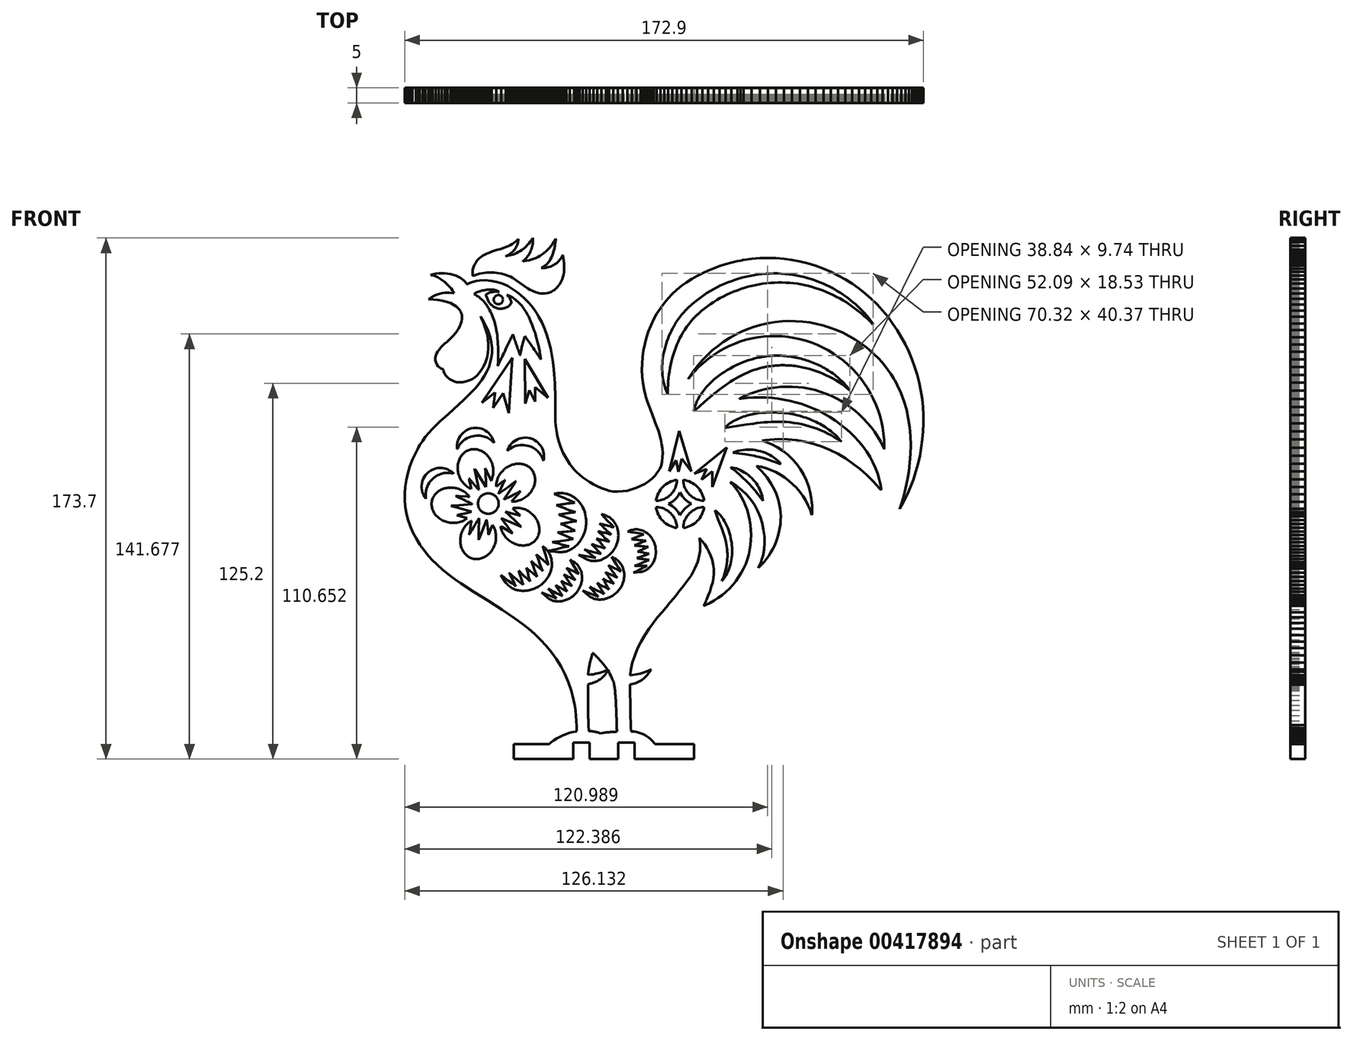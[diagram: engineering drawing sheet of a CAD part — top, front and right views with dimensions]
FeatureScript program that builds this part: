
annotation { "Feature Type Name" : "Feature", "Feature Type Description" : "" }
export const myFeature = defineFeature(function(context is Context, id is Id, definition is map)
    precondition{}
    {
        {
            var Q0;
            Q0=qCreatedBy(makeId("Front.planeOp"),FACE);
            var sketch = newSketch(context, id + "F0", { "sketchPlane" : qUnion([Q0])});
            skLineSegment(sketch, "E0", {"start": v(-42.96, 87.62) * mm, "end": v(-43, 82.82) * mm});
            skLineSegment(sketch, "E1", {"start": v(-43, 82.82) * mm, "end": v(-44.86, 86.57) * mm});
            skLineSegment(sketch, "E2", {"start": v(-44.86, 86.57) * mm, "end": v(-46.3, 82.2) * mm});
            skLineSegment(sketch, "E3", {"start": v(-46.3, 82.2) * mm, "end": v(-46.39, 97.03) * mm});
            skLineSegment(sketch, "E4", {"start": v(-46.39, 97.03) * mm, "end": v(-38.64, 84.08) * mm});
            skLineSegment(sketch, "E5", {"start": v(-38.64, 84.08) * mm, "end": v(-42.96, 87.62) * mm});
            skCircle(sketch, "E6", {"center": v(-55.22, 116.82) * mm, "radius": 1.54 * mm});
            skLineSegment(sketch, "E7", {"start": v(-50.59, 97.44) * mm, "end": v(-51.67, 79.01) * mm});
            skLineSegment(sketch, "E8", {"start": v(-51.67, 79.01) * mm, "end": v(-53.6, 85.56) * mm});
            skLineSegment(sketch, "E9", {"start": v(-53.6, 85.56) * mm, "end": v(-56.93, 80.73) * mm});
            skLineSegment(sketch, "E10", {"start": v(-56.93, 80.73) * mm, "end": v(-56.24, 85.8) * mm});
            skLineSegment(sketch, "E11", {"start": v(-56.24, 85.8) * mm, "end": v(-60.69, 82.38) * mm});
            skLineSegment(sketch, "E12", {"start": v(-60.69, 82.38) * mm, "end": v(-50.59, 97.44) * mm});
            skCircle(sketch, "E13", {"center": v(-58.57, 48.84) * mm, "radius": 3.43 * mm});
            skLineSegment(sketch, "E14", {"start": v(16.07, 54.36) * mm, "end": v(16.08, 59.58) * mm});
            skLineSegment(sketch, "E15", {"start": v(16.08, 59.58) * mm, "end": v(12.58, 56.76) * mm});
            skLineSegment(sketch, "E16", {"start": v(12.58, 56.76) * mm, "end": v(14.2, 60.34) * mm});
            skLineSegment(sketch, "E17", {"start": v(14.2, 60.34) * mm, "end": v(10.18, 58.8) * mm});
            skLineSegment(sketch, "E18", {"start": v(10.18, 58.8) * mm, "end": v(20.87, 67.64) * mm});
            skLineSegment(sketch, "E19", {"start": v(20.87, 67.64) * mm, "end": v(16.07, 54.36) * mm});
            skLineSegment(sketch, "E20", {"start": v(9.07, 59.54) * mm, "end": v(5.98, 63.75) * mm});
            skLineSegment(sketch, "E21", {"start": v(5.98, 63.75) * mm, "end": v(4.84, 59.4) * mm});
            skLineSegment(sketch, "E22", {"start": v(4.84, 59.4) * mm, "end": v(4.01, 63.23) * mm});
            skLineSegment(sketch, "E23", {"start": v(4.01, 63.23) * mm, "end": v(1.7, 59.6) * mm});
            skLineSegment(sketch, "E24", {"start": v(1.7, 59.6) * mm, "end": v(5.04, 73.08) * mm});
            skLineSegment(sketch, "E25", {"start": v(5.04, 73.08) * mm, "end": v(9.07, 59.54) * mm});
            skLineSegment(sketch, "E26", {"start": v(69.55, 108.65) * mm, "end": v(68.66, 109.56) * mm});
            skLineSegment(sketch, "E27", {"start": v(68.66, 109.56) * mm, "end": v(67.74, 110.45) * mm});
            skLineSegment(sketch, "E28", {"start": v(67.74, 110.45) * mm, "end": v(66.8, 111.3) * mm});
            skLineSegment(sketch, "E29", {"start": v(66.8, 111.3) * mm, "end": v(65.85, 112.14) * mm});
            skLineSegment(sketch, "E30", {"start": v(65.85, 112.14) * mm, "end": v(64.87, 112.95) * mm});
            skLineSegment(sketch, "E31", {"start": v(64.87, 112.95) * mm, "end": v(63.87, 113.73) * mm});
            skLineSegment(sketch, "E32", {"start": v(63.87, 113.73) * mm, "end": v(62.86, 114.48) * mm});
            skLineSegment(sketch, "E33", {"start": v(62.86, 114.48) * mm, "end": v(61.82, 115.2) * mm});
            skLineSegment(sketch, "E34", {"start": v(61.82, 115.2) * mm, "end": v(60.77, 115.9) * mm});
            skLineSegment(sketch, "E35", {"start": v(60.77, 115.9) * mm, "end": v(59.7, 116.57) * mm});
            skLineSegment(sketch, "E36", {"start": v(59.7, 116.57) * mm, "end": v(58.6, 117.2) * mm});
            skLineSegment(sketch, "E37", {"start": v(58.6, 117.2) * mm, "end": v(57.5, 117.8) * mm});
            skLineSegment(sketch, "E38", {"start": v(57.5, 117.8) * mm, "end": v(56.38, 118.37) * mm});
            skLineSegment(sketch, "E39", {"start": v(56.38, 118.37) * mm, "end": v(55.24, 118.9) * mm});
            skLineSegment(sketch, "E40", {"start": v(55.24, 118.9) * mm, "end": v(54.09, 119.41) * mm});
            skLineSegment(sketch, "E41", {"start": v(54.09, 119.41) * mm, "end": v(52.92, 119.88) * mm});
            skLineSegment(sketch, "E42", {"start": v(52.92, 119.88) * mm, "end": v(51.74, 120.31) * mm});
            skLineSegment(sketch, "E43", {"start": v(51.74, 120.31) * mm, "end": v(50.54, 120.7) * mm});
            skLineSegment(sketch, "E44", {"start": v(50.54, 120.7) * mm, "end": v(49.34, 121.07) * mm});
            skLineSegment(sketch, "E45", {"start": v(49.34, 121.07) * mm, "end": v(48.11, 121.39) * mm});
            skLineSegment(sketch, "E46", {"start": v(48.11, 121.39) * mm, "end": v(46.88, 121.67) * mm});
            skLineSegment(sketch, "E47", {"start": v(46.88, 121.67) * mm, "end": v(45.63, 121.92) * mm});
            skLineSegment(sketch, "E48", {"start": v(45.63, 121.92) * mm, "end": v(44.38, 122.12) * mm});
            skLineSegment(sketch, "E49", {"start": v(44.38, 122.12) * mm, "end": v(43.11, 122.29) * mm});
            skLineSegment(sketch, "E50", {"start": v(43.11, 122.29) * mm, "end": v(41.83, 122.41) * mm});
            skLineSegment(sketch, "E51", {"start": v(41.83, 122.41) * mm, "end": v(41.2, 122.46) * mm});
            skLineSegment(sketch, "E52", {"start": v(41.2, 122.46) * mm, "end": v(40.56, 122.5) * mm});
            skLineSegment(sketch, "E53", {"start": v(40.56, 122.5) * mm, "end": v(39.3, 122.53) * mm});
            skLineSegment(sketch, "E54", {"start": v(39.3, 122.53) * mm, "end": v(38.04, 122.53) * mm});
            skLineSegment(sketch, "E55", {"start": v(38.04, 122.53) * mm, "end": v(36.78, 122.5) * mm});
            skLineSegment(sketch, "E56", {"start": v(36.78, 122.5) * mm, "end": v(35.52, 122.41) * mm});
            skLineSegment(sketch, "E57", {"start": v(35.52, 122.41) * mm, "end": v(34.26, 122.29) * mm});
            skLineSegment(sketch, "E58", {"start": v(34.26, 122.29) * mm, "end": v(33, 122.13) * mm});
            skLineSegment(sketch, "E59", {"start": v(33, 122.13) * mm, "end": v(31.76, 121.93) * mm});
            skLineSegment(sketch, "E60", {"start": v(31.76, 121.93) * mm, "end": v(30.52, 121.7) * mm});
            skLineSegment(sketch, "E61", {"start": v(30.52, 121.7) * mm, "end": v(29.28, 121.42) * mm});
            skLineSegment(sketch, "E62", {"start": v(29.28, 121.42) * mm, "end": v(28.06, 121.1) * mm});
            skLineSegment(sketch, "E63", {"start": v(28.06, 121.1) * mm, "end": v(26.84, 120.76) * mm});
            skLineSegment(sketch, "E64", {"start": v(26.84, 120.76) * mm, "end": v(25.63, 120.37) * mm});
            skLineSegment(sketch, "E65", {"start": v(25.63, 120.37) * mm, "end": v(24.44, 119.95) * mm});
            skLineSegment(sketch, "E66", {"start": v(24.44, 119.95) * mm, "end": v(23.26, 119.5) * mm});
            skLineSegment(sketch, "E67", {"start": v(23.26, 119.5) * mm, "end": v(22.1, 119) * mm});
            skLineSegment(sketch, "E68", {"start": v(22.1, 119) * mm, "end": v(20.94, 118.47) * mm});
            skLineSegment(sketch, "E69", {"start": v(20.94, 118.47) * mm, "end": v(19.8, 117.9) * mm});
            skLineSegment(sketch, "E70", {"start": v(19.8, 117.9) * mm, "end": v(18.7, 117.3) * mm});
            skLineSegment(sketch, "E71", {"start": v(18.7, 117.3) * mm, "end": v(17.6, 116.66) * mm});
            skLineSegment(sketch, "E72", {"start": v(17.6, 116.66) * mm, "end": v(16.52, 116) * mm});
            skLineSegment(sketch, "E73", {"start": v(16.52, 116) * mm, "end": v(15.46, 115.3) * mm});
            skLineSegment(sketch, "E74", {"start": v(15.46, 115.3) * mm, "end": v(14.43, 114.56) * mm});
            skLineSegment(sketch, "E75", {"start": v(14.43, 114.56) * mm, "end": v(13.42, 113.79) * mm});
            skLineSegment(sketch, "E76", {"start": v(13.42, 113.79) * mm, "end": v(12.44, 112.99) * mm});
            skLineSegment(sketch, "E77", {"start": v(12.44, 112.99) * mm, "end": v(11.49, 112.15) * mm});
            skLineSegment(sketch, "E78", {"start": v(11.49, 112.15) * mm, "end": v(11.25, 111.94) * mm});
            skLineSegment(sketch, "E79", {"start": v(11.25, 111.94) * mm, "end": v(11.04, 111.74) * mm});
            skLineSegment(sketch, "E80", {"start": v(11.04, 111.74) * mm, "end": v(10.61, 111.34) * mm});
            skLineSegment(sketch, "E81", {"start": v(10.61, 111.34) * mm, "end": v(9.8, 110.5) * mm});
            skLineSegment(sketch, "E82", {"start": v(9.8, 110.5) * mm, "end": v(9.03, 109.63) * mm});
            skLineSegment(sketch, "E83", {"start": v(9.03, 109.63) * mm, "end": v(8.3, 108.74) * mm});
            skLineSegment(sketch, "E84", {"start": v(8.3, 108.74) * mm, "end": v(7.6, 107.82) * mm});
            skLineSegment(sketch, "E85", {"start": v(7.6, 107.82) * mm, "end": v(6.95, 106.88) * mm});
            skLineSegment(sketch, "E86", {"start": v(6.95, 106.88) * mm, "end": v(6.34, 105.9) * mm});
            skLineSegment(sketch, "E87", {"start": v(6.34, 105.9) * mm, "end": v(5.77, 104.92) * mm});
            skLineSegment(sketch, "E88", {"start": v(5.77, 104.92) * mm, "end": v(5.24, 103.9) * mm});
            skLineSegment(sketch, "E89", {"start": v(5.24, 103.9) * mm, "end": v(4.74, 102.87) * mm});
            skLineSegment(sketch, "E90", {"start": v(4.74, 102.87) * mm, "end": v(4.28, 101.83) * mm});
            skLineSegment(sketch, "E91", {"start": v(4.28, 101.83) * mm, "end": v(3.85, 100.76) * mm});
            skLineSegment(sketch, "E92", {"start": v(3.85, 100.76) * mm, "end": v(3.46, 99.68) * mm});
            skLineSegment(sketch, "E93", {"start": v(3.46, 99.68) * mm, "end": v(3.1, 98.59) * mm});
            skLineSegment(sketch, "E94", {"start": v(3.1, 98.59) * mm, "end": v(2.78, 97.48) * mm});
            skLineSegment(sketch, "E95", {"start": v(2.78, 97.48) * mm, "end": v(2.5, 96.37) * mm});
            skLineSegment(sketch, "E96", {"start": v(2.5, 96.37) * mm, "end": v(2.24, 95.24) * mm});
            skLineSegment(sketch, "E97", {"start": v(2.24, 95.24) * mm, "end": v(2.01, 94.11) * mm});
            skLineSegment(sketch, "E98", {"start": v(2.01, 94.11) * mm, "end": v(1.82, 92.97) * mm});
            skLineSegment(sketch, "E99", {"start": v(1.82, 92.97) * mm, "end": v(1.66, 91.83) * mm});
            skLineSegment(sketch, "E100", {"start": v(1.66, 91.83) * mm, "end": v(1.52, 90.68) * mm});
            skLineSegment(sketch, "E101", {"start": v(1.52, 90.68) * mm, "end": v(1.42, 89.54) * mm});
            skLineSegment(sketch, "E102", {"start": v(1.42, 89.54) * mm, "end": v(1.34, 88.39) * mm});
            skLineSegment(sketch, "E103", {"start": v(1.34, 88.39) * mm, "end": v(1.29, 87.24) * mm});
            skLineSegment(sketch, "E104", {"start": v(1.29, 87.24) * mm, "end": v(1.26, 86.1) * mm});
            skLineSegment(sketch, "E105", {"start": v(1.26, 86.1) * mm, "end": v(1.26, 85.53) * mm});
            skLineSegment(sketch, "E106", {"start": v(1.26, 85.53) * mm, "end": v(1.26, 85.24) * mm});
            skLineSegment(sketch, "E107", {"start": v(1.26, 85.24) * mm, "end": v(1.26, 85.2) * mm});
            skLineSegment(sketch, "E108", {"start": v(1.26, 85.2) * mm, "end": v(1.26, 85.2) * mm});
            skLineSegment(sketch, "E109", {"start": v(1.26, 85.2) * mm, "end": v(1.23, 85.25) * mm});
            skLineSegment(sketch, "E110", {"start": v(1.23, 85.25) * mm, "end": v(1.18, 85.36) * mm});
            skLineSegment(sketch, "E111", {"start": v(1.18, 85.36) * mm, "end": v(0.8, 86.24) * mm});
            skLineSegment(sketch, "E112", {"start": v(0.8, 86.24) * mm, "end": v(0.47, 87.14) * mm});
            skLineSegment(sketch, "E113", {"start": v(0.47, 87.14) * mm, "end": v(0.19, 88.04) * mm});
            skLineSegment(sketch, "E114", {"start": v(0.19, 88.04) * mm, "end": v(-0.05, 88.96) * mm});
            skLineSegment(sketch, "E115", {"start": v(-0.05, 88.96) * mm, "end": v(-0.25, 89.88) * mm});
            skLineSegment(sketch, "E116", {"start": v(-0.25, 89.88) * mm, "end": v(-0.4, 90.8) * mm});
            skLineSegment(sketch, "E117", {"start": v(-0.4, 90.8) * mm, "end": v(-0.52, 91.75) * mm});
            skLineSegment(sketch, "E118", {"start": v(-0.52, 91.75) * mm, "end": v(-0.6, 92.69) * mm});
            skLineSegment(sketch, "E119", {"start": v(-0.6, 92.69) * mm, "end": v(-0.62, 93.63) * mm});
            skLineSegment(sketch, "E120", {"start": v(-0.62, 93.63) * mm, "end": v(-0.62, 94.58) * mm});
            skLineSegment(sketch, "E121", {"start": v(-0.62, 94.58) * mm, "end": v(-0.57, 95.53) * mm});
            skLineSegment(sketch, "E122", {"start": v(-0.57, 95.53) * mm, "end": v(-0.5, 96.47) * mm});
            skLineSegment(sketch, "E123", {"start": v(-0.5, 96.47) * mm, "end": v(-0.38, 97.42) * mm});
            skLineSegment(sketch, "E124", {"start": v(-0.38, 97.42) * mm, "end": v(-0.23, 98.36) * mm});
            skLineSegment(sketch, "E125", {"start": v(-0.23, 98.36) * mm, "end": v(-0.05, 99.3) * mm});
            skLineSegment(sketch, "E126", {"start": v(-0.05, 99.3) * mm, "end": v(0.17, 100.23) * mm});
            skLineSegment(sketch, "E127", {"start": v(0.17, 100.23) * mm, "end": v(0.41, 101.15) * mm});
            skLineSegment(sketch, "E128", {"start": v(0.41, 101.15) * mm, "end": v(0.69, 102.07) * mm});
            skLineSegment(sketch, "E129", {"start": v(0.69, 102.07) * mm, "end": v(0.99, 102.98) * mm});
            skLineSegment(sketch, "E130", {"start": v(0.99, 102.98) * mm, "end": v(1.32, 103.87) * mm});
            skLineSegment(sketch, "E131", {"start": v(1.32, 103.87) * mm, "end": v(1.68, 104.75) * mm});
            skLineSegment(sketch, "E132", {"start": v(1.68, 104.75) * mm, "end": v(2.06, 105.62) * mm});
            skLineSegment(sketch, "E133", {"start": v(2.06, 105.62) * mm, "end": v(2.47, 106.48) * mm});
            skLineSegment(sketch, "E134", {"start": v(2.47, 106.48) * mm, "end": v(2.9, 107.32) * mm});
            skLineSegment(sketch, "E135", {"start": v(2.9, 107.32) * mm, "end": v(3.36, 108.14) * mm});
            skLineSegment(sketch, "E136", {"start": v(3.36, 108.14) * mm, "end": v(3.47, 108.34) * mm});
            skLineSegment(sketch, "E137", {"start": v(3.47, 108.34) * mm, "end": v(3.53, 108.44) * mm});
            skLineSegment(sketch, "E138", {"start": v(3.53, 108.44) * mm, "end": v(3.58, 108.52) * mm});
            skLineSegment(sketch, "E139", {"start": v(3.58, 108.52) * mm, "end": v(3.74, 108.8) * mm});
            skLineSegment(sketch, "E140", {"start": v(3.74, 108.8) * mm, "end": v(4.09, 109.34) * mm});
            skLineSegment(sketch, "E141", {"start": v(4.09, 109.34) * mm, "end": v(4.44, 109.88) * mm});
            skLineSegment(sketch, "E142", {"start": v(4.44, 109.88) * mm, "end": v(4.8, 110.4) * mm});
            skLineSegment(sketch, "E143", {"start": v(4.8, 110.4) * mm, "end": v(5.2, 110.92) * mm});
            skLineSegment(sketch, "E144", {"start": v(5.2, 110.92) * mm, "end": v(5.58, 111.43) * mm});
            skLineSegment(sketch, "E145", {"start": v(5.58, 111.43) * mm, "end": v(5.99, 111.92) * mm});
            skLineSegment(sketch, "E146", {"start": v(5.99, 111.92) * mm, "end": v(6.4, 112.4) * mm});
            skLineSegment(sketch, "E147", {"start": v(6.4, 112.4) * mm, "end": v(7.26, 113.35) * mm});
            skLineSegment(sketch, "E148", {"start": v(7.26, 113.35) * mm, "end": v(8.17, 114.26) * mm});
            skLineSegment(sketch, "E149", {"start": v(8.17, 114.26) * mm, "end": v(9.1, 115.12) * mm});
            skLineSegment(sketch, "E150", {"start": v(9.1, 115.12) * mm, "end": v(10.08, 115.96) * mm});
            skLineSegment(sketch, "E151", {"start": v(10.08, 115.96) * mm, "end": v(11.08, 116.76) * mm});
            skLineSegment(sketch, "E152", {"start": v(11.08, 116.76) * mm, "end": v(12.1, 117.52) * mm});
            skLineSegment(sketch, "E153", {"start": v(12.1, 117.52) * mm, "end": v(13.16, 118.26) * mm});
            skLineSegment(sketch, "E154", {"start": v(13.16, 118.26) * mm, "end": v(14.24, 118.96) * mm});
            skLineSegment(sketch, "E155", {"start": v(14.24, 118.96) * mm, "end": v(15.33, 119.63) * mm});
            skLineSegment(sketch, "E156", {"start": v(15.33, 119.63) * mm, "end": v(16.47, 120.29) * mm});
            skLineSegment(sketch, "E157", {"start": v(16.47, 120.29) * mm, "end": v(17.63, 120.9) * mm});
            skLineSegment(sketch, "E158", {"start": v(17.63, 120.9) * mm, "end": v(18.8, 121.49) * mm});
            skLineSegment(sketch, "E159", {"start": v(18.8, 121.49) * mm, "end": v(20, 122.03) * mm});
            skLineSegment(sketch, "E160", {"start": v(20, 122.03) * mm, "end": v(21.2, 122.54) * mm});
            skLineSegment(sketch, "E161", {"start": v(21.2, 122.54) * mm, "end": v(22.43, 123) * mm});
            skLineSegment(sketch, "E162", {"start": v(22.43, 123) * mm, "end": v(23.67, 123.43) * mm});
            skLineSegment(sketch, "E163", {"start": v(23.67, 123.43) * mm, "end": v(24.91, 123.82) * mm});
            skLineSegment(sketch, "E164", {"start": v(24.91, 123.82) * mm, "end": v(26.17, 124.18) * mm});
            skLineSegment(sketch, "E165", {"start": v(26.17, 124.18) * mm, "end": v(27.44, 124.49) * mm});
            skLineSegment(sketch, "E166", {"start": v(27.44, 124.49) * mm, "end": v(28.71, 124.76) * mm});
            skLineSegment(sketch, "E167", {"start": v(28.71, 124.76) * mm, "end": v(30, 125) * mm});
            skLineSegment(sketch, "E168", {"start": v(30, 125) * mm, "end": v(31.28, 125.2) * mm});
            skLineSegment(sketch, "E169", {"start": v(31.28, 125.2) * mm, "end": v(32.58, 125.35) * mm});
            skLineSegment(sketch, "E170", {"start": v(32.58, 125.35) * mm, "end": v(33.87, 125.46) * mm});
            skLineSegment(sketch, "E171", {"start": v(33.87, 125.46) * mm, "end": v(35.18, 125.53) * mm});
            skLineSegment(sketch, "E172", {"start": v(35.18, 125.53) * mm, "end": v(36.48, 125.56) * mm});
            skLineSegment(sketch, "E173", {"start": v(36.48, 125.56) * mm, "end": v(37.78, 125.56) * mm});
            skLineSegment(sketch, "E174", {"start": v(37.78, 125.56) * mm, "end": v(39.09, 125.5) * mm});
            skLineSegment(sketch, "E175", {"start": v(39.09, 125.5) * mm, "end": v(40.39, 125.41) * mm});
            skLineSegment(sketch, "E176", {"start": v(40.39, 125.41) * mm, "end": v(41.69, 125.28) * mm});
            skLineSegment(sketch, "E177", {"start": v(41.69, 125.28) * mm, "end": v(42.98, 125.1) * mm});
            skLineSegment(sketch, "E178", {"start": v(42.98, 125.1) * mm, "end": v(44.28, 124.88) * mm});
            skLineSegment(sketch, "E179", {"start": v(44.28, 124.88) * mm, "end": v(45.56, 124.62) * mm});
            skLineSegment(sketch, "E180", {"start": v(45.56, 124.62) * mm, "end": v(46.84, 124.32) * mm});
            skLineSegment(sketch, "E181", {"start": v(46.84, 124.32) * mm, "end": v(47.48, 124.15) * mm});
            skLineSegment(sketch, "E182", {"start": v(47.48, 124.15) * mm, "end": v(47.63, 124.11) * mm});
            skLineSegment(sketch, "E183", {"start": v(47.63, 124.11) * mm, "end": v(47.76, 124.07) * mm});
            skLineSegment(sketch, "E184", {"start": v(47.76, 124.07) * mm, "end": v(48.02, 124) * mm});
            skLineSegment(sketch, "E185", {"start": v(48.02, 124) * mm, "end": v(49.05, 123.69) * mm});
            skLineSegment(sketch, "E186", {"start": v(49.05, 123.69) * mm, "end": v(50.07, 123.35) * mm});
            skLineSegment(sketch, "E187", {"start": v(50.07, 123.35) * mm, "end": v(51.08, 122.98) * mm});
            skLineSegment(sketch, "E188", {"start": v(51.08, 122.98) * mm, "end": v(52.08, 122.6) * mm});
            skLineSegment(sketch, "E189", {"start": v(52.08, 122.6) * mm, "end": v(53.06, 122.17) * mm});
            skLineSegment(sketch, "E190", {"start": v(53.06, 122.17) * mm, "end": v(54.04, 121.73) * mm});
            skLineSegment(sketch, "E191", {"start": v(54.04, 121.73) * mm, "end": v(55, 121.26) * mm});
            skLineSegment(sketch, "E192", {"start": v(55, 121.26) * mm, "end": v(55.95, 120.77) * mm});
            skLineSegment(sketch, "E193", {"start": v(55.95, 120.77) * mm, "end": v(56.88, 120.25) * mm});
            skLineSegment(sketch, "E194", {"start": v(56.88, 120.25) * mm, "end": v(57.8, 119.7) * mm});
            skLineSegment(sketch, "E195", {"start": v(57.8, 119.7) * mm, "end": v(58.7, 119.14) * mm});
            skLineSegment(sketch, "E196", {"start": v(58.7, 119.14) * mm, "end": v(59.6, 118.55) * mm});
            skLineSegment(sketch, "E197", {"start": v(59.6, 118.55) * mm, "end": v(60.47, 117.94) * mm});
            skLineSegment(sketch, "E198", {"start": v(60.47, 117.94) * mm, "end": v(61.33, 117.3) * mm});
            skLineSegment(sketch, "E199", {"start": v(61.33, 117.3) * mm, "end": v(62.17, 116.65) * mm});
            skLineSegment(sketch, "E200", {"start": v(62.17, 116.65) * mm, "end": v(63, 115.97) * mm});
            skLineSegment(sketch, "E201", {"start": v(63, 115.97) * mm, "end": v(63.8, 115.27) * mm});
            skLineSegment(sketch, "E202", {"start": v(63.8, 115.27) * mm, "end": v(64.6, 114.55) * mm});
            skLineSegment(sketch, "E203", {"start": v(64.6, 114.55) * mm, "end": v(65.36, 113.8) * mm});
            skLineSegment(sketch, "E204", {"start": v(65.36, 113.8) * mm, "end": v(66.11, 113.04) * mm});
            skLineSegment(sketch, "E205", {"start": v(66.11, 113.04) * mm, "end": v(66.85, 112.26) * mm});
            skLineSegment(sketch, "E206", {"start": v(66.85, 112.26) * mm, "end": v(67.56, 111.46) * mm});
            skLineSegment(sketch, "E207", {"start": v(67.56, 111.46) * mm, "end": v(68.25, 110.64) * mm});
            skLineSegment(sketch, "E208", {"start": v(68.25, 110.64) * mm, "end": v(68.92, 109.8) * mm});
            skLineSegment(sketch, "E209", {"start": v(68.92, 109.8) * mm, "end": v(69.57, 108.94) * mm});
            skLineSegment(sketch, "E210", {"start": v(69.57, 108.94) * mm, "end": v(69.65, 108.83) * mm});
            skLineSegment(sketch, "E211", {"start": v(69.65, 108.83) * mm, "end": v(69.69, 108.78) * mm});
            skLineSegment(sketch, "E212", {"start": v(69.69, 108.78) * mm, "end": v(69.7, 108.77) * mm});
            skLineSegment(sketch, "E213", {"start": v(69.7, 108.77) * mm, "end": v(69.7, 108.77) * mm});
            skLineSegment(sketch, "E214", {"start": v(69.7, 108.77) * mm, "end": v(69.7, 108.76) * mm});
            skLineSegment(sketch, "E215", {"start": v(69.7, 108.76) * mm, "end": v(69.7, 108.76) * mm});
            skLineSegment(sketch, "E216", {"start": v(69.7, 108.76) * mm, "end": v(69.7, 108.75) * mm});
            skLineSegment(sketch, "E217", {"start": v(69.7, 108.75) * mm, "end": v(69.64, 108.72) * mm});
            skLineSegment(sketch, "E218", {"start": v(69.64, 108.72) * mm, "end": v(69.55, 108.65) * mm});
            skLineSegment(sketch, "E219", {"start": v(19.2, 92.16) * mm, "end": v(20.14, 92.78) * mm});
            skLineSegment(sketch, "E220", {"start": v(20.14, 92.78) * mm, "end": v(21.08, 93.37) * mm});
            skLineSegment(sketch, "E221", {"start": v(21.08, 93.37) * mm, "end": v(22.05, 93.93) * mm});
            skLineSegment(sketch, "E222", {"start": v(22.05, 93.93) * mm, "end": v(23.03, 94.45) * mm});
            skLineSegment(sketch, "E223", {"start": v(23.03, 94.45) * mm, "end": v(24.03, 94.95) * mm});
            skLineSegment(sketch, "E224", {"start": v(24.03, 94.95) * mm, "end": v(25.05, 95.42) * mm});
            skLineSegment(sketch, "E225", {"start": v(25.05, 95.42) * mm, "end": v(26.08, 95.85) * mm});
            skLineSegment(sketch, "E226", {"start": v(26.08, 95.85) * mm, "end": v(27.12, 96.25) * mm});
            skLineSegment(sketch, "E227", {"start": v(27.12, 96.25) * mm, "end": v(28.18, 96.61) * mm});
            skLineSegment(sketch, "E228", {"start": v(28.18, 96.61) * mm, "end": v(29.24, 96.94) * mm});
            skLineSegment(sketch, "E229", {"start": v(29.24, 96.94) * mm, "end": v(30.32, 97.24) * mm});
            skLineSegment(sketch, "E230", {"start": v(30.32, 97.24) * mm, "end": v(31.4, 97.5) * mm});
            skLineSegment(sketch, "E231", {"start": v(31.4, 97.5) * mm, "end": v(31.95, 97.61) * mm});
            skLineSegment(sketch, "E232", {"start": v(31.95, 97.61) * mm, "end": v(32.22, 97.66) * mm});
            skLineSegment(sketch, "E233", {"start": v(32.22, 97.66) * mm, "end": v(32.26, 97.67) * mm});
            skLineSegment(sketch, "E234", {"start": v(32.26, 97.67) * mm, "end": v(32.28, 97.67) * mm});
            skLineSegment(sketch, "E235", {"start": v(32.28, 97.67) * mm, "end": v(32.3, 97.68) * mm});
            skLineSegment(sketch, "E236", {"start": v(32.3, 97.68) * mm, "end": v(32.46, 97.7) * mm});
            skLineSegment(sketch, "E237", {"start": v(32.46, 97.7) * mm, "end": v(32.78, 97.76) * mm});
            skLineSegment(sketch, "E238", {"start": v(32.78, 97.76) * mm, "end": v(33.4, 97.86) * mm});
            skLineSegment(sketch, "E239", {"start": v(33.4, 97.86) * mm, "end": v(34.03, 97.95) * mm});
            skLineSegment(sketch, "E240", {"start": v(34.03, 97.95) * mm, "end": v(34.67, 98.02) * mm});
            skLineSegment(sketch, "E241", {"start": v(34.67, 98.02) * mm, "end": v(35.3, 98.08) * mm});
            skLineSegment(sketch, "E242", {"start": v(35.3, 98.08) * mm, "end": v(35.94, 98.12) * mm});
            skLineSegment(sketch, "E243", {"start": v(35.94, 98.12) * mm, "end": v(36.59, 98.15) * mm});
            skLineSegment(sketch, "E244", {"start": v(36.59, 98.15) * mm, "end": v(37.23, 98.16) * mm});
            skLineSegment(sketch, "E245", {"start": v(37.23, 98.16) * mm, "end": v(37.88, 98.16) * mm});
            skLineSegment(sketch, "E246", {"start": v(37.88, 98.16) * mm, "end": v(38.52, 98.15) * mm});
            skLineSegment(sketch, "E247", {"start": v(38.52, 98.15) * mm, "end": v(39.17, 98.13) * mm});
            skLineSegment(sketch, "E248", {"start": v(39.17, 98.13) * mm, "end": v(39.82, 98.09) * mm});
            skLineSegment(sketch, "E249", {"start": v(39.82, 98.09) * mm, "end": v(40.47, 98.03) * mm});
            skLineSegment(sketch, "E250", {"start": v(40.47, 98.03) * mm, "end": v(41.12, 97.97) * mm});
            skLineSegment(sketch, "E251", {"start": v(41.12, 97.97) * mm, "end": v(41.77, 97.89) * mm});
            skLineSegment(sketch, "E252", {"start": v(41.77, 97.89) * mm, "end": v(42.42, 97.8) * mm});
            skLineSegment(sketch, "E253", {"start": v(42.42, 97.8) * mm, "end": v(43.07, 97.69) * mm});
            skLineSegment(sketch, "E254", {"start": v(43.07, 97.69) * mm, "end": v(43.71, 97.57) * mm});
            skLineSegment(sketch, "E255", {"start": v(43.71, 97.57) * mm, "end": v(44.36, 97.44) * mm});
            skLineSegment(sketch, "E256", {"start": v(44.36, 97.44) * mm, "end": v(45, 97.29) * mm});
            skLineSegment(sketch, "E257", {"start": v(45, 97.29) * mm, "end": v(45.64, 97.13) * mm});
            skLineSegment(sketch, "E258", {"start": v(45.64, 97.13) * mm, "end": v(46.27, 96.96) * mm});
            skLineSegment(sketch, "E259", {"start": v(46.27, 96.96) * mm, "end": v(46.9, 96.78) * mm});
            skLineSegment(sketch, "E260", {"start": v(46.9, 96.78) * mm, "end": v(47.54, 96.58) * mm});
            skLineSegment(sketch, "E261", {"start": v(47.54, 96.58) * mm, "end": v(48.16, 96.37) * mm});
            skLineSegment(sketch, "E262", {"start": v(48.16, 96.37) * mm, "end": v(48.78, 96.15) * mm});
            skLineSegment(sketch, "E263", {"start": v(48.78, 96.15) * mm, "end": v(49.4, 95.92) * mm});
            skLineSegment(sketch, "E264", {"start": v(49.4, 95.92) * mm, "end": v(50.01, 95.67) * mm});
            skLineSegment(sketch, "E265", {"start": v(50.01, 95.67) * mm, "end": v(50.62, 95.41) * mm});
            skLineSegment(sketch, "E266", {"start": v(50.62, 95.41) * mm, "end": v(51.22, 95.14) * mm});
            skLineSegment(sketch, "E267", {"start": v(51.22, 95.14) * mm, "end": v(51.81, 94.86) * mm});
            skLineSegment(sketch, "E268", {"start": v(51.81, 94.86) * mm, "end": v(52.4, 94.56) * mm});
            skLineSegment(sketch, "E269", {"start": v(52.4, 94.56) * mm, "end": v(52.98, 94.26) * mm});
            skLineSegment(sketch, "E270", {"start": v(52.98, 94.26) * mm, "end": v(53.55, 93.94) * mm});
            skLineSegment(sketch, "E271", {"start": v(53.55, 93.94) * mm, "end": v(54.12, 93.6) * mm});
            skLineSegment(sketch, "E272", {"start": v(54.12, 93.6) * mm, "end": v(54.67, 93.26) * mm});
            skLineSegment(sketch, "E273", {"start": v(54.67, 93.26) * mm, "end": v(55.22, 92.91) * mm});
            skLineSegment(sketch, "E274", {"start": v(55.22, 92.91) * mm, "end": v(55.76, 92.55) * mm});
            skLineSegment(sketch, "E275", {"start": v(55.76, 92.55) * mm, "end": v(56.3, 92.17) * mm});
            skLineSegment(sketch, "E276", {"start": v(56.3, 92.17) * mm, "end": v(56.82, 91.78) * mm});
            skLineSegment(sketch, "E277", {"start": v(56.82, 91.78) * mm, "end": v(57.33, 91.38) * mm});
            skLineSegment(sketch, "E278", {"start": v(57.33, 91.38) * mm, "end": v(57.83, 90.97) * mm});
            skLineSegment(sketch, "E279", {"start": v(57.83, 90.97) * mm, "end": v(58.32, 90.55) * mm});
            skLineSegment(sketch, "E280", {"start": v(58.32, 90.55) * mm, "end": v(58.8, 90.11) * mm});
            skLineSegment(sketch, "E281", {"start": v(58.8, 90.11) * mm, "end": v(59.27, 89.67) * mm});
            skLineSegment(sketch, "E282", {"start": v(59.27, 89.67) * mm, "end": v(59.73, 89.21) * mm});
            skLineSegment(sketch, "E283", {"start": v(59.73, 89.21) * mm, "end": v(60.17, 88.75) * mm});
            skLineSegment(sketch, "E284", {"start": v(60.17, 88.75) * mm, "end": v(60.6, 88.27) * mm});
            skLineSegment(sketch, "E285", {"start": v(60.6, 88.27) * mm, "end": v(61.03, 87.78) * mm});
            skLineSegment(sketch, "E286", {"start": v(61.03, 87.78) * mm, "end": v(61.43, 87.28) * mm});
            skLineSegment(sketch, "E287", {"start": v(61.43, 87.28) * mm, "end": v(61.83, 86.78) * mm});
            skLineSegment(sketch, "E288", {"start": v(61.83, 86.78) * mm, "end": v(61.92, 86.65) * mm});
            skLineSegment(sketch, "E289", {"start": v(61.92, 86.65) * mm, "end": v(61.97, 86.58) * mm});
            skLineSegment(sketch, "E290", {"start": v(61.97, 86.58) * mm, "end": v(61.98, 86.57) * mm});
            skLineSegment(sketch, "E291", {"start": v(61.98, 86.57) * mm, "end": v(61.96, 86.58) * mm});
            skLineSegment(sketch, "E292", {"start": v(61.96, 86.58) * mm, "end": v(61.94, 86.6) * mm});
            skLineSegment(sketch, "E293", {"start": v(61.94, 86.6) * mm, "end": v(61.7, 86.8) * mm});
            skLineSegment(sketch, "E294", {"start": v(61.7, 86.8) * mm, "end": v(61.25, 87.18) * mm});
            skLineSegment(sketch, "E295", {"start": v(61.25, 87.18) * mm, "end": v(60.3, 87.91) * mm});
            skLineSegment(sketch, "E296", {"start": v(60.3, 87.91) * mm, "end": v(59.34, 88.62) * mm});
            skLineSegment(sketch, "E297", {"start": v(59.34, 88.62) * mm, "end": v(58.34, 89.29) * mm});
            skLineSegment(sketch, "E298", {"start": v(58.34, 89.29) * mm, "end": v(57.32, 89.92) * mm});
            skLineSegment(sketch, "E299", {"start": v(57.32, 89.92) * mm, "end": v(56.28, 90.53) * mm});
            skLineSegment(sketch, "E300", {"start": v(56.28, 90.53) * mm, "end": v(55.21, 91.1) * mm});
            skLineSegment(sketch, "E301", {"start": v(55.21, 91.1) * mm, "end": v(54.13, 91.63) * mm});
            skLineSegment(sketch, "E302", {"start": v(54.13, 91.63) * mm, "end": v(53.02, 92.13) * mm});
            skLineSegment(sketch, "E303", {"start": v(53.02, 92.13) * mm, "end": v(51.9, 92.59) * mm});
            skLineSegment(sketch, "E304", {"start": v(51.9, 92.59) * mm, "end": v(50.76, 93) * mm});
            skLineSegment(sketch, "E305", {"start": v(50.76, 93) * mm, "end": v(49.61, 93.4) * mm});
            skLineSegment(sketch, "E306", {"start": v(49.61, 93.4) * mm, "end": v(48.45, 93.73) * mm});
            skLineSegment(sketch, "E307", {"start": v(48.45, 93.73) * mm, "end": v(47.28, 94.04) * mm});
            skLineSegment(sketch, "E308", {"start": v(47.28, 94.04) * mm, "end": v(46.1, 94.3) * mm});
            skLineSegment(sketch, "E309", {"start": v(46.1, 94.3) * mm, "end": v(44.9, 94.52) * mm});
            skLineSegment(sketch, "E310", {"start": v(44.9, 94.52) * mm, "end": v(43.72, 94.7) * mm});
            skLineSegment(sketch, "E311", {"start": v(43.72, 94.7) * mm, "end": v(43.12, 94.77) * mm});
            skLineSegment(sketch, "E312", {"start": v(43.12, 94.77) * mm, "end": v(42.52, 94.83) * mm});
            skLineSegment(sketch, "E313", {"start": v(42.52, 94.83) * mm, "end": v(41.92, 94.88) * mm});
            skLineSegment(sketch, "E314", {"start": v(41.92, 94.88) * mm, "end": v(41.32, 94.91) * mm});
            skLineSegment(sketch, "E315", {"start": v(41.32, 94.91) * mm, "end": v(40.72, 94.94) * mm});
            skLineSegment(sketch, "E316", {"start": v(40.72, 94.94) * mm, "end": v(40.12, 94.96) * mm});
            skLineSegment(sketch, "E317", {"start": v(40.12, 94.96) * mm, "end": v(39.52, 94.96) * mm});
            skLineSegment(sketch, "E318", {"start": v(39.52, 94.96) * mm, "end": v(38.92, 94.95) * mm});
            skLineSegment(sketch, "E319", {"start": v(38.92, 94.95) * mm, "end": v(38.32, 94.94) * mm});
            skLineSegment(sketch, "E320", {"start": v(38.32, 94.94) * mm, "end": v(37.72, 94.9) * mm});
            skLineSegment(sketch, "E321", {"start": v(37.72, 94.9) * mm, "end": v(37.12, 94.86) * mm});
            skLineSegment(sketch, "E322", {"start": v(37.12, 94.86) * mm, "end": v(36.53, 94.8) * mm});
            skLineSegment(sketch, "E323", {"start": v(36.53, 94.8) * mm, "end": v(35.93, 94.74) * mm});
            skLineSegment(sketch, "E324", {"start": v(35.93, 94.74) * mm, "end": v(35.34, 94.66) * mm});
            skLineSegment(sketch, "E325", {"start": v(35.34, 94.66) * mm, "end": v(34.75, 94.57) * mm});
            skLineSegment(sketch, "E326", {"start": v(34.75, 94.57) * mm, "end": v(34.16, 94.46) * mm});
            skLineSegment(sketch, "E327", {"start": v(34.16, 94.46) * mm, "end": v(33.57, 94.35) * mm});
            skLineSegment(sketch, "E328", {"start": v(33.57, 94.35) * mm, "end": v(33.28, 94.28) * mm});
            skLineSegment(sketch, "E329", {"start": v(33.28, 94.28) * mm, "end": v(33, 94.22) * mm});
            skLineSegment(sketch, "E330", {"start": v(33, 94.22) * mm, "end": v(31.93, 93.95) * mm});
            skLineSegment(sketch, "E331", {"start": v(31.93, 93.95) * mm, "end": v(30.87, 93.64) * mm});
            skLineSegment(sketch, "E332", {"start": v(30.87, 93.64) * mm, "end": v(29.84, 93.3) * mm});
            skLineSegment(sketch, "E333", {"start": v(29.84, 93.3) * mm, "end": v(28.82, 92.91) * mm});
            skLineSegment(sketch, "E334", {"start": v(28.82, 92.91) * mm, "end": v(27.82, 92.5) * mm});
            skLineSegment(sketch, "E335", {"start": v(27.82, 92.5) * mm, "end": v(26.83, 92.05) * mm});
            skLineSegment(sketch, "E336", {"start": v(26.83, 92.05) * mm, "end": v(25.86, 91.58) * mm});
            skLineSegment(sketch, "E337", {"start": v(25.86, 91.58) * mm, "end": v(24.9, 91.08) * mm});
            skLineSegment(sketch, "E338", {"start": v(24.9, 91.08) * mm, "end": v(23.97, 90.55) * mm});
            skLineSegment(sketch, "E339", {"start": v(23.97, 90.55) * mm, "end": v(23.04, 90) * mm});
            skLineSegment(sketch, "E340", {"start": v(23.04, 90) * mm, "end": v(22.12, 89.42) * mm});
            skLineSegment(sketch, "E341", {"start": v(22.12, 89.42) * mm, "end": v(21.22, 88.82) * mm});
            skLineSegment(sketch, "E342", {"start": v(21.22, 88.82) * mm, "end": v(20.33, 88.2) * mm});
            skLineSegment(sketch, "E343", {"start": v(20.33, 88.2) * mm, "end": v(19.44, 87.57) * mm});
            skLineSegment(sketch, "E344", {"start": v(19.44, 87.57) * mm, "end": v(18.57, 86.92) * mm});
            skLineSegment(sketch, "E345", {"start": v(18.57, 86.92) * mm, "end": v(17.7, 86.26) * mm});
            skLineSegment(sketch, "E346", {"start": v(17.7, 86.26) * mm, "end": v(16.85, 85.58) * mm});
            skLineSegment(sketch, "E347", {"start": v(16.85, 85.58) * mm, "end": v(16, 84.9) * mm});
            skLineSegment(sketch, "E348", {"start": v(16, 84.9) * mm, "end": v(15.16, 84.2) * mm});
            skLineSegment(sketch, "E349", {"start": v(15.16, 84.2) * mm, "end": v(13.5, 82.78) * mm});
            skLineSegment(sketch, "E350", {"start": v(13.5, 82.78) * mm, "end": v(11.85, 81.35) * mm});
            skLineSegment(sketch, "E351", {"start": v(11.85, 81.35) * mm, "end": v(10.22, 79.92) * mm});
            skLineSegment(sketch, "E352", {"start": v(10.22, 79.92) * mm, "end": v(10.01, 79.74) * mm});
            skLineSegment(sketch, "E353", {"start": v(10.01, 79.74) * mm, "end": v(9.91, 79.65) * mm});
            skLineSegment(sketch, "E354", {"start": v(9.91, 79.65) * mm, "end": v(9.9, 79.64) * mm});
            skLineSegment(sketch, "E355", {"start": v(9.9, 79.64) * mm, "end": v(9.9, 79.64) * mm});
            skLineSegment(sketch, "E356", {"start": v(9.9, 79.64) * mm, "end": v(9.9, 79.65) * mm});
            skLineSegment(sketch, "E357", {"start": v(9.9, 79.65) * mm, "end": v(9.9, 79.7) * mm});
            skLineSegment(sketch, "E358", {"start": v(9.9, 79.7) * mm, "end": v(9.96, 80) * mm});
            skLineSegment(sketch, "E359", {"start": v(9.96, 80) * mm, "end": v(10.1, 80.59) * mm});
            skLineSegment(sketch, "E360", {"start": v(10.1, 80.59) * mm, "end": v(10.28, 81.18) * mm});
            skLineSegment(sketch, "E361", {"start": v(10.28, 81.18) * mm, "end": v(10.48, 81.76) * mm});
            skLineSegment(sketch, "E362", {"start": v(10.48, 81.76) * mm, "end": v(10.7, 82.33) * mm});
            skLineSegment(sketch, "E363", {"start": v(10.7, 82.33) * mm, "end": v(10.95, 82.9) * mm});
            skLineSegment(sketch, "E364", {"start": v(10.95, 82.9) * mm, "end": v(11.22, 83.46) * mm});
            skLineSegment(sketch, "E365", {"start": v(11.22, 83.46) * mm, "end": v(11.52, 84.02) * mm});
            skLineSegment(sketch, "E366", {"start": v(11.52, 84.02) * mm, "end": v(11.83, 84.56) * mm});
            skLineSegment(sketch, "E367", {"start": v(11.83, 84.56) * mm, "end": v(12.16, 85.1) * mm});
            skLineSegment(sketch, "E368", {"start": v(12.16, 85.1) * mm, "end": v(12.52, 85.62) * mm});
            skLineSegment(sketch, "E369", {"start": v(12.52, 85.62) * mm, "end": v(12.89, 86.14) * mm});
            skLineSegment(sketch, "E370", {"start": v(12.89, 86.14) * mm, "end": v(13.27, 86.65) * mm});
            skLineSegment(sketch, "E371", {"start": v(13.27, 86.65) * mm, "end": v(13.67, 87.15) * mm});
            skLineSegment(sketch, "E372", {"start": v(13.67, 87.15) * mm, "end": v(14.09, 87.63) * mm});
            skLineSegment(sketch, "E373", {"start": v(14.09, 87.63) * mm, "end": v(14.52, 88.1) * mm});
            skLineSegment(sketch, "E374", {"start": v(14.52, 88.1) * mm, "end": v(14.95, 88.57) * mm});
            skLineSegment(sketch, "E375", {"start": v(14.95, 88.57) * mm, "end": v(15.4, 89.02) * mm});
            skLineSegment(sketch, "E376", {"start": v(15.4, 89.02) * mm, "end": v(15.86, 89.46) * mm});
            skLineSegment(sketch, "E377", {"start": v(15.86, 89.46) * mm, "end": v(16.32, 89.89) * mm});
            skLineSegment(sketch, "E378", {"start": v(16.32, 89.89) * mm, "end": v(16.8, 90.3) * mm});
            skLineSegment(sketch, "E379", {"start": v(16.8, 90.3) * mm, "end": v(17.27, 90.7) * mm});
            skLineSegment(sketch, "E380", {"start": v(17.27, 90.7) * mm, "end": v(17.75, 91.09) * mm});
            skLineSegment(sketch, "E381", {"start": v(17.75, 91.09) * mm, "end": v(18.24, 91.46) * mm});
            skLineSegment(sketch, "E382", {"start": v(18.24, 91.46) * mm, "end": v(18.72, 91.82) * mm});
            skLineSegment(sketch, "E383", {"start": v(18.72, 91.82) * mm, "end": v(19.2, 92.16) * mm});
            skLineSegment(sketch, "E384", {"start": v(38.88, 79.13) * mm, "end": v(39.57, 79.08) * mm});
            skLineSegment(sketch, "E385", {"start": v(39.57, 79.08) * mm, "end": v(40.27, 79) * mm});
            skLineSegment(sketch, "E386", {"start": v(40.27, 79) * mm, "end": v(41.67, 78.82) * mm});
            skLineSegment(sketch, "E387", {"start": v(41.67, 78.82) * mm, "end": v(43.08, 78.57) * mm});
            skLineSegment(sketch, "E388", {"start": v(43.08, 78.57) * mm, "end": v(44.49, 78.26) * mm});
            skLineSegment(sketch, "E389", {"start": v(44.49, 78.26) * mm, "end": v(45.2, 78.08) * mm});
            skLineSegment(sketch, "E390", {"start": v(45.2, 78.08) * mm, "end": v(45.9, 77.88) * mm});
            skLineSegment(sketch, "E391", {"start": v(45.9, 77.88) * mm, "end": v(46.6, 77.67) * mm});
            skLineSegment(sketch, "E392", {"start": v(46.6, 77.67) * mm, "end": v(47.28, 77.44) * mm});
            skLineSegment(sketch, "E393", {"start": v(47.28, 77.44) * mm, "end": v(47.97, 77.2) * mm});
            skLineSegment(sketch, "E394", {"start": v(47.97, 77.2) * mm, "end": v(48.66, 76.93) * mm});
            skLineSegment(sketch, "E395", {"start": v(48.66, 76.93) * mm, "end": v(49.33, 76.65) * mm});
            skLineSegment(sketch, "E396", {"start": v(49.33, 76.65) * mm, "end": v(50, 76.36) * mm});
            skLineSegment(sketch, "E397", {"start": v(50, 76.36) * mm, "end": v(50.67, 76.05) * mm});
            skLineSegment(sketch, "E398", {"start": v(50.67, 76.05) * mm, "end": v(51.32, 75.73) * mm});
            skLineSegment(sketch, "E399", {"start": v(51.32, 75.73) * mm, "end": v(51.96, 75.39) * mm});
            skLineSegment(sketch, "E400", {"start": v(51.96, 75.39) * mm, "end": v(52.6, 75.03) * mm});
            skLineSegment(sketch, "E401", {"start": v(52.6, 75.03) * mm, "end": v(53.22, 74.66) * mm});
            skLineSegment(sketch, "E402", {"start": v(53.22, 74.66) * mm, "end": v(53.83, 74.27) * mm});
            skLineSegment(sketch, "E403", {"start": v(53.83, 74.27) * mm, "end": v(54.43, 73.86) * mm});
            skLineSegment(sketch, "E404", {"start": v(54.43, 73.86) * mm, "end": v(55.01, 73.44) * mm});
            skLineSegment(sketch, "E405", {"start": v(55.01, 73.44) * mm, "end": v(55.58, 73) * mm});
            skLineSegment(sketch, "E406", {"start": v(55.58, 73) * mm, "end": v(56.14, 72.55) * mm});
            skLineSegment(sketch, "E407", {"start": v(56.14, 72.55) * mm, "end": v(56.67, 72.08) * mm});
            skLineSegment(sketch, "E408", {"start": v(56.67, 72.08) * mm, "end": v(57.2, 71.6) * mm});
            skLineSegment(sketch, "E409", {"start": v(57.2, 71.6) * mm, "end": v(57.7, 71.09) * mm});
            skLineSegment(sketch, "E410", {"start": v(57.7, 71.09) * mm, "end": v(58.19, 70.57) * mm});
            skLineSegment(sketch, "E411", {"start": v(58.19, 70.57) * mm, "end": v(58.65, 70.03) * mm});
            skLineSegment(sketch, "E412", {"start": v(58.65, 70.03) * mm, "end": v(59.1, 69.48) * mm});
            skLineSegment(sketch, "E413", {"start": v(59.1, 69.48) * mm, "end": v(58.02, 70.23) * mm});
            skLineSegment(sketch, "E414", {"start": v(58.02, 70.23) * mm, "end": v(56.9, 70.93) * mm});
            skLineSegment(sketch, "E415", {"start": v(56.9, 70.93) * mm, "end": v(55.77, 71.58) * mm});
            skLineSegment(sketch, "E416", {"start": v(55.77, 71.58) * mm, "end": v(54.6, 72.2) * mm});
            skLineSegment(sketch, "E417", {"start": v(54.6, 72.2) * mm, "end": v(53.41, 72.77) * mm});
            skLineSegment(sketch, "E418", {"start": v(53.41, 72.77) * mm, "end": v(52.2, 73.3) * mm});
            skLineSegment(sketch, "E419", {"start": v(52.2, 73.3) * mm, "end": v(50.97, 73.78) * mm});
            skLineSegment(sketch, "E420", {"start": v(50.97, 73.78) * mm, "end": v(49.72, 74.22) * mm});
            skLineSegment(sketch, "E421", {"start": v(49.72, 74.22) * mm, "end": v(48.45, 74.61) * mm});
            skLineSegment(sketch, "E422", {"start": v(48.45, 74.61) * mm, "end": v(47.18, 74.96) * mm});
            skLineSegment(sketch, "E423", {"start": v(47.18, 74.96) * mm, "end": v(45.89, 75.27) * mm});
            skLineSegment(sketch, "E424", {"start": v(45.89, 75.27) * mm, "end": v(44.6, 75.53) * mm});
            skLineSegment(sketch, "E425", {"start": v(44.6, 75.53) * mm, "end": v(43.29, 75.74) * mm});
            skLineSegment(sketch, "E426", {"start": v(43.29, 75.74) * mm, "end": v(41.98, 75.9) * mm});
            skLineSegment(sketch, "E427", {"start": v(41.98, 75.9) * mm, "end": v(40.68, 76.03) * mm});
            skLineSegment(sketch, "E428", {"start": v(40.68, 76.03) * mm, "end": v(39.37, 76.1) * mm});
            skLineSegment(sketch, "E429", {"start": v(39.37, 76.1) * mm, "end": v(38.17, 76.13) * mm});
            skLineSegment(sketch, "E430", {"start": v(38.17, 76.13) * mm, "end": v(36.97, 76.12) * mm});
            skLineSegment(sketch, "E431", {"start": v(36.97, 76.12) * mm, "end": v(35.77, 76.08) * mm});
            skLineSegment(sketch, "E432", {"start": v(35.77, 76.08) * mm, "end": v(34.57, 76) * mm});
            skLineSegment(sketch, "E433", {"start": v(34.57, 76) * mm, "end": v(33.37, 75.91) * mm});
            skLineSegment(sketch, "E434", {"start": v(33.37, 75.91) * mm, "end": v(32.18, 75.8) * mm});
            skLineSegment(sketch, "E435", {"start": v(32.18, 75.8) * mm, "end": v(30.98, 75.66) * mm});
            skLineSegment(sketch, "E436", {"start": v(30.98, 75.66) * mm, "end": v(29.78, 75.5) * mm});
            skLineSegment(sketch, "E437", {"start": v(29.78, 75.5) * mm, "end": v(27.4, 75.16) * mm});
            skLineSegment(sketch, "E438", {"start": v(27.4, 75.16) * mm, "end": v(25, 74.79) * mm});
            skLineSegment(sketch, "E439", {"start": v(25, 74.79) * mm, "end": v(22.63, 74.42) * mm});
            skLineSegment(sketch, "E440", {"start": v(22.63, 74.42) * mm, "end": v(20.26, 74.07) * mm});
            skLineSegment(sketch, "E441", {"start": v(20.26, 74.07) * mm, "end": v(20.7, 74.5) * mm});
            skLineSegment(sketch, "E442", {"start": v(20.7, 74.5) * mm, "end": v(21.15, 74.9) * mm});
            skLineSegment(sketch, "E443", {"start": v(21.15, 74.9) * mm, "end": v(21.62, 75.29) * mm});
            skLineSegment(sketch, "E444", {"start": v(21.62, 75.29) * mm, "end": v(22.1, 75.65) * mm});
            skLineSegment(sketch, "E445", {"start": v(22.1, 75.65) * mm, "end": v(22.6, 76) * mm});
            skLineSegment(sketch, "E446", {"start": v(22.6, 76) * mm, "end": v(23.13, 76.31) * mm});
            skLineSegment(sketch, "E447", {"start": v(23.13, 76.31) * mm, "end": v(23.66, 76.61) * mm});
            skLineSegment(sketch, "E448", {"start": v(23.66, 76.61) * mm, "end": v(24.21, 76.9) * mm});
            skLineSegment(sketch, "E449", {"start": v(24.21, 76.9) * mm, "end": v(24.77, 77.16) * mm});
            skLineSegment(sketch, "E450", {"start": v(24.77, 77.16) * mm, "end": v(25.34, 77.4) * mm});
            skLineSegment(sketch, "E451", {"start": v(25.34, 77.4) * mm, "end": v(25.92, 77.63) * mm});
            skLineSegment(sketch, "E452", {"start": v(25.92, 77.63) * mm, "end": v(26.52, 77.84) * mm});
            skLineSegment(sketch, "E453", {"start": v(26.52, 77.84) * mm, "end": v(27.12, 78.03) * mm});
            skLineSegment(sketch, "E454", {"start": v(27.12, 78.03) * mm, "end": v(27.73, 78.2) * mm});
            skLineSegment(sketch, "E455", {"start": v(27.73, 78.2) * mm, "end": v(28.34, 78.37) * mm});
            skLineSegment(sketch, "E456", {"start": v(28.34, 78.37) * mm, "end": v(28.96, 78.51) * mm});
            skLineSegment(sketch, "E457", {"start": v(28.96, 78.51) * mm, "end": v(30.22, 78.75) * mm});
            skLineSegment(sketch, "E458", {"start": v(30.22, 78.75) * mm, "end": v(31.48, 78.94) * mm});
            skLineSegment(sketch, "E459", {"start": v(31.48, 78.94) * mm, "end": v(32.75, 79.08) * mm});
            skLineSegment(sketch, "E460", {"start": v(32.75, 79.08) * mm, "end": v(34.02, 79.17) * mm});
            skLineSegment(sketch, "E461", {"start": v(34.02, 79.17) * mm, "end": v(35.27, 79.22) * mm});
            skLineSegment(sketch, "E462", {"start": v(35.27, 79.22) * mm, "end": v(36.5, 79.22) * mm});
            skLineSegment(sketch, "E463", {"start": v(36.5, 79.22) * mm, "end": v(37.7, 79.2) * mm});
            skLineSegment(sketch, "E464", {"start": v(37.7, 79.2) * mm, "end": v(38.88, 79.13) * mm});
            skLineSegment(sketch, "E465", {"start": v(39, 61.98) * mm, "end": v(36.07, 63) * mm});
            skLineSegment(sketch, "E466", {"start": v(36.07, 63) * mm, "end": v(34.6, 63.5) * mm});
            skLineSegment(sketch, "E467", {"start": v(34.6, 63.5) * mm, "end": v(33.13, 63.97) * mm});
            skLineSegment(sketch, "E468", {"start": v(33.13, 63.97) * mm, "end": v(31.64, 64.4) * mm});
            skLineSegment(sketch, "E469", {"start": v(31.64, 64.4) * mm, "end": v(30.88, 64.58) * mm});
            skLineSegment(sketch, "E470", {"start": v(30.88, 64.58) * mm, "end": v(30.12, 64.74) * mm});
            skLineSegment(sketch, "E471", {"start": v(30.12, 64.74) * mm, "end": v(28.6, 65.02) * mm});
            skLineSegment(sketch, "E472", {"start": v(28.6, 65.02) * mm, "end": v(27.06, 65.25) * mm});
            skLineSegment(sketch, "E473", {"start": v(27.06, 65.25) * mm, "end": v(23.99, 65.66) * mm});
            skLineSegment(sketch, "E474", {"start": v(23.99, 65.66) * mm, "end": v(23.22, 65.78) * mm});
            skLineSegment(sketch, "E475", {"start": v(23.22, 65.78) * mm, "end": v(23.03, 65.8) * mm});
            skLineSegment(sketch, "E476", {"start": v(23.03, 65.8) * mm, "end": v(22.98, 65.81) * mm});
            skLineSegment(sketch, "E477", {"start": v(22.98, 65.81) * mm, "end": v(22.97, 65.82) * mm});
            skLineSegment(sketch, "E478", {"start": v(22.97, 65.82) * mm, "end": v(22.98, 65.82) * mm});
            skLineSegment(sketch, "E479", {"start": v(22.98, 65.82) * mm, "end": v(23.02, 65.84) * mm});
            skLineSegment(sketch, "E480", {"start": v(23.02, 65.84) * mm, "end": v(23.2, 65.92) * mm});
            skLineSegment(sketch, "E481", {"start": v(23.2, 65.92) * mm, "end": v(23.97, 66.2) * mm});
            skLineSegment(sketch, "E482", {"start": v(23.97, 66.2) * mm, "end": v(24.74, 66.43) * mm});
            skLineSegment(sketch, "E483", {"start": v(24.74, 66.43) * mm, "end": v(25.54, 66.6) * mm});
            skLineSegment(sketch, "E484", {"start": v(25.54, 66.6) * mm, "end": v(26.35, 66.73) * mm});
            skLineSegment(sketch, "E485", {"start": v(26.35, 66.73) * mm, "end": v(27.17, 66.8) * mm});
            skLineSegment(sketch, "E486", {"start": v(27.17, 66.8) * mm, "end": v(28, 66.84) * mm});
            skLineSegment(sketch, "E487", {"start": v(28, 66.84) * mm, "end": v(28.83, 66.82) * mm});
            skLineSegment(sketch, "E488", {"start": v(28.83, 66.82) * mm, "end": v(29.66, 66.75) * mm});
            skLineSegment(sketch, "E489", {"start": v(29.66, 66.75) * mm, "end": v(30.5, 66.64) * mm});
            skLineSegment(sketch, "E490", {"start": v(30.5, 66.64) * mm, "end": v(31.31, 66.49) * mm});
            skLineSegment(sketch, "E491", {"start": v(31.31, 66.49) * mm, "end": v(32.13, 66.28) * mm});
            skLineSegment(sketch, "E492", {"start": v(32.13, 66.28) * mm, "end": v(32.93, 66.04) * mm});
            skLineSegment(sketch, "E493", {"start": v(32.93, 66.04) * mm, "end": v(33.72, 65.75) * mm});
            skLineSegment(sketch, "E494", {"start": v(33.72, 65.75) * mm, "end": v(34.48, 65.42) * mm});
            skLineSegment(sketch, "E495", {"start": v(34.48, 65.42) * mm, "end": v(35.22, 65.05) * mm});
            skLineSegment(sketch, "E496", {"start": v(35.22, 65.05) * mm, "end": v(35.94, 64.64) * mm});
            skLineSegment(sketch, "E497", {"start": v(35.94, 64.64) * mm, "end": v(36.63, 64.18) * mm});
            skLineSegment(sketch, "E498", {"start": v(36.63, 64.18) * mm, "end": v(37.28, 63.69) * mm});
            skLineSegment(sketch, "E499", {"start": v(37.28, 63.69) * mm, "end": v(37.9, 63.16) * mm});
            skLineSegment(sketch, "E500", {"start": v(37.9, 63.16) * mm, "end": v(38.47, 62.59) * mm});
            skLineSegment(sketch, "E501", {"start": v(38.47, 62.59) * mm, "end": v(39, 61.98) * mm});
            skLineSegment(sketch, "E502", {"start": v(32.98, 49.8) * mm, "end": v(32.06, 50.93) * mm});
            skLineSegment(sketch, "E503", {"start": v(32.06, 50.93) * mm, "end": v(31.16, 52.06) * mm});
            skLineSegment(sketch, "E504", {"start": v(31.16, 52.06) * mm, "end": v(30.26, 53.2) * mm});
            skLineSegment(sketch, "E505", {"start": v(30.26, 53.2) * mm, "end": v(29.34, 54.3) * mm});
            skLineSegment(sketch, "E506", {"start": v(29.34, 54.3) * mm, "end": v(28.37, 55.4) * mm});
            skLineSegment(sketch, "E507", {"start": v(28.37, 55.4) * mm, "end": v(27.36, 56.44) * mm});
            skLineSegment(sketch, "E508", {"start": v(27.36, 56.44) * mm, "end": v(26.3, 57.43) * mm});
            skLineSegment(sketch, "E509", {"start": v(26.3, 57.43) * mm, "end": v(25.22, 58.4) * mm});
            skLineSegment(sketch, "E510", {"start": v(25.22, 58.4) * mm, "end": v(23.04, 60.3) * mm});
            skLineSegment(sketch, "E511", {"start": v(23.04, 60.3) * mm, "end": v(22.5, 60.78) * mm});
            skLineSegment(sketch, "E512", {"start": v(22.5, 60.78) * mm, "end": v(22.36, 60.9) * mm});
            skLineSegment(sketch, "E513", {"start": v(22.36, 60.9) * mm, "end": v(22.33, 60.93) * mm});
            skLineSegment(sketch, "E514", {"start": v(22.33, 60.93) * mm, "end": v(22.32, 60.94) * mm});
            skLineSegment(sketch, "E515", {"start": v(22.32, 60.94) * mm, "end": v(22.33, 60.94) * mm});
            skLineSegment(sketch, "E516", {"start": v(22.33, 60.94) * mm, "end": v(22.38, 60.93) * mm});
            skLineSegment(sketch, "E517", {"start": v(22.38, 60.93) * mm, "end": v(22.56, 60.9) * mm});
            skLineSegment(sketch, "E518", {"start": v(22.56, 60.9) * mm, "end": v(23.3, 60.75) * mm});
            skLineSegment(sketch, "E519", {"start": v(23.3, 60.75) * mm, "end": v(24.04, 60.54) * mm});
            skLineSegment(sketch, "E520", {"start": v(24.04, 60.54) * mm, "end": v(24.76, 60.29) * mm});
            skLineSegment(sketch, "E521", {"start": v(24.76, 60.29) * mm, "end": v(25.46, 59.99) * mm});
            skLineSegment(sketch, "E522", {"start": v(25.46, 59.99) * mm, "end": v(26.15, 59.64) * mm});
            skLineSegment(sketch, "E523", {"start": v(26.15, 59.64) * mm, "end": v(26.82, 59.24) * mm});
            skLineSegment(sketch, "E524", {"start": v(26.82, 59.24) * mm, "end": v(27.47, 58.8) * mm});
            skLineSegment(sketch, "E525", {"start": v(27.47, 58.8) * mm, "end": v(28.1, 58.34) * mm});
            skLineSegment(sketch, "E526", {"start": v(28.1, 58.34) * mm, "end": v(28.7, 57.83) * mm});
            skLineSegment(sketch, "E527", {"start": v(28.7, 57.83) * mm, "end": v(29.27, 57.29) * mm});
            skLineSegment(sketch, "E528", {"start": v(29.27, 57.29) * mm, "end": v(29.8, 56.71) * mm});
            skLineSegment(sketch, "E529", {"start": v(29.8, 56.71) * mm, "end": v(30.31, 56.11) * mm});
            skLineSegment(sketch, "E530", {"start": v(30.31, 56.11) * mm, "end": v(30.78, 55.48) * mm});
            skLineSegment(sketch, "E531", {"start": v(30.78, 55.48) * mm, "end": v(31.22, 54.83) * mm});
            skLineSegment(sketch, "E532", {"start": v(31.22, 54.83) * mm, "end": v(31.61, 54.16) * mm});
            skLineSegment(sketch, "E533", {"start": v(31.61, 54.16) * mm, "end": v(31.96, 53.46) * mm});
            skLineSegment(sketch, "E534", {"start": v(31.96, 53.46) * mm, "end": v(32.26, 52.76) * mm});
            skLineSegment(sketch, "E535", {"start": v(32.26, 52.76) * mm, "end": v(32.52, 52.03) * mm});
            skLineSegment(sketch, "E536", {"start": v(32.52, 52.03) * mm, "end": v(32.73, 51.3) * mm});
            skLineSegment(sketch, "E537", {"start": v(32.73, 51.3) * mm, "end": v(32.88, 50.56) * mm});
            skLineSegment(sketch, "E538", {"start": v(32.88, 50.56) * mm, "end": v(32.98, 49.8) * mm});
            skLineSegment(sketch, "E539", {"start": v(22.61, 35.03) * mm, "end": v(22.69, 34.22) * mm});
            skLineSegment(sketch, "E540", {"start": v(22.69, 34.22) * mm, "end": v(22.72, 33.4) * mm});
            skLineSegment(sketch, "E541", {"start": v(22.72, 33.4) * mm, "end": v(22.72, 32.6) * mm});
            skLineSegment(sketch, "E542", {"start": v(22.72, 32.6) * mm, "end": v(22.69, 31.8) * mm});
            skLineSegment(sketch, "E543", {"start": v(22.69, 31.8) * mm, "end": v(22.61, 31) * mm});
            skLineSegment(sketch, "E544", {"start": v(22.61, 31) * mm, "end": v(22.5, 30.22) * mm});
            skLineSegment(sketch, "E545", {"start": v(22.5, 30.22) * mm, "end": v(22.36, 29.44) * mm});
            skLineSegment(sketch, "E546", {"start": v(22.36, 29.44) * mm, "end": v(22.17, 28.67) * mm});
            skLineSegment(sketch, "E547", {"start": v(22.17, 28.67) * mm, "end": v(21.95, 27.91) * mm});
            skLineSegment(sketch, "E548", {"start": v(21.95, 27.91) * mm, "end": v(21.7, 27.17) * mm});
            skLineSegment(sketch, "E549", {"start": v(21.7, 27.17) * mm, "end": v(21.4, 26.43) * mm});
            skLineSegment(sketch, "E550", {"start": v(21.4, 26.43) * mm, "end": v(21.06, 25.71) * mm});
            skLineSegment(sketch, "E551", {"start": v(21.06, 25.71) * mm, "end": v(20.68, 25) * mm});
            skLineSegment(sketch, "E552", {"start": v(20.68, 25) * mm, "end": v(20.27, 24.32) * mm});
            skLineSegment(sketch, "E553", {"start": v(20.27, 24.32) * mm, "end": v(19.82, 23.64) * mm});
            skLineSegment(sketch, "E554", {"start": v(19.82, 23.64) * mm, "end": v(19.33, 22.99) * mm});
            skLineSegment(sketch, "E555", {"start": v(19.33, 22.99) * mm, "end": v(19.85, 24.37) * mm});
            skLineSegment(sketch, "E556", {"start": v(19.85, 24.37) * mm, "end": v(20.29, 25.75) * mm});
            skLineSegment(sketch, "E557", {"start": v(20.29, 25.75) * mm, "end": v(20.64, 27.14) * mm});
            skLineSegment(sketch, "E558", {"start": v(20.64, 27.14) * mm, "end": v(20.9, 28.53) * mm});
            skLineSegment(sketch, "E559", {"start": v(20.9, 28.53) * mm, "end": v(21.07, 29.95) * mm});
            skLineSegment(sketch, "E560", {"start": v(21.07, 29.95) * mm, "end": v(21.14, 31.38) * mm});
            skLineSegment(sketch, "E561", {"start": v(21.14, 31.38) * mm, "end": v(21.13, 32.1) * mm});
            skLineSegment(sketch, "E562", {"start": v(21.13, 32.1) * mm, "end": v(21.1, 32.83) * mm});
            skLineSegment(sketch, "E563", {"start": v(21.1, 32.83) * mm, "end": v(21.03, 33.56) * mm});
            skLineSegment(sketch, "E564", {"start": v(21.03, 33.56) * mm, "end": v(20.93, 34.3) * mm});
            skLineSegment(sketch, "E565", {"start": v(20.93, 34.3) * mm, "end": v(20.8, 35.1) * mm});
            skLineSegment(sketch, "E566", {"start": v(20.8, 35.1) * mm, "end": v(20.63, 35.9) * mm});
            skLineSegment(sketch, "E567", {"start": v(20.63, 35.9) * mm, "end": v(20.23, 37.46) * mm});
            skLineSegment(sketch, "E568", {"start": v(20.23, 37.46) * mm, "end": v(19.75, 39) * mm});
            skLineSegment(sketch, "E569", {"start": v(19.75, 39) * mm, "end": v(19.21, 40.52) * mm});
            skLineSegment(sketch, "E570", {"start": v(19.21, 40.52) * mm, "end": v(18.06, 43.55) * mm});
            skLineSegment(sketch, "E571", {"start": v(18.06, 43.55) * mm, "end": v(17.5, 45.06) * mm});
            skLineSegment(sketch, "E572", {"start": v(17.5, 45.06) * mm, "end": v(16.97, 46.59) * mm});
            skLineSegment(sketch, "E573", {"start": v(16.97, 46.59) * mm, "end": v(17.6, 46.09) * mm});
            skLineSegment(sketch, "E574", {"start": v(17.6, 46.09) * mm, "end": v(18.2, 45.54) * mm});
            skLineSegment(sketch, "E575", {"start": v(18.2, 45.54) * mm, "end": v(18.75, 44.94) * mm});
            skLineSegment(sketch, "E576", {"start": v(18.75, 44.94) * mm, "end": v(19.26, 44.3) * mm});
            skLineSegment(sketch, "E577", {"start": v(19.26, 44.3) * mm, "end": v(19.74, 43.62) * mm});
            skLineSegment(sketch, "E578", {"start": v(19.74, 43.62) * mm, "end": v(20.17, 42.9) * mm});
            skLineSegment(sketch, "E579", {"start": v(20.17, 42.9) * mm, "end": v(20.57, 42.17) * mm});
            skLineSegment(sketch, "E580", {"start": v(20.57, 42.17) * mm, "end": v(20.93, 41.4) * mm});
            skLineSegment(sketch, "E581", {"start": v(20.93, 41.4) * mm, "end": v(21.26, 40.63) * mm});
            skLineSegment(sketch, "E582", {"start": v(21.26, 40.63) * mm, "end": v(21.55, 39.83) * mm});
            skLineSegment(sketch, "E583", {"start": v(21.55, 39.83) * mm, "end": v(21.8, 39.03) * mm});
            skLineSegment(sketch, "E584", {"start": v(21.8, 39.03) * mm, "end": v(22.03, 38.22) * mm});
            skLineSegment(sketch, "E585", {"start": v(22.03, 38.22) * mm, "end": v(22.22, 37.41) * mm});
            skLineSegment(sketch, "E586", {"start": v(22.22, 37.41) * mm, "end": v(22.38, 36.6) * mm});
            skLineSegment(sketch, "E587", {"start": v(22.38, 36.6) * mm, "end": v(22.51, 35.81) * mm});
            skLineSegment(sketch, "E588", {"start": v(22.51, 35.81) * mm, "end": v(22.61, 35.03) * mm});
            skLineSegment(sketch, "E589", {"start": v(6.42, 56.73) * mm, "end": v(7.1, 56.6) * mm});
            skLineSegment(sketch, "E590", {"start": v(7.1, 56.6) * mm, "end": v(7.74, 56.44) * mm});
            skLineSegment(sketch, "E591", {"start": v(7.74, 56.44) * mm, "end": v(8.36, 56.22) * mm});
            skLineSegment(sketch, "E592", {"start": v(8.36, 56.22) * mm, "end": v(8.96, 55.95) * mm});
            skLineSegment(sketch, "E593", {"start": v(8.96, 55.95) * mm, "end": v(9.53, 55.63) * mm});
            skLineSegment(sketch, "E594", {"start": v(9.53, 55.63) * mm, "end": v(10.08, 55.27) * mm});
            skLineSegment(sketch, "E595", {"start": v(10.08, 55.27) * mm, "end": v(10.59, 54.87) * mm});
            skLineSegment(sketch, "E596", {"start": v(10.59, 54.87) * mm, "end": v(11.07, 54.43) * mm});
            skLineSegment(sketch, "E597", {"start": v(11.07, 54.43) * mm, "end": v(11.5, 53.96) * mm});
            skLineSegment(sketch, "E598", {"start": v(11.5, 53.96) * mm, "end": v(11.9, 53.44) * mm});
            skLineSegment(sketch, "E599", {"start": v(11.9, 53.44) * mm, "end": v(12.27, 52.9) * mm});
            skLineSegment(sketch, "E600", {"start": v(12.27, 52.9) * mm, "end": v(12.58, 52.33) * mm});
            skLineSegment(sketch, "E601", {"start": v(12.58, 52.33) * mm, "end": v(12.85, 51.73) * mm});
            skLineSegment(sketch, "E602", {"start": v(12.85, 51.73) * mm, "end": v(13.07, 51.1) * mm});
            skLineSegment(sketch, "E603", {"start": v(13.07, 51.1) * mm, "end": v(13.24, 50.46) * mm});
            skLineSegment(sketch, "E604", {"start": v(13.24, 50.46) * mm, "end": v(13.36, 49.8) * mm});
            skLineSegment(sketch, "E605", {"start": v(13.36, 49.8) * mm, "end": v(12.65, 49.83) * mm});
            skLineSegment(sketch, "E606", {"start": v(12.65, 49.83) * mm, "end": v(11.97, 49.94) * mm});
            skLineSegment(sketch, "E607", {"start": v(11.97, 49.94) * mm, "end": v(11.3, 50.12) * mm});
            skLineSegment(sketch, "E608", {"start": v(11.3, 50.12) * mm, "end": v(10.68, 50.36) * mm});
            skLineSegment(sketch, "E609", {"start": v(10.68, 50.36) * mm, "end": v(10.07, 50.65) * mm});
            skLineSegment(sketch, "E610", {"start": v(10.07, 50.65) * mm, "end": v(9.5, 51) * mm});
            skLineSegment(sketch, "E611", {"start": v(9.5, 51) * mm, "end": v(8.97, 51.4) * mm});
            skLineSegment(sketch, "E612", {"start": v(8.97, 51.4) * mm, "end": v(8.48, 51.85) * mm});
            skLineSegment(sketch, "E613", {"start": v(8.48, 51.85) * mm, "end": v(8.03, 52.34) * mm});
            skLineSegment(sketch, "E614", {"start": v(8.03, 52.34) * mm, "end": v(7.63, 52.87) * mm});
            skLineSegment(sketch, "E615", {"start": v(7.63, 52.87) * mm, "end": v(7.28, 53.44) * mm});
            skLineSegment(sketch, "E616", {"start": v(7.28, 53.44) * mm, "end": v(7, 54.04) * mm});
            skLineSegment(sketch, "E617", {"start": v(7, 54.04) * mm, "end": v(6.75, 54.68) * mm});
            skLineSegment(sketch, "E618", {"start": v(6.75, 54.68) * mm, "end": v(6.58, 55.34) * mm});
            skLineSegment(sketch, "E619", {"start": v(6.58, 55.34) * mm, "end": v(6.47, 56.02) * mm});
            skLineSegment(sketch, "E620", {"start": v(6.47, 56.02) * mm, "end": v(6.42, 56.73) * mm});
            skLineSegment(sketch, "E621", {"start": v(6.42, 40.72) * mm, "end": v(6.47, 41.43) * mm});
            skLineSegment(sketch, "E622", {"start": v(6.47, 41.43) * mm, "end": v(6.58, 42.11) * mm});
            skLineSegment(sketch, "E623", {"start": v(6.58, 42.11) * mm, "end": v(6.75, 42.77) * mm});
            skLineSegment(sketch, "E624", {"start": v(6.75, 42.77) * mm, "end": v(6.99, 43.4) * mm});
            skLineSegment(sketch, "E625", {"start": v(6.99, 43.4) * mm, "end": v(7.28, 44) * mm});
            skLineSegment(sketch, "E626", {"start": v(7.28, 44) * mm, "end": v(7.63, 44.58) * mm});
            skLineSegment(sketch, "E627", {"start": v(7.63, 44.58) * mm, "end": v(8.03, 45.1) * mm});
            skLineSegment(sketch, "E628", {"start": v(8.03, 45.1) * mm, "end": v(8.48, 45.6) * mm});
            skLineSegment(sketch, "E629", {"start": v(8.48, 45.6) * mm, "end": v(8.97, 46.05) * mm});
            skLineSegment(sketch, "E630", {"start": v(8.97, 46.05) * mm, "end": v(9.5, 46.45) * mm});
            skLineSegment(sketch, "E631", {"start": v(9.5, 46.45) * mm, "end": v(10.07, 46.8) * mm});
            skLineSegment(sketch, "E632", {"start": v(10.07, 46.8) * mm, "end": v(10.68, 47.1) * mm});
            skLineSegment(sketch, "E633", {"start": v(10.68, 47.1) * mm, "end": v(11.3, 47.33) * mm});
            skLineSegment(sketch, "E634", {"start": v(11.3, 47.33) * mm, "end": v(11.97, 47.5) * mm});
            skLineSegment(sketch, "E635", {"start": v(11.97, 47.5) * mm, "end": v(12.65, 47.61) * mm});
            skLineSegment(sketch, "E636", {"start": v(12.65, 47.61) * mm, "end": v(13.36, 47.66) * mm});
            skLineSegment(sketch, "E637", {"start": v(13.36, 47.66) * mm, "end": v(13.24, 46.99) * mm});
            skLineSegment(sketch, "E638", {"start": v(13.24, 46.99) * mm, "end": v(13.07, 46.34) * mm});
            skLineSegment(sketch, "E639", {"start": v(13.07, 46.34) * mm, "end": v(12.85, 45.72) * mm});
            skLineSegment(sketch, "E640", {"start": v(12.85, 45.72) * mm, "end": v(12.58, 45.12) * mm});
            skLineSegment(sketch, "E641", {"start": v(12.58, 45.12) * mm, "end": v(12.27, 44.55) * mm});
            skLineSegment(sketch, "E642", {"start": v(12.27, 44.55) * mm, "end": v(11.9, 44) * mm});
            skLineSegment(sketch, "E643", {"start": v(11.9, 44) * mm, "end": v(11.5, 43.5) * mm});
            skLineSegment(sketch, "E644", {"start": v(11.5, 43.5) * mm, "end": v(11.07, 43.01) * mm});
            skLineSegment(sketch, "E645", {"start": v(11.07, 43.01) * mm, "end": v(10.59, 42.57) * mm});
            skLineSegment(sketch, "E646", {"start": v(10.59, 42.57) * mm, "end": v(10.08, 42.17) * mm});
            skLineSegment(sketch, "E647", {"start": v(10.08, 42.17) * mm, "end": v(9.53, 41.81) * mm});
            skLineSegment(sketch, "E648", {"start": v(9.53, 41.81) * mm, "end": v(8.96, 41.5) * mm});
            skLineSegment(sketch, "E649", {"start": v(8.96, 41.5) * mm, "end": v(8.36, 41.23) * mm});
            skLineSegment(sketch, "E650", {"start": v(8.36, 41.23) * mm, "end": v(7.74, 41) * mm});
            skLineSegment(sketch, "E651", {"start": v(7.74, 41) * mm, "end": v(7.1, 40.84) * mm});
            skLineSegment(sketch, "E652", {"start": v(7.1, 40.84) * mm, "end": v(6.42, 40.72) * mm});
            skLineSegment(sketch, "E653", {"start": v(5.36, 44.9) * mm, "end": v(4.63, 46.07) * mm});
            skLineSegment(sketch, "E654", {"start": v(4.63, 46.07) * mm, "end": v(3.74, 47.1) * mm});
            skLineSegment(sketch, "E655", {"start": v(3.74, 47.1) * mm, "end": v(2.7, 48) * mm});
            skLineSegment(sketch, "E656", {"start": v(2.7, 48) * mm, "end": v(1.54, 48.72) * mm});
            skLineSegment(sketch, "E657", {"start": v(1.54, 48.72) * mm, "end": v(2.7, 49.45) * mm});
            skLineSegment(sketch, "E658", {"start": v(2.7, 49.45) * mm, "end": v(3.74, 50.34) * mm});
            skLineSegment(sketch, "E659", {"start": v(3.74, 50.34) * mm, "end": v(4.63, 51.38) * mm});
            skLineSegment(sketch, "E660", {"start": v(4.63, 51.38) * mm, "end": v(5.36, 52.54) * mm});
            skLineSegment(sketch, "E661", {"start": v(5.36, 52.54) * mm, "end": v(6.09, 51.38) * mm});
            skLineSegment(sketch, "E662", {"start": v(6.09, 51.38) * mm, "end": v(6.98, 50.34) * mm});
            skLineSegment(sketch, "E663", {"start": v(6.98, 50.34) * mm, "end": v(8.01, 49.45) * mm});
            skLineSegment(sketch, "E664", {"start": v(8.01, 49.45) * mm, "end": v(9.17, 48.72) * mm});
            skLineSegment(sketch, "E665", {"start": v(9.17, 48.72) * mm, "end": v(8.01, 48) * mm});
            skLineSegment(sketch, "E666", {"start": v(8.01, 48) * mm, "end": v(6.98, 47.1) * mm});
            skLineSegment(sketch, "E667", {"start": v(6.98, 47.1) * mm, "end": v(6.09, 46.07) * mm});
            skLineSegment(sketch, "E668", {"start": v(6.09, 46.07) * mm, "end": v(5.36, 44.9) * mm});
            skLineSegment(sketch, "E669", {"start": v(-2.65, 47.66) * mm, "end": v(-1.94, 47.61) * mm});
            skLineSegment(sketch, "E670", {"start": v(-1.94, 47.61) * mm, "end": v(-1.26, 47.5) * mm});
            skLineSegment(sketch, "E671", {"start": v(-1.26, 47.5) * mm, "end": v(-0.6, 47.33) * mm});
            skLineSegment(sketch, "E672", {"start": v(-0.6, 47.33) * mm, "end": v(0.04, 47.1) * mm});
            skLineSegment(sketch, "E673", {"start": v(0.04, 47.1) * mm, "end": v(0.64, 46.8) * mm});
            skLineSegment(sketch, "E674", {"start": v(0.64, 46.8) * mm, "end": v(1.21, 46.45) * mm});
            skLineSegment(sketch, "E675", {"start": v(1.21, 46.45) * mm, "end": v(1.74, 46.05) * mm});
            skLineSegment(sketch, "E676", {"start": v(1.74, 46.05) * mm, "end": v(2.23, 45.6) * mm});
            skLineSegment(sketch, "E677", {"start": v(2.23, 45.6) * mm, "end": v(2.68, 45.1) * mm});
            skLineSegment(sketch, "E678", {"start": v(2.68, 45.1) * mm, "end": v(3.08, 44.58) * mm});
            skLineSegment(sketch, "E679", {"start": v(3.08, 44.58) * mm, "end": v(3.43, 44) * mm});
            skLineSegment(sketch, "E680", {"start": v(3.43, 44) * mm, "end": v(3.72, 43.4) * mm});
            skLineSegment(sketch, "E681", {"start": v(3.72, 43.4) * mm, "end": v(3.96, 42.77) * mm});
            skLineSegment(sketch, "E682", {"start": v(3.96, 42.77) * mm, "end": v(4.14, 42.11) * mm});
            skLineSegment(sketch, "E683", {"start": v(4.14, 42.11) * mm, "end": v(4.25, 41.43) * mm});
            skLineSegment(sketch, "E684", {"start": v(4.25, 41.43) * mm, "end": v(4.3, 40.72) * mm});
            skLineSegment(sketch, "E685", {"start": v(4.3, 40.72) * mm, "end": v(3.62, 40.84) * mm});
            skLineSegment(sketch, "E686", {"start": v(3.62, 40.84) * mm, "end": v(2.98, 41) * mm});
            skLineSegment(sketch, "E687", {"start": v(2.98, 41) * mm, "end": v(2.35, 41.23) * mm});
            skLineSegment(sketch, "E688", {"start": v(2.35, 41.23) * mm, "end": v(1.75, 41.5) * mm});
            skLineSegment(sketch, "E689", {"start": v(1.75, 41.5) * mm, "end": v(1.18, 41.81) * mm});
            skLineSegment(sketch, "E690", {"start": v(1.18, 41.81) * mm, "end": v(0.64, 42.17) * mm});
            skLineSegment(sketch, "E691", {"start": v(0.64, 42.17) * mm, "end": v(0.13, 42.58) * mm});
            skLineSegment(sketch, "E692", {"start": v(0.13, 42.58) * mm, "end": v(-0.35, 43.02) * mm});
            skLineSegment(sketch, "E693", {"start": v(-0.35, 43.02) * mm, "end": v(-0.8, 43.5) * mm});
            skLineSegment(sketch, "E694", {"start": v(-0.8, 43.5) * mm, "end": v(-1.2, 44) * mm});
            skLineSegment(sketch, "E695", {"start": v(-1.2, 44) * mm, "end": v(-1.55, 44.55) * mm});
            skLineSegment(sketch, "E696", {"start": v(-1.55, 44.55) * mm, "end": v(-1.87, 45.12) * mm});
            skLineSegment(sketch, "E697", {"start": v(-1.87, 45.12) * mm, "end": v(-2.14, 45.72) * mm});
            skLineSegment(sketch, "E698", {"start": v(-2.14, 45.72) * mm, "end": v(-2.36, 46.34) * mm});
            skLineSegment(sketch, "E699", {"start": v(-2.36, 46.34) * mm, "end": v(-2.53, 46.99) * mm});
            skLineSegment(sketch, "E700", {"start": v(-2.53, 46.99) * mm, "end": v(-2.65, 47.66) * mm});
            skLineSegment(sketch, "E701", {"start": v(-7.86, 26.04) * mm, "end": v(-10.21, 25.73) * mm});
            skLineSegment(sketch, "E702", {"start": v(-10.21, 25.73) * mm, "end": v(-9.65, 25.99) * mm});
            skLineSegment(sketch, "E703", {"start": v(-9.65, 25.99) * mm, "end": v(-9.08, 26.27) * mm});
            skLineSegment(sketch, "E704", {"start": v(-9.08, 26.27) * mm, "end": v(-7.9, 26.89) * mm});
            skLineSegment(sketch, "E705", {"start": v(-7.9, 26.89) * mm, "end": v(-6.73, 27.5) * mm});
            skLineSegment(sketch, "E706", {"start": v(-6.73, 27.5) * mm, "end": v(-6.15, 27.79) * mm});
            skLineSegment(sketch, "E707", {"start": v(-6.15, 27.79) * mm, "end": v(-5.6, 28.04) * mm});
            skLineSegment(sketch, "E708", {"start": v(-5.6, 28.04) * mm, "end": v(-6.08, 28.02) * mm});
            skLineSegment(sketch, "E709", {"start": v(-6.08, 28.02) * mm, "end": v(-6.6, 28.02) * mm});
            skLineSegment(sketch, "E710", {"start": v(-6.6, 28.02) * mm, "end": v(-7.68, 28.06) * mm});
            skLineSegment(sketch, "E711", {"start": v(-7.68, 28.06) * mm, "end": v(-8.76, 28.1) * mm});
            skLineSegment(sketch, "E712", {"start": v(-8.76, 28.1) * mm, "end": v(-9.28, 28.1) * mm});
            skLineSegment(sketch, "E713", {"start": v(-9.28, 28.1) * mm, "end": v(-9.77, 28.07) * mm});
            skLineSegment(sketch, "E714", {"start": v(-9.77, 28.07) * mm, "end": v(-9.08, 28.3) * mm});
            skLineSegment(sketch, "E715", {"start": v(-9.08, 28.3) * mm, "end": v(-8.43, 28.54) * mm});
            skLineSegment(sketch, "E716", {"start": v(-8.43, 28.54) * mm, "end": v(-7.81, 28.78) * mm});
            skLineSegment(sketch, "E717", {"start": v(-7.81, 28.78) * mm, "end": v(-7.22, 29.04) * mm});
            skLineSegment(sketch, "E718", {"start": v(-7.22, 29.04) * mm, "end": v(-6.1, 29.54) * mm});
            skLineSegment(sketch, "E719", {"start": v(-6.1, 29.54) * mm, "end": v(-5, 30.02) * mm});
            skLineSegment(sketch, "E720", {"start": v(-5, 30.02) * mm, "end": v(-5.3, 30.06) * mm});
            skLineSegment(sketch, "E721", {"start": v(-5.3, 30.06) * mm, "end": v(-5.58, 30.1) * mm});
            skLineSegment(sketch, "E722", {"start": v(-5.58, 30.1) * mm, "end": v(-6.1, 30.18) * mm});
            skLineSegment(sketch, "E723", {"start": v(-6.1, 30.18) * mm, "end": v(-6.57, 30.25) * mm});
            skLineSegment(sketch, "E724", {"start": v(-6.57, 30.25) * mm, "end": v(-7.02, 30.32) * mm});
            skLineSegment(sketch, "E725", {"start": v(-7.02, 30.32) * mm, "end": v(-7.47, 30.39) * mm});
            skLineSegment(sketch, "E726", {"start": v(-7.47, 30.39) * mm, "end": v(-7.95, 30.47) * mm});
            skLineSegment(sketch, "E727", {"start": v(-7.95, 30.47) * mm, "end": v(-8.47, 30.55) * mm});
            skLineSegment(sketch, "E728", {"start": v(-8.47, 30.55) * mm, "end": v(-8.76, 30.6) * mm});
            skLineSegment(sketch, "E729", {"start": v(-8.76, 30.6) * mm, "end": v(-9.06, 30.65) * mm});
            skLineSegment(sketch, "E730", {"start": v(-9.06, 30.65) * mm, "end": v(-8.51, 30.81) * mm});
            skLineSegment(sketch, "E731", {"start": v(-8.51, 30.81) * mm, "end": v(-8, 30.98) * mm});
            skLineSegment(sketch, "E732", {"start": v(-8, 30.98) * mm, "end": v(-7.05, 31.32) * mm});
            skLineSegment(sketch, "E733", {"start": v(-7.05, 31.32) * mm, "end": v(-6.58, 31.5) * mm});
            skLineSegment(sketch, "E734", {"start": v(-6.58, 31.5) * mm, "end": v(-6.1, 31.7) * mm});
            skLineSegment(sketch, "E735", {"start": v(-6.1, 31.7) * mm, "end": v(-5.58, 31.9) * mm});
            skLineSegment(sketch, "E736", {"start": v(-5.58, 31.9) * mm, "end": v(-5.01, 32.1) * mm});
            skLineSegment(sketch, "E737", {"start": v(-5.01, 32.1) * mm, "end": v(-5.35, 32.14) * mm});
            skLineSegment(sketch, "E738", {"start": v(-5.35, 32.14) * mm, "end": v(-5.65, 32.19) * mm});
            skLineSegment(sketch, "E739", {"start": v(-5.65, 32.19) * mm, "end": v(-5.92, 32.24) * mm});
            skLineSegment(sketch, "E740", {"start": v(-5.92, 32.24) * mm, "end": v(-6.16, 32.29) * mm});
            skLineSegment(sketch, "E741", {"start": v(-6.16, 32.29) * mm, "end": v(-6.58, 32.4) * mm});
            skLineSegment(sketch, "E742", {"start": v(-6.58, 32.4) * mm, "end": v(-6.95, 32.5) * mm});
            skLineSegment(sketch, "E743", {"start": v(-6.95, 32.5) * mm, "end": v(-7.32, 32.6) * mm});
            skLineSegment(sketch, "E744", {"start": v(-7.32, 32.6) * mm, "end": v(-7.73, 32.69) * mm});
            skLineSegment(sketch, "E745", {"start": v(-7.73, 32.69) * mm, "end": v(-7.96, 32.73) * mm});
            skLineSegment(sketch, "E746", {"start": v(-7.96, 32.73) * mm, "end": v(-8.22, 32.77) * mm});
            skLineSegment(sketch, "E747", {"start": v(-8.22, 32.77) * mm, "end": v(-8.5, 32.8) * mm});
            skLineSegment(sketch, "E748", {"start": v(-8.5, 32.8) * mm, "end": v(-8.82, 32.83) * mm});
            skLineSegment(sketch, "E749", {"start": v(-8.82, 32.83) * mm, "end": v(-8.52, 32.95) * mm});
            skLineSegment(sketch, "E750", {"start": v(-8.52, 32.95) * mm, "end": v(-8.25, 33.06) * mm});
            skLineSegment(sketch, "E751", {"start": v(-8.25, 33.06) * mm, "end": v(-8, 33.16) * mm});
            skLineSegment(sketch, "E752", {"start": v(-8, 33.16) * mm, "end": v(-7.79, 33.26) * mm});
            skLineSegment(sketch, "E753", {"start": v(-7.79, 33.26) * mm, "end": v(-7.4, 33.44) * mm});
            skLineSegment(sketch, "E754", {"start": v(-7.4, 33.44) * mm, "end": v(-7.04, 33.61) * mm});
            skLineSegment(sketch, "E755", {"start": v(-7.04, 33.61) * mm, "end": v(-6.68, 33.79) * mm});
            skLineSegment(sketch, "E756", {"start": v(-6.68, 33.79) * mm, "end": v(-6.3, 33.97) * mm});
            skLineSegment(sketch, "E757", {"start": v(-6.3, 33.97) * mm, "end": v(-6.07, 34.07) * mm});
            skLineSegment(sketch, "E758", {"start": v(-6.07, 34.07) * mm, "end": v(-5.83, 34.17) * mm});
            skLineSegment(sketch, "E759", {"start": v(-5.83, 34.17) * mm, "end": v(-5.56, 34.28) * mm});
            skLineSegment(sketch, "E760", {"start": v(-5.56, 34.28) * mm, "end": v(-5.26, 34.4) * mm});
            skLineSegment(sketch, "E761", {"start": v(-5.26, 34.4) * mm, "end": v(-5.63, 34.43) * mm});
            skLineSegment(sketch, "E762", {"start": v(-5.63, 34.43) * mm, "end": v(-5.97, 34.46) * mm});
            skLineSegment(sketch, "E763", {"start": v(-5.97, 34.46) * mm, "end": v(-6.3, 34.48) * mm});
            skLineSegment(sketch, "E764", {"start": v(-6.3, 34.48) * mm, "end": v(-6.59, 34.51) * mm});
            skLineSegment(sketch, "E765", {"start": v(-6.59, 34.51) * mm, "end": v(-7.13, 34.57) * mm});
            skLineSegment(sketch, "E766", {"start": v(-7.13, 34.57) * mm, "end": v(-7.63, 34.63) * mm});
            skLineSegment(sketch, "E767", {"start": v(-7.63, 34.63) * mm, "end": v(-8.12, 34.7) * mm});
            skLineSegment(sketch, "E768", {"start": v(-8.12, 34.7) * mm, "end": v(-8.63, 34.76) * mm});
            skLineSegment(sketch, "E769", {"start": v(-8.63, 34.76) * mm, "end": v(-9.2, 34.82) * mm});
            skLineSegment(sketch, "E770", {"start": v(-9.2, 34.82) * mm, "end": v(-9.5, 34.85) * mm});
            skLineSegment(sketch, "E771", {"start": v(-9.5, 34.85) * mm, "end": v(-9.84, 34.89) * mm});
            skLineSegment(sketch, "E772", {"start": v(-9.84, 34.89) * mm, "end": v(-9.53, 35) * mm});
            skLineSegment(sketch, "E773", {"start": v(-9.53, 35) * mm, "end": v(-9.26, 35.12) * mm});
            skLineSegment(sketch, "E774", {"start": v(-9.26, 35.12) * mm, "end": v(-9, 35.22) * mm});
            skLineSegment(sketch, "E775", {"start": v(-9, 35.22) * mm, "end": v(-8.77, 35.32) * mm});
            skLineSegment(sketch, "E776", {"start": v(-8.77, 35.32) * mm, "end": v(-8.33, 35.51) * mm});
            skLineSegment(sketch, "E777", {"start": v(-8.33, 35.51) * mm, "end": v(-7.93, 35.69) * mm});
            skLineSegment(sketch, "E778", {"start": v(-7.93, 35.69) * mm, "end": v(-7.52, 35.86) * mm});
            skLineSegment(sketch, "E779", {"start": v(-7.52, 35.86) * mm, "end": v(-7.08, 36.05) * mm});
            skLineSegment(sketch, "E780", {"start": v(-7.08, 36.05) * mm, "end": v(-6.85, 36.14) * mm});
            skLineSegment(sketch, "E781", {"start": v(-6.85, 36.14) * mm, "end": v(-6.59, 36.25) * mm});
            skLineSegment(sketch, "E782", {"start": v(-6.59, 36.25) * mm, "end": v(-6.31, 36.35) * mm});
            skLineSegment(sketch, "E783", {"start": v(-6.31, 36.35) * mm, "end": v(-6, 36.47) * mm});
            skLineSegment(sketch, "E784", {"start": v(-6, 36.47) * mm, "end": v(-6.36, 36.49) * mm});
            skLineSegment(sketch, "E785", {"start": v(-6.36, 36.49) * mm, "end": v(-6.68, 36.5) * mm});
            skLineSegment(sketch, "E786", {"start": v(-6.68, 36.5) * mm, "end": v(-7.29, 36.55) * mm});
            skLineSegment(sketch, "E787", {"start": v(-7.29, 36.55) * mm, "end": v(-7.85, 36.6) * mm});
            skLineSegment(sketch, "E788", {"start": v(-7.85, 36.6) * mm, "end": v(-8.39, 36.66) * mm});
            skLineSegment(sketch, "E789", {"start": v(-8.39, 36.66) * mm, "end": v(-8.93, 36.73) * mm});
            skLineSegment(sketch, "E790", {"start": v(-8.93, 36.73) * mm, "end": v(-9.5, 36.8) * mm});
            skLineSegment(sketch, "E791", {"start": v(-9.5, 36.8) * mm, "end": v(-9.82, 36.84) * mm});
            skLineSegment(sketch, "E792", {"start": v(-9.82, 36.84) * mm, "end": v(-10.15, 36.88) * mm});
            skLineSegment(sketch, "E793", {"start": v(-10.15, 36.88) * mm, "end": v(-10.5, 36.92) * mm});
            skLineSegment(sketch, "E794", {"start": v(-10.5, 36.92) * mm, "end": v(-10.88, 36.96) * mm});
            skLineSegment(sketch, "E795", {"start": v(-10.88, 36.96) * mm, "end": v(-10.52, 37.1) * mm});
            skLineSegment(sketch, "E796", {"start": v(-10.52, 37.1) * mm, "end": v(-10.2, 37.22) * mm});
            skLineSegment(sketch, "E797", {"start": v(-10.2, 37.22) * mm, "end": v(-9.92, 37.34) * mm});
            skLineSegment(sketch, "E798", {"start": v(-9.92, 37.34) * mm, "end": v(-9.65, 37.45) * mm});
            skLineSegment(sketch, "E799", {"start": v(-9.65, 37.45) * mm, "end": v(-9.18, 37.65) * mm});
            skLineSegment(sketch, "E800", {"start": v(-9.18, 37.65) * mm, "end": v(-8.74, 37.84) * mm});
            skLineSegment(sketch, "E801", {"start": v(-8.74, 37.84) * mm, "end": v(-8.32, 38.01) * mm});
            skLineSegment(sketch, "E802", {"start": v(-8.32, 38.01) * mm, "end": v(-7.87, 38.2) * mm});
            skLineSegment(sketch, "E803", {"start": v(-7.87, 38.2) * mm, "end": v(-7.62, 38.3) * mm});
            skLineSegment(sketch, "E804", {"start": v(-7.62, 38.3) * mm, "end": v(-7.36, 38.4) * mm});
            skLineSegment(sketch, "E805", {"start": v(-7.36, 38.4) * mm, "end": v(-7.07, 38.5) * mm});
            skLineSegment(sketch, "E806", {"start": v(-7.07, 38.5) * mm, "end": v(-6.75, 38.62) * mm});
            skLineSegment(sketch, "E807", {"start": v(-6.75, 38.62) * mm, "end": v(-8.1, 38.85) * mm});
            skLineSegment(sketch, "E808", {"start": v(-8.1, 38.85) * mm, "end": v(-9.41, 39.08) * mm});
            skLineSegment(sketch, "E809", {"start": v(-9.41, 39.08) * mm, "end": v(-10.73, 39.3) * mm});
            skLineSegment(sketch, "E810", {"start": v(-10.73, 39.3) * mm, "end": v(-12.08, 39.54) * mm});
            skLineSegment(sketch, "E811", {"start": v(-12.08, 39.54) * mm, "end": v(-11.7, 39.7) * mm});
            skLineSegment(sketch, "E812", {"start": v(-11.7, 39.7) * mm, "end": v(-11.32, 39.84) * mm});
            skLineSegment(sketch, "E813", {"start": v(-11.32, 39.84) * mm, "end": v(-10.92, 39.97) * mm});
            skLineSegment(sketch, "E814", {"start": v(-10.92, 39.97) * mm, "end": v(-10.51, 40.08) * mm});
            skLineSegment(sketch, "E815", {"start": v(-10.51, 40.08) * mm, "end": v(-10.1, 40.16) * mm});
            skLineSegment(sketch, "E816", {"start": v(-10.1, 40.16) * mm, "end": v(-9.68, 40.21) * mm});
            skLineSegment(sketch, "E817", {"start": v(-9.68, 40.21) * mm, "end": v(-9.27, 40.23) * mm});
            skLineSegment(sketch, "E818", {"start": v(-9.27, 40.23) * mm, "end": v(-8.86, 40.21) * mm});
            skLineSegment(sketch, "E819", {"start": v(-8.86, 40.21) * mm, "end": v(-8.36, 40.14) * mm});
            skLineSegment(sketch, "E820", {"start": v(-8.36, 40.14) * mm, "end": v(-7.87, 40.04) * mm});
            skLineSegment(sketch, "E821", {"start": v(-7.87, 40.04) * mm, "end": v(-7.4, 39.9) * mm});
            skLineSegment(sketch, "E822", {"start": v(-7.4, 39.9) * mm, "end": v(-6.93, 39.71) * mm});
            skLineSegment(sketch, "E823", {"start": v(-6.93, 39.71) * mm, "end": v(-6.5, 39.5) * mm});
            skLineSegment(sketch, "E824", {"start": v(-6.5, 39.5) * mm, "end": v(-6.07, 39.25) * mm});
            skLineSegment(sketch, "E825", {"start": v(-6.07, 39.25) * mm, "end": v(-5.66, 38.98) * mm});
            skLineSegment(sketch, "E826", {"start": v(-5.66, 38.98) * mm, "end": v(-5.28, 38.67) * mm});
            skLineSegment(sketch, "E827", {"start": v(-5.28, 38.67) * mm, "end": v(-4.92, 38.33) * mm});
            skLineSegment(sketch, "E828", {"start": v(-4.92, 38.33) * mm, "end": v(-4.58, 37.96) * mm});
            skLineSegment(sketch, "E829", {"start": v(-4.58, 37.96) * mm, "end": v(-4.26, 37.57) * mm});
            skLineSegment(sketch, "E830", {"start": v(-4.26, 37.57) * mm, "end": v(-3.97, 37.15) * mm});
            skLineSegment(sketch, "E831", {"start": v(-3.97, 37.15) * mm, "end": v(-3.7, 36.7) * mm});
            skLineSegment(sketch, "E832", {"start": v(-3.7, 36.7) * mm, "end": v(-3.47, 36.23) * mm});
            skLineSegment(sketch, "E833", {"start": v(-3.47, 36.23) * mm, "end": v(-3.26, 35.74) * mm});
            skLineSegment(sketch, "E834", {"start": v(-3.26, 35.74) * mm, "end": v(-3.08, 35.23) * mm});
            skLineSegment(sketch, "E835", {"start": v(-3.08, 35.23) * mm, "end": v(-2.97, 34.87) * mm});
            skLineSegment(sketch, "E836", {"start": v(-2.97, 34.87) * mm, "end": v(-2.89, 34.5) * mm});
            skLineSegment(sketch, "E837", {"start": v(-2.89, 34.5) * mm, "end": v(-2.82, 34.13) * mm});
            skLineSegment(sketch, "E838", {"start": v(-2.82, 34.13) * mm, "end": v(-2.77, 33.75) * mm});
            skLineSegment(sketch, "E839", {"start": v(-2.77, 33.75) * mm, "end": v(-2.72, 33) * mm});
            skLineSegment(sketch, "E840", {"start": v(-2.72, 33) * mm, "end": v(-2.75, 32.25) * mm});
            skLineSegment(sketch, "E841", {"start": v(-2.75, 32.25) * mm, "end": v(-2.84, 31.5) * mm});
            skLineSegment(sketch, "E842", {"start": v(-2.84, 31.5) * mm, "end": v(-3, 30.78) * mm});
            skLineSegment(sketch, "E843", {"start": v(-3, 30.78) * mm, "end": v(-3.22, 30.07) * mm});
            skLineSegment(sketch, "E844", {"start": v(-3.22, 30.07) * mm, "end": v(-3.5, 29.4) * mm});
            skLineSegment(sketch, "E845", {"start": v(-3.5, 29.4) * mm, "end": v(-3.68, 29.08) * mm});
            skLineSegment(sketch, "E846", {"start": v(-3.68, 29.08) * mm, "end": v(-3.86, 28.77) * mm});
            skLineSegment(sketch, "E847", {"start": v(-3.86, 28.77) * mm, "end": v(-4.05, 28.47) * mm});
            skLineSegment(sketch, "E848", {"start": v(-4.05, 28.47) * mm, "end": v(-4.27, 28.18) * mm});
            skLineSegment(sketch, "E849", {"start": v(-4.27, 28.18) * mm, "end": v(-4.5, 27.9) * mm});
            skLineSegment(sketch, "E850", {"start": v(-4.5, 27.9) * mm, "end": v(-4.73, 27.64) * mm});
            skLineSegment(sketch, "E851", {"start": v(-4.73, 27.64) * mm, "end": v(-4.98, 27.4) * mm});
            skLineSegment(sketch, "E852", {"start": v(-4.98, 27.4) * mm, "end": v(-5.25, 27.17) * mm});
            skLineSegment(sketch, "E853", {"start": v(-5.25, 27.17) * mm, "end": v(-5.53, 26.96) * mm});
            skLineSegment(sketch, "E854", {"start": v(-5.53, 26.96) * mm, "end": v(-5.83, 26.77) * mm});
            skLineSegment(sketch, "E855", {"start": v(-5.83, 26.77) * mm, "end": v(-6.14, 26.6) * mm});
            skLineSegment(sketch, "E856", {"start": v(-6.14, 26.6) * mm, "end": v(-6.46, 26.44) * mm});
            skLineSegment(sketch, "E857", {"start": v(-6.46, 26.44) * mm, "end": v(-6.79, 26.3) * mm});
            skLineSegment(sketch, "E858", {"start": v(-6.79, 26.3) * mm, "end": v(-7.13, 26.2) * mm});
            skLineSegment(sketch, "E859", {"start": v(-7.13, 26.2) * mm, "end": v(-7.5, 26.1) * mm});
            skLineSegment(sketch, "E860", {"start": v(-7.5, 26.1) * mm, "end": v(-7.86, 26.04) * mm});
            skLineSegment(sketch, "E861", {"start": v(-14.45, 20.89) * mm, "end": v(-14.66, 20.54) * mm});
            skLineSegment(sketch, "E862", {"start": v(-14.66, 20.54) * mm, "end": v(-14.9, 20.22) * mm});
            skLineSegment(sketch, "E863", {"start": v(-14.9, 20.22) * mm, "end": v(-15.14, 19.9) * mm});
            skLineSegment(sketch, "E864", {"start": v(-15.14, 19.9) * mm, "end": v(-15.4, 19.6) * mm});
            skLineSegment(sketch, "E865", {"start": v(-15.4, 19.6) * mm, "end": v(-15.68, 19.3) * mm});
            skLineSegment(sketch, "E866", {"start": v(-15.68, 19.3) * mm, "end": v(-15.97, 19.03) * mm});
            skLineSegment(sketch, "E867", {"start": v(-15.97, 19.03) * mm, "end": v(-16.27, 18.76) * mm});
            skLineSegment(sketch, "E868", {"start": v(-16.27, 18.76) * mm, "end": v(-16.59, 18.51) * mm});
            skLineSegment(sketch, "E869", {"start": v(-16.59, 18.51) * mm, "end": v(-16.9, 18.28) * mm});
            skLineSegment(sketch, "E870", {"start": v(-16.9, 18.28) * mm, "end": v(-17.24, 18.06) * mm});
            skLineSegment(sketch, "E871", {"start": v(-17.24, 18.06) * mm, "end": v(-17.58, 17.86) * mm});
            skLineSegment(sketch, "E872", {"start": v(-17.58, 17.86) * mm, "end": v(-17.93, 17.68) * mm});
            skLineSegment(sketch, "E873", {"start": v(-17.93, 17.68) * mm, "end": v(-18.29, 17.5) * mm});
            skLineSegment(sketch, "E874", {"start": v(-18.29, 17.5) * mm, "end": v(-18.65, 17.36) * mm});
            skLineSegment(sketch, "E875", {"start": v(-18.65, 17.36) * mm, "end": v(-19.01, 17.22) * mm});
            skLineSegment(sketch, "E876", {"start": v(-19.01, 17.22) * mm, "end": v(-19.38, 17.1) * mm});
            skLineSegment(sketch, "E877", {"start": v(-19.38, 17.1) * mm, "end": v(-19.76, 17.01) * mm});
            skLineSegment(sketch, "E878", {"start": v(-19.76, 17.01) * mm, "end": v(-20.13, 16.94) * mm});
            skLineSegment(sketch, "E879", {"start": v(-20.13, 16.94) * mm, "end": v(-20.51, 16.88) * mm});
            skLineSegment(sketch, "E880", {"start": v(-20.51, 16.88) * mm, "end": v(-20.89, 16.85) * mm});
            skLineSegment(sketch, "E881", {"start": v(-20.89, 16.85) * mm, "end": v(-21.27, 16.83) * mm});
            skLineSegment(sketch, "E882", {"start": v(-21.27, 16.83) * mm, "end": v(-21.64, 16.84) * mm});
            skLineSegment(sketch, "E883", {"start": v(-21.64, 16.84) * mm, "end": v(-22.02, 16.87) * mm});
            skLineSegment(sketch, "E884", {"start": v(-22.02, 16.87) * mm, "end": v(-22.39, 16.92) * mm});
            skLineSegment(sketch, "E885", {"start": v(-22.39, 16.92) * mm, "end": v(-22.75, 17) * mm});
            skLineSegment(sketch, "E886", {"start": v(-22.75, 17) * mm, "end": v(-23.11, 17.09) * mm});
            skLineSegment(sketch, "E887", {"start": v(-23.11, 17.09) * mm, "end": v(-23.47, 17.21) * mm});
            skLineSegment(sketch, "E888", {"start": v(-23.47, 17.21) * mm, "end": v(-23.82, 17.36) * mm});
            skLineSegment(sketch, "E889", {"start": v(-23.82, 17.36) * mm, "end": v(-24.16, 17.53) * mm});
            skLineSegment(sketch, "E890", {"start": v(-24.16, 17.53) * mm, "end": v(-24.5, 17.72) * mm});
            skLineSegment(sketch, "E891", {"start": v(-24.5, 17.72) * mm, "end": v(-24.82, 17.94) * mm});
            skLineSegment(sketch, "E892", {"start": v(-24.82, 17.94) * mm, "end": v(-25.13, 18.2) * mm});
            skLineSegment(sketch, "E893", {"start": v(-25.13, 18.2) * mm, "end": v(-27.03, 19.84) * mm});
            skLineSegment(sketch, "E894", {"start": v(-27.03, 19.84) * mm, "end": v(-26.43, 19.58) * mm});
            skLineSegment(sketch, "E895", {"start": v(-26.43, 19.58) * mm, "end": v(-25.8, 19.32) * mm});
            skLineSegment(sketch, "E896", {"start": v(-25.8, 19.32) * mm, "end": v(-24.48, 18.82) * mm});
            skLineSegment(sketch, "E897", {"start": v(-24.48, 18.82) * mm, "end": v(-23.16, 18.33) * mm});
            skLineSegment(sketch, "E898", {"start": v(-23.16, 18.33) * mm, "end": v(-22.53, 18.07) * mm});
            skLineSegment(sketch, "E899", {"start": v(-22.53, 18.07) * mm, "end": v(-21.93, 17.8) * mm});
            skLineSegment(sketch, "E900", {"start": v(-21.93, 17.8) * mm, "end": v(-22.3, 18.17) * mm});
            skLineSegment(sketch, "E901", {"start": v(-22.3, 18.17) * mm, "end": v(-22.66, 18.58) * mm});
            skLineSegment(sketch, "E902", {"start": v(-22.66, 18.58) * mm, "end": v(-23.4, 19.47) * mm});
            skLineSegment(sketch, "E903", {"start": v(-23.4, 19.47) * mm, "end": v(-24.13, 20.36) * mm});
            skLineSegment(sketch, "E904", {"start": v(-24.13, 20.36) * mm, "end": v(-24.5, 20.77) * mm});
            skLineSegment(sketch, "E905", {"start": v(-24.5, 20.77) * mm, "end": v(-24.86, 21.14) * mm});
            skLineSegment(sketch, "E906", {"start": v(-24.86, 21.14) * mm, "end": v(-24.2, 20.75) * mm});
            skLineSegment(sketch, "E907", {"start": v(-24.2, 20.75) * mm, "end": v(-23.54, 20.4) * mm});
            skLineSegment(sketch, "E908", {"start": v(-23.54, 20.4) * mm, "end": v(-22.91, 20.1) * mm});
            skLineSegment(sketch, "E909", {"start": v(-22.91, 20.1) * mm, "end": v(-22.3, 19.8) * mm});
            skLineSegment(sketch, "E910", {"start": v(-22.3, 19.8) * mm, "end": v(-21.1, 19.26) * mm});
            skLineSegment(sketch, "E911", {"start": v(-21.1, 19.26) * mm, "end": v(-19.94, 18.73) * mm});
            skLineSegment(sketch, "E912", {"start": v(-19.94, 18.73) * mm, "end": v(-20.12, 19) * mm});
            skLineSegment(sketch, "E913", {"start": v(-20.12, 19) * mm, "end": v(-20.3, 19.25) * mm});
            skLineSegment(sketch, "E914", {"start": v(-20.3, 19.25) * mm, "end": v(-20.6, 19.72) * mm});
            skLineSegment(sketch, "E915", {"start": v(-20.6, 19.72) * mm, "end": v(-20.88, 20.14) * mm});
            skLineSegment(sketch, "E916", {"start": v(-20.88, 20.14) * mm, "end": v(-21.14, 20.54) * mm});
            skLineSegment(sketch, "E917", {"start": v(-21.14, 20.54) * mm, "end": v(-21.4, 20.95) * mm});
            skLineSegment(sketch, "E918", {"start": v(-21.4, 20.95) * mm, "end": v(-21.67, 21.39) * mm});
            skLineSegment(sketch, "E919", {"start": v(-21.67, 21.39) * mm, "end": v(-21.97, 21.86) * mm});
            skLineSegment(sketch, "E920", {"start": v(-21.97, 21.86) * mm, "end": v(-22.14, 22.12) * mm});
            skLineSegment(sketch, "E921", {"start": v(-22.14, 22.12) * mm, "end": v(-22.31, 22.4) * mm});
            skLineSegment(sketch, "E922", {"start": v(-22.31, 22.4) * mm, "end": v(-21.8, 22.08) * mm});
            skLineSegment(sketch, "E923", {"start": v(-21.8, 22.08) * mm, "end": v(-21.3, 21.8) * mm});
            skLineSegment(sketch, "E924", {"start": v(-21.3, 21.8) * mm, "end": v(-20.36, 21.28) * mm});
            skLineSegment(sketch, "E925", {"start": v(-20.36, 21.28) * mm, "end": v(-19.88, 21.04) * mm});
            skLineSegment(sketch, "E926", {"start": v(-19.88, 21.04) * mm, "end": v(-19.39, 20.78) * mm});
            skLineSegment(sketch, "E927", {"start": v(-19.39, 20.78) * mm, "end": v(-18.87, 20.51) * mm});
            skLineSegment(sketch, "E928", {"start": v(-18.87, 20.51) * mm, "end": v(-18.3, 20.21) * mm});
            skLineSegment(sketch, "E929", {"start": v(-18.3, 20.21) * mm, "end": v(-18.5, 20.5) * mm});
            skLineSegment(sketch, "E930", {"start": v(-18.5, 20.5) * mm, "end": v(-18.68, 20.78) * mm});
            skLineSegment(sketch, "E931", {"start": v(-18.68, 20.78) * mm, "end": v(-18.83, 21.02) * mm});
            skLineSegment(sketch, "E932", {"start": v(-18.83, 21.02) * mm, "end": v(-18.96, 21.25) * mm});
            skLineSegment(sketch, "E933", {"start": v(-18.96, 21.25) * mm, "end": v(-19.07, 21.46) * mm});
            skLineSegment(sketch, "E934", {"start": v(-19.07, 21.46) * mm, "end": v(-19.18, 21.66) * mm});
            skLineSegment(sketch, "E935", {"start": v(-19.18, 21.66) * mm, "end": v(-19.36, 22.03) * mm});
            skLineSegment(sketch, "E936", {"start": v(-19.36, 22.03) * mm, "end": v(-19.54, 22.4) * mm});
            skLineSegment(sketch, "E937", {"start": v(-19.54, 22.4) * mm, "end": v(-19.75, 22.78) * mm});
            skLineSegment(sketch, "E938", {"start": v(-19.75, 22.78) * mm, "end": v(-19.88, 23) * mm});
            skLineSegment(sketch, "E939", {"start": v(-19.88, 23) * mm, "end": v(-20.04, 23.23) * mm});
            skLineSegment(sketch, "E940", {"start": v(-20.04, 23.23) * mm, "end": v(-20.21, 23.47) * mm});
            skLineSegment(sketch, "E941", {"start": v(-20.21, 23.47) * mm, "end": v(-20.41, 23.75) * mm});
            skLineSegment(sketch, "E942", {"start": v(-20.41, 23.75) * mm, "end": v(-20.1, 23.6) * mm});
            skLineSegment(sketch, "E943", {"start": v(-20.1, 23.6) * mm, "end": v(-19.83, 23.46) * mm});
            skLineSegment(sketch, "E944", {"start": v(-19.83, 23.46) * mm, "end": v(-19.57, 23.34) * mm});
            skLineSegment(sketch, "E945", {"start": v(-19.57, 23.34) * mm, "end": v(-19.34, 23.23) * mm});
            skLineSegment(sketch, "E946", {"start": v(-19.34, 23.23) * mm, "end": v(-18.92, 23.05) * mm});
            skLineSegment(sketch, "E947", {"start": v(-18.92, 23.05) * mm, "end": v(-18.53, 22.89) * mm});
            skLineSegment(sketch, "E948", {"start": v(-18.53, 22.89) * mm, "end": v(-18.14, 22.73) * mm});
            skLineSegment(sketch, "E949", {"start": v(-18.14, 22.73) * mm, "end": v(-17.72, 22.54) * mm});
            skLineSegment(sketch, "E950", {"start": v(-17.72, 22.54) * mm, "end": v(-17.49, 22.44) * mm});
            skLineSegment(sketch, "E951", {"start": v(-17.49, 22.44) * mm, "end": v(-17.23, 22.32) * mm});
            skLineSegment(sketch, "E952", {"start": v(-17.23, 22.32) * mm, "end": v(-16.96, 22.18) * mm});
            skLineSegment(sketch, "E953", {"start": v(-16.96, 22.18) * mm, "end": v(-16.65, 22.03) * mm});
            skLineSegment(sketch, "E954", {"start": v(-16.65, 22.03) * mm, "end": v(-16.89, 22.34) * mm});
            skLineSegment(sketch, "E955", {"start": v(-16.89, 22.34) * mm, "end": v(-17.11, 22.63) * mm});
            skLineSegment(sketch, "E956", {"start": v(-17.11, 22.63) * mm, "end": v(-17.31, 22.9) * mm});
            skLineSegment(sketch, "E957", {"start": v(-17.31, 22.9) * mm, "end": v(-17.5, 23.16) * mm});
            skLineSegment(sketch, "E958", {"start": v(-17.5, 23.16) * mm, "end": v(-17.83, 23.63) * mm});
            skLineSegment(sketch, "E959", {"start": v(-17.83, 23.63) * mm, "end": v(-18.14, 24.07) * mm});
            skLineSegment(sketch, "E960", {"start": v(-18.14, 24.07) * mm, "end": v(-18.44, 24.5) * mm});
            skLineSegment(sketch, "E961", {"start": v(-18.44, 24.5) * mm, "end": v(-18.75, 24.96) * mm});
            skLineSegment(sketch, "E962", {"start": v(-18.75, 24.96) * mm, "end": v(-18.91, 25.2) * mm});
            skLineSegment(sketch, "E963", {"start": v(-18.91, 25.2) * mm, "end": v(-19.1, 25.45) * mm});
            skLineSegment(sketch, "E964", {"start": v(-19.1, 25.45) * mm, "end": v(-19.29, 25.72) * mm});
            skLineSegment(sketch, "E965", {"start": v(-19.29, 25.72) * mm, "end": v(-19.5, 26) * mm});
            skLineSegment(sketch, "E966", {"start": v(-19.5, 26) * mm, "end": v(-19.19, 25.85) * mm});
            skLineSegment(sketch, "E967", {"start": v(-19.19, 25.85) * mm, "end": v(-18.9, 25.71) * mm});
            skLineSegment(sketch, "E968", {"start": v(-18.9, 25.71) * mm, "end": v(-18.64, 25.58) * mm});
            skLineSegment(sketch, "E969", {"start": v(-18.64, 25.58) * mm, "end": v(-18.4, 25.46) * mm});
            skLineSegment(sketch, "E970", {"start": v(-18.4, 25.46) * mm, "end": v(-17.94, 25.25) * mm});
            skLineSegment(sketch, "E971", {"start": v(-17.94, 25.25) * mm, "end": v(-17.5, 25.06) * mm});
            skLineSegment(sketch, "E972", {"start": v(-17.5, 25.06) * mm, "end": v(-17.08, 24.86) * mm});
            skLineSegment(sketch, "E973", {"start": v(-17.08, 24.86) * mm, "end": v(-16.63, 24.64) * mm});
            skLineSegment(sketch, "E974", {"start": v(-16.63, 24.64) * mm, "end": v(-16.39, 24.52) * mm});
            skLineSegment(sketch, "E975", {"start": v(-16.39, 24.52) * mm, "end": v(-16.12, 24.39) * mm});
            skLineSegment(sketch, "E976", {"start": v(-16.12, 24.39) * mm, "end": v(-15.84, 24.24) * mm});
            skLineSegment(sketch, "E977", {"start": v(-15.84, 24.24) * mm, "end": v(-15.53, 24.08) * mm});
            skLineSegment(sketch, "E978", {"start": v(-15.53, 24.08) * mm, "end": v(-15.77, 24.37) * mm});
            skLineSegment(sketch, "E979", {"start": v(-15.77, 24.37) * mm, "end": v(-15.99, 24.65) * mm});
            skLineSegment(sketch, "E980", {"start": v(-15.99, 24.65) * mm, "end": v(-16.38, 25.16) * mm});
            skLineSegment(sketch, "E981", {"start": v(-16.38, 25.16) * mm, "end": v(-16.73, 25.64) * mm});
            skLineSegment(sketch, "E982", {"start": v(-16.73, 25.64) * mm, "end": v(-17.06, 26.1) * mm});
            skLineSegment(sketch, "E983", {"start": v(-17.06, 26.1) * mm, "end": v(-17.4, 26.59) * mm});
            skLineSegment(sketch, "E984", {"start": v(-17.4, 26.59) * mm, "end": v(-17.74, 27.1) * mm});
            skLineSegment(sketch, "E985", {"start": v(-17.74, 27.1) * mm, "end": v(-17.93, 27.37) * mm});
            skLineSegment(sketch, "E986", {"start": v(-17.93, 27.37) * mm, "end": v(-18.13, 27.66) * mm});
            skLineSegment(sketch, "E987", {"start": v(-18.13, 27.66) * mm, "end": v(-18.35, 27.97) * mm});
            skLineSegment(sketch, "E988", {"start": v(-18.35, 27.97) * mm, "end": v(-18.58, 28.3) * mm});
            skLineSegment(sketch, "E989", {"start": v(-18.58, 28.3) * mm, "end": v(-18.23, 28.11) * mm});
            skLineSegment(sketch, "E990", {"start": v(-18.23, 28.11) * mm, "end": v(-17.9, 27.95) * mm});
            skLineSegment(sketch, "E991", {"start": v(-17.9, 27.95) * mm, "end": v(-17.6, 27.8) * mm});
            skLineSegment(sketch, "E992", {"start": v(-17.6, 27.8) * mm, "end": v(-17.33, 27.67) * mm});
            skLineSegment(sketch, "E993", {"start": v(-17.33, 27.67) * mm, "end": v(-17.07, 27.55) * mm});
            skLineSegment(sketch, "E994", {"start": v(-17.07, 27.55) * mm, "end": v(-16.83, 27.43) * mm});
            skLineSegment(sketch, "E995", {"start": v(-16.83, 27.43) * mm, "end": v(-16.38, 27.22) * mm});
            skLineSegment(sketch, "E996", {"start": v(-16.38, 27.22) * mm, "end": v(-15.94, 27.01) * mm});
            skLineSegment(sketch, "E997", {"start": v(-15.94, 27.01) * mm, "end": v(-15.48, 26.78) * mm});
            skLineSegment(sketch, "E998", {"start": v(-15.48, 26.78) * mm, "end": v(-15.23, 26.65) * mm});
            skLineSegment(sketch, "E999", {"start": v(-15.23, 26.65) * mm, "end": v(-14.96, 26.51) * mm});
            skLineSegment(sketch, "E1000", {"start": v(-14.96, 26.51) * mm, "end": v(-14.67, 26.36) * mm});
            skLineSegment(sketch, "E1001", {"start": v(-14.67, 26.36) * mm, "end": v(-14.35, 26.19) * mm});
            skLineSegment(sketch, "E1002", {"start": v(-14.35, 26.19) * mm, "end": v(-15.11, 27.42) * mm});
            skLineSegment(sketch, "E1003", {"start": v(-15.11, 27.42) * mm, "end": v(-15.87, 28.63) * mm});
            skLineSegment(sketch, "E1004", {"start": v(-15.87, 28.63) * mm, "end": v(-16.63, 29.83) * mm});
            skLineSegment(sketch, "E1005", {"start": v(-16.63, 29.83) * mm, "end": v(-17.39, 31.07) * mm});
            skLineSegment(sketch, "E1006", {"start": v(-17.39, 31.07) * mm, "end": v(-17, 30.89) * mm});
            skLineSegment(sketch, "E1007", {"start": v(-17, 30.89) * mm, "end": v(-16.6, 30.68) * mm});
            skLineSegment(sketch, "E1008", {"start": v(-16.6, 30.68) * mm, "end": v(-16.23, 30.45) * mm});
            skLineSegment(sketch, "E1009", {"start": v(-16.23, 30.45) * mm, "end": v(-15.85, 30.2) * mm});
            skLineSegment(sketch, "E1010", {"start": v(-15.85, 30.2) * mm, "end": v(-15.5, 29.94) * mm});
            skLineSegment(sketch, "E1011", {"start": v(-15.5, 29.94) * mm, "end": v(-15.16, 29.64) * mm});
            skLineSegment(sketch, "E1012", {"start": v(-15.16, 29.64) * mm, "end": v(-14.85, 29.33) * mm});
            skLineSegment(sketch, "E1013", {"start": v(-14.85, 29.33) * mm, "end": v(-14.58, 29) * mm});
            skLineSegment(sketch, "E1014", {"start": v(-14.58, 29) * mm, "end": v(-14.28, 28.54) * mm});
            skLineSegment(sketch, "E1015", {"start": v(-14.28, 28.54) * mm, "end": v(-14.01, 28.08) * mm});
            skLineSegment(sketch, "E1016", {"start": v(-14.01, 28.08) * mm, "end": v(-13.8, 27.6) * mm});
            skLineSegment(sketch, "E1017", {"start": v(-13.8, 27.6) * mm, "end": v(-13.61, 27.11) * mm});
            skLineSegment(sketch, "E1018", {"start": v(-13.61, 27.11) * mm, "end": v(-13.47, 26.6) * mm});
            skLineSegment(sketch, "E1019", {"start": v(-13.47, 26.6) * mm, "end": v(-13.37, 26.1) * mm});
            skLineSegment(sketch, "E1020", {"start": v(-13.37, 26.1) * mm, "end": v(-13.3, 25.58) * mm});
            skLineSegment(sketch, "E1021", {"start": v(-13.3, 25.58) * mm, "end": v(-13.28, 25.06) * mm});
            skLineSegment(sketch, "E1022", {"start": v(-13.28, 25.06) * mm, "end": v(-13.29, 24.53) * mm});
            skLineSegment(sketch, "E1023", {"start": v(-13.29, 24.53) * mm, "end": v(-13.34, 24) * mm});
            skLineSegment(sketch, "E1024", {"start": v(-13.34, 24) * mm, "end": v(-13.43, 23.47) * mm});
            skLineSegment(sketch, "E1025", {"start": v(-13.43, 23.47) * mm, "end": v(-13.56, 22.94) * mm});
            skLineSegment(sketch, "E1026", {"start": v(-13.56, 22.94) * mm, "end": v(-13.72, 22.42) * mm});
            skLineSegment(sketch, "E1027", {"start": v(-13.72, 22.42) * mm, "end": v(-13.93, 21.9) * mm});
            skLineSegment(sketch, "E1028", {"start": v(-13.93, 21.9) * mm, "end": v(-14.17, 21.39) * mm});
            skLineSegment(sketch, "E1029", {"start": v(-14.17, 21.39) * mm, "end": v(-14.45, 20.89) * mm});
            skLineSegment(sketch, "E1030", {"start": v(-25.36, -8.24) * mm, "end": v(-25.17, -6.81) * mm});
            skLineSegment(sketch, "E1031", {"start": v(-25.17, -6.81) * mm, "end": v(-24.92, -5.42) * mm});
            skLineSegment(sketch, "E1032", {"start": v(-24.92, -5.42) * mm, "end": v(-24.62, -4.06) * mm});
            skLineSegment(sketch, "E1033", {"start": v(-24.62, -4.06) * mm, "end": v(-24.28, -2.73) * mm});
            skLineSegment(sketch, "E1034", {"start": v(-24.28, -2.73) * mm, "end": v(-23.9, -1.43) * mm});
            skLineSegment(sketch, "E1035", {"start": v(-23.9, -1.43) * mm, "end": v(-23.8, -1.11) * mm});
            skLineSegment(sketch, "E1036", {"start": v(-23.8, -1.11) * mm, "end": v(-23.77, -1.03) * mm});
            skLineSegment(sketch, "E1037", {"start": v(-23.77, -1.03) * mm, "end": v(-23.75, -1.01) * mm});
            skLineSegment(sketch, "E1038", {"start": v(-23.75, -1.01) * mm, "end": v(-23.71, -1.04) * mm});
            skLineSegment(sketch, "E1039", {"start": v(-23.71, -1.04) * mm, "end": v(-23.58, -1.16) * mm});
            skLineSegment(sketch, "E1040", {"start": v(-23.58, -1.16) * mm, "end": v(-23.05, -1.64) * mm});
            skLineSegment(sketch, "E1041", {"start": v(-23.05, -1.64) * mm, "end": v(-22.03, -2.62) * mm});
            skLineSegment(sketch, "E1042", {"start": v(-22.03, -2.62) * mm, "end": v(-21.07, -3.63) * mm});
            skLineSegment(sketch, "E1043", {"start": v(-21.07, -3.63) * mm, "end": v(-20.18, -4.69) * mm});
            skLineSegment(sketch, "E1044", {"start": v(-20.18, -4.69) * mm, "end": v(-19.36, -5.79) * mm});
            skLineSegment(sketch, "E1045", {"start": v(-19.36, -5.79) * mm, "end": v(-18.98, -6.35) * mm});
            skLineSegment(sketch, "E1046", {"start": v(-18.98, -6.35) * mm, "end": v(-18.88, -6.5) * mm});
            skLineSegment(sketch, "E1047", {"start": v(-18.88, -6.5) * mm, "end": v(-18.86, -6.55) * mm});
            skLineSegment(sketch, "E1048", {"start": v(-18.86, -6.55) * mm, "end": v(-18.9, -6.57) * mm});
            skLineSegment(sketch, "E1049", {"start": v(-18.9, -6.57) * mm, "end": v(-19.02, -6.64) * mm});
            skLineSegment(sketch, "E1050", {"start": v(-19.02, -6.64) * mm, "end": v(-19.34, -6.8) * mm});
            skLineSegment(sketch, "E1051", {"start": v(-19.34, -6.8) * mm, "end": v(-19.72, -6.98) * mm});
            skLineSegment(sketch, "E1052", {"start": v(-19.72, -6.98) * mm, "end": v(-20.18, -7.18) * mm});
            skLineSegment(sketch, "E1053", {"start": v(-20.18, -7.18) * mm, "end": v(-20.7, -7.37) * mm});
            skLineSegment(sketch, "E1054", {"start": v(-20.7, -7.37) * mm, "end": v(-21.3, -7.56) * mm});
            skLineSegment(sketch, "E1055", {"start": v(-21.3, -7.56) * mm, "end": v(-21.97, -7.75) * mm});
            skLineSegment(sketch, "E1056", {"start": v(-21.97, -7.75) * mm, "end": v(-22.71, -7.91) * mm});
            skLineSegment(sketch, "E1057", {"start": v(-22.71, -7.91) * mm, "end": v(-23.53, -8.06) * mm});
            skLineSegment(sketch, "E1058", {"start": v(-23.53, -8.06) * mm, "end": v(-24.4, -8.17) * mm});
            skLineSegment(sketch, "E1059", {"start": v(-24.4, -8.17) * mm, "end": v(-25.36, -8.24) * mm});
            skLineSegment(sketch, "E1060", {"start": v(-21.27, -27.76) * mm, "end": v(-21.72, -27.6) * mm});
            skLineSegment(sketch, "E1061", {"start": v(-21.72, -27.6) * mm, "end": v(-22.16, -27.46) * mm});
            skLineSegment(sketch, "E1062", {"start": v(-22.16, -27.46) * mm, "end": v(-22.37, -27.4) * mm});
            skLineSegment(sketch, "E1063", {"start": v(-22.37, -27.4) * mm, "end": v(-22.58, -27.34) * mm});
            skLineSegment(sketch, "E1064", {"start": v(-22.58, -27.34) * mm, "end": v(-22.79, -27.3) * mm});
            skLineSegment(sketch, "E1065", {"start": v(-22.79, -27.3) * mm, "end": v(-22.99, -27.24) * mm});
            skLineSegment(sketch, "E1066", {"start": v(-22.99, -27.24) * mm, "end": v(-23.18, -27.2) * mm});
            skLineSegment(sketch, "E1067", {"start": v(-23.18, -27.2) * mm, "end": v(-23.37, -27.17) * mm});
            skLineSegment(sketch, "E1068", {"start": v(-23.37, -27.17) * mm, "end": v(-23.56, -27.14) * mm});
            skLineSegment(sketch, "E1069", {"start": v(-23.56, -27.14) * mm, "end": v(-23.74, -27.11) * mm});
            skLineSegment(sketch, "E1070", {"start": v(-23.74, -27.11) * mm, "end": v(-23.9, -27.09) * mm});
            skLineSegment(sketch, "E1071", {"start": v(-23.9, -27.09) * mm, "end": v(-24.07, -27.07) * mm});
            skLineSegment(sketch, "E1072", {"start": v(-24.07, -27.07) * mm, "end": v(-24.23, -27.06) * mm});
            skLineSegment(sketch, "E1073", {"start": v(-24.23, -27.06) * mm, "end": v(-24.38, -27.05) * mm});
            skLineSegment(sketch, "E1074", {"start": v(-24.38, -27.05) * mm, "end": v(-24.52, -27.05) * mm});
            skLineSegment(sketch, "E1075", {"start": v(-24.52, -27.05) * mm, "end": v(-24.65, -27.05) * mm});
            skLineSegment(sketch, "E1076", {"start": v(-24.65, -27.05) * mm, "end": v(-24.77, -27.06) * mm});
            skLineSegment(sketch, "E1077", {"start": v(-24.77, -27.06) * mm, "end": v(-24.88, -27.07) * mm});
            skLineSegment(sketch, "E1078", {"start": v(-24.88, -27.07) * mm, "end": v(-24.99, -27.09) * mm});
            skLineSegment(sketch, "E1079", {"start": v(-24.99, -27.09) * mm, "end": v(-25.01, -27.1) * mm});
            skLineSegment(sketch, "E1080", {"start": v(-25.01, -27.1) * mm, "end": v(-25.02, -27.1) * mm});
            skLineSegment(sketch, "E1081", {"start": v(-25.02, -27.1) * mm, "end": v(-25.02, -27.09) * mm});
            skLineSegment(sketch, "E1082", {"start": v(-25.02, -27.09) * mm, "end": v(-25.02, -27.08) * mm});
            skLineSegment(sketch, "E1083", {"start": v(-25.02, -27.08) * mm, "end": v(-25.03, -27.04) * mm});
            skLineSegment(sketch, "E1084", {"start": v(-25.03, -27.04) * mm, "end": v(-25.04, -26.96) * mm});
            skLineSegment(sketch, "E1085", {"start": v(-25.04, -26.96) * mm, "end": v(-25.05, -26.87) * mm});
            skLineSegment(sketch, "E1086", {"start": v(-25.05, -26.87) * mm, "end": v(-25.06, -26.77) * mm});
            skLineSegment(sketch, "E1087", {"start": v(-25.06, -26.77) * mm, "end": v(-25.07, -26.66) * mm});
            skLineSegment(sketch, "E1088", {"start": v(-25.07, -26.66) * mm, "end": v(-25.08, -26.54) * mm});
            skLineSegment(sketch, "E1089", {"start": v(-25.08, -26.54) * mm, "end": v(-25.1, -26.42) * mm});
            skLineSegment(sketch, "E1090", {"start": v(-25.1, -26.42) * mm, "end": v(-25.1, -26.29) * mm});
            skLineSegment(sketch, "E1091", {"start": v(-25.1, -26.29) * mm, "end": v(-25.11, -26.15) * mm});
            skLineSegment(sketch, "E1092", {"start": v(-25.11, -26.15) * mm, "end": v(-25.12, -26) * mm});
            skLineSegment(sketch, "E1093", {"start": v(-25.12, -26) * mm, "end": v(-25.13, -25.84) * mm});
            skLineSegment(sketch, "E1094", {"start": v(-25.13, -25.84) * mm, "end": v(-25.14, -25.68) * mm});
            skLineSegment(sketch, "E1095", {"start": v(-25.14, -25.68) * mm, "end": v(-25.15, -25.5) * mm});
            skLineSegment(sketch, "E1096", {"start": v(-25.15, -25.5) * mm, "end": v(-25.16, -25.15) * mm});
            skLineSegment(sketch, "E1097", {"start": v(-25.16, -25.15) * mm, "end": v(-25.18, -24.77) * mm});
            skLineSegment(sketch, "E1098", {"start": v(-25.18, -24.77) * mm, "end": v(-25.2, -24.37) * mm});
            skLineSegment(sketch, "E1099", {"start": v(-25.2, -24.37) * mm, "end": v(-25.2, -23.94) * mm});
            skLineSegment(sketch, "E1100", {"start": v(-25.2, -23.94) * mm, "end": v(-25.22, -23.5) * mm});
            skLineSegment(sketch, "E1101", {"start": v(-25.22, -23.5) * mm, "end": v(-25.23, -23.04) * mm});
            skLineSegment(sketch, "E1102", {"start": v(-25.23, -23.04) * mm, "end": v(-25.25, -22.57) * mm});
            skLineSegment(sketch, "E1103", {"start": v(-25.25, -22.57) * mm, "end": v(-25.26, -22.08) * mm});
            skLineSegment(sketch, "E1104", {"start": v(-25.26, -22.08) * mm, "end": v(-25.27, -21.59) * mm});
            skLineSegment(sketch, "E1105", {"start": v(-25.27, -21.59) * mm, "end": v(-25.28, -21.08) * mm});
            skLineSegment(sketch, "E1106", {"start": v(-25.28, -21.08) * mm, "end": v(-25.29, -20.57) * mm});
            skLineSegment(sketch, "E1107", {"start": v(-25.29, -20.57) * mm, "end": v(-25.32, -18.5) * mm});
            skLineSegment(sketch, "E1108", {"start": v(-25.32, -18.5) * mm, "end": v(-25.33, -17.48) * mm});
            skLineSegment(sketch, "E1109", {"start": v(-25.33, -17.48) * mm, "end": v(-25.33, -16.98) * mm});
            skLineSegment(sketch, "E1110", {"start": v(-25.33, -16.98) * mm, "end": v(-25.34, -16.49) * mm});
            skLineSegment(sketch, "E1111", {"start": v(-25.34, -16.49) * mm, "end": v(-25.34, -16) * mm});
            skLineSegment(sketch, "E1112", {"start": v(-25.34, -16) * mm, "end": v(-25.34, -15.54) * mm});
            skLineSegment(sketch, "E1113", {"start": v(-25.34, -15.54) * mm, "end": v(-25.35, -15.08) * mm});
            skLineSegment(sketch, "E1114", {"start": v(-25.35, -15.08) * mm, "end": v(-25.35, -14.65) * mm});
            skLineSegment(sketch, "E1115", {"start": v(-25.35, -14.65) * mm, "end": v(-25.35, -14.23) * mm});
            skLineSegment(sketch, "E1116", {"start": v(-25.35, -14.23) * mm, "end": v(-25.35, -13.83) * mm});
            skLineSegment(sketch, "E1117", {"start": v(-25.35, -13.83) * mm, "end": v(-25.35, -13.46) * mm});
            skLineSegment(sketch, "E1118", {"start": v(-25.35, -13.46) * mm, "end": v(-25.35, -13.28) * mm});
            skLineSegment(sketch, "E1119", {"start": v(-25.35, -13.28) * mm, "end": v(-25.36, -13.1) * mm});
            skLineSegment(sketch, "E1120", {"start": v(-25.36, -13.1) * mm, "end": v(-25.36, -12.94) * mm});
            skLineSegment(sketch, "E1121", {"start": v(-25.36, -12.94) * mm, "end": v(-25.36, -12.78) * mm});
            skLineSegment(sketch, "E1122", {"start": v(-25.36, -12.78) * mm, "end": v(-25.36, -12.63) * mm});
            skLineSegment(sketch, "E1123", {"start": v(-25.36, -12.63) * mm, "end": v(-25.36, -12.49) * mm});
            skLineSegment(sketch, "E1124", {"start": v(-25.36, -12.49) * mm, "end": v(-25.36, -12.35) * mm});
            skLineSegment(sketch, "E1125", {"start": v(-25.36, -12.35) * mm, "end": v(-25.36, -12.22) * mm});
            skLineSegment(sketch, "E1126", {"start": v(-25.36, -12.22) * mm, "end": v(-25.36, -12.1) * mm});
            skLineSegment(sketch, "E1127", {"start": v(-25.36, -12.1) * mm, "end": v(-25.36, -11.99) * mm});
            skLineSegment(sketch, "E1128", {"start": v(-25.36, -11.99) * mm, "end": v(-25.36, -11.89) * mm});
            skLineSegment(sketch, "E1129", {"start": v(-25.36, -11.89) * mm, "end": v(-25.36, -11.8) * mm});
            skLineSegment(sketch, "E1130", {"start": v(-25.36, -11.8) * mm, "end": v(-25.35, -11.7) * mm});
            skLineSegment(sketch, "E1131", {"start": v(-25.35, -11.7) * mm, "end": v(-25.35, -11.63) * mm});
            skLineSegment(sketch, "E1132", {"start": v(-25.35, -11.63) * mm, "end": v(-25.35, -11.56) * mm});
            skLineSegment(sketch, "E1133", {"start": v(-25.35, -11.56) * mm, "end": v(-25.35, -11.5) * mm});
            skLineSegment(sketch, "E1134", {"start": v(-25.35, -11.5) * mm, "end": v(-25.35, -11.46) * mm});
            skLineSegment(sketch, "E1135", {"start": v(-25.35, -11.46) * mm, "end": v(-25.35, -11.42) * mm});
            skLineSegment(sketch, "E1136", {"start": v(-25.35, -11.42) * mm, "end": v(-25.35, -11.4) * mm});
            skLineSegment(sketch, "E1137", {"start": v(-25.35, -11.4) * mm, "end": v(-25.35, -11.38) * mm});
            skLineSegment(sketch, "E1138", {"start": v(-25.35, -11.38) * mm, "end": v(-25.35, -11.38) * mm});
            skLineSegment(sketch, "E1139", {"start": v(-25.35, -11.38) * mm, "end": v(-25.34, -11.37) * mm});
            skLineSegment(sketch, "E1140", {"start": v(-25.34, -11.37) * mm, "end": v(-25.32, -11.37) * mm});
            skLineSegment(sketch, "E1141", {"start": v(-25.32, -11.37) * mm, "end": v(-25.25, -11.36) * mm});
            skLineSegment(sketch, "E1142", {"start": v(-25.25, -11.36) * mm, "end": v(-24.93, -11.3) * mm});
            skLineSegment(sketch, "E1143", {"start": v(-24.93, -11.3) * mm, "end": v(-24.6, -11.22) * mm});
            skLineSegment(sketch, "E1144", {"start": v(-24.6, -11.22) * mm, "end": v(-24.27, -11.14) * mm});
            skLineSegment(sketch, "E1145", {"start": v(-24.27, -11.14) * mm, "end": v(-23.94, -11.04) * mm});
            skLineSegment(sketch, "E1146", {"start": v(-23.94, -11.04) * mm, "end": v(-23.6, -10.93) * mm});
            skLineSegment(sketch, "E1147", {"start": v(-23.6, -10.93) * mm, "end": v(-23.26, -10.8) * mm});
            skLineSegment(sketch, "E1148", {"start": v(-23.26, -10.8) * mm, "end": v(-22.93, -10.67) * mm});
            skLineSegment(sketch, "E1149", {"start": v(-22.93, -10.67) * mm, "end": v(-22.59, -10.51) * mm});
            skLineSegment(sketch, "E1150", {"start": v(-22.59, -10.51) * mm, "end": v(-22.25, -10.34) * mm});
            skLineSegment(sketch, "E1151", {"start": v(-22.25, -10.34) * mm, "end": v(-21.92, -10.16) * mm});
            skLineSegment(sketch, "E1152", {"start": v(-21.92, -10.16) * mm, "end": v(-21.6, -9.95) * mm});
            skLineSegment(sketch, "E1153", {"start": v(-21.6, -9.95) * mm, "end": v(-21.27, -9.73) * mm});
            skLineSegment(sketch, "E1154", {"start": v(-21.27, -9.73) * mm, "end": v(-20.95, -9.49) * mm});
            skLineSegment(sketch, "E1155", {"start": v(-20.95, -9.49) * mm, "end": v(-20.63, -9.22) * mm});
            skLineSegment(sketch, "E1156", {"start": v(-20.63, -9.22) * mm, "end": v(-20.33, -8.94) * mm});
            skLineSegment(sketch, "E1157", {"start": v(-20.33, -8.94) * mm, "end": v(-20.03, -8.64) * mm});
            skLineSegment(sketch, "E1158", {"start": v(-20.03, -8.64) * mm, "end": v(-19.74, -8.31) * mm});
            skLineSegment(sketch, "E1159", {"start": v(-19.74, -8.31) * mm, "end": v(-19.6, -8.14) * mm});
            skLineSegment(sketch, "E1160", {"start": v(-19.6, -8.14) * mm, "end": v(-19.47, -7.96) * mm});
            skLineSegment(sketch, "E1161", {"start": v(-19.47, -7.96) * mm, "end": v(-19.33, -7.78) * mm});
            skLineSegment(sketch, "E1162", {"start": v(-19.33, -7.78) * mm, "end": v(-19.2, -7.59) * mm});
            skLineSegment(sketch, "E1163", {"start": v(-19.2, -7.59) * mm, "end": v(-19.08, -7.4) * mm});
            skLineSegment(sketch, "E1164", {"start": v(-19.08, -7.4) * mm, "end": v(-18.95, -7.2) * mm});
            skLineSegment(sketch, "E1165", {"start": v(-18.95, -7.2) * mm, "end": v(-18.83, -6.98) * mm});
            skLineSegment(sketch, "E1166", {"start": v(-18.83, -6.98) * mm, "end": v(-18.71, -6.77) * mm});
            skLineSegment(sketch, "E1167", {"start": v(-18.71, -6.77) * mm, "end": v(-18.36, -7.36) * mm});
            skLineSegment(sketch, "E1168", {"start": v(-18.36, -7.36) * mm, "end": v(-18.02, -7.96) * mm});
            skLineSegment(sketch, "E1169", {"start": v(-18.02, -7.96) * mm, "end": v(-17.7, -8.58) * mm});
            skLineSegment(sketch, "E1170", {"start": v(-17.7, -8.58) * mm, "end": v(-17.4, -9.2) * mm});
            skLineSegment(sketch, "E1171", {"start": v(-17.4, -9.2) * mm, "end": v(-17.26, -9.53) * mm});
            skLineSegment(sketch, "E1172", {"start": v(-17.26, -9.53) * mm, "end": v(-17.13, -9.85) * mm});
            skLineSegment(sketch, "E1173", {"start": v(-17.13, -9.85) * mm, "end": v(-17.06, -10.01) * mm});
            skLineSegment(sketch, "E1174", {"start": v(-17.06, -10.01) * mm, "end": v(-17.05, -10.05) * mm});
            skLineSegment(sketch, "E1175", {"start": v(-17.05, -10.05) * mm, "end": v(-17.04, -10.06) * mm});
            skLineSegment(sketch, "E1176", {"start": v(-17.04, -10.06) * mm, "end": v(-17.03, -10.08) * mm});
            skLineSegment(sketch, "E1177", {"start": v(-17.03, -10.08) * mm, "end": v(-17.02, -10.12) * mm});
            skLineSegment(sketch, "E1178", {"start": v(-17.02, -10.12) * mm, "end": v(-16.98, -10.2) * mm});
            skLineSegment(sketch, "E1179", {"start": v(-16.98, -10.2) * mm, "end": v(-16.94, -10.28) * mm});
            skLineSegment(sketch, "E1180", {"start": v(-16.94, -10.28) * mm, "end": v(-16.9, -10.38) * mm});
            skLineSegment(sketch, "E1181", {"start": v(-16.9, -10.38) * mm, "end": v(-16.87, -10.48) * mm});
            skLineSegment(sketch, "E1182", {"start": v(-16.87, -10.48) * mm, "end": v(-16.83, -10.6) * mm});
            skLineSegment(sketch, "E1183", {"start": v(-16.83, -10.6) * mm, "end": v(-16.8, -10.71) * mm});
            skLineSegment(sketch, "E1184", {"start": v(-16.8, -10.71) * mm, "end": v(-16.76, -10.84) * mm});
            skLineSegment(sketch, "E1185", {"start": v(-16.76, -10.84) * mm, "end": v(-16.73, -10.97) * mm});
            skLineSegment(sketch, "E1186", {"start": v(-16.73, -10.97) * mm, "end": v(-16.7, -11.1) * mm});
            skLineSegment(sketch, "E1187", {"start": v(-16.7, -11.1) * mm, "end": v(-16.67, -11.25) * mm});
            skLineSegment(sketch, "E1188", {"start": v(-16.67, -11.25) * mm, "end": v(-16.6, -11.55) * mm});
            skLineSegment(sketch, "E1189", {"start": v(-16.6, -11.55) * mm, "end": v(-16.55, -11.88) * mm});
            skLineSegment(sketch, "E1190", {"start": v(-16.55, -11.88) * mm, "end": v(-16.5, -12.24) * mm});
            skLineSegment(sketch, "E1191", {"start": v(-16.5, -12.24) * mm, "end": v(-16.45, -12.6) * mm});
            skLineSegment(sketch, "E1192", {"start": v(-16.45, -12.6) * mm, "end": v(-16.4, -13) * mm});
            skLineSegment(sketch, "E1193", {"start": v(-16.4, -13) * mm, "end": v(-16.35, -13.4) * mm});
            skLineSegment(sketch, "E1194", {"start": v(-16.35, -13.4) * mm, "end": v(-16.3, -13.84) * mm});
            skLineSegment(sketch, "E1195", {"start": v(-16.3, -13.84) * mm, "end": v(-16.27, -14.28) * mm});
            skLineSegment(sketch, "E1196", {"start": v(-16.27, -14.28) * mm, "end": v(-16.23, -14.73) * mm});
            skLineSegment(sketch, "E1197", {"start": v(-16.23, -14.73) * mm, "end": v(-16.2, -15.2) * mm});
            skLineSegment(sketch, "E1198", {"start": v(-16.2, -15.2) * mm, "end": v(-16.16, -15.67) * mm});
            skLineSegment(sketch, "E1199", {"start": v(-16.16, -15.67) * mm, "end": v(-16.12, -16.16) * mm});
            skLineSegment(sketch, "E1200", {"start": v(-16.12, -16.16) * mm, "end": v(-16.1, -16.65) * mm});
            skLineSegment(sketch, "E1201", {"start": v(-16.1, -16.65) * mm, "end": v(-16.06, -17.15) * mm});
            skLineSegment(sketch, "E1202", {"start": v(-16.06, -17.15) * mm, "end": v(-16.01, -18.17) * mm});
            skLineSegment(sketch, "E1203", {"start": v(-16.01, -18.17) * mm, "end": v(-15.92, -20.2) * mm});
            skLineSegment(sketch, "E1204", {"start": v(-15.92, -20.2) * mm, "end": v(-15.89, -21.21) * mm});
            skLineSegment(sketch, "E1205", {"start": v(-15.89, -21.21) * mm, "end": v(-15.87, -21.7) * mm});
            skLineSegment(sketch, "E1206", {"start": v(-15.87, -21.7) * mm, "end": v(-15.86, -22.19) * mm});
            skLineSegment(sketch, "E1207", {"start": v(-15.86, -22.19) * mm, "end": v(-15.84, -22.66) * mm});
            skLineSegment(sketch, "E1208", {"start": v(-15.84, -22.66) * mm, "end": v(-15.83, -23.13) * mm});
            skLineSegment(sketch, "E1209", {"start": v(-15.83, -23.13) * mm, "end": v(-15.81, -23.58) * mm});
            skLineSegment(sketch, "E1210", {"start": v(-15.81, -23.58) * mm, "end": v(-15.8, -24.02) * mm});
            skLineSegment(sketch, "E1211", {"start": v(-15.8, -24.02) * mm, "end": v(-15.79, -24.45) * mm});
            skLineSegment(sketch, "E1212", {"start": v(-15.79, -24.45) * mm, "end": v(-15.78, -24.86) * mm});
            skLineSegment(sketch, "E1213", {"start": v(-15.78, -24.86) * mm, "end": v(-15.76, -25.25) * mm});
            skLineSegment(sketch, "E1214", {"start": v(-15.76, -25.25) * mm, "end": v(-15.75, -25.62) * mm});
            skLineSegment(sketch, "E1215", {"start": v(-15.75, -25.62) * mm, "end": v(-15.74, -25.97) * mm});
            skLineSegment(sketch, "E1216", {"start": v(-15.74, -25.97) * mm, "end": v(-15.73, -26.3) * mm});
            skLineSegment(sketch, "E1217", {"start": v(-15.73, -26.3) * mm, "end": v(-15.72, -26.6) * mm});
            skLineSegment(sketch, "E1218", {"start": v(-15.72, -26.6) * mm, "end": v(-15.7, -26.74) * mm});
            skLineSegment(sketch, "E1219", {"start": v(-15.7, -26.74) * mm, "end": v(-15.7, -26.88) * mm});
            skLineSegment(sketch, "E1220", {"start": v(-15.7, -26.88) * mm, "end": v(-15.7, -27.01) * mm});
            skLineSegment(sketch, "E1221", {"start": v(-15.7, -27.01) * mm, "end": v(-15.7, -27.13) * mm});
            skLineSegment(sketch, "E1222", {"start": v(-15.7, -27.13) * mm, "end": v(-15.69, -27.2) * mm});
            skLineSegment(sketch, "E1223", {"start": v(-15.69, -27.2) * mm, "end": v(-15.69, -27.2) * mm});
            skLineSegment(sketch, "E1224", {"start": v(-15.69, -27.2) * mm, "end": v(-15.69, -27.21) * mm});
            skLineSegment(sketch, "E1225", {"start": v(-15.69, -27.21) * mm, "end": v(-15.7, -27.21) * mm});
            skLineSegment(sketch, "E1226", {"start": v(-15.7, -27.21) * mm, "end": v(-15.74, -27.22) * mm});
            skLineSegment(sketch, "E1227", {"start": v(-15.74, -27.22) * mm, "end": v(-15.92, -27.23) * mm});
            skLineSegment(sketch, "E1228", {"start": v(-15.92, -27.23) * mm, "end": v(-16.11, -27.24) * mm});
            skLineSegment(sketch, "E1229", {"start": v(-16.11, -27.24) * mm, "end": v(-16.31, -27.25) * mm});
            skLineSegment(sketch, "E1230", {"start": v(-16.31, -27.25) * mm, "end": v(-16.52, -27.26) * mm});
            skLineSegment(sketch, "E1231", {"start": v(-16.52, -27.26) * mm, "end": v(-16.74, -27.27) * mm});
            skLineSegment(sketch, "E1232", {"start": v(-16.74, -27.27) * mm, "end": v(-16.97, -27.28) * mm});
            skLineSegment(sketch, "E1233", {"start": v(-16.97, -27.28) * mm, "end": v(-17.21, -27.3) * mm});
            skLineSegment(sketch, "E1234", {"start": v(-17.21, -27.3) * mm, "end": v(-17.46, -27.3) * mm});
            skLineSegment(sketch, "E1235", {"start": v(-17.46, -27.3) * mm, "end": v(-17.72, -27.32) * mm});
            skLineSegment(sketch, "E1236", {"start": v(-17.72, -27.32) * mm, "end": v(-17.98, -27.34) * mm});
            skLineSegment(sketch, "E1237", {"start": v(-17.98, -27.34) * mm, "end": v(-18.25, -27.36) * mm});
            skLineSegment(sketch, "E1238", {"start": v(-18.25, -27.36) * mm, "end": v(-18.53, -27.38) * mm});
            skLineSegment(sketch, "E1239", {"start": v(-18.53, -27.38) * mm, "end": v(-18.81, -27.4) * mm});
            skLineSegment(sketch, "E1240", {"start": v(-18.81, -27.4) * mm, "end": v(-19.1, -27.44) * mm});
            skLineSegment(sketch, "E1241", {"start": v(-19.1, -27.44) * mm, "end": v(-19.4, -27.47) * mm});
            skLineSegment(sketch, "E1242", {"start": v(-19.4, -27.47) * mm, "end": v(-19.7, -27.5) * mm});
            skLineSegment(sketch, "E1243", {"start": v(-19.7, -27.5) * mm, "end": v(-20, -27.55) * mm});
            skLineSegment(sketch, "E1244", {"start": v(-20, -27.55) * mm, "end": v(-20.63, -27.64) * mm});
            skLineSegment(sketch, "E1245", {"start": v(-20.63, -27.64) * mm, "end": v(-21.27, -27.76) * mm});
            skLineSegment(sketch, "E1246", {"start": v(-28.46, 20.17) * mm, "end": v(-28.67, 19.84) * mm});
            skLineSegment(sketch, "E1247", {"start": v(-28.67, 19.84) * mm, "end": v(-28.9, 19.51) * mm});
            skLineSegment(sketch, "E1248", {"start": v(-28.9, 19.51) * mm, "end": v(-29.14, 19.2) * mm});
            skLineSegment(sketch, "E1249", {"start": v(-29.14, 19.2) * mm, "end": v(-29.4, 18.9) * mm});
            skLineSegment(sketch, "E1250", {"start": v(-29.4, 18.9) * mm, "end": v(-29.67, 18.62) * mm});
            skLineSegment(sketch, "E1251", {"start": v(-29.67, 18.62) * mm, "end": v(-29.95, 18.35) * mm});
            skLineSegment(sketch, "E1252", {"start": v(-29.95, 18.35) * mm, "end": v(-30.25, 18.1) * mm});
            skLineSegment(sketch, "E1253", {"start": v(-30.25, 18.1) * mm, "end": v(-30.55, 17.85) * mm});
            skLineSegment(sketch, "E1254", {"start": v(-30.55, 17.85) * mm, "end": v(-30.87, 17.62) * mm});
            skLineSegment(sketch, "E1255", {"start": v(-30.87, 17.62) * mm, "end": v(-31.2, 17.4) * mm});
            skLineSegment(sketch, "E1256", {"start": v(-31.2, 17.4) * mm, "end": v(-31.53, 17.2) * mm});
            skLineSegment(sketch, "E1257", {"start": v(-31.53, 17.2) * mm, "end": v(-31.87, 17.03) * mm});
            skLineSegment(sketch, "E1258", {"start": v(-31.87, 17.03) * mm, "end": v(-32.22, 16.86) * mm});
            skLineSegment(sketch, "E1259", {"start": v(-32.22, 16.86) * mm, "end": v(-32.57, 16.72) * mm});
            skLineSegment(sketch, "E1260", {"start": v(-32.57, 16.72) * mm, "end": v(-32.93, 16.59) * mm});
            skLineSegment(sketch, "E1261", {"start": v(-32.93, 16.59) * mm, "end": v(-33.3, 16.47) * mm});
            skLineSegment(sketch, "E1262", {"start": v(-33.3, 16.47) * mm, "end": v(-33.66, 16.38) * mm});
            skLineSegment(sketch, "E1263", {"start": v(-33.66, 16.38) * mm, "end": v(-34.03, 16.3) * mm});
            skLineSegment(sketch, "E1264", {"start": v(-34.03, 16.3) * mm, "end": v(-34.4, 16.25) * mm});
            skLineSegment(sketch, "E1265", {"start": v(-34.4, 16.25) * mm, "end": v(-34.77, 16.22) * mm});
            skLineSegment(sketch, "E1266", {"start": v(-34.77, 16.22) * mm, "end": v(-35.13, 16.2) * mm});
            skLineSegment(sketch, "E1267", {"start": v(-35.13, 16.2) * mm, "end": v(-35.5, 16.2) * mm});
            skLineSegment(sketch, "E1268", {"start": v(-35.5, 16.2) * mm, "end": v(-35.87, 16.24) * mm});
            skLineSegment(sketch, "E1269", {"start": v(-35.87, 16.24) * mm, "end": v(-36.23, 16.29) * mm});
            skLineSegment(sketch, "E1270", {"start": v(-36.23, 16.29) * mm, "end": v(-36.59, 16.36) * mm});
            skLineSegment(sketch, "E1271", {"start": v(-36.59, 16.36) * mm, "end": v(-36.94, 16.45) * mm});
            skLineSegment(sketch, "E1272", {"start": v(-36.94, 16.45) * mm, "end": v(-37.29, 16.57) * mm});
            skLineSegment(sketch, "E1273", {"start": v(-37.29, 16.57) * mm, "end": v(-37.63, 16.72) * mm});
            skLineSegment(sketch, "E1274", {"start": v(-37.63, 16.72) * mm, "end": v(-37.96, 16.88) * mm});
            skLineSegment(sketch, "E1275", {"start": v(-37.96, 16.88) * mm, "end": v(-38.3, 17.07) * mm});
            skLineSegment(sketch, "E1276", {"start": v(-38.3, 17.07) * mm, "end": v(-38.6, 17.29) * mm});
            skLineSegment(sketch, "E1277", {"start": v(-38.6, 17.29) * mm, "end": v(-38.91, 17.53) * mm});
            skLineSegment(sketch, "E1278", {"start": v(-38.91, 17.53) * mm, "end": v(-40.77, 19.15) * mm});
            skLineSegment(sketch, "E1279", {"start": v(-40.77, 19.15) * mm, "end": v(-40.19, 18.89) * mm});
            skLineSegment(sketch, "E1280", {"start": v(-40.19, 18.89) * mm, "end": v(-39.57, 18.64) * mm});
            skLineSegment(sketch, "E1281", {"start": v(-39.57, 18.64) * mm, "end": v(-38.28, 18.15) * mm});
            skLineSegment(sketch, "E1282", {"start": v(-38.28, 18.15) * mm, "end": v(-36.99, 17.67) * mm});
            skLineSegment(sketch, "E1283", {"start": v(-36.99, 17.67) * mm, "end": v(-36.37, 17.41) * mm});
            skLineSegment(sketch, "E1284", {"start": v(-36.37, 17.41) * mm, "end": v(-35.79, 17.15) * mm});
            skLineSegment(sketch, "E1285", {"start": v(-35.79, 17.15) * mm, "end": v(-36.14, 17.52) * mm});
            skLineSegment(sketch, "E1286", {"start": v(-36.14, 17.52) * mm, "end": v(-36.5, 17.92) * mm});
            skLineSegment(sketch, "E1287", {"start": v(-36.5, 17.92) * mm, "end": v(-37.22, 18.78) * mm});
            skLineSegment(sketch, "E1288", {"start": v(-37.22, 18.78) * mm, "end": v(-37.93, 19.65) * mm});
            skLineSegment(sketch, "E1289", {"start": v(-37.93, 19.65) * mm, "end": v(-38.3, 20.05) * mm});
            skLineSegment(sketch, "E1290", {"start": v(-38.3, 20.05) * mm, "end": v(-38.65, 20.42) * mm});
            skLineSegment(sketch, "E1291", {"start": v(-38.65, 20.42) * mm, "end": v(-38, 20.04) * mm});
            skLineSegment(sketch, "E1292", {"start": v(-38, 20.04) * mm, "end": v(-37.36, 19.7) * mm});
            skLineSegment(sketch, "E1293", {"start": v(-37.36, 19.7) * mm, "end": v(-36.74, 19.4) * mm});
            skLineSegment(sketch, "E1294", {"start": v(-36.74, 19.4) * mm, "end": v(-36.14, 19.1) * mm});
            skLineSegment(sketch, "E1295", {"start": v(-36.14, 19.1) * mm, "end": v(-34.97, 18.58) * mm});
            skLineSegment(sketch, "E1296", {"start": v(-34.97, 18.58) * mm, "end": v(-33.84, 18.06) * mm});
            skLineSegment(sketch, "E1297", {"start": v(-33.84, 18.06) * mm, "end": v(-34.02, 18.32) * mm});
            skLineSegment(sketch, "E1298", {"start": v(-34.02, 18.32) * mm, "end": v(-34.18, 18.57) * mm});
            skLineSegment(sketch, "E1299", {"start": v(-34.18, 18.57) * mm, "end": v(-34.48, 19.02) * mm});
            skLineSegment(sketch, "E1300", {"start": v(-34.48, 19.02) * mm, "end": v(-34.75, 19.44) * mm});
            skLineSegment(sketch, "E1301", {"start": v(-34.75, 19.44) * mm, "end": v(-35, 19.84) * mm});
            skLineSegment(sketch, "E1302", {"start": v(-35, 19.84) * mm, "end": v(-35.26, 20.23) * mm});
            skLineSegment(sketch, "E1303", {"start": v(-35.26, 20.23) * mm, "end": v(-35.53, 20.66) * mm});
            skLineSegment(sketch, "E1304", {"start": v(-35.53, 20.66) * mm, "end": v(-35.82, 21.12) * mm});
            skLineSegment(sketch, "E1305", {"start": v(-35.82, 21.12) * mm, "end": v(-35.98, 21.38) * mm});
            skLineSegment(sketch, "E1306", {"start": v(-35.98, 21.38) * mm, "end": v(-36.16, 21.65) * mm});
            skLineSegment(sketch, "E1307", {"start": v(-36.16, 21.65) * mm, "end": v(-35.65, 21.34) * mm});
            skLineSegment(sketch, "E1308", {"start": v(-35.65, 21.34) * mm, "end": v(-35.17, 21.05) * mm});
            skLineSegment(sketch, "E1309", {"start": v(-35.17, 21.05) * mm, "end": v(-34.25, 20.55) * mm});
            skLineSegment(sketch, "E1310", {"start": v(-34.25, 20.55) * mm, "end": v(-33.78, 20.32) * mm});
            skLineSegment(sketch, "E1311", {"start": v(-33.78, 20.32) * mm, "end": v(-33.3, 20.07) * mm});
            skLineSegment(sketch, "E1312", {"start": v(-33.3, 20.07) * mm, "end": v(-32.79, 19.8) * mm});
            skLineSegment(sketch, "E1313", {"start": v(-32.79, 19.8) * mm, "end": v(-32.24, 19.5) * mm});
            skLineSegment(sketch, "E1314", {"start": v(-32.24, 19.5) * mm, "end": v(-32.43, 19.8) * mm});
            skLineSegment(sketch, "E1315", {"start": v(-32.43, 19.8) * mm, "end": v(-32.6, 20.06) * mm});
            skLineSegment(sketch, "E1316", {"start": v(-32.6, 20.06) * mm, "end": v(-32.75, 20.3) * mm});
            skLineSegment(sketch, "E1317", {"start": v(-32.75, 20.3) * mm, "end": v(-32.88, 20.53) * mm});
            skLineSegment(sketch, "E1318", {"start": v(-32.88, 20.53) * mm, "end": v(-33.09, 20.93) * mm});
            skLineSegment(sketch, "E1319", {"start": v(-33.09, 20.93) * mm, "end": v(-33.27, 21.29) * mm});
            skLineSegment(sketch, "E1320", {"start": v(-33.27, 21.29) * mm, "end": v(-33.44, 21.65) * mm});
            skLineSegment(sketch, "E1321", {"start": v(-33.44, 21.65) * mm, "end": v(-33.66, 22.03) * mm});
            skLineSegment(sketch, "E1322", {"start": v(-33.66, 22.03) * mm, "end": v(-33.78, 22.23) * mm});
            skLineSegment(sketch, "E1323", {"start": v(-33.78, 22.23) * mm, "end": v(-33.93, 22.46) * mm});
            skLineSegment(sketch, "E1324", {"start": v(-33.93, 22.46) * mm, "end": v(-34.1, 22.7) * mm});
            skLineSegment(sketch, "E1325", {"start": v(-34.1, 22.7) * mm, "end": v(-34.3, 22.97) * mm});
            skLineSegment(sketch, "E1326", {"start": v(-34.3, 22.97) * mm, "end": v(-34, 22.82) * mm});
            skLineSegment(sketch, "E1327", {"start": v(-34, 22.82) * mm, "end": v(-33.73, 22.69) * mm});
            skLineSegment(sketch, "E1328", {"start": v(-33.73, 22.69) * mm, "end": v(-33.48, 22.57) * mm});
            skLineSegment(sketch, "E1329", {"start": v(-33.48, 22.57) * mm, "end": v(-33.25, 22.47) * mm});
            skLineSegment(sketch, "E1330", {"start": v(-33.25, 22.47) * mm, "end": v(-32.84, 22.29) * mm});
            skLineSegment(sketch, "E1331", {"start": v(-32.84, 22.29) * mm, "end": v(-32.46, 22.13) * mm});
            skLineSegment(sketch, "E1332", {"start": v(-32.46, 22.13) * mm, "end": v(-32.08, 21.97) * mm});
            skLineSegment(sketch, "E1333", {"start": v(-32.08, 21.97) * mm, "end": v(-31.67, 21.79) * mm});
            skLineSegment(sketch, "E1334", {"start": v(-31.67, 21.79) * mm, "end": v(-31.44, 21.69) * mm});
            skLineSegment(sketch, "E1335", {"start": v(-31.44, 21.69) * mm, "end": v(-31.19, 21.57) * mm});
            skLineSegment(sketch, "E1336", {"start": v(-31.19, 21.57) * mm, "end": v(-30.92, 21.44) * mm});
            skLineSegment(sketch, "E1337", {"start": v(-30.92, 21.44) * mm, "end": v(-30.62, 21.29) * mm});
            skLineSegment(sketch, "E1338", {"start": v(-30.62, 21.29) * mm, "end": v(-30.85, 21.6) * mm});
            skLineSegment(sketch, "E1339", {"start": v(-30.85, 21.6) * mm, "end": v(-31.07, 21.88) * mm});
            skLineSegment(sketch, "E1340", {"start": v(-31.07, 21.88) * mm, "end": v(-31.27, 22.15) * mm});
            skLineSegment(sketch, "E1341", {"start": v(-31.27, 22.15) * mm, "end": v(-31.45, 22.4) * mm});
            skLineSegment(sketch, "E1342", {"start": v(-31.45, 22.4) * mm, "end": v(-31.78, 22.86) * mm});
            skLineSegment(sketch, "E1343", {"start": v(-31.78, 22.86) * mm, "end": v(-32.08, 23.29) * mm});
            skLineSegment(sketch, "E1344", {"start": v(-32.08, 23.29) * mm, "end": v(-32.37, 23.7) * mm});
            skLineSegment(sketch, "E1345", {"start": v(-32.37, 23.7) * mm, "end": v(-32.67, 24.15) * mm});
            skLineSegment(sketch, "E1346", {"start": v(-32.67, 24.15) * mm, "end": v(-32.83, 24.38) * mm});
            skLineSegment(sketch, "E1347", {"start": v(-32.83, 24.38) * mm, "end": v(-33, 24.63) * mm});
            skLineSegment(sketch, "E1348", {"start": v(-33, 24.63) * mm, "end": v(-33.2, 24.9) * mm});
            skLineSegment(sketch, "E1349", {"start": v(-33.2, 24.9) * mm, "end": v(-33.4, 25.18) * mm});
            skLineSegment(sketch, "E1350", {"start": v(-33.4, 25.18) * mm, "end": v(-33.1, 25.03) * mm});
            skLineSegment(sketch, "E1351", {"start": v(-33.1, 25.03) * mm, "end": v(-32.82, 24.89) * mm});
            skLineSegment(sketch, "E1352", {"start": v(-32.82, 24.89) * mm, "end": v(-32.56, 24.76) * mm});
            skLineSegment(sketch, "E1353", {"start": v(-32.56, 24.76) * mm, "end": v(-32.32, 24.65) * mm});
            skLineSegment(sketch, "E1354", {"start": v(-32.32, 24.65) * mm, "end": v(-31.88, 24.44) * mm});
            skLineSegment(sketch, "E1355", {"start": v(-31.88, 24.44) * mm, "end": v(-31.46, 24.25) * mm});
            skLineSegment(sketch, "E1356", {"start": v(-31.46, 24.25) * mm, "end": v(-31.04, 24.05) * mm});
            skLineSegment(sketch, "E1357", {"start": v(-31.04, 24.05) * mm, "end": v(-30.6, 23.84) * mm});
            skLineSegment(sketch, "E1358", {"start": v(-30.6, 23.84) * mm, "end": v(-30.36, 23.72) * mm});
            skLineSegment(sketch, "E1359", {"start": v(-30.36, 23.72) * mm, "end": v(-30.1, 23.6) * mm});
            skLineSegment(sketch, "E1360", {"start": v(-30.1, 23.6) * mm, "end": v(-29.83, 23.45) * mm});
            skLineSegment(sketch, "E1361", {"start": v(-29.83, 23.45) * mm, "end": v(-29.53, 23.3) * mm});
            skLineSegment(sketch, "E1362", {"start": v(-29.53, 23.3) * mm, "end": v(-29.76, 23.58) * mm});
            skLineSegment(sketch, "E1363", {"start": v(-29.76, 23.58) * mm, "end": v(-29.97, 23.85) * mm});
            skLineSegment(sketch, "E1364", {"start": v(-29.97, 23.85) * mm, "end": v(-30.35, 24.35) * mm});
            skLineSegment(sketch, "E1365", {"start": v(-30.35, 24.35) * mm, "end": v(-30.7, 24.82) * mm});
            skLineSegment(sketch, "E1366", {"start": v(-30.7, 24.82) * mm, "end": v(-31.02, 25.28) * mm});
            skLineSegment(sketch, "E1367", {"start": v(-31.02, 25.28) * mm, "end": v(-31.35, 25.75) * mm});
            skLineSegment(sketch, "E1368", {"start": v(-31.35, 25.75) * mm, "end": v(-31.69, 26.25) * mm});
            skLineSegment(sketch, "E1369", {"start": v(-31.69, 26.25) * mm, "end": v(-31.87, 26.51) * mm});
            skLineSegment(sketch, "E1370", {"start": v(-31.87, 26.51) * mm, "end": v(-32.07, 26.8) * mm});
            skLineSegment(sketch, "E1371", {"start": v(-32.07, 26.8) * mm, "end": v(-32.28, 27.1) * mm});
            skLineSegment(sketch, "E1372", {"start": v(-32.28, 27.1) * mm, "end": v(-32.5, 27.42) * mm});
            skLineSegment(sketch, "E1373", {"start": v(-32.5, 27.42) * mm, "end": v(-32.16, 27.24) * mm});
            skLineSegment(sketch, "E1374", {"start": v(-32.16, 27.24) * mm, "end": v(-31.84, 27.08) * mm});
            skLineSegment(sketch, "E1375", {"start": v(-31.84, 27.08) * mm, "end": v(-31.55, 26.94) * mm});
            skLineSegment(sketch, "E1376", {"start": v(-31.55, 26.94) * mm, "end": v(-31.28, 26.8) * mm});
            skLineSegment(sketch, "E1377", {"start": v(-31.28, 26.8) * mm, "end": v(-30.8, 26.58) * mm});
            skLineSegment(sketch, "E1378", {"start": v(-30.8, 26.58) * mm, "end": v(-30.36, 26.37) * mm});
            skLineSegment(sketch, "E1379", {"start": v(-30.36, 26.37) * mm, "end": v(-29.92, 26.16) * mm});
            skLineSegment(sketch, "E1380", {"start": v(-29.92, 26.16) * mm, "end": v(-29.47, 25.94) * mm});
            skLineSegment(sketch, "E1381", {"start": v(-29.47, 25.94) * mm, "end": v(-29.23, 25.81) * mm});
            skLineSegment(sketch, "E1382", {"start": v(-29.23, 25.81) * mm, "end": v(-28.97, 25.68) * mm});
            skLineSegment(sketch, "E1383", {"start": v(-28.97, 25.68) * mm, "end": v(-28.68, 25.52) * mm});
            skLineSegment(sketch, "E1384", {"start": v(-28.68, 25.52) * mm, "end": v(-28.37, 25.36) * mm});
            skLineSegment(sketch, "E1385", {"start": v(-28.37, 25.36) * mm, "end": v(-29.11, 26.56) * mm});
            skLineSegment(sketch, "E1386", {"start": v(-29.11, 26.56) * mm, "end": v(-29.85, 27.74) * mm});
            skLineSegment(sketch, "E1387", {"start": v(-29.85, 27.74) * mm, "end": v(-30.6, 28.92) * mm});
            skLineSegment(sketch, "E1388", {"start": v(-30.6, 28.92) * mm, "end": v(-31.34, 30.13) * mm});
            skLineSegment(sketch, "E1389", {"start": v(-31.34, 30.13) * mm, "end": v(-30.96, 29.95) * mm});
            skLineSegment(sketch, "E1390", {"start": v(-30.96, 29.95) * mm, "end": v(-30.58, 29.75) * mm});
            skLineSegment(sketch, "E1391", {"start": v(-30.58, 29.75) * mm, "end": v(-30.2, 29.53) * mm});
            skLineSegment(sketch, "E1392", {"start": v(-30.2, 29.53) * mm, "end": v(-29.84, 29.29) * mm});
            skLineSegment(sketch, "E1393", {"start": v(-29.84, 29.29) * mm, "end": v(-29.49, 29.02) * mm});
            skLineSegment(sketch, "E1394", {"start": v(-29.49, 29.02) * mm, "end": v(-29.16, 28.74) * mm});
            skLineSegment(sketch, "E1395", {"start": v(-29.16, 28.74) * mm, "end": v(-28.86, 28.43) * mm});
            skLineSegment(sketch, "E1396", {"start": v(-28.86, 28.43) * mm, "end": v(-28.59, 28.1) * mm});
            skLineSegment(sketch, "E1397", {"start": v(-28.59, 28.1) * mm, "end": v(-28.3, 27.66) * mm});
            skLineSegment(sketch, "E1398", {"start": v(-28.3, 27.66) * mm, "end": v(-28.04, 27.2) * mm});
            skLineSegment(sketch, "E1399", {"start": v(-28.04, 27.2) * mm, "end": v(-27.82, 26.74) * mm});
            skLineSegment(sketch, "E1400", {"start": v(-27.82, 26.74) * mm, "end": v(-27.65, 26.26) * mm});
            skLineSegment(sketch, "E1401", {"start": v(-27.65, 26.26) * mm, "end": v(-27.5, 25.77) * mm});
            skLineSegment(sketch, "E1402", {"start": v(-27.5, 25.77) * mm, "end": v(-27.4, 25.27) * mm});
            skLineSegment(sketch, "E1403", {"start": v(-27.4, 25.27) * mm, "end": v(-27.34, 24.76) * mm});
            skLineSegment(sketch, "E1404", {"start": v(-27.34, 24.76) * mm, "end": v(-27.32, 24.25) * mm});
            skLineSegment(sketch, "E1405", {"start": v(-27.32, 24.25) * mm, "end": v(-27.33, 23.73) * mm});
            skLineSegment(sketch, "E1406", {"start": v(-27.33, 23.73) * mm, "end": v(-27.38, 23.22) * mm});
            skLineSegment(sketch, "E1407", {"start": v(-27.38, 23.22) * mm, "end": v(-27.47, 22.7) * mm});
            skLineSegment(sketch, "E1408", {"start": v(-27.47, 22.7) * mm, "end": v(-27.6, 22.18) * mm});
            skLineSegment(sketch, "E1409", {"start": v(-27.6, 22.18) * mm, "end": v(-27.76, 21.67) * mm});
            skLineSegment(sketch, "E1410", {"start": v(-27.76, 21.67) * mm, "end": v(-27.95, 21.16) * mm});
            skLineSegment(sketch, "E1411", {"start": v(-27.95, 21.16) * mm, "end": v(-28.2, 20.66) * mm});
            skLineSegment(sketch, "E1412", {"start": v(-28.2, 20.66) * mm, "end": v(-28.46, 20.17) * mm});
            skLineSegment(sketch, "E1413", {"start": v(-52.83, 22.65) * mm, "end": v(-54.45, 25.05) * mm});
            skLineSegment(sketch, "E1414", {"start": v(-54.45, 25.05) * mm, "end": v(-53.87, 24.58) * mm});
            skLineSegment(sketch, "E1415", {"start": v(-53.87, 24.58) * mm, "end": v(-53.24, 24.1) * mm});
            skLineSegment(sketch, "E1416", {"start": v(-53.24, 24.1) * mm, "end": v(-51.92, 23.16) * mm});
            skLineSegment(sketch, "E1417", {"start": v(-51.92, 23.16) * mm, "end": v(-50.6, 22.22) * mm});
            skLineSegment(sketch, "E1418", {"start": v(-50.6, 22.22) * mm, "end": v(-49.98, 21.75) * mm});
            skLineSegment(sketch, "E1419", {"start": v(-49.98, 21.75) * mm, "end": v(-49.4, 21.27) * mm});
            skLineSegment(sketch, "E1420", {"start": v(-49.4, 21.27) * mm, "end": v(-49.69, 21.8) * mm});
            skLineSegment(sketch, "E1421", {"start": v(-49.69, 21.8) * mm, "end": v(-49.97, 22.36) * mm});
            skLineSegment(sketch, "E1422", {"start": v(-49.97, 22.36) * mm, "end": v(-50.25, 22.95) * mm});
            skLineSegment(sketch, "E1423", {"start": v(-50.25, 22.95) * mm, "end": v(-50.52, 23.56) * mm});
            skLineSegment(sketch, "E1424", {"start": v(-50.52, 23.56) * mm, "end": v(-50.8, 24.17) * mm});
            skLineSegment(sketch, "E1425", {"start": v(-50.8, 24.17) * mm, "end": v(-51.08, 24.77) * mm});
            skLineSegment(sketch, "E1426", {"start": v(-51.08, 24.77) * mm, "end": v(-51.36, 25.33) * mm});
            skLineSegment(sketch, "E1427", {"start": v(-51.36, 25.33) * mm, "end": v(-51.66, 25.85) * mm});
            skLineSegment(sketch, "E1428", {"start": v(-51.66, 25.85) * mm, "end": v(-51.03, 25.22) * mm});
            skLineSegment(sketch, "E1429", {"start": v(-51.03, 25.22) * mm, "end": v(-50.41, 24.64) * mm});
            skLineSegment(sketch, "E1430", {"start": v(-50.41, 24.64) * mm, "end": v(-49.8, 24.1) * mm});
            skLineSegment(sketch, "E1431", {"start": v(-49.8, 24.1) * mm, "end": v(-49.2, 23.6) * mm});
            skLineSegment(sketch, "E1432", {"start": v(-49.2, 23.6) * mm, "end": v(-48.62, 23.12) * mm});
            skLineSegment(sketch, "E1433", {"start": v(-48.62, 23.12) * mm, "end": v(-48.04, 22.65) * mm});
            skLineSegment(sketch, "E1434", {"start": v(-48.04, 22.65) * mm, "end": v(-46.9, 21.72) * mm});
            skLineSegment(sketch, "E1435", {"start": v(-46.9, 21.72) * mm, "end": v(-47.03, 22.07) * mm});
            skLineSegment(sketch, "E1436", {"start": v(-47.03, 22.07) * mm, "end": v(-47.14, 22.4) * mm});
            skLineSegment(sketch, "E1437", {"start": v(-47.14, 22.4) * mm, "end": v(-47.24, 22.7) * mm});
            skLineSegment(sketch, "E1438", {"start": v(-47.24, 22.7) * mm, "end": v(-47.34, 23) * mm});
            skLineSegment(sketch, "E1439", {"start": v(-47.34, 23) * mm, "end": v(-47.52, 23.56) * mm});
            skLineSegment(sketch, "E1440", {"start": v(-47.52, 23.56) * mm, "end": v(-47.7, 24.09) * mm});
            skLineSegment(sketch, "E1441", {"start": v(-47.7, 24.09) * mm, "end": v(-47.86, 24.62) * mm});
            skLineSegment(sketch, "E1442", {"start": v(-47.86, 24.62) * mm, "end": v(-48.04, 25.18) * mm});
            skLineSegment(sketch, "E1443", {"start": v(-48.04, 25.18) * mm, "end": v(-48.13, 25.48) * mm});
            skLineSegment(sketch, "E1444", {"start": v(-48.13, 25.48) * mm, "end": v(-48.23, 25.8) * mm});
            skLineSegment(sketch, "E1445", {"start": v(-48.23, 25.8) * mm, "end": v(-48.34, 26.14) * mm});
            skLineSegment(sketch, "E1446", {"start": v(-48.34, 26.14) * mm, "end": v(-48.45, 26.5) * mm});
            skLineSegment(sketch, "E1447", {"start": v(-48.45, 26.5) * mm, "end": v(-48.2, 26.24) * mm});
            skLineSegment(sketch, "E1448", {"start": v(-48.2, 26.24) * mm, "end": v(-47.97, 25.99) * mm});
            skLineSegment(sketch, "E1449", {"start": v(-47.97, 25.99) * mm, "end": v(-47.51, 25.52) * mm});
            skLineSegment(sketch, "E1450", {"start": v(-47.51, 25.52) * mm, "end": v(-47.06, 25.09) * mm});
            skLineSegment(sketch, "E1451", {"start": v(-47.06, 25.09) * mm, "end": v(-46.61, 24.67) * mm});
            skLineSegment(sketch, "E1452", {"start": v(-46.61, 24.67) * mm, "end": v(-46.16, 24.26) * mm});
            skLineSegment(sketch, "E1453", {"start": v(-46.16, 24.26) * mm, "end": v(-45.68, 23.83) * mm});
            skLineSegment(sketch, "E1454", {"start": v(-45.68, 23.83) * mm, "end": v(-45.18, 23.38) * mm});
            skLineSegment(sketch, "E1455", {"start": v(-45.18, 23.38) * mm, "end": v(-44.92, 23.13) * mm});
            skLineSegment(sketch, "E1456", {"start": v(-44.92, 23.13) * mm, "end": v(-44.64, 22.87) * mm});
            skLineSegment(sketch, "E1457", {"start": v(-44.64, 22.87) * mm, "end": v(-44.78, 23.27) * mm});
            skLineSegment(sketch, "E1458", {"start": v(-44.78, 23.27) * mm, "end": v(-44.9, 23.62) * mm});
            skLineSegment(sketch, "E1459", {"start": v(-44.9, 23.62) * mm, "end": v(-44.99, 23.94) * mm});
            skLineSegment(sketch, "E1460", {"start": v(-44.99, 23.94) * mm, "end": v(-45.07, 24.23) * mm});
            skLineSegment(sketch, "E1461", {"start": v(-45.07, 24.23) * mm, "end": v(-45.13, 24.5) * mm});
            skLineSegment(sketch, "E1462", {"start": v(-45.13, 24.5) * mm, "end": v(-45.18, 24.74) * mm});
            skLineSegment(sketch, "E1463", {"start": v(-45.18, 24.74) * mm, "end": v(-45.28, 25.21) * mm});
            skLineSegment(sketch, "E1464", {"start": v(-45.28, 25.21) * mm, "end": v(-45.37, 25.67) * mm});
            skLineSegment(sketch, "E1465", {"start": v(-45.37, 25.67) * mm, "end": v(-45.43, 25.91) * mm});
            skLineSegment(sketch, "E1466", {"start": v(-45.43, 25.91) * mm, "end": v(-45.5, 26.17) * mm});
            skLineSegment(sketch, "E1467", {"start": v(-45.5, 26.17) * mm, "end": v(-45.58, 26.44) * mm});
            skLineSegment(sketch, "E1468", {"start": v(-45.58, 26.44) * mm, "end": v(-45.67, 26.74) * mm});
            skLineSegment(sketch, "E1469", {"start": v(-45.67, 26.74) * mm, "end": v(-45.8, 27.07) * mm});
            skLineSegment(sketch, "E1470", {"start": v(-45.8, 27.07) * mm, "end": v(-45.94, 27.43) * mm});
            skLineSegment(sketch, "E1471", {"start": v(-45.94, 27.43) * mm, "end": v(-45.64, 27.17) * mm});
            skLineSegment(sketch, "E1472", {"start": v(-45.64, 27.17) * mm, "end": v(-45.37, 26.94) * mm});
            skLineSegment(sketch, "E1473", {"start": v(-45.37, 26.94) * mm, "end": v(-45.13, 26.73) * mm});
            skLineSegment(sketch, "E1474", {"start": v(-45.13, 26.73) * mm, "end": v(-44.9, 26.54) * mm});
            skLineSegment(sketch, "E1475", {"start": v(-44.9, 26.54) * mm, "end": v(-44.69, 26.37) * mm});
            skLineSegment(sketch, "E1476", {"start": v(-44.69, 26.37) * mm, "end": v(-44.49, 26.21) * mm});
            skLineSegment(sketch, "E1477", {"start": v(-44.49, 26.21) * mm, "end": v(-44.1, 25.92) * mm});
            skLineSegment(sketch, "E1478", {"start": v(-44.1, 25.92) * mm, "end": v(-43.72, 25.62) * mm});
            skLineSegment(sketch, "E1479", {"start": v(-43.72, 25.62) * mm, "end": v(-43.52, 25.46) * mm});
            skLineSegment(sketch, "E1480", {"start": v(-43.52, 25.46) * mm, "end": v(-43.3, 25.3) * mm});
            skLineSegment(sketch, "E1481", {"start": v(-43.3, 25.3) * mm, "end": v(-43.08, 25.1) * mm});
            skLineSegment(sketch, "E1482", {"start": v(-43.08, 25.1) * mm, "end": v(-42.83, 24.9) * mm});
            skLineSegment(sketch, "E1483", {"start": v(-42.83, 24.9) * mm, "end": v(-42.56, 24.67) * mm});
            skLineSegment(sketch, "E1484", {"start": v(-42.56, 24.67) * mm, "end": v(-42.26, 24.4) * mm});
            skLineSegment(sketch, "E1485", {"start": v(-42.26, 24.4) * mm, "end": v(-42.44, 24.83) * mm});
            skLineSegment(sketch, "E1486", {"start": v(-42.44, 24.83) * mm, "end": v(-42.6, 25.21) * mm});
            skLineSegment(sketch, "E1487", {"start": v(-42.6, 25.21) * mm, "end": v(-42.74, 25.58) * mm});
            skLineSegment(sketch, "E1488", {"start": v(-42.74, 25.58) * mm, "end": v(-42.87, 25.92) * mm});
            skLineSegment(sketch, "E1489", {"start": v(-42.87, 25.92) * mm, "end": v(-43, 26.23) * mm});
            skLineSegment(sketch, "E1490", {"start": v(-43, 26.23) * mm, "end": v(-43.1, 26.54) * mm});
            skLineSegment(sketch, "E1491", {"start": v(-43.1, 26.54) * mm, "end": v(-43.32, 27.12) * mm});
            skLineSegment(sketch, "E1492", {"start": v(-43.32, 27.12) * mm, "end": v(-43.52, 27.69) * mm});
            skLineSegment(sketch, "E1493", {"start": v(-43.52, 27.69) * mm, "end": v(-43.73, 28.28) * mm});
            skLineSegment(sketch, "E1494", {"start": v(-43.73, 28.28) * mm, "end": v(-43.84, 28.6) * mm});
            skLineSegment(sketch, "E1495", {"start": v(-43.84, 28.6) * mm, "end": v(-43.97, 28.93) * mm});
            skLineSegment(sketch, "E1496", {"start": v(-43.97, 28.93) * mm, "end": v(-44.1, 29.29) * mm});
            skLineSegment(sketch, "E1497", {"start": v(-44.1, 29.29) * mm, "end": v(-44.25, 29.67) * mm});
            skLineSegment(sketch, "E1498", {"start": v(-44.25, 29.67) * mm, "end": v(-43.95, 29.4) * mm});
            skLineSegment(sketch, "E1499", {"start": v(-43.95, 29.4) * mm, "end": v(-43.68, 29.17) * mm});
            skLineSegment(sketch, "E1500", {"start": v(-43.68, 29.17) * mm, "end": v(-43.42, 28.95) * mm});
            skLineSegment(sketch, "E1501", {"start": v(-43.42, 28.95) * mm, "end": v(-43.18, 28.74) * mm});
            skLineSegment(sketch, "E1502", {"start": v(-43.18, 28.74) * mm, "end": v(-42.74, 28.37) * mm});
            skLineSegment(sketch, "E1503", {"start": v(-42.74, 28.37) * mm, "end": v(-42.32, 28.02) * mm});
            skLineSegment(sketch, "E1504", {"start": v(-42.32, 28.02) * mm, "end": v(-41.9, 27.68) * mm});
            skLineSegment(sketch, "E1505", {"start": v(-41.9, 27.68) * mm, "end": v(-41.47, 27.3) * mm});
            skLineSegment(sketch, "E1506", {"start": v(-41.47, 27.3) * mm, "end": v(-41.23, 27.1) * mm});
            skLineSegment(sketch, "E1507", {"start": v(-41.23, 27.1) * mm, "end": v(-40.98, 26.87) * mm});
            skLineSegment(sketch, "E1508", {"start": v(-40.98, 26.87) * mm, "end": v(-40.7, 26.63) * mm});
            skLineSegment(sketch, "E1509", {"start": v(-40.7, 26.63) * mm, "end": v(-40.42, 26.36) * mm});
            skLineSegment(sketch, "E1510", {"start": v(-40.42, 26.36) * mm, "end": v(-40.6, 26.75) * mm});
            skLineSegment(sketch, "E1511", {"start": v(-40.6, 26.75) * mm, "end": v(-40.75, 27.12) * mm});
            skLineSegment(sketch, "E1512", {"start": v(-40.75, 27.12) * mm, "end": v(-40.9, 27.47) * mm});
            skLineSegment(sketch, "E1513", {"start": v(-40.9, 27.47) * mm, "end": v(-41.04, 27.8) * mm});
            skLineSegment(sketch, "E1514", {"start": v(-41.04, 27.8) * mm, "end": v(-41.29, 28.44) * mm});
            skLineSegment(sketch, "E1515", {"start": v(-41.29, 28.44) * mm, "end": v(-41.52, 29.06) * mm});
            skLineSegment(sketch, "E1516", {"start": v(-41.52, 29.06) * mm, "end": v(-41.74, 29.7) * mm});
            skLineSegment(sketch, "E1517", {"start": v(-41.74, 29.7) * mm, "end": v(-41.98, 30.36) * mm});
            skLineSegment(sketch, "E1518", {"start": v(-41.98, 30.36) * mm, "end": v(-42.1, 30.72) * mm});
            skLineSegment(sketch, "E1519", {"start": v(-42.1, 30.72) * mm, "end": v(-42.25, 31.1) * mm});
            skLineSegment(sketch, "E1520", {"start": v(-42.25, 31.1) * mm, "end": v(-42.4, 31.51) * mm});
            skLineSegment(sketch, "E1521", {"start": v(-42.4, 31.51) * mm, "end": v(-42.56, 31.95) * mm});
            skLineSegment(sketch, "E1522", {"start": v(-42.56, 31.95) * mm, "end": v(-42.21, 31.64) * mm});
            skLineSegment(sketch, "E1523", {"start": v(-42.21, 31.64) * mm, "end": v(-41.9, 31.36) * mm});
            skLineSegment(sketch, "E1524", {"start": v(-41.9, 31.36) * mm, "end": v(-41.61, 31.1) * mm});
            skLineSegment(sketch, "E1525", {"start": v(-41.61, 31.1) * mm, "end": v(-41.35, 30.88) * mm});
            skLineSegment(sketch, "E1526", {"start": v(-41.35, 30.88) * mm, "end": v(-41.1, 30.67) * mm});
            skLineSegment(sketch, "E1527", {"start": v(-41.1, 30.67) * mm, "end": v(-40.87, 30.47) * mm});
            skLineSegment(sketch, "E1528", {"start": v(-40.87, 30.47) * mm, "end": v(-40.43, 30.1) * mm});
            skLineSegment(sketch, "E1529", {"start": v(-40.43, 30.1) * mm, "end": v(-40, 29.73) * mm});
            skLineSegment(sketch, "E1530", {"start": v(-40, 29.73) * mm, "end": v(-39.55, 29.34) * mm});
            skLineSegment(sketch, "E1531", {"start": v(-39.55, 29.34) * mm, "end": v(-39.31, 29.13) * mm});
            skLineSegment(sketch, "E1532", {"start": v(-39.31, 29.13) * mm, "end": v(-39.06, 28.9) * mm});
            skLineSegment(sketch, "E1533", {"start": v(-39.06, 28.9) * mm, "end": v(-38.78, 28.63) * mm});
            skLineSegment(sketch, "E1534", {"start": v(-38.78, 28.63) * mm, "end": v(-38.48, 28.35) * mm});
            skLineSegment(sketch, "E1535", {"start": v(-38.48, 28.35) * mm, "end": v(-38.96, 29.95) * mm});
            skLineSegment(sketch, "E1536", {"start": v(-38.96, 29.95) * mm, "end": v(-39.44, 31.51) * mm});
            skLineSegment(sketch, "E1537", {"start": v(-39.44, 31.51) * mm, "end": v(-39.93, 33.07) * mm});
            skLineSegment(sketch, "E1538", {"start": v(-39.93, 33.07) * mm, "end": v(-40.4, 34.67) * mm});
            skLineSegment(sketch, "E1539", {"start": v(-40.4, 34.67) * mm, "end": v(-40.03, 34.35) * mm});
            skLineSegment(sketch, "E1540", {"start": v(-40.03, 34.35) * mm, "end": v(-39.66, 34.01) * mm});
            skLineSegment(sketch, "E1541", {"start": v(-39.66, 34.01) * mm, "end": v(-39.3, 33.65) * mm});
            skLineSegment(sketch, "E1542", {"start": v(-39.3, 33.65) * mm, "end": v(-38.95, 33.26) * mm});
            skLineSegment(sketch, "E1543", {"start": v(-38.95, 33.26) * mm, "end": v(-38.63, 32.85) * mm});
            skLineSegment(sketch, "E1544", {"start": v(-38.63, 32.85) * mm, "end": v(-38.35, 32.43) * mm});
            skLineSegment(sketch, "E1545", {"start": v(-38.35, 32.43) * mm, "end": v(-38.1, 31.99) * mm});
            skLineSegment(sketch, "E1546", {"start": v(-38.1, 31.99) * mm, "end": v(-37.9, 31.53) * mm});
            skLineSegment(sketch, "E1547", {"start": v(-37.9, 31.53) * mm, "end": v(-37.7, 30.94) * mm});
            skLineSegment(sketch, "E1548", {"start": v(-37.7, 30.94) * mm, "end": v(-37.54, 30.35) * mm});
            skLineSegment(sketch, "E1549", {"start": v(-37.54, 30.35) * mm, "end": v(-37.44, 29.75) * mm});
            skLineSegment(sketch, "E1550", {"start": v(-37.44, 29.75) * mm, "end": v(-37.38, 29.15) * mm});
            skLineSegment(sketch, "E1551", {"start": v(-37.38, 29.15) * mm, "end": v(-37.37, 28.55) * mm});
            skLineSegment(sketch, "E1552", {"start": v(-37.37, 28.55) * mm, "end": v(-37.4, 27.95) * mm});
            skLineSegment(sketch, "E1553", {"start": v(-37.4, 27.95) * mm, "end": v(-37.5, 27.36) * mm});
            skLineSegment(sketch, "E1554", {"start": v(-37.5, 27.36) * mm, "end": v(-37.62, 26.77) * mm});
            skLineSegment(sketch, "E1555", {"start": v(-37.62, 26.77) * mm, "end": v(-37.79, 26.19) * mm});
            skLineSegment(sketch, "E1556", {"start": v(-37.79, 26.19) * mm, "end": v(-38, 25.61) * mm});
            skLineSegment(sketch, "E1557", {"start": v(-38, 25.61) * mm, "end": v(-38.26, 25.05) * mm});
            skLineSegment(sketch, "E1558", {"start": v(-38.26, 25.05) * mm, "end": v(-38.56, 24.5) * mm});
            skLineSegment(sketch, "E1559", {"start": v(-38.56, 24.5) * mm, "end": v(-38.9, 23.97) * mm});
            skLineSegment(sketch, "E1560", {"start": v(-38.9, 23.97) * mm, "end": v(-39.28, 23.45) * mm});
            skLineSegment(sketch, "E1561", {"start": v(-39.28, 23.45) * mm, "end": v(-39.7, 22.96) * mm});
            skLineSegment(sketch, "E1562", {"start": v(-39.7, 22.96) * mm, "end": v(-40.16, 22.48) * mm});
            skLineSegment(sketch, "E1563", {"start": v(-40.16, 22.48) * mm, "end": v(-40.5, 22.17) * mm});
            skLineSegment(sketch, "E1564", {"start": v(-40.5, 22.17) * mm, "end": v(-40.85, 21.87) * mm});
            skLineSegment(sketch, "E1565", {"start": v(-40.85, 21.87) * mm, "end": v(-41.22, 21.6) * mm});
            skLineSegment(sketch, "E1566", {"start": v(-41.22, 21.6) * mm, "end": v(-41.6, 21.33) * mm});
            skLineSegment(sketch, "E1567", {"start": v(-41.6, 21.33) * mm, "end": v(-42, 21.09) * mm});
            skLineSegment(sketch, "E1568", {"start": v(-42, 21.09) * mm, "end": v(-42.4, 20.87) * mm});
            skLineSegment(sketch, "E1569", {"start": v(-42.4, 20.87) * mm, "end": v(-42.82, 20.66) * mm});
            skLineSegment(sketch, "E1570", {"start": v(-42.82, 20.66) * mm, "end": v(-43.24, 20.48) * mm});
            skLineSegment(sketch, "E1571", {"start": v(-43.24, 20.48) * mm, "end": v(-43.67, 20.32) * mm});
            skLineSegment(sketch, "E1572", {"start": v(-43.67, 20.32) * mm, "end": v(-44.1, 20.17) * mm});
            skLineSegment(sketch, "E1573", {"start": v(-44.1, 20.17) * mm, "end": v(-44.54, 20.05) * mm});
            skLineSegment(sketch, "E1574", {"start": v(-44.54, 20.05) * mm, "end": v(-44.98, 19.95) * mm});
            skLineSegment(sketch, "E1575", {"start": v(-44.98, 19.95) * mm, "end": v(-45.43, 19.86) * mm});
            skLineSegment(sketch, "E1576", {"start": v(-45.43, 19.86) * mm, "end": v(-45.87, 19.8) * mm});
            skLineSegment(sketch, "E1577", {"start": v(-45.87, 19.8) * mm, "end": v(-46.32, 19.76) * mm});
            skLineSegment(sketch, "E1578", {"start": v(-46.32, 19.76) * mm, "end": v(-46.77, 19.75) * mm});
            skLineSegment(sketch, "E1579", {"start": v(-46.77, 19.75) * mm, "end": v(-47.2, 19.75) * mm});
            skLineSegment(sketch, "E1580", {"start": v(-47.2, 19.75) * mm, "end": v(-47.65, 19.78) * mm});
            skLineSegment(sketch, "E1581", {"start": v(-47.65, 19.78) * mm, "end": v(-48.09, 19.83) * mm});
            skLineSegment(sketch, "E1582", {"start": v(-48.09, 19.83) * mm, "end": v(-48.52, 19.9) * mm});
            skLineSegment(sketch, "E1583", {"start": v(-48.52, 19.9) * mm, "end": v(-48.94, 20) * mm});
            skLineSegment(sketch, "E1584", {"start": v(-48.94, 20) * mm, "end": v(-49.35, 20.12) * mm});
            skLineSegment(sketch, "E1585", {"start": v(-49.35, 20.12) * mm, "end": v(-49.76, 20.26) * mm});
            skLineSegment(sketch, "E1586", {"start": v(-49.76, 20.26) * mm, "end": v(-50.16, 20.42) * mm});
            skLineSegment(sketch, "E1587", {"start": v(-50.16, 20.42) * mm, "end": v(-50.54, 20.62) * mm});
            skLineSegment(sketch, "E1588", {"start": v(-50.54, 20.62) * mm, "end": v(-50.92, 20.83) * mm});
            skLineSegment(sketch, "E1589", {"start": v(-50.92, 20.83) * mm, "end": v(-51.28, 21.07) * mm});
            skLineSegment(sketch, "E1590", {"start": v(-51.28, 21.07) * mm, "end": v(-51.62, 21.34) * mm});
            skLineSegment(sketch, "E1591", {"start": v(-51.62, 21.34) * mm, "end": v(-51.95, 21.63) * mm});
            skLineSegment(sketch, "E1592", {"start": v(-51.95, 21.63) * mm, "end": v(-52.26, 21.94) * mm});
            skLineSegment(sketch, "E1593", {"start": v(-52.26, 21.94) * mm, "end": v(-52.56, 22.28) * mm});
            skLineSegment(sketch, "E1594", {"start": v(-52.56, 22.28) * mm, "end": v(-52.83, 22.65) * mm});
            skLineSegment(sketch, "E1595", {"start": v(-56.35, 35.36) * mm, "end": v(-56.49, 34.95) * mm});
            skLineSegment(sketch, "E1596", {"start": v(-56.49, 34.95) * mm, "end": v(-56.65, 34.54) * mm});
            skLineSegment(sketch, "E1597", {"start": v(-56.65, 34.54) * mm, "end": v(-56.84, 34.15) * mm});
            skLineSegment(sketch, "E1598", {"start": v(-56.84, 34.15) * mm, "end": v(-57.04, 33.78) * mm});
            skLineSegment(sketch, "E1599", {"start": v(-57.04, 33.78) * mm, "end": v(-57.25, 33.42) * mm});
            skLineSegment(sketch, "E1600", {"start": v(-57.25, 33.42) * mm, "end": v(-57.49, 33.08) * mm});
            skLineSegment(sketch, "E1601", {"start": v(-57.49, 33.08) * mm, "end": v(-57.74, 32.75) * mm});
            skLineSegment(sketch, "E1602", {"start": v(-57.74, 32.75) * mm, "end": v(-58, 32.45) * mm});
            skLineSegment(sketch, "E1603", {"start": v(-58, 32.45) * mm, "end": v(-58.28, 32.16) * mm});
            skLineSegment(sketch, "E1604", {"start": v(-58.28, 32.16) * mm, "end": v(-58.57, 31.89) * mm});
            skLineSegment(sketch, "E1605", {"start": v(-58.57, 31.89) * mm, "end": v(-58.87, 31.64) * mm});
            skLineSegment(sketch, "E1606", {"start": v(-58.87, 31.64) * mm, "end": v(-59.18, 31.4) * mm});
            skLineSegment(sketch, "E1607", {"start": v(-59.18, 31.4) * mm, "end": v(-59.5, 31.2) * mm});
            skLineSegment(sketch, "E1608", {"start": v(-59.5, 31.2) * mm, "end": v(-59.83, 31) * mm});
            skLineSegment(sketch, "E1609", {"start": v(-59.83, 31) * mm, "end": v(-60.17, 30.84) * mm});
            skLineSegment(sketch, "E1610", {"start": v(-60.17, 30.84) * mm, "end": v(-60.51, 30.7) * mm});
            skLineSegment(sketch, "E1611", {"start": v(-60.51, 30.7) * mm, "end": v(-60.87, 30.57) * mm});
            skLineSegment(sketch, "E1612", {"start": v(-60.87, 30.57) * mm, "end": v(-61.22, 30.47) * mm});
            skLineSegment(sketch, "E1613", {"start": v(-61.22, 30.47) * mm, "end": v(-61.58, 30.4) * mm});
            skLineSegment(sketch, "E1614", {"start": v(-61.58, 30.4) * mm, "end": v(-61.94, 30.34) * mm});
            skLineSegment(sketch, "E1615", {"start": v(-61.94, 30.34) * mm, "end": v(-62.3, 30.32) * mm});
            skLineSegment(sketch, "E1616", {"start": v(-62.3, 30.32) * mm, "end": v(-62.67, 30.32) * mm});
            skLineSegment(sketch, "E1617", {"start": v(-62.67, 30.32) * mm, "end": v(-63.04, 30.35) * mm});
            skLineSegment(sketch, "E1618", {"start": v(-63.04, 30.35) * mm, "end": v(-63.4, 30.4) * mm});
            skLineSegment(sketch, "E1619", {"start": v(-63.4, 30.4) * mm, "end": v(-63.77, 30.49) * mm});
            skLineSegment(sketch, "E1620", {"start": v(-63.77, 30.49) * mm, "end": v(-64.13, 30.6) * mm});
            skLineSegment(sketch, "E1621", {"start": v(-64.13, 30.6) * mm, "end": v(-64.48, 30.73) * mm});
            skLineSegment(sketch, "E1622", {"start": v(-64.48, 30.73) * mm, "end": v(-64.82, 30.9) * mm});
            skLineSegment(sketch, "E1623", {"start": v(-64.82, 30.9) * mm, "end": v(-65.14, 31.07) * mm});
            skLineSegment(sketch, "E1624", {"start": v(-65.14, 31.07) * mm, "end": v(-65.44, 31.28) * mm});
            skLineSegment(sketch, "E1625", {"start": v(-65.44, 31.28) * mm, "end": v(-65.73, 31.5) * mm});
            skLineSegment(sketch, "E1626", {"start": v(-65.73, 31.5) * mm, "end": v(-66, 31.75) * mm});
            skLineSegment(sketch, "E1627", {"start": v(-66, 31.75) * mm, "end": v(-66.26, 32) * mm});
            skLineSegment(sketch, "E1628", {"start": v(-66.26, 32) * mm, "end": v(-66.5, 32.29) * mm});
            skLineSegment(sketch, "E1629", {"start": v(-66.5, 32.29) * mm, "end": v(-66.72, 32.59) * mm});
            skLineSegment(sketch, "E1630", {"start": v(-66.72, 32.59) * mm, "end": v(-66.92, 32.9) * mm});
            skLineSegment(sketch, "E1631", {"start": v(-66.92, 32.9) * mm, "end": v(-67.1, 33.23) * mm});
            skLineSegment(sketch, "E1632", {"start": v(-67.1, 33.23) * mm, "end": v(-67.27, 33.57) * mm});
            skLineSegment(sketch, "E1633", {"start": v(-67.27, 33.57) * mm, "end": v(-67.42, 33.92) * mm});
            skLineSegment(sketch, "E1634", {"start": v(-67.42, 33.92) * mm, "end": v(-67.55, 34.29) * mm});
            skLineSegment(sketch, "E1635", {"start": v(-67.55, 34.29) * mm, "end": v(-67.66, 34.66) * mm});
            skLineSegment(sketch, "E1636", {"start": v(-67.66, 34.66) * mm, "end": v(-67.75, 35.05) * mm});
            skLineSegment(sketch, "E1637", {"start": v(-67.75, 35.05) * mm, "end": v(-67.81, 35.44) * mm});
            skLineSegment(sketch, "E1638", {"start": v(-67.81, 35.44) * mm, "end": v(-67.86, 35.85) * mm});
            skLineSegment(sketch, "E1639", {"start": v(-67.86, 35.85) * mm, "end": v(-67.88, 36.25) * mm});
            skLineSegment(sketch, "E1640", {"start": v(-67.88, 36.25) * mm, "end": v(-67.88, 36.67) * mm});
            skLineSegment(sketch, "E1641", {"start": v(-67.88, 36.67) * mm, "end": v(-67.86, 37.08) * mm});
            skLineSegment(sketch, "E1642", {"start": v(-67.86, 37.08) * mm, "end": v(-67.82, 37.5) * mm});
            skLineSegment(sketch, "E1643", {"start": v(-67.82, 37.5) * mm, "end": v(-67.75, 37.93) * mm});
            skLineSegment(sketch, "E1644", {"start": v(-67.75, 37.93) * mm, "end": v(-67.66, 38.35) * mm});
            skLineSegment(sketch, "E1645", {"start": v(-67.66, 38.35) * mm, "end": v(-67.54, 38.78) * mm});
            skLineSegment(sketch, "E1646", {"start": v(-67.54, 38.78) * mm, "end": v(-67.51, 38.88) * mm});
            skLineSegment(sketch, "E1647", {"start": v(-67.51, 38.88) * mm, "end": v(-67.5, 38.93) * mm});
            skLineSegment(sketch, "E1648", {"start": v(-67.5, 38.93) * mm, "end": v(-67.46, 39.04) * mm});
            skLineSegment(sketch, "E1649", {"start": v(-67.46, 39.04) * mm, "end": v(-67.3, 39.48) * mm});
            skLineSegment(sketch, "E1650", {"start": v(-67.3, 39.48) * mm, "end": v(-67.11, 39.9) * mm});
            skLineSegment(sketch, "E1651", {"start": v(-67.11, 39.9) * mm, "end": v(-66.91, 40.3) * mm});
            skLineSegment(sketch, "E1652", {"start": v(-66.91, 40.3) * mm, "end": v(-66.69, 40.68) * mm});
            skLineSegment(sketch, "E1653", {"start": v(-66.69, 40.68) * mm, "end": v(-66.45, 41.05) * mm});
            skLineSegment(sketch, "E1654", {"start": v(-66.45, 41.05) * mm, "end": v(-66.19, 41.4) * mm});
            skLineSegment(sketch, "E1655", {"start": v(-66.19, 41.4) * mm, "end": v(-65.91, 41.72) * mm});
            skLineSegment(sketch, "E1656", {"start": v(-65.91, 41.72) * mm, "end": v(-65.62, 42.03) * mm});
            skLineSegment(sketch, "E1657", {"start": v(-65.62, 42.03) * mm, "end": v(-65.32, 42.32) * mm});
            skLineSegment(sketch, "E1658", {"start": v(-65.32, 42.32) * mm, "end": v(-65, 42.58) * mm});
            skLineSegment(sketch, "E1659", {"start": v(-65, 42.58) * mm, "end": v(-64.67, 42.82) * mm});
            skLineSegment(sketch, "E1660", {"start": v(-64.67, 42.82) * mm, "end": v(-64.33, 43.04) * mm});
            skLineSegment(sketch, "E1661", {"start": v(-64.33, 43.04) * mm, "end": v(-64.24, 43.1) * mm});
            skLineSegment(sketch, "E1662", {"start": v(-64.24, 43.1) * mm, "end": v(-64.2, 43.12) * mm});
            skLineSegment(sketch, "E1663", {"start": v(-64.2, 43.12) * mm, "end": v(-64.2, 43.11) * mm});
            skLineSegment(sketch, "E1664", {"start": v(-64.2, 43.11) * mm, "end": v(-64.2, 43.1) * mm});
            skLineSegment(sketch, "E1665", {"start": v(-64.2, 43.1) * mm, "end": v(-64.22, 42.91) * mm});
            skLineSegment(sketch, "E1666", {"start": v(-64.22, 42.91) * mm, "end": v(-64.28, 42.55) * mm});
            skLineSegment(sketch, "E1667", {"start": v(-64.28, 42.55) * mm, "end": v(-64.7, 39.69) * mm});
            skLineSegment(sketch, "E1668", {"start": v(-64.7, 39.69) * mm, "end": v(-64.82, 38.97) * mm});
            skLineSegment(sketch, "E1669", {"start": v(-64.82, 38.97) * mm, "end": v(-64.87, 38.62) * mm});
            skLineSegment(sketch, "E1670", {"start": v(-64.87, 38.62) * mm, "end": v(-64.88, 38.57) * mm});
            skLineSegment(sketch, "E1671", {"start": v(-64.88, 38.57) * mm, "end": v(-64.88, 38.55) * mm});
            skLineSegment(sketch, "E1672", {"start": v(-64.88, 38.55) * mm, "end": v(-64.87, 38.56) * mm});
            skLineSegment(sketch, "E1673", {"start": v(-64.87, 38.56) * mm, "end": v(-64.8, 38.67) * mm});
            skLineSegment(sketch, "E1674", {"start": v(-64.8, 38.67) * mm, "end": v(-64.68, 38.9) * mm});
            skLineSegment(sketch, "E1675", {"start": v(-64.68, 38.9) * mm, "end": v(-64.39, 39.39) * mm});
            skLineSegment(sketch, "E1676", {"start": v(-64.39, 39.39) * mm, "end": v(-64.08, 39.91) * mm});
            skLineSegment(sketch, "E1677", {"start": v(-64.08, 39.91) * mm, "end": v(-63.43, 41.02) * mm});
            skLineSegment(sketch, "E1678", {"start": v(-63.43, 41.02) * mm, "end": v(-63.1, 41.57) * mm});
            skLineSegment(sketch, "E1679", {"start": v(-63.1, 41.57) * mm, "end": v(-62.79, 42.1) * mm});
            skLineSegment(sketch, "E1680", {"start": v(-62.79, 42.1) * mm, "end": v(-62.5, 42.58) * mm});
            skLineSegment(sketch, "E1681", {"start": v(-62.5, 42.58) * mm, "end": v(-62.23, 43.02) * mm});
            skLineSegment(sketch, "E1682", {"start": v(-62.23, 43.02) * mm, "end": v(-62.12, 43.2) * mm});
            skLineSegment(sketch, "E1683", {"start": v(-62.12, 43.2) * mm, "end": v(-62.01, 43.38) * mm});
            skLineSegment(sketch, "E1684", {"start": v(-62.01, 43.38) * mm, "end": v(-61.92, 43.53) * mm});
            skLineSegment(sketch, "E1685", {"start": v(-61.92, 43.53) * mm, "end": v(-61.84, 43.66) * mm});
            skLineSegment(sketch, "E1686", {"start": v(-61.84, 43.66) * mm, "end": v(-61.78, 43.76) * mm});
            skLineSegment(sketch, "E1687", {"start": v(-61.78, 43.76) * mm, "end": v(-61.73, 43.84) * mm});
            skLineSegment(sketch, "E1688", {"start": v(-61.73, 43.84) * mm, "end": v(-61.7, 43.88) * mm});
            skLineSegment(sketch, "E1689", {"start": v(-61.7, 43.88) * mm, "end": v(-61.69, 43.9) * mm});
            skLineSegment(sketch, "E1690", {"start": v(-61.69, 43.9) * mm, "end": v(-61.74, 39.39) * mm});
            skLineSegment(sketch, "E1691", {"start": v(-61.74, 39.39) * mm, "end": v(-61.76, 37.13) * mm});
            skLineSegment(sketch, "E1692", {"start": v(-61.76, 37.13) * mm, "end": v(-61.76, 36.85) * mm});
            skLineSegment(sketch, "E1693", {"start": v(-61.76, 36.85) * mm, "end": v(-61.76, 36.71) * mm});
            skLineSegment(sketch, "E1694", {"start": v(-61.76, 36.71) * mm, "end": v(-61.76, 36.69) * mm});
            skLineSegment(sketch, "E1695", {"start": v(-61.76, 36.69) * mm, "end": v(-61.75, 36.72) * mm});
            skLineSegment(sketch, "E1696", {"start": v(-61.75, 36.72) * mm, "end": v(-61.72, 36.79) * mm});
            skLineSegment(sketch, "E1697", {"start": v(-61.72, 36.79) * mm, "end": v(-61.52, 37.31) * mm});
            skLineSegment(sketch, "E1698", {"start": v(-61.52, 37.31) * mm, "end": v(-61.12, 38.36) * mm});
            skLineSegment(sketch, "E1699", {"start": v(-61.12, 38.36) * mm, "end": v(-59.5, 42.56) * mm});
            skLineSegment(sketch, "E1700", {"start": v(-59.5, 42.56) * mm, "end": v(-59.3, 43.08) * mm});
            skLineSegment(sketch, "E1701", {"start": v(-59.3, 43.08) * mm, "end": v(-59.2, 43.34) * mm});
            skLineSegment(sketch, "E1702", {"start": v(-59.2, 43.34) * mm, "end": v(-59.17, 43.4) * mm});
            skLineSegment(sketch, "E1703", {"start": v(-59.17, 43.4) * mm, "end": v(-59.17, 43.4) * mm});
            skLineSegment(sketch, "E1704", {"start": v(-59.17, 43.4) * mm, "end": v(-59.17, 43.38) * mm});
            skLineSegment(sketch, "E1705", {"start": v(-59.17, 43.38) * mm, "end": v(-59.15, 43.34) * mm});
            skLineSegment(sketch, "E1706", {"start": v(-59.15, 43.34) * mm, "end": v(-59.13, 43.27) * mm});
            skLineSegment(sketch, "E1707", {"start": v(-59.13, 43.27) * mm, "end": v(-59.11, 43.17) * mm});
            skLineSegment(sketch, "E1708", {"start": v(-59.11, 43.17) * mm, "end": v(-59.1, 43.06) * mm});
            skLineSegment(sketch, "E1709", {"start": v(-59.1, 43.06) * mm, "end": v(-59.04, 42.76) * mm});
            skLineSegment(sketch, "E1710", {"start": v(-59.04, 42.76) * mm, "end": v(-58.98, 42.39) * mm});
            skLineSegment(sketch, "E1711", {"start": v(-58.98, 42.39) * mm, "end": v(-58.92, 41.96) * mm});
            skLineSegment(sketch, "E1712", {"start": v(-58.92, 41.96) * mm, "end": v(-58.85, 41.48) * mm});
            skLineSegment(sketch, "E1713", {"start": v(-58.85, 41.48) * mm, "end": v(-58.58, 39.45) * mm});
            skLineSegment(sketch, "E1714", {"start": v(-58.58, 39.45) * mm, "end": v(-58.53, 38.97) * mm});
            skLineSegment(sketch, "E1715", {"start": v(-58.53, 38.97) * mm, "end": v(-58.48, 38.54) * mm});
            skLineSegment(sketch, "E1716", {"start": v(-58.48, 38.54) * mm, "end": v(-58.47, 38.44) * mm});
            skLineSegment(sketch, "E1717", {"start": v(-58.47, 38.44) * mm, "end": v(-58.47, 38.4) * mm});
            skLineSegment(sketch, "E1718", {"start": v(-58.47, 38.4) * mm, "end": v(-58.47, 38.4) * mm});
            skLineSegment(sketch, "E1719", {"start": v(-58.47, 38.4) * mm, "end": v(-58.46, 38.4) * mm});
            skLineSegment(sketch, "E1720", {"start": v(-58.46, 38.4) * mm, "end": v(-58.4, 38.54) * mm});
            skLineSegment(sketch, "E1721", {"start": v(-58.4, 38.54) * mm, "end": v(-58.3, 38.8) * mm});
            skLineSegment(sketch, "E1722", {"start": v(-58.3, 38.8) * mm, "end": v(-57.5, 40.86) * mm});
            skLineSegment(sketch, "E1723", {"start": v(-57.5, 40.86) * mm, "end": v(-57.3, 41.38) * mm});
            skLineSegment(sketch, "E1724", {"start": v(-57.3, 41.38) * mm, "end": v(-57.2, 41.63) * mm});
            skLineSegment(sketch, "E1725", {"start": v(-57.2, 41.63) * mm, "end": v(-57.2, 41.67) * mm});
            skLineSegment(sketch, "E1726", {"start": v(-57.2, 41.67) * mm, "end": v(-57.18, 41.68) * mm});
            skLineSegment(sketch, "E1727", {"start": v(-57.18, 41.68) * mm, "end": v(-57.17, 41.67) * mm});
            skLineSegment(sketch, "E1728", {"start": v(-57.17, 41.67) * mm, "end": v(-57.1, 41.57) * mm});
            skLineSegment(sketch, "E1729", {"start": v(-57.1, 41.57) * mm, "end": v(-56.97, 41.37) * mm});
            skLineSegment(sketch, "E1730", {"start": v(-56.97, 41.37) * mm, "end": v(-56.73, 40.95) * mm});
            skLineSegment(sketch, "E1731", {"start": v(-56.73, 40.95) * mm, "end": v(-56.53, 40.5) * mm});
            skLineSegment(sketch, "E1732", {"start": v(-56.53, 40.5) * mm, "end": v(-56.35, 40.05) * mm});
            skLineSegment(sketch, "E1733", {"start": v(-56.35, 40.05) * mm, "end": v(-56.2, 39.57) * mm});
            skLineSegment(sketch, "E1734", {"start": v(-56.2, 39.57) * mm, "end": v(-56.1, 39.08) * mm});
            skLineSegment(sketch, "E1735", {"start": v(-56.1, 39.08) * mm, "end": v(-56.03, 38.57) * mm});
            skLineSegment(sketch, "E1736", {"start": v(-56.03, 38.57) * mm, "end": v(-55.99, 38.05) * mm});
            skLineSegment(sketch, "E1737", {"start": v(-55.99, 38.05) * mm, "end": v(-55.98, 37.52) * mm});
            skLineSegment(sketch, "E1738", {"start": v(-55.98, 37.52) * mm, "end": v(-56.02, 37) * mm});
            skLineSegment(sketch, "E1739", {"start": v(-56.02, 37) * mm, "end": v(-56.09, 36.45) * mm});
            skLineSegment(sketch, "E1740", {"start": v(-56.09, 36.45) * mm, "end": v(-56.2, 35.9) * mm});
            skLineSegment(sketch, "E1741", {"start": v(-56.2, 35.9) * mm, "end": v(-56.35, 35.36) * mm});
            skLineSegment(sketch, "E1742", {"start": v(-71.84, 42.54) * mm, "end": v(-72.27, 42.64) * mm});
            skLineSegment(sketch, "E1743", {"start": v(-72.27, 42.64) * mm, "end": v(-72.68, 42.77) * mm});
            skLineSegment(sketch, "E1744", {"start": v(-72.68, 42.77) * mm, "end": v(-73.09, 42.9) * mm});
            skLineSegment(sketch, "E1745", {"start": v(-73.09, 42.9) * mm, "end": v(-73.48, 43.07) * mm});
            skLineSegment(sketch, "E1746", {"start": v(-73.48, 43.07) * mm, "end": v(-73.86, 43.25) * mm});
            skLineSegment(sketch, "E1747", {"start": v(-73.86, 43.25) * mm, "end": v(-74.22, 43.45) * mm});
            skLineSegment(sketch, "E1748", {"start": v(-74.22, 43.45) * mm, "end": v(-74.57, 43.67) * mm});
            skLineSegment(sketch, "E1749", {"start": v(-74.57, 43.67) * mm, "end": v(-74.9, 43.9) * mm});
            skLineSegment(sketch, "E1750", {"start": v(-74.9, 43.9) * mm, "end": v(-75.22, 44.15) * mm});
            skLineSegment(sketch, "E1751", {"start": v(-75.22, 44.15) * mm, "end": v(-75.51, 44.41) * mm});
            skLineSegment(sketch, "E1752", {"start": v(-75.51, 44.41) * mm, "end": v(-75.8, 44.69) * mm});
            skLineSegment(sketch, "E1753", {"start": v(-75.8, 44.69) * mm, "end": v(-76.05, 44.98) * mm});
            skLineSegment(sketch, "E1754", {"start": v(-76.05, 44.98) * mm, "end": v(-76.3, 45.28) * mm});
            skLineSegment(sketch, "E1755", {"start": v(-76.3, 45.28) * mm, "end": v(-76.51, 45.59) * mm});
            skLineSegment(sketch, "E1756", {"start": v(-76.51, 45.59) * mm, "end": v(-76.71, 45.9) * mm});
            skLineSegment(sketch, "E1757", {"start": v(-76.71, 45.9) * mm, "end": v(-76.9, 46.23) * mm});
            skLineSegment(sketch, "E1758", {"start": v(-76.9, 46.23) * mm, "end": v(-77.05, 46.57) * mm});
            skLineSegment(sketch, "E1759", {"start": v(-77.05, 46.57) * mm, "end": v(-77.18, 46.92) * mm});
            skLineSegment(sketch, "E1760", {"start": v(-77.18, 46.92) * mm, "end": v(-77.3, 47.27) * mm});
            skLineSegment(sketch, "E1761", {"start": v(-77.3, 47.27) * mm, "end": v(-77.38, 47.62) * mm});
            skLineSegment(sketch, "E1762", {"start": v(-77.38, 47.62) * mm, "end": v(-77.44, 47.98) * mm});
            skLineSegment(sketch, "E1763", {"start": v(-77.44, 47.98) * mm, "end": v(-77.47, 48.35) * mm});
            skLineSegment(sketch, "E1764", {"start": v(-77.47, 48.35) * mm, "end": v(-77.48, 48.72) * mm});
            skLineSegment(sketch, "E1765", {"start": v(-77.48, 48.72) * mm, "end": v(-77.46, 49.09) * mm});
            skLineSegment(sketch, "E1766", {"start": v(-77.46, 49.09) * mm, "end": v(-77.41, 49.46) * mm});
            skLineSegment(sketch, "E1767", {"start": v(-77.41, 49.46) * mm, "end": v(-77.34, 49.83) * mm});
            skLineSegment(sketch, "E1768", {"start": v(-77.34, 49.83) * mm, "end": v(-77.24, 50.19) * mm});
            skLineSegment(sketch, "E1769", {"start": v(-77.24, 50.19) * mm, "end": v(-77.11, 50.53) * mm});
            skLineSegment(sketch, "E1770", {"start": v(-77.11, 50.53) * mm, "end": v(-76.96, 50.87) * mm});
            skLineSegment(sketch, "E1771", {"start": v(-76.96, 50.87) * mm, "end": v(-76.79, 51.2) * mm});
            skLineSegment(sketch, "E1772", {"start": v(-76.79, 51.2) * mm, "end": v(-76.6, 51.5) * mm});
            skLineSegment(sketch, "E1773", {"start": v(-76.6, 51.5) * mm, "end": v(-76.38, 51.8) * mm});
            skLineSegment(sketch, "E1774", {"start": v(-76.38, 51.8) * mm, "end": v(-76.14, 52.08) * mm});
            skLineSegment(sketch, "E1775", {"start": v(-76.14, 52.08) * mm, "end": v(-75.88, 52.34) * mm});
            skLineSegment(sketch, "E1776", {"start": v(-75.88, 52.34) * mm, "end": v(-75.6, 52.6) * mm});
            skLineSegment(sketch, "E1777", {"start": v(-75.6, 52.6) * mm, "end": v(-75.32, 52.83) * mm});
            skLineSegment(sketch, "E1778", {"start": v(-75.32, 52.83) * mm, "end": v(-75, 53.04) * mm});
            skLineSegment(sketch, "E1779", {"start": v(-75, 53.04) * mm, "end": v(-74.68, 53.24) * mm});
            skLineSegment(sketch, "E1780", {"start": v(-74.68, 53.24) * mm, "end": v(-74.35, 53.42) * mm});
            skLineSegment(sketch, "E1781", {"start": v(-74.35, 53.42) * mm, "end": v(-74, 53.59) * mm});
            skLineSegment(sketch, "E1782", {"start": v(-74, 53.59) * mm, "end": v(-73.63, 53.73) * mm});
            skLineSegment(sketch, "E1783", {"start": v(-73.63, 53.73) * mm, "end": v(-73.26, 53.85) * mm});
            skLineSegment(sketch, "E1784", {"start": v(-73.26, 53.85) * mm, "end": v(-72.87, 53.96) * mm});
            skLineSegment(sketch, "E1785", {"start": v(-72.87, 53.96) * mm, "end": v(-72.48, 54.04) * mm});
            skLineSegment(sketch, "E1786", {"start": v(-72.48, 54.04) * mm, "end": v(-72.07, 54.1) * mm});
            skLineSegment(sketch, "E1787", {"start": v(-72.07, 54.1) * mm, "end": v(-71.66, 54.15) * mm});
            skLineSegment(sketch, "E1788", {"start": v(-71.66, 54.15) * mm, "end": v(-71.24, 54.17) * mm});
            skLineSegment(sketch, "E1789", {"start": v(-71.24, 54.17) * mm, "end": v(-70.82, 54.16) * mm});
            skLineSegment(sketch, "E1790", {"start": v(-70.82, 54.16) * mm, "end": v(-70.4, 54.14) * mm});
            skLineSegment(sketch, "E1791", {"start": v(-70.4, 54.14) * mm, "end": v(-69.96, 54.09) * mm});
            skLineSegment(sketch, "E1792", {"start": v(-69.96, 54.09) * mm, "end": v(-69.52, 54.01) * mm});
            skLineSegment(sketch, "E1793", {"start": v(-69.52, 54.01) * mm, "end": v(-69.43, 54) * mm});
            skLineSegment(sketch, "E1794", {"start": v(-69.43, 54) * mm, "end": v(-69.37, 53.98) * mm});
            skLineSegment(sketch, "E1795", {"start": v(-69.37, 53.98) * mm, "end": v(-69.25, 53.96) * mm});
            skLineSegment(sketch, "E1796", {"start": v(-69.25, 53.96) * mm, "end": v(-68.8, 53.84) * mm});
            skLineSegment(sketch, "E1797", {"start": v(-68.8, 53.84) * mm, "end": v(-68.37, 53.7) * mm});
            skLineSegment(sketch, "E1798", {"start": v(-68.37, 53.7) * mm, "end": v(-67.95, 53.53) * mm});
            skLineSegment(sketch, "E1799", {"start": v(-67.95, 53.53) * mm, "end": v(-67.55, 53.35) * mm});
            skLineSegment(sketch, "E1800", {"start": v(-67.55, 53.35) * mm, "end": v(-67.16, 53.14) * mm});
            skLineSegment(sketch, "E1801", {"start": v(-67.16, 53.14) * mm, "end": v(-66.8, 52.92) * mm});
            skLineSegment(sketch, "E1802", {"start": v(-66.8, 52.92) * mm, "end": v(-66.44, 52.68) * mm});
            skLineSegment(sketch, "E1803", {"start": v(-66.44, 52.68) * mm, "end": v(-66.1, 52.42) * mm});
            skLineSegment(sketch, "E1804", {"start": v(-66.1, 52.42) * mm, "end": v(-65.79, 52.14) * mm});
            skLineSegment(sketch, "E1805", {"start": v(-65.79, 52.14) * mm, "end": v(-65.5, 51.85) * mm});
            skLineSegment(sketch, "E1806", {"start": v(-65.5, 51.85) * mm, "end": v(-65.22, 51.55) * mm});
            skLineSegment(sketch, "E1807", {"start": v(-65.22, 51.55) * mm, "end": v(-64.97, 51.23) * mm});
            skLineSegment(sketch, "E1808", {"start": v(-64.97, 51.23) * mm, "end": v(-64.9, 51.15) * mm});
            skLineSegment(sketch, "E1809", {"start": v(-64.9, 51.15) * mm, "end": v(-64.88, 51.11) * mm});
            skLineSegment(sketch, "E1810", {"start": v(-64.88, 51.11) * mm, "end": v(-64.89, 51.1) * mm});
            skLineSegment(sketch, "E1811", {"start": v(-64.89, 51.1) * mm, "end": v(-64.9, 51.1) * mm});
            skLineSegment(sketch, "E1812", {"start": v(-64.9, 51.1) * mm, "end": v(-65.09, 51.11) * mm});
            skLineSegment(sketch, "E1813", {"start": v(-65.09, 51.11) * mm, "end": v(-65.45, 51.13) * mm});
            skLineSegment(sketch, "E1814", {"start": v(-65.45, 51.13) * mm, "end": v(-68.34, 51.28) * mm});
            skLineSegment(sketch, "E1815", {"start": v(-68.34, 51.28) * mm, "end": v(-69.07, 51.32) * mm});
            skLineSegment(sketch, "E1816", {"start": v(-69.07, 51.32) * mm, "end": v(-69.43, 51.34) * mm});
            skLineSegment(sketch, "E1817", {"start": v(-69.43, 51.34) * mm, "end": v(-69.47, 51.34) * mm});
            skLineSegment(sketch, "E1818", {"start": v(-69.47, 51.34) * mm, "end": v(-69.5, 51.34) * mm});
            skLineSegment(sketch, "E1819", {"start": v(-69.5, 51.34) * mm, "end": v(-69.48, 51.33) * mm});
            skLineSegment(sketch, "E1820", {"start": v(-69.48, 51.33) * mm, "end": v(-69.37, 51.28) * mm});
            skLineSegment(sketch, "E1821", {"start": v(-69.37, 51.28) * mm, "end": v(-69.13, 51.17) * mm});
            skLineSegment(sketch, "E1822", {"start": v(-69.13, 51.17) * mm, "end": v(-68.61, 50.93) * mm});
            skLineSegment(sketch, "E1823", {"start": v(-68.61, 50.93) * mm, "end": v(-68.06, 50.68) * mm});
            skLineSegment(sketch, "E1824", {"start": v(-68.06, 50.68) * mm, "end": v(-66.9, 50.13) * mm});
            skLineSegment(sketch, "E1825", {"start": v(-66.9, 50.13) * mm, "end": v(-66.32, 49.86) * mm});
            skLineSegment(sketch, "E1826", {"start": v(-66.32, 49.86) * mm, "end": v(-65.76, 49.6) * mm});
            skLineSegment(sketch, "E1827", {"start": v(-65.76, 49.6) * mm, "end": v(-65.25, 49.36) * mm});
            skLineSegment(sketch, "E1828", {"start": v(-65.25, 49.36) * mm, "end": v(-64.8, 49.14) * mm});
            skLineSegment(sketch, "E1829", {"start": v(-64.8, 49.14) * mm, "end": v(-64.6, 49.05) * mm});
            skLineSegment(sketch, "E1830", {"start": v(-64.6, 49.05) * mm, "end": v(-64.4, 48.96) * mm});
            skLineSegment(sketch, "E1831", {"start": v(-64.4, 48.96) * mm, "end": v(-64.25, 48.88) * mm});
            skLineSegment(sketch, "E1832", {"start": v(-64.25, 48.88) * mm, "end": v(-64.12, 48.82) * mm});
            skLineSegment(sketch, "E1833", {"start": v(-64.12, 48.82) * mm, "end": v(-64, 48.76) * mm});
            skLineSegment(sketch, "E1834", {"start": v(-64, 48.76) * mm, "end": v(-63.93, 48.72) * mm});
            skLineSegment(sketch, "E1835", {"start": v(-63.93, 48.72) * mm, "end": v(-63.88, 48.7) * mm});
            skLineSegment(sketch, "E1836", {"start": v(-63.88, 48.7) * mm, "end": v(-63.86, 48.68) * mm});
            skLineSegment(sketch, "E1837", {"start": v(-63.86, 48.68) * mm, "end": v(-68.35, 48.3) * mm});
            skLineSegment(sketch, "E1838", {"start": v(-68.35, 48.3) * mm, "end": v(-70.6, 48.1) * mm});
            skLineSegment(sketch, "E1839", {"start": v(-70.6, 48.1) * mm, "end": v(-70.88, 48.07) * mm});
            skLineSegment(sketch, "E1840", {"start": v(-70.88, 48.07) * mm, "end": v(-71.02, 48.06) * mm});
            skLineSegment(sketch, "E1841", {"start": v(-71.02, 48.06) * mm, "end": v(-71.04, 48.06) * mm});
            skLineSegment(sketch, "E1842", {"start": v(-71.04, 48.06) * mm, "end": v(-71, 48.05) * mm});
            skLineSegment(sketch, "E1843", {"start": v(-71, 48.05) * mm, "end": v(-70.94, 48.03) * mm});
            skLineSegment(sketch, "E1844", {"start": v(-70.94, 48.03) * mm, "end": v(-70.4, 47.88) * mm});
            skLineSegment(sketch, "E1845", {"start": v(-70.4, 47.88) * mm, "end": v(-69.32, 47.58) * mm});
            skLineSegment(sketch, "E1846", {"start": v(-69.32, 47.58) * mm, "end": v(-64.98, 46.37) * mm});
            skLineSegment(sketch, "E1847", {"start": v(-64.98, 46.37) * mm, "end": v(-64.44, 46.22) * mm});
            skLineSegment(sketch, "E1848", {"start": v(-64.44, 46.22) * mm, "end": v(-64.17, 46.15) * mm});
            skLineSegment(sketch, "E1849", {"start": v(-64.17, 46.15) * mm, "end": v(-64.12, 46.13) * mm});
            skLineSegment(sketch, "E1850", {"start": v(-64.12, 46.13) * mm, "end": v(-64.12, 46.13) * mm});
            skLineSegment(sketch, "E1851", {"start": v(-64.12, 46.13) * mm, "end": v(-64.13, 46.12) * mm});
            skLineSegment(sketch, "E1852", {"start": v(-64.13, 46.12) * mm, "end": v(-64.17, 46.1) * mm});
            skLineSegment(sketch, "E1853", {"start": v(-64.17, 46.1) * mm, "end": v(-64.24, 46.08) * mm});
            skLineSegment(sketch, "E1854", {"start": v(-64.24, 46.08) * mm, "end": v(-64.33, 46.05) * mm});
            skLineSegment(sketch, "E1855", {"start": v(-64.33, 46.05) * mm, "end": v(-64.45, 46.02) * mm});
            skLineSegment(sketch, "E1856", {"start": v(-64.45, 46.02) * mm, "end": v(-64.74, 45.94) * mm});
            skLineSegment(sketch, "E1857", {"start": v(-64.74, 45.94) * mm, "end": v(-65.1, 45.84) * mm});
            skLineSegment(sketch, "E1858", {"start": v(-65.1, 45.84) * mm, "end": v(-65.52, 45.74) * mm});
            skLineSegment(sketch, "E1859", {"start": v(-65.52, 45.74) * mm, "end": v(-65.99, 45.62) * mm});
            skLineSegment(sketch, "E1860", {"start": v(-65.99, 45.62) * mm, "end": v(-68, 45.16) * mm});
            skLineSegment(sketch, "E1861", {"start": v(-68, 45.16) * mm, "end": v(-68.46, 45.06) * mm});
            skLineSegment(sketch, "E1862", {"start": v(-68.46, 45.06) * mm, "end": v(-68.88, 44.98) * mm});
            skLineSegment(sketch, "E1863", {"start": v(-68.88, 44.98) * mm, "end": v(-68.98, 44.96) * mm});
            skLineSegment(sketch, "E1864", {"start": v(-68.98, 44.96) * mm, "end": v(-69.03, 44.95) * mm});
            skLineSegment(sketch, "E1865", {"start": v(-69.03, 44.95) * mm, "end": v(-69.03, 44.94) * mm});
            skLineSegment(sketch, "E1866", {"start": v(-69.03, 44.94) * mm, "end": v(-69.01, 44.94) * mm});
            skLineSegment(sketch, "E1867", {"start": v(-69.01, 44.94) * mm, "end": v(-68.88, 44.9) * mm});
            skLineSegment(sketch, "E1868", {"start": v(-68.88, 44.9) * mm, "end": v(-68.61, 44.83) * mm});
            skLineSegment(sketch, "E1869", {"start": v(-68.61, 44.83) * mm, "end": v(-66.48, 44.23) * mm});
            skLineSegment(sketch, "E1870", {"start": v(-66.48, 44.23) * mm, "end": v(-65.95, 44.08) * mm});
            skLineSegment(sketch, "E1871", {"start": v(-65.95, 44.08) * mm, "end": v(-65.68, 44) * mm});
            skLineSegment(sketch, "E1872", {"start": v(-65.68, 44) * mm, "end": v(-65.65, 44) * mm});
            skLineSegment(sketch, "E1873", {"start": v(-65.65, 44) * mm, "end": v(-65.63, 43.99) * mm});
            skLineSegment(sketch, "E1874", {"start": v(-65.63, 43.99) * mm, "end": v(-65.64, 43.97) * mm});
            skLineSegment(sketch, "E1875", {"start": v(-65.64, 43.97) * mm, "end": v(-65.73, 43.9) * mm});
            skLineSegment(sketch, "E1876", {"start": v(-65.73, 43.9) * mm, "end": v(-65.92, 43.74) * mm});
            skLineSegment(sketch, "E1877", {"start": v(-65.92, 43.74) * mm, "end": v(-66.31, 43.47) * mm});
            skLineSegment(sketch, "E1878", {"start": v(-66.31, 43.47) * mm, "end": v(-66.73, 43.22) * mm});
            skLineSegment(sketch, "E1879", {"start": v(-66.73, 43.22) * mm, "end": v(-67.17, 43) * mm});
            skLineSegment(sketch, "E1880", {"start": v(-67.17, 43) * mm, "end": v(-67.64, 42.81) * mm});
            skLineSegment(sketch, "E1881", {"start": v(-67.64, 42.81) * mm, "end": v(-68.12, 42.66) * mm});
            skLineSegment(sketch, "E1882", {"start": v(-68.12, 42.66) * mm, "end": v(-68.61, 42.53) * mm});
            skLineSegment(sketch, "E1883", {"start": v(-68.61, 42.53) * mm, "end": v(-69.13, 42.44) * mm});
            skLineSegment(sketch, "E1884", {"start": v(-69.13, 42.44) * mm, "end": v(-69.65, 42.39) * mm});
            skLineSegment(sketch, "E1885", {"start": v(-69.65, 42.39) * mm, "end": v(-70.19, 42.37) * mm});
            skLineSegment(sketch, "E1886", {"start": v(-70.19, 42.37) * mm, "end": v(-70.73, 42.39) * mm});
            skLineSegment(sketch, "E1887", {"start": v(-70.73, 42.39) * mm, "end": v(-71.28, 42.44) * mm});
            skLineSegment(sketch, "E1888", {"start": v(-71.28, 42.44) * mm, "end": v(-71.84, 42.54) * mm});
            skLineSegment(sketch, "E1889", {"start": v(-79.84, 51.15) * mm, "end": v(-80.22, 51.84) * mm});
            skLineSegment(sketch, "E1890", {"start": v(-80.22, 51.84) * mm, "end": v(-80.5, 52.56) * mm});
            skLineSegment(sketch, "E1891", {"start": v(-80.5, 52.56) * mm, "end": v(-80.7, 53.3) * mm});
            skLineSegment(sketch, "E1892", {"start": v(-80.7, 53.3) * mm, "end": v(-80.8, 54.05) * mm});
            skLineSegment(sketch, "E1893", {"start": v(-80.8, 54.05) * mm, "end": v(-80.8, 54.8) * mm});
            skLineSegment(sketch, "E1894", {"start": v(-80.8, 54.8) * mm, "end": v(-80.72, 55.54) * mm});
            skLineSegment(sketch, "E1895", {"start": v(-80.72, 55.54) * mm, "end": v(-80.55, 56.27) * mm});
            skLineSegment(sketch, "E1896", {"start": v(-80.55, 56.27) * mm, "end": v(-80.3, 56.97) * mm});
            skLineSegment(sketch, "E1897", {"start": v(-80.3, 56.97) * mm, "end": v(-79.96, 57.64) * mm});
            skLineSegment(sketch, "E1898", {"start": v(-79.96, 57.64) * mm, "end": v(-79.54, 58.27) * mm});
            skLineSegment(sketch, "E1899", {"start": v(-79.54, 58.27) * mm, "end": v(-79.04, 58.85) * mm});
            skLineSegment(sketch, "E1900", {"start": v(-79.04, 58.85) * mm, "end": v(-78.46, 59.37) * mm});
            skLineSegment(sketch, "E1901", {"start": v(-78.46, 59.37) * mm, "end": v(-78.14, 59.6) * mm});
            skLineSegment(sketch, "E1902", {"start": v(-78.14, 59.6) * mm, "end": v(-77.82, 59.81) * mm});
            skLineSegment(sketch, "E1903", {"start": v(-77.82, 59.81) * mm, "end": v(-77.2, 60.14) * mm});
            skLineSegment(sketch, "E1904", {"start": v(-77.2, 60.14) * mm, "end": v(-76.58, 60.4) * mm});
            skLineSegment(sketch, "E1905", {"start": v(-76.58, 60.4) * mm, "end": v(-75.93, 60.57) * mm});
            skLineSegment(sketch, "E1906", {"start": v(-75.93, 60.57) * mm, "end": v(-75.28, 60.68) * mm});
            skLineSegment(sketch, "E1907", {"start": v(-75.28, 60.68) * mm, "end": v(-74.62, 60.72) * mm});
            skLineSegment(sketch, "E1908", {"start": v(-74.62, 60.72) * mm, "end": v(-73.97, 60.68) * mm});
            skLineSegment(sketch, "E1909", {"start": v(-73.97, 60.68) * mm, "end": v(-73.32, 60.58) * mm});
            skLineSegment(sketch, "E1910", {"start": v(-73.32, 60.58) * mm, "end": v(-72.7, 60.42) * mm});
            skLineSegment(sketch, "E1911", {"start": v(-72.7, 60.42) * mm, "end": v(-72.08, 60.19) * mm});
            skLineSegment(sketch, "E1912", {"start": v(-72.08, 60.19) * mm, "end": v(-71.5, 59.9) * mm});
            skLineSegment(sketch, "E1913", {"start": v(-71.5, 59.9) * mm, "end": v(-70.94, 59.53) * mm});
            skLineSegment(sketch, "E1914", {"start": v(-70.94, 59.53) * mm, "end": v(-70.42, 59.11) * mm});
            skLineSegment(sketch, "E1915", {"start": v(-70.42, 59.11) * mm, "end": v(-70.17, 58.88) * mm});
            skLineSegment(sketch, "E1916", {"start": v(-70.17, 58.88) * mm, "end": v(-70.14, 58.85) * mm});
            skLineSegment(sketch, "E1917", {"start": v(-70.14, 58.85) * mm, "end": v(-70.14, 58.83) * mm});
            skLineSegment(sketch, "E1918", {"start": v(-70.14, 58.83) * mm, "end": v(-70.2, 58.85) * mm});
            skLineSegment(sketch, "E1919", {"start": v(-70.2, 58.85) * mm, "end": v(-70.3, 58.88) * mm});
            skLineSegment(sketch, "E1920", {"start": v(-70.3, 58.88) * mm, "end": v(-70.77, 58.97) * mm});
            skLineSegment(sketch, "E1921", {"start": v(-70.77, 58.97) * mm, "end": v(-71.23, 59.04) * mm});
            skLineSegment(sketch, "E1922", {"start": v(-71.23, 59.04) * mm, "end": v(-71.7, 59.08) * mm});
            skLineSegment(sketch, "E1923", {"start": v(-71.7, 59.08) * mm, "end": v(-72.18, 59.09) * mm});
            skLineSegment(sketch, "E1924", {"start": v(-72.18, 59.09) * mm, "end": v(-72.65, 59.06) * mm});
            skLineSegment(sketch, "E1925", {"start": v(-72.65, 59.06) * mm, "end": v(-73.12, 59.01) * mm});
            skLineSegment(sketch, "E1926", {"start": v(-73.12, 59.01) * mm, "end": v(-73.6, 58.93) * mm});
            skLineSegment(sketch, "E1927", {"start": v(-73.6, 58.93) * mm, "end": v(-74.06, 58.81) * mm});
            skLineSegment(sketch, "E1928", {"start": v(-74.06, 58.81) * mm, "end": v(-74.52, 58.67) * mm});
            skLineSegment(sketch, "E1929", {"start": v(-74.52, 58.67) * mm, "end": v(-74.97, 58.49) * mm});
            skLineSegment(sketch, "E1930", {"start": v(-74.97, 58.49) * mm, "end": v(-75.42, 58.28) * mm});
            skLineSegment(sketch, "E1931", {"start": v(-75.42, 58.28) * mm, "end": v(-75.86, 58.03) * mm});
            skLineSegment(sketch, "E1932", {"start": v(-75.86, 58.03) * mm, "end": v(-76.1, 57.89) * mm});
            skLineSegment(sketch, "E1933", {"start": v(-76.1, 57.89) * mm, "end": v(-76.38, 57.69) * mm});
            skLineSegment(sketch, "E1934", {"start": v(-76.38, 57.69) * mm, "end": v(-76.93, 57.25) * mm});
            skLineSegment(sketch, "E1935", {"start": v(-76.93, 57.25) * mm, "end": v(-77.43, 56.78) * mm});
            skLineSegment(sketch, "E1936", {"start": v(-77.43, 56.78) * mm, "end": v(-77.87, 56.26) * mm});
            skLineSegment(sketch, "E1937", {"start": v(-77.87, 56.26) * mm, "end": v(-78.26, 55.71) * mm});
            skLineSegment(sketch, "E1938", {"start": v(-78.26, 55.71) * mm, "end": v(-78.6, 55.13) * mm});
            skLineSegment(sketch, "E1939", {"start": v(-78.6, 55.13) * mm, "end": v(-78.88, 54.53) * mm});
            skLineSegment(sketch, "E1940", {"start": v(-78.88, 54.53) * mm, "end": v(-79.1, 53.9) * mm});
            skLineSegment(sketch, "E1941", {"start": v(-79.1, 53.9) * mm, "end": v(-79.28, 53.27) * mm});
            skLineSegment(sketch, "E1942", {"start": v(-79.28, 53.27) * mm, "end": v(-79.39, 52.61) * mm});
            skLineSegment(sketch, "E1943", {"start": v(-79.39, 52.61) * mm, "end": v(-79.44, 51.95) * mm});
            skLineSegment(sketch, "E1944", {"start": v(-79.44, 51.95) * mm, "end": v(-79.43, 51.29) * mm});
            skLineSegment(sketch, "E1945", {"start": v(-79.43, 51.29) * mm, "end": v(-79.36, 50.62) * mm});
            skLineSegment(sketch, "E1946", {"start": v(-79.36, 50.62) * mm, "end": v(-79.35, 50.54) * mm});
            skLineSegment(sketch, "E1947", {"start": v(-79.35, 50.54) * mm, "end": v(-79.34, 50.5) * mm});
            skLineSegment(sketch, "E1948", {"start": v(-79.34, 50.5) * mm, "end": v(-79.35, 50.49) * mm});
            skLineSegment(sketch, "E1949", {"start": v(-79.35, 50.49) * mm, "end": v(-79.36, 50.5) * mm});
            skLineSegment(sketch, "E1950", {"start": v(-79.36, 50.5) * mm, "end": v(-79.38, 50.53) * mm});
            skLineSegment(sketch, "E1951", {"start": v(-79.38, 50.53) * mm, "end": v(-79.54, 50.73) * mm});
            skLineSegment(sketch, "E1952", {"start": v(-79.54, 50.73) * mm, "end": v(-79.84, 51.15) * mm});
            skLineSegment(sketch, "E1953", {"start": v(-59.28, 54.4) * mm, "end": v(-61.73, 58.2) * mm});
            skLineSegment(sketch, "E1954", {"start": v(-61.73, 58.2) * mm, "end": v(-62.96, 60.08) * mm});
            skLineSegment(sketch, "E1955", {"start": v(-62.96, 60.08) * mm, "end": v(-63.11, 60.32) * mm});
            skLineSegment(sketch, "E1956", {"start": v(-63.11, 60.32) * mm, "end": v(-63.2, 60.44) * mm});
            skLineSegment(sketch, "E1957", {"start": v(-63.2, 60.44) * mm, "end": v(-63.2, 60.46) * mm});
            skLineSegment(sketch, "E1958", {"start": v(-63.2, 60.46) * mm, "end": v(-63.2, 60.42) * mm});
            skLineSegment(sketch, "E1959", {"start": v(-63.2, 60.42) * mm, "end": v(-63.18, 60.35) * mm});
            skLineSegment(sketch, "E1960", {"start": v(-63.18, 60.35) * mm, "end": v(-63.06, 59.8) * mm});
            skLineSegment(sketch, "E1961", {"start": v(-63.06, 59.8) * mm, "end": v(-62.82, 58.7) * mm});
            skLineSegment(sketch, "E1962", {"start": v(-62.82, 58.7) * mm, "end": v(-61.84, 54.32) * mm});
            skLineSegment(sketch, "E1963", {"start": v(-61.84, 54.32) * mm, "end": v(-61.72, 53.77) * mm});
            skLineSegment(sketch, "E1964", {"start": v(-61.72, 53.77) * mm, "end": v(-61.66, 53.5) * mm});
            skLineSegment(sketch, "E1965", {"start": v(-61.66, 53.5) * mm, "end": v(-61.65, 53.44) * mm});
            skLineSegment(sketch, "E1966", {"start": v(-61.65, 53.44) * mm, "end": v(-61.65, 53.44) * mm});
            skLineSegment(sketch, "E1967", {"start": v(-61.65, 53.44) * mm, "end": v(-61.66, 53.44) * mm});
            skLineSegment(sketch, "E1968", {"start": v(-61.66, 53.44) * mm, "end": v(-61.7, 53.47) * mm});
            skLineSegment(sketch, "E1969", {"start": v(-61.7, 53.47) * mm, "end": v(-61.75, 53.52) * mm});
            skLineSegment(sketch, "E1970", {"start": v(-61.75, 53.52) * mm, "end": v(-61.82, 53.59) * mm});
            skLineSegment(sketch, "E1971", {"start": v(-61.82, 53.59) * mm, "end": v(-61.9, 53.67) * mm});
            skLineSegment(sketch, "E1972", {"start": v(-61.9, 53.67) * mm, "end": v(-62.11, 53.9) * mm});
            skLineSegment(sketch, "E1973", {"start": v(-62.11, 53.9) * mm, "end": v(-62.37, 54.17) * mm});
            skLineSegment(sketch, "E1974", {"start": v(-62.37, 54.17) * mm, "end": v(-62.66, 54.5) * mm});
            skLineSegment(sketch, "E1975", {"start": v(-62.66, 54.5) * mm, "end": v(-62.98, 54.85) * mm});
            skLineSegment(sketch, "E1976", {"start": v(-62.98, 54.85) * mm, "end": v(-64.33, 56.4) * mm});
            skLineSegment(sketch, "E1977", {"start": v(-64.33, 56.4) * mm, "end": v(-64.63, 56.76) * mm});
            skLineSegment(sketch, "E1978", {"start": v(-64.63, 56.76) * mm, "end": v(-64.91, 57.1) * mm});
            skLineSegment(sketch, "E1979", {"start": v(-64.91, 57.1) * mm, "end": v(-64.97, 57.18) * mm});
            skLineSegment(sketch, "E1980", {"start": v(-64.97, 57.18) * mm, "end": v(-65, 57.21) * mm});
            skLineSegment(sketch, "E1981", {"start": v(-65, 57.21) * mm, "end": v(-65, 57.21) * mm});
            skLineSegment(sketch, "E1982", {"start": v(-65, 57.21) * mm, "end": v(-65, 57.2) * mm});
            skLineSegment(sketch, "E1983", {"start": v(-65, 57.2) * mm, "end": v(-64.97, 57.06) * mm});
            skLineSegment(sketch, "E1984", {"start": v(-64.97, 57.06) * mm, "end": v(-64.92, 56.79) * mm});
            skLineSegment(sketch, "E1985", {"start": v(-64.92, 56.79) * mm, "end": v(-64.44, 54.62) * mm});
            skLineSegment(sketch, "E1986", {"start": v(-64.44, 54.62) * mm, "end": v(-64.32, 54.08) * mm});
            skLineSegment(sketch, "E1987", {"start": v(-64.32, 54.08) * mm, "end": v(-64.27, 53.81) * mm});
            skLineSegment(sketch, "E1988", {"start": v(-64.27, 53.81) * mm, "end": v(-64.26, 53.78) * mm});
            skLineSegment(sketch, "E1989", {"start": v(-64.26, 53.78) * mm, "end": v(-64.25, 53.76) * mm});
            skLineSegment(sketch, "E1990", {"start": v(-64.25, 53.76) * mm, "end": v(-64.28, 53.77) * mm});
            skLineSegment(sketch, "E1991", {"start": v(-64.28, 53.77) * mm, "end": v(-64.39, 53.81) * mm});
            skLineSegment(sketch, "E1992", {"start": v(-64.39, 53.81) * mm, "end": v(-64.6, 53.9) * mm});
            skLineSegment(sketch, "E1993", {"start": v(-64.6, 53.9) * mm, "end": v(-65.03, 54.12) * mm});
            skLineSegment(sketch, "E1994", {"start": v(-65.03, 54.12) * mm, "end": v(-65.45, 54.38) * mm});
            skLineSegment(sketch, "E1995", {"start": v(-65.45, 54.38) * mm, "end": v(-65.85, 54.66) * mm});
            skLineSegment(sketch, "E1996", {"start": v(-65.85, 54.66) * mm, "end": v(-66.23, 54.98) * mm});
            skLineSegment(sketch, "E1997", {"start": v(-66.23, 54.98) * mm, "end": v(-66.6, 55.33) * mm});
            skLineSegment(sketch, "E1998", {"start": v(-66.6, 55.33) * mm, "end": v(-66.94, 55.71) * mm});
            skLineSegment(sketch, "E1999", {"start": v(-66.94, 55.71) * mm, "end": v(-67.26, 56.12) * mm});
            skLineSegment(sketch, "E2000", {"start": v(-67.26, 56.12) * mm, "end": v(-67.56, 56.56) * mm});
            skLineSegment(sketch, "E2001", {"start": v(-67.56, 56.56) * mm, "end": v(-67.83, 57.02) * mm});
            skLineSegment(sketch, "E2002", {"start": v(-67.83, 57.02) * mm, "end": v(-68.06, 57.51) * mm});
            skLineSegment(sketch, "E2003", {"start": v(-68.06, 57.51) * mm, "end": v(-68.27, 58.03) * mm});
            skLineSegment(sketch, "E2004", {"start": v(-68.27, 58.03) * mm, "end": v(-68.45, 58.56) * mm});
            skLineSegment(sketch, "E2005", {"start": v(-68.45, 58.56) * mm, "end": v(-68.56, 58.99) * mm});
            skLineSegment(sketch, "E2006", {"start": v(-68.56, 58.99) * mm, "end": v(-68.65, 59.42) * mm});
            skLineSegment(sketch, "E2007", {"start": v(-68.65, 59.42) * mm, "end": v(-68.71, 59.84) * mm});
            skLineSegment(sketch, "E2008", {"start": v(-68.71, 59.84) * mm, "end": v(-68.75, 60.26) * mm});
            skLineSegment(sketch, "E2009", {"start": v(-68.75, 60.26) * mm, "end": v(-68.77, 60.68) * mm});
            skLineSegment(sketch, "E2010", {"start": v(-68.77, 60.68) * mm, "end": v(-68.76, 61.1) * mm});
            skLineSegment(sketch, "E2011", {"start": v(-68.76, 61.1) * mm, "end": v(-68.74, 61.5) * mm});
            skLineSegment(sketch, "E2012", {"start": v(-68.74, 61.5) * mm, "end": v(-68.69, 61.9) * mm});
            skLineSegment(sketch, "E2013", {"start": v(-68.69, 61.9) * mm, "end": v(-68.61, 62.3) * mm});
            skLineSegment(sketch, "E2014", {"start": v(-68.61, 62.3) * mm, "end": v(-68.52, 62.69) * mm});
            skLineSegment(sketch, "E2015", {"start": v(-68.52, 62.69) * mm, "end": v(-68.41, 63.06) * mm});
            skLineSegment(sketch, "E2016", {"start": v(-68.41, 63.06) * mm, "end": v(-68.28, 63.43) * mm});
            skLineSegment(sketch, "E2017", {"start": v(-68.28, 63.43) * mm, "end": v(-68.13, 63.78) * mm});
            skLineSegment(sketch, "E2018", {"start": v(-68.13, 63.78) * mm, "end": v(-67.96, 64.12) * mm});
            skLineSegment(sketch, "E2019", {"start": v(-67.96, 64.12) * mm, "end": v(-67.77, 64.45) * mm});
            skLineSegment(sketch, "E2020", {"start": v(-67.77, 64.45) * mm, "end": v(-67.56, 64.76) * mm});
            skLineSegment(sketch, "E2021", {"start": v(-67.56, 64.76) * mm, "end": v(-67.34, 65.06) * mm});
            skLineSegment(sketch, "E2022", {"start": v(-67.34, 65.06) * mm, "end": v(-67.1, 65.34) * mm});
            skLineSegment(sketch, "E2023", {"start": v(-67.1, 65.34) * mm, "end": v(-66.84, 65.6) * mm});
            skLineSegment(sketch, "E2024", {"start": v(-66.84, 65.6) * mm, "end": v(-66.56, 65.84) * mm});
            skLineSegment(sketch, "E2025", {"start": v(-66.56, 65.84) * mm, "end": v(-66.27, 66.06) * mm});
            skLineSegment(sketch, "E2026", {"start": v(-66.27, 66.06) * mm, "end": v(-65.97, 66.26) * mm});
            skLineSegment(sketch, "E2027", {"start": v(-65.97, 66.26) * mm, "end": v(-65.65, 66.44) * mm});
            skLineSegment(sketch, "E2028", {"start": v(-65.65, 66.44) * mm, "end": v(-65.31, 66.6) * mm});
            skLineSegment(sketch, "E2029", {"start": v(-65.31, 66.6) * mm, "end": v(-64.96, 66.73) * mm});
            skLineSegment(sketch, "E2030", {"start": v(-64.96, 66.73) * mm, "end": v(-64.6, 66.84) * mm});
            skLineSegment(sketch, "E2031", {"start": v(-64.6, 66.84) * mm, "end": v(-64.24, 66.92) * mm});
            skLineSegment(sketch, "E2032", {"start": v(-64.24, 66.92) * mm, "end": v(-63.87, 66.97) * mm});
            skLineSegment(sketch, "E2033", {"start": v(-63.87, 66.97) * mm, "end": v(-63.5, 67) * mm});
            skLineSegment(sketch, "E2034", {"start": v(-63.5, 67) * mm, "end": v(-63.14, 67) * mm});
            skLineSegment(sketch, "E2035", {"start": v(-63.14, 67) * mm, "end": v(-62.77, 66.97) * mm});
            skLineSegment(sketch, "E2036", {"start": v(-62.77, 66.97) * mm, "end": v(-62.4, 66.92) * mm});
            skLineSegment(sketch, "E2037", {"start": v(-62.4, 66.92) * mm, "end": v(-62.05, 66.84) * mm});
            skLineSegment(sketch, "E2038", {"start": v(-62.05, 66.84) * mm, "end": v(-61.7, 66.74) * mm});
            skLineSegment(sketch, "E2039", {"start": v(-61.7, 66.74) * mm, "end": v(-61.35, 66.61) * mm});
            skLineSegment(sketch, "E2040", {"start": v(-61.35, 66.61) * mm, "end": v(-61, 66.47) * mm});
            skLineSegment(sketch, "E2041", {"start": v(-61, 66.47) * mm, "end": v(-60.67, 66.3) * mm});
            skLineSegment(sketch, "E2042", {"start": v(-60.67, 66.3) * mm, "end": v(-60.34, 66.1) * mm});
            skLineSegment(sketch, "E2043", {"start": v(-60.34, 66.1) * mm, "end": v(-60.02, 65.9) * mm});
            skLineSegment(sketch, "E2044", {"start": v(-60.02, 65.9) * mm, "end": v(-59.71, 65.66) * mm});
            skLineSegment(sketch, "E2045", {"start": v(-59.71, 65.66) * mm, "end": v(-59.41, 65.4) * mm});
            skLineSegment(sketch, "E2046", {"start": v(-59.41, 65.4) * mm, "end": v(-59.13, 65.13) * mm});
            skLineSegment(sketch, "E2047", {"start": v(-59.13, 65.13) * mm, "end": v(-58.85, 64.84) * mm});
            skLineSegment(sketch, "E2048", {"start": v(-58.85, 64.84) * mm, "end": v(-58.6, 64.53) * mm});
            skLineSegment(sketch, "E2049", {"start": v(-58.6, 64.53) * mm, "end": v(-58.35, 64.2) * mm});
            skLineSegment(sketch, "E2050", {"start": v(-58.35, 64.2) * mm, "end": v(-58.12, 63.86) * mm});
            skLineSegment(sketch, "E2051", {"start": v(-58.12, 63.86) * mm, "end": v(-57.9, 63.5) * mm});
            skLineSegment(sketch, "E2052", {"start": v(-57.9, 63.5) * mm, "end": v(-57.7, 63.13) * mm});
            skLineSegment(sketch, "E2053", {"start": v(-57.7, 63.13) * mm, "end": v(-57.53, 62.74) * mm});
            skLineSegment(sketch, "E2054", {"start": v(-57.53, 62.74) * mm, "end": v(-57.37, 62.33) * mm});
            skLineSegment(sketch, "E2055", {"start": v(-57.37, 62.33) * mm, "end": v(-57.23, 61.91) * mm});
            skLineSegment(sketch, "E2056", {"start": v(-57.23, 61.91) * mm, "end": v(-57.2, 61.82) * mm});
            skLineSegment(sketch, "E2057", {"start": v(-57.2, 61.82) * mm, "end": v(-57.19, 61.76) * mm});
            skLineSegment(sketch, "E2058", {"start": v(-57.19, 61.76) * mm, "end": v(-57.16, 61.65) * mm});
            skLineSegment(sketch, "E2059", {"start": v(-57.16, 61.65) * mm, "end": v(-57.05, 61.2) * mm});
            skLineSegment(sketch, "E2060", {"start": v(-57.05, 61.2) * mm, "end": v(-56.97, 60.75) * mm});
            skLineSegment(sketch, "E2061", {"start": v(-56.97, 60.75) * mm, "end": v(-56.92, 60.3) * mm});
            skLineSegment(sketch, "E2062", {"start": v(-56.92, 60.3) * mm, "end": v(-56.9, 59.86) * mm});
            skLineSegment(sketch, "E2063", {"start": v(-56.9, 59.86) * mm, "end": v(-56.9, 59.42) * mm});
            skLineSegment(sketch, "E2064", {"start": v(-56.9, 59.42) * mm, "end": v(-56.92, 58.99) * mm});
            skLineSegment(sketch, "E2065", {"start": v(-56.92, 58.99) * mm, "end": v(-56.96, 58.56) * mm});
            skLineSegment(sketch, "E2066", {"start": v(-56.96, 58.56) * mm, "end": v(-57.04, 58.14) * mm});
            skLineSegment(sketch, "E2067", {"start": v(-57.04, 58.14) * mm, "end": v(-57.13, 57.74) * mm});
            skLineSegment(sketch, "E2068", {"start": v(-57.13, 57.74) * mm, "end": v(-57.25, 57.34) * mm});
            skLineSegment(sketch, "E2069", {"start": v(-57.25, 57.34) * mm, "end": v(-57.39, 56.95) * mm});
            skLineSegment(sketch, "E2070", {"start": v(-57.39, 56.95) * mm, "end": v(-57.55, 56.58) * mm});
            skLineSegment(sketch, "E2071", {"start": v(-57.55, 56.58) * mm, "end": v(-57.6, 56.5) * mm});
            skLineSegment(sketch, "E2072", {"start": v(-57.6, 56.5) * mm, "end": v(-57.61, 56.45) * mm});
            skLineSegment(sketch, "E2073", {"start": v(-57.61, 56.45) * mm, "end": v(-57.62, 56.45) * mm});
            skLineSegment(sketch, "E2074", {"start": v(-57.62, 56.45) * mm, "end": v(-57.63, 56.47) * mm});
            skLineSegment(sketch, "E2075", {"start": v(-57.63, 56.47) * mm, "end": v(-57.7, 56.63) * mm});
            skLineSegment(sketch, "E2076", {"start": v(-57.7, 56.63) * mm, "end": v(-57.86, 56.96) * mm});
            skLineSegment(sketch, "E2077", {"start": v(-57.86, 56.96) * mm, "end": v(-59.09, 59.59) * mm});
            skLineSegment(sketch, "E2078", {"start": v(-59.09, 59.59) * mm, "end": v(-59.4, 60.24) * mm});
            skLineSegment(sketch, "E2079", {"start": v(-59.4, 60.24) * mm, "end": v(-59.55, 60.57) * mm});
            skLineSegment(sketch, "E2080", {"start": v(-59.55, 60.57) * mm, "end": v(-59.57, 60.61) * mm});
            skLineSegment(sketch, "E2081", {"start": v(-59.57, 60.61) * mm, "end": v(-59.58, 60.63) * mm});
            skLineSegment(sketch, "E2082", {"start": v(-59.58, 60.63) * mm, "end": v(-59.58, 60.61) * mm});
            skLineSegment(sketch, "E2083", {"start": v(-59.58, 60.61) * mm, "end": v(-59.57, 60.49) * mm});
            skLineSegment(sketch, "E2084", {"start": v(-59.57, 60.49) * mm, "end": v(-59.56, 60.23) * mm});
            skLineSegment(sketch, "E2085", {"start": v(-59.56, 60.23) * mm, "end": v(-59.52, 59.66) * mm});
            skLineSegment(sketch, "E2086", {"start": v(-59.52, 59.66) * mm, "end": v(-59.49, 59.05) * mm});
            skLineSegment(sketch, "E2087", {"start": v(-59.49, 59.05) * mm, "end": v(-59.42, 57.77) * mm});
            skLineSegment(sketch, "E2088", {"start": v(-59.42, 57.77) * mm, "end": v(-59.4, 57.13) * mm});
            skLineSegment(sketch, "E2089", {"start": v(-59.4, 57.13) * mm, "end": v(-59.36, 56.52) * mm});
            skLineSegment(sketch, "E2090", {"start": v(-59.36, 56.52) * mm, "end": v(-59.33, 55.95) * mm});
            skLineSegment(sketch, "E2091", {"start": v(-59.33, 55.95) * mm, "end": v(-59.31, 55.45) * mm});
            skLineSegment(sketch, "E2092", {"start": v(-59.31, 55.45) * mm, "end": v(-59.3, 55.22) * mm});
            skLineSegment(sketch, "E2093", {"start": v(-59.3, 55.22) * mm, "end": v(-59.3, 55.02) * mm});
            skLineSegment(sketch, "E2094", {"start": v(-59.3, 55.02) * mm, "end": v(-59.29, 54.85) * mm});
            skLineSegment(sketch, "E2095", {"start": v(-59.29, 54.85) * mm, "end": v(-59.28, 54.7) * mm});
            skLineSegment(sketch, "E2096", {"start": v(-59.28, 54.7) * mm, "end": v(-59.28, 54.57) * mm});
            skLineSegment(sketch, "E2097", {"start": v(-59.28, 54.57) * mm, "end": v(-59.28, 54.48) * mm});
            skLineSegment(sketch, "E2098", {"start": v(-59.28, 54.48) * mm, "end": v(-59.28, 54.43) * mm});
            skLineSegment(sketch, "E2099", {"start": v(-59.28, 54.43) * mm, "end": v(-59.28, 54.4) * mm});
            skLineSegment(sketch, "E2100", {"start": v(-62.78, 74.07) * mm, "end": v(-62.08, 74.03) * mm});
            skLineSegment(sketch, "E2101", {"start": v(-62.08, 74.03) * mm, "end": v(-61.4, 73.92) * mm});
            skLineSegment(sketch, "E2102", {"start": v(-61.4, 73.92) * mm, "end": v(-60.76, 73.73) * mm});
            skLineSegment(sketch, "E2103", {"start": v(-60.76, 73.73) * mm, "end": v(-60.14, 73.49) * mm});
            skLineSegment(sketch, "E2104", {"start": v(-60.14, 73.49) * mm, "end": v(-59.56, 73.18) * mm});
            skLineSegment(sketch, "E2105", {"start": v(-59.56, 73.18) * mm, "end": v(-59.01, 72.8) * mm});
            skLineSegment(sketch, "E2106", {"start": v(-59.01, 72.8) * mm, "end": v(-58.51, 72.38) * mm});
            skLineSegment(sketch, "E2107", {"start": v(-58.51, 72.38) * mm, "end": v(-58.06, 71.91) * mm});
            skLineSegment(sketch, "E2108", {"start": v(-58.06, 71.91) * mm, "end": v(-57.66, 71.4) * mm});
            skLineSegment(sketch, "E2109", {"start": v(-57.66, 71.4) * mm, "end": v(-57.3, 70.84) * mm});
            skLineSegment(sketch, "E2110", {"start": v(-57.3, 70.84) * mm, "end": v(-57.02, 70.24) * mm});
            skLineSegment(sketch, "E2111", {"start": v(-57.02, 70.24) * mm, "end": v(-56.8, 69.6) * mm});
            skLineSegment(sketch, "E2112", {"start": v(-56.8, 69.6) * mm, "end": v(-56.7, 69.28) * mm});
            skLineSegment(sketch, "E2113", {"start": v(-56.7, 69.28) * mm, "end": v(-56.67, 69.12) * mm});
            skLineSegment(sketch, "E2114", {"start": v(-56.67, 69.12) * mm, "end": v(-56.67, 69.09) * mm});
            skLineSegment(sketch, "E2115", {"start": v(-56.67, 69.09) * mm, "end": v(-56.69, 69.11) * mm});
            skLineSegment(sketch, "E2116", {"start": v(-56.69, 69.11) * mm, "end": v(-56.73, 69.15) * mm});
            skLineSegment(sketch, "E2117", {"start": v(-56.73, 69.15) * mm, "end": v(-57.06, 69.49) * mm});
            skLineSegment(sketch, "E2118", {"start": v(-57.06, 69.49) * mm, "end": v(-57.41, 69.8) * mm});
            skLineSegment(sketch, "E2119", {"start": v(-57.41, 69.8) * mm, "end": v(-57.79, 70.1) * mm});
            skLineSegment(sketch, "E2120", {"start": v(-57.79, 70.1) * mm, "end": v(-58.18, 70.36) * mm});
            skLineSegment(sketch, "E2121", {"start": v(-58.18, 70.36) * mm, "end": v(-58.58, 70.6) * mm});
            skLineSegment(sketch, "E2122", {"start": v(-58.58, 70.6) * mm, "end": v(-59, 70.81) * mm});
            skLineSegment(sketch, "E2123", {"start": v(-59, 70.81) * mm, "end": v(-59.45, 71) * mm});
            skLineSegment(sketch, "E2124", {"start": v(-59.45, 71) * mm, "end": v(-59.9, 71.16) * mm});
            skLineSegment(sketch, "E2125", {"start": v(-59.9, 71.16) * mm, "end": v(-60.37, 71.3) * mm});
            skLineSegment(sketch, "E2126", {"start": v(-60.37, 71.3) * mm, "end": v(-60.85, 71.4) * mm});
            skLineSegment(sketch, "E2127", {"start": v(-60.85, 71.4) * mm, "end": v(-61.34, 71.46) * mm});
            skLineSegment(sketch, "E2128", {"start": v(-61.34, 71.46) * mm, "end": v(-61.84, 71.5) * mm});
            skLineSegment(sketch, "E2129", {"start": v(-61.84, 71.5) * mm, "end": v(-62.1, 71.5) * mm});
            skLineSegment(sketch, "E2130", {"start": v(-62.1, 71.5) * mm, "end": v(-62.43, 71.5) * mm});
            skLineSegment(sketch, "E2131", {"start": v(-62.43, 71.5) * mm, "end": v(-63.13, 71.44) * mm});
            skLineSegment(sketch, "E2132", {"start": v(-63.13, 71.44) * mm, "end": v(-63.81, 71.32) * mm});
            skLineSegment(sketch, "E2133", {"start": v(-63.81, 71.32) * mm, "end": v(-64.47, 71.13) * mm});
            skLineSegment(sketch, "E2134", {"start": v(-64.47, 71.13) * mm, "end": v(-65.1, 70.9) * mm});
            skLineSegment(sketch, "E2135", {"start": v(-65.1, 70.9) * mm, "end": v(-65.7, 70.6) * mm});
            skLineSegment(sketch, "E2136", {"start": v(-65.7, 70.6) * mm, "end": v(-66.27, 70.25) * mm});
            skLineSegment(sketch, "E2137", {"start": v(-66.27, 70.25) * mm, "end": v(-66.8, 69.85) * mm});
            skLineSegment(sketch, "E2138", {"start": v(-66.8, 69.85) * mm, "end": v(-67.3, 69.4) * mm});
            skLineSegment(sketch, "E2139", {"start": v(-67.3, 69.4) * mm, "end": v(-67.76, 68.93) * mm});
            skLineSegment(sketch, "E2140", {"start": v(-67.76, 68.93) * mm, "end": v(-68.17, 68.4) * mm});
            skLineSegment(sketch, "E2141", {"start": v(-68.17, 68.4) * mm, "end": v(-68.53, 67.84) * mm});
            skLineSegment(sketch, "E2142", {"start": v(-68.53, 67.84) * mm, "end": v(-68.85, 67.25) * mm});
            skLineSegment(sketch, "E2143", {"start": v(-68.85, 67.25) * mm, "end": v(-68.92, 67.1) * mm});
            skLineSegment(sketch, "E2144", {"start": v(-68.92, 67.1) * mm, "end": v(-68.95, 67.02) * mm});
            skLineSegment(sketch, "E2145", {"start": v(-68.95, 67.02) * mm, "end": v(-68.96, 67) * mm});
            skLineSegment(sketch, "E2146", {"start": v(-68.96, 67) * mm, "end": v(-68.96, 67.04) * mm});
            skLineSegment(sketch, "E2147", {"start": v(-68.96, 67.04) * mm, "end": v(-68.97, 67.1) * mm});
            skLineSegment(sketch, "E2148", {"start": v(-68.97, 67.1) * mm, "end": v(-69.01, 67.62) * mm});
            skLineSegment(sketch, "E2149", {"start": v(-69.01, 67.62) * mm, "end": v(-69.02, 67.75) * mm});
            skLineSegment(sketch, "E2150", {"start": v(-69.02, 67.75) * mm, "end": v(-69.02, 67.82) * mm});
            skLineSegment(sketch, "E2151", {"start": v(-69.02, 67.82) * mm, "end": v(-69.02, 67.82) * mm});
            skLineSegment(sketch, "E2152", {"start": v(-69.02, 67.82) * mm, "end": v(-69.02, 67.83) * mm});
            skLineSegment(sketch, "E2153", {"start": v(-69.02, 67.83) * mm, "end": v(-69.02, 67.87) * mm});
            skLineSegment(sketch, "E2154", {"start": v(-69.02, 67.87) * mm, "end": v(-69.01, 68.07) * mm});
            skLineSegment(sketch, "E2155", {"start": v(-69.01, 68.07) * mm, "end": v(-68.99, 68.47) * mm});
            skLineSegment(sketch, "E2156", {"start": v(-68.99, 68.47) * mm, "end": v(-68.86, 69.24) * mm});
            skLineSegment(sketch, "E2157", {"start": v(-68.86, 69.24) * mm, "end": v(-68.64, 69.97) * mm});
            skLineSegment(sketch, "E2158", {"start": v(-68.64, 69.97) * mm, "end": v(-68.34, 70.67) * mm});
            skLineSegment(sketch, "E2159", {"start": v(-68.34, 70.67) * mm, "end": v(-67.95, 71.32) * mm});
            skLineSegment(sketch, "E2160", {"start": v(-67.95, 71.32) * mm, "end": v(-67.5, 71.91) * mm});
            skLineSegment(sketch, "E2161", {"start": v(-67.5, 71.91) * mm, "end": v(-66.97, 72.45) * mm});
            skLineSegment(sketch, "E2162", {"start": v(-66.97, 72.45) * mm, "end": v(-66.39, 72.92) * mm});
            skLineSegment(sketch, "E2163", {"start": v(-66.39, 72.92) * mm, "end": v(-65.75, 73.32) * mm});
            skLineSegment(sketch, "E2164", {"start": v(-65.75, 73.32) * mm, "end": v(-65.07, 73.64) * mm});
            skLineSegment(sketch, "E2165", {"start": v(-65.07, 73.64) * mm, "end": v(-64.34, 73.87) * mm});
            skLineSegment(sketch, "E2166", {"start": v(-64.34, 73.87) * mm, "end": v(-63.57, 74.02) * mm});
            skLineSegment(sketch, "E2167", {"start": v(-63.57, 74.02) * mm, "end": v(-62.78, 74.07) * mm});
            skLineSegment(sketch, "E2168", {"start": v(-63.33, 118.69) * mm, "end": v(-63.16, 118.8) * mm});
            skLineSegment(sketch, "E2169", {"start": v(-63.16, 118.8) * mm, "end": v(-62.97, 118.92) * mm});
            skLineSegment(sketch, "E2170", {"start": v(-62.97, 118.92) * mm, "end": v(-62.78, 119.04) * mm});
            skLineSegment(sketch, "E2171", {"start": v(-62.78, 119.04) * mm, "end": v(-62.58, 119.14) * mm});
            skLineSegment(sketch, "E2172", {"start": v(-62.58, 119.14) * mm, "end": v(-62.14, 119.35) * mm});
            skLineSegment(sketch, "E2173", {"start": v(-62.14, 119.35) * mm, "end": v(-61.68, 119.53) * mm});
            skLineSegment(sketch, "E2174", {"start": v(-61.68, 119.53) * mm, "end": v(-61.18, 119.7) * mm});
            skLineSegment(sketch, "E2175", {"start": v(-61.18, 119.7) * mm, "end": v(-60.67, 119.84) * mm});
            skLineSegment(sketch, "E2176", {"start": v(-60.67, 119.84) * mm, "end": v(-60.14, 119.96) * mm});
            skLineSegment(sketch, "E2177", {"start": v(-60.14, 119.96) * mm, "end": v(-59.6, 120.05) * mm});
            skLineSegment(sketch, "E2178", {"start": v(-59.6, 120.05) * mm, "end": v(-59.06, 120.12) * mm});
            skLineSegment(sketch, "E2179", {"start": v(-59.06, 120.12) * mm, "end": v(-58.51, 120.16) * mm});
            skLineSegment(sketch, "E2180", {"start": v(-58.51, 120.16) * mm, "end": v(-57.98, 120.18) * mm});
            skLineSegment(sketch, "E2181", {"start": v(-57.98, 120.18) * mm, "end": v(-57.46, 120.17) * mm});
            skLineSegment(sketch, "E2182", {"start": v(-57.46, 120.17) * mm, "end": v(-56.97, 120.13) * mm});
            skLineSegment(sketch, "E2183", {"start": v(-56.97, 120.13) * mm, "end": v(-56.73, 120.1) * mm});
            skLineSegment(sketch, "E2184", {"start": v(-56.73, 120.1) * mm, "end": v(-56.5, 120.05) * mm});
            skLineSegment(sketch, "E2185", {"start": v(-56.5, 120.05) * mm, "end": v(-56.27, 120) * mm});
            skLineSegment(sketch, "E2186", {"start": v(-56.27, 120) * mm, "end": v(-56.05, 119.95) * mm});
            skLineSegment(sketch, "E2187", {"start": v(-56.05, 119.95) * mm, "end": v(-55.85, 119.88) * mm});
            skLineSegment(sketch, "E2188", {"start": v(-55.85, 119.88) * mm, "end": v(-55.65, 119.8) * mm});
            skLineSegment(sketch, "E2189", {"start": v(-55.65, 119.8) * mm, "end": v(-55.47, 119.73) * mm});
            skLineSegment(sketch, "E2190", {"start": v(-55.47, 119.73) * mm, "end": v(-55.3, 119.64) * mm});
            skLineSegment(sketch, "E2191", {"start": v(-55.3, 119.64) * mm, "end": v(-55.13, 119.54) * mm});
            skLineSegment(sketch, "E2192", {"start": v(-55.13, 119.54) * mm, "end": v(-54.98, 119.43) * mm});
            skLineSegment(sketch, "E2193", {"start": v(-54.98, 119.43) * mm, "end": v(-54.91, 119.37) * mm});
            skLineSegment(sketch, "E2194", {"start": v(-54.91, 119.37) * mm, "end": v(-54.9, 119.36) * mm});
            skLineSegment(sketch, "E2195", {"start": v(-54.9, 119.36) * mm, "end": v(-54.91, 119.36) * mm});
            skLineSegment(sketch, "E2196", {"start": v(-54.91, 119.36) * mm, "end": v(-54.93, 119.37) * mm});
            skLineSegment(sketch, "E2197", {"start": v(-54.93, 119.37) * mm, "end": v(-54.98, 119.38) * mm});
            skLineSegment(sketch, "E2198", {"start": v(-54.98, 119.38) * mm, "end": v(-55.14, 119.4) * mm});
            skLineSegment(sketch, "E2199", {"start": v(-55.14, 119.4) * mm, "end": v(-55.46, 119.45) * mm});
            skLineSegment(sketch, "E2200", {"start": v(-55.46, 119.45) * mm, "end": v(-55.78, 119.48) * mm});
            skLineSegment(sketch, "E2201", {"start": v(-55.78, 119.48) * mm, "end": v(-56.08, 119.5) * mm});
            skLineSegment(sketch, "E2202", {"start": v(-56.08, 119.5) * mm, "end": v(-56.38, 119.5) * mm});
            skLineSegment(sketch, "E2203", {"start": v(-56.38, 119.5) * mm, "end": v(-56.66, 119.47) * mm});
            skLineSegment(sketch, "E2204", {"start": v(-56.66, 119.47) * mm, "end": v(-56.94, 119.44) * mm});
            skLineSegment(sketch, "E2205", {"start": v(-56.94, 119.44) * mm, "end": v(-57.2, 119.4) * mm});
            skLineSegment(sketch, "E2206", {"start": v(-57.2, 119.4) * mm, "end": v(-57.45, 119.34) * mm});
            skLineSegment(sketch, "E2207", {"start": v(-57.45, 119.34) * mm, "end": v(-57.7, 119.28) * mm});
            skLineSegment(sketch, "E2208", {"start": v(-57.7, 119.28) * mm, "end": v(-57.93, 119.2) * mm});
            skLineSegment(sketch, "E2209", {"start": v(-57.93, 119.2) * mm, "end": v(-58.16, 119.13) * mm});
            skLineSegment(sketch, "E2210", {"start": v(-58.16, 119.13) * mm, "end": v(-58.37, 119.04) * mm});
            skLineSegment(sketch, "E2211", {"start": v(-58.37, 119.04) * mm, "end": v(-58.57, 118.95) * mm});
            skLineSegment(sketch, "E2212", {"start": v(-58.57, 118.95) * mm, "end": v(-58.76, 118.86) * mm});
            skLineSegment(sketch, "E2213", {"start": v(-58.76, 118.86) * mm, "end": v(-58.94, 118.76) * mm});
            skLineSegment(sketch, "E2214", {"start": v(-58.94, 118.76) * mm, "end": v(-59.1, 118.67) * mm});
            skLineSegment(sketch, "E2215", {"start": v(-59.1, 118.67) * mm, "end": v(-59.27, 118.57) * mm});
            skLineSegment(sketch, "E2216", {"start": v(-59.27, 118.57) * mm, "end": v(-59.34, 118.53) * mm});
            skLineSegment(sketch, "E2217", {"start": v(-59.34, 118.53) * mm, "end": v(-59.35, 118.52) * mm});
            skLineSegment(sketch, "E2218", {"start": v(-59.35, 118.52) * mm, "end": v(-59.35, 118.51) * mm});
            skLineSegment(sketch, "E2219", {"start": v(-59.35, 118.51) * mm, "end": v(-59.34, 118.5) * mm});
            skLineSegment(sketch, "E2220", {"start": v(-59.34, 118.5) * mm, "end": v(-59.33, 118.46) * mm});
            skLineSegment(sketch, "E2221", {"start": v(-59.33, 118.46) * mm, "end": v(-59.29, 118.3) * mm});
            skLineSegment(sketch, "E2222", {"start": v(-59.29, 118.3) * mm, "end": v(-59.2, 118) * mm});
            skLineSegment(sketch, "E2223", {"start": v(-59.2, 118) * mm, "end": v(-58.97, 117.36) * mm});
            skLineSegment(sketch, "E2224", {"start": v(-58.97, 117.36) * mm, "end": v(-58.84, 117.05) * mm});
            skLineSegment(sketch, "E2225", {"start": v(-58.84, 117.05) * mm, "end": v(-58.7, 116.74) * mm});
            skLineSegment(sketch, "E2226", {"start": v(-58.7, 116.74) * mm, "end": v(-58.56, 116.44) * mm});
            skLineSegment(sketch, "E2227", {"start": v(-58.56, 116.44) * mm, "end": v(-58.4, 116.15) * mm});
            skLineSegment(sketch, "E2228", {"start": v(-58.4, 116.15) * mm, "end": v(-58.23, 115.88) * mm});
            skLineSegment(sketch, "E2229", {"start": v(-58.23, 115.88) * mm, "end": v(-58.05, 115.62) * mm});
            skLineSegment(sketch, "E2230", {"start": v(-58.05, 115.62) * mm, "end": v(-57.84, 115.37) * mm});
            skLineSegment(sketch, "E2231", {"start": v(-57.84, 115.37) * mm, "end": v(-57.6, 115.13) * mm});
            skLineSegment(sketch, "E2232", {"start": v(-57.6, 115.13) * mm, "end": v(-57.35, 114.9) * mm});
            skLineSegment(sketch, "E2233", {"start": v(-57.35, 114.9) * mm, "end": v(-57.08, 114.69) * mm});
            skLineSegment(sketch, "E2234", {"start": v(-57.08, 114.69) * mm, "end": v(-56.8, 114.5) * mm});
            skLineSegment(sketch, "E2235", {"start": v(-56.8, 114.5) * mm, "end": v(-56.5, 114.32) * mm});
            skLineSegment(sketch, "E2236", {"start": v(-56.5, 114.32) * mm, "end": v(-56.2, 114.17) * mm});
            skLineSegment(sketch, "E2237", {"start": v(-56.2, 114.17) * mm, "end": v(-55.9, 114.04) * mm});
            skLineSegment(sketch, "E2238", {"start": v(-55.9, 114.04) * mm, "end": v(-55.75, 113.99) * mm});
            skLineSegment(sketch, "E2239", {"start": v(-55.75, 113.99) * mm, "end": v(-55.73, 113.98) * mm});
            skLineSegment(sketch, "E2240", {"start": v(-55.73, 113.98) * mm, "end": v(-55.7, 113.97) * mm});
            skLineSegment(sketch, "E2241", {"start": v(-55.7, 113.97) * mm, "end": v(-55.63, 113.95) * mm});
            skLineSegment(sketch, "E2242", {"start": v(-55.63, 113.95) * mm, "end": v(-55.49, 113.91) * mm});
            skLineSegment(sketch, "E2243", {"start": v(-55.49, 113.91) * mm, "end": v(-55.2, 113.85) * mm});
            skLineSegment(sketch, "E2244", {"start": v(-55.2, 113.85) * mm, "end": v(-54.9, 113.81) * mm});
            skLineSegment(sketch, "E2245", {"start": v(-54.9, 113.81) * mm, "end": v(-54.58, 113.8) * mm});
            skLineSegment(sketch, "E2246", {"start": v(-54.58, 113.8) * mm, "end": v(-54.27, 113.8) * mm});
            skLineSegment(sketch, "E2247", {"start": v(-54.27, 113.8) * mm, "end": v(-53.95, 113.83) * mm});
            skLineSegment(sketch, "E2248", {"start": v(-53.95, 113.83) * mm, "end": v(-53.63, 113.88) * mm});
            skLineSegment(sketch, "E2249", {"start": v(-53.63, 113.88) * mm, "end": v(-53.32, 113.95) * mm});
            skLineSegment(sketch, "E2250", {"start": v(-53.32, 113.95) * mm, "end": v(-53, 114.03) * mm});
            skLineSegment(sketch, "E2251", {"start": v(-53, 114.03) * mm, "end": v(-52.7, 114.14) * mm});
            skLineSegment(sketch, "E2252", {"start": v(-52.7, 114.14) * mm, "end": v(-52.41, 114.27) * mm});
            skLineSegment(sketch, "E2253", {"start": v(-52.41, 114.27) * mm, "end": v(-52.13, 114.41) * mm});
            skLineSegment(sketch, "E2254", {"start": v(-52.13, 114.41) * mm, "end": v(-51.87, 114.57) * mm});
            skLineSegment(sketch, "E2255", {"start": v(-51.87, 114.57) * mm, "end": v(-51.63, 114.75) * mm});
            skLineSegment(sketch, "E2256", {"start": v(-51.63, 114.75) * mm, "end": v(-51.4, 114.95) * mm});
            skLineSegment(sketch, "E2257", {"start": v(-51.4, 114.95) * mm, "end": v(-51.2, 115.17) * mm});
            skLineSegment(sketch, "E2258", {"start": v(-51.2, 115.17) * mm, "end": v(-51.04, 115.4) * mm});
            skLineSegment(sketch, "E2259", {"start": v(-51.04, 115.4) * mm, "end": v(-50.9, 115.65) * mm});
            skLineSegment(sketch, "E2260", {"start": v(-50.9, 115.65) * mm, "end": v(-50.87, 115.71) * mm});
            skLineSegment(sketch, "E2261", {"start": v(-50.87, 115.71) * mm, "end": v(-50.85, 115.74) * mm});
            skLineSegment(sketch, "E2262", {"start": v(-50.85, 115.74) * mm, "end": v(-50.84, 115.76) * mm});
            skLineSegment(sketch, "E2263", {"start": v(-50.84, 115.76) * mm, "end": v(-50.85, 115.76) * mm});
            skLineSegment(sketch, "E2264", {"start": v(-50.85, 115.76) * mm, "end": v(-50.86, 115.82) * mm});
            skLineSegment(sketch, "E2265", {"start": v(-50.86, 115.82) * mm, "end": v(-50.9, 116.04) * mm});
            skLineSegment(sketch, "E2266", {"start": v(-50.9, 116.04) * mm, "end": v(-50.97, 116.3) * mm});
            skLineSegment(sketch, "E2267", {"start": v(-50.97, 116.3) * mm, "end": v(-51.05, 116.58) * mm});
            skLineSegment(sketch, "E2268", {"start": v(-51.05, 116.58) * mm, "end": v(-51.17, 116.88) * mm});
            skLineSegment(sketch, "E2269", {"start": v(-51.17, 116.88) * mm, "end": v(-51.32, 117.2) * mm});
            skLineSegment(sketch, "E2270", {"start": v(-51.32, 117.2) * mm, "end": v(-51.41, 117.35) * mm});
            skLineSegment(sketch, "E2271", {"start": v(-51.41, 117.35) * mm, "end": v(-51.51, 117.51) * mm});
            skLineSegment(sketch, "E2272", {"start": v(-51.51, 117.51) * mm, "end": v(-51.63, 117.67) * mm});
            skLineSegment(sketch, "E2273", {"start": v(-51.63, 117.67) * mm, "end": v(-51.75, 117.83) * mm});
            skLineSegment(sketch, "E2274", {"start": v(-51.75, 117.83) * mm, "end": v(-51.9, 117.98) * mm});
            skLineSegment(sketch, "E2275", {"start": v(-51.9, 117.98) * mm, "end": v(-52.05, 118.14) * mm});
            skLineSegment(sketch, "E2276", {"start": v(-52.05, 118.14) * mm, "end": v(-52.21, 118.29) * mm});
            skLineSegment(sketch, "E2277", {"start": v(-52.21, 118.29) * mm, "end": v(-52.3, 118.36) * mm});
            skLineSegment(sketch, "E2278", {"start": v(-52.3, 118.36) * mm, "end": v(-52.33, 118.38) * mm});
            skLineSegment(sketch, "E2279", {"start": v(-52.33, 118.38) * mm, "end": v(-52.34, 118.38) * mm});
            skLineSegment(sketch, "E2280", {"start": v(-52.34, 118.38) * mm, "end": v(-52.34, 118.39) * mm});
            skLineSegment(sketch, "E2281", {"start": v(-52.34, 118.39) * mm, "end": v(-52.32, 118.38) * mm});
            skLineSegment(sketch, "E2282", {"start": v(-52.32, 118.38) * mm, "end": v(-52.18, 118.33) * mm});
            skLineSegment(sketch, "E2283", {"start": v(-52.18, 118.33) * mm, "end": v(-51.63, 118.1) * mm});
            skLineSegment(sketch, "E2284", {"start": v(-51.63, 118.1) * mm, "end": v(-51.1, 117.85) * mm});
            skLineSegment(sketch, "E2285", {"start": v(-51.1, 117.85) * mm, "end": v(-50.58, 117.56) * mm});
            skLineSegment(sketch, "E2286", {"start": v(-50.58, 117.56) * mm, "end": v(-50.08, 117.23) * mm});
            skLineSegment(sketch, "E2287", {"start": v(-50.08, 117.23) * mm, "end": v(-49.6, 116.88) * mm});
            skLineSegment(sketch, "E2288", {"start": v(-49.6, 116.88) * mm, "end": v(-49.13, 116.5) * mm});
            skLineSegment(sketch, "E2289", {"start": v(-49.13, 116.5) * mm, "end": v(-48.68, 116.1) * mm});
            skLineSegment(sketch, "E2290", {"start": v(-48.68, 116.1) * mm, "end": v(-48.25, 115.68) * mm});
            skLineSegment(sketch, "E2291", {"start": v(-48.25, 115.68) * mm, "end": v(-47.84, 115.23) * mm});
            skLineSegment(sketch, "E2292", {"start": v(-47.84, 115.23) * mm, "end": v(-47.44, 114.77) * mm});
            skLineSegment(sketch, "E2293", {"start": v(-47.44, 114.77) * mm, "end": v(-47.06, 114.3) * mm});
            skLineSegment(sketch, "E2294", {"start": v(-47.06, 114.3) * mm, "end": v(-46.7, 113.8) * mm});
            skLineSegment(sketch, "E2295", {"start": v(-46.7, 113.8) * mm, "end": v(-46.36, 113.3) * mm});
            skLineSegment(sketch, "E2296", {"start": v(-46.36, 113.3) * mm, "end": v(-46.04, 112.79) * mm});
            skLineSegment(sketch, "E2297", {"start": v(-46.04, 112.79) * mm, "end": v(-45.73, 112.27) * mm});
            skLineSegment(sketch, "E2298", {"start": v(-45.73, 112.27) * mm, "end": v(-45.44, 111.74) * mm});
            skLineSegment(sketch, "E2299", {"start": v(-45.44, 111.74) * mm, "end": v(-45.17, 111.21) * mm});
            skLineSegment(sketch, "E2300", {"start": v(-45.17, 111.21) * mm, "end": v(-44.92, 110.68) * mm});
            skLineSegment(sketch, "E2301", {"start": v(-44.92, 110.68) * mm, "end": v(-44.43, 109.58) * mm});
            skLineSegment(sketch, "E2302", {"start": v(-44.43, 109.58) * mm, "end": v(-43.98, 108.47) * mm});
            skLineSegment(sketch, "E2303", {"start": v(-43.98, 108.47) * mm, "end": v(-43.57, 107.38) * mm});
            skLineSegment(sketch, "E2304", {"start": v(-43.57, 107.38) * mm, "end": v(-43.2, 106.3) * mm});
            skLineSegment(sketch, "E2305", {"start": v(-43.2, 106.3) * mm, "end": v(-43.02, 105.77) * mm});
            skLineSegment(sketch, "E2306", {"start": v(-43.02, 105.77) * mm, "end": v(-42.86, 105.24) * mm});
            skLineSegment(sketch, "E2307", {"start": v(-42.86, 105.24) * mm, "end": v(-42.7, 104.72) * mm});
            skLineSegment(sketch, "E2308", {"start": v(-42.7, 104.72) * mm, "end": v(-42.55, 104.21) * mm});
            skLineSegment(sketch, "E2309", {"start": v(-42.55, 104.21) * mm, "end": v(-42.41, 103.71) * mm});
            skLineSegment(sketch, "E2310", {"start": v(-42.41, 103.71) * mm, "end": v(-42.28, 103.22) * mm});
            skLineSegment(sketch, "E2311", {"start": v(-42.28, 103.22) * mm, "end": v(-42.16, 102.74) * mm});
            skLineSegment(sketch, "E2312", {"start": v(-42.16, 102.74) * mm, "end": v(-42.04, 102.27) * mm});
            skLineSegment(sketch, "E2313", {"start": v(-42.04, 102.27) * mm, "end": v(-41.94, 101.82) * mm});
            skLineSegment(sketch, "E2314", {"start": v(-41.94, 101.82) * mm, "end": v(-41.83, 101.38) * mm});
            skLineSegment(sketch, "E2315", {"start": v(-41.83, 101.38) * mm, "end": v(-41.74, 100.95) * mm});
            skLineSegment(sketch, "E2316", {"start": v(-41.74, 100.95) * mm, "end": v(-41.65, 100.55) * mm});
            skLineSegment(sketch, "E2317", {"start": v(-41.65, 100.55) * mm, "end": v(-41.57, 100.15) * mm});
            skLineSegment(sketch, "E2318", {"start": v(-41.57, 100.15) * mm, "end": v(-41.5, 99.78) * mm});
            skLineSegment(sketch, "E2319", {"start": v(-41.5, 99.78) * mm, "end": v(-41.43, 99.42) * mm});
            skLineSegment(sketch, "E2320", {"start": v(-41.43, 99.42) * mm, "end": v(-41.37, 99.08) * mm});
            skLineSegment(sketch, "E2321", {"start": v(-41.37, 99.08) * mm, "end": v(-41.31, 98.77) * mm});
            skLineSegment(sketch, "E2322", {"start": v(-41.31, 98.77) * mm, "end": v(-41.26, 98.47) * mm});
            skLineSegment(sketch, "E2323", {"start": v(-41.26, 98.47) * mm, "end": v(-41.22, 98.2) * mm});
            skLineSegment(sketch, "E2324", {"start": v(-41.22, 98.2) * mm, "end": v(-41.18, 97.94) * mm});
            skLineSegment(sketch, "E2325", {"start": v(-41.18, 97.94) * mm, "end": v(-41.14, 97.72) * mm});
            skLineSegment(sketch, "E2326", {"start": v(-41.14, 97.72) * mm, "end": v(-41.11, 97.52) * mm});
            skLineSegment(sketch, "E2327", {"start": v(-41.11, 97.52) * mm, "end": v(-41.09, 97.34) * mm});
            skLineSegment(sketch, "E2328", {"start": v(-41.09, 97.34) * mm, "end": v(-41.07, 97.19) * mm});
            skLineSegment(sketch, "E2329", {"start": v(-41.07, 97.19) * mm, "end": v(-41.05, 97.07) * mm});
            skLineSegment(sketch, "E2330", {"start": v(-41.05, 97.07) * mm, "end": v(-41.04, 96.97) * mm});
            skLineSegment(sketch, "E2331", {"start": v(-41.04, 96.97) * mm, "end": v(-41.03, 96.91) * mm});
            skLineSegment(sketch, "E2332", {"start": v(-41.03, 96.91) * mm, "end": v(-41.03, 96.88) * mm});
            skLineSegment(sketch, "E2333", {"start": v(-41.03, 96.88) * mm, "end": v(-41.03, 96.87) * mm});
            skLineSegment(sketch, "E2334", {"start": v(-41.03, 96.87) * mm, "end": v(-41.04, 96.9) * mm});
            skLineSegment(sketch, "E2335", {"start": v(-41.04, 96.9) * mm, "end": v(-41.07, 96.94) * mm});
            skLineSegment(sketch, "E2336", {"start": v(-41.07, 96.94) * mm, "end": v(-41.11, 97) * mm});
            skLineSegment(sketch, "E2337", {"start": v(-41.11, 97) * mm, "end": v(-41.17, 97.09) * mm});
            skLineSegment(sketch, "E2338", {"start": v(-41.17, 97.09) * mm, "end": v(-41.24, 97.2) * mm});
            skLineSegment(sketch, "E2339", {"start": v(-41.24, 97.2) * mm, "end": v(-41.32, 97.32) * mm});
            skLineSegment(sketch, "E2340", {"start": v(-41.32, 97.32) * mm, "end": v(-41.41, 97.46) * mm});
            skLineSegment(sketch, "E2341", {"start": v(-41.41, 97.46) * mm, "end": v(-41.51, 97.61) * mm});
            skLineSegment(sketch, "E2342", {"start": v(-41.51, 97.61) * mm, "end": v(-41.63, 97.78) * mm});
            skLineSegment(sketch, "E2343", {"start": v(-41.63, 97.78) * mm, "end": v(-41.75, 97.97) * mm});
            skLineSegment(sketch, "E2344", {"start": v(-41.75, 97.97) * mm, "end": v(-41.88, 98.17) * mm});
            skLineSegment(sketch, "E2345", {"start": v(-41.88, 98.17) * mm, "end": v(-42.02, 98.38) * mm});
            skLineSegment(sketch, "E2346", {"start": v(-42.02, 98.38) * mm, "end": v(-42.17, 98.6) * mm});
            skLineSegment(sketch, "E2347", {"start": v(-42.17, 98.6) * mm, "end": v(-42.32, 98.84) * mm});
            skLineSegment(sketch, "E2348", {"start": v(-42.32, 98.84) * mm, "end": v(-42.48, 99.08) * mm});
            skLineSegment(sketch, "E2349", {"start": v(-42.48, 99.08) * mm, "end": v(-42.83, 99.59) * mm});
            skLineSegment(sketch, "E2350", {"start": v(-42.83, 99.59) * mm, "end": v(-43.19, 100.12) * mm});
            skLineSegment(sketch, "E2351", {"start": v(-43.19, 100.12) * mm, "end": v(-43.56, 100.68) * mm});
            skLineSegment(sketch, "E2352", {"start": v(-43.56, 100.68) * mm, "end": v(-43.95, 101.24) * mm});
            skLineSegment(sketch, "E2353", {"start": v(-43.95, 101.24) * mm, "end": v(-44.73, 102.37) * mm});
            skLineSegment(sketch, "E2354", {"start": v(-44.73, 102.37) * mm, "end": v(-45.11, 102.91) * mm});
            skLineSegment(sketch, "E2355", {"start": v(-45.11, 102.91) * mm, "end": v(-45.5, 103.44) * mm});
            skLineSegment(sketch, "E2356", {"start": v(-45.5, 103.44) * mm, "end": v(-45.85, 103.93) * mm});
            skLineSegment(sketch, "E2357", {"start": v(-45.85, 103.93) * mm, "end": v(-46.03, 104.17) * mm});
            skLineSegment(sketch, "E2358", {"start": v(-46.03, 104.17) * mm, "end": v(-46.2, 104.4) * mm});
            skLineSegment(sketch, "E2359", {"start": v(-46.2, 104.4) * mm, "end": v(-46.36, 104.6) * mm});
            skLineSegment(sketch, "E2360", {"start": v(-46.36, 104.6) * mm, "end": v(-46.38, 104.63) * mm});
            skLineSegment(sketch, "E2361", {"start": v(-46.38, 104.63) * mm, "end": v(-46.4, 104.62) * mm});
            skLineSegment(sketch, "E2362", {"start": v(-46.4, 104.62) * mm, "end": v(-46.4, 104.58) * mm});
            skLineSegment(sketch, "E2363", {"start": v(-46.4, 104.58) * mm, "end": v(-46.43, 104.5) * mm});
            skLineSegment(sketch, "E2364", {"start": v(-46.43, 104.5) * mm, "end": v(-46.55, 104.14) * mm});
            skLineSegment(sketch, "E2365", {"start": v(-46.55, 104.14) * mm, "end": v(-46.67, 103.75) * mm});
            skLineSegment(sketch, "E2366", {"start": v(-46.67, 103.75) * mm, "end": v(-46.8, 103.33) * mm});
            skLineSegment(sketch, "E2367", {"start": v(-46.8, 103.33) * mm, "end": v(-46.91, 102.9) * mm});
            skLineSegment(sketch, "E2368", {"start": v(-46.91, 102.9) * mm, "end": v(-47.03, 102.44) * mm});
            skLineSegment(sketch, "E2369", {"start": v(-47.03, 102.44) * mm, "end": v(-47.26, 101.52) * mm});
            skLineSegment(sketch, "E2370", {"start": v(-47.26, 101.52) * mm, "end": v(-47.36, 101.06) * mm});
            skLineSegment(sketch, "E2371", {"start": v(-47.36, 101.06) * mm, "end": v(-47.47, 100.62) * mm});
            skLineSegment(sketch, "E2372", {"start": v(-47.47, 100.62) * mm, "end": v(-47.56, 100.2) * mm});
            skLineSegment(sketch, "E2373", {"start": v(-47.56, 100.2) * mm, "end": v(-47.65, 99.8) * mm});
            skLineSegment(sketch, "E2374", {"start": v(-47.65, 99.8) * mm, "end": v(-47.73, 99.44) * mm});
            skLineSegment(sketch, "E2375", {"start": v(-47.73, 99.44) * mm, "end": v(-47.77, 99.27) * mm});
            skLineSegment(sketch, "E2376", {"start": v(-47.77, 99.27) * mm, "end": v(-47.8, 99.11) * mm});
            skLineSegment(sketch, "E2377", {"start": v(-47.8, 99.11) * mm, "end": v(-47.83, 98.97) * mm});
            skLineSegment(sketch, "E2378", {"start": v(-47.83, 98.97) * mm, "end": v(-47.86, 98.84) * mm});
            skLineSegment(sketch, "E2379", {"start": v(-47.86, 98.84) * mm, "end": v(-47.89, 98.72) * mm});
            skLineSegment(sketch, "E2380", {"start": v(-47.89, 98.72) * mm, "end": v(-47.9, 98.61) * mm});
            skLineSegment(sketch, "E2381", {"start": v(-47.9, 98.61) * mm, "end": v(-47.93, 98.52) * mm});
            skLineSegment(sketch, "E2382", {"start": v(-47.93, 98.52) * mm, "end": v(-47.94, 98.44) * mm});
            skLineSegment(sketch, "E2383", {"start": v(-47.94, 98.44) * mm, "end": v(-47.95, 98.38) * mm});
            skLineSegment(sketch, "E2384", {"start": v(-47.95, 98.38) * mm, "end": v(-47.96, 98.34) * mm});
            skLineSegment(sketch, "E2385", {"start": v(-47.96, 98.34) * mm, "end": v(-47.97, 98.32) * mm});
            skLineSegment(sketch, "E2386", {"start": v(-47.97, 98.32) * mm, "end": v(-47.97, 98.32) * mm});
            skLineSegment(sketch, "E2387", {"start": v(-47.97, 98.32) * mm, "end": v(-47.97, 98.33) * mm});
            skLineSegment(sketch, "E2388", {"start": v(-47.97, 98.33) * mm, "end": v(-47.99, 98.37) * mm});
            skLineSegment(sketch, "E2389", {"start": v(-47.99, 98.37) * mm, "end": v(-48, 98.42) * mm});
            skLineSegment(sketch, "E2390", {"start": v(-48, 98.42) * mm, "end": v(-48.03, 98.5) * mm});
            skLineSegment(sketch, "E2391", {"start": v(-48.03, 98.5) * mm, "end": v(-48.07, 98.59) * mm});
            skLineSegment(sketch, "E2392", {"start": v(-48.07, 98.59) * mm, "end": v(-48.1, 98.7) * mm});
            skLineSegment(sketch, "E2393", {"start": v(-48.1, 98.7) * mm, "end": v(-48.15, 98.82) * mm});
            skLineSegment(sketch, "E2394", {"start": v(-48.15, 98.82) * mm, "end": v(-48.2, 98.96) * mm});
            skLineSegment(sketch, "E2395", {"start": v(-48.2, 98.96) * mm, "end": v(-48.26, 99.1) * mm});
            skLineSegment(sketch, "E2396", {"start": v(-48.26, 99.1) * mm, "end": v(-48.32, 99.27) * mm});
            skLineSegment(sketch, "E2397", {"start": v(-48.32, 99.27) * mm, "end": v(-48.38, 99.45) * mm});
            skLineSegment(sketch, "E2398", {"start": v(-48.38, 99.45) * mm, "end": v(-48.45, 99.64) * mm});
            skLineSegment(sketch, "E2399", {"start": v(-48.45, 99.64) * mm, "end": v(-48.6, 100.04) * mm});
            skLineSegment(sketch, "E2400", {"start": v(-48.6, 100.04) * mm, "end": v(-48.75, 100.48) * mm});
            skLineSegment(sketch, "E2401", {"start": v(-48.75, 100.48) * mm, "end": v(-48.92, 100.95) * mm});
            skLineSegment(sketch, "E2402", {"start": v(-48.92, 100.95) * mm, "end": v(-49.09, 101.44) * mm});
            skLineSegment(sketch, "E2403", {"start": v(-49.09, 101.44) * mm, "end": v(-49.26, 101.94) * mm});
            skLineSegment(sketch, "E2404", {"start": v(-49.26, 101.94) * mm, "end": v(-49.6, 102.95) * mm});
            skLineSegment(sketch, "E2405", {"start": v(-49.6, 102.95) * mm, "end": v(-49.78, 103.45) * mm});
            skLineSegment(sketch, "E2406", {"start": v(-49.78, 103.45) * mm, "end": v(-49.94, 103.93) * mm});
            skLineSegment(sketch, "E2407", {"start": v(-49.94, 103.93) * mm, "end": v(-50.08, 104.4) * mm});
            skLineSegment(sketch, "E2408", {"start": v(-50.08, 104.4) * mm, "end": v(-50.22, 104.82) * mm});
            skLineSegment(sketch, "E2409", {"start": v(-50.22, 104.82) * mm, "end": v(-50.28, 105.03) * mm});
            skLineSegment(sketch, "E2410", {"start": v(-50.28, 105.03) * mm, "end": v(-50.34, 105.22) * mm});
            skLineSegment(sketch, "E2411", {"start": v(-50.34, 105.22) * mm, "end": v(-50.35, 105.27) * mm});
            skLineSegment(sketch, "E2412", {"start": v(-50.35, 105.27) * mm, "end": v(-50.35, 105.27) * mm});
            skLineSegment(sketch, "E2413", {"start": v(-50.35, 105.27) * mm, "end": v(-50.36, 105.27) * mm});
            skLineSegment(sketch, "E2414", {"start": v(-50.36, 105.27) * mm, "end": v(-50.36, 105.25) * mm});
            skLineSegment(sketch, "E2415", {"start": v(-50.36, 105.25) * mm, "end": v(-50.38, 105.21) * mm});
            skLineSegment(sketch, "E2416", {"start": v(-50.38, 105.21) * mm, "end": v(-50.45, 105.07) * mm});
            skLineSegment(sketch, "E2417", {"start": v(-50.45, 105.07) * mm, "end": v(-50.6, 104.78) * mm});
            skLineSegment(sketch, "E2418", {"start": v(-50.6, 104.78) * mm, "end": v(-50.75, 104.47) * mm});
            skLineSegment(sketch, "E2419", {"start": v(-50.75, 104.47) * mm, "end": v(-50.9, 104.15) * mm});
            skLineSegment(sketch, "E2420", {"start": v(-50.9, 104.15) * mm, "end": v(-51.07, 103.81) * mm});
            skLineSegment(sketch, "E2421", {"start": v(-51.07, 103.81) * mm, "end": v(-51.24, 103.47) * mm});
            skLineSegment(sketch, "E2422", {"start": v(-51.24, 103.47) * mm, "end": v(-51.59, 102.75) * mm});
            skLineSegment(sketch, "E2423", {"start": v(-51.59, 102.75) * mm, "end": v(-51.95, 102) * mm});
            skLineSegment(sketch, "E2424", {"start": v(-51.95, 102) * mm, "end": v(-52.68, 100.48) * mm});
            skLineSegment(sketch, "E2425", {"start": v(-52.68, 100.48) * mm, "end": v(-53.04, 99.72) * mm});
            skLineSegment(sketch, "E2426", {"start": v(-53.04, 99.72) * mm, "end": v(-53.4, 98.98) * mm});
            skLineSegment(sketch, "E2427", {"start": v(-53.4, 98.98) * mm, "end": v(-53.73, 98.26) * mm});
            skLineSegment(sketch, "E2428", {"start": v(-53.73, 98.26) * mm, "end": v(-53.9, 97.92) * mm});
            skLineSegment(sketch, "E2429", {"start": v(-53.9, 97.92) * mm, "end": v(-54.06, 97.58) * mm});
            skLineSegment(sketch, "E2430", {"start": v(-54.06, 97.58) * mm, "end": v(-54.2, 97.26) * mm});
            skLineSegment(sketch, "E2431", {"start": v(-54.2, 97.26) * mm, "end": v(-54.35, 96.95) * mm});
            skLineSegment(sketch, "E2432", {"start": v(-54.35, 96.95) * mm, "end": v(-54.5, 96.66) * mm});
            skLineSegment(sketch, "E2433", {"start": v(-54.5, 96.66) * mm, "end": v(-54.62, 96.38) * mm});
            skLineSegment(sketch, "E2434", {"start": v(-54.62, 96.38) * mm, "end": v(-54.75, 96.12) * mm});
            skLineSegment(sketch, "E2435", {"start": v(-54.75, 96.12) * mm, "end": v(-54.86, 95.88) * mm});
            skLineSegment(sketch, "E2436", {"start": v(-54.86, 95.88) * mm, "end": v(-54.96, 95.66) * mm});
            skLineSegment(sketch, "E2437", {"start": v(-54.96, 95.66) * mm, "end": v(-55.06, 95.46) * mm});
            skLineSegment(sketch, "E2438", {"start": v(-55.06, 95.46) * mm, "end": v(-55.14, 95.28) * mm});
            skLineSegment(sketch, "E2439", {"start": v(-55.14, 95.28) * mm, "end": v(-55.21, 95.13) * mm});
            skLineSegment(sketch, "E2440", {"start": v(-55.21, 95.13) * mm, "end": v(-55.27, 95) * mm});
            skLineSegment(sketch, "E2441", {"start": v(-55.27, 95) * mm, "end": v(-55.32, 94.9) * mm});
            skLineSegment(sketch, "E2442", {"start": v(-55.32, 94.9) * mm, "end": v(-55.35, 94.83) * mm});
            skLineSegment(sketch, "E2443", {"start": v(-55.35, 94.83) * mm, "end": v(-55.37, 94.8) * mm});
            skLineSegment(sketch, "E2444", {"start": v(-55.37, 94.8) * mm, "end": v(-55.38, 94.78) * mm});
            skLineSegment(sketch, "E2445", {"start": v(-55.38, 94.78) * mm, "end": v(-55.38, 94.8) * mm});
            skLineSegment(sketch, "E2446", {"start": v(-55.38, 94.8) * mm, "end": v(-55.37, 94.85) * mm});
            skLineSegment(sketch, "E2447", {"start": v(-55.37, 94.85) * mm, "end": v(-55.37, 94.93) * mm});
            skLineSegment(sketch, "E2448", {"start": v(-55.37, 94.93) * mm, "end": v(-55.36, 95.04) * mm});
            skLineSegment(sketch, "E2449", {"start": v(-55.36, 95.04) * mm, "end": v(-55.35, 95.18) * mm});
            skLineSegment(sketch, "E2450", {"start": v(-55.35, 95.18) * mm, "end": v(-55.35, 95.34) * mm});
            skLineSegment(sketch, "E2451", {"start": v(-55.35, 95.34) * mm, "end": v(-55.34, 95.53) * mm});
            skLineSegment(sketch, "E2452", {"start": v(-55.34, 95.53) * mm, "end": v(-55.33, 95.74) * mm});
            skLineSegment(sketch, "E2453", {"start": v(-55.33, 95.74) * mm, "end": v(-55.32, 95.98) * mm});
            skLineSegment(sketch, "E2454", {"start": v(-55.32, 95.98) * mm, "end": v(-55.31, 96.23) * mm});
            skLineSegment(sketch, "E2455", {"start": v(-55.31, 96.23) * mm, "end": v(-55.3, 96.51) * mm});
            skLineSegment(sketch, "E2456", {"start": v(-55.3, 96.51) * mm, "end": v(-55.3, 96.81) * mm});
            skLineSegment(sketch, "E2457", {"start": v(-55.3, 96.81) * mm, "end": v(-55.29, 97.13) * mm});
            skLineSegment(sketch, "E2458", {"start": v(-55.29, 97.13) * mm, "end": v(-55.28, 97.46) * mm});
            skLineSegment(sketch, "E2459", {"start": v(-55.28, 97.46) * mm, "end": v(-55.28, 97.82) * mm});
            skLineSegment(sketch, "E2460", {"start": v(-55.28, 97.82) * mm, "end": v(-55.27, 98.18) * mm});
            skLineSegment(sketch, "E2461", {"start": v(-55.27, 98.18) * mm, "end": v(-55.27, 98.56) * mm});
            skLineSegment(sketch, "E2462", {"start": v(-55.27, 98.56) * mm, "end": v(-55.27, 98.96) * mm});
            skLineSegment(sketch, "E2463", {"start": v(-55.27, 98.96) * mm, "end": v(-55.28, 99.36) * mm});
            skLineSegment(sketch, "E2464", {"start": v(-55.28, 99.36) * mm, "end": v(-55.3, 100.2) * mm});
            skLineSegment(sketch, "E2465", {"start": v(-55.3, 100.2) * mm, "end": v(-55.32, 101.09) * mm});
            skLineSegment(sketch, "E2466", {"start": v(-55.32, 101.09) * mm, "end": v(-55.36, 102) * mm});
            skLineSegment(sketch, "E2467", {"start": v(-55.36, 102) * mm, "end": v(-55.42, 102.92) * mm});
            skLineSegment(sketch, "E2468", {"start": v(-55.42, 102.92) * mm, "end": v(-55.5, 103.86) * mm});
            skLineSegment(sketch, "E2469", {"start": v(-55.5, 103.86) * mm, "end": v(-55.6, 104.8) * mm});
            skLineSegment(sketch, "E2470", {"start": v(-55.6, 104.8) * mm, "end": v(-55.72, 105.72) * mm});
            skLineSegment(sketch, "E2471", {"start": v(-55.72, 105.72) * mm, "end": v(-55.86, 106.63) * mm});
            skLineSegment(sketch, "E2472", {"start": v(-55.86, 106.63) * mm, "end": v(-55.94, 107.07) * mm});
            skLineSegment(sketch, "E2473", {"start": v(-55.94, 107.07) * mm, "end": v(-55.97, 107.18) * mm});
            skLineSegment(sketch, "E2474", {"start": v(-55.97, 107.18) * mm, "end": v(-55.98, 107.24) * mm});
            skLineSegment(sketch, "E2475", {"start": v(-55.98, 107.24) * mm, "end": v(-55.99, 107.28) * mm});
            skLineSegment(sketch, "E2476", {"start": v(-55.99, 107.28) * mm, "end": v(-56.01, 107.42) * mm});
            skLineSegment(sketch, "E2477", {"start": v(-56.01, 107.42) * mm, "end": v(-56.08, 107.7) * mm});
            skLineSegment(sketch, "E2478", {"start": v(-56.08, 107.7) * mm, "end": v(-56.14, 108) * mm});
            skLineSegment(sketch, "E2479", {"start": v(-56.14, 108) * mm, "end": v(-56.3, 108.61) * mm});
            skLineSegment(sketch, "E2480", {"start": v(-56.3, 108.61) * mm, "end": v(-56.47, 109.26) * mm});
            skLineSegment(sketch, "E2481", {"start": v(-56.47, 109.26) * mm, "end": v(-56.68, 109.93) * mm});
            skLineSegment(sketch, "E2482", {"start": v(-56.68, 109.93) * mm, "end": v(-56.9, 110.62) * mm});
            skLineSegment(sketch, "E2483", {"start": v(-56.9, 110.62) * mm, "end": v(-57.17, 111.32) * mm});
            skLineSegment(sketch, "E2484", {"start": v(-57.17, 111.32) * mm, "end": v(-57.47, 112.03) * mm});
            skLineSegment(sketch, "E2485", {"start": v(-57.47, 112.03) * mm, "end": v(-57.8, 112.75) * mm});
            skLineSegment(sketch, "E2486", {"start": v(-57.8, 112.75) * mm, "end": v(-58.16, 113.45) * mm});
            skLineSegment(sketch, "E2487", {"start": v(-58.16, 113.45) * mm, "end": v(-58.56, 114.15) * mm});
            skLineSegment(sketch, "E2488", {"start": v(-58.56, 114.15) * mm, "end": v(-58.78, 114.5) * mm});
            skLineSegment(sketch, "E2489", {"start": v(-58.78, 114.5) * mm, "end": v(-59, 114.83) * mm});
            skLineSegment(sketch, "E2490", {"start": v(-59, 114.83) * mm, "end": v(-59.24, 115.17) * mm});
            skLineSegment(sketch, "E2491", {"start": v(-59.24, 115.17) * mm, "end": v(-59.48, 115.5) * mm});
            skLineSegment(sketch, "E2492", {"start": v(-59.48, 115.5) * mm, "end": v(-59.74, 115.82) * mm});
            skLineSegment(sketch, "E2493", {"start": v(-59.74, 115.82) * mm, "end": v(-60, 116.13) * mm});
            skLineSegment(sketch, "E2494", {"start": v(-60, 116.13) * mm, "end": v(-60.29, 116.43) * mm});
            skLineSegment(sketch, "E2495", {"start": v(-60.29, 116.43) * mm, "end": v(-60.58, 116.73) * mm});
            skLineSegment(sketch, "E2496", {"start": v(-60.58, 116.73) * mm, "end": v(-60.88, 117.02) * mm});
            skLineSegment(sketch, "E2497", {"start": v(-60.88, 117.02) * mm, "end": v(-61.19, 117.3) * mm});
            skLineSegment(sketch, "E2498", {"start": v(-61.19, 117.3) * mm, "end": v(-61.51, 117.56) * mm});
            skLineSegment(sketch, "E2499", {"start": v(-61.51, 117.56) * mm, "end": v(-61.85, 117.8) * mm});
            skLineSegment(sketch, "E2500", {"start": v(-61.85, 117.8) * mm, "end": v(-62.2, 118.05) * mm});
            skLineSegment(sketch, "E2501", {"start": v(-62.2, 118.05) * mm, "end": v(-62.56, 118.28) * mm});
            skLineSegment(sketch, "E2502", {"start": v(-62.56, 118.28) * mm, "end": v(-62.94, 118.49) * mm});
            skLineSegment(sketch, "E2503", {"start": v(-62.94, 118.49) * mm, "end": v(-63.33, 118.69) * mm});
            skLineSegment(sketch, "E2504", {"start": v(-44.1, 67.65) * mm, "end": v(-44.76, 67.92) * mm});
            skLineSegment(sketch, "E2505", {"start": v(-44.76, 67.92) * mm, "end": v(-45.42, 68.12) * mm});
            skLineSegment(sketch, "E2506", {"start": v(-45.42, 68.12) * mm, "end": v(-46.1, 68.26) * mm});
            skLineSegment(sketch, "E2507", {"start": v(-46.1, 68.26) * mm, "end": v(-46.76, 68.34) * mm});
            skLineSegment(sketch, "E2508", {"start": v(-46.76, 68.34) * mm, "end": v(-47.44, 68.35) * mm});
            skLineSegment(sketch, "E2509", {"start": v(-47.44, 68.35) * mm, "end": v(-48.1, 68.3) * mm});
            skLineSegment(sketch, "E2510", {"start": v(-48.1, 68.3) * mm, "end": v(-48.76, 68.2) * mm});
            skLineSegment(sketch, "E2511", {"start": v(-48.76, 68.2) * mm, "end": v(-49.4, 68.04) * mm});
            skLineSegment(sketch, "E2512", {"start": v(-49.4, 68.04) * mm, "end": v(-50.03, 67.82) * mm});
            skLineSegment(sketch, "E2513", {"start": v(-50.03, 67.82) * mm, "end": v(-50.63, 67.54) * mm});
            skLineSegment(sketch, "E2514", {"start": v(-50.63, 67.54) * mm, "end": v(-51.2, 67.21) * mm});
            skLineSegment(sketch, "E2515", {"start": v(-51.2, 67.21) * mm, "end": v(-51.75, 66.83) * mm});
            skLineSegment(sketch, "E2516", {"start": v(-51.75, 66.83) * mm, "end": v(-52.01, 66.62) * mm});
            skLineSegment(sketch, "E2517", {"start": v(-52.01, 66.62) * mm, "end": v(-52.14, 66.51) * mm});
            skLineSegment(sketch, "E2518", {"start": v(-52.14, 66.51) * mm, "end": v(-52.17, 66.49) * mm});
            skLineSegment(sketch, "E2519", {"start": v(-52.17, 66.49) * mm, "end": v(-52.17, 66.5) * mm});
            skLineSegment(sketch, "E2520", {"start": v(-52.17, 66.5) * mm, "end": v(-52.16, 66.5) * mm});
            skLineSegment(sketch, "E2521", {"start": v(-52.16, 66.5) * mm, "end": v(-52.14, 66.56) * mm});
            skLineSegment(sketch, "E2522", {"start": v(-52.14, 66.56) * mm, "end": v(-52.1, 66.68) * mm});
            skLineSegment(sketch, "E2523", {"start": v(-52.1, 66.68) * mm, "end": v(-51.91, 67.16) * mm});
            skLineSegment(sketch, "E2524", {"start": v(-51.91, 67.16) * mm, "end": v(-51.89, 67.22) * mm});
            skLineSegment(sketch, "E2525", {"start": v(-51.89, 67.22) * mm, "end": v(-51.87, 67.25) * mm});
            skLineSegment(sketch, "E2526", {"start": v(-51.87, 67.25) * mm, "end": v(-51.86, 67.28) * mm});
            skLineSegment(sketch, "E2527", {"start": v(-51.86, 67.28) * mm, "end": v(-51.82, 67.37) * mm});
            skLineSegment(sketch, "E2528", {"start": v(-51.82, 67.37) * mm, "end": v(-51.73, 67.55) * mm});
            skLineSegment(sketch, "E2529", {"start": v(-51.73, 67.55) * mm, "end": v(-51.31, 68.21) * mm});
            skLineSegment(sketch, "E2530", {"start": v(-51.31, 68.21) * mm, "end": v(-50.83, 68.81) * mm});
            skLineSegment(sketch, "E2531", {"start": v(-50.83, 68.81) * mm, "end": v(-50.28, 69.34) * mm});
            skLineSegment(sketch, "E2532", {"start": v(-50.28, 69.34) * mm, "end": v(-49.68, 69.8) * mm});
            skLineSegment(sketch, "E2533", {"start": v(-49.68, 69.8) * mm, "end": v(-49.03, 70.17) * mm});
            skLineSegment(sketch, "E2534", {"start": v(-49.03, 70.17) * mm, "end": v(-48.34, 70.46) * mm});
            skLineSegment(sketch, "E2535", {"start": v(-48.34, 70.46) * mm, "end": v(-47.63, 70.67) * mm});
            skLineSegment(sketch, "E2536", {"start": v(-47.63, 70.67) * mm, "end": v(-46.89, 70.8) * mm});
            skLineSegment(sketch, "E2537", {"start": v(-46.89, 70.8) * mm, "end": v(-46.14, 70.82) * mm});
            skLineSegment(sketch, "E2538", {"start": v(-46.14, 70.82) * mm, "end": v(-45.38, 70.76) * mm});
            skLineSegment(sketch, "E2539", {"start": v(-45.38, 70.76) * mm, "end": v(-44.62, 70.6) * mm});
            skLineSegment(sketch, "E2540", {"start": v(-44.62, 70.6) * mm, "end": v(-43.88, 70.36) * mm});
            skLineSegment(sketch, "E2541", {"start": v(-43.88, 70.36) * mm, "end": v(-43.52, 70.2) * mm});
            skLineSegment(sketch, "E2542", {"start": v(-43.52, 70.2) * mm, "end": v(-43.21, 70.03) * mm});
            skLineSegment(sketch, "E2543", {"start": v(-43.21, 70.03) * mm, "end": v(-42.63, 69.67) * mm});
            skLineSegment(sketch, "E2544", {"start": v(-42.63, 69.67) * mm, "end": v(-42.1, 69.25) * mm});
            skLineSegment(sketch, "E2545", {"start": v(-42.1, 69.25) * mm, "end": v(-41.63, 68.78) * mm});
            skLineSegment(sketch, "E2546", {"start": v(-41.63, 68.78) * mm, "end": v(-41.21, 68.27) * mm});
            skLineSegment(sketch, "E2547", {"start": v(-41.21, 68.27) * mm, "end": v(-40.86, 67.71) * mm});
            skLineSegment(sketch, "E2548", {"start": v(-40.86, 67.71) * mm, "end": v(-40.56, 67.13) * mm});
            skLineSegment(sketch, "E2549", {"start": v(-40.56, 67.13) * mm, "end": v(-40.33, 66.52) * mm});
            skLineSegment(sketch, "E2550", {"start": v(-40.33, 66.52) * mm, "end": v(-40.16, 65.9) * mm});
            skLineSegment(sketch, "E2551", {"start": v(-40.16, 65.9) * mm, "end": v(-40.06, 65.24) * mm});
            skLineSegment(sketch, "E2552", {"start": v(-40.06, 65.24) * mm, "end": v(-40.02, 64.59) * mm});
            skLineSegment(sketch, "E2553", {"start": v(-40.02, 64.59) * mm, "end": v(-40.06, 63.92) * mm});
            skLineSegment(sketch, "E2554", {"start": v(-40.06, 63.92) * mm, "end": v(-40.17, 63.26) * mm});
            skLineSegment(sketch, "E2555", {"start": v(-40.17, 63.26) * mm, "end": v(-40.19, 63.18) * mm});
            skLineSegment(sketch, "E2556", {"start": v(-40.19, 63.18) * mm, "end": v(-40.2, 63.14) * mm});
            skLineSegment(sketch, "E2557", {"start": v(-40.2, 63.14) * mm, "end": v(-40.2, 63.15) * mm});
            skLineSegment(sketch, "E2558", {"start": v(-40.2, 63.15) * mm, "end": v(-40.24, 63.26) * mm});
            skLineSegment(sketch, "E2559", {"start": v(-40.24, 63.26) * mm, "end": v(-40.32, 63.49) * mm});
            skLineSegment(sketch, "E2560", {"start": v(-40.32, 63.49) * mm, "end": v(-40.5, 63.92) * mm});
            skLineSegment(sketch, "E2561", {"start": v(-40.5, 63.92) * mm, "end": v(-40.7, 64.35) * mm});
            skLineSegment(sketch, "E2562", {"start": v(-40.7, 64.35) * mm, "end": v(-40.92, 64.76) * mm});
            skLineSegment(sketch, "E2563", {"start": v(-40.92, 64.76) * mm, "end": v(-41.18, 65.16) * mm});
            skLineSegment(sketch, "E2564", {"start": v(-41.18, 65.16) * mm, "end": v(-41.46, 65.54) * mm});
            skLineSegment(sketch, "E2565", {"start": v(-41.46, 65.54) * mm, "end": v(-41.76, 65.9) * mm});
            skLineSegment(sketch, "E2566", {"start": v(-41.76, 65.9) * mm, "end": v(-42.1, 66.25) * mm});
            skLineSegment(sketch, "E2567", {"start": v(-42.1, 66.25) * mm, "end": v(-42.45, 66.58) * mm});
            skLineSegment(sketch, "E2568", {"start": v(-42.45, 66.58) * mm, "end": v(-42.83, 66.88) * mm});
            skLineSegment(sketch, "E2569", {"start": v(-42.83, 66.88) * mm, "end": v(-43.23, 67.16) * mm});
            skLineSegment(sketch, "E2570", {"start": v(-43.23, 67.16) * mm, "end": v(-43.66, 67.42) * mm});
            skLineSegment(sketch, "E2571", {"start": v(-43.66, 67.42) * mm, "end": v(-44.1, 67.65) * mm});
            skLineSegment(sketch, "E2572", {"start": v(-54.23, 43.92) * mm, "end": v(-50.07, 42.18) * mm});
            skLineSegment(sketch, "E2573", {"start": v(-50.07, 42.18) * mm, "end": v(-47.98, 41.31) * mm});
            skLineSegment(sketch, "E2574", {"start": v(-47.98, 41.31) * mm, "end": v(-47.72, 41.2) * mm});
            skLineSegment(sketch, "E2575", {"start": v(-47.72, 41.2) * mm, "end": v(-47.6, 41.15) * mm});
            skLineSegment(sketch, "E2576", {"start": v(-47.6, 41.15) * mm, "end": v(-47.57, 41.14) * mm});
            skLineSegment(sketch, "E2577", {"start": v(-47.57, 41.14) * mm, "end": v(-47.6, 41.17) * mm});
            skLineSegment(sketch, "E2578", {"start": v(-47.6, 41.17) * mm, "end": v(-47.65, 41.22) * mm});
            skLineSegment(sketch, "E2579", {"start": v(-47.65, 41.22) * mm, "end": v(-48.06, 41.6) * mm});
            skLineSegment(sketch, "E2580", {"start": v(-48.06, 41.6) * mm, "end": v(-48.88, 42.37) * mm});
            skLineSegment(sketch, "E2581", {"start": v(-48.88, 42.37) * mm, "end": v(-52.16, 45.44) * mm});
            skLineSegment(sketch, "E2582", {"start": v(-52.16, 45.44) * mm, "end": v(-52.57, 45.83) * mm});
            skLineSegment(sketch, "E2583", {"start": v(-52.57, 45.83) * mm, "end": v(-52.78, 46.02) * mm});
            skLineSegment(sketch, "E2584", {"start": v(-52.78, 46.02) * mm, "end": v(-52.82, 46.06) * mm});
            skLineSegment(sketch, "E2585", {"start": v(-52.82, 46.06) * mm, "end": v(-52.81, 46.06) * mm});
            skLineSegment(sketch, "E2586", {"start": v(-52.81, 46.06) * mm, "end": v(-52.8, 46.06) * mm});
            skLineSegment(sketch, "E2587", {"start": v(-52.8, 46.06) * mm, "end": v(-52.76, 46.06) * mm});
            skLineSegment(sketch, "E2588", {"start": v(-52.76, 46.06) * mm, "end": v(-52.69, 46.05) * mm});
            skLineSegment(sketch, "E2589", {"start": v(-52.69, 46.05) * mm, "end": v(-52.59, 46.03) * mm});
            skLineSegment(sketch, "E2590", {"start": v(-52.59, 46.03) * mm, "end": v(-52.47, 46) * mm});
            skLineSegment(sketch, "E2591", {"start": v(-52.47, 46) * mm, "end": v(-52.18, 45.95) * mm});
            skLineSegment(sketch, "E2592", {"start": v(-52.18, 45.95) * mm, "end": v(-51.8, 45.86) * mm});
            skLineSegment(sketch, "E2593", {"start": v(-51.8, 45.86) * mm, "end": v(-51.39, 45.76) * mm});
            skLineSegment(sketch, "E2594", {"start": v(-51.39, 45.76) * mm, "end": v(-50.92, 45.64) * mm});
            skLineSegment(sketch, "E2595", {"start": v(-50.92, 45.64) * mm, "end": v(-48.94, 45.12) * mm});
            skLineSegment(sketch, "E2596", {"start": v(-48.94, 45.12) * mm, "end": v(-48.48, 45) * mm});
            skLineSegment(sketch, "E2597", {"start": v(-48.48, 45) * mm, "end": v(-48.06, 44.88) * mm});
            skLineSegment(sketch, "E2598", {"start": v(-48.06, 44.88) * mm, "end": v(-47.96, 44.85) * mm});
            skLineSegment(sketch, "E2599", {"start": v(-47.96, 44.85) * mm, "end": v(-47.92, 44.83) * mm});
            skLineSegment(sketch, "E2600", {"start": v(-47.92, 44.83) * mm, "end": v(-47.91, 44.84) * mm});
            skLineSegment(sketch, "E2601", {"start": v(-47.91, 44.84) * mm, "end": v(-47.93, 44.85) * mm});
            skLineSegment(sketch, "E2602", {"start": v(-47.93, 44.85) * mm, "end": v(-48.03, 44.95) * mm});
            skLineSegment(sketch, "E2603", {"start": v(-48.03, 44.95) * mm, "end": v(-48.23, 45.14) * mm});
            skLineSegment(sketch, "E2604", {"start": v(-48.23, 45.14) * mm, "end": v(-49.84, 46.66) * mm});
            skLineSegment(sketch, "E2605", {"start": v(-49.84, 46.66) * mm, "end": v(-50.24, 47.04) * mm});
            skLineSegment(sketch, "E2606", {"start": v(-50.24, 47.04) * mm, "end": v(-50.44, 47.23) * mm});
            skLineSegment(sketch, "E2607", {"start": v(-50.44, 47.23) * mm, "end": v(-50.47, 47.25) * mm});
            skLineSegment(sketch, "E2608", {"start": v(-50.47, 47.25) * mm, "end": v(-50.48, 47.26) * mm});
            skLineSegment(sketch, "E2609", {"start": v(-50.48, 47.26) * mm, "end": v(-50.46, 47.27) * mm});
            skLineSegment(sketch, "E2610", {"start": v(-50.46, 47.27) * mm, "end": v(-50.35, 47.3) * mm});
            skLineSegment(sketch, "E2611", {"start": v(-50.35, 47.3) * mm, "end": v(-50.11, 47.34) * mm});
            skLineSegment(sketch, "E2612", {"start": v(-50.11, 47.34) * mm, "end": v(-49.63, 47.4) * mm});
            skLineSegment(sketch, "E2613", {"start": v(-49.63, 47.4) * mm, "end": v(-49.15, 47.43) * mm});
            skLineSegment(sketch, "E2614", {"start": v(-49.15, 47.43) * mm, "end": v(-48.66, 47.42) * mm});
            skLineSegment(sketch, "E2615", {"start": v(-48.66, 47.42) * mm, "end": v(-48.16, 47.37) * mm});
            skLineSegment(sketch, "E2616", {"start": v(-48.16, 47.37) * mm, "end": v(-47.66, 47.29) * mm});
            skLineSegment(sketch, "E2617", {"start": v(-47.66, 47.29) * mm, "end": v(-47.16, 47.17) * mm});
            skLineSegment(sketch, "E2618", {"start": v(-47.16, 47.17) * mm, "end": v(-46.67, 47) * mm});
            skLineSegment(sketch, "E2619", {"start": v(-46.67, 47) * mm, "end": v(-46.18, 46.81) * mm});
            skLineSegment(sketch, "E2620", {"start": v(-46.18, 46.81) * mm, "end": v(-45.7, 46.58) * mm});
            skLineSegment(sketch, "E2621", {"start": v(-45.7, 46.58) * mm, "end": v(-45.22, 46.31) * mm});
            skLineSegment(sketch, "E2622", {"start": v(-45.22, 46.31) * mm, "end": v(-44.76, 46) * mm});
            skLineSegment(sketch, "E2623", {"start": v(-44.76, 46) * mm, "end": v(-44.31, 45.67) * mm});
            skLineSegment(sketch, "E2624", {"start": v(-44.31, 45.67) * mm, "end": v(-43.98, 45.38) * mm});
            skLineSegment(sketch, "E2625", {"start": v(-43.98, 45.38) * mm, "end": v(-43.66, 45.07) * mm});
            skLineSegment(sketch, "E2626", {"start": v(-43.66, 45.07) * mm, "end": v(-43.37, 44.76) * mm});
            skLineSegment(sketch, "E2627", {"start": v(-43.37, 44.76) * mm, "end": v(-43.1, 44.43) * mm});
            skLineSegment(sketch, "E2628", {"start": v(-43.1, 44.43) * mm, "end": v(-42.85, 44.1) * mm});
            skLineSegment(sketch, "E2629", {"start": v(-42.85, 44.1) * mm, "end": v(-42.62, 43.75) * mm});
            skLineSegment(sketch, "E2630", {"start": v(-42.62, 43.75) * mm, "end": v(-42.41, 43.4) * mm});
            skLineSegment(sketch, "E2631", {"start": v(-42.41, 43.4) * mm, "end": v(-42.23, 43.04) * mm});
            skLineSegment(sketch, "E2632", {"start": v(-42.23, 43.04) * mm, "end": v(-42.06, 42.67) * mm});
            skLineSegment(sketch, "E2633", {"start": v(-42.06, 42.67) * mm, "end": v(-41.92, 42.3) * mm});
            skLineSegment(sketch, "E2634", {"start": v(-41.92, 42.3) * mm, "end": v(-41.8, 41.93) * mm});
            skLineSegment(sketch, "E2635", {"start": v(-41.8, 41.93) * mm, "end": v(-41.7, 41.55) * mm});
            skLineSegment(sketch, "E2636", {"start": v(-41.7, 41.55) * mm, "end": v(-41.63, 41.17) * mm});
            skLineSegment(sketch, "E2637", {"start": v(-41.63, 41.17) * mm, "end": v(-41.58, 40.8) * mm});
            skLineSegment(sketch, "E2638", {"start": v(-41.58, 40.8) * mm, "end": v(-41.55, 40.42) * mm});
            skLineSegment(sketch, "E2639", {"start": v(-41.55, 40.42) * mm, "end": v(-41.55, 40.05) * mm});
            skLineSegment(sketch, "E2640", {"start": v(-41.55, 40.05) * mm, "end": v(-41.56, 39.68) * mm});
            skLineSegment(sketch, "E2641", {"start": v(-41.56, 39.68) * mm, "end": v(-41.6, 39.3) * mm});
            skLineSegment(sketch, "E2642", {"start": v(-41.6, 39.3) * mm, "end": v(-41.67, 38.95) * mm});
            skLineSegment(sketch, "E2643", {"start": v(-41.67, 38.95) * mm, "end": v(-41.76, 38.6) * mm});
            skLineSegment(sketch, "E2644", {"start": v(-41.76, 38.6) * mm, "end": v(-41.88, 38.24) * mm});
            skLineSegment(sketch, "E2645", {"start": v(-41.88, 38.24) * mm, "end": v(-42.01, 37.9) * mm});
            skLineSegment(sketch, "E2646", {"start": v(-42.01, 37.9) * mm, "end": v(-42.18, 37.58) * mm});
            skLineSegment(sketch, "E2647", {"start": v(-42.18, 37.58) * mm, "end": v(-42.37, 37.26) * mm});
            skLineSegment(sketch, "E2648", {"start": v(-42.37, 37.26) * mm, "end": v(-42.58, 36.95) * mm});
            skLineSegment(sketch, "E2649", {"start": v(-42.58, 36.95) * mm, "end": v(-42.82, 36.66) * mm});
            skLineSegment(sketch, "E2650", {"start": v(-42.82, 36.66) * mm, "end": v(-43.07, 36.39) * mm});
            skLineSegment(sketch, "E2651", {"start": v(-43.07, 36.39) * mm, "end": v(-43.35, 36.14) * mm});
            skLineSegment(sketch, "E2652", {"start": v(-43.35, 36.14) * mm, "end": v(-43.63, 35.9) * mm});
            skLineSegment(sketch, "E2653", {"start": v(-43.63, 35.9) * mm, "end": v(-43.94, 35.7) * mm});
            skLineSegment(sketch, "E2654", {"start": v(-43.94, 35.7) * mm, "end": v(-44.25, 35.52) * mm});
            skLineSegment(sketch, "E2655", {"start": v(-44.25, 35.52) * mm, "end": v(-44.58, 35.36) * mm});
            skLineSegment(sketch, "E2656", {"start": v(-44.58, 35.36) * mm, "end": v(-44.92, 35.22) * mm});
            skLineSegment(sketch, "E2657", {"start": v(-44.92, 35.22) * mm, "end": v(-45.27, 35.1) * mm});
            skLineSegment(sketch, "E2658", {"start": v(-45.27, 35.1) * mm, "end": v(-45.63, 35) * mm});
            skLineSegment(sketch, "E2659", {"start": v(-45.63, 35) * mm, "end": v(-46, 34.94) * mm});
            skLineSegment(sketch, "E2660", {"start": v(-46, 34.94) * mm, "end": v(-46.37, 34.89) * mm});
            skLineSegment(sketch, "E2661", {"start": v(-46.37, 34.89) * mm, "end": v(-46.75, 34.86) * mm});
            skLineSegment(sketch, "E2662", {"start": v(-46.75, 34.86) * mm, "end": v(-47.13, 34.86) * mm});
            skLineSegment(sketch, "E2663", {"start": v(-47.13, 34.86) * mm, "end": v(-47.52, 34.88) * mm});
            skLineSegment(sketch, "E2664", {"start": v(-47.52, 34.88) * mm, "end": v(-47.91, 34.92) * mm});
            skLineSegment(sketch, "E2665", {"start": v(-47.91, 34.92) * mm, "end": v(-48.3, 34.98) * mm});
            skLineSegment(sketch, "E2666", {"start": v(-48.3, 34.98) * mm, "end": v(-48.7, 35.07) * mm});
            skLineSegment(sketch, "E2667", {"start": v(-48.7, 35.07) * mm, "end": v(-49.08, 35.18) * mm});
            skLineSegment(sketch, "E2668", {"start": v(-49.08, 35.18) * mm, "end": v(-49.47, 35.3) * mm});
            skLineSegment(sketch, "E2669", {"start": v(-49.47, 35.3) * mm, "end": v(-49.85, 35.46) * mm});
            skLineSegment(sketch, "E2670", {"start": v(-49.85, 35.46) * mm, "end": v(-50.23, 35.64) * mm});
            skLineSegment(sketch, "E2671", {"start": v(-50.23, 35.64) * mm, "end": v(-50.6, 35.84) * mm});
            skLineSegment(sketch, "E2672", {"start": v(-50.6, 35.84) * mm, "end": v(-50.97, 36.06) * mm});
            skLineSegment(sketch, "E2673", {"start": v(-50.97, 36.06) * mm, "end": v(-51.33, 36.3) * mm});
            skLineSegment(sketch, "E2674", {"start": v(-51.33, 36.3) * mm, "end": v(-51.68, 36.57) * mm});
            skLineSegment(sketch, "E2675", {"start": v(-51.68, 36.57) * mm, "end": v(-51.76, 36.63) * mm});
            skLineSegment(sketch, "E2676", {"start": v(-51.76, 36.63) * mm, "end": v(-51.8, 36.67) * mm});
            skLineSegment(sketch, "E2677", {"start": v(-51.8, 36.67) * mm, "end": v(-51.9, 36.75) * mm});
            skLineSegment(sketch, "E2678", {"start": v(-51.9, 36.75) * mm, "end": v(-52.24, 37.06) * mm});
            skLineSegment(sketch, "E2679", {"start": v(-52.24, 37.06) * mm, "end": v(-52.55, 37.39) * mm});
            skLineSegment(sketch, "E2680", {"start": v(-52.55, 37.39) * mm, "end": v(-52.85, 37.73) * mm});
            skLineSegment(sketch, "E2681", {"start": v(-52.85, 37.73) * mm, "end": v(-53.12, 38.08) * mm});
            skLineSegment(sketch, "E2682", {"start": v(-53.12, 38.08) * mm, "end": v(-53.37, 38.44) * mm});
            skLineSegment(sketch, "E2683", {"start": v(-53.37, 38.44) * mm, "end": v(-53.6, 38.8) * mm});
            skLineSegment(sketch, "E2684", {"start": v(-53.6, 38.8) * mm, "end": v(-53.8, 39.19) * mm});
            skLineSegment(sketch, "E2685", {"start": v(-53.8, 39.19) * mm, "end": v(-53.97, 39.57) * mm});
            skLineSegment(sketch, "E2686", {"start": v(-53.97, 39.57) * mm, "end": v(-54.12, 39.96) * mm});
            skLineSegment(sketch, "E2687", {"start": v(-54.12, 39.96) * mm, "end": v(-54.25, 40.35) * mm});
            skLineSegment(sketch, "E2688", {"start": v(-54.25, 40.35) * mm, "end": v(-54.35, 40.75) * mm});
            skLineSegment(sketch, "E2689", {"start": v(-54.35, 40.75) * mm, "end": v(-54.43, 41.15) * mm});
            skLineSegment(sketch, "E2690", {"start": v(-54.43, 41.15) * mm, "end": v(-54.44, 41.25) * mm});
            skLineSegment(sketch, "E2691", {"start": v(-54.44, 41.25) * mm, "end": v(-54.45, 41.3) * mm});
            skLineSegment(sketch, "E2692", {"start": v(-54.45, 41.3) * mm, "end": v(-54.44, 41.3) * mm});
            skLineSegment(sketch, "E2693", {"start": v(-54.44, 41.3) * mm, "end": v(-54.42, 41.29) * mm});
            skLineSegment(sketch, "E2694", {"start": v(-54.42, 41.29) * mm, "end": v(-54.27, 41.2) * mm});
            skLineSegment(sketch, "E2695", {"start": v(-54.27, 41.2) * mm, "end": v(-53.95, 41.01) * mm});
            skLineSegment(sketch, "E2696", {"start": v(-53.95, 41.01) * mm, "end": v(-51.46, 39.54) * mm});
            skLineSegment(sketch, "E2697", {"start": v(-51.46, 39.54) * mm, "end": v(-50.84, 39.17) * mm});
            skLineSegment(sketch, "E2698", {"start": v(-50.84, 39.17) * mm, "end": v(-50.53, 38.99) * mm});
            skLineSegment(sketch, "E2699", {"start": v(-50.53, 38.99) * mm, "end": v(-50.49, 38.96) * mm});
            skLineSegment(sketch, "E2700", {"start": v(-50.49, 38.96) * mm, "end": v(-50.47, 38.95) * mm});
            skLineSegment(sketch, "E2701", {"start": v(-50.47, 38.95) * mm, "end": v(-50.48, 38.97) * mm});
            skLineSegment(sketch, "E2702", {"start": v(-50.48, 38.97) * mm, "end": v(-50.55, 39.07) * mm});
            skLineSegment(sketch, "E2703", {"start": v(-50.55, 39.07) * mm, "end": v(-50.71, 39.27) * mm});
            skLineSegment(sketch, "E2704", {"start": v(-50.71, 39.27) * mm, "end": v(-51.06, 39.72) * mm});
            skLineSegment(sketch, "E2705", {"start": v(-51.06, 39.72) * mm, "end": v(-51.43, 40.2) * mm});
            skLineSegment(sketch, "E2706", {"start": v(-51.43, 40.2) * mm, "end": v(-52.21, 41.23) * mm});
            skLineSegment(sketch, "E2707", {"start": v(-52.21, 41.23) * mm, "end": v(-52.6, 41.74) * mm});
            skLineSegment(sketch, "E2708", {"start": v(-52.6, 41.74) * mm, "end": v(-52.97, 42.22) * mm});
            skLineSegment(sketch, "E2709", {"start": v(-52.97, 42.22) * mm, "end": v(-53.31, 42.68) * mm});
            skLineSegment(sketch, "E2710", {"start": v(-53.31, 42.68) * mm, "end": v(-53.61, 43.08) * mm});
            skLineSegment(sketch, "E2711", {"start": v(-53.61, 43.08) * mm, "end": v(-53.75, 43.26) * mm});
            skLineSegment(sketch, "E2712", {"start": v(-53.75, 43.26) * mm, "end": v(-53.87, 43.42) * mm});
            skLineSegment(sketch, "E2713", {"start": v(-53.87, 43.42) * mm, "end": v(-53.97, 43.56) * mm});
            skLineSegment(sketch, "E2714", {"start": v(-53.97, 43.56) * mm, "end": v(-54.06, 43.68) * mm});
            skLineSegment(sketch, "E2715", {"start": v(-54.06, 43.68) * mm, "end": v(-54.13, 43.78) * mm});
            skLineSegment(sketch, "E2716", {"start": v(-54.13, 43.78) * mm, "end": v(-54.19, 43.86) * mm});
            skLineSegment(sketch, "E2717", {"start": v(-54.19, 43.86) * mm, "end": v(-54.22, 43.9) * mm});
            skLineSegment(sketch, "E2718", {"start": v(-54.22, 43.9) * mm, "end": v(-54.23, 43.92) * mm});
            skLineSegment(sketch, "E2719", {"start": v(-55.9, 54.53) * mm, "end": v(-55.91, 55) * mm});
            skLineSegment(sketch, "E2720", {"start": v(-55.91, 55) * mm, "end": v(-55.88, 55.49) * mm});
            skLineSegment(sketch, "E2721", {"start": v(-55.88, 55.49) * mm, "end": v(-55.8, 55.97) * mm});
            skLineSegment(sketch, "E2722", {"start": v(-55.8, 55.97) * mm, "end": v(-55.7, 56.45) * mm});
            skLineSegment(sketch, "E2723", {"start": v(-55.7, 56.45) * mm, "end": v(-55.55, 56.93) * mm});
            skLineSegment(sketch, "E2724", {"start": v(-55.55, 56.93) * mm, "end": v(-55.37, 57.4) * mm});
            skLineSegment(sketch, "E2725", {"start": v(-55.37, 57.4) * mm, "end": v(-55.16, 57.87) * mm});
            skLineSegment(sketch, "E2726", {"start": v(-55.16, 57.87) * mm, "end": v(-54.9, 58.33) * mm});
            skLineSegment(sketch, "E2727", {"start": v(-54.9, 58.33) * mm, "end": v(-54.61, 58.77) * mm});
            skLineSegment(sketch, "E2728", {"start": v(-54.61, 58.77) * mm, "end": v(-54.3, 59.2) * mm});
            skLineSegment(sketch, "E2729", {"start": v(-54.3, 59.2) * mm, "end": v(-53.93, 59.61) * mm});
            skLineSegment(sketch, "E2730", {"start": v(-53.93, 59.61) * mm, "end": v(-53.54, 60) * mm});
            skLineSegment(sketch, "E2731", {"start": v(-53.54, 60) * mm, "end": v(-53.33, 60.2) * mm});
            skLineSegment(sketch, "E2732", {"start": v(-53.33, 60.2) * mm, "end": v(-53.22, 60.29) * mm});
            skLineSegment(sketch, "E2733", {"start": v(-53.22, 60.29) * mm, "end": v(-53.15, 60.35) * mm});
            skLineSegment(sketch, "E2734", {"start": v(-53.15, 60.35) * mm, "end": v(-53.06, 60.42) * mm});
            skLineSegment(sketch, "E2735", {"start": v(-53.06, 60.42) * mm, "end": v(-52.71, 60.68) * mm});
            skLineSegment(sketch, "E2736", {"start": v(-52.71, 60.68) * mm, "end": v(-52.36, 60.93) * mm});
            skLineSegment(sketch, "E2737", {"start": v(-52.36, 60.93) * mm, "end": v(-51.99, 61.15) * mm});
            skLineSegment(sketch, "E2738", {"start": v(-51.99, 61.15) * mm, "end": v(-51.62, 61.34) * mm});
            skLineSegment(sketch, "E2739", {"start": v(-51.62, 61.34) * mm, "end": v(-51.24, 61.52) * mm});
            skLineSegment(sketch, "E2740", {"start": v(-51.24, 61.52) * mm, "end": v(-50.85, 61.67) * mm});
            skLineSegment(sketch, "E2741", {"start": v(-50.85, 61.67) * mm, "end": v(-50.47, 61.8) * mm});
            skLineSegment(sketch, "E2742", {"start": v(-50.47, 61.8) * mm, "end": v(-50.08, 61.9) * mm});
            skLineSegment(sketch, "E2743", {"start": v(-50.08, 61.9) * mm, "end": v(-49.69, 62) * mm});
            skLineSegment(sketch, "E2744", {"start": v(-49.69, 62) * mm, "end": v(-49.3, 62.06) * mm});
            skLineSegment(sketch, "E2745", {"start": v(-49.3, 62.06) * mm, "end": v(-48.91, 62.1) * mm});
            skLineSegment(sketch, "E2746", {"start": v(-48.91, 62.1) * mm, "end": v(-48.52, 62.11) * mm});
            skLineSegment(sketch, "E2747", {"start": v(-48.52, 62.11) * mm, "end": v(-48.14, 62.1) * mm});
            skLineSegment(sketch, "E2748", {"start": v(-48.14, 62.1) * mm, "end": v(-47.76, 62.08) * mm});
            skLineSegment(sketch, "E2749", {"start": v(-47.76, 62.08) * mm, "end": v(-47.4, 62.03) * mm});
            skLineSegment(sketch, "E2750", {"start": v(-47.4, 62.03) * mm, "end": v(-47.03, 61.96) * mm});
            skLineSegment(sketch, "E2751", {"start": v(-47.03, 61.96) * mm, "end": v(-46.67, 61.86) * mm});
            skLineSegment(sketch, "E2752", {"start": v(-46.67, 61.86) * mm, "end": v(-46.32, 61.75) * mm});
            skLineSegment(sketch, "E2753", {"start": v(-46.32, 61.75) * mm, "end": v(-45.98, 61.6) * mm});
            skLineSegment(sketch, "E2754", {"start": v(-45.98, 61.6) * mm, "end": v(-45.65, 61.44) * mm});
            skLineSegment(sketch, "E2755", {"start": v(-45.65, 61.44) * mm, "end": v(-45.34, 61.26) * mm});
            skLineSegment(sketch, "E2756", {"start": v(-45.34, 61.26) * mm, "end": v(-45.03, 61.05) * mm});
            skLineSegment(sketch, "E2757", {"start": v(-45.03, 61.05) * mm, "end": v(-44.75, 60.82) * mm});
            skLineSegment(sketch, "E2758", {"start": v(-44.75, 60.82) * mm, "end": v(-44.47, 60.57) * mm});
            skLineSegment(sketch, "E2759", {"start": v(-44.47, 60.57) * mm, "end": v(-44.22, 60.3) * mm});
            skLineSegment(sketch, "E2760", {"start": v(-44.22, 60.3) * mm, "end": v(-43.98, 60) * mm});
            skLineSegment(sketch, "E2761", {"start": v(-43.98, 60) * mm, "end": v(-43.77, 59.7) * mm});
            skLineSegment(sketch, "E2762", {"start": v(-43.77, 59.7) * mm, "end": v(-43.59, 59.37) * mm});
            skLineSegment(sketch, "E2763", {"start": v(-43.59, 59.37) * mm, "end": v(-43.42, 59.04) * mm});
            skLineSegment(sketch, "E2764", {"start": v(-43.42, 59.04) * mm, "end": v(-43.29, 58.7) * mm});
            skLineSegment(sketch, "E2765", {"start": v(-43.29, 58.7) * mm, "end": v(-43.18, 58.35) * mm});
            skLineSegment(sketch, "E2766", {"start": v(-43.18, 58.35) * mm, "end": v(-43.09, 58) * mm});
            skLineSegment(sketch, "E2767", {"start": v(-43.09, 58) * mm, "end": v(-43.02, 57.64) * mm});
            skLineSegment(sketch, "E2768", {"start": v(-43.02, 57.64) * mm, "end": v(-42.98, 57.27) * mm});
            skLineSegment(sketch, "E2769", {"start": v(-42.98, 57.27) * mm, "end": v(-42.97, 56.9) * mm});
            skLineSegment(sketch, "E2770", {"start": v(-42.97, 56.9) * mm, "end": v(-42.97, 56.52) * mm});
            skLineSegment(sketch, "E2771", {"start": v(-42.97, 56.52) * mm, "end": v(-43, 56.15) * mm});
            skLineSegment(sketch, "E2772", {"start": v(-43, 56.15) * mm, "end": v(-43.06, 55.77) * mm});
            skLineSegment(sketch, "E2773", {"start": v(-43.06, 55.77) * mm, "end": v(-43.13, 55.4) * mm});
            skLineSegment(sketch, "E2774", {"start": v(-43.13, 55.4) * mm, "end": v(-43.23, 55.02) * mm});
            skLineSegment(sketch, "E2775", {"start": v(-43.23, 55.02) * mm, "end": v(-43.35, 54.64) * mm});
            skLineSegment(sketch, "E2776", {"start": v(-43.35, 54.64) * mm, "end": v(-43.5, 54.27) * mm});
            skLineSegment(sketch, "E2777", {"start": v(-43.5, 54.27) * mm, "end": v(-43.66, 53.9) * mm});
            skLineSegment(sketch, "E2778", {"start": v(-43.66, 53.9) * mm, "end": v(-43.85, 53.55) * mm});
            skLineSegment(sketch, "E2779", {"start": v(-43.85, 53.55) * mm, "end": v(-44.06, 53.2) * mm});
            skLineSegment(sketch, "E2780", {"start": v(-44.06, 53.2) * mm, "end": v(-44.29, 52.85) * mm});
            skLineSegment(sketch, "E2781", {"start": v(-44.29, 52.85) * mm, "end": v(-44.54, 52.5) * mm});
            skLineSegment(sketch, "E2782", {"start": v(-44.54, 52.5) * mm, "end": v(-44.81, 52.18) * mm});
            skLineSegment(sketch, "E2783", {"start": v(-44.81, 52.18) * mm, "end": v(-45.1, 51.87) * mm});
            skLineSegment(sketch, "E2784", {"start": v(-45.1, 51.87) * mm, "end": v(-45.42, 51.56) * mm});
            skLineSegment(sketch, "E2785", {"start": v(-45.42, 51.56) * mm, "end": v(-45.58, 51.42) * mm});
            skLineSegment(sketch, "E2786", {"start": v(-45.58, 51.42) * mm, "end": v(-45.67, 51.34) * mm});
            skLineSegment(sketch, "E2787", {"start": v(-45.67, 51.34) * mm, "end": v(-45.72, 51.3) * mm});
            skLineSegment(sketch, "E2788", {"start": v(-45.72, 51.3) * mm, "end": v(-45.9, 51.15) * mm});
            skLineSegment(sketch, "E2789", {"start": v(-45.9, 51.15) * mm, "end": v(-46.28, 50.88) * mm});
            skLineSegment(sketch, "E2790", {"start": v(-46.28, 50.88) * mm, "end": v(-46.66, 50.63) * mm});
            skLineSegment(sketch, "E2791", {"start": v(-46.66, 50.63) * mm, "end": v(-47.05, 50.4) * mm});
            skLineSegment(sketch, "E2792", {"start": v(-47.05, 50.4) * mm, "end": v(-47.44, 50.21) * mm});
            skLineSegment(sketch, "E2793", {"start": v(-47.44, 50.21) * mm, "end": v(-47.84, 50.04) * mm});
            skLineSegment(sketch, "E2794", {"start": v(-47.84, 50.04) * mm, "end": v(-48.25, 49.9) * mm});
            skLineSegment(sketch, "E2795", {"start": v(-48.25, 49.9) * mm, "end": v(-48.66, 49.77) * mm});
            skLineSegment(sketch, "E2796", {"start": v(-48.66, 49.77) * mm, "end": v(-49.07, 49.67) * mm});
            skLineSegment(sketch, "E2797", {"start": v(-49.07, 49.67) * mm, "end": v(-49.48, 49.6) * mm});
            skLineSegment(sketch, "E2798", {"start": v(-49.48, 49.6) * mm, "end": v(-49.9, 49.55) * mm});
            skLineSegment(sketch, "E2799", {"start": v(-49.9, 49.55) * mm, "end": v(-50.3, 49.53) * mm});
            skLineSegment(sketch, "E2800", {"start": v(-50.3, 49.53) * mm, "end": v(-50.7, 49.53) * mm});
            skLineSegment(sketch, "E2801", {"start": v(-50.7, 49.53) * mm, "end": v(-50.75, 49.53) * mm});
            skLineSegment(sketch, "E2802", {"start": v(-50.75, 49.53) * mm, "end": v(-50.78, 49.53) * mm});
            skLineSegment(sketch, "E2803", {"start": v(-50.78, 49.53) * mm, "end": v(-50.77, 49.55) * mm});
            skLineSegment(sketch, "E2804", {"start": v(-50.77, 49.55) * mm, "end": v(-50.71, 49.62) * mm});
            skLineSegment(sketch, "E2805", {"start": v(-50.71, 49.62) * mm, "end": v(-50.6, 49.75) * mm});
            skLineSegment(sketch, "E2806", {"start": v(-50.6, 49.75) * mm, "end": v(-49.64, 50.84) * mm});
            skLineSegment(sketch, "E2807", {"start": v(-49.64, 50.84) * mm, "end": v(-47.73, 53.02) * mm});
            skLineSegment(sketch, "E2808", {"start": v(-47.73, 53.02) * mm, "end": v(-48.2, 52.79) * mm});
            skLineSegment(sketch, "E2809", {"start": v(-48.2, 52.79) * mm, "end": v(-48.7, 52.52) * mm});
            skLineSegment(sketch, "E2810", {"start": v(-48.7, 52.52) * mm, "end": v(-49.26, 52.24) * mm});
            skLineSegment(sketch, "E2811", {"start": v(-49.26, 52.24) * mm, "end": v(-49.83, 51.96) * mm});
            skLineSegment(sketch, "E2812", {"start": v(-49.83, 51.96) * mm, "end": v(-50.98, 51.38) * mm});
            skLineSegment(sketch, "E2813", {"start": v(-50.98, 51.38) * mm, "end": v(-51.52, 51.1) * mm});
            skLineSegment(sketch, "E2814", {"start": v(-51.52, 51.1) * mm, "end": v(-52.02, 50.86) * mm});
            skLineSegment(sketch, "E2815", {"start": v(-52.02, 50.86) * mm, "end": v(-52.46, 50.64) * mm});
            skLineSegment(sketch, "E2816", {"start": v(-52.46, 50.64) * mm, "end": v(-52.65, 50.55) * mm});
            skLineSegment(sketch, "E2817", {"start": v(-52.65, 50.55) * mm, "end": v(-52.82, 50.47) * mm});
            skLineSegment(sketch, "E2818", {"start": v(-52.82, 50.47) * mm, "end": v(-52.97, 50.4) * mm});
            skLineSegment(sketch, "E2819", {"start": v(-52.97, 50.4) * mm, "end": v(-53.1, 50.33) * mm});
            skLineSegment(sketch, "E2820", {"start": v(-53.1, 50.33) * mm, "end": v(-53.2, 50.29) * mm});
            skLineSegment(sketch, "E2821", {"start": v(-53.2, 50.29) * mm, "end": v(-53.26, 50.25) * mm});
            skLineSegment(sketch, "E2822", {"start": v(-53.26, 50.25) * mm, "end": v(-53.3, 50.24) * mm});
            skLineSegment(sketch, "E2823", {"start": v(-53.3, 50.24) * mm, "end": v(-53.31, 50.24) * mm});
            skLineSegment(sketch, "E2824", {"start": v(-53.31, 50.24) * mm, "end": v(-53.3, 50.24) * mm});
            skLineSegment(sketch, "E2825", {"start": v(-53.3, 50.24) * mm, "end": v(-53.29, 50.27) * mm});
            skLineSegment(sketch, "E2826", {"start": v(-53.29, 50.27) * mm, "end": v(-53.25, 50.33) * mm});
            skLineSegment(sketch, "E2827", {"start": v(-53.25, 50.33) * mm, "end": v(-52.94, 50.8) * mm});
            skLineSegment(sketch, "E2828", {"start": v(-52.94, 50.8) * mm, "end": v(-52.32, 51.75) * mm});
            skLineSegment(sketch, "E2829", {"start": v(-52.32, 51.75) * mm, "end": v(-49.85, 55.52) * mm});
            skLineSegment(sketch, "E2830", {"start": v(-49.85, 55.52) * mm, "end": v(-49.54, 55.99) * mm});
            skLineSegment(sketch, "E2831", {"start": v(-49.54, 55.99) * mm, "end": v(-49.38, 56.22) * mm});
            skLineSegment(sketch, "E2832", {"start": v(-49.38, 56.22) * mm, "end": v(-49.36, 56.25) * mm});
            skLineSegment(sketch, "E2833", {"start": v(-49.36, 56.25) * mm, "end": v(-49.35, 56.27) * mm});
            skLineSegment(sketch, "E2834", {"start": v(-49.35, 56.27) * mm, "end": v(-49.36, 56.26) * mm});
            skLineSegment(sketch, "E2835", {"start": v(-49.36, 56.26) * mm, "end": v(-49.42, 56.22) * mm});
            skLineSegment(sketch, "E2836", {"start": v(-49.42, 56.22) * mm, "end": v(-49.53, 56.14) * mm});
            skLineSegment(sketch, "E2837", {"start": v(-49.53, 56.14) * mm, "end": v(-50.44, 55.47) * mm});
            skLineSegment(sketch, "E2838", {"start": v(-50.44, 55.47) * mm, "end": v(-52.25, 54.14) * mm});
            skLineSegment(sketch, "E2839", {"start": v(-52.25, 54.14) * mm, "end": v(-54.07, 52.81) * mm});
            skLineSegment(sketch, "E2840", {"start": v(-54.07, 52.81) * mm, "end": v(-54.97, 52.15) * mm});
            skLineSegment(sketch, "E2841", {"start": v(-54.97, 52.15) * mm, "end": v(-55.09, 52.07) * mm});
            skLineSegment(sketch, "E2842", {"start": v(-55.09, 52.07) * mm, "end": v(-55.14, 52.03) * mm});
            skLineSegment(sketch, "E2843", {"start": v(-55.14, 52.03) * mm, "end": v(-55.15, 52.02) * mm});
            skLineSegment(sketch, "E2844", {"start": v(-55.15, 52.02) * mm, "end": v(-55.15, 52.05) * mm});
            skLineSegment(sketch, "E2845", {"start": v(-55.15, 52.05) * mm, "end": v(-55.14, 52.1) * mm});
            skLineSegment(sketch, "E2846", {"start": v(-55.14, 52.1) * mm, "end": v(-55.1, 52.18) * mm});
            skLineSegment(sketch, "E2847", {"start": v(-55.1, 52.18) * mm, "end": v(-55.07, 52.28) * mm});
            skLineSegment(sketch, "E2848", {"start": v(-55.07, 52.28) * mm, "end": v(-55.02, 52.4) * mm});
            skLineSegment(sketch, "E2849", {"start": v(-55.02, 52.4) * mm, "end": v(-54.9, 52.7) * mm});
            skLineSegment(sketch, "E2850", {"start": v(-54.9, 52.7) * mm, "end": v(-54.74, 53.05) * mm});
            skLineSegment(sketch, "E2851", {"start": v(-54.74, 53.05) * mm, "end": v(-54.56, 53.45) * mm});
            skLineSegment(sketch, "E2852", {"start": v(-54.56, 53.45) * mm, "end": v(-54.36, 53.9) * mm});
            skLineSegment(sketch, "E2853", {"start": v(-54.36, 53.9) * mm, "end": v(-54.14, 54.36) * mm});
            skLineSegment(sketch, "E2854", {"start": v(-54.14, 54.36) * mm, "end": v(-53.7, 55.3) * mm});
            skLineSegment(sketch, "E2855", {"start": v(-53.7, 55.3) * mm, "end": v(-53.48, 55.75) * mm});
            skLineSegment(sketch, "E2856", {"start": v(-53.48, 55.75) * mm, "end": v(-53.27, 56.17) * mm});
            skLineSegment(sketch, "E2857", {"start": v(-53.27, 56.17) * mm, "end": v(-53.08, 56.55) * mm});
            skLineSegment(sketch, "E2858", {"start": v(-53.08, 56.55) * mm, "end": v(-53.06, 56.6) * mm});
            skLineSegment(sketch, "E2859", {"start": v(-53.06, 56.6) * mm, "end": v(-53.05, 56.61) * mm});
            skLineSegment(sketch, "E2860", {"start": v(-53.05, 56.61) * mm, "end": v(-53.05, 56.6) * mm});
            skLineSegment(sketch, "E2861", {"start": v(-53.05, 56.6) * mm, "end": v(-53.11, 56.57) * mm});
            skLineSegment(sketch, "E2862", {"start": v(-53.11, 56.57) * mm, "end": v(-53.22, 56.49) * mm});
            skLineSegment(sketch, "E2863", {"start": v(-53.22, 56.49) * mm, "end": v(-54.12, 55.83) * mm});
            skLineSegment(sketch, "E2864", {"start": v(-54.12, 55.83) * mm, "end": v(-55.9, 54.53) * mm});
            skLineSegment(sketch, "E2865", {"start": v(-35.48, 39.24) * mm, "end": v(-35.07, 39.25) * mm});
            skLineSegment(sketch, "E2866", {"start": v(-35.07, 39.25) * mm, "end": v(-34.69, 39.27) * mm});
            skLineSegment(sketch, "E2867", {"start": v(-34.69, 39.27) * mm, "end": v(-33.95, 39.32) * mm});
            skLineSegment(sketch, "E2868", {"start": v(-33.95, 39.32) * mm, "end": v(-33.25, 39.39) * mm});
            skLineSegment(sketch, "E2869", {"start": v(-33.25, 39.39) * mm, "end": v(-32.57, 39.47) * mm});
            skLineSegment(sketch, "E2870", {"start": v(-32.57, 39.47) * mm, "end": v(-31.88, 39.56) * mm});
            skLineSegment(sketch, "E2871", {"start": v(-31.88, 39.56) * mm, "end": v(-31.16, 39.65) * mm});
            skLineSegment(sketch, "E2872", {"start": v(-31.16, 39.65) * mm, "end": v(-30.79, 39.7) * mm});
            skLineSegment(sketch, "E2873", {"start": v(-30.79, 39.7) * mm, "end": v(-30.4, 39.74) * mm});
            skLineSegment(sketch, "E2874", {"start": v(-30.4, 39.74) * mm, "end": v(-30, 39.8) * mm});
            skLineSegment(sketch, "E2875", {"start": v(-30, 39.8) * mm, "end": v(-29.58, 39.84) * mm});
            skLineSegment(sketch, "E2876", {"start": v(-29.58, 39.84) * mm, "end": v(-29.8, 39.92) * mm});
            skLineSegment(sketch, "E2877", {"start": v(-29.8, 39.92) * mm, "end": v(-30.02, 40) * mm});
            skLineSegment(sketch, "E2878", {"start": v(-30.02, 40) * mm, "end": v(-30.4, 40.17) * mm});
            skLineSegment(sketch, "E2879", {"start": v(-30.4, 40.17) * mm, "end": v(-30.74, 40.32) * mm});
            skLineSegment(sketch, "E2880", {"start": v(-30.74, 40.32) * mm, "end": v(-31.05, 40.47) * mm});
            skLineSegment(sketch, "E2881", {"start": v(-31.05, 40.47) * mm, "end": v(-31.32, 40.6) * mm});
            skLineSegment(sketch, "E2882", {"start": v(-31.32, 40.6) * mm, "end": v(-31.58, 40.74) * mm});
            skLineSegment(sketch, "E2883", {"start": v(-31.58, 40.74) * mm, "end": v(-32.04, 41) * mm});
            skLineSegment(sketch, "E2884", {"start": v(-32.04, 41) * mm, "end": v(-32.5, 41.27) * mm});
            skLineSegment(sketch, "E2885", {"start": v(-32.5, 41.27) * mm, "end": v(-32.76, 41.4) * mm});
            skLineSegment(sketch, "E2886", {"start": v(-32.76, 41.4) * mm, "end": v(-33.02, 41.52) * mm});
            skLineSegment(sketch, "E2887", {"start": v(-33.02, 41.52) * mm, "end": v(-33.32, 41.65) * mm});
            skLineSegment(sketch, "E2888", {"start": v(-33.32, 41.65) * mm, "end": v(-33.65, 41.79) * mm});
            skLineSegment(sketch, "E2889", {"start": v(-33.65, 41.79) * mm, "end": v(-34.02, 41.93) * mm});
            skLineSegment(sketch, "E2890", {"start": v(-34.02, 41.93) * mm, "end": v(-34.44, 42.07) * mm});
            skLineSegment(sketch, "E2891", {"start": v(-34.44, 42.07) * mm, "end": v(-34, 42.13) * mm});
            skLineSegment(sketch, "E2892", {"start": v(-34, 42.13) * mm, "end": v(-33.6, 42.2) * mm});
            skLineSegment(sketch, "E2893", {"start": v(-33.6, 42.2) * mm, "end": v(-33.24, 42.25) * mm});
            skLineSegment(sketch, "E2894", {"start": v(-33.24, 42.25) * mm, "end": v(-32.9, 42.3) * mm});
            skLineSegment(sketch, "E2895", {"start": v(-32.9, 42.3) * mm, "end": v(-32.6, 42.37) * mm});
            skLineSegment(sketch, "E2896", {"start": v(-32.6, 42.37) * mm, "end": v(-32.32, 42.42) * mm});
            skLineSegment(sketch, "E2897", {"start": v(-32.32, 42.42) * mm, "end": v(-31.79, 42.53) * mm});
            skLineSegment(sketch, "E2898", {"start": v(-31.79, 42.53) * mm, "end": v(-31.26, 42.64) * mm});
            skLineSegment(sketch, "E2899", {"start": v(-31.26, 42.64) * mm, "end": v(-30.97, 42.7) * mm});
            skLineSegment(sketch, "E2900", {"start": v(-30.97, 42.7) * mm, "end": v(-30.67, 42.76) * mm});
            skLineSegment(sketch, "E2901", {"start": v(-30.67, 42.76) * mm, "end": v(-30.34, 42.82) * mm});
            skLineSegment(sketch, "E2902", {"start": v(-30.34, 42.82) * mm, "end": v(-29.98, 42.88) * mm});
            skLineSegment(sketch, "E2903", {"start": v(-29.98, 42.88) * mm, "end": v(-29.59, 42.94) * mm});
            skLineSegment(sketch, "E2904", {"start": v(-29.59, 42.94) * mm, "end": v(-29.14, 43) * mm});
            skLineSegment(sketch, "E2905", {"start": v(-29.14, 43) * mm, "end": v(-29.63, 43.16) * mm});
            skLineSegment(sketch, "E2906", {"start": v(-29.63, 43.16) * mm, "end": v(-30.08, 43.3) * mm});
            skLineSegment(sketch, "E2907", {"start": v(-30.08, 43.3) * mm, "end": v(-30.5, 43.45) * mm});
            skLineSegment(sketch, "E2908", {"start": v(-30.5, 43.45) * mm, "end": v(-30.89, 43.58) * mm});
            skLineSegment(sketch, "E2909", {"start": v(-30.89, 43.58) * mm, "end": v(-31.25, 43.71) * mm});
            skLineSegment(sketch, "E2910", {"start": v(-31.25, 43.71) * mm, "end": v(-31.6, 43.84) * mm});
            skLineSegment(sketch, "E2911", {"start": v(-31.6, 43.84) * mm, "end": v(-32.24, 44.09) * mm});
            skLineSegment(sketch, "E2912", {"start": v(-32.24, 44.09) * mm, "end": v(-32.88, 44.33) * mm});
            skLineSegment(sketch, "E2913", {"start": v(-32.88, 44.33) * mm, "end": v(-33.54, 44.59) * mm});
            skLineSegment(sketch, "E2914", {"start": v(-33.54, 44.59) * mm, "end": v(-33.9, 44.72) * mm});
            skLineSegment(sketch, "E2915", {"start": v(-33.9, 44.72) * mm, "end": v(-34.27, 44.86) * mm});
            skLineSegment(sketch, "E2916", {"start": v(-34.27, 44.86) * mm, "end": v(-34.68, 45) * mm});
            skLineSegment(sketch, "E2917", {"start": v(-34.68, 45) * mm, "end": v(-35.11, 45.16) * mm});
            skLineSegment(sketch, "E2918", {"start": v(-35.11, 45.16) * mm, "end": v(-34.67, 45.22) * mm});
            skLineSegment(sketch, "E2919", {"start": v(-34.67, 45.22) * mm, "end": v(-34.26, 45.28) * mm});
            skLineSegment(sketch, "E2920", {"start": v(-34.26, 45.28) * mm, "end": v(-33.89, 45.34) * mm});
            skLineSegment(sketch, "E2921", {"start": v(-33.89, 45.34) * mm, "end": v(-33.53, 45.4) * mm});
            skLineSegment(sketch, "E2922", {"start": v(-33.53, 45.4) * mm, "end": v(-33.2, 45.45) * mm});
            skLineSegment(sketch, "E2923", {"start": v(-33.2, 45.45) * mm, "end": v(-32.9, 45.5) * mm});
            skLineSegment(sketch, "E2924", {"start": v(-32.9, 45.5) * mm, "end": v(-32.3, 45.6) * mm});
            skLineSegment(sketch, "E2925", {"start": v(-32.3, 45.6) * mm, "end": v(-31.69, 45.7) * mm});
            skLineSegment(sketch, "E2926", {"start": v(-31.69, 45.7) * mm, "end": v(-31.38, 45.75) * mm});
            skLineSegment(sketch, "E2927", {"start": v(-31.38, 45.75) * mm, "end": v(-31.05, 45.8) * mm});
            skLineSegment(sketch, "E2928", {"start": v(-31.05, 45.8) * mm, "end": v(-30.7, 45.86) * mm});
            skLineSegment(sketch, "E2929", {"start": v(-30.7, 45.86) * mm, "end": v(-30.32, 45.9) * mm});
            skLineSegment(sketch, "E2930", {"start": v(-30.32, 45.9) * mm, "end": v(-29.9, 45.96) * mm});
            skLineSegment(sketch, "E2931", {"start": v(-29.9, 45.96) * mm, "end": v(-29.46, 46.02) * mm});
            skLineSegment(sketch, "E2932", {"start": v(-29.46, 46.02) * mm, "end": v(-29.93, 46.15) * mm});
            skLineSegment(sketch, "E2933", {"start": v(-29.93, 46.15) * mm, "end": v(-30.36, 46.28) * mm});
            skLineSegment(sketch, "E2934", {"start": v(-30.36, 46.28) * mm, "end": v(-30.77, 46.41) * mm});
            skLineSegment(sketch, "E2935", {"start": v(-30.77, 46.41) * mm, "end": v(-31.16, 46.54) * mm});
            skLineSegment(sketch, "E2936", {"start": v(-31.16, 46.54) * mm, "end": v(-31.88, 46.8) * mm});
            skLineSegment(sketch, "E2937", {"start": v(-31.88, 46.8) * mm, "end": v(-32.58, 47.05) * mm});
            skLineSegment(sketch, "E2938", {"start": v(-32.58, 47.05) * mm, "end": v(-33.3, 47.32) * mm});
            skLineSegment(sketch, "E2939", {"start": v(-33.3, 47.32) * mm, "end": v(-33.66, 47.47) * mm});
            skLineSegment(sketch, "E2940", {"start": v(-33.66, 47.47) * mm, "end": v(-34.04, 47.61) * mm});
            skLineSegment(sketch, "E2941", {"start": v(-34.04, 47.61) * mm, "end": v(-34.45, 47.77) * mm});
            skLineSegment(sketch, "E2942", {"start": v(-34.45, 47.77) * mm, "end": v(-34.87, 47.93) * mm});
            skLineSegment(sketch, "E2943", {"start": v(-34.87, 47.93) * mm, "end": v(-35.33, 48.1) * mm});
            skLineSegment(sketch, "E2944", {"start": v(-35.33, 48.1) * mm, "end": v(-35.82, 48.28) * mm});
            skLineSegment(sketch, "E2945", {"start": v(-35.82, 48.28) * mm, "end": v(-35.3, 48.35) * mm});
            skLineSegment(sketch, "E2946", {"start": v(-35.3, 48.35) * mm, "end": v(-34.84, 48.41) * mm});
            skLineSegment(sketch, "E2947", {"start": v(-34.84, 48.41) * mm, "end": v(-34.41, 48.48) * mm});
            skLineSegment(sketch, "E2948", {"start": v(-34.41, 48.48) * mm, "end": v(-34.02, 48.53) * mm});
            skLineSegment(sketch, "E2949", {"start": v(-34.02, 48.53) * mm, "end": v(-33.66, 48.6) * mm});
            skLineSegment(sketch, "E2950", {"start": v(-33.66, 48.6) * mm, "end": v(-33.32, 48.64) * mm});
            skLineSegment(sketch, "E2951", {"start": v(-33.32, 48.64) * mm, "end": v(-32.68, 48.75) * mm});
            skLineSegment(sketch, "E2952", {"start": v(-32.68, 48.75) * mm, "end": v(-32.05, 48.85) * mm});
            skLineSegment(sketch, "E2953", {"start": v(-32.05, 48.85) * mm, "end": v(-31.73, 48.9) * mm});
            skLineSegment(sketch, "E2954", {"start": v(-31.73, 48.9) * mm, "end": v(-31.39, 48.94) * mm});
            skLineSegment(sketch, "E2955", {"start": v(-31.39, 48.94) * mm, "end": v(-31.03, 48.99) * mm});
            skLineSegment(sketch, "E2956", {"start": v(-31.03, 48.99) * mm, "end": v(-30.64, 49.04) * mm});
            skLineSegment(sketch, "E2957", {"start": v(-30.64, 49.04) * mm, "end": v(-30.21, 49.08) * mm});
            skLineSegment(sketch, "E2958", {"start": v(-30.21, 49.08) * mm, "end": v(-29.75, 49.13) * mm});
            skLineSegment(sketch, "E2959", {"start": v(-29.75, 49.13) * mm, "end": v(-30.61, 49.52) * mm});
            skLineSegment(sketch, "E2960", {"start": v(-30.61, 49.52) * mm, "end": v(-31.47, 49.9) * mm});
            skLineSegment(sketch, "E2961", {"start": v(-31.47, 49.9) * mm, "end": v(-33.16, 50.63) * mm});
            skLineSegment(sketch, "E2962", {"start": v(-33.16, 50.63) * mm, "end": v(-34.86, 51.36) * mm});
            skLineSegment(sketch, "E2963", {"start": v(-34.86, 51.36) * mm, "end": v(-35.71, 51.74) * mm});
            skLineSegment(sketch, "E2964", {"start": v(-35.71, 51.74) * mm, "end": v(-36.58, 52.13) * mm});
            skLineSegment(sketch, "E2965", {"start": v(-36.58, 52.13) * mm, "end": v(-36.03, 52.21) * mm});
            skLineSegment(sketch, "E2966", {"start": v(-36.03, 52.21) * mm, "end": v(-35.46, 52.28) * mm});
            skLineSegment(sketch, "E2967", {"start": v(-35.46, 52.28) * mm, "end": v(-34.88, 52.32) * mm});
            skLineSegment(sketch, "E2968", {"start": v(-34.88, 52.32) * mm, "end": v(-34.3, 52.33) * mm});
            skLineSegment(sketch, "E2969", {"start": v(-34.3, 52.33) * mm, "end": v(-33.72, 52.3) * mm});
            skLineSegment(sketch, "E2970", {"start": v(-33.72, 52.3) * mm, "end": v(-33.15, 52.24) * mm});
            skLineSegment(sketch, "E2971", {"start": v(-33.15, 52.24) * mm, "end": v(-32.59, 52.13) * mm});
            skLineSegment(sketch, "E2972", {"start": v(-32.59, 52.13) * mm, "end": v(-32.31, 52.06) * mm});
            skLineSegment(sketch, "E2973", {"start": v(-32.31, 52.06) * mm, "end": v(-32.04, 51.97) * mm});
            skLineSegment(sketch, "E2974", {"start": v(-32.04, 51.97) * mm, "end": v(-31.72, 51.85) * mm});
            skLineSegment(sketch, "E2975", {"start": v(-31.72, 51.85) * mm, "end": v(-31.4, 51.71) * mm});
            skLineSegment(sketch, "E2976", {"start": v(-31.4, 51.71) * mm, "end": v(-31.08, 51.56) * mm});
            skLineSegment(sketch, "E2977", {"start": v(-31.08, 51.56) * mm, "end": v(-30.77, 51.4) * mm});
            skLineSegment(sketch, "E2978", {"start": v(-30.77, 51.4) * mm, "end": v(-30.48, 51.24) * mm});
            skLineSegment(sketch, "E2979", {"start": v(-30.48, 51.24) * mm, "end": v(-30.19, 51.06) * mm});
            skLineSegment(sketch, "E2980", {"start": v(-30.19, 51.06) * mm, "end": v(-29.9, 50.87) * mm});
            skLineSegment(sketch, "E2981", {"start": v(-29.9, 50.87) * mm, "end": v(-29.63, 50.67) * mm});
            skLineSegment(sketch, "E2982", {"start": v(-29.63, 50.67) * mm, "end": v(-29.37, 50.45) * mm});
            skLineSegment(sketch, "E2983", {"start": v(-29.37, 50.45) * mm, "end": v(-29.11, 50.23) * mm});
            skLineSegment(sketch, "E2984", {"start": v(-29.11, 50.23) * mm, "end": v(-28.62, 49.76) * mm});
            skLineSegment(sketch, "E2985", {"start": v(-28.62, 49.76) * mm, "end": v(-28.18, 49.26) * mm});
            skLineSegment(sketch, "E2986", {"start": v(-28.18, 49.26) * mm, "end": v(-27.76, 48.71) * mm});
            skLineSegment(sketch, "E2987", {"start": v(-27.76, 48.71) * mm, "end": v(-27.39, 48.14) * mm});
            skLineSegment(sketch, "E2988", {"start": v(-27.39, 48.14) * mm, "end": v(-27.06, 47.54) * mm});
            skLineSegment(sketch, "E2989", {"start": v(-27.06, 47.54) * mm, "end": v(-26.76, 46.9) * mm});
            skLineSegment(sketch, "E2990", {"start": v(-26.76, 46.9) * mm, "end": v(-26.51, 46.25) * mm});
            skLineSegment(sketch, "E2991", {"start": v(-26.51, 46.25) * mm, "end": v(-26.3, 45.56) * mm});
            skLineSegment(sketch, "E2992", {"start": v(-26.3, 45.56) * mm, "end": v(-26.14, 44.86) * mm});
            skLineSegment(sketch, "E2993", {"start": v(-26.14, 44.86) * mm, "end": v(-26.02, 44.13) * mm});
            skLineSegment(sketch, "E2994", {"start": v(-26.02, 44.13) * mm, "end": v(-25.95, 43.4) * mm});
            skLineSegment(sketch, "E2995", {"start": v(-25.95, 43.4) * mm, "end": v(-25.93, 42.87) * mm});
            skLineSegment(sketch, "E2996", {"start": v(-25.93, 42.87) * mm, "end": v(-25.94, 42.35) * mm});
            skLineSegment(sketch, "E2997", {"start": v(-25.94, 42.35) * mm, "end": v(-25.97, 41.83) * mm});
            skLineSegment(sketch, "E2998", {"start": v(-25.97, 41.83) * mm, "end": v(-26.03, 41.3) * mm});
            skLineSegment(sketch, "E2999", {"start": v(-26.03, 41.3) * mm, "end": v(-26.1, 40.8) * mm});
            skLineSegment(sketch, "E3000", {"start": v(-26.1, 40.8) * mm, "end": v(-26.21, 40.28) * mm});
            skLineSegment(sketch, "E3001", {"start": v(-26.21, 40.28) * mm, "end": v(-26.34, 39.78) * mm});
            skLineSegment(sketch, "E3002", {"start": v(-26.34, 39.78) * mm, "end": v(-26.5, 39.28) * mm});
            skLineSegment(sketch, "E3003", {"start": v(-26.5, 39.28) * mm, "end": v(-26.67, 38.8) * mm});
            skLineSegment(sketch, "E3004", {"start": v(-26.67, 38.8) * mm, "end": v(-26.86, 38.32) * mm});
            skLineSegment(sketch, "E3005", {"start": v(-26.86, 38.32) * mm, "end": v(-27.08, 37.85) * mm});
            skLineSegment(sketch, "E3006", {"start": v(-27.08, 37.85) * mm, "end": v(-27.32, 37.4) * mm});
            skLineSegment(sketch, "E3007", {"start": v(-27.32, 37.4) * mm, "end": v(-27.57, 36.96) * mm});
            skLineSegment(sketch, "E3008", {"start": v(-27.57, 36.96) * mm, "end": v(-27.85, 36.53) * mm});
            skLineSegment(sketch, "E3009", {"start": v(-27.85, 36.53) * mm, "end": v(-28.14, 36.12) * mm});
            skLineSegment(sketch, "E3010", {"start": v(-28.14, 36.12) * mm, "end": v(-28.46, 35.72) * mm});
            skLineSegment(sketch, "E3011", {"start": v(-28.46, 35.72) * mm, "end": v(-28.79, 35.35) * mm});
            skLineSegment(sketch, "E3012", {"start": v(-28.79, 35.35) * mm, "end": v(-29.13, 34.99) * mm});
            skLineSegment(sketch, "E3013", {"start": v(-29.13, 34.99) * mm, "end": v(-29.5, 34.65) * mm});
            skLineSegment(sketch, "E3014", {"start": v(-29.5, 34.65) * mm, "end": v(-29.87, 34.34) * mm});
            skLineSegment(sketch, "E3015", {"start": v(-29.87, 34.34) * mm, "end": v(-30.27, 34.04) * mm});
            skLineSegment(sketch, "E3016", {"start": v(-30.27, 34.04) * mm, "end": v(-30.67, 33.78) * mm});
            skLineSegment(sketch, "E3017", {"start": v(-30.67, 33.78) * mm, "end": v(-31.1, 33.53) * mm});
            skLineSegment(sketch, "E3018", {"start": v(-31.1, 33.53) * mm, "end": v(-31.53, 33.31) * mm});
            skLineSegment(sketch, "E3019", {"start": v(-31.53, 33.31) * mm, "end": v(-31.97, 33.12) * mm});
            skLineSegment(sketch, "E3020", {"start": v(-31.97, 33.12) * mm, "end": v(-32.43, 32.96) * mm});
            skLineSegment(sketch, "E3021", {"start": v(-32.43, 32.96) * mm, "end": v(-32.9, 32.83) * mm});
            skLineSegment(sketch, "E3022", {"start": v(-32.9, 32.83) * mm, "end": v(-33.38, 32.73) * mm});
            skLineSegment(sketch, "E3023", {"start": v(-33.38, 32.73) * mm, "end": v(-33.87, 32.66) * mm});
            skLineSegment(sketch, "E3024", {"start": v(-33.87, 32.66) * mm, "end": v(-34.37, 32.63) * mm});
            skLineSegment(sketch, "E3025", {"start": v(-34.37, 32.63) * mm, "end": v(-34.88, 32.62) * mm});
            skLineSegment(sketch, "E3026", {"start": v(-34.88, 32.62) * mm, "end": v(-35.4, 32.66) * mm});
            skLineSegment(sketch, "E3027", {"start": v(-35.4, 32.66) * mm, "end": v(-36.2, 32.75) * mm});
            skLineSegment(sketch, "E3028", {"start": v(-36.2, 32.75) * mm, "end": v(-37.02, 32.85) * mm});
            skLineSegment(sketch, "E3029", {"start": v(-37.02, 32.85) * mm, "end": v(-37.84, 32.94) * mm});
            skLineSegment(sketch, "E3030", {"start": v(-37.84, 32.94) * mm, "end": v(-38.64, 33.03) * mm});
            skLineSegment(sketch, "E3031", {"start": v(-38.64, 33.03) * mm, "end": v(-38.23, 33.1) * mm});
            skLineSegment(sketch, "E3032", {"start": v(-38.23, 33.1) * mm, "end": v(-37.8, 33.18) * mm});
            skLineSegment(sketch, "E3033", {"start": v(-37.8, 33.18) * mm, "end": v(-36.95, 33.37) * mm});
            skLineSegment(sketch, "E3034", {"start": v(-36.95, 33.37) * mm, "end": v(-36.06, 33.59) * mm});
            skLineSegment(sketch, "E3035", {"start": v(-36.06, 33.59) * mm, "end": v(-35.17, 33.81) * mm});
            skLineSegment(sketch, "E3036", {"start": v(-35.17, 33.81) * mm, "end": v(-34.28, 34.04) * mm});
            skLineSegment(sketch, "E3037", {"start": v(-34.28, 34.04) * mm, "end": v(-33.4, 34.25) * mm});
            skLineSegment(sketch, "E3038", {"start": v(-33.4, 34.25) * mm, "end": v(-32.53, 34.44) * mm});
            skLineSegment(sketch, "E3039", {"start": v(-32.53, 34.44) * mm, "end": v(-32.1, 34.52) * mm});
            skLineSegment(sketch, "E3040", {"start": v(-32.1, 34.52) * mm, "end": v(-31.7, 34.6) * mm});
            skLineSegment(sketch, "E3041", {"start": v(-31.7, 34.6) * mm, "end": v(-32.02, 34.65) * mm});
            skLineSegment(sketch, "E3042", {"start": v(-32.02, 34.65) * mm, "end": v(-32.36, 34.72) * mm});
            skLineSegment(sketch, "E3043", {"start": v(-32.36, 34.72) * mm, "end": v(-33.05, 34.9) * mm});
            skLineSegment(sketch, "E3044", {"start": v(-33.05, 34.9) * mm, "end": v(-33.76, 35.09) * mm});
            skLineSegment(sketch, "E3045", {"start": v(-33.76, 35.09) * mm, "end": v(-34.48, 35.3) * mm});
            skLineSegment(sketch, "E3046", {"start": v(-34.48, 35.3) * mm, "end": v(-35.2, 35.51) * mm});
            skLineSegment(sketch, "E3047", {"start": v(-35.2, 35.51) * mm, "end": v(-35.92, 35.71) * mm});
            skLineSegment(sketch, "E3048", {"start": v(-35.92, 35.71) * mm, "end": v(-36.61, 35.88) * mm});
            skLineSegment(sketch, "E3049", {"start": v(-36.61, 35.88) * mm, "end": v(-36.95, 35.95) * mm});
            skLineSegment(sketch, "E3050", {"start": v(-36.95, 35.95) * mm, "end": v(-37.27, 36.01) * mm});
            skLineSegment(sketch, "E3051", {"start": v(-37.27, 36.01) * mm, "end": v(-36.77, 36.05) * mm});
            skLineSegment(sketch, "E3052", {"start": v(-36.77, 36.05) * mm, "end": v(-36.28, 36.09) * mm});
            skLineSegment(sketch, "E3053", {"start": v(-36.28, 36.09) * mm, "end": v(-35.8, 36.14) * mm});
            skLineSegment(sketch, "E3054", {"start": v(-35.8, 36.14) * mm, "end": v(-35.33, 36.2) * mm});
            skLineSegment(sketch, "E3055", {"start": v(-35.33, 36.2) * mm, "end": v(-34.42, 36.32) * mm});
            skLineSegment(sketch, "E3056", {"start": v(-34.42, 36.32) * mm, "end": v(-33.55, 36.46) * mm});
            skLineSegment(sketch, "E3057", {"start": v(-33.55, 36.46) * mm, "end": v(-32.7, 36.61) * mm});
            skLineSegment(sketch, "E3058", {"start": v(-32.7, 36.61) * mm, "end": v(-31.88, 36.77) * mm});
            skLineSegment(sketch, "E3059", {"start": v(-31.88, 36.77) * mm, "end": v(-30.25, 37.05) * mm});
            skLineSegment(sketch, "E3060", {"start": v(-30.25, 37.05) * mm, "end": v(-30.64, 37.2) * mm});
            skLineSegment(sketch, "E3061", {"start": v(-30.64, 37.2) * mm, "end": v(-31, 37.35) * mm});
            skLineSegment(sketch, "E3062", {"start": v(-31, 37.35) * mm, "end": v(-31.35, 37.49) * mm});
            skLineSegment(sketch, "E3063", {"start": v(-31.35, 37.49) * mm, "end": v(-31.67, 37.62) * mm});
            skLineSegment(sketch, "E3064", {"start": v(-31.67, 37.62) * mm, "end": v(-32.28, 37.87) * mm});
            skLineSegment(sketch, "E3065", {"start": v(-32.28, 37.87) * mm, "end": v(-32.86, 38.11) * mm});
            skLineSegment(sketch, "E3066", {"start": v(-32.86, 38.11) * mm, "end": v(-33.44, 38.36) * mm});
            skLineSegment(sketch, "E3067", {"start": v(-33.44, 38.36) * mm, "end": v(-34.05, 38.62) * mm});
            skLineSegment(sketch, "E3068", {"start": v(-34.05, 38.62) * mm, "end": v(-34.37, 38.76) * mm});
            skLineSegment(sketch, "E3069", {"start": v(-34.37, 38.76) * mm, "end": v(-34.72, 38.9) * mm});
            skLineSegment(sketch, "E3070", {"start": v(-34.72, 38.9) * mm, "end": v(-35.08, 39.07) * mm});
            skLineSegment(sketch, "E3071", {"start": v(-35.08, 39.07) * mm, "end": v(-35.48, 39.24) * mm});
            skLineSegment(sketch, "E3072", {"start": v(-22.47, 37.13) * mm, "end": v(-22.12, 37.03) * mm});
            skLineSegment(sketch, "E3073", {"start": v(-22.12, 37.03) * mm, "end": v(-21.8, 36.95) * mm});
            skLineSegment(sketch, "E3074", {"start": v(-21.8, 36.95) * mm, "end": v(-21.52, 36.88) * mm});
            skLineSegment(sketch, "E3075", {"start": v(-21.52, 36.88) * mm, "end": v(-21.25, 36.82) * mm});
            skLineSegment(sketch, "E3076", {"start": v(-21.25, 36.82) * mm, "end": v(-20.78, 36.72) * mm});
            skLineSegment(sketch, "E3077", {"start": v(-20.78, 36.72) * mm, "end": v(-20.35, 36.63) * mm});
            skLineSegment(sketch, "E3078", {"start": v(-20.35, 36.63) * mm, "end": v(-19.92, 36.54) * mm});
            skLineSegment(sketch, "E3079", {"start": v(-19.92, 36.54) * mm, "end": v(-19.45, 36.44) * mm});
            skLineSegment(sketch, "E3080", {"start": v(-19.45, 36.44) * mm, "end": v(-19.18, 36.37) * mm});
            skLineSegment(sketch, "E3081", {"start": v(-19.18, 36.37) * mm, "end": v(-18.9, 36.3) * mm});
            skLineSegment(sketch, "E3082", {"start": v(-18.9, 36.3) * mm, "end": v(-18.58, 36.22) * mm});
            skLineSegment(sketch, "E3083", {"start": v(-18.58, 36.22) * mm, "end": v(-18.23, 36.12) * mm});
            skLineSegment(sketch, "E3084", {"start": v(-18.23, 36.12) * mm, "end": v(-18.55, 36.4) * mm});
            skLineSegment(sketch, "E3085", {"start": v(-18.55, 36.4) * mm, "end": v(-18.83, 36.65) * mm});
            skLineSegment(sketch, "E3086", {"start": v(-18.83, 36.65) * mm, "end": v(-19.1, 36.9) * mm});
            skLineSegment(sketch, "E3087", {"start": v(-19.1, 36.9) * mm, "end": v(-19.34, 37.12) * mm});
            skLineSegment(sketch, "E3088", {"start": v(-19.34, 37.12) * mm, "end": v(-19.78, 37.54) * mm});
            skLineSegment(sketch, "E3089", {"start": v(-19.78, 37.54) * mm, "end": v(-20.19, 37.93) * mm});
            skLineSegment(sketch, "E3090", {"start": v(-20.19, 37.93) * mm, "end": v(-20.58, 38.31) * mm});
            skLineSegment(sketch, "E3091", {"start": v(-20.58, 38.31) * mm, "end": v(-21, 38.72) * mm});
            skLineSegment(sketch, "E3092", {"start": v(-21, 38.72) * mm, "end": v(-21.21, 38.93) * mm});
            skLineSegment(sketch, "E3093", {"start": v(-21.21, 38.93) * mm, "end": v(-21.45, 39.15) * mm});
            skLineSegment(sketch, "E3094", {"start": v(-21.45, 39.15) * mm, "end": v(-21.7, 39.4) * mm});
            skLineSegment(sketch, "E3095", {"start": v(-21.7, 39.4) * mm, "end": v(-21.98, 39.65) * mm});
            skLineSegment(sketch, "E3096", {"start": v(-21.98, 39.65) * mm, "end": v(-21.63, 39.55) * mm});
            skLineSegment(sketch, "E3097", {"start": v(-21.63, 39.55) * mm, "end": v(-21.3, 39.46) * mm});
            skLineSegment(sketch, "E3098", {"start": v(-21.3, 39.46) * mm, "end": v(-21, 39.38) * mm});
            skLineSegment(sketch, "E3099", {"start": v(-21, 39.38) * mm, "end": v(-20.73, 39.31) * mm});
            skLineSegment(sketch, "E3100", {"start": v(-20.73, 39.31) * mm, "end": v(-20.22, 39.19) * mm});
            skLineSegment(sketch, "E3101", {"start": v(-20.22, 39.19) * mm, "end": v(-19.74, 39.07) * mm});
            skLineSegment(sketch, "E3102", {"start": v(-19.74, 39.07) * mm, "end": v(-19.26, 38.95) * mm});
            skLineSegment(sketch, "E3103", {"start": v(-19.26, 38.95) * mm, "end": v(-18.75, 38.82) * mm});
            skLineSegment(sketch, "E3104", {"start": v(-18.75, 38.82) * mm, "end": v(-18.47, 38.75) * mm});
            skLineSegment(sketch, "E3105", {"start": v(-18.47, 38.75) * mm, "end": v(-18.17, 38.66) * mm});
            skLineSegment(sketch, "E3106", {"start": v(-18.17, 38.66) * mm, "end": v(-17.85, 38.57) * mm});
            skLineSegment(sketch, "E3107", {"start": v(-17.85, 38.57) * mm, "end": v(-17.5, 38.47) * mm});
            skLineSegment(sketch, "E3108", {"start": v(-17.5, 38.47) * mm, "end": v(-17.8, 38.72) * mm});
            skLineSegment(sketch, "E3109", {"start": v(-17.8, 38.72) * mm, "end": v(-18.08, 38.96) * mm});
            skLineSegment(sketch, "E3110", {"start": v(-18.08, 38.96) * mm, "end": v(-18.35, 39.18) * mm});
            skLineSegment(sketch, "E3111", {"start": v(-18.35, 39.18) * mm, "end": v(-18.6, 39.4) * mm});
            skLineSegment(sketch, "E3112", {"start": v(-18.6, 39.4) * mm, "end": v(-19.05, 39.83) * mm});
            skLineSegment(sketch, "E3113", {"start": v(-19.05, 39.83) * mm, "end": v(-19.5, 40.24) * mm});
            skLineSegment(sketch, "E3114", {"start": v(-19.5, 40.24) * mm, "end": v(-19.93, 40.67) * mm});
            skLineSegment(sketch, "E3115", {"start": v(-19.93, 40.67) * mm, "end": v(-20.4, 41.13) * mm});
            skLineSegment(sketch, "E3116", {"start": v(-20.4, 41.13) * mm, "end": v(-20.64, 41.37) * mm});
            skLineSegment(sketch, "E3117", {"start": v(-20.64, 41.37) * mm, "end": v(-20.91, 41.63) * mm});
            skLineSegment(sketch, "E3118", {"start": v(-20.91, 41.63) * mm, "end": v(-21.2, 41.9) * mm});
            skLineSegment(sketch, "E3119", {"start": v(-21.2, 41.9) * mm, "end": v(-21.5, 42.2) * mm});
            skLineSegment(sketch, "E3120", {"start": v(-21.5, 42.2) * mm, "end": v(-21.1, 42.08) * mm});
            skLineSegment(sketch, "E3121", {"start": v(-21.1, 42.08) * mm, "end": v(-20.73, 41.98) * mm});
            skLineSegment(sketch, "E3122", {"start": v(-20.73, 41.98) * mm, "end": v(-20.4, 41.89) * mm});
            skLineSegment(sketch, "E3123", {"start": v(-20.4, 41.89) * mm, "end": v(-20.08, 41.8) * mm});
            skLineSegment(sketch, "E3124", {"start": v(-20.08, 41.8) * mm, "end": v(-19.8, 41.73) * mm});
            skLineSegment(sketch, "E3125", {"start": v(-19.8, 41.73) * mm, "end": v(-19.52, 41.66) * mm});
            skLineSegment(sketch, "E3126", {"start": v(-19.52, 41.66) * mm, "end": v(-19.02, 41.53) * mm});
            skLineSegment(sketch, "E3127", {"start": v(-19.02, 41.53) * mm, "end": v(-18.52, 41.4) * mm});
            skLineSegment(sketch, "E3128", {"start": v(-18.52, 41.4) * mm, "end": v(-18, 41.26) * mm});
            skLineSegment(sketch, "E3129", {"start": v(-18, 41.26) * mm, "end": v(-17.71, 41.18) * mm});
            skLineSegment(sketch, "E3130", {"start": v(-17.71, 41.18) * mm, "end": v(-17.4, 41.1) * mm});
            skLineSegment(sketch, "E3131", {"start": v(-17.4, 41.1) * mm, "end": v(-17.07, 41) * mm});
            skLineSegment(sketch, "E3132", {"start": v(-17.07, 41) * mm, "end": v(-16.71, 40.88) * mm});
            skLineSegment(sketch, "E3133", {"start": v(-16.71, 40.88) * mm, "end": v(-17.75, 42) * mm});
            skLineSegment(sketch, "E3134", {"start": v(-17.75, 42) * mm, "end": v(-18.77, 43.09) * mm});
            skLineSegment(sketch, "E3135", {"start": v(-18.77, 43.09) * mm, "end": v(-19.8, 44.18) * mm});
            skLineSegment(sketch, "E3136", {"start": v(-19.8, 44.18) * mm, "end": v(-20.83, 45.3) * mm});
            skLineSegment(sketch, "E3137", {"start": v(-20.83, 45.3) * mm, "end": v(-20.4, 45.18) * mm});
            skLineSegment(sketch, "E3138", {"start": v(-20.4, 45.18) * mm, "end": v(-19.95, 45.05) * mm});
            skLineSegment(sketch, "E3139", {"start": v(-19.95, 45.05) * mm, "end": v(-19.5, 44.9) * mm});
            skLineSegment(sketch, "E3140", {"start": v(-19.5, 44.9) * mm, "end": v(-19.07, 44.72) * mm});
            skLineSegment(sketch, "E3141", {"start": v(-19.07, 44.72) * mm, "end": v(-18.65, 44.51) * mm});
            skLineSegment(sketch, "E3142", {"start": v(-18.65, 44.51) * mm, "end": v(-18.24, 44.28) * mm});
            skLineSegment(sketch, "E3143", {"start": v(-18.24, 44.28) * mm, "end": v(-17.86, 44.02) * mm});
            skLineSegment(sketch, "E3144", {"start": v(-17.86, 44.02) * mm, "end": v(-17.51, 43.72) * mm});
            skLineSegment(sketch, "E3145", {"start": v(-17.51, 43.72) * mm, "end": v(-17.11, 43.32) * mm});
            skLineSegment(sketch, "E3146", {"start": v(-17.11, 43.32) * mm, "end": v(-16.75, 42.9) * mm});
            skLineSegment(sketch, "E3147", {"start": v(-16.75, 42.9) * mm, "end": v(-16.42, 42.45) * mm});
            skLineSegment(sketch, "E3148", {"start": v(-16.42, 42.45) * mm, "end": v(-16.14, 41.98) * mm});
            skLineSegment(sketch, "E3149", {"start": v(-16.14, 41.98) * mm, "end": v(-15.89, 41.5) * mm});
            skLineSegment(sketch, "E3150", {"start": v(-15.89, 41.5) * mm, "end": v(-15.68, 40.99) * mm});
            skLineSegment(sketch, "E3151", {"start": v(-15.68, 40.99) * mm, "end": v(-15.5, 40.46) * mm});
            skLineSegment(sketch, "E3152", {"start": v(-15.5, 40.46) * mm, "end": v(-15.37, 39.93) * mm});
            skLineSegment(sketch, "E3153", {"start": v(-15.37, 39.93) * mm, "end": v(-15.28, 39.38) * mm});
            skLineSegment(sketch, "E3154", {"start": v(-15.28, 39.38) * mm, "end": v(-15.23, 38.83) * mm});
            skLineSegment(sketch, "E3155", {"start": v(-15.23, 38.83) * mm, "end": v(-15.21, 38.26) * mm});
            skLineSegment(sketch, "E3156", {"start": v(-15.21, 38.26) * mm, "end": v(-15.23, 37.7) * mm});
            skLineSegment(sketch, "E3157", {"start": v(-15.23, 37.7) * mm, "end": v(-15.3, 37.12) * mm});
            skLineSegment(sketch, "E3158", {"start": v(-15.3, 37.12) * mm, "end": v(-15.4, 36.54) * mm});
            skLineSegment(sketch, "E3159", {"start": v(-15.4, 36.54) * mm, "end": v(-15.55, 35.97) * mm});
            skLineSegment(sketch, "E3160", {"start": v(-15.55, 35.97) * mm, "end": v(-15.73, 35.4) * mm});
            skLineSegment(sketch, "E3161", {"start": v(-15.73, 35.4) * mm, "end": v(-15.89, 35) * mm});
            skLineSegment(sketch, "E3162", {"start": v(-15.89, 35) * mm, "end": v(-16.06, 34.61) * mm});
            skLineSegment(sketch, "E3163", {"start": v(-16.06, 34.61) * mm, "end": v(-16.25, 34.23) * mm});
            skLineSegment(sketch, "E3164", {"start": v(-16.25, 34.23) * mm, "end": v(-16.46, 33.87) * mm});
            skLineSegment(sketch, "E3165", {"start": v(-16.46, 33.87) * mm, "end": v(-16.68, 33.51) * mm});
            skLineSegment(sketch, "E3166", {"start": v(-16.68, 33.51) * mm, "end": v(-16.93, 33.17) * mm});
            skLineSegment(sketch, "E3167", {"start": v(-16.93, 33.17) * mm, "end": v(-17.18, 32.83) * mm});
            skLineSegment(sketch, "E3168", {"start": v(-17.18, 32.83) * mm, "end": v(-17.46, 32.51) * mm});
            skLineSegment(sketch, "E3169", {"start": v(-17.46, 32.51) * mm, "end": v(-17.74, 32.2) * mm});
            skLineSegment(sketch, "E3170", {"start": v(-17.74, 32.2) * mm, "end": v(-18.04, 31.91) * mm});
            skLineSegment(sketch, "E3171", {"start": v(-18.04, 31.91) * mm, "end": v(-18.35, 31.64) * mm});
            skLineSegment(sketch, "E3172", {"start": v(-18.35, 31.64) * mm, "end": v(-18.67, 31.37) * mm});
            skLineSegment(sketch, "E3173", {"start": v(-18.67, 31.37) * mm, "end": v(-19, 31.13) * mm});
            skLineSegment(sketch, "E3174", {"start": v(-19, 31.13) * mm, "end": v(-19.35, 30.9) * mm});
            skLineSegment(sketch, "E3175", {"start": v(-19.35, 30.9) * mm, "end": v(-19.7, 30.69) * mm});
            skLineSegment(sketch, "E3176", {"start": v(-19.7, 30.69) * mm, "end": v(-20.06, 30.5) * mm});
            skLineSegment(sketch, "E3177", {"start": v(-20.06, 30.5) * mm, "end": v(-20.42, 30.32) * mm});
            skLineSegment(sketch, "E3178", {"start": v(-20.42, 30.32) * mm, "end": v(-20.8, 30.17) * mm});
            skLineSegment(sketch, "E3179", {"start": v(-20.8, 30.17) * mm, "end": v(-21.17, 30.03) * mm});
            skLineSegment(sketch, "E3180", {"start": v(-21.17, 30.03) * mm, "end": v(-21.55, 29.92) * mm});
            skLineSegment(sketch, "E3181", {"start": v(-21.55, 29.92) * mm, "end": v(-21.94, 29.83) * mm});
            skLineSegment(sketch, "E3182", {"start": v(-21.94, 29.83) * mm, "end": v(-22.33, 29.76) * mm});
            skLineSegment(sketch, "E3183", {"start": v(-22.33, 29.76) * mm, "end": v(-22.72, 29.71) * mm});
            skLineSegment(sketch, "E3184", {"start": v(-22.72, 29.71) * mm, "end": v(-23.11, 29.69) * mm});
            skLineSegment(sketch, "E3185", {"start": v(-23.11, 29.69) * mm, "end": v(-23.5, 29.7) * mm});
            skLineSegment(sketch, "E3186", {"start": v(-23.5, 29.7) * mm, "end": v(-23.9, 29.72) * mm});
            skLineSegment(sketch, "E3187", {"start": v(-23.9, 29.72) * mm, "end": v(-24.29, 29.77) * mm});
            skLineSegment(sketch, "E3188", {"start": v(-24.29, 29.77) * mm, "end": v(-24.68, 29.85) * mm});
            skLineSegment(sketch, "E3189", {"start": v(-24.68, 29.85) * mm, "end": v(-25.07, 29.95) * mm});
            skLineSegment(sketch, "E3190", {"start": v(-25.07, 29.95) * mm, "end": v(-25.45, 30.09) * mm});
            skLineSegment(sketch, "E3191", {"start": v(-25.45, 30.09) * mm, "end": v(-25.83, 30.25) * mm});
            skLineSegment(sketch, "E3192", {"start": v(-25.83, 30.25) * mm, "end": v(-26.2, 30.44) * mm});
            skLineSegment(sketch, "E3193", {"start": v(-26.2, 30.44) * mm, "end": v(-28.5, 31.76) * mm});
            skLineSegment(sketch, "E3194", {"start": v(-28.5, 31.76) * mm, "end": v(-27.83, 31.6) * mm});
            skLineSegment(sketch, "E3195", {"start": v(-27.83, 31.6) * mm, "end": v(-27.12, 31.47) * mm});
            skLineSegment(sketch, "E3196", {"start": v(-27.12, 31.47) * mm, "end": v(-25.66, 31.23) * mm});
            skLineSegment(sketch, "E3197", {"start": v(-25.66, 31.23) * mm, "end": v(-24.2, 30.98) * mm});
            skLineSegment(sketch, "E3198", {"start": v(-24.2, 30.98) * mm, "end": v(-23.5, 30.85) * mm});
            skLineSegment(sketch, "E3199", {"start": v(-23.5, 30.85) * mm, "end": v(-22.83, 30.7) * mm});
            skLineSegment(sketch, "E3200", {"start": v(-22.83, 30.7) * mm, "end": v(-23.28, 31) * mm});
            skLineSegment(sketch, "E3201", {"start": v(-23.28, 31) * mm, "end": v(-23.74, 31.35) * mm});
            skLineSegment(sketch, "E3202", {"start": v(-23.74, 31.35) * mm, "end": v(-24.67, 32.12) * mm});
            skLineSegment(sketch, "E3203", {"start": v(-24.67, 32.12) * mm, "end": v(-25.6, 32.88) * mm});
            skLineSegment(sketch, "E3204", {"start": v(-25.6, 32.88) * mm, "end": v(-26.07, 33.23) * mm});
            skLineSegment(sketch, "E3205", {"start": v(-26.07, 33.23) * mm, "end": v(-26.52, 33.54) * mm});
            skLineSegment(sketch, "E3206", {"start": v(-26.52, 33.54) * mm, "end": v(-25.75, 33.27) * mm});
            skLineSegment(sketch, "E3207", {"start": v(-25.75, 33.27) * mm, "end": v(-25.01, 33.05) * mm});
            skLineSegment(sketch, "E3208", {"start": v(-25.01, 33.05) * mm, "end": v(-24.3, 32.85) * mm});
            skLineSegment(sketch, "E3209", {"start": v(-24.3, 32.85) * mm, "end": v(-23.6, 32.68) * mm});
            skLineSegment(sketch, "E3210", {"start": v(-23.6, 32.68) * mm, "end": v(-22.27, 32.37) * mm});
            skLineSegment(sketch, "E3211", {"start": v(-22.27, 32.37) * mm, "end": v(-20.96, 32.05) * mm});
            skLineSegment(sketch, "E3212", {"start": v(-20.96, 32.05) * mm, "end": v(-21.2, 32.3) * mm});
            skLineSegment(sketch, "E3213", {"start": v(-21.2, 32.3) * mm, "end": v(-21.43, 32.52) * mm});
            skLineSegment(sketch, "E3214", {"start": v(-21.43, 32.52) * mm, "end": v(-21.84, 32.94) * mm});
            skLineSegment(sketch, "E3215", {"start": v(-21.84, 32.94) * mm, "end": v(-22.2, 33.32) * mm});
            skLineSegment(sketch, "E3216", {"start": v(-22.2, 33.32) * mm, "end": v(-22.56, 33.68) * mm});
            skLineSegment(sketch, "E3217", {"start": v(-22.56, 33.68) * mm, "end": v(-22.91, 34.05) * mm});
            skLineSegment(sketch, "E3218", {"start": v(-22.91, 34.05) * mm, "end": v(-23.28, 34.44) * mm});
            skLineSegment(sketch, "E3219", {"start": v(-23.28, 34.44) * mm, "end": v(-23.48, 34.65) * mm});
            skLineSegment(sketch, "E3220", {"start": v(-23.48, 34.65) * mm, "end": v(-23.69, 34.87) * mm});
            skLineSegment(sketch, "E3221", {"start": v(-23.69, 34.87) * mm, "end": v(-23.91, 35.1) * mm});
            skLineSegment(sketch, "E3222", {"start": v(-23.91, 35.1) * mm, "end": v(-24.15, 35.36) * mm});
            skLineSegment(sketch, "E3223", {"start": v(-24.15, 35.36) * mm, "end": v(-23.55, 35.13) * mm});
            skLineSegment(sketch, "E3224", {"start": v(-23.55, 35.13) * mm, "end": v(-22.99, 34.93) * mm});
            skLineSegment(sketch, "E3225", {"start": v(-22.99, 34.93) * mm, "end": v(-21.91, 34.6) * mm});
            skLineSegment(sketch, "E3226", {"start": v(-21.91, 34.6) * mm, "end": v(-21.37, 34.44) * mm});
            skLineSegment(sketch, "E3227", {"start": v(-21.37, 34.44) * mm, "end": v(-20.8, 34.28) * mm});
            skLineSegment(sketch, "E3228", {"start": v(-20.8, 34.28) * mm, "end": v(-20.21, 34.1) * mm});
            skLineSegment(sketch, "E3229", {"start": v(-20.21, 34.1) * mm, "end": v(-19.57, 33.91) * mm});
            skLineSegment(sketch, "E3230", {"start": v(-19.57, 33.91) * mm, "end": v(-19.84, 34.18) * mm});
            skLineSegment(sketch, "E3231", {"start": v(-19.84, 34.18) * mm, "end": v(-20.08, 34.42) * mm});
            skLineSegment(sketch, "E3232", {"start": v(-20.08, 34.42) * mm, "end": v(-20.28, 34.64) * mm});
            skLineSegment(sketch, "E3233", {"start": v(-20.28, 34.64) * mm, "end": v(-20.46, 34.85) * mm});
            skLineSegment(sketch, "E3234", {"start": v(-20.46, 34.85) * mm, "end": v(-20.62, 35.05) * mm});
            skLineSegment(sketch, "E3235", {"start": v(-20.62, 35.05) * mm, "end": v(-20.77, 35.23) * mm});
            skLineSegment(sketch, "E3236", {"start": v(-20.77, 35.23) * mm, "end": v(-21.03, 35.58) * mm});
            skLineSegment(sketch, "E3237", {"start": v(-21.03, 35.58) * mm, "end": v(-21.3, 35.92) * mm});
            skLineSegment(sketch, "E3238", {"start": v(-21.3, 35.92) * mm, "end": v(-21.43, 36.1) * mm});
            skLineSegment(sketch, "E3239", {"start": v(-21.43, 36.1) * mm, "end": v(-21.6, 36.27) * mm});
            skLineSegment(sketch, "E3240", {"start": v(-21.6, 36.27) * mm, "end": v(-21.77, 36.46) * mm});
            skLineSegment(sketch, "E3241", {"start": v(-21.77, 36.46) * mm, "end": v(-21.97, 36.67) * mm});
            skLineSegment(sketch, "E3242", {"start": v(-21.97, 36.67) * mm, "end": v(-22.2, 36.9) * mm});
            skLineSegment(sketch, "E3243", {"start": v(-22.2, 36.9) * mm, "end": v(-22.47, 37.13) * mm});
            skLineSegment(sketch, "E3244", {"start": v(4.3, 56.73) * mm, "end": v(4.25, 56.02) * mm});
            skLineSegment(sketch, "E3245", {"start": v(4.25, 56.02) * mm, "end": v(4.14, 55.34) * mm});
            skLineSegment(sketch, "E3246", {"start": v(4.14, 55.34) * mm, "end": v(3.96, 54.68) * mm});
            skLineSegment(sketch, "E3247", {"start": v(3.96, 54.68) * mm, "end": v(3.72, 54.04) * mm});
            skLineSegment(sketch, "E3248", {"start": v(3.72, 54.04) * mm, "end": v(3.43, 53.44) * mm});
            skLineSegment(sketch, "E3249", {"start": v(3.43, 53.44) * mm, "end": v(3.08, 52.87) * mm});
            skLineSegment(sketch, "E3250", {"start": v(3.08, 52.87) * mm, "end": v(2.68, 52.34) * mm});
            skLineSegment(sketch, "E3251", {"start": v(2.68, 52.34) * mm, "end": v(2.23, 51.85) * mm});
            skLineSegment(sketch, "E3252", {"start": v(2.23, 51.85) * mm, "end": v(1.74, 51.4) * mm});
            skLineSegment(sketch, "E3253", {"start": v(1.74, 51.4) * mm, "end": v(1.21, 51) * mm});
            skLineSegment(sketch, "E3254", {"start": v(1.21, 51) * mm, "end": v(0.64, 50.65) * mm});
            skLineSegment(sketch, "E3255", {"start": v(0.64, 50.65) * mm, "end": v(0.04, 50.36) * mm});
            skLineSegment(sketch, "E3256", {"start": v(0.04, 50.36) * mm, "end": v(-0.6, 50.12) * mm});
            skLineSegment(sketch, "E3257", {"start": v(-0.6, 50.12) * mm, "end": v(-1.26, 49.94) * mm});
            skLineSegment(sketch, "E3258", {"start": v(-1.26, 49.94) * mm, "end": v(-1.94, 49.83) * mm});
            skLineSegment(sketch, "E3259", {"start": v(-1.94, 49.83) * mm, "end": v(-2.65, 49.8) * mm});
            skLineSegment(sketch, "E3260", {"start": v(-2.65, 49.8) * mm, "end": v(-2.53, 50.46) * mm});
            skLineSegment(sketch, "E3261", {"start": v(-2.53, 50.46) * mm, "end": v(-2.36, 51.1) * mm});
            skLineSegment(sketch, "E3262", {"start": v(-2.36, 51.1) * mm, "end": v(-2.14, 51.73) * mm});
            skLineSegment(sketch, "E3263", {"start": v(-2.14, 51.73) * mm, "end": v(-1.87, 52.33) * mm});
            skLineSegment(sketch, "E3264", {"start": v(-1.87, 52.33) * mm, "end": v(-1.55, 52.9) * mm});
            skLineSegment(sketch, "E3265", {"start": v(-1.55, 52.9) * mm, "end": v(-1.2, 53.44) * mm});
            skLineSegment(sketch, "E3266", {"start": v(-1.2, 53.44) * mm, "end": v(-0.8, 53.96) * mm});
            skLineSegment(sketch, "E3267", {"start": v(-0.8, 53.96) * mm, "end": v(-0.35, 54.43) * mm});
            skLineSegment(sketch, "E3268", {"start": v(-0.35, 54.43) * mm, "end": v(0.13, 54.87) * mm});
            skLineSegment(sketch, "E3269", {"start": v(0.13, 54.87) * mm, "end": v(0.64, 55.27) * mm});
            skLineSegment(sketch, "E3270", {"start": v(0.64, 55.27) * mm, "end": v(1.18, 55.63) * mm});
            skLineSegment(sketch, "E3271", {"start": v(1.18, 55.63) * mm, "end": v(1.75, 55.95) * mm});
            skLineSegment(sketch, "E3272", {"start": v(1.75, 55.95) * mm, "end": v(2.35, 56.22) * mm});
            skLineSegment(sketch, "E3273", {"start": v(2.35, 56.22) * mm, "end": v(2.98, 56.44) * mm});
            skLineSegment(sketch, "E3274", {"start": v(2.98, 56.44) * mm, "end": v(3.62, 56.6) * mm});
            skLineSegment(sketch, "E3275", {"start": v(3.62, 56.6) * mm, "end": v(4.3, 56.73) * mm});
            skLineSegment(sketch, "E3276", {"start": v(85.61, 86.45) * mm, "end": v(85.07, 89.12) * mm});
            skLineSegment(sketch, "E3277", {"start": v(85.07, 89.12) * mm, "end": v(84.4, 91.76) * mm});
            skLineSegment(sketch, "E3278", {"start": v(84.4, 91.76) * mm, "end": v(83.6, 94.37) * mm});
            skLineSegment(sketch, "E3279", {"start": v(83.6, 94.37) * mm, "end": v(82.66, 96.93) * mm});
            skLineSegment(sketch, "E3280", {"start": v(82.66, 96.93) * mm, "end": v(81.61, 99.44) * mm});
            skLineSegment(sketch, "E3281", {"start": v(81.61, 99.44) * mm, "end": v(80.44, 101.9) * mm});
            skLineSegment(sketch, "E3282", {"start": v(80.44, 101.9) * mm, "end": v(79.15, 104.3) * mm});
            skLineSegment(sketch, "E3283", {"start": v(79.15, 104.3) * mm, "end": v(77.74, 106.63) * mm});
            skLineSegment(sketch, "E3284", {"start": v(77.74, 106.63) * mm, "end": v(76.22, 108.9) * mm});
            skLineSegment(sketch, "E3285", {"start": v(76.22, 108.9) * mm, "end": v(74.6, 111.07) * mm});
            skLineSegment(sketch, "E3286", {"start": v(74.6, 111.07) * mm, "end": v(72.86, 113.17) * mm});
            skLineSegment(sketch, "E3287", {"start": v(72.86, 113.17) * mm, "end": v(71.03, 115.17) * mm});
            skLineSegment(sketch, "E3288", {"start": v(71.03, 115.17) * mm, "end": v(69.1, 117.07) * mm});
            skLineSegment(sketch, "E3289", {"start": v(69.1, 117.07) * mm, "end": v(67.06, 118.88) * mm});
            skLineSegment(sketch, "E3290", {"start": v(67.06, 118.88) * mm, "end": v(64.94, 120.57) * mm});
            skLineSegment(sketch, "E3291", {"start": v(64.94, 120.57) * mm, "end": v(62.72, 122.14) * mm});
            skLineSegment(sketch, "E3292", {"start": v(62.72, 122.14) * mm, "end": v(60.42, 123.6) * mm});
            skLineSegment(sketch, "E3293", {"start": v(60.42, 123.6) * mm, "end": v(58.05, 124.91) * mm});
            skLineSegment(sketch, "E3294", {"start": v(58.05, 124.91) * mm, "end": v(55.62, 126.1) * mm});
            skLineSegment(sketch, "E3295", {"start": v(55.62, 126.1) * mm, "end": v(53.12, 127.17) * mm});
            skLineSegment(sketch, "E3296", {"start": v(53.12, 127.17) * mm, "end": v(50.57, 128.1) * mm});
            skLineSegment(sketch, "E3297", {"start": v(50.57, 128.1) * mm, "end": v(47.98, 128.9) * mm});
            skLineSegment(sketch, "E3298", {"start": v(47.98, 128.9) * mm, "end": v(45.35, 129.55) * mm});
            skLineSegment(sketch, "E3299", {"start": v(45.35, 129.55) * mm, "end": v(42.7, 130.07) * mm});
            skLineSegment(sketch, "E3300", {"start": v(42.7, 130.07) * mm, "end": v(40.02, 130.44) * mm});
            skLineSegment(sketch, "E3301", {"start": v(40.02, 130.44) * mm, "end": v(37.32, 130.67) * mm});
            skLineSegment(sketch, "E3302", {"start": v(37.32, 130.67) * mm, "end": v(34.62, 130.74) * mm});
            skLineSegment(sketch, "E3303", {"start": v(34.62, 130.74) * mm, "end": v(31.92, 130.67) * mm});
            skLineSegment(sketch, "E3304", {"start": v(31.92, 130.67) * mm, "end": v(29.23, 130.44) * mm});
            skLineSegment(sketch, "E3305", {"start": v(29.23, 130.44) * mm, "end": v(26.56, 130.06) * mm});
            skLineSegment(sketch, "E3306", {"start": v(26.56, 130.06) * mm, "end": v(26.23, 130) * mm});
            skLineSegment(sketch, "E3307", {"start": v(26.23, 130) * mm, "end": v(25.98, 129.95) * mm});
            skLineSegment(sketch, "E3308", {"start": v(25.98, 129.95) * mm, "end": v(25.48, 129.86) * mm});
            skLineSegment(sketch, "E3309", {"start": v(25.48, 129.86) * mm, "end": v(24.48, 129.65) * mm});
            skLineSegment(sketch, "E3310", {"start": v(24.48, 129.65) * mm, "end": v(22.48, 129.18) * mm});
            skLineSegment(sketch, "E3311", {"start": v(22.48, 129.18) * mm, "end": v(20.5, 128.64) * mm});
            skLineSegment(sketch, "E3312", {"start": v(20.5, 128.64) * mm, "end": v(18.53, 128.02) * mm});
            skLineSegment(sketch, "E3313", {"start": v(18.53, 128.02) * mm, "end": v(16.58, 127.32) * mm});
            skLineSegment(sketch, "E3314", {"start": v(16.58, 127.32) * mm, "end": v(14.67, 126.54) * mm});
            skLineSegment(sketch, "E3315", {"start": v(14.67, 126.54) * mm, "end": v(12.8, 125.67) * mm});
            skLineSegment(sketch, "E3316", {"start": v(12.8, 125.67) * mm, "end": v(10.97, 124.73) * mm});
            skLineSegment(sketch, "E3317", {"start": v(10.97, 124.73) * mm, "end": v(9.2, 123.7) * mm});
            skLineSegment(sketch, "E3318", {"start": v(9.2, 123.7) * mm, "end": v(7.48, 122.59) * mm});
            skLineSegment(sketch, "E3319", {"start": v(7.48, 122.59) * mm, "end": v(5.83, 121.39) * mm});
            skLineSegment(sketch, "E3320", {"start": v(5.83, 121.39) * mm, "end": v(4.25, 120.1) * mm});
            skLineSegment(sketch, "E3321", {"start": v(4.25, 120.1) * mm, "end": v(2.76, 118.73) * mm});
            skLineSegment(sketch, "E3322", {"start": v(2.76, 118.73) * mm, "end": v(1.35, 117.26) * mm});
            skLineSegment(sketch, "E3323", {"start": v(1.35, 117.26) * mm, "end": v(0.04, 115.71) * mm});
            skLineSegment(sketch, "E3324", {"start": v(0.04, 115.71) * mm, "end": v(-1.23, 113.98) * mm});
            skLineSegment(sketch, "E3325", {"start": v(-1.23, 113.98) * mm, "end": v(-2.4, 112.14) * mm});
            skLineSegment(sketch, "E3326", {"start": v(-2.4, 112.14) * mm, "end": v(-3.46, 110.23) * mm});
            skLineSegment(sketch, "E3327", {"start": v(-3.46, 110.23) * mm, "end": v(-4.39, 108.26) * mm});
            skLineSegment(sketch, "E3328", {"start": v(-4.39, 108.26) * mm, "end": v(-5.2, 106.23) * mm});
            skLineSegment(sketch, "E3329", {"start": v(-5.2, 106.23) * mm, "end": v(-5.87, 104.16) * mm});
            skLineSegment(sketch, "E3330", {"start": v(-5.87, 104.16) * mm, "end": v(-6.43, 102.04) * mm});
            skLineSegment(sketch, "E3331", {"start": v(-6.43, 102.04) * mm, "end": v(-6.85, 99.9) * mm});
            skLineSegment(sketch, "E3332", {"start": v(-6.85, 99.9) * mm, "end": v(-7.15, 97.73) * mm});
            skLineSegment(sketch, "E3333", {"start": v(-7.15, 97.73) * mm, "end": v(-7.3, 95.55) * mm});
            skLineSegment(sketch, "E3334", {"start": v(-7.3, 95.55) * mm, "end": v(-7.34, 93.36) * mm});
            skLineSegment(sketch, "E3335", {"start": v(-7.34, 93.36) * mm, "end": v(-7.23, 91.18) * mm});
            skLineSegment(sketch, "E3336", {"start": v(-7.23, 91.18) * mm, "end": v(-7, 89) * mm});
            skLineSegment(sketch, "E3337", {"start": v(-7, 89) * mm, "end": v(-6.61, 86.85) * mm});
            skLineSegment(sketch, "E3338", {"start": v(-6.61, 86.85) * mm, "end": v(-6.1, 84.72) * mm});
            skLineSegment(sketch, "E3339", {"start": v(-6.1, 84.72) * mm, "end": v(-5.95, 84.2) * mm});
            skLineSegment(sketch, "E3340", {"start": v(-5.95, 84.2) * mm, "end": v(-5.84, 83.84) * mm});
            skLineSegment(sketch, "E3341", {"start": v(-5.84, 83.84) * mm, "end": v(-5.6, 83.12) * mm});
            skLineSegment(sketch, "E3342", {"start": v(-5.6, 83.12) * mm, "end": v(-5.11, 81.67) * mm});
            skLineSegment(sketch, "E3343", {"start": v(-5.11, 81.67) * mm, "end": v(-4.02, 78.78) * mm});
            skLineSegment(sketch, "E3344", {"start": v(-4.02, 78.78) * mm, "end": v(-2.9, 75.9) * mm});
            skLineSegment(sketch, "E3345", {"start": v(-2.9, 75.9) * mm, "end": v(-1.86, 73) * mm});
            skLineSegment(sketch, "E3346", {"start": v(-1.86, 73) * mm, "end": v(-1.03, 70.1) * mm});
            skLineSegment(sketch, "E3347", {"start": v(-1.03, 70.1) * mm, "end": v(-0.73, 68.65) * mm});
            skLineSegment(sketch, "E3348", {"start": v(-0.73, 68.65) * mm, "end": v(-0.53, 67.2) * mm});
            skLineSegment(sketch, "E3349", {"start": v(-0.53, 67.2) * mm, "end": v(-0.44, 65.73) * mm});
            skLineSegment(sketch, "E3350", {"start": v(-0.44, 65.73) * mm, "end": v(-0.48, 64.26) * mm});
            skLineSegment(sketch, "E3351", {"start": v(-0.48, 64.26) * mm, "end": v(-0.66, 62.79) * mm});
            skLineSegment(sketch, "E3352", {"start": v(-0.66, 62.79) * mm, "end": v(-0.8, 62.11) * mm});
            skLineSegment(sketch, "E3353", {"start": v(-0.8, 62.11) * mm, "end": v(-0.96, 61.53) * mm});
            skLineSegment(sketch, "E3354", {"start": v(-0.96, 61.53) * mm, "end": v(-1.46, 60.38) * mm});
            skLineSegment(sketch, "E3355", {"start": v(-1.46, 60.38) * mm, "end": v(-2.15, 59.27) * mm});
            skLineSegment(sketch, "E3356", {"start": v(-2.15, 59.27) * mm, "end": v(-3.01, 58.21) * mm});
            skLineSegment(sketch, "E3357", {"start": v(-3.01, 58.21) * mm, "end": v(-4.03, 57.21) * mm});
            skLineSegment(sketch, "E3358", {"start": v(-4.03, 57.21) * mm, "end": v(-5.18, 56.29) * mm});
            skLineSegment(sketch, "E3359", {"start": v(-5.18, 56.29) * mm, "end": v(-6.44, 55.45) * mm});
            skLineSegment(sketch, "E3360", {"start": v(-6.44, 55.45) * mm, "end": v(-7.8, 54.7) * mm});
            skLineSegment(sketch, "E3361", {"start": v(-7.8, 54.7) * mm, "end": v(-9.24, 54.06) * mm});
            skLineSegment(sketch, "E3362", {"start": v(-9.24, 54.06) * mm, "end": v(-10.73, 53.54) * mm});
            skLineSegment(sketch, "E3363", {"start": v(-10.73, 53.54) * mm, "end": v(-12.25, 53.16) * mm});
            skLineSegment(sketch, "E3364", {"start": v(-12.25, 53.16) * mm, "end": v(-13.8, 52.91) * mm});
            skLineSegment(sketch, "E3365", {"start": v(-13.8, 52.91) * mm, "end": v(-15.34, 52.82) * mm});
            skLineSegment(sketch, "E3366", {"start": v(-15.34, 52.82) * mm, "end": v(-16.86, 52.9) * mm});
            skLineSegment(sketch, "E3367", {"start": v(-16.86, 52.9) * mm, "end": v(-18.34, 53.15) * mm});
            skLineSegment(sketch, "E3368", {"start": v(-18.34, 53.15) * mm, "end": v(-18.7, 53.24) * mm});
            skLineSegment(sketch, "E3369", {"start": v(-18.7, 53.24) * mm, "end": v(-18.92, 53.3) * mm});
            skLineSegment(sketch, "E3370", {"start": v(-18.92, 53.3) * mm, "end": v(-19.31, 53.44) * mm});
            skLineSegment(sketch, "E3371", {"start": v(-19.31, 53.44) * mm, "end": v(-20.82, 54) * mm});
            skLineSegment(sketch, "E3372", {"start": v(-20.82, 54) * mm, "end": v(-22.24, 54.62) * mm});
            skLineSegment(sketch, "E3373", {"start": v(-22.24, 54.62) * mm, "end": v(-23.56, 55.28) * mm});
            skLineSegment(sketch, "E3374", {"start": v(-23.56, 55.28) * mm, "end": v(-24.8, 56) * mm});
            skLineSegment(sketch, "E3375", {"start": v(-24.8, 56) * mm, "end": v(-25.97, 56.75) * mm});
            skLineSegment(sketch, "E3376", {"start": v(-25.97, 56.75) * mm, "end": v(-27.05, 57.55) * mm});
            skLineSegment(sketch, "E3377", {"start": v(-27.05, 57.55) * mm, "end": v(-28.05, 58.38) * mm});
            skLineSegment(sketch, "E3378", {"start": v(-28.05, 58.38) * mm, "end": v(-28.98, 59.24) * mm});
            skLineSegment(sketch, "E3379", {"start": v(-28.98, 59.24) * mm, "end": v(-29.83, 60.13) * mm});
            skLineSegment(sketch, "E3380", {"start": v(-29.83, 60.13) * mm, "end": v(-31.34, 61.97) * mm});
            skLineSegment(sketch, "E3381", {"start": v(-31.34, 61.97) * mm, "end": v(-32.6, 63.88) * mm});
            skLineSegment(sketch, "E3382", {"start": v(-32.6, 63.88) * mm, "end": v(-33.63, 65.81) * mm});
            skLineSegment(sketch, "E3383", {"start": v(-33.63, 65.81) * mm, "end": v(-34.45, 67.75) * mm});
            skLineSegment(sketch, "E3384", {"start": v(-34.45, 67.75) * mm, "end": v(-35.08, 69.65) * mm});
            skLineSegment(sketch, "E3385", {"start": v(-35.08, 69.65) * mm, "end": v(-35.55, 71.5) * mm});
            skLineSegment(sketch, "E3386", {"start": v(-35.55, 71.5) * mm, "end": v(-35.88, 73.24) * mm});
            skLineSegment(sketch, "E3387", {"start": v(-35.88, 73.24) * mm, "end": v(-36.1, 74.87) * mm});
            skLineSegment(sketch, "E3388", {"start": v(-36.1, 74.87) * mm, "end": v(-36.2, 76.33) * mm});
            skLineSegment(sketch, "E3389", {"start": v(-36.2, 76.33) * mm, "end": v(-36.25, 77.62) * mm});
            skLineSegment(sketch, "E3390", {"start": v(-36.25, 77.62) * mm, "end": v(-36.25, 77.9) * mm});
            skLineSegment(sketch, "E3391", {"start": v(-36.25, 77.9) * mm, "end": v(-36.25, 78.04) * mm});
            skLineSegment(sketch, "E3392", {"start": v(-36.25, 78.04) * mm, "end": v(-36.24, 78.29) * mm});
            skLineSegment(sketch, "E3393", {"start": v(-36.24, 78.29) * mm, "end": v(-36.23, 79.44) * mm});
            skLineSegment(sketch, "E3394", {"start": v(-36.23, 79.44) * mm, "end": v(-36.24, 84.11) * mm});
            skLineSegment(sketch, "E3395", {"start": v(-36.24, 84.11) * mm, "end": v(-36.37, 88.84) * mm});
            skLineSegment(sketch, "E3396", {"start": v(-36.37, 88.84) * mm, "end": v(-36.7, 93.55) * mm});
            skLineSegment(sketch, "E3397", {"start": v(-36.7, 93.55) * mm, "end": v(-36.98, 95.89) * mm});
            skLineSegment(sketch, "E3398", {"start": v(-36.98, 95.89) * mm, "end": v(-37.33, 98.2) * mm});
            skLineSegment(sketch, "E3399", {"start": v(-37.33, 98.2) * mm, "end": v(-37.78, 100.49) * mm});
            skLineSegment(sketch, "E3400", {"start": v(-37.78, 100.49) * mm, "end": v(-38.33, 102.73) * mm});
            skLineSegment(sketch, "E3401", {"start": v(-38.33, 102.73) * mm, "end": v(-39, 104.93) * mm});
            skLineSegment(sketch, "E3402", {"start": v(-39, 104.93) * mm, "end": v(-39.79, 107.08) * mm});
            skLineSegment(sketch, "E3403", {"start": v(-39.79, 107.08) * mm, "end": v(-40.7, 109.17) * mm});
            skLineSegment(sketch, "E3404", {"start": v(-40.7, 109.17) * mm, "end": v(-41.77, 111.2) * mm});
            skLineSegment(sketch, "E3405", {"start": v(-41.77, 111.2) * mm, "end": v(-42.34, 112.14) * mm});
            skLineSegment(sketch, "E3406", {"start": v(-42.34, 112.14) * mm, "end": v(-42.58, 112.52) * mm});
            skLineSegment(sketch, "E3407", {"start": v(-42.58, 112.52) * mm, "end": v(-43.08, 113.27) * mm});
            skLineSegment(sketch, "E3408", {"start": v(-43.08, 113.27) * mm, "end": v(-44.13, 114.69) * mm});
            skLineSegment(sketch, "E3409", {"start": v(-44.13, 114.69) * mm, "end": v(-45.25, 116) * mm});
            skLineSegment(sketch, "E3410", {"start": v(-45.25, 116) * mm, "end": v(-46.45, 117.23) * mm});
            skLineSegment(sketch, "E3411", {"start": v(-46.45, 117.23) * mm, "end": v(-47.73, 118.38) * mm});
            skLineSegment(sketch, "E3412", {"start": v(-47.73, 118.38) * mm, "end": v(-49.1, 119.44) * mm});
            skLineSegment(sketch, "E3413", {"start": v(-49.1, 119.44) * mm, "end": v(-50.55, 120.44) * mm});
            skLineSegment(sketch, "E3414", {"start": v(-50.55, 120.44) * mm, "end": v(-52.1, 121.36) * mm});
            skLineSegment(sketch, "E3415", {"start": v(-52.1, 121.36) * mm, "end": v(-53.82, 122.15) * mm});
            skLineSegment(sketch, "E3416", {"start": v(-53.82, 122.15) * mm, "end": v(-55.68, 122.74) * mm});
            skLineSegment(sketch, "E3417", {"start": v(-55.68, 122.74) * mm, "end": v(-57.62, 123.12) * mm});
            skLineSegment(sketch, "E3418", {"start": v(-57.62, 123.12) * mm, "end": v(-59.6, 123.27) * mm});
            skLineSegment(sketch, "E3419", {"start": v(-59.6, 123.27) * mm, "end": v(-61.54, 123.18) * mm});
            skLineSegment(sketch, "E3420", {"start": v(-61.54, 123.18) * mm, "end": v(-62.5, 123.04) * mm});
            skLineSegment(sketch, "E3421", {"start": v(-62.5, 123.04) * mm, "end": v(-63.42, 122.83) * mm});
            skLineSegment(sketch, "E3422", {"start": v(-63.42, 122.83) * mm, "end": v(-64.3, 122.55) * mm});
            skLineSegment(sketch, "E3423", {"start": v(-64.3, 122.55) * mm, "end": v(-65.16, 122.2) * mm});
            skLineSegment(sketch, "E3424", {"start": v(-65.16, 122.2) * mm, "end": v(-65.57, 122) * mm});
            skLineSegment(sketch, "E3425", {"start": v(-65.57, 122) * mm, "end": v(-65.65, 121.97) * mm});
            skLineSegment(sketch, "E3426", {"start": v(-65.65, 121.97) * mm, "end": v(-65.7, 122.04) * mm});
            skLineSegment(sketch, "E3427", {"start": v(-65.7, 122.04) * mm, "end": v(-65.77, 122.17) * mm});
            skLineSegment(sketch, "E3428", {"start": v(-65.77, 122.17) * mm, "end": v(-66.17, 122.68) * mm});
            skLineSegment(sketch, "E3429", {"start": v(-66.17, 122.68) * mm, "end": v(-66.66, 123.17) * mm});
            skLineSegment(sketch, "E3430", {"start": v(-66.66, 123.17) * mm, "end": v(-67.24, 123.63) * mm});
            skLineSegment(sketch, "E3431", {"start": v(-67.24, 123.63) * mm, "end": v(-67.9, 124.06) * mm});
            skLineSegment(sketch, "E3432", {"start": v(-67.9, 124.06) * mm, "end": v(-68.63, 124.46) * mm});
            skLineSegment(sketch, "E3433", {"start": v(-68.63, 124.46) * mm, "end": v(-69.43, 124.8) * mm});
            skLineSegment(sketch, "E3434", {"start": v(-69.43, 124.8) * mm, "end": v(-70.28, 125.1) * mm});
            skLineSegment(sketch, "E3435", {"start": v(-70.28, 125.1) * mm, "end": v(-71.18, 125.34) * mm});
            skLineSegment(sketch, "E3436", {"start": v(-71.18, 125.34) * mm, "end": v(-72.12, 125.52) * mm});
            skLineSegment(sketch, "E3437", {"start": v(-72.12, 125.52) * mm, "end": v(-73.1, 125.63) * mm});
            skLineSegment(sketch, "E3438", {"start": v(-73.1, 125.63) * mm, "end": v(-74.1, 125.66) * mm});
            skLineSegment(sketch, "E3439", {"start": v(-74.1, 125.66) * mm, "end": v(-75.11, 125.6) * mm});
            skLineSegment(sketch, "E3440", {"start": v(-75.11, 125.6) * mm, "end": v(-76.14, 125.46) * mm});
            skLineSegment(sketch, "E3441", {"start": v(-76.14, 125.46) * mm, "end": v(-77.17, 125.22) * mm});
            skLineSegment(sketch, "E3442", {"start": v(-77.17, 125.22) * mm, "end": v(-77.68, 125.06) * mm});
            skLineSegment(sketch, "E3443", {"start": v(-77.68, 125.06) * mm, "end": v(-77.8, 125.02) * mm});
            skLineSegment(sketch, "E3444", {"start": v(-77.8, 125.02) * mm, "end": v(-77.79, 125.01) * mm});
            skLineSegment(sketch, "E3445", {"start": v(-77.79, 125.01) * mm, "end": v(-77.68, 125) * mm});
            skLineSegment(sketch, "E3446", {"start": v(-77.68, 125) * mm, "end": v(-77.2, 124.94) * mm});
            skLineSegment(sketch, "E3447", {"start": v(-77.2, 124.94) * mm, "end": v(-76.68, 124.8) * mm});
            skLineSegment(sketch, "E3448", {"start": v(-76.68, 124.8) * mm, "end": v(-76.12, 124.58) * mm});
            skLineSegment(sketch, "E3449", {"start": v(-76.12, 124.58) * mm, "end": v(-75.52, 124.3) * mm});
            skLineSegment(sketch, "E3450", {"start": v(-75.52, 124.3) * mm, "end": v(-74.28, 123.57) * mm});
            skLineSegment(sketch, "E3451", {"start": v(-74.28, 123.57) * mm, "end": v(-73.03, 122.66) * mm});
            skLineSegment(sketch, "E3452", {"start": v(-73.03, 122.66) * mm, "end": v(-71.88, 121.61) * mm});
            skLineSegment(sketch, "E3453", {"start": v(-71.88, 121.61) * mm, "end": v(-70.9, 120.5) * mm});
            skLineSegment(sketch, "E3454", {"start": v(-70.9, 120.5) * mm, "end": v(-70.5, 119.92) * mm});
            skLineSegment(sketch, "E3455", {"start": v(-70.5, 119.92) * mm, "end": v(-70.18, 119.35) * mm});
            skLineSegment(sketch, "E3456", {"start": v(-70.18, 119.35) * mm, "end": v(-70.05, 119.07) * mm});
            skLineSegment(sketch, "E3457", {"start": v(-70.05, 119.07) * mm, "end": v(-70, 118.96) * mm});
            skLineSegment(sketch, "E3458", {"start": v(-70, 118.96) * mm, "end": v(-70.04, 118.96) * mm});
            skLineSegment(sketch, "E3459", {"start": v(-70.04, 118.96) * mm, "end": v(-70.17, 118.99) * mm});
            skLineSegment(sketch, "E3460", {"start": v(-70.17, 118.99) * mm, "end": v(-70.44, 119.03) * mm});
            skLineSegment(sketch, "E3461", {"start": v(-70.44, 119.03) * mm, "end": v(-71.51, 119.14) * mm});
            skLineSegment(sketch, "E3462", {"start": v(-71.51, 119.14) * mm, "end": v(-71.78, 119.15) * mm});
            skLineSegment(sketch, "E3463", {"start": v(-71.78, 119.15) * mm, "end": v(-71.92, 119.16) * mm});
            skLineSegment(sketch, "E3464", {"start": v(-71.92, 119.16) * mm, "end": v(-71.99, 119.16) * mm});
            skLineSegment(sketch, "E3465", {"start": v(-71.99, 119.16) * mm, "end": v(-72.02, 119.16) * mm});
            skLineSegment(sketch, "E3466", {"start": v(-72.02, 119.16) * mm, "end": v(-72.13, 119.16) * mm});
            skLineSegment(sketch, "E3467", {"start": v(-72.13, 119.16) * mm, "end": v(-73.06, 119.1) * mm});
            skLineSegment(sketch, "E3468", {"start": v(-73.06, 119.1) * mm, "end": v(-73.99, 118.97) * mm});
            skLineSegment(sketch, "E3469", {"start": v(-73.99, 118.97) * mm, "end": v(-74.9, 118.75) * mm});
            skLineSegment(sketch, "E3470", {"start": v(-74.9, 118.75) * mm, "end": v(-75.78, 118.46) * mm});
            skLineSegment(sketch, "E3471", {"start": v(-75.78, 118.46) * mm, "end": v(-76.64, 118.1) * mm});
            skLineSegment(sketch, "E3472", {"start": v(-76.64, 118.1) * mm, "end": v(-77.46, 117.66) * mm});
            skLineSegment(sketch, "E3473", {"start": v(-77.46, 117.66) * mm, "end": v(-78.24, 117.15) * mm});
            skLineSegment(sketch, "E3474", {"start": v(-78.24, 117.15) * mm, "end": v(-78.43, 117.02) * mm});
            skLineSegment(sketch, "E3475", {"start": v(-78.43, 117.02) * mm, "end": v(-78.52, 116.94) * mm});
            skLineSegment(sketch, "E3476", {"start": v(-78.52, 116.94) * mm, "end": v(-78.53, 116.92) * mm});
            skLineSegment(sketch, "E3477", {"start": v(-78.53, 116.92) * mm, "end": v(-78.49, 116.92) * mm});
            skLineSegment(sketch, "E3478", {"start": v(-78.49, 116.92) * mm, "end": v(-78.13, 116.92) * mm});
            skLineSegment(sketch, "E3479", {"start": v(-78.13, 116.92) * mm, "end": v(-76.7, 116.85) * mm});
            skLineSegment(sketch, "E3480", {"start": v(-76.7, 116.85) * mm, "end": v(-75.3, 116.69) * mm});
            skLineSegment(sketch, "E3481", {"start": v(-75.3, 116.69) * mm, "end": v(-73.89, 116.45) * mm});
            skLineSegment(sketch, "E3482", {"start": v(-73.89, 116.45) * mm, "end": v(-72.47, 116.14) * mm});
            skLineSegment(sketch, "E3483", {"start": v(-72.47, 116.14) * mm, "end": v(-71.1, 115.65) * mm});
            skLineSegment(sketch, "E3484", {"start": v(-71.1, 115.65) * mm, "end": v(-69.82, 114.96) * mm});
            skLineSegment(sketch, "E3485", {"start": v(-69.82, 114.96) * mm, "end": v(-69.24, 114.54) * mm});
            skLineSegment(sketch, "E3486", {"start": v(-69.24, 114.54) * mm, "end": v(-68.7, 114.06) * mm});
            skLineSegment(sketch, "E3487", {"start": v(-68.7, 114.06) * mm, "end": v(-68.22, 113.53) * mm});
            skLineSegment(sketch, "E3488", {"start": v(-68.22, 113.53) * mm, "end": v(-67.98, 113.19) * mm});
            skLineSegment(sketch, "E3489", {"start": v(-67.98, 113.19) * mm, "end": v(-67.75, 112.78) * mm});
            skLineSegment(sketch, "E3490", {"start": v(-67.75, 112.78) * mm, "end": v(-67.54, 112.3) * mm});
            skLineSegment(sketch, "E3491", {"start": v(-67.54, 112.3) * mm, "end": v(-67.39, 111.75) * mm});
            skLineSegment(sketch, "E3492", {"start": v(-67.39, 111.75) * mm, "end": v(-67.3, 111.12) * mm});
            skLineSegment(sketch, "E3493", {"start": v(-67.3, 111.12) * mm, "end": v(-67.3, 110.43) * mm});
            skLineSegment(sketch, "E3494", {"start": v(-67.3, 110.43) * mm, "end": v(-67.43, 109.66) * mm});
            skLineSegment(sketch, "E3495", {"start": v(-67.43, 109.66) * mm, "end": v(-67.68, 108.81) * mm});
            skLineSegment(sketch, "E3496", {"start": v(-67.68, 108.81) * mm, "end": v(-68.08, 107.9) * mm});
            skLineSegment(sketch, "E3497", {"start": v(-68.08, 107.9) * mm, "end": v(-68.66, 106.9) * mm});
            skLineSegment(sketch, "E3498", {"start": v(-68.66, 106.9) * mm, "end": v(-69.43, 105.8) * mm});
            skLineSegment(sketch, "E3499", {"start": v(-69.43, 105.8) * mm, "end": v(-70.42, 104.65) * mm});
            skLineSegment(sketch, "E3500", {"start": v(-70.42, 104.65) * mm, "end": v(-71.64, 103.4) * mm});
            skLineSegment(sketch, "E3501", {"start": v(-71.64, 103.4) * mm, "end": v(-72.34, 102.75) * mm});
            skLineSegment(sketch, "E3502", {"start": v(-72.34, 102.75) * mm, "end": v(-73.12, 102.08) * mm});
            skLineSegment(sketch, "E3503", {"start": v(-73.12, 102.08) * mm, "end": v(-74.2, 101.1) * mm});
            skLineSegment(sketch, "E3504", {"start": v(-74.2, 101.1) * mm, "end": v(-75.14, 100) * mm});
            skLineSegment(sketch, "E3505", {"start": v(-75.14, 100) * mm, "end": v(-75.53, 99.4) * mm});
            skLineSegment(sketch, "E3506", {"start": v(-75.53, 99.4) * mm, "end": v(-75.85, 98.77) * mm});
            skLineSegment(sketch, "E3507", {"start": v(-75.85, 98.77) * mm, "end": v(-76.08, 98.1) * mm});
            skLineSegment(sketch, "E3508", {"start": v(-76.08, 98.1) * mm, "end": v(-76.2, 97.4) * mm});
            skLineSegment(sketch, "E3509", {"start": v(-76.2, 97.4) * mm, "end": v(-76.18, 96.67) * mm});
            skLineSegment(sketch, "E3510", {"start": v(-76.18, 96.67) * mm, "end": v(-76.03, 95.95) * mm});
            skLineSegment(sketch, "E3511", {"start": v(-76.03, 95.95) * mm, "end": v(-75.76, 95.28) * mm});
            skLineSegment(sketch, "E3512", {"start": v(-75.76, 95.28) * mm, "end": v(-75.37, 94.68) * mm});
            skLineSegment(sketch, "E3513", {"start": v(-75.37, 94.68) * mm, "end": v(-74.87, 94.19) * mm});
            skLineSegment(sketch, "E3514", {"start": v(-74.87, 94.19) * mm, "end": v(-74.29, 93.83) * mm});
            skLineSegment(sketch, "E3515", {"start": v(-74.29, 93.83) * mm, "end": v(-73.61, 93.63) * mm});
            skLineSegment(sketch, "E3516", {"start": v(-73.61, 93.63) * mm, "end": v(-73.46, 92.9) * mm});
            skLineSegment(sketch, "E3517", {"start": v(-73.46, 92.9) * mm, "end": v(-73.15, 92.16) * mm});
            skLineSegment(sketch, "E3518", {"start": v(-73.15, 92.16) * mm, "end": v(-72.68, 91.48) * mm});
            skLineSegment(sketch, "E3519", {"start": v(-72.68, 91.48) * mm, "end": v(-72.08, 90.86) * mm});
            skLineSegment(sketch, "E3520", {"start": v(-72.08, 90.86) * mm, "end": v(-71.4, 90.32) * mm});
            skLineSegment(sketch, "E3521", {"start": v(-71.4, 90.32) * mm, "end": v(-70.65, 89.88) * mm});
            skLineSegment(sketch, "E3522", {"start": v(-70.65, 89.88) * mm, "end": v(-69.87, 89.54) * mm});
            skLineSegment(sketch, "E3523", {"start": v(-69.87, 89.54) * mm, "end": v(-69.09, 89.33) * mm});
            skLineSegment(sketch, "E3524", {"start": v(-69.09, 89.33) * mm, "end": v(-68.17, 89.25) * mm});
            skLineSegment(sketch, "E3525", {"start": v(-68.17, 89.25) * mm, "end": v(-67.15, 89.32) * mm});
            skLineSegment(sketch, "E3526", {"start": v(-67.15, 89.32) * mm, "end": v(-66.07, 89.53) * mm});
            skLineSegment(sketch, "E3527", {"start": v(-66.07, 89.53) * mm, "end": v(-64.99, 89.87) * mm});
            skLineSegment(sketch, "E3528", {"start": v(-64.99, 89.87) * mm, "end": v(-63.96, 90.33) * mm});
            skLineSegment(sketch, "E3529", {"start": v(-63.96, 90.33) * mm, "end": v(-63.03, 90.9) * mm});
            skLineSegment(sketch, "E3530", {"start": v(-63.03, 90.9) * mm, "end": v(-62.26, 91.59) * mm});
            skLineSegment(sketch, "E3531", {"start": v(-62.26, 91.59) * mm, "end": v(-62.16, 91.7) * mm});
            skLineSegment(sketch, "E3532", {"start": v(-62.16, 91.7) * mm, "end": v(-61.83, 92.08) * mm});
            skLineSegment(sketch, "E3533", {"start": v(-61.83, 92.08) * mm, "end": v(-61.24, 92.86) * mm});
            skLineSegment(sketch, "E3534", {"start": v(-61.24, 92.86) * mm, "end": v(-60.25, 94.42) * mm});
            skLineSegment(sketch, "E3535", {"start": v(-60.25, 94.42) * mm, "end": v(-59.5, 95.99) * mm});
            skLineSegment(sketch, "E3536", {"start": v(-59.5, 95.99) * mm, "end": v(-58.98, 97.55) * mm});
            skLineSegment(sketch, "E3537", {"start": v(-58.98, 97.55) * mm, "end": v(-58.66, 99.1) * mm});
            skLineSegment(sketch, "E3538", {"start": v(-58.66, 99.1) * mm, "end": v(-58.52, 100.6) * mm});
            skLineSegment(sketch, "E3539", {"start": v(-58.52, 100.6) * mm, "end": v(-58.52, 102.08) * mm});
            skLineSegment(sketch, "E3540", {"start": v(-58.52, 102.08) * mm, "end": v(-58.66, 103.5) * mm});
            skLineSegment(sketch, "E3541", {"start": v(-58.66, 103.5) * mm, "end": v(-58.89, 104.86) * mm});
            skLineSegment(sketch, "E3542", {"start": v(-58.89, 104.86) * mm, "end": v(-59.2, 106.14) * mm});
            skLineSegment(sketch, "E3543", {"start": v(-59.2, 106.14) * mm, "end": v(-59.56, 107.34) * mm});
            skLineSegment(sketch, "E3544", {"start": v(-59.56, 107.34) * mm, "end": v(-59.95, 108.44) * mm});
            skLineSegment(sketch, "E3545", {"start": v(-59.95, 108.44) * mm, "end": v(-60.34, 109.43) * mm});
            skLineSegment(sketch, "E3546", {"start": v(-60.34, 109.43) * mm, "end": v(-60.71, 110.3) * mm});
            skLineSegment(sketch, "E3547", {"start": v(-60.71, 110.3) * mm, "end": v(-61.04, 111.04) * mm});
            skLineSegment(sketch, "E3548", {"start": v(-61.04, 111.04) * mm, "end": v(-61.1, 111.2) * mm});
            skLineSegment(sketch, "E3549", {"start": v(-61.1, 111.2) * mm, "end": v(-61.12, 111.22) * mm});
            skLineSegment(sketch, "E3550", {"start": v(-61.12, 111.22) * mm, "end": v(-61.11, 111.22) * mm});
            skLineSegment(sketch, "E3551", {"start": v(-61.11, 111.22) * mm, "end": v(-61.07, 111.15) * mm});
            skLineSegment(sketch, "E3552", {"start": v(-61.07, 111.15) * mm, "end": v(-60.9, 110.88) * mm});
            skLineSegment(sketch, "E3553", {"start": v(-60.9, 110.88) * mm, "end": v(-60.59, 110.35) * mm});
            skLineSegment(sketch, "E3554", {"start": v(-60.59, 110.35) * mm, "end": v(-59.47, 108.27) * mm});
            skLineSegment(sketch, "E3555", {"start": v(-59.47, 108.27) * mm, "end": v(-58.6, 106.28) * mm});
            skLineSegment(sketch, "E3556", {"start": v(-58.6, 106.28) * mm, "end": v(-57.97, 104.37) * mm});
            skLineSegment(sketch, "E3557", {"start": v(-57.97, 104.37) * mm, "end": v(-57.56, 102.53) * mm});
            skLineSegment(sketch, "E3558", {"start": v(-57.56, 102.53) * mm, "end": v(-57.36, 100.77) * mm});
            skLineSegment(sketch, "E3559", {"start": v(-57.36, 100.77) * mm, "end": v(-57.36, 99.07) * mm});
            skLineSegment(sketch, "E3560", {"start": v(-57.36, 99.07) * mm, "end": v(-57.53, 97.44) * mm});
            skLineSegment(sketch, "E3561", {"start": v(-57.53, 97.44) * mm, "end": v(-57.88, 95.86) * mm});
            skLineSegment(sketch, "E3562", {"start": v(-57.88, 95.86) * mm, "end": v(-58.39, 94.34) * mm});
            skLineSegment(sketch, "E3563", {"start": v(-58.39, 94.34) * mm, "end": v(-59.04, 92.87) * mm});
            skLineSegment(sketch, "E3564", {"start": v(-59.04, 92.87) * mm, "end": v(-59.82, 91.44) * mm});
            skLineSegment(sketch, "E3565", {"start": v(-59.82, 91.44) * mm, "end": v(-60.72, 90.05) * mm});
            skLineSegment(sketch, "E3566", {"start": v(-60.72, 90.05) * mm, "end": v(-61.72, 88.7) * mm});
            skLineSegment(sketch, "E3567", {"start": v(-61.72, 88.7) * mm, "end": v(-62.82, 87.38) * mm});
            skLineSegment(sketch, "E3568", {"start": v(-62.82, 87.38) * mm, "end": v(-63.99, 86.1) * mm});
            skLineSegment(sketch, "E3569", {"start": v(-63.99, 86.1) * mm, "end": v(-66.52, 83.57) * mm});
            skLineSegment(sketch, "E3570", {"start": v(-66.52, 83.57) * mm, "end": v(-71.95, 78.66) * mm});
            skLineSegment(sketch, "E3571", {"start": v(-71.95, 78.66) * mm, "end": v(-74.65, 76.2) * mm});
            skLineSegment(sketch, "E3572", {"start": v(-74.65, 76.2) * mm, "end": v(-77.19, 73.7) * mm});
            skLineSegment(sketch, "E3573", {"start": v(-77.19, 73.7) * mm, "end": v(-78.36, 72.4) * mm});
            skLineSegment(sketch, "E3574", {"start": v(-78.36, 72.4) * mm, "end": v(-79.47, 71.1) * mm});
            skLineSegment(sketch, "E3575", {"start": v(-79.47, 71.1) * mm, "end": v(-80.48, 69.75) * mm});
            skLineSegment(sketch, "E3576", {"start": v(-80.48, 69.75) * mm, "end": v(-81.38, 68.38) * mm});
            skLineSegment(sketch, "E3577", {"start": v(-81.38, 68.38) * mm, "end": v(-81.8, 67.67) * mm});
            skLineSegment(sketch, "E3578", {"start": v(-81.8, 67.67) * mm, "end": v(-82.14, 67.03) * mm});
            skLineSegment(sketch, "E3579", {"start": v(-82.14, 67.03) * mm, "end": v(-82.74, 65.85) * mm});
            skLineSegment(sketch, "E3580", {"start": v(-82.74, 65.85) * mm, "end": v(-83.8, 63.5) * mm});
            skLineSegment(sketch, "E3581", {"start": v(-83.8, 63.5) * mm, "end": v(-84.7, 61.2) * mm});
            skLineSegment(sketch, "E3582", {"start": v(-84.7, 61.2) * mm, "end": v(-85.4, 58.91) * mm});
            skLineSegment(sketch, "E3583", {"start": v(-85.4, 58.91) * mm, "end": v(-85.94, 56.66) * mm});
            skLineSegment(sketch, "E3584", {"start": v(-85.94, 56.66) * mm, "end": v(-86.29, 54.42) * mm});
            skLineSegment(sketch, "E3585", {"start": v(-86.29, 54.42) * mm, "end": v(-86.45, 52.21) * mm});
            skLineSegment(sketch, "E3586", {"start": v(-86.45, 52.21) * mm, "end": v(-86.44, 50.02) * mm});
            skLineSegment(sketch, "E3587", {"start": v(-86.44, 50.02) * mm, "end": v(-86.25, 47.85) * mm});
            skLineSegment(sketch, "E3588", {"start": v(-86.25, 47.85) * mm, "end": v(-85.87, 45.7) * mm});
            skLineSegment(sketch, "E3589", {"start": v(-85.87, 45.7) * mm, "end": v(-85.32, 43.55) * mm});
            skLineSegment(sketch, "E3590", {"start": v(-85.32, 43.55) * mm, "end": v(-84.58, 41.42) * mm});
            skLineSegment(sketch, "E3591", {"start": v(-84.58, 41.42) * mm, "end": v(-83.67, 39.3) * mm});
            skLineSegment(sketch, "E3592", {"start": v(-83.67, 39.3) * mm, "end": v(-82.57, 37.19) * mm});
            skLineSegment(sketch, "E3593", {"start": v(-82.57, 37.19) * mm, "end": v(-81.29, 35.08) * mm});
            skLineSegment(sketch, "E3594", {"start": v(-81.29, 35.08) * mm, "end": v(-80.94, 34.55) * mm});
            skLineSegment(sketch, "E3595", {"start": v(-80.94, 34.55) * mm, "end": v(-80.76, 34.29) * mm});
            skLineSegment(sketch, "E3596", {"start": v(-80.76, 34.29) * mm, "end": v(-80.64, 34.1) * mm});
            skLineSegment(sketch, "E3597", {"start": v(-80.64, 34.1) * mm, "end": v(-80.47, 33.86) * mm});
            skLineSegment(sketch, "E3598", {"start": v(-80.47, 33.86) * mm, "end": v(-79, 31.96) * mm});
            skLineSegment(sketch, "E3599", {"start": v(-79, 31.96) * mm, "end": v(-77.4, 30.15) * mm});
            skLineSegment(sketch, "E3600", {"start": v(-77.4, 30.15) * mm, "end": v(-75.66, 28.44) * mm});
            skLineSegment(sketch, "E3601", {"start": v(-75.66, 28.44) * mm, "end": v(-73.8, 26.8) * mm});
            skLineSegment(sketch, "E3602", {"start": v(-73.8, 26.8) * mm, "end": v(-71.84, 25.22) * mm});
            skLineSegment(sketch, "E3603", {"start": v(-71.84, 25.22) * mm, "end": v(-69.79, 23.7) * mm});
            skLineSegment(sketch, "E3604", {"start": v(-69.79, 23.7) * mm, "end": v(-67.66, 22.21) * mm});
            skLineSegment(sketch, "E3605", {"start": v(-67.66, 22.21) * mm, "end": v(-63.23, 19.32) * mm});
            skLineSegment(sketch, "E3606", {"start": v(-63.23, 19.32) * mm, "end": v(-58.65, 16.46) * mm});
            skLineSegment(sketch, "E3607", {"start": v(-58.65, 16.46) * mm, "end": v(-54.05, 13.53) * mm});
            skLineSegment(sketch, "E3608", {"start": v(-54.05, 13.53) * mm, "end": v(-49.52, 10.44) * mm});
            skLineSegment(sketch, "E3609", {"start": v(-49.52, 10.44) * mm, "end": v(-47.32, 8.8) * mm});
            skLineSegment(sketch, "E3610", {"start": v(-47.32, 8.8) * mm, "end": v(-45.18, 7.09) * mm});
            skLineSegment(sketch, "E3611", {"start": v(-45.18, 7.09) * mm, "end": v(-43.1, 5.3) * mm});
            skLineSegment(sketch, "E3612", {"start": v(-43.1, 5.3) * mm, "end": v(-41.13, 3.4) * mm});
            skLineSegment(sketch, "E3613", {"start": v(-41.13, 3.4) * mm, "end": v(-39.25, 1.39) * mm});
            skLineSegment(sketch, "E3614", {"start": v(-39.25, 1.39) * mm, "end": v(-37.5, -0.74) * mm});
            skLineSegment(sketch, "E3615", {"start": v(-37.5, -0.74) * mm, "end": v(-35.86, -3) * mm});
            skLineSegment(sketch, "E3616", {"start": v(-35.86, -3) * mm, "end": v(-34.37, -5.41) * mm});
            skLineSegment(sketch, "E3617", {"start": v(-34.37, -5.41) * mm, "end": v(-33.03, -7.98) * mm});
            skLineSegment(sketch, "E3618", {"start": v(-33.03, -7.98) * mm, "end": v(-31.87, -10.71) * mm});
            skLineSegment(sketch, "E3619", {"start": v(-31.87, -10.71) * mm, "end": v(-30.89, -13.63) * mm});
            skLineSegment(sketch, "E3620", {"start": v(-30.89, -13.63) * mm, "end": v(-30.47, -15.16) * mm});
            skLineSegment(sketch, "E3621", {"start": v(-30.47, -15.16) * mm, "end": v(-30.1, -16.74) * mm});
            skLineSegment(sketch, "E3622", {"start": v(-30.1, -16.74) * mm, "end": v(-29.8, -18.37) * mm});
            skLineSegment(sketch, "E3623", {"start": v(-29.8, -18.37) * mm, "end": v(-29.53, -20.05) * mm});
            skLineSegment(sketch, "E3624", {"start": v(-29.53, -20.05) * mm, "end": v(-29.33, -21.78) * mm});
            skLineSegment(sketch, "E3625", {"start": v(-29.33, -21.78) * mm, "end": v(-29.18, -23.57) * mm});
            skLineSegment(sketch, "E3626", {"start": v(-29.18, -23.57) * mm, "end": v(-29.1, -25.42) * mm});
            skLineSegment(sketch, "E3627", {"start": v(-29.1, -25.42) * mm, "end": v(-29.08, -26.36) * mm});
            skLineSegment(sketch, "E3628", {"start": v(-29.08, -26.36) * mm, "end": v(-29.08, -26.84) * mm});
            skLineSegment(sketch, "E3629", {"start": v(-29.08, -26.84) * mm, "end": v(-29.07, -27.08) * mm});
            skLineSegment(sketch, "E3630", {"start": v(-29.07, -27.08) * mm, "end": v(-29.1, -27.1) * mm});
            skLineSegment(sketch, "E3631", {"start": v(-29.1, -27.1) * mm, "end": v(-29.4, -27.13) * mm});
            skLineSegment(sketch, "E3632", {"start": v(-29.4, -27.13) * mm, "end": v(-30.11, -27.24) * mm});
            skLineSegment(sketch, "E3633", {"start": v(-30.11, -27.24) * mm, "end": v(-30.91, -27.42) * mm});
            skLineSegment(sketch, "E3634", {"start": v(-30.91, -27.42) * mm, "end": v(-31.79, -27.68) * mm});
            skLineSegment(sketch, "E3635", {"start": v(-31.79, -27.68) * mm, "end": v(-32.72, -28) * mm});
            skLineSegment(sketch, "E3636", {"start": v(-32.72, -28) * mm, "end": v(-33.7, -28.4) * mm});
            skLineSegment(sketch, "E3637", {"start": v(-33.7, -28.4) * mm, "end": v(-34.7, -28.89) * mm});
            skLineSegment(sketch, "E3638", {"start": v(-34.7, -28.89) * mm, "end": v(-35.72, -29.45) * mm});
            skLineSegment(sketch, "E3639", {"start": v(-35.72, -29.45) * mm, "end": v(-36.74, -30.08) * mm});
            skLineSegment(sketch, "E3640", {"start": v(-36.74, -30.08) * mm, "end": v(-37.73, -30.8) * mm});
            skLineSegment(sketch, "E3641", {"start": v(-37.73, -30.8) * mm, "end": v(-38.68, -31.6) * mm});
            skLineSegment(sketch, "E3642", {"start": v(-38.68, -31.6) * mm, "end": v(-39.58, -32.49) * mm});
            skLineSegment(sketch, "E3643", {"start": v(-39.58, -32.49) * mm, "end": v(-40.42, -33.46) * mm});
            skLineSegment(sketch, "E3644", {"start": v(-40.42, -33.46) * mm, "end": v(-41.16, -34.51) * mm});
            skLineSegment(sketch, "E3645", {"start": v(-41.16, -34.51) * mm, "end": v(-41.8, -35.66) * mm});
            skLineSegment(sketch, "E3646", {"start": v(-41.8, -35.66) * mm, "end": v(-42.09, -36.26) * mm});
            skLineSegment(sketch, "E3647", {"start": v(-42.09, -36.26) * mm, "end": v(-42.1, -36.3) * mm});
            skLineSegment(sketch, "E3648", {"start": v(-42.1, -36.3) * mm, "end": v(-42.08, -36.27) * mm});
            skLineSegment(sketch, "E3649", {"start": v(-42.08, -36.27) * mm, "end": v(-42.02, -36.22) * mm});
            skLineSegment(sketch, "E3650", {"start": v(-42.02, -36.22) * mm, "end": v(-41.91, -36.13) * mm});
            skLineSegment(sketch, "E3651", {"start": v(-41.91, -36.13) * mm, "end": v(-41.7, -35.93) * mm});
            skLineSegment(sketch, "E3652", {"start": v(-41.7, -35.93) * mm, "end": v(-40.87, -35.21) * mm});
            skLineSegment(sketch, "E3653", {"start": v(-40.87, -35.21) * mm, "end": v(-40.07, -34.57) * mm});
            skLineSegment(sketch, "E3654", {"start": v(-40.07, -34.57) * mm, "end": v(-38.5, -33.5) * mm});
            skLineSegment(sketch, "E3655", {"start": v(-38.5, -33.5) * mm, "end": v(-36.93, -32.67) * mm});
            skLineSegment(sketch, "E3656", {"start": v(-36.93, -32.67) * mm, "end": v(-35.26, -32.05) * mm});
            skLineSegment(sketch, "E3657", {"start": v(-35.26, -32.05) * mm, "end": v(-33.42, -31.6) * mm});
            skLineSegment(sketch, "E3658", {"start": v(-33.42, -31.6) * mm, "end": v(-32.42, -31.41) * mm});
            skLineSegment(sketch, "E3659", {"start": v(-32.42, -31.41) * mm, "end": v(-31.35, -31.26) * mm});
            skLineSegment(sketch, "E3660", {"start": v(-31.35, -31.26) * mm, "end": v(-30.2, -31.12) * mm});
            skLineSegment(sketch, "E3661", {"start": v(-30.2, -31.12) * mm, "end": v(-28.95, -31) * mm});
            skLineSegment(sketch, "E3662", {"start": v(-28.95, -31) * mm, "end": v(-28.3, -30.95) * mm});
            skLineSegment(sketch, "E3663", {"start": v(-28.3, -30.95) * mm, "end": v(-28.2, -30.95) * mm});
            skLineSegment(sketch, "E3664", {"start": v(-28.2, -30.95) * mm, "end": v(-28.18, -30.95) * mm});
            skLineSegment(sketch, "E3665", {"start": v(-28.18, -30.95) * mm, "end": v(-28.2, -30.97) * mm});
            skLineSegment(sketch, "E3666", {"start": v(-28.2, -30.97) * mm, "end": v(-28.25, -31.02) * mm});
            skLineSegment(sketch, "E3667", {"start": v(-28.25, -31.02) * mm, "end": v(-28.44, -31.2) * mm});
            skLineSegment(sketch, "E3668", {"start": v(-28.44, -31.2) * mm, "end": v(-29.17, -31.97) * mm});
            skLineSegment(sketch, "E3669", {"start": v(-29.17, -31.97) * mm, "end": v(-29.85, -32.84) * mm});
            skLineSegment(sketch, "E3670", {"start": v(-29.85, -32.84) * mm, "end": v(-30.45, -33.81) * mm});
            skLineSegment(sketch, "E3671", {"start": v(-30.45, -33.81) * mm, "end": v(-30.6, -34.07) * mm});
            skLineSegment(sketch, "E3672", {"start": v(-30.6, -34.07) * mm, "end": v(-30.66, -34.2) * mm});
            skLineSegment(sketch, "E3673", {"start": v(-30.66, -34.2) * mm, "end": v(-30.68, -34.24) * mm});
            skLineSegment(sketch, "E3674", {"start": v(-30.68, -34.24) * mm, "end": v(-30.55, -34.1) * mm});
            skLineSegment(sketch, "E3675", {"start": v(-30.55, -34.1) * mm, "end": v(-30.25, -33.8) * mm});
            skLineSegment(sketch, "E3676", {"start": v(-30.25, -33.8) * mm, "end": v(-29.76, -33.35) * mm});
            skLineSegment(sketch, "E3677", {"start": v(-29.76, -33.35) * mm, "end": v(-29.1, -32.81) * mm});
            skLineSegment(sketch, "E3678", {"start": v(-29.1, -32.81) * mm, "end": v(-28.28, -32.22) * mm});
            skLineSegment(sketch, "E3679", {"start": v(-28.28, -32.22) * mm, "end": v(-27.3, -31.6) * mm});
            skLineSegment(sketch, "E3680", {"start": v(-27.3, -31.6) * mm, "end": v(-26.15, -31.02) * mm});
            skLineSegment(sketch, "E3681", {"start": v(-26.15, -31.02) * mm, "end": v(-25.84, -30.88) * mm});
            skLineSegment(sketch, "E3682", {"start": v(-25.84, -30.88) * mm, "end": v(-25.7, -30.82) * mm});
            skLineSegment(sketch, "E3683", {"start": v(-25.7, -30.82) * mm, "end": v(-25.66, -30.82) * mm});
            skLineSegment(sketch, "E3684", {"start": v(-25.66, -30.82) * mm, "end": v(-25.5, -30.83) * mm});
            skLineSegment(sketch, "E3685", {"start": v(-25.5, -30.83) * mm, "end": v(-25.19, -30.83) * mm});
            skLineSegment(sketch, "E3686", {"start": v(-25.19, -30.83) * mm, "end": v(-23.93, -30.9) * mm});
            skLineSegment(sketch, "E3687", {"start": v(-23.93, -30.9) * mm, "end": v(-23.63, -30.93) * mm});
            skLineSegment(sketch, "E3688", {"start": v(-23.63, -30.93) * mm, "end": v(-23.47, -30.95) * mm});
            skLineSegment(sketch, "E3689", {"start": v(-23.47, -30.95) * mm, "end": v(-23.4, -30.96) * mm});
            skLineSegment(sketch, "E3690", {"start": v(-23.4, -30.96) * mm, "end": v(-23.36, -30.96) * mm});
            skLineSegment(sketch, "E3691", {"start": v(-23.36, -30.96) * mm, "end": v(-23.46, -31.02) * mm});
            skLineSegment(sketch, "E3692", {"start": v(-23.46, -31.02) * mm, "end": v(-24.3, -31.53) * mm});
            skLineSegment(sketch, "E3693", {"start": v(-24.3, -31.53) * mm, "end": v(-25.17, -32.12) * mm});
            skLineSegment(sketch, "E3694", {"start": v(-25.17, -32.12) * mm, "end": v(-26, -32.8) * mm});
            skLineSegment(sketch, "E3695", {"start": v(-26, -32.8) * mm, "end": v(-26.78, -33.61) * mm});
            skLineSegment(sketch, "E3696", {"start": v(-26.78, -33.61) * mm, "end": v(-27.48, -34.56) * mm});
            skLineSegment(sketch, "E3697", {"start": v(-27.48, -34.56) * mm, "end": v(-28.07, -35.67) * mm});
            skLineSegment(sketch, "E3698", {"start": v(-28.07, -35.67) * mm, "end": v(-28.15, -35.9) * mm});
            skLineSegment(sketch, "E3699", {"start": v(-26.64, -35.8) * mm, "end": v(-25.4, -34.91) * mm});
            skLineSegment(sketch, "E3700", {"start": v(-25.4, -34.91) * mm, "end": v(-24.18, -34.16) * mm});
            skLineSegment(sketch, "E3701", {"start": v(-24.18, -34.16) * mm, "end": v(-22.92, -33.54) * mm});
            skLineSegment(sketch, "E3702", {"start": v(-22.92, -33.54) * mm, "end": v(-21.58, -33.04) * mm});
            skLineSegment(sketch, "E3703", {"start": v(-21.58, -33.04) * mm, "end": v(-20.15, -32.63) * mm});
            skLineSegment(sketch, "E3704", {"start": v(-20.15, -32.63) * mm, "end": v(-19.37, -32.46) * mm});
            skLineSegment(sketch, "E3705", {"start": v(-19.37, -32.46) * mm, "end": v(-18.98, -32.38) * mm});
            skLineSegment(sketch, "E3706", {"start": v(-18.98, -32.38) * mm, "end": v(-18.77, -32.35) * mm});
            skLineSegment(sketch, "E3707", {"start": v(-18.77, -32.35) * mm, "end": v(-18.67, -32.33) * mm});
            skLineSegment(sketch, "E3708", {"start": v(-18.67, -32.33) * mm, "end": v(-18.63, -32.34) * mm});
            skLineSegment(sketch, "E3709", {"start": v(-18.63, -32.34) * mm, "end": v(-18.12, -32.62) * mm});
            skLineSegment(sketch, "E3710", {"start": v(-18.12, -32.62) * mm, "end": v(-17.18, -33.26) * mm});
            skLineSegment(sketch, "E3711", {"start": v(-17.18, -33.26) * mm, "end": v(-16.33, -33.99) * mm});
            skLineSegment(sketch, "E3712", {"start": v(-16.33, -33.99) * mm, "end": v(-15.6, -34.82) * mm});
            skLineSegment(sketch, "E3713", {"start": v(-15.6, -34.82) * mm, "end": v(-15.43, -35.02) * mm});
            skLineSegment(sketch, "E3714", {"start": v(-15.43, -35.02) * mm, "end": v(-15.43, -34.79) * mm});
            skLineSegment(sketch, "E3715", {"start": v(-15.43, -34.79) * mm, "end": v(-15.45, -34.34) * mm});
            skLineSegment(sketch, "E3716", {"start": v(-15.45, -34.34) * mm, "end": v(-15.57, -33.5) * mm});
            skLineSegment(sketch, "E3717", {"start": v(-15.57, -33.5) * mm, "end": v(-15.78, -32.71) * mm});
            skLineSegment(sketch, "E3718", {"start": v(-15.78, -32.71) * mm, "end": v(-16.1, -31.98) * mm});
            skLineSegment(sketch, "E3719", {"start": v(-16.1, -31.98) * mm, "end": v(-14.94, -31.87) * mm});
            skLineSegment(sketch, "E3720", {"start": v(-14.94, -31.87) * mm, "end": v(-14.34, -31.82) * mm});
            skLineSegment(sketch, "E3721", {"start": v(-14.34, -31.82) * mm, "end": v(-14.03, -31.8) * mm});
            skLineSegment(sketch, "E3722", {"start": v(-14.03, -31.8) * mm, "end": v(-13.87, -31.79) * mm});
            skLineSegment(sketch, "E3723", {"start": v(-13.87, -31.79) * mm, "end": v(-12.92, -31.73) * mm});
            skLineSegment(sketch, "E3724", {"start": v(-12.92, -31.73) * mm, "end": v(-10.97, -31.69) * mm});
            skLineSegment(sketch, "E3725", {"start": v(-10.97, -31.69) * mm, "end": v(-9.13, -31.77) * mm});
            skLineSegment(sketch, "E3726", {"start": v(-9.13, -31.77) * mm, "end": v(-7.4, -32.02) * mm});
            skLineSegment(sketch, "E3727", {"start": v(-7.4, -32.02) * mm, "end": v(-5.81, -32.44) * mm});
            skLineSegment(sketch, "E3728", {"start": v(-5.81, -32.44) * mm, "end": v(-5.08, -32.73) * mm});
            skLineSegment(sketch, "E3729", {"start": v(-5.08, -32.73) * mm, "end": v(-4.39, -33.08) * mm});
            skLineSegment(sketch, "E3730", {"start": v(-4.39, -33.08) * mm, "end": v(-3.74, -33.48) * mm});
            skLineSegment(sketch, "E3731", {"start": v(-3.74, -33.48) * mm, "end": v(-3.14, -33.94) * mm});
            skLineSegment(sketch, "E3732", {"start": v(-3.14, -33.94) * mm, "end": v(-2.6, -34.47) * mm});
            skLineSegment(sketch, "E3733", {"start": v(-2.6, -34.47) * mm, "end": v(-2.1, -35.07) * mm});
            skLineSegment(sketch, "E3734", {"start": v(-2.1, -35.07) * mm, "end": v(-2.04, -35.14) * mm});
            skLineSegment(sketch, "E3735", {"start": v(-2.04, -35.14) * mm, "end": v(-2.04, -34.98) * mm});
            skLineSegment(sketch, "E3736", {"start": v(-2.04, -34.98) * mm, "end": v(-2.05, -34.68) * mm});
            skLineSegment(sketch, "E3737", {"start": v(-2.05, -34.68) * mm, "end": v(-2.09, -34.1) * mm});
            skLineSegment(sketch, "E3738", {"start": v(-2.09, -34.1) * mm, "end": v(-2.3, -33.02) * mm});
            skLineSegment(sketch, "E3739", {"start": v(-2.3, -33.02) * mm, "end": v(-2.67, -32.03) * mm});
            skLineSegment(sketch, "E3740", {"start": v(-2.67, -32.03) * mm, "end": v(-3.17, -31.14) * mm});
            skLineSegment(sketch, "E3741", {"start": v(-3.17, -31.14) * mm, "end": v(-3.78, -30.35) * mm});
            skLineSegment(sketch, "E3742", {"start": v(-3.78, -30.35) * mm, "end": v(-4.48, -29.66) * mm});
            skLineSegment(sketch, "E3743", {"start": v(-4.48, -29.66) * mm, "end": v(-5.23, -29.05) * mm});
            skLineSegment(sketch, "E3744", {"start": v(-5.23, -29.05) * mm, "end": v(-6.03, -28.53) * mm});
            skLineSegment(sketch, "E3745", {"start": v(-6.03, -28.53) * mm, "end": v(-6.85, -28.1) * mm});
            skLineSegment(sketch, "E3746", {"start": v(-6.85, -28.1) * mm, "end": v(-7.67, -27.76) * mm});
            skLineSegment(sketch, "E3747", {"start": v(-7.67, -27.76) * mm, "end": v(-8.45, -27.49) * mm});
            skLineSegment(sketch, "E3748", {"start": v(-8.45, -27.49) * mm, "end": v(-9.19, -27.3) * mm});
            skLineSegment(sketch, "E3749", {"start": v(-9.19, -27.3) * mm, "end": v(-9.86, -27.18) * mm});
            skLineSegment(sketch, "E3750", {"start": v(-9.86, -27.18) * mm, "end": v(-10.43, -27.14) * mm});
            skLineSegment(sketch, "E3751", {"start": v(-10.43, -27.14) * mm, "end": v(-10.88, -27.17) * mm});
            skLineSegment(sketch, "E3752", {"start": v(-10.88, -27.17) * mm, "end": v(-10.95, -27.15) * mm});
            skLineSegment(sketch, "E3753", {"start": v(-10.95, -27.15) * mm, "end": v(-10.97, -27.04) * mm});
            skLineSegment(sketch, "E3754", {"start": v(-10.97, -27.04) * mm, "end": v(-11, -26.75) * mm});
            skLineSegment(sketch, "E3755", {"start": v(-11, -26.75) * mm, "end": v(-11.06, -25.99) * mm});
            skLineSegment(sketch, "E3756", {"start": v(-11.06, -25.99) * mm, "end": v(-11.1, -25) * mm});
            skLineSegment(sketch, "E3757", {"start": v(-11.1, -25) * mm, "end": v(-11.15, -23.82) * mm});
            skLineSegment(sketch, "E3758", {"start": v(-11.15, -23.82) * mm, "end": v(-11.18, -22.5) * mm});
            skLineSegment(sketch, "E3759", {"start": v(-11.18, -22.5) * mm, "end": v(-11.23, -19.63) * mm});
            skLineSegment(sketch, "E3760", {"start": v(-11.23, -19.63) * mm, "end": v(-11.27, -16.74) * mm});
            skLineSegment(sketch, "E3761", {"start": v(-11.27, -16.74) * mm, "end": v(-11.28, -15.4) * mm});
            skLineSegment(sketch, "E3762", {"start": v(-11.28, -15.4) * mm, "end": v(-11.28, -14.19) * mm});
            skLineSegment(sketch, "E3763", {"start": v(-11.28, -14.19) * mm, "end": v(-11.29, -13.14) * mm});
            skLineSegment(sketch, "E3764", {"start": v(-11.29, -13.14) * mm, "end": v(-11.29, -12.31) * mm});
            skLineSegment(sketch, "E3765", {"start": v(-11.29, -12.31) * mm, "end": v(-11.29, -12) * mm});
            skLineSegment(sketch, "E3766", {"start": v(-11.29, -12) * mm, "end": v(-11.28, -11.75) * mm});
            skLineSegment(sketch, "E3767", {"start": v(-11.28, -11.75) * mm, "end": v(-11.28, -11.57) * mm});
            skLineSegment(sketch, "E3768", {"start": v(-11.28, -11.57) * mm, "end": v(-11.28, -11.48) * mm});
            skLineSegment(sketch, "E3769", {"start": v(-11.28, -11.48) * mm, "end": v(-11.27, -11.47) * mm});
            skLineSegment(sketch, "E3770", {"start": v(-11.27, -11.47) * mm, "end": v(-11.16, -11.45) * mm});
            skLineSegment(sketch, "E3771", {"start": v(-11.16, -11.45) * mm, "end": v(-10.92, -11.4) * mm});
            skLineSegment(sketch, "E3772", {"start": v(-10.92, -11.4) * mm, "end": v(-10.44, -11.3) * mm});
            skLineSegment(sketch, "E3773", {"start": v(-10.44, -11.3) * mm, "end": v(-9.44, -11) * mm});
            skLineSegment(sketch, "E3774", {"start": v(-9.44, -11) * mm, "end": v(-8.44, -10.57) * mm});
            skLineSegment(sketch, "E3775", {"start": v(-8.44, -10.57) * mm, "end": v(-7.45, -10) * mm});
            skLineSegment(sketch, "E3776", {"start": v(-7.45, -10) * mm, "end": v(-6.5, -9.28) * mm});
            skLineSegment(sketch, "E3777", {"start": v(-6.5, -9.28) * mm, "end": v(-5.63, -8.36) * mm});
            skLineSegment(sketch, "E3778", {"start": v(-5.63, -8.36) * mm, "end": v(-4.85, -7.24) * mm});
            skLineSegment(sketch, "E3779", {"start": v(-4.85, -7.24) * mm, "end": v(-4.5, -6.6) * mm});
            skLineSegment(sketch, "E3780", {"start": v(-4.5, -6.6) * mm, "end": v(-4.42, -6.43) * mm});
            skLineSegment(sketch, "E3781", {"start": v(-4.42, -6.43) * mm, "end": v(-4.41, -6.4) * mm});
            skLineSegment(sketch, "E3782", {"start": v(-4.41, -6.4) * mm, "end": v(-4.42, -6.42) * mm});
            skLineSegment(sketch, "E3783", {"start": v(-4.42, -6.42) * mm, "end": v(-4.5, -6.46) * mm});
            skLineSegment(sketch, "E3784", {"start": v(-4.5, -6.46) * mm, "end": v(-4.63, -6.55) * mm});
            skLineSegment(sketch, "E3785", {"start": v(-4.63, -6.55) * mm, "end": v(-5.09, -6.8) * mm});
            skLineSegment(sketch, "E3786", {"start": v(-5.09, -6.8) * mm, "end": v(-5.78, -7.13) * mm});
            skLineSegment(sketch, "E3787", {"start": v(-5.78, -7.13) * mm, "end": v(-6.72, -7.5) * mm});
            skLineSegment(sketch, "E3788", {"start": v(-6.72, -7.5) * mm, "end": v(-7.9, -7.84) * mm});
            skLineSegment(sketch, "E3789", {"start": v(-7.9, -7.84) * mm, "end": v(-9.32, -8.13) * mm});
            skLineSegment(sketch, "E3790", {"start": v(-9.32, -8.13) * mm, "end": v(-10.97, -8.31) * mm});
            skLineSegment(sketch, "E3791", {"start": v(-10.97, -8.31) * mm, "end": v(-11.2, -8.33) * mm});
            skLineSegment(sketch, "E3792", {"start": v(-11.2, -8.33) * mm, "end": v(-11.26, -8.33) * mm});
            skLineSegment(sketch, "E3793", {"start": v(-11.26, -8.33) * mm, "end": v(-11.28, -8.33) * mm});
            skLineSegment(sketch, "E3794", {"start": v(-11.28, -8.33) * mm, "end": v(-11.29, -8.27) * mm});
            skLineSegment(sketch, "E3795", {"start": v(-11.29, -8.27) * mm, "end": v(-11.25, -7.95) * mm});
            skLineSegment(sketch, "E3796", {"start": v(-11.25, -7.95) * mm, "end": v(-11.07, -6.66) * mm});
            skLineSegment(sketch, "E3797", {"start": v(-11.07, -6.66) * mm, "end": v(-10.52, -4.15) * mm});
            skLineSegment(sketch, "E3798", {"start": v(-10.52, -4.15) * mm, "end": v(-9.74, -1.72) * mm});
            skLineSegment(sketch, "E3799", {"start": v(-9.74, -1.72) * mm, "end": v(-8.76, 0.62) * mm});
            skLineSegment(sketch, "E3800", {"start": v(-8.76, 0.62) * mm, "end": v(-7.63, 2.86) * mm});
            skLineSegment(sketch, "E3801", {"start": v(-7.63, 2.86) * mm, "end": v(-6.37, 5.02) * mm});
            skLineSegment(sketch, "E3802", {"start": v(-6.37, 5.02) * mm, "end": v(-5.01, 7.07) * mm});
            skLineSegment(sketch, "E3803", {"start": v(-5.01, 7.07) * mm, "end": v(-3.6, 9.03) * mm});
            skLineSegment(sketch, "E3804", {"start": v(-3.6, 9.03) * mm, "end": v(-2.15, 10.89) * mm});
            skLineSegment(sketch, "E3805", {"start": v(-2.15, 10.89) * mm, "end": v(-0.71, 12.64) * mm});
            skLineSegment(sketch, "E3806", {"start": v(-0.71, 12.64) * mm, "end": v(0.68, 14.29) * mm});
            skLineSegment(sketch, "E3807", {"start": v(0.68, 14.29) * mm, "end": v(2, 15.83) * mm});
            skLineSegment(sketch, "E3808", {"start": v(2, 15.83) * mm, "end": v(3.23, 17.26) * mm});
            skLineSegment(sketch, "E3809", {"start": v(3.23, 17.26) * mm, "end": v(4.3, 18.58) * mm});
            skLineSegment(sketch, "E3810", {"start": v(4.3, 18.58) * mm, "end": v(5.22, 19.78) * mm});
            skLineSegment(sketch, "E3811", {"start": v(5.22, 19.78) * mm, "end": v(6.03, 20.82) * mm});
            skLineSegment(sketch, "E3812", {"start": v(6.03, 20.82) * mm, "end": v(7.64, 22.85) * mm});
            skLineSegment(sketch, "E3813", {"start": v(7.64, 22.85) * mm, "end": v(9.08, 24.96) * mm});
            skLineSegment(sketch, "E3814", {"start": v(9.08, 24.96) * mm, "end": v(10.29, 27.15) * mm});
            skLineSegment(sketch, "E3815", {"start": v(10.29, 27.15) * mm, "end": v(10.8, 28.28) * mm});
            skLineSegment(sketch, "E3816", {"start": v(10.8, 28.28) * mm, "end": v(11.22, 29.43) * mm});
            skLineSegment(sketch, "E3817", {"start": v(11.22, 29.43) * mm, "end": v(11.58, 30.6) * mm});
            skLineSegment(sketch, "E3818", {"start": v(11.58, 30.6) * mm, "end": v(11.84, 31.79) * mm});
            skLineSegment(sketch, "E3819", {"start": v(11.84, 31.79) * mm, "end": v(12, 33) * mm});
            skLineSegment(sketch, "E3820", {"start": v(12, 33) * mm, "end": v(12.08, 34.22) * mm});
            skLineSegment(sketch, "E3821", {"start": v(12.08, 34.22) * mm, "end": v(12.05, 35.46) * mm});
            skLineSegment(sketch, "E3822", {"start": v(12.05, 35.46) * mm, "end": v(11.9, 36.73) * mm});
            skLineSegment(sketch, "E3823", {"start": v(11.9, 36.73) * mm, "end": v(11.85, 37.05) * mm});
            skLineSegment(sketch, "E3824", {"start": v(11.85, 37.05) * mm, "end": v(11.82, 37.2) * mm});
            skLineSegment(sketch, "E3825", {"start": v(11.82, 37.2) * mm, "end": v(11.8, 37.29) * mm});
            skLineSegment(sketch, "E3826", {"start": v(11.8, 37.29) * mm, "end": v(11.8, 37.31) * mm});
            skLineSegment(sketch, "E3827", {"start": v(11.8, 37.31) * mm, "end": v(12.07, 37.05) * mm});
            skLineSegment(sketch, "E3828", {"start": v(12.07, 37.05) * mm, "end": v(12.57, 36.5) * mm});
            skLineSegment(sketch, "E3829", {"start": v(12.57, 36.5) * mm, "end": v(13.5, 35.35) * mm});
            skLineSegment(sketch, "E3830", {"start": v(13.5, 35.35) * mm, "end": v(14.31, 34.1) * mm});
            skLineSegment(sketch, "E3831", {"start": v(14.31, 34.1) * mm, "end": v(15.01, 32.8) * mm});
            skLineSegment(sketch, "E3832", {"start": v(15.01, 32.8) * mm, "end": v(15.6, 31.43) * mm});
            skLineSegment(sketch, "E3833", {"start": v(15.6, 31.43) * mm, "end": v(16.04, 30.01) * mm});
            skLineSegment(sketch, "E3834", {"start": v(16.04, 30.01) * mm, "end": v(16.36, 28.56) * mm});
            skLineSegment(sketch, "E3835", {"start": v(16.36, 28.56) * mm, "end": v(16.54, 27.1) * mm});
            skLineSegment(sketch, "E3836", {"start": v(16.54, 27.1) * mm, "end": v(16.56, 25.6) * mm});
            skLineSegment(sketch, "E3837", {"start": v(16.56, 25.6) * mm, "end": v(16.43, 24.07) * mm});
            skLineSegment(sketch, "E3838", {"start": v(16.43, 24.07) * mm, "end": v(16.16, 22.55) * mm});
            skLineSegment(sketch, "E3839", {"start": v(16.16, 22.55) * mm, "end": v(15.78, 21.04) * mm});
            skLineSegment(sketch, "E3840", {"start": v(15.78, 21.04) * mm, "end": v(15.3, 19.56) * mm});
            skLineSegment(sketch, "E3841", {"start": v(15.3, 19.56) * mm, "end": v(14.75, 18.11) * mm});
            skLineSegment(sketch, "E3842", {"start": v(14.75, 18.11) * mm, "end": v(14.14, 16.73) * mm});
            skLineSegment(sketch, "E3843", {"start": v(14.14, 16.73) * mm, "end": v(13.98, 16.39) * mm});
            skLineSegment(sketch, "E3844", {"start": v(13.98, 16.39) * mm, "end": v(13.95, 16.31) * mm});
            skLineSegment(sketch, "E3845", {"start": v(13.95, 16.31) * mm, "end": v(13.93, 16.29) * mm});
            skLineSegment(sketch, "E3846", {"start": v(13.93, 16.29) * mm, "end": v(13.88, 16.18) * mm});
            skLineSegment(sketch, "E3847", {"start": v(13.88, 16.18) * mm, "end": v(13.5, 15.36) * mm});
            skLineSegment(sketch, "E3848", {"start": v(13.5, 15.36) * mm, "end": v(13.3, 14.95) * mm});
            skLineSegment(sketch, "E3849", {"start": v(13.3, 14.95) * mm, "end": v(13.25, 14.84) * mm});
            skLineSegment(sketch, "E3850", {"start": v(13.25, 14.84) * mm, "end": v(13.22, 14.8) * mm});
            skLineSegment(sketch, "E3851", {"start": v(13.22, 14.8) * mm, "end": v(13.22, 14.78) * mm});
            skLineSegment(sketch, "E3852", {"start": v(13.22, 14.78) * mm, "end": v(13.37, 14.84) * mm});
            skLineSegment(sketch, "E3853", {"start": v(13.37, 14.84) * mm, "end": v(13.75, 15) * mm});
            skLineSegment(sketch, "E3854", {"start": v(13.75, 15) * mm, "end": v(15.24, 15.68) * mm});
            skLineSegment(sketch, "E3855", {"start": v(15.24, 15.68) * mm, "end": v(16.68, 16.47) * mm});
            skLineSegment(sketch, "E3856", {"start": v(16.68, 16.47) * mm, "end": v(18.06, 17.35) * mm});
            skLineSegment(sketch, "E3857", {"start": v(18.06, 17.35) * mm, "end": v(19.38, 18.32) * mm});
            skLineSegment(sketch, "E3858", {"start": v(19.38, 18.32) * mm, "end": v(20.64, 19.38) * mm});
            skLineSegment(sketch, "E3859", {"start": v(20.64, 19.38) * mm, "end": v(21.82, 20.52) * mm});
            skLineSegment(sketch, "E3860", {"start": v(21.82, 20.52) * mm, "end": v(22.93, 21.73) * mm});
            skLineSegment(sketch, "E3861", {"start": v(22.93, 21.73) * mm, "end": v(23.96, 23.01) * mm});
            skLineSegment(sketch, "E3862", {"start": v(23.96, 23.01) * mm, "end": v(24.91, 24.36) * mm});
            skLineSegment(sketch, "E3863", {"start": v(24.91, 24.36) * mm, "end": v(25.77, 25.76) * mm});
            skLineSegment(sketch, "E3864", {"start": v(25.77, 25.76) * mm, "end": v(26.54, 27.22) * mm});
            skLineSegment(sketch, "E3865", {"start": v(26.54, 27.22) * mm, "end": v(27.2, 28.72) * mm});
            skLineSegment(sketch, "E3866", {"start": v(27.2, 28.72) * mm, "end": v(27.78, 30.27) * mm});
            skLineSegment(sketch, "E3867", {"start": v(27.78, 30.27) * mm, "end": v(28.24, 31.85) * mm});
            skLineSegment(sketch, "E3868", {"start": v(28.24, 31.85) * mm, "end": v(28.6, 33.46) * mm});
            skLineSegment(sketch, "E3869", {"start": v(28.6, 33.46) * mm, "end": v(28.84, 35.1) * mm});
            skLineSegment(sketch, "E3870", {"start": v(28.84, 35.1) * mm, "end": v(28.98, 36.75) * mm});
            skLineSegment(sketch, "E3871", {"start": v(28.98, 36.75) * mm, "end": v(29.03, 38.4) * mm});
            skLineSegment(sketch, "E3872", {"start": v(29.03, 38.4) * mm, "end": v(28.97, 40.07) * mm});
            skLineSegment(sketch, "E3873", {"start": v(28.97, 40.07) * mm, "end": v(28.82, 41.72) * mm});
            skLineSegment(sketch, "E3874", {"start": v(28.82, 41.72) * mm, "end": v(28.56, 43.36) * mm});
            skLineSegment(sketch, "E3875", {"start": v(28.56, 43.36) * mm, "end": v(28.2, 44.98) * mm});
            skLineSegment(sketch, "E3876", {"start": v(28.2, 44.98) * mm, "end": v(27.74, 46.57) * mm});
            skLineSegment(sketch, "E3877", {"start": v(27.74, 46.57) * mm, "end": v(27.19, 48.12) * mm});
            skLineSegment(sketch, "E3878", {"start": v(27.19, 48.12) * mm, "end": v(26.53, 49.63) * mm});
            skLineSegment(sketch, "E3879", {"start": v(26.53, 49.63) * mm, "end": v(25.78, 51.09) * mm});
            skLineSegment(sketch, "E3880", {"start": v(25.78, 51.09) * mm, "end": v(24.92, 52.49) * mm});
            skLineSegment(sketch, "E3881", {"start": v(24.92, 52.49) * mm, "end": v(23.97, 53.82) * mm});
            skLineSegment(sketch, "E3882", {"start": v(23.97, 53.82) * mm, "end": v(22.92, 55.09) * mm});
            skLineSegment(sketch, "E3883", {"start": v(22.92, 55.09) * mm, "end": v(22.36, 55.69) * mm});
            skLineSegment(sketch, "E3884", {"start": v(22.36, 55.69) * mm, "end": v(22.07, 55.98) * mm});
            skLineSegment(sketch, "E3885", {"start": v(22.07, 55.98) * mm, "end": v(22.28, 55.88) * mm});
            skLineSegment(sketch, "E3886", {"start": v(22.28, 55.88) * mm, "end": v(24.15, 54.72) * mm});
            skLineSegment(sketch, "E3887", {"start": v(24.15, 54.72) * mm, "end": v(25.9, 53.38) * mm});
            skLineSegment(sketch, "E3888", {"start": v(25.9, 53.38) * mm, "end": v(27.49, 51.86) * mm});
            skLineSegment(sketch, "E3889", {"start": v(27.49, 51.86) * mm, "end": v(28.92, 50.18) * mm});
            skLineSegment(sketch, "E3890", {"start": v(28.92, 50.18) * mm, "end": v(30.17, 48.36) * mm});
            skLineSegment(sketch, "E3891", {"start": v(30.17, 48.36) * mm, "end": v(31.23, 46.42) * mm});
            skLineSegment(sketch, "E3892", {"start": v(31.23, 46.42) * mm, "end": v(32.08, 44.39) * mm});
            skLineSegment(sketch, "E3893", {"start": v(32.08, 44.39) * mm, "end": v(32.71, 42.27) * mm});
            skLineSegment(sketch, "E3894", {"start": v(32.71, 42.27) * mm, "end": v(33.17, 40.1) * mm});
            skLineSegment(sketch, "E3895", {"start": v(33.17, 40.1) * mm, "end": v(33.44, 37.9) * mm});
            skLineSegment(sketch, "E3896", {"start": v(33.44, 37.9) * mm, "end": v(33.51, 35.7) * mm});
            skLineSegment(sketch, "E3897", {"start": v(33.51, 35.7) * mm, "end": v(33.36, 33.51) * mm});
            skLineSegment(sketch, "E3898", {"start": v(33.36, 33.51) * mm, "end": v(32.96, 31.37) * mm});
            skLineSegment(sketch, "E3899", {"start": v(32.96, 31.37) * mm, "end": v(32.67, 30.32) * mm});
            skLineSegment(sketch, "E3900", {"start": v(32.67, 30.32) * mm, "end": v(32.31, 29.3) * mm});
            skLineSegment(sketch, "E3901", {"start": v(32.31, 29.3) * mm, "end": v(31.89, 28.3) * mm});
            skLineSegment(sketch, "E3902", {"start": v(31.89, 28.3) * mm, "end": v(31.65, 27.8) * mm});
            skLineSegment(sketch, "E3903", {"start": v(31.65, 27.8) * mm, "end": v(31.52, 27.56) * mm});
            skLineSegment(sketch, "E3904", {"start": v(31.52, 27.56) * mm, "end": v(31.46, 27.43) * mm});
            skLineSegment(sketch, "E3905", {"start": v(31.46, 27.43) * mm, "end": v(31.56, 27.53) * mm});
            skLineSegment(sketch, "E3906", {"start": v(31.56, 27.53) * mm, "end": v(32.47, 28.42) * mm});
            skLineSegment(sketch, "E3907", {"start": v(32.47, 28.42) * mm, "end": v(33.33, 29.36) * mm});
            skLineSegment(sketch, "E3908", {"start": v(33.33, 29.36) * mm, "end": v(34.13, 30.35) * mm});
            skLineSegment(sketch, "E3909", {"start": v(34.13, 30.35) * mm, "end": v(34.88, 31.39) * mm});
            skLineSegment(sketch, "E3910", {"start": v(34.88, 31.39) * mm, "end": v(35.56, 32.46) * mm});
            skLineSegment(sketch, "E3911", {"start": v(35.56, 32.46) * mm, "end": v(36.2, 33.57) * mm});
            skLineSegment(sketch, "E3912", {"start": v(36.2, 33.57) * mm, "end": v(36.76, 34.72) * mm});
            skLineSegment(sketch, "E3913", {"start": v(36.76, 34.72) * mm, "end": v(37.26, 35.9) * mm});
            skLineSegment(sketch, "E3914", {"start": v(37.26, 35.9) * mm, "end": v(37.7, 37.1) * mm});
            skLineSegment(sketch, "E3915", {"start": v(37.7, 37.1) * mm, "end": v(38.07, 38.31) * mm});
            skLineSegment(sketch, "E3916", {"start": v(38.07, 38.31) * mm, "end": v(38.38, 39.56) * mm});
            skLineSegment(sketch, "E3917", {"start": v(38.38, 39.56) * mm, "end": v(38.62, 40.81) * mm});
            skLineSegment(sketch, "E3918", {"start": v(38.62, 40.81) * mm, "end": v(38.78, 42.08) * mm});
            skLineSegment(sketch, "E3919", {"start": v(38.78, 42.08) * mm, "end": v(38.87, 43.36) * mm});
            skLineSegment(sketch, "E3920", {"start": v(38.87, 43.36) * mm, "end": v(38.9, 44.64) * mm});
            skLineSegment(sketch, "E3921", {"start": v(38.9, 44.64) * mm, "end": v(38.83, 45.91) * mm});
            skLineSegment(sketch, "E3922", {"start": v(38.83, 45.91) * mm, "end": v(38.7, 47.18) * mm});
            skLineSegment(sketch, "E3923", {"start": v(38.7, 47.18) * mm, "end": v(38.47, 48.43) * mm});
            skLineSegment(sketch, "E3924", {"start": v(38.47, 48.43) * mm, "end": v(38.18, 49.67) * mm});
            skLineSegment(sketch, "E3925", {"start": v(38.18, 49.67) * mm, "end": v(37.81, 50.9) * mm});
            skLineSegment(sketch, "E3926", {"start": v(37.81, 50.9) * mm, "end": v(37.38, 52.09) * mm});
            skLineSegment(sketch, "E3927", {"start": v(37.38, 52.09) * mm, "end": v(36.87, 53.26) * mm});
            skLineSegment(sketch, "E3928", {"start": v(36.87, 53.26) * mm, "end": v(35.68, 55.52) * mm});
            skLineSegment(sketch, "E3929", {"start": v(35.68, 55.52) * mm, "end": v(34.25, 57.64) * mm});
            skLineSegment(sketch, "E3930", {"start": v(34.25, 57.64) * mm, "end": v(32.6, 59.6) * mm});
            skLineSegment(sketch, "E3931", {"start": v(32.6, 59.6) * mm, "end": v(30.77, 61.4) * mm});
            skLineSegment(sketch, "E3932", {"start": v(30.77, 61.4) * mm, "end": v(32.48, 61.06) * mm});
            skLineSegment(sketch, "E3933", {"start": v(32.48, 61.06) * mm, "end": v(34.15, 60.6) * mm});
            skLineSegment(sketch, "E3934", {"start": v(34.15, 60.6) * mm, "end": v(35.77, 60) * mm});
            skLineSegment(sketch, "E3935", {"start": v(35.77, 60) * mm, "end": v(37.34, 59.28) * mm});
            skLineSegment(sketch, "E3936", {"start": v(37.34, 59.28) * mm, "end": v(38.85, 58.44) * mm});
            skLineSegment(sketch, "E3937", {"start": v(38.85, 58.44) * mm, "end": v(40.29, 57.5) * mm});
            skLineSegment(sketch, "E3938", {"start": v(40.29, 57.5) * mm, "end": v(41.65, 56.45) * mm});
            skLineSegment(sketch, "E3939", {"start": v(41.65, 56.45) * mm, "end": v(42.94, 55.3) * mm});
            skLineSegment(sketch, "E3940", {"start": v(42.94, 55.3) * mm, "end": v(44.15, 54.07) * mm});
            skLineSegment(sketch, "E3941", {"start": v(44.15, 54.07) * mm, "end": v(45.26, 52.75) * mm});
            skLineSegment(sketch, "E3942", {"start": v(45.26, 52.75) * mm, "end": v(46.28, 51.35) * mm});
            skLineSegment(sketch, "E3943", {"start": v(46.28, 51.35) * mm, "end": v(47.2, 49.87) * mm});
            skLineSegment(sketch, "E3944", {"start": v(47.2, 49.87) * mm, "end": v(48, 48.33) * mm});
            skLineSegment(sketch, "E3945", {"start": v(48, 48.33) * mm, "end": v(48.69, 46.73) * mm});
            skLineSegment(sketch, "E3946", {"start": v(48.69, 46.73) * mm, "end": v(49.25, 45.07) * mm});
            skLineSegment(sketch, "E3947", {"start": v(49.25, 45.07) * mm, "end": v(49.28, 44.97) * mm});
            skLineSegment(sketch, "E3948", {"start": v(49.28, 44.97) * mm, "end": v(49.29, 45.04) * mm});
            skLineSegment(sketch, "E3949", {"start": v(49.29, 45.04) * mm, "end": v(49.3, 45.17) * mm});
            skLineSegment(sketch, "E3950", {"start": v(49.3, 45.17) * mm, "end": v(49.32, 45.44) * mm});
            skLineSegment(sketch, "E3951", {"start": v(49.32, 45.44) * mm, "end": v(49.35, 45.98) * mm});
            skLineSegment(sketch, "E3952", {"start": v(49.35, 45.98) * mm, "end": v(49.36, 48.13) * mm});
            skLineSegment(sketch, "E3953", {"start": v(49.36, 48.13) * mm, "end": v(49.17, 50.28) * mm});
            skLineSegment(sketch, "E3954", {"start": v(49.17, 50.28) * mm, "end": v(48.8, 52.4) * mm});
            skLineSegment(sketch, "E3955", {"start": v(48.8, 52.4) * mm, "end": v(48.23, 54.49) * mm});
            skLineSegment(sketch, "E3956", {"start": v(48.23, 54.49) * mm, "end": v(47.49, 56.51) * mm});
            skLineSegment(sketch, "E3957", {"start": v(47.49, 56.51) * mm, "end": v(46.57, 58.46) * mm});
            skLineSegment(sketch, "E3958", {"start": v(46.57, 58.46) * mm, "end": v(45.47, 60.32) * mm});
            skLineSegment(sketch, "E3959", {"start": v(45.47, 60.32) * mm, "end": v(44.22, 62.06) * mm});
            skLineSegment(sketch, "E3960", {"start": v(44.22, 62.06) * mm, "end": v(42.8, 63.65) * mm});
            skLineSegment(sketch, "E3961", {"start": v(42.8, 63.65) * mm, "end": v(41.26, 65.1) * mm});
            skLineSegment(sketch, "E3962", {"start": v(41.26, 65.1) * mm, "end": v(39.59, 66.4) * mm});
            skLineSegment(sketch, "E3963", {"start": v(39.59, 66.4) * mm, "end": v(37.8, 67.54) * mm});
            skLineSegment(sketch, "E3964", {"start": v(37.8, 67.54) * mm, "end": v(35.92, 68.53) * mm});
            skLineSegment(sketch, "E3965", {"start": v(35.92, 68.53) * mm, "end": v(33.95, 69.37) * mm});
            skLineSegment(sketch, "E3966", {"start": v(33.95, 69.37) * mm, "end": v(32.94, 69.72) * mm});
            skLineSegment(sketch, "E3967", {"start": v(32.94, 69.72) * mm, "end": v(32.81, 69.77) * mm});
            skLineSegment(sketch, "E3968", {"start": v(32.81, 69.77) * mm, "end": v(32.8, 69.79) * mm});
            skLineSegment(sketch, "E3969", {"start": v(32.8, 69.79) * mm, "end": v(32.98, 69.82) * mm});
            skLineSegment(sketch, "E3970", {"start": v(32.98, 69.82) * mm, "end": v(33.74, 69.94) * mm});
            skLineSegment(sketch, "E3971", {"start": v(33.74, 69.94) * mm, "end": v(35.24, 70.14) * mm});
            skLineSegment(sketch, "E3972", {"start": v(35.24, 70.14) * mm, "end": v(38.24, 70.34) * mm});
            skLineSegment(sketch, "E3973", {"start": v(38.24, 70.34) * mm, "end": v(41.2, 70.3) * mm});
            skLineSegment(sketch, "E3974", {"start": v(41.2, 70.3) * mm, "end": v(44.13, 70) * mm});
            skLineSegment(sketch, "E3975", {"start": v(44.13, 70) * mm, "end": v(47.01, 69.5) * mm});
            skLineSegment(sketch, "E3976", {"start": v(47.01, 69.5) * mm, "end": v(49.84, 68.77) * mm});
            skLineSegment(sketch, "E3977", {"start": v(49.84, 68.77) * mm, "end": v(52.62, 67.83) * mm});
            skLineSegment(sketch, "E3978", {"start": v(52.62, 67.83) * mm, "end": v(55.32, 66.68) * mm});
            skLineSegment(sketch, "E3979", {"start": v(55.32, 66.68) * mm, "end": v(57.96, 65.35) * mm});
            skLineSegment(sketch, "E3980", {"start": v(57.96, 65.35) * mm, "end": v(60.52, 63.84) * mm});
            skLineSegment(sketch, "E3981", {"start": v(60.52, 63.84) * mm, "end": v(63, 62.15) * mm});
            skLineSegment(sketch, "E3982", {"start": v(63, 62.15) * mm, "end": v(65.38, 60.3) * mm});
            skLineSegment(sketch, "E3983", {"start": v(65.38, 60.3) * mm, "end": v(67.66, 58.3) * mm});
            skLineSegment(sketch, "E3984", {"start": v(67.66, 58.3) * mm, "end": v(69.84, 56.16) * mm});
            skLineSegment(sketch, "E3985", {"start": v(69.84, 56.16) * mm, "end": v(71.9, 53.88) * mm});
            skLineSegment(sketch, "E3986", {"start": v(71.9, 53.88) * mm, "end": v(72.16, 53.58) * mm});
            skLineSegment(sketch, "E3987", {"start": v(72.16, 53.58) * mm, "end": v(72.28, 53.44) * mm});
            skLineSegment(sketch, "E3988", {"start": v(72.28, 53.44) * mm, "end": v(72.34, 53.36) * mm});
            skLineSegment(sketch, "E3989", {"start": v(72.34, 53.36) * mm, "end": v(72.37, 53.32) * mm});
            skLineSegment(sketch, "E3990", {"start": v(72.37, 53.32) * mm, "end": v(72.37, 53.35) * mm});
            skLineSegment(sketch, "E3991", {"start": v(72.37, 53.35) * mm, "end": v(72.32, 53.86) * mm});
            skLineSegment(sketch, "E3992", {"start": v(72.32, 53.86) * mm, "end": v(72.18, 54.86) * mm});
            skLineSegment(sketch, "E3993", {"start": v(72.18, 54.86) * mm, "end": v(71.78, 56.85) * mm});
            skLineSegment(sketch, "E3994", {"start": v(71.78, 56.85) * mm, "end": v(71.21, 58.8) * mm});
            skLineSegment(sketch, "E3995", {"start": v(71.21, 58.8) * mm, "end": v(70.49, 60.72) * mm});
            skLineSegment(sketch, "E3996", {"start": v(70.49, 60.72) * mm, "end": v(69.62, 62.6) * mm});
            skLineSegment(sketch, "E3997", {"start": v(69.62, 62.6) * mm, "end": v(68.62, 64.43) * mm});
            skLineSegment(sketch, "E3998", {"start": v(68.62, 64.43) * mm, "end": v(67.5, 66.2) * mm});
            skLineSegment(sketch, "E3999", {"start": v(67.5, 66.2) * mm, "end": v(66.25, 67.91) * mm});
            skLineSegment(sketch, "E4000", {"start": v(66.25, 67.91) * mm, "end": v(64.9, 69.56) * mm});
            skLineSegment(sketch, "E4001", {"start": v(64.9, 69.56) * mm, "end": v(63.47, 71.14) * mm});
            skLineSegment(sketch, "E4002", {"start": v(63.47, 71.14) * mm, "end": v(61.95, 72.64) * mm});
            skLineSegment(sketch, "E4003", {"start": v(61.95, 72.64) * mm, "end": v(60.35, 74.05) * mm});
            skLineSegment(sketch, "E4004", {"start": v(60.35, 74.05) * mm, "end": v(58.7, 75.38) * mm});
            skLineSegment(sketch, "E4005", {"start": v(58.7, 75.38) * mm, "end": v(56.99, 76.6) * mm});
            skLineSegment(sketch, "E4006", {"start": v(56.99, 76.6) * mm, "end": v(55.24, 77.74) * mm});
            skLineSegment(sketch, "E4007", {"start": v(55.24, 77.74) * mm, "end": v(53.45, 78.77) * mm});
            skLineSegment(sketch, "E4008", {"start": v(53.45, 78.77) * mm, "end": v(51.62, 79.71) * mm});
            skLineSegment(sketch, "E4009", {"start": v(51.62, 79.71) * mm, "end": v(49.76, 80.57) * mm});
            skLineSegment(sketch, "E4010", {"start": v(49.76, 80.57) * mm, "end": v(47.86, 81.33) * mm});
            skLineSegment(sketch, "E4011", {"start": v(47.86, 81.33) * mm, "end": v(45.93, 82) * mm});
            skLineSegment(sketch, "E4012", {"start": v(45.93, 82) * mm, "end": v(43.97, 82.6) * mm});
            skLineSegment(sketch, "E4013", {"start": v(43.97, 82.6) * mm, "end": v(42, 83.1) * mm});
            skLineSegment(sketch, "E4014", {"start": v(42, 83.1) * mm, "end": v(40, 83.5) * mm});
            skLineSegment(sketch, "E4015", {"start": v(40, 83.5) * mm, "end": v(37.98, 83.82) * mm});
            skLineSegment(sketch, "E4016", {"start": v(37.98, 83.82) * mm, "end": v(35.95, 84.05) * mm});
            skLineSegment(sketch, "E4017", {"start": v(35.95, 84.05) * mm, "end": v(33.9, 84.19) * mm});
            skLineSegment(sketch, "E4018", {"start": v(33.9, 84.19) * mm, "end": v(31.86, 84.24) * mm});
            skLineSegment(sketch, "E4019", {"start": v(31.86, 84.24) * mm, "end": v(29.82, 84.2) * mm});
            skLineSegment(sketch, "E4020", {"start": v(29.82, 84.2) * mm, "end": v(27.77, 84.07) * mm});
            skLineSegment(sketch, "E4021", {"start": v(27.77, 84.07) * mm, "end": v(25.73, 83.86) * mm});
            skLineSegment(sketch, "E4022", {"start": v(25.73, 83.86) * mm, "end": v(25.22, 83.79) * mm});
            skLineSegment(sketch, "E4023", {"start": v(25.22, 83.79) * mm, "end": v(25.1, 83.77) * mm});
            skLineSegment(sketch, "E4024", {"start": v(25.1, 83.77) * mm, "end": v(25.03, 83.76) * mm});
            skLineSegment(sketch, "E4025", {"start": v(25.03, 83.76) * mm, "end": v(25.05, 83.78) * mm});
            skLineSegment(sketch, "E4026", {"start": v(25.05, 83.78) * mm, "end": v(25.26, 83.89) * mm});
            skLineSegment(sketch, "E4027", {"start": v(25.26, 83.89) * mm, "end": v(26.1, 84.32) * mm});
            skLineSegment(sketch, "E4028", {"start": v(26.1, 84.32) * mm, "end": v(27.84, 85.1) * mm});
            skLineSegment(sketch, "E4029", {"start": v(27.84, 85.1) * mm, "end": v(29.61, 85.8) * mm});
            skLineSegment(sketch, "E4030", {"start": v(29.61, 85.8) * mm, "end": v(31.42, 86.38) * mm});
            skLineSegment(sketch, "E4031", {"start": v(31.42, 86.38) * mm, "end": v(33.26, 86.87) * mm});
            skLineSegment(sketch, "E4032", {"start": v(33.26, 86.87) * mm, "end": v(35.13, 87.26) * mm});
            skLineSegment(sketch, "E4033", {"start": v(35.13, 87.26) * mm, "end": v(37, 87.54) * mm});
            skLineSegment(sketch, "E4034", {"start": v(37, 87.54) * mm, "end": v(38.9, 87.73) * mm});
            skLineSegment(sketch, "E4035", {"start": v(38.9, 87.73) * mm, "end": v(40.8, 87.81) * mm});
            skLineSegment(sketch, "E4036", {"start": v(40.8, 87.81) * mm, "end": v(42.7, 87.8) * mm});
            skLineSegment(sketch, "E4037", {"start": v(42.7, 87.8) * mm, "end": v(44.6, 87.68) * mm});
            skLineSegment(sketch, "E4038", {"start": v(44.6, 87.68) * mm, "end": v(46.5, 87.45) * mm});
            skLineSegment(sketch, "E4039", {"start": v(46.5, 87.45) * mm, "end": v(48.38, 87.13) * mm});
            skLineSegment(sketch, "E4040", {"start": v(48.38, 87.13) * mm, "end": v(50.23, 86.7) * mm});
            skLineSegment(sketch, "E4041", {"start": v(50.23, 86.7) * mm, "end": v(52.06, 86.16) * mm});
            skLineSegment(sketch, "E4042", {"start": v(52.06, 86.16) * mm, "end": v(53.86, 85.52) * mm});
            skLineSegment(sketch, "E4043", {"start": v(53.86, 85.52) * mm, "end": v(55.62, 84.79) * mm});
            skLineSegment(sketch, "E4044", {"start": v(55.62, 84.79) * mm, "end": v(57.34, 83.95) * mm});
            skLineSegment(sketch, "E4045", {"start": v(57.34, 83.95) * mm, "end": v(59.01, 83.03) * mm});
            skLineSegment(sketch, "E4046", {"start": v(59.01, 83.03) * mm, "end": v(60.63, 82.02) * mm});
            skLineSegment(sketch, "E4047", {"start": v(60.63, 82.02) * mm, "end": v(62.2, 80.92) * mm});
            skLineSegment(sketch, "E4048", {"start": v(62.2, 80.92) * mm, "end": v(63.7, 79.74) * mm});
            skLineSegment(sketch, "E4049", {"start": v(63.7, 79.74) * mm, "end": v(65.14, 78.49) * mm});
            skLineSegment(sketch, "E4050", {"start": v(65.14, 78.49) * mm, "end": v(66.5, 77.16) * mm});
            skLineSegment(sketch, "E4051", {"start": v(66.5, 77.16) * mm, "end": v(67.8, 75.75) * mm});
            skLineSegment(sketch, "E4052", {"start": v(67.8, 75.75) * mm, "end": v(69.03, 74.28) * mm});
            skLineSegment(sketch, "E4053", {"start": v(69.03, 74.28) * mm, "end": v(70.16, 72.75) * mm});
            skLineSegment(sketch, "E4054", {"start": v(70.16, 72.75) * mm, "end": v(71.22, 71.16) * mm});
            skLineSegment(sketch, "E4055", {"start": v(71.22, 71.16) * mm, "end": v(72.18, 69.5) * mm});
            skLineSegment(sketch, "E4056", {"start": v(72.18, 69.5) * mm, "end": v(73.05, 67.8) * mm});
            skLineSegment(sketch, "E4057", {"start": v(73.05, 67.8) * mm, "end": v(73.25, 67.36) * mm});
            skLineSegment(sketch, "E4058", {"start": v(73.25, 67.36) * mm, "end": v(73.35, 67.14) * mm});
            skLineSegment(sketch, "E4059", {"start": v(73.35, 67.14) * mm, "end": v(73.4, 67.03) * mm});
            skLineSegment(sketch, "E4060", {"start": v(73.4, 67.03) * mm, "end": v(73.42, 66.98) * mm});
            skLineSegment(sketch, "E4061", {"start": v(73.42, 66.98) * mm, "end": v(73.42, 67.04) * mm});
            skLineSegment(sketch, "E4062", {"start": v(73.42, 67.04) * mm, "end": v(73.43, 68.05) * mm});
            skLineSegment(sketch, "E4063", {"start": v(73.43, 68.05) * mm, "end": v(73.35, 70.09) * mm});
            skLineSegment(sketch, "E4064", {"start": v(73.35, 70.09) * mm, "end": v(73.16, 72.11) * mm});
            skLineSegment(sketch, "E4065", {"start": v(73.16, 72.11) * mm, "end": v(72.86, 74.13) * mm});
            skLineSegment(sketch, "E4066", {"start": v(72.86, 74.13) * mm, "end": v(72.44, 76.12) * mm});
            skLineSegment(sketch, "E4067", {"start": v(72.44, 76.12) * mm, "end": v(71.92, 78.1) * mm});
            skLineSegment(sketch, "E4068", {"start": v(71.92, 78.1) * mm, "end": v(71.3, 80.03) * mm});
            skLineSegment(sketch, "E4069", {"start": v(71.3, 80.03) * mm, "end": v(70.57, 81.93) * mm});
            skLineSegment(sketch, "E4070", {"start": v(70.57, 81.93) * mm, "end": v(69.74, 83.8) * mm});
            skLineSegment(sketch, "E4071", {"start": v(69.74, 83.8) * mm, "end": v(68.8, 85.6) * mm});
            skLineSegment(sketch, "E4072", {"start": v(68.8, 85.6) * mm, "end": v(67.79, 87.37) * mm});
            skLineSegment(sketch, "E4073", {"start": v(67.79, 87.37) * mm, "end": v(66.67, 89.07) * mm});
            skLineSegment(sketch, "E4074", {"start": v(66.67, 89.07) * mm, "end": v(65.46, 90.7) * mm});
            skLineSegment(sketch, "E4075", {"start": v(65.46, 90.7) * mm, "end": v(64.17, 92.27) * mm});
            skLineSegment(sketch, "E4076", {"start": v(64.17, 92.27) * mm, "end": v(62.78, 93.77) * mm});
            skLineSegment(sketch, "E4077", {"start": v(62.78, 93.77) * mm, "end": v(61.32, 95.18) * mm});
            skLineSegment(sketch, "E4078", {"start": v(61.32, 95.18) * mm, "end": v(59.78, 96.5) * mm});
            skLineSegment(sketch, "E4079", {"start": v(59.78, 96.5) * mm, "end": v(58.16, 97.73) * mm});
            skLineSegment(sketch, "E4080", {"start": v(58.16, 97.73) * mm, "end": v(56.48, 98.87) * mm});
            skLineSegment(sketch, "E4081", {"start": v(56.48, 98.87) * mm, "end": v(54.74, 99.91) * mm});
            skLineSegment(sketch, "E4082", {"start": v(54.74, 99.91) * mm, "end": v(52.95, 100.86) * mm});
            skLineSegment(sketch, "E4083", {"start": v(52.95, 100.86) * mm, "end": v(51.1, 101.71) * mm});
            skLineSegment(sketch, "E4084", {"start": v(51.1, 101.71) * mm, "end": v(49.22, 102.46) * mm});
            skLineSegment(sketch, "E4085", {"start": v(49.22, 102.46) * mm, "end": v(47.3, 103.1) * mm});
            skLineSegment(sketch, "E4086", {"start": v(47.3, 103.1) * mm, "end": v(45.34, 103.65) * mm});
            skLineSegment(sketch, "E4087", {"start": v(45.34, 103.65) * mm, "end": v(43.37, 104.08) * mm});
            skLineSegment(sketch, "E4088", {"start": v(43.37, 104.08) * mm, "end": v(41.37, 104.4) * mm});
            skLineSegment(sketch, "E4089", {"start": v(41.37, 104.4) * mm, "end": v(39.36, 104.62) * mm});
            skLineSegment(sketch, "E4090", {"start": v(39.36, 104.62) * mm, "end": v(37.34, 104.72) * mm});
            skLineSegment(sketch, "E4091", {"start": v(37.34, 104.72) * mm, "end": v(35.31, 104.7) * mm});
            skLineSegment(sketch, "E4092", {"start": v(35.31, 104.7) * mm, "end": v(33.3, 104.57) * mm});
            skLineSegment(sketch, "E4093", {"start": v(33.3, 104.57) * mm, "end": v(31.3, 104.32) * mm});
            skLineSegment(sketch, "E4094", {"start": v(31.3, 104.32) * mm, "end": v(29.3, 103.94) * mm});
            skLineSegment(sketch, "E4095", {"start": v(29.3, 103.94) * mm, "end": v(27.35, 103.45) * mm});
            skLineSegment(sketch, "E4096", {"start": v(27.35, 103.45) * mm, "end": v(25.42, 102.85) * mm});
            skLineSegment(sketch, "E4097", {"start": v(25.42, 102.85) * mm, "end": v(23.53, 102.14) * mm});
            skLineSegment(sketch, "E4098", {"start": v(23.53, 102.14) * mm, "end": v(21.68, 101.33) * mm});
            skLineSegment(sketch, "E4099", {"start": v(21.68, 101.33) * mm, "end": v(19.87, 100.42) * mm});
            skLineSegment(sketch, "E4100", {"start": v(19.87, 100.42) * mm, "end": v(18.12, 99.4) * mm});
            skLineSegment(sketch, "E4101", {"start": v(18.12, 99.4) * mm, "end": v(16.42, 98.3) * mm});
            skLineSegment(sketch, "E4102", {"start": v(16.42, 98.3) * mm, "end": v(14.78, 97.1) * mm});
            skLineSegment(sketch, "E4103", {"start": v(14.78, 97.1) * mm, "end": v(13.2, 95.82) * mm});
            skLineSegment(sketch, "E4104", {"start": v(13.2, 95.82) * mm, "end": v(11.7, 94.46) * mm});
            skLineSegment(sketch, "E4105", {"start": v(11.7, 94.46) * mm, "end": v(10.28, 93.02) * mm});
            skLineSegment(sketch, "E4106", {"start": v(10.28, 93.02) * mm, "end": v(8.93, 91.5) * mm});
            skLineSegment(sketch, "E4107", {"start": v(8.93, 91.5) * mm, "end": v(8.3, 90.71) * mm});
            skLineSegment(sketch, "E4108", {"start": v(8.3, 90.71) * mm, "end": v(8.14, 90.52) * mm});
            skLineSegment(sketch, "E4109", {"start": v(8.14, 90.52) * mm, "end": v(8.12, 90.5) * mm});
            skLineSegment(sketch, "E4110", {"start": v(8.12, 90.5) * mm, "end": v(8.16, 90.56) * mm});
            skLineSegment(sketch, "E4111", {"start": v(8.16, 90.56) * mm, "end": v(8.23, 90.68) * mm});
            skLineSegment(sketch, "E4112", {"start": v(8.23, 90.68) * mm, "end": v(8.54, 91.18) * mm});
            skLineSegment(sketch, "E4113", {"start": v(8.54, 91.18) * mm, "end": v(9.85, 93.1) * mm});
            skLineSegment(sketch, "E4114", {"start": v(9.85, 93.1) * mm, "end": v(11.28, 94.94) * mm});
            skLineSegment(sketch, "E4115", {"start": v(11.28, 94.94) * mm, "end": v(12.8, 96.69) * mm});
            skLineSegment(sketch, "E4116", {"start": v(12.8, 96.69) * mm, "end": v(14.43, 98.35) * mm});
            skLineSegment(sketch, "E4117", {"start": v(14.43, 98.35) * mm, "end": v(16.15, 99.91) * mm});
            skLineSegment(sketch, "E4118", {"start": v(16.15, 99.91) * mm, "end": v(17.95, 101.37) * mm});
            skLineSegment(sketch, "E4119", {"start": v(17.95, 101.37) * mm, "end": v(19.83, 102.73) * mm});
            skLineSegment(sketch, "E4120", {"start": v(19.83, 102.73) * mm, "end": v(21.79, 103.99) * mm});
            skLineSegment(sketch, "E4121", {"start": v(21.79, 103.99) * mm, "end": v(23.81, 105.13) * mm});
            skLineSegment(sketch, "E4122", {"start": v(23.81, 105.13) * mm, "end": v(25.9, 106.15) * mm});
            skLineSegment(sketch, "E4123", {"start": v(25.9, 106.15) * mm, "end": v(28.03, 107.05) * mm});
            skLineSegment(sketch, "E4124", {"start": v(28.03, 107.05) * mm, "end": v(30.21, 107.83) * mm});
            skLineSegment(sketch, "E4125", {"start": v(30.21, 107.83) * mm, "end": v(32.44, 108.47) * mm});
            skLineSegment(sketch, "E4126", {"start": v(32.44, 108.47) * mm, "end": v(34.7, 108.99) * mm});
            skLineSegment(sketch, "E4127", {"start": v(34.7, 108.99) * mm, "end": v(37, 109.37) * mm});
            skLineSegment(sketch, "E4128", {"start": v(37, 109.37) * mm, "end": v(39.3, 109.6) * mm});
            skLineSegment(sketch, "E4129", {"start": v(39.3, 109.6) * mm, "end": v(41.62, 109.7) * mm});
            skLineSegment(sketch, "E4130", {"start": v(41.62, 109.7) * mm, "end": v(43.94, 109.66) * mm});
            skLineSegment(sketch, "E4131", {"start": v(43.94, 109.66) * mm, "end": v(46.25, 109.49) * mm});
            skLineSegment(sketch, "E4132", {"start": v(46.25, 109.49) * mm, "end": v(48.55, 109.18) * mm});
            skLineSegment(sketch, "E4133", {"start": v(48.55, 109.18) * mm, "end": v(50.84, 108.74) * mm});
            skLineSegment(sketch, "E4134", {"start": v(50.84, 108.74) * mm, "end": v(53.1, 108.18) * mm});
            skLineSegment(sketch, "E4135", {"start": v(53.1, 108.18) * mm, "end": v(55.31, 107.5) * mm});
            skLineSegment(sketch, "E4136", {"start": v(55.31, 107.5) * mm, "end": v(57.5, 106.68) * mm});
            skLineSegment(sketch, "E4137", {"start": v(57.5, 106.68) * mm, "end": v(59.62, 105.74) * mm});
            skLineSegment(sketch, "E4138", {"start": v(59.62, 105.74) * mm, "end": v(61.7, 104.69) * mm});
            skLineSegment(sketch, "E4139", {"start": v(61.7, 104.69) * mm, "end": v(63.7, 103.52) * mm});
            skLineSegment(sketch, "E4140", {"start": v(63.7, 103.52) * mm, "end": v(65.65, 102.23) * mm});
            skLineSegment(sketch, "E4141", {"start": v(65.65, 102.23) * mm, "end": v(67.51, 100.83) * mm});
            skLineSegment(sketch, "E4142", {"start": v(67.51, 100.83) * mm, "end": v(68.41, 100.1) * mm});
            skLineSegment(sketch, "E4143", {"start": v(68.41, 100.1) * mm, "end": v(68.85, 99.7) * mm});
            skLineSegment(sketch, "E4144", {"start": v(68.85, 99.7) * mm, "end": v(69.03, 99.56) * mm});
            skLineSegment(sketch, "E4145", {"start": v(69.03, 99.56) * mm, "end": v(70.26, 98.42) * mm});
            skLineSegment(sketch, "E4146", {"start": v(70.26, 98.42) * mm, "end": v(71.44, 97.23) * mm});
            skLineSegment(sketch, "E4147", {"start": v(71.44, 97.23) * mm, "end": v(72.57, 96) * mm});
            skLineSegment(sketch, "E4148", {"start": v(72.57, 96) * mm, "end": v(73.65, 94.7) * mm});
            skLineSegment(sketch, "E4149", {"start": v(73.65, 94.7) * mm, "end": v(74.66, 93.38) * mm});
            skLineSegment(sketch, "E4150", {"start": v(74.66, 93.38) * mm, "end": v(75.62, 92) * mm});
            skLineSegment(sketch, "E4151", {"start": v(75.62, 92) * mm, "end": v(76.52, 90.58) * mm});
            skLineSegment(sketch, "E4152", {"start": v(76.52, 90.58) * mm, "end": v(76.73, 90.22) * mm});
            skLineSegment(sketch, "E4153", {"start": v(76.73, 90.22) * mm, "end": v(76.84, 90.04) * mm});
            skLineSegment(sketch, "E4154", {"start": v(76.84, 90.04) * mm, "end": v(77, 89.76) * mm});
            skLineSegment(sketch, "E4155", {"start": v(77, 89.76) * mm, "end": v(77.7, 88.45) * mm});
            skLineSegment(sketch, "E4156", {"start": v(77.7, 88.45) * mm, "end": v(78.94, 85.76) * mm});
            skLineSegment(sketch, "E4157", {"start": v(78.94, 85.76) * mm, "end": v(79.98, 82.98) * mm});
            skLineSegment(sketch, "E4158", {"start": v(79.98, 82.98) * mm, "end": v(80.8, 80.13) * mm});
            skLineSegment(sketch, "E4159", {"start": v(80.8, 80.13) * mm, "end": v(81.44, 77.23) * mm});
            skLineSegment(sketch, "E4160", {"start": v(81.44, 77.23) * mm, "end": v(81.88, 74.28) * mm});
            skLineSegment(sketch, "E4161", {"start": v(81.88, 74.28) * mm, "end": v(82.13, 71.32) * mm});
            skLineSegment(sketch, "E4162", {"start": v(82.13, 71.32) * mm, "end": v(82.2, 68.34) * mm});
            skLineSegment(sketch, "E4163", {"start": v(82.2, 68.34) * mm, "end": v(82.13, 65.4) * mm});
            skLineSegment(sketch, "E4164", {"start": v(82.13, 65.4) * mm, "end": v(81.92, 62.48) * mm});
            skLineSegment(sketch, "E4165", {"start": v(81.92, 62.48) * mm, "end": v(81.6, 59.6) * mm});
            skLineSegment(sketch, "E4166", {"start": v(81.6, 59.6) * mm, "end": v(81.13, 56.73) * mm});
            skLineSegment(sketch, "E4167", {"start": v(81.13, 56.73) * mm, "end": v(80.54, 53.89) * mm});
            skLineSegment(sketch, "E4168", {"start": v(80.54, 53.89) * mm, "end": v(79.82, 51.07) * mm});
            skLineSegment(sketch, "E4169", {"start": v(79.82, 51.07) * mm, "end": v(78.97, 48.26) * mm});
            skLineSegment(sketch, "E4170", {"start": v(78.97, 48.26) * mm, "end": v(78.74, 47.56) * mm});
            skLineSegment(sketch, "E4171", {"start": v(78.74, 47.56) * mm, "end": v(78.62, 47.2) * mm});
            skLineSegment(sketch, "E4172", {"start": v(78.62, 47.2) * mm, "end": v(78.56, 47.03) * mm});
            skLineSegment(sketch, "E4173", {"start": v(78.56, 47.03) * mm, "end": v(78.53, 46.94) * mm});
            skLineSegment(sketch, "E4174", {"start": v(78.53, 46.94) * mm, "end": v(78.6, 47.08) * mm});
            skLineSegment(sketch, "E4175", {"start": v(78.6, 47.08) * mm, "end": v(79.9, 49.47) * mm});
            skLineSegment(sketch, "E4176", {"start": v(79.9, 49.47) * mm, "end": v(81.07, 51.91) * mm});
            skLineSegment(sketch, "E4177", {"start": v(81.07, 51.91) * mm, "end": v(82.14, 54.41) * mm});
            skLineSegment(sketch, "E4178", {"start": v(82.14, 54.41) * mm, "end": v(83.1, 56.96) * mm});
            skLineSegment(sketch, "E4179", {"start": v(83.1, 56.96) * mm, "end": v(83.94, 59.54) * mm});
            skLineSegment(sketch, "E4180", {"start": v(83.94, 59.54) * mm, "end": v(84.66, 62.17) * mm});
            skLineSegment(sketch, "E4181", {"start": v(84.66, 62.17) * mm, "end": v(85.26, 64.82) * mm});
            skLineSegment(sketch, "E4182", {"start": v(85.26, 64.82) * mm, "end": v(85.74, 67.5) * mm});
            skLineSegment(sketch, "E4183", {"start": v(85.74, 67.5) * mm, "end": v(86.1, 70.2) * mm});
            skLineSegment(sketch, "E4184", {"start": v(86.1, 70.2) * mm, "end": v(86.34, 72.9) * mm});
            skLineSegment(sketch, "E4185", {"start": v(86.34, 72.9) * mm, "end": v(86.45, 75.62) * mm});
            skLineSegment(sketch, "E4186", {"start": v(86.45, 75.62) * mm, "end": v(86.44, 78.34) * mm});
            skLineSegment(sketch, "E4187", {"start": v(86.44, 78.34) * mm, "end": v(86.3, 81.05) * mm});
            skLineSegment(sketch, "E4188", {"start": v(86.3, 81.05) * mm, "end": v(86.02, 83.76) * mm});
            skLineSegment(sketch, "E4189", {"start": v(86.02, 83.76) * mm, "end": v(85.61, 86.45) * mm});
            skLineSegment(sketch, "E4190", {"start": v(-50.46, 124.06) * mm, "end": v(-49.17, 123.23) * mm});
            skLineSegment(sketch, "E4191", {"start": v(-49.17, 123.23) * mm, "end": v(-47.92, 122.34) * mm});
            skLineSegment(sketch, "E4192", {"start": v(-47.92, 122.34) * mm, "end": v(-46.67, 121.44) * mm});
            skLineSegment(sketch, "E4193", {"start": v(-46.67, 121.44) * mm, "end": v(-45.4, 120.6) * mm});
            skLineSegment(sketch, "E4194", {"start": v(-45.4, 120.6) * mm, "end": v(-44.74, 120.2) * mm});
            skLineSegment(sketch, "E4195", {"start": v(-44.74, 120.2) * mm, "end": v(-44.05, 119.84) * mm});
            skLineSegment(sketch, "E4196", {"start": v(-44.05, 119.84) * mm, "end": v(-43.34, 119.53) * mm});
            skLineSegment(sketch, "E4197", {"start": v(-43.34, 119.53) * mm, "end": v(-42.61, 119.26) * mm});
            skLineSegment(sketch, "E4198", {"start": v(-42.61, 119.26) * mm, "end": v(-41.87, 119.05) * mm});
            skLineSegment(sketch, "E4199", {"start": v(-41.87, 119.05) * mm, "end": v(-41.12, 118.91) * mm});
            skLineSegment(sketch, "E4200", {"start": v(-41.12, 118.91) * mm, "end": v(-40.36, 118.85) * mm});
            skLineSegment(sketch, "E4201", {"start": v(-40.36, 118.85) * mm, "end": v(-39.6, 118.87) * mm});
            skLineSegment(sketch, "E4202", {"start": v(-39.6, 118.87) * mm, "end": v(-38.86, 118.99) * mm});
            skLineSegment(sketch, "E4203", {"start": v(-38.86, 118.99) * mm, "end": v(-38.44, 119.1) * mm});
            skLineSegment(sketch, "E4204", {"start": v(-38.44, 119.1) * mm, "end": v(-38.03, 119.24) * mm});
            skLineSegment(sketch, "E4205", {"start": v(-38.03, 119.24) * mm, "end": v(-37.63, 119.41) * mm});
            skLineSegment(sketch, "E4206", {"start": v(-37.63, 119.41) * mm, "end": v(-37.25, 119.61) * mm});
            skLineSegment(sketch, "E4207", {"start": v(-37.25, 119.61) * mm, "end": v(-36.88, 119.84) * mm});
            skLineSegment(sketch, "E4208", {"start": v(-36.88, 119.84) * mm, "end": v(-36.53, 120.09) * mm});
            skLineSegment(sketch, "E4209", {"start": v(-36.53, 120.09) * mm, "end": v(-36.2, 120.36) * mm});
            skLineSegment(sketch, "E4210", {"start": v(-36.2, 120.36) * mm, "end": v(-35.87, 120.65) * mm});
            skLineSegment(sketch, "E4211", {"start": v(-35.87, 120.65) * mm, "end": v(-35.28, 121.3) * mm});
            skLineSegment(sketch, "E4212", {"start": v(-35.28, 121.3) * mm, "end": v(-34.76, 122.02) * mm});
            skLineSegment(sketch, "E4213", {"start": v(-34.76, 122.02) * mm, "end": v(-34.31, 122.78) * mm});
            skLineSegment(sketch, "E4214", {"start": v(-34.31, 122.78) * mm, "end": v(-33.95, 123.6) * mm});
            skLineSegment(sketch, "E4215", {"start": v(-33.95, 123.6) * mm, "end": v(-33.68, 124.42) * mm});
            skLineSegment(sketch, "E4216", {"start": v(-33.68, 124.42) * mm, "end": v(-33.49, 125.29) * mm});
            skLineSegment(sketch, "E4217", {"start": v(-33.49, 125.29) * mm, "end": v(-33.36, 126.17) * mm});
            skLineSegment(sketch, "E4218", {"start": v(-33.36, 126.17) * mm, "end": v(-33.3, 127.07) * mm});
            skLineSegment(sketch, "E4219", {"start": v(-33.3, 127.07) * mm, "end": v(-33.3, 127.98) * mm});
            skLineSegment(sketch, "E4220", {"start": v(-33.3, 127.98) * mm, "end": v(-33.36, 128.9) * mm});
            skLineSegment(sketch, "E4221", {"start": v(-33.36, 128.9) * mm, "end": v(-33.45, 129.8) * mm});
            skLineSegment(sketch, "E4222", {"start": v(-33.45, 129.8) * mm, "end": v(-33.58, 130.7) * mm});
            skLineSegment(sketch, "E4223", {"start": v(-33.58, 130.7) * mm, "end": v(-33.73, 131.57) * mm});
            skLineSegment(sketch, "E4224", {"start": v(-33.73, 131.57) * mm, "end": v(-33.75, 131.68) * mm});
            skLineSegment(sketch, "E4225", {"start": v(-33.75, 131.68) * mm, "end": v(-33.8, 131.58) * mm});
            skLineSegment(sketch, "E4226", {"start": v(-33.8, 131.58) * mm, "end": v(-33.92, 131.34) * mm});
            skLineSegment(sketch, "E4227", {"start": v(-33.92, 131.34) * mm, "end": v(-34.17, 130.88) * mm});
            skLineSegment(sketch, "E4228", {"start": v(-34.17, 130.88) * mm, "end": v(-34.46, 130.45) * mm});
            skLineSegment(sketch, "E4229", {"start": v(-34.46, 130.45) * mm, "end": v(-34.78, 130.04) * mm});
            skLineSegment(sketch, "E4230", {"start": v(-34.78, 130.04) * mm, "end": v(-35.12, 129.65) * mm});
            skLineSegment(sketch, "E4231", {"start": v(-35.12, 129.65) * mm, "end": v(-35.5, 129.29) * mm});
            skLineSegment(sketch, "E4232", {"start": v(-35.5, 129.29) * mm, "end": v(-35.9, 128.96) * mm});
            skLineSegment(sketch, "E4233", {"start": v(-35.9, 128.96) * mm, "end": v(-36.31, 128.65) * mm});
            skLineSegment(sketch, "E4234", {"start": v(-36.31, 128.65) * mm, "end": v(-36.75, 128.38) * mm});
            skLineSegment(sketch, "E4235", {"start": v(-36.75, 128.38) * mm, "end": v(-37.2, 128.13) * mm});
            skLineSegment(sketch, "E4236", {"start": v(-37.2, 128.13) * mm, "end": v(-37.68, 127.92) * mm});
            skLineSegment(sketch, "E4237", {"start": v(-37.68, 127.92) * mm, "end": v(-38.17, 127.74) * mm});
            skLineSegment(sketch, "E4238", {"start": v(-38.17, 127.74) * mm, "end": v(-38.67, 127.6) * mm});
            skLineSegment(sketch, "E4239", {"start": v(-38.67, 127.6) * mm, "end": v(-39.18, 127.48) * mm});
            skLineSegment(sketch, "E4240", {"start": v(-39.18, 127.48) * mm, "end": v(-39.7, 127.4) * mm});
            skLineSegment(sketch, "E4241", {"start": v(-39.7, 127.4) * mm, "end": v(-40.21, 127.37) * mm});
            skLineSegment(sketch, "E4242", {"start": v(-40.21, 127.37) * mm, "end": v(-40.74, 127.38) * mm});
            skLineSegment(sketch, "E4243", {"start": v(-40.74, 127.38) * mm, "end": v(-40.87, 127.38) * mm});
            skLineSegment(sketch, "E4244", {"start": v(-40.87, 127.38) * mm, "end": v(-40.9, 127.39) * mm});
            skLineSegment(sketch, "E4245", {"start": v(-40.9, 127.39) * mm, "end": v(-40.9, 127.4) * mm});
            skLineSegment(sketch, "E4246", {"start": v(-40.9, 127.4) * mm, "end": v(-40.86, 127.41) * mm});
            skLineSegment(sketch, "E4247", {"start": v(-40.86, 127.41) * mm, "end": v(-40.7, 127.48) * mm});
            skLineSegment(sketch, "E4248", {"start": v(-40.7, 127.48) * mm, "end": v(-40.12, 127.81) * mm});
            skLineSegment(sketch, "E4249", {"start": v(-40.12, 127.81) * mm, "end": v(-39.57, 128.21) * mm});
            skLineSegment(sketch, "E4250", {"start": v(-39.57, 128.21) * mm, "end": v(-39.06, 128.67) * mm});
            skLineSegment(sketch, "E4251", {"start": v(-39.06, 128.67) * mm, "end": v(-38.6, 129.18) * mm});
            skLineSegment(sketch, "E4252", {"start": v(-38.6, 129.18) * mm, "end": v(-38.2, 129.73) * mm});
            skLineSegment(sketch, "E4253", {"start": v(-38.2, 129.73) * mm, "end": v(-37.82, 130.31) * mm});
            skLineSegment(sketch, "E4254", {"start": v(-37.82, 130.31) * mm, "end": v(-37.5, 130.93) * mm});
            skLineSegment(sketch, "E4255", {"start": v(-37.5, 130.93) * mm, "end": v(-37.23, 131.56) * mm});
            skLineSegment(sketch, "E4256", {"start": v(-37.23, 131.56) * mm, "end": v(-37, 132.2) * mm});
            skLineSegment(sketch, "E4257", {"start": v(-37, 132.2) * mm, "end": v(-36.81, 132.83) * mm});
            skLineSegment(sketch, "E4258", {"start": v(-36.81, 132.83) * mm, "end": v(-36.65, 133.45) * mm});
            skLineSegment(sketch, "E4259", {"start": v(-36.65, 133.45) * mm, "end": v(-36.4, 134.7) * mm});
            skLineSegment(sketch, "E4260", {"start": v(-36.4, 134.7) * mm, "end": v(-36.22, 135.97) * mm});
            skLineSegment(sketch, "E4261", {"start": v(-36.22, 135.97) * mm, "end": v(-36.15, 136.63) * mm});
            skLineSegment(sketch, "E4262", {"start": v(-36.15, 136.63) * mm, "end": v(-36.12, 136.96) * mm});
            skLineSegment(sketch, "E4263", {"start": v(-36.12, 136.96) * mm, "end": v(-36.12, 137.05) * mm});
            skLineSegment(sketch, "E4264", {"start": v(-36.12, 137.05) * mm, "end": v(-36.11, 137.1) * mm});
            skLineSegment(sketch, "E4265", {"start": v(-36.11, 137.1) * mm, "end": v(-36.1, 137.11) * mm});
            skLineSegment(sketch, "E4266", {"start": v(-36.1, 137.11) * mm, "end": v(-36.1, 137.12) * mm});
            skLineSegment(sketch, "E4267", {"start": v(-36.1, 137.12) * mm, "end": v(-36.12, 137.1) * mm});
            skLineSegment(sketch, "E4268", {"start": v(-36.12, 137.1) * mm, "end": v(-36.3, 136.73) * mm});
            skLineSegment(sketch, "E4269", {"start": v(-36.3, 136.73) * mm, "end": v(-36.7, 136.03) * mm});
            skLineSegment(sketch, "E4270", {"start": v(-36.7, 136.03) * mm, "end": v(-37.14, 135.35) * mm});
            skLineSegment(sketch, "E4271", {"start": v(-37.14, 135.35) * mm, "end": v(-37.62, 134.7) * mm});
            skLineSegment(sketch, "E4272", {"start": v(-37.62, 134.7) * mm, "end": v(-38.15, 134.08) * mm});
            skLineSegment(sketch, "E4273", {"start": v(-38.15, 134.08) * mm, "end": v(-38.71, 133.49) * mm});
            skLineSegment(sketch, "E4274", {"start": v(-38.71, 133.49) * mm, "end": v(-39.31, 132.93) * mm});
            skLineSegment(sketch, "E4275", {"start": v(-39.31, 132.93) * mm, "end": v(-39.94, 132.41) * mm});
            skLineSegment(sketch, "E4276", {"start": v(-39.94, 132.41) * mm, "end": v(-40.6, 131.93) * mm});
            skLineSegment(sketch, "E4277", {"start": v(-40.6, 131.93) * mm, "end": v(-41.3, 131.49) * mm});
            skLineSegment(sketch, "E4278", {"start": v(-41.3, 131.49) * mm, "end": v(-42, 131.09) * mm});
            skLineSegment(sketch, "E4279", {"start": v(-42, 131.09) * mm, "end": v(-42.74, 130.73) * mm});
            skLineSegment(sketch, "E4280", {"start": v(-42.74, 130.73) * mm, "end": v(-43.49, 130.41) * mm});
            skLineSegment(sketch, "E4281", {"start": v(-43.49, 130.41) * mm, "end": v(-44.26, 130.15) * mm});
            skLineSegment(sketch, "E4282", {"start": v(-44.26, 130.15) * mm, "end": v(-45.04, 129.93) * mm});
            skLineSegment(sketch, "E4283", {"start": v(-45.04, 129.93) * mm, "end": v(-45.83, 129.76) * mm});
            skLineSegment(sketch, "E4284", {"start": v(-45.83, 129.76) * mm, "end": v(-46.63, 129.64) * mm});
            skLineSegment(sketch, "E4285", {"start": v(-46.63, 129.64) * mm, "end": v(-47.04, 129.6) * mm});
            skLineSegment(sketch, "E4286", {"start": v(-47.04, 129.6) * mm, "end": v(-47.06, 129.6) * mm});
            skLineSegment(sketch, "E4287", {"start": v(-47.06, 129.6) * mm, "end": v(-47.05, 129.61) * mm});
            skLineSegment(sketch, "E4288", {"start": v(-47.05, 129.61) * mm, "end": v(-47.03, 129.63) * mm});
            skLineSegment(sketch, "E4289", {"start": v(-47.03, 129.63) * mm, "end": v(-46.98, 129.68) * mm});
            skLineSegment(sketch, "E4290", {"start": v(-46.98, 129.68) * mm, "end": v(-46.88, 129.76) * mm});
            skLineSegment(sketch, "E4291", {"start": v(-46.88, 129.76) * mm, "end": v(-46.49, 130.11) * mm});
            skLineSegment(sketch, "E4292", {"start": v(-46.49, 130.11) * mm, "end": v(-46.12, 130.48) * mm});
            skLineSegment(sketch, "E4293", {"start": v(-46.12, 130.48) * mm, "end": v(-45.78, 130.87) * mm});
            skLineSegment(sketch, "E4294", {"start": v(-45.78, 130.87) * mm, "end": v(-45.46, 131.28) * mm});
            skLineSegment(sketch, "E4295", {"start": v(-45.46, 131.28) * mm, "end": v(-45.17, 131.7) * mm});
            skLineSegment(sketch, "E4296", {"start": v(-45.17, 131.7) * mm, "end": v(-44.9, 132.14) * mm});
            skLineSegment(sketch, "E4297", {"start": v(-44.9, 132.14) * mm, "end": v(-44.65, 132.6) * mm});
            skLineSegment(sketch, "E4298", {"start": v(-44.65, 132.6) * mm, "end": v(-44.44, 133.06) * mm});
            skLineSegment(sketch, "E4299", {"start": v(-44.44, 133.06) * mm, "end": v(-44.25, 133.54) * mm});
            skLineSegment(sketch, "E4300", {"start": v(-44.25, 133.54) * mm, "end": v(-44.08, 134.02) * mm});
            skLineSegment(sketch, "E4301", {"start": v(-44.08, 134.02) * mm, "end": v(-43.95, 134.52) * mm});
            skLineSegment(sketch, "E4302", {"start": v(-43.95, 134.52) * mm, "end": v(-43.84, 135.02) * mm});
            skLineSegment(sketch, "E4303", {"start": v(-43.84, 135.02) * mm, "end": v(-43.76, 135.53) * mm});
            skLineSegment(sketch, "E4304", {"start": v(-43.76, 135.53) * mm, "end": v(-43.71, 136.05) * mm});
            skLineSegment(sketch, "E4305", {"start": v(-43.71, 136.05) * mm, "end": v(-43.7, 136.57) * mm});
            skLineSegment(sketch, "E4306", {"start": v(-43.7, 136.57) * mm, "end": v(-43.7, 137.1) * mm});
            skLineSegment(sketch, "E4307", {"start": v(-43.7, 137.1) * mm, "end": v(-43.72, 137.35) * mm});
            skLineSegment(sketch, "E4308", {"start": v(-43.72, 137.35) * mm, "end": v(-43.72, 137.39) * mm});
            skLineSegment(sketch, "E4309", {"start": v(-43.72, 137.39) * mm, "end": v(-43.72, 137.4) * mm});
            skLineSegment(sketch, "E4310", {"start": v(-43.72, 137.4) * mm, "end": v(-43.73, 137.4) * mm});
            skLineSegment(sketch, "E4311", {"start": v(-43.73, 137.4) * mm, "end": v(-43.78, 137.32) * mm});
            skLineSegment(sketch, "E4312", {"start": v(-43.78, 137.32) * mm, "end": v(-43.86, 137.18) * mm});
            skLineSegment(sketch, "E4313", {"start": v(-43.86, 137.18) * mm, "end": v(-44.23, 136.63) * mm});
            skLineSegment(sketch, "E4314", {"start": v(-44.23, 136.63) * mm, "end": v(-44.62, 136.1) * mm});
            skLineSegment(sketch, "E4315", {"start": v(-44.62, 136.1) * mm, "end": v(-45.04, 135.58) * mm});
            skLineSegment(sketch, "E4316", {"start": v(-45.04, 135.58) * mm, "end": v(-45.48, 135.09) * mm});
            skLineSegment(sketch, "E4317", {"start": v(-45.48, 135.09) * mm, "end": v(-45.94, 134.62) * mm});
            skLineSegment(sketch, "E4318", {"start": v(-45.94, 134.62) * mm, "end": v(-46.43, 134.17) * mm});
            skLineSegment(sketch, "E4319", {"start": v(-46.43, 134.17) * mm, "end": v(-46.93, 133.76) * mm});
            skLineSegment(sketch, "E4320", {"start": v(-46.93, 133.76) * mm, "end": v(-47.46, 133.37) * mm});
            skLineSegment(sketch, "E4321", {"start": v(-47.46, 133.37) * mm, "end": v(-48, 133) * mm});
            skLineSegment(sketch, "E4322", {"start": v(-48, 133) * mm, "end": v(-48.56, 132.67) * mm});
            skLineSegment(sketch, "E4323", {"start": v(-48.56, 132.67) * mm, "end": v(-49.14, 132.37) * mm});
            skLineSegment(sketch, "E4324", {"start": v(-49.14, 132.37) * mm, "end": v(-49.74, 132.1) * mm});
            skLineSegment(sketch, "E4325", {"start": v(-49.74, 132.1) * mm, "end": v(-50.35, 131.88) * mm});
            skLineSegment(sketch, "E4326", {"start": v(-50.35, 131.88) * mm, "end": v(-50.97, 131.68) * mm});
            skLineSegment(sketch, "E4327", {"start": v(-50.97, 131.68) * mm, "end": v(-51.6, 131.52) * mm});
            skLineSegment(sketch, "E4328", {"start": v(-51.6, 131.52) * mm, "end": v(-52.25, 131.4) * mm});
            skLineSegment(sketch, "E4329", {"start": v(-52.25, 131.4) * mm, "end": v(-52.58, 131.36) * mm});
            skLineSegment(sketch, "E4330", {"start": v(-52.58, 131.36) * mm, "end": v(-52.66, 131.35) * mm});
            skLineSegment(sketch, "E4331", {"start": v(-52.66, 131.35) * mm, "end": v(-52.68, 131.35) * mm});
            skLineSegment(sketch, "E4332", {"start": v(-52.68, 131.35) * mm, "end": v(-52.68, 131.35) * mm});
            skLineSegment(sketch, "E4333", {"start": v(-52.68, 131.35) * mm, "end": v(-52.66, 131.36) * mm});
            skLineSegment(sketch, "E4334", {"start": v(-52.66, 131.36) * mm, "end": v(-52.56, 131.4) * mm});
            skLineSegment(sketch, "E4335", {"start": v(-52.56, 131.4) * mm, "end": v(-52.16, 131.6) * mm});
            skLineSegment(sketch, "E4336", {"start": v(-52.16, 131.6) * mm, "end": v(-51.77, 131.81) * mm});
            skLineSegment(sketch, "E4337", {"start": v(-51.77, 131.81) * mm, "end": v(-51.4, 132.05) * mm});
            skLineSegment(sketch, "E4338", {"start": v(-51.4, 132.05) * mm, "end": v(-51.04, 132.31) * mm});
            skLineSegment(sketch, "E4339", {"start": v(-51.04, 132.31) * mm, "end": v(-50.7, 132.6) * mm});
            skLineSegment(sketch, "E4340", {"start": v(-50.7, 132.6) * mm, "end": v(-50.39, 132.89) * mm});
            skLineSegment(sketch, "E4341", {"start": v(-50.39, 132.89) * mm, "end": v(-50.09, 133.2) * mm});
            skLineSegment(sketch, "E4342", {"start": v(-50.09, 133.2) * mm, "end": v(-49.81, 133.54) * mm});
            skLineSegment(sketch, "E4343", {"start": v(-49.81, 133.54) * mm, "end": v(-49.56, 133.9) * mm});
            skLineSegment(sketch, "E4344", {"start": v(-49.56, 133.9) * mm, "end": v(-49.33, 134.26) * mm});
            skLineSegment(sketch, "E4345", {"start": v(-49.33, 134.26) * mm, "end": v(-49.13, 134.64) * mm});
            skLineSegment(sketch, "E4346", {"start": v(-49.13, 134.64) * mm, "end": v(-48.95, 135.03) * mm});
            skLineSegment(sketch, "E4347", {"start": v(-48.95, 135.03) * mm, "end": v(-48.8, 135.43) * mm});
            skLineSegment(sketch, "E4348", {"start": v(-48.8, 135.43) * mm, "end": v(-48.7, 135.85) * mm});
            skLineSegment(sketch, "E4349", {"start": v(-48.7, 135.85) * mm, "end": v(-48.6, 136.28) * mm});
            skLineSegment(sketch, "E4350", {"start": v(-48.6, 136.28) * mm, "end": v(-48.55, 136.71) * mm});
            skLineSegment(sketch, "E4351", {"start": v(-48.55, 136.71) * mm, "end": v(-48.54, 136.93) * mm});
            skLineSegment(sketch, "E4352", {"start": v(-48.54, 136.93) * mm, "end": v(-48.54, 137.03) * mm});
            skLineSegment(sketch, "E4353", {"start": v(-48.54, 137.03) * mm, "end": v(-48.6, 136.96) * mm});
            skLineSegment(sketch, "E4354", {"start": v(-48.6, 136.96) * mm, "end": v(-49.2, 136.39) * mm});
            skLineSegment(sketch, "E4355", {"start": v(-49.2, 136.39) * mm, "end": v(-49.84, 135.88) * mm});
            skLineSegment(sketch, "E4356", {"start": v(-49.84, 135.88) * mm, "end": v(-50.52, 135.43) * mm});
            skLineSegment(sketch, "E4357", {"start": v(-50.52, 135.43) * mm, "end": v(-51.23, 135.03) * mm});
            skLineSegment(sketch, "E4358", {"start": v(-51.23, 135.03) * mm, "end": v(-51.98, 134.68) * mm});
            skLineSegment(sketch, "E4359", {"start": v(-51.98, 134.68) * mm, "end": v(-52.75, 134.36) * mm});
            skLineSegment(sketch, "E4360", {"start": v(-52.75, 134.36) * mm, "end": v(-54.31, 133.8) * mm});
            skLineSegment(sketch, "E4361", {"start": v(-54.31, 133.8) * mm, "end": v(-55.89, 133.3) * mm});
            skLineSegment(sketch, "E4362", {"start": v(-55.89, 133.3) * mm, "end": v(-57.46, 132.8) * mm});
            skLineSegment(sketch, "E4363", {"start": v(-57.46, 132.8) * mm, "end": v(-58.23, 132.5) * mm});
            skLineSegment(sketch, "E4364", {"start": v(-58.23, 132.5) * mm, "end": v(-58.99, 132.18) * mm});
            skLineSegment(sketch, "E4365", {"start": v(-58.99, 132.18) * mm, "end": v(-59.73, 131.83) * mm});
            skLineSegment(sketch, "E4366", {"start": v(-59.73, 131.83) * mm, "end": v(-60.44, 131.42) * mm});
            skLineSegment(sketch, "E4367", {"start": v(-60.44, 131.42) * mm, "end": v(-61.12, 130.97) * mm});
            skLineSegment(sketch, "E4368", {"start": v(-61.12, 130.97) * mm, "end": v(-61.44, 130.7) * mm});
            skLineSegment(sketch, "E4369", {"start": v(-61.44, 130.7) * mm, "end": v(-61.75, 130.42) * mm});
            skLineSegment(sketch, "E4370", {"start": v(-61.75, 130.42) * mm, "end": v(-62.32, 129.8) * mm});
            skLineSegment(sketch, "E4371", {"start": v(-62.32, 129.8) * mm, "end": v(-62.82, 129.1) * mm});
            skLineSegment(sketch, "E4372", {"start": v(-62.82, 129.1) * mm, "end": v(-63.22, 128.33) * mm});
            skLineSegment(sketch, "E4373", {"start": v(-63.22, 128.33) * mm, "end": v(-63.4, 127.93) * mm});
            skLineSegment(sketch, "E4374", {"start": v(-63.4, 127.93) * mm, "end": v(-63.54, 127.53) * mm});
            skLineSegment(sketch, "E4375", {"start": v(-63.54, 127.53) * mm, "end": v(-63.65, 127.12) * mm});
            skLineSegment(sketch, "E4376", {"start": v(-63.65, 127.12) * mm, "end": v(-63.74, 126.7) * mm});
            skLineSegment(sketch, "E4377", {"start": v(-63.74, 126.7) * mm, "end": v(-63.8, 126.29) * mm});
            skLineSegment(sketch, "E4378", {"start": v(-63.8, 126.29) * mm, "end": v(-63.82, 125.87) * mm});
            skLineSegment(sketch, "E4379", {"start": v(-63.82, 125.87) * mm, "end": v(-63.81, 125.45) * mm});
            skLineSegment(sketch, "E4380", {"start": v(-63.81, 125.45) * mm, "end": v(-63.77, 125.04) * mm});
            skLineSegment(sketch, "E4381", {"start": v(-63.77, 125.04) * mm, "end": v(-63.74, 124.84) * mm});
            skLineSegment(sketch, "E4382", {"start": v(-63.74, 124.84) * mm, "end": v(-63.72, 124.74) * mm});
            skLineSegment(sketch, "E4383", {"start": v(-63.72, 124.74) * mm, "end": v(-63.7, 124.69) * mm});
            skLineSegment(sketch, "E4384", {"start": v(-63.7, 124.69) * mm, "end": v(-63.7, 124.67) * mm});
            skLineSegment(sketch, "E4385", {"start": v(-63.7, 124.67) * mm, "end": v(-63.66, 124.69) * mm});
            skLineSegment(sketch, "E4386", {"start": v(-63.66, 124.69) * mm, "end": v(-62.97, 125) * mm});
            skLineSegment(sketch, "E4387", {"start": v(-62.97, 125) * mm, "end": v(-62.24, 125.26) * mm});
            skLineSegment(sketch, "E4388", {"start": v(-62.24, 125.26) * mm, "end": v(-61.49, 125.48) * mm});
            skLineSegment(sketch, "E4389", {"start": v(-61.49, 125.48) * mm, "end": v(-60.7, 125.65) * mm});
            skLineSegment(sketch, "E4390", {"start": v(-60.7, 125.65) * mm, "end": v(-59.9, 125.78) * mm});
            skLineSegment(sketch, "E4391", {"start": v(-59.9, 125.78) * mm, "end": v(-59.07, 125.86) * mm});
            skLineSegment(sketch, "E4392", {"start": v(-59.07, 125.86) * mm, "end": v(-58.24, 125.9) * mm});
            skLineSegment(sketch, "E4393", {"start": v(-58.24, 125.9) * mm, "end": v(-57.4, 125.9) * mm});
            skLineSegment(sketch, "E4394", {"start": v(-57.4, 125.9) * mm, "end": v(-56.56, 125.84) * mm});
            skLineSegment(sketch, "E4395", {"start": v(-56.56, 125.84) * mm, "end": v(-55.72, 125.76) * mm});
            skLineSegment(sketch, "E4396", {"start": v(-55.72, 125.76) * mm, "end": v(-54.9, 125.63) * mm});
            skLineSegment(sketch, "E4397", {"start": v(-54.9, 125.63) * mm, "end": v(-54.1, 125.46) * mm});
            skLineSegment(sketch, "E4398", {"start": v(-54.1, 125.46) * mm, "end": v(-53.3, 125.25) * mm});
            skLineSegment(sketch, "E4399", {"start": v(-53.3, 125.25) * mm, "end": v(-52.54, 125.01) * mm});
            skLineSegment(sketch, "E4400", {"start": v(-52.54, 125.01) * mm, "end": v(-51.81, 124.73) * mm});
            skLineSegment(sketch, "E4401", {"start": v(-51.81, 124.73) * mm, "end": v(-51.12, 124.41) * mm});
            skLineSegment(sketch, "E4402", {"start": v(-51.12, 124.41) * mm, "end": v(-50.46, 124.06) * mm});
            skLineSegment(sketch, "E4403", {"start": v(-26.69, -35.85) * mm, "end": v(-26.64, -35.8) * mm});
            skLineSegment(sketch, "E4404", {"start": v(-28.15, -35.9) * mm, "end": v(-26.69, -35.85) * mm});
            skSolve(sketch);
        }
        {
            var Q0;
            Q0 = qSketchRegion(id + "F0", true);
            extrude(context, id + "F1", {"entities" : qUnion([Q0]), "depth" : 5 * mm});
        }
        {
            var Q0;
            Q0=makeQuery(id+"F1.opExtrude","CAP_FACE",FACE,{"disambiguationData":[OSD([sQuery(id+"F0.wireOp",EDGE,"E0"),sQuery(id+"F0.wireOp",EDGE,"E1"),sQuery(id+"F0.wireOp",EDGE,"E2"),sQuery(id+"F0.wireOp",EDGE,"E3"),sQuery(id+"F0.wireOp",EDGE,"E4"),sQuery(id+"F0.wireOp",EDGE,"E5"),sQuery(id+"F0.wireOp",EDGE,"E6"),sQuery(id+"F0.wireOp",EDGE,"E7"),sQuery(id+"F0.wireOp",EDGE,"E8"),sQuery(id+"F0.wireOp",EDGE,"E9"),sQuery(id+"F0.wireOp",EDGE,"E10"),sQuery(id+"F0.wireOp",EDGE,"E11"),sQuery(id+"F0.wireOp",EDGE,"E12"),sQuery(id+"F0.wireOp",EDGE,"E13"),sQuery(id+"F0.wireOp",EDGE,"E14"),sQuery(id+"F0.wireOp",EDGE,"E15"),sQuery(id+"F0.wireOp",EDGE,"E16"),sQuery(id+"F0.wireOp",EDGE,"E17"),sQuery(id+"F0.wireOp",EDGE,"E18"),sQuery(id+"F0.wireOp",EDGE,"E19"),sQuery(id+"F0.wireOp",EDGE,"E20"),sQuery(id+"F0.wireOp",EDGE,"E21"),sQuery(id+"F0.wireOp",EDGE,"E22"),sQuery(id+"F0.wireOp",EDGE,"E23"),sQuery(id+"F0.wireOp",EDGE,"E24"),sQuery(id+"F0.wireOp",EDGE,"E25"),sQuery(id+"F0.wireOp",EDGE,"E26"),sQuery(id+"F0.wireOp",EDGE,"E27"),sQuery(id+"F0.wireOp",EDGE,"E28"),sQuery(id+"F0.wireOp",EDGE,"E29"),sQuery(id+"F0.wireOp",EDGE,"E30"),sQuery(id+"F0.wireOp",EDGE,"E31"),sQuery(id+"F0.wireOp",EDGE,"E32"),sQuery(id+"F0.wireOp",EDGE,"E33"),sQuery(id+"F0.wireOp",EDGE,"E34"),sQuery(id+"F0.wireOp",EDGE,"E35"),sQuery(id+"F0.wireOp",EDGE,"E36"),sQuery(id+"F0.wireOp",EDGE,"E37"),sQuery(id+"F0.wireOp",EDGE,"E38"),sQuery(id+"F0.wireOp",EDGE,"E39"),sQuery(id+"F0.wireOp",EDGE,"E40"),sQuery(id+"F0.wireOp",EDGE,"E41"),sQuery(id+"F0.wireOp",EDGE,"E42"),sQuery(id+"F0.wireOp",EDGE,"E43"),sQuery(id+"F0.wireOp",EDGE,"E44"),sQuery(id+"F0.wireOp",EDGE,"E45"),sQuery(id+"F0.wireOp",EDGE,"E46"),sQuery(id+"F0.wireOp",EDGE,"E47"),sQuery(id+"F0.wireOp",EDGE,"E48"),sQuery(id+"F0.wireOp",EDGE,"E49"),sQuery(id+"F0.wireOp",EDGE,"E50"),sQuery(id+"F0.wireOp",EDGE,"E51"),sQuery(id+"F0.wireOp",EDGE,"E52"),sQuery(id+"F0.wireOp",EDGE,"E53"),sQuery(id+"F0.wireOp",EDGE,"E54"),sQuery(id+"F0.wireOp",EDGE,"E55"),sQuery(id+"F0.wireOp",EDGE,"E56"),sQuery(id+"F0.wireOp",EDGE,"E57"),sQuery(id+"F0.wireOp",EDGE,"E58"),sQuery(id+"F0.wireOp",EDGE,"E59"),sQuery(id+"F0.wireOp",EDGE,"E60"),sQuery(id+"F0.wireOp",EDGE,"E61"),sQuery(id+"F0.wireOp",EDGE,"E62"),sQuery(id+"F0.wireOp",EDGE,"E63"),sQuery(id+"F0.wireOp",EDGE,"E64"),sQuery(id+"F0.wireOp",EDGE,"E65"),sQuery(id+"F0.wireOp",EDGE,"E66"),sQuery(id+"F0.wireOp",EDGE,"E67"),sQuery(id+"F0.wireOp",EDGE,"E68"),sQuery(id+"F0.wireOp",EDGE,"E69"),sQuery(id+"F0.wireOp",EDGE,"E70"),sQuery(id+"F0.wireOp",EDGE,"E71"),sQuery(id+"F0.wireOp",EDGE,"E72"),sQuery(id+"F0.wireOp",EDGE,"E73"),sQuery(id+"F0.wireOp",EDGE,"E74"),sQuery(id+"F0.wireOp",EDGE,"E75"),sQuery(id+"F0.wireOp",EDGE,"E76"),sQuery(id+"F0.wireOp",EDGE,"E77"),sQuery(id+"F0.wireOp",EDGE,"E78"),sQuery(id+"F0.wireOp",EDGE,"E79"),sQuery(id+"F0.wireOp",EDGE,"E80"),sQuery(id+"F0.wireOp",EDGE,"E81"),sQuery(id+"F0.wireOp",EDGE,"E82"),sQuery(id+"F0.wireOp",EDGE,"E83"),sQuery(id+"F0.wireOp",EDGE,"E84"),sQuery(id+"F0.wireOp",EDGE,"E85"),sQuery(id+"F0.wireOp",EDGE,"E86"),sQuery(id+"F0.wireOp",EDGE,"E87"),sQuery(id+"F0.wireOp",EDGE,"E88"),sQuery(id+"F0.wireOp",EDGE,"E89"),sQuery(id+"F0.wireOp",EDGE,"E90"),sQuery(id+"F0.wireOp",EDGE,"E91"),sQuery(id+"F0.wireOp",EDGE,"E92"),sQuery(id+"F0.wireOp",EDGE,"E93"),sQuery(id+"F0.wireOp",EDGE,"E94"),sQuery(id+"F0.wireOp",EDGE,"E95"),sQuery(id+"F0.wireOp",EDGE,"E96"),sQuery(id+"F0.wireOp",EDGE,"E97"),sQuery(id+"F0.wireOp",EDGE,"E98"),sQuery(id+"F0.wireOp",EDGE,"E99"),sQuery(id+"F0.wireOp",EDGE,"E100"),sQuery(id+"F0.wireOp",EDGE,"E101"),sQuery(id+"F0.wireOp",EDGE,"E102"),sQuery(id+"F0.wireOp",EDGE,"E103"),sQuery(id+"F0.wireOp",EDGE,"E104"),sQuery(id+"F0.wireOp",EDGE,"E105"),sQuery(id+"F0.wireOp",EDGE,"E106"),sQuery(id+"F0.wireOp",EDGE,"E107"),sQuery(id+"F0.wireOp",EDGE,"E108"),sQuery(id+"F0.wireOp",EDGE,"E108"),sQuery(id+"F0.wireOp",EDGE,"E109"),sQuery(id+"F0.wireOp",EDGE,"E110"),sQuery(id+"F0.wireOp",EDGE,"E111"),sQuery(id+"F0.wireOp",EDGE,"E112"),sQuery(id+"F0.wireOp",EDGE,"E113"),sQuery(id+"F0.wireOp",EDGE,"E114"),sQuery(id+"F0.wireOp",EDGE,"E115"),sQuery(id+"F0.wireOp",EDGE,"E116"),sQuery(id+"F0.wireOp",EDGE,"E117"),sQuery(id+"F0.wireOp",EDGE,"E118"),sQuery(id+"F0.wireOp",EDGE,"E119"),sQuery(id+"F0.wireOp",EDGE,"E120"),sQuery(id+"F0.wireOp",EDGE,"E121"),sQuery(id+"F0.wireOp",EDGE,"E122"),sQuery(id+"F0.wireOp",EDGE,"E123"),sQuery(id+"F0.wireOp",EDGE,"E124"),sQuery(id+"F0.wireOp",EDGE,"E125"),sQuery(id+"F0.wireOp",EDGE,"E126"),sQuery(id+"F0.wireOp",EDGE,"E127"),sQuery(id+"F0.wireOp",EDGE,"E128"),sQuery(id+"F0.wireOp",EDGE,"E129"),sQuery(id+"F0.wireOp",EDGE,"E130"),sQuery(id+"F0.wireOp",EDGE,"E131"),sQuery(id+"F0.wireOp",EDGE,"E132"),sQuery(id+"F0.wireOp",EDGE,"E133"),sQuery(id+"F0.wireOp",EDGE,"E134"),sQuery(id+"F0.wireOp",EDGE,"E135"),sQuery(id+"F0.wireOp",EDGE,"E136"),sQuery(id+"F0.wireOp",EDGE,"E137"),sQuery(id+"F0.wireOp",EDGE,"E138"),sQuery(id+"F0.wireOp",EDGE,"E139"),sQuery(id+"F0.wireOp",EDGE,"E140"),sQuery(id+"F0.wireOp",EDGE,"E141"),sQuery(id+"F0.wireOp",EDGE,"E142"),sQuery(id+"F0.wireOp",EDGE,"E143"),sQuery(id+"F0.wireOp",EDGE,"E144"),sQuery(id+"F0.wireOp",EDGE,"E145"),sQuery(id+"F0.wireOp",EDGE,"E146"),sQuery(id+"F0.wireOp",EDGE,"E147"),sQuery(id+"F0.wireOp",EDGE,"E148"),sQuery(id+"F0.wireOp",EDGE,"E149"),sQuery(id+"F0.wireOp",EDGE,"E150"),sQuery(id+"F0.wireOp",EDGE,"E151"),sQuery(id+"F0.wireOp",EDGE,"E152"),sQuery(id+"F0.wireOp",EDGE,"E153"),sQuery(id+"F0.wireOp",EDGE,"E154"),sQuery(id+"F0.wireOp",EDGE,"E155"),sQuery(id+"F0.wireOp",EDGE,"E156"),sQuery(id+"F0.wireOp",EDGE,"E157"),sQuery(id+"F0.wireOp",EDGE,"E158"),sQuery(id+"F0.wireOp",EDGE,"E159"),sQuery(id+"F0.wireOp",EDGE,"E160"),sQuery(id+"F0.wireOp",EDGE,"E161"),sQuery(id+"F0.wireOp",EDGE,"E162"),sQuery(id+"F0.wireOp",EDGE,"E163"),sQuery(id+"F0.wireOp",EDGE,"E164"),sQuery(id+"F0.wireOp",EDGE,"E165"),sQuery(id+"F0.wireOp",EDGE,"E166"),sQuery(id+"F0.wireOp",EDGE,"E167"),sQuery(id+"F0.wireOp",EDGE,"E168"),sQuery(id+"F0.wireOp",EDGE,"E169"),sQuery(id+"F0.wireOp",EDGE,"E170"),sQuery(id+"F0.wireOp",EDGE,"E171"),sQuery(id+"F0.wireOp",EDGE,"E172"),sQuery(id+"F0.wireOp",EDGE,"E173"),sQuery(id+"F0.wireOp",EDGE,"E174"),sQuery(id+"F0.wireOp",EDGE,"E175"),sQuery(id+"F0.wireOp",EDGE,"E176"),sQuery(id+"F0.wireOp",EDGE,"E177"),sQuery(id+"F0.wireOp",EDGE,"E178"),sQuery(id+"F0.wireOp",EDGE,"E179"),sQuery(id+"F0.wireOp",EDGE,"E180"),sQuery(id+"F0.wireOp",EDGE,"E181"),sQuery(id+"F0.wireOp",EDGE,"E182"),sQuery(id+"F0.wireOp",EDGE,"E183"),sQuery(id+"F0.wireOp",EDGE,"E184"),sQuery(id+"F0.wireOp",EDGE,"E185"),sQuery(id+"F0.wireOp",EDGE,"E186"),sQuery(id+"F0.wireOp",EDGE,"E187"),sQuery(id+"F0.wireOp",EDGE,"E188"),sQuery(id+"F0.wireOp",EDGE,"E189"),sQuery(id+"F0.wireOp",EDGE,"E190"),sQuery(id+"F0.wireOp",EDGE,"E191"),sQuery(id+"F0.wireOp",EDGE,"E192"),sQuery(id+"F0.wireOp",EDGE,"E193"),sQuery(id+"F0.wireOp",EDGE,"E194"),sQuery(id+"F0.wireOp",EDGE,"E195"),sQuery(id+"F0.wireOp",EDGE,"E196"),sQuery(id+"F0.wireOp",EDGE,"E197"),sQuery(id+"F0.wireOp",EDGE,"E198"),sQuery(id+"F0.wireOp",EDGE,"E199"),sQuery(id+"F0.wireOp",EDGE,"E200"),sQuery(id+"F0.wireOp",EDGE,"E201"),sQuery(id+"F0.wireOp",EDGE,"E202"),sQuery(id+"F0.wireOp",EDGE,"E203"),sQuery(id+"F0.wireOp",EDGE,"E204"),sQuery(id+"F0.wireOp",EDGE,"E205"),sQuery(id+"F0.wireOp",EDGE,"E206"),sQuery(id+"F0.wireOp",EDGE,"E207"),sQuery(id+"F0.wireOp",EDGE,"E208"),sQuery(id+"F0.wireOp",EDGE,"E209"),sQuery(id+"F0.wireOp",EDGE,"E210"),sQuery(id+"F0.wireOp",EDGE,"E211"),sQuery(id+"F0.wireOp",EDGE,"E212"),sQuery(id+"F0.wireOp",EDGE,"E214"),sQuery(id+"F0.wireOp",EDGE,"E215"),sQuery(id+"F0.wireOp",EDGE,"E216"),sQuery(id+"F0.wireOp",EDGE,"E217"),sQuery(id+"F0.wireOp",EDGE,"E218"),sQuery(id+"F0.wireOp",EDGE,"E219"),sQuery(id+"F0.wireOp",EDGE,"E220"),sQuery(id+"F0.wireOp",EDGE,"E221"),sQuery(id+"F0.wireOp",EDGE,"E222"),sQuery(id+"F0.wireOp",EDGE,"E223"),sQuery(id+"F0.wireOp",EDGE,"E224"),sQuery(id+"F0.wireOp",EDGE,"E225"),sQuery(id+"F0.wireOp",EDGE,"E226"),sQuery(id+"F0.wireOp",EDGE,"E227"),sQuery(id+"F0.wireOp",EDGE,"E228"),sQuery(id+"F0.wireOp",EDGE,"E229"),sQuery(id+"F0.wireOp",EDGE,"E230"),sQuery(id+"F0.wireOp",EDGE,"E231"),sQuery(id+"F0.wireOp",EDGE,"E232"),sQuery(id+"F0.wireOp",EDGE,"E233"),sQuery(id+"F0.wireOp",EDGE,"E234"),sQuery(id+"F0.wireOp",EDGE,"E235"),sQuery(id+"F0.wireOp",EDGE,"E236"),sQuery(id+"F0.wireOp",EDGE,"E237"),sQuery(id+"F0.wireOp",EDGE,"E238"),sQuery(id+"F0.wireOp",EDGE,"E239"),sQuery(id+"F0.wireOp",EDGE,"E240"),sQuery(id+"F0.wireOp",EDGE,"E241"),sQuery(id+"F0.wireOp",EDGE,"E242"),sQuery(id+"F0.wireOp",EDGE,"E243"),sQuery(id+"F0.wireOp",EDGE,"E244"),sQuery(id+"F0.wireOp",EDGE,"E245"),sQuery(id+"F0.wireOp",EDGE,"E246"),sQuery(id+"F0.wireOp",EDGE,"E247"),sQuery(id+"F0.wireOp",EDGE,"E248"),sQuery(id+"F0.wireOp",EDGE,"E249"),sQuery(id+"F0.wireOp",EDGE,"E250"),sQuery(id+"F0.wireOp",EDGE,"E251"),sQuery(id+"F0.wireOp",EDGE,"E252"),sQuery(id+"F0.wireOp",EDGE,"E253"),sQuery(id+"F0.wireOp",EDGE,"E254"),sQuery(id+"F0.wireOp",EDGE,"E255"),sQuery(id+"F0.wireOp",EDGE,"E256"),sQuery(id+"F0.wireOp",EDGE,"E257"),sQuery(id+"F0.wireOp",EDGE,"E258"),sQuery(id+"F0.wireOp",EDGE,"E259"),sQuery(id+"F0.wireOp",EDGE,"E260"),sQuery(id+"F0.wireOp",EDGE,"E261"),sQuery(id+"F0.wireOp",EDGE,"E262"),sQuery(id+"F0.wireOp",EDGE,"E263"),sQuery(id+"F0.wireOp",EDGE,"E264"),sQuery(id+"F0.wireOp",EDGE,"E265"),sQuery(id+"F0.wireOp",EDGE,"E266"),sQuery(id+"F0.wireOp",EDGE,"E267"),sQuery(id+"F0.wireOp",EDGE,"E268"),sQuery(id+"F0.wireOp",EDGE,"E269"),sQuery(id+"F0.wireOp",EDGE,"E270"),sQuery(id+"F0.wireOp",EDGE,"E271"),sQuery(id+"F0.wireOp",EDGE,"E272"),sQuery(id+"F0.wireOp",EDGE,"E273"),sQuery(id+"F0.wireOp",EDGE,"E274"),sQuery(id+"F0.wireOp",EDGE,"E275"),sQuery(id+"F0.wireOp",EDGE,"E276"),sQuery(id+"F0.wireOp",EDGE,"E277"),sQuery(id+"F0.wireOp",EDGE,"E278"),sQuery(id+"F0.wireOp",EDGE,"E279"),sQuery(id+"F0.wireOp",EDGE,"E280"),sQuery(id+"F0.wireOp",EDGE,"E281"),sQuery(id+"F0.wireOp",EDGE,"E282"),sQuery(id+"F0.wireOp",EDGE,"E283"),sQuery(id+"F0.wireOp",EDGE,"E284"),sQuery(id+"F0.wireOp",EDGE,"E285"),sQuery(id+"F0.wireOp",EDGE,"E286"),sQuery(id+"F0.wireOp",EDGE,"E287"),sQuery(id+"F0.wireOp",EDGE,"E288"),sQuery(id+"F0.wireOp",EDGE,"E289"),sQuery(id+"F0.wireOp",EDGE,"E290"),sQuery(id+"F0.wireOp",EDGE,"E291"),sQuery(id+"F0.wireOp",EDGE,"E292"),sQuery(id+"F0.wireOp",EDGE,"E293"),sQuery(id+"F0.wireOp",EDGE,"E294"),sQuery(id+"F0.wireOp",EDGE,"E295"),sQuery(id+"F0.wireOp",EDGE,"E296"),sQuery(id+"F0.wireOp",EDGE,"E297"),sQuery(id+"F0.wireOp",EDGE,"E298"),sQuery(id+"F0.wireOp",EDGE,"E299"),sQuery(id+"F0.wireOp",EDGE,"E300"),sQuery(id+"F0.wireOp",EDGE,"E301"),sQuery(id+"F0.wireOp",EDGE,"E302"),sQuery(id+"F0.wireOp",EDGE,"E303"),sQuery(id+"F0.wireOp",EDGE,"E304"),sQuery(id+"F0.wireOp",EDGE,"E305"),sQuery(id+"F0.wireOp",EDGE,"E306"),sQuery(id+"F0.wireOp",EDGE,"E307"),sQuery(id+"F0.wireOp",EDGE,"E308"),sQuery(id+"F0.wireOp",EDGE,"E309"),sQuery(id+"F0.wireOp",EDGE,"E310"),sQuery(id+"F0.wireOp",EDGE,"E311"),sQuery(id+"F0.wireOp",EDGE,"E312"),sQuery(id+"F0.wireOp",EDGE,"E313"),sQuery(id+"F0.wireOp",EDGE,"E314"),sQuery(id+"F0.wireOp",EDGE,"E315"),sQuery(id+"F0.wireOp",EDGE,"E316"),sQuery(id+"F0.wireOp",EDGE,"E317"),sQuery(id+"F0.wireOp",EDGE,"E318"),sQuery(id+"F0.wireOp",EDGE,"E319"),sQuery(id+"F0.wireOp",EDGE,"E320"),sQuery(id+"F0.wireOp",EDGE,"E321"),sQuery(id+"F0.wireOp",EDGE,"E322"),sQuery(id+"F0.wireOp",EDGE,"E323"),sQuery(id+"F0.wireOp",EDGE,"E324"),sQuery(id+"F0.wireOp",EDGE,"E325"),sQuery(id+"F0.wireOp",EDGE,"E326"),sQuery(id+"F0.wireOp",EDGE,"E327"),sQuery(id+"F0.wireOp",EDGE,"E328"),sQuery(id+"F0.wireOp",EDGE,"E329"),sQuery(id+"F0.wireOp",EDGE,"E330"),sQuery(id+"F0.wireOp",EDGE,"E331"),sQuery(id+"F0.wireOp",EDGE,"E332"),sQuery(id+"F0.wireOp",EDGE,"E333"),sQuery(id+"F0.wireOp",EDGE,"E334"),sQuery(id+"F0.wireOp",EDGE,"E335"),sQuery(id+"F0.wireOp",EDGE,"E336"),sQuery(id+"F0.wireOp",EDGE,"E337"),sQuery(id+"F0.wireOp",EDGE,"E338"),sQuery(id+"F0.wireOp",EDGE,"E339"),sQuery(id+"F0.wireOp",EDGE,"E340"),sQuery(id+"F0.wireOp",EDGE,"E341"),sQuery(id+"F0.wireOp",EDGE,"E342"),sQuery(id+"F0.wireOp",EDGE,"E343"),sQuery(id+"F0.wireOp",EDGE,"E344"),sQuery(id+"F0.wireOp",EDGE,"E345"),sQuery(id+"F0.wireOp",EDGE,"E346"),sQuery(id+"F0.wireOp",EDGE,"E347"),sQuery(id+"F0.wireOp",EDGE,"E348"),sQuery(id+"F0.wireOp",EDGE,"E349"),sQuery(id+"F0.wireOp",EDGE,"E350"),sQuery(id+"F0.wireOp",EDGE,"E351"),sQuery(id+"F0.wireOp",EDGE,"E352"),sQuery(id+"F0.wireOp",EDGE,"E353"),sQuery(id+"F0.wireOp",EDGE,"E354"),sQuery(id+"F0.wireOp",EDGE,"E355"),sQuery(id+"F0.wireOp",EDGE,"E356"),sQuery(id+"F0.wireOp",EDGE,"E357"),sQuery(id+"F0.wireOp",EDGE,"E358"),sQuery(id+"F0.wireOp",EDGE,"E359"),sQuery(id+"F0.wireOp",EDGE,"E360"),sQuery(id+"F0.wireOp",EDGE,"E361"),sQuery(id+"F0.wireOp",EDGE,"E362"),sQuery(id+"F0.wireOp",EDGE,"E363"),sQuery(id+"F0.wireOp",EDGE,"E364"),sQuery(id+"F0.wireOp",EDGE,"E365"),sQuery(id+"F0.wireOp",EDGE,"E366"),sQuery(id+"F0.wireOp",EDGE,"E367"),sQuery(id+"F0.wireOp",EDGE,"E368"),sQuery(id+"F0.wireOp",EDGE,"E369"),sQuery(id+"F0.wireOp",EDGE,"E370"),sQuery(id+"F0.wireOp",EDGE,"E371"),sQuery(id+"F0.wireOp",EDGE,"E372"),sQuery(id+"F0.wireOp",EDGE,"E373"),sQuery(id+"F0.wireOp",EDGE,"E374"),sQuery(id+"F0.wireOp",EDGE,"E375"),sQuery(id+"F0.wireOp",EDGE,"E376"),sQuery(id+"F0.wireOp",EDGE,"E377"),sQuery(id+"F0.wireOp",EDGE,"E378"),sQuery(id+"F0.wireOp",EDGE,"E379"),sQuery(id+"F0.wireOp",EDGE,"E380"),sQuery(id+"F0.wireOp",EDGE,"E381"),sQuery(id+"F0.wireOp",EDGE,"E382"),sQuery(id+"F0.wireOp",EDGE,"E383"),sQuery(id+"F0.wireOp",EDGE,"E384"),sQuery(id+"F0.wireOp",EDGE,"E385"),sQuery(id+"F0.wireOp",EDGE,"E386"),sQuery(id+"F0.wireOp",EDGE,"E387"),sQuery(id+"F0.wireOp",EDGE,"E388"),sQuery(id+"F0.wireOp",EDGE,"E389"),sQuery(id+"F0.wireOp",EDGE,"E390"),sQuery(id+"F0.wireOp",EDGE,"E391"),sQuery(id+"F0.wireOp",EDGE,"E392"),sQuery(id+"F0.wireOp",EDGE,"E393"),sQuery(id+"F0.wireOp",EDGE,"E394"),sQuery(id+"F0.wireOp",EDGE,"E395"),sQuery(id+"F0.wireOp",EDGE,"E396"),sQuery(id+"F0.wireOp",EDGE,"E397"),sQuery(id+"F0.wireOp",EDGE,"E398"),sQuery(id+"F0.wireOp",EDGE,"E399"),sQuery(id+"F0.wireOp",EDGE,"E400"),sQuery(id+"F0.wireOp",EDGE,"E401"),sQuery(id+"F0.wireOp",EDGE,"E402"),sQuery(id+"F0.wireOp",EDGE,"E403"),sQuery(id+"F0.wireOp",EDGE,"E404"),sQuery(id+"F0.wireOp",EDGE,"E405"),sQuery(id+"F0.wireOp",EDGE,"E406"),sQuery(id+"F0.wireOp",EDGE,"E407"),sQuery(id+"F0.wireOp",EDGE,"E408"),sQuery(id+"F0.wireOp",EDGE,"E409"),sQuery(id+"F0.wireOp",EDGE,"E410"),sQuery(id+"F0.wireOp",EDGE,"E411"),sQuery(id+"F0.wireOp",EDGE,"E412"),sQuery(id+"F0.wireOp",EDGE,"E413"),sQuery(id+"F0.wireOp",EDGE,"E414"),sQuery(id+"F0.wireOp",EDGE,"E415"),sQuery(id+"F0.wireOp",EDGE,"E416"),sQuery(id+"F0.wireOp",EDGE,"E417"),sQuery(id+"F0.wireOp",EDGE,"E418"),sQuery(id+"F0.wireOp",EDGE,"E419"),sQuery(id+"F0.wireOp",EDGE,"E420"),sQuery(id+"F0.wireOp",EDGE,"E421"),sQuery(id+"F0.wireOp",EDGE,"E422"),sQuery(id+"F0.wireOp",EDGE,"E423"),sQuery(id+"F0.wireOp",EDGE,"E424"),sQuery(id+"F0.wireOp",EDGE,"E425"),sQuery(id+"F0.wireOp",EDGE,"E426"),sQuery(id+"F0.wireOp",EDGE,"E427"),sQuery(id+"F0.wireOp",EDGE,"E428"),sQuery(id+"F0.wireOp",EDGE,"E429"),sQuery(id+"F0.wireOp",EDGE,"E430"),sQuery(id+"F0.wireOp",EDGE,"E431"),sQuery(id+"F0.wireOp",EDGE,"E432"),sQuery(id+"F0.wireOp",EDGE,"E433"),sQuery(id+"F0.wireOp",EDGE,"E434"),sQuery(id+"F0.wireOp",EDGE,"E435"),sQuery(id+"F0.wireOp",EDGE,"E436"),sQuery(id+"F0.wireOp",EDGE,"E437"),sQuery(id+"F0.wireOp",EDGE,"E438"),sQuery(id+"F0.wireOp",EDGE,"E439"),sQuery(id+"F0.wireOp",EDGE,"E440"),sQuery(id+"F0.wireOp",EDGE,"E441"),sQuery(id+"F0.wireOp",EDGE,"E442"),sQuery(id+"F0.wireOp",EDGE,"E443"),sQuery(id+"F0.wireOp",EDGE,"E444"),sQuery(id+"F0.wireOp",EDGE,"E445"),sQuery(id+"F0.wireOp",EDGE,"E446"),sQuery(id+"F0.wireOp",EDGE,"E447"),sQuery(id+"F0.wireOp",EDGE,"E448"),sQuery(id+"F0.wireOp",EDGE,"E449"),sQuery(id+"F0.wireOp",EDGE,"E450"),sQuery(id+"F0.wireOp",EDGE,"E451"),sQuery(id+"F0.wireOp",EDGE,"E452"),sQuery(id+"F0.wireOp",EDGE,"E453"),sQuery(id+"F0.wireOp",EDGE,"E454"),sQuery(id+"F0.wireOp",EDGE,"E455"),sQuery(id+"F0.wireOp",EDGE,"E456"),sQuery(id+"F0.wireOp",EDGE,"E457"),sQuery(id+"F0.wireOp",EDGE,"E458"),sQuery(id+"F0.wireOp",EDGE,"E459"),sQuery(id+"F0.wireOp",EDGE,"E460"),sQuery(id+"F0.wireOp",EDGE,"E461"),sQuery(id+"F0.wireOp",EDGE,"E462"),sQuery(id+"F0.wireOp",EDGE,"E463"),sQuery(id+"F0.wireOp",EDGE,"E464"),sQuery(id+"F0.wireOp",EDGE,"E465"),sQuery(id+"F0.wireOp",EDGE,"E466"),sQuery(id+"F0.wireOp",EDGE,"E467"),sQuery(id+"F0.wireOp",EDGE,"E468"),sQuery(id+"F0.wireOp",EDGE,"E469"),sQuery(id+"F0.wireOp",EDGE,"E470"),sQuery(id+"F0.wireOp",EDGE,"E471"),sQuery(id+"F0.wireOp",EDGE,"E472"),sQuery(id+"F0.wireOp",EDGE,"E473"),sQuery(id+"F0.wireOp",EDGE,"E474"),sQuery(id+"F0.wireOp",EDGE,"E475"),sQuery(id+"F0.wireOp",EDGE,"E476"),sQuery(id+"F0.wireOp",EDGE,"E477"),sQuery(id+"F0.wireOp",EDGE,"E478"),sQuery(id+"F0.wireOp",EDGE,"E479"),sQuery(id+"F0.wireOp",EDGE,"E480"),sQuery(id+"F0.wireOp",EDGE,"E481"),sQuery(id+"F0.wireOp",EDGE,"E482"),sQuery(id+"F0.wireOp",EDGE,"E483"),sQuery(id+"F0.wireOp",EDGE,"E484"),sQuery(id+"F0.wireOp",EDGE,"E485"),sQuery(id+"F0.wireOp",EDGE,"E486"),sQuery(id+"F0.wireOp",EDGE,"E487"),sQuery(id+"F0.wireOp",EDGE,"E488"),sQuery(id+"F0.wireOp",EDGE,"E489"),sQuery(id+"F0.wireOp",EDGE,"E490"),sQuery(id+"F0.wireOp",EDGE,"E491"),sQuery(id+"F0.wireOp",EDGE,"E492"),sQuery(id+"F0.wireOp",EDGE,"E493"),sQuery(id+"F0.wireOp",EDGE,"E494"),sQuery(id+"F0.wireOp",EDGE,"E495"),sQuery(id+"F0.wireOp",EDGE,"E496"),sQuery(id+"F0.wireOp",EDGE,"E497"),sQuery(id+"F0.wireOp",EDGE,"E498"),sQuery(id+"F0.wireOp",EDGE,"E499"),sQuery(id+"F0.wireOp",EDGE,"E500"),sQuery(id+"F0.wireOp",EDGE,"E501"),sQuery(id+"F0.wireOp",EDGE,"E502"),sQuery(id+"F0.wireOp",EDGE,"E503"),sQuery(id+"F0.wireOp",EDGE,"E504"),sQuery(id+"F0.wireOp",EDGE,"E505"),sQuery(id+"F0.wireOp",EDGE,"E506"),sQuery(id+"F0.wireOp",EDGE,"E507"),sQuery(id+"F0.wireOp",EDGE,"E508"),sQuery(id+"F0.wireOp",EDGE,"E509"),sQuery(id+"F0.wireOp",EDGE,"E510"),sQuery(id+"F0.wireOp",EDGE,"E511"),sQuery(id+"F0.wireOp",EDGE,"E512"),sQuery(id+"F0.wireOp",EDGE,"E513"),sQuery(id+"F0.wireOp",EDGE,"E514"),sQuery(id+"F0.wireOp",EDGE,"E515"),sQuery(id+"F0.wireOp",EDGE,"E516"),sQuery(id+"F0.wireOp",EDGE,"E517"),sQuery(id+"F0.wireOp",EDGE,"E518"),sQuery(id+"F0.wireOp",EDGE,"E519"),sQuery(id+"F0.wireOp",EDGE,"E520"),sQuery(id+"F0.wireOp",EDGE,"E521"),sQuery(id+"F0.wireOp",EDGE,"E522"),sQuery(id+"F0.wireOp",EDGE,"E523"),sQuery(id+"F0.wireOp",EDGE,"E524"),sQuery(id+"F0.wireOp",EDGE,"E525"),sQuery(id+"F0.wireOp",EDGE,"E526"),sQuery(id+"F0.wireOp",EDGE,"E527"),sQuery(id+"F0.wireOp",EDGE,"E528"),sQuery(id+"F0.wireOp",EDGE,"E529"),sQuery(id+"F0.wireOp",EDGE,"E530"),sQuery(id+"F0.wireOp",EDGE,"E531"),sQuery(id+"F0.wireOp",EDGE,"E532"),sQuery(id+"F0.wireOp",EDGE,"E533"),sQuery(id+"F0.wireOp",EDGE,"E534"),sQuery(id+"F0.wireOp",EDGE,"E535"),sQuery(id+"F0.wireOp",EDGE,"E536"),sQuery(id+"F0.wireOp",EDGE,"E537"),sQuery(id+"F0.wireOp",EDGE,"E538"),sQuery(id+"F0.wireOp",EDGE,"E539"),sQuery(id+"F0.wireOp",EDGE,"E540"),sQuery(id+"F0.wireOp",EDGE,"E541"),sQuery(id+"F0.wireOp",EDGE,"E542"),sQuery(id+"F0.wireOp",EDGE,"E543"),sQuery(id+"F0.wireOp",EDGE,"E544"),sQuery(id+"F0.wireOp",EDGE,"E545"),sQuery(id+"F0.wireOp",EDGE,"E546"),sQuery(id+"F0.wireOp",EDGE,"E547"),sQuery(id+"F0.wireOp",EDGE,"E548"),sQuery(id+"F0.wireOp",EDGE,"E549"),sQuery(id+"F0.wireOp",EDGE,"E550"),sQuery(id+"F0.wireOp",EDGE,"E551"),sQuery(id+"F0.wireOp",EDGE,"E552"),sQuery(id+"F0.wireOp",EDGE,"E553"),sQuery(id+"F0.wireOp",EDGE,"E554"),sQuery(id+"F0.wireOp",EDGE,"E555"),sQuery(id+"F0.wireOp",EDGE,"E556"),sQuery(id+"F0.wireOp",EDGE,"E557"),sQuery(id+"F0.wireOp",EDGE,"E558"),sQuery(id+"F0.wireOp",EDGE,"E559"),sQuery(id+"F0.wireOp",EDGE,"E560"),sQuery(id+"F0.wireOp",EDGE,"E561"),sQuery(id+"F0.wireOp",EDGE,"E562"),sQuery(id+"F0.wireOp",EDGE,"E563"),sQuery(id+"F0.wireOp",EDGE,"E564"),sQuery(id+"F0.wireOp",EDGE,"E565"),sQuery(id+"F0.wireOp",EDGE,"E566"),sQuery(id+"F0.wireOp",EDGE,"E567"),sQuery(id+"F0.wireOp",EDGE,"E568"),sQuery(id+"F0.wireOp",EDGE,"E569"),sQuery(id+"F0.wireOp",EDGE,"E570"),sQuery(id+"F0.wireOp",EDGE,"E571"),sQuery(id+"F0.wireOp",EDGE,"E572"),sQuery(id+"F0.wireOp",EDGE,"E573"),sQuery(id+"F0.wireOp",EDGE,"E574"),sQuery(id+"F0.wireOp",EDGE,"E575"),sQuery(id+"F0.wireOp",EDGE,"E576"),sQuery(id+"F0.wireOp",EDGE,"E577"),sQuery(id+"F0.wireOp",EDGE,"E578"),sQuery(id+"F0.wireOp",EDGE,"E579"),sQuery(id+"F0.wireOp",EDGE,"E580"),sQuery(id+"F0.wireOp",EDGE,"E581"),sQuery(id+"F0.wireOp",EDGE,"E582"),sQuery(id+"F0.wireOp",EDGE,"E583"),sQuery(id+"F0.wireOp",EDGE,"E584"),sQuery(id+"F0.wireOp",EDGE,"E585"),sQuery(id+"F0.wireOp",EDGE,"E586"),sQuery(id+"F0.wireOp",EDGE,"E587"),sQuery(id+"F0.wireOp",EDGE,"E588"),sQuery(id+"F0.wireOp",EDGE,"E589"),sQuery(id+"F0.wireOp",EDGE,"E590"),sQuery(id+"F0.wireOp",EDGE,"E591"),sQuery(id+"F0.wireOp",EDGE,"E592"),sQuery(id+"F0.wireOp",EDGE,"E593"),sQuery(id+"F0.wireOp",EDGE,"E594"),sQuery(id+"F0.wireOp",EDGE,"E595"),sQuery(id+"F0.wireOp",EDGE,"E596"),sQuery(id+"F0.wireOp",EDGE,"E597"),sQuery(id+"F0.wireOp",EDGE,"E598"),sQuery(id+"F0.wireOp",EDGE,"E599"),sQuery(id+"F0.wireOp",EDGE,"E600"),sQuery(id+"F0.wireOp",EDGE,"E601"),sQuery(id+"F0.wireOp",EDGE,"E602"),sQuery(id+"F0.wireOp",EDGE,"E603"),sQuery(id+"F0.wireOp",EDGE,"E604"),sQuery(id+"F0.wireOp",EDGE,"E605"),sQuery(id+"F0.wireOp",EDGE,"E606"),sQuery(id+"F0.wireOp",EDGE,"E607"),sQuery(id+"F0.wireOp",EDGE,"E608"),sQuery(id+"F0.wireOp",EDGE,"E609"),sQuery(id+"F0.wireOp",EDGE,"E610"),sQuery(id+"F0.wireOp",EDGE,"E611"),sQuery(id+"F0.wireOp",EDGE,"E612"),sQuery(id+"F0.wireOp",EDGE,"E613"),sQuery(id+"F0.wireOp",EDGE,"E614"),sQuery(id+"F0.wireOp",EDGE,"E615"),sQuery(id+"F0.wireOp",EDGE,"E616"),sQuery(id+"F0.wireOp",EDGE,"E617"),sQuery(id+"F0.wireOp",EDGE,"E618"),sQuery(id+"F0.wireOp",EDGE,"E619"),sQuery(id+"F0.wireOp",EDGE,"E620"),sQuery(id+"F0.wireOp",EDGE,"E621"),sQuery(id+"F0.wireOp",EDGE,"E622"),sQuery(id+"F0.wireOp",EDGE,"E623"),sQuery(id+"F0.wireOp",EDGE,"E624"),sQuery(id+"F0.wireOp",EDGE,"E625"),sQuery(id+"F0.wireOp",EDGE,"E626"),sQuery(id+"F0.wireOp",EDGE,"E627"),sQuery(id+"F0.wireOp",EDGE,"E628"),sQuery(id+"F0.wireOp",EDGE,"E629"),sQuery(id+"F0.wireOp",EDGE,"E630"),sQuery(id+"F0.wireOp",EDGE,"E631"),sQuery(id+"F0.wireOp",EDGE,"E632"),sQuery(id+"F0.wireOp",EDGE,"E633"),sQuery(id+"F0.wireOp",EDGE,"E634"),sQuery(id+"F0.wireOp",EDGE,"E635"),sQuery(id+"F0.wireOp",EDGE,"E636"),sQuery(id+"F0.wireOp",EDGE,"E637"),sQuery(id+"F0.wireOp",EDGE,"E638"),sQuery(id+"F0.wireOp",EDGE,"E639"),sQuery(id+"F0.wireOp",EDGE,"E640"),sQuery(id+"F0.wireOp",EDGE,"E641"),sQuery(id+"F0.wireOp",EDGE,"E642"),sQuery(id+"F0.wireOp",EDGE,"E643"),sQuery(id+"F0.wireOp",EDGE,"E644"),sQuery(id+"F0.wireOp",EDGE,"E645"),sQuery(id+"F0.wireOp",EDGE,"E646"),sQuery(id+"F0.wireOp",EDGE,"E647"),sQuery(id+"F0.wireOp",EDGE,"E648"),sQuery(id+"F0.wireOp",EDGE,"E649"),sQuery(id+"F0.wireOp",EDGE,"E650"),sQuery(id+"F0.wireOp",EDGE,"E651"),sQuery(id+"F0.wireOp",EDGE,"E652"),sQuery(id+"F0.wireOp",EDGE,"E653"),sQuery(id+"F0.wireOp",EDGE,"E654"),sQuery(id+"F0.wireOp",EDGE,"E655"),sQuery(id+"F0.wireOp",EDGE,"E656"),sQuery(id+"F0.wireOp",EDGE,"E657"),sQuery(id+"F0.wireOp",EDGE,"E658"),sQuery(id+"F0.wireOp",EDGE,"E659"),sQuery(id+"F0.wireOp",EDGE,"E660"),sQuery(id+"F0.wireOp",EDGE,"E661"),sQuery(id+"F0.wireOp",EDGE,"E662"),sQuery(id+"F0.wireOp",EDGE,"E663"),sQuery(id+"F0.wireOp",EDGE,"E664"),sQuery(id+"F0.wireOp",EDGE,"E665"),sQuery(id+"F0.wireOp",EDGE,"E666"),sQuery(id+"F0.wireOp",EDGE,"E667"),sQuery(id+"F0.wireOp",EDGE,"E668"),sQuery(id+"F0.wireOp",EDGE,"E669"),sQuery(id+"F0.wireOp",EDGE,"E670"),sQuery(id+"F0.wireOp",EDGE,"E671"),sQuery(id+"F0.wireOp",EDGE,"E672"),sQuery(id+"F0.wireOp",EDGE,"E673"),sQuery(id+"F0.wireOp",EDGE,"E674"),sQuery(id+"F0.wireOp",EDGE,"E675"),sQuery(id+"F0.wireOp",EDGE,"E676"),sQuery(id+"F0.wireOp",EDGE,"E677"),sQuery(id+"F0.wireOp",EDGE,"E678"),sQuery(id+"F0.wireOp",EDGE,"E679"),sQuery(id+"F0.wireOp",EDGE,"E680"),sQuery(id+"F0.wireOp",EDGE,"E681"),sQuery(id+"F0.wireOp",EDGE,"E682"),sQuery(id+"F0.wireOp",EDGE,"E683"),sQuery(id+"F0.wireOp",EDGE,"E684"),sQuery(id+"F0.wireOp",EDGE,"E685"),sQuery(id+"F0.wireOp",EDGE,"E686"),sQuery(id+"F0.wireOp",EDGE,"E687"),sQuery(id+"F0.wireOp",EDGE,"E688"),sQuery(id+"F0.wireOp",EDGE,"E689"),sQuery(id+"F0.wireOp",EDGE,"E690"),sQuery(id+"F0.wireOp",EDGE,"E691"),sQuery(id+"F0.wireOp",EDGE,"E692"),sQuery(id+"F0.wireOp",EDGE,"E693"),sQuery(id+"F0.wireOp",EDGE,"E694"),sQuery(id+"F0.wireOp",EDGE,"E695"),sQuery(id+"F0.wireOp",EDGE,"E696"),sQuery(id+"F0.wireOp",EDGE,"E697"),sQuery(id+"F0.wireOp",EDGE,"E698"),sQuery(id+"F0.wireOp",EDGE,"E699"),sQuery(id+"F0.wireOp",EDGE,"E700"),sQuery(id+"F0.wireOp",EDGE,"E701"),sQuery(id+"F0.wireOp",EDGE,"E702"),sQuery(id+"F0.wireOp",EDGE,"E703"),sQuery(id+"F0.wireOp",EDGE,"E704"),sQuery(id+"F0.wireOp",EDGE,"E705"),sQuery(id+"F0.wireOp",EDGE,"E706"),sQuery(id+"F0.wireOp",EDGE,"E707"),sQuery(id+"F0.wireOp",EDGE,"E708"),sQuery(id+"F0.wireOp",EDGE,"E709"),sQuery(id+"F0.wireOp",EDGE,"E710"),sQuery(id+"F0.wireOp",EDGE,"E711"),sQuery(id+"F0.wireOp",EDGE,"E712"),sQuery(id+"F0.wireOp",EDGE,"E713"),sQuery(id+"F0.wireOp",EDGE,"E714"),sQuery(id+"F0.wireOp",EDGE,"E715"),sQuery(id+"F0.wireOp",EDGE,"E716"),sQuery(id+"F0.wireOp",EDGE,"E717"),sQuery(id+"F0.wireOp",EDGE,"E718"),sQuery(id+"F0.wireOp",EDGE,"E719"),sQuery(id+"F0.wireOp",EDGE,"E720"),sQuery(id+"F0.wireOp",EDGE,"E721"),sQuery(id+"F0.wireOp",EDGE,"E722"),sQuery(id+"F0.wireOp",EDGE,"E723"),sQuery(id+"F0.wireOp",EDGE,"E724"),sQuery(id+"F0.wireOp",EDGE,"E725"),sQuery(id+"F0.wireOp",EDGE,"E726"),sQuery(id+"F0.wireOp",EDGE,"E727"),sQuery(id+"F0.wireOp",EDGE,"E728"),sQuery(id+"F0.wireOp",EDGE,"E729"),sQuery(id+"F0.wireOp",EDGE,"E730"),sQuery(id+"F0.wireOp",EDGE,"E731"),sQuery(id+"F0.wireOp",EDGE,"E732"),sQuery(id+"F0.wireOp",EDGE,"E733"),sQuery(id+"F0.wireOp",EDGE,"E734"),sQuery(id+"F0.wireOp",EDGE,"E735"),sQuery(id+"F0.wireOp",EDGE,"E736"),sQuery(id+"F0.wireOp",EDGE,"E737"),sQuery(id+"F0.wireOp",EDGE,"E738"),sQuery(id+"F0.wireOp",EDGE,"E739"),sQuery(id+"F0.wireOp",EDGE,"E740"),sQuery(id+"F0.wireOp",EDGE,"E741"),sQuery(id+"F0.wireOp",EDGE,"E742"),sQuery(id+"F0.wireOp",EDGE,"E743"),sQuery(id+"F0.wireOp",EDGE,"E744"),sQuery(id+"F0.wireOp",EDGE,"E745"),sQuery(id+"F0.wireOp",EDGE,"E746"),sQuery(id+"F0.wireOp",EDGE,"E747"),sQuery(id+"F0.wireOp",EDGE,"E748"),sQuery(id+"F0.wireOp",EDGE,"E749"),sQuery(id+"F0.wireOp",EDGE,"E750"),sQuery(id+"F0.wireOp",EDGE,"E751"),sQuery(id+"F0.wireOp",EDGE,"E752"),sQuery(id+"F0.wireOp",EDGE,"E753"),sQuery(id+"F0.wireOp",EDGE,"E754"),sQuery(id+"F0.wireOp",EDGE,"E755"),sQuery(id+"F0.wireOp",EDGE,"E756"),sQuery(id+"F0.wireOp",EDGE,"E757"),sQuery(id+"F0.wireOp",EDGE,"E758"),sQuery(id+"F0.wireOp",EDGE,"E759"),sQuery(id+"F0.wireOp",EDGE,"E760"),sQuery(id+"F0.wireOp",EDGE,"E761"),sQuery(id+"F0.wireOp",EDGE,"E762"),sQuery(id+"F0.wireOp",EDGE,"E763"),sQuery(id+"F0.wireOp",EDGE,"E764"),sQuery(id+"F0.wireOp",EDGE,"E765"),sQuery(id+"F0.wireOp",EDGE,"E766"),sQuery(id+"F0.wireOp",EDGE,"E767"),sQuery(id+"F0.wireOp",EDGE,"E768"),sQuery(id+"F0.wireOp",EDGE,"E769"),sQuery(id+"F0.wireOp",EDGE,"E770"),sQuery(id+"F0.wireOp",EDGE,"E771"),sQuery(id+"F0.wireOp",EDGE,"E772"),sQuery(id+"F0.wireOp",EDGE,"E773"),sQuery(id+"F0.wireOp",EDGE,"E774"),sQuery(id+"F0.wireOp",EDGE,"E775"),sQuery(id+"F0.wireOp",EDGE,"E776"),sQuery(id+"F0.wireOp",EDGE,"E777"),sQuery(id+"F0.wireOp",EDGE,"E778"),sQuery(id+"F0.wireOp",EDGE,"E779"),sQuery(id+"F0.wireOp",EDGE,"E780"),sQuery(id+"F0.wireOp",EDGE,"E781"),sQuery(id+"F0.wireOp",EDGE,"E782"),sQuery(id+"F0.wireOp",EDGE,"E783"),sQuery(id+"F0.wireOp",EDGE,"E784"),sQuery(id+"F0.wireOp",EDGE,"E785"),sQuery(id+"F0.wireOp",EDGE,"E786"),sQuery(id+"F0.wireOp",EDGE,"E787"),sQuery(id+"F0.wireOp",EDGE,"E788"),sQuery(id+"F0.wireOp",EDGE,"E789"),sQuery(id+"F0.wireOp",EDGE,"E790"),sQuery(id+"F0.wireOp",EDGE,"E791"),sQuery(id+"F0.wireOp",EDGE,"E792"),sQuery(id+"F0.wireOp",EDGE,"E793"),sQuery(id+"F0.wireOp",EDGE,"E794"),sQuery(id+"F0.wireOp",EDGE,"E795"),sQuery(id+"F0.wireOp",EDGE,"E796"),sQuery(id+"F0.wireOp",EDGE,"E797"),sQuery(id+"F0.wireOp",EDGE,"E798"),sQuery(id+"F0.wireOp",EDGE,"E799"),sQuery(id+"F0.wireOp",EDGE,"E800"),sQuery(id+"F0.wireOp",EDGE,"E801"),sQuery(id+"F0.wireOp",EDGE,"E802"),sQuery(id+"F0.wireOp",EDGE,"E803"),sQuery(id+"F0.wireOp",EDGE,"E804"),sQuery(id+"F0.wireOp",EDGE,"E805"),sQuery(id+"F0.wireOp",EDGE,"E806"),sQuery(id+"F0.wireOp",EDGE,"E807"),sQuery(id+"F0.wireOp",EDGE,"E808"),sQuery(id+"F0.wireOp",EDGE,"E809"),sQuery(id+"F0.wireOp",EDGE,"E810"),sQuery(id+"F0.wireOp",EDGE,"E811"),sQuery(id+"F0.wireOp",EDGE,"E812"),sQuery(id+"F0.wireOp",EDGE,"E813"),sQuery(id+"F0.wireOp",EDGE,"E814"),sQuery(id+"F0.wireOp",EDGE,"E815"),sQuery(id+"F0.wireOp",EDGE,"E816"),sQuery(id+"F0.wireOp",EDGE,"E817"),sQuery(id+"F0.wireOp",EDGE,"E818"),sQuery(id+"F0.wireOp",EDGE,"E819"),sQuery(id+"F0.wireOp",EDGE,"E820"),sQuery(id+"F0.wireOp",EDGE,"E821"),sQuery(id+"F0.wireOp",EDGE,"E822"),sQuery(id+"F0.wireOp",EDGE,"E823"),sQuery(id+"F0.wireOp",EDGE,"E824"),sQuery(id+"F0.wireOp",EDGE,"E825"),sQuery(id+"F0.wireOp",EDGE,"E826"),sQuery(id+"F0.wireOp",EDGE,"E827"),sQuery(id+"F0.wireOp",EDGE,"E828"),sQuery(id+"F0.wireOp",EDGE,"E829"),sQuery(id+"F0.wireOp",EDGE,"E830"),sQuery(id+"F0.wireOp",EDGE,"E831"),sQuery(id+"F0.wireOp",EDGE,"E832"),sQuery(id+"F0.wireOp",EDGE,"E833"),sQuery(id+"F0.wireOp",EDGE,"E834"),sQuery(id+"F0.wireOp",EDGE,"E835"),sQuery(id+"F0.wireOp",EDGE,"E836"),sQuery(id+"F0.wireOp",EDGE,"E837"),sQuery(id+"F0.wireOp",EDGE,"E838"),sQuery(id+"F0.wireOp",EDGE,"E839"),sQuery(id+"F0.wireOp",EDGE,"E840"),sQuery(id+"F0.wireOp",EDGE,"E841"),sQuery(id+"F0.wireOp",EDGE,"E842"),sQuery(id+"F0.wireOp",EDGE,"E843"),sQuery(id+"F0.wireOp",EDGE,"E844"),sQuery(id+"F0.wireOp",EDGE,"E845"),sQuery(id+"F0.wireOp",EDGE,"E846"),sQuery(id+"F0.wireOp",EDGE,"E847"),sQuery(id+"F0.wireOp",EDGE,"E848"),sQuery(id+"F0.wireOp",EDGE,"E849"),sQuery(id+"F0.wireOp",EDGE,"E850"),sQuery(id+"F0.wireOp",EDGE,"E851"),sQuery(id+"F0.wireOp",EDGE,"E852"),sQuery(id+"F0.wireOp",EDGE,"E853"),sQuery(id+"F0.wireOp",EDGE,"E854"),sQuery(id+"F0.wireOp",EDGE,"E855"),sQuery(id+"F0.wireOp",EDGE,"E856"),sQuery(id+"F0.wireOp",EDGE,"E857"),sQuery(id+"F0.wireOp",EDGE,"E858"),sQuery(id+"F0.wireOp",EDGE,"E859"),sQuery(id+"F0.wireOp",EDGE,"E860"),sQuery(id+"F0.wireOp",EDGE,"E861"),sQuery(id+"F0.wireOp",EDGE,"E862"),sQuery(id+"F0.wireOp",EDGE,"E863"),sQuery(id+"F0.wireOp",EDGE,"E864"),sQuery(id+"F0.wireOp",EDGE,"E865"),sQuery(id+"F0.wireOp",EDGE,"E866"),sQuery(id+"F0.wireOp",EDGE,"E867"),sQuery(id+"F0.wireOp",EDGE,"E868"),sQuery(id+"F0.wireOp",EDGE,"E869"),sQuery(id+"F0.wireOp",EDGE,"E870"),sQuery(id+"F0.wireOp",EDGE,"E871"),sQuery(id+"F0.wireOp",EDGE,"E872"),sQuery(id+"F0.wireOp",EDGE,"E873"),sQuery(id+"F0.wireOp",EDGE,"E874"),sQuery(id+"F0.wireOp",EDGE,"E875"),sQuery(id+"F0.wireOp",EDGE,"E876"),sQuery(id+"F0.wireOp",EDGE,"E877"),sQuery(id+"F0.wireOp",EDGE,"E878"),sQuery(id+"F0.wireOp",EDGE,"E879"),sQuery(id+"F0.wireOp",EDGE,"E880"),sQuery(id+"F0.wireOp",EDGE,"E881"),sQuery(id+"F0.wireOp",EDGE,"E882"),sQuery(id+"F0.wireOp",EDGE,"E883"),sQuery(id+"F0.wireOp",EDGE,"E884"),sQuery(id+"F0.wireOp",EDGE,"E885"),sQuery(id+"F0.wireOp",EDGE,"E886"),sQuery(id+"F0.wireOp",EDGE,"E887"),sQuery(id+"F0.wireOp",EDGE,"E888"),sQuery(id+"F0.wireOp",EDGE,"E889"),sQuery(id+"F0.wireOp",EDGE,"E890"),sQuery(id+"F0.wireOp",EDGE,"E891"),sQuery(id+"F0.wireOp",EDGE,"E892"),sQuery(id+"F0.wireOp",EDGE,"E893"),sQuery(id+"F0.wireOp",EDGE,"E894"),sQuery(id+"F0.wireOp",EDGE,"E895"),sQuery(id+"F0.wireOp",EDGE,"E896"),sQuery(id+"F0.wireOp",EDGE,"E897"),sQuery(id+"F0.wireOp",EDGE,"E898"),sQuery(id+"F0.wireOp",EDGE,"E899"),sQuery(id+"F0.wireOp",EDGE,"E900"),sQuery(id+"F0.wireOp",EDGE,"E901"),sQuery(id+"F0.wireOp",EDGE,"E902"),sQuery(id+"F0.wireOp",EDGE,"E903"),sQuery(id+"F0.wireOp",EDGE,"E904"),sQuery(id+"F0.wireOp",EDGE,"E905"),sQuery(id+"F0.wireOp",EDGE,"E906"),sQuery(id+"F0.wireOp",EDGE,"E907"),sQuery(id+"F0.wireOp",EDGE,"E908"),sQuery(id+"F0.wireOp",EDGE,"E909"),sQuery(id+"F0.wireOp",EDGE,"E910"),sQuery(id+"F0.wireOp",EDGE,"E911"),sQuery(id+"F0.wireOp",EDGE,"E912"),sQuery(id+"F0.wireOp",EDGE,"E913"),sQuery(id+"F0.wireOp",EDGE,"E914"),sQuery(id+"F0.wireOp",EDGE,"E915"),sQuery(id+"F0.wireOp",EDGE,"E916"),sQuery(id+"F0.wireOp",EDGE,"E917"),sQuery(id+"F0.wireOp",EDGE,"E918"),sQuery(id+"F0.wireOp",EDGE,"E919"),sQuery(id+"F0.wireOp",EDGE,"E920"),sQuery(id+"F0.wireOp",EDGE,"E921"),sQuery(id+"F0.wireOp",EDGE,"E922"),sQuery(id+"F0.wireOp",EDGE,"E923"),sQuery(id+"F0.wireOp",EDGE,"E924"),sQuery(id+"F0.wireOp",EDGE,"E925"),sQuery(id+"F0.wireOp",EDGE,"E926"),sQuery(id+"F0.wireOp",EDGE,"E927"),sQuery(id+"F0.wireOp",EDGE,"E928"),sQuery(id+"F0.wireOp",EDGE,"E929"),sQuery(id+"F0.wireOp",EDGE,"E930"),sQuery(id+"F0.wireOp",EDGE,"E931"),sQuery(id+"F0.wireOp",EDGE,"E932"),sQuery(id+"F0.wireOp",EDGE,"E933"),sQuery(id+"F0.wireOp",EDGE,"E934"),sQuery(id+"F0.wireOp",EDGE,"E935"),sQuery(id+"F0.wireOp",EDGE,"E936"),sQuery(id+"F0.wireOp",EDGE,"E937"),sQuery(id+"F0.wireOp",EDGE,"E938"),sQuery(id+"F0.wireOp",EDGE,"E939"),sQuery(id+"F0.wireOp",EDGE,"E940"),sQuery(id+"F0.wireOp",EDGE,"E941"),sQuery(id+"F0.wireOp",EDGE,"E942"),sQuery(id+"F0.wireOp",EDGE,"E943"),sQuery(id+"F0.wireOp",EDGE,"E944"),sQuery(id+"F0.wireOp",EDGE,"E945"),sQuery(id+"F0.wireOp",EDGE,"E946"),sQuery(id+"F0.wireOp",EDGE,"E947"),sQuery(id+"F0.wireOp",EDGE,"E948"),sQuery(id+"F0.wireOp",EDGE,"E949"),sQuery(id+"F0.wireOp",EDGE,"E950"),sQuery(id+"F0.wireOp",EDGE,"E951"),sQuery(id+"F0.wireOp",EDGE,"E952"),sQuery(id+"F0.wireOp",EDGE,"E953"),sQuery(id+"F0.wireOp",EDGE,"E954"),sQuery(id+"F0.wireOp",EDGE,"E955"),sQuery(id+"F0.wireOp",EDGE,"E956"),sQuery(id+"F0.wireOp",EDGE,"E957"),sQuery(id+"F0.wireOp",EDGE,"E958"),sQuery(id+"F0.wireOp",EDGE,"E959"),sQuery(id+"F0.wireOp",EDGE,"E960"),sQuery(id+"F0.wireOp",EDGE,"E961"),sQuery(id+"F0.wireOp",EDGE,"E962"),sQuery(id+"F0.wireOp",EDGE,"E963"),sQuery(id+"F0.wireOp",EDGE,"E964"),sQuery(id+"F0.wireOp",EDGE,"E965"),sQuery(id+"F0.wireOp",EDGE,"E966"),sQuery(id+"F0.wireOp",EDGE,"E967"),sQuery(id+"F0.wireOp",EDGE,"E968"),sQuery(id+"F0.wireOp",EDGE,"E969"),sQuery(id+"F0.wireOp",EDGE,"E970"),sQuery(id+"F0.wireOp",EDGE,"E971"),sQuery(id+"F0.wireOp",EDGE,"E972"),sQuery(id+"F0.wireOp",EDGE,"E973"),sQuery(id+"F0.wireOp",EDGE,"E974"),sQuery(id+"F0.wireOp",EDGE,"E975"),sQuery(id+"F0.wireOp",EDGE,"E976"),sQuery(id+"F0.wireOp",EDGE,"E977"),sQuery(id+"F0.wireOp",EDGE,"E978"),sQuery(id+"F0.wireOp",EDGE,"E979"),sQuery(id+"F0.wireOp",EDGE,"E980"),sQuery(id+"F0.wireOp",EDGE,"E981"),sQuery(id+"F0.wireOp",EDGE,"E982"),sQuery(id+"F0.wireOp",EDGE,"E983"),sQuery(id+"F0.wireOp",EDGE,"E984"),sQuery(id+"F0.wireOp",EDGE,"E985"),sQuery(id+"F0.wireOp",EDGE,"E986"),sQuery(id+"F0.wireOp",EDGE,"E987"),sQuery(id+"F0.wireOp",EDGE,"E988"),sQuery(id+"F0.wireOp",EDGE,"E989"),sQuery(id+"F0.wireOp",EDGE,"E990"),sQuery(id+"F0.wireOp",EDGE,"E991"),sQuery(id+"F0.wireOp",EDGE,"E992"),sQuery(id+"F0.wireOp",EDGE,"E993"),sQuery(id+"F0.wireOp",EDGE,"E994"),sQuery(id+"F0.wireOp",EDGE,"E995"),sQuery(id+"F0.wireOp",EDGE,"E996"),sQuery(id+"F0.wireOp",EDGE,"E997"),sQuery(id+"F0.wireOp",EDGE,"E998"),sQuery(id+"F0.wireOp",EDGE,"E999"),sQuery(id+"F0.wireOp",EDGE,"E1000"),sQuery(id+"F0.wireOp",EDGE,"E1001"),sQuery(id+"F0.wireOp",EDGE,"E1002"),sQuery(id+"F0.wireOp",EDGE,"E1003"),sQuery(id+"F0.wireOp",EDGE,"E1004"),sQuery(id+"F0.wireOp",EDGE,"E1005"),sQuery(id+"F0.wireOp",EDGE,"E1006"),sQuery(id+"F0.wireOp",EDGE,"E1007"),sQuery(id+"F0.wireOp",EDGE,"E1008"),sQuery(id+"F0.wireOp",EDGE,"E1009"),sQuery(id+"F0.wireOp",EDGE,"E1010"),sQuery(id+"F0.wireOp",EDGE,"E1011"),sQuery(id+"F0.wireOp",EDGE,"E1012"),sQuery(id+"F0.wireOp",EDGE,"E1013"),sQuery(id+"F0.wireOp",EDGE,"E1014"),sQuery(id+"F0.wireOp",EDGE,"E1015"),sQuery(id+"F0.wireOp",EDGE,"E1016"),sQuery(id+"F0.wireOp",EDGE,"E1017"),sQuery(id+"F0.wireOp",EDGE,"E1018"),sQuery(id+"F0.wireOp",EDGE,"E1019"),sQuery(id+"F0.wireOp",EDGE,"E1020"),sQuery(id+"F0.wireOp",EDGE,"E1021"),sQuery(id+"F0.wireOp",EDGE,"E1022"),sQuery(id+"F0.wireOp",EDGE,"E1023"),sQuery(id+"F0.wireOp",EDGE,"E1024"),sQuery(id+"F0.wireOp",EDGE,"E1025"),sQuery(id+"F0.wireOp",EDGE,"E1026"),sQuery(id+"F0.wireOp",EDGE,"E1027"),sQuery(id+"F0.wireOp",EDGE,"E1028"),sQuery(id+"F0.wireOp",EDGE,"E1029"),sQuery(id+"F0.wireOp",EDGE,"E1030"),sQuery(id+"F0.wireOp",EDGE,"E1031"),sQuery(id+"F0.wireOp",EDGE,"E1032"),sQuery(id+"F0.wireOp",EDGE,"E1033"),sQuery(id+"F0.wireOp",EDGE,"E1034"),sQuery(id+"F0.wireOp",EDGE,"E1035"),sQuery(id+"F0.wireOp",EDGE,"E1036"),sQuery(id+"F0.wireOp",EDGE,"E1037"),sQuery(id+"F0.wireOp",EDGE,"E1038"),sQuery(id+"F0.wireOp",EDGE,"E1039"),sQuery(id+"F0.wireOp",EDGE,"E1040"),sQuery(id+"F0.wireOp",EDGE,"E1041"),sQuery(id+"F0.wireOp",EDGE,"E1042"),sQuery(id+"F0.wireOp",EDGE,"E1043"),sQuery(id+"F0.wireOp",EDGE,"E1044"),sQuery(id+"F0.wireOp",EDGE,"E1045"),sQuery(id+"F0.wireOp",EDGE,"E1046"),sQuery(id+"F0.wireOp",EDGE,"E1047"),sQuery(id+"F0.wireOp",EDGE,"E1048"),sQuery(id+"F0.wireOp",EDGE,"E1049"),sQuery(id+"F0.wireOp",EDGE,"E1050"),sQuery(id+"F0.wireOp",EDGE,"E1051"),sQuery(id+"F0.wireOp",EDGE,"E1052"),sQuery(id+"F0.wireOp",EDGE,"E1053"),sQuery(id+"F0.wireOp",EDGE,"E1054"),sQuery(id+"F0.wireOp",EDGE,"E1055"),sQuery(id+"F0.wireOp",EDGE,"E1056"),sQuery(id+"F0.wireOp",EDGE,"E1057"),sQuery(id+"F0.wireOp",EDGE,"E1058"),sQuery(id+"F0.wireOp",EDGE,"E1059"),sQuery(id+"F0.wireOp",EDGE,"E1060"),sQuery(id+"F0.wireOp",EDGE,"E1061"),sQuery(id+"F0.wireOp",EDGE,"E1062"),sQuery(id+"F0.wireOp",EDGE,"E1063"),sQuery(id+"F0.wireOp",EDGE,"E1064"),sQuery(id+"F0.wireOp",EDGE,"E1065"),sQuery(id+"F0.wireOp",EDGE,"E1066"),sQuery(id+"F0.wireOp",EDGE,"E1067"),sQuery(id+"F0.wireOp",EDGE,"E1068"),sQuery(id+"F0.wireOp",EDGE,"E1069"),sQuery(id+"F0.wireOp",EDGE,"E1070"),sQuery(id+"F0.wireOp",EDGE,"E1071"),sQuery(id+"F0.wireOp",EDGE,"E1072"),sQuery(id+"F0.wireOp",EDGE,"E1073"),sQuery(id+"F0.wireOp",EDGE,"E1074"),sQuery(id+"F0.wireOp",EDGE,"E1075"),sQuery(id+"F0.wireOp",EDGE,"E1076"),sQuery(id+"F0.wireOp",EDGE,"E1077"),sQuery(id+"F0.wireOp",EDGE,"E1078"),sQuery(id+"F0.wireOp",EDGE,"E1079"),sQuery(id+"F0.wireOp",EDGE,"E1080"),sQuery(id+"F0.wireOp",EDGE,"E1081"),sQuery(id+"F0.wireOp",EDGE,"E1082"),sQuery(id+"F0.wireOp",EDGE,"E1083"),sQuery(id+"F0.wireOp",EDGE,"E1084"),sQuery(id+"F0.wireOp",EDGE,"E1085"),sQuery(id+"F0.wireOp",EDGE,"E1086"),sQuery(id+"F0.wireOp",EDGE,"E1087"),sQuery(id+"F0.wireOp",EDGE,"E1088"),sQuery(id+"F0.wireOp",EDGE,"E1089"),sQuery(id+"F0.wireOp",EDGE,"E1090"),sQuery(id+"F0.wireOp",EDGE,"E1091"),sQuery(id+"F0.wireOp",EDGE,"E1092"),sQuery(id+"F0.wireOp",EDGE,"E1093"),sQuery(id+"F0.wireOp",EDGE,"E1094"),sQuery(id+"F0.wireOp",EDGE,"E1095"),sQuery(id+"F0.wireOp",EDGE,"E1096"),sQuery(id+"F0.wireOp",EDGE,"E1097"),sQuery(id+"F0.wireOp",EDGE,"E1098"),sQuery(id+"F0.wireOp",EDGE,"E1099"),sQuery(id+"F0.wireOp",EDGE,"E1100"),sQuery(id+"F0.wireOp",EDGE,"E1101"),sQuery(id+"F0.wireOp",EDGE,"E1102"),sQuery(id+"F0.wireOp",EDGE,"E1103"),sQuery(id+"F0.wireOp",EDGE,"E1104"),sQuery(id+"F0.wireOp",EDGE,"E1105"),sQuery(id+"F0.wireOp",EDGE,"E1106"),sQuery(id+"F0.wireOp",EDGE,"E1107"),sQuery(id+"F0.wireOp",EDGE,"E1108"),sQuery(id+"F0.wireOp",EDGE,"E1109"),sQuery(id+"F0.wireOp",EDGE,"E1110"),sQuery(id+"F0.wireOp",EDGE,"E1111"),sQuery(id+"F0.wireOp",EDGE,"E1112"),sQuery(id+"F0.wireOp",EDGE,"E1113"),sQuery(id+"F0.wireOp",EDGE,"E1114"),sQuery(id+"F0.wireOp",EDGE,"E1115"),sQuery(id+"F0.wireOp",EDGE,"E1116"),sQuery(id+"F0.wireOp",EDGE,"E1117"),sQuery(id+"F0.wireOp",EDGE,"E1118"),sQuery(id+"F0.wireOp",EDGE,"E1119"),sQuery(id+"F0.wireOp",EDGE,"E1120"),sQuery(id+"F0.wireOp",EDGE,"E1121"),sQuery(id+"F0.wireOp",EDGE,"E1122"),sQuery(id+"F0.wireOp",EDGE,"E1123"),sQuery(id+"F0.wireOp",EDGE,"E1124"),sQuery(id+"F0.wireOp",EDGE,"E1125"),sQuery(id+"F0.wireOp",EDGE,"E1126"),sQuery(id+"F0.wireOp",EDGE,"E1127"),sQuery(id+"F0.wireOp",EDGE,"E1128"),sQuery(id+"F0.wireOp",EDGE,"E1129"),sQuery(id+"F0.wireOp",EDGE,"E1130"),sQuery(id+"F0.wireOp",EDGE,"E1131"),sQuery(id+"F0.wireOp",EDGE,"E1132"),sQuery(id+"F0.wireOp",EDGE,"E1133"),sQuery(id+"F0.wireOp",EDGE,"E1134"),sQuery(id+"F0.wireOp",EDGE,"E1135"),sQuery(id+"F0.wireOp",EDGE,"E1136"),sQuery(id+"F0.wireOp",EDGE,"E1137"),sQuery(id+"F0.wireOp",EDGE,"E1138"),sQuery(id+"F0.wireOp",EDGE,"E1138"),sQuery(id+"F0.wireOp",EDGE,"E1139"),sQuery(id+"F0.wireOp",EDGE,"E1140"),sQuery(id+"F0.wireOp",EDGE,"E1141"),sQuery(id+"F0.wireOp",EDGE,"E1142"),sQuery(id+"F0.wireOp",EDGE,"E1143"),sQuery(id+"F0.wireOp",EDGE,"E1144"),sQuery(id+"F0.wireOp",EDGE,"E1145"),sQuery(id+"F0.wireOp",EDGE,"E1146"),sQuery(id+"F0.wireOp",EDGE,"E1147"),sQuery(id+"F0.wireOp",EDGE,"E1148"),sQuery(id+"F0.wireOp",EDGE,"E1149"),sQuery(id+"F0.wireOp",EDGE,"E1150"),sQuery(id+"F0.wireOp",EDGE,"E1151"),sQuery(id+"F0.wireOp",EDGE,"E1152"),sQuery(id+"F0.wireOp",EDGE,"E1153"),sQuery(id+"F0.wireOp",EDGE,"E1154"),sQuery(id+"F0.wireOp",EDGE,"E1155"),sQuery(id+"F0.wireOp",EDGE,"E1156"),sQuery(id+"F0.wireOp",EDGE,"E1157"),sQuery(id+"F0.wireOp",EDGE,"E1158"),sQuery(id+"F0.wireOp",EDGE,"E1159"),sQuery(id+"F0.wireOp",EDGE,"E1160"),sQuery(id+"F0.wireOp",EDGE,"E1161"),sQuery(id+"F0.wireOp",EDGE,"E1162"),sQuery(id+"F0.wireOp",EDGE,"E1163"),sQuery(id+"F0.wireOp",EDGE,"E1164"),sQuery(id+"F0.wireOp",EDGE,"E1165"),sQuery(id+"F0.wireOp",EDGE,"E1166"),sQuery(id+"F0.wireOp",EDGE,"E1167"),sQuery(id+"F0.wireOp",EDGE,"E1168"),sQuery(id+"F0.wireOp",EDGE,"E1169"),sQuery(id+"F0.wireOp",EDGE,"E1170"),sQuery(id+"F0.wireOp",EDGE,"E1171"),sQuery(id+"F0.wireOp",EDGE,"E1172"),sQuery(id+"F0.wireOp",EDGE,"E1173"),sQuery(id+"F0.wireOp",EDGE,"E1174"),sQuery(id+"F0.wireOp",EDGE,"E1175"),sQuery(id+"F0.wireOp",EDGE,"E1176"),sQuery(id+"F0.wireOp",EDGE,"E1177"),sQuery(id+"F0.wireOp",EDGE,"E1178"),sQuery(id+"F0.wireOp",EDGE,"E1179"),sQuery(id+"F0.wireOp",EDGE,"E1180"),sQuery(id+"F0.wireOp",EDGE,"E1181"),sQuery(id+"F0.wireOp",EDGE,"E1182"),sQuery(id+"F0.wireOp",EDGE,"E1183"),sQuery(id+"F0.wireOp",EDGE,"E1184"),sQuery(id+"F0.wireOp",EDGE,"E1185"),sQuery(id+"F0.wireOp",EDGE,"E1186"),sQuery(id+"F0.wireOp",EDGE,"E1187"),sQuery(id+"F0.wireOp",EDGE,"E1188"),sQuery(id+"F0.wireOp",EDGE,"E1189"),sQuery(id+"F0.wireOp",EDGE,"E1190"),sQuery(id+"F0.wireOp",EDGE,"E1191"),sQuery(id+"F0.wireOp",EDGE,"E1192"),sQuery(id+"F0.wireOp",EDGE,"E1193"),sQuery(id+"F0.wireOp",EDGE,"E1194"),sQuery(id+"F0.wireOp",EDGE,"E1195"),sQuery(id+"F0.wireOp",EDGE,"E1196"),sQuery(id+"F0.wireOp",EDGE,"E1197"),sQuery(id+"F0.wireOp",EDGE,"E1198"),sQuery(id+"F0.wireOp",EDGE,"E1199"),sQuery(id+"F0.wireOp",EDGE,"E1200"),sQuery(id+"F0.wireOp",EDGE,"E1201"),sQuery(id+"F0.wireOp",EDGE,"E1202"),sQuery(id+"F0.wireOp",EDGE,"E1203"),sQuery(id+"F0.wireOp",EDGE,"E1204"),sQuery(id+"F0.wireOp",EDGE,"E1205"),sQuery(id+"F0.wireOp",EDGE,"E1206"),sQuery(id+"F0.wireOp",EDGE,"E1207"),sQuery(id+"F0.wireOp",EDGE,"E1208"),sQuery(id+"F0.wireOp",EDGE,"E1209"),sQuery(id+"F0.wireOp",EDGE,"E1210"),sQuery(id+"F0.wireOp",EDGE,"E1211"),sQuery(id+"F0.wireOp",EDGE,"E1212"),sQuery(id+"F0.wireOp",EDGE,"E1213"),sQuery(id+"F0.wireOp",EDGE,"E1214"),sQuery(id+"F0.wireOp",EDGE,"E1215"),sQuery(id+"F0.wireOp",EDGE,"E1216"),sQuery(id+"F0.wireOp",EDGE,"E1217"),sQuery(id+"F0.wireOp",EDGE,"E1218"),sQuery(id+"F0.wireOp",EDGE,"E1219"),sQuery(id+"F0.wireOp",EDGE,"E1220"),sQuery(id+"F0.wireOp",EDGE,"E1221"),sQuery(id+"F0.wireOp",EDGE,"E1222"),sQuery(id+"F0.wireOp",EDGE,"E1223"),sQuery(id+"F0.wireOp",EDGE,"E1224"),sQuery(id+"F0.wireOp",EDGE,"E1225"),sQuery(id+"F0.wireOp",EDGE,"E1226"),sQuery(id+"F0.wireOp",EDGE,"E1227"),sQuery(id+"F0.wireOp",EDGE,"E1228"),sQuery(id+"F0.wireOp",EDGE,"E1229"),sQuery(id+"F0.wireOp",EDGE,"E1230"),sQuery(id+"F0.wireOp",EDGE,"E1231"),sQuery(id+"F0.wireOp",EDGE,"E1232"),sQuery(id+"F0.wireOp",EDGE,"E1233"),sQuery(id+"F0.wireOp",EDGE,"E1234"),sQuery(id+"F0.wireOp",EDGE,"E1235"),sQuery(id+"F0.wireOp",EDGE,"E1236"),sQuery(id+"F0.wireOp",EDGE,"E1237"),sQuery(id+"F0.wireOp",EDGE,"E1238"),sQuery(id+"F0.wireOp",EDGE,"E1239"),sQuery(id+"F0.wireOp",EDGE,"E1240"),sQuery(id+"F0.wireOp",EDGE,"E1241"),sQuery(id+"F0.wireOp",EDGE,"E1242"),sQuery(id+"F0.wireOp",EDGE,"E1243"),sQuery(id+"F0.wireOp",EDGE,"E1244"),sQuery(id+"F0.wireOp",EDGE,"E1245"),sQuery(id+"F0.wireOp",EDGE,"E1246"),sQuery(id+"F0.wireOp",EDGE,"E1247"),sQuery(id+"F0.wireOp",EDGE,"E1248"),sQuery(id+"F0.wireOp",EDGE,"E1249"),sQuery(id+"F0.wireOp",EDGE,"E1250"),sQuery(id+"F0.wireOp",EDGE,"E1251"),sQuery(id+"F0.wireOp",EDGE,"E1252"),sQuery(id+"F0.wireOp",EDGE,"E1253"),sQuery(id+"F0.wireOp",EDGE,"E1254"),sQuery(id+"F0.wireOp",EDGE,"E1255"),sQuery(id+"F0.wireOp",EDGE,"E1256"),sQuery(id+"F0.wireOp",EDGE,"E1257"),sQuery(id+"F0.wireOp",EDGE,"E1258"),sQuery(id+"F0.wireOp",EDGE,"E1259"),sQuery(id+"F0.wireOp",EDGE,"E1260"),sQuery(id+"F0.wireOp",EDGE,"E1261"),sQuery(id+"F0.wireOp",EDGE,"E1262"),sQuery(id+"F0.wireOp",EDGE,"E1263"),sQuery(id+"F0.wireOp",EDGE,"E1264"),sQuery(id+"F0.wireOp",EDGE,"E1265"),sQuery(id+"F0.wireOp",EDGE,"E1266"),sQuery(id+"F0.wireOp",EDGE,"E1267"),sQuery(id+"F0.wireOp",EDGE,"E1268"),sQuery(id+"F0.wireOp",EDGE,"E1269"),sQuery(id+"F0.wireOp",EDGE,"E1270"),sQuery(id+"F0.wireOp",EDGE,"E1271"),sQuery(id+"F0.wireOp",EDGE,"E1272"),sQuery(id+"F0.wireOp",EDGE,"E1273"),sQuery(id+"F0.wireOp",EDGE,"E1274"),sQuery(id+"F0.wireOp",EDGE,"E1275"),sQuery(id+"F0.wireOp",EDGE,"E1276"),sQuery(id+"F0.wireOp",EDGE,"E1277"),sQuery(id+"F0.wireOp",EDGE,"E1278"),sQuery(id+"F0.wireOp",EDGE,"E1279"),sQuery(id+"F0.wireOp",EDGE,"E1280"),sQuery(id+"F0.wireOp",EDGE,"E1281"),sQuery(id+"F0.wireOp",EDGE,"E1282"),sQuery(id+"F0.wireOp",EDGE,"E1283"),sQuery(id+"F0.wireOp",EDGE,"E1284"),sQuery(id+"F0.wireOp",EDGE,"E1285"),sQuery(id+"F0.wireOp",EDGE,"E1286"),sQuery(id+"F0.wireOp",EDGE,"E1287"),sQuery(id+"F0.wireOp",EDGE,"E1288"),sQuery(id+"F0.wireOp",EDGE,"E1289"),sQuery(id+"F0.wireOp",EDGE,"E1290"),sQuery(id+"F0.wireOp",EDGE,"E1291"),sQuery(id+"F0.wireOp",EDGE,"E1292"),sQuery(id+"F0.wireOp",EDGE,"E1293"),sQuery(id+"F0.wireOp",EDGE,"E1294"),sQuery(id+"F0.wireOp",EDGE,"E1295"),sQuery(id+"F0.wireOp",EDGE,"E1296"),sQuery(id+"F0.wireOp",EDGE,"E1297"),sQuery(id+"F0.wireOp",EDGE,"E1298"),sQuery(id+"F0.wireOp",EDGE,"E1299"),sQuery(id+"F0.wireOp",EDGE,"E1300"),sQuery(id+"F0.wireOp",EDGE,"E1301"),sQuery(id+"F0.wireOp",EDGE,"E1302"),sQuery(id+"F0.wireOp",EDGE,"E1303"),sQuery(id+"F0.wireOp",EDGE,"E1304"),sQuery(id+"F0.wireOp",EDGE,"E1305"),sQuery(id+"F0.wireOp",EDGE,"E1306"),sQuery(id+"F0.wireOp",EDGE,"E1307"),sQuery(id+"F0.wireOp",EDGE,"E1308"),sQuery(id+"F0.wireOp",EDGE,"E1309"),sQuery(id+"F0.wireOp",EDGE,"E1310"),sQuery(id+"F0.wireOp",EDGE,"E1311"),sQuery(id+"F0.wireOp",EDGE,"E1312"),sQuery(id+"F0.wireOp",EDGE,"E1313"),sQuery(id+"F0.wireOp",EDGE,"E1314"),sQuery(id+"F0.wireOp",EDGE,"E1315"),sQuery(id+"F0.wireOp",EDGE,"E1316"),sQuery(id+"F0.wireOp",EDGE,"E1317"),sQuery(id+"F0.wireOp",EDGE,"E1318"),sQuery(id+"F0.wireOp",EDGE,"E1319"),sQuery(id+"F0.wireOp",EDGE,"E1320"),sQuery(id+"F0.wireOp",EDGE,"E1321"),sQuery(id+"F0.wireOp",EDGE,"E1322"),sQuery(id+"F0.wireOp",EDGE,"E1323"),sQuery(id+"F0.wireOp",EDGE,"E1324"),sQuery(id+"F0.wireOp",EDGE,"E1325"),sQuery(id+"F0.wireOp",EDGE,"E1326"),sQuery(id+"F0.wireOp",EDGE,"E1327"),sQuery(id+"F0.wireOp",EDGE,"E1328"),sQuery(id+"F0.wireOp",EDGE,"E1329"),sQuery(id+"F0.wireOp",EDGE,"E1330"),sQuery(id+"F0.wireOp",EDGE,"E1331"),sQuery(id+"F0.wireOp",EDGE,"E1332"),sQuery(id+"F0.wireOp",EDGE,"E1333"),sQuery(id+"F0.wireOp",EDGE,"E1334"),sQuery(id+"F0.wireOp",EDGE,"E1335"),sQuery(id+"F0.wireOp",EDGE,"E1336"),sQuery(id+"F0.wireOp",EDGE,"E1337"),sQuery(id+"F0.wireOp",EDGE,"E1338"),sQuery(id+"F0.wireOp",EDGE,"E1339"),sQuery(id+"F0.wireOp",EDGE,"E1340"),sQuery(id+"F0.wireOp",EDGE,"E1341"),sQuery(id+"F0.wireOp",EDGE,"E1342"),sQuery(id+"F0.wireOp",EDGE,"E1343"),sQuery(id+"F0.wireOp",EDGE,"E1344"),sQuery(id+"F0.wireOp",EDGE,"E1345"),sQuery(id+"F0.wireOp",EDGE,"E1346"),sQuery(id+"F0.wireOp",EDGE,"E1347"),sQuery(id+"F0.wireOp",EDGE,"E1348"),sQuery(id+"F0.wireOp",EDGE,"E1349"),sQuery(id+"F0.wireOp",EDGE,"E1350"),sQuery(id+"F0.wireOp",EDGE,"E1351"),sQuery(id+"F0.wireOp",EDGE,"E1352"),sQuery(id+"F0.wireOp",EDGE,"E1353"),sQuery(id+"F0.wireOp",EDGE,"E1354"),sQuery(id+"F0.wireOp",EDGE,"E1355"),sQuery(id+"F0.wireOp",EDGE,"E1356"),sQuery(id+"F0.wireOp",EDGE,"E1357"),sQuery(id+"F0.wireOp",EDGE,"E1358"),sQuery(id+"F0.wireOp",EDGE,"E1359"),sQuery(id+"F0.wireOp",EDGE,"E1360"),sQuery(id+"F0.wireOp",EDGE,"E1361"),sQuery(id+"F0.wireOp",EDGE,"E1362"),sQuery(id+"F0.wireOp",EDGE,"E1363"),sQuery(id+"F0.wireOp",EDGE,"E1364"),sQuery(id+"F0.wireOp",EDGE,"E1365"),sQuery(id+"F0.wireOp",EDGE,"E1366"),sQuery(id+"F0.wireOp",EDGE,"E1367"),sQuery(id+"F0.wireOp",EDGE,"E1368"),sQuery(id+"F0.wireOp",EDGE,"E1369"),sQuery(id+"F0.wireOp",EDGE,"E1370"),sQuery(id+"F0.wireOp",EDGE,"E1371"),sQuery(id+"F0.wireOp",EDGE,"E1372"),sQuery(id+"F0.wireOp",EDGE,"E1373"),sQuery(id+"F0.wireOp",EDGE,"E1374"),sQuery(id+"F0.wireOp",EDGE,"E1375"),sQuery(id+"F0.wireOp",EDGE,"E1376"),sQuery(id+"F0.wireOp",EDGE,"E1377"),sQuery(id+"F0.wireOp",EDGE,"E1378"),sQuery(id+"F0.wireOp",EDGE,"E1379"),sQuery(id+"F0.wireOp",EDGE,"E1380"),sQuery(id+"F0.wireOp",EDGE,"E1381"),sQuery(id+"F0.wireOp",EDGE,"E1382"),sQuery(id+"F0.wireOp",EDGE,"E1383"),sQuery(id+"F0.wireOp",EDGE,"E1384"),sQuery(id+"F0.wireOp",EDGE,"E1385"),sQuery(id+"F0.wireOp",EDGE,"E1386"),sQuery(id+"F0.wireOp",EDGE,"E1387"),sQuery(id+"F0.wireOp",EDGE,"E1388"),sQuery(id+"F0.wireOp",EDGE,"E1389"),sQuery(id+"F0.wireOp",EDGE,"E1390"),sQuery(id+"F0.wireOp",EDGE,"E1391"),sQuery(id+"F0.wireOp",EDGE,"E1392"),sQuery(id+"F0.wireOp",EDGE,"E1393"),sQuery(id+"F0.wireOp",EDGE,"E1394"),sQuery(id+"F0.wireOp",EDGE,"E1395"),sQuery(id+"F0.wireOp",EDGE,"E1396"),sQuery(id+"F0.wireOp",EDGE,"E1397"),sQuery(id+"F0.wireOp",EDGE,"E1398"),sQuery(id+"F0.wireOp",EDGE,"E1399"),sQuery(id+"F0.wireOp",EDGE,"E1400"),sQuery(id+"F0.wireOp",EDGE,"E1401"),sQuery(id+"F0.wireOp",EDGE,"E1402"),sQuery(id+"F0.wireOp",EDGE,"E1403"),sQuery(id+"F0.wireOp",EDGE,"E1404"),sQuery(id+"F0.wireOp",EDGE,"E1405"),sQuery(id+"F0.wireOp",EDGE,"E1406"),sQuery(id+"F0.wireOp",EDGE,"E1407"),sQuery(id+"F0.wireOp",EDGE,"E1408"),sQuery(id+"F0.wireOp",EDGE,"E1409"),sQuery(id+"F0.wireOp",EDGE,"E1410"),sQuery(id+"F0.wireOp",EDGE,"E1411"),sQuery(id+"F0.wireOp",EDGE,"E1412"),sQuery(id+"F0.wireOp",EDGE,"E1413"),sQuery(id+"F0.wireOp",EDGE,"E1414"),sQuery(id+"F0.wireOp",EDGE,"E1415"),sQuery(id+"F0.wireOp",EDGE,"E1416"),sQuery(id+"F0.wireOp",EDGE,"E1417"),sQuery(id+"F0.wireOp",EDGE,"E1418"),sQuery(id+"F0.wireOp",EDGE,"E1419"),sQuery(id+"F0.wireOp",EDGE,"E1420"),sQuery(id+"F0.wireOp",EDGE,"E1421"),sQuery(id+"F0.wireOp",EDGE,"E1422"),sQuery(id+"F0.wireOp",EDGE,"E1423"),sQuery(id+"F0.wireOp",EDGE,"E1424"),sQuery(id+"F0.wireOp",EDGE,"E1425"),sQuery(id+"F0.wireOp",EDGE,"E1426"),sQuery(id+"F0.wireOp",EDGE,"E1427"),sQuery(id+"F0.wireOp",EDGE,"E1428"),sQuery(id+"F0.wireOp",EDGE,"E1429"),sQuery(id+"F0.wireOp",EDGE,"E1430"),sQuery(id+"F0.wireOp",EDGE,"E1431"),sQuery(id+"F0.wireOp",EDGE,"E1432"),sQuery(id+"F0.wireOp",EDGE,"E1433"),sQuery(id+"F0.wireOp",EDGE,"E1434"),sQuery(id+"F0.wireOp",EDGE,"E1435"),sQuery(id+"F0.wireOp",EDGE,"E1436"),sQuery(id+"F0.wireOp",EDGE,"E1437"),sQuery(id+"F0.wireOp",EDGE,"E1438"),sQuery(id+"F0.wireOp",EDGE,"E1439"),sQuery(id+"F0.wireOp",EDGE,"E1440"),sQuery(id+"F0.wireOp",EDGE,"E1441"),sQuery(id+"F0.wireOp",EDGE,"E1442"),sQuery(id+"F0.wireOp",EDGE,"E1443"),sQuery(id+"F0.wireOp",EDGE,"E1444"),sQuery(id+"F0.wireOp",EDGE,"E1445"),sQuery(id+"F0.wireOp",EDGE,"E1446"),sQuery(id+"F0.wireOp",EDGE,"E1447"),sQuery(id+"F0.wireOp",EDGE,"E1448"),sQuery(id+"F0.wireOp",EDGE,"E1449"),sQuery(id+"F0.wireOp",EDGE,"E1450"),sQuery(id+"F0.wireOp",EDGE,"E1451"),sQuery(id+"F0.wireOp",EDGE,"E1452"),sQuery(id+"F0.wireOp",EDGE,"E1453"),sQuery(id+"F0.wireOp",EDGE,"E1454"),sQuery(id+"F0.wireOp",EDGE,"E1455"),sQuery(id+"F0.wireOp",EDGE,"E1456"),sQuery(id+"F0.wireOp",EDGE,"E1457"),sQuery(id+"F0.wireOp",EDGE,"E1458"),sQuery(id+"F0.wireOp",EDGE,"E1459"),sQuery(id+"F0.wireOp",EDGE,"E1460"),sQuery(id+"F0.wireOp",EDGE,"E1461"),sQuery(id+"F0.wireOp",EDGE,"E1462"),sQuery(id+"F0.wireOp",EDGE,"E1463"),sQuery(id+"F0.wireOp",EDGE,"E1464"),sQuery(id+"F0.wireOp",EDGE,"E1465"),sQuery(id+"F0.wireOp",EDGE,"E1466"),sQuery(id+"F0.wireOp",EDGE,"E1467"),sQuery(id+"F0.wireOp",EDGE,"E1468"),sQuery(id+"F0.wireOp",EDGE,"E1469"),sQuery(id+"F0.wireOp",EDGE,"E1470"),sQuery(id+"F0.wireOp",EDGE,"E1471"),sQuery(id+"F0.wireOp",EDGE,"E1472"),sQuery(id+"F0.wireOp",EDGE,"E1473"),sQuery(id+"F0.wireOp",EDGE,"E1474"),sQuery(id+"F0.wireOp",EDGE,"E1475"),sQuery(id+"F0.wireOp",EDGE,"E1476"),sQuery(id+"F0.wireOp",EDGE,"E1477"),sQuery(id+"F0.wireOp",EDGE,"E1478"),sQuery(id+"F0.wireOp",EDGE,"E1479"),sQuery(id+"F0.wireOp",EDGE,"E1480"),sQuery(id+"F0.wireOp",EDGE,"E1481"),sQuery(id+"F0.wireOp",EDGE,"E1482"),sQuery(id+"F0.wireOp",EDGE,"E1483"),sQuery(id+"F0.wireOp",EDGE,"E1484"),sQuery(id+"F0.wireOp",EDGE,"E1485"),sQuery(id+"F0.wireOp",EDGE,"E1486"),sQuery(id+"F0.wireOp",EDGE,"E1487"),sQuery(id+"F0.wireOp",EDGE,"E1488"),sQuery(id+"F0.wireOp",EDGE,"E1489"),sQuery(id+"F0.wireOp",EDGE,"E1490"),sQuery(id+"F0.wireOp",EDGE,"E1491"),sQuery(id+"F0.wireOp",EDGE,"E1492"),sQuery(id+"F0.wireOp",EDGE,"E1493"),sQuery(id+"F0.wireOp",EDGE,"E1494"),sQuery(id+"F0.wireOp",EDGE,"E1495"),sQuery(id+"F0.wireOp",EDGE,"E1496"),sQuery(id+"F0.wireOp",EDGE,"E1497"),sQuery(id+"F0.wireOp",EDGE,"E1498"),sQuery(id+"F0.wireOp",EDGE,"E1499"),sQuery(id+"F0.wireOp",EDGE,"E1500"),sQuery(id+"F0.wireOp",EDGE,"E1501"),sQuery(id+"F0.wireOp",EDGE,"E1502"),sQuery(id+"F0.wireOp",EDGE,"E1503"),sQuery(id+"F0.wireOp",EDGE,"E1504"),sQuery(id+"F0.wireOp",EDGE,"E1505"),sQuery(id+"F0.wireOp",EDGE,"E1506"),sQuery(id+"F0.wireOp",EDGE,"E1507"),sQuery(id+"F0.wireOp",EDGE,"E1508"),sQuery(id+"F0.wireOp",EDGE,"E1509"),sQuery(id+"F0.wireOp",EDGE,"E1510"),sQuery(id+"F0.wireOp",EDGE,"E1511"),sQuery(id+"F0.wireOp",EDGE,"E1512"),sQuery(id+"F0.wireOp",EDGE,"E1513"),sQuery(id+"F0.wireOp",EDGE,"E1514"),sQuery(id+"F0.wireOp",EDGE,"E1515"),sQuery(id+"F0.wireOp",EDGE,"E1516"),sQuery(id+"F0.wireOp",EDGE,"E1517"),sQuery(id+"F0.wireOp",EDGE,"E1518"),sQuery(id+"F0.wireOp",EDGE,"E1519"),sQuery(id+"F0.wireOp",EDGE,"E1520"),sQuery(id+"F0.wireOp",EDGE,"E1521"),sQuery(id+"F0.wireOp",EDGE,"E1522"),sQuery(id+"F0.wireOp",EDGE,"E1523"),sQuery(id+"F0.wireOp",EDGE,"E1524"),sQuery(id+"F0.wireOp",EDGE,"E1525"),sQuery(id+"F0.wireOp",EDGE,"E1526"),sQuery(id+"F0.wireOp",EDGE,"E1527"),sQuery(id+"F0.wireOp",EDGE,"E1528"),sQuery(id+"F0.wireOp",EDGE,"E1529"),sQuery(id+"F0.wireOp",EDGE,"E1530"),sQuery(id+"F0.wireOp",EDGE,"E1531"),sQuery(id+"F0.wireOp",EDGE,"E1532"),sQuery(id+"F0.wireOp",EDGE,"E1533"),sQuery(id+"F0.wireOp",EDGE,"E1534"),sQuery(id+"F0.wireOp",EDGE,"E1535"),sQuery(id+"F0.wireOp",EDGE,"E1536"),sQuery(id+"F0.wireOp",EDGE,"E1537"),sQuery(id+"F0.wireOp",EDGE,"E1538"),sQuery(id+"F0.wireOp",EDGE,"E1539"),sQuery(id+"F0.wireOp",EDGE,"E1540"),sQuery(id+"F0.wireOp",EDGE,"E1541"),sQuery(id+"F0.wireOp",EDGE,"E1542"),sQuery(id+"F0.wireOp",EDGE,"E1543"),sQuery(id+"F0.wireOp",EDGE,"E1544"),sQuery(id+"F0.wireOp",EDGE,"E1545"),sQuery(id+"F0.wireOp",EDGE,"E1546"),sQuery(id+"F0.wireOp",EDGE,"E1547"),sQuery(id+"F0.wireOp",EDGE,"E1548"),sQuery(id+"F0.wireOp",EDGE,"E1549"),sQuery(id+"F0.wireOp",EDGE,"E1550"),sQuery(id+"F0.wireOp",EDGE,"E1551"),sQuery(id+"F0.wireOp",EDGE,"E1552"),sQuery(id+"F0.wireOp",EDGE,"E1553"),sQuery(id+"F0.wireOp",EDGE,"E1554"),sQuery(id+"F0.wireOp",EDGE,"E1555"),sQuery(id+"F0.wireOp",EDGE,"E1556"),sQuery(id+"F0.wireOp",EDGE,"E1557"),sQuery(id+"F0.wireOp",EDGE,"E1558"),sQuery(id+"F0.wireOp",EDGE,"E1559"),sQuery(id+"F0.wireOp",EDGE,"E1560"),sQuery(id+"F0.wireOp",EDGE,"E1561"),sQuery(id+"F0.wireOp",EDGE,"E1562"),sQuery(id+"F0.wireOp",EDGE,"E1563"),sQuery(id+"F0.wireOp",EDGE,"E1564"),sQuery(id+"F0.wireOp",EDGE,"E1565"),sQuery(id+"F0.wireOp",EDGE,"E1566"),sQuery(id+"F0.wireOp",EDGE,"E1567"),sQuery(id+"F0.wireOp",EDGE,"E1568"),sQuery(id+"F0.wireOp",EDGE,"E1569"),sQuery(id+"F0.wireOp",EDGE,"E1570"),sQuery(id+"F0.wireOp",EDGE,"E1571"),sQuery(id+"F0.wireOp",EDGE,"E1572"),sQuery(id+"F0.wireOp",EDGE,"E1573"),sQuery(id+"F0.wireOp",EDGE,"E1574"),sQuery(id+"F0.wireOp",EDGE,"E1575"),sQuery(id+"F0.wireOp",EDGE,"E1576"),sQuery(id+"F0.wireOp",EDGE,"E1577"),sQuery(id+"F0.wireOp",EDGE,"E1578"),sQuery(id+"F0.wireOp",EDGE,"E1579"),sQuery(id+"F0.wireOp",EDGE,"E1580"),sQuery(id+"F0.wireOp",EDGE,"E1581"),sQuery(id+"F0.wireOp",EDGE,"E1582"),sQuery(id+"F0.wireOp",EDGE,"E1583"),sQuery(id+"F0.wireOp",EDGE,"E1584"),sQuery(id+"F0.wireOp",EDGE,"E1585"),sQuery(id+"F0.wireOp",EDGE,"E1586"),sQuery(id+"F0.wireOp",EDGE,"E1587"),sQuery(id+"F0.wireOp",EDGE,"E1588"),sQuery(id+"F0.wireOp",EDGE,"E1589"),sQuery(id+"F0.wireOp",EDGE,"E1590"),sQuery(id+"F0.wireOp",EDGE,"E1591"),sQuery(id+"F0.wireOp",EDGE,"E1592"),sQuery(id+"F0.wireOp",EDGE,"E1593"),sQuery(id+"F0.wireOp",EDGE,"E1594"),sQuery(id+"F0.wireOp",EDGE,"E1595"),sQuery(id+"F0.wireOp",EDGE,"E1596"),sQuery(id+"F0.wireOp",EDGE,"E1597"),sQuery(id+"F0.wireOp",EDGE,"E1598"),sQuery(id+"F0.wireOp",EDGE,"E1599"),sQuery(id+"F0.wireOp",EDGE,"E1600"),sQuery(id+"F0.wireOp",EDGE,"E1601"),sQuery(id+"F0.wireOp",EDGE,"E1602"),sQuery(id+"F0.wireOp",EDGE,"E1603"),sQuery(id+"F0.wireOp",EDGE,"E1604"),sQuery(id+"F0.wireOp",EDGE,"E1605"),sQuery(id+"F0.wireOp",EDGE,"E1606"),sQuery(id+"F0.wireOp",EDGE,"E1607"),sQuery(id+"F0.wireOp",EDGE,"E1608"),sQuery(id+"F0.wireOp",EDGE,"E1609"),sQuery(id+"F0.wireOp",EDGE,"E1610"),sQuery(id+"F0.wireOp",EDGE,"E1611"),sQuery(id+"F0.wireOp",EDGE,"E1612"),sQuery(id+"F0.wireOp",EDGE,"E1613"),sQuery(id+"F0.wireOp",EDGE,"E1614"),sQuery(id+"F0.wireOp",EDGE,"E1615"),sQuery(id+"F0.wireOp",EDGE,"E1616"),sQuery(id+"F0.wireOp",EDGE,"E1617"),sQuery(id+"F0.wireOp",EDGE,"E1618"),sQuery(id+"F0.wireOp",EDGE,"E1619"),sQuery(id+"F0.wireOp",EDGE,"E1620"),sQuery(id+"F0.wireOp",EDGE,"E1621"),sQuery(id+"F0.wireOp",EDGE,"E1622"),sQuery(id+"F0.wireOp",EDGE,"E1623"),sQuery(id+"F0.wireOp",EDGE,"E1624"),sQuery(id+"F0.wireOp",EDGE,"E1625"),sQuery(id+"F0.wireOp",EDGE,"E1626"),sQuery(id+"F0.wireOp",EDGE,"E1627"),sQuery(id+"F0.wireOp",EDGE,"E1628"),sQuery(id+"F0.wireOp",EDGE,"E1629"),sQuery(id+"F0.wireOp",EDGE,"E1630"),sQuery(id+"F0.wireOp",EDGE,"E1631"),sQuery(id+"F0.wireOp",EDGE,"E1632"),sQuery(id+"F0.wireOp",EDGE,"E1633"),sQuery(id+"F0.wireOp",EDGE,"E1634"),sQuery(id+"F0.wireOp",EDGE,"E1635"),sQuery(id+"F0.wireOp",EDGE,"E1636"),sQuery(id+"F0.wireOp",EDGE,"E1637"),sQuery(id+"F0.wireOp",EDGE,"E1638"),sQuery(id+"F0.wireOp",EDGE,"E1639"),sQuery(id+"F0.wireOp",EDGE,"E1640"),sQuery(id+"F0.wireOp",EDGE,"E1641"),sQuery(id+"F0.wireOp",EDGE,"E1642"),sQuery(id+"F0.wireOp",EDGE,"E1643"),sQuery(id+"F0.wireOp",EDGE,"E1644"),sQuery(id+"F0.wireOp",EDGE,"E1645"),sQuery(id+"F0.wireOp",EDGE,"E1646"),sQuery(id+"F0.wireOp",EDGE,"E1647"),sQuery(id+"F0.wireOp",EDGE,"E1648"),sQuery(id+"F0.wireOp",EDGE,"E1649"),sQuery(id+"F0.wireOp",EDGE,"E1650"),sQuery(id+"F0.wireOp",EDGE,"E1651"),sQuery(id+"F0.wireOp",EDGE,"E1652"),sQuery(id+"F0.wireOp",EDGE,"E1653"),sQuery(id+"F0.wireOp",EDGE,"E1654"),sQuery(id+"F0.wireOp",EDGE,"E1655"),sQuery(id+"F0.wireOp",EDGE,"E1656"),sQuery(id+"F0.wireOp",EDGE,"E1657"),sQuery(id+"F0.wireOp",EDGE,"E1658"),sQuery(id+"F0.wireOp",EDGE,"E1659"),sQuery(id+"F0.wireOp",EDGE,"E1660"),sQuery(id+"F0.wireOp",EDGE,"E1661"),sQuery(id+"F0.wireOp",EDGE,"E1662"),sQuery(id+"F0.wireOp",EDGE,"E1663"),sQuery(id+"F0.wireOp",EDGE,"E1664"),sQuery(id+"F0.wireOp",EDGE,"E1665"),sQuery(id+"F0.wireOp",EDGE,"E1666"),sQuery(id+"F0.wireOp",EDGE,"E1667"),sQuery(id+"F0.wireOp",EDGE,"E1668"),sQuery(id+"F0.wireOp",EDGE,"E1669"),sQuery(id+"F0.wireOp",EDGE,"E1670"),sQuery(id+"F0.wireOp",EDGE,"E1671"),sQuery(id+"F0.wireOp",EDGE,"E1672"),sQuery(id+"F0.wireOp",EDGE,"E1673"),sQuery(id+"F0.wireOp",EDGE,"E1674"),sQuery(id+"F0.wireOp",EDGE,"E1675"),sQuery(id+"F0.wireOp",EDGE,"E1676"),sQuery(id+"F0.wireOp",EDGE,"E1677"),sQuery(id+"F0.wireOp",EDGE,"E1678"),sQuery(id+"F0.wireOp",EDGE,"E1679"),sQuery(id+"F0.wireOp",EDGE,"E1680"),sQuery(id+"F0.wireOp",EDGE,"E1681"),sQuery(id+"F0.wireOp",EDGE,"E1682"),sQuery(id+"F0.wireOp",EDGE,"E1683"),sQuery(id+"F0.wireOp",EDGE,"E1684"),sQuery(id+"F0.wireOp",EDGE,"E1685"),sQuery(id+"F0.wireOp",EDGE,"E1686"),sQuery(id+"F0.wireOp",EDGE,"E1687"),sQuery(id+"F0.wireOp",EDGE,"E1688"),sQuery(id+"F0.wireOp",EDGE,"E1689"),sQuery(id+"F0.wireOp",EDGE,"E1690"),sQuery(id+"F0.wireOp",EDGE,"E1691"),sQuery(id+"F0.wireOp",EDGE,"E1692"),sQuery(id+"F0.wireOp",EDGE,"E1693"),sQuery(id+"F0.wireOp",EDGE,"E1694"),sQuery(id+"F0.wireOp",EDGE,"E1695"),sQuery(id+"F0.wireOp",EDGE,"E1696"),sQuery(id+"F0.wireOp",EDGE,"E1697"),sQuery(id+"F0.wireOp",EDGE,"E1698"),sQuery(id+"F0.wireOp",EDGE,"E1699"),sQuery(id+"F0.wireOp",EDGE,"E1700"),sQuery(id+"F0.wireOp",EDGE,"E1701"),sQuery(id+"F0.wireOp",EDGE,"E1702"),sQuery(id+"F0.wireOp",EDGE,"E1703"),sQuery(id+"F0.wireOp",EDGE,"E1704"),sQuery(id+"F0.wireOp",EDGE,"E1705"),sQuery(id+"F0.wireOp",EDGE,"E1706"),sQuery(id+"F0.wireOp",EDGE,"E1707"),sQuery(id+"F0.wireOp",EDGE,"E1708"),sQuery(id+"F0.wireOp",EDGE,"E1709"),sQuery(id+"F0.wireOp",EDGE,"E1710"),sQuery(id+"F0.wireOp",EDGE,"E1711"),sQuery(id+"F0.wireOp",EDGE,"E1712"),sQuery(id+"F0.wireOp",EDGE,"E1713"),sQuery(id+"F0.wireOp",EDGE,"E1714"),sQuery(id+"F0.wireOp",EDGE,"E1715"),sQuery(id+"F0.wireOp",EDGE,"E1716"),sQuery(id+"F0.wireOp",EDGE,"E1717"),sQuery(id+"F0.wireOp",EDGE,"E1718"),sQuery(id+"F0.wireOp",EDGE,"E1719"),sQuery(id+"F0.wireOp",EDGE,"E1720"),sQuery(id+"F0.wireOp",EDGE,"E1721"),sQuery(id+"F0.wireOp",EDGE,"E1722"),sQuery(id+"F0.wireOp",EDGE,"E1723"),sQuery(id+"F0.wireOp",EDGE,"E1724"),sQuery(id+"F0.wireOp",EDGE,"E1725"),sQuery(id+"F0.wireOp",EDGE,"E1726"),sQuery(id+"F0.wireOp",EDGE,"E1727"),sQuery(id+"F0.wireOp",EDGE,"E1728"),sQuery(id+"F0.wireOp",EDGE,"E1729"),sQuery(id+"F0.wireOp",EDGE,"E1730"),sQuery(id+"F0.wireOp",EDGE,"E1731"),sQuery(id+"F0.wireOp",EDGE,"E1732"),sQuery(id+"F0.wireOp",EDGE,"E1733"),sQuery(id+"F0.wireOp",EDGE,"E1734"),sQuery(id+"F0.wireOp",EDGE,"E1735"),sQuery(id+"F0.wireOp",EDGE,"E1736"),sQuery(id+"F0.wireOp",EDGE,"E1737"),sQuery(id+"F0.wireOp",EDGE,"E1738"),sQuery(id+"F0.wireOp",EDGE,"E1739"),sQuery(id+"F0.wireOp",EDGE,"E1740"),sQuery(id+"F0.wireOp",EDGE,"E1741"),sQuery(id+"F0.wireOp",EDGE,"E1742"),sQuery(id+"F0.wireOp",EDGE,"E1743"),sQuery(id+"F0.wireOp",EDGE,"E1744"),sQuery(id+"F0.wireOp",EDGE,"E1745"),sQuery(id+"F0.wireOp",EDGE,"E1746"),sQuery(id+"F0.wireOp",EDGE,"E1747"),sQuery(id+"F0.wireOp",EDGE,"E1748"),sQuery(id+"F0.wireOp",EDGE,"E1749"),sQuery(id+"F0.wireOp",EDGE,"E1750"),sQuery(id+"F0.wireOp",EDGE,"E1751"),sQuery(id+"F0.wireOp",EDGE,"E1752"),sQuery(id+"F0.wireOp",EDGE,"E1753"),sQuery(id+"F0.wireOp",EDGE,"E1754"),sQuery(id+"F0.wireOp",EDGE,"E1755"),sQuery(id+"F0.wireOp",EDGE,"E1756"),sQuery(id+"F0.wireOp",EDGE,"E1757"),sQuery(id+"F0.wireOp",EDGE,"E1758"),sQuery(id+"F0.wireOp",EDGE,"E1759"),sQuery(id+"F0.wireOp",EDGE,"E1760"),sQuery(id+"F0.wireOp",EDGE,"E1761"),sQuery(id+"F0.wireOp",EDGE,"E1762"),sQuery(id+"F0.wireOp",EDGE,"E1763"),sQuery(id+"F0.wireOp",EDGE,"E1764"),sQuery(id+"F0.wireOp",EDGE,"E1765"),sQuery(id+"F0.wireOp",EDGE,"E1766"),sQuery(id+"F0.wireOp",EDGE,"E1767"),sQuery(id+"F0.wireOp",EDGE,"E1768"),sQuery(id+"F0.wireOp",EDGE,"E1769"),sQuery(id+"F0.wireOp",EDGE,"E1770"),sQuery(id+"F0.wireOp",EDGE,"E1771"),sQuery(id+"F0.wireOp",EDGE,"E1772"),sQuery(id+"F0.wireOp",EDGE,"E1773"),sQuery(id+"F0.wireOp",EDGE,"E1774"),sQuery(id+"F0.wireOp",EDGE,"E1775"),sQuery(id+"F0.wireOp",EDGE,"E1776"),sQuery(id+"F0.wireOp",EDGE,"E1777"),sQuery(id+"F0.wireOp",EDGE,"E1778"),sQuery(id+"F0.wireOp",EDGE,"E1779"),sQuery(id+"F0.wireOp",EDGE,"E1780"),sQuery(id+"F0.wireOp",EDGE,"E1781"),sQuery(id+"F0.wireOp",EDGE,"E1782"),sQuery(id+"F0.wireOp",EDGE,"E1783"),sQuery(id+"F0.wireOp",EDGE,"E1784"),sQuery(id+"F0.wireOp",EDGE,"E1785"),sQuery(id+"F0.wireOp",EDGE,"E1786"),sQuery(id+"F0.wireOp",EDGE,"E1787"),sQuery(id+"F0.wireOp",EDGE,"E1788"),sQuery(id+"F0.wireOp",EDGE,"E1789"),sQuery(id+"F0.wireOp",EDGE,"E1790"),sQuery(id+"F0.wireOp",EDGE,"E1791"),sQuery(id+"F0.wireOp",EDGE,"E1792"),sQuery(id+"F0.wireOp",EDGE,"E1793"),sQuery(id+"F0.wireOp",EDGE,"E1794"),sQuery(id+"F0.wireOp",EDGE,"E1795"),sQuery(id+"F0.wireOp",EDGE,"E1796"),sQuery(id+"F0.wireOp",EDGE,"E1797"),sQuery(id+"F0.wireOp",EDGE,"E1798"),sQuery(id+"F0.wireOp",EDGE,"E1799"),sQuery(id+"F0.wireOp",EDGE,"E1800"),sQuery(id+"F0.wireOp",EDGE,"E1801"),sQuery(id+"F0.wireOp",EDGE,"E1802"),sQuery(id+"F0.wireOp",EDGE,"E1803"),sQuery(id+"F0.wireOp",EDGE,"E1804"),sQuery(id+"F0.wireOp",EDGE,"E1805"),sQuery(id+"F0.wireOp",EDGE,"E1806"),sQuery(id+"F0.wireOp",EDGE,"E1807"),sQuery(id+"F0.wireOp",EDGE,"E1808"),sQuery(id+"F0.wireOp",EDGE,"E1809"),sQuery(id+"F0.wireOp",EDGE,"E1810"),sQuery(id+"F0.wireOp",EDGE,"E1811"),sQuery(id+"F0.wireOp",EDGE,"E1812"),sQuery(id+"F0.wireOp",EDGE,"E1813"),sQuery(id+"F0.wireOp",EDGE,"E1814"),sQuery(id+"F0.wireOp",EDGE,"E1815"),sQuery(id+"F0.wireOp",EDGE,"E1816"),sQuery(id+"F0.wireOp",EDGE,"E1817"),sQuery(id+"F0.wireOp",EDGE,"E1818"),sQuery(id+"F0.wireOp",EDGE,"E1819"),sQuery(id+"F0.wireOp",EDGE,"E1820"),sQuery(id+"F0.wireOp",EDGE,"E1821"),sQuery(id+"F0.wireOp",EDGE,"E1822"),sQuery(id+"F0.wireOp",EDGE,"E1823"),sQuery(id+"F0.wireOp",EDGE,"E1824"),sQuery(id+"F0.wireOp",EDGE,"E1825"),sQuery(id+"F0.wireOp",EDGE,"E1826"),sQuery(id+"F0.wireOp",EDGE,"E1827"),sQuery(id+"F0.wireOp",EDGE,"E1828"),sQuery(id+"F0.wireOp",EDGE,"E1829"),sQuery(id+"F0.wireOp",EDGE,"E1830"),sQuery(id+"F0.wireOp",EDGE,"E1831"),sQuery(id+"F0.wireOp",EDGE,"E1832"),sQuery(id+"F0.wireOp",EDGE,"E1833"),sQuery(id+"F0.wireOp",EDGE,"E1834"),sQuery(id+"F0.wireOp",EDGE,"E1835"),sQuery(id+"F0.wireOp",EDGE,"E1836"),sQuery(id+"F0.wireOp",EDGE,"E1837"),sQuery(id+"F0.wireOp",EDGE,"E1838"),sQuery(id+"F0.wireOp",EDGE,"E1839"),sQuery(id+"F0.wireOp",EDGE,"E1840"),sQuery(id+"F0.wireOp",EDGE,"E1841"),sQuery(id+"F0.wireOp",EDGE,"E1842"),sQuery(id+"F0.wireOp",EDGE,"E1843"),sQuery(id+"F0.wireOp",EDGE,"E1844"),sQuery(id+"F0.wireOp",EDGE,"E1845"),sQuery(id+"F0.wireOp",EDGE,"E1846"),sQuery(id+"F0.wireOp",EDGE,"E1847"),sQuery(id+"F0.wireOp",EDGE,"E1848"),sQuery(id+"F0.wireOp",EDGE,"E1849"),sQuery(id+"F0.wireOp",EDGE,"E1850"),sQuery(id+"F0.wireOp",EDGE,"E1851"),sQuery(id+"F0.wireOp",EDGE,"E1852"),sQuery(id+"F0.wireOp",EDGE,"E1853"),sQuery(id+"F0.wireOp",EDGE,"E1854"),sQuery(id+"F0.wireOp",EDGE,"E1855"),sQuery(id+"F0.wireOp",EDGE,"E1856"),sQuery(id+"F0.wireOp",EDGE,"E1857"),sQuery(id+"F0.wireOp",EDGE,"E1858"),sQuery(id+"F0.wireOp",EDGE,"E1859"),sQuery(id+"F0.wireOp",EDGE,"E1860"),sQuery(id+"F0.wireOp",EDGE,"E1861"),sQuery(id+"F0.wireOp",EDGE,"E1862"),sQuery(id+"F0.wireOp",EDGE,"E1863"),sQuery(id+"F0.wireOp",EDGE,"E1864"),sQuery(id+"F0.wireOp",EDGE,"E1865"),sQuery(id+"F0.wireOp",EDGE,"E1866"),sQuery(id+"F0.wireOp",EDGE,"E1867"),sQuery(id+"F0.wireOp",EDGE,"E1868"),sQuery(id+"F0.wireOp",EDGE,"E1869"),sQuery(id+"F0.wireOp",EDGE,"E1870"),sQuery(id+"F0.wireOp",EDGE,"E1871"),sQuery(id+"F0.wireOp",EDGE,"E1872"),sQuery(id+"F0.wireOp",EDGE,"E1873"),sQuery(id+"F0.wireOp",EDGE,"E1874"),sQuery(id+"F0.wireOp",EDGE,"E1875"),sQuery(id+"F0.wireOp",EDGE,"E1876"),sQuery(id+"F0.wireOp",EDGE,"E1877"),sQuery(id+"F0.wireOp",EDGE,"E1878"),sQuery(id+"F0.wireOp",EDGE,"E1879"),sQuery(id+"F0.wireOp",EDGE,"E1880"),sQuery(id+"F0.wireOp",EDGE,"E1881"),sQuery(id+"F0.wireOp",EDGE,"E1882"),sQuery(id+"F0.wireOp",EDGE,"E1883"),sQuery(id+"F0.wireOp",EDGE,"E1884"),sQuery(id+"F0.wireOp",EDGE,"E1885"),sQuery(id+"F0.wireOp",EDGE,"E1886"),sQuery(id+"F0.wireOp",EDGE,"E1887"),sQuery(id+"F0.wireOp",EDGE,"E1888"),sQuery(id+"F0.wireOp",EDGE,"E1889"),sQuery(id+"F0.wireOp",EDGE,"E1890"),sQuery(id+"F0.wireOp",EDGE,"E1891"),sQuery(id+"F0.wireOp",EDGE,"E1892"),sQuery(id+"F0.wireOp",EDGE,"E1893"),sQuery(id+"F0.wireOp",EDGE,"E1894"),sQuery(id+"F0.wireOp",EDGE,"E1895"),sQuery(id+"F0.wireOp",EDGE,"E1896"),sQuery(id+"F0.wireOp",EDGE,"E1897"),sQuery(id+"F0.wireOp",EDGE,"E1898"),sQuery(id+"F0.wireOp",EDGE,"E1899"),sQuery(id+"F0.wireOp",EDGE,"E1900"),sQuery(id+"F0.wireOp",EDGE,"E1901"),sQuery(id+"F0.wireOp",EDGE,"E1902"),sQuery(id+"F0.wireOp",EDGE,"E1903"),sQuery(id+"F0.wireOp",EDGE,"E1904"),sQuery(id+"F0.wireOp",EDGE,"E1905"),sQuery(id+"F0.wireOp",EDGE,"E1906"),sQuery(id+"F0.wireOp",EDGE,"E1907"),sQuery(id+"F0.wireOp",EDGE,"E1908"),sQuery(id+"F0.wireOp",EDGE,"E1909"),sQuery(id+"F0.wireOp",EDGE,"E1910"),sQuery(id+"F0.wireOp",EDGE,"E1911"),sQuery(id+"F0.wireOp",EDGE,"E1912"),sQuery(id+"F0.wireOp",EDGE,"E1913"),sQuery(id+"F0.wireOp",EDGE,"E1914"),sQuery(id+"F0.wireOp",EDGE,"E1915"),sQuery(id+"F0.wireOp",EDGE,"E1916"),sQuery(id+"F0.wireOp",EDGE,"E1917"),sQuery(id+"F0.wireOp",EDGE,"E1918"),sQuery(id+"F0.wireOp",EDGE,"E1919"),sQuery(id+"F0.wireOp",EDGE,"E1920"),sQuery(id+"F0.wireOp",EDGE,"E1921"),sQuery(id+"F0.wireOp",EDGE,"E1922"),sQuery(id+"F0.wireOp",EDGE,"E1923"),sQuery(id+"F0.wireOp",EDGE,"E1924"),sQuery(id+"F0.wireOp",EDGE,"E1925"),sQuery(id+"F0.wireOp",EDGE,"E1926"),sQuery(id+"F0.wireOp",EDGE,"E1927"),sQuery(id+"F0.wireOp",EDGE,"E1928"),sQuery(id+"F0.wireOp",EDGE,"E1929"),sQuery(id+"F0.wireOp",EDGE,"E1930"),sQuery(id+"F0.wireOp",EDGE,"E1931"),sQuery(id+"F0.wireOp",EDGE,"E1932"),sQuery(id+"F0.wireOp",EDGE,"E1933"),sQuery(id+"F0.wireOp",EDGE,"E1934"),sQuery(id+"F0.wireOp",EDGE,"E1935"),sQuery(id+"F0.wireOp",EDGE,"E1936"),sQuery(id+"F0.wireOp",EDGE,"E1937"),sQuery(id+"F0.wireOp",EDGE,"E1938"),sQuery(id+"F0.wireOp",EDGE,"E1939"),sQuery(id+"F0.wireOp",EDGE,"E1940"),sQuery(id+"F0.wireOp",EDGE,"E1941"),sQuery(id+"F0.wireOp",EDGE,"E1942"),sQuery(id+"F0.wireOp",EDGE,"E1943"),sQuery(id+"F0.wireOp",EDGE,"E1944"),sQuery(id+"F0.wireOp",EDGE,"E1945"),sQuery(id+"F0.wireOp",EDGE,"E1946"),sQuery(id+"F0.wireOp",EDGE,"E1947"),sQuery(id+"F0.wireOp",EDGE,"E1948"),sQuery(id+"F0.wireOp",EDGE,"E1949"),sQuery(id+"F0.wireOp",EDGE,"E1950"),sQuery(id+"F0.wireOp",EDGE,"E1951"),sQuery(id+"F0.wireOp",EDGE,"E1952"),sQuery(id+"F0.wireOp",EDGE,"E1953"),sQuery(id+"F0.wireOp",EDGE,"E1954"),sQuery(id+"F0.wireOp",EDGE,"E1955"),sQuery(id+"F0.wireOp",EDGE,"E1956"),sQuery(id+"F0.wireOp",EDGE,"E1957"),sQuery(id+"F0.wireOp",EDGE,"E1958"),sQuery(id+"F0.wireOp",EDGE,"E1959"),sQuery(id+"F0.wireOp",EDGE,"E1960"),sQuery(id+"F0.wireOp",EDGE,"E1961"),sQuery(id+"F0.wireOp",EDGE,"E1962"),sQuery(id+"F0.wireOp",EDGE,"E1963"),sQuery(id+"F0.wireOp",EDGE,"E1964"),sQuery(id+"F0.wireOp",EDGE,"E1965"),sQuery(id+"F0.wireOp",EDGE,"E1966"),sQuery(id+"F0.wireOp",EDGE,"E1967"),sQuery(id+"F0.wireOp",EDGE,"E1968"),sQuery(id+"F0.wireOp",EDGE,"E1969"),sQuery(id+"F0.wireOp",EDGE,"E1970"),sQuery(id+"F0.wireOp",EDGE,"E1971"),sQuery(id+"F0.wireOp",EDGE,"E1972"),sQuery(id+"F0.wireOp",EDGE,"E1973"),sQuery(id+"F0.wireOp",EDGE,"E1974"),sQuery(id+"F0.wireOp",EDGE,"E1975"),sQuery(id+"F0.wireOp",EDGE,"E1976"),sQuery(id+"F0.wireOp",EDGE,"E1977"),sQuery(id+"F0.wireOp",EDGE,"E1978"),sQuery(id+"F0.wireOp",EDGE,"E1979"),sQuery(id+"F0.wireOp",EDGE,"E1980"),sQuery(id+"F0.wireOp",EDGE,"E1981"),sQuery(id+"F0.wireOp",EDGE,"E1982"),sQuery(id+"F0.wireOp",EDGE,"E1983"),sQuery(id+"F0.wireOp",EDGE,"E1984"),sQuery(id+"F0.wireOp",EDGE,"E1985"),sQuery(id+"F0.wireOp",EDGE,"E1986"),sQuery(id+"F0.wireOp",EDGE,"E1987"),sQuery(id+"F0.wireOp",EDGE,"E1988"),sQuery(id+"F0.wireOp",EDGE,"E1989"),sQuery(id+"F0.wireOp",EDGE,"E1990"),sQuery(id+"F0.wireOp",EDGE,"E1991"),sQuery(id+"F0.wireOp",EDGE,"E1992"),sQuery(id+"F0.wireOp",EDGE,"E1993"),sQuery(id+"F0.wireOp",EDGE,"E1994"),sQuery(id+"F0.wireOp",EDGE,"E1995"),sQuery(id+"F0.wireOp",EDGE,"E1996"),sQuery(id+"F0.wireOp",EDGE,"E1997"),sQuery(id+"F0.wireOp",EDGE,"E1998"),sQuery(id+"F0.wireOp",EDGE,"E1999"),sQuery(id+"F0.wireOp",EDGE,"E2000"),sQuery(id+"F0.wireOp",EDGE,"E2001"),sQuery(id+"F0.wireOp",EDGE,"E2002"),sQuery(id+"F0.wireOp",EDGE,"E2003"),sQuery(id+"F0.wireOp",EDGE,"E2004"),sQuery(id+"F0.wireOp",EDGE,"E2005"),sQuery(id+"F0.wireOp",EDGE,"E2006"),sQuery(id+"F0.wireOp",EDGE,"E2007"),sQuery(id+"F0.wireOp",EDGE,"E2008"),sQuery(id+"F0.wireOp",EDGE,"E2009"),sQuery(id+"F0.wireOp",EDGE,"E2010"),sQuery(id+"F0.wireOp",EDGE,"E2011"),sQuery(id+"F0.wireOp",EDGE,"E2012"),sQuery(id+"F0.wireOp",EDGE,"E2013"),sQuery(id+"F0.wireOp",EDGE,"E2014"),sQuery(id+"F0.wireOp",EDGE,"E2015"),sQuery(id+"F0.wireOp",EDGE,"E2016"),sQuery(id+"F0.wireOp",EDGE,"E2017"),sQuery(id+"F0.wireOp",EDGE,"E2018"),sQuery(id+"F0.wireOp",EDGE,"E2019"),sQuery(id+"F0.wireOp",EDGE,"E2020"),sQuery(id+"F0.wireOp",EDGE,"E2021"),sQuery(id+"F0.wireOp",EDGE,"E2022"),sQuery(id+"F0.wireOp",EDGE,"E2023"),sQuery(id+"F0.wireOp",EDGE,"E2024"),sQuery(id+"F0.wireOp",EDGE,"E2025"),sQuery(id+"F0.wireOp",EDGE,"E2026"),sQuery(id+"F0.wireOp",EDGE,"E2027"),sQuery(id+"F0.wireOp",EDGE,"E2028"),sQuery(id+"F0.wireOp",EDGE,"E2029"),sQuery(id+"F0.wireOp",EDGE,"E2030"),sQuery(id+"F0.wireOp",EDGE,"E2031"),sQuery(id+"F0.wireOp",EDGE,"E2032"),sQuery(id+"F0.wireOp",EDGE,"E2033"),sQuery(id+"F0.wireOp",EDGE,"E2034"),sQuery(id+"F0.wireOp",EDGE,"E2035"),sQuery(id+"F0.wireOp",EDGE,"E2036"),sQuery(id+"F0.wireOp",EDGE,"E2037"),sQuery(id+"F0.wireOp",EDGE,"E2038"),sQuery(id+"F0.wireOp",EDGE,"E2039"),sQuery(id+"F0.wireOp",EDGE,"E2040"),sQuery(id+"F0.wireOp",EDGE,"E2041"),sQuery(id+"F0.wireOp",EDGE,"E2042"),sQuery(id+"F0.wireOp",EDGE,"E2043"),sQuery(id+"F0.wireOp",EDGE,"E2044"),sQuery(id+"F0.wireOp",EDGE,"E2045"),sQuery(id+"F0.wireOp",EDGE,"E2046"),sQuery(id+"F0.wireOp",EDGE,"E2047"),sQuery(id+"F0.wireOp",EDGE,"E2048"),sQuery(id+"F0.wireOp",EDGE,"E2049"),sQuery(id+"F0.wireOp",EDGE,"E2050"),sQuery(id+"F0.wireOp",EDGE,"E2051"),sQuery(id+"F0.wireOp",EDGE,"E2052"),sQuery(id+"F0.wireOp",EDGE,"E2053"),sQuery(id+"F0.wireOp",EDGE,"E2054"),sQuery(id+"F0.wireOp",EDGE,"E2055"),sQuery(id+"F0.wireOp",EDGE,"E2056"),sQuery(id+"F0.wireOp",EDGE,"E2057"),sQuery(id+"F0.wireOp",EDGE,"E2058"),sQuery(id+"F0.wireOp",EDGE,"E2059"),sQuery(id+"F0.wireOp",EDGE,"E2060"),sQuery(id+"F0.wireOp",EDGE,"E2061"),sQuery(id+"F0.wireOp",EDGE,"E2062"),sQuery(id+"F0.wireOp",EDGE,"E2063"),sQuery(id+"F0.wireOp",EDGE,"E2064"),sQuery(id+"F0.wireOp",EDGE,"E2065"),sQuery(id+"F0.wireOp",EDGE,"E2066"),sQuery(id+"F0.wireOp",EDGE,"E2067"),sQuery(id+"F0.wireOp",EDGE,"E2068"),sQuery(id+"F0.wireOp",EDGE,"E2069"),sQuery(id+"F0.wireOp",EDGE,"E2070"),sQuery(id+"F0.wireOp",EDGE,"E2071"),sQuery(id+"F0.wireOp",EDGE,"E2072"),sQuery(id+"F0.wireOp",EDGE,"E2073"),sQuery(id+"F0.wireOp",EDGE,"E2074"),sQuery(id+"F0.wireOp",EDGE,"E2075"),sQuery(id+"F0.wireOp",EDGE,"E2076"),sQuery(id+"F0.wireOp",EDGE,"E2077"),sQuery(id+"F0.wireOp",EDGE,"E2078"),sQuery(id+"F0.wireOp",EDGE,"E2079"),sQuery(id+"F0.wireOp",EDGE,"E2080"),sQuery(id+"F0.wireOp",EDGE,"E2081"),sQuery(id+"F0.wireOp",EDGE,"E2082"),sQuery(id+"F0.wireOp",EDGE,"E2083"),sQuery(id+"F0.wireOp",EDGE,"E2084"),sQuery(id+"F0.wireOp",EDGE,"E2085"),sQuery(id+"F0.wireOp",EDGE,"E2086"),sQuery(id+"F0.wireOp",EDGE,"E2087"),sQuery(id+"F0.wireOp",EDGE,"E2088"),sQuery(id+"F0.wireOp",EDGE,"E2089"),sQuery(id+"F0.wireOp",EDGE,"E2090"),sQuery(id+"F0.wireOp",EDGE,"E2091"),sQuery(id+"F0.wireOp",EDGE,"E2092"),sQuery(id+"F0.wireOp",EDGE,"E2093"),sQuery(id+"F0.wireOp",EDGE,"E2094"),sQuery(id+"F0.wireOp",EDGE,"E2095"),sQuery(id+"F0.wireOp",EDGE,"E2096"),sQuery(id+"F0.wireOp",EDGE,"E2097"),sQuery(id+"F0.wireOp",EDGE,"E2098"),sQuery(id+"F0.wireOp",EDGE,"E2099"),sQuery(id+"F0.wireOp",EDGE,"E2100"),sQuery(id+"F0.wireOp",EDGE,"E2101"),sQuery(id+"F0.wireOp",EDGE,"E2102"),sQuery(id+"F0.wireOp",EDGE,"E2103"),sQuery(id+"F0.wireOp",EDGE,"E2104"),sQuery(id+"F0.wireOp",EDGE,"E2105"),sQuery(id+"F0.wireOp",EDGE,"E2106"),sQuery(id+"F0.wireOp",EDGE,"E2107"),sQuery(id+"F0.wireOp",EDGE,"E2108"),sQuery(id+"F0.wireOp",EDGE,"E2109"),sQuery(id+"F0.wireOp",EDGE,"E2110"),sQuery(id+"F0.wireOp",EDGE,"E2111"),sQuery(id+"F0.wireOp",EDGE,"E2112"),sQuery(id+"F0.wireOp",EDGE,"E2113"),sQuery(id+"F0.wireOp",EDGE,"E2114"),sQuery(id+"F0.wireOp",EDGE,"E2115"),sQuery(id+"F0.wireOp",EDGE,"E2116"),sQuery(id+"F0.wireOp",EDGE,"E2117"),sQuery(id+"F0.wireOp",EDGE,"E2118"),sQuery(id+"F0.wireOp",EDGE,"E2119"),sQuery(id+"F0.wireOp",EDGE,"E2120"),sQuery(id+"F0.wireOp",EDGE,"E2121"),sQuery(id+"F0.wireOp",EDGE,"E2122"),sQuery(id+"F0.wireOp",EDGE,"E2123"),sQuery(id+"F0.wireOp",EDGE,"E2124"),sQuery(id+"F0.wireOp",EDGE,"E2125"),sQuery(id+"F0.wireOp",EDGE,"E2126"),sQuery(id+"F0.wireOp",EDGE,"E2127"),sQuery(id+"F0.wireOp",EDGE,"E2128"),sQuery(id+"F0.wireOp",EDGE,"E2129"),sQuery(id+"F0.wireOp",EDGE,"E2130"),sQuery(id+"F0.wireOp",EDGE,"E2131"),sQuery(id+"F0.wireOp",EDGE,"E2132"),sQuery(id+"F0.wireOp",EDGE,"E2133"),sQuery(id+"F0.wireOp",EDGE,"E2134"),sQuery(id+"F0.wireOp",EDGE,"E2135"),sQuery(id+"F0.wireOp",EDGE,"E2136"),sQuery(id+"F0.wireOp",EDGE,"E2137"),sQuery(id+"F0.wireOp",EDGE,"E2138"),sQuery(id+"F0.wireOp",EDGE,"E2139"),sQuery(id+"F0.wireOp",EDGE,"E2140"),sQuery(id+"F0.wireOp",EDGE,"E2141"),sQuery(id+"F0.wireOp",EDGE,"E2142"),sQuery(id+"F0.wireOp",EDGE,"E2143"),sQuery(id+"F0.wireOp",EDGE,"E2144"),sQuery(id+"F0.wireOp",EDGE,"E2145"),sQuery(id+"F0.wireOp",EDGE,"E2146"),sQuery(id+"F0.wireOp",EDGE,"E2147"),sQuery(id+"F0.wireOp",EDGE,"E2148"),sQuery(id+"F0.wireOp",EDGE,"E2149"),sQuery(id+"F0.wireOp",EDGE,"E2150"),sQuery(id+"F0.wireOp",EDGE,"E2151"),sQuery(id+"F0.wireOp",EDGE,"E2152"),sQuery(id+"F0.wireOp",EDGE,"E2153"),sQuery(id+"F0.wireOp",EDGE,"E2154"),sQuery(id+"F0.wireOp",EDGE,"E2155"),sQuery(id+"F0.wireOp",EDGE,"E2156"),sQuery(id+"F0.wireOp",EDGE,"E2157"),sQuery(id+"F0.wireOp",EDGE,"E2158"),sQuery(id+"F0.wireOp",EDGE,"E2159"),sQuery(id+"F0.wireOp",EDGE,"E2160"),sQuery(id+"F0.wireOp",EDGE,"E2161"),sQuery(id+"F0.wireOp",EDGE,"E2162"),sQuery(id+"F0.wireOp",EDGE,"E2163"),sQuery(id+"F0.wireOp",EDGE,"E2164"),sQuery(id+"F0.wireOp",EDGE,"E2165"),sQuery(id+"F0.wireOp",EDGE,"E2166"),sQuery(id+"F0.wireOp",EDGE,"E2167"),sQuery(id+"F0.wireOp",EDGE,"E2168"),sQuery(id+"F0.wireOp",EDGE,"E2169"),sQuery(id+"F0.wireOp",EDGE,"E2170"),sQuery(id+"F0.wireOp",EDGE,"E2171"),sQuery(id+"F0.wireOp",EDGE,"E2172"),sQuery(id+"F0.wireOp",EDGE,"E2173"),sQuery(id+"F0.wireOp",EDGE,"E2174"),sQuery(id+"F0.wireOp",EDGE,"E2175"),sQuery(id+"F0.wireOp",EDGE,"E2176"),sQuery(id+"F0.wireOp",EDGE,"E2177"),sQuery(id+"F0.wireOp",EDGE,"E2178"),sQuery(id+"F0.wireOp",EDGE,"E2179"),sQuery(id+"F0.wireOp",EDGE,"E2180"),sQuery(id+"F0.wireOp",EDGE,"E2181"),sQuery(id+"F0.wireOp",EDGE,"E2182"),sQuery(id+"F0.wireOp",EDGE,"E2183"),sQuery(id+"F0.wireOp",EDGE,"E2184"),sQuery(id+"F0.wireOp",EDGE,"E2185"),sQuery(id+"F0.wireOp",EDGE,"E2186"),sQuery(id+"F0.wireOp",EDGE,"E2187"),sQuery(id+"F0.wireOp",EDGE,"E2188"),sQuery(id+"F0.wireOp",EDGE,"E2189"),sQuery(id+"F0.wireOp",EDGE,"E2190"),sQuery(id+"F0.wireOp",EDGE,"E2191"),sQuery(id+"F0.wireOp",EDGE,"E2192"),sQuery(id+"F0.wireOp",EDGE,"E2193"),sQuery(id+"F0.wireOp",EDGE,"E2194"),sQuery(id+"F0.wireOp",EDGE,"E2195"),sQuery(id+"F0.wireOp",EDGE,"E2196"),sQuery(id+"F0.wireOp",EDGE,"E2197"),sQuery(id+"F0.wireOp",EDGE,"E2198"),sQuery(id+"F0.wireOp",EDGE,"E2199"),sQuery(id+"F0.wireOp",EDGE,"E2200"),sQuery(id+"F0.wireOp",EDGE,"E2201"),sQuery(id+"F0.wireOp",EDGE,"E2202"),sQuery(id+"F0.wireOp",EDGE,"E2203"),sQuery(id+"F0.wireOp",EDGE,"E2204"),sQuery(id+"F0.wireOp",EDGE,"E2205"),sQuery(id+"F0.wireOp",EDGE,"E2206"),sQuery(id+"F0.wireOp",EDGE,"E2207"),sQuery(id+"F0.wireOp",EDGE,"E2208"),sQuery(id+"F0.wireOp",EDGE,"E2209"),sQuery(id+"F0.wireOp",EDGE,"E2210"),sQuery(id+"F0.wireOp",EDGE,"E2211"),sQuery(id+"F0.wireOp",EDGE,"E2212"),sQuery(id+"F0.wireOp",EDGE,"E2213"),sQuery(id+"F0.wireOp",EDGE,"E2214"),sQuery(id+"F0.wireOp",EDGE,"E2215"),sQuery(id+"F0.wireOp",EDGE,"E2216"),sQuery(id+"F0.wireOp",EDGE,"E2217"),sQuery(id+"F0.wireOp",EDGE,"E2218"),sQuery(id+"F0.wireOp",EDGE,"E2219"),sQuery(id+"F0.wireOp",EDGE,"E2220"),sQuery(id+"F0.wireOp",EDGE,"E2221"),sQuery(id+"F0.wireOp",EDGE,"E2222"),sQuery(id+"F0.wireOp",EDGE,"E2223"),sQuery(id+"F0.wireOp",EDGE,"E2224"),sQuery(id+"F0.wireOp",EDGE,"E2225"),sQuery(id+"F0.wireOp",EDGE,"E2226"),sQuery(id+"F0.wireOp",EDGE,"E2227"),sQuery(id+"F0.wireOp",EDGE,"E2228"),sQuery(id+"F0.wireOp",EDGE,"E2229"),sQuery(id+"F0.wireOp",EDGE,"E2230"),sQuery(id+"F0.wireOp",EDGE,"E2231"),sQuery(id+"F0.wireOp",EDGE,"E2232"),sQuery(id+"F0.wireOp",EDGE,"E2233"),sQuery(id+"F0.wireOp",EDGE,"E2234"),sQuery(id+"F0.wireOp",EDGE,"E2235"),sQuery(id+"F0.wireOp",EDGE,"E2236"),sQuery(id+"F0.wireOp",EDGE,"E2237"),sQuery(id+"F0.wireOp",EDGE,"E2238"),sQuery(id+"F0.wireOp",EDGE,"E2239"),sQuery(id+"F0.wireOp",EDGE,"E2240"),sQuery(id+"F0.wireOp",EDGE,"E2241"),sQuery(id+"F0.wireOp",EDGE,"E2242"),sQuery(id+"F0.wireOp",EDGE,"E2243"),sQuery(id+"F0.wireOp",EDGE,"E2244"),sQuery(id+"F0.wireOp",EDGE,"E2245"),sQuery(id+"F0.wireOp",EDGE,"E2246"),sQuery(id+"F0.wireOp",EDGE,"E2247"),sQuery(id+"F0.wireOp",EDGE,"E2248"),sQuery(id+"F0.wireOp",EDGE,"E2249"),sQuery(id+"F0.wireOp",EDGE,"E2250"),sQuery(id+"F0.wireOp",EDGE,"E2251"),sQuery(id+"F0.wireOp",EDGE,"E2252"),sQuery(id+"F0.wireOp",EDGE,"E2253"),sQuery(id+"F0.wireOp",EDGE,"E2254"),sQuery(id+"F0.wireOp",EDGE,"E2255"),sQuery(id+"F0.wireOp",EDGE,"E2256"),sQuery(id+"F0.wireOp",EDGE,"E2257"),sQuery(id+"F0.wireOp",EDGE,"E2258"),sQuery(id+"F0.wireOp",EDGE,"E2259"),sQuery(id+"F0.wireOp",EDGE,"E2260"),sQuery(id+"F0.wireOp",EDGE,"E2261"),sQuery(id+"F0.wireOp",EDGE,"E2262"),sQuery(id+"F0.wireOp",EDGE,"E2263"),sQuery(id+"F0.wireOp",EDGE,"E2264"),sQuery(id+"F0.wireOp",EDGE,"E2265"),sQuery(id+"F0.wireOp",EDGE,"E2266"),sQuery(id+"F0.wireOp",EDGE,"E2267"),sQuery(id+"F0.wireOp",EDGE,"E2268"),sQuery(id+"F0.wireOp",EDGE,"E2269"),sQuery(id+"F0.wireOp",EDGE,"E2270"),sQuery(id+"F0.wireOp",EDGE,"E2271"),sQuery(id+"F0.wireOp",EDGE,"E2272"),sQuery(id+"F0.wireOp",EDGE,"E2273"),sQuery(id+"F0.wireOp",EDGE,"E2274"),sQuery(id+"F0.wireOp",EDGE,"E2275"),sQuery(id+"F0.wireOp",EDGE,"E2276"),sQuery(id+"F0.wireOp",EDGE,"E2277"),sQuery(id+"F0.wireOp",EDGE,"E2278"),sQuery(id+"F0.wireOp",EDGE,"E2279"),sQuery(id+"F0.wireOp",EDGE,"E2280"),sQuery(id+"F0.wireOp",EDGE,"E2281"),sQuery(id+"F0.wireOp",EDGE,"E2282"),sQuery(id+"F0.wireOp",EDGE,"E2283"),sQuery(id+"F0.wireOp",EDGE,"E2284"),sQuery(id+"F0.wireOp",EDGE,"E2285"),sQuery(id+"F0.wireOp",EDGE,"E2286"),sQuery(id+"F0.wireOp",EDGE,"E2287"),sQuery(id+"F0.wireOp",EDGE,"E2288"),sQuery(id+"F0.wireOp",EDGE,"E2289"),sQuery(id+"F0.wireOp",EDGE,"E2290"),sQuery(id+"F0.wireOp",EDGE,"E2291"),sQuery(id+"F0.wireOp",EDGE,"E2292"),sQuery(id+"F0.wireOp",EDGE,"E2293"),sQuery(id+"F0.wireOp",EDGE,"E2294"),sQuery(id+"F0.wireOp",EDGE,"E2295"),sQuery(id+"F0.wireOp",EDGE,"E2296"),sQuery(id+"F0.wireOp",EDGE,"E2297"),sQuery(id+"F0.wireOp",EDGE,"E2298"),sQuery(id+"F0.wireOp",EDGE,"E2299"),sQuery(id+"F0.wireOp",EDGE,"E2300"),sQuery(id+"F0.wireOp",EDGE,"E2301"),sQuery(id+"F0.wireOp",EDGE,"E2302"),sQuery(id+"F0.wireOp",EDGE,"E2303"),sQuery(id+"F0.wireOp",EDGE,"E2304"),sQuery(id+"F0.wireOp",EDGE,"E2305"),sQuery(id+"F0.wireOp",EDGE,"E2306"),sQuery(id+"F0.wireOp",EDGE,"E2307"),sQuery(id+"F0.wireOp",EDGE,"E2308"),sQuery(id+"F0.wireOp",EDGE,"E2309"),sQuery(id+"F0.wireOp",EDGE,"E2310"),sQuery(id+"F0.wireOp",EDGE,"E2311"),sQuery(id+"F0.wireOp",EDGE,"E2312"),sQuery(id+"F0.wireOp",EDGE,"E2313"),sQuery(id+"F0.wireOp",EDGE,"E2314"),sQuery(id+"F0.wireOp",EDGE,"E2315"),sQuery(id+"F0.wireOp",EDGE,"E2316"),sQuery(id+"F0.wireOp",EDGE,"E2317"),sQuery(id+"F0.wireOp",EDGE,"E2318"),sQuery(id+"F0.wireOp",EDGE,"E2319"),sQuery(id+"F0.wireOp",EDGE,"E2320"),sQuery(id+"F0.wireOp",EDGE,"E2321"),sQuery(id+"F0.wireOp",EDGE,"E2322"),sQuery(id+"F0.wireOp",EDGE,"E2323"),sQuery(id+"F0.wireOp",EDGE,"E2324"),sQuery(id+"F0.wireOp",EDGE,"E2325"),sQuery(id+"F0.wireOp",EDGE,"E2326"),sQuery(id+"F0.wireOp",EDGE,"E2327"),sQuery(id+"F0.wireOp",EDGE,"E2328"),sQuery(id+"F0.wireOp",EDGE,"E2329"),sQuery(id+"F0.wireOp",EDGE,"E2330"),sQuery(id+"F0.wireOp",EDGE,"E2331"),sQuery(id+"F0.wireOp",EDGE,"E2332"),sQuery(id+"F0.wireOp",EDGE,"E2333"),sQuery(id+"F0.wireOp",EDGE,"E2334"),sQuery(id+"F0.wireOp",EDGE,"E2335"),sQuery(id+"F0.wireOp",EDGE,"E2336"),sQuery(id+"F0.wireOp",EDGE,"E2337"),sQuery(id+"F0.wireOp",EDGE,"E2338"),sQuery(id+"F0.wireOp",EDGE,"E2339"),sQuery(id+"F0.wireOp",EDGE,"E2340"),sQuery(id+"F0.wireOp",EDGE,"E2341"),sQuery(id+"F0.wireOp",EDGE,"E2342"),sQuery(id+"F0.wireOp",EDGE,"E2343"),sQuery(id+"F0.wireOp",EDGE,"E2344"),sQuery(id+"F0.wireOp",EDGE,"E2345"),sQuery(id+"F0.wireOp",EDGE,"E2346"),sQuery(id+"F0.wireOp",EDGE,"E2347"),sQuery(id+"F0.wireOp",EDGE,"E2348"),sQuery(id+"F0.wireOp",EDGE,"E2349"),sQuery(id+"F0.wireOp",EDGE,"E2350"),sQuery(id+"F0.wireOp",EDGE,"E2351"),sQuery(id+"F0.wireOp",EDGE,"E2352"),sQuery(id+"F0.wireOp",EDGE,"E2353"),sQuery(id+"F0.wireOp",EDGE,"E2354"),sQuery(id+"F0.wireOp",EDGE,"E2355"),sQuery(id+"F0.wireOp",EDGE,"E2356"),sQuery(id+"F0.wireOp",EDGE,"E2357"),sQuery(id+"F0.wireOp",EDGE,"E2358"),sQuery(id+"F0.wireOp",EDGE,"E2359"),sQuery(id+"F0.wireOp",EDGE,"E2360"),sQuery(id+"F0.wireOp",EDGE,"E2361"),sQuery(id+"F0.wireOp",EDGE,"E2362"),sQuery(id+"F0.wireOp",EDGE,"E2363"),sQuery(id+"F0.wireOp",EDGE,"E2364"),sQuery(id+"F0.wireOp",EDGE,"E2365"),sQuery(id+"F0.wireOp",EDGE,"E2366"),sQuery(id+"F0.wireOp",EDGE,"E2367"),sQuery(id+"F0.wireOp",EDGE,"E2368"),sQuery(id+"F0.wireOp",EDGE,"E2369"),sQuery(id+"F0.wireOp",EDGE,"E2370"),sQuery(id+"F0.wireOp",EDGE,"E2371"),sQuery(id+"F0.wireOp",EDGE,"E2372"),sQuery(id+"F0.wireOp",EDGE,"E2373"),sQuery(id+"F0.wireOp",EDGE,"E2374"),sQuery(id+"F0.wireOp",EDGE,"E2375"),sQuery(id+"F0.wireOp",EDGE,"E2376"),sQuery(id+"F0.wireOp",EDGE,"E2377"),sQuery(id+"F0.wireOp",EDGE,"E2378"),sQuery(id+"F0.wireOp",EDGE,"E2379"),sQuery(id+"F0.wireOp",EDGE,"E2380"),sQuery(id+"F0.wireOp",EDGE,"E2381"),sQuery(id+"F0.wireOp",EDGE,"E2382"),sQuery(id+"F0.wireOp",EDGE,"E2383"),sQuery(id+"F0.wireOp",EDGE,"E2384"),sQuery(id+"F0.wireOp",EDGE,"E2385"),sQuery(id+"F0.wireOp",EDGE,"E2386"),sQuery(id+"F0.wireOp",EDGE,"E2387"),sQuery(id+"F0.wireOp",EDGE,"E2388"),sQuery(id+"F0.wireOp",EDGE,"E2389"),sQuery(id+"F0.wireOp",EDGE,"E2390"),sQuery(id+"F0.wireOp",EDGE,"E2391"),sQuery(id+"F0.wireOp",EDGE,"E2392"),sQuery(id+"F0.wireOp",EDGE,"E2393"),sQuery(id+"F0.wireOp",EDGE,"E2394"),sQuery(id+"F0.wireOp",EDGE,"E2395"),sQuery(id+"F0.wireOp",EDGE,"E2396"),sQuery(id+"F0.wireOp",EDGE,"E2397"),sQuery(id+"F0.wireOp",EDGE,"E2398"),sQuery(id+"F0.wireOp",EDGE,"E2399"),sQuery(id+"F0.wireOp",EDGE,"E2400"),sQuery(id+"F0.wireOp",EDGE,"E2401"),sQuery(id+"F0.wireOp",EDGE,"E2402"),sQuery(id+"F0.wireOp",EDGE,"E2403"),sQuery(id+"F0.wireOp",EDGE,"E2404"),sQuery(id+"F0.wireOp",EDGE,"E2405"),sQuery(id+"F0.wireOp",EDGE,"E2406"),sQuery(id+"F0.wireOp",EDGE,"E2407"),sQuery(id+"F0.wireOp",EDGE,"E2408"),sQuery(id+"F0.wireOp",EDGE,"E2409"),sQuery(id+"F0.wireOp",EDGE,"E2410"),sQuery(id+"F0.wireOp",EDGE,"E2411"),sQuery(id+"F0.wireOp",EDGE,"E2412"),sQuery(id+"F0.wireOp",EDGE,"E2413"),sQuery(id+"F0.wireOp",EDGE,"E2414"),sQuery(id+"F0.wireOp",EDGE,"E2415"),sQuery(id+"F0.wireOp",EDGE,"E2416"),sQuery(id+"F0.wireOp",EDGE,"E2417"),sQuery(id+"F0.wireOp",EDGE,"E2418"),sQuery(id+"F0.wireOp",EDGE,"E2419"),sQuery(id+"F0.wireOp",EDGE,"E2420"),sQuery(id+"F0.wireOp",EDGE,"E2421"),sQuery(id+"F0.wireOp",EDGE,"E2422"),sQuery(id+"F0.wireOp",EDGE,"E2423"),sQuery(id+"F0.wireOp",EDGE,"E2424"),sQuery(id+"F0.wireOp",EDGE,"E2425"),sQuery(id+"F0.wireOp",EDGE,"E2426"),sQuery(id+"F0.wireOp",EDGE,"E2427"),sQuery(id+"F0.wireOp",EDGE,"E2428"),sQuery(id+"F0.wireOp",EDGE,"E2429"),sQuery(id+"F0.wireOp",EDGE,"E2430"),sQuery(id+"F0.wireOp",EDGE,"E2431"),sQuery(id+"F0.wireOp",EDGE,"E2432"),sQuery(id+"F0.wireOp",EDGE,"E2433"),sQuery(id+"F0.wireOp",EDGE,"E2434"),sQuery(id+"F0.wireOp",EDGE,"E2435"),sQuery(id+"F0.wireOp",EDGE,"E2436"),sQuery(id+"F0.wireOp",EDGE,"E2437"),sQuery(id+"F0.wireOp",EDGE,"E2438"),sQuery(id+"F0.wireOp",EDGE,"E2439"),sQuery(id+"F0.wireOp",EDGE,"E2440"),sQuery(id+"F0.wireOp",EDGE,"E2441"),sQuery(id+"F0.wireOp",EDGE,"E2442"),sQuery(id+"F0.wireOp",EDGE,"E2443"),sQuery(id+"F0.wireOp",EDGE,"E2444"),sQuery(id+"F0.wireOp",EDGE,"E2445"),sQuery(id+"F0.wireOp",EDGE,"E2446"),sQuery(id+"F0.wireOp",EDGE,"E2447"),sQuery(id+"F0.wireOp",EDGE,"E2448"),sQuery(id+"F0.wireOp",EDGE,"E2449"),sQuery(id+"F0.wireOp",EDGE,"E2450"),sQuery(id+"F0.wireOp",EDGE,"E2451"),sQuery(id+"F0.wireOp",EDGE,"E2452"),sQuery(id+"F0.wireOp",EDGE,"E2453"),sQuery(id+"F0.wireOp",EDGE,"E2454"),sQuery(id+"F0.wireOp",EDGE,"E2455"),sQuery(id+"F0.wireOp",EDGE,"E2456"),sQuery(id+"F0.wireOp",EDGE,"E2457"),sQuery(id+"F0.wireOp",EDGE,"E2458"),sQuery(id+"F0.wireOp",EDGE,"E2459"),sQuery(id+"F0.wireOp",EDGE,"E2460"),sQuery(id+"F0.wireOp",EDGE,"E2461"),sQuery(id+"F0.wireOp",EDGE,"E2462"),sQuery(id+"F0.wireOp",EDGE,"E2463"),sQuery(id+"F0.wireOp",EDGE,"E2464"),sQuery(id+"F0.wireOp",EDGE,"E2465"),sQuery(id+"F0.wireOp",EDGE,"E2466"),sQuery(id+"F0.wireOp",EDGE,"E2467"),sQuery(id+"F0.wireOp",EDGE,"E2468"),sQuery(id+"F0.wireOp",EDGE,"E2469"),sQuery(id+"F0.wireOp",EDGE,"E2470"),sQuery(id+"F0.wireOp",EDGE,"E2471"),sQuery(id+"F0.wireOp",EDGE,"E2472"),sQuery(id+"F0.wireOp",EDGE,"E2473"),sQuery(id+"F0.wireOp",EDGE,"E2474"),sQuery(id+"F0.wireOp",EDGE,"E2475"),sQuery(id+"F0.wireOp",EDGE,"E2476"),sQuery(id+"F0.wireOp",EDGE,"E2477"),sQuery(id+"F0.wireOp",EDGE,"E2478"),sQuery(id+"F0.wireOp",EDGE,"E2479"),sQuery(id+"F0.wireOp",EDGE,"E2480"),sQuery(id+"F0.wireOp",EDGE,"E2481"),sQuery(id+"F0.wireOp",EDGE,"E2482"),sQuery(id+"F0.wireOp",EDGE,"E2483"),sQuery(id+"F0.wireOp",EDGE,"E2484"),sQuery(id+"F0.wireOp",EDGE,"E2485"),sQuery(id+"F0.wireOp",EDGE,"E2486"),sQuery(id+"F0.wireOp",EDGE,"E2487"),sQuery(id+"F0.wireOp",EDGE,"E2488"),sQuery(id+"F0.wireOp",EDGE,"E2489"),sQuery(id+"F0.wireOp",EDGE,"E2490"),sQuery(id+"F0.wireOp",EDGE,"E2491"),sQuery(id+"F0.wireOp",EDGE,"E2492"),sQuery(id+"F0.wireOp",EDGE,"E2493"),sQuery(id+"F0.wireOp",EDGE,"E2494"),sQuery(id+"F0.wireOp",EDGE,"E2495"),sQuery(id+"F0.wireOp",EDGE,"E2496"),sQuery(id+"F0.wireOp",EDGE,"E2497"),sQuery(id+"F0.wireOp",EDGE,"E2498"),sQuery(id+"F0.wireOp",EDGE,"E2499"),sQuery(id+"F0.wireOp",EDGE,"E2500"),sQuery(id+"F0.wireOp",EDGE,"E2501"),sQuery(id+"F0.wireOp",EDGE,"E2502"),sQuery(id+"F0.wireOp",EDGE,"E2503"),sQuery(id+"F0.wireOp",EDGE,"E2504"),sQuery(id+"F0.wireOp",EDGE,"E2505"),sQuery(id+"F0.wireOp",EDGE,"E2506"),sQuery(id+"F0.wireOp",EDGE,"E2507"),sQuery(id+"F0.wireOp",EDGE,"E2508"),sQuery(id+"F0.wireOp",EDGE,"E2509"),sQuery(id+"F0.wireOp",EDGE,"E2510"),sQuery(id+"F0.wireOp",EDGE,"E2511"),sQuery(id+"F0.wireOp",EDGE,"E2512"),sQuery(id+"F0.wireOp",EDGE,"E2513"),sQuery(id+"F0.wireOp",EDGE,"E2514"),sQuery(id+"F0.wireOp",EDGE,"E2515"),sQuery(id+"F0.wireOp",EDGE,"E2516"),sQuery(id+"F0.wireOp",EDGE,"E2517"),sQuery(id+"F0.wireOp",EDGE,"E2518"),sQuery(id+"F0.wireOp",EDGE,"E2519"),sQuery(id+"F0.wireOp",EDGE,"E2520"),sQuery(id+"F0.wireOp",EDGE,"E2521"),sQuery(id+"F0.wireOp",EDGE,"E2522"),sQuery(id+"F0.wireOp",EDGE,"E2523"),sQuery(id+"F0.wireOp",EDGE,"E2524"),sQuery(id+"F0.wireOp",EDGE,"E2525"),sQuery(id+"F0.wireOp",EDGE,"E2526"),sQuery(id+"F0.wireOp",EDGE,"E2527"),sQuery(id+"F0.wireOp",EDGE,"E2528"),sQuery(id+"F0.wireOp",EDGE,"E2529"),sQuery(id+"F0.wireOp",EDGE,"E2530"),sQuery(id+"F0.wireOp",EDGE,"E2531"),sQuery(id+"F0.wireOp",EDGE,"E2532"),sQuery(id+"F0.wireOp",EDGE,"E2533"),sQuery(id+"F0.wireOp",EDGE,"E2534"),sQuery(id+"F0.wireOp",EDGE,"E2535"),sQuery(id+"F0.wireOp",EDGE,"E2536"),sQuery(id+"F0.wireOp",EDGE,"E2537"),sQuery(id+"F0.wireOp",EDGE,"E2538"),sQuery(id+"F0.wireOp",EDGE,"E2539"),sQuery(id+"F0.wireOp",EDGE,"E2540"),sQuery(id+"F0.wireOp",EDGE,"E2541"),sQuery(id+"F0.wireOp",EDGE,"E2542"),sQuery(id+"F0.wireOp",EDGE,"E2543"),sQuery(id+"F0.wireOp",EDGE,"E2544"),sQuery(id+"F0.wireOp",EDGE,"E2545"),sQuery(id+"F0.wireOp",EDGE,"E2546"),sQuery(id+"F0.wireOp",EDGE,"E2547"),sQuery(id+"F0.wireOp",EDGE,"E2548"),sQuery(id+"F0.wireOp",EDGE,"E2549"),sQuery(id+"F0.wireOp",EDGE,"E2550"),sQuery(id+"F0.wireOp",EDGE,"E2551"),sQuery(id+"F0.wireOp",EDGE,"E2552"),sQuery(id+"F0.wireOp",EDGE,"E2553"),sQuery(id+"F0.wireOp",EDGE,"E2554"),sQuery(id+"F0.wireOp",EDGE,"E2555"),sQuery(id+"F0.wireOp",EDGE,"E2556"),sQuery(id+"F0.wireOp",EDGE,"E2557"),sQuery(id+"F0.wireOp",EDGE,"E2558"),sQuery(id+"F0.wireOp",EDGE,"E2559"),sQuery(id+"F0.wireOp",EDGE,"E2560"),sQuery(id+"F0.wireOp",EDGE,"E2561"),sQuery(id+"F0.wireOp",EDGE,"E2562"),sQuery(id+"F0.wireOp",EDGE,"E2563"),sQuery(id+"F0.wireOp",EDGE,"E2564"),sQuery(id+"F0.wireOp",EDGE,"E2565"),sQuery(id+"F0.wireOp",EDGE,"E2566"),sQuery(id+"F0.wireOp",EDGE,"E2567"),sQuery(id+"F0.wireOp",EDGE,"E2568"),sQuery(id+"F0.wireOp",EDGE,"E2569"),sQuery(id+"F0.wireOp",EDGE,"E2570"),sQuery(id+"F0.wireOp",EDGE,"E2571"),sQuery(id+"F0.wireOp",EDGE,"E2572"),sQuery(id+"F0.wireOp",EDGE,"E2573"),sQuery(id+"F0.wireOp",EDGE,"E2574"),sQuery(id+"F0.wireOp",EDGE,"E2575"),sQuery(id+"F0.wireOp",EDGE,"E2576"),sQuery(id+"F0.wireOp",EDGE,"E2577"),sQuery(id+"F0.wireOp",EDGE,"E2578"),sQuery(id+"F0.wireOp",EDGE,"E2579"),sQuery(id+"F0.wireOp",EDGE,"E2580"),sQuery(id+"F0.wireOp",EDGE,"E2581"),sQuery(id+"F0.wireOp",EDGE,"E2582"),sQuery(id+"F0.wireOp",EDGE,"E2583"),sQuery(id+"F0.wireOp",EDGE,"E2584"),sQuery(id+"F0.wireOp",EDGE,"E2585"),sQuery(id+"F0.wireOp",EDGE,"E2586"),sQuery(id+"F0.wireOp",EDGE,"E2587"),sQuery(id+"F0.wireOp",EDGE,"E2588"),sQuery(id+"F0.wireOp",EDGE,"E2589"),sQuery(id+"F0.wireOp",EDGE,"E2590"),sQuery(id+"F0.wireOp",EDGE,"E2591"),sQuery(id+"F0.wireOp",EDGE,"E2592"),sQuery(id+"F0.wireOp",EDGE,"E2593"),sQuery(id+"F0.wireOp",EDGE,"E2594"),sQuery(id+"F0.wireOp",EDGE,"E2595"),sQuery(id+"F0.wireOp",EDGE,"E2596"),sQuery(id+"F0.wireOp",EDGE,"E2597"),sQuery(id+"F0.wireOp",EDGE,"E2598"),sQuery(id+"F0.wireOp",EDGE,"E2599"),sQuery(id+"F0.wireOp",EDGE,"E2600"),sQuery(id+"F0.wireOp",EDGE,"E2601"),sQuery(id+"F0.wireOp",EDGE,"E2602"),sQuery(id+"F0.wireOp",EDGE,"E2603"),sQuery(id+"F0.wireOp",EDGE,"E2604"),sQuery(id+"F0.wireOp",EDGE,"E2605"),sQuery(id+"F0.wireOp",EDGE,"E2606"),sQuery(id+"F0.wireOp",EDGE,"E2607"),sQuery(id+"F0.wireOp",EDGE,"E2608"),sQuery(id+"F0.wireOp",EDGE,"E2609"),sQuery(id+"F0.wireOp",EDGE,"E2610"),sQuery(id+"F0.wireOp",EDGE,"E2611"),sQuery(id+"F0.wireOp",EDGE,"E2612"),sQuery(id+"F0.wireOp",EDGE,"E2613"),sQuery(id+"F0.wireOp",EDGE,"E2614"),sQuery(id+"F0.wireOp",EDGE,"E2615"),sQuery(id+"F0.wireOp",EDGE,"E2616"),sQuery(id+"F0.wireOp",EDGE,"E2617"),sQuery(id+"F0.wireOp",EDGE,"E2618"),sQuery(id+"F0.wireOp",EDGE,"E2619"),sQuery(id+"F0.wireOp",EDGE,"E2620"),sQuery(id+"F0.wireOp",EDGE,"E2621"),sQuery(id+"F0.wireOp",EDGE,"E2622"),sQuery(id+"F0.wireOp",EDGE,"E2623"),sQuery(id+"F0.wireOp",EDGE,"E2624"),sQuery(id+"F0.wireOp",EDGE,"E2625"),sQuery(id+"F0.wireOp",EDGE,"E2626"),sQuery(id+"F0.wireOp",EDGE,"E2627"),sQuery(id+"F0.wireOp",EDGE,"E2628"),sQuery(id+"F0.wireOp",EDGE,"E2629"),sQuery(id+"F0.wireOp",EDGE,"E2630"),sQuery(id+"F0.wireOp",EDGE,"E2631"),sQuery(id+"F0.wireOp",EDGE,"E2632"),sQuery(id+"F0.wireOp",EDGE,"E2633"),sQuery(id+"F0.wireOp",EDGE,"E2634"),sQuery(id+"F0.wireOp",EDGE,"E2635"),sQuery(id+"F0.wireOp",EDGE,"E2636"),sQuery(id+"F0.wireOp",EDGE,"E2637"),sQuery(id+"F0.wireOp",EDGE,"E2638"),sQuery(id+"F0.wireOp",EDGE,"E2639"),sQuery(id+"F0.wireOp",EDGE,"E2640"),sQuery(id+"F0.wireOp",EDGE,"E2641"),sQuery(id+"F0.wireOp",EDGE,"E2642"),sQuery(id+"F0.wireOp",EDGE,"E2643"),sQuery(id+"F0.wireOp",EDGE,"E2644"),sQuery(id+"F0.wireOp",EDGE,"E2645"),sQuery(id+"F0.wireOp",EDGE,"E2646"),sQuery(id+"F0.wireOp",EDGE,"E2647"),sQuery(id+"F0.wireOp",EDGE,"E2648"),sQuery(id+"F0.wireOp",EDGE,"E2649"),sQuery(id+"F0.wireOp",EDGE,"E2650"),sQuery(id+"F0.wireOp",EDGE,"E2651"),sQuery(id+"F0.wireOp",EDGE,"E2652"),sQuery(id+"F0.wireOp",EDGE,"E2653"),sQuery(id+"F0.wireOp",EDGE,"E2654"),sQuery(id+"F0.wireOp",EDGE,"E2655"),sQuery(id+"F0.wireOp",EDGE,"E2656"),sQuery(id+"F0.wireOp",EDGE,"E2657"),sQuery(id+"F0.wireOp",EDGE,"E2658"),sQuery(id+"F0.wireOp",EDGE,"E2659"),sQuery(id+"F0.wireOp",EDGE,"E2660"),sQuery(id+"F0.wireOp",EDGE,"E2661"),sQuery(id+"F0.wireOp",EDGE,"E2662"),sQuery(id+"F0.wireOp",EDGE,"E2663"),sQuery(id+"F0.wireOp",EDGE,"E2664"),sQuery(id+"F0.wireOp",EDGE,"E2665"),sQuery(id+"F0.wireOp",EDGE,"E2666"),sQuery(id+"F0.wireOp",EDGE,"E2667"),sQuery(id+"F0.wireOp",EDGE,"E2668"),sQuery(id+"F0.wireOp",EDGE,"E2669"),sQuery(id+"F0.wireOp",EDGE,"E2670"),sQuery(id+"F0.wireOp",EDGE,"E2671"),sQuery(id+"F0.wireOp",EDGE,"E2672"),sQuery(id+"F0.wireOp",EDGE,"E2673"),sQuery(id+"F0.wireOp",EDGE,"E2674"),sQuery(id+"F0.wireOp",EDGE,"E2675"),sQuery(id+"F0.wireOp",EDGE,"E2676"),sQuery(id+"F0.wireOp",EDGE,"E2677"),sQuery(id+"F0.wireOp",EDGE,"E2678"),sQuery(id+"F0.wireOp",EDGE,"E2679"),sQuery(id+"F0.wireOp",EDGE,"E2680"),sQuery(id+"F0.wireOp",EDGE,"E2681"),sQuery(id+"F0.wireOp",EDGE,"E2682"),sQuery(id+"F0.wireOp",EDGE,"E2683"),sQuery(id+"F0.wireOp",EDGE,"E2684"),sQuery(id+"F0.wireOp",EDGE,"E2685"),sQuery(id+"F0.wireOp",EDGE,"E2686"),sQuery(id+"F0.wireOp",EDGE,"E2687"),sQuery(id+"F0.wireOp",EDGE,"E2688"),sQuery(id+"F0.wireOp",EDGE,"E2689"),sQuery(id+"F0.wireOp",EDGE,"E2690"),sQuery(id+"F0.wireOp",EDGE,"E2691"),sQuery(id+"F0.wireOp",EDGE,"E2692"),sQuery(id+"F0.wireOp",EDGE,"E2693"),sQuery(id+"F0.wireOp",EDGE,"E2694"),sQuery(id+"F0.wireOp",EDGE,"E2695"),sQuery(id+"F0.wireOp",EDGE,"E2696"),sQuery(id+"F0.wireOp",EDGE,"E2697"),sQuery(id+"F0.wireOp",EDGE,"E2698"),sQuery(id+"F0.wireOp",EDGE,"E2699"),sQuery(id+"F0.wireOp",EDGE,"E2700"),sQuery(id+"F0.wireOp",EDGE,"E2701"),sQuery(id+"F0.wireOp",EDGE,"E2702"),sQuery(id+"F0.wireOp",EDGE,"E2703"),sQuery(id+"F0.wireOp",EDGE,"E2704"),sQuery(id+"F0.wireOp",EDGE,"E2705"),sQuery(id+"F0.wireOp",EDGE,"E2706"),sQuery(id+"F0.wireOp",EDGE,"E2707"),sQuery(id+"F0.wireOp",EDGE,"E2708"),sQuery(id+"F0.wireOp",EDGE,"E2709"),sQuery(id+"F0.wireOp",EDGE,"E2710"),sQuery(id+"F0.wireOp",EDGE,"E2711"),sQuery(id+"F0.wireOp",EDGE,"E2712"),sQuery(id+"F0.wireOp",EDGE,"E2713"),sQuery(id+"F0.wireOp",EDGE,"E2714"),sQuery(id+"F0.wireOp",EDGE,"E2715"),sQuery(id+"F0.wireOp",EDGE,"E2716"),sQuery(id+"F0.wireOp",EDGE,"E2717"),sQuery(id+"F0.wireOp",EDGE,"E2718"),sQuery(id+"F0.wireOp",EDGE,"E2719"),sQuery(id+"F0.wireOp",EDGE,"E2720"),sQuery(id+"F0.wireOp",EDGE,"E2721"),sQuery(id+"F0.wireOp",EDGE,"E2722"),sQuery(id+"F0.wireOp",EDGE,"E2723"),sQuery(id+"F0.wireOp",EDGE,"E2724"),sQuery(id+"F0.wireOp",EDGE,"E2725"),sQuery(id+"F0.wireOp",EDGE,"E2726"),sQuery(id+"F0.wireOp",EDGE,"E2727"),sQuery(id+"F0.wireOp",EDGE,"E2728"),sQuery(id+"F0.wireOp",EDGE,"E2729"),sQuery(id+"F0.wireOp",EDGE,"E2730"),sQuery(id+"F0.wireOp",EDGE,"E2731"),sQuery(id+"F0.wireOp",EDGE,"E2732"),sQuery(id+"F0.wireOp",EDGE,"E2733"),sQuery(id+"F0.wireOp",EDGE,"E2734"),sQuery(id+"F0.wireOp",EDGE,"E2735"),sQuery(id+"F0.wireOp",EDGE,"E2736"),sQuery(id+"F0.wireOp",EDGE,"E2737"),sQuery(id+"F0.wireOp",EDGE,"E2738"),sQuery(id+"F0.wireOp",EDGE,"E2739"),sQuery(id+"F0.wireOp",EDGE,"E2740"),sQuery(id+"F0.wireOp",EDGE,"E2741"),sQuery(id+"F0.wireOp",EDGE,"E2742"),sQuery(id+"F0.wireOp",EDGE,"E2743"),sQuery(id+"F0.wireOp",EDGE,"E2744"),sQuery(id+"F0.wireOp",EDGE,"E2745"),sQuery(id+"F0.wireOp",EDGE,"E2746"),sQuery(id+"F0.wireOp",EDGE,"E2747"),sQuery(id+"F0.wireOp",EDGE,"E2748"),sQuery(id+"F0.wireOp",EDGE,"E2749"),sQuery(id+"F0.wireOp",EDGE,"E2750"),sQuery(id+"F0.wireOp",EDGE,"E2751"),sQuery(id+"F0.wireOp",EDGE,"E2752"),sQuery(id+"F0.wireOp",EDGE,"E2753"),sQuery(id+"F0.wireOp",EDGE,"E2754"),sQuery(id+"F0.wireOp",EDGE,"E2755"),sQuery(id+"F0.wireOp",EDGE,"E2756"),sQuery(id+"F0.wireOp",EDGE,"E2757"),sQuery(id+"F0.wireOp",EDGE,"E2758"),sQuery(id+"F0.wireOp",EDGE,"E2759"),sQuery(id+"F0.wireOp",EDGE,"E2760"),sQuery(id+"F0.wireOp",EDGE,"E2761"),sQuery(id+"F0.wireOp",EDGE,"E2762"),sQuery(id+"F0.wireOp",EDGE,"E2763"),sQuery(id+"F0.wireOp",EDGE,"E2764"),sQuery(id+"F0.wireOp",EDGE,"E2765"),sQuery(id+"F0.wireOp",EDGE,"E2766"),sQuery(id+"F0.wireOp",EDGE,"E2767"),sQuery(id+"F0.wireOp",EDGE,"E2768"),sQuery(id+"F0.wireOp",EDGE,"E2769"),sQuery(id+"F0.wireOp",EDGE,"E2770"),sQuery(id+"F0.wireOp",EDGE,"E2771"),sQuery(id+"F0.wireOp",EDGE,"E2772"),sQuery(id+"F0.wireOp",EDGE,"E2773"),sQuery(id+"F0.wireOp",EDGE,"E2774"),sQuery(id+"F0.wireOp",EDGE,"E2775"),sQuery(id+"F0.wireOp",EDGE,"E2776"),sQuery(id+"F0.wireOp",EDGE,"E2777"),sQuery(id+"F0.wireOp",EDGE,"E2778"),sQuery(id+"F0.wireOp",EDGE,"E2779"),sQuery(id+"F0.wireOp",EDGE,"E2780"),sQuery(id+"F0.wireOp",EDGE,"E2781"),sQuery(id+"F0.wireOp",EDGE,"E2782"),sQuery(id+"F0.wireOp",EDGE,"E2783"),sQuery(id+"F0.wireOp",EDGE,"E2784"),sQuery(id+"F0.wireOp",EDGE,"E2785"),sQuery(id+"F0.wireOp",EDGE,"E2786"),sQuery(id+"F0.wireOp",EDGE,"E2787"),sQuery(id+"F0.wireOp",EDGE,"E2788"),sQuery(id+"F0.wireOp",EDGE,"E2789"),sQuery(id+"F0.wireOp",EDGE,"E2790"),sQuery(id+"F0.wireOp",EDGE,"E2791"),sQuery(id+"F0.wireOp",EDGE,"E2792"),sQuery(id+"F0.wireOp",EDGE,"E2793"),sQuery(id+"F0.wireOp",EDGE,"E2794"),sQuery(id+"F0.wireOp",EDGE,"E2795"),sQuery(id+"F0.wireOp",EDGE,"E2796"),sQuery(id+"F0.wireOp",EDGE,"E2797"),sQuery(id+"F0.wireOp",EDGE,"E2798"),sQuery(id+"F0.wireOp",EDGE,"E2799"),sQuery(id+"F0.wireOp",EDGE,"E2800"),sQuery(id+"F0.wireOp",EDGE,"E2801"),sQuery(id+"F0.wireOp",EDGE,"E2802"),sQuery(id+"F0.wireOp",EDGE,"E2803"),sQuery(id+"F0.wireOp",EDGE,"E2804"),sQuery(id+"F0.wireOp",EDGE,"E2805"),sQuery(id+"F0.wireOp",EDGE,"E2806"),sQuery(id+"F0.wireOp",EDGE,"E2807"),sQuery(id+"F0.wireOp",EDGE,"E2808"),sQuery(id+"F0.wireOp",EDGE,"E2809"),sQuery(id+"F0.wireOp",EDGE,"E2810"),sQuery(id+"F0.wireOp",EDGE,"E2811"),sQuery(id+"F0.wireOp",EDGE,"E2812"),sQuery(id+"F0.wireOp",EDGE,"E2813"),sQuery(id+"F0.wireOp",EDGE,"E2814"),sQuery(id+"F0.wireOp",EDGE,"E2815"),sQuery(id+"F0.wireOp",EDGE,"E2816"),sQuery(id+"F0.wireOp",EDGE,"E2817"),sQuery(id+"F0.wireOp",EDGE,"E2818"),sQuery(id+"F0.wireOp",EDGE,"E2819"),sQuery(id+"F0.wireOp",EDGE,"E2820"),sQuery(id+"F0.wireOp",EDGE,"E2821"),sQuery(id+"F0.wireOp",EDGE,"E2822"),sQuery(id+"F0.wireOp",EDGE,"E2823"),sQuery(id+"F0.wireOp",EDGE,"E2824"),sQuery(id+"F0.wireOp",EDGE,"E2825"),sQuery(id+"F0.wireOp",EDGE,"E2826"),sQuery(id+"F0.wireOp",EDGE,"E2827"),sQuery(id+"F0.wireOp",EDGE,"E2828"),sQuery(id+"F0.wireOp",EDGE,"E2829"),sQuery(id+"F0.wireOp",EDGE,"E2830"),sQuery(id+"F0.wireOp",EDGE,"E2831"),sQuery(id+"F0.wireOp",EDGE,"E2832"),sQuery(id+"F0.wireOp",EDGE,"E2833"),sQuery(id+"F0.wireOp",EDGE,"E2834"),sQuery(id+"F0.wireOp",EDGE,"E2835"),sQuery(id+"F0.wireOp",EDGE,"E2836"),sQuery(id+"F0.wireOp",EDGE,"E2837"),sQuery(id+"F0.wireOp",EDGE,"E2838"),sQuery(id+"F0.wireOp",EDGE,"E2839"),sQuery(id+"F0.wireOp",EDGE,"E2840"),sQuery(id+"F0.wireOp",EDGE,"E2841"),sQuery(id+"F0.wireOp",EDGE,"E2842"),sQuery(id+"F0.wireOp",EDGE,"E2843"),sQuery(id+"F0.wireOp",EDGE,"E2844"),sQuery(id+"F0.wireOp",EDGE,"E2845"),sQuery(id+"F0.wireOp",EDGE,"E2846"),sQuery(id+"F0.wireOp",EDGE,"E2847"),sQuery(id+"F0.wireOp",EDGE,"E2848"),sQuery(id+"F0.wireOp",EDGE,"E2849"),sQuery(id+"F0.wireOp",EDGE,"E2850"),sQuery(id+"F0.wireOp",EDGE,"E2851"),sQuery(id+"F0.wireOp",EDGE,"E2852"),sQuery(id+"F0.wireOp",EDGE,"E2853"),sQuery(id+"F0.wireOp",EDGE,"E2854"),sQuery(id+"F0.wireOp",EDGE,"E2855"),sQuery(id+"F0.wireOp",EDGE,"E2856"),sQuery(id+"F0.wireOp",EDGE,"E2857"),sQuery(id+"F0.wireOp",EDGE,"E2858"),sQuery(id+"F0.wireOp",EDGE,"E2859"),sQuery(id+"F0.wireOp",EDGE,"E2860"),sQuery(id+"F0.wireOp",EDGE,"E2861"),sQuery(id+"F0.wireOp",EDGE,"E2862"),sQuery(id+"F0.wireOp",EDGE,"E2863"),sQuery(id+"F0.wireOp",EDGE,"E2864"),sQuery(id+"F0.wireOp",EDGE,"E2865"),sQuery(id+"F0.wireOp",EDGE,"E2866"),sQuery(id+"F0.wireOp",EDGE,"E2867"),sQuery(id+"F0.wireOp",EDGE,"E2868"),sQuery(id+"F0.wireOp",EDGE,"E2869"),sQuery(id+"F0.wireOp",EDGE,"E2870"),sQuery(id+"F0.wireOp",EDGE,"E2871"),sQuery(id+"F0.wireOp",EDGE,"E2872"),sQuery(id+"F0.wireOp",EDGE,"E2873"),sQuery(id+"F0.wireOp",EDGE,"E2874"),sQuery(id+"F0.wireOp",EDGE,"E2875"),sQuery(id+"F0.wireOp",EDGE,"E2876"),sQuery(id+"F0.wireOp",EDGE,"E2877"),sQuery(id+"F0.wireOp",EDGE,"E2878"),sQuery(id+"F0.wireOp",EDGE,"E2879"),sQuery(id+"F0.wireOp",EDGE,"E2880"),sQuery(id+"F0.wireOp",EDGE,"E2881"),sQuery(id+"F0.wireOp",EDGE,"E2882"),sQuery(id+"F0.wireOp",EDGE,"E2883"),sQuery(id+"F0.wireOp",EDGE,"E2884"),sQuery(id+"F0.wireOp",EDGE,"E2885"),sQuery(id+"F0.wireOp",EDGE,"E2886"),sQuery(id+"F0.wireOp",EDGE,"E2887"),sQuery(id+"F0.wireOp",EDGE,"E2888"),sQuery(id+"F0.wireOp",EDGE,"E2889"),sQuery(id+"F0.wireOp",EDGE,"E2890"),sQuery(id+"F0.wireOp",EDGE,"E2891"),sQuery(id+"F0.wireOp",EDGE,"E2892"),sQuery(id+"F0.wireOp",EDGE,"E2893"),sQuery(id+"F0.wireOp",EDGE,"E2894"),sQuery(id+"F0.wireOp",EDGE,"E2895"),sQuery(id+"F0.wireOp",EDGE,"E2896"),sQuery(id+"F0.wireOp",EDGE,"E2897"),sQuery(id+"F0.wireOp",EDGE,"E2898"),sQuery(id+"F0.wireOp",EDGE,"E2899"),sQuery(id+"F0.wireOp",EDGE,"E2900"),sQuery(id+"F0.wireOp",EDGE,"E2901"),sQuery(id+"F0.wireOp",EDGE,"E2902"),sQuery(id+"F0.wireOp",EDGE,"E2903"),sQuery(id+"F0.wireOp",EDGE,"E2904"),sQuery(id+"F0.wireOp",EDGE,"E2905"),sQuery(id+"F0.wireOp",EDGE,"E2906"),sQuery(id+"F0.wireOp",EDGE,"E2907"),sQuery(id+"F0.wireOp",EDGE,"E2908"),sQuery(id+"F0.wireOp",EDGE,"E2909"),sQuery(id+"F0.wireOp",EDGE,"E2910"),sQuery(id+"F0.wireOp",EDGE,"E2911"),sQuery(id+"F0.wireOp",EDGE,"E2912"),sQuery(id+"F0.wireOp",EDGE,"E2913"),sQuery(id+"F0.wireOp",EDGE,"E2914"),sQuery(id+"F0.wireOp",EDGE,"E2915"),sQuery(id+"F0.wireOp",EDGE,"E2916"),sQuery(id+"F0.wireOp",EDGE,"E2917"),sQuery(id+"F0.wireOp",EDGE,"E2918"),sQuery(id+"F0.wireOp",EDGE,"E2919"),sQuery(id+"F0.wireOp",EDGE,"E2920"),sQuery(id+"F0.wireOp",EDGE,"E2921"),sQuery(id+"F0.wireOp",EDGE,"E2922"),sQuery(id+"F0.wireOp",EDGE,"E2923"),sQuery(id+"F0.wireOp",EDGE,"E2924"),sQuery(id+"F0.wireOp",EDGE,"E2925"),sQuery(id+"F0.wireOp",EDGE,"E2926"),sQuery(id+"F0.wireOp",EDGE,"E2927"),sQuery(id+"F0.wireOp",EDGE,"E2928"),sQuery(id+"F0.wireOp",EDGE,"E2929"),sQuery(id+"F0.wireOp",EDGE,"E2930"),sQuery(id+"F0.wireOp",EDGE,"E2931"),sQuery(id+"F0.wireOp",EDGE,"E2932"),sQuery(id+"F0.wireOp",EDGE,"E2933"),sQuery(id+"F0.wireOp",EDGE,"E2934"),sQuery(id+"F0.wireOp",EDGE,"E2935"),sQuery(id+"F0.wireOp",EDGE,"E2936"),sQuery(id+"F0.wireOp",EDGE,"E2937"),sQuery(id+"F0.wireOp",EDGE,"E2938"),sQuery(id+"F0.wireOp",EDGE,"E2939"),sQuery(id+"F0.wireOp",EDGE,"E2940"),sQuery(id+"F0.wireOp",EDGE,"E2941"),sQuery(id+"F0.wireOp",EDGE,"E2942"),sQuery(id+"F0.wireOp",EDGE,"E2943"),sQuery(id+"F0.wireOp",EDGE,"E2944"),sQuery(id+"F0.wireOp",EDGE,"E2945"),sQuery(id+"F0.wireOp",EDGE,"E2946"),sQuery(id+"F0.wireOp",EDGE,"E2947"),sQuery(id+"F0.wireOp",EDGE,"E2948"),sQuery(id+"F0.wireOp",EDGE,"E2949"),sQuery(id+"F0.wireOp",EDGE,"E2950"),sQuery(id+"F0.wireOp",EDGE,"E2951"),sQuery(id+"F0.wireOp",EDGE,"E2952"),sQuery(id+"F0.wireOp",EDGE,"E2953"),sQuery(id+"F0.wireOp",EDGE,"E2954"),sQuery(id+"F0.wireOp",EDGE,"E2955"),sQuery(id+"F0.wireOp",EDGE,"E2956"),sQuery(id+"F0.wireOp",EDGE,"E2957"),sQuery(id+"F0.wireOp",EDGE,"E2958"),sQuery(id+"F0.wireOp",EDGE,"E2959"),sQuery(id+"F0.wireOp",EDGE,"E2960"),sQuery(id+"F0.wireOp",EDGE,"E2961"),sQuery(id+"F0.wireOp",EDGE,"E2962"),sQuery(id+"F0.wireOp",EDGE,"E2963"),sQuery(id+"F0.wireOp",EDGE,"E2964"),sQuery(id+"F0.wireOp",EDGE,"E2965"),sQuery(id+"F0.wireOp",EDGE,"E2966"),sQuery(id+"F0.wireOp",EDGE,"E2967"),sQuery(id+"F0.wireOp",EDGE,"E2968"),sQuery(id+"F0.wireOp",EDGE,"E2969"),sQuery(id+"F0.wireOp",EDGE,"E2970"),sQuery(id+"F0.wireOp",EDGE,"E2971"),sQuery(id+"F0.wireOp",EDGE,"E2972"),sQuery(id+"F0.wireOp",EDGE,"E2973"),sQuery(id+"F0.wireOp",EDGE,"E2974"),sQuery(id+"F0.wireOp",EDGE,"E2975"),sQuery(id+"F0.wireOp",EDGE,"E2976"),sQuery(id+"F0.wireOp",EDGE,"E2977"),sQuery(id+"F0.wireOp",EDGE,"E2978"),sQuery(id+"F0.wireOp",EDGE,"E2979"),sQuery(id+"F0.wireOp",EDGE,"E2980"),sQuery(id+"F0.wireOp",EDGE,"E2981"),sQuery(id+"F0.wireOp",EDGE,"E2982"),sQuery(id+"F0.wireOp",EDGE,"E2983"),sQuery(id+"F0.wireOp",EDGE,"E2984"),sQuery(id+"F0.wireOp",EDGE,"E2985"),sQuery(id+"F0.wireOp",EDGE,"E2986"),sQuery(id+"F0.wireOp",EDGE,"E2987"),sQuery(id+"F0.wireOp",EDGE,"E2988"),sQuery(id+"F0.wireOp",EDGE,"E2989"),sQuery(id+"F0.wireOp",EDGE,"E2990"),sQuery(id+"F0.wireOp",EDGE,"E2991"),sQuery(id+"F0.wireOp",EDGE,"E2992"),sQuery(id+"F0.wireOp",EDGE,"E2993"),sQuery(id+"F0.wireOp",EDGE,"E2994"),sQuery(id+"F0.wireOp",EDGE,"E2995"),sQuery(id+"F0.wireOp",EDGE,"E2996"),sQuery(id+"F0.wireOp",EDGE,"E2997"),sQuery(id+"F0.wireOp",EDGE,"E2998"),sQuery(id+"F0.wireOp",EDGE,"E2999"),sQuery(id+"F0.wireOp",EDGE,"E3000"),sQuery(id+"F0.wireOp",EDGE,"E3001"),sQuery(id+"F0.wireOp",EDGE,"E3002"),sQuery(id+"F0.wireOp",EDGE,"E3003"),sQuery(id+"F0.wireOp",EDGE,"E3004"),sQuery(id+"F0.wireOp",EDGE,"E3005"),sQuery(id+"F0.wireOp",EDGE,"E3006"),sQuery(id+"F0.wireOp",EDGE,"E3007"),sQuery(id+"F0.wireOp",EDGE,"E3008"),sQuery(id+"F0.wireOp",EDGE,"E3009"),sQuery(id+"F0.wireOp",EDGE,"E3010"),sQuery(id+"F0.wireOp",EDGE,"E3011"),sQuery(id+"F0.wireOp",EDGE,"E3012"),sQuery(id+"F0.wireOp",EDGE,"E3013"),sQuery(id+"F0.wireOp",EDGE,"E3014"),sQuery(id+"F0.wireOp",EDGE,"E3015"),sQuery(id+"F0.wireOp",EDGE,"E3016"),sQuery(id+"F0.wireOp",EDGE,"E3017"),sQuery(id+"F0.wireOp",EDGE,"E3018"),sQuery(id+"F0.wireOp",EDGE,"E3019"),sQuery(id+"F0.wireOp",EDGE,"E3020"),sQuery(id+"F0.wireOp",EDGE,"E3021"),sQuery(id+"F0.wireOp",EDGE,"E3022"),sQuery(id+"F0.wireOp",EDGE,"E3023"),sQuery(id+"F0.wireOp",EDGE,"E3024"),sQuery(id+"F0.wireOp",EDGE,"E3025"),sQuery(id+"F0.wireOp",EDGE,"E3026"),sQuery(id+"F0.wireOp",EDGE,"E3027"),sQuery(id+"F0.wireOp",EDGE,"E3028"),sQuery(id+"F0.wireOp",EDGE,"E3029"),sQuery(id+"F0.wireOp",EDGE,"E3030"),sQuery(id+"F0.wireOp",EDGE,"E3031"),sQuery(id+"F0.wireOp",EDGE,"E3032"),sQuery(id+"F0.wireOp",EDGE,"E3033"),sQuery(id+"F0.wireOp",EDGE,"E3034"),sQuery(id+"F0.wireOp",EDGE,"E3035"),sQuery(id+"F0.wireOp",EDGE,"E3036"),sQuery(id+"F0.wireOp",EDGE,"E3037"),sQuery(id+"F0.wireOp",EDGE,"E3038"),sQuery(id+"F0.wireOp",EDGE,"E3039"),sQuery(id+"F0.wireOp",EDGE,"E3040"),sQuery(id+"F0.wireOp",EDGE,"E3041"),sQuery(id+"F0.wireOp",EDGE,"E3042"),sQuery(id+"F0.wireOp",EDGE,"E3043"),sQuery(id+"F0.wireOp",EDGE,"E3044"),sQuery(id+"F0.wireOp",EDGE,"E3045"),sQuery(id+"F0.wireOp",EDGE,"E3046"),sQuery(id+"F0.wireOp",EDGE,"E3047"),sQuery(id+"F0.wireOp",EDGE,"E3048"),sQuery(id+"F0.wireOp",EDGE,"E3049"),sQuery(id+"F0.wireOp",EDGE,"E3050"),sQuery(id+"F0.wireOp",EDGE,"E3051"),sQuery(id+"F0.wireOp",EDGE,"E3052"),sQuery(id+"F0.wireOp",EDGE,"E3053"),sQuery(id+"F0.wireOp",EDGE,"E3054"),sQuery(id+"F0.wireOp",EDGE,"E3055"),sQuery(id+"F0.wireOp",EDGE,"E3056"),sQuery(id+"F0.wireOp",EDGE,"E3057"),sQuery(id+"F0.wireOp",EDGE,"E3058"),sQuery(id+"F0.wireOp",EDGE,"E3059"),sQuery(id+"F0.wireOp",EDGE,"E3060"),sQuery(id+"F0.wireOp",EDGE,"E3061"),sQuery(id+"F0.wireOp",EDGE,"E3062"),sQuery(id+"F0.wireOp",EDGE,"E3063"),sQuery(id+"F0.wireOp",EDGE,"E3064"),sQuery(id+"F0.wireOp",EDGE,"E3065"),sQuery(id+"F0.wireOp",EDGE,"E3066"),sQuery(id+"F0.wireOp",EDGE,"E3067"),sQuery(id+"F0.wireOp",EDGE,"E3068"),sQuery(id+"F0.wireOp",EDGE,"E3069"),sQuery(id+"F0.wireOp",EDGE,"E3070"),sQuery(id+"F0.wireOp",EDGE,"E3071"),sQuery(id+"F0.wireOp",EDGE,"E3072"),sQuery(id+"F0.wireOp",EDGE,"E3073"),sQuery(id+"F0.wireOp",EDGE,"E3074"),sQuery(id+"F0.wireOp",EDGE,"E3075"),sQuery(id+"F0.wireOp",EDGE,"E3076"),sQuery(id+"F0.wireOp",EDGE,"E3077"),sQuery(id+"F0.wireOp",EDGE,"E3078"),sQuery(id+"F0.wireOp",EDGE,"E3079"),sQuery(id+"F0.wireOp",EDGE,"E3080"),sQuery(id+"F0.wireOp",EDGE,"E3081"),sQuery(id+"F0.wireOp",EDGE,"E3082"),sQuery(id+"F0.wireOp",EDGE,"E3083"),sQuery(id+"F0.wireOp",EDGE,"E3084"),sQuery(id+"F0.wireOp",EDGE,"E3085"),sQuery(id+"F0.wireOp",EDGE,"E3086"),sQuery(id+"F0.wireOp",EDGE,"E3087"),sQuery(id+"F0.wireOp",EDGE,"E3088"),sQuery(id+"F0.wireOp",EDGE,"E3089"),sQuery(id+"F0.wireOp",EDGE,"E3090"),sQuery(id+"F0.wireOp",EDGE,"E3091"),sQuery(id+"F0.wireOp",EDGE,"E3092"),sQuery(id+"F0.wireOp",EDGE,"E3093"),sQuery(id+"F0.wireOp",EDGE,"E3094"),sQuery(id+"F0.wireOp",EDGE,"E3095"),sQuery(id+"F0.wireOp",EDGE,"E3096"),sQuery(id+"F0.wireOp",EDGE,"E3097"),sQuery(id+"F0.wireOp",EDGE,"E3098"),sQuery(id+"F0.wireOp",EDGE,"E3099"),sQuery(id+"F0.wireOp",EDGE,"E3100"),sQuery(id+"F0.wireOp",EDGE,"E3101"),sQuery(id+"F0.wireOp",EDGE,"E3102"),sQuery(id+"F0.wireOp",EDGE,"E3103"),sQuery(id+"F0.wireOp",EDGE,"E3104"),sQuery(id+"F0.wireOp",EDGE,"E3105"),sQuery(id+"F0.wireOp",EDGE,"E3106"),sQuery(id+"F0.wireOp",EDGE,"E3107"),sQuery(id+"F0.wireOp",EDGE,"E3108"),sQuery(id+"F0.wireOp",EDGE,"E3109"),sQuery(id+"F0.wireOp",EDGE,"E3110"),sQuery(id+"F0.wireOp",EDGE,"E3111"),sQuery(id+"F0.wireOp",EDGE,"E3112"),sQuery(id+"F0.wireOp",EDGE,"E3113"),sQuery(id+"F0.wireOp",EDGE,"E3114"),sQuery(id+"F0.wireOp",EDGE,"E3115"),sQuery(id+"F0.wireOp",EDGE,"E3116"),sQuery(id+"F0.wireOp",EDGE,"E3117"),sQuery(id+"F0.wireOp",EDGE,"E3118"),sQuery(id+"F0.wireOp",EDGE,"E3119"),sQuery(id+"F0.wireOp",EDGE,"E3120"),sQuery(id+"F0.wireOp",EDGE,"E3121"),sQuery(id+"F0.wireOp",EDGE,"E3122"),sQuery(id+"F0.wireOp",EDGE,"E3123"),sQuery(id+"F0.wireOp",EDGE,"E3124"),sQuery(id+"F0.wireOp",EDGE,"E3125"),sQuery(id+"F0.wireOp",EDGE,"E3126"),sQuery(id+"F0.wireOp",EDGE,"E3127"),sQuery(id+"F0.wireOp",EDGE,"E3128"),sQuery(id+"F0.wireOp",EDGE,"E3129"),sQuery(id+"F0.wireOp",EDGE,"E3130"),sQuery(id+"F0.wireOp",EDGE,"E3131"),sQuery(id+"F0.wireOp",EDGE,"E3132"),sQuery(id+"F0.wireOp",EDGE,"E3133"),sQuery(id+"F0.wireOp",EDGE,"E3134"),sQuery(id+"F0.wireOp",EDGE,"E3135"),sQuery(id+"F0.wireOp",EDGE,"E3136"),sQuery(id+"F0.wireOp",EDGE,"E3137"),sQuery(id+"F0.wireOp",EDGE,"E3138"),sQuery(id+"F0.wireOp",EDGE,"E3139"),sQuery(id+"F0.wireOp",EDGE,"E3140"),sQuery(id+"F0.wireOp",EDGE,"E3141"),sQuery(id+"F0.wireOp",EDGE,"E3142"),sQuery(id+"F0.wireOp",EDGE,"E3143"),sQuery(id+"F0.wireOp",EDGE,"E3144"),sQuery(id+"F0.wireOp",EDGE,"E3145"),sQuery(id+"F0.wireOp",EDGE,"E3146"),sQuery(id+"F0.wireOp",EDGE,"E3147"),sQuery(id+"F0.wireOp",EDGE,"E3148"),sQuery(id+"F0.wireOp",EDGE,"E3149"),sQuery(id+"F0.wireOp",EDGE,"E3150"),sQuery(id+"F0.wireOp",EDGE,"E3151"),sQuery(id+"F0.wireOp",EDGE,"E3152"),sQuery(id+"F0.wireOp",EDGE,"E3153"),sQuery(id+"F0.wireOp",EDGE,"E3154"),sQuery(id+"F0.wireOp",EDGE,"E3155"),sQuery(id+"F0.wireOp",EDGE,"E3156"),sQuery(id+"F0.wireOp",EDGE,"E3157"),sQuery(id+"F0.wireOp",EDGE,"E3158"),sQuery(id+"F0.wireOp",EDGE,"E3159"),sQuery(id+"F0.wireOp",EDGE,"E3160"),sQuery(id+"F0.wireOp",EDGE,"E3161"),sQuery(id+"F0.wireOp",EDGE,"E3162"),sQuery(id+"F0.wireOp",EDGE,"E3163"),sQuery(id+"F0.wireOp",EDGE,"E3164"),sQuery(id+"F0.wireOp",EDGE,"E3165"),sQuery(id+"F0.wireOp",EDGE,"E3166"),sQuery(id+"F0.wireOp",EDGE,"E3167"),sQuery(id+"F0.wireOp",EDGE,"E3168"),sQuery(id+"F0.wireOp",EDGE,"E3169"),sQuery(id+"F0.wireOp",EDGE,"E3170"),sQuery(id+"F0.wireOp",EDGE,"E3171"),sQuery(id+"F0.wireOp",EDGE,"E3172"),sQuery(id+"F0.wireOp",EDGE,"E3173"),sQuery(id+"F0.wireOp",EDGE,"E3174"),sQuery(id+"F0.wireOp",EDGE,"E3175"),sQuery(id+"F0.wireOp",EDGE,"E3176"),sQuery(id+"F0.wireOp",EDGE,"E3177"),sQuery(id+"F0.wireOp",EDGE,"E3178"),sQuery(id+"F0.wireOp",EDGE,"E3179"),sQuery(id+"F0.wireOp",EDGE,"E3180"),sQuery(id+"F0.wireOp",EDGE,"E3181"),sQuery(id+"F0.wireOp",EDGE,"E3182"),sQuery(id+"F0.wireOp",EDGE,"E3183"),sQuery(id+"F0.wireOp",EDGE,"E3184"),sQuery(id+"F0.wireOp",EDGE,"E3185"),sQuery(id+"F0.wireOp",EDGE,"E3186"),sQuery(id+"F0.wireOp",EDGE,"E3187"),sQuery(id+"F0.wireOp",EDGE,"E3188"),sQuery(id+"F0.wireOp",EDGE,"E3189"),sQuery(id+"F0.wireOp",EDGE,"E3190"),sQuery(id+"F0.wireOp",EDGE,"E3191"),sQuery(id+"F0.wireOp",EDGE,"E3192"),sQuery(id+"F0.wireOp",EDGE,"E3193"),sQuery(id+"F0.wireOp",EDGE,"E3194"),sQuery(id+"F0.wireOp",EDGE,"E3195"),sQuery(id+"F0.wireOp",EDGE,"E3196"),sQuery(id+"F0.wireOp",EDGE,"E3197"),sQuery(id+"F0.wireOp",EDGE,"E3198"),sQuery(id+"F0.wireOp",EDGE,"E3199"),sQuery(id+"F0.wireOp",EDGE,"E3200"),sQuery(id+"F0.wireOp",EDGE,"E3201"),sQuery(id+"F0.wireOp",EDGE,"E3202"),sQuery(id+"F0.wireOp",EDGE,"E3203"),sQuery(id+"F0.wireOp",EDGE,"E3204"),sQuery(id+"F0.wireOp",EDGE,"E3205"),sQuery(id+"F0.wireOp",EDGE,"E3206"),sQuery(id+"F0.wireOp",EDGE,"E3207"),sQuery(id+"F0.wireOp",EDGE,"E3208"),sQuery(id+"F0.wireOp",EDGE,"E3209"),sQuery(id+"F0.wireOp",EDGE,"E3210"),sQuery(id+"F0.wireOp",EDGE,"E3211"),sQuery(id+"F0.wireOp",EDGE,"E3212"),sQuery(id+"F0.wireOp",EDGE,"E3213"),sQuery(id+"F0.wireOp",EDGE,"E3214"),sQuery(id+"F0.wireOp",EDGE,"E3215"),sQuery(id+"F0.wireOp",EDGE,"E3216"),sQuery(id+"F0.wireOp",EDGE,"E3217"),sQuery(id+"F0.wireOp",EDGE,"E3218"),sQuery(id+"F0.wireOp",EDGE,"E3219"),sQuery(id+"F0.wireOp",EDGE,"E3220"),sQuery(id+"F0.wireOp",EDGE,"E3221"),sQuery(id+"F0.wireOp",EDGE,"E3222"),sQuery(id+"F0.wireOp",EDGE,"E3223"),sQuery(id+"F0.wireOp",EDGE,"E3224"),sQuery(id+"F0.wireOp",EDGE,"E3225"),sQuery(id+"F0.wireOp",EDGE,"E3226"),sQuery(id+"F0.wireOp",EDGE,"E3227"),sQuery(id+"F0.wireOp",EDGE,"E3228"),sQuery(id+"F0.wireOp",EDGE,"E3229"),sQuery(id+"F0.wireOp",EDGE,"E3230"),sQuery(id+"F0.wireOp",EDGE,"E3231"),sQuery(id+"F0.wireOp",EDGE,"E3232"),sQuery(id+"F0.wireOp",EDGE,"E3233"),sQuery(id+"F0.wireOp",EDGE,"E3234"),sQuery(id+"F0.wireOp",EDGE,"E3235"),sQuery(id+"F0.wireOp",EDGE,"E3236"),sQuery(id+"F0.wireOp",EDGE,"E3237"),sQuery(id+"F0.wireOp",EDGE,"E3238"),sQuery(id+"F0.wireOp",EDGE,"E3239"),sQuery(id+"F0.wireOp",EDGE,"E3240"),sQuery(id+"F0.wireOp",EDGE,"E3241"),sQuery(id+"F0.wireOp",EDGE,"E3242"),sQuery(id+"F0.wireOp",EDGE,"E3243"),sQuery(id+"F0.wireOp",EDGE,"E3244"),sQuery(id+"F0.wireOp",EDGE,"E3245"),sQuery(id+"F0.wireOp",EDGE,"E3246"),sQuery(id+"F0.wireOp",EDGE,"E3247"),sQuery(id+"F0.wireOp",EDGE,"E3248"),sQuery(id+"F0.wireOp",EDGE,"E3249"),sQuery(id+"F0.wireOp",EDGE,"E3250"),sQuery(id+"F0.wireOp",EDGE,"E3251"),sQuery(id+"F0.wireOp",EDGE,"E3252"),sQuery(id+"F0.wireOp",EDGE,"E3253"),sQuery(id+"F0.wireOp",EDGE,"E3254"),sQuery(id+"F0.wireOp",EDGE,"E3255"),sQuery(id+"F0.wireOp",EDGE,"E3256"),sQuery(id+"F0.wireOp",EDGE,"E3257"),sQuery(id+"F0.wireOp",EDGE,"E3258"),sQuery(id+"F0.wireOp",EDGE,"E3259"),sQuery(id+"F0.wireOp",EDGE,"E3260"),sQuery(id+"F0.wireOp",EDGE,"E3261"),sQuery(id+"F0.wireOp",EDGE,"E3262"),sQuery(id+"F0.wireOp",EDGE,"E3263"),sQuery(id+"F0.wireOp",EDGE,"E3264"),sQuery(id+"F0.wireOp",EDGE,"E3265"),sQuery(id+"F0.wireOp",EDGE,"E3266"),sQuery(id+"F0.wireOp",EDGE,"E3267"),sQuery(id+"F0.wireOp",EDGE,"E3268"),sQuery(id+"F0.wireOp",EDGE,"E3269"),sQuery(id+"F0.wireOp",EDGE,"E3270"),sQuery(id+"F0.wireOp",EDGE,"E3271"),sQuery(id+"F0.wireOp",EDGE,"E3272"),sQuery(id+"F0.wireOp",EDGE,"E3273"),sQuery(id+"F0.wireOp",EDGE,"E3274"),sQuery(id+"F0.wireOp",EDGE,"E3275"),sQuery(id+"F0.wireOp",EDGE,"E3276"),sQuery(id+"F0.wireOp",EDGE,"E3277"),sQuery(id+"F0.wireOp",EDGE,"E3278"),sQuery(id+"F0.wireOp",EDGE,"E3279"),sQuery(id+"F0.wireOp",EDGE,"E3280"),sQuery(id+"F0.wireOp",EDGE,"E3281"),sQuery(id+"F0.wireOp",EDGE,"E3282"),sQuery(id+"F0.wireOp",EDGE,"E3283"),sQuery(id+"F0.wireOp",EDGE,"E3284"),sQuery(id+"F0.wireOp",EDGE,"E3285"),sQuery(id+"F0.wireOp",EDGE,"E3286"),sQuery(id+"F0.wireOp",EDGE,"E3287"),sQuery(id+"F0.wireOp",EDGE,"E3288"),sQuery(id+"F0.wireOp",EDGE,"E3289"),sQuery(id+"F0.wireOp",EDGE,"E3290"),sQuery(id+"F0.wireOp",EDGE,"E3291"),sQuery(id+"F0.wireOp",EDGE,"E3292"),sQuery(id+"F0.wireOp",EDGE,"E3293"),sQuery(id+"F0.wireOp",EDGE,"E3294"),sQuery(id+"F0.wireOp",EDGE,"E3295"),sQuery(id+"F0.wireOp",EDGE,"E3296"),sQuery(id+"F0.wireOp",EDGE,"E3297"),sQuery(id+"F0.wireOp",EDGE,"E3298"),sQuery(id+"F0.wireOp",EDGE,"E3299"),sQuery(id+"F0.wireOp",EDGE,"E3300"),sQuery(id+"F0.wireOp",EDGE,"E3301"),sQuery(id+"F0.wireOp",EDGE,"E3302"),sQuery(id+"F0.wireOp",EDGE,"E3303"),sQuery(id+"F0.wireOp",EDGE,"E3304"),sQuery(id+"F0.wireOp",EDGE,"E3305"),sQuery(id+"F0.wireOp",EDGE,"E3306"),sQuery(id+"F0.wireOp",EDGE,"E3307"),sQuery(id+"F0.wireOp",EDGE,"E3308"),sQuery(id+"F0.wireOp",EDGE,"E3309"),sQuery(id+"F0.wireOp",EDGE,"E3310"),sQuery(id+"F0.wireOp",EDGE,"E3311"),sQuery(id+"F0.wireOp",EDGE,"E3312"),sQuery(id+"F0.wireOp",EDGE,"E3313"),sQuery(id+"F0.wireOp",EDGE,"E3314"),sQuery(id+"F0.wireOp",EDGE,"E3315"),sQuery(id+"F0.wireOp",EDGE,"E3316"),sQuery(id+"F0.wireOp",EDGE,"E3317"),sQuery(id+"F0.wireOp",EDGE,"E3318"),sQuery(id+"F0.wireOp",EDGE,"E3319"),sQuery(id+"F0.wireOp",EDGE,"E3320"),sQuery(id+"F0.wireOp",EDGE,"E3321"),sQuery(id+"F0.wireOp",EDGE,"E3322"),sQuery(id+"F0.wireOp",EDGE,"E3323"),sQuery(id+"F0.wireOp",EDGE,"E3324"),sQuery(id+"F0.wireOp",EDGE,"E3325"),sQuery(id+"F0.wireOp",EDGE,"E3326"),sQuery(id+"F0.wireOp",EDGE,"E3327"),sQuery(id+"F0.wireOp",EDGE,"E3328"),sQuery(id+"F0.wireOp",EDGE,"E3329"),sQuery(id+"F0.wireOp",EDGE,"E3330"),sQuery(id+"F0.wireOp",EDGE,"E3331"),sQuery(id+"F0.wireOp",EDGE,"E3332"),sQuery(id+"F0.wireOp",EDGE,"E3333"),sQuery(id+"F0.wireOp",EDGE,"E3334"),sQuery(id+"F0.wireOp",EDGE,"E3335"),sQuery(id+"F0.wireOp",EDGE,"E3336"),sQuery(id+"F0.wireOp",EDGE,"E3337"),sQuery(id+"F0.wireOp",EDGE,"E3338"),sQuery(id+"F0.wireOp",EDGE,"E3339"),sQuery(id+"F0.wireOp",EDGE,"E3340"),sQuery(id+"F0.wireOp",EDGE,"E3341"),sQuery(id+"F0.wireOp",EDGE,"E3342"),sQuery(id+"F0.wireOp",EDGE,"E3343"),sQuery(id+"F0.wireOp",EDGE,"E3344"),sQuery(id+"F0.wireOp",EDGE,"E3345"),sQuery(id+"F0.wireOp",EDGE,"E3346"),sQuery(id+"F0.wireOp",EDGE,"E3347"),sQuery(id+"F0.wireOp",EDGE,"E3348"),sQuery(id+"F0.wireOp",EDGE,"E3349"),sQuery(id+"F0.wireOp",EDGE,"E3350"),sQuery(id+"F0.wireOp",EDGE,"E3351"),sQuery(id+"F0.wireOp",EDGE,"E3352"),sQuery(id+"F0.wireOp",EDGE,"E3353"),sQuery(id+"F0.wireOp",EDGE,"E3354"),sQuery(id+"F0.wireOp",EDGE,"E3355"),sQuery(id+"F0.wireOp",EDGE,"E3356"),sQuery(id+"F0.wireOp",EDGE,"E3357"),sQuery(id+"F0.wireOp",EDGE,"E3358"),sQuery(id+"F0.wireOp",EDGE,"E3359"),sQuery(id+"F0.wireOp",EDGE,"E3360"),sQuery(id+"F0.wireOp",EDGE,"E3361"),sQuery(id+"F0.wireOp",EDGE,"E3362"),sQuery(id+"F0.wireOp",EDGE,"E3363"),sQuery(id+"F0.wireOp",EDGE,"E3364"),sQuery(id+"F0.wireOp",EDGE,"E3365"),sQuery(id+"F0.wireOp",EDGE,"E3366"),sQuery(id+"F0.wireOp",EDGE,"E3367"),sQuery(id+"F0.wireOp",EDGE,"E3368"),sQuery(id+"F0.wireOp",EDGE,"E3369"),sQuery(id+"F0.wireOp",EDGE,"E3370"),sQuery(id+"F0.wireOp",EDGE,"E3371"),sQuery(id+"F0.wireOp",EDGE,"E3372"),sQuery(id+"F0.wireOp",EDGE,"E3373"),sQuery(id+"F0.wireOp",EDGE,"E3374"),sQuery(id+"F0.wireOp",EDGE,"E3375"),sQuery(id+"F0.wireOp",EDGE,"E3376"),sQuery(id+"F0.wireOp",EDGE,"E3377"),sQuery(id+"F0.wireOp",EDGE,"E3378"),sQuery(id+"F0.wireOp",EDGE,"E3379"),sQuery(id+"F0.wireOp",EDGE,"E3380"),sQuery(id+"F0.wireOp",EDGE,"E3381"),sQuery(id+"F0.wireOp",EDGE,"E3382"),sQuery(id+"F0.wireOp",EDGE,"E3383"),sQuery(id+"F0.wireOp",EDGE,"E3384"),sQuery(id+"F0.wireOp",EDGE,"E3385"),sQuery(id+"F0.wireOp",EDGE,"E3386"),sQuery(id+"F0.wireOp",EDGE,"E3387"),sQuery(id+"F0.wireOp",EDGE,"E3388"),sQuery(id+"F0.wireOp",EDGE,"E3389"),sQuery(id+"F0.wireOp",EDGE,"E3390"),sQuery(id+"F0.wireOp",EDGE,"E3391"),sQuery(id+"F0.wireOp",EDGE,"E3392"),sQuery(id+"F0.wireOp",EDGE,"E3393"),sQuery(id+"F0.wireOp",EDGE,"E3394"),sQuery(id+"F0.wireOp",EDGE,"E3395"),sQuery(id+"F0.wireOp",EDGE,"E3396"),sQuery(id+"F0.wireOp",EDGE,"E3397"),sQuery(id+"F0.wireOp",EDGE,"E3398"),sQuery(id+"F0.wireOp",EDGE,"E3399"),sQuery(id+"F0.wireOp",EDGE,"E3400"),sQuery(id+"F0.wireOp",EDGE,"E3401"),sQuery(id+"F0.wireOp",EDGE,"E3402"),sQuery(id+"F0.wireOp",EDGE,"E3403"),sQuery(id+"F0.wireOp",EDGE,"E3404"),sQuery(id+"F0.wireOp",EDGE,"E3405"),sQuery(id+"F0.wireOp",EDGE,"E3406"),sQuery(id+"F0.wireOp",EDGE,"E3407"),sQuery(id+"F0.wireOp",EDGE,"E3408"),sQuery(id+"F0.wireOp",EDGE,"E3409"),sQuery(id+"F0.wireOp",EDGE,"E3410"),sQuery(id+"F0.wireOp",EDGE,"E3411"),sQuery(id+"F0.wireOp",EDGE,"E3412"),sQuery(id+"F0.wireOp",EDGE,"E3413"),sQuery(id+"F0.wireOp",EDGE,"E3414"),sQuery(id+"F0.wireOp",EDGE,"E3415"),sQuery(id+"F0.wireOp",EDGE,"E3416"),sQuery(id+"F0.wireOp",EDGE,"E3417"),sQuery(id+"F0.wireOp",EDGE,"E3418"),sQuery(id+"F0.wireOp",EDGE,"E3419"),sQuery(id+"F0.wireOp",EDGE,"E3420"),sQuery(id+"F0.wireOp",EDGE,"E3421"),sQuery(id+"F0.wireOp",EDGE,"E3422"),sQuery(id+"F0.wireOp",EDGE,"E3423"),sQuery(id+"F0.wireOp",EDGE,"E3424"),sQuery(id+"F0.wireOp",EDGE,"E3425"),sQuery(id+"F0.wireOp",EDGE,"E3426"),sQuery(id+"F0.wireOp",EDGE,"E3427"),sQuery(id+"F0.wireOp",EDGE,"E3428"),sQuery(id+"F0.wireOp",EDGE,"E3429"),sQuery(id+"F0.wireOp",EDGE,"E3430"),sQuery(id+"F0.wireOp",EDGE,"E3431"),sQuery(id+"F0.wireOp",EDGE,"E3432"),sQuery(id+"F0.wireOp",EDGE,"E3433"),sQuery(id+"F0.wireOp",EDGE,"E3434"),sQuery(id+"F0.wireOp",EDGE,"E3435"),sQuery(id+"F0.wireOp",EDGE,"E3436"),sQuery(id+"F0.wireOp",EDGE,"E3437"),sQuery(id+"F0.wireOp",EDGE,"E3438"),sQuery(id+"F0.wireOp",EDGE,"E3439"),sQuery(id+"F0.wireOp",EDGE,"E3440"),sQuery(id+"F0.wireOp",EDGE,"E3441"),sQuery(id+"F0.wireOp",EDGE,"E3442"),sQuery(id+"F0.wireOp",EDGE,"E3443"),sQuery(id+"F0.wireOp",EDGE,"E3444"),sQuery(id+"F0.wireOp",EDGE,"E3445"),sQuery(id+"F0.wireOp",EDGE,"E3446"),sQuery(id+"F0.wireOp",EDGE,"E3447"),sQuery(id+"F0.wireOp",EDGE,"E3448"),sQuery(id+"F0.wireOp",EDGE,"E3449"),sQuery(id+"F0.wireOp",EDGE,"E3450"),sQuery(id+"F0.wireOp",EDGE,"E3451"),sQuery(id+"F0.wireOp",EDGE,"E3452"),sQuery(id+"F0.wireOp",EDGE,"E3453"),sQuery(id+"F0.wireOp",EDGE,"E3454"),sQuery(id+"F0.wireOp",EDGE,"E3455"),sQuery(id+"F0.wireOp",EDGE,"E3456"),sQuery(id+"F0.wireOp",EDGE,"E3457"),sQuery(id+"F0.wireOp",EDGE,"E3458"),sQuery(id+"F0.wireOp",EDGE,"E3459"),sQuery(id+"F0.wireOp",EDGE,"E3460"),sQuery(id+"F0.wireOp",EDGE,"E3461"),sQuery(id+"F0.wireOp",EDGE,"E3462"),sQuery(id+"F0.wireOp",EDGE,"E3463"),sQuery(id+"F0.wireOp",EDGE,"E3464"),sQuery(id+"F0.wireOp",EDGE,"E3465"),sQuery(id+"F0.wireOp",EDGE,"E3466"),sQuery(id+"F0.wireOp",EDGE,"E3467"),sQuery(id+"F0.wireOp",EDGE,"E3468"),sQuery(id+"F0.wireOp",EDGE,"E3469"),sQuery(id+"F0.wireOp",EDGE,"E3470"),sQuery(id+"F0.wireOp",EDGE,"E3471"),sQuery(id+"F0.wireOp",EDGE,"E3472"),sQuery(id+"F0.wireOp",EDGE,"E3473"),sQuery(id+"F0.wireOp",EDGE,"E3474"),sQuery(id+"F0.wireOp",EDGE,"E3475"),sQuery(id+"F0.wireOp",EDGE,"E3476"),sQuery(id+"F0.wireOp",EDGE,"E3477"),sQuery(id+"F0.wireOp",EDGE,"E3478"),sQuery(id+"F0.wireOp",EDGE,"E3479"),sQuery(id+"F0.wireOp",EDGE,"E3480"),sQuery(id+"F0.wireOp",EDGE,"E3481"),sQuery(id+"F0.wireOp",EDGE,"E3482"),sQuery(id+"F0.wireOp",EDGE,"E3483"),sQuery(id+"F0.wireOp",EDGE,"E3484"),sQuery(id+"F0.wireOp",EDGE,"E3485"),sQuery(id+"F0.wireOp",EDGE,"E3486"),sQuery(id+"F0.wireOp",EDGE,"E3487"),sQuery(id+"F0.wireOp",EDGE,"E3488"),sQuery(id+"F0.wireOp",EDGE,"E3489"),sQuery(id+"F0.wireOp",EDGE,"E3490"),sQuery(id+"F0.wireOp",EDGE,"E3491"),sQuery(id+"F0.wireOp",EDGE,"E3492"),sQuery(id+"F0.wireOp",EDGE,"E3493"),sQuery(id+"F0.wireOp",EDGE,"E3494"),sQuery(id+"F0.wireOp",EDGE,"E3495"),sQuery(id+"F0.wireOp",EDGE,"E3496"),sQuery(id+"F0.wireOp",EDGE,"E3497"),sQuery(id+"F0.wireOp",EDGE,"E3498"),sQuery(id+"F0.wireOp",EDGE,"E3499"),sQuery(id+"F0.wireOp",EDGE,"E3500"),sQuery(id+"F0.wireOp",EDGE,"E3501"),sQuery(id+"F0.wireOp",EDGE,"E3502"),sQuery(id+"F0.wireOp",EDGE,"E3503"),sQuery(id+"F0.wireOp",EDGE,"E3504"),sQuery(id+"F0.wireOp",EDGE,"E3505"),sQuery(id+"F0.wireOp",EDGE,"E3506"),sQuery(id+"F0.wireOp",EDGE,"E3507"),sQuery(id+"F0.wireOp",EDGE,"E3508"),sQuery(id+"F0.wireOp",EDGE,"E3509"),sQuery(id+"F0.wireOp",EDGE,"E3510"),sQuery(id+"F0.wireOp",EDGE,"E3511"),sQuery(id+"F0.wireOp",EDGE,"E3512"),sQuery(id+"F0.wireOp",EDGE,"E3513"),sQuery(id+"F0.wireOp",EDGE,"E3514"),sQuery(id+"F0.wireOp",EDGE,"E3515"),sQuery(id+"F0.wireOp",EDGE,"E3516"),sQuery(id+"F0.wireOp",EDGE,"E3517"),sQuery(id+"F0.wireOp",EDGE,"E3518"),sQuery(id+"F0.wireOp",EDGE,"E3519"),sQuery(id+"F0.wireOp",EDGE,"E3520"),sQuery(id+"F0.wireOp",EDGE,"E3521"),sQuery(id+"F0.wireOp",EDGE,"E3522"),sQuery(id+"F0.wireOp",EDGE,"E3523"),sQuery(id+"F0.wireOp",EDGE,"E3524"),sQuery(id+"F0.wireOp",EDGE,"E3525"),sQuery(id+"F0.wireOp",EDGE,"E3526"),sQuery(id+"F0.wireOp",EDGE,"E3527"),sQuery(id+"F0.wireOp",EDGE,"E3528"),sQuery(id+"F0.wireOp",EDGE,"E3529"),sQuery(id+"F0.wireOp",EDGE,"E3530"),sQuery(id+"F0.wireOp",EDGE,"E3531"),sQuery(id+"F0.wireOp",EDGE,"E3532"),sQuery(id+"F0.wireOp",EDGE,"E3533"),sQuery(id+"F0.wireOp",EDGE,"E3534"),sQuery(id+"F0.wireOp",EDGE,"E3535"),sQuery(id+"F0.wireOp",EDGE,"E3536"),sQuery(id+"F0.wireOp",EDGE,"E3537"),sQuery(id+"F0.wireOp",EDGE,"E3538"),sQuery(id+"F0.wireOp",EDGE,"E3539"),sQuery(id+"F0.wireOp",EDGE,"E3540"),sQuery(id+"F0.wireOp",EDGE,"E3541"),sQuery(id+"F0.wireOp",EDGE,"E3542"),sQuery(id+"F0.wireOp",EDGE,"E3543"),sQuery(id+"F0.wireOp",EDGE,"E3544"),sQuery(id+"F0.wireOp",EDGE,"E3545"),sQuery(id+"F0.wireOp",EDGE,"E3546"),sQuery(id+"F0.wireOp",EDGE,"E3547"),sQuery(id+"F0.wireOp",EDGE,"E3548"),sQuery(id+"F0.wireOp",EDGE,"E3549"),sQuery(id+"F0.wireOp",EDGE,"E3550"),sQuery(id+"F0.wireOp",EDGE,"E3551"),sQuery(id+"F0.wireOp",EDGE,"E3552"),sQuery(id+"F0.wireOp",EDGE,"E3553"),sQuery(id+"F0.wireOp",EDGE,"E3554"),sQuery(id+"F0.wireOp",EDGE,"E3555"),sQuery(id+"F0.wireOp",EDGE,"E3556"),sQuery(id+"F0.wireOp",EDGE,"E3557"),sQuery(id+"F0.wireOp",EDGE,"E3558"),sQuery(id+"F0.wireOp",EDGE,"E3559"),sQuery(id+"F0.wireOp",EDGE,"E3560"),sQuery(id+"F0.wireOp",EDGE,"E3561"),sQuery(id+"F0.wireOp",EDGE,"E3562"),sQuery(id+"F0.wireOp",EDGE,"E3563"),sQuery(id+"F0.wireOp",EDGE,"E3564"),sQuery(id+"F0.wireOp",EDGE,"E3565"),sQuery(id+"F0.wireOp",EDGE,"E3566"),sQuery(id+"F0.wireOp",EDGE,"E3567"),sQuery(id+"F0.wireOp",EDGE,"E3568"),sQuery(id+"F0.wireOp",EDGE,"E3569"),sQuery(id+"F0.wireOp",EDGE,"E3570"),sQuery(id+"F0.wireOp",EDGE,"E3571"),sQuery(id+"F0.wireOp",EDGE,"E3572"),sQuery(id+"F0.wireOp",EDGE,"E3573"),sQuery(id+"F0.wireOp",EDGE,"E3574"),sQuery(id+"F0.wireOp",EDGE,"E3575"),sQuery(id+"F0.wireOp",EDGE,"E3576"),sQuery(id+"F0.wireOp",EDGE,"E3577"),sQuery(id+"F0.wireOp",EDGE,"E3578"),sQuery(id+"F0.wireOp",EDGE,"E3579"),sQuery(id+"F0.wireOp",EDGE,"E3580"),sQuery(id+"F0.wireOp",EDGE,"E3581"),sQuery(id+"F0.wireOp",EDGE,"E3582"),sQuery(id+"F0.wireOp",EDGE,"E3583"),sQuery(id+"F0.wireOp",EDGE,"E3584"),sQuery(id+"F0.wireOp",EDGE,"E3585"),sQuery(id+"F0.wireOp",EDGE,"E3586"),sQuery(id+"F0.wireOp",EDGE,"E3587"),sQuery(id+"F0.wireOp",EDGE,"E3588"),sQuery(id+"F0.wireOp",EDGE,"E3589"),sQuery(id+"F0.wireOp",EDGE,"E3590"),sQuery(id+"F0.wireOp",EDGE,"E3591"),sQuery(id+"F0.wireOp",EDGE,"E3592"),sQuery(id+"F0.wireOp",EDGE,"E3593"),sQuery(id+"F0.wireOp",EDGE,"E3594"),sQuery(id+"F0.wireOp",EDGE,"E3595"),sQuery(id+"F0.wireOp",EDGE,"E3596"),sQuery(id+"F0.wireOp",EDGE,"E3597"),sQuery(id+"F0.wireOp",EDGE,"E3598"),sQuery(id+"F0.wireOp",EDGE,"E3599"),sQuery(id+"F0.wireOp",EDGE,"E3600"),sQuery(id+"F0.wireOp",EDGE,"E3601"),sQuery(id+"F0.wireOp",EDGE,"E3602"),sQuery(id+"F0.wireOp",EDGE,"E3603"),sQuery(id+"F0.wireOp",EDGE,"E3604"),sQuery(id+"F0.wireOp",EDGE,"E3605"),sQuery(id+"F0.wireOp",EDGE,"E3606"),sQuery(id+"F0.wireOp",EDGE,"E3607"),sQuery(id+"F0.wireOp",EDGE,"E3608"),sQuery(id+"F0.wireOp",EDGE,"E3609"),sQuery(id+"F0.wireOp",EDGE,"E3610"),sQuery(id+"F0.wireOp",EDGE,"E3611"),sQuery(id+"F0.wireOp",EDGE,"E3612"),sQuery(id+"F0.wireOp",EDGE,"E3613"),sQuery(id+"F0.wireOp",EDGE,"E3614"),sQuery(id+"F0.wireOp",EDGE,"E3615"),sQuery(id+"F0.wireOp",EDGE,"E3616"),sQuery(id+"F0.wireOp",EDGE,"E3617"),sQuery(id+"F0.wireOp",EDGE,"E3618"),sQuery(id+"F0.wireOp",EDGE,"E3619"),sQuery(id+"F0.wireOp",EDGE,"E3620"),sQuery(id+"F0.wireOp",EDGE,"E3621"),sQuery(id+"F0.wireOp",EDGE,"E3622"),sQuery(id+"F0.wireOp",EDGE,"E3623"),sQuery(id+"F0.wireOp",EDGE,"E3624"),sQuery(id+"F0.wireOp",EDGE,"E3625"),sQuery(id+"F0.wireOp",EDGE,"E3626"),sQuery(id+"F0.wireOp",EDGE,"E3627"),sQuery(id+"F0.wireOp",EDGE,"E3628"),sQuery(id+"F0.wireOp",EDGE,"E3629"),sQuery(id+"F0.wireOp",EDGE,"E3630"),sQuery(id+"F0.wireOp",EDGE,"E3631"),sQuery(id+"F0.wireOp",EDGE,"E3632"),sQuery(id+"F0.wireOp",EDGE,"E3633"),sQuery(id+"F0.wireOp",EDGE,"E3634"),sQuery(id+"F0.wireOp",EDGE,"E3635"),sQuery(id+"F0.wireOp",EDGE,"E3636"),sQuery(id+"F0.wireOp",EDGE,"E3637"),sQuery(id+"F0.wireOp",EDGE,"E3638"),sQuery(id+"F0.wireOp",EDGE,"E3639"),sQuery(id+"F0.wireOp",EDGE,"E3640"),sQuery(id+"F0.wireOp",EDGE,"E3641"),sQuery(id+"F0.wireOp",EDGE,"E3642"),sQuery(id+"F0.wireOp",EDGE,"E3643"),sQuery(id+"F0.wireOp",EDGE,"E3644"),sQuery(id+"F0.wireOp",EDGE,"E3645"),sQuery(id+"F0.wireOp",EDGE,"E3646"),sQuery(id+"F0.wireOp",EDGE,"E3647"),sQuery(id+"F0.wireOp",EDGE,"E3648"),sQuery(id+"F0.wireOp",EDGE,"E3649"),sQuery(id+"F0.wireOp",EDGE,"E3650"),sQuery(id+"F0.wireOp",EDGE,"E3651"),sQuery(id+"F0.wireOp",EDGE,"E3652"),sQuery(id+"F0.wireOp",EDGE,"E3653"),sQuery(id+"F0.wireOp",EDGE,"E3654"),sQuery(id+"F0.wireOp",EDGE,"E3655"),sQuery(id+"F0.wireOp",EDGE,"E3656"),sQuery(id+"F0.wireOp",EDGE,"E3657"),sQuery(id+"F0.wireOp",EDGE,"E3658"),sQuery(id+"F0.wireOp",EDGE,"E3659"),sQuery(id+"F0.wireOp",EDGE,"E3660"),sQuery(id+"F0.wireOp",EDGE,"E3661"),sQuery(id+"F0.wireOp",EDGE,"E3662"),sQuery(id+"F0.wireOp",EDGE,"E3663"),sQuery(id+"F0.wireOp",EDGE,"E3664"),sQuery(id+"F0.wireOp",EDGE,"E3665"),sQuery(id+"F0.wireOp",EDGE,"E3666"),sQuery(id+"F0.wireOp",EDGE,"E3667"),sQuery(id+"F0.wireOp",EDGE,"E3668"),sQuery(id+"F0.wireOp",EDGE,"E3669"),sQuery(id+"F0.wireOp",EDGE,"E3670"),sQuery(id+"F0.wireOp",EDGE,"E3671"),sQuery(id+"F0.wireOp",EDGE,"E3672"),sQuery(id+"F0.wireOp",EDGE,"E3673"),sQuery(id+"F0.wireOp",EDGE,"E3674"),sQuery(id+"F0.wireOp",EDGE,"E3675"),sQuery(id+"F0.wireOp",EDGE,"E3676"),sQuery(id+"F0.wireOp",EDGE,"E3677"),sQuery(id+"F0.wireOp",EDGE,"E3678"),sQuery(id+"F0.wireOp",EDGE,"E3679"),sQuery(id+"F0.wireOp",EDGE,"E3680"),sQuery(id+"F0.wireOp",EDGE,"E3681"),sQuery(id+"F0.wireOp",EDGE,"E3682"),sQuery(id+"F0.wireOp",EDGE,"E3683"),sQuery(id+"F0.wireOp",EDGE,"E3684"),sQuery(id+"F0.wireOp",EDGE,"E3685"),sQuery(id+"F0.wireOp",EDGE,"E3686"),sQuery(id+"F0.wireOp",EDGE,"E3687"),sQuery(id+"F0.wireOp",EDGE,"E3688"),sQuery(id+"F0.wireOp",EDGE,"E3689"),sQuery(id+"F0.wireOp",EDGE,"E3690"),sQuery(id+"F0.wireOp",EDGE,"E3691"),sQuery(id+"F0.wireOp",EDGE,"E3692"),sQuery(id+"F0.wireOp",EDGE,"E3693"),sQuery(id+"F0.wireOp",EDGE,"E3694"),sQuery(id+"F0.wireOp",EDGE,"E3695"),sQuery(id+"F0.wireOp",EDGE,"E3696"),sQuery(id+"F0.wireOp",EDGE,"E3697"),sQuery(id+"F0.wireOp",EDGE,"E3698"),sQuery(id+"F0.wireOp",EDGE,"E3699"),sQuery(id+"F0.wireOp",EDGE,"E3700"),sQuery(id+"F0.wireOp",EDGE,"E3701"),sQuery(id+"F0.wireOp",EDGE,"E3702"),sQuery(id+"F0.wireOp",EDGE,"E3703"),sQuery(id+"F0.wireOp",EDGE,"E3704"),sQuery(id+"F0.wireOp",EDGE,"E3705"),sQuery(id+"F0.wireOp",EDGE,"E3706"),sQuery(id+"F0.wireOp",EDGE,"E3707"),sQuery(id+"F0.wireOp",EDGE,"E3708"),sQuery(id+"F0.wireOp",EDGE,"E3709"),sQuery(id+"F0.wireOp",EDGE,"E3710"),sQuery(id+"F0.wireOp",EDGE,"E3711"),sQuery(id+"F0.wireOp",EDGE,"E3712"),sQuery(id+"F0.wireOp",EDGE,"E3713"),sQuery(id+"F0.wireOp",EDGE,"E3714"),sQuery(id+"F0.wireOp",EDGE,"E3715"),sQuery(id+"F0.wireOp",EDGE,"E3716"),sQuery(id+"F0.wireOp",EDGE,"E3717"),sQuery(id+"F0.wireOp",EDGE,"E3718"),sQuery(id+"F0.wireOp",EDGE,"E3719"),sQuery(id+"F0.wireOp",EDGE,"E3720"),sQuery(id+"F0.wireOp",EDGE,"E3721"),sQuery(id+"F0.wireOp",EDGE,"E3722"),sQuery(id+"F0.wireOp",EDGE,"E3723"),sQuery(id+"F0.wireOp",EDGE,"E3724"),sQuery(id+"F0.wireOp",EDGE,"E3725"),sQuery(id+"F0.wireOp",EDGE,"E3726"),sQuery(id+"F0.wireOp",EDGE,"E3727"),sQuery(id+"F0.wireOp",EDGE,"E3728"),sQuery(id+"F0.wireOp",EDGE,"E3729"),sQuery(id+"F0.wireOp",EDGE,"E3730"),sQuery(id+"F0.wireOp",EDGE,"E3731"),sQuery(id+"F0.wireOp",EDGE,"E3732"),sQuery(id+"F0.wireOp",EDGE,"E3733"),sQuery(id+"F0.wireOp",EDGE,"E3734"),sQuery(id+"F0.wireOp",EDGE,"E3735"),sQuery(id+"F0.wireOp",EDGE,"E3736"),sQuery(id+"F0.wireOp",EDGE,"E3737"),sQuery(id+"F0.wireOp",EDGE,"E3738"),sQuery(id+"F0.wireOp",EDGE,"E3739"),sQuery(id+"F0.wireOp",EDGE,"E3740"),sQuery(id+"F0.wireOp",EDGE,"E3741"),sQuery(id+"F0.wireOp",EDGE,"E3742"),sQuery(id+"F0.wireOp",EDGE,"E3743"),sQuery(id+"F0.wireOp",EDGE,"E3744"),sQuery(id+"F0.wireOp",EDGE,"E3745"),sQuery(id+"F0.wireOp",EDGE,"E3746"),sQuery(id+"F0.wireOp",EDGE,"E3747"),sQuery(id+"F0.wireOp",EDGE,"E3748"),sQuery(id+"F0.wireOp",EDGE,"E3749"),sQuery(id+"F0.wireOp",EDGE,"E3750"),sQuery(id+"F0.wireOp",EDGE,"E3751"),sQuery(id+"F0.wireOp",EDGE,"E3752"),sQuery(id+"F0.wireOp",EDGE,"E3753"),sQuery(id+"F0.wireOp",EDGE,"E3754"),sQuery(id+"F0.wireOp",EDGE,"E3755"),sQuery(id+"F0.wireOp",EDGE,"E3756"),sQuery(id+"F0.wireOp",EDGE,"E3757"),sQuery(id+"F0.wireOp",EDGE,"E3758"),sQuery(id+"F0.wireOp",EDGE,"E3759"),sQuery(id+"F0.wireOp",EDGE,"E3760"),sQuery(id+"F0.wireOp",EDGE,"E3761"),sQuery(id+"F0.wireOp",EDGE,"E3762"),sQuery(id+"F0.wireOp",EDGE,"E3763"),sQuery(id+"F0.wireOp",EDGE,"E3764"),sQuery(id+"F0.wireOp",EDGE,"E3765"),sQuery(id+"F0.wireOp",EDGE,"E3766"),sQuery(id+"F0.wireOp",EDGE,"E3767"),sQuery(id+"F0.wireOp",EDGE,"E3768"),sQuery(id+"F0.wireOp",EDGE,"E3769"),sQuery(id+"F0.wireOp",EDGE,"E3770"),sQuery(id+"F0.wireOp",EDGE,"E3771"),sQuery(id+"F0.wireOp",EDGE,"E3772"),sQuery(id+"F0.wireOp",EDGE,"E3773"),sQuery(id+"F0.wireOp",EDGE,"E3774"),sQuery(id+"F0.wireOp",EDGE,"E3775"),sQuery(id+"F0.wireOp",EDGE,"E3776"),sQuery(id+"F0.wireOp",EDGE,"E3777"),sQuery(id+"F0.wireOp",EDGE,"E3778"),sQuery(id+"F0.wireOp",EDGE,"E3779"),sQuery(id+"F0.wireOp",EDGE,"E3780"),sQuery(id+"F0.wireOp",EDGE,"E3781"),sQuery(id+"F0.wireOp",EDGE,"E3782"),sQuery(id+"F0.wireOp",EDGE,"E3783"),sQuery(id+"F0.wireOp",EDGE,"E3784"),sQuery(id+"F0.wireOp",EDGE,"E3785"),sQuery(id+"F0.wireOp",EDGE,"E3786"),sQuery(id+"F0.wireOp",EDGE,"E3787"),sQuery(id+"F0.wireOp",EDGE,"E3788"),sQuery(id+"F0.wireOp",EDGE,"E3789"),sQuery(id+"F0.wireOp",EDGE,"E3790"),sQuery(id+"F0.wireOp",EDGE,"E3791"),sQuery(id+"F0.wireOp",EDGE,"E3792"),sQuery(id+"F0.wireOp",EDGE,"E3793"),sQuery(id+"F0.wireOp",EDGE,"E3794"),sQuery(id+"F0.wireOp",EDGE,"E3795"),sQuery(id+"F0.wireOp",EDGE,"E3796"),sQuery(id+"F0.wireOp",EDGE,"E3797"),sQuery(id+"F0.wireOp",EDGE,"E3798"),sQuery(id+"F0.wireOp",EDGE,"E3799"),sQuery(id+"F0.wireOp",EDGE,"E3800"),sQuery(id+"F0.wireOp",EDGE,"E3801"),sQuery(id+"F0.wireOp",EDGE,"E3802"),sQuery(id+"F0.wireOp",EDGE,"E3803"),sQuery(id+"F0.wireOp",EDGE,"E3804"),sQuery(id+"F0.wireOp",EDGE,"E3805"),sQuery(id+"F0.wireOp",EDGE,"E3806"),sQuery(id+"F0.wireOp",EDGE,"E3807"),sQuery(id+"F0.wireOp",EDGE,"E3808"),sQuery(id+"F0.wireOp",EDGE,"E3809"),sQuery(id+"F0.wireOp",EDGE,"E3810"),sQuery(id+"F0.wireOp",EDGE,"E3811"),sQuery(id+"F0.wireOp",EDGE,"E3812"),sQuery(id+"F0.wireOp",EDGE,"E3813"),sQuery(id+"F0.wireOp",EDGE,"E3814"),sQuery(id+"F0.wireOp",EDGE,"E3815"),sQuery(id+"F0.wireOp",EDGE,"E3816"),sQuery(id+"F0.wireOp",EDGE,"E3817"),sQuery(id+"F0.wireOp",EDGE,"E3818"),sQuery(id+"F0.wireOp",EDGE,"E3819"),sQuery(id+"F0.wireOp",EDGE,"E3820"),sQuery(id+"F0.wireOp",EDGE,"E3821"),sQuery(id+"F0.wireOp",EDGE,"E3822"),sQuery(id+"F0.wireOp",EDGE,"E3823"),sQuery(id+"F0.wireOp",EDGE,"E3824"),sQuery(id+"F0.wireOp",EDGE,"E3825"),sQuery(id+"F0.wireOp",EDGE,"E3826"),sQuery(id+"F0.wireOp",EDGE,"E3827"),sQuery(id+"F0.wireOp",EDGE,"E3828"),sQuery(id+"F0.wireOp",EDGE,"E3829"),sQuery(id+"F0.wireOp",EDGE,"E3830"),sQuery(id+"F0.wireOp",EDGE,"E3831"),sQuery(id+"F0.wireOp",EDGE,"E3832"),sQuery(id+"F0.wireOp",EDGE,"E3833"),sQuery(id+"F0.wireOp",EDGE,"E3834"),sQuery(id+"F0.wireOp",EDGE,"E3835"),sQuery(id+"F0.wireOp",EDGE,"E3836"),sQuery(id+"F0.wireOp",EDGE,"E3837"),sQuery(id+"F0.wireOp",EDGE,"E3838"),sQuery(id+"F0.wireOp",EDGE,"E3839"),sQuery(id+"F0.wireOp",EDGE,"E3840"),sQuery(id+"F0.wireOp",EDGE,"E3841"),sQuery(id+"F0.wireOp",EDGE,"E3842"),sQuery(id+"F0.wireOp",EDGE,"E3843"),sQuery(id+"F0.wireOp",EDGE,"E3844"),sQuery(id+"F0.wireOp",EDGE,"E3845"),sQuery(id+"F0.wireOp",EDGE,"E3846"),sQuery(id+"F0.wireOp",EDGE,"E3847"),sQuery(id+"F0.wireOp",EDGE,"E3848"),sQuery(id+"F0.wireOp",EDGE,"E3849"),sQuery(id+"F0.wireOp",EDGE,"E3850"),sQuery(id+"F0.wireOp",EDGE,"E3851"),sQuery(id+"F0.wireOp",EDGE,"E3852"),sQuery(id+"F0.wireOp",EDGE,"E3853"),sQuery(id+"F0.wireOp",EDGE,"E3854"),sQuery(id+"F0.wireOp",EDGE,"E3855"),sQuery(id+"F0.wireOp",EDGE,"E3856"),sQuery(id+"F0.wireOp",EDGE,"E3857"),sQuery(id+"F0.wireOp",EDGE,"E3858"),sQuery(id+"F0.wireOp",EDGE,"E3859"),sQuery(id+"F0.wireOp",EDGE,"E3860"),sQuery(id+"F0.wireOp",EDGE,"E3861"),sQuery(id+"F0.wireOp",EDGE,"E3862"),sQuery(id+"F0.wireOp",EDGE,"E3863"),sQuery(id+"F0.wireOp",EDGE,"E3864"),sQuery(id+"F0.wireOp",EDGE,"E3865"),sQuery(id+"F0.wireOp",EDGE,"E3866"),sQuery(id+"F0.wireOp",EDGE,"E3867"),sQuery(id+"F0.wireOp",EDGE,"E3868"),sQuery(id+"F0.wireOp",EDGE,"E3869"),sQuery(id+"F0.wireOp",EDGE,"E3870"),sQuery(id+"F0.wireOp",EDGE,"E3871"),sQuery(id+"F0.wireOp",EDGE,"E3872"),sQuery(id+"F0.wireOp",EDGE,"E3873"),sQuery(id+"F0.wireOp",EDGE,"E3874"),sQuery(id+"F0.wireOp",EDGE,"E3875"),sQuery(id+"F0.wireOp",EDGE,"E3876"),sQuery(id+"F0.wireOp",EDGE,"E3877"),sQuery(id+"F0.wireOp",EDGE,"E3878"),sQuery(id+"F0.wireOp",EDGE,"E3879"),sQuery(id+"F0.wireOp",EDGE,"E3880"),sQuery(id+"F0.wireOp",EDGE,"E3881"),sQuery(id+"F0.wireOp",EDGE,"E3882"),sQuery(id+"F0.wireOp",EDGE,"E3883"),sQuery(id+"F0.wireOp",EDGE,"E3884"),sQuery(id+"F0.wireOp",EDGE,"E3885"),sQuery(id+"F0.wireOp",EDGE,"E3886"),sQuery(id+"F0.wireOp",EDGE,"E3887"),sQuery(id+"F0.wireOp",EDGE,"E3888"),sQuery(id+"F0.wireOp",EDGE,"E3889"),sQuery(id+"F0.wireOp",EDGE,"E3890"),sQuery(id+"F0.wireOp",EDGE,"E3891"),sQuery(id+"F0.wireOp",EDGE,"E3892"),sQuery(id+"F0.wireOp",EDGE,"E3893"),sQuery(id+"F0.wireOp",EDGE,"E3894"),sQuery(id+"F0.wireOp",EDGE,"E3895"),sQuery(id+"F0.wireOp",EDGE,"E3896"),sQuery(id+"F0.wireOp",EDGE,"E3897"),sQuery(id+"F0.wireOp",EDGE,"E3898"),sQuery(id+"F0.wireOp",EDGE,"E3899"),sQuery(id+"F0.wireOp",EDGE,"E3900"),sQuery(id+"F0.wireOp",EDGE,"E3901"),sQuery(id+"F0.wireOp",EDGE,"E3902"),sQuery(id+"F0.wireOp",EDGE,"E3903"),sQuery(id+"F0.wireOp",EDGE,"E3904"),sQuery(id+"F0.wireOp",EDGE,"E3905"),sQuery(id+"F0.wireOp",EDGE,"E3906"),sQuery(id+"F0.wireOp",EDGE,"E3907"),sQuery(id+"F0.wireOp",EDGE,"E3908"),sQuery(id+"F0.wireOp",EDGE,"E3909"),sQuery(id+"F0.wireOp",EDGE,"E3910"),sQuery(id+"F0.wireOp",EDGE,"E3911"),sQuery(id+"F0.wireOp",EDGE,"E3912"),sQuery(id+"F0.wireOp",EDGE,"E3913"),sQuery(id+"F0.wireOp",EDGE,"E3914"),sQuery(id+"F0.wireOp",EDGE,"E3915"),sQuery(id+"F0.wireOp",EDGE,"E3916"),sQuery(id+"F0.wireOp",EDGE,"E3917"),sQuery(id+"F0.wireOp",EDGE,"E3918"),sQuery(id+"F0.wireOp",EDGE,"E3919"),sQuery(id+"F0.wireOp",EDGE,"E3920"),sQuery(id+"F0.wireOp",EDGE,"E3921"),sQuery(id+"F0.wireOp",EDGE,"E3922"),sQuery(id+"F0.wireOp",EDGE,"E3923"),sQuery(id+"F0.wireOp",EDGE,"E3924"),sQuery(id+"F0.wireOp",EDGE,"E3925"),sQuery(id+"F0.wireOp",EDGE,"E3926"),sQuery(id+"F0.wireOp",EDGE,"E3927"),sQuery(id+"F0.wireOp",EDGE,"E3928"),sQuery(id+"F0.wireOp",EDGE,"E3929"),sQuery(id+"F0.wireOp",EDGE,"E3930"),sQuery(id+"F0.wireOp",EDGE,"E3931"),sQuery(id+"F0.wireOp",EDGE,"E3932"),sQuery(id+"F0.wireOp",EDGE,"E3933"),sQuery(id+"F0.wireOp",EDGE,"E3934"),sQuery(id+"F0.wireOp",EDGE,"E3935"),sQuery(id+"F0.wireOp",EDGE,"E3936"),sQuery(id+"F0.wireOp",EDGE,"E3937"),sQuery(id+"F0.wireOp",EDGE,"E3938"),sQuery(id+"F0.wireOp",EDGE,"E3939"),sQuery(id+"F0.wireOp",EDGE,"E3940"),sQuery(id+"F0.wireOp",EDGE,"E3941"),sQuery(id+"F0.wireOp",EDGE,"E3942"),sQuery(id+"F0.wireOp",EDGE,"E3943"),sQuery(id+"F0.wireOp",EDGE,"E3944"),sQuery(id+"F0.wireOp",EDGE,"E3945"),sQuery(id+"F0.wireOp",EDGE,"E3946"),sQuery(id+"F0.wireOp",EDGE,"E3947"),sQuery(id+"F0.wireOp",EDGE,"E3948"),sQuery(id+"F0.wireOp",EDGE,"E3949"),sQuery(id+"F0.wireOp",EDGE,"E3950"),sQuery(id+"F0.wireOp",EDGE,"E3951"),sQuery(id+"F0.wireOp",EDGE,"E3952"),sQuery(id+"F0.wireOp",EDGE,"E3953"),sQuery(id+"F0.wireOp",EDGE,"E3954"),sQuery(id+"F0.wireOp",EDGE,"E3955"),sQuery(id+"F0.wireOp",EDGE,"E3956"),sQuery(id+"F0.wireOp",EDGE,"E3957"),sQuery(id+"F0.wireOp",EDGE,"E3958"),sQuery(id+"F0.wireOp",EDGE,"E3959"),sQuery(id+"F0.wireOp",EDGE,"E3960"),sQuery(id+"F0.wireOp",EDGE,"E3961"),sQuery(id+"F0.wireOp",EDGE,"E3962"),sQuery(id+"F0.wireOp",EDGE,"E3963"),sQuery(id+"F0.wireOp",EDGE,"E3964"),sQuery(id+"F0.wireOp",EDGE,"E3965"),sQuery(id+"F0.wireOp",EDGE,"E3966"),sQuery(id+"F0.wireOp",EDGE,"E3967"),sQuery(id+"F0.wireOp",EDGE,"E3968"),sQuery(id+"F0.wireOp",EDGE,"E3969"),sQuery(id+"F0.wireOp",EDGE,"E3970"),sQuery(id+"F0.wireOp",EDGE,"E3971"),sQuery(id+"F0.wireOp",EDGE,"E3972"),sQuery(id+"F0.wireOp",EDGE,"E3973"),sQuery(id+"F0.wireOp",EDGE,"E3974"),sQuery(id+"F0.wireOp",EDGE,"E3975"),sQuery(id+"F0.wireOp",EDGE,"E3976"),sQuery(id+"F0.wireOp",EDGE,"E3977"),sQuery(id+"F0.wireOp",EDGE,"E3978"),sQuery(id+"F0.wireOp",EDGE,"E3979"),sQuery(id+"F0.wireOp",EDGE,"E3980"),sQuery(id+"F0.wireOp",EDGE,"E3981"),sQuery(id+"F0.wireOp",EDGE,"E3982"),sQuery(id+"F0.wireOp",EDGE,"E3983"),sQuery(id+"F0.wireOp",EDGE,"E3984"),sQuery(id+"F0.wireOp",EDGE,"E3985"),sQuery(id+"F0.wireOp",EDGE,"E3986"),sQuery(id+"F0.wireOp",EDGE,"E3987"),sQuery(id+"F0.wireOp",EDGE,"E3988"),sQuery(id+"F0.wireOp",EDGE,"E3989"),sQuery(id+"F0.wireOp",EDGE,"E3990"),sQuery(id+"F0.wireOp",EDGE,"E3991"),sQuery(id+"F0.wireOp",EDGE,"E3992"),sQuery(id+"F0.wireOp",EDGE,"E3993"),sQuery(id+"F0.wireOp",EDGE,"E3994"),sQuery(id+"F0.wireOp",EDGE,"E3995"),sQuery(id+"F0.wireOp",EDGE,"E3996"),sQuery(id+"F0.wireOp",EDGE,"E3997"),sQuery(id+"F0.wireOp",EDGE,"E3998"),sQuery(id+"F0.wireOp",EDGE,"E3999"),sQuery(id+"F0.wireOp",EDGE,"E4000"),sQuery(id+"F0.wireOp",EDGE,"E4001"),sQuery(id+"F0.wireOp",EDGE,"E4002"),sQuery(id+"F0.wireOp",EDGE,"E4003"),sQuery(id+"F0.wireOp",EDGE,"E4004"),sQuery(id+"F0.wireOp",EDGE,"E4005"),sQuery(id+"F0.wireOp",EDGE,"E4006"),sQuery(id+"F0.wireOp",EDGE,"E4007"),sQuery(id+"F0.wireOp",EDGE,"E4008"),sQuery(id+"F0.wireOp",EDGE,"E4009"),sQuery(id+"F0.wireOp",EDGE,"E4010"),sQuery(id+"F0.wireOp",EDGE,"E4011"),sQuery(id+"F0.wireOp",EDGE,"E4012"),sQuery(id+"F0.wireOp",EDGE,"E4013"),sQuery(id+"F0.wireOp",EDGE,"E4014"),sQuery(id+"F0.wireOp",EDGE,"E4015"),sQuery(id+"F0.wireOp",EDGE,"E4016"),sQuery(id+"F0.wireOp",EDGE,"E4017"),sQuery(id+"F0.wireOp",EDGE,"E4018"),sQuery(id+"F0.wireOp",EDGE,"E4019"),sQuery(id+"F0.wireOp",EDGE,"E4020"),sQuery(id+"F0.wireOp",EDGE,"E4021"),sQuery(id+"F0.wireOp",EDGE,"E4022"),sQuery(id+"F0.wireOp",EDGE,"E4023"),sQuery(id+"F0.wireOp",EDGE,"E4024"),sQuery(id+"F0.wireOp",EDGE,"E4025"),sQuery(id+"F0.wireOp",EDGE,"E4026"),sQuery(id+"F0.wireOp",EDGE,"E4027"),sQuery(id+"F0.wireOp",EDGE,"E4028"),sQuery(id+"F0.wireOp",EDGE,"E4029"),sQuery(id+"F0.wireOp",EDGE,"E4030"),sQuery(id+"F0.wireOp",EDGE,"E4031"),sQuery(id+"F0.wireOp",EDGE,"E4032"),sQuery(id+"F0.wireOp",EDGE,"E4033"),sQuery(id+"F0.wireOp",EDGE,"E4034"),sQuery(id+"F0.wireOp",EDGE,"E4035"),sQuery(id+"F0.wireOp",EDGE,"E4036"),sQuery(id+"F0.wireOp",EDGE,"E4037"),sQuery(id+"F0.wireOp",EDGE,"E4038"),sQuery(id+"F0.wireOp",EDGE,"E4039"),sQuery(id+"F0.wireOp",EDGE,"E4040"),sQuery(id+"F0.wireOp",EDGE,"E4041"),sQuery(id+"F0.wireOp",EDGE,"E4042"),sQuery(id+"F0.wireOp",EDGE,"E4043"),sQuery(id+"F0.wireOp",EDGE,"E4044"),sQuery(id+"F0.wireOp",EDGE,"E4045"),sQuery(id+"F0.wireOp",EDGE,"E4046"),sQuery(id+"F0.wireOp",EDGE,"E4047"),sQuery(id+"F0.wireOp",EDGE,"E4048"),sQuery(id+"F0.wireOp",EDGE,"E4049"),sQuery(id+"F0.wireOp",EDGE,"E4050"),sQuery(id+"F0.wireOp",EDGE,"E4051"),sQuery(id+"F0.wireOp",EDGE,"E4052"),sQuery(id+"F0.wireOp",EDGE,"E4053"),sQuery(id+"F0.wireOp",EDGE,"E4054"),sQuery(id+"F0.wireOp",EDGE,"E4055"),sQuery(id+"F0.wireOp",EDGE,"E4056"),sQuery(id+"F0.wireOp",EDGE,"E4057"),sQuery(id+"F0.wireOp",EDGE,"E4058"),sQuery(id+"F0.wireOp",EDGE,"E4059"),sQuery(id+"F0.wireOp",EDGE,"E4060"),sQuery(id+"F0.wireOp",EDGE,"E4061"),sQuery(id+"F0.wireOp",EDGE,"E4062"),sQuery(id+"F0.wireOp",EDGE,"E4063"),sQuery(id+"F0.wireOp",EDGE,"E4064"),sQuery(id+"F0.wireOp",EDGE,"E4065"),sQuery(id+"F0.wireOp",EDGE,"E4066"),sQuery(id+"F0.wireOp",EDGE,"E4067"),sQuery(id+"F0.wireOp",EDGE,"E4068"),sQuery(id+"F0.wireOp",EDGE,"E4069"),sQuery(id+"F0.wireOp",EDGE,"E4070"),sQuery(id+"F0.wireOp",EDGE,"E4071"),sQuery(id+"F0.wireOp",EDGE,"E4072"),sQuery(id+"F0.wireOp",EDGE,"E4073"),sQuery(id+"F0.wireOp",EDGE,"E4074"),sQuery(id+"F0.wireOp",EDGE,"E4075"),sQuery(id+"F0.wireOp",EDGE,"E4076"),sQuery(id+"F0.wireOp",EDGE,"E4077"),sQuery(id+"F0.wireOp",EDGE,"E4078"),sQuery(id+"F0.wireOp",EDGE,"E4079"),sQuery(id+"F0.wireOp",EDGE,"E4080"),sQuery(id+"F0.wireOp",EDGE,"E4081"),sQuery(id+"F0.wireOp",EDGE,"E4082"),sQuery(id+"F0.wireOp",EDGE,"E4083"),sQuery(id+"F0.wireOp",EDGE,"E4084"),sQuery(id+"F0.wireOp",EDGE,"E4085"),sQuery(id+"F0.wireOp",EDGE,"E4086"),sQuery(id+"F0.wireOp",EDGE,"E4087"),sQuery(id+"F0.wireOp",EDGE,"E4088"),sQuery(id+"F0.wireOp",EDGE,"E4089"),sQuery(id+"F0.wireOp",EDGE,"E4090"),sQuery(id+"F0.wireOp",EDGE,"E4091"),sQuery(id+"F0.wireOp",EDGE,"E4092"),sQuery(id+"F0.wireOp",EDGE,"E4093"),sQuery(id+"F0.wireOp",EDGE,"E4094"),sQuery(id+"F0.wireOp",EDGE,"E4095"),sQuery(id+"F0.wireOp",EDGE,"E4096"),sQuery(id+"F0.wireOp",EDGE,"E4097"),sQuery(id+"F0.wireOp",EDGE,"E4098"),sQuery(id+"F0.wireOp",EDGE,"E4099"),sQuery(id+"F0.wireOp",EDGE,"E4100"),sQuery(id+"F0.wireOp",EDGE,"E4101"),sQuery(id+"F0.wireOp",EDGE,"E4102"),sQuery(id+"F0.wireOp",EDGE,"E4103"),sQuery(id+"F0.wireOp",EDGE,"E4104"),sQuery(id+"F0.wireOp",EDGE,"E4105"),sQuery(id+"F0.wireOp",EDGE,"E4106"),sQuery(id+"F0.wireOp",EDGE,"E4107"),sQuery(id+"F0.wireOp",EDGE,"E4108"),sQuery(id+"F0.wireOp",EDGE,"E4109"),sQuery(id+"F0.wireOp",EDGE,"E4110"),sQuery(id+"F0.wireOp",EDGE,"E4111"),sQuery(id+"F0.wireOp",EDGE,"E4112"),sQuery(id+"F0.wireOp",EDGE,"E4113"),sQuery(id+"F0.wireOp",EDGE,"E4114"),sQuery(id+"F0.wireOp",EDGE,"E4115"),sQuery(id+"F0.wireOp",EDGE,"E4116"),sQuery(id+"F0.wireOp",EDGE,"E4117"),sQuery(id+"F0.wireOp",EDGE,"E4118"),sQuery(id+"F0.wireOp",EDGE,"E4119"),sQuery(id+"F0.wireOp",EDGE,"E4120"),sQuery(id+"F0.wireOp",EDGE,"E4121"),sQuery(id+"F0.wireOp",EDGE,"E4122"),sQuery(id+"F0.wireOp",EDGE,"E4123"),sQuery(id+"F0.wireOp",EDGE,"E4124"),sQuery(id+"F0.wireOp",EDGE,"E4125"),sQuery(id+"F0.wireOp",EDGE,"E4126"),sQuery(id+"F0.wireOp",EDGE,"E4127"),sQuery(id+"F0.wireOp",EDGE,"E4128"),sQuery(id+"F0.wireOp",EDGE,"E4129"),sQuery(id+"F0.wireOp",EDGE,"E4130"),sQuery(id+"F0.wireOp",EDGE,"E4131"),sQuery(id+"F0.wireOp",EDGE,"E4132"),sQuery(id+"F0.wireOp",EDGE,"E4133"),sQuery(id+"F0.wireOp",EDGE,"E4134"),sQuery(id+"F0.wireOp",EDGE,"E4135"),sQuery(id+"F0.wireOp",EDGE,"E4136"),sQuery(id+"F0.wireOp",EDGE,"E4137"),sQuery(id+"F0.wireOp",EDGE,"E4138"),sQuery(id+"F0.wireOp",EDGE,"E4139"),sQuery(id+"F0.wireOp",EDGE,"E4140"),sQuery(id+"F0.wireOp",EDGE,"E4141"),sQuery(id+"F0.wireOp",EDGE,"E4142"),sQuery(id+"F0.wireOp",EDGE,"E4143"),sQuery(id+"F0.wireOp",EDGE,"E4144"),sQuery(id+"F0.wireOp",EDGE,"E4145"),sQuery(id+"F0.wireOp",EDGE,"E4146"),sQuery(id+"F0.wireOp",EDGE,"E4147"),sQuery(id+"F0.wireOp",EDGE,"E4148"),sQuery(id+"F0.wireOp",EDGE,"E4149"),sQuery(id+"F0.wireOp",EDGE,"E4150"),sQuery(id+"F0.wireOp",EDGE,"E4151"),sQuery(id+"F0.wireOp",EDGE,"E4152"),sQuery(id+"F0.wireOp",EDGE,"E4153"),sQuery(id+"F0.wireOp",EDGE,"E4154"),sQuery(id+"F0.wireOp",EDGE,"E4155"),sQuery(id+"F0.wireOp",EDGE,"E4156"),sQuery(id+"F0.wireOp",EDGE,"E4157"),sQuery(id+"F0.wireOp",EDGE,"E4158"),sQuery(id+"F0.wireOp",EDGE,"E4159"),sQuery(id+"F0.wireOp",EDGE,"E4160"),sQuery(id+"F0.wireOp",EDGE,"E4161"),sQuery(id+"F0.wireOp",EDGE,"E4162"),sQuery(id+"F0.wireOp",EDGE,"E4163"),sQuery(id+"F0.wireOp",EDGE,"E4164"),sQuery(id+"F0.wireOp",EDGE,"E4165"),sQuery(id+"F0.wireOp",EDGE,"E4166"),sQuery(id+"F0.wireOp",EDGE,"E4167"),sQuery(id+"F0.wireOp",EDGE,"E4168"),sQuery(id+"F0.wireOp",EDGE,"E4169"),sQuery(id+"F0.wireOp",EDGE,"E4170"),sQuery(id+"F0.wireOp",EDGE,"E4171"),sQuery(id+"F0.wireOp",EDGE,"E4172"),sQuery(id+"F0.wireOp",EDGE,"E4173"),sQuery(id+"F0.wireOp",EDGE,"E4174"),sQuery(id+"F0.wireOp",EDGE,"E4175"),sQuery(id+"F0.wireOp",EDGE,"E4176"),sQuery(id+"F0.wireOp",EDGE,"E4177"),sQuery(id+"F0.wireOp",EDGE,"E4178"),sQuery(id+"F0.wireOp",EDGE,"E4179"),sQuery(id+"F0.wireOp",EDGE,"E4180"),sQuery(id+"F0.wireOp",EDGE,"E4181"),sQuery(id+"F0.wireOp",EDGE,"E4182"),sQuery(id+"F0.wireOp",EDGE,"E4183"),sQuery(id+"F0.wireOp",EDGE,"E4184"),sQuery(id+"F0.wireOp",EDGE,"E4185"),sQuery(id+"F0.wireOp",EDGE,"E4186"),sQuery(id+"F0.wireOp",EDGE,"E4187"),sQuery(id+"F0.wireOp",EDGE,"E4188"),sQuery(id+"F0.wireOp",EDGE,"E4189"),sQuery(id+"F0.wireOp",EDGE,"E4403"),sQuery(id+"F0.wireOp",EDGE,"E4404")])],"isStart":false});
            var sketch = newSketch(context, id + "F2", { "sketchPlane" : qUnion([Q0])});
            skLineSegment(sketch, "E4405.bottom", {"start": v(-50.04, -31.3) * mm, "end": v(9.96, -31.3) * mm});
            skLineSegment(sketch, "E4405.top", {"start": v(-50.04, -36.3) * mm, "end": v(9.96, -36.3) * mm});
            skLineSegment(sketch, "E4405.left", {"start": v(-50.04, -31.3) * mm, "end": v(-50.04, -36.3) * mm});
            skLineSegment(sketch, "E4405.right", {"start": v(9.96, -31.3) * mm, "end": v(9.96, -36.3) * mm});
            skLineSegment(sketch, "E4406.bottom", {"start": v(-32.77, -31.3) * mm, "end": v(-22.41, -31.3) * mm});
            skLineSegment(sketch, "E4406.top", {"start": v(-32.77, -30.03) * mm, "end": v(-22.41, -30.03) * mm});
            skLineSegment(sketch, "E4406.left", {"start": v(-32.77, -31.3) * mm, "end": v(-32.77, -30.03) * mm});
            skLineSegment(sketch, "E4406.right", {"start": v(-22.41, -31.3) * mm, "end": v(-22.41, -30.03) * mm});
            skSolve(sketch);
        }
        {
            var Q0;
            Q0 = qSketchRegion(id + "F2", true);
            var Q1;
            {var subQ0=sQuery(id+"F2.wireOp",EDGE,"E4405.left");Q1=makeQuery(id+"F2.imprint","IMPRINT",FACE,{"disambiguationData":[TD([[makeQuery(id+"F2.imprint","IMPRINT",EDGE,{"derivedFrom":subQ0}),1.0]])]});}
            var Q2;
            Q2=makeQuery(id+"F1.opExtrude","CAP_FACE",FACE,{"disambiguationData":[OSD([sQuery(id+"F0.wireOp",EDGE,"E0"),sQuery(id+"F0.wireOp",EDGE,"E1"),sQuery(id+"F0.wireOp",EDGE,"E2"),sQuery(id+"F0.wireOp",EDGE,"E3"),sQuery(id+"F0.wireOp",EDGE,"E4"),sQuery(id+"F0.wireOp",EDGE,"E5"),sQuery(id+"F0.wireOp",EDGE,"E6"),sQuery(id+"F0.wireOp",EDGE,"E7"),sQuery(id+"F0.wireOp",EDGE,"E8"),sQuery(id+"F0.wireOp",EDGE,"E9"),sQuery(id+"F0.wireOp",EDGE,"E10"),sQuery(id+"F0.wireOp",EDGE,"E11"),sQuery(id+"F0.wireOp",EDGE,"E12"),sQuery(id+"F0.wireOp",EDGE,"E13"),sQuery(id+"F0.wireOp",EDGE,"E14"),sQuery(id+"F0.wireOp",EDGE,"E15"),sQuery(id+"F0.wireOp",EDGE,"E16"),sQuery(id+"F0.wireOp",EDGE,"E17"),sQuery(id+"F0.wireOp",EDGE,"E18"),sQuery(id+"F0.wireOp",EDGE,"E19"),sQuery(id+"F0.wireOp",EDGE,"E20"),sQuery(id+"F0.wireOp",EDGE,"E21"),sQuery(id+"F0.wireOp",EDGE,"E22"),sQuery(id+"F0.wireOp",EDGE,"E23"),sQuery(id+"F0.wireOp",EDGE,"E24"),sQuery(id+"F0.wireOp",EDGE,"E25"),sQuery(id+"F0.wireOp",EDGE,"E26"),sQuery(id+"F0.wireOp",EDGE,"E27"),sQuery(id+"F0.wireOp",EDGE,"E28"),sQuery(id+"F0.wireOp",EDGE,"E29"),sQuery(id+"F0.wireOp",EDGE,"E30"),sQuery(id+"F0.wireOp",EDGE,"E31"),sQuery(id+"F0.wireOp",EDGE,"E32"),sQuery(id+"F0.wireOp",EDGE,"E33"),sQuery(id+"F0.wireOp",EDGE,"E34"),sQuery(id+"F0.wireOp",EDGE,"E35"),sQuery(id+"F0.wireOp",EDGE,"E36"),sQuery(id+"F0.wireOp",EDGE,"E37"),sQuery(id+"F0.wireOp",EDGE,"E38"),sQuery(id+"F0.wireOp",EDGE,"E39"),sQuery(id+"F0.wireOp",EDGE,"E40"),sQuery(id+"F0.wireOp",EDGE,"E41"),sQuery(id+"F0.wireOp",EDGE,"E42"),sQuery(id+"F0.wireOp",EDGE,"E43"),sQuery(id+"F0.wireOp",EDGE,"E44"),sQuery(id+"F0.wireOp",EDGE,"E45"),sQuery(id+"F0.wireOp",EDGE,"E46"),sQuery(id+"F0.wireOp",EDGE,"E47"),sQuery(id+"F0.wireOp",EDGE,"E48"),sQuery(id+"F0.wireOp",EDGE,"E49"),sQuery(id+"F0.wireOp",EDGE,"E50"),sQuery(id+"F0.wireOp",EDGE,"E51"),sQuery(id+"F0.wireOp",EDGE,"E52"),sQuery(id+"F0.wireOp",EDGE,"E53"),sQuery(id+"F0.wireOp",EDGE,"E54"),sQuery(id+"F0.wireOp",EDGE,"E55"),sQuery(id+"F0.wireOp",EDGE,"E56"),sQuery(id+"F0.wireOp",EDGE,"E57"),sQuery(id+"F0.wireOp",EDGE,"E58"),sQuery(id+"F0.wireOp",EDGE,"E59"),sQuery(id+"F0.wireOp",EDGE,"E60"),sQuery(id+"F0.wireOp",EDGE,"E61"),sQuery(id+"F0.wireOp",EDGE,"E62"),sQuery(id+"F0.wireOp",EDGE,"E63"),sQuery(id+"F0.wireOp",EDGE,"E64"),sQuery(id+"F0.wireOp",EDGE,"E65"),sQuery(id+"F0.wireOp",EDGE,"E66"),sQuery(id+"F0.wireOp",EDGE,"E67"),sQuery(id+"F0.wireOp",EDGE,"E68"),sQuery(id+"F0.wireOp",EDGE,"E69"),sQuery(id+"F0.wireOp",EDGE,"E70"),sQuery(id+"F0.wireOp",EDGE,"E71"),sQuery(id+"F0.wireOp",EDGE,"E72"),sQuery(id+"F0.wireOp",EDGE,"E73"),sQuery(id+"F0.wireOp",EDGE,"E74"),sQuery(id+"F0.wireOp",EDGE,"E75"),sQuery(id+"F0.wireOp",EDGE,"E76"),sQuery(id+"F0.wireOp",EDGE,"E77"),sQuery(id+"F0.wireOp",EDGE,"E78"),sQuery(id+"F0.wireOp",EDGE,"E79"),sQuery(id+"F0.wireOp",EDGE,"E80"),sQuery(id+"F0.wireOp",EDGE,"E81"),sQuery(id+"F0.wireOp",EDGE,"E82"),sQuery(id+"F0.wireOp",EDGE,"E83"),sQuery(id+"F0.wireOp",EDGE,"E84"),sQuery(id+"F0.wireOp",EDGE,"E85"),sQuery(id+"F0.wireOp",EDGE,"E86"),sQuery(id+"F0.wireOp",EDGE,"E87"),sQuery(id+"F0.wireOp",EDGE,"E88"),sQuery(id+"F0.wireOp",EDGE,"E89"),sQuery(id+"F0.wireOp",EDGE,"E90"),sQuery(id+"F0.wireOp",EDGE,"E91"),sQuery(id+"F0.wireOp",EDGE,"E92"),sQuery(id+"F0.wireOp",EDGE,"E93"),sQuery(id+"F0.wireOp",EDGE,"E94"),sQuery(id+"F0.wireOp",EDGE,"E95"),sQuery(id+"F0.wireOp",EDGE,"E96"),sQuery(id+"F0.wireOp",EDGE,"E97"),sQuery(id+"F0.wireOp",EDGE,"E98"),sQuery(id+"F0.wireOp",EDGE,"E99"),sQuery(id+"F0.wireOp",EDGE,"E100"),sQuery(id+"F0.wireOp",EDGE,"E101"),sQuery(id+"F0.wireOp",EDGE,"E102"),sQuery(id+"F0.wireOp",EDGE,"E103"),sQuery(id+"F0.wireOp",EDGE,"E104"),sQuery(id+"F0.wireOp",EDGE,"E105"),sQuery(id+"F0.wireOp",EDGE,"E106"),sQuery(id+"F0.wireOp",EDGE,"E107"),sQuery(id+"F0.wireOp",EDGE,"E108"),sQuery(id+"F0.wireOp",EDGE,"E108"),sQuery(id+"F0.wireOp",EDGE,"E109"),sQuery(id+"F0.wireOp",EDGE,"E110"),sQuery(id+"F0.wireOp",EDGE,"E111"),sQuery(id+"F0.wireOp",EDGE,"E112"),sQuery(id+"F0.wireOp",EDGE,"E113"),sQuery(id+"F0.wireOp",EDGE,"E114"),sQuery(id+"F0.wireOp",EDGE,"E115"),sQuery(id+"F0.wireOp",EDGE,"E116"),sQuery(id+"F0.wireOp",EDGE,"E117"),sQuery(id+"F0.wireOp",EDGE,"E118"),sQuery(id+"F0.wireOp",EDGE,"E119"),sQuery(id+"F0.wireOp",EDGE,"E120"),sQuery(id+"F0.wireOp",EDGE,"E121"),sQuery(id+"F0.wireOp",EDGE,"E122"),sQuery(id+"F0.wireOp",EDGE,"E123"),sQuery(id+"F0.wireOp",EDGE,"E124"),sQuery(id+"F0.wireOp",EDGE,"E125"),sQuery(id+"F0.wireOp",EDGE,"E126"),sQuery(id+"F0.wireOp",EDGE,"E127"),sQuery(id+"F0.wireOp",EDGE,"E128"),sQuery(id+"F0.wireOp",EDGE,"E129"),sQuery(id+"F0.wireOp",EDGE,"E130"),sQuery(id+"F0.wireOp",EDGE,"E131"),sQuery(id+"F0.wireOp",EDGE,"E132"),sQuery(id+"F0.wireOp",EDGE,"E133"),sQuery(id+"F0.wireOp",EDGE,"E134"),sQuery(id+"F0.wireOp",EDGE,"E135"),sQuery(id+"F0.wireOp",EDGE,"E136"),sQuery(id+"F0.wireOp",EDGE,"E137"),sQuery(id+"F0.wireOp",EDGE,"E138"),sQuery(id+"F0.wireOp",EDGE,"E139"),sQuery(id+"F0.wireOp",EDGE,"E140"),sQuery(id+"F0.wireOp",EDGE,"E141"),sQuery(id+"F0.wireOp",EDGE,"E142"),sQuery(id+"F0.wireOp",EDGE,"E143"),sQuery(id+"F0.wireOp",EDGE,"E144"),sQuery(id+"F0.wireOp",EDGE,"E145"),sQuery(id+"F0.wireOp",EDGE,"E146"),sQuery(id+"F0.wireOp",EDGE,"E147"),sQuery(id+"F0.wireOp",EDGE,"E148"),sQuery(id+"F0.wireOp",EDGE,"E149"),sQuery(id+"F0.wireOp",EDGE,"E150"),sQuery(id+"F0.wireOp",EDGE,"E151"),sQuery(id+"F0.wireOp",EDGE,"E152"),sQuery(id+"F0.wireOp",EDGE,"E153"),sQuery(id+"F0.wireOp",EDGE,"E154"),sQuery(id+"F0.wireOp",EDGE,"E155"),sQuery(id+"F0.wireOp",EDGE,"E156"),sQuery(id+"F0.wireOp",EDGE,"E157"),sQuery(id+"F0.wireOp",EDGE,"E158"),sQuery(id+"F0.wireOp",EDGE,"E159"),sQuery(id+"F0.wireOp",EDGE,"E160"),sQuery(id+"F0.wireOp",EDGE,"E161"),sQuery(id+"F0.wireOp",EDGE,"E162"),sQuery(id+"F0.wireOp",EDGE,"E163"),sQuery(id+"F0.wireOp",EDGE,"E164"),sQuery(id+"F0.wireOp",EDGE,"E165"),sQuery(id+"F0.wireOp",EDGE,"E166"),sQuery(id+"F0.wireOp",EDGE,"E167"),sQuery(id+"F0.wireOp",EDGE,"E168"),sQuery(id+"F0.wireOp",EDGE,"E169"),sQuery(id+"F0.wireOp",EDGE,"E170"),sQuery(id+"F0.wireOp",EDGE,"E171"),sQuery(id+"F0.wireOp",EDGE,"E172"),sQuery(id+"F0.wireOp",EDGE,"E173"),sQuery(id+"F0.wireOp",EDGE,"E174"),sQuery(id+"F0.wireOp",EDGE,"E175"),sQuery(id+"F0.wireOp",EDGE,"E176"),sQuery(id+"F0.wireOp",EDGE,"E177"),sQuery(id+"F0.wireOp",EDGE,"E178"),sQuery(id+"F0.wireOp",EDGE,"E179"),sQuery(id+"F0.wireOp",EDGE,"E180"),sQuery(id+"F0.wireOp",EDGE,"E181"),sQuery(id+"F0.wireOp",EDGE,"E182"),sQuery(id+"F0.wireOp",EDGE,"E183"),sQuery(id+"F0.wireOp",EDGE,"E184"),sQuery(id+"F0.wireOp",EDGE,"E185"),sQuery(id+"F0.wireOp",EDGE,"E186"),sQuery(id+"F0.wireOp",EDGE,"E187"),sQuery(id+"F0.wireOp",EDGE,"E188"),sQuery(id+"F0.wireOp",EDGE,"E189"),sQuery(id+"F0.wireOp",EDGE,"E190"),sQuery(id+"F0.wireOp",EDGE,"E191"),sQuery(id+"F0.wireOp",EDGE,"E192"),sQuery(id+"F0.wireOp",EDGE,"E193"),sQuery(id+"F0.wireOp",EDGE,"E194"),sQuery(id+"F0.wireOp",EDGE,"E195"),sQuery(id+"F0.wireOp",EDGE,"E196"),sQuery(id+"F0.wireOp",EDGE,"E197"),sQuery(id+"F0.wireOp",EDGE,"E198"),sQuery(id+"F0.wireOp",EDGE,"E199"),sQuery(id+"F0.wireOp",EDGE,"E200"),sQuery(id+"F0.wireOp",EDGE,"E201"),sQuery(id+"F0.wireOp",EDGE,"E202"),sQuery(id+"F0.wireOp",EDGE,"E203"),sQuery(id+"F0.wireOp",EDGE,"E204"),sQuery(id+"F0.wireOp",EDGE,"E205"),sQuery(id+"F0.wireOp",EDGE,"E206"),sQuery(id+"F0.wireOp",EDGE,"E207"),sQuery(id+"F0.wireOp",EDGE,"E208"),sQuery(id+"F0.wireOp",EDGE,"E209"),sQuery(id+"F0.wireOp",EDGE,"E210"),sQuery(id+"F0.wireOp",EDGE,"E211"),sQuery(id+"F0.wireOp",EDGE,"E212"),sQuery(id+"F0.wireOp",EDGE,"E214"),sQuery(id+"F0.wireOp",EDGE,"E215"),sQuery(id+"F0.wireOp",EDGE,"E216"),sQuery(id+"F0.wireOp",EDGE,"E217"),sQuery(id+"F0.wireOp",EDGE,"E218"),sQuery(id+"F0.wireOp",EDGE,"E219"),sQuery(id+"F0.wireOp",EDGE,"E220"),sQuery(id+"F0.wireOp",EDGE,"E221"),sQuery(id+"F0.wireOp",EDGE,"E222"),sQuery(id+"F0.wireOp",EDGE,"E223"),sQuery(id+"F0.wireOp",EDGE,"E224"),sQuery(id+"F0.wireOp",EDGE,"E225"),sQuery(id+"F0.wireOp",EDGE,"E226"),sQuery(id+"F0.wireOp",EDGE,"E227"),sQuery(id+"F0.wireOp",EDGE,"E228"),sQuery(id+"F0.wireOp",EDGE,"E229"),sQuery(id+"F0.wireOp",EDGE,"E230"),sQuery(id+"F0.wireOp",EDGE,"E231"),sQuery(id+"F0.wireOp",EDGE,"E232"),sQuery(id+"F0.wireOp",EDGE,"E233"),sQuery(id+"F0.wireOp",EDGE,"E234"),sQuery(id+"F0.wireOp",EDGE,"E235"),sQuery(id+"F0.wireOp",EDGE,"E236"),sQuery(id+"F0.wireOp",EDGE,"E237"),sQuery(id+"F0.wireOp",EDGE,"E238"),sQuery(id+"F0.wireOp",EDGE,"E239"),sQuery(id+"F0.wireOp",EDGE,"E240"),sQuery(id+"F0.wireOp",EDGE,"E241"),sQuery(id+"F0.wireOp",EDGE,"E242"),sQuery(id+"F0.wireOp",EDGE,"E243"),sQuery(id+"F0.wireOp",EDGE,"E244"),sQuery(id+"F0.wireOp",EDGE,"E245"),sQuery(id+"F0.wireOp",EDGE,"E246"),sQuery(id+"F0.wireOp",EDGE,"E247"),sQuery(id+"F0.wireOp",EDGE,"E248"),sQuery(id+"F0.wireOp",EDGE,"E249"),sQuery(id+"F0.wireOp",EDGE,"E250"),sQuery(id+"F0.wireOp",EDGE,"E251"),sQuery(id+"F0.wireOp",EDGE,"E252"),sQuery(id+"F0.wireOp",EDGE,"E253"),sQuery(id+"F0.wireOp",EDGE,"E254"),sQuery(id+"F0.wireOp",EDGE,"E255"),sQuery(id+"F0.wireOp",EDGE,"E256"),sQuery(id+"F0.wireOp",EDGE,"E257"),sQuery(id+"F0.wireOp",EDGE,"E258"),sQuery(id+"F0.wireOp",EDGE,"E259"),sQuery(id+"F0.wireOp",EDGE,"E260"),sQuery(id+"F0.wireOp",EDGE,"E261"),sQuery(id+"F0.wireOp",EDGE,"E262"),sQuery(id+"F0.wireOp",EDGE,"E263"),sQuery(id+"F0.wireOp",EDGE,"E264"),sQuery(id+"F0.wireOp",EDGE,"E265"),sQuery(id+"F0.wireOp",EDGE,"E266"),sQuery(id+"F0.wireOp",EDGE,"E267"),sQuery(id+"F0.wireOp",EDGE,"E268"),sQuery(id+"F0.wireOp",EDGE,"E269"),sQuery(id+"F0.wireOp",EDGE,"E270"),sQuery(id+"F0.wireOp",EDGE,"E271"),sQuery(id+"F0.wireOp",EDGE,"E272"),sQuery(id+"F0.wireOp",EDGE,"E273"),sQuery(id+"F0.wireOp",EDGE,"E274"),sQuery(id+"F0.wireOp",EDGE,"E275"),sQuery(id+"F0.wireOp",EDGE,"E276"),sQuery(id+"F0.wireOp",EDGE,"E277"),sQuery(id+"F0.wireOp",EDGE,"E278"),sQuery(id+"F0.wireOp",EDGE,"E279"),sQuery(id+"F0.wireOp",EDGE,"E280"),sQuery(id+"F0.wireOp",EDGE,"E281"),sQuery(id+"F0.wireOp",EDGE,"E282"),sQuery(id+"F0.wireOp",EDGE,"E283"),sQuery(id+"F0.wireOp",EDGE,"E284"),sQuery(id+"F0.wireOp",EDGE,"E285"),sQuery(id+"F0.wireOp",EDGE,"E286"),sQuery(id+"F0.wireOp",EDGE,"E287"),sQuery(id+"F0.wireOp",EDGE,"E288"),sQuery(id+"F0.wireOp",EDGE,"E289"),sQuery(id+"F0.wireOp",EDGE,"E290"),sQuery(id+"F0.wireOp",EDGE,"E291"),sQuery(id+"F0.wireOp",EDGE,"E292"),sQuery(id+"F0.wireOp",EDGE,"E293"),sQuery(id+"F0.wireOp",EDGE,"E294"),sQuery(id+"F0.wireOp",EDGE,"E295"),sQuery(id+"F0.wireOp",EDGE,"E296"),sQuery(id+"F0.wireOp",EDGE,"E297"),sQuery(id+"F0.wireOp",EDGE,"E298"),sQuery(id+"F0.wireOp",EDGE,"E299"),sQuery(id+"F0.wireOp",EDGE,"E300"),sQuery(id+"F0.wireOp",EDGE,"E301"),sQuery(id+"F0.wireOp",EDGE,"E302"),sQuery(id+"F0.wireOp",EDGE,"E303"),sQuery(id+"F0.wireOp",EDGE,"E304"),sQuery(id+"F0.wireOp",EDGE,"E305"),sQuery(id+"F0.wireOp",EDGE,"E306"),sQuery(id+"F0.wireOp",EDGE,"E307"),sQuery(id+"F0.wireOp",EDGE,"E308"),sQuery(id+"F0.wireOp",EDGE,"E309"),sQuery(id+"F0.wireOp",EDGE,"E310"),sQuery(id+"F0.wireOp",EDGE,"E311"),sQuery(id+"F0.wireOp",EDGE,"E312"),sQuery(id+"F0.wireOp",EDGE,"E313"),sQuery(id+"F0.wireOp",EDGE,"E314"),sQuery(id+"F0.wireOp",EDGE,"E315"),sQuery(id+"F0.wireOp",EDGE,"E316"),sQuery(id+"F0.wireOp",EDGE,"E317"),sQuery(id+"F0.wireOp",EDGE,"E318"),sQuery(id+"F0.wireOp",EDGE,"E319"),sQuery(id+"F0.wireOp",EDGE,"E320"),sQuery(id+"F0.wireOp",EDGE,"E321"),sQuery(id+"F0.wireOp",EDGE,"E322"),sQuery(id+"F0.wireOp",EDGE,"E323"),sQuery(id+"F0.wireOp",EDGE,"E324"),sQuery(id+"F0.wireOp",EDGE,"E325"),sQuery(id+"F0.wireOp",EDGE,"E326"),sQuery(id+"F0.wireOp",EDGE,"E327"),sQuery(id+"F0.wireOp",EDGE,"E328"),sQuery(id+"F0.wireOp",EDGE,"E329"),sQuery(id+"F0.wireOp",EDGE,"E330"),sQuery(id+"F0.wireOp",EDGE,"E331"),sQuery(id+"F0.wireOp",EDGE,"E332"),sQuery(id+"F0.wireOp",EDGE,"E333"),sQuery(id+"F0.wireOp",EDGE,"E334"),sQuery(id+"F0.wireOp",EDGE,"E335"),sQuery(id+"F0.wireOp",EDGE,"E336"),sQuery(id+"F0.wireOp",EDGE,"E337"),sQuery(id+"F0.wireOp",EDGE,"E338"),sQuery(id+"F0.wireOp",EDGE,"E339"),sQuery(id+"F0.wireOp",EDGE,"E340"),sQuery(id+"F0.wireOp",EDGE,"E341"),sQuery(id+"F0.wireOp",EDGE,"E342"),sQuery(id+"F0.wireOp",EDGE,"E343"),sQuery(id+"F0.wireOp",EDGE,"E344"),sQuery(id+"F0.wireOp",EDGE,"E345"),sQuery(id+"F0.wireOp",EDGE,"E346"),sQuery(id+"F0.wireOp",EDGE,"E347"),sQuery(id+"F0.wireOp",EDGE,"E348"),sQuery(id+"F0.wireOp",EDGE,"E349"),sQuery(id+"F0.wireOp",EDGE,"E350"),sQuery(id+"F0.wireOp",EDGE,"E351"),sQuery(id+"F0.wireOp",EDGE,"E352"),sQuery(id+"F0.wireOp",EDGE,"E353"),sQuery(id+"F0.wireOp",EDGE,"E354"),sQuery(id+"F0.wireOp",EDGE,"E355"),sQuery(id+"F0.wireOp",EDGE,"E356"),sQuery(id+"F0.wireOp",EDGE,"E357"),sQuery(id+"F0.wireOp",EDGE,"E358"),sQuery(id+"F0.wireOp",EDGE,"E359"),sQuery(id+"F0.wireOp",EDGE,"E360"),sQuery(id+"F0.wireOp",EDGE,"E361"),sQuery(id+"F0.wireOp",EDGE,"E362"),sQuery(id+"F0.wireOp",EDGE,"E363"),sQuery(id+"F0.wireOp",EDGE,"E364"),sQuery(id+"F0.wireOp",EDGE,"E365"),sQuery(id+"F0.wireOp",EDGE,"E366"),sQuery(id+"F0.wireOp",EDGE,"E367"),sQuery(id+"F0.wireOp",EDGE,"E368"),sQuery(id+"F0.wireOp",EDGE,"E369"),sQuery(id+"F0.wireOp",EDGE,"E370"),sQuery(id+"F0.wireOp",EDGE,"E371"),sQuery(id+"F0.wireOp",EDGE,"E372"),sQuery(id+"F0.wireOp",EDGE,"E373"),sQuery(id+"F0.wireOp",EDGE,"E374"),sQuery(id+"F0.wireOp",EDGE,"E375"),sQuery(id+"F0.wireOp",EDGE,"E376"),sQuery(id+"F0.wireOp",EDGE,"E377"),sQuery(id+"F0.wireOp",EDGE,"E378"),sQuery(id+"F0.wireOp",EDGE,"E379"),sQuery(id+"F0.wireOp",EDGE,"E380"),sQuery(id+"F0.wireOp",EDGE,"E381"),sQuery(id+"F0.wireOp",EDGE,"E382"),sQuery(id+"F0.wireOp",EDGE,"E383"),sQuery(id+"F0.wireOp",EDGE,"E384"),sQuery(id+"F0.wireOp",EDGE,"E385"),sQuery(id+"F0.wireOp",EDGE,"E386"),sQuery(id+"F0.wireOp",EDGE,"E387"),sQuery(id+"F0.wireOp",EDGE,"E388"),sQuery(id+"F0.wireOp",EDGE,"E389"),sQuery(id+"F0.wireOp",EDGE,"E390"),sQuery(id+"F0.wireOp",EDGE,"E391"),sQuery(id+"F0.wireOp",EDGE,"E392"),sQuery(id+"F0.wireOp",EDGE,"E393"),sQuery(id+"F0.wireOp",EDGE,"E394"),sQuery(id+"F0.wireOp",EDGE,"E395"),sQuery(id+"F0.wireOp",EDGE,"E396"),sQuery(id+"F0.wireOp",EDGE,"E397"),sQuery(id+"F0.wireOp",EDGE,"E398"),sQuery(id+"F0.wireOp",EDGE,"E399"),sQuery(id+"F0.wireOp",EDGE,"E400"),sQuery(id+"F0.wireOp",EDGE,"E401"),sQuery(id+"F0.wireOp",EDGE,"E402"),sQuery(id+"F0.wireOp",EDGE,"E403"),sQuery(id+"F0.wireOp",EDGE,"E404"),sQuery(id+"F0.wireOp",EDGE,"E405"),sQuery(id+"F0.wireOp",EDGE,"E406"),sQuery(id+"F0.wireOp",EDGE,"E407"),sQuery(id+"F0.wireOp",EDGE,"E408"),sQuery(id+"F0.wireOp",EDGE,"E409"),sQuery(id+"F0.wireOp",EDGE,"E410"),sQuery(id+"F0.wireOp",EDGE,"E411"),sQuery(id+"F0.wireOp",EDGE,"E412"),sQuery(id+"F0.wireOp",EDGE,"E413"),sQuery(id+"F0.wireOp",EDGE,"E414"),sQuery(id+"F0.wireOp",EDGE,"E415"),sQuery(id+"F0.wireOp",EDGE,"E416"),sQuery(id+"F0.wireOp",EDGE,"E417"),sQuery(id+"F0.wireOp",EDGE,"E418"),sQuery(id+"F0.wireOp",EDGE,"E419"),sQuery(id+"F0.wireOp",EDGE,"E420"),sQuery(id+"F0.wireOp",EDGE,"E421"),sQuery(id+"F0.wireOp",EDGE,"E422"),sQuery(id+"F0.wireOp",EDGE,"E423"),sQuery(id+"F0.wireOp",EDGE,"E424"),sQuery(id+"F0.wireOp",EDGE,"E425"),sQuery(id+"F0.wireOp",EDGE,"E426"),sQuery(id+"F0.wireOp",EDGE,"E427"),sQuery(id+"F0.wireOp",EDGE,"E428"),sQuery(id+"F0.wireOp",EDGE,"E429"),sQuery(id+"F0.wireOp",EDGE,"E430"),sQuery(id+"F0.wireOp",EDGE,"E431"),sQuery(id+"F0.wireOp",EDGE,"E432"),sQuery(id+"F0.wireOp",EDGE,"E433"),sQuery(id+"F0.wireOp",EDGE,"E434"),sQuery(id+"F0.wireOp",EDGE,"E435"),sQuery(id+"F0.wireOp",EDGE,"E436"),sQuery(id+"F0.wireOp",EDGE,"E437"),sQuery(id+"F0.wireOp",EDGE,"E438"),sQuery(id+"F0.wireOp",EDGE,"E439"),sQuery(id+"F0.wireOp",EDGE,"E440"),sQuery(id+"F0.wireOp",EDGE,"E441"),sQuery(id+"F0.wireOp",EDGE,"E442"),sQuery(id+"F0.wireOp",EDGE,"E443"),sQuery(id+"F0.wireOp",EDGE,"E444"),sQuery(id+"F0.wireOp",EDGE,"E445"),sQuery(id+"F0.wireOp",EDGE,"E446"),sQuery(id+"F0.wireOp",EDGE,"E447"),sQuery(id+"F0.wireOp",EDGE,"E448"),sQuery(id+"F0.wireOp",EDGE,"E449"),sQuery(id+"F0.wireOp",EDGE,"E450"),sQuery(id+"F0.wireOp",EDGE,"E451"),sQuery(id+"F0.wireOp",EDGE,"E452"),sQuery(id+"F0.wireOp",EDGE,"E453"),sQuery(id+"F0.wireOp",EDGE,"E454"),sQuery(id+"F0.wireOp",EDGE,"E455"),sQuery(id+"F0.wireOp",EDGE,"E456"),sQuery(id+"F0.wireOp",EDGE,"E457"),sQuery(id+"F0.wireOp",EDGE,"E458"),sQuery(id+"F0.wireOp",EDGE,"E459"),sQuery(id+"F0.wireOp",EDGE,"E460"),sQuery(id+"F0.wireOp",EDGE,"E461"),sQuery(id+"F0.wireOp",EDGE,"E462"),sQuery(id+"F0.wireOp",EDGE,"E463"),sQuery(id+"F0.wireOp",EDGE,"E464"),sQuery(id+"F0.wireOp",EDGE,"E465"),sQuery(id+"F0.wireOp",EDGE,"E466"),sQuery(id+"F0.wireOp",EDGE,"E467"),sQuery(id+"F0.wireOp",EDGE,"E468"),sQuery(id+"F0.wireOp",EDGE,"E469"),sQuery(id+"F0.wireOp",EDGE,"E470"),sQuery(id+"F0.wireOp",EDGE,"E471"),sQuery(id+"F0.wireOp",EDGE,"E472"),sQuery(id+"F0.wireOp",EDGE,"E473"),sQuery(id+"F0.wireOp",EDGE,"E474"),sQuery(id+"F0.wireOp",EDGE,"E475"),sQuery(id+"F0.wireOp",EDGE,"E476"),sQuery(id+"F0.wireOp",EDGE,"E477"),sQuery(id+"F0.wireOp",EDGE,"E478"),sQuery(id+"F0.wireOp",EDGE,"E479"),sQuery(id+"F0.wireOp",EDGE,"E480"),sQuery(id+"F0.wireOp",EDGE,"E481"),sQuery(id+"F0.wireOp",EDGE,"E482"),sQuery(id+"F0.wireOp",EDGE,"E483"),sQuery(id+"F0.wireOp",EDGE,"E484"),sQuery(id+"F0.wireOp",EDGE,"E485"),sQuery(id+"F0.wireOp",EDGE,"E486"),sQuery(id+"F0.wireOp",EDGE,"E487"),sQuery(id+"F0.wireOp",EDGE,"E488"),sQuery(id+"F0.wireOp",EDGE,"E489"),sQuery(id+"F0.wireOp",EDGE,"E490"),sQuery(id+"F0.wireOp",EDGE,"E491"),sQuery(id+"F0.wireOp",EDGE,"E492"),sQuery(id+"F0.wireOp",EDGE,"E493"),sQuery(id+"F0.wireOp",EDGE,"E494"),sQuery(id+"F0.wireOp",EDGE,"E495"),sQuery(id+"F0.wireOp",EDGE,"E496"),sQuery(id+"F0.wireOp",EDGE,"E497"),sQuery(id+"F0.wireOp",EDGE,"E498"),sQuery(id+"F0.wireOp",EDGE,"E499"),sQuery(id+"F0.wireOp",EDGE,"E500"),sQuery(id+"F0.wireOp",EDGE,"E501"),sQuery(id+"F0.wireOp",EDGE,"E502"),sQuery(id+"F0.wireOp",EDGE,"E503"),sQuery(id+"F0.wireOp",EDGE,"E504"),sQuery(id+"F0.wireOp",EDGE,"E505"),sQuery(id+"F0.wireOp",EDGE,"E506"),sQuery(id+"F0.wireOp",EDGE,"E507"),sQuery(id+"F0.wireOp",EDGE,"E508"),sQuery(id+"F0.wireOp",EDGE,"E509"),sQuery(id+"F0.wireOp",EDGE,"E510"),sQuery(id+"F0.wireOp",EDGE,"E511"),sQuery(id+"F0.wireOp",EDGE,"E512"),sQuery(id+"F0.wireOp",EDGE,"E513"),sQuery(id+"F0.wireOp",EDGE,"E514"),sQuery(id+"F0.wireOp",EDGE,"E515"),sQuery(id+"F0.wireOp",EDGE,"E516"),sQuery(id+"F0.wireOp",EDGE,"E517"),sQuery(id+"F0.wireOp",EDGE,"E518"),sQuery(id+"F0.wireOp",EDGE,"E519"),sQuery(id+"F0.wireOp",EDGE,"E520"),sQuery(id+"F0.wireOp",EDGE,"E521"),sQuery(id+"F0.wireOp",EDGE,"E522"),sQuery(id+"F0.wireOp",EDGE,"E523"),sQuery(id+"F0.wireOp",EDGE,"E524"),sQuery(id+"F0.wireOp",EDGE,"E525"),sQuery(id+"F0.wireOp",EDGE,"E526"),sQuery(id+"F0.wireOp",EDGE,"E527"),sQuery(id+"F0.wireOp",EDGE,"E528"),sQuery(id+"F0.wireOp",EDGE,"E529"),sQuery(id+"F0.wireOp",EDGE,"E530"),sQuery(id+"F0.wireOp",EDGE,"E531"),sQuery(id+"F0.wireOp",EDGE,"E532"),sQuery(id+"F0.wireOp",EDGE,"E533"),sQuery(id+"F0.wireOp",EDGE,"E534"),sQuery(id+"F0.wireOp",EDGE,"E535"),sQuery(id+"F0.wireOp",EDGE,"E536"),sQuery(id+"F0.wireOp",EDGE,"E537"),sQuery(id+"F0.wireOp",EDGE,"E538"),sQuery(id+"F0.wireOp",EDGE,"E539"),sQuery(id+"F0.wireOp",EDGE,"E540"),sQuery(id+"F0.wireOp",EDGE,"E541"),sQuery(id+"F0.wireOp",EDGE,"E542"),sQuery(id+"F0.wireOp",EDGE,"E543"),sQuery(id+"F0.wireOp",EDGE,"E544"),sQuery(id+"F0.wireOp",EDGE,"E545"),sQuery(id+"F0.wireOp",EDGE,"E546"),sQuery(id+"F0.wireOp",EDGE,"E547"),sQuery(id+"F0.wireOp",EDGE,"E548"),sQuery(id+"F0.wireOp",EDGE,"E549"),sQuery(id+"F0.wireOp",EDGE,"E550"),sQuery(id+"F0.wireOp",EDGE,"E551"),sQuery(id+"F0.wireOp",EDGE,"E552"),sQuery(id+"F0.wireOp",EDGE,"E553"),sQuery(id+"F0.wireOp",EDGE,"E554"),sQuery(id+"F0.wireOp",EDGE,"E555"),sQuery(id+"F0.wireOp",EDGE,"E556"),sQuery(id+"F0.wireOp",EDGE,"E557"),sQuery(id+"F0.wireOp",EDGE,"E558"),sQuery(id+"F0.wireOp",EDGE,"E559"),sQuery(id+"F0.wireOp",EDGE,"E560"),sQuery(id+"F0.wireOp",EDGE,"E561"),sQuery(id+"F0.wireOp",EDGE,"E562"),sQuery(id+"F0.wireOp",EDGE,"E563"),sQuery(id+"F0.wireOp",EDGE,"E564"),sQuery(id+"F0.wireOp",EDGE,"E565"),sQuery(id+"F0.wireOp",EDGE,"E566"),sQuery(id+"F0.wireOp",EDGE,"E567"),sQuery(id+"F0.wireOp",EDGE,"E568"),sQuery(id+"F0.wireOp",EDGE,"E569"),sQuery(id+"F0.wireOp",EDGE,"E570"),sQuery(id+"F0.wireOp",EDGE,"E571"),sQuery(id+"F0.wireOp",EDGE,"E572"),sQuery(id+"F0.wireOp",EDGE,"E573"),sQuery(id+"F0.wireOp",EDGE,"E574"),sQuery(id+"F0.wireOp",EDGE,"E575"),sQuery(id+"F0.wireOp",EDGE,"E576"),sQuery(id+"F0.wireOp",EDGE,"E577"),sQuery(id+"F0.wireOp",EDGE,"E578"),sQuery(id+"F0.wireOp",EDGE,"E579"),sQuery(id+"F0.wireOp",EDGE,"E580"),sQuery(id+"F0.wireOp",EDGE,"E581"),sQuery(id+"F0.wireOp",EDGE,"E582"),sQuery(id+"F0.wireOp",EDGE,"E583"),sQuery(id+"F0.wireOp",EDGE,"E584"),sQuery(id+"F0.wireOp",EDGE,"E585"),sQuery(id+"F0.wireOp",EDGE,"E586"),sQuery(id+"F0.wireOp",EDGE,"E587"),sQuery(id+"F0.wireOp",EDGE,"E588"),sQuery(id+"F0.wireOp",EDGE,"E589"),sQuery(id+"F0.wireOp",EDGE,"E590"),sQuery(id+"F0.wireOp",EDGE,"E591"),sQuery(id+"F0.wireOp",EDGE,"E592"),sQuery(id+"F0.wireOp",EDGE,"E593"),sQuery(id+"F0.wireOp",EDGE,"E594"),sQuery(id+"F0.wireOp",EDGE,"E595"),sQuery(id+"F0.wireOp",EDGE,"E596"),sQuery(id+"F0.wireOp",EDGE,"E597"),sQuery(id+"F0.wireOp",EDGE,"E598"),sQuery(id+"F0.wireOp",EDGE,"E599"),sQuery(id+"F0.wireOp",EDGE,"E600"),sQuery(id+"F0.wireOp",EDGE,"E601"),sQuery(id+"F0.wireOp",EDGE,"E602"),sQuery(id+"F0.wireOp",EDGE,"E603"),sQuery(id+"F0.wireOp",EDGE,"E604"),sQuery(id+"F0.wireOp",EDGE,"E605"),sQuery(id+"F0.wireOp",EDGE,"E606"),sQuery(id+"F0.wireOp",EDGE,"E607"),sQuery(id+"F0.wireOp",EDGE,"E608"),sQuery(id+"F0.wireOp",EDGE,"E609"),sQuery(id+"F0.wireOp",EDGE,"E610"),sQuery(id+"F0.wireOp",EDGE,"E611"),sQuery(id+"F0.wireOp",EDGE,"E612"),sQuery(id+"F0.wireOp",EDGE,"E613"),sQuery(id+"F0.wireOp",EDGE,"E614"),sQuery(id+"F0.wireOp",EDGE,"E615"),sQuery(id+"F0.wireOp",EDGE,"E616"),sQuery(id+"F0.wireOp",EDGE,"E617"),sQuery(id+"F0.wireOp",EDGE,"E618"),sQuery(id+"F0.wireOp",EDGE,"E619"),sQuery(id+"F0.wireOp",EDGE,"E620"),sQuery(id+"F0.wireOp",EDGE,"E621"),sQuery(id+"F0.wireOp",EDGE,"E622"),sQuery(id+"F0.wireOp",EDGE,"E623"),sQuery(id+"F0.wireOp",EDGE,"E624"),sQuery(id+"F0.wireOp",EDGE,"E625"),sQuery(id+"F0.wireOp",EDGE,"E626"),sQuery(id+"F0.wireOp",EDGE,"E627"),sQuery(id+"F0.wireOp",EDGE,"E628"),sQuery(id+"F0.wireOp",EDGE,"E629"),sQuery(id+"F0.wireOp",EDGE,"E630"),sQuery(id+"F0.wireOp",EDGE,"E631"),sQuery(id+"F0.wireOp",EDGE,"E632"),sQuery(id+"F0.wireOp",EDGE,"E633"),sQuery(id+"F0.wireOp",EDGE,"E634"),sQuery(id+"F0.wireOp",EDGE,"E635"),sQuery(id+"F0.wireOp",EDGE,"E636"),sQuery(id+"F0.wireOp",EDGE,"E637"),sQuery(id+"F0.wireOp",EDGE,"E638"),sQuery(id+"F0.wireOp",EDGE,"E639"),sQuery(id+"F0.wireOp",EDGE,"E640"),sQuery(id+"F0.wireOp",EDGE,"E641"),sQuery(id+"F0.wireOp",EDGE,"E642"),sQuery(id+"F0.wireOp",EDGE,"E643"),sQuery(id+"F0.wireOp",EDGE,"E644"),sQuery(id+"F0.wireOp",EDGE,"E645"),sQuery(id+"F0.wireOp",EDGE,"E646"),sQuery(id+"F0.wireOp",EDGE,"E647"),sQuery(id+"F0.wireOp",EDGE,"E648"),sQuery(id+"F0.wireOp",EDGE,"E649"),sQuery(id+"F0.wireOp",EDGE,"E650"),sQuery(id+"F0.wireOp",EDGE,"E651"),sQuery(id+"F0.wireOp",EDGE,"E652"),sQuery(id+"F0.wireOp",EDGE,"E653"),sQuery(id+"F0.wireOp",EDGE,"E654"),sQuery(id+"F0.wireOp",EDGE,"E655"),sQuery(id+"F0.wireOp",EDGE,"E656"),sQuery(id+"F0.wireOp",EDGE,"E657"),sQuery(id+"F0.wireOp",EDGE,"E658"),sQuery(id+"F0.wireOp",EDGE,"E659"),sQuery(id+"F0.wireOp",EDGE,"E660"),sQuery(id+"F0.wireOp",EDGE,"E661"),sQuery(id+"F0.wireOp",EDGE,"E662"),sQuery(id+"F0.wireOp",EDGE,"E663"),sQuery(id+"F0.wireOp",EDGE,"E664"),sQuery(id+"F0.wireOp",EDGE,"E665"),sQuery(id+"F0.wireOp",EDGE,"E666"),sQuery(id+"F0.wireOp",EDGE,"E667"),sQuery(id+"F0.wireOp",EDGE,"E668"),sQuery(id+"F0.wireOp",EDGE,"E669"),sQuery(id+"F0.wireOp",EDGE,"E670"),sQuery(id+"F0.wireOp",EDGE,"E671"),sQuery(id+"F0.wireOp",EDGE,"E672"),sQuery(id+"F0.wireOp",EDGE,"E673"),sQuery(id+"F0.wireOp",EDGE,"E674"),sQuery(id+"F0.wireOp",EDGE,"E675"),sQuery(id+"F0.wireOp",EDGE,"E676"),sQuery(id+"F0.wireOp",EDGE,"E677"),sQuery(id+"F0.wireOp",EDGE,"E678"),sQuery(id+"F0.wireOp",EDGE,"E679"),sQuery(id+"F0.wireOp",EDGE,"E680"),sQuery(id+"F0.wireOp",EDGE,"E681"),sQuery(id+"F0.wireOp",EDGE,"E682"),sQuery(id+"F0.wireOp",EDGE,"E683"),sQuery(id+"F0.wireOp",EDGE,"E684"),sQuery(id+"F0.wireOp",EDGE,"E685"),sQuery(id+"F0.wireOp",EDGE,"E686"),sQuery(id+"F0.wireOp",EDGE,"E687"),sQuery(id+"F0.wireOp",EDGE,"E688"),sQuery(id+"F0.wireOp",EDGE,"E689"),sQuery(id+"F0.wireOp",EDGE,"E690"),sQuery(id+"F0.wireOp",EDGE,"E691"),sQuery(id+"F0.wireOp",EDGE,"E692"),sQuery(id+"F0.wireOp",EDGE,"E693"),sQuery(id+"F0.wireOp",EDGE,"E694"),sQuery(id+"F0.wireOp",EDGE,"E695"),sQuery(id+"F0.wireOp",EDGE,"E696"),sQuery(id+"F0.wireOp",EDGE,"E697"),sQuery(id+"F0.wireOp",EDGE,"E698"),sQuery(id+"F0.wireOp",EDGE,"E699"),sQuery(id+"F0.wireOp",EDGE,"E700"),sQuery(id+"F0.wireOp",EDGE,"E701"),sQuery(id+"F0.wireOp",EDGE,"E702"),sQuery(id+"F0.wireOp",EDGE,"E703"),sQuery(id+"F0.wireOp",EDGE,"E704"),sQuery(id+"F0.wireOp",EDGE,"E705"),sQuery(id+"F0.wireOp",EDGE,"E706"),sQuery(id+"F0.wireOp",EDGE,"E707"),sQuery(id+"F0.wireOp",EDGE,"E708"),sQuery(id+"F0.wireOp",EDGE,"E709"),sQuery(id+"F0.wireOp",EDGE,"E710"),sQuery(id+"F0.wireOp",EDGE,"E711"),sQuery(id+"F0.wireOp",EDGE,"E712"),sQuery(id+"F0.wireOp",EDGE,"E713"),sQuery(id+"F0.wireOp",EDGE,"E714"),sQuery(id+"F0.wireOp",EDGE,"E715"),sQuery(id+"F0.wireOp",EDGE,"E716"),sQuery(id+"F0.wireOp",EDGE,"E717"),sQuery(id+"F0.wireOp",EDGE,"E718"),sQuery(id+"F0.wireOp",EDGE,"E719"),sQuery(id+"F0.wireOp",EDGE,"E720"),sQuery(id+"F0.wireOp",EDGE,"E721"),sQuery(id+"F0.wireOp",EDGE,"E722"),sQuery(id+"F0.wireOp",EDGE,"E723"),sQuery(id+"F0.wireOp",EDGE,"E724"),sQuery(id+"F0.wireOp",EDGE,"E725"),sQuery(id+"F0.wireOp",EDGE,"E726"),sQuery(id+"F0.wireOp",EDGE,"E727"),sQuery(id+"F0.wireOp",EDGE,"E728"),sQuery(id+"F0.wireOp",EDGE,"E729"),sQuery(id+"F0.wireOp",EDGE,"E730"),sQuery(id+"F0.wireOp",EDGE,"E731"),sQuery(id+"F0.wireOp",EDGE,"E732"),sQuery(id+"F0.wireOp",EDGE,"E733"),sQuery(id+"F0.wireOp",EDGE,"E734"),sQuery(id+"F0.wireOp",EDGE,"E735"),sQuery(id+"F0.wireOp",EDGE,"E736"),sQuery(id+"F0.wireOp",EDGE,"E737"),sQuery(id+"F0.wireOp",EDGE,"E738"),sQuery(id+"F0.wireOp",EDGE,"E739"),sQuery(id+"F0.wireOp",EDGE,"E740"),sQuery(id+"F0.wireOp",EDGE,"E741"),sQuery(id+"F0.wireOp",EDGE,"E742"),sQuery(id+"F0.wireOp",EDGE,"E743"),sQuery(id+"F0.wireOp",EDGE,"E744"),sQuery(id+"F0.wireOp",EDGE,"E745"),sQuery(id+"F0.wireOp",EDGE,"E746"),sQuery(id+"F0.wireOp",EDGE,"E747"),sQuery(id+"F0.wireOp",EDGE,"E748"),sQuery(id+"F0.wireOp",EDGE,"E749"),sQuery(id+"F0.wireOp",EDGE,"E750"),sQuery(id+"F0.wireOp",EDGE,"E751"),sQuery(id+"F0.wireOp",EDGE,"E752"),sQuery(id+"F0.wireOp",EDGE,"E753"),sQuery(id+"F0.wireOp",EDGE,"E754"),sQuery(id+"F0.wireOp",EDGE,"E755"),sQuery(id+"F0.wireOp",EDGE,"E756"),sQuery(id+"F0.wireOp",EDGE,"E757"),sQuery(id+"F0.wireOp",EDGE,"E758"),sQuery(id+"F0.wireOp",EDGE,"E759"),sQuery(id+"F0.wireOp",EDGE,"E760"),sQuery(id+"F0.wireOp",EDGE,"E761"),sQuery(id+"F0.wireOp",EDGE,"E762"),sQuery(id+"F0.wireOp",EDGE,"E763"),sQuery(id+"F0.wireOp",EDGE,"E764"),sQuery(id+"F0.wireOp",EDGE,"E765"),sQuery(id+"F0.wireOp",EDGE,"E766"),sQuery(id+"F0.wireOp",EDGE,"E767"),sQuery(id+"F0.wireOp",EDGE,"E768"),sQuery(id+"F0.wireOp",EDGE,"E769"),sQuery(id+"F0.wireOp",EDGE,"E770"),sQuery(id+"F0.wireOp",EDGE,"E771"),sQuery(id+"F0.wireOp",EDGE,"E772"),sQuery(id+"F0.wireOp",EDGE,"E773"),sQuery(id+"F0.wireOp",EDGE,"E774"),sQuery(id+"F0.wireOp",EDGE,"E775"),sQuery(id+"F0.wireOp",EDGE,"E776"),sQuery(id+"F0.wireOp",EDGE,"E777"),sQuery(id+"F0.wireOp",EDGE,"E778"),sQuery(id+"F0.wireOp",EDGE,"E779"),sQuery(id+"F0.wireOp",EDGE,"E780"),sQuery(id+"F0.wireOp",EDGE,"E781"),sQuery(id+"F0.wireOp",EDGE,"E782"),sQuery(id+"F0.wireOp",EDGE,"E783"),sQuery(id+"F0.wireOp",EDGE,"E784"),sQuery(id+"F0.wireOp",EDGE,"E785"),sQuery(id+"F0.wireOp",EDGE,"E786"),sQuery(id+"F0.wireOp",EDGE,"E787"),sQuery(id+"F0.wireOp",EDGE,"E788"),sQuery(id+"F0.wireOp",EDGE,"E789"),sQuery(id+"F0.wireOp",EDGE,"E790"),sQuery(id+"F0.wireOp",EDGE,"E791"),sQuery(id+"F0.wireOp",EDGE,"E792"),sQuery(id+"F0.wireOp",EDGE,"E793"),sQuery(id+"F0.wireOp",EDGE,"E794"),sQuery(id+"F0.wireOp",EDGE,"E795"),sQuery(id+"F0.wireOp",EDGE,"E796"),sQuery(id+"F0.wireOp",EDGE,"E797"),sQuery(id+"F0.wireOp",EDGE,"E798"),sQuery(id+"F0.wireOp",EDGE,"E799"),sQuery(id+"F0.wireOp",EDGE,"E800"),sQuery(id+"F0.wireOp",EDGE,"E801"),sQuery(id+"F0.wireOp",EDGE,"E802"),sQuery(id+"F0.wireOp",EDGE,"E803"),sQuery(id+"F0.wireOp",EDGE,"E804"),sQuery(id+"F0.wireOp",EDGE,"E805"),sQuery(id+"F0.wireOp",EDGE,"E806"),sQuery(id+"F0.wireOp",EDGE,"E807"),sQuery(id+"F0.wireOp",EDGE,"E808"),sQuery(id+"F0.wireOp",EDGE,"E809"),sQuery(id+"F0.wireOp",EDGE,"E810"),sQuery(id+"F0.wireOp",EDGE,"E811"),sQuery(id+"F0.wireOp",EDGE,"E812"),sQuery(id+"F0.wireOp",EDGE,"E813"),sQuery(id+"F0.wireOp",EDGE,"E814"),sQuery(id+"F0.wireOp",EDGE,"E815"),sQuery(id+"F0.wireOp",EDGE,"E816"),sQuery(id+"F0.wireOp",EDGE,"E817"),sQuery(id+"F0.wireOp",EDGE,"E818"),sQuery(id+"F0.wireOp",EDGE,"E819"),sQuery(id+"F0.wireOp",EDGE,"E820"),sQuery(id+"F0.wireOp",EDGE,"E821"),sQuery(id+"F0.wireOp",EDGE,"E822"),sQuery(id+"F0.wireOp",EDGE,"E823"),sQuery(id+"F0.wireOp",EDGE,"E824"),sQuery(id+"F0.wireOp",EDGE,"E825"),sQuery(id+"F0.wireOp",EDGE,"E826"),sQuery(id+"F0.wireOp",EDGE,"E827"),sQuery(id+"F0.wireOp",EDGE,"E828"),sQuery(id+"F0.wireOp",EDGE,"E829"),sQuery(id+"F0.wireOp",EDGE,"E830"),sQuery(id+"F0.wireOp",EDGE,"E831"),sQuery(id+"F0.wireOp",EDGE,"E832"),sQuery(id+"F0.wireOp",EDGE,"E833"),sQuery(id+"F0.wireOp",EDGE,"E834"),sQuery(id+"F0.wireOp",EDGE,"E835"),sQuery(id+"F0.wireOp",EDGE,"E836"),sQuery(id+"F0.wireOp",EDGE,"E837"),sQuery(id+"F0.wireOp",EDGE,"E838"),sQuery(id+"F0.wireOp",EDGE,"E839"),sQuery(id+"F0.wireOp",EDGE,"E840"),sQuery(id+"F0.wireOp",EDGE,"E841"),sQuery(id+"F0.wireOp",EDGE,"E842"),sQuery(id+"F0.wireOp",EDGE,"E843"),sQuery(id+"F0.wireOp",EDGE,"E844"),sQuery(id+"F0.wireOp",EDGE,"E845"),sQuery(id+"F0.wireOp",EDGE,"E846"),sQuery(id+"F0.wireOp",EDGE,"E847"),sQuery(id+"F0.wireOp",EDGE,"E848"),sQuery(id+"F0.wireOp",EDGE,"E849"),sQuery(id+"F0.wireOp",EDGE,"E850"),sQuery(id+"F0.wireOp",EDGE,"E851"),sQuery(id+"F0.wireOp",EDGE,"E852"),sQuery(id+"F0.wireOp",EDGE,"E853"),sQuery(id+"F0.wireOp",EDGE,"E854"),sQuery(id+"F0.wireOp",EDGE,"E855"),sQuery(id+"F0.wireOp",EDGE,"E856"),sQuery(id+"F0.wireOp",EDGE,"E857"),sQuery(id+"F0.wireOp",EDGE,"E858"),sQuery(id+"F0.wireOp",EDGE,"E859"),sQuery(id+"F0.wireOp",EDGE,"E860"),sQuery(id+"F0.wireOp",EDGE,"E861"),sQuery(id+"F0.wireOp",EDGE,"E862"),sQuery(id+"F0.wireOp",EDGE,"E863"),sQuery(id+"F0.wireOp",EDGE,"E864"),sQuery(id+"F0.wireOp",EDGE,"E865"),sQuery(id+"F0.wireOp",EDGE,"E866"),sQuery(id+"F0.wireOp",EDGE,"E867"),sQuery(id+"F0.wireOp",EDGE,"E868"),sQuery(id+"F0.wireOp",EDGE,"E869"),sQuery(id+"F0.wireOp",EDGE,"E870"),sQuery(id+"F0.wireOp",EDGE,"E871"),sQuery(id+"F0.wireOp",EDGE,"E872"),sQuery(id+"F0.wireOp",EDGE,"E873"),sQuery(id+"F0.wireOp",EDGE,"E874"),sQuery(id+"F0.wireOp",EDGE,"E875"),sQuery(id+"F0.wireOp",EDGE,"E876"),sQuery(id+"F0.wireOp",EDGE,"E877"),sQuery(id+"F0.wireOp",EDGE,"E878"),sQuery(id+"F0.wireOp",EDGE,"E879"),sQuery(id+"F0.wireOp",EDGE,"E880"),sQuery(id+"F0.wireOp",EDGE,"E881"),sQuery(id+"F0.wireOp",EDGE,"E882"),sQuery(id+"F0.wireOp",EDGE,"E883"),sQuery(id+"F0.wireOp",EDGE,"E884"),sQuery(id+"F0.wireOp",EDGE,"E885"),sQuery(id+"F0.wireOp",EDGE,"E886"),sQuery(id+"F0.wireOp",EDGE,"E887"),sQuery(id+"F0.wireOp",EDGE,"E888"),sQuery(id+"F0.wireOp",EDGE,"E889"),sQuery(id+"F0.wireOp",EDGE,"E890"),sQuery(id+"F0.wireOp",EDGE,"E891"),sQuery(id+"F0.wireOp",EDGE,"E892"),sQuery(id+"F0.wireOp",EDGE,"E893"),sQuery(id+"F0.wireOp",EDGE,"E894"),sQuery(id+"F0.wireOp",EDGE,"E895"),sQuery(id+"F0.wireOp",EDGE,"E896"),sQuery(id+"F0.wireOp",EDGE,"E897"),sQuery(id+"F0.wireOp",EDGE,"E898"),sQuery(id+"F0.wireOp",EDGE,"E899"),sQuery(id+"F0.wireOp",EDGE,"E900"),sQuery(id+"F0.wireOp",EDGE,"E901"),sQuery(id+"F0.wireOp",EDGE,"E902"),sQuery(id+"F0.wireOp",EDGE,"E903"),sQuery(id+"F0.wireOp",EDGE,"E904"),sQuery(id+"F0.wireOp",EDGE,"E905"),sQuery(id+"F0.wireOp",EDGE,"E906"),sQuery(id+"F0.wireOp",EDGE,"E907"),sQuery(id+"F0.wireOp",EDGE,"E908"),sQuery(id+"F0.wireOp",EDGE,"E909"),sQuery(id+"F0.wireOp",EDGE,"E910"),sQuery(id+"F0.wireOp",EDGE,"E911"),sQuery(id+"F0.wireOp",EDGE,"E912"),sQuery(id+"F0.wireOp",EDGE,"E913"),sQuery(id+"F0.wireOp",EDGE,"E914"),sQuery(id+"F0.wireOp",EDGE,"E915"),sQuery(id+"F0.wireOp",EDGE,"E916"),sQuery(id+"F0.wireOp",EDGE,"E917"),sQuery(id+"F0.wireOp",EDGE,"E918"),sQuery(id+"F0.wireOp",EDGE,"E919"),sQuery(id+"F0.wireOp",EDGE,"E920"),sQuery(id+"F0.wireOp",EDGE,"E921"),sQuery(id+"F0.wireOp",EDGE,"E922"),sQuery(id+"F0.wireOp",EDGE,"E923"),sQuery(id+"F0.wireOp",EDGE,"E924"),sQuery(id+"F0.wireOp",EDGE,"E925"),sQuery(id+"F0.wireOp",EDGE,"E926"),sQuery(id+"F0.wireOp",EDGE,"E927"),sQuery(id+"F0.wireOp",EDGE,"E928"),sQuery(id+"F0.wireOp",EDGE,"E929"),sQuery(id+"F0.wireOp",EDGE,"E930"),sQuery(id+"F0.wireOp",EDGE,"E931"),sQuery(id+"F0.wireOp",EDGE,"E932"),sQuery(id+"F0.wireOp",EDGE,"E933"),sQuery(id+"F0.wireOp",EDGE,"E934"),sQuery(id+"F0.wireOp",EDGE,"E935"),sQuery(id+"F0.wireOp",EDGE,"E936"),sQuery(id+"F0.wireOp",EDGE,"E937"),sQuery(id+"F0.wireOp",EDGE,"E938"),sQuery(id+"F0.wireOp",EDGE,"E939"),sQuery(id+"F0.wireOp",EDGE,"E940"),sQuery(id+"F0.wireOp",EDGE,"E941"),sQuery(id+"F0.wireOp",EDGE,"E942"),sQuery(id+"F0.wireOp",EDGE,"E943"),sQuery(id+"F0.wireOp",EDGE,"E944"),sQuery(id+"F0.wireOp",EDGE,"E945"),sQuery(id+"F0.wireOp",EDGE,"E946"),sQuery(id+"F0.wireOp",EDGE,"E947"),sQuery(id+"F0.wireOp",EDGE,"E948"),sQuery(id+"F0.wireOp",EDGE,"E949"),sQuery(id+"F0.wireOp",EDGE,"E950"),sQuery(id+"F0.wireOp",EDGE,"E951"),sQuery(id+"F0.wireOp",EDGE,"E952"),sQuery(id+"F0.wireOp",EDGE,"E953"),sQuery(id+"F0.wireOp",EDGE,"E954"),sQuery(id+"F0.wireOp",EDGE,"E955"),sQuery(id+"F0.wireOp",EDGE,"E956"),sQuery(id+"F0.wireOp",EDGE,"E957"),sQuery(id+"F0.wireOp",EDGE,"E958"),sQuery(id+"F0.wireOp",EDGE,"E959"),sQuery(id+"F0.wireOp",EDGE,"E960"),sQuery(id+"F0.wireOp",EDGE,"E961"),sQuery(id+"F0.wireOp",EDGE,"E962"),sQuery(id+"F0.wireOp",EDGE,"E963"),sQuery(id+"F0.wireOp",EDGE,"E964"),sQuery(id+"F0.wireOp",EDGE,"E965"),sQuery(id+"F0.wireOp",EDGE,"E966"),sQuery(id+"F0.wireOp",EDGE,"E967"),sQuery(id+"F0.wireOp",EDGE,"E968"),sQuery(id+"F0.wireOp",EDGE,"E969"),sQuery(id+"F0.wireOp",EDGE,"E970"),sQuery(id+"F0.wireOp",EDGE,"E971"),sQuery(id+"F0.wireOp",EDGE,"E972"),sQuery(id+"F0.wireOp",EDGE,"E973"),sQuery(id+"F0.wireOp",EDGE,"E974"),sQuery(id+"F0.wireOp",EDGE,"E975"),sQuery(id+"F0.wireOp",EDGE,"E976"),sQuery(id+"F0.wireOp",EDGE,"E977"),sQuery(id+"F0.wireOp",EDGE,"E978"),sQuery(id+"F0.wireOp",EDGE,"E979"),sQuery(id+"F0.wireOp",EDGE,"E980"),sQuery(id+"F0.wireOp",EDGE,"E981"),sQuery(id+"F0.wireOp",EDGE,"E982"),sQuery(id+"F0.wireOp",EDGE,"E983"),sQuery(id+"F0.wireOp",EDGE,"E984"),sQuery(id+"F0.wireOp",EDGE,"E985"),sQuery(id+"F0.wireOp",EDGE,"E986"),sQuery(id+"F0.wireOp",EDGE,"E987"),sQuery(id+"F0.wireOp",EDGE,"E988"),sQuery(id+"F0.wireOp",EDGE,"E989"),sQuery(id+"F0.wireOp",EDGE,"E990"),sQuery(id+"F0.wireOp",EDGE,"E991"),sQuery(id+"F0.wireOp",EDGE,"E992"),sQuery(id+"F0.wireOp",EDGE,"E993"),sQuery(id+"F0.wireOp",EDGE,"E994"),sQuery(id+"F0.wireOp",EDGE,"E995"),sQuery(id+"F0.wireOp",EDGE,"E996"),sQuery(id+"F0.wireOp",EDGE,"E997"),sQuery(id+"F0.wireOp",EDGE,"E998"),sQuery(id+"F0.wireOp",EDGE,"E999"),sQuery(id+"F0.wireOp",EDGE,"E1000"),sQuery(id+"F0.wireOp",EDGE,"E1001"),sQuery(id+"F0.wireOp",EDGE,"E1002"),sQuery(id+"F0.wireOp",EDGE,"E1003"),sQuery(id+"F0.wireOp",EDGE,"E1004"),sQuery(id+"F0.wireOp",EDGE,"E1005"),sQuery(id+"F0.wireOp",EDGE,"E1006"),sQuery(id+"F0.wireOp",EDGE,"E1007"),sQuery(id+"F0.wireOp",EDGE,"E1008"),sQuery(id+"F0.wireOp",EDGE,"E1009"),sQuery(id+"F0.wireOp",EDGE,"E1010"),sQuery(id+"F0.wireOp",EDGE,"E1011"),sQuery(id+"F0.wireOp",EDGE,"E1012"),sQuery(id+"F0.wireOp",EDGE,"E1013"),sQuery(id+"F0.wireOp",EDGE,"E1014"),sQuery(id+"F0.wireOp",EDGE,"E1015"),sQuery(id+"F0.wireOp",EDGE,"E1016"),sQuery(id+"F0.wireOp",EDGE,"E1017"),sQuery(id+"F0.wireOp",EDGE,"E1018"),sQuery(id+"F0.wireOp",EDGE,"E1019"),sQuery(id+"F0.wireOp",EDGE,"E1020"),sQuery(id+"F0.wireOp",EDGE,"E1021"),sQuery(id+"F0.wireOp",EDGE,"E1022"),sQuery(id+"F0.wireOp",EDGE,"E1023"),sQuery(id+"F0.wireOp",EDGE,"E1024"),sQuery(id+"F0.wireOp",EDGE,"E1025"),sQuery(id+"F0.wireOp",EDGE,"E1026"),sQuery(id+"F0.wireOp",EDGE,"E1027"),sQuery(id+"F0.wireOp",EDGE,"E1028"),sQuery(id+"F0.wireOp",EDGE,"E1029"),sQuery(id+"F0.wireOp",EDGE,"E1030"),sQuery(id+"F0.wireOp",EDGE,"E1031"),sQuery(id+"F0.wireOp",EDGE,"E1032"),sQuery(id+"F0.wireOp",EDGE,"E1033"),sQuery(id+"F0.wireOp",EDGE,"E1034"),sQuery(id+"F0.wireOp",EDGE,"E1035"),sQuery(id+"F0.wireOp",EDGE,"E1036"),sQuery(id+"F0.wireOp",EDGE,"E1037"),sQuery(id+"F0.wireOp",EDGE,"E1038"),sQuery(id+"F0.wireOp",EDGE,"E1039"),sQuery(id+"F0.wireOp",EDGE,"E1040"),sQuery(id+"F0.wireOp",EDGE,"E1041"),sQuery(id+"F0.wireOp",EDGE,"E1042"),sQuery(id+"F0.wireOp",EDGE,"E1043"),sQuery(id+"F0.wireOp",EDGE,"E1044"),sQuery(id+"F0.wireOp",EDGE,"E1045"),sQuery(id+"F0.wireOp",EDGE,"E1046"),sQuery(id+"F0.wireOp",EDGE,"E1047"),sQuery(id+"F0.wireOp",EDGE,"E1048"),sQuery(id+"F0.wireOp",EDGE,"E1049"),sQuery(id+"F0.wireOp",EDGE,"E1050"),sQuery(id+"F0.wireOp",EDGE,"E1051"),sQuery(id+"F0.wireOp",EDGE,"E1052"),sQuery(id+"F0.wireOp",EDGE,"E1053"),sQuery(id+"F0.wireOp",EDGE,"E1054"),sQuery(id+"F0.wireOp",EDGE,"E1055"),sQuery(id+"F0.wireOp",EDGE,"E1056"),sQuery(id+"F0.wireOp",EDGE,"E1057"),sQuery(id+"F0.wireOp",EDGE,"E1058"),sQuery(id+"F0.wireOp",EDGE,"E1059"),sQuery(id+"F0.wireOp",EDGE,"E1060"),sQuery(id+"F0.wireOp",EDGE,"E1061"),sQuery(id+"F0.wireOp",EDGE,"E1062"),sQuery(id+"F0.wireOp",EDGE,"E1063"),sQuery(id+"F0.wireOp",EDGE,"E1064"),sQuery(id+"F0.wireOp",EDGE,"E1065"),sQuery(id+"F0.wireOp",EDGE,"E1066"),sQuery(id+"F0.wireOp",EDGE,"E1067"),sQuery(id+"F0.wireOp",EDGE,"E1068"),sQuery(id+"F0.wireOp",EDGE,"E1069"),sQuery(id+"F0.wireOp",EDGE,"E1070"),sQuery(id+"F0.wireOp",EDGE,"E1071"),sQuery(id+"F0.wireOp",EDGE,"E1072"),sQuery(id+"F0.wireOp",EDGE,"E1073"),sQuery(id+"F0.wireOp",EDGE,"E1074"),sQuery(id+"F0.wireOp",EDGE,"E1075"),sQuery(id+"F0.wireOp",EDGE,"E1076"),sQuery(id+"F0.wireOp",EDGE,"E1077"),sQuery(id+"F0.wireOp",EDGE,"E1078"),sQuery(id+"F0.wireOp",EDGE,"E1079"),sQuery(id+"F0.wireOp",EDGE,"E1080"),sQuery(id+"F0.wireOp",EDGE,"E1081"),sQuery(id+"F0.wireOp",EDGE,"E1082"),sQuery(id+"F0.wireOp",EDGE,"E1083"),sQuery(id+"F0.wireOp",EDGE,"E1084"),sQuery(id+"F0.wireOp",EDGE,"E1085"),sQuery(id+"F0.wireOp",EDGE,"E1086"),sQuery(id+"F0.wireOp",EDGE,"E1087"),sQuery(id+"F0.wireOp",EDGE,"E1088"),sQuery(id+"F0.wireOp",EDGE,"E1089"),sQuery(id+"F0.wireOp",EDGE,"E1090"),sQuery(id+"F0.wireOp",EDGE,"E1091"),sQuery(id+"F0.wireOp",EDGE,"E1092"),sQuery(id+"F0.wireOp",EDGE,"E1093"),sQuery(id+"F0.wireOp",EDGE,"E1094"),sQuery(id+"F0.wireOp",EDGE,"E1095"),sQuery(id+"F0.wireOp",EDGE,"E1096"),sQuery(id+"F0.wireOp",EDGE,"E1097"),sQuery(id+"F0.wireOp",EDGE,"E1098"),sQuery(id+"F0.wireOp",EDGE,"E1099"),sQuery(id+"F0.wireOp",EDGE,"E1100"),sQuery(id+"F0.wireOp",EDGE,"E1101"),sQuery(id+"F0.wireOp",EDGE,"E1102"),sQuery(id+"F0.wireOp",EDGE,"E1103"),sQuery(id+"F0.wireOp",EDGE,"E1104"),sQuery(id+"F0.wireOp",EDGE,"E1105"),sQuery(id+"F0.wireOp",EDGE,"E1106"),sQuery(id+"F0.wireOp",EDGE,"E1107"),sQuery(id+"F0.wireOp",EDGE,"E1108"),sQuery(id+"F0.wireOp",EDGE,"E1109"),sQuery(id+"F0.wireOp",EDGE,"E1110"),sQuery(id+"F0.wireOp",EDGE,"E1111"),sQuery(id+"F0.wireOp",EDGE,"E1112"),sQuery(id+"F0.wireOp",EDGE,"E1113"),sQuery(id+"F0.wireOp",EDGE,"E1114"),sQuery(id+"F0.wireOp",EDGE,"E1115"),sQuery(id+"F0.wireOp",EDGE,"E1116"),sQuery(id+"F0.wireOp",EDGE,"E1117"),sQuery(id+"F0.wireOp",EDGE,"E1118"),sQuery(id+"F0.wireOp",EDGE,"E1119"),sQuery(id+"F0.wireOp",EDGE,"E1120"),sQuery(id+"F0.wireOp",EDGE,"E1121"),sQuery(id+"F0.wireOp",EDGE,"E1122"),sQuery(id+"F0.wireOp",EDGE,"E1123"),sQuery(id+"F0.wireOp",EDGE,"E1124"),sQuery(id+"F0.wireOp",EDGE,"E1125"),sQuery(id+"F0.wireOp",EDGE,"E1126"),sQuery(id+"F0.wireOp",EDGE,"E1127"),sQuery(id+"F0.wireOp",EDGE,"E1128"),sQuery(id+"F0.wireOp",EDGE,"E1129"),sQuery(id+"F0.wireOp",EDGE,"E1130"),sQuery(id+"F0.wireOp",EDGE,"E1131"),sQuery(id+"F0.wireOp",EDGE,"E1132"),sQuery(id+"F0.wireOp",EDGE,"E1133"),sQuery(id+"F0.wireOp",EDGE,"E1134"),sQuery(id+"F0.wireOp",EDGE,"E1135"),sQuery(id+"F0.wireOp",EDGE,"E1136"),sQuery(id+"F0.wireOp",EDGE,"E1137"),sQuery(id+"F0.wireOp",EDGE,"E1138"),sQuery(id+"F0.wireOp",EDGE,"E1138"),sQuery(id+"F0.wireOp",EDGE,"E1139"),sQuery(id+"F0.wireOp",EDGE,"E1140"),sQuery(id+"F0.wireOp",EDGE,"E1141"),sQuery(id+"F0.wireOp",EDGE,"E1142"),sQuery(id+"F0.wireOp",EDGE,"E1143"),sQuery(id+"F0.wireOp",EDGE,"E1144"),sQuery(id+"F0.wireOp",EDGE,"E1145"),sQuery(id+"F0.wireOp",EDGE,"E1146"),sQuery(id+"F0.wireOp",EDGE,"E1147"),sQuery(id+"F0.wireOp",EDGE,"E1148"),sQuery(id+"F0.wireOp",EDGE,"E1149"),sQuery(id+"F0.wireOp",EDGE,"E1150"),sQuery(id+"F0.wireOp",EDGE,"E1151"),sQuery(id+"F0.wireOp",EDGE,"E1152"),sQuery(id+"F0.wireOp",EDGE,"E1153"),sQuery(id+"F0.wireOp",EDGE,"E1154"),sQuery(id+"F0.wireOp",EDGE,"E1155"),sQuery(id+"F0.wireOp",EDGE,"E1156"),sQuery(id+"F0.wireOp",EDGE,"E1157"),sQuery(id+"F0.wireOp",EDGE,"E1158"),sQuery(id+"F0.wireOp",EDGE,"E1159"),sQuery(id+"F0.wireOp",EDGE,"E1160"),sQuery(id+"F0.wireOp",EDGE,"E1161"),sQuery(id+"F0.wireOp",EDGE,"E1162"),sQuery(id+"F0.wireOp",EDGE,"E1163"),sQuery(id+"F0.wireOp",EDGE,"E1164"),sQuery(id+"F0.wireOp",EDGE,"E1165"),sQuery(id+"F0.wireOp",EDGE,"E1166"),sQuery(id+"F0.wireOp",EDGE,"E1167"),sQuery(id+"F0.wireOp",EDGE,"E1168"),sQuery(id+"F0.wireOp",EDGE,"E1169"),sQuery(id+"F0.wireOp",EDGE,"E1170"),sQuery(id+"F0.wireOp",EDGE,"E1171"),sQuery(id+"F0.wireOp",EDGE,"E1172"),sQuery(id+"F0.wireOp",EDGE,"E1173"),sQuery(id+"F0.wireOp",EDGE,"E1174"),sQuery(id+"F0.wireOp",EDGE,"E1175"),sQuery(id+"F0.wireOp",EDGE,"E1176"),sQuery(id+"F0.wireOp",EDGE,"E1177"),sQuery(id+"F0.wireOp",EDGE,"E1178"),sQuery(id+"F0.wireOp",EDGE,"E1179"),sQuery(id+"F0.wireOp",EDGE,"E1180"),sQuery(id+"F0.wireOp",EDGE,"E1181"),sQuery(id+"F0.wireOp",EDGE,"E1182"),sQuery(id+"F0.wireOp",EDGE,"E1183"),sQuery(id+"F0.wireOp",EDGE,"E1184"),sQuery(id+"F0.wireOp",EDGE,"E1185"),sQuery(id+"F0.wireOp",EDGE,"E1186"),sQuery(id+"F0.wireOp",EDGE,"E1187"),sQuery(id+"F0.wireOp",EDGE,"E1188"),sQuery(id+"F0.wireOp",EDGE,"E1189"),sQuery(id+"F0.wireOp",EDGE,"E1190"),sQuery(id+"F0.wireOp",EDGE,"E1191"),sQuery(id+"F0.wireOp",EDGE,"E1192"),sQuery(id+"F0.wireOp",EDGE,"E1193"),sQuery(id+"F0.wireOp",EDGE,"E1194"),sQuery(id+"F0.wireOp",EDGE,"E1195"),sQuery(id+"F0.wireOp",EDGE,"E1196"),sQuery(id+"F0.wireOp",EDGE,"E1197"),sQuery(id+"F0.wireOp",EDGE,"E1198"),sQuery(id+"F0.wireOp",EDGE,"E1199"),sQuery(id+"F0.wireOp",EDGE,"E1200"),sQuery(id+"F0.wireOp",EDGE,"E1201"),sQuery(id+"F0.wireOp",EDGE,"E1202"),sQuery(id+"F0.wireOp",EDGE,"E1203"),sQuery(id+"F0.wireOp",EDGE,"E1204"),sQuery(id+"F0.wireOp",EDGE,"E1205"),sQuery(id+"F0.wireOp",EDGE,"E1206"),sQuery(id+"F0.wireOp",EDGE,"E1207"),sQuery(id+"F0.wireOp",EDGE,"E1208"),sQuery(id+"F0.wireOp",EDGE,"E1209"),sQuery(id+"F0.wireOp",EDGE,"E1210"),sQuery(id+"F0.wireOp",EDGE,"E1211"),sQuery(id+"F0.wireOp",EDGE,"E1212"),sQuery(id+"F0.wireOp",EDGE,"E1213"),sQuery(id+"F0.wireOp",EDGE,"E1214"),sQuery(id+"F0.wireOp",EDGE,"E1215"),sQuery(id+"F0.wireOp",EDGE,"E1216"),sQuery(id+"F0.wireOp",EDGE,"E1217"),sQuery(id+"F0.wireOp",EDGE,"E1218"),sQuery(id+"F0.wireOp",EDGE,"E1219"),sQuery(id+"F0.wireOp",EDGE,"E1220"),sQuery(id+"F0.wireOp",EDGE,"E1221"),sQuery(id+"F0.wireOp",EDGE,"E1222"),sQuery(id+"F0.wireOp",EDGE,"E1223"),sQuery(id+"F0.wireOp",EDGE,"E1224"),sQuery(id+"F0.wireOp",EDGE,"E1225"),sQuery(id+"F0.wireOp",EDGE,"E1226"),sQuery(id+"F0.wireOp",EDGE,"E1227"),sQuery(id+"F0.wireOp",EDGE,"E1228"),sQuery(id+"F0.wireOp",EDGE,"E1229"),sQuery(id+"F0.wireOp",EDGE,"E1230"),sQuery(id+"F0.wireOp",EDGE,"E1231"),sQuery(id+"F0.wireOp",EDGE,"E1232"),sQuery(id+"F0.wireOp",EDGE,"E1233"),sQuery(id+"F0.wireOp",EDGE,"E1234"),sQuery(id+"F0.wireOp",EDGE,"E1235"),sQuery(id+"F0.wireOp",EDGE,"E1236"),sQuery(id+"F0.wireOp",EDGE,"E1237"),sQuery(id+"F0.wireOp",EDGE,"E1238"),sQuery(id+"F0.wireOp",EDGE,"E1239"),sQuery(id+"F0.wireOp",EDGE,"E1240"),sQuery(id+"F0.wireOp",EDGE,"E1241"),sQuery(id+"F0.wireOp",EDGE,"E1242"),sQuery(id+"F0.wireOp",EDGE,"E1243"),sQuery(id+"F0.wireOp",EDGE,"E1244"),sQuery(id+"F0.wireOp",EDGE,"E1245"),sQuery(id+"F0.wireOp",EDGE,"E1246"),sQuery(id+"F0.wireOp",EDGE,"E1247"),sQuery(id+"F0.wireOp",EDGE,"E1248"),sQuery(id+"F0.wireOp",EDGE,"E1249"),sQuery(id+"F0.wireOp",EDGE,"E1250"),sQuery(id+"F0.wireOp",EDGE,"E1251"),sQuery(id+"F0.wireOp",EDGE,"E1252"),sQuery(id+"F0.wireOp",EDGE,"E1253"),sQuery(id+"F0.wireOp",EDGE,"E1254"),sQuery(id+"F0.wireOp",EDGE,"E1255"),sQuery(id+"F0.wireOp",EDGE,"E1256"),sQuery(id+"F0.wireOp",EDGE,"E1257"),sQuery(id+"F0.wireOp",EDGE,"E1258"),sQuery(id+"F0.wireOp",EDGE,"E1259"),sQuery(id+"F0.wireOp",EDGE,"E1260"),sQuery(id+"F0.wireOp",EDGE,"E1261"),sQuery(id+"F0.wireOp",EDGE,"E1262"),sQuery(id+"F0.wireOp",EDGE,"E1263"),sQuery(id+"F0.wireOp",EDGE,"E1264"),sQuery(id+"F0.wireOp",EDGE,"E1265"),sQuery(id+"F0.wireOp",EDGE,"E1266"),sQuery(id+"F0.wireOp",EDGE,"E1267"),sQuery(id+"F0.wireOp",EDGE,"E1268"),sQuery(id+"F0.wireOp",EDGE,"E1269"),sQuery(id+"F0.wireOp",EDGE,"E1270"),sQuery(id+"F0.wireOp",EDGE,"E1271"),sQuery(id+"F0.wireOp",EDGE,"E1272"),sQuery(id+"F0.wireOp",EDGE,"E1273"),sQuery(id+"F0.wireOp",EDGE,"E1274"),sQuery(id+"F0.wireOp",EDGE,"E1275"),sQuery(id+"F0.wireOp",EDGE,"E1276"),sQuery(id+"F0.wireOp",EDGE,"E1277"),sQuery(id+"F0.wireOp",EDGE,"E1278"),sQuery(id+"F0.wireOp",EDGE,"E1279"),sQuery(id+"F0.wireOp",EDGE,"E1280"),sQuery(id+"F0.wireOp",EDGE,"E1281"),sQuery(id+"F0.wireOp",EDGE,"E1282"),sQuery(id+"F0.wireOp",EDGE,"E1283"),sQuery(id+"F0.wireOp",EDGE,"E1284"),sQuery(id+"F0.wireOp",EDGE,"E1285"),sQuery(id+"F0.wireOp",EDGE,"E1286"),sQuery(id+"F0.wireOp",EDGE,"E1287"),sQuery(id+"F0.wireOp",EDGE,"E1288"),sQuery(id+"F0.wireOp",EDGE,"E1289"),sQuery(id+"F0.wireOp",EDGE,"E1290"),sQuery(id+"F0.wireOp",EDGE,"E1291"),sQuery(id+"F0.wireOp",EDGE,"E1292"),sQuery(id+"F0.wireOp",EDGE,"E1293"),sQuery(id+"F0.wireOp",EDGE,"E1294"),sQuery(id+"F0.wireOp",EDGE,"E1295"),sQuery(id+"F0.wireOp",EDGE,"E1296"),sQuery(id+"F0.wireOp",EDGE,"E1297"),sQuery(id+"F0.wireOp",EDGE,"E1298"),sQuery(id+"F0.wireOp",EDGE,"E1299"),sQuery(id+"F0.wireOp",EDGE,"E1300"),sQuery(id+"F0.wireOp",EDGE,"E1301"),sQuery(id+"F0.wireOp",EDGE,"E1302"),sQuery(id+"F0.wireOp",EDGE,"E1303"),sQuery(id+"F0.wireOp",EDGE,"E1304"),sQuery(id+"F0.wireOp",EDGE,"E1305"),sQuery(id+"F0.wireOp",EDGE,"E1306"),sQuery(id+"F0.wireOp",EDGE,"E1307"),sQuery(id+"F0.wireOp",EDGE,"E1308"),sQuery(id+"F0.wireOp",EDGE,"E1309"),sQuery(id+"F0.wireOp",EDGE,"E1310"),sQuery(id+"F0.wireOp",EDGE,"E1311"),sQuery(id+"F0.wireOp",EDGE,"E1312"),sQuery(id+"F0.wireOp",EDGE,"E1313"),sQuery(id+"F0.wireOp",EDGE,"E1314"),sQuery(id+"F0.wireOp",EDGE,"E1315"),sQuery(id+"F0.wireOp",EDGE,"E1316"),sQuery(id+"F0.wireOp",EDGE,"E1317"),sQuery(id+"F0.wireOp",EDGE,"E1318"),sQuery(id+"F0.wireOp",EDGE,"E1319"),sQuery(id+"F0.wireOp",EDGE,"E1320"),sQuery(id+"F0.wireOp",EDGE,"E1321"),sQuery(id+"F0.wireOp",EDGE,"E1322"),sQuery(id+"F0.wireOp",EDGE,"E1323"),sQuery(id+"F0.wireOp",EDGE,"E1324"),sQuery(id+"F0.wireOp",EDGE,"E1325"),sQuery(id+"F0.wireOp",EDGE,"E1326"),sQuery(id+"F0.wireOp",EDGE,"E1327"),sQuery(id+"F0.wireOp",EDGE,"E1328"),sQuery(id+"F0.wireOp",EDGE,"E1329"),sQuery(id+"F0.wireOp",EDGE,"E1330"),sQuery(id+"F0.wireOp",EDGE,"E1331"),sQuery(id+"F0.wireOp",EDGE,"E1332"),sQuery(id+"F0.wireOp",EDGE,"E1333"),sQuery(id+"F0.wireOp",EDGE,"E1334"),sQuery(id+"F0.wireOp",EDGE,"E1335"),sQuery(id+"F0.wireOp",EDGE,"E1336"),sQuery(id+"F0.wireOp",EDGE,"E1337"),sQuery(id+"F0.wireOp",EDGE,"E1338"),sQuery(id+"F0.wireOp",EDGE,"E1339"),sQuery(id+"F0.wireOp",EDGE,"E1340"),sQuery(id+"F0.wireOp",EDGE,"E1341"),sQuery(id+"F0.wireOp",EDGE,"E1342"),sQuery(id+"F0.wireOp",EDGE,"E1343"),sQuery(id+"F0.wireOp",EDGE,"E1344"),sQuery(id+"F0.wireOp",EDGE,"E1345"),sQuery(id+"F0.wireOp",EDGE,"E1346"),sQuery(id+"F0.wireOp",EDGE,"E1347"),sQuery(id+"F0.wireOp",EDGE,"E1348"),sQuery(id+"F0.wireOp",EDGE,"E1349"),sQuery(id+"F0.wireOp",EDGE,"E1350"),sQuery(id+"F0.wireOp",EDGE,"E1351"),sQuery(id+"F0.wireOp",EDGE,"E1352"),sQuery(id+"F0.wireOp",EDGE,"E1353"),sQuery(id+"F0.wireOp",EDGE,"E1354"),sQuery(id+"F0.wireOp",EDGE,"E1355"),sQuery(id+"F0.wireOp",EDGE,"E1356"),sQuery(id+"F0.wireOp",EDGE,"E1357"),sQuery(id+"F0.wireOp",EDGE,"E1358"),sQuery(id+"F0.wireOp",EDGE,"E1359"),sQuery(id+"F0.wireOp",EDGE,"E1360"),sQuery(id+"F0.wireOp",EDGE,"E1361"),sQuery(id+"F0.wireOp",EDGE,"E1362"),sQuery(id+"F0.wireOp",EDGE,"E1363"),sQuery(id+"F0.wireOp",EDGE,"E1364"),sQuery(id+"F0.wireOp",EDGE,"E1365"),sQuery(id+"F0.wireOp",EDGE,"E1366"),sQuery(id+"F0.wireOp",EDGE,"E1367"),sQuery(id+"F0.wireOp",EDGE,"E1368"),sQuery(id+"F0.wireOp",EDGE,"E1369"),sQuery(id+"F0.wireOp",EDGE,"E1370"),sQuery(id+"F0.wireOp",EDGE,"E1371"),sQuery(id+"F0.wireOp",EDGE,"E1372"),sQuery(id+"F0.wireOp",EDGE,"E1373"),sQuery(id+"F0.wireOp",EDGE,"E1374"),sQuery(id+"F0.wireOp",EDGE,"E1375"),sQuery(id+"F0.wireOp",EDGE,"E1376"),sQuery(id+"F0.wireOp",EDGE,"E1377"),sQuery(id+"F0.wireOp",EDGE,"E1378"),sQuery(id+"F0.wireOp",EDGE,"E1379"),sQuery(id+"F0.wireOp",EDGE,"E1380"),sQuery(id+"F0.wireOp",EDGE,"E1381"),sQuery(id+"F0.wireOp",EDGE,"E1382"),sQuery(id+"F0.wireOp",EDGE,"E1383"),sQuery(id+"F0.wireOp",EDGE,"E1384"),sQuery(id+"F0.wireOp",EDGE,"E1385"),sQuery(id+"F0.wireOp",EDGE,"E1386"),sQuery(id+"F0.wireOp",EDGE,"E1387"),sQuery(id+"F0.wireOp",EDGE,"E1388"),sQuery(id+"F0.wireOp",EDGE,"E1389"),sQuery(id+"F0.wireOp",EDGE,"E1390"),sQuery(id+"F0.wireOp",EDGE,"E1391"),sQuery(id+"F0.wireOp",EDGE,"E1392"),sQuery(id+"F0.wireOp",EDGE,"E1393"),sQuery(id+"F0.wireOp",EDGE,"E1394"),sQuery(id+"F0.wireOp",EDGE,"E1395"),sQuery(id+"F0.wireOp",EDGE,"E1396"),sQuery(id+"F0.wireOp",EDGE,"E1397"),sQuery(id+"F0.wireOp",EDGE,"E1398"),sQuery(id+"F0.wireOp",EDGE,"E1399"),sQuery(id+"F0.wireOp",EDGE,"E1400"),sQuery(id+"F0.wireOp",EDGE,"E1401"),sQuery(id+"F0.wireOp",EDGE,"E1402"),sQuery(id+"F0.wireOp",EDGE,"E1403"),sQuery(id+"F0.wireOp",EDGE,"E1404"),sQuery(id+"F0.wireOp",EDGE,"E1405"),sQuery(id+"F0.wireOp",EDGE,"E1406"),sQuery(id+"F0.wireOp",EDGE,"E1407"),sQuery(id+"F0.wireOp",EDGE,"E1408"),sQuery(id+"F0.wireOp",EDGE,"E1409"),sQuery(id+"F0.wireOp",EDGE,"E1410"),sQuery(id+"F0.wireOp",EDGE,"E1411"),sQuery(id+"F0.wireOp",EDGE,"E1412"),sQuery(id+"F0.wireOp",EDGE,"E1413"),sQuery(id+"F0.wireOp",EDGE,"E1414"),sQuery(id+"F0.wireOp",EDGE,"E1415"),sQuery(id+"F0.wireOp",EDGE,"E1416"),sQuery(id+"F0.wireOp",EDGE,"E1417"),sQuery(id+"F0.wireOp",EDGE,"E1418"),sQuery(id+"F0.wireOp",EDGE,"E1419"),sQuery(id+"F0.wireOp",EDGE,"E1420"),sQuery(id+"F0.wireOp",EDGE,"E1421"),sQuery(id+"F0.wireOp",EDGE,"E1422"),sQuery(id+"F0.wireOp",EDGE,"E1423"),sQuery(id+"F0.wireOp",EDGE,"E1424"),sQuery(id+"F0.wireOp",EDGE,"E1425"),sQuery(id+"F0.wireOp",EDGE,"E1426"),sQuery(id+"F0.wireOp",EDGE,"E1427"),sQuery(id+"F0.wireOp",EDGE,"E1428"),sQuery(id+"F0.wireOp",EDGE,"E1429"),sQuery(id+"F0.wireOp",EDGE,"E1430"),sQuery(id+"F0.wireOp",EDGE,"E1431"),sQuery(id+"F0.wireOp",EDGE,"E1432"),sQuery(id+"F0.wireOp",EDGE,"E1433"),sQuery(id+"F0.wireOp",EDGE,"E1434"),sQuery(id+"F0.wireOp",EDGE,"E1435"),sQuery(id+"F0.wireOp",EDGE,"E1436"),sQuery(id+"F0.wireOp",EDGE,"E1437"),sQuery(id+"F0.wireOp",EDGE,"E1438"),sQuery(id+"F0.wireOp",EDGE,"E1439"),sQuery(id+"F0.wireOp",EDGE,"E1440"),sQuery(id+"F0.wireOp",EDGE,"E1441"),sQuery(id+"F0.wireOp",EDGE,"E1442"),sQuery(id+"F0.wireOp",EDGE,"E1443"),sQuery(id+"F0.wireOp",EDGE,"E1444"),sQuery(id+"F0.wireOp",EDGE,"E1445"),sQuery(id+"F0.wireOp",EDGE,"E1446"),sQuery(id+"F0.wireOp",EDGE,"E1447"),sQuery(id+"F0.wireOp",EDGE,"E1448"),sQuery(id+"F0.wireOp",EDGE,"E1449"),sQuery(id+"F0.wireOp",EDGE,"E1450"),sQuery(id+"F0.wireOp",EDGE,"E1451"),sQuery(id+"F0.wireOp",EDGE,"E1452"),sQuery(id+"F0.wireOp",EDGE,"E1453"),sQuery(id+"F0.wireOp",EDGE,"E1454"),sQuery(id+"F0.wireOp",EDGE,"E1455"),sQuery(id+"F0.wireOp",EDGE,"E1456"),sQuery(id+"F0.wireOp",EDGE,"E1457"),sQuery(id+"F0.wireOp",EDGE,"E1458"),sQuery(id+"F0.wireOp",EDGE,"E1459"),sQuery(id+"F0.wireOp",EDGE,"E1460"),sQuery(id+"F0.wireOp",EDGE,"E1461"),sQuery(id+"F0.wireOp",EDGE,"E1462"),sQuery(id+"F0.wireOp",EDGE,"E1463"),sQuery(id+"F0.wireOp",EDGE,"E1464"),sQuery(id+"F0.wireOp",EDGE,"E1465"),sQuery(id+"F0.wireOp",EDGE,"E1466"),sQuery(id+"F0.wireOp",EDGE,"E1467"),sQuery(id+"F0.wireOp",EDGE,"E1468"),sQuery(id+"F0.wireOp",EDGE,"E1469"),sQuery(id+"F0.wireOp",EDGE,"E1470"),sQuery(id+"F0.wireOp",EDGE,"E1471"),sQuery(id+"F0.wireOp",EDGE,"E1472"),sQuery(id+"F0.wireOp",EDGE,"E1473"),sQuery(id+"F0.wireOp",EDGE,"E1474"),sQuery(id+"F0.wireOp",EDGE,"E1475"),sQuery(id+"F0.wireOp",EDGE,"E1476"),sQuery(id+"F0.wireOp",EDGE,"E1477"),sQuery(id+"F0.wireOp",EDGE,"E1478"),sQuery(id+"F0.wireOp",EDGE,"E1479"),sQuery(id+"F0.wireOp",EDGE,"E1480"),sQuery(id+"F0.wireOp",EDGE,"E1481"),sQuery(id+"F0.wireOp",EDGE,"E1482"),sQuery(id+"F0.wireOp",EDGE,"E1483"),sQuery(id+"F0.wireOp",EDGE,"E1484"),sQuery(id+"F0.wireOp",EDGE,"E1485"),sQuery(id+"F0.wireOp",EDGE,"E1486"),sQuery(id+"F0.wireOp",EDGE,"E1487"),sQuery(id+"F0.wireOp",EDGE,"E1488"),sQuery(id+"F0.wireOp",EDGE,"E1489"),sQuery(id+"F0.wireOp",EDGE,"E1490"),sQuery(id+"F0.wireOp",EDGE,"E1491"),sQuery(id+"F0.wireOp",EDGE,"E1492"),sQuery(id+"F0.wireOp",EDGE,"E1493"),sQuery(id+"F0.wireOp",EDGE,"E1494"),sQuery(id+"F0.wireOp",EDGE,"E1495"),sQuery(id+"F0.wireOp",EDGE,"E1496"),sQuery(id+"F0.wireOp",EDGE,"E1497"),sQuery(id+"F0.wireOp",EDGE,"E1498"),sQuery(id+"F0.wireOp",EDGE,"E1499"),sQuery(id+"F0.wireOp",EDGE,"E1500"),sQuery(id+"F0.wireOp",EDGE,"E1501"),sQuery(id+"F0.wireOp",EDGE,"E1502"),sQuery(id+"F0.wireOp",EDGE,"E1503"),sQuery(id+"F0.wireOp",EDGE,"E1504"),sQuery(id+"F0.wireOp",EDGE,"E1505"),sQuery(id+"F0.wireOp",EDGE,"E1506"),sQuery(id+"F0.wireOp",EDGE,"E1507"),sQuery(id+"F0.wireOp",EDGE,"E1508"),sQuery(id+"F0.wireOp",EDGE,"E1509"),sQuery(id+"F0.wireOp",EDGE,"E1510"),sQuery(id+"F0.wireOp",EDGE,"E1511"),sQuery(id+"F0.wireOp",EDGE,"E1512"),sQuery(id+"F0.wireOp",EDGE,"E1513"),sQuery(id+"F0.wireOp",EDGE,"E1514"),sQuery(id+"F0.wireOp",EDGE,"E1515"),sQuery(id+"F0.wireOp",EDGE,"E1516"),sQuery(id+"F0.wireOp",EDGE,"E1517"),sQuery(id+"F0.wireOp",EDGE,"E1518"),sQuery(id+"F0.wireOp",EDGE,"E1519"),sQuery(id+"F0.wireOp",EDGE,"E1520"),sQuery(id+"F0.wireOp",EDGE,"E1521"),sQuery(id+"F0.wireOp",EDGE,"E1522"),sQuery(id+"F0.wireOp",EDGE,"E1523"),sQuery(id+"F0.wireOp",EDGE,"E1524"),sQuery(id+"F0.wireOp",EDGE,"E1525"),sQuery(id+"F0.wireOp",EDGE,"E1526"),sQuery(id+"F0.wireOp",EDGE,"E1527"),sQuery(id+"F0.wireOp",EDGE,"E1528"),sQuery(id+"F0.wireOp",EDGE,"E1529"),sQuery(id+"F0.wireOp",EDGE,"E1530"),sQuery(id+"F0.wireOp",EDGE,"E1531"),sQuery(id+"F0.wireOp",EDGE,"E1532"),sQuery(id+"F0.wireOp",EDGE,"E1533"),sQuery(id+"F0.wireOp",EDGE,"E1534"),sQuery(id+"F0.wireOp",EDGE,"E1535"),sQuery(id+"F0.wireOp",EDGE,"E1536"),sQuery(id+"F0.wireOp",EDGE,"E1537"),sQuery(id+"F0.wireOp",EDGE,"E1538"),sQuery(id+"F0.wireOp",EDGE,"E1539"),sQuery(id+"F0.wireOp",EDGE,"E1540"),sQuery(id+"F0.wireOp",EDGE,"E1541"),sQuery(id+"F0.wireOp",EDGE,"E1542"),sQuery(id+"F0.wireOp",EDGE,"E1543"),sQuery(id+"F0.wireOp",EDGE,"E1544"),sQuery(id+"F0.wireOp",EDGE,"E1545"),sQuery(id+"F0.wireOp",EDGE,"E1546"),sQuery(id+"F0.wireOp",EDGE,"E1547"),sQuery(id+"F0.wireOp",EDGE,"E1548"),sQuery(id+"F0.wireOp",EDGE,"E1549"),sQuery(id+"F0.wireOp",EDGE,"E1550"),sQuery(id+"F0.wireOp",EDGE,"E1551"),sQuery(id+"F0.wireOp",EDGE,"E1552"),sQuery(id+"F0.wireOp",EDGE,"E1553"),sQuery(id+"F0.wireOp",EDGE,"E1554"),sQuery(id+"F0.wireOp",EDGE,"E1555"),sQuery(id+"F0.wireOp",EDGE,"E1556"),sQuery(id+"F0.wireOp",EDGE,"E1557"),sQuery(id+"F0.wireOp",EDGE,"E1558"),sQuery(id+"F0.wireOp",EDGE,"E1559"),sQuery(id+"F0.wireOp",EDGE,"E1560"),sQuery(id+"F0.wireOp",EDGE,"E1561"),sQuery(id+"F0.wireOp",EDGE,"E1562"),sQuery(id+"F0.wireOp",EDGE,"E1563"),sQuery(id+"F0.wireOp",EDGE,"E1564"),sQuery(id+"F0.wireOp",EDGE,"E1565"),sQuery(id+"F0.wireOp",EDGE,"E1566"),sQuery(id+"F0.wireOp",EDGE,"E1567"),sQuery(id+"F0.wireOp",EDGE,"E1568"),sQuery(id+"F0.wireOp",EDGE,"E1569"),sQuery(id+"F0.wireOp",EDGE,"E1570"),sQuery(id+"F0.wireOp",EDGE,"E1571"),sQuery(id+"F0.wireOp",EDGE,"E1572"),sQuery(id+"F0.wireOp",EDGE,"E1573"),sQuery(id+"F0.wireOp",EDGE,"E1574"),sQuery(id+"F0.wireOp",EDGE,"E1575"),sQuery(id+"F0.wireOp",EDGE,"E1576"),sQuery(id+"F0.wireOp",EDGE,"E1577"),sQuery(id+"F0.wireOp",EDGE,"E1578"),sQuery(id+"F0.wireOp",EDGE,"E1579"),sQuery(id+"F0.wireOp",EDGE,"E1580"),sQuery(id+"F0.wireOp",EDGE,"E1581"),sQuery(id+"F0.wireOp",EDGE,"E1582"),sQuery(id+"F0.wireOp",EDGE,"E1583"),sQuery(id+"F0.wireOp",EDGE,"E1584"),sQuery(id+"F0.wireOp",EDGE,"E1585"),sQuery(id+"F0.wireOp",EDGE,"E1586"),sQuery(id+"F0.wireOp",EDGE,"E1587"),sQuery(id+"F0.wireOp",EDGE,"E1588"),sQuery(id+"F0.wireOp",EDGE,"E1589"),sQuery(id+"F0.wireOp",EDGE,"E1590"),sQuery(id+"F0.wireOp",EDGE,"E1591"),sQuery(id+"F0.wireOp",EDGE,"E1592"),sQuery(id+"F0.wireOp",EDGE,"E1593"),sQuery(id+"F0.wireOp",EDGE,"E1594"),sQuery(id+"F0.wireOp",EDGE,"E1595"),sQuery(id+"F0.wireOp",EDGE,"E1596"),sQuery(id+"F0.wireOp",EDGE,"E1597"),sQuery(id+"F0.wireOp",EDGE,"E1598"),sQuery(id+"F0.wireOp",EDGE,"E1599"),sQuery(id+"F0.wireOp",EDGE,"E1600"),sQuery(id+"F0.wireOp",EDGE,"E1601"),sQuery(id+"F0.wireOp",EDGE,"E1602"),sQuery(id+"F0.wireOp",EDGE,"E1603"),sQuery(id+"F0.wireOp",EDGE,"E1604"),sQuery(id+"F0.wireOp",EDGE,"E1605"),sQuery(id+"F0.wireOp",EDGE,"E1606"),sQuery(id+"F0.wireOp",EDGE,"E1607"),sQuery(id+"F0.wireOp",EDGE,"E1608"),sQuery(id+"F0.wireOp",EDGE,"E1609"),sQuery(id+"F0.wireOp",EDGE,"E1610"),sQuery(id+"F0.wireOp",EDGE,"E1611"),sQuery(id+"F0.wireOp",EDGE,"E1612"),sQuery(id+"F0.wireOp",EDGE,"E1613"),sQuery(id+"F0.wireOp",EDGE,"E1614"),sQuery(id+"F0.wireOp",EDGE,"E1615"),sQuery(id+"F0.wireOp",EDGE,"E1616"),sQuery(id+"F0.wireOp",EDGE,"E1617"),sQuery(id+"F0.wireOp",EDGE,"E1618"),sQuery(id+"F0.wireOp",EDGE,"E1619"),sQuery(id+"F0.wireOp",EDGE,"E1620"),sQuery(id+"F0.wireOp",EDGE,"E1621"),sQuery(id+"F0.wireOp",EDGE,"E1622"),sQuery(id+"F0.wireOp",EDGE,"E1623"),sQuery(id+"F0.wireOp",EDGE,"E1624"),sQuery(id+"F0.wireOp",EDGE,"E1625"),sQuery(id+"F0.wireOp",EDGE,"E1626"),sQuery(id+"F0.wireOp",EDGE,"E1627"),sQuery(id+"F0.wireOp",EDGE,"E1628"),sQuery(id+"F0.wireOp",EDGE,"E1629"),sQuery(id+"F0.wireOp",EDGE,"E1630"),sQuery(id+"F0.wireOp",EDGE,"E1631"),sQuery(id+"F0.wireOp",EDGE,"E1632"),sQuery(id+"F0.wireOp",EDGE,"E1633"),sQuery(id+"F0.wireOp",EDGE,"E1634"),sQuery(id+"F0.wireOp",EDGE,"E1635"),sQuery(id+"F0.wireOp",EDGE,"E1636"),sQuery(id+"F0.wireOp",EDGE,"E1637"),sQuery(id+"F0.wireOp",EDGE,"E1638"),sQuery(id+"F0.wireOp",EDGE,"E1639"),sQuery(id+"F0.wireOp",EDGE,"E1640"),sQuery(id+"F0.wireOp",EDGE,"E1641"),sQuery(id+"F0.wireOp",EDGE,"E1642"),sQuery(id+"F0.wireOp",EDGE,"E1643"),sQuery(id+"F0.wireOp",EDGE,"E1644"),sQuery(id+"F0.wireOp",EDGE,"E1645"),sQuery(id+"F0.wireOp",EDGE,"E1646"),sQuery(id+"F0.wireOp",EDGE,"E1647"),sQuery(id+"F0.wireOp",EDGE,"E1648"),sQuery(id+"F0.wireOp",EDGE,"E1649"),sQuery(id+"F0.wireOp",EDGE,"E1650"),sQuery(id+"F0.wireOp",EDGE,"E1651"),sQuery(id+"F0.wireOp",EDGE,"E1652"),sQuery(id+"F0.wireOp",EDGE,"E1653"),sQuery(id+"F0.wireOp",EDGE,"E1654"),sQuery(id+"F0.wireOp",EDGE,"E1655"),sQuery(id+"F0.wireOp",EDGE,"E1656"),sQuery(id+"F0.wireOp",EDGE,"E1657"),sQuery(id+"F0.wireOp",EDGE,"E1658"),sQuery(id+"F0.wireOp",EDGE,"E1659"),sQuery(id+"F0.wireOp",EDGE,"E1660"),sQuery(id+"F0.wireOp",EDGE,"E1661"),sQuery(id+"F0.wireOp",EDGE,"E1662"),sQuery(id+"F0.wireOp",EDGE,"E1663"),sQuery(id+"F0.wireOp",EDGE,"E1664"),sQuery(id+"F0.wireOp",EDGE,"E1665"),sQuery(id+"F0.wireOp",EDGE,"E1666"),sQuery(id+"F0.wireOp",EDGE,"E1667"),sQuery(id+"F0.wireOp",EDGE,"E1668"),sQuery(id+"F0.wireOp",EDGE,"E1669"),sQuery(id+"F0.wireOp",EDGE,"E1670"),sQuery(id+"F0.wireOp",EDGE,"E1671"),sQuery(id+"F0.wireOp",EDGE,"E1672"),sQuery(id+"F0.wireOp",EDGE,"E1673"),sQuery(id+"F0.wireOp",EDGE,"E1674"),sQuery(id+"F0.wireOp",EDGE,"E1675"),sQuery(id+"F0.wireOp",EDGE,"E1676"),sQuery(id+"F0.wireOp",EDGE,"E1677"),sQuery(id+"F0.wireOp",EDGE,"E1678"),sQuery(id+"F0.wireOp",EDGE,"E1679"),sQuery(id+"F0.wireOp",EDGE,"E1680"),sQuery(id+"F0.wireOp",EDGE,"E1681"),sQuery(id+"F0.wireOp",EDGE,"E1682"),sQuery(id+"F0.wireOp",EDGE,"E1683"),sQuery(id+"F0.wireOp",EDGE,"E1684"),sQuery(id+"F0.wireOp",EDGE,"E1685"),sQuery(id+"F0.wireOp",EDGE,"E1686"),sQuery(id+"F0.wireOp",EDGE,"E1687"),sQuery(id+"F0.wireOp",EDGE,"E1688"),sQuery(id+"F0.wireOp",EDGE,"E1689"),sQuery(id+"F0.wireOp",EDGE,"E1690"),sQuery(id+"F0.wireOp",EDGE,"E1691"),sQuery(id+"F0.wireOp",EDGE,"E1692"),sQuery(id+"F0.wireOp",EDGE,"E1693"),sQuery(id+"F0.wireOp",EDGE,"E1694"),sQuery(id+"F0.wireOp",EDGE,"E1695"),sQuery(id+"F0.wireOp",EDGE,"E1696"),sQuery(id+"F0.wireOp",EDGE,"E1697"),sQuery(id+"F0.wireOp",EDGE,"E1698"),sQuery(id+"F0.wireOp",EDGE,"E1699"),sQuery(id+"F0.wireOp",EDGE,"E1700"),sQuery(id+"F0.wireOp",EDGE,"E1701"),sQuery(id+"F0.wireOp",EDGE,"E1702"),sQuery(id+"F0.wireOp",EDGE,"E1703"),sQuery(id+"F0.wireOp",EDGE,"E1704"),sQuery(id+"F0.wireOp",EDGE,"E1705"),sQuery(id+"F0.wireOp",EDGE,"E1706"),sQuery(id+"F0.wireOp",EDGE,"E1707"),sQuery(id+"F0.wireOp",EDGE,"E1708"),sQuery(id+"F0.wireOp",EDGE,"E1709"),sQuery(id+"F0.wireOp",EDGE,"E1710"),sQuery(id+"F0.wireOp",EDGE,"E1711"),sQuery(id+"F0.wireOp",EDGE,"E1712"),sQuery(id+"F0.wireOp",EDGE,"E1713"),sQuery(id+"F0.wireOp",EDGE,"E1714"),sQuery(id+"F0.wireOp",EDGE,"E1715"),sQuery(id+"F0.wireOp",EDGE,"E1716"),sQuery(id+"F0.wireOp",EDGE,"E1717"),sQuery(id+"F0.wireOp",EDGE,"E1718"),sQuery(id+"F0.wireOp",EDGE,"E1719"),sQuery(id+"F0.wireOp",EDGE,"E1720"),sQuery(id+"F0.wireOp",EDGE,"E1721"),sQuery(id+"F0.wireOp",EDGE,"E1722"),sQuery(id+"F0.wireOp",EDGE,"E1723"),sQuery(id+"F0.wireOp",EDGE,"E1724"),sQuery(id+"F0.wireOp",EDGE,"E1725"),sQuery(id+"F0.wireOp",EDGE,"E1726"),sQuery(id+"F0.wireOp",EDGE,"E1727"),sQuery(id+"F0.wireOp",EDGE,"E1728"),sQuery(id+"F0.wireOp",EDGE,"E1729"),sQuery(id+"F0.wireOp",EDGE,"E1730"),sQuery(id+"F0.wireOp",EDGE,"E1731"),sQuery(id+"F0.wireOp",EDGE,"E1732"),sQuery(id+"F0.wireOp",EDGE,"E1733"),sQuery(id+"F0.wireOp",EDGE,"E1734"),sQuery(id+"F0.wireOp",EDGE,"E1735"),sQuery(id+"F0.wireOp",EDGE,"E1736"),sQuery(id+"F0.wireOp",EDGE,"E1737"),sQuery(id+"F0.wireOp",EDGE,"E1738"),sQuery(id+"F0.wireOp",EDGE,"E1739"),sQuery(id+"F0.wireOp",EDGE,"E1740"),sQuery(id+"F0.wireOp",EDGE,"E1741"),sQuery(id+"F0.wireOp",EDGE,"E1742"),sQuery(id+"F0.wireOp",EDGE,"E1743"),sQuery(id+"F0.wireOp",EDGE,"E1744"),sQuery(id+"F0.wireOp",EDGE,"E1745"),sQuery(id+"F0.wireOp",EDGE,"E1746"),sQuery(id+"F0.wireOp",EDGE,"E1747"),sQuery(id+"F0.wireOp",EDGE,"E1748"),sQuery(id+"F0.wireOp",EDGE,"E1749"),sQuery(id+"F0.wireOp",EDGE,"E1750"),sQuery(id+"F0.wireOp",EDGE,"E1751"),sQuery(id+"F0.wireOp",EDGE,"E1752"),sQuery(id+"F0.wireOp",EDGE,"E1753"),sQuery(id+"F0.wireOp",EDGE,"E1754"),sQuery(id+"F0.wireOp",EDGE,"E1755"),sQuery(id+"F0.wireOp",EDGE,"E1756"),sQuery(id+"F0.wireOp",EDGE,"E1757"),sQuery(id+"F0.wireOp",EDGE,"E1758"),sQuery(id+"F0.wireOp",EDGE,"E1759"),sQuery(id+"F0.wireOp",EDGE,"E1760"),sQuery(id+"F0.wireOp",EDGE,"E1761"),sQuery(id+"F0.wireOp",EDGE,"E1762"),sQuery(id+"F0.wireOp",EDGE,"E1763"),sQuery(id+"F0.wireOp",EDGE,"E1764"),sQuery(id+"F0.wireOp",EDGE,"E1765"),sQuery(id+"F0.wireOp",EDGE,"E1766"),sQuery(id+"F0.wireOp",EDGE,"E1767"),sQuery(id+"F0.wireOp",EDGE,"E1768"),sQuery(id+"F0.wireOp",EDGE,"E1769"),sQuery(id+"F0.wireOp",EDGE,"E1770"),sQuery(id+"F0.wireOp",EDGE,"E1771"),sQuery(id+"F0.wireOp",EDGE,"E1772"),sQuery(id+"F0.wireOp",EDGE,"E1773"),sQuery(id+"F0.wireOp",EDGE,"E1774"),sQuery(id+"F0.wireOp",EDGE,"E1775"),sQuery(id+"F0.wireOp",EDGE,"E1776"),sQuery(id+"F0.wireOp",EDGE,"E1777"),sQuery(id+"F0.wireOp",EDGE,"E1778"),sQuery(id+"F0.wireOp",EDGE,"E1779"),sQuery(id+"F0.wireOp",EDGE,"E1780"),sQuery(id+"F0.wireOp",EDGE,"E1781"),sQuery(id+"F0.wireOp",EDGE,"E1782"),sQuery(id+"F0.wireOp",EDGE,"E1783"),sQuery(id+"F0.wireOp",EDGE,"E1784"),sQuery(id+"F0.wireOp",EDGE,"E1785"),sQuery(id+"F0.wireOp",EDGE,"E1786"),sQuery(id+"F0.wireOp",EDGE,"E1787"),sQuery(id+"F0.wireOp",EDGE,"E1788"),sQuery(id+"F0.wireOp",EDGE,"E1789"),sQuery(id+"F0.wireOp",EDGE,"E1790"),sQuery(id+"F0.wireOp",EDGE,"E1791"),sQuery(id+"F0.wireOp",EDGE,"E1792"),sQuery(id+"F0.wireOp",EDGE,"E1793"),sQuery(id+"F0.wireOp",EDGE,"E1794"),sQuery(id+"F0.wireOp",EDGE,"E1795"),sQuery(id+"F0.wireOp",EDGE,"E1796"),sQuery(id+"F0.wireOp",EDGE,"E1797"),sQuery(id+"F0.wireOp",EDGE,"E1798"),sQuery(id+"F0.wireOp",EDGE,"E1799"),sQuery(id+"F0.wireOp",EDGE,"E1800"),sQuery(id+"F0.wireOp",EDGE,"E1801"),sQuery(id+"F0.wireOp",EDGE,"E1802"),sQuery(id+"F0.wireOp",EDGE,"E1803"),sQuery(id+"F0.wireOp",EDGE,"E1804"),sQuery(id+"F0.wireOp",EDGE,"E1805"),sQuery(id+"F0.wireOp",EDGE,"E1806"),sQuery(id+"F0.wireOp",EDGE,"E1807"),sQuery(id+"F0.wireOp",EDGE,"E1808"),sQuery(id+"F0.wireOp",EDGE,"E1809"),sQuery(id+"F0.wireOp",EDGE,"E1810"),sQuery(id+"F0.wireOp",EDGE,"E1811"),sQuery(id+"F0.wireOp",EDGE,"E1812"),sQuery(id+"F0.wireOp",EDGE,"E1813"),sQuery(id+"F0.wireOp",EDGE,"E1814"),sQuery(id+"F0.wireOp",EDGE,"E1815"),sQuery(id+"F0.wireOp",EDGE,"E1816"),sQuery(id+"F0.wireOp",EDGE,"E1817"),sQuery(id+"F0.wireOp",EDGE,"E1818"),sQuery(id+"F0.wireOp",EDGE,"E1819"),sQuery(id+"F0.wireOp",EDGE,"E1820"),sQuery(id+"F0.wireOp",EDGE,"E1821"),sQuery(id+"F0.wireOp",EDGE,"E1822"),sQuery(id+"F0.wireOp",EDGE,"E1823"),sQuery(id+"F0.wireOp",EDGE,"E1824"),sQuery(id+"F0.wireOp",EDGE,"E1825"),sQuery(id+"F0.wireOp",EDGE,"E1826"),sQuery(id+"F0.wireOp",EDGE,"E1827"),sQuery(id+"F0.wireOp",EDGE,"E1828"),sQuery(id+"F0.wireOp",EDGE,"E1829"),sQuery(id+"F0.wireOp",EDGE,"E1830"),sQuery(id+"F0.wireOp",EDGE,"E1831"),sQuery(id+"F0.wireOp",EDGE,"E1832"),sQuery(id+"F0.wireOp",EDGE,"E1833"),sQuery(id+"F0.wireOp",EDGE,"E1834"),sQuery(id+"F0.wireOp",EDGE,"E1835"),sQuery(id+"F0.wireOp",EDGE,"E1836"),sQuery(id+"F0.wireOp",EDGE,"E1837"),sQuery(id+"F0.wireOp",EDGE,"E1838"),sQuery(id+"F0.wireOp",EDGE,"E1839"),sQuery(id+"F0.wireOp",EDGE,"E1840"),sQuery(id+"F0.wireOp",EDGE,"E1841"),sQuery(id+"F0.wireOp",EDGE,"E1842"),sQuery(id+"F0.wireOp",EDGE,"E1843"),sQuery(id+"F0.wireOp",EDGE,"E1844"),sQuery(id+"F0.wireOp",EDGE,"E1845"),sQuery(id+"F0.wireOp",EDGE,"E1846"),sQuery(id+"F0.wireOp",EDGE,"E1847"),sQuery(id+"F0.wireOp",EDGE,"E1848"),sQuery(id+"F0.wireOp",EDGE,"E1849"),sQuery(id+"F0.wireOp",EDGE,"E1850"),sQuery(id+"F0.wireOp",EDGE,"E1851"),sQuery(id+"F0.wireOp",EDGE,"E1852"),sQuery(id+"F0.wireOp",EDGE,"E1853"),sQuery(id+"F0.wireOp",EDGE,"E1854"),sQuery(id+"F0.wireOp",EDGE,"E1855"),sQuery(id+"F0.wireOp",EDGE,"E1856"),sQuery(id+"F0.wireOp",EDGE,"E1857"),sQuery(id+"F0.wireOp",EDGE,"E1858"),sQuery(id+"F0.wireOp",EDGE,"E1859"),sQuery(id+"F0.wireOp",EDGE,"E1860"),sQuery(id+"F0.wireOp",EDGE,"E1861"),sQuery(id+"F0.wireOp",EDGE,"E1862"),sQuery(id+"F0.wireOp",EDGE,"E1863"),sQuery(id+"F0.wireOp",EDGE,"E1864"),sQuery(id+"F0.wireOp",EDGE,"E1865"),sQuery(id+"F0.wireOp",EDGE,"E1866"),sQuery(id+"F0.wireOp",EDGE,"E1867"),sQuery(id+"F0.wireOp",EDGE,"E1868"),sQuery(id+"F0.wireOp",EDGE,"E1869"),sQuery(id+"F0.wireOp",EDGE,"E1870"),sQuery(id+"F0.wireOp",EDGE,"E1871"),sQuery(id+"F0.wireOp",EDGE,"E1872"),sQuery(id+"F0.wireOp",EDGE,"E1873"),sQuery(id+"F0.wireOp",EDGE,"E1874"),sQuery(id+"F0.wireOp",EDGE,"E1875"),sQuery(id+"F0.wireOp",EDGE,"E1876"),sQuery(id+"F0.wireOp",EDGE,"E1877"),sQuery(id+"F0.wireOp",EDGE,"E1878"),sQuery(id+"F0.wireOp",EDGE,"E1879"),sQuery(id+"F0.wireOp",EDGE,"E1880"),sQuery(id+"F0.wireOp",EDGE,"E1881"),sQuery(id+"F0.wireOp",EDGE,"E1882"),sQuery(id+"F0.wireOp",EDGE,"E1883"),sQuery(id+"F0.wireOp",EDGE,"E1884"),sQuery(id+"F0.wireOp",EDGE,"E1885"),sQuery(id+"F0.wireOp",EDGE,"E1886"),sQuery(id+"F0.wireOp",EDGE,"E1887"),sQuery(id+"F0.wireOp",EDGE,"E1888"),sQuery(id+"F0.wireOp",EDGE,"E1889"),sQuery(id+"F0.wireOp",EDGE,"E1890"),sQuery(id+"F0.wireOp",EDGE,"E1891"),sQuery(id+"F0.wireOp",EDGE,"E1892"),sQuery(id+"F0.wireOp",EDGE,"E1893"),sQuery(id+"F0.wireOp",EDGE,"E1894"),sQuery(id+"F0.wireOp",EDGE,"E1895"),sQuery(id+"F0.wireOp",EDGE,"E1896"),sQuery(id+"F0.wireOp",EDGE,"E1897"),sQuery(id+"F0.wireOp",EDGE,"E1898"),sQuery(id+"F0.wireOp",EDGE,"E1899"),sQuery(id+"F0.wireOp",EDGE,"E1900"),sQuery(id+"F0.wireOp",EDGE,"E1901"),sQuery(id+"F0.wireOp",EDGE,"E1902"),sQuery(id+"F0.wireOp",EDGE,"E1903"),sQuery(id+"F0.wireOp",EDGE,"E1904"),sQuery(id+"F0.wireOp",EDGE,"E1905"),sQuery(id+"F0.wireOp",EDGE,"E1906"),sQuery(id+"F0.wireOp",EDGE,"E1907"),sQuery(id+"F0.wireOp",EDGE,"E1908"),sQuery(id+"F0.wireOp",EDGE,"E1909"),sQuery(id+"F0.wireOp",EDGE,"E1910"),sQuery(id+"F0.wireOp",EDGE,"E1911"),sQuery(id+"F0.wireOp",EDGE,"E1912"),sQuery(id+"F0.wireOp",EDGE,"E1913"),sQuery(id+"F0.wireOp",EDGE,"E1914"),sQuery(id+"F0.wireOp",EDGE,"E1915"),sQuery(id+"F0.wireOp",EDGE,"E1916"),sQuery(id+"F0.wireOp",EDGE,"E1917"),sQuery(id+"F0.wireOp",EDGE,"E1918"),sQuery(id+"F0.wireOp",EDGE,"E1919"),sQuery(id+"F0.wireOp",EDGE,"E1920"),sQuery(id+"F0.wireOp",EDGE,"E1921"),sQuery(id+"F0.wireOp",EDGE,"E1922"),sQuery(id+"F0.wireOp",EDGE,"E1923"),sQuery(id+"F0.wireOp",EDGE,"E1924"),sQuery(id+"F0.wireOp",EDGE,"E1925"),sQuery(id+"F0.wireOp",EDGE,"E1926"),sQuery(id+"F0.wireOp",EDGE,"E1927"),sQuery(id+"F0.wireOp",EDGE,"E1928"),sQuery(id+"F0.wireOp",EDGE,"E1929"),sQuery(id+"F0.wireOp",EDGE,"E1930"),sQuery(id+"F0.wireOp",EDGE,"E1931"),sQuery(id+"F0.wireOp",EDGE,"E1932"),sQuery(id+"F0.wireOp",EDGE,"E1933"),sQuery(id+"F0.wireOp",EDGE,"E1934"),sQuery(id+"F0.wireOp",EDGE,"E1935"),sQuery(id+"F0.wireOp",EDGE,"E1936"),sQuery(id+"F0.wireOp",EDGE,"E1937"),sQuery(id+"F0.wireOp",EDGE,"E1938"),sQuery(id+"F0.wireOp",EDGE,"E1939"),sQuery(id+"F0.wireOp",EDGE,"E1940"),sQuery(id+"F0.wireOp",EDGE,"E1941"),sQuery(id+"F0.wireOp",EDGE,"E1942"),sQuery(id+"F0.wireOp",EDGE,"E1943"),sQuery(id+"F0.wireOp",EDGE,"E1944"),sQuery(id+"F0.wireOp",EDGE,"E1945"),sQuery(id+"F0.wireOp",EDGE,"E1946"),sQuery(id+"F0.wireOp",EDGE,"E1947"),sQuery(id+"F0.wireOp",EDGE,"E1948"),sQuery(id+"F0.wireOp",EDGE,"E1949"),sQuery(id+"F0.wireOp",EDGE,"E1950"),sQuery(id+"F0.wireOp",EDGE,"E1951"),sQuery(id+"F0.wireOp",EDGE,"E1952"),sQuery(id+"F0.wireOp",EDGE,"E1953"),sQuery(id+"F0.wireOp",EDGE,"E1954"),sQuery(id+"F0.wireOp",EDGE,"E1955"),sQuery(id+"F0.wireOp",EDGE,"E1956"),sQuery(id+"F0.wireOp",EDGE,"E1957"),sQuery(id+"F0.wireOp",EDGE,"E1958"),sQuery(id+"F0.wireOp",EDGE,"E1959"),sQuery(id+"F0.wireOp",EDGE,"E1960"),sQuery(id+"F0.wireOp",EDGE,"E1961"),sQuery(id+"F0.wireOp",EDGE,"E1962"),sQuery(id+"F0.wireOp",EDGE,"E1963"),sQuery(id+"F0.wireOp",EDGE,"E1964"),sQuery(id+"F0.wireOp",EDGE,"E1965"),sQuery(id+"F0.wireOp",EDGE,"E1966"),sQuery(id+"F0.wireOp",EDGE,"E1967"),sQuery(id+"F0.wireOp",EDGE,"E1968"),sQuery(id+"F0.wireOp",EDGE,"E1969"),sQuery(id+"F0.wireOp",EDGE,"E1970"),sQuery(id+"F0.wireOp",EDGE,"E1971"),sQuery(id+"F0.wireOp",EDGE,"E1972"),sQuery(id+"F0.wireOp",EDGE,"E1973"),sQuery(id+"F0.wireOp",EDGE,"E1974"),sQuery(id+"F0.wireOp",EDGE,"E1975"),sQuery(id+"F0.wireOp",EDGE,"E1976"),sQuery(id+"F0.wireOp",EDGE,"E1977"),sQuery(id+"F0.wireOp",EDGE,"E1978"),sQuery(id+"F0.wireOp",EDGE,"E1979"),sQuery(id+"F0.wireOp",EDGE,"E1980"),sQuery(id+"F0.wireOp",EDGE,"E1981"),sQuery(id+"F0.wireOp",EDGE,"E1982"),sQuery(id+"F0.wireOp",EDGE,"E1983"),sQuery(id+"F0.wireOp",EDGE,"E1984"),sQuery(id+"F0.wireOp",EDGE,"E1985"),sQuery(id+"F0.wireOp",EDGE,"E1986"),sQuery(id+"F0.wireOp",EDGE,"E1987"),sQuery(id+"F0.wireOp",EDGE,"E1988"),sQuery(id+"F0.wireOp",EDGE,"E1989"),sQuery(id+"F0.wireOp",EDGE,"E1990"),sQuery(id+"F0.wireOp",EDGE,"E1991"),sQuery(id+"F0.wireOp",EDGE,"E1992"),sQuery(id+"F0.wireOp",EDGE,"E1993"),sQuery(id+"F0.wireOp",EDGE,"E1994"),sQuery(id+"F0.wireOp",EDGE,"E1995"),sQuery(id+"F0.wireOp",EDGE,"E1996"),sQuery(id+"F0.wireOp",EDGE,"E1997"),sQuery(id+"F0.wireOp",EDGE,"E1998"),sQuery(id+"F0.wireOp",EDGE,"E1999"),sQuery(id+"F0.wireOp",EDGE,"E2000"),sQuery(id+"F0.wireOp",EDGE,"E2001"),sQuery(id+"F0.wireOp",EDGE,"E2002"),sQuery(id+"F0.wireOp",EDGE,"E2003"),sQuery(id+"F0.wireOp",EDGE,"E2004"),sQuery(id+"F0.wireOp",EDGE,"E2005"),sQuery(id+"F0.wireOp",EDGE,"E2006"),sQuery(id+"F0.wireOp",EDGE,"E2007"),sQuery(id+"F0.wireOp",EDGE,"E2008"),sQuery(id+"F0.wireOp",EDGE,"E2009"),sQuery(id+"F0.wireOp",EDGE,"E2010"),sQuery(id+"F0.wireOp",EDGE,"E2011"),sQuery(id+"F0.wireOp",EDGE,"E2012"),sQuery(id+"F0.wireOp",EDGE,"E2013"),sQuery(id+"F0.wireOp",EDGE,"E2014"),sQuery(id+"F0.wireOp",EDGE,"E2015"),sQuery(id+"F0.wireOp",EDGE,"E2016"),sQuery(id+"F0.wireOp",EDGE,"E2017"),sQuery(id+"F0.wireOp",EDGE,"E2018"),sQuery(id+"F0.wireOp",EDGE,"E2019"),sQuery(id+"F0.wireOp",EDGE,"E2020"),sQuery(id+"F0.wireOp",EDGE,"E2021"),sQuery(id+"F0.wireOp",EDGE,"E2022"),sQuery(id+"F0.wireOp",EDGE,"E2023"),sQuery(id+"F0.wireOp",EDGE,"E2024"),sQuery(id+"F0.wireOp",EDGE,"E2025"),sQuery(id+"F0.wireOp",EDGE,"E2026"),sQuery(id+"F0.wireOp",EDGE,"E2027"),sQuery(id+"F0.wireOp",EDGE,"E2028"),sQuery(id+"F0.wireOp",EDGE,"E2029"),sQuery(id+"F0.wireOp",EDGE,"E2030"),sQuery(id+"F0.wireOp",EDGE,"E2031"),sQuery(id+"F0.wireOp",EDGE,"E2032"),sQuery(id+"F0.wireOp",EDGE,"E2033"),sQuery(id+"F0.wireOp",EDGE,"E2034"),sQuery(id+"F0.wireOp",EDGE,"E2035"),sQuery(id+"F0.wireOp",EDGE,"E2036"),sQuery(id+"F0.wireOp",EDGE,"E2037"),sQuery(id+"F0.wireOp",EDGE,"E2038"),sQuery(id+"F0.wireOp",EDGE,"E2039"),sQuery(id+"F0.wireOp",EDGE,"E2040"),sQuery(id+"F0.wireOp",EDGE,"E2041"),sQuery(id+"F0.wireOp",EDGE,"E2042"),sQuery(id+"F0.wireOp",EDGE,"E2043"),sQuery(id+"F0.wireOp",EDGE,"E2044"),sQuery(id+"F0.wireOp",EDGE,"E2045"),sQuery(id+"F0.wireOp",EDGE,"E2046"),sQuery(id+"F0.wireOp",EDGE,"E2047"),sQuery(id+"F0.wireOp",EDGE,"E2048"),sQuery(id+"F0.wireOp",EDGE,"E2049"),sQuery(id+"F0.wireOp",EDGE,"E2050"),sQuery(id+"F0.wireOp",EDGE,"E2051"),sQuery(id+"F0.wireOp",EDGE,"E2052"),sQuery(id+"F0.wireOp",EDGE,"E2053"),sQuery(id+"F0.wireOp",EDGE,"E2054"),sQuery(id+"F0.wireOp",EDGE,"E2055"),sQuery(id+"F0.wireOp",EDGE,"E2056"),sQuery(id+"F0.wireOp",EDGE,"E2057"),sQuery(id+"F0.wireOp",EDGE,"E2058"),sQuery(id+"F0.wireOp",EDGE,"E2059"),sQuery(id+"F0.wireOp",EDGE,"E2060"),sQuery(id+"F0.wireOp",EDGE,"E2061"),sQuery(id+"F0.wireOp",EDGE,"E2062"),sQuery(id+"F0.wireOp",EDGE,"E2063"),sQuery(id+"F0.wireOp",EDGE,"E2064"),sQuery(id+"F0.wireOp",EDGE,"E2065"),sQuery(id+"F0.wireOp",EDGE,"E2066"),sQuery(id+"F0.wireOp",EDGE,"E2067"),sQuery(id+"F0.wireOp",EDGE,"E2068"),sQuery(id+"F0.wireOp",EDGE,"E2069"),sQuery(id+"F0.wireOp",EDGE,"E2070"),sQuery(id+"F0.wireOp",EDGE,"E2071"),sQuery(id+"F0.wireOp",EDGE,"E2072"),sQuery(id+"F0.wireOp",EDGE,"E2073"),sQuery(id+"F0.wireOp",EDGE,"E2074"),sQuery(id+"F0.wireOp",EDGE,"E2075"),sQuery(id+"F0.wireOp",EDGE,"E2076"),sQuery(id+"F0.wireOp",EDGE,"E2077"),sQuery(id+"F0.wireOp",EDGE,"E2078"),sQuery(id+"F0.wireOp",EDGE,"E2079"),sQuery(id+"F0.wireOp",EDGE,"E2080"),sQuery(id+"F0.wireOp",EDGE,"E2081"),sQuery(id+"F0.wireOp",EDGE,"E2082"),sQuery(id+"F0.wireOp",EDGE,"E2083"),sQuery(id+"F0.wireOp",EDGE,"E2084"),sQuery(id+"F0.wireOp",EDGE,"E2085"),sQuery(id+"F0.wireOp",EDGE,"E2086"),sQuery(id+"F0.wireOp",EDGE,"E2087"),sQuery(id+"F0.wireOp",EDGE,"E2088"),sQuery(id+"F0.wireOp",EDGE,"E2089"),sQuery(id+"F0.wireOp",EDGE,"E2090"),sQuery(id+"F0.wireOp",EDGE,"E2091"),sQuery(id+"F0.wireOp",EDGE,"E2092"),sQuery(id+"F0.wireOp",EDGE,"E2093"),sQuery(id+"F0.wireOp",EDGE,"E2094"),sQuery(id+"F0.wireOp",EDGE,"E2095"),sQuery(id+"F0.wireOp",EDGE,"E2096"),sQuery(id+"F0.wireOp",EDGE,"E2097"),sQuery(id+"F0.wireOp",EDGE,"E2098"),sQuery(id+"F0.wireOp",EDGE,"E2099"),sQuery(id+"F0.wireOp",EDGE,"E2100"),sQuery(id+"F0.wireOp",EDGE,"E2101"),sQuery(id+"F0.wireOp",EDGE,"E2102"),sQuery(id+"F0.wireOp",EDGE,"E2103"),sQuery(id+"F0.wireOp",EDGE,"E2104"),sQuery(id+"F0.wireOp",EDGE,"E2105"),sQuery(id+"F0.wireOp",EDGE,"E2106"),sQuery(id+"F0.wireOp",EDGE,"E2107"),sQuery(id+"F0.wireOp",EDGE,"E2108"),sQuery(id+"F0.wireOp",EDGE,"E2109"),sQuery(id+"F0.wireOp",EDGE,"E2110"),sQuery(id+"F0.wireOp",EDGE,"E2111"),sQuery(id+"F0.wireOp",EDGE,"E2112"),sQuery(id+"F0.wireOp",EDGE,"E2113"),sQuery(id+"F0.wireOp",EDGE,"E2114"),sQuery(id+"F0.wireOp",EDGE,"E2115"),sQuery(id+"F0.wireOp",EDGE,"E2116"),sQuery(id+"F0.wireOp",EDGE,"E2117"),sQuery(id+"F0.wireOp",EDGE,"E2118"),sQuery(id+"F0.wireOp",EDGE,"E2119"),sQuery(id+"F0.wireOp",EDGE,"E2120"),sQuery(id+"F0.wireOp",EDGE,"E2121"),sQuery(id+"F0.wireOp",EDGE,"E2122"),sQuery(id+"F0.wireOp",EDGE,"E2123"),sQuery(id+"F0.wireOp",EDGE,"E2124"),sQuery(id+"F0.wireOp",EDGE,"E2125"),sQuery(id+"F0.wireOp",EDGE,"E2126"),sQuery(id+"F0.wireOp",EDGE,"E2127"),sQuery(id+"F0.wireOp",EDGE,"E2128"),sQuery(id+"F0.wireOp",EDGE,"E2129"),sQuery(id+"F0.wireOp",EDGE,"E2130"),sQuery(id+"F0.wireOp",EDGE,"E2131"),sQuery(id+"F0.wireOp",EDGE,"E2132"),sQuery(id+"F0.wireOp",EDGE,"E2133"),sQuery(id+"F0.wireOp",EDGE,"E2134"),sQuery(id+"F0.wireOp",EDGE,"E2135"),sQuery(id+"F0.wireOp",EDGE,"E2136"),sQuery(id+"F0.wireOp",EDGE,"E2137"),sQuery(id+"F0.wireOp",EDGE,"E2138"),sQuery(id+"F0.wireOp",EDGE,"E2139"),sQuery(id+"F0.wireOp",EDGE,"E2140"),sQuery(id+"F0.wireOp",EDGE,"E2141"),sQuery(id+"F0.wireOp",EDGE,"E2142"),sQuery(id+"F0.wireOp",EDGE,"E2143"),sQuery(id+"F0.wireOp",EDGE,"E2144"),sQuery(id+"F0.wireOp",EDGE,"E2145"),sQuery(id+"F0.wireOp",EDGE,"E2146"),sQuery(id+"F0.wireOp",EDGE,"E2147"),sQuery(id+"F0.wireOp",EDGE,"E2148"),sQuery(id+"F0.wireOp",EDGE,"E2149"),sQuery(id+"F0.wireOp",EDGE,"E2150"),sQuery(id+"F0.wireOp",EDGE,"E2151"),sQuery(id+"F0.wireOp",EDGE,"E2152"),sQuery(id+"F0.wireOp",EDGE,"E2153"),sQuery(id+"F0.wireOp",EDGE,"E2154"),sQuery(id+"F0.wireOp",EDGE,"E2155"),sQuery(id+"F0.wireOp",EDGE,"E2156"),sQuery(id+"F0.wireOp",EDGE,"E2157"),sQuery(id+"F0.wireOp",EDGE,"E2158"),sQuery(id+"F0.wireOp",EDGE,"E2159"),sQuery(id+"F0.wireOp",EDGE,"E2160"),sQuery(id+"F0.wireOp",EDGE,"E2161"),sQuery(id+"F0.wireOp",EDGE,"E2162"),sQuery(id+"F0.wireOp",EDGE,"E2163"),sQuery(id+"F0.wireOp",EDGE,"E2164"),sQuery(id+"F0.wireOp",EDGE,"E2165"),sQuery(id+"F0.wireOp",EDGE,"E2166"),sQuery(id+"F0.wireOp",EDGE,"E2167"),sQuery(id+"F0.wireOp",EDGE,"E2168"),sQuery(id+"F0.wireOp",EDGE,"E2169"),sQuery(id+"F0.wireOp",EDGE,"E2170"),sQuery(id+"F0.wireOp",EDGE,"E2171"),sQuery(id+"F0.wireOp",EDGE,"E2172"),sQuery(id+"F0.wireOp",EDGE,"E2173"),sQuery(id+"F0.wireOp",EDGE,"E2174"),sQuery(id+"F0.wireOp",EDGE,"E2175"),sQuery(id+"F0.wireOp",EDGE,"E2176"),sQuery(id+"F0.wireOp",EDGE,"E2177"),sQuery(id+"F0.wireOp",EDGE,"E2178"),sQuery(id+"F0.wireOp",EDGE,"E2179"),sQuery(id+"F0.wireOp",EDGE,"E2180"),sQuery(id+"F0.wireOp",EDGE,"E2181"),sQuery(id+"F0.wireOp",EDGE,"E2182"),sQuery(id+"F0.wireOp",EDGE,"E2183"),sQuery(id+"F0.wireOp",EDGE,"E2184"),sQuery(id+"F0.wireOp",EDGE,"E2185"),sQuery(id+"F0.wireOp",EDGE,"E2186"),sQuery(id+"F0.wireOp",EDGE,"E2187"),sQuery(id+"F0.wireOp",EDGE,"E2188"),sQuery(id+"F0.wireOp",EDGE,"E2189"),sQuery(id+"F0.wireOp",EDGE,"E2190"),sQuery(id+"F0.wireOp",EDGE,"E2191"),sQuery(id+"F0.wireOp",EDGE,"E2192"),sQuery(id+"F0.wireOp",EDGE,"E2193"),sQuery(id+"F0.wireOp",EDGE,"E2194"),sQuery(id+"F0.wireOp",EDGE,"E2195"),sQuery(id+"F0.wireOp",EDGE,"E2196"),sQuery(id+"F0.wireOp",EDGE,"E2197"),sQuery(id+"F0.wireOp",EDGE,"E2198"),sQuery(id+"F0.wireOp",EDGE,"E2199"),sQuery(id+"F0.wireOp",EDGE,"E2200"),sQuery(id+"F0.wireOp",EDGE,"E2201"),sQuery(id+"F0.wireOp",EDGE,"E2202"),sQuery(id+"F0.wireOp",EDGE,"E2203"),sQuery(id+"F0.wireOp",EDGE,"E2204"),sQuery(id+"F0.wireOp",EDGE,"E2205"),sQuery(id+"F0.wireOp",EDGE,"E2206"),sQuery(id+"F0.wireOp",EDGE,"E2207"),sQuery(id+"F0.wireOp",EDGE,"E2208"),sQuery(id+"F0.wireOp",EDGE,"E2209"),sQuery(id+"F0.wireOp",EDGE,"E2210"),sQuery(id+"F0.wireOp",EDGE,"E2211"),sQuery(id+"F0.wireOp",EDGE,"E2212"),sQuery(id+"F0.wireOp",EDGE,"E2213"),sQuery(id+"F0.wireOp",EDGE,"E2214"),sQuery(id+"F0.wireOp",EDGE,"E2215"),sQuery(id+"F0.wireOp",EDGE,"E2216"),sQuery(id+"F0.wireOp",EDGE,"E2217"),sQuery(id+"F0.wireOp",EDGE,"E2218"),sQuery(id+"F0.wireOp",EDGE,"E2219"),sQuery(id+"F0.wireOp",EDGE,"E2220"),sQuery(id+"F0.wireOp",EDGE,"E2221"),sQuery(id+"F0.wireOp",EDGE,"E2222"),sQuery(id+"F0.wireOp",EDGE,"E2223"),sQuery(id+"F0.wireOp",EDGE,"E2224"),sQuery(id+"F0.wireOp",EDGE,"E2225"),sQuery(id+"F0.wireOp",EDGE,"E2226"),sQuery(id+"F0.wireOp",EDGE,"E2227"),sQuery(id+"F0.wireOp",EDGE,"E2228"),sQuery(id+"F0.wireOp",EDGE,"E2229"),sQuery(id+"F0.wireOp",EDGE,"E2230"),sQuery(id+"F0.wireOp",EDGE,"E2231"),sQuery(id+"F0.wireOp",EDGE,"E2232"),sQuery(id+"F0.wireOp",EDGE,"E2233"),sQuery(id+"F0.wireOp",EDGE,"E2234"),sQuery(id+"F0.wireOp",EDGE,"E2235"),sQuery(id+"F0.wireOp",EDGE,"E2236"),sQuery(id+"F0.wireOp",EDGE,"E2237"),sQuery(id+"F0.wireOp",EDGE,"E2238"),sQuery(id+"F0.wireOp",EDGE,"E2239"),sQuery(id+"F0.wireOp",EDGE,"E2240"),sQuery(id+"F0.wireOp",EDGE,"E2241"),sQuery(id+"F0.wireOp",EDGE,"E2242"),sQuery(id+"F0.wireOp",EDGE,"E2243"),sQuery(id+"F0.wireOp",EDGE,"E2244"),sQuery(id+"F0.wireOp",EDGE,"E2245"),sQuery(id+"F0.wireOp",EDGE,"E2246"),sQuery(id+"F0.wireOp",EDGE,"E2247"),sQuery(id+"F0.wireOp",EDGE,"E2248"),sQuery(id+"F0.wireOp",EDGE,"E2249"),sQuery(id+"F0.wireOp",EDGE,"E2250"),sQuery(id+"F0.wireOp",EDGE,"E2251"),sQuery(id+"F0.wireOp",EDGE,"E2252"),sQuery(id+"F0.wireOp",EDGE,"E2253"),sQuery(id+"F0.wireOp",EDGE,"E2254"),sQuery(id+"F0.wireOp",EDGE,"E2255"),sQuery(id+"F0.wireOp",EDGE,"E2256"),sQuery(id+"F0.wireOp",EDGE,"E2257"),sQuery(id+"F0.wireOp",EDGE,"E2258"),sQuery(id+"F0.wireOp",EDGE,"E2259"),sQuery(id+"F0.wireOp",EDGE,"E2260"),sQuery(id+"F0.wireOp",EDGE,"E2261"),sQuery(id+"F0.wireOp",EDGE,"E2262"),sQuery(id+"F0.wireOp",EDGE,"E2263"),sQuery(id+"F0.wireOp",EDGE,"E2264"),sQuery(id+"F0.wireOp",EDGE,"E2265"),sQuery(id+"F0.wireOp",EDGE,"E2266"),sQuery(id+"F0.wireOp",EDGE,"E2267"),sQuery(id+"F0.wireOp",EDGE,"E2268"),sQuery(id+"F0.wireOp",EDGE,"E2269"),sQuery(id+"F0.wireOp",EDGE,"E2270"),sQuery(id+"F0.wireOp",EDGE,"E2271"),sQuery(id+"F0.wireOp",EDGE,"E2272"),sQuery(id+"F0.wireOp",EDGE,"E2273"),sQuery(id+"F0.wireOp",EDGE,"E2274"),sQuery(id+"F0.wireOp",EDGE,"E2275"),sQuery(id+"F0.wireOp",EDGE,"E2276"),sQuery(id+"F0.wireOp",EDGE,"E2277"),sQuery(id+"F0.wireOp",EDGE,"E2278"),sQuery(id+"F0.wireOp",EDGE,"E2279"),sQuery(id+"F0.wireOp",EDGE,"E2280"),sQuery(id+"F0.wireOp",EDGE,"E2281"),sQuery(id+"F0.wireOp",EDGE,"E2282"),sQuery(id+"F0.wireOp",EDGE,"E2283"),sQuery(id+"F0.wireOp",EDGE,"E2284"),sQuery(id+"F0.wireOp",EDGE,"E2285"),sQuery(id+"F0.wireOp",EDGE,"E2286"),sQuery(id+"F0.wireOp",EDGE,"E2287"),sQuery(id+"F0.wireOp",EDGE,"E2288"),sQuery(id+"F0.wireOp",EDGE,"E2289"),sQuery(id+"F0.wireOp",EDGE,"E2290"),sQuery(id+"F0.wireOp",EDGE,"E2291"),sQuery(id+"F0.wireOp",EDGE,"E2292"),sQuery(id+"F0.wireOp",EDGE,"E2293"),sQuery(id+"F0.wireOp",EDGE,"E2294"),sQuery(id+"F0.wireOp",EDGE,"E2295"),sQuery(id+"F0.wireOp",EDGE,"E2296"),sQuery(id+"F0.wireOp",EDGE,"E2297"),sQuery(id+"F0.wireOp",EDGE,"E2298"),sQuery(id+"F0.wireOp",EDGE,"E2299"),sQuery(id+"F0.wireOp",EDGE,"E2300"),sQuery(id+"F0.wireOp",EDGE,"E2301"),sQuery(id+"F0.wireOp",EDGE,"E2302"),sQuery(id+"F0.wireOp",EDGE,"E2303"),sQuery(id+"F0.wireOp",EDGE,"E2304"),sQuery(id+"F0.wireOp",EDGE,"E2305"),sQuery(id+"F0.wireOp",EDGE,"E2306"),sQuery(id+"F0.wireOp",EDGE,"E2307"),sQuery(id+"F0.wireOp",EDGE,"E2308"),sQuery(id+"F0.wireOp",EDGE,"E2309"),sQuery(id+"F0.wireOp",EDGE,"E2310"),sQuery(id+"F0.wireOp",EDGE,"E2311"),sQuery(id+"F0.wireOp",EDGE,"E2312"),sQuery(id+"F0.wireOp",EDGE,"E2313"),sQuery(id+"F0.wireOp",EDGE,"E2314"),sQuery(id+"F0.wireOp",EDGE,"E2315"),sQuery(id+"F0.wireOp",EDGE,"E2316"),sQuery(id+"F0.wireOp",EDGE,"E2317"),sQuery(id+"F0.wireOp",EDGE,"E2318"),sQuery(id+"F0.wireOp",EDGE,"E2319"),sQuery(id+"F0.wireOp",EDGE,"E2320"),sQuery(id+"F0.wireOp",EDGE,"E2321"),sQuery(id+"F0.wireOp",EDGE,"E2322"),sQuery(id+"F0.wireOp",EDGE,"E2323"),sQuery(id+"F0.wireOp",EDGE,"E2324"),sQuery(id+"F0.wireOp",EDGE,"E2325"),sQuery(id+"F0.wireOp",EDGE,"E2326"),sQuery(id+"F0.wireOp",EDGE,"E2327"),sQuery(id+"F0.wireOp",EDGE,"E2328"),sQuery(id+"F0.wireOp",EDGE,"E2329"),sQuery(id+"F0.wireOp",EDGE,"E2330"),sQuery(id+"F0.wireOp",EDGE,"E2331"),sQuery(id+"F0.wireOp",EDGE,"E2332"),sQuery(id+"F0.wireOp",EDGE,"E2333"),sQuery(id+"F0.wireOp",EDGE,"E2334"),sQuery(id+"F0.wireOp",EDGE,"E2335"),sQuery(id+"F0.wireOp",EDGE,"E2336"),sQuery(id+"F0.wireOp",EDGE,"E2337"),sQuery(id+"F0.wireOp",EDGE,"E2338"),sQuery(id+"F0.wireOp",EDGE,"E2339"),sQuery(id+"F0.wireOp",EDGE,"E2340"),sQuery(id+"F0.wireOp",EDGE,"E2341"),sQuery(id+"F0.wireOp",EDGE,"E2342"),sQuery(id+"F0.wireOp",EDGE,"E2343"),sQuery(id+"F0.wireOp",EDGE,"E2344"),sQuery(id+"F0.wireOp",EDGE,"E2345"),sQuery(id+"F0.wireOp",EDGE,"E2346"),sQuery(id+"F0.wireOp",EDGE,"E2347"),sQuery(id+"F0.wireOp",EDGE,"E2348"),sQuery(id+"F0.wireOp",EDGE,"E2349"),sQuery(id+"F0.wireOp",EDGE,"E2350"),sQuery(id+"F0.wireOp",EDGE,"E2351"),sQuery(id+"F0.wireOp",EDGE,"E2352"),sQuery(id+"F0.wireOp",EDGE,"E2353"),sQuery(id+"F0.wireOp",EDGE,"E2354"),sQuery(id+"F0.wireOp",EDGE,"E2355"),sQuery(id+"F0.wireOp",EDGE,"E2356"),sQuery(id+"F0.wireOp",EDGE,"E2357"),sQuery(id+"F0.wireOp",EDGE,"E2358"),sQuery(id+"F0.wireOp",EDGE,"E2359"),sQuery(id+"F0.wireOp",EDGE,"E2360"),sQuery(id+"F0.wireOp",EDGE,"E2361"),sQuery(id+"F0.wireOp",EDGE,"E2362"),sQuery(id+"F0.wireOp",EDGE,"E2363"),sQuery(id+"F0.wireOp",EDGE,"E2364"),sQuery(id+"F0.wireOp",EDGE,"E2365"),sQuery(id+"F0.wireOp",EDGE,"E2366"),sQuery(id+"F0.wireOp",EDGE,"E2367"),sQuery(id+"F0.wireOp",EDGE,"E2368"),sQuery(id+"F0.wireOp",EDGE,"E2369"),sQuery(id+"F0.wireOp",EDGE,"E2370"),sQuery(id+"F0.wireOp",EDGE,"E2371"),sQuery(id+"F0.wireOp",EDGE,"E2372"),sQuery(id+"F0.wireOp",EDGE,"E2373"),sQuery(id+"F0.wireOp",EDGE,"E2374"),sQuery(id+"F0.wireOp",EDGE,"E2375"),sQuery(id+"F0.wireOp",EDGE,"E2376"),sQuery(id+"F0.wireOp",EDGE,"E2377"),sQuery(id+"F0.wireOp",EDGE,"E2378"),sQuery(id+"F0.wireOp",EDGE,"E2379"),sQuery(id+"F0.wireOp",EDGE,"E2380"),sQuery(id+"F0.wireOp",EDGE,"E2381"),sQuery(id+"F0.wireOp",EDGE,"E2382"),sQuery(id+"F0.wireOp",EDGE,"E2383"),sQuery(id+"F0.wireOp",EDGE,"E2384"),sQuery(id+"F0.wireOp",EDGE,"E2385"),sQuery(id+"F0.wireOp",EDGE,"E2386"),sQuery(id+"F0.wireOp",EDGE,"E2387"),sQuery(id+"F0.wireOp",EDGE,"E2388"),sQuery(id+"F0.wireOp",EDGE,"E2389"),sQuery(id+"F0.wireOp",EDGE,"E2390"),sQuery(id+"F0.wireOp",EDGE,"E2391"),sQuery(id+"F0.wireOp",EDGE,"E2392"),sQuery(id+"F0.wireOp",EDGE,"E2393"),sQuery(id+"F0.wireOp",EDGE,"E2394"),sQuery(id+"F0.wireOp",EDGE,"E2395"),sQuery(id+"F0.wireOp",EDGE,"E2396"),sQuery(id+"F0.wireOp",EDGE,"E2397"),sQuery(id+"F0.wireOp",EDGE,"E2398"),sQuery(id+"F0.wireOp",EDGE,"E2399"),sQuery(id+"F0.wireOp",EDGE,"E2400"),sQuery(id+"F0.wireOp",EDGE,"E2401"),sQuery(id+"F0.wireOp",EDGE,"E2402"),sQuery(id+"F0.wireOp",EDGE,"E2403"),sQuery(id+"F0.wireOp",EDGE,"E2404"),sQuery(id+"F0.wireOp",EDGE,"E2405"),sQuery(id+"F0.wireOp",EDGE,"E2406"),sQuery(id+"F0.wireOp",EDGE,"E2407"),sQuery(id+"F0.wireOp",EDGE,"E2408"),sQuery(id+"F0.wireOp",EDGE,"E2409"),sQuery(id+"F0.wireOp",EDGE,"E2410"),sQuery(id+"F0.wireOp",EDGE,"E2411"),sQuery(id+"F0.wireOp",EDGE,"E2412"),sQuery(id+"F0.wireOp",EDGE,"E2413"),sQuery(id+"F0.wireOp",EDGE,"E2414"),sQuery(id+"F0.wireOp",EDGE,"E2415"),sQuery(id+"F0.wireOp",EDGE,"E2416"),sQuery(id+"F0.wireOp",EDGE,"E2417"),sQuery(id+"F0.wireOp",EDGE,"E2418"),sQuery(id+"F0.wireOp",EDGE,"E2419"),sQuery(id+"F0.wireOp",EDGE,"E2420"),sQuery(id+"F0.wireOp",EDGE,"E2421"),sQuery(id+"F0.wireOp",EDGE,"E2422"),sQuery(id+"F0.wireOp",EDGE,"E2423"),sQuery(id+"F0.wireOp",EDGE,"E2424"),sQuery(id+"F0.wireOp",EDGE,"E2425"),sQuery(id+"F0.wireOp",EDGE,"E2426"),sQuery(id+"F0.wireOp",EDGE,"E2427"),sQuery(id+"F0.wireOp",EDGE,"E2428"),sQuery(id+"F0.wireOp",EDGE,"E2429"),sQuery(id+"F0.wireOp",EDGE,"E2430"),sQuery(id+"F0.wireOp",EDGE,"E2431"),sQuery(id+"F0.wireOp",EDGE,"E2432"),sQuery(id+"F0.wireOp",EDGE,"E2433"),sQuery(id+"F0.wireOp",EDGE,"E2434"),sQuery(id+"F0.wireOp",EDGE,"E2435"),sQuery(id+"F0.wireOp",EDGE,"E2436"),sQuery(id+"F0.wireOp",EDGE,"E2437"),sQuery(id+"F0.wireOp",EDGE,"E2438"),sQuery(id+"F0.wireOp",EDGE,"E2439"),sQuery(id+"F0.wireOp",EDGE,"E2440"),sQuery(id+"F0.wireOp",EDGE,"E2441"),sQuery(id+"F0.wireOp",EDGE,"E2442"),sQuery(id+"F0.wireOp",EDGE,"E2443"),sQuery(id+"F0.wireOp",EDGE,"E2444"),sQuery(id+"F0.wireOp",EDGE,"E2445"),sQuery(id+"F0.wireOp",EDGE,"E2446"),sQuery(id+"F0.wireOp",EDGE,"E2447"),sQuery(id+"F0.wireOp",EDGE,"E2448"),sQuery(id+"F0.wireOp",EDGE,"E2449"),sQuery(id+"F0.wireOp",EDGE,"E2450"),sQuery(id+"F0.wireOp",EDGE,"E2451"),sQuery(id+"F0.wireOp",EDGE,"E2452"),sQuery(id+"F0.wireOp",EDGE,"E2453"),sQuery(id+"F0.wireOp",EDGE,"E2454"),sQuery(id+"F0.wireOp",EDGE,"E2455"),sQuery(id+"F0.wireOp",EDGE,"E2456"),sQuery(id+"F0.wireOp",EDGE,"E2457"),sQuery(id+"F0.wireOp",EDGE,"E2458"),sQuery(id+"F0.wireOp",EDGE,"E2459"),sQuery(id+"F0.wireOp",EDGE,"E2460"),sQuery(id+"F0.wireOp",EDGE,"E2461"),sQuery(id+"F0.wireOp",EDGE,"E2462"),sQuery(id+"F0.wireOp",EDGE,"E2463"),sQuery(id+"F0.wireOp",EDGE,"E2464"),sQuery(id+"F0.wireOp",EDGE,"E2465"),sQuery(id+"F0.wireOp",EDGE,"E2466"),sQuery(id+"F0.wireOp",EDGE,"E2467"),sQuery(id+"F0.wireOp",EDGE,"E2468"),sQuery(id+"F0.wireOp",EDGE,"E2469"),sQuery(id+"F0.wireOp",EDGE,"E2470"),sQuery(id+"F0.wireOp",EDGE,"E2471"),sQuery(id+"F0.wireOp",EDGE,"E2472"),sQuery(id+"F0.wireOp",EDGE,"E2473"),sQuery(id+"F0.wireOp",EDGE,"E2474"),sQuery(id+"F0.wireOp",EDGE,"E2475"),sQuery(id+"F0.wireOp",EDGE,"E2476"),sQuery(id+"F0.wireOp",EDGE,"E2477"),sQuery(id+"F0.wireOp",EDGE,"E2478"),sQuery(id+"F0.wireOp",EDGE,"E2479"),sQuery(id+"F0.wireOp",EDGE,"E2480"),sQuery(id+"F0.wireOp",EDGE,"E2481"),sQuery(id+"F0.wireOp",EDGE,"E2482"),sQuery(id+"F0.wireOp",EDGE,"E2483"),sQuery(id+"F0.wireOp",EDGE,"E2484"),sQuery(id+"F0.wireOp",EDGE,"E2485"),sQuery(id+"F0.wireOp",EDGE,"E2486"),sQuery(id+"F0.wireOp",EDGE,"E2487"),sQuery(id+"F0.wireOp",EDGE,"E2488"),sQuery(id+"F0.wireOp",EDGE,"E2489"),sQuery(id+"F0.wireOp",EDGE,"E2490"),sQuery(id+"F0.wireOp",EDGE,"E2491"),sQuery(id+"F0.wireOp",EDGE,"E2492"),sQuery(id+"F0.wireOp",EDGE,"E2493"),sQuery(id+"F0.wireOp",EDGE,"E2494"),sQuery(id+"F0.wireOp",EDGE,"E2495"),sQuery(id+"F0.wireOp",EDGE,"E2496"),sQuery(id+"F0.wireOp",EDGE,"E2497"),sQuery(id+"F0.wireOp",EDGE,"E2498"),sQuery(id+"F0.wireOp",EDGE,"E2499"),sQuery(id+"F0.wireOp",EDGE,"E2500"),sQuery(id+"F0.wireOp",EDGE,"E2501"),sQuery(id+"F0.wireOp",EDGE,"E2502"),sQuery(id+"F0.wireOp",EDGE,"E2503"),sQuery(id+"F0.wireOp",EDGE,"E2504"),sQuery(id+"F0.wireOp",EDGE,"E2505"),sQuery(id+"F0.wireOp",EDGE,"E2506"),sQuery(id+"F0.wireOp",EDGE,"E2507"),sQuery(id+"F0.wireOp",EDGE,"E2508"),sQuery(id+"F0.wireOp",EDGE,"E2509"),sQuery(id+"F0.wireOp",EDGE,"E2510"),sQuery(id+"F0.wireOp",EDGE,"E2511"),sQuery(id+"F0.wireOp",EDGE,"E2512"),sQuery(id+"F0.wireOp",EDGE,"E2513"),sQuery(id+"F0.wireOp",EDGE,"E2514"),sQuery(id+"F0.wireOp",EDGE,"E2515"),sQuery(id+"F0.wireOp",EDGE,"E2516"),sQuery(id+"F0.wireOp",EDGE,"E2517"),sQuery(id+"F0.wireOp",EDGE,"E2518"),sQuery(id+"F0.wireOp",EDGE,"E2519"),sQuery(id+"F0.wireOp",EDGE,"E2520"),sQuery(id+"F0.wireOp",EDGE,"E2521"),sQuery(id+"F0.wireOp",EDGE,"E2522"),sQuery(id+"F0.wireOp",EDGE,"E2523"),sQuery(id+"F0.wireOp",EDGE,"E2524"),sQuery(id+"F0.wireOp",EDGE,"E2525"),sQuery(id+"F0.wireOp",EDGE,"E2526"),sQuery(id+"F0.wireOp",EDGE,"E2527"),sQuery(id+"F0.wireOp",EDGE,"E2528"),sQuery(id+"F0.wireOp",EDGE,"E2529"),sQuery(id+"F0.wireOp",EDGE,"E2530"),sQuery(id+"F0.wireOp",EDGE,"E2531"),sQuery(id+"F0.wireOp",EDGE,"E2532"),sQuery(id+"F0.wireOp",EDGE,"E2533"),sQuery(id+"F0.wireOp",EDGE,"E2534"),sQuery(id+"F0.wireOp",EDGE,"E2535"),sQuery(id+"F0.wireOp",EDGE,"E2536"),sQuery(id+"F0.wireOp",EDGE,"E2537"),sQuery(id+"F0.wireOp",EDGE,"E2538"),sQuery(id+"F0.wireOp",EDGE,"E2539"),sQuery(id+"F0.wireOp",EDGE,"E2540"),sQuery(id+"F0.wireOp",EDGE,"E2541"),sQuery(id+"F0.wireOp",EDGE,"E2542"),sQuery(id+"F0.wireOp",EDGE,"E2543"),sQuery(id+"F0.wireOp",EDGE,"E2544"),sQuery(id+"F0.wireOp",EDGE,"E2545"),sQuery(id+"F0.wireOp",EDGE,"E2546"),sQuery(id+"F0.wireOp",EDGE,"E2547"),sQuery(id+"F0.wireOp",EDGE,"E2548"),sQuery(id+"F0.wireOp",EDGE,"E2549"),sQuery(id+"F0.wireOp",EDGE,"E2550"),sQuery(id+"F0.wireOp",EDGE,"E2551"),sQuery(id+"F0.wireOp",EDGE,"E2552"),sQuery(id+"F0.wireOp",EDGE,"E2553"),sQuery(id+"F0.wireOp",EDGE,"E2554"),sQuery(id+"F0.wireOp",EDGE,"E2555"),sQuery(id+"F0.wireOp",EDGE,"E2556"),sQuery(id+"F0.wireOp",EDGE,"E2557"),sQuery(id+"F0.wireOp",EDGE,"E2558"),sQuery(id+"F0.wireOp",EDGE,"E2559"),sQuery(id+"F0.wireOp",EDGE,"E2560"),sQuery(id+"F0.wireOp",EDGE,"E2561"),sQuery(id+"F0.wireOp",EDGE,"E2562"),sQuery(id+"F0.wireOp",EDGE,"E2563"),sQuery(id+"F0.wireOp",EDGE,"E2564"),sQuery(id+"F0.wireOp",EDGE,"E2565"),sQuery(id+"F0.wireOp",EDGE,"E2566"),sQuery(id+"F0.wireOp",EDGE,"E2567"),sQuery(id+"F0.wireOp",EDGE,"E2568"),sQuery(id+"F0.wireOp",EDGE,"E2569"),sQuery(id+"F0.wireOp",EDGE,"E2570"),sQuery(id+"F0.wireOp",EDGE,"E2571"),sQuery(id+"F0.wireOp",EDGE,"E2572"),sQuery(id+"F0.wireOp",EDGE,"E2573"),sQuery(id+"F0.wireOp",EDGE,"E2574"),sQuery(id+"F0.wireOp",EDGE,"E2575"),sQuery(id+"F0.wireOp",EDGE,"E2576"),sQuery(id+"F0.wireOp",EDGE,"E2577"),sQuery(id+"F0.wireOp",EDGE,"E2578"),sQuery(id+"F0.wireOp",EDGE,"E2579"),sQuery(id+"F0.wireOp",EDGE,"E2580"),sQuery(id+"F0.wireOp",EDGE,"E2581"),sQuery(id+"F0.wireOp",EDGE,"E2582"),sQuery(id+"F0.wireOp",EDGE,"E2583"),sQuery(id+"F0.wireOp",EDGE,"E2584"),sQuery(id+"F0.wireOp",EDGE,"E2585"),sQuery(id+"F0.wireOp",EDGE,"E2586"),sQuery(id+"F0.wireOp",EDGE,"E2587"),sQuery(id+"F0.wireOp",EDGE,"E2588"),sQuery(id+"F0.wireOp",EDGE,"E2589"),sQuery(id+"F0.wireOp",EDGE,"E2590"),sQuery(id+"F0.wireOp",EDGE,"E2591"),sQuery(id+"F0.wireOp",EDGE,"E2592"),sQuery(id+"F0.wireOp",EDGE,"E2593"),sQuery(id+"F0.wireOp",EDGE,"E2594"),sQuery(id+"F0.wireOp",EDGE,"E2595"),sQuery(id+"F0.wireOp",EDGE,"E2596"),sQuery(id+"F0.wireOp",EDGE,"E2597"),sQuery(id+"F0.wireOp",EDGE,"E2598"),sQuery(id+"F0.wireOp",EDGE,"E2599"),sQuery(id+"F0.wireOp",EDGE,"E2600"),sQuery(id+"F0.wireOp",EDGE,"E2601"),sQuery(id+"F0.wireOp",EDGE,"E2602"),sQuery(id+"F0.wireOp",EDGE,"E2603"),sQuery(id+"F0.wireOp",EDGE,"E2604"),sQuery(id+"F0.wireOp",EDGE,"E2605"),sQuery(id+"F0.wireOp",EDGE,"E2606"),sQuery(id+"F0.wireOp",EDGE,"E2607"),sQuery(id+"F0.wireOp",EDGE,"E2608"),sQuery(id+"F0.wireOp",EDGE,"E2609"),sQuery(id+"F0.wireOp",EDGE,"E2610"),sQuery(id+"F0.wireOp",EDGE,"E2611"),sQuery(id+"F0.wireOp",EDGE,"E2612"),sQuery(id+"F0.wireOp",EDGE,"E2613"),sQuery(id+"F0.wireOp",EDGE,"E2614"),sQuery(id+"F0.wireOp",EDGE,"E2615"),sQuery(id+"F0.wireOp",EDGE,"E2616"),sQuery(id+"F0.wireOp",EDGE,"E2617"),sQuery(id+"F0.wireOp",EDGE,"E2618"),sQuery(id+"F0.wireOp",EDGE,"E2619"),sQuery(id+"F0.wireOp",EDGE,"E2620"),sQuery(id+"F0.wireOp",EDGE,"E2621"),sQuery(id+"F0.wireOp",EDGE,"E2622"),sQuery(id+"F0.wireOp",EDGE,"E2623"),sQuery(id+"F0.wireOp",EDGE,"E2624"),sQuery(id+"F0.wireOp",EDGE,"E2625"),sQuery(id+"F0.wireOp",EDGE,"E2626"),sQuery(id+"F0.wireOp",EDGE,"E2627"),sQuery(id+"F0.wireOp",EDGE,"E2628"),sQuery(id+"F0.wireOp",EDGE,"E2629"),sQuery(id+"F0.wireOp",EDGE,"E2630"),sQuery(id+"F0.wireOp",EDGE,"E2631"),sQuery(id+"F0.wireOp",EDGE,"E2632"),sQuery(id+"F0.wireOp",EDGE,"E2633"),sQuery(id+"F0.wireOp",EDGE,"E2634"),sQuery(id+"F0.wireOp",EDGE,"E2635"),sQuery(id+"F0.wireOp",EDGE,"E2636"),sQuery(id+"F0.wireOp",EDGE,"E2637"),sQuery(id+"F0.wireOp",EDGE,"E2638"),sQuery(id+"F0.wireOp",EDGE,"E2639"),sQuery(id+"F0.wireOp",EDGE,"E2640"),sQuery(id+"F0.wireOp",EDGE,"E2641"),sQuery(id+"F0.wireOp",EDGE,"E2642"),sQuery(id+"F0.wireOp",EDGE,"E2643"),sQuery(id+"F0.wireOp",EDGE,"E2644"),sQuery(id+"F0.wireOp",EDGE,"E2645"),sQuery(id+"F0.wireOp",EDGE,"E2646"),sQuery(id+"F0.wireOp",EDGE,"E2647"),sQuery(id+"F0.wireOp",EDGE,"E2648"),sQuery(id+"F0.wireOp",EDGE,"E2649"),sQuery(id+"F0.wireOp",EDGE,"E2650"),sQuery(id+"F0.wireOp",EDGE,"E2651"),sQuery(id+"F0.wireOp",EDGE,"E2652"),sQuery(id+"F0.wireOp",EDGE,"E2653"),sQuery(id+"F0.wireOp",EDGE,"E2654"),sQuery(id+"F0.wireOp",EDGE,"E2655"),sQuery(id+"F0.wireOp",EDGE,"E2656"),sQuery(id+"F0.wireOp",EDGE,"E2657"),sQuery(id+"F0.wireOp",EDGE,"E2658"),sQuery(id+"F0.wireOp",EDGE,"E2659"),sQuery(id+"F0.wireOp",EDGE,"E2660"),sQuery(id+"F0.wireOp",EDGE,"E2661"),sQuery(id+"F0.wireOp",EDGE,"E2662"),sQuery(id+"F0.wireOp",EDGE,"E2663"),sQuery(id+"F0.wireOp",EDGE,"E2664"),sQuery(id+"F0.wireOp",EDGE,"E2665"),sQuery(id+"F0.wireOp",EDGE,"E2666"),sQuery(id+"F0.wireOp",EDGE,"E2667"),sQuery(id+"F0.wireOp",EDGE,"E2668"),sQuery(id+"F0.wireOp",EDGE,"E2669"),sQuery(id+"F0.wireOp",EDGE,"E2670"),sQuery(id+"F0.wireOp",EDGE,"E2671"),sQuery(id+"F0.wireOp",EDGE,"E2672"),sQuery(id+"F0.wireOp",EDGE,"E2673"),sQuery(id+"F0.wireOp",EDGE,"E2674"),sQuery(id+"F0.wireOp",EDGE,"E2675"),sQuery(id+"F0.wireOp",EDGE,"E2676"),sQuery(id+"F0.wireOp",EDGE,"E2677"),sQuery(id+"F0.wireOp",EDGE,"E2678"),sQuery(id+"F0.wireOp",EDGE,"E2679"),sQuery(id+"F0.wireOp",EDGE,"E2680"),sQuery(id+"F0.wireOp",EDGE,"E2681"),sQuery(id+"F0.wireOp",EDGE,"E2682"),sQuery(id+"F0.wireOp",EDGE,"E2683"),sQuery(id+"F0.wireOp",EDGE,"E2684"),sQuery(id+"F0.wireOp",EDGE,"E2685"),sQuery(id+"F0.wireOp",EDGE,"E2686"),sQuery(id+"F0.wireOp",EDGE,"E2687"),sQuery(id+"F0.wireOp",EDGE,"E2688"),sQuery(id+"F0.wireOp",EDGE,"E2689"),sQuery(id+"F0.wireOp",EDGE,"E2690"),sQuery(id+"F0.wireOp",EDGE,"E2691"),sQuery(id+"F0.wireOp",EDGE,"E2692"),sQuery(id+"F0.wireOp",EDGE,"E2693"),sQuery(id+"F0.wireOp",EDGE,"E2694"),sQuery(id+"F0.wireOp",EDGE,"E2695"),sQuery(id+"F0.wireOp",EDGE,"E2696"),sQuery(id+"F0.wireOp",EDGE,"E2697"),sQuery(id+"F0.wireOp",EDGE,"E2698"),sQuery(id+"F0.wireOp",EDGE,"E2699"),sQuery(id+"F0.wireOp",EDGE,"E2700"),sQuery(id+"F0.wireOp",EDGE,"E2701"),sQuery(id+"F0.wireOp",EDGE,"E2702"),sQuery(id+"F0.wireOp",EDGE,"E2703"),sQuery(id+"F0.wireOp",EDGE,"E2704"),sQuery(id+"F0.wireOp",EDGE,"E2705"),sQuery(id+"F0.wireOp",EDGE,"E2706"),sQuery(id+"F0.wireOp",EDGE,"E2707"),sQuery(id+"F0.wireOp",EDGE,"E2708"),sQuery(id+"F0.wireOp",EDGE,"E2709"),sQuery(id+"F0.wireOp",EDGE,"E2710"),sQuery(id+"F0.wireOp",EDGE,"E2711"),sQuery(id+"F0.wireOp",EDGE,"E2712"),sQuery(id+"F0.wireOp",EDGE,"E2713"),sQuery(id+"F0.wireOp",EDGE,"E2714"),sQuery(id+"F0.wireOp",EDGE,"E2715"),sQuery(id+"F0.wireOp",EDGE,"E2716"),sQuery(id+"F0.wireOp",EDGE,"E2717"),sQuery(id+"F0.wireOp",EDGE,"E2718"),sQuery(id+"F0.wireOp",EDGE,"E2719"),sQuery(id+"F0.wireOp",EDGE,"E2720"),sQuery(id+"F0.wireOp",EDGE,"E2721"),sQuery(id+"F0.wireOp",EDGE,"E2722"),sQuery(id+"F0.wireOp",EDGE,"E2723"),sQuery(id+"F0.wireOp",EDGE,"E2724"),sQuery(id+"F0.wireOp",EDGE,"E2725"),sQuery(id+"F0.wireOp",EDGE,"E2726"),sQuery(id+"F0.wireOp",EDGE,"E2727"),sQuery(id+"F0.wireOp",EDGE,"E2728"),sQuery(id+"F0.wireOp",EDGE,"E2729"),sQuery(id+"F0.wireOp",EDGE,"E2730"),sQuery(id+"F0.wireOp",EDGE,"E2731"),sQuery(id+"F0.wireOp",EDGE,"E2732"),sQuery(id+"F0.wireOp",EDGE,"E2733"),sQuery(id+"F0.wireOp",EDGE,"E2734"),sQuery(id+"F0.wireOp",EDGE,"E2735"),sQuery(id+"F0.wireOp",EDGE,"E2736"),sQuery(id+"F0.wireOp",EDGE,"E2737"),sQuery(id+"F0.wireOp",EDGE,"E2738"),sQuery(id+"F0.wireOp",EDGE,"E2739"),sQuery(id+"F0.wireOp",EDGE,"E2740"),sQuery(id+"F0.wireOp",EDGE,"E2741"),sQuery(id+"F0.wireOp",EDGE,"E2742"),sQuery(id+"F0.wireOp",EDGE,"E2743"),sQuery(id+"F0.wireOp",EDGE,"E2744"),sQuery(id+"F0.wireOp",EDGE,"E2745"),sQuery(id+"F0.wireOp",EDGE,"E2746"),sQuery(id+"F0.wireOp",EDGE,"E2747"),sQuery(id+"F0.wireOp",EDGE,"E2748"),sQuery(id+"F0.wireOp",EDGE,"E2749"),sQuery(id+"F0.wireOp",EDGE,"E2750"),sQuery(id+"F0.wireOp",EDGE,"E2751"),sQuery(id+"F0.wireOp",EDGE,"E2752"),sQuery(id+"F0.wireOp",EDGE,"E2753"),sQuery(id+"F0.wireOp",EDGE,"E2754"),sQuery(id+"F0.wireOp",EDGE,"E2755"),sQuery(id+"F0.wireOp",EDGE,"E2756"),sQuery(id+"F0.wireOp",EDGE,"E2757"),sQuery(id+"F0.wireOp",EDGE,"E2758"),sQuery(id+"F0.wireOp",EDGE,"E2759"),sQuery(id+"F0.wireOp",EDGE,"E2760"),sQuery(id+"F0.wireOp",EDGE,"E2761"),sQuery(id+"F0.wireOp",EDGE,"E2762"),sQuery(id+"F0.wireOp",EDGE,"E2763"),sQuery(id+"F0.wireOp",EDGE,"E2764"),sQuery(id+"F0.wireOp",EDGE,"E2765"),sQuery(id+"F0.wireOp",EDGE,"E2766"),sQuery(id+"F0.wireOp",EDGE,"E2767"),sQuery(id+"F0.wireOp",EDGE,"E2768"),sQuery(id+"F0.wireOp",EDGE,"E2769"),sQuery(id+"F0.wireOp",EDGE,"E2770"),sQuery(id+"F0.wireOp",EDGE,"E2771"),sQuery(id+"F0.wireOp",EDGE,"E2772"),sQuery(id+"F0.wireOp",EDGE,"E2773"),sQuery(id+"F0.wireOp",EDGE,"E2774"),sQuery(id+"F0.wireOp",EDGE,"E2775"),sQuery(id+"F0.wireOp",EDGE,"E2776"),sQuery(id+"F0.wireOp",EDGE,"E2777"),sQuery(id+"F0.wireOp",EDGE,"E2778"),sQuery(id+"F0.wireOp",EDGE,"E2779"),sQuery(id+"F0.wireOp",EDGE,"E2780"),sQuery(id+"F0.wireOp",EDGE,"E2781"),sQuery(id+"F0.wireOp",EDGE,"E2782"),sQuery(id+"F0.wireOp",EDGE,"E2783"),sQuery(id+"F0.wireOp",EDGE,"E2784"),sQuery(id+"F0.wireOp",EDGE,"E2785"),sQuery(id+"F0.wireOp",EDGE,"E2786"),sQuery(id+"F0.wireOp",EDGE,"E2787"),sQuery(id+"F0.wireOp",EDGE,"E2788"),sQuery(id+"F0.wireOp",EDGE,"E2789"),sQuery(id+"F0.wireOp",EDGE,"E2790"),sQuery(id+"F0.wireOp",EDGE,"E2791"),sQuery(id+"F0.wireOp",EDGE,"E2792"),sQuery(id+"F0.wireOp",EDGE,"E2793"),sQuery(id+"F0.wireOp",EDGE,"E2794"),sQuery(id+"F0.wireOp",EDGE,"E2795"),sQuery(id+"F0.wireOp",EDGE,"E2796"),sQuery(id+"F0.wireOp",EDGE,"E2797"),sQuery(id+"F0.wireOp",EDGE,"E2798"),sQuery(id+"F0.wireOp",EDGE,"E2799"),sQuery(id+"F0.wireOp",EDGE,"E2800"),sQuery(id+"F0.wireOp",EDGE,"E2801"),sQuery(id+"F0.wireOp",EDGE,"E2802"),sQuery(id+"F0.wireOp",EDGE,"E2803"),sQuery(id+"F0.wireOp",EDGE,"E2804"),sQuery(id+"F0.wireOp",EDGE,"E2805"),sQuery(id+"F0.wireOp",EDGE,"E2806"),sQuery(id+"F0.wireOp",EDGE,"E2807"),sQuery(id+"F0.wireOp",EDGE,"E2808"),sQuery(id+"F0.wireOp",EDGE,"E2809"),sQuery(id+"F0.wireOp",EDGE,"E2810"),sQuery(id+"F0.wireOp",EDGE,"E2811"),sQuery(id+"F0.wireOp",EDGE,"E2812"),sQuery(id+"F0.wireOp",EDGE,"E2813"),sQuery(id+"F0.wireOp",EDGE,"E2814"),sQuery(id+"F0.wireOp",EDGE,"E2815"),sQuery(id+"F0.wireOp",EDGE,"E2816"),sQuery(id+"F0.wireOp",EDGE,"E2817"),sQuery(id+"F0.wireOp",EDGE,"E2818"),sQuery(id+"F0.wireOp",EDGE,"E2819"),sQuery(id+"F0.wireOp",EDGE,"E2820"),sQuery(id+"F0.wireOp",EDGE,"E2821"),sQuery(id+"F0.wireOp",EDGE,"E2822"),sQuery(id+"F0.wireOp",EDGE,"E2823"),sQuery(id+"F0.wireOp",EDGE,"E2824"),sQuery(id+"F0.wireOp",EDGE,"E2825"),sQuery(id+"F0.wireOp",EDGE,"E2826"),sQuery(id+"F0.wireOp",EDGE,"E2827"),sQuery(id+"F0.wireOp",EDGE,"E2828"),sQuery(id+"F0.wireOp",EDGE,"E2829"),sQuery(id+"F0.wireOp",EDGE,"E2830"),sQuery(id+"F0.wireOp",EDGE,"E2831"),sQuery(id+"F0.wireOp",EDGE,"E2832"),sQuery(id+"F0.wireOp",EDGE,"E2833"),sQuery(id+"F0.wireOp",EDGE,"E2834"),sQuery(id+"F0.wireOp",EDGE,"E2835"),sQuery(id+"F0.wireOp",EDGE,"E2836"),sQuery(id+"F0.wireOp",EDGE,"E2837"),sQuery(id+"F0.wireOp",EDGE,"E2838"),sQuery(id+"F0.wireOp",EDGE,"E2839"),sQuery(id+"F0.wireOp",EDGE,"E2840"),sQuery(id+"F0.wireOp",EDGE,"E2841"),sQuery(id+"F0.wireOp",EDGE,"E2842"),sQuery(id+"F0.wireOp",EDGE,"E2843"),sQuery(id+"F0.wireOp",EDGE,"E2844"),sQuery(id+"F0.wireOp",EDGE,"E2845"),sQuery(id+"F0.wireOp",EDGE,"E2846"),sQuery(id+"F0.wireOp",EDGE,"E2847"),sQuery(id+"F0.wireOp",EDGE,"E2848"),sQuery(id+"F0.wireOp",EDGE,"E2849"),sQuery(id+"F0.wireOp",EDGE,"E2850"),sQuery(id+"F0.wireOp",EDGE,"E2851"),sQuery(id+"F0.wireOp",EDGE,"E2852"),sQuery(id+"F0.wireOp",EDGE,"E2853"),sQuery(id+"F0.wireOp",EDGE,"E2854"),sQuery(id+"F0.wireOp",EDGE,"E2855"),sQuery(id+"F0.wireOp",EDGE,"E2856"),sQuery(id+"F0.wireOp",EDGE,"E2857"),sQuery(id+"F0.wireOp",EDGE,"E2858"),sQuery(id+"F0.wireOp",EDGE,"E2859"),sQuery(id+"F0.wireOp",EDGE,"E2860"),sQuery(id+"F0.wireOp",EDGE,"E2861"),sQuery(id+"F0.wireOp",EDGE,"E2862"),sQuery(id+"F0.wireOp",EDGE,"E2863"),sQuery(id+"F0.wireOp",EDGE,"E2864"),sQuery(id+"F0.wireOp",EDGE,"E2865"),sQuery(id+"F0.wireOp",EDGE,"E2866"),sQuery(id+"F0.wireOp",EDGE,"E2867"),sQuery(id+"F0.wireOp",EDGE,"E2868"),sQuery(id+"F0.wireOp",EDGE,"E2869"),sQuery(id+"F0.wireOp",EDGE,"E2870"),sQuery(id+"F0.wireOp",EDGE,"E2871"),sQuery(id+"F0.wireOp",EDGE,"E2872"),sQuery(id+"F0.wireOp",EDGE,"E2873"),sQuery(id+"F0.wireOp",EDGE,"E2874"),sQuery(id+"F0.wireOp",EDGE,"E2875"),sQuery(id+"F0.wireOp",EDGE,"E2876"),sQuery(id+"F0.wireOp",EDGE,"E2877"),sQuery(id+"F0.wireOp",EDGE,"E2878"),sQuery(id+"F0.wireOp",EDGE,"E2879"),sQuery(id+"F0.wireOp",EDGE,"E2880"),sQuery(id+"F0.wireOp",EDGE,"E2881"),sQuery(id+"F0.wireOp",EDGE,"E2882"),sQuery(id+"F0.wireOp",EDGE,"E2883"),sQuery(id+"F0.wireOp",EDGE,"E2884"),sQuery(id+"F0.wireOp",EDGE,"E2885"),sQuery(id+"F0.wireOp",EDGE,"E2886"),sQuery(id+"F0.wireOp",EDGE,"E2887"),sQuery(id+"F0.wireOp",EDGE,"E2888"),sQuery(id+"F0.wireOp",EDGE,"E2889"),sQuery(id+"F0.wireOp",EDGE,"E2890"),sQuery(id+"F0.wireOp",EDGE,"E2891"),sQuery(id+"F0.wireOp",EDGE,"E2892"),sQuery(id+"F0.wireOp",EDGE,"E2893"),sQuery(id+"F0.wireOp",EDGE,"E2894"),sQuery(id+"F0.wireOp",EDGE,"E2895"),sQuery(id+"F0.wireOp",EDGE,"E2896"),sQuery(id+"F0.wireOp",EDGE,"E2897"),sQuery(id+"F0.wireOp",EDGE,"E2898"),sQuery(id+"F0.wireOp",EDGE,"E2899"),sQuery(id+"F0.wireOp",EDGE,"E2900"),sQuery(id+"F0.wireOp",EDGE,"E2901"),sQuery(id+"F0.wireOp",EDGE,"E2902"),sQuery(id+"F0.wireOp",EDGE,"E2903"),sQuery(id+"F0.wireOp",EDGE,"E2904"),sQuery(id+"F0.wireOp",EDGE,"E2905"),sQuery(id+"F0.wireOp",EDGE,"E2906"),sQuery(id+"F0.wireOp",EDGE,"E2907"),sQuery(id+"F0.wireOp",EDGE,"E2908"),sQuery(id+"F0.wireOp",EDGE,"E2909"),sQuery(id+"F0.wireOp",EDGE,"E2910"),sQuery(id+"F0.wireOp",EDGE,"E2911"),sQuery(id+"F0.wireOp",EDGE,"E2912"),sQuery(id+"F0.wireOp",EDGE,"E2913"),sQuery(id+"F0.wireOp",EDGE,"E2914"),sQuery(id+"F0.wireOp",EDGE,"E2915"),sQuery(id+"F0.wireOp",EDGE,"E2916"),sQuery(id+"F0.wireOp",EDGE,"E2917"),sQuery(id+"F0.wireOp",EDGE,"E2918"),sQuery(id+"F0.wireOp",EDGE,"E2919"),sQuery(id+"F0.wireOp",EDGE,"E2920"),sQuery(id+"F0.wireOp",EDGE,"E2921"),sQuery(id+"F0.wireOp",EDGE,"E2922"),sQuery(id+"F0.wireOp",EDGE,"E2923"),sQuery(id+"F0.wireOp",EDGE,"E2924"),sQuery(id+"F0.wireOp",EDGE,"E2925"),sQuery(id+"F0.wireOp",EDGE,"E2926"),sQuery(id+"F0.wireOp",EDGE,"E2927"),sQuery(id+"F0.wireOp",EDGE,"E2928"),sQuery(id+"F0.wireOp",EDGE,"E2929"),sQuery(id+"F0.wireOp",EDGE,"E2930"),sQuery(id+"F0.wireOp",EDGE,"E2931"),sQuery(id+"F0.wireOp",EDGE,"E2932"),sQuery(id+"F0.wireOp",EDGE,"E2933"),sQuery(id+"F0.wireOp",EDGE,"E2934"),sQuery(id+"F0.wireOp",EDGE,"E2935"),sQuery(id+"F0.wireOp",EDGE,"E2936"),sQuery(id+"F0.wireOp",EDGE,"E2937"),sQuery(id+"F0.wireOp",EDGE,"E2938"),sQuery(id+"F0.wireOp",EDGE,"E2939"),sQuery(id+"F0.wireOp",EDGE,"E2940"),sQuery(id+"F0.wireOp",EDGE,"E2941"),sQuery(id+"F0.wireOp",EDGE,"E2942"),sQuery(id+"F0.wireOp",EDGE,"E2943"),sQuery(id+"F0.wireOp",EDGE,"E2944"),sQuery(id+"F0.wireOp",EDGE,"E2945"),sQuery(id+"F0.wireOp",EDGE,"E2946"),sQuery(id+"F0.wireOp",EDGE,"E2947"),sQuery(id+"F0.wireOp",EDGE,"E2948"),sQuery(id+"F0.wireOp",EDGE,"E2949"),sQuery(id+"F0.wireOp",EDGE,"E2950"),sQuery(id+"F0.wireOp",EDGE,"E2951"),sQuery(id+"F0.wireOp",EDGE,"E2952"),sQuery(id+"F0.wireOp",EDGE,"E2953"),sQuery(id+"F0.wireOp",EDGE,"E2954"),sQuery(id+"F0.wireOp",EDGE,"E2955"),sQuery(id+"F0.wireOp",EDGE,"E2956"),sQuery(id+"F0.wireOp",EDGE,"E2957"),sQuery(id+"F0.wireOp",EDGE,"E2958"),sQuery(id+"F0.wireOp",EDGE,"E2959"),sQuery(id+"F0.wireOp",EDGE,"E2960"),sQuery(id+"F0.wireOp",EDGE,"E2961"),sQuery(id+"F0.wireOp",EDGE,"E2962"),sQuery(id+"F0.wireOp",EDGE,"E2963"),sQuery(id+"F0.wireOp",EDGE,"E2964"),sQuery(id+"F0.wireOp",EDGE,"E2965"),sQuery(id+"F0.wireOp",EDGE,"E2966"),sQuery(id+"F0.wireOp",EDGE,"E2967"),sQuery(id+"F0.wireOp",EDGE,"E2968"),sQuery(id+"F0.wireOp",EDGE,"E2969"),sQuery(id+"F0.wireOp",EDGE,"E2970"),sQuery(id+"F0.wireOp",EDGE,"E2971"),sQuery(id+"F0.wireOp",EDGE,"E2972"),sQuery(id+"F0.wireOp",EDGE,"E2973"),sQuery(id+"F0.wireOp",EDGE,"E2974"),sQuery(id+"F0.wireOp",EDGE,"E2975"),sQuery(id+"F0.wireOp",EDGE,"E2976"),sQuery(id+"F0.wireOp",EDGE,"E2977"),sQuery(id+"F0.wireOp",EDGE,"E2978"),sQuery(id+"F0.wireOp",EDGE,"E2979"),sQuery(id+"F0.wireOp",EDGE,"E2980"),sQuery(id+"F0.wireOp",EDGE,"E2981"),sQuery(id+"F0.wireOp",EDGE,"E2982"),sQuery(id+"F0.wireOp",EDGE,"E2983"),sQuery(id+"F0.wireOp",EDGE,"E2984"),sQuery(id+"F0.wireOp",EDGE,"E2985"),sQuery(id+"F0.wireOp",EDGE,"E2986"),sQuery(id+"F0.wireOp",EDGE,"E2987"),sQuery(id+"F0.wireOp",EDGE,"E2988"),sQuery(id+"F0.wireOp",EDGE,"E2989"),sQuery(id+"F0.wireOp",EDGE,"E2990"),sQuery(id+"F0.wireOp",EDGE,"E2991"),sQuery(id+"F0.wireOp",EDGE,"E2992"),sQuery(id+"F0.wireOp",EDGE,"E2993"),sQuery(id+"F0.wireOp",EDGE,"E2994"),sQuery(id+"F0.wireOp",EDGE,"E2995"),sQuery(id+"F0.wireOp",EDGE,"E2996"),sQuery(id+"F0.wireOp",EDGE,"E2997"),sQuery(id+"F0.wireOp",EDGE,"E2998"),sQuery(id+"F0.wireOp",EDGE,"E2999"),sQuery(id+"F0.wireOp",EDGE,"E3000"),sQuery(id+"F0.wireOp",EDGE,"E3001"),sQuery(id+"F0.wireOp",EDGE,"E3002"),sQuery(id+"F0.wireOp",EDGE,"E3003"),sQuery(id+"F0.wireOp",EDGE,"E3004"),sQuery(id+"F0.wireOp",EDGE,"E3005"),sQuery(id+"F0.wireOp",EDGE,"E3006"),sQuery(id+"F0.wireOp",EDGE,"E3007"),sQuery(id+"F0.wireOp",EDGE,"E3008"),sQuery(id+"F0.wireOp",EDGE,"E3009"),sQuery(id+"F0.wireOp",EDGE,"E3010"),sQuery(id+"F0.wireOp",EDGE,"E3011"),sQuery(id+"F0.wireOp",EDGE,"E3012"),sQuery(id+"F0.wireOp",EDGE,"E3013"),sQuery(id+"F0.wireOp",EDGE,"E3014"),sQuery(id+"F0.wireOp",EDGE,"E3015"),sQuery(id+"F0.wireOp",EDGE,"E3016"),sQuery(id+"F0.wireOp",EDGE,"E3017"),sQuery(id+"F0.wireOp",EDGE,"E3018"),sQuery(id+"F0.wireOp",EDGE,"E3019"),sQuery(id+"F0.wireOp",EDGE,"E3020"),sQuery(id+"F0.wireOp",EDGE,"E3021"),sQuery(id+"F0.wireOp",EDGE,"E3022"),sQuery(id+"F0.wireOp",EDGE,"E3023"),sQuery(id+"F0.wireOp",EDGE,"E3024"),sQuery(id+"F0.wireOp",EDGE,"E3025"),sQuery(id+"F0.wireOp",EDGE,"E3026"),sQuery(id+"F0.wireOp",EDGE,"E3027"),sQuery(id+"F0.wireOp",EDGE,"E3028"),sQuery(id+"F0.wireOp",EDGE,"E3029"),sQuery(id+"F0.wireOp",EDGE,"E3030"),sQuery(id+"F0.wireOp",EDGE,"E3031"),sQuery(id+"F0.wireOp",EDGE,"E3032"),sQuery(id+"F0.wireOp",EDGE,"E3033"),sQuery(id+"F0.wireOp",EDGE,"E3034"),sQuery(id+"F0.wireOp",EDGE,"E3035"),sQuery(id+"F0.wireOp",EDGE,"E3036"),sQuery(id+"F0.wireOp",EDGE,"E3037"),sQuery(id+"F0.wireOp",EDGE,"E3038"),sQuery(id+"F0.wireOp",EDGE,"E3039"),sQuery(id+"F0.wireOp",EDGE,"E3040"),sQuery(id+"F0.wireOp",EDGE,"E3041"),sQuery(id+"F0.wireOp",EDGE,"E3042"),sQuery(id+"F0.wireOp",EDGE,"E3043"),sQuery(id+"F0.wireOp",EDGE,"E3044"),sQuery(id+"F0.wireOp",EDGE,"E3045"),sQuery(id+"F0.wireOp",EDGE,"E3046"),sQuery(id+"F0.wireOp",EDGE,"E3047"),sQuery(id+"F0.wireOp",EDGE,"E3048"),sQuery(id+"F0.wireOp",EDGE,"E3049"),sQuery(id+"F0.wireOp",EDGE,"E3050"),sQuery(id+"F0.wireOp",EDGE,"E3051"),sQuery(id+"F0.wireOp",EDGE,"E3052"),sQuery(id+"F0.wireOp",EDGE,"E3053"),sQuery(id+"F0.wireOp",EDGE,"E3054"),sQuery(id+"F0.wireOp",EDGE,"E3055"),sQuery(id+"F0.wireOp",EDGE,"E3056"),sQuery(id+"F0.wireOp",EDGE,"E3057"),sQuery(id+"F0.wireOp",EDGE,"E3058"),sQuery(id+"F0.wireOp",EDGE,"E3059"),sQuery(id+"F0.wireOp",EDGE,"E3060"),sQuery(id+"F0.wireOp",EDGE,"E3061"),sQuery(id+"F0.wireOp",EDGE,"E3062"),sQuery(id+"F0.wireOp",EDGE,"E3063"),sQuery(id+"F0.wireOp",EDGE,"E3064"),sQuery(id+"F0.wireOp",EDGE,"E3065"),sQuery(id+"F0.wireOp",EDGE,"E3066"),sQuery(id+"F0.wireOp",EDGE,"E3067"),sQuery(id+"F0.wireOp",EDGE,"E3068"),sQuery(id+"F0.wireOp",EDGE,"E3069"),sQuery(id+"F0.wireOp",EDGE,"E3070"),sQuery(id+"F0.wireOp",EDGE,"E3071"),sQuery(id+"F0.wireOp",EDGE,"E3072"),sQuery(id+"F0.wireOp",EDGE,"E3073"),sQuery(id+"F0.wireOp",EDGE,"E3074"),sQuery(id+"F0.wireOp",EDGE,"E3075"),sQuery(id+"F0.wireOp",EDGE,"E3076"),sQuery(id+"F0.wireOp",EDGE,"E3077"),sQuery(id+"F0.wireOp",EDGE,"E3078"),sQuery(id+"F0.wireOp",EDGE,"E3079"),sQuery(id+"F0.wireOp",EDGE,"E3080"),sQuery(id+"F0.wireOp",EDGE,"E3081"),sQuery(id+"F0.wireOp",EDGE,"E3082"),sQuery(id+"F0.wireOp",EDGE,"E3083"),sQuery(id+"F0.wireOp",EDGE,"E3084"),sQuery(id+"F0.wireOp",EDGE,"E3085"),sQuery(id+"F0.wireOp",EDGE,"E3086"),sQuery(id+"F0.wireOp",EDGE,"E3087"),sQuery(id+"F0.wireOp",EDGE,"E3088"),sQuery(id+"F0.wireOp",EDGE,"E3089"),sQuery(id+"F0.wireOp",EDGE,"E3090"),sQuery(id+"F0.wireOp",EDGE,"E3091"),sQuery(id+"F0.wireOp",EDGE,"E3092"),sQuery(id+"F0.wireOp",EDGE,"E3093"),sQuery(id+"F0.wireOp",EDGE,"E3094"),sQuery(id+"F0.wireOp",EDGE,"E3095"),sQuery(id+"F0.wireOp",EDGE,"E3096"),sQuery(id+"F0.wireOp",EDGE,"E3097"),sQuery(id+"F0.wireOp",EDGE,"E3098"),sQuery(id+"F0.wireOp",EDGE,"E3099"),sQuery(id+"F0.wireOp",EDGE,"E3100"),sQuery(id+"F0.wireOp",EDGE,"E3101"),sQuery(id+"F0.wireOp",EDGE,"E3102"),sQuery(id+"F0.wireOp",EDGE,"E3103"),sQuery(id+"F0.wireOp",EDGE,"E3104"),sQuery(id+"F0.wireOp",EDGE,"E3105"),sQuery(id+"F0.wireOp",EDGE,"E3106"),sQuery(id+"F0.wireOp",EDGE,"E3107"),sQuery(id+"F0.wireOp",EDGE,"E3108"),sQuery(id+"F0.wireOp",EDGE,"E3109"),sQuery(id+"F0.wireOp",EDGE,"E3110"),sQuery(id+"F0.wireOp",EDGE,"E3111"),sQuery(id+"F0.wireOp",EDGE,"E3112"),sQuery(id+"F0.wireOp",EDGE,"E3113"),sQuery(id+"F0.wireOp",EDGE,"E3114"),sQuery(id+"F0.wireOp",EDGE,"E3115"),sQuery(id+"F0.wireOp",EDGE,"E3116"),sQuery(id+"F0.wireOp",EDGE,"E3117"),sQuery(id+"F0.wireOp",EDGE,"E3118"),sQuery(id+"F0.wireOp",EDGE,"E3119"),sQuery(id+"F0.wireOp",EDGE,"E3120"),sQuery(id+"F0.wireOp",EDGE,"E3121"),sQuery(id+"F0.wireOp",EDGE,"E3122"),sQuery(id+"F0.wireOp",EDGE,"E3123"),sQuery(id+"F0.wireOp",EDGE,"E3124"),sQuery(id+"F0.wireOp",EDGE,"E3125"),sQuery(id+"F0.wireOp",EDGE,"E3126"),sQuery(id+"F0.wireOp",EDGE,"E3127"),sQuery(id+"F0.wireOp",EDGE,"E3128"),sQuery(id+"F0.wireOp",EDGE,"E3129"),sQuery(id+"F0.wireOp",EDGE,"E3130"),sQuery(id+"F0.wireOp",EDGE,"E3131"),sQuery(id+"F0.wireOp",EDGE,"E3132"),sQuery(id+"F0.wireOp",EDGE,"E3133"),sQuery(id+"F0.wireOp",EDGE,"E3134"),sQuery(id+"F0.wireOp",EDGE,"E3135"),sQuery(id+"F0.wireOp",EDGE,"E3136"),sQuery(id+"F0.wireOp",EDGE,"E3137"),sQuery(id+"F0.wireOp",EDGE,"E3138"),sQuery(id+"F0.wireOp",EDGE,"E3139"),sQuery(id+"F0.wireOp",EDGE,"E3140"),sQuery(id+"F0.wireOp",EDGE,"E3141"),sQuery(id+"F0.wireOp",EDGE,"E3142"),sQuery(id+"F0.wireOp",EDGE,"E3143"),sQuery(id+"F0.wireOp",EDGE,"E3144"),sQuery(id+"F0.wireOp",EDGE,"E3145"),sQuery(id+"F0.wireOp",EDGE,"E3146"),sQuery(id+"F0.wireOp",EDGE,"E3147"),sQuery(id+"F0.wireOp",EDGE,"E3148"),sQuery(id+"F0.wireOp",EDGE,"E3149"),sQuery(id+"F0.wireOp",EDGE,"E3150"),sQuery(id+"F0.wireOp",EDGE,"E3151"),sQuery(id+"F0.wireOp",EDGE,"E3152"),sQuery(id+"F0.wireOp",EDGE,"E3153"),sQuery(id+"F0.wireOp",EDGE,"E3154"),sQuery(id+"F0.wireOp",EDGE,"E3155"),sQuery(id+"F0.wireOp",EDGE,"E3156"),sQuery(id+"F0.wireOp",EDGE,"E3157"),sQuery(id+"F0.wireOp",EDGE,"E3158"),sQuery(id+"F0.wireOp",EDGE,"E3159"),sQuery(id+"F0.wireOp",EDGE,"E3160"),sQuery(id+"F0.wireOp",EDGE,"E3161"),sQuery(id+"F0.wireOp",EDGE,"E3162"),sQuery(id+"F0.wireOp",EDGE,"E3163"),sQuery(id+"F0.wireOp",EDGE,"E3164"),sQuery(id+"F0.wireOp",EDGE,"E3165"),sQuery(id+"F0.wireOp",EDGE,"E3166"),sQuery(id+"F0.wireOp",EDGE,"E3167"),sQuery(id+"F0.wireOp",EDGE,"E3168"),sQuery(id+"F0.wireOp",EDGE,"E3169"),sQuery(id+"F0.wireOp",EDGE,"E3170"),sQuery(id+"F0.wireOp",EDGE,"E3171"),sQuery(id+"F0.wireOp",EDGE,"E3172"),sQuery(id+"F0.wireOp",EDGE,"E3173"),sQuery(id+"F0.wireOp",EDGE,"E3174"),sQuery(id+"F0.wireOp",EDGE,"E3175"),sQuery(id+"F0.wireOp",EDGE,"E3176"),sQuery(id+"F0.wireOp",EDGE,"E3177"),sQuery(id+"F0.wireOp",EDGE,"E3178"),sQuery(id+"F0.wireOp",EDGE,"E3179"),sQuery(id+"F0.wireOp",EDGE,"E3180"),sQuery(id+"F0.wireOp",EDGE,"E3181"),sQuery(id+"F0.wireOp",EDGE,"E3182"),sQuery(id+"F0.wireOp",EDGE,"E3183"),sQuery(id+"F0.wireOp",EDGE,"E3184"),sQuery(id+"F0.wireOp",EDGE,"E3185"),sQuery(id+"F0.wireOp",EDGE,"E3186"),sQuery(id+"F0.wireOp",EDGE,"E3187"),sQuery(id+"F0.wireOp",EDGE,"E3188"),sQuery(id+"F0.wireOp",EDGE,"E3189"),sQuery(id+"F0.wireOp",EDGE,"E3190"),sQuery(id+"F0.wireOp",EDGE,"E3191"),sQuery(id+"F0.wireOp",EDGE,"E3192"),sQuery(id+"F0.wireOp",EDGE,"E3193"),sQuery(id+"F0.wireOp",EDGE,"E3194"),sQuery(id+"F0.wireOp",EDGE,"E3195"),sQuery(id+"F0.wireOp",EDGE,"E3196"),sQuery(id+"F0.wireOp",EDGE,"E3197"),sQuery(id+"F0.wireOp",EDGE,"E3198"),sQuery(id+"F0.wireOp",EDGE,"E3199"),sQuery(id+"F0.wireOp",EDGE,"E3200"),sQuery(id+"F0.wireOp",EDGE,"E3201"),sQuery(id+"F0.wireOp",EDGE,"E3202"),sQuery(id+"F0.wireOp",EDGE,"E3203"),sQuery(id+"F0.wireOp",EDGE,"E3204"),sQuery(id+"F0.wireOp",EDGE,"E3205"),sQuery(id+"F0.wireOp",EDGE,"E3206"),sQuery(id+"F0.wireOp",EDGE,"E3207"),sQuery(id+"F0.wireOp",EDGE,"E3208"),sQuery(id+"F0.wireOp",EDGE,"E3209"),sQuery(id+"F0.wireOp",EDGE,"E3210"),sQuery(id+"F0.wireOp",EDGE,"E3211"),sQuery(id+"F0.wireOp",EDGE,"E3212"),sQuery(id+"F0.wireOp",EDGE,"E3213"),sQuery(id+"F0.wireOp",EDGE,"E3214"),sQuery(id+"F0.wireOp",EDGE,"E3215"),sQuery(id+"F0.wireOp",EDGE,"E3216"),sQuery(id+"F0.wireOp",EDGE,"E3217"),sQuery(id+"F0.wireOp",EDGE,"E3218"),sQuery(id+"F0.wireOp",EDGE,"E3219"),sQuery(id+"F0.wireOp",EDGE,"E3220"),sQuery(id+"F0.wireOp",EDGE,"E3221"),sQuery(id+"F0.wireOp",EDGE,"E3222"),sQuery(id+"F0.wireOp",EDGE,"E3223"),sQuery(id+"F0.wireOp",EDGE,"E3224"),sQuery(id+"F0.wireOp",EDGE,"E3225"),sQuery(id+"F0.wireOp",EDGE,"E3226"),sQuery(id+"F0.wireOp",EDGE,"E3227"),sQuery(id+"F0.wireOp",EDGE,"E3228"),sQuery(id+"F0.wireOp",EDGE,"E3229"),sQuery(id+"F0.wireOp",EDGE,"E3230"),sQuery(id+"F0.wireOp",EDGE,"E3231"),sQuery(id+"F0.wireOp",EDGE,"E3232"),sQuery(id+"F0.wireOp",EDGE,"E3233"),sQuery(id+"F0.wireOp",EDGE,"E3234"),sQuery(id+"F0.wireOp",EDGE,"E3235"),sQuery(id+"F0.wireOp",EDGE,"E3236"),sQuery(id+"F0.wireOp",EDGE,"E3237"),sQuery(id+"F0.wireOp",EDGE,"E3238"),sQuery(id+"F0.wireOp",EDGE,"E3239"),sQuery(id+"F0.wireOp",EDGE,"E3240"),sQuery(id+"F0.wireOp",EDGE,"E3241"),sQuery(id+"F0.wireOp",EDGE,"E3242"),sQuery(id+"F0.wireOp",EDGE,"E3243"),sQuery(id+"F0.wireOp",EDGE,"E3244"),sQuery(id+"F0.wireOp",EDGE,"E3245"),sQuery(id+"F0.wireOp",EDGE,"E3246"),sQuery(id+"F0.wireOp",EDGE,"E3247"),sQuery(id+"F0.wireOp",EDGE,"E3248"),sQuery(id+"F0.wireOp",EDGE,"E3249"),sQuery(id+"F0.wireOp",EDGE,"E3250"),sQuery(id+"F0.wireOp",EDGE,"E3251"),sQuery(id+"F0.wireOp",EDGE,"E3252"),sQuery(id+"F0.wireOp",EDGE,"E3253"),sQuery(id+"F0.wireOp",EDGE,"E3254"),sQuery(id+"F0.wireOp",EDGE,"E3255"),sQuery(id+"F0.wireOp",EDGE,"E3256"),sQuery(id+"F0.wireOp",EDGE,"E3257"),sQuery(id+"F0.wireOp",EDGE,"E3258"),sQuery(id+"F0.wireOp",EDGE,"E3259"),sQuery(id+"F0.wireOp",EDGE,"E3260"),sQuery(id+"F0.wireOp",EDGE,"E3261"),sQuery(id+"F0.wireOp",EDGE,"E3262"),sQuery(id+"F0.wireOp",EDGE,"E3263"),sQuery(id+"F0.wireOp",EDGE,"E3264"),sQuery(id+"F0.wireOp",EDGE,"E3265"),sQuery(id+"F0.wireOp",EDGE,"E3266"),sQuery(id+"F0.wireOp",EDGE,"E3267"),sQuery(id+"F0.wireOp",EDGE,"E3268"),sQuery(id+"F0.wireOp",EDGE,"E3269"),sQuery(id+"F0.wireOp",EDGE,"E3270"),sQuery(id+"F0.wireOp",EDGE,"E3271"),sQuery(id+"F0.wireOp",EDGE,"E3272"),sQuery(id+"F0.wireOp",EDGE,"E3273"),sQuery(id+"F0.wireOp",EDGE,"E3274"),sQuery(id+"F0.wireOp",EDGE,"E3275"),sQuery(id+"F0.wireOp",EDGE,"E3276"),sQuery(id+"F0.wireOp",EDGE,"E3277"),sQuery(id+"F0.wireOp",EDGE,"E3278"),sQuery(id+"F0.wireOp",EDGE,"E3279"),sQuery(id+"F0.wireOp",EDGE,"E3280"),sQuery(id+"F0.wireOp",EDGE,"E3281"),sQuery(id+"F0.wireOp",EDGE,"E3282"),sQuery(id+"F0.wireOp",EDGE,"E3283"),sQuery(id+"F0.wireOp",EDGE,"E3284"),sQuery(id+"F0.wireOp",EDGE,"E3285"),sQuery(id+"F0.wireOp",EDGE,"E3286"),sQuery(id+"F0.wireOp",EDGE,"E3287"),sQuery(id+"F0.wireOp",EDGE,"E3288"),sQuery(id+"F0.wireOp",EDGE,"E3289"),sQuery(id+"F0.wireOp",EDGE,"E3290"),sQuery(id+"F0.wireOp",EDGE,"E3291"),sQuery(id+"F0.wireOp",EDGE,"E3292"),sQuery(id+"F0.wireOp",EDGE,"E3293"),sQuery(id+"F0.wireOp",EDGE,"E3294"),sQuery(id+"F0.wireOp",EDGE,"E3295"),sQuery(id+"F0.wireOp",EDGE,"E3296"),sQuery(id+"F0.wireOp",EDGE,"E3297"),sQuery(id+"F0.wireOp",EDGE,"E3298"),sQuery(id+"F0.wireOp",EDGE,"E3299"),sQuery(id+"F0.wireOp",EDGE,"E3300"),sQuery(id+"F0.wireOp",EDGE,"E3301"),sQuery(id+"F0.wireOp",EDGE,"E3302"),sQuery(id+"F0.wireOp",EDGE,"E3303"),sQuery(id+"F0.wireOp",EDGE,"E3304"),sQuery(id+"F0.wireOp",EDGE,"E3305"),sQuery(id+"F0.wireOp",EDGE,"E3306"),sQuery(id+"F0.wireOp",EDGE,"E3307"),sQuery(id+"F0.wireOp",EDGE,"E3308"),sQuery(id+"F0.wireOp",EDGE,"E3309"),sQuery(id+"F0.wireOp",EDGE,"E3310"),sQuery(id+"F0.wireOp",EDGE,"E3311"),sQuery(id+"F0.wireOp",EDGE,"E3312"),sQuery(id+"F0.wireOp",EDGE,"E3313"),sQuery(id+"F0.wireOp",EDGE,"E3314"),sQuery(id+"F0.wireOp",EDGE,"E3315"),sQuery(id+"F0.wireOp",EDGE,"E3316"),sQuery(id+"F0.wireOp",EDGE,"E3317"),sQuery(id+"F0.wireOp",EDGE,"E3318"),sQuery(id+"F0.wireOp",EDGE,"E3319"),sQuery(id+"F0.wireOp",EDGE,"E3320"),sQuery(id+"F0.wireOp",EDGE,"E3321"),sQuery(id+"F0.wireOp",EDGE,"E3322"),sQuery(id+"F0.wireOp",EDGE,"E3323"),sQuery(id+"F0.wireOp",EDGE,"E3324"),sQuery(id+"F0.wireOp",EDGE,"E3325"),sQuery(id+"F0.wireOp",EDGE,"E3326"),sQuery(id+"F0.wireOp",EDGE,"E3327"),sQuery(id+"F0.wireOp",EDGE,"E3328"),sQuery(id+"F0.wireOp",EDGE,"E3329"),sQuery(id+"F0.wireOp",EDGE,"E3330"),sQuery(id+"F0.wireOp",EDGE,"E3331"),sQuery(id+"F0.wireOp",EDGE,"E3332"),sQuery(id+"F0.wireOp",EDGE,"E3333"),sQuery(id+"F0.wireOp",EDGE,"E3334"),sQuery(id+"F0.wireOp",EDGE,"E3335"),sQuery(id+"F0.wireOp",EDGE,"E3336"),sQuery(id+"F0.wireOp",EDGE,"E3337"),sQuery(id+"F0.wireOp",EDGE,"E3338"),sQuery(id+"F0.wireOp",EDGE,"E3339"),sQuery(id+"F0.wireOp",EDGE,"E3340"),sQuery(id+"F0.wireOp",EDGE,"E3341"),sQuery(id+"F0.wireOp",EDGE,"E3342"),sQuery(id+"F0.wireOp",EDGE,"E3343"),sQuery(id+"F0.wireOp",EDGE,"E3344"),sQuery(id+"F0.wireOp",EDGE,"E3345"),sQuery(id+"F0.wireOp",EDGE,"E3346"),sQuery(id+"F0.wireOp",EDGE,"E3347"),sQuery(id+"F0.wireOp",EDGE,"E3348"),sQuery(id+"F0.wireOp",EDGE,"E3349"),sQuery(id+"F0.wireOp",EDGE,"E3350"),sQuery(id+"F0.wireOp",EDGE,"E3351"),sQuery(id+"F0.wireOp",EDGE,"E3352"),sQuery(id+"F0.wireOp",EDGE,"E3353"),sQuery(id+"F0.wireOp",EDGE,"E3354"),sQuery(id+"F0.wireOp",EDGE,"E3355"),sQuery(id+"F0.wireOp",EDGE,"E3356"),sQuery(id+"F0.wireOp",EDGE,"E3357"),sQuery(id+"F0.wireOp",EDGE,"E3358"),sQuery(id+"F0.wireOp",EDGE,"E3359"),sQuery(id+"F0.wireOp",EDGE,"E3360"),sQuery(id+"F0.wireOp",EDGE,"E3361"),sQuery(id+"F0.wireOp",EDGE,"E3362"),sQuery(id+"F0.wireOp",EDGE,"E3363"),sQuery(id+"F0.wireOp",EDGE,"E3364"),sQuery(id+"F0.wireOp",EDGE,"E3365"),sQuery(id+"F0.wireOp",EDGE,"E3366"),sQuery(id+"F0.wireOp",EDGE,"E3367"),sQuery(id+"F0.wireOp",EDGE,"E3368"),sQuery(id+"F0.wireOp",EDGE,"E3369"),sQuery(id+"F0.wireOp",EDGE,"E3370"),sQuery(id+"F0.wireOp",EDGE,"E3371"),sQuery(id+"F0.wireOp",EDGE,"E3372"),sQuery(id+"F0.wireOp",EDGE,"E3373"),sQuery(id+"F0.wireOp",EDGE,"E3374"),sQuery(id+"F0.wireOp",EDGE,"E3375"),sQuery(id+"F0.wireOp",EDGE,"E3376"),sQuery(id+"F0.wireOp",EDGE,"E3377"),sQuery(id+"F0.wireOp",EDGE,"E3378"),sQuery(id+"F0.wireOp",EDGE,"E3379"),sQuery(id+"F0.wireOp",EDGE,"E3380"),sQuery(id+"F0.wireOp",EDGE,"E3381"),sQuery(id+"F0.wireOp",EDGE,"E3382"),sQuery(id+"F0.wireOp",EDGE,"E3383"),sQuery(id+"F0.wireOp",EDGE,"E3384"),sQuery(id+"F0.wireOp",EDGE,"E3385"),sQuery(id+"F0.wireOp",EDGE,"E3386"),sQuery(id+"F0.wireOp",EDGE,"E3387"),sQuery(id+"F0.wireOp",EDGE,"E3388"),sQuery(id+"F0.wireOp",EDGE,"E3389"),sQuery(id+"F0.wireOp",EDGE,"E3390"),sQuery(id+"F0.wireOp",EDGE,"E3391"),sQuery(id+"F0.wireOp",EDGE,"E3392"),sQuery(id+"F0.wireOp",EDGE,"E3393"),sQuery(id+"F0.wireOp",EDGE,"E3394"),sQuery(id+"F0.wireOp",EDGE,"E3395"),sQuery(id+"F0.wireOp",EDGE,"E3396"),sQuery(id+"F0.wireOp",EDGE,"E3397"),sQuery(id+"F0.wireOp",EDGE,"E3398"),sQuery(id+"F0.wireOp",EDGE,"E3399"),sQuery(id+"F0.wireOp",EDGE,"E3400"),sQuery(id+"F0.wireOp",EDGE,"E3401"),sQuery(id+"F0.wireOp",EDGE,"E3402"),sQuery(id+"F0.wireOp",EDGE,"E3403"),sQuery(id+"F0.wireOp",EDGE,"E3404"),sQuery(id+"F0.wireOp",EDGE,"E3405"),sQuery(id+"F0.wireOp",EDGE,"E3406"),sQuery(id+"F0.wireOp",EDGE,"E3407"),sQuery(id+"F0.wireOp",EDGE,"E3408"),sQuery(id+"F0.wireOp",EDGE,"E3409"),sQuery(id+"F0.wireOp",EDGE,"E3410"),sQuery(id+"F0.wireOp",EDGE,"E3411"),sQuery(id+"F0.wireOp",EDGE,"E3412"),sQuery(id+"F0.wireOp",EDGE,"E3413"),sQuery(id+"F0.wireOp",EDGE,"E3414"),sQuery(id+"F0.wireOp",EDGE,"E3415"),sQuery(id+"F0.wireOp",EDGE,"E3416"),sQuery(id+"F0.wireOp",EDGE,"E3417"),sQuery(id+"F0.wireOp",EDGE,"E3418"),sQuery(id+"F0.wireOp",EDGE,"E3419"),sQuery(id+"F0.wireOp",EDGE,"E3420"),sQuery(id+"F0.wireOp",EDGE,"E3421"),sQuery(id+"F0.wireOp",EDGE,"E3422"),sQuery(id+"F0.wireOp",EDGE,"E3423"),sQuery(id+"F0.wireOp",EDGE,"E3424"),sQuery(id+"F0.wireOp",EDGE,"E3425"),sQuery(id+"F0.wireOp",EDGE,"E3426"),sQuery(id+"F0.wireOp",EDGE,"E3427"),sQuery(id+"F0.wireOp",EDGE,"E3428"),sQuery(id+"F0.wireOp",EDGE,"E3429"),sQuery(id+"F0.wireOp",EDGE,"E3430"),sQuery(id+"F0.wireOp",EDGE,"E3431"),sQuery(id+"F0.wireOp",EDGE,"E3432"),sQuery(id+"F0.wireOp",EDGE,"E3433"),sQuery(id+"F0.wireOp",EDGE,"E3434"),sQuery(id+"F0.wireOp",EDGE,"E3435"),sQuery(id+"F0.wireOp",EDGE,"E3436"),sQuery(id+"F0.wireOp",EDGE,"E3437"),sQuery(id+"F0.wireOp",EDGE,"E3438"),sQuery(id+"F0.wireOp",EDGE,"E3439"),sQuery(id+"F0.wireOp",EDGE,"E3440"),sQuery(id+"F0.wireOp",EDGE,"E3441"),sQuery(id+"F0.wireOp",EDGE,"E3442"),sQuery(id+"F0.wireOp",EDGE,"E3443"),sQuery(id+"F0.wireOp",EDGE,"E3444"),sQuery(id+"F0.wireOp",EDGE,"E3445"),sQuery(id+"F0.wireOp",EDGE,"E3446"),sQuery(id+"F0.wireOp",EDGE,"E3447"),sQuery(id+"F0.wireOp",EDGE,"E3448"),sQuery(id+"F0.wireOp",EDGE,"E3449"),sQuery(id+"F0.wireOp",EDGE,"E3450"),sQuery(id+"F0.wireOp",EDGE,"E3451"),sQuery(id+"F0.wireOp",EDGE,"E3452"),sQuery(id+"F0.wireOp",EDGE,"E3453"),sQuery(id+"F0.wireOp",EDGE,"E3454"),sQuery(id+"F0.wireOp",EDGE,"E3455"),sQuery(id+"F0.wireOp",EDGE,"E3456"),sQuery(id+"F0.wireOp",EDGE,"E3457"),sQuery(id+"F0.wireOp",EDGE,"E3458"),sQuery(id+"F0.wireOp",EDGE,"E3459"),sQuery(id+"F0.wireOp",EDGE,"E3460"),sQuery(id+"F0.wireOp",EDGE,"E3461"),sQuery(id+"F0.wireOp",EDGE,"E3462"),sQuery(id+"F0.wireOp",EDGE,"E3463"),sQuery(id+"F0.wireOp",EDGE,"E3464"),sQuery(id+"F0.wireOp",EDGE,"E3465"),sQuery(id+"F0.wireOp",EDGE,"E3466"),sQuery(id+"F0.wireOp",EDGE,"E3467"),sQuery(id+"F0.wireOp",EDGE,"E3468"),sQuery(id+"F0.wireOp",EDGE,"E3469"),sQuery(id+"F0.wireOp",EDGE,"E3470"),sQuery(id+"F0.wireOp",EDGE,"E3471"),sQuery(id+"F0.wireOp",EDGE,"E3472"),sQuery(id+"F0.wireOp",EDGE,"E3473"),sQuery(id+"F0.wireOp",EDGE,"E3474"),sQuery(id+"F0.wireOp",EDGE,"E3475"),sQuery(id+"F0.wireOp",EDGE,"E3476"),sQuery(id+"F0.wireOp",EDGE,"E3477"),sQuery(id+"F0.wireOp",EDGE,"E3478"),sQuery(id+"F0.wireOp",EDGE,"E3479"),sQuery(id+"F0.wireOp",EDGE,"E3480"),sQuery(id+"F0.wireOp",EDGE,"E3481"),sQuery(id+"F0.wireOp",EDGE,"E3482"),sQuery(id+"F0.wireOp",EDGE,"E3483"),sQuery(id+"F0.wireOp",EDGE,"E3484"),sQuery(id+"F0.wireOp",EDGE,"E3485"),sQuery(id+"F0.wireOp",EDGE,"E3486"),sQuery(id+"F0.wireOp",EDGE,"E3487"),sQuery(id+"F0.wireOp",EDGE,"E3488"),sQuery(id+"F0.wireOp",EDGE,"E3489"),sQuery(id+"F0.wireOp",EDGE,"E3490"),sQuery(id+"F0.wireOp",EDGE,"E3491"),sQuery(id+"F0.wireOp",EDGE,"E3492"),sQuery(id+"F0.wireOp",EDGE,"E3493"),sQuery(id+"F0.wireOp",EDGE,"E3494"),sQuery(id+"F0.wireOp",EDGE,"E3495"),sQuery(id+"F0.wireOp",EDGE,"E3496"),sQuery(id+"F0.wireOp",EDGE,"E3497"),sQuery(id+"F0.wireOp",EDGE,"E3498"),sQuery(id+"F0.wireOp",EDGE,"E3499"),sQuery(id+"F0.wireOp",EDGE,"E3500"),sQuery(id+"F0.wireOp",EDGE,"E3501"),sQuery(id+"F0.wireOp",EDGE,"E3502"),sQuery(id+"F0.wireOp",EDGE,"E3503"),sQuery(id+"F0.wireOp",EDGE,"E3504"),sQuery(id+"F0.wireOp",EDGE,"E3505"),sQuery(id+"F0.wireOp",EDGE,"E3506"),sQuery(id+"F0.wireOp",EDGE,"E3507"),sQuery(id+"F0.wireOp",EDGE,"E3508"),sQuery(id+"F0.wireOp",EDGE,"E3509"),sQuery(id+"F0.wireOp",EDGE,"E3510"),sQuery(id+"F0.wireOp",EDGE,"E3511"),sQuery(id+"F0.wireOp",EDGE,"E3512"),sQuery(id+"F0.wireOp",EDGE,"E3513"),sQuery(id+"F0.wireOp",EDGE,"E3514"),sQuery(id+"F0.wireOp",EDGE,"E3515"),sQuery(id+"F0.wireOp",EDGE,"E3516"),sQuery(id+"F0.wireOp",EDGE,"E3517"),sQuery(id+"F0.wireOp",EDGE,"E3518"),sQuery(id+"F0.wireOp",EDGE,"E3519"),sQuery(id+"F0.wireOp",EDGE,"E3520"),sQuery(id+"F0.wireOp",EDGE,"E3521"),sQuery(id+"F0.wireOp",EDGE,"E3522"),sQuery(id+"F0.wireOp",EDGE,"E3523"),sQuery(id+"F0.wireOp",EDGE,"E3524"),sQuery(id+"F0.wireOp",EDGE,"E3525"),sQuery(id+"F0.wireOp",EDGE,"E3526"),sQuery(id+"F0.wireOp",EDGE,"E3527"),sQuery(id+"F0.wireOp",EDGE,"E3528"),sQuery(id+"F0.wireOp",EDGE,"E3529"),sQuery(id+"F0.wireOp",EDGE,"E3530"),sQuery(id+"F0.wireOp",EDGE,"E3531"),sQuery(id+"F0.wireOp",EDGE,"E3532"),sQuery(id+"F0.wireOp",EDGE,"E3533"),sQuery(id+"F0.wireOp",EDGE,"E3534"),sQuery(id+"F0.wireOp",EDGE,"E3535"),sQuery(id+"F0.wireOp",EDGE,"E3536"),sQuery(id+"F0.wireOp",EDGE,"E3537"),sQuery(id+"F0.wireOp",EDGE,"E3538"),sQuery(id+"F0.wireOp",EDGE,"E3539"),sQuery(id+"F0.wireOp",EDGE,"E3540"),sQuery(id+"F0.wireOp",EDGE,"E3541"),sQuery(id+"F0.wireOp",EDGE,"E3542"),sQuery(id+"F0.wireOp",EDGE,"E3543"),sQuery(id+"F0.wireOp",EDGE,"E3544"),sQuery(id+"F0.wireOp",EDGE,"E3545"),sQuery(id+"F0.wireOp",EDGE,"E3546"),sQuery(id+"F0.wireOp",EDGE,"E3547"),sQuery(id+"F0.wireOp",EDGE,"E3548"),sQuery(id+"F0.wireOp",EDGE,"E3549"),sQuery(id+"F0.wireOp",EDGE,"E3550"),sQuery(id+"F0.wireOp",EDGE,"E3551"),sQuery(id+"F0.wireOp",EDGE,"E3552"),sQuery(id+"F0.wireOp",EDGE,"E3553"),sQuery(id+"F0.wireOp",EDGE,"E3554"),sQuery(id+"F0.wireOp",EDGE,"E3555"),sQuery(id+"F0.wireOp",EDGE,"E3556"),sQuery(id+"F0.wireOp",EDGE,"E3557"),sQuery(id+"F0.wireOp",EDGE,"E3558"),sQuery(id+"F0.wireOp",EDGE,"E3559"),sQuery(id+"F0.wireOp",EDGE,"E3560"),sQuery(id+"F0.wireOp",EDGE,"E3561"),sQuery(id+"F0.wireOp",EDGE,"E3562"),sQuery(id+"F0.wireOp",EDGE,"E3563"),sQuery(id+"F0.wireOp",EDGE,"E3564"),sQuery(id+"F0.wireOp",EDGE,"E3565"),sQuery(id+"F0.wireOp",EDGE,"E3566"),sQuery(id+"F0.wireOp",EDGE,"E3567"),sQuery(id+"F0.wireOp",EDGE,"E3568"),sQuery(id+"F0.wireOp",EDGE,"E3569"),sQuery(id+"F0.wireOp",EDGE,"E3570"),sQuery(id+"F0.wireOp",EDGE,"E3571"),sQuery(id+"F0.wireOp",EDGE,"E3572"),sQuery(id+"F0.wireOp",EDGE,"E3573"),sQuery(id+"F0.wireOp",EDGE,"E3574"),sQuery(id+"F0.wireOp",EDGE,"E3575"),sQuery(id+"F0.wireOp",EDGE,"E3576"),sQuery(id+"F0.wireOp",EDGE,"E3577"),sQuery(id+"F0.wireOp",EDGE,"E3578"),sQuery(id+"F0.wireOp",EDGE,"E3579"),sQuery(id+"F0.wireOp",EDGE,"E3580"),sQuery(id+"F0.wireOp",EDGE,"E3581"),sQuery(id+"F0.wireOp",EDGE,"E3582"),sQuery(id+"F0.wireOp",EDGE,"E3583"),sQuery(id+"F0.wireOp",EDGE,"E3584"),sQuery(id+"F0.wireOp",EDGE,"E3585"),sQuery(id+"F0.wireOp",EDGE,"E3586"),sQuery(id+"F0.wireOp",EDGE,"E3587"),sQuery(id+"F0.wireOp",EDGE,"E3588"),sQuery(id+"F0.wireOp",EDGE,"E3589"),sQuery(id+"F0.wireOp",EDGE,"E3590"),sQuery(id+"F0.wireOp",EDGE,"E3591"),sQuery(id+"F0.wireOp",EDGE,"E3592"),sQuery(id+"F0.wireOp",EDGE,"E3593"),sQuery(id+"F0.wireOp",EDGE,"E3594"),sQuery(id+"F0.wireOp",EDGE,"E3595"),sQuery(id+"F0.wireOp",EDGE,"E3596"),sQuery(id+"F0.wireOp",EDGE,"E3597"),sQuery(id+"F0.wireOp",EDGE,"E3598"),sQuery(id+"F0.wireOp",EDGE,"E3599"),sQuery(id+"F0.wireOp",EDGE,"E3600"),sQuery(id+"F0.wireOp",EDGE,"E3601"),sQuery(id+"F0.wireOp",EDGE,"E3602"),sQuery(id+"F0.wireOp",EDGE,"E3603"),sQuery(id+"F0.wireOp",EDGE,"E3604"),sQuery(id+"F0.wireOp",EDGE,"E3605"),sQuery(id+"F0.wireOp",EDGE,"E3606"),sQuery(id+"F0.wireOp",EDGE,"E3607"),sQuery(id+"F0.wireOp",EDGE,"E3608"),sQuery(id+"F0.wireOp",EDGE,"E3609"),sQuery(id+"F0.wireOp",EDGE,"E3610"),sQuery(id+"F0.wireOp",EDGE,"E3611"),sQuery(id+"F0.wireOp",EDGE,"E3612"),sQuery(id+"F0.wireOp",EDGE,"E3613"),sQuery(id+"F0.wireOp",EDGE,"E3614"),sQuery(id+"F0.wireOp",EDGE,"E3615"),sQuery(id+"F0.wireOp",EDGE,"E3616"),sQuery(id+"F0.wireOp",EDGE,"E3617"),sQuery(id+"F0.wireOp",EDGE,"E3618"),sQuery(id+"F0.wireOp",EDGE,"E3619"),sQuery(id+"F0.wireOp",EDGE,"E3620"),sQuery(id+"F0.wireOp",EDGE,"E3621"),sQuery(id+"F0.wireOp",EDGE,"E3622"),sQuery(id+"F0.wireOp",EDGE,"E3623"),sQuery(id+"F0.wireOp",EDGE,"E3624"),sQuery(id+"F0.wireOp",EDGE,"E3625"),sQuery(id+"F0.wireOp",EDGE,"E3626"),sQuery(id+"F0.wireOp",EDGE,"E3627"),sQuery(id+"F0.wireOp",EDGE,"E3628"),sQuery(id+"F0.wireOp",EDGE,"E3629"),sQuery(id+"F0.wireOp",EDGE,"E3630"),sQuery(id+"F0.wireOp",EDGE,"E3631"),sQuery(id+"F0.wireOp",EDGE,"E3632"),sQuery(id+"F0.wireOp",EDGE,"E3633"),sQuery(id+"F0.wireOp",EDGE,"E3634"),sQuery(id+"F0.wireOp",EDGE,"E3635"),sQuery(id+"F0.wireOp",EDGE,"E3636"),sQuery(id+"F0.wireOp",EDGE,"E3637"),sQuery(id+"F0.wireOp",EDGE,"E3638"),sQuery(id+"F0.wireOp",EDGE,"E3639"),sQuery(id+"F0.wireOp",EDGE,"E3640"),sQuery(id+"F0.wireOp",EDGE,"E3641"),sQuery(id+"F0.wireOp",EDGE,"E3642"),sQuery(id+"F0.wireOp",EDGE,"E3643"),sQuery(id+"F0.wireOp",EDGE,"E3644"),sQuery(id+"F0.wireOp",EDGE,"E3645"),sQuery(id+"F0.wireOp",EDGE,"E3646"),sQuery(id+"F0.wireOp",EDGE,"E3647"),sQuery(id+"F0.wireOp",EDGE,"E3648"),sQuery(id+"F0.wireOp",EDGE,"E3649"),sQuery(id+"F0.wireOp",EDGE,"E3650"),sQuery(id+"F0.wireOp",EDGE,"E3651"),sQuery(id+"F0.wireOp",EDGE,"E3652"),sQuery(id+"F0.wireOp",EDGE,"E3653"),sQuery(id+"F0.wireOp",EDGE,"E3654"),sQuery(id+"F0.wireOp",EDGE,"E3655"),sQuery(id+"F0.wireOp",EDGE,"E3656"),sQuery(id+"F0.wireOp",EDGE,"E3657"),sQuery(id+"F0.wireOp",EDGE,"E3658"),sQuery(id+"F0.wireOp",EDGE,"E3659"),sQuery(id+"F0.wireOp",EDGE,"E3660"),sQuery(id+"F0.wireOp",EDGE,"E3661"),sQuery(id+"F0.wireOp",EDGE,"E3662"),sQuery(id+"F0.wireOp",EDGE,"E3663"),sQuery(id+"F0.wireOp",EDGE,"E3664"),sQuery(id+"F0.wireOp",EDGE,"E3665"),sQuery(id+"F0.wireOp",EDGE,"E3666"),sQuery(id+"F0.wireOp",EDGE,"E3667"),sQuery(id+"F0.wireOp",EDGE,"E3668"),sQuery(id+"F0.wireOp",EDGE,"E3669"),sQuery(id+"F0.wireOp",EDGE,"E3670"),sQuery(id+"F0.wireOp",EDGE,"E3671"),sQuery(id+"F0.wireOp",EDGE,"E3672"),sQuery(id+"F0.wireOp",EDGE,"E3673"),sQuery(id+"F0.wireOp",EDGE,"E3674"),sQuery(id+"F0.wireOp",EDGE,"E3675"),sQuery(id+"F0.wireOp",EDGE,"E3676"),sQuery(id+"F0.wireOp",EDGE,"E3677"),sQuery(id+"F0.wireOp",EDGE,"E3678"),sQuery(id+"F0.wireOp",EDGE,"E3679"),sQuery(id+"F0.wireOp",EDGE,"E3680"),sQuery(id+"F0.wireOp",EDGE,"E3681"),sQuery(id+"F0.wireOp",EDGE,"E3682"),sQuery(id+"F0.wireOp",EDGE,"E3683"),sQuery(id+"F0.wireOp",EDGE,"E3684"),sQuery(id+"F0.wireOp",EDGE,"E3685"),sQuery(id+"F0.wireOp",EDGE,"E3686"),sQuery(id+"F0.wireOp",EDGE,"E3687"),sQuery(id+"F0.wireOp",EDGE,"E3688"),sQuery(id+"F0.wireOp",EDGE,"E3689"),sQuery(id+"F0.wireOp",EDGE,"E3690"),sQuery(id+"F0.wireOp",EDGE,"E3691"),sQuery(id+"F0.wireOp",EDGE,"E3692"),sQuery(id+"F0.wireOp",EDGE,"E3693"),sQuery(id+"F0.wireOp",EDGE,"E3694"),sQuery(id+"F0.wireOp",EDGE,"E3695"),sQuery(id+"F0.wireOp",EDGE,"E3696"),sQuery(id+"F0.wireOp",EDGE,"E3697"),sQuery(id+"F0.wireOp",EDGE,"E3698"),sQuery(id+"F0.wireOp",EDGE,"E3699"),sQuery(id+"F0.wireOp",EDGE,"E3700"),sQuery(id+"F0.wireOp",EDGE,"E3701"),sQuery(id+"F0.wireOp",EDGE,"E3702"),sQuery(id+"F0.wireOp",EDGE,"E3703"),sQuery(id+"F0.wireOp",EDGE,"E3704"),sQuery(id+"F0.wireOp",EDGE,"E3705"),sQuery(id+"F0.wireOp",EDGE,"E3706"),sQuery(id+"F0.wireOp",EDGE,"E3707"),sQuery(id+"F0.wireOp",EDGE,"E3708"),sQuery(id+"F0.wireOp",EDGE,"E3709"),sQuery(id+"F0.wireOp",EDGE,"E3710"),sQuery(id+"F0.wireOp",EDGE,"E3711"),sQuery(id+"F0.wireOp",EDGE,"E3712"),sQuery(id+"F0.wireOp",EDGE,"E3713"),sQuery(id+"F0.wireOp",EDGE,"E3714"),sQuery(id+"F0.wireOp",EDGE,"E3715"),sQuery(id+"F0.wireOp",EDGE,"E3716"),sQuery(id+"F0.wireOp",EDGE,"E3717"),sQuery(id+"F0.wireOp",EDGE,"E3718"),sQuery(id+"F0.wireOp",EDGE,"E3719"),sQuery(id+"F0.wireOp",EDGE,"E3720"),sQuery(id+"F0.wireOp",EDGE,"E3721"),sQuery(id+"F0.wireOp",EDGE,"E3722"),sQuery(id+"F0.wireOp",EDGE,"E3723"),sQuery(id+"F0.wireOp",EDGE,"E3724"),sQuery(id+"F0.wireOp",EDGE,"E3725"),sQuery(id+"F0.wireOp",EDGE,"E3726"),sQuery(id+"F0.wireOp",EDGE,"E3727"),sQuery(id+"F0.wireOp",EDGE,"E3728"),sQuery(id+"F0.wireOp",EDGE,"E3729"),sQuery(id+"F0.wireOp",EDGE,"E3730"),sQuery(id+"F0.wireOp",EDGE,"E3731"),sQuery(id+"F0.wireOp",EDGE,"E3732"),sQuery(id+"F0.wireOp",EDGE,"E3733"),sQuery(id+"F0.wireOp",EDGE,"E3734"),sQuery(id+"F0.wireOp",EDGE,"E3735"),sQuery(id+"F0.wireOp",EDGE,"E3736"),sQuery(id+"F0.wireOp",EDGE,"E3737"),sQuery(id+"F0.wireOp",EDGE,"E3738"),sQuery(id+"F0.wireOp",EDGE,"E3739"),sQuery(id+"F0.wireOp",EDGE,"E3740"),sQuery(id+"F0.wireOp",EDGE,"E3741"),sQuery(id+"F0.wireOp",EDGE,"E3742"),sQuery(id+"F0.wireOp",EDGE,"E3743"),sQuery(id+"F0.wireOp",EDGE,"E3744"),sQuery(id+"F0.wireOp",EDGE,"E3745"),sQuery(id+"F0.wireOp",EDGE,"E3746"),sQuery(id+"F0.wireOp",EDGE,"E3747"),sQuery(id+"F0.wireOp",EDGE,"E3748"),sQuery(id+"F0.wireOp",EDGE,"E3749"),sQuery(id+"F0.wireOp",EDGE,"E3750"),sQuery(id+"F0.wireOp",EDGE,"E3751"),sQuery(id+"F0.wireOp",EDGE,"E3752"),sQuery(id+"F0.wireOp",EDGE,"E3753"),sQuery(id+"F0.wireOp",EDGE,"E3754"),sQuery(id+"F0.wireOp",EDGE,"E3755"),sQuery(id+"F0.wireOp",EDGE,"E3756"),sQuery(id+"F0.wireOp",EDGE,"E3757"),sQuery(id+"F0.wireOp",EDGE,"E3758"),sQuery(id+"F0.wireOp",EDGE,"E3759"),sQuery(id+"F0.wireOp",EDGE,"E3760"),sQuery(id+"F0.wireOp",EDGE,"E3761"),sQuery(id+"F0.wireOp",EDGE,"E3762"),sQuery(id+"F0.wireOp",EDGE,"E3763"),sQuery(id+"F0.wireOp",EDGE,"E3764"),sQuery(id+"F0.wireOp",EDGE,"E3765"),sQuery(id+"F0.wireOp",EDGE,"E3766"),sQuery(id+"F0.wireOp",EDGE,"E3767"),sQuery(id+"F0.wireOp",EDGE,"E3768"),sQuery(id+"F0.wireOp",EDGE,"E3769"),sQuery(id+"F0.wireOp",EDGE,"E3770"),sQuery(id+"F0.wireOp",EDGE,"E3771"),sQuery(id+"F0.wireOp",EDGE,"E3772"),sQuery(id+"F0.wireOp",EDGE,"E3773"),sQuery(id+"F0.wireOp",EDGE,"E3774"),sQuery(id+"F0.wireOp",EDGE,"E3775"),sQuery(id+"F0.wireOp",EDGE,"E3776"),sQuery(id+"F0.wireOp",EDGE,"E3777"),sQuery(id+"F0.wireOp",EDGE,"E3778"),sQuery(id+"F0.wireOp",EDGE,"E3779"),sQuery(id+"F0.wireOp",EDGE,"E3780"),sQuery(id+"F0.wireOp",EDGE,"E3781"),sQuery(id+"F0.wireOp",EDGE,"E3782"),sQuery(id+"F0.wireOp",EDGE,"E3783"),sQuery(id+"F0.wireOp",EDGE,"E3784"),sQuery(id+"F0.wireOp",EDGE,"E3785"),sQuery(id+"F0.wireOp",EDGE,"E3786"),sQuery(id+"F0.wireOp",EDGE,"E3787"),sQuery(id+"F0.wireOp",EDGE,"E3788"),sQuery(id+"F0.wireOp",EDGE,"E3789"),sQuery(id+"F0.wireOp",EDGE,"E3790"),sQuery(id+"F0.wireOp",EDGE,"E3791"),sQuery(id+"F0.wireOp",EDGE,"E3792"),sQuery(id+"F0.wireOp",EDGE,"E3793"),sQuery(id+"F0.wireOp",EDGE,"E3794"),sQuery(id+"F0.wireOp",EDGE,"E3795"),sQuery(id+"F0.wireOp",EDGE,"E3796"),sQuery(id+"F0.wireOp",EDGE,"E3797"),sQuery(id+"F0.wireOp",EDGE,"E3798"),sQuery(id+"F0.wireOp",EDGE,"E3799"),sQuery(id+"F0.wireOp",EDGE,"E3800"),sQuery(id+"F0.wireOp",EDGE,"E3801"),sQuery(id+"F0.wireOp",EDGE,"E3802"),sQuery(id+"F0.wireOp",EDGE,"E3803"),sQuery(id+"F0.wireOp",EDGE,"E3804"),sQuery(id+"F0.wireOp",EDGE,"E3805"),sQuery(id+"F0.wireOp",EDGE,"E3806"),sQuery(id+"F0.wireOp",EDGE,"E3807"),sQuery(id+"F0.wireOp",EDGE,"E3808"),sQuery(id+"F0.wireOp",EDGE,"E3809"),sQuery(id+"F0.wireOp",EDGE,"E3810"),sQuery(id+"F0.wireOp",EDGE,"E3811"),sQuery(id+"F0.wireOp",EDGE,"E3812"),sQuery(id+"F0.wireOp",EDGE,"E3813"),sQuery(id+"F0.wireOp",EDGE,"E3814"),sQuery(id+"F0.wireOp",EDGE,"E3815"),sQuery(id+"F0.wireOp",EDGE,"E3816"),sQuery(id+"F0.wireOp",EDGE,"E3817"),sQuery(id+"F0.wireOp",EDGE,"E3818"),sQuery(id+"F0.wireOp",EDGE,"E3819"),sQuery(id+"F0.wireOp",EDGE,"E3820"),sQuery(id+"F0.wireOp",EDGE,"E3821"),sQuery(id+"F0.wireOp",EDGE,"E3822"),sQuery(id+"F0.wireOp",EDGE,"E3823"),sQuery(id+"F0.wireOp",EDGE,"E3824"),sQuery(id+"F0.wireOp",EDGE,"E3825"),sQuery(id+"F0.wireOp",EDGE,"E3826"),sQuery(id+"F0.wireOp",EDGE,"E3827"),sQuery(id+"F0.wireOp",EDGE,"E3828"),sQuery(id+"F0.wireOp",EDGE,"E3829"),sQuery(id+"F0.wireOp",EDGE,"E3830"),sQuery(id+"F0.wireOp",EDGE,"E3831"),sQuery(id+"F0.wireOp",EDGE,"E3832"),sQuery(id+"F0.wireOp",EDGE,"E3833"),sQuery(id+"F0.wireOp",EDGE,"E3834"),sQuery(id+"F0.wireOp",EDGE,"E3835"),sQuery(id+"F0.wireOp",EDGE,"E3836"),sQuery(id+"F0.wireOp",EDGE,"E3837"),sQuery(id+"F0.wireOp",EDGE,"E3838"),sQuery(id+"F0.wireOp",EDGE,"E3839"),sQuery(id+"F0.wireOp",EDGE,"E3840"),sQuery(id+"F0.wireOp",EDGE,"E3841"),sQuery(id+"F0.wireOp",EDGE,"E3842"),sQuery(id+"F0.wireOp",EDGE,"E3843"),sQuery(id+"F0.wireOp",EDGE,"E3844"),sQuery(id+"F0.wireOp",EDGE,"E3845"),sQuery(id+"F0.wireOp",EDGE,"E3846"),sQuery(id+"F0.wireOp",EDGE,"E3847"),sQuery(id+"F0.wireOp",EDGE,"E3848"),sQuery(id+"F0.wireOp",EDGE,"E3849"),sQuery(id+"F0.wireOp",EDGE,"E3850"),sQuery(id+"F0.wireOp",EDGE,"E3851"),sQuery(id+"F0.wireOp",EDGE,"E3852"),sQuery(id+"F0.wireOp",EDGE,"E3853"),sQuery(id+"F0.wireOp",EDGE,"E3854"),sQuery(id+"F0.wireOp",EDGE,"E3855"),sQuery(id+"F0.wireOp",EDGE,"E3856"),sQuery(id+"F0.wireOp",EDGE,"E3857"),sQuery(id+"F0.wireOp",EDGE,"E3858"),sQuery(id+"F0.wireOp",EDGE,"E3859"),sQuery(id+"F0.wireOp",EDGE,"E3860"),sQuery(id+"F0.wireOp",EDGE,"E3861"),sQuery(id+"F0.wireOp",EDGE,"E3862"),sQuery(id+"F0.wireOp",EDGE,"E3863"),sQuery(id+"F0.wireOp",EDGE,"E3864"),sQuery(id+"F0.wireOp",EDGE,"E3865"),sQuery(id+"F0.wireOp",EDGE,"E3866"),sQuery(id+"F0.wireOp",EDGE,"E3867"),sQuery(id+"F0.wireOp",EDGE,"E3868"),sQuery(id+"F0.wireOp",EDGE,"E3869"),sQuery(id+"F0.wireOp",EDGE,"E3870"),sQuery(id+"F0.wireOp",EDGE,"E3871"),sQuery(id+"F0.wireOp",EDGE,"E3872"),sQuery(id+"F0.wireOp",EDGE,"E3873"),sQuery(id+"F0.wireOp",EDGE,"E3874"),sQuery(id+"F0.wireOp",EDGE,"E3875"),sQuery(id+"F0.wireOp",EDGE,"E3876"),sQuery(id+"F0.wireOp",EDGE,"E3877"),sQuery(id+"F0.wireOp",EDGE,"E3878"),sQuery(id+"F0.wireOp",EDGE,"E3879"),sQuery(id+"F0.wireOp",EDGE,"E3880"),sQuery(id+"F0.wireOp",EDGE,"E3881"),sQuery(id+"F0.wireOp",EDGE,"E3882"),sQuery(id+"F0.wireOp",EDGE,"E3883"),sQuery(id+"F0.wireOp",EDGE,"E3884"),sQuery(id+"F0.wireOp",EDGE,"E3885"),sQuery(id+"F0.wireOp",EDGE,"E3886"),sQuery(id+"F0.wireOp",EDGE,"E3887"),sQuery(id+"F0.wireOp",EDGE,"E3888"),sQuery(id+"F0.wireOp",EDGE,"E3889"),sQuery(id+"F0.wireOp",EDGE,"E3890"),sQuery(id+"F0.wireOp",EDGE,"E3891"),sQuery(id+"F0.wireOp",EDGE,"E3892"),sQuery(id+"F0.wireOp",EDGE,"E3893"),sQuery(id+"F0.wireOp",EDGE,"E3894"),sQuery(id+"F0.wireOp",EDGE,"E3895"),sQuery(id+"F0.wireOp",EDGE,"E3896"),sQuery(id+"F0.wireOp",EDGE,"E3897"),sQuery(id+"F0.wireOp",EDGE,"E3898"),sQuery(id+"F0.wireOp",EDGE,"E3899"),sQuery(id+"F0.wireOp",EDGE,"E3900"),sQuery(id+"F0.wireOp",EDGE,"E3901"),sQuery(id+"F0.wireOp",EDGE,"E3902"),sQuery(id+"F0.wireOp",EDGE,"E3903"),sQuery(id+"F0.wireOp",EDGE,"E3904"),sQuery(id+"F0.wireOp",EDGE,"E3905"),sQuery(id+"F0.wireOp",EDGE,"E3906"),sQuery(id+"F0.wireOp",EDGE,"E3907"),sQuery(id+"F0.wireOp",EDGE,"E3908"),sQuery(id+"F0.wireOp",EDGE,"E3909"),sQuery(id+"F0.wireOp",EDGE,"E3910"),sQuery(id+"F0.wireOp",EDGE,"E3911"),sQuery(id+"F0.wireOp",EDGE,"E3912"),sQuery(id+"F0.wireOp",EDGE,"E3913"),sQuery(id+"F0.wireOp",EDGE,"E3914"),sQuery(id+"F0.wireOp",EDGE,"E3915"),sQuery(id+"F0.wireOp",EDGE,"E3916"),sQuery(id+"F0.wireOp",EDGE,"E3917"),sQuery(id+"F0.wireOp",EDGE,"E3918"),sQuery(id+"F0.wireOp",EDGE,"E3919"),sQuery(id+"F0.wireOp",EDGE,"E3920"),sQuery(id+"F0.wireOp",EDGE,"E3921"),sQuery(id+"F0.wireOp",EDGE,"E3922"),sQuery(id+"F0.wireOp",EDGE,"E3923"),sQuery(id+"F0.wireOp",EDGE,"E3924"),sQuery(id+"F0.wireOp",EDGE,"E3925"),sQuery(id+"F0.wireOp",EDGE,"E3926"),sQuery(id+"F0.wireOp",EDGE,"E3927"),sQuery(id+"F0.wireOp",EDGE,"E3928"),sQuery(id+"F0.wireOp",EDGE,"E3929"),sQuery(id+"F0.wireOp",EDGE,"E3930"),sQuery(id+"F0.wireOp",EDGE,"E3931"),sQuery(id+"F0.wireOp",EDGE,"E3932"),sQuery(id+"F0.wireOp",EDGE,"E3933"),sQuery(id+"F0.wireOp",EDGE,"E3934"),sQuery(id+"F0.wireOp",EDGE,"E3935"),sQuery(id+"F0.wireOp",EDGE,"E3936"),sQuery(id+"F0.wireOp",EDGE,"E3937"),sQuery(id+"F0.wireOp",EDGE,"E3938"),sQuery(id+"F0.wireOp",EDGE,"E3939"),sQuery(id+"F0.wireOp",EDGE,"E3940"),sQuery(id+"F0.wireOp",EDGE,"E3941"),sQuery(id+"F0.wireOp",EDGE,"E3942"),sQuery(id+"F0.wireOp",EDGE,"E3943"),sQuery(id+"F0.wireOp",EDGE,"E3944"),sQuery(id+"F0.wireOp",EDGE,"E3945"),sQuery(id+"F0.wireOp",EDGE,"E3946"),sQuery(id+"F0.wireOp",EDGE,"E3947"),sQuery(id+"F0.wireOp",EDGE,"E3948"),sQuery(id+"F0.wireOp",EDGE,"E3949"),sQuery(id+"F0.wireOp",EDGE,"E3950"),sQuery(id+"F0.wireOp",EDGE,"E3951"),sQuery(id+"F0.wireOp",EDGE,"E3952"),sQuery(id+"F0.wireOp",EDGE,"E3953"),sQuery(id+"F0.wireOp",EDGE,"E3954"),sQuery(id+"F0.wireOp",EDGE,"E3955"),sQuery(id+"F0.wireOp",EDGE,"E3956"),sQuery(id+"F0.wireOp",EDGE,"E3957"),sQuery(id+"F0.wireOp",EDGE,"E3958"),sQuery(id+"F0.wireOp",EDGE,"E3959"),sQuery(id+"F0.wireOp",EDGE,"E3960"),sQuery(id+"F0.wireOp",EDGE,"E3961"),sQuery(id+"F0.wireOp",EDGE,"E3962"),sQuery(id+"F0.wireOp",EDGE,"E3963"),sQuery(id+"F0.wireOp",EDGE,"E3964"),sQuery(id+"F0.wireOp",EDGE,"E3965"),sQuery(id+"F0.wireOp",EDGE,"E3966"),sQuery(id+"F0.wireOp",EDGE,"E3967"),sQuery(id+"F0.wireOp",EDGE,"E3968"),sQuery(id+"F0.wireOp",EDGE,"E3969"),sQuery(id+"F0.wireOp",EDGE,"E3970"),sQuery(id+"F0.wireOp",EDGE,"E3971"),sQuery(id+"F0.wireOp",EDGE,"E3972"),sQuery(id+"F0.wireOp",EDGE,"E3973"),sQuery(id+"F0.wireOp",EDGE,"E3974"),sQuery(id+"F0.wireOp",EDGE,"E3975"),sQuery(id+"F0.wireOp",EDGE,"E3976"),sQuery(id+"F0.wireOp",EDGE,"E3977"),sQuery(id+"F0.wireOp",EDGE,"E3978"),sQuery(id+"F0.wireOp",EDGE,"E3979"),sQuery(id+"F0.wireOp",EDGE,"E3980"),sQuery(id+"F0.wireOp",EDGE,"E3981"),sQuery(id+"F0.wireOp",EDGE,"E3982"),sQuery(id+"F0.wireOp",EDGE,"E3983"),sQuery(id+"F0.wireOp",EDGE,"E3984"),sQuery(id+"F0.wireOp",EDGE,"E3985"),sQuery(id+"F0.wireOp",EDGE,"E3986"),sQuery(id+"F0.wireOp",EDGE,"E3987"),sQuery(id+"F0.wireOp",EDGE,"E3988"),sQuery(id+"F0.wireOp",EDGE,"E3989"),sQuery(id+"F0.wireOp",EDGE,"E3990"),sQuery(id+"F0.wireOp",EDGE,"E3991"),sQuery(id+"F0.wireOp",EDGE,"E3992"),sQuery(id+"F0.wireOp",EDGE,"E3993"),sQuery(id+"F0.wireOp",EDGE,"E3994"),sQuery(id+"F0.wireOp",EDGE,"E3995"),sQuery(id+"F0.wireOp",EDGE,"E3996"),sQuery(id+"F0.wireOp",EDGE,"E3997"),sQuery(id+"F0.wireOp",EDGE,"E3998"),sQuery(id+"F0.wireOp",EDGE,"E3999"),sQuery(id+"F0.wireOp",EDGE,"E4000"),sQuery(id+"F0.wireOp",EDGE,"E4001"),sQuery(id+"F0.wireOp",EDGE,"E4002"),sQuery(id+"F0.wireOp",EDGE,"E4003"),sQuery(id+"F0.wireOp",EDGE,"E4004"),sQuery(id+"F0.wireOp",EDGE,"E4005"),sQuery(id+"F0.wireOp",EDGE,"E4006"),sQuery(id+"F0.wireOp",EDGE,"E4007"),sQuery(id+"F0.wireOp",EDGE,"E4008"),sQuery(id+"F0.wireOp",EDGE,"E4009"),sQuery(id+"F0.wireOp",EDGE,"E4010"),sQuery(id+"F0.wireOp",EDGE,"E4011"),sQuery(id+"F0.wireOp",EDGE,"E4012"),sQuery(id+"F0.wireOp",EDGE,"E4013"),sQuery(id+"F0.wireOp",EDGE,"E4014"),sQuery(id+"F0.wireOp",EDGE,"E4015"),sQuery(id+"F0.wireOp",EDGE,"E4016"),sQuery(id+"F0.wireOp",EDGE,"E4017"),sQuery(id+"F0.wireOp",EDGE,"E4018"),sQuery(id+"F0.wireOp",EDGE,"E4019"),sQuery(id+"F0.wireOp",EDGE,"E4020"),sQuery(id+"F0.wireOp",EDGE,"E4021"),sQuery(id+"F0.wireOp",EDGE,"E4022"),sQuery(id+"F0.wireOp",EDGE,"E4023"),sQuery(id+"F0.wireOp",EDGE,"E4024"),sQuery(id+"F0.wireOp",EDGE,"E4025"),sQuery(id+"F0.wireOp",EDGE,"E4026"),sQuery(id+"F0.wireOp",EDGE,"E4027"),sQuery(id+"F0.wireOp",EDGE,"E4028"),sQuery(id+"F0.wireOp",EDGE,"E4029"),sQuery(id+"F0.wireOp",EDGE,"E4030"),sQuery(id+"F0.wireOp",EDGE,"E4031"),sQuery(id+"F0.wireOp",EDGE,"E4032"),sQuery(id+"F0.wireOp",EDGE,"E4033"),sQuery(id+"F0.wireOp",EDGE,"E4034"),sQuery(id+"F0.wireOp",EDGE,"E4035"),sQuery(id+"F0.wireOp",EDGE,"E4036"),sQuery(id+"F0.wireOp",EDGE,"E4037"),sQuery(id+"F0.wireOp",EDGE,"E4038"),sQuery(id+"F0.wireOp",EDGE,"E4039"),sQuery(id+"F0.wireOp",EDGE,"E4040"),sQuery(id+"F0.wireOp",EDGE,"E4041"),sQuery(id+"F0.wireOp",EDGE,"E4042"),sQuery(id+"F0.wireOp",EDGE,"E4043"),sQuery(id+"F0.wireOp",EDGE,"E4044"),sQuery(id+"F0.wireOp",EDGE,"E4045"),sQuery(id+"F0.wireOp",EDGE,"E4046"),sQuery(id+"F0.wireOp",EDGE,"E4047"),sQuery(id+"F0.wireOp",EDGE,"E4048"),sQuery(id+"F0.wireOp",EDGE,"E4049"),sQuery(id+"F0.wireOp",EDGE,"E4050"),sQuery(id+"F0.wireOp",EDGE,"E4051"),sQuery(id+"F0.wireOp",EDGE,"E4052"),sQuery(id+"F0.wireOp",EDGE,"E4053"),sQuery(id+"F0.wireOp",EDGE,"E4054"),sQuery(id+"F0.wireOp",EDGE,"E4055"),sQuery(id+"F0.wireOp",EDGE,"E4056"),sQuery(id+"F0.wireOp",EDGE,"E4057"),sQuery(id+"F0.wireOp",EDGE,"E4058"),sQuery(id+"F0.wireOp",EDGE,"E4059"),sQuery(id+"F0.wireOp",EDGE,"E4060"),sQuery(id+"F0.wireOp",EDGE,"E4061"),sQuery(id+"F0.wireOp",EDGE,"E4062"),sQuery(id+"F0.wireOp",EDGE,"E4063"),sQuery(id+"F0.wireOp",EDGE,"E4064"),sQuery(id+"F0.wireOp",EDGE,"E4065"),sQuery(id+"F0.wireOp",EDGE,"E4066"),sQuery(id+"F0.wireOp",EDGE,"E4067"),sQuery(id+"F0.wireOp",EDGE,"E4068"),sQuery(id+"F0.wireOp",EDGE,"E4069"),sQuery(id+"F0.wireOp",EDGE,"E4070"),sQuery(id+"F0.wireOp",EDGE,"E4071"),sQuery(id+"F0.wireOp",EDGE,"E4072"),sQuery(id+"F0.wireOp",EDGE,"E4073"),sQuery(id+"F0.wireOp",EDGE,"E4074"),sQuery(id+"F0.wireOp",EDGE,"E4075"),sQuery(id+"F0.wireOp",EDGE,"E4076"),sQuery(id+"F0.wireOp",EDGE,"E4077"),sQuery(id+"F0.wireOp",EDGE,"E4078"),sQuery(id+"F0.wireOp",EDGE,"E4079"),sQuery(id+"F0.wireOp",EDGE,"E4080"),sQuery(id+"F0.wireOp",EDGE,"E4081"),sQuery(id+"F0.wireOp",EDGE,"E4082"),sQuery(id+"F0.wireOp",EDGE,"E4083"),sQuery(id+"F0.wireOp",EDGE,"E4084"),sQuery(id+"F0.wireOp",EDGE,"E4085"),sQuery(id+"F0.wireOp",EDGE,"E4086"),sQuery(id+"F0.wireOp",EDGE,"E4087"),sQuery(id+"F0.wireOp",EDGE,"E4088"),sQuery(id+"F0.wireOp",EDGE,"E4089"),sQuery(id+"F0.wireOp",EDGE,"E4090"),sQuery(id+"F0.wireOp",EDGE,"E4091"),sQuery(id+"F0.wireOp",EDGE,"E4092"),sQuery(id+"F0.wireOp",EDGE,"E4093"),sQuery(id+"F0.wireOp",EDGE,"E4094"),sQuery(id+"F0.wireOp",EDGE,"E4095"),sQuery(id+"F0.wireOp",EDGE,"E4096"),sQuery(id+"F0.wireOp",EDGE,"E4097"),sQuery(id+"F0.wireOp",EDGE,"E4098"),sQuery(id+"F0.wireOp",EDGE,"E4099"),sQuery(id+"F0.wireOp",EDGE,"E4100"),sQuery(id+"F0.wireOp",EDGE,"E4101"),sQuery(id+"F0.wireOp",EDGE,"E4102"),sQuery(id+"F0.wireOp",EDGE,"E4103"),sQuery(id+"F0.wireOp",EDGE,"E4104"),sQuery(id+"F0.wireOp",EDGE,"E4105"),sQuery(id+"F0.wireOp",EDGE,"E4106"),sQuery(id+"F0.wireOp",EDGE,"E4107"),sQuery(id+"F0.wireOp",EDGE,"E4108"),sQuery(id+"F0.wireOp",EDGE,"E4109"),sQuery(id+"F0.wireOp",EDGE,"E4110"),sQuery(id+"F0.wireOp",EDGE,"E4111"),sQuery(id+"F0.wireOp",EDGE,"E4112"),sQuery(id+"F0.wireOp",EDGE,"E4113"),sQuery(id+"F0.wireOp",EDGE,"E4114"),sQuery(id+"F0.wireOp",EDGE,"E4115"),sQuery(id+"F0.wireOp",EDGE,"E4116"),sQuery(id+"F0.wireOp",EDGE,"E4117"),sQuery(id+"F0.wireOp",EDGE,"E4118"),sQuery(id+"F0.wireOp",EDGE,"E4119"),sQuery(id+"F0.wireOp",EDGE,"E4120"),sQuery(id+"F0.wireOp",EDGE,"E4121"),sQuery(id+"F0.wireOp",EDGE,"E4122"),sQuery(id+"F0.wireOp",EDGE,"E4123"),sQuery(id+"F0.wireOp",EDGE,"E4124"),sQuery(id+"F0.wireOp",EDGE,"E4125"),sQuery(id+"F0.wireOp",EDGE,"E4126"),sQuery(id+"F0.wireOp",EDGE,"E4127"),sQuery(id+"F0.wireOp",EDGE,"E4128"),sQuery(id+"F0.wireOp",EDGE,"E4129"),sQuery(id+"F0.wireOp",EDGE,"E4130"),sQuery(id+"F0.wireOp",EDGE,"E4131"),sQuery(id+"F0.wireOp",EDGE,"E4132"),sQuery(id+"F0.wireOp",EDGE,"E4133"),sQuery(id+"F0.wireOp",EDGE,"E4134"),sQuery(id+"F0.wireOp",EDGE,"E4135"),sQuery(id+"F0.wireOp",EDGE,"E4136"),sQuery(id+"F0.wireOp",EDGE,"E4137"),sQuery(id+"F0.wireOp",EDGE,"E4138"),sQuery(id+"F0.wireOp",EDGE,"E4139"),sQuery(id+"F0.wireOp",EDGE,"E4140"),sQuery(id+"F0.wireOp",EDGE,"E4141"),sQuery(id+"F0.wireOp",EDGE,"E4142"),sQuery(id+"F0.wireOp",EDGE,"E4143"),sQuery(id+"F0.wireOp",EDGE,"E4144"),sQuery(id+"F0.wireOp",EDGE,"E4145"),sQuery(id+"F0.wireOp",EDGE,"E4146"),sQuery(id+"F0.wireOp",EDGE,"E4147"),sQuery(id+"F0.wireOp",EDGE,"E4148"),sQuery(id+"F0.wireOp",EDGE,"E4149"),sQuery(id+"F0.wireOp",EDGE,"E4150"),sQuery(id+"F0.wireOp",EDGE,"E4151"),sQuery(id+"F0.wireOp",EDGE,"E4152"),sQuery(id+"F0.wireOp",EDGE,"E4153"),sQuery(id+"F0.wireOp",EDGE,"E4154"),sQuery(id+"F0.wireOp",EDGE,"E4155"),sQuery(id+"F0.wireOp",EDGE,"E4156"),sQuery(id+"F0.wireOp",EDGE,"E4157"),sQuery(id+"F0.wireOp",EDGE,"E4158"),sQuery(id+"F0.wireOp",EDGE,"E4159"),sQuery(id+"F0.wireOp",EDGE,"E4160"),sQuery(id+"F0.wireOp",EDGE,"E4161"),sQuery(id+"F0.wireOp",EDGE,"E4162"),sQuery(id+"F0.wireOp",EDGE,"E4163"),sQuery(id+"F0.wireOp",EDGE,"E4164"),sQuery(id+"F0.wireOp",EDGE,"E4165"),sQuery(id+"F0.wireOp",EDGE,"E4166"),sQuery(id+"F0.wireOp",EDGE,"E4167"),sQuery(id+"F0.wireOp",EDGE,"E4168"),sQuery(id+"F0.wireOp",EDGE,"E4169"),sQuery(id+"F0.wireOp",EDGE,"E4170"),sQuery(id+"F0.wireOp",EDGE,"E4171"),sQuery(id+"F0.wireOp",EDGE,"E4172"),sQuery(id+"F0.wireOp",EDGE,"E4173"),sQuery(id+"F0.wireOp",EDGE,"E4174"),sQuery(id+"F0.wireOp",EDGE,"E4175"),sQuery(id+"F0.wireOp",EDGE,"E4176"),sQuery(id+"F0.wireOp",EDGE,"E4177"),sQuery(id+"F0.wireOp",EDGE,"E4178"),sQuery(id+"F0.wireOp",EDGE,"E4179"),sQuery(id+"F0.wireOp",EDGE,"E4180"),sQuery(id+"F0.wireOp",EDGE,"E4181"),sQuery(id+"F0.wireOp",EDGE,"E4182"),sQuery(id+"F0.wireOp",EDGE,"E4183"),sQuery(id+"F0.wireOp",EDGE,"E4184"),sQuery(id+"F0.wireOp",EDGE,"E4185"),sQuery(id+"F0.wireOp",EDGE,"E4186"),sQuery(id+"F0.wireOp",EDGE,"E4187"),sQuery(id+"F0.wireOp",EDGE,"E4188"),sQuery(id+"F0.wireOp",EDGE,"E4189"),sQuery(id+"F0.wireOp",EDGE,"E4403"),sQuery(id+"F0.wireOp",EDGE,"E4404")])],"isStart":true});
            extrude(context, id + "F3", {"entities" : qUnion([Q0, Q1]), "operationType" : NewBodyOperationType.ADD, "endBound" : BoundingType.UP_TO_SURFACE, "oppositeDirection" : true, "endBoundEntityFace" : qUnion([Q2]), "depth" : 16.1 * mm});
        }
        {
            var Q0;
            Q0=makeQuery(id+"F3.boolean.opBoolean","MERGE",FACE,{"derivedFrom":[makeQuery(id+"F1.opExtrude","CAP_FACE",FACE,{"disambiguationData":[OSD([sQuery(id+"F0.wireOp",EDGE,"E0"),sQuery(id+"F0.wireOp",EDGE,"E1"),sQuery(id+"F0.wireOp",EDGE,"E2"),sQuery(id+"F0.wireOp",EDGE,"E3"),sQuery(id+"F0.wireOp",EDGE,"E4"),sQuery(id+"F0.wireOp",EDGE,"E5"),sQuery(id+"F0.wireOp",EDGE,"E6"),sQuery(id+"F0.wireOp",EDGE,"E7"),sQuery(id+"F0.wireOp",EDGE,"E8"),sQuery(id+"F0.wireOp",EDGE,"E9"),sQuery(id+"F0.wireOp",EDGE,"E10"),sQuery(id+"F0.wireOp",EDGE,"E11"),sQuery(id+"F0.wireOp",EDGE,"E12"),sQuery(id+"F0.wireOp",EDGE,"E13"),sQuery(id+"F0.wireOp",EDGE,"E14"),sQuery(id+"F0.wireOp",EDGE,"E15"),sQuery(id+"F0.wireOp",EDGE,"E16"),sQuery(id+"F0.wireOp",EDGE,"E17"),sQuery(id+"F0.wireOp",EDGE,"E18"),sQuery(id+"F0.wireOp",EDGE,"E19"),sQuery(id+"F0.wireOp",EDGE,"E20"),sQuery(id+"F0.wireOp",EDGE,"E21"),sQuery(id+"F0.wireOp",EDGE,"E22"),sQuery(id+"F0.wireOp",EDGE,"E23"),sQuery(id+"F0.wireOp",EDGE,"E24"),sQuery(id+"F0.wireOp",EDGE,"E25"),sQuery(id+"F0.wireOp",EDGE,"E26"),sQuery(id+"F0.wireOp",EDGE,"E27"),sQuery(id+"F0.wireOp",EDGE,"E28"),sQuery(id+"F0.wireOp",EDGE,"E29"),sQuery(id+"F0.wireOp",EDGE,"E30"),sQuery(id+"F0.wireOp",EDGE,"E31"),sQuery(id+"F0.wireOp",EDGE,"E32"),sQuery(id+"F0.wireOp",EDGE,"E33"),sQuery(id+"F0.wireOp",EDGE,"E34"),sQuery(id+"F0.wireOp",EDGE,"E35"),sQuery(id+"F0.wireOp",EDGE,"E36"),sQuery(id+"F0.wireOp",EDGE,"E37"),sQuery(id+"F0.wireOp",EDGE,"E38"),sQuery(id+"F0.wireOp",EDGE,"E39"),sQuery(id+"F0.wireOp",EDGE,"E40"),sQuery(id+"F0.wireOp",EDGE,"E41"),sQuery(id+"F0.wireOp",EDGE,"E42"),sQuery(id+"F0.wireOp",EDGE,"E43"),sQuery(id+"F0.wireOp",EDGE,"E44"),sQuery(id+"F0.wireOp",EDGE,"E45"),sQuery(id+"F0.wireOp",EDGE,"E46"),sQuery(id+"F0.wireOp",EDGE,"E47"),sQuery(id+"F0.wireOp",EDGE,"E48"),sQuery(id+"F0.wireOp",EDGE,"E49"),sQuery(id+"F0.wireOp",EDGE,"E50"),sQuery(id+"F0.wireOp",EDGE,"E51"),sQuery(id+"F0.wireOp",EDGE,"E52"),sQuery(id+"F0.wireOp",EDGE,"E53"),sQuery(id+"F0.wireOp",EDGE,"E54"),sQuery(id+"F0.wireOp",EDGE,"E55"),sQuery(id+"F0.wireOp",EDGE,"E56"),sQuery(id+"F0.wireOp",EDGE,"E57"),sQuery(id+"F0.wireOp",EDGE,"E58"),sQuery(id+"F0.wireOp",EDGE,"E59"),sQuery(id+"F0.wireOp",EDGE,"E60"),sQuery(id+"F0.wireOp",EDGE,"E61"),sQuery(id+"F0.wireOp",EDGE,"E62"),sQuery(id+"F0.wireOp",EDGE,"E63"),sQuery(id+"F0.wireOp",EDGE,"E64"),sQuery(id+"F0.wireOp",EDGE,"E65"),sQuery(id+"F0.wireOp",EDGE,"E66"),sQuery(id+"F0.wireOp",EDGE,"E67"),sQuery(id+"F0.wireOp",EDGE,"E68"),sQuery(id+"F0.wireOp",EDGE,"E69"),sQuery(id+"F0.wireOp",EDGE,"E70"),sQuery(id+"F0.wireOp",EDGE,"E71"),sQuery(id+"F0.wireOp",EDGE,"E72"),sQuery(id+"F0.wireOp",EDGE,"E73"),sQuery(id+"F0.wireOp",EDGE,"E74"),sQuery(id+"F0.wireOp",EDGE,"E75"),sQuery(id+"F0.wireOp",EDGE,"E76"),sQuery(id+"F0.wireOp",EDGE,"E77"),sQuery(id+"F0.wireOp",EDGE,"E78"),sQuery(id+"F0.wireOp",EDGE,"E79"),sQuery(id+"F0.wireOp",EDGE,"E80"),sQuery(id+"F0.wireOp",EDGE,"E81"),sQuery(id+"F0.wireOp",EDGE,"E82"),sQuery(id+"F0.wireOp",EDGE,"E83"),sQuery(id+"F0.wireOp",EDGE,"E84"),sQuery(id+"F0.wireOp",EDGE,"E85"),sQuery(id+"F0.wireOp",EDGE,"E86"),sQuery(id+"F0.wireOp",EDGE,"E87"),sQuery(id+"F0.wireOp",EDGE,"E88"),sQuery(id+"F0.wireOp",EDGE,"E89"),sQuery(id+"F0.wireOp",EDGE,"E90"),sQuery(id+"F0.wireOp",EDGE,"E91"),sQuery(id+"F0.wireOp",EDGE,"E92"),sQuery(id+"F0.wireOp",EDGE,"E93"),sQuery(id+"F0.wireOp",EDGE,"E94"),sQuery(id+"F0.wireOp",EDGE,"E95"),sQuery(id+"F0.wireOp",EDGE,"E96"),sQuery(id+"F0.wireOp",EDGE,"E97"),sQuery(id+"F0.wireOp",EDGE,"E98"),sQuery(id+"F0.wireOp",EDGE,"E99"),sQuery(id+"F0.wireOp",EDGE,"E100"),sQuery(id+"F0.wireOp",EDGE,"E101"),sQuery(id+"F0.wireOp",EDGE,"E102"),sQuery(id+"F0.wireOp",EDGE,"E103"),sQuery(id+"F0.wireOp",EDGE,"E104"),sQuery(id+"F0.wireOp",EDGE,"E105"),sQuery(id+"F0.wireOp",EDGE,"E106"),sQuery(id+"F0.wireOp",EDGE,"E107"),sQuery(id+"F0.wireOp",EDGE,"E108"),sQuery(id+"F0.wireOp",EDGE,"E108"),sQuery(id+"F0.wireOp",EDGE,"E109"),sQuery(id+"F0.wireOp",EDGE,"E110"),sQuery(id+"F0.wireOp",EDGE,"E111"),sQuery(id+"F0.wireOp",EDGE,"E112"),sQuery(id+"F0.wireOp",EDGE,"E113"),sQuery(id+"F0.wireOp",EDGE,"E114"),sQuery(id+"F0.wireOp",EDGE,"E115"),sQuery(id+"F0.wireOp",EDGE,"E116"),sQuery(id+"F0.wireOp",EDGE,"E117"),sQuery(id+"F0.wireOp",EDGE,"E118"),sQuery(id+"F0.wireOp",EDGE,"E119"),sQuery(id+"F0.wireOp",EDGE,"E120"),sQuery(id+"F0.wireOp",EDGE,"E121"),sQuery(id+"F0.wireOp",EDGE,"E122"),sQuery(id+"F0.wireOp",EDGE,"E123"),sQuery(id+"F0.wireOp",EDGE,"E124"),sQuery(id+"F0.wireOp",EDGE,"E125"),sQuery(id+"F0.wireOp",EDGE,"E126"),sQuery(id+"F0.wireOp",EDGE,"E127"),sQuery(id+"F0.wireOp",EDGE,"E128"),sQuery(id+"F0.wireOp",EDGE,"E129"),sQuery(id+"F0.wireOp",EDGE,"E130"),sQuery(id+"F0.wireOp",EDGE,"E131"),sQuery(id+"F0.wireOp",EDGE,"E132"),sQuery(id+"F0.wireOp",EDGE,"E133"),sQuery(id+"F0.wireOp",EDGE,"E134"),sQuery(id+"F0.wireOp",EDGE,"E135"),sQuery(id+"F0.wireOp",EDGE,"E136"),sQuery(id+"F0.wireOp",EDGE,"E137"),sQuery(id+"F0.wireOp",EDGE,"E138"),sQuery(id+"F0.wireOp",EDGE,"E139"),sQuery(id+"F0.wireOp",EDGE,"E140"),sQuery(id+"F0.wireOp",EDGE,"E141"),sQuery(id+"F0.wireOp",EDGE,"E142"),sQuery(id+"F0.wireOp",EDGE,"E143"),sQuery(id+"F0.wireOp",EDGE,"E144"),sQuery(id+"F0.wireOp",EDGE,"E145"),sQuery(id+"F0.wireOp",EDGE,"E146"),sQuery(id+"F0.wireOp",EDGE,"E147"),sQuery(id+"F0.wireOp",EDGE,"E148"),sQuery(id+"F0.wireOp",EDGE,"E149"),sQuery(id+"F0.wireOp",EDGE,"E150"),sQuery(id+"F0.wireOp",EDGE,"E151"),sQuery(id+"F0.wireOp",EDGE,"E152"),sQuery(id+"F0.wireOp",EDGE,"E153"),sQuery(id+"F0.wireOp",EDGE,"E154"),sQuery(id+"F0.wireOp",EDGE,"E155"),sQuery(id+"F0.wireOp",EDGE,"E156"),sQuery(id+"F0.wireOp",EDGE,"E157"),sQuery(id+"F0.wireOp",EDGE,"E158"),sQuery(id+"F0.wireOp",EDGE,"E159"),sQuery(id+"F0.wireOp",EDGE,"E160"),sQuery(id+"F0.wireOp",EDGE,"E161"),sQuery(id+"F0.wireOp",EDGE,"E162"),sQuery(id+"F0.wireOp",EDGE,"E163"),sQuery(id+"F0.wireOp",EDGE,"E164"),sQuery(id+"F0.wireOp",EDGE,"E165"),sQuery(id+"F0.wireOp",EDGE,"E166"),sQuery(id+"F0.wireOp",EDGE,"E167"),sQuery(id+"F0.wireOp",EDGE,"E168"),sQuery(id+"F0.wireOp",EDGE,"E169"),sQuery(id+"F0.wireOp",EDGE,"E170"),sQuery(id+"F0.wireOp",EDGE,"E171"),sQuery(id+"F0.wireOp",EDGE,"E172"),sQuery(id+"F0.wireOp",EDGE,"E173"),sQuery(id+"F0.wireOp",EDGE,"E174"),sQuery(id+"F0.wireOp",EDGE,"E175"),sQuery(id+"F0.wireOp",EDGE,"E176"),sQuery(id+"F0.wireOp",EDGE,"E177"),sQuery(id+"F0.wireOp",EDGE,"E178"),sQuery(id+"F0.wireOp",EDGE,"E179"),sQuery(id+"F0.wireOp",EDGE,"E180"),sQuery(id+"F0.wireOp",EDGE,"E181"),sQuery(id+"F0.wireOp",EDGE,"E182"),sQuery(id+"F0.wireOp",EDGE,"E183"),sQuery(id+"F0.wireOp",EDGE,"E184"),sQuery(id+"F0.wireOp",EDGE,"E185"),sQuery(id+"F0.wireOp",EDGE,"E186"),sQuery(id+"F0.wireOp",EDGE,"E187"),sQuery(id+"F0.wireOp",EDGE,"E188"),sQuery(id+"F0.wireOp",EDGE,"E189"),sQuery(id+"F0.wireOp",EDGE,"E190"),sQuery(id+"F0.wireOp",EDGE,"E191"),sQuery(id+"F0.wireOp",EDGE,"E192"),sQuery(id+"F0.wireOp",EDGE,"E193"),sQuery(id+"F0.wireOp",EDGE,"E194"),sQuery(id+"F0.wireOp",EDGE,"E195"),sQuery(id+"F0.wireOp",EDGE,"E196"),sQuery(id+"F0.wireOp",EDGE,"E197"),sQuery(id+"F0.wireOp",EDGE,"E198"),sQuery(id+"F0.wireOp",EDGE,"E199"),sQuery(id+"F0.wireOp",EDGE,"E200"),sQuery(id+"F0.wireOp",EDGE,"E201"),sQuery(id+"F0.wireOp",EDGE,"E202"),sQuery(id+"F0.wireOp",EDGE,"E203"),sQuery(id+"F0.wireOp",EDGE,"E204"),sQuery(id+"F0.wireOp",EDGE,"E205"),sQuery(id+"F0.wireOp",EDGE,"E206"),sQuery(id+"F0.wireOp",EDGE,"E207"),sQuery(id+"F0.wireOp",EDGE,"E208"),sQuery(id+"F0.wireOp",EDGE,"E209"),sQuery(id+"F0.wireOp",EDGE,"E210"),sQuery(id+"F0.wireOp",EDGE,"E211"),sQuery(id+"F0.wireOp",EDGE,"E212"),sQuery(id+"F0.wireOp",EDGE,"E214"),sQuery(id+"F0.wireOp",EDGE,"E215"),sQuery(id+"F0.wireOp",EDGE,"E216"),sQuery(id+"F0.wireOp",EDGE,"E217"),sQuery(id+"F0.wireOp",EDGE,"E218"),sQuery(id+"F0.wireOp",EDGE,"E219"),sQuery(id+"F0.wireOp",EDGE,"E220"),sQuery(id+"F0.wireOp",EDGE,"E221"),sQuery(id+"F0.wireOp",EDGE,"E222"),sQuery(id+"F0.wireOp",EDGE,"E223"),sQuery(id+"F0.wireOp",EDGE,"E224"),sQuery(id+"F0.wireOp",EDGE,"E225"),sQuery(id+"F0.wireOp",EDGE,"E226"),sQuery(id+"F0.wireOp",EDGE,"E227"),sQuery(id+"F0.wireOp",EDGE,"E228"),sQuery(id+"F0.wireOp",EDGE,"E229"),sQuery(id+"F0.wireOp",EDGE,"E230"),sQuery(id+"F0.wireOp",EDGE,"E231"),sQuery(id+"F0.wireOp",EDGE,"E232"),sQuery(id+"F0.wireOp",EDGE,"E233"),sQuery(id+"F0.wireOp",EDGE,"E234"),sQuery(id+"F0.wireOp",EDGE,"E235"),sQuery(id+"F0.wireOp",EDGE,"E236"),sQuery(id+"F0.wireOp",EDGE,"E237"),sQuery(id+"F0.wireOp",EDGE,"E238"),sQuery(id+"F0.wireOp",EDGE,"E239"),sQuery(id+"F0.wireOp",EDGE,"E240"),sQuery(id+"F0.wireOp",EDGE,"E241"),sQuery(id+"F0.wireOp",EDGE,"E242"),sQuery(id+"F0.wireOp",EDGE,"E243"),sQuery(id+"F0.wireOp",EDGE,"E244"),sQuery(id+"F0.wireOp",EDGE,"E245"),sQuery(id+"F0.wireOp",EDGE,"E246"),sQuery(id+"F0.wireOp",EDGE,"E247"),sQuery(id+"F0.wireOp",EDGE,"E248"),sQuery(id+"F0.wireOp",EDGE,"E249"),sQuery(id+"F0.wireOp",EDGE,"E250"),sQuery(id+"F0.wireOp",EDGE,"E251"),sQuery(id+"F0.wireOp",EDGE,"E252"),sQuery(id+"F0.wireOp",EDGE,"E253"),sQuery(id+"F0.wireOp",EDGE,"E254"),sQuery(id+"F0.wireOp",EDGE,"E255"),sQuery(id+"F0.wireOp",EDGE,"E256"),sQuery(id+"F0.wireOp",EDGE,"E257"),sQuery(id+"F0.wireOp",EDGE,"E258"),sQuery(id+"F0.wireOp",EDGE,"E259"),sQuery(id+"F0.wireOp",EDGE,"E260"),sQuery(id+"F0.wireOp",EDGE,"E261"),sQuery(id+"F0.wireOp",EDGE,"E262"),sQuery(id+"F0.wireOp",EDGE,"E263"),sQuery(id+"F0.wireOp",EDGE,"E264"),sQuery(id+"F0.wireOp",EDGE,"E265"),sQuery(id+"F0.wireOp",EDGE,"E266"),sQuery(id+"F0.wireOp",EDGE,"E267"),sQuery(id+"F0.wireOp",EDGE,"E268"),sQuery(id+"F0.wireOp",EDGE,"E269"),sQuery(id+"F0.wireOp",EDGE,"E270"),sQuery(id+"F0.wireOp",EDGE,"E271"),sQuery(id+"F0.wireOp",EDGE,"E272"),sQuery(id+"F0.wireOp",EDGE,"E273"),sQuery(id+"F0.wireOp",EDGE,"E274"),sQuery(id+"F0.wireOp",EDGE,"E275"),sQuery(id+"F0.wireOp",EDGE,"E276"),sQuery(id+"F0.wireOp",EDGE,"E277"),sQuery(id+"F0.wireOp",EDGE,"E278"),sQuery(id+"F0.wireOp",EDGE,"E279"),sQuery(id+"F0.wireOp",EDGE,"E280"),sQuery(id+"F0.wireOp",EDGE,"E281"),sQuery(id+"F0.wireOp",EDGE,"E282"),sQuery(id+"F0.wireOp",EDGE,"E283"),sQuery(id+"F0.wireOp",EDGE,"E284"),sQuery(id+"F0.wireOp",EDGE,"E285"),sQuery(id+"F0.wireOp",EDGE,"E286"),sQuery(id+"F0.wireOp",EDGE,"E287"),sQuery(id+"F0.wireOp",EDGE,"E288"),sQuery(id+"F0.wireOp",EDGE,"E289"),sQuery(id+"F0.wireOp",EDGE,"E290"),sQuery(id+"F0.wireOp",EDGE,"E291"),sQuery(id+"F0.wireOp",EDGE,"E292"),sQuery(id+"F0.wireOp",EDGE,"E293"),sQuery(id+"F0.wireOp",EDGE,"E294"),sQuery(id+"F0.wireOp",EDGE,"E295"),sQuery(id+"F0.wireOp",EDGE,"E296"),sQuery(id+"F0.wireOp",EDGE,"E297"),sQuery(id+"F0.wireOp",EDGE,"E298"),sQuery(id+"F0.wireOp",EDGE,"E299"),sQuery(id+"F0.wireOp",EDGE,"E300"),sQuery(id+"F0.wireOp",EDGE,"E301"),sQuery(id+"F0.wireOp",EDGE,"E302"),sQuery(id+"F0.wireOp",EDGE,"E303"),sQuery(id+"F0.wireOp",EDGE,"E304"),sQuery(id+"F0.wireOp",EDGE,"E305"),sQuery(id+"F0.wireOp",EDGE,"E306"),sQuery(id+"F0.wireOp",EDGE,"E307"),sQuery(id+"F0.wireOp",EDGE,"E308"),sQuery(id+"F0.wireOp",EDGE,"E309"),sQuery(id+"F0.wireOp",EDGE,"E310"),sQuery(id+"F0.wireOp",EDGE,"E311"),sQuery(id+"F0.wireOp",EDGE,"E312"),sQuery(id+"F0.wireOp",EDGE,"E313"),sQuery(id+"F0.wireOp",EDGE,"E314"),sQuery(id+"F0.wireOp",EDGE,"E315"),sQuery(id+"F0.wireOp",EDGE,"E316"),sQuery(id+"F0.wireOp",EDGE,"E317"),sQuery(id+"F0.wireOp",EDGE,"E318"),sQuery(id+"F0.wireOp",EDGE,"E319"),sQuery(id+"F0.wireOp",EDGE,"E320"),sQuery(id+"F0.wireOp",EDGE,"E321"),sQuery(id+"F0.wireOp",EDGE,"E322"),sQuery(id+"F0.wireOp",EDGE,"E323"),sQuery(id+"F0.wireOp",EDGE,"E324"),sQuery(id+"F0.wireOp",EDGE,"E325"),sQuery(id+"F0.wireOp",EDGE,"E326"),sQuery(id+"F0.wireOp",EDGE,"E327"),sQuery(id+"F0.wireOp",EDGE,"E328"),sQuery(id+"F0.wireOp",EDGE,"E329"),sQuery(id+"F0.wireOp",EDGE,"E330"),sQuery(id+"F0.wireOp",EDGE,"E331"),sQuery(id+"F0.wireOp",EDGE,"E332"),sQuery(id+"F0.wireOp",EDGE,"E333"),sQuery(id+"F0.wireOp",EDGE,"E334"),sQuery(id+"F0.wireOp",EDGE,"E335"),sQuery(id+"F0.wireOp",EDGE,"E336"),sQuery(id+"F0.wireOp",EDGE,"E337"),sQuery(id+"F0.wireOp",EDGE,"E338"),sQuery(id+"F0.wireOp",EDGE,"E339"),sQuery(id+"F0.wireOp",EDGE,"E340"),sQuery(id+"F0.wireOp",EDGE,"E341"),sQuery(id+"F0.wireOp",EDGE,"E342"),sQuery(id+"F0.wireOp",EDGE,"E343"),sQuery(id+"F0.wireOp",EDGE,"E344"),sQuery(id+"F0.wireOp",EDGE,"E345"),sQuery(id+"F0.wireOp",EDGE,"E346"),sQuery(id+"F0.wireOp",EDGE,"E347"),sQuery(id+"F0.wireOp",EDGE,"E348"),sQuery(id+"F0.wireOp",EDGE,"E349"),sQuery(id+"F0.wireOp",EDGE,"E350"),sQuery(id+"F0.wireOp",EDGE,"E351"),sQuery(id+"F0.wireOp",EDGE,"E352"),sQuery(id+"F0.wireOp",EDGE,"E353"),sQuery(id+"F0.wireOp",EDGE,"E354"),sQuery(id+"F0.wireOp",EDGE,"E355"),sQuery(id+"F0.wireOp",EDGE,"E356"),sQuery(id+"F0.wireOp",EDGE,"E357"),sQuery(id+"F0.wireOp",EDGE,"E358"),sQuery(id+"F0.wireOp",EDGE,"E359"),sQuery(id+"F0.wireOp",EDGE,"E360"),sQuery(id+"F0.wireOp",EDGE,"E361"),sQuery(id+"F0.wireOp",EDGE,"E362"),sQuery(id+"F0.wireOp",EDGE,"E363"),sQuery(id+"F0.wireOp",EDGE,"E364"),sQuery(id+"F0.wireOp",EDGE,"E365"),sQuery(id+"F0.wireOp",EDGE,"E366"),sQuery(id+"F0.wireOp",EDGE,"E367"),sQuery(id+"F0.wireOp",EDGE,"E368"),sQuery(id+"F0.wireOp",EDGE,"E369"),sQuery(id+"F0.wireOp",EDGE,"E370"),sQuery(id+"F0.wireOp",EDGE,"E371"),sQuery(id+"F0.wireOp",EDGE,"E372"),sQuery(id+"F0.wireOp",EDGE,"E373"),sQuery(id+"F0.wireOp",EDGE,"E374"),sQuery(id+"F0.wireOp",EDGE,"E375"),sQuery(id+"F0.wireOp",EDGE,"E376"),sQuery(id+"F0.wireOp",EDGE,"E377"),sQuery(id+"F0.wireOp",EDGE,"E378"),sQuery(id+"F0.wireOp",EDGE,"E379"),sQuery(id+"F0.wireOp",EDGE,"E380"),sQuery(id+"F0.wireOp",EDGE,"E381"),sQuery(id+"F0.wireOp",EDGE,"E382"),sQuery(id+"F0.wireOp",EDGE,"E383"),sQuery(id+"F0.wireOp",EDGE,"E384"),sQuery(id+"F0.wireOp",EDGE,"E385"),sQuery(id+"F0.wireOp",EDGE,"E386"),sQuery(id+"F0.wireOp",EDGE,"E387"),sQuery(id+"F0.wireOp",EDGE,"E388"),sQuery(id+"F0.wireOp",EDGE,"E389"),sQuery(id+"F0.wireOp",EDGE,"E390"),sQuery(id+"F0.wireOp",EDGE,"E391"),sQuery(id+"F0.wireOp",EDGE,"E392"),sQuery(id+"F0.wireOp",EDGE,"E393"),sQuery(id+"F0.wireOp",EDGE,"E394"),sQuery(id+"F0.wireOp",EDGE,"E395"),sQuery(id+"F0.wireOp",EDGE,"E396"),sQuery(id+"F0.wireOp",EDGE,"E397"),sQuery(id+"F0.wireOp",EDGE,"E398"),sQuery(id+"F0.wireOp",EDGE,"E399"),sQuery(id+"F0.wireOp",EDGE,"E400"),sQuery(id+"F0.wireOp",EDGE,"E401"),sQuery(id+"F0.wireOp",EDGE,"E402"),sQuery(id+"F0.wireOp",EDGE,"E403"),sQuery(id+"F0.wireOp",EDGE,"E404"),sQuery(id+"F0.wireOp",EDGE,"E405"),sQuery(id+"F0.wireOp",EDGE,"E406"),sQuery(id+"F0.wireOp",EDGE,"E407"),sQuery(id+"F0.wireOp",EDGE,"E408"),sQuery(id+"F0.wireOp",EDGE,"E409"),sQuery(id+"F0.wireOp",EDGE,"E410"),sQuery(id+"F0.wireOp",EDGE,"E411"),sQuery(id+"F0.wireOp",EDGE,"E412"),sQuery(id+"F0.wireOp",EDGE,"E413"),sQuery(id+"F0.wireOp",EDGE,"E414"),sQuery(id+"F0.wireOp",EDGE,"E415"),sQuery(id+"F0.wireOp",EDGE,"E416"),sQuery(id+"F0.wireOp",EDGE,"E417"),sQuery(id+"F0.wireOp",EDGE,"E418"),sQuery(id+"F0.wireOp",EDGE,"E419"),sQuery(id+"F0.wireOp",EDGE,"E420"),sQuery(id+"F0.wireOp",EDGE,"E421"),sQuery(id+"F0.wireOp",EDGE,"E422"),sQuery(id+"F0.wireOp",EDGE,"E423"),sQuery(id+"F0.wireOp",EDGE,"E424"),sQuery(id+"F0.wireOp",EDGE,"E425"),sQuery(id+"F0.wireOp",EDGE,"E426"),sQuery(id+"F0.wireOp",EDGE,"E427"),sQuery(id+"F0.wireOp",EDGE,"E428"),sQuery(id+"F0.wireOp",EDGE,"E429"),sQuery(id+"F0.wireOp",EDGE,"E430"),sQuery(id+"F0.wireOp",EDGE,"E431"),sQuery(id+"F0.wireOp",EDGE,"E432"),sQuery(id+"F0.wireOp",EDGE,"E433"),sQuery(id+"F0.wireOp",EDGE,"E434"),sQuery(id+"F0.wireOp",EDGE,"E435"),sQuery(id+"F0.wireOp",EDGE,"E436"),sQuery(id+"F0.wireOp",EDGE,"E437"),sQuery(id+"F0.wireOp",EDGE,"E438"),sQuery(id+"F0.wireOp",EDGE,"E439"),sQuery(id+"F0.wireOp",EDGE,"E440"),sQuery(id+"F0.wireOp",EDGE,"E441"),sQuery(id+"F0.wireOp",EDGE,"E442"),sQuery(id+"F0.wireOp",EDGE,"E443"),sQuery(id+"F0.wireOp",EDGE,"E444"),sQuery(id+"F0.wireOp",EDGE,"E445"),sQuery(id+"F0.wireOp",EDGE,"E446"),sQuery(id+"F0.wireOp",EDGE,"E447"),sQuery(id+"F0.wireOp",EDGE,"E448"),sQuery(id+"F0.wireOp",EDGE,"E449"),sQuery(id+"F0.wireOp",EDGE,"E450"),sQuery(id+"F0.wireOp",EDGE,"E451"),sQuery(id+"F0.wireOp",EDGE,"E452"),sQuery(id+"F0.wireOp",EDGE,"E453"),sQuery(id+"F0.wireOp",EDGE,"E454"),sQuery(id+"F0.wireOp",EDGE,"E455"),sQuery(id+"F0.wireOp",EDGE,"E456"),sQuery(id+"F0.wireOp",EDGE,"E457"),sQuery(id+"F0.wireOp",EDGE,"E458"),sQuery(id+"F0.wireOp",EDGE,"E459"),sQuery(id+"F0.wireOp",EDGE,"E460"),sQuery(id+"F0.wireOp",EDGE,"E461"),sQuery(id+"F0.wireOp",EDGE,"E462"),sQuery(id+"F0.wireOp",EDGE,"E463"),sQuery(id+"F0.wireOp",EDGE,"E464"),sQuery(id+"F0.wireOp",EDGE,"E465"),sQuery(id+"F0.wireOp",EDGE,"E466"),sQuery(id+"F0.wireOp",EDGE,"E467"),sQuery(id+"F0.wireOp",EDGE,"E468"),sQuery(id+"F0.wireOp",EDGE,"E469"),sQuery(id+"F0.wireOp",EDGE,"E470"),sQuery(id+"F0.wireOp",EDGE,"E471"),sQuery(id+"F0.wireOp",EDGE,"E472"),sQuery(id+"F0.wireOp",EDGE,"E473"),sQuery(id+"F0.wireOp",EDGE,"E474"),sQuery(id+"F0.wireOp",EDGE,"E475"),sQuery(id+"F0.wireOp",EDGE,"E476"),sQuery(id+"F0.wireOp",EDGE,"E477"),sQuery(id+"F0.wireOp",EDGE,"E478"),sQuery(id+"F0.wireOp",EDGE,"E479"),sQuery(id+"F0.wireOp",EDGE,"E480"),sQuery(id+"F0.wireOp",EDGE,"E481"),sQuery(id+"F0.wireOp",EDGE,"E482"),sQuery(id+"F0.wireOp",EDGE,"E483"),sQuery(id+"F0.wireOp",EDGE,"E484"),sQuery(id+"F0.wireOp",EDGE,"E485"),sQuery(id+"F0.wireOp",EDGE,"E486"),sQuery(id+"F0.wireOp",EDGE,"E487"),sQuery(id+"F0.wireOp",EDGE,"E488"),sQuery(id+"F0.wireOp",EDGE,"E489"),sQuery(id+"F0.wireOp",EDGE,"E490"),sQuery(id+"F0.wireOp",EDGE,"E491"),sQuery(id+"F0.wireOp",EDGE,"E492"),sQuery(id+"F0.wireOp",EDGE,"E493"),sQuery(id+"F0.wireOp",EDGE,"E494"),sQuery(id+"F0.wireOp",EDGE,"E495"),sQuery(id+"F0.wireOp",EDGE,"E496"),sQuery(id+"F0.wireOp",EDGE,"E497"),sQuery(id+"F0.wireOp",EDGE,"E498"),sQuery(id+"F0.wireOp",EDGE,"E499"),sQuery(id+"F0.wireOp",EDGE,"E500"),sQuery(id+"F0.wireOp",EDGE,"E501"),sQuery(id+"F0.wireOp",EDGE,"E502"),sQuery(id+"F0.wireOp",EDGE,"E503"),sQuery(id+"F0.wireOp",EDGE,"E504"),sQuery(id+"F0.wireOp",EDGE,"E505"),sQuery(id+"F0.wireOp",EDGE,"E506"),sQuery(id+"F0.wireOp",EDGE,"E507"),sQuery(id+"F0.wireOp",EDGE,"E508"),sQuery(id+"F0.wireOp",EDGE,"E509"),sQuery(id+"F0.wireOp",EDGE,"E510"),sQuery(id+"F0.wireOp",EDGE,"E511"),sQuery(id+"F0.wireOp",EDGE,"E512"),sQuery(id+"F0.wireOp",EDGE,"E513"),sQuery(id+"F0.wireOp",EDGE,"E514"),sQuery(id+"F0.wireOp",EDGE,"E515"),sQuery(id+"F0.wireOp",EDGE,"E516"),sQuery(id+"F0.wireOp",EDGE,"E517"),sQuery(id+"F0.wireOp",EDGE,"E518"),sQuery(id+"F0.wireOp",EDGE,"E519"),sQuery(id+"F0.wireOp",EDGE,"E520"),sQuery(id+"F0.wireOp",EDGE,"E521"),sQuery(id+"F0.wireOp",EDGE,"E522"),sQuery(id+"F0.wireOp",EDGE,"E523"),sQuery(id+"F0.wireOp",EDGE,"E524"),sQuery(id+"F0.wireOp",EDGE,"E525"),sQuery(id+"F0.wireOp",EDGE,"E526"),sQuery(id+"F0.wireOp",EDGE,"E527"),sQuery(id+"F0.wireOp",EDGE,"E528"),sQuery(id+"F0.wireOp",EDGE,"E529"),sQuery(id+"F0.wireOp",EDGE,"E530"),sQuery(id+"F0.wireOp",EDGE,"E531"),sQuery(id+"F0.wireOp",EDGE,"E532"),sQuery(id+"F0.wireOp",EDGE,"E533"),sQuery(id+"F0.wireOp",EDGE,"E534"),sQuery(id+"F0.wireOp",EDGE,"E535"),sQuery(id+"F0.wireOp",EDGE,"E536"),sQuery(id+"F0.wireOp",EDGE,"E537"),sQuery(id+"F0.wireOp",EDGE,"E538"),sQuery(id+"F0.wireOp",EDGE,"E539"),sQuery(id+"F0.wireOp",EDGE,"E540"),sQuery(id+"F0.wireOp",EDGE,"E541"),sQuery(id+"F0.wireOp",EDGE,"E542"),sQuery(id+"F0.wireOp",EDGE,"E543"),sQuery(id+"F0.wireOp",EDGE,"E544"),sQuery(id+"F0.wireOp",EDGE,"E545"),sQuery(id+"F0.wireOp",EDGE,"E546"),sQuery(id+"F0.wireOp",EDGE,"E547"),sQuery(id+"F0.wireOp",EDGE,"E548"),sQuery(id+"F0.wireOp",EDGE,"E549"),sQuery(id+"F0.wireOp",EDGE,"E550"),sQuery(id+"F0.wireOp",EDGE,"E551"),sQuery(id+"F0.wireOp",EDGE,"E552"),sQuery(id+"F0.wireOp",EDGE,"E553"),sQuery(id+"F0.wireOp",EDGE,"E554"),sQuery(id+"F0.wireOp",EDGE,"E555"),sQuery(id+"F0.wireOp",EDGE,"E556"),sQuery(id+"F0.wireOp",EDGE,"E557"),sQuery(id+"F0.wireOp",EDGE,"E558"),sQuery(id+"F0.wireOp",EDGE,"E559"),sQuery(id+"F0.wireOp",EDGE,"E560"),sQuery(id+"F0.wireOp",EDGE,"E561"),sQuery(id+"F0.wireOp",EDGE,"E562"),sQuery(id+"F0.wireOp",EDGE,"E563"),sQuery(id+"F0.wireOp",EDGE,"E564"),sQuery(id+"F0.wireOp",EDGE,"E565"),sQuery(id+"F0.wireOp",EDGE,"E566"),sQuery(id+"F0.wireOp",EDGE,"E567"),sQuery(id+"F0.wireOp",EDGE,"E568"),sQuery(id+"F0.wireOp",EDGE,"E569"),sQuery(id+"F0.wireOp",EDGE,"E570"),sQuery(id+"F0.wireOp",EDGE,"E571"),sQuery(id+"F0.wireOp",EDGE,"E572"),sQuery(id+"F0.wireOp",EDGE,"E573"),sQuery(id+"F0.wireOp",EDGE,"E574"),sQuery(id+"F0.wireOp",EDGE,"E575"),sQuery(id+"F0.wireOp",EDGE,"E576"),sQuery(id+"F0.wireOp",EDGE,"E577"),sQuery(id+"F0.wireOp",EDGE,"E578"),sQuery(id+"F0.wireOp",EDGE,"E579"),sQuery(id+"F0.wireOp",EDGE,"E580"),sQuery(id+"F0.wireOp",EDGE,"E581"),sQuery(id+"F0.wireOp",EDGE,"E582"),sQuery(id+"F0.wireOp",EDGE,"E583"),sQuery(id+"F0.wireOp",EDGE,"E584"),sQuery(id+"F0.wireOp",EDGE,"E585"),sQuery(id+"F0.wireOp",EDGE,"E586"),sQuery(id+"F0.wireOp",EDGE,"E587"),sQuery(id+"F0.wireOp",EDGE,"E588"),sQuery(id+"F0.wireOp",EDGE,"E589"),sQuery(id+"F0.wireOp",EDGE,"E590"),sQuery(id+"F0.wireOp",EDGE,"E591"),sQuery(id+"F0.wireOp",EDGE,"E592"),sQuery(id+"F0.wireOp",EDGE,"E593"),sQuery(id+"F0.wireOp",EDGE,"E594"),sQuery(id+"F0.wireOp",EDGE,"E595"),sQuery(id+"F0.wireOp",EDGE,"E596"),sQuery(id+"F0.wireOp",EDGE,"E597"),sQuery(id+"F0.wireOp",EDGE,"E598"),sQuery(id+"F0.wireOp",EDGE,"E599"),sQuery(id+"F0.wireOp",EDGE,"E600"),sQuery(id+"F0.wireOp",EDGE,"E601"),sQuery(id+"F0.wireOp",EDGE,"E602"),sQuery(id+"F0.wireOp",EDGE,"E603"),sQuery(id+"F0.wireOp",EDGE,"E604"),sQuery(id+"F0.wireOp",EDGE,"E605"),sQuery(id+"F0.wireOp",EDGE,"E606"),sQuery(id+"F0.wireOp",EDGE,"E607"),sQuery(id+"F0.wireOp",EDGE,"E608"),sQuery(id+"F0.wireOp",EDGE,"E609"),sQuery(id+"F0.wireOp",EDGE,"E610"),sQuery(id+"F0.wireOp",EDGE,"E611"),sQuery(id+"F0.wireOp",EDGE,"E612"),sQuery(id+"F0.wireOp",EDGE,"E613"),sQuery(id+"F0.wireOp",EDGE,"E614"),sQuery(id+"F0.wireOp",EDGE,"E615"),sQuery(id+"F0.wireOp",EDGE,"E616"),sQuery(id+"F0.wireOp",EDGE,"E617"),sQuery(id+"F0.wireOp",EDGE,"E618"),sQuery(id+"F0.wireOp",EDGE,"E619"),sQuery(id+"F0.wireOp",EDGE,"E620"),sQuery(id+"F0.wireOp",EDGE,"E621"),sQuery(id+"F0.wireOp",EDGE,"E622"),sQuery(id+"F0.wireOp",EDGE,"E623"),sQuery(id+"F0.wireOp",EDGE,"E624"),sQuery(id+"F0.wireOp",EDGE,"E625"),sQuery(id+"F0.wireOp",EDGE,"E626"),sQuery(id+"F0.wireOp",EDGE,"E627"),sQuery(id+"F0.wireOp",EDGE,"E628"),sQuery(id+"F0.wireOp",EDGE,"E629"),sQuery(id+"F0.wireOp",EDGE,"E630"),sQuery(id+"F0.wireOp",EDGE,"E631"),sQuery(id+"F0.wireOp",EDGE,"E632"),sQuery(id+"F0.wireOp",EDGE,"E633"),sQuery(id+"F0.wireOp",EDGE,"E634"),sQuery(id+"F0.wireOp",EDGE,"E635"),sQuery(id+"F0.wireOp",EDGE,"E636"),sQuery(id+"F0.wireOp",EDGE,"E637"),sQuery(id+"F0.wireOp",EDGE,"E638"),sQuery(id+"F0.wireOp",EDGE,"E639"),sQuery(id+"F0.wireOp",EDGE,"E640"),sQuery(id+"F0.wireOp",EDGE,"E641"),sQuery(id+"F0.wireOp",EDGE,"E642"),sQuery(id+"F0.wireOp",EDGE,"E643"),sQuery(id+"F0.wireOp",EDGE,"E644"),sQuery(id+"F0.wireOp",EDGE,"E645"),sQuery(id+"F0.wireOp",EDGE,"E646"),sQuery(id+"F0.wireOp",EDGE,"E647"),sQuery(id+"F0.wireOp",EDGE,"E648"),sQuery(id+"F0.wireOp",EDGE,"E649"),sQuery(id+"F0.wireOp",EDGE,"E650"),sQuery(id+"F0.wireOp",EDGE,"E651"),sQuery(id+"F0.wireOp",EDGE,"E652"),sQuery(id+"F0.wireOp",EDGE,"E653"),sQuery(id+"F0.wireOp",EDGE,"E654"),sQuery(id+"F0.wireOp",EDGE,"E655"),sQuery(id+"F0.wireOp",EDGE,"E656"),sQuery(id+"F0.wireOp",EDGE,"E657"),sQuery(id+"F0.wireOp",EDGE,"E658"),sQuery(id+"F0.wireOp",EDGE,"E659"),sQuery(id+"F0.wireOp",EDGE,"E660"),sQuery(id+"F0.wireOp",EDGE,"E661"),sQuery(id+"F0.wireOp",EDGE,"E662"),sQuery(id+"F0.wireOp",EDGE,"E663"),sQuery(id+"F0.wireOp",EDGE,"E664"),sQuery(id+"F0.wireOp",EDGE,"E665"),sQuery(id+"F0.wireOp",EDGE,"E666"),sQuery(id+"F0.wireOp",EDGE,"E667"),sQuery(id+"F0.wireOp",EDGE,"E668"),sQuery(id+"F0.wireOp",EDGE,"E669"),sQuery(id+"F0.wireOp",EDGE,"E670"),sQuery(id+"F0.wireOp",EDGE,"E671"),sQuery(id+"F0.wireOp",EDGE,"E672"),sQuery(id+"F0.wireOp",EDGE,"E673"),sQuery(id+"F0.wireOp",EDGE,"E674"),sQuery(id+"F0.wireOp",EDGE,"E675"),sQuery(id+"F0.wireOp",EDGE,"E676"),sQuery(id+"F0.wireOp",EDGE,"E677"),sQuery(id+"F0.wireOp",EDGE,"E678"),sQuery(id+"F0.wireOp",EDGE,"E679"),sQuery(id+"F0.wireOp",EDGE,"E680"),sQuery(id+"F0.wireOp",EDGE,"E681"),sQuery(id+"F0.wireOp",EDGE,"E682"),sQuery(id+"F0.wireOp",EDGE,"E683"),sQuery(id+"F0.wireOp",EDGE,"E684"),sQuery(id+"F0.wireOp",EDGE,"E685"),sQuery(id+"F0.wireOp",EDGE,"E686"),sQuery(id+"F0.wireOp",EDGE,"E687"),sQuery(id+"F0.wireOp",EDGE,"E688"),sQuery(id+"F0.wireOp",EDGE,"E689"),sQuery(id+"F0.wireOp",EDGE,"E690"),sQuery(id+"F0.wireOp",EDGE,"E691"),sQuery(id+"F0.wireOp",EDGE,"E692"),sQuery(id+"F0.wireOp",EDGE,"E693"),sQuery(id+"F0.wireOp",EDGE,"E694"),sQuery(id+"F0.wireOp",EDGE,"E695"),sQuery(id+"F0.wireOp",EDGE,"E696"),sQuery(id+"F0.wireOp",EDGE,"E697"),sQuery(id+"F0.wireOp",EDGE,"E698"),sQuery(id+"F0.wireOp",EDGE,"E699"),sQuery(id+"F0.wireOp",EDGE,"E700"),sQuery(id+"F0.wireOp",EDGE,"E701"),sQuery(id+"F0.wireOp",EDGE,"E702"),sQuery(id+"F0.wireOp",EDGE,"E703"),sQuery(id+"F0.wireOp",EDGE,"E704"),sQuery(id+"F0.wireOp",EDGE,"E705"),sQuery(id+"F0.wireOp",EDGE,"E706"),sQuery(id+"F0.wireOp",EDGE,"E707"),sQuery(id+"F0.wireOp",EDGE,"E708"),sQuery(id+"F0.wireOp",EDGE,"E709"),sQuery(id+"F0.wireOp",EDGE,"E710"),sQuery(id+"F0.wireOp",EDGE,"E711"),sQuery(id+"F0.wireOp",EDGE,"E712"),sQuery(id+"F0.wireOp",EDGE,"E713"),sQuery(id+"F0.wireOp",EDGE,"E714"),sQuery(id+"F0.wireOp",EDGE,"E715"),sQuery(id+"F0.wireOp",EDGE,"E716"),sQuery(id+"F0.wireOp",EDGE,"E717"),sQuery(id+"F0.wireOp",EDGE,"E718"),sQuery(id+"F0.wireOp",EDGE,"E719"),sQuery(id+"F0.wireOp",EDGE,"E720"),sQuery(id+"F0.wireOp",EDGE,"E721"),sQuery(id+"F0.wireOp",EDGE,"E722"),sQuery(id+"F0.wireOp",EDGE,"E723"),sQuery(id+"F0.wireOp",EDGE,"E724"),sQuery(id+"F0.wireOp",EDGE,"E725"),sQuery(id+"F0.wireOp",EDGE,"E726"),sQuery(id+"F0.wireOp",EDGE,"E727"),sQuery(id+"F0.wireOp",EDGE,"E728"),sQuery(id+"F0.wireOp",EDGE,"E729"),sQuery(id+"F0.wireOp",EDGE,"E730"),sQuery(id+"F0.wireOp",EDGE,"E731"),sQuery(id+"F0.wireOp",EDGE,"E732"),sQuery(id+"F0.wireOp",EDGE,"E733"),sQuery(id+"F0.wireOp",EDGE,"E734"),sQuery(id+"F0.wireOp",EDGE,"E735"),sQuery(id+"F0.wireOp",EDGE,"E736"),sQuery(id+"F0.wireOp",EDGE,"E737"),sQuery(id+"F0.wireOp",EDGE,"E738"),sQuery(id+"F0.wireOp",EDGE,"E739"),sQuery(id+"F0.wireOp",EDGE,"E740"),sQuery(id+"F0.wireOp",EDGE,"E741"),sQuery(id+"F0.wireOp",EDGE,"E742"),sQuery(id+"F0.wireOp",EDGE,"E743"),sQuery(id+"F0.wireOp",EDGE,"E744"),sQuery(id+"F0.wireOp",EDGE,"E745"),sQuery(id+"F0.wireOp",EDGE,"E746"),sQuery(id+"F0.wireOp",EDGE,"E747"),sQuery(id+"F0.wireOp",EDGE,"E748"),sQuery(id+"F0.wireOp",EDGE,"E749"),sQuery(id+"F0.wireOp",EDGE,"E750"),sQuery(id+"F0.wireOp",EDGE,"E751"),sQuery(id+"F0.wireOp",EDGE,"E752"),sQuery(id+"F0.wireOp",EDGE,"E753"),sQuery(id+"F0.wireOp",EDGE,"E754"),sQuery(id+"F0.wireOp",EDGE,"E755"),sQuery(id+"F0.wireOp",EDGE,"E756"),sQuery(id+"F0.wireOp",EDGE,"E757"),sQuery(id+"F0.wireOp",EDGE,"E758"),sQuery(id+"F0.wireOp",EDGE,"E759"),sQuery(id+"F0.wireOp",EDGE,"E760"),sQuery(id+"F0.wireOp",EDGE,"E761"),sQuery(id+"F0.wireOp",EDGE,"E762"),sQuery(id+"F0.wireOp",EDGE,"E763"),sQuery(id+"F0.wireOp",EDGE,"E764"),sQuery(id+"F0.wireOp",EDGE,"E765"),sQuery(id+"F0.wireOp",EDGE,"E766"),sQuery(id+"F0.wireOp",EDGE,"E767"),sQuery(id+"F0.wireOp",EDGE,"E768"),sQuery(id+"F0.wireOp",EDGE,"E769"),sQuery(id+"F0.wireOp",EDGE,"E770"),sQuery(id+"F0.wireOp",EDGE,"E771"),sQuery(id+"F0.wireOp",EDGE,"E772"),sQuery(id+"F0.wireOp",EDGE,"E773"),sQuery(id+"F0.wireOp",EDGE,"E774"),sQuery(id+"F0.wireOp",EDGE,"E775"),sQuery(id+"F0.wireOp",EDGE,"E776"),sQuery(id+"F0.wireOp",EDGE,"E777"),sQuery(id+"F0.wireOp",EDGE,"E778"),sQuery(id+"F0.wireOp",EDGE,"E779"),sQuery(id+"F0.wireOp",EDGE,"E780"),sQuery(id+"F0.wireOp",EDGE,"E781"),sQuery(id+"F0.wireOp",EDGE,"E782"),sQuery(id+"F0.wireOp",EDGE,"E783"),sQuery(id+"F0.wireOp",EDGE,"E784"),sQuery(id+"F0.wireOp",EDGE,"E785"),sQuery(id+"F0.wireOp",EDGE,"E786"),sQuery(id+"F0.wireOp",EDGE,"E787"),sQuery(id+"F0.wireOp",EDGE,"E788"),sQuery(id+"F0.wireOp",EDGE,"E789"),sQuery(id+"F0.wireOp",EDGE,"E790"),sQuery(id+"F0.wireOp",EDGE,"E791"),sQuery(id+"F0.wireOp",EDGE,"E792"),sQuery(id+"F0.wireOp",EDGE,"E793"),sQuery(id+"F0.wireOp",EDGE,"E794"),sQuery(id+"F0.wireOp",EDGE,"E795"),sQuery(id+"F0.wireOp",EDGE,"E796"),sQuery(id+"F0.wireOp",EDGE,"E797"),sQuery(id+"F0.wireOp",EDGE,"E798"),sQuery(id+"F0.wireOp",EDGE,"E799"),sQuery(id+"F0.wireOp",EDGE,"E800"),sQuery(id+"F0.wireOp",EDGE,"E801"),sQuery(id+"F0.wireOp",EDGE,"E802"),sQuery(id+"F0.wireOp",EDGE,"E803"),sQuery(id+"F0.wireOp",EDGE,"E804"),sQuery(id+"F0.wireOp",EDGE,"E805"),sQuery(id+"F0.wireOp",EDGE,"E806"),sQuery(id+"F0.wireOp",EDGE,"E807"),sQuery(id+"F0.wireOp",EDGE,"E808"),sQuery(id+"F0.wireOp",EDGE,"E809"),sQuery(id+"F0.wireOp",EDGE,"E810"),sQuery(id+"F0.wireOp",EDGE,"E811"),sQuery(id+"F0.wireOp",EDGE,"E812"),sQuery(id+"F0.wireOp",EDGE,"E813"),sQuery(id+"F0.wireOp",EDGE,"E814"),sQuery(id+"F0.wireOp",EDGE,"E815"),sQuery(id+"F0.wireOp",EDGE,"E816"),sQuery(id+"F0.wireOp",EDGE,"E817"),sQuery(id+"F0.wireOp",EDGE,"E818"),sQuery(id+"F0.wireOp",EDGE,"E819"),sQuery(id+"F0.wireOp",EDGE,"E820"),sQuery(id+"F0.wireOp",EDGE,"E821"),sQuery(id+"F0.wireOp",EDGE,"E822"),sQuery(id+"F0.wireOp",EDGE,"E823"),sQuery(id+"F0.wireOp",EDGE,"E824"),sQuery(id+"F0.wireOp",EDGE,"E825"),sQuery(id+"F0.wireOp",EDGE,"E826"),sQuery(id+"F0.wireOp",EDGE,"E827"),sQuery(id+"F0.wireOp",EDGE,"E828"),sQuery(id+"F0.wireOp",EDGE,"E829"),sQuery(id+"F0.wireOp",EDGE,"E830"),sQuery(id+"F0.wireOp",EDGE,"E831"),sQuery(id+"F0.wireOp",EDGE,"E832"),sQuery(id+"F0.wireOp",EDGE,"E833"),sQuery(id+"F0.wireOp",EDGE,"E834"),sQuery(id+"F0.wireOp",EDGE,"E835"),sQuery(id+"F0.wireOp",EDGE,"E836"),sQuery(id+"F0.wireOp",EDGE,"E837"),sQuery(id+"F0.wireOp",EDGE,"E838"),sQuery(id+"F0.wireOp",EDGE,"E839"),sQuery(id+"F0.wireOp",EDGE,"E840"),sQuery(id+"F0.wireOp",EDGE,"E841"),sQuery(id+"F0.wireOp",EDGE,"E842"),sQuery(id+"F0.wireOp",EDGE,"E843"),sQuery(id+"F0.wireOp",EDGE,"E844"),sQuery(id+"F0.wireOp",EDGE,"E845"),sQuery(id+"F0.wireOp",EDGE,"E846"),sQuery(id+"F0.wireOp",EDGE,"E847"),sQuery(id+"F0.wireOp",EDGE,"E848"),sQuery(id+"F0.wireOp",EDGE,"E849"),sQuery(id+"F0.wireOp",EDGE,"E850"),sQuery(id+"F0.wireOp",EDGE,"E851"),sQuery(id+"F0.wireOp",EDGE,"E852"),sQuery(id+"F0.wireOp",EDGE,"E853"),sQuery(id+"F0.wireOp",EDGE,"E854"),sQuery(id+"F0.wireOp",EDGE,"E855"),sQuery(id+"F0.wireOp",EDGE,"E856"),sQuery(id+"F0.wireOp",EDGE,"E857"),sQuery(id+"F0.wireOp",EDGE,"E858"),sQuery(id+"F0.wireOp",EDGE,"E859"),sQuery(id+"F0.wireOp",EDGE,"E860"),sQuery(id+"F0.wireOp",EDGE,"E861"),sQuery(id+"F0.wireOp",EDGE,"E862"),sQuery(id+"F0.wireOp",EDGE,"E863"),sQuery(id+"F0.wireOp",EDGE,"E864"),sQuery(id+"F0.wireOp",EDGE,"E865"),sQuery(id+"F0.wireOp",EDGE,"E866"),sQuery(id+"F0.wireOp",EDGE,"E867"),sQuery(id+"F0.wireOp",EDGE,"E868"),sQuery(id+"F0.wireOp",EDGE,"E869"),sQuery(id+"F0.wireOp",EDGE,"E870"),sQuery(id+"F0.wireOp",EDGE,"E871"),sQuery(id+"F0.wireOp",EDGE,"E872"),sQuery(id+"F0.wireOp",EDGE,"E873"),sQuery(id+"F0.wireOp",EDGE,"E874"),sQuery(id+"F0.wireOp",EDGE,"E875"),sQuery(id+"F0.wireOp",EDGE,"E876"),sQuery(id+"F0.wireOp",EDGE,"E877"),sQuery(id+"F0.wireOp",EDGE,"E878"),sQuery(id+"F0.wireOp",EDGE,"E879"),sQuery(id+"F0.wireOp",EDGE,"E880"),sQuery(id+"F0.wireOp",EDGE,"E881"),sQuery(id+"F0.wireOp",EDGE,"E882"),sQuery(id+"F0.wireOp",EDGE,"E883"),sQuery(id+"F0.wireOp",EDGE,"E884"),sQuery(id+"F0.wireOp",EDGE,"E885"),sQuery(id+"F0.wireOp",EDGE,"E886"),sQuery(id+"F0.wireOp",EDGE,"E887"),sQuery(id+"F0.wireOp",EDGE,"E888"),sQuery(id+"F0.wireOp",EDGE,"E889"),sQuery(id+"F0.wireOp",EDGE,"E890"),sQuery(id+"F0.wireOp",EDGE,"E891"),sQuery(id+"F0.wireOp",EDGE,"E892"),sQuery(id+"F0.wireOp",EDGE,"E893"),sQuery(id+"F0.wireOp",EDGE,"E894"),sQuery(id+"F0.wireOp",EDGE,"E895"),sQuery(id+"F0.wireOp",EDGE,"E896"),sQuery(id+"F0.wireOp",EDGE,"E897"),sQuery(id+"F0.wireOp",EDGE,"E898"),sQuery(id+"F0.wireOp",EDGE,"E899"),sQuery(id+"F0.wireOp",EDGE,"E900"),sQuery(id+"F0.wireOp",EDGE,"E901"),sQuery(id+"F0.wireOp",EDGE,"E902"),sQuery(id+"F0.wireOp",EDGE,"E903"),sQuery(id+"F0.wireOp",EDGE,"E904"),sQuery(id+"F0.wireOp",EDGE,"E905"),sQuery(id+"F0.wireOp",EDGE,"E906"),sQuery(id+"F0.wireOp",EDGE,"E907"),sQuery(id+"F0.wireOp",EDGE,"E908"),sQuery(id+"F0.wireOp",EDGE,"E909"),sQuery(id+"F0.wireOp",EDGE,"E910"),sQuery(id+"F0.wireOp",EDGE,"E911"),sQuery(id+"F0.wireOp",EDGE,"E912"),sQuery(id+"F0.wireOp",EDGE,"E913"),sQuery(id+"F0.wireOp",EDGE,"E914"),sQuery(id+"F0.wireOp",EDGE,"E915"),sQuery(id+"F0.wireOp",EDGE,"E916"),sQuery(id+"F0.wireOp",EDGE,"E917"),sQuery(id+"F0.wireOp",EDGE,"E918"),sQuery(id+"F0.wireOp",EDGE,"E919"),sQuery(id+"F0.wireOp",EDGE,"E920"),sQuery(id+"F0.wireOp",EDGE,"E921"),sQuery(id+"F0.wireOp",EDGE,"E922"),sQuery(id+"F0.wireOp",EDGE,"E923"),sQuery(id+"F0.wireOp",EDGE,"E924"),sQuery(id+"F0.wireOp",EDGE,"E925"),sQuery(id+"F0.wireOp",EDGE,"E926"),sQuery(id+"F0.wireOp",EDGE,"E927"),sQuery(id+"F0.wireOp",EDGE,"E928"),sQuery(id+"F0.wireOp",EDGE,"E929"),sQuery(id+"F0.wireOp",EDGE,"E930"),sQuery(id+"F0.wireOp",EDGE,"E931"),sQuery(id+"F0.wireOp",EDGE,"E932"),sQuery(id+"F0.wireOp",EDGE,"E933"),sQuery(id+"F0.wireOp",EDGE,"E934"),sQuery(id+"F0.wireOp",EDGE,"E935"),sQuery(id+"F0.wireOp",EDGE,"E936"),sQuery(id+"F0.wireOp",EDGE,"E937"),sQuery(id+"F0.wireOp",EDGE,"E938"),sQuery(id+"F0.wireOp",EDGE,"E939"),sQuery(id+"F0.wireOp",EDGE,"E940"),sQuery(id+"F0.wireOp",EDGE,"E941"),sQuery(id+"F0.wireOp",EDGE,"E942"),sQuery(id+"F0.wireOp",EDGE,"E943"),sQuery(id+"F0.wireOp",EDGE,"E944"),sQuery(id+"F0.wireOp",EDGE,"E945"),sQuery(id+"F0.wireOp",EDGE,"E946"),sQuery(id+"F0.wireOp",EDGE,"E947"),sQuery(id+"F0.wireOp",EDGE,"E948"),sQuery(id+"F0.wireOp",EDGE,"E949"),sQuery(id+"F0.wireOp",EDGE,"E950"),sQuery(id+"F0.wireOp",EDGE,"E951"),sQuery(id+"F0.wireOp",EDGE,"E952"),sQuery(id+"F0.wireOp",EDGE,"E953"),sQuery(id+"F0.wireOp",EDGE,"E954"),sQuery(id+"F0.wireOp",EDGE,"E955"),sQuery(id+"F0.wireOp",EDGE,"E956"),sQuery(id+"F0.wireOp",EDGE,"E957"),sQuery(id+"F0.wireOp",EDGE,"E958"),sQuery(id+"F0.wireOp",EDGE,"E959"),sQuery(id+"F0.wireOp",EDGE,"E960"),sQuery(id+"F0.wireOp",EDGE,"E961"),sQuery(id+"F0.wireOp",EDGE,"E962"),sQuery(id+"F0.wireOp",EDGE,"E963"),sQuery(id+"F0.wireOp",EDGE,"E964"),sQuery(id+"F0.wireOp",EDGE,"E965"),sQuery(id+"F0.wireOp",EDGE,"E966"),sQuery(id+"F0.wireOp",EDGE,"E967"),sQuery(id+"F0.wireOp",EDGE,"E968"),sQuery(id+"F0.wireOp",EDGE,"E969"),sQuery(id+"F0.wireOp",EDGE,"E970"),sQuery(id+"F0.wireOp",EDGE,"E971"),sQuery(id+"F0.wireOp",EDGE,"E972"),sQuery(id+"F0.wireOp",EDGE,"E973"),sQuery(id+"F0.wireOp",EDGE,"E974"),sQuery(id+"F0.wireOp",EDGE,"E975"),sQuery(id+"F0.wireOp",EDGE,"E976"),sQuery(id+"F0.wireOp",EDGE,"E977"),sQuery(id+"F0.wireOp",EDGE,"E978"),sQuery(id+"F0.wireOp",EDGE,"E979"),sQuery(id+"F0.wireOp",EDGE,"E980"),sQuery(id+"F0.wireOp",EDGE,"E981"),sQuery(id+"F0.wireOp",EDGE,"E982"),sQuery(id+"F0.wireOp",EDGE,"E983"),sQuery(id+"F0.wireOp",EDGE,"E984"),sQuery(id+"F0.wireOp",EDGE,"E985"),sQuery(id+"F0.wireOp",EDGE,"E986"),sQuery(id+"F0.wireOp",EDGE,"E987"),sQuery(id+"F0.wireOp",EDGE,"E988"),sQuery(id+"F0.wireOp",EDGE,"E989"),sQuery(id+"F0.wireOp",EDGE,"E990"),sQuery(id+"F0.wireOp",EDGE,"E991"),sQuery(id+"F0.wireOp",EDGE,"E992"),sQuery(id+"F0.wireOp",EDGE,"E993"),sQuery(id+"F0.wireOp",EDGE,"E994"),sQuery(id+"F0.wireOp",EDGE,"E995"),sQuery(id+"F0.wireOp",EDGE,"E996"),sQuery(id+"F0.wireOp",EDGE,"E997"),sQuery(id+"F0.wireOp",EDGE,"E998"),sQuery(id+"F0.wireOp",EDGE,"E999"),sQuery(id+"F0.wireOp",EDGE,"E1000"),sQuery(id+"F0.wireOp",EDGE,"E1001"),sQuery(id+"F0.wireOp",EDGE,"E1002"),sQuery(id+"F0.wireOp",EDGE,"E1003"),sQuery(id+"F0.wireOp",EDGE,"E1004"),sQuery(id+"F0.wireOp",EDGE,"E1005"),sQuery(id+"F0.wireOp",EDGE,"E1006"),sQuery(id+"F0.wireOp",EDGE,"E1007"),sQuery(id+"F0.wireOp",EDGE,"E1008"),sQuery(id+"F0.wireOp",EDGE,"E1009"),sQuery(id+"F0.wireOp",EDGE,"E1010"),sQuery(id+"F0.wireOp",EDGE,"E1011"),sQuery(id+"F0.wireOp",EDGE,"E1012"),sQuery(id+"F0.wireOp",EDGE,"E1013"),sQuery(id+"F0.wireOp",EDGE,"E1014"),sQuery(id+"F0.wireOp",EDGE,"E1015"),sQuery(id+"F0.wireOp",EDGE,"E1016"),sQuery(id+"F0.wireOp",EDGE,"E1017"),sQuery(id+"F0.wireOp",EDGE,"E1018"),sQuery(id+"F0.wireOp",EDGE,"E1019"),sQuery(id+"F0.wireOp",EDGE,"E1020"),sQuery(id+"F0.wireOp",EDGE,"E1021"),sQuery(id+"F0.wireOp",EDGE,"E1022"),sQuery(id+"F0.wireOp",EDGE,"E1023"),sQuery(id+"F0.wireOp",EDGE,"E1024"),sQuery(id+"F0.wireOp",EDGE,"E1025"),sQuery(id+"F0.wireOp",EDGE,"E1026"),sQuery(id+"F0.wireOp",EDGE,"E1027"),sQuery(id+"F0.wireOp",EDGE,"E1028"),sQuery(id+"F0.wireOp",EDGE,"E1029"),sQuery(id+"F0.wireOp",EDGE,"E1030"),sQuery(id+"F0.wireOp",EDGE,"E1031"),sQuery(id+"F0.wireOp",EDGE,"E1032"),sQuery(id+"F0.wireOp",EDGE,"E1033"),sQuery(id+"F0.wireOp",EDGE,"E1034"),sQuery(id+"F0.wireOp",EDGE,"E1035"),sQuery(id+"F0.wireOp",EDGE,"E1036"),sQuery(id+"F0.wireOp",EDGE,"E1037"),sQuery(id+"F0.wireOp",EDGE,"E1038"),sQuery(id+"F0.wireOp",EDGE,"E1039"),sQuery(id+"F0.wireOp",EDGE,"E1040"),sQuery(id+"F0.wireOp",EDGE,"E1041"),sQuery(id+"F0.wireOp",EDGE,"E1042"),sQuery(id+"F0.wireOp",EDGE,"E1043"),sQuery(id+"F0.wireOp",EDGE,"E1044"),sQuery(id+"F0.wireOp",EDGE,"E1045"),sQuery(id+"F0.wireOp",EDGE,"E1046"),sQuery(id+"F0.wireOp",EDGE,"E1047"),sQuery(id+"F0.wireOp",EDGE,"E1048"),sQuery(id+"F0.wireOp",EDGE,"E1049"),sQuery(id+"F0.wireOp",EDGE,"E1050"),sQuery(id+"F0.wireOp",EDGE,"E1051"),sQuery(id+"F0.wireOp",EDGE,"E1052"),sQuery(id+"F0.wireOp",EDGE,"E1053"),sQuery(id+"F0.wireOp",EDGE,"E1054"),sQuery(id+"F0.wireOp",EDGE,"E1055"),sQuery(id+"F0.wireOp",EDGE,"E1056"),sQuery(id+"F0.wireOp",EDGE,"E1057"),sQuery(id+"F0.wireOp",EDGE,"E1058"),sQuery(id+"F0.wireOp",EDGE,"E1059"),sQuery(id+"F0.wireOp",EDGE,"E1060"),sQuery(id+"F0.wireOp",EDGE,"E1061"),sQuery(id+"F0.wireOp",EDGE,"E1062"),sQuery(id+"F0.wireOp",EDGE,"E1063"),sQuery(id+"F0.wireOp",EDGE,"E1064"),sQuery(id+"F0.wireOp",EDGE,"E1065"),sQuery(id+"F0.wireOp",EDGE,"E1066"),sQuery(id+"F0.wireOp",EDGE,"E1067"),sQuery(id+"F0.wireOp",EDGE,"E1068"),sQuery(id+"F0.wireOp",EDGE,"E1069"),sQuery(id+"F0.wireOp",EDGE,"E1070"),sQuery(id+"F0.wireOp",EDGE,"E1071"),sQuery(id+"F0.wireOp",EDGE,"E1072"),sQuery(id+"F0.wireOp",EDGE,"E1073"),sQuery(id+"F0.wireOp",EDGE,"E1074"),sQuery(id+"F0.wireOp",EDGE,"E1075"),sQuery(id+"F0.wireOp",EDGE,"E1076"),sQuery(id+"F0.wireOp",EDGE,"E1077"),sQuery(id+"F0.wireOp",EDGE,"E1078"),sQuery(id+"F0.wireOp",EDGE,"E1079"),sQuery(id+"F0.wireOp",EDGE,"E1080"),sQuery(id+"F0.wireOp",EDGE,"E1081"),sQuery(id+"F0.wireOp",EDGE,"E1082"),sQuery(id+"F0.wireOp",EDGE,"E1083"),sQuery(id+"F0.wireOp",EDGE,"E1084"),sQuery(id+"F0.wireOp",EDGE,"E1085"),sQuery(id+"F0.wireOp",EDGE,"E1086"),sQuery(id+"F0.wireOp",EDGE,"E1087"),sQuery(id+"F0.wireOp",EDGE,"E1088"),sQuery(id+"F0.wireOp",EDGE,"E1089"),sQuery(id+"F0.wireOp",EDGE,"E1090"),sQuery(id+"F0.wireOp",EDGE,"E1091"),sQuery(id+"F0.wireOp",EDGE,"E1092"),sQuery(id+"F0.wireOp",EDGE,"E1093"),sQuery(id+"F0.wireOp",EDGE,"E1094"),sQuery(id+"F0.wireOp",EDGE,"E1095"),sQuery(id+"F0.wireOp",EDGE,"E1096"),sQuery(id+"F0.wireOp",EDGE,"E1097"),sQuery(id+"F0.wireOp",EDGE,"E1098"),sQuery(id+"F0.wireOp",EDGE,"E1099"),sQuery(id+"F0.wireOp",EDGE,"E1100"),sQuery(id+"F0.wireOp",EDGE,"E1101"),sQuery(id+"F0.wireOp",EDGE,"E1102"),sQuery(id+"F0.wireOp",EDGE,"E1103"),sQuery(id+"F0.wireOp",EDGE,"E1104"),sQuery(id+"F0.wireOp",EDGE,"E1105"),sQuery(id+"F0.wireOp",EDGE,"E1106"),sQuery(id+"F0.wireOp",EDGE,"E1107"),sQuery(id+"F0.wireOp",EDGE,"E1108"),sQuery(id+"F0.wireOp",EDGE,"E1109"),sQuery(id+"F0.wireOp",EDGE,"E1110"),sQuery(id+"F0.wireOp",EDGE,"E1111"),sQuery(id+"F0.wireOp",EDGE,"E1112"),sQuery(id+"F0.wireOp",EDGE,"E1113"),sQuery(id+"F0.wireOp",EDGE,"E1114"),sQuery(id+"F0.wireOp",EDGE,"E1115"),sQuery(id+"F0.wireOp",EDGE,"E1116"),sQuery(id+"F0.wireOp",EDGE,"E1117"),sQuery(id+"F0.wireOp",EDGE,"E1118"),sQuery(id+"F0.wireOp",EDGE,"E1119"),sQuery(id+"F0.wireOp",EDGE,"E1120"),sQuery(id+"F0.wireOp",EDGE,"E1121"),sQuery(id+"F0.wireOp",EDGE,"E1122"),sQuery(id+"F0.wireOp",EDGE,"E1123"),sQuery(id+"F0.wireOp",EDGE,"E1124"),sQuery(id+"F0.wireOp",EDGE,"E1125"),sQuery(id+"F0.wireOp",EDGE,"E1126"),sQuery(id+"F0.wireOp",EDGE,"E1127"),sQuery(id+"F0.wireOp",EDGE,"E1128"),sQuery(id+"F0.wireOp",EDGE,"E1129"),sQuery(id+"F0.wireOp",EDGE,"E1130"),sQuery(id+"F0.wireOp",EDGE,"E1131"),sQuery(id+"F0.wireOp",EDGE,"E1132"),sQuery(id+"F0.wireOp",EDGE,"E1133"),sQuery(id+"F0.wireOp",EDGE,"E1134"),sQuery(id+"F0.wireOp",EDGE,"E1135"),sQuery(id+"F0.wireOp",EDGE,"E1136"),sQuery(id+"F0.wireOp",EDGE,"E1137"),sQuery(id+"F0.wireOp",EDGE,"E1138"),sQuery(id+"F0.wireOp",EDGE,"E1138"),sQuery(id+"F0.wireOp",EDGE,"E1139"),sQuery(id+"F0.wireOp",EDGE,"E1140"),sQuery(id+"F0.wireOp",EDGE,"E1141"),sQuery(id+"F0.wireOp",EDGE,"E1142"),sQuery(id+"F0.wireOp",EDGE,"E1143"),sQuery(id+"F0.wireOp",EDGE,"E1144"),sQuery(id+"F0.wireOp",EDGE,"E1145"),sQuery(id+"F0.wireOp",EDGE,"E1146"),sQuery(id+"F0.wireOp",EDGE,"E1147"),sQuery(id+"F0.wireOp",EDGE,"E1148"),sQuery(id+"F0.wireOp",EDGE,"E1149"),sQuery(id+"F0.wireOp",EDGE,"E1150"),sQuery(id+"F0.wireOp",EDGE,"E1151"),sQuery(id+"F0.wireOp",EDGE,"E1152"),sQuery(id+"F0.wireOp",EDGE,"E1153"),sQuery(id+"F0.wireOp",EDGE,"E1154"),sQuery(id+"F0.wireOp",EDGE,"E1155"),sQuery(id+"F0.wireOp",EDGE,"E1156"),sQuery(id+"F0.wireOp",EDGE,"E1157"),sQuery(id+"F0.wireOp",EDGE,"E1158"),sQuery(id+"F0.wireOp",EDGE,"E1159"),sQuery(id+"F0.wireOp",EDGE,"E1160"),sQuery(id+"F0.wireOp",EDGE,"E1161"),sQuery(id+"F0.wireOp",EDGE,"E1162"),sQuery(id+"F0.wireOp",EDGE,"E1163"),sQuery(id+"F0.wireOp",EDGE,"E1164"),sQuery(id+"F0.wireOp",EDGE,"E1165"),sQuery(id+"F0.wireOp",EDGE,"E1166"),sQuery(id+"F0.wireOp",EDGE,"E1167"),sQuery(id+"F0.wireOp",EDGE,"E1168"),sQuery(id+"F0.wireOp",EDGE,"E1169"),sQuery(id+"F0.wireOp",EDGE,"E1170"),sQuery(id+"F0.wireOp",EDGE,"E1171"),sQuery(id+"F0.wireOp",EDGE,"E1172"),sQuery(id+"F0.wireOp",EDGE,"E1173"),sQuery(id+"F0.wireOp",EDGE,"E1174"),sQuery(id+"F0.wireOp",EDGE,"E1175"),sQuery(id+"F0.wireOp",EDGE,"E1176"),sQuery(id+"F0.wireOp",EDGE,"E1177"),sQuery(id+"F0.wireOp",EDGE,"E1178"),sQuery(id+"F0.wireOp",EDGE,"E1179"),sQuery(id+"F0.wireOp",EDGE,"E1180"),sQuery(id+"F0.wireOp",EDGE,"E1181"),sQuery(id+"F0.wireOp",EDGE,"E1182"),sQuery(id+"F0.wireOp",EDGE,"E1183"),sQuery(id+"F0.wireOp",EDGE,"E1184"),sQuery(id+"F0.wireOp",EDGE,"E1185"),sQuery(id+"F0.wireOp",EDGE,"E1186"),sQuery(id+"F0.wireOp",EDGE,"E1187"),sQuery(id+"F0.wireOp",EDGE,"E1188"),sQuery(id+"F0.wireOp",EDGE,"E1189"),sQuery(id+"F0.wireOp",EDGE,"E1190"),sQuery(id+"F0.wireOp",EDGE,"E1191"),sQuery(id+"F0.wireOp",EDGE,"E1192"),sQuery(id+"F0.wireOp",EDGE,"E1193"),sQuery(id+"F0.wireOp",EDGE,"E1194"),sQuery(id+"F0.wireOp",EDGE,"E1195"),sQuery(id+"F0.wireOp",EDGE,"E1196"),sQuery(id+"F0.wireOp",EDGE,"E1197"),sQuery(id+"F0.wireOp",EDGE,"E1198"),sQuery(id+"F0.wireOp",EDGE,"E1199"),sQuery(id+"F0.wireOp",EDGE,"E1200"),sQuery(id+"F0.wireOp",EDGE,"E1201"),sQuery(id+"F0.wireOp",EDGE,"E1202"),sQuery(id+"F0.wireOp",EDGE,"E1203"),sQuery(id+"F0.wireOp",EDGE,"E1204"),sQuery(id+"F0.wireOp",EDGE,"E1205"),sQuery(id+"F0.wireOp",EDGE,"E1206"),sQuery(id+"F0.wireOp",EDGE,"E1207"),sQuery(id+"F0.wireOp",EDGE,"E1208"),sQuery(id+"F0.wireOp",EDGE,"E1209"),sQuery(id+"F0.wireOp",EDGE,"E1210"),sQuery(id+"F0.wireOp",EDGE,"E1211"),sQuery(id+"F0.wireOp",EDGE,"E1212"),sQuery(id+"F0.wireOp",EDGE,"E1213"),sQuery(id+"F0.wireOp",EDGE,"E1214"),sQuery(id+"F0.wireOp",EDGE,"E1215"),sQuery(id+"F0.wireOp",EDGE,"E1216"),sQuery(id+"F0.wireOp",EDGE,"E1217"),sQuery(id+"F0.wireOp",EDGE,"E1218"),sQuery(id+"F0.wireOp",EDGE,"E1219"),sQuery(id+"F0.wireOp",EDGE,"E1220"),sQuery(id+"F0.wireOp",EDGE,"E1221"),sQuery(id+"F0.wireOp",EDGE,"E1222"),sQuery(id+"F0.wireOp",EDGE,"E1223"),sQuery(id+"F0.wireOp",EDGE,"E1224"),sQuery(id+"F0.wireOp",EDGE,"E1225"),sQuery(id+"F0.wireOp",EDGE,"E1226"),sQuery(id+"F0.wireOp",EDGE,"E1227"),sQuery(id+"F0.wireOp",EDGE,"E1228"),sQuery(id+"F0.wireOp",EDGE,"E1229"),sQuery(id+"F0.wireOp",EDGE,"E1230"),sQuery(id+"F0.wireOp",EDGE,"E1231"),sQuery(id+"F0.wireOp",EDGE,"E1232"),sQuery(id+"F0.wireOp",EDGE,"E1233"),sQuery(id+"F0.wireOp",EDGE,"E1234"),sQuery(id+"F0.wireOp",EDGE,"E1235"),sQuery(id+"F0.wireOp",EDGE,"E1236"),sQuery(id+"F0.wireOp",EDGE,"E1237"),sQuery(id+"F0.wireOp",EDGE,"E1238"),sQuery(id+"F0.wireOp",EDGE,"E1239"),sQuery(id+"F0.wireOp",EDGE,"E1240"),sQuery(id+"F0.wireOp",EDGE,"E1241"),sQuery(id+"F0.wireOp",EDGE,"E1242"),sQuery(id+"F0.wireOp",EDGE,"E1243"),sQuery(id+"F0.wireOp",EDGE,"E1244"),sQuery(id+"F0.wireOp",EDGE,"E1245"),sQuery(id+"F0.wireOp",EDGE,"E1246"),sQuery(id+"F0.wireOp",EDGE,"E1247"),sQuery(id+"F0.wireOp",EDGE,"E1248"),sQuery(id+"F0.wireOp",EDGE,"E1249"),sQuery(id+"F0.wireOp",EDGE,"E1250"),sQuery(id+"F0.wireOp",EDGE,"E1251"),sQuery(id+"F0.wireOp",EDGE,"E1252"),sQuery(id+"F0.wireOp",EDGE,"E1253"),sQuery(id+"F0.wireOp",EDGE,"E1254"),sQuery(id+"F0.wireOp",EDGE,"E1255"),sQuery(id+"F0.wireOp",EDGE,"E1256"),sQuery(id+"F0.wireOp",EDGE,"E1257"),sQuery(id+"F0.wireOp",EDGE,"E1258"),sQuery(id+"F0.wireOp",EDGE,"E1259"),sQuery(id+"F0.wireOp",EDGE,"E1260"),sQuery(id+"F0.wireOp",EDGE,"E1261"),sQuery(id+"F0.wireOp",EDGE,"E1262"),sQuery(id+"F0.wireOp",EDGE,"E1263"),sQuery(id+"F0.wireOp",EDGE,"E1264"),sQuery(id+"F0.wireOp",EDGE,"E1265"),sQuery(id+"F0.wireOp",EDGE,"E1266"),sQuery(id+"F0.wireOp",EDGE,"E1267"),sQuery(id+"F0.wireOp",EDGE,"E1268"),sQuery(id+"F0.wireOp",EDGE,"E1269"),sQuery(id+"F0.wireOp",EDGE,"E1270"),sQuery(id+"F0.wireOp",EDGE,"E1271"),sQuery(id+"F0.wireOp",EDGE,"E1272"),sQuery(id+"F0.wireOp",EDGE,"E1273"),sQuery(id+"F0.wireOp",EDGE,"E1274"),sQuery(id+"F0.wireOp",EDGE,"E1275"),sQuery(id+"F0.wireOp",EDGE,"E1276"),sQuery(id+"F0.wireOp",EDGE,"E1277"),sQuery(id+"F0.wireOp",EDGE,"E1278"),sQuery(id+"F0.wireOp",EDGE,"E1279"),sQuery(id+"F0.wireOp",EDGE,"E1280"),sQuery(id+"F0.wireOp",EDGE,"E1281"),sQuery(id+"F0.wireOp",EDGE,"E1282"),sQuery(id+"F0.wireOp",EDGE,"E1283"),sQuery(id+"F0.wireOp",EDGE,"E1284"),sQuery(id+"F0.wireOp",EDGE,"E1285"),sQuery(id+"F0.wireOp",EDGE,"E1286"),sQuery(id+"F0.wireOp",EDGE,"E1287"),sQuery(id+"F0.wireOp",EDGE,"E1288"),sQuery(id+"F0.wireOp",EDGE,"E1289"),sQuery(id+"F0.wireOp",EDGE,"E1290"),sQuery(id+"F0.wireOp",EDGE,"E1291"),sQuery(id+"F0.wireOp",EDGE,"E1292"),sQuery(id+"F0.wireOp",EDGE,"E1293"),sQuery(id+"F0.wireOp",EDGE,"E1294"),sQuery(id+"F0.wireOp",EDGE,"E1295"),sQuery(id+"F0.wireOp",EDGE,"E1296"),sQuery(id+"F0.wireOp",EDGE,"E1297"),sQuery(id+"F0.wireOp",EDGE,"E1298"),sQuery(id+"F0.wireOp",EDGE,"E1299"),sQuery(id+"F0.wireOp",EDGE,"E1300"),sQuery(id+"F0.wireOp",EDGE,"E1301"),sQuery(id+"F0.wireOp",EDGE,"E1302"),sQuery(id+"F0.wireOp",EDGE,"E1303"),sQuery(id+"F0.wireOp",EDGE,"E1304"),sQuery(id+"F0.wireOp",EDGE,"E1305"),sQuery(id+"F0.wireOp",EDGE,"E1306"),sQuery(id+"F0.wireOp",EDGE,"E1307"),sQuery(id+"F0.wireOp",EDGE,"E1308"),sQuery(id+"F0.wireOp",EDGE,"E1309"),sQuery(id+"F0.wireOp",EDGE,"E1310"),sQuery(id+"F0.wireOp",EDGE,"E1311"),sQuery(id+"F0.wireOp",EDGE,"E1312"),sQuery(id+"F0.wireOp",EDGE,"E1313"),sQuery(id+"F0.wireOp",EDGE,"E1314"),sQuery(id+"F0.wireOp",EDGE,"E1315"),sQuery(id+"F0.wireOp",EDGE,"E1316"),sQuery(id+"F0.wireOp",EDGE,"E1317"),sQuery(id+"F0.wireOp",EDGE,"E1318"),sQuery(id+"F0.wireOp",EDGE,"E1319"),sQuery(id+"F0.wireOp",EDGE,"E1320"),sQuery(id+"F0.wireOp",EDGE,"E1321"),sQuery(id+"F0.wireOp",EDGE,"E1322"),sQuery(id+"F0.wireOp",EDGE,"E1323"),sQuery(id+"F0.wireOp",EDGE,"E1324"),sQuery(id+"F0.wireOp",EDGE,"E1325"),sQuery(id+"F0.wireOp",EDGE,"E1326"),sQuery(id+"F0.wireOp",EDGE,"E1327"),sQuery(id+"F0.wireOp",EDGE,"E1328"),sQuery(id+"F0.wireOp",EDGE,"E1329"),sQuery(id+"F0.wireOp",EDGE,"E1330"),sQuery(id+"F0.wireOp",EDGE,"E1331"),sQuery(id+"F0.wireOp",EDGE,"E1332"),sQuery(id+"F0.wireOp",EDGE,"E1333"),sQuery(id+"F0.wireOp",EDGE,"E1334"),sQuery(id+"F0.wireOp",EDGE,"E1335"),sQuery(id+"F0.wireOp",EDGE,"E1336"),sQuery(id+"F0.wireOp",EDGE,"E1337"),sQuery(id+"F0.wireOp",EDGE,"E1338"),sQuery(id+"F0.wireOp",EDGE,"E1339"),sQuery(id+"F0.wireOp",EDGE,"E1340"),sQuery(id+"F0.wireOp",EDGE,"E1341"),sQuery(id+"F0.wireOp",EDGE,"E1342"),sQuery(id+"F0.wireOp",EDGE,"E1343"),sQuery(id+"F0.wireOp",EDGE,"E1344"),sQuery(id+"F0.wireOp",EDGE,"E1345"),sQuery(id+"F0.wireOp",EDGE,"E1346"),sQuery(id+"F0.wireOp",EDGE,"E1347"),sQuery(id+"F0.wireOp",EDGE,"E1348"),sQuery(id+"F0.wireOp",EDGE,"E1349"),sQuery(id+"F0.wireOp",EDGE,"E1350"),sQuery(id+"F0.wireOp",EDGE,"E1351"),sQuery(id+"F0.wireOp",EDGE,"E1352"),sQuery(id+"F0.wireOp",EDGE,"E1353"),sQuery(id+"F0.wireOp",EDGE,"E1354"),sQuery(id+"F0.wireOp",EDGE,"E1355"),sQuery(id+"F0.wireOp",EDGE,"E1356"),sQuery(id+"F0.wireOp",EDGE,"E1357"),sQuery(id+"F0.wireOp",EDGE,"E1358"),sQuery(id+"F0.wireOp",EDGE,"E1359"),sQuery(id+"F0.wireOp",EDGE,"E1360"),sQuery(id+"F0.wireOp",EDGE,"E1361"),sQuery(id+"F0.wireOp",EDGE,"E1362"),sQuery(id+"F0.wireOp",EDGE,"E1363"),sQuery(id+"F0.wireOp",EDGE,"E1364"),sQuery(id+"F0.wireOp",EDGE,"E1365"),sQuery(id+"F0.wireOp",EDGE,"E1366"),sQuery(id+"F0.wireOp",EDGE,"E1367"),sQuery(id+"F0.wireOp",EDGE,"E1368"),sQuery(id+"F0.wireOp",EDGE,"E1369"),sQuery(id+"F0.wireOp",EDGE,"E1370"),sQuery(id+"F0.wireOp",EDGE,"E1371"),sQuery(id+"F0.wireOp",EDGE,"E1372"),sQuery(id+"F0.wireOp",EDGE,"E1373"),sQuery(id+"F0.wireOp",EDGE,"E1374"),sQuery(id+"F0.wireOp",EDGE,"E1375"),sQuery(id+"F0.wireOp",EDGE,"E1376"),sQuery(id+"F0.wireOp",EDGE,"E1377"),sQuery(id+"F0.wireOp",EDGE,"E1378"),sQuery(id+"F0.wireOp",EDGE,"E1379"),sQuery(id+"F0.wireOp",EDGE,"E1380"),sQuery(id+"F0.wireOp",EDGE,"E1381"),sQuery(id+"F0.wireOp",EDGE,"E1382"),sQuery(id+"F0.wireOp",EDGE,"E1383"),sQuery(id+"F0.wireOp",EDGE,"E1384"),sQuery(id+"F0.wireOp",EDGE,"E1385"),sQuery(id+"F0.wireOp",EDGE,"E1386"),sQuery(id+"F0.wireOp",EDGE,"E1387"),sQuery(id+"F0.wireOp",EDGE,"E1388"),sQuery(id+"F0.wireOp",EDGE,"E1389"),sQuery(id+"F0.wireOp",EDGE,"E1390"),sQuery(id+"F0.wireOp",EDGE,"E1391"),sQuery(id+"F0.wireOp",EDGE,"E1392"),sQuery(id+"F0.wireOp",EDGE,"E1393"),sQuery(id+"F0.wireOp",EDGE,"E1394"),sQuery(id+"F0.wireOp",EDGE,"E1395"),sQuery(id+"F0.wireOp",EDGE,"E1396"),sQuery(id+"F0.wireOp",EDGE,"E1397"),sQuery(id+"F0.wireOp",EDGE,"E1398"),sQuery(id+"F0.wireOp",EDGE,"E1399"),sQuery(id+"F0.wireOp",EDGE,"E1400"),sQuery(id+"F0.wireOp",EDGE,"E1401"),sQuery(id+"F0.wireOp",EDGE,"E1402"),sQuery(id+"F0.wireOp",EDGE,"E1403"),sQuery(id+"F0.wireOp",EDGE,"E1404"),sQuery(id+"F0.wireOp",EDGE,"E1405"),sQuery(id+"F0.wireOp",EDGE,"E1406"),sQuery(id+"F0.wireOp",EDGE,"E1407"),sQuery(id+"F0.wireOp",EDGE,"E1408"),sQuery(id+"F0.wireOp",EDGE,"E1409"),sQuery(id+"F0.wireOp",EDGE,"E1410"),sQuery(id+"F0.wireOp",EDGE,"E1411"),sQuery(id+"F0.wireOp",EDGE,"E1412"),sQuery(id+"F0.wireOp",EDGE,"E1413"),sQuery(id+"F0.wireOp",EDGE,"E1414"),sQuery(id+"F0.wireOp",EDGE,"E1415"),sQuery(id+"F0.wireOp",EDGE,"E1416"),sQuery(id+"F0.wireOp",EDGE,"E1417"),sQuery(id+"F0.wireOp",EDGE,"E1418"),sQuery(id+"F0.wireOp",EDGE,"E1419"),sQuery(id+"F0.wireOp",EDGE,"E1420"),sQuery(id+"F0.wireOp",EDGE,"E1421"),sQuery(id+"F0.wireOp",EDGE,"E1422"),sQuery(id+"F0.wireOp",EDGE,"E1423"),sQuery(id+"F0.wireOp",EDGE,"E1424"),sQuery(id+"F0.wireOp",EDGE,"E1425"),sQuery(id+"F0.wireOp",EDGE,"E1426"),sQuery(id+"F0.wireOp",EDGE,"E1427"),sQuery(id+"F0.wireOp",EDGE,"E1428"),sQuery(id+"F0.wireOp",EDGE,"E1429"),sQuery(id+"F0.wireOp",EDGE,"E1430"),sQuery(id+"F0.wireOp",EDGE,"E1431"),sQuery(id+"F0.wireOp",EDGE,"E1432"),sQuery(id+"F0.wireOp",EDGE,"E1433"),sQuery(id+"F0.wireOp",EDGE,"E1434"),sQuery(id+"F0.wireOp",EDGE,"E1435"),sQuery(id+"F0.wireOp",EDGE,"E1436"),sQuery(id+"F0.wireOp",EDGE,"E1437"),sQuery(id+"F0.wireOp",EDGE,"E1438"),sQuery(id+"F0.wireOp",EDGE,"E1439"),sQuery(id+"F0.wireOp",EDGE,"E1440"),sQuery(id+"F0.wireOp",EDGE,"E1441"),sQuery(id+"F0.wireOp",EDGE,"E1442"),sQuery(id+"F0.wireOp",EDGE,"E1443"),sQuery(id+"F0.wireOp",EDGE,"E1444"),sQuery(id+"F0.wireOp",EDGE,"E1445"),sQuery(id+"F0.wireOp",EDGE,"E1446"),sQuery(id+"F0.wireOp",EDGE,"E1447"),sQuery(id+"F0.wireOp",EDGE,"E1448"),sQuery(id+"F0.wireOp",EDGE,"E1449"),sQuery(id+"F0.wireOp",EDGE,"E1450"),sQuery(id+"F0.wireOp",EDGE,"E1451"),sQuery(id+"F0.wireOp",EDGE,"E1452"),sQuery(id+"F0.wireOp",EDGE,"E1453"),sQuery(id+"F0.wireOp",EDGE,"E1454"),sQuery(id+"F0.wireOp",EDGE,"E1455"),sQuery(id+"F0.wireOp",EDGE,"E1456"),sQuery(id+"F0.wireOp",EDGE,"E1457"),sQuery(id+"F0.wireOp",EDGE,"E1458"),sQuery(id+"F0.wireOp",EDGE,"E1459"),sQuery(id+"F0.wireOp",EDGE,"E1460"),sQuery(id+"F0.wireOp",EDGE,"E1461"),sQuery(id+"F0.wireOp",EDGE,"E1462"),sQuery(id+"F0.wireOp",EDGE,"E1463"),sQuery(id+"F0.wireOp",EDGE,"E1464"),sQuery(id+"F0.wireOp",EDGE,"E1465"),sQuery(id+"F0.wireOp",EDGE,"E1466"),sQuery(id+"F0.wireOp",EDGE,"E1467"),sQuery(id+"F0.wireOp",EDGE,"E1468"),sQuery(id+"F0.wireOp",EDGE,"E1469"),sQuery(id+"F0.wireOp",EDGE,"E1470"),sQuery(id+"F0.wireOp",EDGE,"E1471"),sQuery(id+"F0.wireOp",EDGE,"E1472"),sQuery(id+"F0.wireOp",EDGE,"E1473"),sQuery(id+"F0.wireOp",EDGE,"E1474"),sQuery(id+"F0.wireOp",EDGE,"E1475"),sQuery(id+"F0.wireOp",EDGE,"E1476"),sQuery(id+"F0.wireOp",EDGE,"E1477"),sQuery(id+"F0.wireOp",EDGE,"E1478"),sQuery(id+"F0.wireOp",EDGE,"E1479"),sQuery(id+"F0.wireOp",EDGE,"E1480"),sQuery(id+"F0.wireOp",EDGE,"E1481"),sQuery(id+"F0.wireOp",EDGE,"E1482"),sQuery(id+"F0.wireOp",EDGE,"E1483"),sQuery(id+"F0.wireOp",EDGE,"E1484"),sQuery(id+"F0.wireOp",EDGE,"E1485"),sQuery(id+"F0.wireOp",EDGE,"E1486"),sQuery(id+"F0.wireOp",EDGE,"E1487"),sQuery(id+"F0.wireOp",EDGE,"E1488"),sQuery(id+"F0.wireOp",EDGE,"E1489"),sQuery(id+"F0.wireOp",EDGE,"E1490"),sQuery(id+"F0.wireOp",EDGE,"E1491"),sQuery(id+"F0.wireOp",EDGE,"E1492"),sQuery(id+"F0.wireOp",EDGE,"E1493"),sQuery(id+"F0.wireOp",EDGE,"E1494"),sQuery(id+"F0.wireOp",EDGE,"E1495"),sQuery(id+"F0.wireOp",EDGE,"E1496"),sQuery(id+"F0.wireOp",EDGE,"E1497"),sQuery(id+"F0.wireOp",EDGE,"E1498"),sQuery(id+"F0.wireOp",EDGE,"E1499"),sQuery(id+"F0.wireOp",EDGE,"E1500"),sQuery(id+"F0.wireOp",EDGE,"E1501"),sQuery(id+"F0.wireOp",EDGE,"E1502"),sQuery(id+"F0.wireOp",EDGE,"E1503"),sQuery(id+"F0.wireOp",EDGE,"E1504"),sQuery(id+"F0.wireOp",EDGE,"E1505"),sQuery(id+"F0.wireOp",EDGE,"E1506"),sQuery(id+"F0.wireOp",EDGE,"E1507"),sQuery(id+"F0.wireOp",EDGE,"E1508"),sQuery(id+"F0.wireOp",EDGE,"E1509"),sQuery(id+"F0.wireOp",EDGE,"E1510"),sQuery(id+"F0.wireOp",EDGE,"E1511"),sQuery(id+"F0.wireOp",EDGE,"E1512"),sQuery(id+"F0.wireOp",EDGE,"E1513"),sQuery(id+"F0.wireOp",EDGE,"E1514"),sQuery(id+"F0.wireOp",EDGE,"E1515"),sQuery(id+"F0.wireOp",EDGE,"E1516"),sQuery(id+"F0.wireOp",EDGE,"E1517"),sQuery(id+"F0.wireOp",EDGE,"E1518"),sQuery(id+"F0.wireOp",EDGE,"E1519"),sQuery(id+"F0.wireOp",EDGE,"E1520"),sQuery(id+"F0.wireOp",EDGE,"E1521"),sQuery(id+"F0.wireOp",EDGE,"E1522"),sQuery(id+"F0.wireOp",EDGE,"E1523"),sQuery(id+"F0.wireOp",EDGE,"E1524"),sQuery(id+"F0.wireOp",EDGE,"E1525"),sQuery(id+"F0.wireOp",EDGE,"E1526"),sQuery(id+"F0.wireOp",EDGE,"E1527"),sQuery(id+"F0.wireOp",EDGE,"E1528"),sQuery(id+"F0.wireOp",EDGE,"E1529"),sQuery(id+"F0.wireOp",EDGE,"E1530"),sQuery(id+"F0.wireOp",EDGE,"E1531"),sQuery(id+"F0.wireOp",EDGE,"E1532"),sQuery(id+"F0.wireOp",EDGE,"E1533"),sQuery(id+"F0.wireOp",EDGE,"E1534"),sQuery(id+"F0.wireOp",EDGE,"E1535"),sQuery(id+"F0.wireOp",EDGE,"E1536"),sQuery(id+"F0.wireOp",EDGE,"E1537"),sQuery(id+"F0.wireOp",EDGE,"E1538"),sQuery(id+"F0.wireOp",EDGE,"E1539"),sQuery(id+"F0.wireOp",EDGE,"E1540"),sQuery(id+"F0.wireOp",EDGE,"E1541"),sQuery(id+"F0.wireOp",EDGE,"E1542"),sQuery(id+"F0.wireOp",EDGE,"E1543"),sQuery(id+"F0.wireOp",EDGE,"E1544"),sQuery(id+"F0.wireOp",EDGE,"E1545"),sQuery(id+"F0.wireOp",EDGE,"E1546"),sQuery(id+"F0.wireOp",EDGE,"E1547"),sQuery(id+"F0.wireOp",EDGE,"E1548"),sQuery(id+"F0.wireOp",EDGE,"E1549"),sQuery(id+"F0.wireOp",EDGE,"E1550"),sQuery(id+"F0.wireOp",EDGE,"E1551"),sQuery(id+"F0.wireOp",EDGE,"E1552"),sQuery(id+"F0.wireOp",EDGE,"E1553"),sQuery(id+"F0.wireOp",EDGE,"E1554"),sQuery(id+"F0.wireOp",EDGE,"E1555"),sQuery(id+"F0.wireOp",EDGE,"E1556"),sQuery(id+"F0.wireOp",EDGE,"E1557"),sQuery(id+"F0.wireOp",EDGE,"E1558"),sQuery(id+"F0.wireOp",EDGE,"E1559"),sQuery(id+"F0.wireOp",EDGE,"E1560"),sQuery(id+"F0.wireOp",EDGE,"E1561"),sQuery(id+"F0.wireOp",EDGE,"E1562"),sQuery(id+"F0.wireOp",EDGE,"E1563"),sQuery(id+"F0.wireOp",EDGE,"E1564"),sQuery(id+"F0.wireOp",EDGE,"E1565"),sQuery(id+"F0.wireOp",EDGE,"E1566"),sQuery(id+"F0.wireOp",EDGE,"E1567"),sQuery(id+"F0.wireOp",EDGE,"E1568"),sQuery(id+"F0.wireOp",EDGE,"E1569"),sQuery(id+"F0.wireOp",EDGE,"E1570"),sQuery(id+"F0.wireOp",EDGE,"E1571"),sQuery(id+"F0.wireOp",EDGE,"E1572"),sQuery(id+"F0.wireOp",EDGE,"E1573"),sQuery(id+"F0.wireOp",EDGE,"E1574"),sQuery(id+"F0.wireOp",EDGE,"E1575"),sQuery(id+"F0.wireOp",EDGE,"E1576"),sQuery(id+"F0.wireOp",EDGE,"E1577"),sQuery(id+"F0.wireOp",EDGE,"E1578"),sQuery(id+"F0.wireOp",EDGE,"E1579"),sQuery(id+"F0.wireOp",EDGE,"E1580"),sQuery(id+"F0.wireOp",EDGE,"E1581"),sQuery(id+"F0.wireOp",EDGE,"E1582"),sQuery(id+"F0.wireOp",EDGE,"E1583"),sQuery(id+"F0.wireOp",EDGE,"E1584"),sQuery(id+"F0.wireOp",EDGE,"E1585"),sQuery(id+"F0.wireOp",EDGE,"E1586"),sQuery(id+"F0.wireOp",EDGE,"E1587"),sQuery(id+"F0.wireOp",EDGE,"E1588"),sQuery(id+"F0.wireOp",EDGE,"E1589"),sQuery(id+"F0.wireOp",EDGE,"E1590"),sQuery(id+"F0.wireOp",EDGE,"E1591"),sQuery(id+"F0.wireOp",EDGE,"E1592"),sQuery(id+"F0.wireOp",EDGE,"E1593"),sQuery(id+"F0.wireOp",EDGE,"E1594"),sQuery(id+"F0.wireOp",EDGE,"E1595"),sQuery(id+"F0.wireOp",EDGE,"E1596"),sQuery(id+"F0.wireOp",EDGE,"E1597"),sQuery(id+"F0.wireOp",EDGE,"E1598"),sQuery(id+"F0.wireOp",EDGE,"E1599"),sQuery(id+"F0.wireOp",EDGE,"E1600"),sQuery(id+"F0.wireOp",EDGE,"E1601"),sQuery(id+"F0.wireOp",EDGE,"E1602"),sQuery(id+"F0.wireOp",EDGE,"E1603"),sQuery(id+"F0.wireOp",EDGE,"E1604"),sQuery(id+"F0.wireOp",EDGE,"E1605"),sQuery(id+"F0.wireOp",EDGE,"E1606"),sQuery(id+"F0.wireOp",EDGE,"E1607"),sQuery(id+"F0.wireOp",EDGE,"E1608"),sQuery(id+"F0.wireOp",EDGE,"E1609"),sQuery(id+"F0.wireOp",EDGE,"E1610"),sQuery(id+"F0.wireOp",EDGE,"E1611"),sQuery(id+"F0.wireOp",EDGE,"E1612"),sQuery(id+"F0.wireOp",EDGE,"E1613"),sQuery(id+"F0.wireOp",EDGE,"E1614"),sQuery(id+"F0.wireOp",EDGE,"E1615"),sQuery(id+"F0.wireOp",EDGE,"E1616"),sQuery(id+"F0.wireOp",EDGE,"E1617"),sQuery(id+"F0.wireOp",EDGE,"E1618"),sQuery(id+"F0.wireOp",EDGE,"E1619"),sQuery(id+"F0.wireOp",EDGE,"E1620"),sQuery(id+"F0.wireOp",EDGE,"E1621"),sQuery(id+"F0.wireOp",EDGE,"E1622"),sQuery(id+"F0.wireOp",EDGE,"E1623"),sQuery(id+"F0.wireOp",EDGE,"E1624"),sQuery(id+"F0.wireOp",EDGE,"E1625"),sQuery(id+"F0.wireOp",EDGE,"E1626"),sQuery(id+"F0.wireOp",EDGE,"E1627"),sQuery(id+"F0.wireOp",EDGE,"E1628"),sQuery(id+"F0.wireOp",EDGE,"E1629"),sQuery(id+"F0.wireOp",EDGE,"E1630"),sQuery(id+"F0.wireOp",EDGE,"E1631"),sQuery(id+"F0.wireOp",EDGE,"E1632"),sQuery(id+"F0.wireOp",EDGE,"E1633"),sQuery(id+"F0.wireOp",EDGE,"E1634"),sQuery(id+"F0.wireOp",EDGE,"E1635"),sQuery(id+"F0.wireOp",EDGE,"E1636"),sQuery(id+"F0.wireOp",EDGE,"E1637"),sQuery(id+"F0.wireOp",EDGE,"E1638"),sQuery(id+"F0.wireOp",EDGE,"E1639"),sQuery(id+"F0.wireOp",EDGE,"E1640"),sQuery(id+"F0.wireOp",EDGE,"E1641"),sQuery(id+"F0.wireOp",EDGE,"E1642"),sQuery(id+"F0.wireOp",EDGE,"E1643"),sQuery(id+"F0.wireOp",EDGE,"E1644"),sQuery(id+"F0.wireOp",EDGE,"E1645"),sQuery(id+"F0.wireOp",EDGE,"E1646"),sQuery(id+"F0.wireOp",EDGE,"E1647"),sQuery(id+"F0.wireOp",EDGE,"E1648"),sQuery(id+"F0.wireOp",EDGE,"E1649"),sQuery(id+"F0.wireOp",EDGE,"E1650"),sQuery(id+"F0.wireOp",EDGE,"E1651"),sQuery(id+"F0.wireOp",EDGE,"E1652"),sQuery(id+"F0.wireOp",EDGE,"E1653"),sQuery(id+"F0.wireOp",EDGE,"E1654"),sQuery(id+"F0.wireOp",EDGE,"E1655"),sQuery(id+"F0.wireOp",EDGE,"E1656"),sQuery(id+"F0.wireOp",EDGE,"E1657"),sQuery(id+"F0.wireOp",EDGE,"E1658"),sQuery(id+"F0.wireOp",EDGE,"E1659"),sQuery(id+"F0.wireOp",EDGE,"E1660"),sQuery(id+"F0.wireOp",EDGE,"E1661"),sQuery(id+"F0.wireOp",EDGE,"E1662"),sQuery(id+"F0.wireOp",EDGE,"E1663"),sQuery(id+"F0.wireOp",EDGE,"E1664"),sQuery(id+"F0.wireOp",EDGE,"E1665"),sQuery(id+"F0.wireOp",EDGE,"E1666"),sQuery(id+"F0.wireOp",EDGE,"E1667"),sQuery(id+"F0.wireOp",EDGE,"E1668"),sQuery(id+"F0.wireOp",EDGE,"E1669"),sQuery(id+"F0.wireOp",EDGE,"E1670"),sQuery(id+"F0.wireOp",EDGE,"E1671"),sQuery(id+"F0.wireOp",EDGE,"E1672"),sQuery(id+"F0.wireOp",EDGE,"E1673"),sQuery(id+"F0.wireOp",EDGE,"E1674"),sQuery(id+"F0.wireOp",EDGE,"E1675"),sQuery(id+"F0.wireOp",EDGE,"E1676"),sQuery(id+"F0.wireOp",EDGE,"E1677"),sQuery(id+"F0.wireOp",EDGE,"E1678"),sQuery(id+"F0.wireOp",EDGE,"E1679"),sQuery(id+"F0.wireOp",EDGE,"E1680"),sQuery(id+"F0.wireOp",EDGE,"E1681"),sQuery(id+"F0.wireOp",EDGE,"E1682"),sQuery(id+"F0.wireOp",EDGE,"E1683"),sQuery(id+"F0.wireOp",EDGE,"E1684"),sQuery(id+"F0.wireOp",EDGE,"E1685"),sQuery(id+"F0.wireOp",EDGE,"E1686"),sQuery(id+"F0.wireOp",EDGE,"E1687"),sQuery(id+"F0.wireOp",EDGE,"E1688"),sQuery(id+"F0.wireOp",EDGE,"E1689"),sQuery(id+"F0.wireOp",EDGE,"E1690"),sQuery(id+"F0.wireOp",EDGE,"E1691"),sQuery(id+"F0.wireOp",EDGE,"E1692"),sQuery(id+"F0.wireOp",EDGE,"E1693"),sQuery(id+"F0.wireOp",EDGE,"E1694"),sQuery(id+"F0.wireOp",EDGE,"E1695"),sQuery(id+"F0.wireOp",EDGE,"E1696"),sQuery(id+"F0.wireOp",EDGE,"E1697"),sQuery(id+"F0.wireOp",EDGE,"E1698"),sQuery(id+"F0.wireOp",EDGE,"E1699"),sQuery(id+"F0.wireOp",EDGE,"E1700"),sQuery(id+"F0.wireOp",EDGE,"E1701"),sQuery(id+"F0.wireOp",EDGE,"E1702"),sQuery(id+"F0.wireOp",EDGE,"E1703"),sQuery(id+"F0.wireOp",EDGE,"E1704"),sQuery(id+"F0.wireOp",EDGE,"E1705"),sQuery(id+"F0.wireOp",EDGE,"E1706"),sQuery(id+"F0.wireOp",EDGE,"E1707"),sQuery(id+"F0.wireOp",EDGE,"E1708"),sQuery(id+"F0.wireOp",EDGE,"E1709"),sQuery(id+"F0.wireOp",EDGE,"E1710"),sQuery(id+"F0.wireOp",EDGE,"E1711"),sQuery(id+"F0.wireOp",EDGE,"E1712"),sQuery(id+"F0.wireOp",EDGE,"E1713"),sQuery(id+"F0.wireOp",EDGE,"E1714"),sQuery(id+"F0.wireOp",EDGE,"E1715"),sQuery(id+"F0.wireOp",EDGE,"E1716"),sQuery(id+"F0.wireOp",EDGE,"E1717"),sQuery(id+"F0.wireOp",EDGE,"E1718"),sQuery(id+"F0.wireOp",EDGE,"E1719"),sQuery(id+"F0.wireOp",EDGE,"E1720"),sQuery(id+"F0.wireOp",EDGE,"E1721"),sQuery(id+"F0.wireOp",EDGE,"E1722"),sQuery(id+"F0.wireOp",EDGE,"E1723"),sQuery(id+"F0.wireOp",EDGE,"E1724"),sQuery(id+"F0.wireOp",EDGE,"E1725"),sQuery(id+"F0.wireOp",EDGE,"E1726"),sQuery(id+"F0.wireOp",EDGE,"E1727"),sQuery(id+"F0.wireOp",EDGE,"E1728"),sQuery(id+"F0.wireOp",EDGE,"E1729"),sQuery(id+"F0.wireOp",EDGE,"E1730"),sQuery(id+"F0.wireOp",EDGE,"E1731"),sQuery(id+"F0.wireOp",EDGE,"E1732"),sQuery(id+"F0.wireOp",EDGE,"E1733"),sQuery(id+"F0.wireOp",EDGE,"E1734"),sQuery(id+"F0.wireOp",EDGE,"E1735"),sQuery(id+"F0.wireOp",EDGE,"E1736"),sQuery(id+"F0.wireOp",EDGE,"E1737"),sQuery(id+"F0.wireOp",EDGE,"E1738"),sQuery(id+"F0.wireOp",EDGE,"E1739"),sQuery(id+"F0.wireOp",EDGE,"E1740"),sQuery(id+"F0.wireOp",EDGE,"E1741"),sQuery(id+"F0.wireOp",EDGE,"E1742"),sQuery(id+"F0.wireOp",EDGE,"E1743"),sQuery(id+"F0.wireOp",EDGE,"E1744"),sQuery(id+"F0.wireOp",EDGE,"E1745"),sQuery(id+"F0.wireOp",EDGE,"E1746"),sQuery(id+"F0.wireOp",EDGE,"E1747"),sQuery(id+"F0.wireOp",EDGE,"E1748"),sQuery(id+"F0.wireOp",EDGE,"E1749"),sQuery(id+"F0.wireOp",EDGE,"E1750"),sQuery(id+"F0.wireOp",EDGE,"E1751"),sQuery(id+"F0.wireOp",EDGE,"E1752"),sQuery(id+"F0.wireOp",EDGE,"E1753"),sQuery(id+"F0.wireOp",EDGE,"E1754"),sQuery(id+"F0.wireOp",EDGE,"E1755"),sQuery(id+"F0.wireOp",EDGE,"E1756"),sQuery(id+"F0.wireOp",EDGE,"E1757"),sQuery(id+"F0.wireOp",EDGE,"E1758"),sQuery(id+"F0.wireOp",EDGE,"E1759"),sQuery(id+"F0.wireOp",EDGE,"E1760"),sQuery(id+"F0.wireOp",EDGE,"E1761"),sQuery(id+"F0.wireOp",EDGE,"E1762"),sQuery(id+"F0.wireOp",EDGE,"E1763"),sQuery(id+"F0.wireOp",EDGE,"E1764"),sQuery(id+"F0.wireOp",EDGE,"E1765"),sQuery(id+"F0.wireOp",EDGE,"E1766"),sQuery(id+"F0.wireOp",EDGE,"E1767"),sQuery(id+"F0.wireOp",EDGE,"E1768"),sQuery(id+"F0.wireOp",EDGE,"E1769"),sQuery(id+"F0.wireOp",EDGE,"E1770"),sQuery(id+"F0.wireOp",EDGE,"E1771"),sQuery(id+"F0.wireOp",EDGE,"E1772"),sQuery(id+"F0.wireOp",EDGE,"E1773"),sQuery(id+"F0.wireOp",EDGE,"E1774"),sQuery(id+"F0.wireOp",EDGE,"E1775"),sQuery(id+"F0.wireOp",EDGE,"E1776"),sQuery(id+"F0.wireOp",EDGE,"E1777"),sQuery(id+"F0.wireOp",EDGE,"E1778"),sQuery(id+"F0.wireOp",EDGE,"E1779"),sQuery(id+"F0.wireOp",EDGE,"E1780"),sQuery(id+"F0.wireOp",EDGE,"E1781"),sQuery(id+"F0.wireOp",EDGE,"E1782"),sQuery(id+"F0.wireOp",EDGE,"E1783"),sQuery(id+"F0.wireOp",EDGE,"E1784"),sQuery(id+"F0.wireOp",EDGE,"E1785"),sQuery(id+"F0.wireOp",EDGE,"E1786"),sQuery(id+"F0.wireOp",EDGE,"E1787"),sQuery(id+"F0.wireOp",EDGE,"E1788"),sQuery(id+"F0.wireOp",EDGE,"E1789"),sQuery(id+"F0.wireOp",EDGE,"E1790"),sQuery(id+"F0.wireOp",EDGE,"E1791"),sQuery(id+"F0.wireOp",EDGE,"E1792"),sQuery(id+"F0.wireOp",EDGE,"E1793"),sQuery(id+"F0.wireOp",EDGE,"E1794"),sQuery(id+"F0.wireOp",EDGE,"E1795"),sQuery(id+"F0.wireOp",EDGE,"E1796"),sQuery(id+"F0.wireOp",EDGE,"E1797"),sQuery(id+"F0.wireOp",EDGE,"E1798"),sQuery(id+"F0.wireOp",EDGE,"E1799"),sQuery(id+"F0.wireOp",EDGE,"E1800"),sQuery(id+"F0.wireOp",EDGE,"E1801"),sQuery(id+"F0.wireOp",EDGE,"E1802"),sQuery(id+"F0.wireOp",EDGE,"E1803"),sQuery(id+"F0.wireOp",EDGE,"E1804"),sQuery(id+"F0.wireOp",EDGE,"E1805"),sQuery(id+"F0.wireOp",EDGE,"E1806"),sQuery(id+"F0.wireOp",EDGE,"E1807"),sQuery(id+"F0.wireOp",EDGE,"E1808"),sQuery(id+"F0.wireOp",EDGE,"E1809"),sQuery(id+"F0.wireOp",EDGE,"E1810"),sQuery(id+"F0.wireOp",EDGE,"E1811"),sQuery(id+"F0.wireOp",EDGE,"E1812"),sQuery(id+"F0.wireOp",EDGE,"E1813"),sQuery(id+"F0.wireOp",EDGE,"E1814"),sQuery(id+"F0.wireOp",EDGE,"E1815"),sQuery(id+"F0.wireOp",EDGE,"E1816"),sQuery(id+"F0.wireOp",EDGE,"E1817"),sQuery(id+"F0.wireOp",EDGE,"E1818"),sQuery(id+"F0.wireOp",EDGE,"E1819"),sQuery(id+"F0.wireOp",EDGE,"E1820"),sQuery(id+"F0.wireOp",EDGE,"E1821"),sQuery(id+"F0.wireOp",EDGE,"E1822"),sQuery(id+"F0.wireOp",EDGE,"E1823"),sQuery(id+"F0.wireOp",EDGE,"E1824"),sQuery(id+"F0.wireOp",EDGE,"E1825"),sQuery(id+"F0.wireOp",EDGE,"E1826"),sQuery(id+"F0.wireOp",EDGE,"E1827"),sQuery(id+"F0.wireOp",EDGE,"E1828"),sQuery(id+"F0.wireOp",EDGE,"E1829"),sQuery(id+"F0.wireOp",EDGE,"E1830"),sQuery(id+"F0.wireOp",EDGE,"E1831"),sQuery(id+"F0.wireOp",EDGE,"E1832"),sQuery(id+"F0.wireOp",EDGE,"E1833"),sQuery(id+"F0.wireOp",EDGE,"E1834"),sQuery(id+"F0.wireOp",EDGE,"E1835"),sQuery(id+"F0.wireOp",EDGE,"E1836"),sQuery(id+"F0.wireOp",EDGE,"E1837"),sQuery(id+"F0.wireOp",EDGE,"E1838"),sQuery(id+"F0.wireOp",EDGE,"E1839"),sQuery(id+"F0.wireOp",EDGE,"E1840"),sQuery(id+"F0.wireOp",EDGE,"E1841"),sQuery(id+"F0.wireOp",EDGE,"E1842"),sQuery(id+"F0.wireOp",EDGE,"E1843"),sQuery(id+"F0.wireOp",EDGE,"E1844"),sQuery(id+"F0.wireOp",EDGE,"E1845"),sQuery(id+"F0.wireOp",EDGE,"E1846"),sQuery(id+"F0.wireOp",EDGE,"E1847"),sQuery(id+"F0.wireOp",EDGE,"E1848"),sQuery(id+"F0.wireOp",EDGE,"E1849"),sQuery(id+"F0.wireOp",EDGE,"E1850"),sQuery(id+"F0.wireOp",EDGE,"E1851"),sQuery(id+"F0.wireOp",EDGE,"E1852"),sQuery(id+"F0.wireOp",EDGE,"E1853"),sQuery(id+"F0.wireOp",EDGE,"E1854"),sQuery(id+"F0.wireOp",EDGE,"E1855"),sQuery(id+"F0.wireOp",EDGE,"E1856"),sQuery(id+"F0.wireOp",EDGE,"E1857"),sQuery(id+"F0.wireOp",EDGE,"E1858"),sQuery(id+"F0.wireOp",EDGE,"E1859"),sQuery(id+"F0.wireOp",EDGE,"E1860"),sQuery(id+"F0.wireOp",EDGE,"E1861"),sQuery(id+"F0.wireOp",EDGE,"E1862"),sQuery(id+"F0.wireOp",EDGE,"E1863"),sQuery(id+"F0.wireOp",EDGE,"E1864"),sQuery(id+"F0.wireOp",EDGE,"E1865"),sQuery(id+"F0.wireOp",EDGE,"E1866"),sQuery(id+"F0.wireOp",EDGE,"E1867"),sQuery(id+"F0.wireOp",EDGE,"E1868"),sQuery(id+"F0.wireOp",EDGE,"E1869"),sQuery(id+"F0.wireOp",EDGE,"E1870"),sQuery(id+"F0.wireOp",EDGE,"E1871"),sQuery(id+"F0.wireOp",EDGE,"E1872"),sQuery(id+"F0.wireOp",EDGE,"E1873"),sQuery(id+"F0.wireOp",EDGE,"E1874"),sQuery(id+"F0.wireOp",EDGE,"E1875"),sQuery(id+"F0.wireOp",EDGE,"E1876"),sQuery(id+"F0.wireOp",EDGE,"E1877"),sQuery(id+"F0.wireOp",EDGE,"E1878"),sQuery(id+"F0.wireOp",EDGE,"E1879"),sQuery(id+"F0.wireOp",EDGE,"E1880"),sQuery(id+"F0.wireOp",EDGE,"E1881"),sQuery(id+"F0.wireOp",EDGE,"E1882"),sQuery(id+"F0.wireOp",EDGE,"E1883"),sQuery(id+"F0.wireOp",EDGE,"E1884"),sQuery(id+"F0.wireOp",EDGE,"E1885"),sQuery(id+"F0.wireOp",EDGE,"E1886"),sQuery(id+"F0.wireOp",EDGE,"E1887"),sQuery(id+"F0.wireOp",EDGE,"E1888"),sQuery(id+"F0.wireOp",EDGE,"E1889"),sQuery(id+"F0.wireOp",EDGE,"E1890"),sQuery(id+"F0.wireOp",EDGE,"E1891"),sQuery(id+"F0.wireOp",EDGE,"E1892"),sQuery(id+"F0.wireOp",EDGE,"E1893"),sQuery(id+"F0.wireOp",EDGE,"E1894"),sQuery(id+"F0.wireOp",EDGE,"E1895"),sQuery(id+"F0.wireOp",EDGE,"E1896"),sQuery(id+"F0.wireOp",EDGE,"E1897"),sQuery(id+"F0.wireOp",EDGE,"E1898"),sQuery(id+"F0.wireOp",EDGE,"E1899"),sQuery(id+"F0.wireOp",EDGE,"E1900"),sQuery(id+"F0.wireOp",EDGE,"E1901"),sQuery(id+"F0.wireOp",EDGE,"E1902"),sQuery(id+"F0.wireOp",EDGE,"E1903"),sQuery(id+"F0.wireOp",EDGE,"E1904"),sQuery(id+"F0.wireOp",EDGE,"E1905"),sQuery(id+"F0.wireOp",EDGE,"E1906"),sQuery(id+"F0.wireOp",EDGE,"E1907"),sQuery(id+"F0.wireOp",EDGE,"E1908"),sQuery(id+"F0.wireOp",EDGE,"E1909"),sQuery(id+"F0.wireOp",EDGE,"E1910"),sQuery(id+"F0.wireOp",EDGE,"E1911"),sQuery(id+"F0.wireOp",EDGE,"E1912"),sQuery(id+"F0.wireOp",EDGE,"E1913"),sQuery(id+"F0.wireOp",EDGE,"E1914"),sQuery(id+"F0.wireOp",EDGE,"E1915"),sQuery(id+"F0.wireOp",EDGE,"E1916"),sQuery(id+"F0.wireOp",EDGE,"E1917"),sQuery(id+"F0.wireOp",EDGE,"E1918"),sQuery(id+"F0.wireOp",EDGE,"E1919"),sQuery(id+"F0.wireOp",EDGE,"E1920"),sQuery(id+"F0.wireOp",EDGE,"E1921"),sQuery(id+"F0.wireOp",EDGE,"E1922"),sQuery(id+"F0.wireOp",EDGE,"E1923"),sQuery(id+"F0.wireOp",EDGE,"E1924"),sQuery(id+"F0.wireOp",EDGE,"E1925"),sQuery(id+"F0.wireOp",EDGE,"E1926"),sQuery(id+"F0.wireOp",EDGE,"E1927"),sQuery(id+"F0.wireOp",EDGE,"E1928"),sQuery(id+"F0.wireOp",EDGE,"E1929"),sQuery(id+"F0.wireOp",EDGE,"E1930"),sQuery(id+"F0.wireOp",EDGE,"E1931"),sQuery(id+"F0.wireOp",EDGE,"E1932"),sQuery(id+"F0.wireOp",EDGE,"E1933"),sQuery(id+"F0.wireOp",EDGE,"E1934"),sQuery(id+"F0.wireOp",EDGE,"E1935"),sQuery(id+"F0.wireOp",EDGE,"E1936"),sQuery(id+"F0.wireOp",EDGE,"E1937"),sQuery(id+"F0.wireOp",EDGE,"E1938"),sQuery(id+"F0.wireOp",EDGE,"E1939"),sQuery(id+"F0.wireOp",EDGE,"E1940"),sQuery(id+"F0.wireOp",EDGE,"E1941"),sQuery(id+"F0.wireOp",EDGE,"E1942"),sQuery(id+"F0.wireOp",EDGE,"E1943"),sQuery(id+"F0.wireOp",EDGE,"E1944"),sQuery(id+"F0.wireOp",EDGE,"E1945"),sQuery(id+"F0.wireOp",EDGE,"E1946"),sQuery(id+"F0.wireOp",EDGE,"E1947"),sQuery(id+"F0.wireOp",EDGE,"E1948"),sQuery(id+"F0.wireOp",EDGE,"E1949"),sQuery(id+"F0.wireOp",EDGE,"E1950"),sQuery(id+"F0.wireOp",EDGE,"E1951"),sQuery(id+"F0.wireOp",EDGE,"E1952"),sQuery(id+"F0.wireOp",EDGE,"E1953"),sQuery(id+"F0.wireOp",EDGE,"E1954"),sQuery(id+"F0.wireOp",EDGE,"E1955"),sQuery(id+"F0.wireOp",EDGE,"E1956"),sQuery(id+"F0.wireOp",EDGE,"E1957"),sQuery(id+"F0.wireOp",EDGE,"E1958"),sQuery(id+"F0.wireOp",EDGE,"E1959"),sQuery(id+"F0.wireOp",EDGE,"E1960"),sQuery(id+"F0.wireOp",EDGE,"E1961"),sQuery(id+"F0.wireOp",EDGE,"E1962"),sQuery(id+"F0.wireOp",EDGE,"E1963"),sQuery(id+"F0.wireOp",EDGE,"E1964"),sQuery(id+"F0.wireOp",EDGE,"E1965"),sQuery(id+"F0.wireOp",EDGE,"E1966"),sQuery(id+"F0.wireOp",EDGE,"E1967"),sQuery(id+"F0.wireOp",EDGE,"E1968"),sQuery(id+"F0.wireOp",EDGE,"E1969"),sQuery(id+"F0.wireOp",EDGE,"E1970"),sQuery(id+"F0.wireOp",EDGE,"E1971"),sQuery(id+"F0.wireOp",EDGE,"E1972"),sQuery(id+"F0.wireOp",EDGE,"E1973"),sQuery(id+"F0.wireOp",EDGE,"E1974"),sQuery(id+"F0.wireOp",EDGE,"E1975"),sQuery(id+"F0.wireOp",EDGE,"E1976"),sQuery(id+"F0.wireOp",EDGE,"E1977"),sQuery(id+"F0.wireOp",EDGE,"E1978"),sQuery(id+"F0.wireOp",EDGE,"E1979"),sQuery(id+"F0.wireOp",EDGE,"E1980"),sQuery(id+"F0.wireOp",EDGE,"E1981"),sQuery(id+"F0.wireOp",EDGE,"E1982"),sQuery(id+"F0.wireOp",EDGE,"E1983"),sQuery(id+"F0.wireOp",EDGE,"E1984"),sQuery(id+"F0.wireOp",EDGE,"E1985"),sQuery(id+"F0.wireOp",EDGE,"E1986"),sQuery(id+"F0.wireOp",EDGE,"E1987"),sQuery(id+"F0.wireOp",EDGE,"E1988"),sQuery(id+"F0.wireOp",EDGE,"E1989"),sQuery(id+"F0.wireOp",EDGE,"E1990"),sQuery(id+"F0.wireOp",EDGE,"E1991"),sQuery(id+"F0.wireOp",EDGE,"E1992"),sQuery(id+"F0.wireOp",EDGE,"E1993"),sQuery(id+"F0.wireOp",EDGE,"E1994"),sQuery(id+"F0.wireOp",EDGE,"E1995"),sQuery(id+"F0.wireOp",EDGE,"E1996"),sQuery(id+"F0.wireOp",EDGE,"E1997"),sQuery(id+"F0.wireOp",EDGE,"E1998"),sQuery(id+"F0.wireOp",EDGE,"E1999"),sQuery(id+"F0.wireOp",EDGE,"E2000"),sQuery(id+"F0.wireOp",EDGE,"E2001"),sQuery(id+"F0.wireOp",EDGE,"E2002"),sQuery(id+"F0.wireOp",EDGE,"E2003"),sQuery(id+"F0.wireOp",EDGE,"E2004"),sQuery(id+"F0.wireOp",EDGE,"E2005"),sQuery(id+"F0.wireOp",EDGE,"E2006"),sQuery(id+"F0.wireOp",EDGE,"E2007"),sQuery(id+"F0.wireOp",EDGE,"E2008"),sQuery(id+"F0.wireOp",EDGE,"E2009"),sQuery(id+"F0.wireOp",EDGE,"E2010"),sQuery(id+"F0.wireOp",EDGE,"E2011"),sQuery(id+"F0.wireOp",EDGE,"E2012"),sQuery(id+"F0.wireOp",EDGE,"E2013"),sQuery(id+"F0.wireOp",EDGE,"E2014"),sQuery(id+"F0.wireOp",EDGE,"E2015"),sQuery(id+"F0.wireOp",EDGE,"E2016"),sQuery(id+"F0.wireOp",EDGE,"E2017"),sQuery(id+"F0.wireOp",EDGE,"E2018"),sQuery(id+"F0.wireOp",EDGE,"E2019"),sQuery(id+"F0.wireOp",EDGE,"E2020"),sQuery(id+"F0.wireOp",EDGE,"E2021"),sQuery(id+"F0.wireOp",EDGE,"E2022"),sQuery(id+"F0.wireOp",EDGE,"E2023"),sQuery(id+"F0.wireOp",EDGE,"E2024"),sQuery(id+"F0.wireOp",EDGE,"E2025"),sQuery(id+"F0.wireOp",EDGE,"E2026"),sQuery(id+"F0.wireOp",EDGE,"E2027"),sQuery(id+"F0.wireOp",EDGE,"E2028"),sQuery(id+"F0.wireOp",EDGE,"E2029"),sQuery(id+"F0.wireOp",EDGE,"E2030"),sQuery(id+"F0.wireOp",EDGE,"E2031"),sQuery(id+"F0.wireOp",EDGE,"E2032"),sQuery(id+"F0.wireOp",EDGE,"E2033"),sQuery(id+"F0.wireOp",EDGE,"E2034"),sQuery(id+"F0.wireOp",EDGE,"E2035"),sQuery(id+"F0.wireOp",EDGE,"E2036"),sQuery(id+"F0.wireOp",EDGE,"E2037"),sQuery(id+"F0.wireOp",EDGE,"E2038"),sQuery(id+"F0.wireOp",EDGE,"E2039"),sQuery(id+"F0.wireOp",EDGE,"E2040"),sQuery(id+"F0.wireOp",EDGE,"E2041"),sQuery(id+"F0.wireOp",EDGE,"E2042"),sQuery(id+"F0.wireOp",EDGE,"E2043"),sQuery(id+"F0.wireOp",EDGE,"E2044"),sQuery(id+"F0.wireOp",EDGE,"E2045"),sQuery(id+"F0.wireOp",EDGE,"E2046"),sQuery(id+"F0.wireOp",EDGE,"E2047"),sQuery(id+"F0.wireOp",EDGE,"E2048"),sQuery(id+"F0.wireOp",EDGE,"E2049"),sQuery(id+"F0.wireOp",EDGE,"E2050"),sQuery(id+"F0.wireOp",EDGE,"E2051"),sQuery(id+"F0.wireOp",EDGE,"E2052"),sQuery(id+"F0.wireOp",EDGE,"E2053"),sQuery(id+"F0.wireOp",EDGE,"E2054"),sQuery(id+"F0.wireOp",EDGE,"E2055"),sQuery(id+"F0.wireOp",EDGE,"E2056"),sQuery(id+"F0.wireOp",EDGE,"E2057"),sQuery(id+"F0.wireOp",EDGE,"E2058"),sQuery(id+"F0.wireOp",EDGE,"E2059"),sQuery(id+"F0.wireOp",EDGE,"E2060"),sQuery(id+"F0.wireOp",EDGE,"E2061"),sQuery(id+"F0.wireOp",EDGE,"E2062"),sQuery(id+"F0.wireOp",EDGE,"E2063"),sQuery(id+"F0.wireOp",EDGE,"E2064"),sQuery(id+"F0.wireOp",EDGE,"E2065"),sQuery(id+"F0.wireOp",EDGE,"E2066"),sQuery(id+"F0.wireOp",EDGE,"E2067"),sQuery(id+"F0.wireOp",EDGE,"E2068"),sQuery(id+"F0.wireOp",EDGE,"E2069"),sQuery(id+"F0.wireOp",EDGE,"E2070"),sQuery(id+"F0.wireOp",EDGE,"E2071"),sQuery(id+"F0.wireOp",EDGE,"E2072"),sQuery(id+"F0.wireOp",EDGE,"E2073"),sQuery(id+"F0.wireOp",EDGE,"E2074"),sQuery(id+"F0.wireOp",EDGE,"E2075"),sQuery(id+"F0.wireOp",EDGE,"E2076"),sQuery(id+"F0.wireOp",EDGE,"E2077"),sQuery(id+"F0.wireOp",EDGE,"E2078"),sQuery(id+"F0.wireOp",EDGE,"E2079"),sQuery(id+"F0.wireOp",EDGE,"E2080"),sQuery(id+"F0.wireOp",EDGE,"E2081"),sQuery(id+"F0.wireOp",EDGE,"E2082"),sQuery(id+"F0.wireOp",EDGE,"E2083"),sQuery(id+"F0.wireOp",EDGE,"E2084"),sQuery(id+"F0.wireOp",EDGE,"E2085"),sQuery(id+"F0.wireOp",EDGE,"E2086"),sQuery(id+"F0.wireOp",EDGE,"E2087"),sQuery(id+"F0.wireOp",EDGE,"E2088"),sQuery(id+"F0.wireOp",EDGE,"E2089"),sQuery(id+"F0.wireOp",EDGE,"E2090"),sQuery(id+"F0.wireOp",EDGE,"E2091"),sQuery(id+"F0.wireOp",EDGE,"E2092"),sQuery(id+"F0.wireOp",EDGE,"E2093"),sQuery(id+"F0.wireOp",EDGE,"E2094"),sQuery(id+"F0.wireOp",EDGE,"E2095"),sQuery(id+"F0.wireOp",EDGE,"E2096"),sQuery(id+"F0.wireOp",EDGE,"E2097"),sQuery(id+"F0.wireOp",EDGE,"E2098"),sQuery(id+"F0.wireOp",EDGE,"E2099"),sQuery(id+"F0.wireOp",EDGE,"E2100"),sQuery(id+"F0.wireOp",EDGE,"E2101"),sQuery(id+"F0.wireOp",EDGE,"E2102"),sQuery(id+"F0.wireOp",EDGE,"E2103"),sQuery(id+"F0.wireOp",EDGE,"E2104"),sQuery(id+"F0.wireOp",EDGE,"E2105"),sQuery(id+"F0.wireOp",EDGE,"E2106"),sQuery(id+"F0.wireOp",EDGE,"E2107"),sQuery(id+"F0.wireOp",EDGE,"E2108"),sQuery(id+"F0.wireOp",EDGE,"E2109"),sQuery(id+"F0.wireOp",EDGE,"E2110"),sQuery(id+"F0.wireOp",EDGE,"E2111"),sQuery(id+"F0.wireOp",EDGE,"E2112"),sQuery(id+"F0.wireOp",EDGE,"E2113"),sQuery(id+"F0.wireOp",EDGE,"E2114"),sQuery(id+"F0.wireOp",EDGE,"E2115"),sQuery(id+"F0.wireOp",EDGE,"E2116"),sQuery(id+"F0.wireOp",EDGE,"E2117"),sQuery(id+"F0.wireOp",EDGE,"E2118"),sQuery(id+"F0.wireOp",EDGE,"E2119"),sQuery(id+"F0.wireOp",EDGE,"E2120"),sQuery(id+"F0.wireOp",EDGE,"E2121"),sQuery(id+"F0.wireOp",EDGE,"E2122"),sQuery(id+"F0.wireOp",EDGE,"E2123"),sQuery(id+"F0.wireOp",EDGE,"E2124"),sQuery(id+"F0.wireOp",EDGE,"E2125"),sQuery(id+"F0.wireOp",EDGE,"E2126"),sQuery(id+"F0.wireOp",EDGE,"E2127"),sQuery(id+"F0.wireOp",EDGE,"E2128"),sQuery(id+"F0.wireOp",EDGE,"E2129"),sQuery(id+"F0.wireOp",EDGE,"E2130"),sQuery(id+"F0.wireOp",EDGE,"E2131"),sQuery(id+"F0.wireOp",EDGE,"E2132"),sQuery(id+"F0.wireOp",EDGE,"E2133"),sQuery(id+"F0.wireOp",EDGE,"E2134"),sQuery(id+"F0.wireOp",EDGE,"E2135"),sQuery(id+"F0.wireOp",EDGE,"E2136"),sQuery(id+"F0.wireOp",EDGE,"E2137"),sQuery(id+"F0.wireOp",EDGE,"E2138"),sQuery(id+"F0.wireOp",EDGE,"E2139"),sQuery(id+"F0.wireOp",EDGE,"E2140"),sQuery(id+"F0.wireOp",EDGE,"E2141"),sQuery(id+"F0.wireOp",EDGE,"E2142"),sQuery(id+"F0.wireOp",EDGE,"E2143"),sQuery(id+"F0.wireOp",EDGE,"E2144"),sQuery(id+"F0.wireOp",EDGE,"E2145"),sQuery(id+"F0.wireOp",EDGE,"E2146"),sQuery(id+"F0.wireOp",EDGE,"E2147"),sQuery(id+"F0.wireOp",EDGE,"E2148"),sQuery(id+"F0.wireOp",EDGE,"E2149"),sQuery(id+"F0.wireOp",EDGE,"E2150"),sQuery(id+"F0.wireOp",EDGE,"E2151"),sQuery(id+"F0.wireOp",EDGE,"E2152"),sQuery(id+"F0.wireOp",EDGE,"E2153"),sQuery(id+"F0.wireOp",EDGE,"E2154"),sQuery(id+"F0.wireOp",EDGE,"E2155"),sQuery(id+"F0.wireOp",EDGE,"E2156"),sQuery(id+"F0.wireOp",EDGE,"E2157"),sQuery(id+"F0.wireOp",EDGE,"E2158"),sQuery(id+"F0.wireOp",EDGE,"E2159"),sQuery(id+"F0.wireOp",EDGE,"E2160"),sQuery(id+"F0.wireOp",EDGE,"E2161"),sQuery(id+"F0.wireOp",EDGE,"E2162"),sQuery(id+"F0.wireOp",EDGE,"E2163"),sQuery(id+"F0.wireOp",EDGE,"E2164"),sQuery(id+"F0.wireOp",EDGE,"E2165"),sQuery(id+"F0.wireOp",EDGE,"E2166"),sQuery(id+"F0.wireOp",EDGE,"E2167"),sQuery(id+"F0.wireOp",EDGE,"E2168"),sQuery(id+"F0.wireOp",EDGE,"E2169"),sQuery(id+"F0.wireOp",EDGE,"E2170"),sQuery(id+"F0.wireOp",EDGE,"E2171"),sQuery(id+"F0.wireOp",EDGE,"E2172"),sQuery(id+"F0.wireOp",EDGE,"E2173"),sQuery(id+"F0.wireOp",EDGE,"E2174"),sQuery(id+"F0.wireOp",EDGE,"E2175"),sQuery(id+"F0.wireOp",EDGE,"E2176"),sQuery(id+"F0.wireOp",EDGE,"E2177"),sQuery(id+"F0.wireOp",EDGE,"E2178"),sQuery(id+"F0.wireOp",EDGE,"E2179"),sQuery(id+"F0.wireOp",EDGE,"E2180"),sQuery(id+"F0.wireOp",EDGE,"E2181"),sQuery(id+"F0.wireOp",EDGE,"E2182"),sQuery(id+"F0.wireOp",EDGE,"E2183"),sQuery(id+"F0.wireOp",EDGE,"E2184"),sQuery(id+"F0.wireOp",EDGE,"E2185"),sQuery(id+"F0.wireOp",EDGE,"E2186"),sQuery(id+"F0.wireOp",EDGE,"E2187"),sQuery(id+"F0.wireOp",EDGE,"E2188"),sQuery(id+"F0.wireOp",EDGE,"E2189"),sQuery(id+"F0.wireOp",EDGE,"E2190"),sQuery(id+"F0.wireOp",EDGE,"E2191"),sQuery(id+"F0.wireOp",EDGE,"E2192"),sQuery(id+"F0.wireOp",EDGE,"E2193"),sQuery(id+"F0.wireOp",EDGE,"E2194"),sQuery(id+"F0.wireOp",EDGE,"E2195"),sQuery(id+"F0.wireOp",EDGE,"E2196"),sQuery(id+"F0.wireOp",EDGE,"E2197"),sQuery(id+"F0.wireOp",EDGE,"E2198"),sQuery(id+"F0.wireOp",EDGE,"E2199"),sQuery(id+"F0.wireOp",EDGE,"E2200"),sQuery(id+"F0.wireOp",EDGE,"E2201"),sQuery(id+"F0.wireOp",EDGE,"E2202"),sQuery(id+"F0.wireOp",EDGE,"E2203"),sQuery(id+"F0.wireOp",EDGE,"E2204"),sQuery(id+"F0.wireOp",EDGE,"E2205"),sQuery(id+"F0.wireOp",EDGE,"E2206"),sQuery(id+"F0.wireOp",EDGE,"E2207"),sQuery(id+"F0.wireOp",EDGE,"E2208"),sQuery(id+"F0.wireOp",EDGE,"E2209"),sQuery(id+"F0.wireOp",EDGE,"E2210"),sQuery(id+"F0.wireOp",EDGE,"E2211"),sQuery(id+"F0.wireOp",EDGE,"E2212"),sQuery(id+"F0.wireOp",EDGE,"E2213"),sQuery(id+"F0.wireOp",EDGE,"E2214"),sQuery(id+"F0.wireOp",EDGE,"E2215"),sQuery(id+"F0.wireOp",EDGE,"E2216"),sQuery(id+"F0.wireOp",EDGE,"E2217"),sQuery(id+"F0.wireOp",EDGE,"E2218"),sQuery(id+"F0.wireOp",EDGE,"E2219"),sQuery(id+"F0.wireOp",EDGE,"E2220"),sQuery(id+"F0.wireOp",EDGE,"E2221"),sQuery(id+"F0.wireOp",EDGE,"E2222"),sQuery(id+"F0.wireOp",EDGE,"E2223"),sQuery(id+"F0.wireOp",EDGE,"E2224"),sQuery(id+"F0.wireOp",EDGE,"E2225"),sQuery(id+"F0.wireOp",EDGE,"E2226"),sQuery(id+"F0.wireOp",EDGE,"E2227"),sQuery(id+"F0.wireOp",EDGE,"E2228"),sQuery(id+"F0.wireOp",EDGE,"E2229"),sQuery(id+"F0.wireOp",EDGE,"E2230"),sQuery(id+"F0.wireOp",EDGE,"E2231"),sQuery(id+"F0.wireOp",EDGE,"E2232"),sQuery(id+"F0.wireOp",EDGE,"E2233"),sQuery(id+"F0.wireOp",EDGE,"E2234"),sQuery(id+"F0.wireOp",EDGE,"E2235"),sQuery(id+"F0.wireOp",EDGE,"E2236"),sQuery(id+"F0.wireOp",EDGE,"E2237"),sQuery(id+"F0.wireOp",EDGE,"E2238"),sQuery(id+"F0.wireOp",EDGE,"E2239"),sQuery(id+"F0.wireOp",EDGE,"E2240"),sQuery(id+"F0.wireOp",EDGE,"E2241"),sQuery(id+"F0.wireOp",EDGE,"E2242"),sQuery(id+"F0.wireOp",EDGE,"E2243"),sQuery(id+"F0.wireOp",EDGE,"E2244"),sQuery(id+"F0.wireOp",EDGE,"E2245"),sQuery(id+"F0.wireOp",EDGE,"E2246"),sQuery(id+"F0.wireOp",EDGE,"E2247"),sQuery(id+"F0.wireOp",EDGE,"E2248"),sQuery(id+"F0.wireOp",EDGE,"E2249"),sQuery(id+"F0.wireOp",EDGE,"E2250"),sQuery(id+"F0.wireOp",EDGE,"E2251"),sQuery(id+"F0.wireOp",EDGE,"E2252"),sQuery(id+"F0.wireOp",EDGE,"E2253"),sQuery(id+"F0.wireOp",EDGE,"E2254"),sQuery(id+"F0.wireOp",EDGE,"E2255"),sQuery(id+"F0.wireOp",EDGE,"E2256"),sQuery(id+"F0.wireOp",EDGE,"E2257"),sQuery(id+"F0.wireOp",EDGE,"E2258"),sQuery(id+"F0.wireOp",EDGE,"E2259"),sQuery(id+"F0.wireOp",EDGE,"E2260"),sQuery(id+"F0.wireOp",EDGE,"E2261"),sQuery(id+"F0.wireOp",EDGE,"E2262"),sQuery(id+"F0.wireOp",EDGE,"E2263"),sQuery(id+"F0.wireOp",EDGE,"E2264"),sQuery(id+"F0.wireOp",EDGE,"E2265"),sQuery(id+"F0.wireOp",EDGE,"E2266"),sQuery(id+"F0.wireOp",EDGE,"E2267"),sQuery(id+"F0.wireOp",EDGE,"E2268"),sQuery(id+"F0.wireOp",EDGE,"E2269"),sQuery(id+"F0.wireOp",EDGE,"E2270"),sQuery(id+"F0.wireOp",EDGE,"E2271"),sQuery(id+"F0.wireOp",EDGE,"E2272"),sQuery(id+"F0.wireOp",EDGE,"E2273"),sQuery(id+"F0.wireOp",EDGE,"E2274"),sQuery(id+"F0.wireOp",EDGE,"E2275"),sQuery(id+"F0.wireOp",EDGE,"E2276"),sQuery(id+"F0.wireOp",EDGE,"E2277"),sQuery(id+"F0.wireOp",EDGE,"E2278"),sQuery(id+"F0.wireOp",EDGE,"E2279"),sQuery(id+"F0.wireOp",EDGE,"E2280"),sQuery(id+"F0.wireOp",EDGE,"E2281"),sQuery(id+"F0.wireOp",EDGE,"E2282"),sQuery(id+"F0.wireOp",EDGE,"E2283"),sQuery(id+"F0.wireOp",EDGE,"E2284"),sQuery(id+"F0.wireOp",EDGE,"E2285"),sQuery(id+"F0.wireOp",EDGE,"E2286"),sQuery(id+"F0.wireOp",EDGE,"E2287"),sQuery(id+"F0.wireOp",EDGE,"E2288"),sQuery(id+"F0.wireOp",EDGE,"E2289"),sQuery(id+"F0.wireOp",EDGE,"E2290"),sQuery(id+"F0.wireOp",EDGE,"E2291"),sQuery(id+"F0.wireOp",EDGE,"E2292"),sQuery(id+"F0.wireOp",EDGE,"E2293"),sQuery(id+"F0.wireOp",EDGE,"E2294"),sQuery(id+"F0.wireOp",EDGE,"E2295"),sQuery(id+"F0.wireOp",EDGE,"E2296"),sQuery(id+"F0.wireOp",EDGE,"E2297"),sQuery(id+"F0.wireOp",EDGE,"E2298"),sQuery(id+"F0.wireOp",EDGE,"E2299"),sQuery(id+"F0.wireOp",EDGE,"E2300"),sQuery(id+"F0.wireOp",EDGE,"E2301"),sQuery(id+"F0.wireOp",EDGE,"E2302"),sQuery(id+"F0.wireOp",EDGE,"E2303"),sQuery(id+"F0.wireOp",EDGE,"E2304"),sQuery(id+"F0.wireOp",EDGE,"E2305"),sQuery(id+"F0.wireOp",EDGE,"E2306"),sQuery(id+"F0.wireOp",EDGE,"E2307"),sQuery(id+"F0.wireOp",EDGE,"E2308"),sQuery(id+"F0.wireOp",EDGE,"E2309"),sQuery(id+"F0.wireOp",EDGE,"E2310"),sQuery(id+"F0.wireOp",EDGE,"E2311"),sQuery(id+"F0.wireOp",EDGE,"E2312"),sQuery(id+"F0.wireOp",EDGE,"E2313"),sQuery(id+"F0.wireOp",EDGE,"E2314"),sQuery(id+"F0.wireOp",EDGE,"E2315"),sQuery(id+"F0.wireOp",EDGE,"E2316"),sQuery(id+"F0.wireOp",EDGE,"E2317"),sQuery(id+"F0.wireOp",EDGE,"E2318"),sQuery(id+"F0.wireOp",EDGE,"E2319"),sQuery(id+"F0.wireOp",EDGE,"E2320"),sQuery(id+"F0.wireOp",EDGE,"E2321"),sQuery(id+"F0.wireOp",EDGE,"E2322"),sQuery(id+"F0.wireOp",EDGE,"E2323"),sQuery(id+"F0.wireOp",EDGE,"E2324"),sQuery(id+"F0.wireOp",EDGE,"E2325"),sQuery(id+"F0.wireOp",EDGE,"E2326"),sQuery(id+"F0.wireOp",EDGE,"E2327"),sQuery(id+"F0.wireOp",EDGE,"E2328"),sQuery(id+"F0.wireOp",EDGE,"E2329"),sQuery(id+"F0.wireOp",EDGE,"E2330"),sQuery(id+"F0.wireOp",EDGE,"E2331"),sQuery(id+"F0.wireOp",EDGE,"E2332"),sQuery(id+"F0.wireOp",EDGE,"E2333"),sQuery(id+"F0.wireOp",EDGE,"E2334"),sQuery(id+"F0.wireOp",EDGE,"E2335"),sQuery(id+"F0.wireOp",EDGE,"E2336"),sQuery(id+"F0.wireOp",EDGE,"E2337"),sQuery(id+"F0.wireOp",EDGE,"E2338"),sQuery(id+"F0.wireOp",EDGE,"E2339"),sQuery(id+"F0.wireOp",EDGE,"E2340"),sQuery(id+"F0.wireOp",EDGE,"E2341"),sQuery(id+"F0.wireOp",EDGE,"E2342"),sQuery(id+"F0.wireOp",EDGE,"E2343"),sQuery(id+"F0.wireOp",EDGE,"E2344"),sQuery(id+"F0.wireOp",EDGE,"E2345"),sQuery(id+"F0.wireOp",EDGE,"E2346"),sQuery(id+"F0.wireOp",EDGE,"E2347"),sQuery(id+"F0.wireOp",EDGE,"E2348"),sQuery(id+"F0.wireOp",EDGE,"E2349"),sQuery(id+"F0.wireOp",EDGE,"E2350"),sQuery(id+"F0.wireOp",EDGE,"E2351"),sQuery(id+"F0.wireOp",EDGE,"E2352"),sQuery(id+"F0.wireOp",EDGE,"E2353"),sQuery(id+"F0.wireOp",EDGE,"E2354"),sQuery(id+"F0.wireOp",EDGE,"E2355"),sQuery(id+"F0.wireOp",EDGE,"E2356"),sQuery(id+"F0.wireOp",EDGE,"E2357"),sQuery(id+"F0.wireOp",EDGE,"E2358"),sQuery(id+"F0.wireOp",EDGE,"E2359"),sQuery(id+"F0.wireOp",EDGE,"E2360"),sQuery(id+"F0.wireOp",EDGE,"E2361"),sQuery(id+"F0.wireOp",EDGE,"E2362"),sQuery(id+"F0.wireOp",EDGE,"E2363"),sQuery(id+"F0.wireOp",EDGE,"E2364"),sQuery(id+"F0.wireOp",EDGE,"E2365"),sQuery(id+"F0.wireOp",EDGE,"E2366"),sQuery(id+"F0.wireOp",EDGE,"E2367"),sQuery(id+"F0.wireOp",EDGE,"E2368"),sQuery(id+"F0.wireOp",EDGE,"E2369"),sQuery(id+"F0.wireOp",EDGE,"E2370"),sQuery(id+"F0.wireOp",EDGE,"E2371"),sQuery(id+"F0.wireOp",EDGE,"E2372"),sQuery(id+"F0.wireOp",EDGE,"E2373"),sQuery(id+"F0.wireOp",EDGE,"E2374"),sQuery(id+"F0.wireOp",EDGE,"E2375"),sQuery(id+"F0.wireOp",EDGE,"E2376"),sQuery(id+"F0.wireOp",EDGE,"E2377"),sQuery(id+"F0.wireOp",EDGE,"E2378"),sQuery(id+"F0.wireOp",EDGE,"E2379"),sQuery(id+"F0.wireOp",EDGE,"E2380"),sQuery(id+"F0.wireOp",EDGE,"E2381"),sQuery(id+"F0.wireOp",EDGE,"E2382"),sQuery(id+"F0.wireOp",EDGE,"E2383"),sQuery(id+"F0.wireOp",EDGE,"E2384"),sQuery(id+"F0.wireOp",EDGE,"E2385"),sQuery(id+"F0.wireOp",EDGE,"E2386"),sQuery(id+"F0.wireOp",EDGE,"E2387"),sQuery(id+"F0.wireOp",EDGE,"E2388"),sQuery(id+"F0.wireOp",EDGE,"E2389"),sQuery(id+"F0.wireOp",EDGE,"E2390"),sQuery(id+"F0.wireOp",EDGE,"E2391"),sQuery(id+"F0.wireOp",EDGE,"E2392"),sQuery(id+"F0.wireOp",EDGE,"E2393"),sQuery(id+"F0.wireOp",EDGE,"E2394"),sQuery(id+"F0.wireOp",EDGE,"E2395"),sQuery(id+"F0.wireOp",EDGE,"E2396"),sQuery(id+"F0.wireOp",EDGE,"E2397"),sQuery(id+"F0.wireOp",EDGE,"E2398"),sQuery(id+"F0.wireOp",EDGE,"E2399"),sQuery(id+"F0.wireOp",EDGE,"E2400"),sQuery(id+"F0.wireOp",EDGE,"E2401"),sQuery(id+"F0.wireOp",EDGE,"E2402"),sQuery(id+"F0.wireOp",EDGE,"E2403"),sQuery(id+"F0.wireOp",EDGE,"E2404"),sQuery(id+"F0.wireOp",EDGE,"E2405"),sQuery(id+"F0.wireOp",EDGE,"E2406"),sQuery(id+"F0.wireOp",EDGE,"E2407"),sQuery(id+"F0.wireOp",EDGE,"E2408"),sQuery(id+"F0.wireOp",EDGE,"E2409"),sQuery(id+"F0.wireOp",EDGE,"E2410"),sQuery(id+"F0.wireOp",EDGE,"E2411"),sQuery(id+"F0.wireOp",EDGE,"E2412"),sQuery(id+"F0.wireOp",EDGE,"E2413"),sQuery(id+"F0.wireOp",EDGE,"E2414"),sQuery(id+"F0.wireOp",EDGE,"E2415"),sQuery(id+"F0.wireOp",EDGE,"E2416"),sQuery(id+"F0.wireOp",EDGE,"E2417"),sQuery(id+"F0.wireOp",EDGE,"E2418"),sQuery(id+"F0.wireOp",EDGE,"E2419"),sQuery(id+"F0.wireOp",EDGE,"E2420"),sQuery(id+"F0.wireOp",EDGE,"E2421"),sQuery(id+"F0.wireOp",EDGE,"E2422"),sQuery(id+"F0.wireOp",EDGE,"E2423"),sQuery(id+"F0.wireOp",EDGE,"E2424"),sQuery(id+"F0.wireOp",EDGE,"E2425"),sQuery(id+"F0.wireOp",EDGE,"E2426"),sQuery(id+"F0.wireOp",EDGE,"E2427"),sQuery(id+"F0.wireOp",EDGE,"E2428"),sQuery(id+"F0.wireOp",EDGE,"E2429"),sQuery(id+"F0.wireOp",EDGE,"E2430"),sQuery(id+"F0.wireOp",EDGE,"E2431"),sQuery(id+"F0.wireOp",EDGE,"E2432"),sQuery(id+"F0.wireOp",EDGE,"E2433"),sQuery(id+"F0.wireOp",EDGE,"E2434"),sQuery(id+"F0.wireOp",EDGE,"E2435"),sQuery(id+"F0.wireOp",EDGE,"E2436"),sQuery(id+"F0.wireOp",EDGE,"E2437"),sQuery(id+"F0.wireOp",EDGE,"E2438"),sQuery(id+"F0.wireOp",EDGE,"E2439"),sQuery(id+"F0.wireOp",EDGE,"E2440"),sQuery(id+"F0.wireOp",EDGE,"E2441"),sQuery(id+"F0.wireOp",EDGE,"E2442"),sQuery(id+"F0.wireOp",EDGE,"E2443"),sQuery(id+"F0.wireOp",EDGE,"E2444"),sQuery(id+"F0.wireOp",EDGE,"E2445"),sQuery(id+"F0.wireOp",EDGE,"E2446"),sQuery(id+"F0.wireOp",EDGE,"E2447"),sQuery(id+"F0.wireOp",EDGE,"E2448"),sQuery(id+"F0.wireOp",EDGE,"E2449"),sQuery(id+"F0.wireOp",EDGE,"E2450"),sQuery(id+"F0.wireOp",EDGE,"E2451"),sQuery(id+"F0.wireOp",EDGE,"E2452"),sQuery(id+"F0.wireOp",EDGE,"E2453"),sQuery(id+"F0.wireOp",EDGE,"E2454"),sQuery(id+"F0.wireOp",EDGE,"E2455"),sQuery(id+"F0.wireOp",EDGE,"E2456"),sQuery(id+"F0.wireOp",EDGE,"E2457"),sQuery(id+"F0.wireOp",EDGE,"E2458"),sQuery(id+"F0.wireOp",EDGE,"E2459"),sQuery(id+"F0.wireOp",EDGE,"E2460"),sQuery(id+"F0.wireOp",EDGE,"E2461"),sQuery(id+"F0.wireOp",EDGE,"E2462"),sQuery(id+"F0.wireOp",EDGE,"E2463"),sQuery(id+"F0.wireOp",EDGE,"E2464"),sQuery(id+"F0.wireOp",EDGE,"E2465"),sQuery(id+"F0.wireOp",EDGE,"E2466"),sQuery(id+"F0.wireOp",EDGE,"E2467"),sQuery(id+"F0.wireOp",EDGE,"E2468"),sQuery(id+"F0.wireOp",EDGE,"E2469"),sQuery(id+"F0.wireOp",EDGE,"E2470"),sQuery(id+"F0.wireOp",EDGE,"E2471"),sQuery(id+"F0.wireOp",EDGE,"E2472"),sQuery(id+"F0.wireOp",EDGE,"E2473"),sQuery(id+"F0.wireOp",EDGE,"E2474"),sQuery(id+"F0.wireOp",EDGE,"E2475"),sQuery(id+"F0.wireOp",EDGE,"E2476"),sQuery(id+"F0.wireOp",EDGE,"E2477"),sQuery(id+"F0.wireOp",EDGE,"E2478"),sQuery(id+"F0.wireOp",EDGE,"E2479"),sQuery(id+"F0.wireOp",EDGE,"E2480"),sQuery(id+"F0.wireOp",EDGE,"E2481"),sQuery(id+"F0.wireOp",EDGE,"E2482"),sQuery(id+"F0.wireOp",EDGE,"E2483"),sQuery(id+"F0.wireOp",EDGE,"E2484"),sQuery(id+"F0.wireOp",EDGE,"E2485"),sQuery(id+"F0.wireOp",EDGE,"E2486"),sQuery(id+"F0.wireOp",EDGE,"E2487"),sQuery(id+"F0.wireOp",EDGE,"E2488"),sQuery(id+"F0.wireOp",EDGE,"E2489"),sQuery(id+"F0.wireOp",EDGE,"E2490"),sQuery(id+"F0.wireOp",EDGE,"E2491"),sQuery(id+"F0.wireOp",EDGE,"E2492"),sQuery(id+"F0.wireOp",EDGE,"E2493"),sQuery(id+"F0.wireOp",EDGE,"E2494"),sQuery(id+"F0.wireOp",EDGE,"E2495"),sQuery(id+"F0.wireOp",EDGE,"E2496"),sQuery(id+"F0.wireOp",EDGE,"E2497"),sQuery(id+"F0.wireOp",EDGE,"E2498"),sQuery(id+"F0.wireOp",EDGE,"E2499"),sQuery(id+"F0.wireOp",EDGE,"E2500"),sQuery(id+"F0.wireOp",EDGE,"E2501"),sQuery(id+"F0.wireOp",EDGE,"E2502"),sQuery(id+"F0.wireOp",EDGE,"E2503"),sQuery(id+"F0.wireOp",EDGE,"E2504"),sQuery(id+"F0.wireOp",EDGE,"E2505"),sQuery(id+"F0.wireOp",EDGE,"E2506"),sQuery(id+"F0.wireOp",EDGE,"E2507"),sQuery(id+"F0.wireOp",EDGE,"E2508"),sQuery(id+"F0.wireOp",EDGE,"E2509"),sQuery(id+"F0.wireOp",EDGE,"E2510"),sQuery(id+"F0.wireOp",EDGE,"E2511"),sQuery(id+"F0.wireOp",EDGE,"E2512"),sQuery(id+"F0.wireOp",EDGE,"E2513"),sQuery(id+"F0.wireOp",EDGE,"E2514"),sQuery(id+"F0.wireOp",EDGE,"E2515"),sQuery(id+"F0.wireOp",EDGE,"E2516"),sQuery(id+"F0.wireOp",EDGE,"E2517"),sQuery(id+"F0.wireOp",EDGE,"E2518"),sQuery(id+"F0.wireOp",EDGE,"E2519"),sQuery(id+"F0.wireOp",EDGE,"E2520"),sQuery(id+"F0.wireOp",EDGE,"E2521"),sQuery(id+"F0.wireOp",EDGE,"E2522"),sQuery(id+"F0.wireOp",EDGE,"E2523"),sQuery(id+"F0.wireOp",EDGE,"E2524"),sQuery(id+"F0.wireOp",EDGE,"E2525"),sQuery(id+"F0.wireOp",EDGE,"E2526"),sQuery(id+"F0.wireOp",EDGE,"E2527"),sQuery(id+"F0.wireOp",EDGE,"E2528"),sQuery(id+"F0.wireOp",EDGE,"E2529"),sQuery(id+"F0.wireOp",EDGE,"E2530"),sQuery(id+"F0.wireOp",EDGE,"E2531"),sQuery(id+"F0.wireOp",EDGE,"E2532"),sQuery(id+"F0.wireOp",EDGE,"E2533"),sQuery(id+"F0.wireOp",EDGE,"E2534"),sQuery(id+"F0.wireOp",EDGE,"E2535"),sQuery(id+"F0.wireOp",EDGE,"E2536"),sQuery(id+"F0.wireOp",EDGE,"E2537"),sQuery(id+"F0.wireOp",EDGE,"E2538"),sQuery(id+"F0.wireOp",EDGE,"E2539"),sQuery(id+"F0.wireOp",EDGE,"E2540"),sQuery(id+"F0.wireOp",EDGE,"E2541"),sQuery(id+"F0.wireOp",EDGE,"E2542"),sQuery(id+"F0.wireOp",EDGE,"E2543"),sQuery(id+"F0.wireOp",EDGE,"E2544"),sQuery(id+"F0.wireOp",EDGE,"E2545"),sQuery(id+"F0.wireOp",EDGE,"E2546"),sQuery(id+"F0.wireOp",EDGE,"E2547"),sQuery(id+"F0.wireOp",EDGE,"E2548"),sQuery(id+"F0.wireOp",EDGE,"E2549"),sQuery(id+"F0.wireOp",EDGE,"E2550"),sQuery(id+"F0.wireOp",EDGE,"E2551"),sQuery(id+"F0.wireOp",EDGE,"E2552"),sQuery(id+"F0.wireOp",EDGE,"E2553"),sQuery(id+"F0.wireOp",EDGE,"E2554"),sQuery(id+"F0.wireOp",EDGE,"E2555"),sQuery(id+"F0.wireOp",EDGE,"E2556"),sQuery(id+"F0.wireOp",EDGE,"E2557"),sQuery(id+"F0.wireOp",EDGE,"E2558"),sQuery(id+"F0.wireOp",EDGE,"E2559"),sQuery(id+"F0.wireOp",EDGE,"E2560"),sQuery(id+"F0.wireOp",EDGE,"E2561"),sQuery(id+"F0.wireOp",EDGE,"E2562"),sQuery(id+"F0.wireOp",EDGE,"E2563"),sQuery(id+"F0.wireOp",EDGE,"E2564"),sQuery(id+"F0.wireOp",EDGE,"E2565"),sQuery(id+"F0.wireOp",EDGE,"E2566"),sQuery(id+"F0.wireOp",EDGE,"E2567"),sQuery(id+"F0.wireOp",EDGE,"E2568"),sQuery(id+"F0.wireOp",EDGE,"E2569"),sQuery(id+"F0.wireOp",EDGE,"E2570"),sQuery(id+"F0.wireOp",EDGE,"E2571"),sQuery(id+"F0.wireOp",EDGE,"E2572"),sQuery(id+"F0.wireOp",EDGE,"E2573"),sQuery(id+"F0.wireOp",EDGE,"E2574"),sQuery(id+"F0.wireOp",EDGE,"E2575"),sQuery(id+"F0.wireOp",EDGE,"E2576"),sQuery(id+"F0.wireOp",EDGE,"E2577"),sQuery(id+"F0.wireOp",EDGE,"E2578"),sQuery(id+"F0.wireOp",EDGE,"E2579"),sQuery(id+"F0.wireOp",EDGE,"E2580"),sQuery(id+"F0.wireOp",EDGE,"E2581"),sQuery(id+"F0.wireOp",EDGE,"E2582"),sQuery(id+"F0.wireOp",EDGE,"E2583"),sQuery(id+"F0.wireOp",EDGE,"E2584"),sQuery(id+"F0.wireOp",EDGE,"E2585"),sQuery(id+"F0.wireOp",EDGE,"E2586"),sQuery(id+"F0.wireOp",EDGE,"E2587"),sQuery(id+"F0.wireOp",EDGE,"E2588"),sQuery(id+"F0.wireOp",EDGE,"E2589"),sQuery(id+"F0.wireOp",EDGE,"E2590"),sQuery(id+"F0.wireOp",EDGE,"E2591"),sQuery(id+"F0.wireOp",EDGE,"E2592"),sQuery(id+"F0.wireOp",EDGE,"E2593"),sQuery(id+"F0.wireOp",EDGE,"E2594"),sQuery(id+"F0.wireOp",EDGE,"E2595"),sQuery(id+"F0.wireOp",EDGE,"E2596"),sQuery(id+"F0.wireOp",EDGE,"E2597"),sQuery(id+"F0.wireOp",EDGE,"E2598"),sQuery(id+"F0.wireOp",EDGE,"E2599"),sQuery(id+"F0.wireOp",EDGE,"E2600"),sQuery(id+"F0.wireOp",EDGE,"E2601"),sQuery(id+"F0.wireOp",EDGE,"E2602"),sQuery(id+"F0.wireOp",EDGE,"E2603"),sQuery(id+"F0.wireOp",EDGE,"E2604"),sQuery(id+"F0.wireOp",EDGE,"E2605"),sQuery(id+"F0.wireOp",EDGE,"E2606"),sQuery(id+"F0.wireOp",EDGE,"E2607"),sQuery(id+"F0.wireOp",EDGE,"E2608"),sQuery(id+"F0.wireOp",EDGE,"E2609"),sQuery(id+"F0.wireOp",EDGE,"E2610"),sQuery(id+"F0.wireOp",EDGE,"E2611"),sQuery(id+"F0.wireOp",EDGE,"E2612"),sQuery(id+"F0.wireOp",EDGE,"E2613"),sQuery(id+"F0.wireOp",EDGE,"E2614"),sQuery(id+"F0.wireOp",EDGE,"E2615"),sQuery(id+"F0.wireOp",EDGE,"E2616"),sQuery(id+"F0.wireOp",EDGE,"E2617"),sQuery(id+"F0.wireOp",EDGE,"E2618"),sQuery(id+"F0.wireOp",EDGE,"E2619"),sQuery(id+"F0.wireOp",EDGE,"E2620"),sQuery(id+"F0.wireOp",EDGE,"E2621"),sQuery(id+"F0.wireOp",EDGE,"E2622"),sQuery(id+"F0.wireOp",EDGE,"E2623"),sQuery(id+"F0.wireOp",EDGE,"E2624"),sQuery(id+"F0.wireOp",EDGE,"E2625"),sQuery(id+"F0.wireOp",EDGE,"E2626"),sQuery(id+"F0.wireOp",EDGE,"E2627"),sQuery(id+"F0.wireOp",EDGE,"E2628"),sQuery(id+"F0.wireOp",EDGE,"E2629"),sQuery(id+"F0.wireOp",EDGE,"E2630"),sQuery(id+"F0.wireOp",EDGE,"E2631"),sQuery(id+"F0.wireOp",EDGE,"E2632"),sQuery(id+"F0.wireOp",EDGE,"E2633"),sQuery(id+"F0.wireOp",EDGE,"E2634"),sQuery(id+"F0.wireOp",EDGE,"E2635"),sQuery(id+"F0.wireOp",EDGE,"E2636"),sQuery(id+"F0.wireOp",EDGE,"E2637"),sQuery(id+"F0.wireOp",EDGE,"E2638"),sQuery(id+"F0.wireOp",EDGE,"E2639"),sQuery(id+"F0.wireOp",EDGE,"E2640"),sQuery(id+"F0.wireOp",EDGE,"E2641"),sQuery(id+"F0.wireOp",EDGE,"E2642"),sQuery(id+"F0.wireOp",EDGE,"E2643"),sQuery(id+"F0.wireOp",EDGE,"E2644"),sQuery(id+"F0.wireOp",EDGE,"E2645"),sQuery(id+"F0.wireOp",EDGE,"E2646"),sQuery(id+"F0.wireOp",EDGE,"E2647"),sQuery(id+"F0.wireOp",EDGE,"E2648"),sQuery(id+"F0.wireOp",EDGE,"E2649"),sQuery(id+"F0.wireOp",EDGE,"E2650"),sQuery(id+"F0.wireOp",EDGE,"E2651"),sQuery(id+"F0.wireOp",EDGE,"E2652"),sQuery(id+"F0.wireOp",EDGE,"E2653"),sQuery(id+"F0.wireOp",EDGE,"E2654"),sQuery(id+"F0.wireOp",EDGE,"E2655"),sQuery(id+"F0.wireOp",EDGE,"E2656"),sQuery(id+"F0.wireOp",EDGE,"E2657"),sQuery(id+"F0.wireOp",EDGE,"E2658"),sQuery(id+"F0.wireOp",EDGE,"E2659"),sQuery(id+"F0.wireOp",EDGE,"E2660"),sQuery(id+"F0.wireOp",EDGE,"E2661"),sQuery(id+"F0.wireOp",EDGE,"E2662"),sQuery(id+"F0.wireOp",EDGE,"E2663"),sQuery(id+"F0.wireOp",EDGE,"E2664"),sQuery(id+"F0.wireOp",EDGE,"E2665"),sQuery(id+"F0.wireOp",EDGE,"E2666"),sQuery(id+"F0.wireOp",EDGE,"E2667"),sQuery(id+"F0.wireOp",EDGE,"E2668"),sQuery(id+"F0.wireOp",EDGE,"E2669"),sQuery(id+"F0.wireOp",EDGE,"E2670"),sQuery(id+"F0.wireOp",EDGE,"E2671"),sQuery(id+"F0.wireOp",EDGE,"E2672"),sQuery(id+"F0.wireOp",EDGE,"E2673"),sQuery(id+"F0.wireOp",EDGE,"E2674"),sQuery(id+"F0.wireOp",EDGE,"E2675"),sQuery(id+"F0.wireOp",EDGE,"E2676"),sQuery(id+"F0.wireOp",EDGE,"E2677"),sQuery(id+"F0.wireOp",EDGE,"E2678"),sQuery(id+"F0.wireOp",EDGE,"E2679"),sQuery(id+"F0.wireOp",EDGE,"E2680"),sQuery(id+"F0.wireOp",EDGE,"E2681"),sQuery(id+"F0.wireOp",EDGE,"E2682"),sQuery(id+"F0.wireOp",EDGE,"E2683"),sQuery(id+"F0.wireOp",EDGE,"E2684"),sQuery(id+"F0.wireOp",EDGE,"E2685"),sQuery(id+"F0.wireOp",EDGE,"E2686"),sQuery(id+"F0.wireOp",EDGE,"E2687"),sQuery(id+"F0.wireOp",EDGE,"E2688"),sQuery(id+"F0.wireOp",EDGE,"E2689"),sQuery(id+"F0.wireOp",EDGE,"E2690"),sQuery(id+"F0.wireOp",EDGE,"E2691"),sQuery(id+"F0.wireOp",EDGE,"E2692"),sQuery(id+"F0.wireOp",EDGE,"E2693"),sQuery(id+"F0.wireOp",EDGE,"E2694"),sQuery(id+"F0.wireOp",EDGE,"E2695"),sQuery(id+"F0.wireOp",EDGE,"E2696"),sQuery(id+"F0.wireOp",EDGE,"E2697"),sQuery(id+"F0.wireOp",EDGE,"E2698"),sQuery(id+"F0.wireOp",EDGE,"E2699"),sQuery(id+"F0.wireOp",EDGE,"E2700"),sQuery(id+"F0.wireOp",EDGE,"E2701"),sQuery(id+"F0.wireOp",EDGE,"E2702"),sQuery(id+"F0.wireOp",EDGE,"E2703"),sQuery(id+"F0.wireOp",EDGE,"E2704"),sQuery(id+"F0.wireOp",EDGE,"E2705"),sQuery(id+"F0.wireOp",EDGE,"E2706"),sQuery(id+"F0.wireOp",EDGE,"E2707"),sQuery(id+"F0.wireOp",EDGE,"E2708"),sQuery(id+"F0.wireOp",EDGE,"E2709"),sQuery(id+"F0.wireOp",EDGE,"E2710"),sQuery(id+"F0.wireOp",EDGE,"E2711"),sQuery(id+"F0.wireOp",EDGE,"E2712"),sQuery(id+"F0.wireOp",EDGE,"E2713"),sQuery(id+"F0.wireOp",EDGE,"E2714"),sQuery(id+"F0.wireOp",EDGE,"E2715"),sQuery(id+"F0.wireOp",EDGE,"E2716"),sQuery(id+"F0.wireOp",EDGE,"E2717"),sQuery(id+"F0.wireOp",EDGE,"E2718"),sQuery(id+"F0.wireOp",EDGE,"E2719"),sQuery(id+"F0.wireOp",EDGE,"E2720"),sQuery(id+"F0.wireOp",EDGE,"E2721"),sQuery(id+"F0.wireOp",EDGE,"E2722"),sQuery(id+"F0.wireOp",EDGE,"E2723"),sQuery(id+"F0.wireOp",EDGE,"E2724"),sQuery(id+"F0.wireOp",EDGE,"E2725"),sQuery(id+"F0.wireOp",EDGE,"E2726"),sQuery(id+"F0.wireOp",EDGE,"E2727"),sQuery(id+"F0.wireOp",EDGE,"E2728"),sQuery(id+"F0.wireOp",EDGE,"E2729"),sQuery(id+"F0.wireOp",EDGE,"E2730"),sQuery(id+"F0.wireOp",EDGE,"E2731"),sQuery(id+"F0.wireOp",EDGE,"E2732"),sQuery(id+"F0.wireOp",EDGE,"E2733"),sQuery(id+"F0.wireOp",EDGE,"E2734"),sQuery(id+"F0.wireOp",EDGE,"E2735"),sQuery(id+"F0.wireOp",EDGE,"E2736"),sQuery(id+"F0.wireOp",EDGE,"E2737"),sQuery(id+"F0.wireOp",EDGE,"E2738"),sQuery(id+"F0.wireOp",EDGE,"E2739"),sQuery(id+"F0.wireOp",EDGE,"E2740"),sQuery(id+"F0.wireOp",EDGE,"E2741"),sQuery(id+"F0.wireOp",EDGE,"E2742"),sQuery(id+"F0.wireOp",EDGE,"E2743"),sQuery(id+"F0.wireOp",EDGE,"E2744"),sQuery(id+"F0.wireOp",EDGE,"E2745"),sQuery(id+"F0.wireOp",EDGE,"E2746"),sQuery(id+"F0.wireOp",EDGE,"E2747"),sQuery(id+"F0.wireOp",EDGE,"E2748"),sQuery(id+"F0.wireOp",EDGE,"E2749"),sQuery(id+"F0.wireOp",EDGE,"E2750"),sQuery(id+"F0.wireOp",EDGE,"E2751"),sQuery(id+"F0.wireOp",EDGE,"E2752"),sQuery(id+"F0.wireOp",EDGE,"E2753"),sQuery(id+"F0.wireOp",EDGE,"E2754"),sQuery(id+"F0.wireOp",EDGE,"E2755"),sQuery(id+"F0.wireOp",EDGE,"E2756"),sQuery(id+"F0.wireOp",EDGE,"E2757"),sQuery(id+"F0.wireOp",EDGE,"E2758"),sQuery(id+"F0.wireOp",EDGE,"E2759"),sQuery(id+"F0.wireOp",EDGE,"E2760"),sQuery(id+"F0.wireOp",EDGE,"E2761"),sQuery(id+"F0.wireOp",EDGE,"E2762"),sQuery(id+"F0.wireOp",EDGE,"E2763"),sQuery(id+"F0.wireOp",EDGE,"E2764"),sQuery(id+"F0.wireOp",EDGE,"E2765"),sQuery(id+"F0.wireOp",EDGE,"E2766"),sQuery(id+"F0.wireOp",EDGE,"E2767"),sQuery(id+"F0.wireOp",EDGE,"E2768"),sQuery(id+"F0.wireOp",EDGE,"E2769"),sQuery(id+"F0.wireOp",EDGE,"E2770"),sQuery(id+"F0.wireOp",EDGE,"E2771"),sQuery(id+"F0.wireOp",EDGE,"E2772"),sQuery(id+"F0.wireOp",EDGE,"E2773"),sQuery(id+"F0.wireOp",EDGE,"E2774"),sQuery(id+"F0.wireOp",EDGE,"E2775"),sQuery(id+"F0.wireOp",EDGE,"E2776"),sQuery(id+"F0.wireOp",EDGE,"E2777"),sQuery(id+"F0.wireOp",EDGE,"E2778"),sQuery(id+"F0.wireOp",EDGE,"E2779"),sQuery(id+"F0.wireOp",EDGE,"E2780"),sQuery(id+"F0.wireOp",EDGE,"E2781"),sQuery(id+"F0.wireOp",EDGE,"E2782"),sQuery(id+"F0.wireOp",EDGE,"E2783"),sQuery(id+"F0.wireOp",EDGE,"E2784"),sQuery(id+"F0.wireOp",EDGE,"E2785"),sQuery(id+"F0.wireOp",EDGE,"E2786"),sQuery(id+"F0.wireOp",EDGE,"E2787"),sQuery(id+"F0.wireOp",EDGE,"E2788"),sQuery(id+"F0.wireOp",EDGE,"E2789"),sQuery(id+"F0.wireOp",EDGE,"E2790"),sQuery(id+"F0.wireOp",EDGE,"E2791"),sQuery(id+"F0.wireOp",EDGE,"E2792"),sQuery(id+"F0.wireOp",EDGE,"E2793"),sQuery(id+"F0.wireOp",EDGE,"E2794"),sQuery(id+"F0.wireOp",EDGE,"E2795"),sQuery(id+"F0.wireOp",EDGE,"E2796"),sQuery(id+"F0.wireOp",EDGE,"E2797"),sQuery(id+"F0.wireOp",EDGE,"E2798"),sQuery(id+"F0.wireOp",EDGE,"E2799"),sQuery(id+"F0.wireOp",EDGE,"E2800"),sQuery(id+"F0.wireOp",EDGE,"E2801"),sQuery(id+"F0.wireOp",EDGE,"E2802"),sQuery(id+"F0.wireOp",EDGE,"E2803"),sQuery(id+"F0.wireOp",EDGE,"E2804"),sQuery(id+"F0.wireOp",EDGE,"E2805"),sQuery(id+"F0.wireOp",EDGE,"E2806"),sQuery(id+"F0.wireOp",EDGE,"E2807"),sQuery(id+"F0.wireOp",EDGE,"E2808"),sQuery(id+"F0.wireOp",EDGE,"E2809"),sQuery(id+"F0.wireOp",EDGE,"E2810"),sQuery(id+"F0.wireOp",EDGE,"E2811"),sQuery(id+"F0.wireOp",EDGE,"E2812"),sQuery(id+"F0.wireOp",EDGE,"E2813"),sQuery(id+"F0.wireOp",EDGE,"E2814"),sQuery(id+"F0.wireOp",EDGE,"E2815"),sQuery(id+"F0.wireOp",EDGE,"E2816"),sQuery(id+"F0.wireOp",EDGE,"E2817"),sQuery(id+"F0.wireOp",EDGE,"E2818"),sQuery(id+"F0.wireOp",EDGE,"E2819"),sQuery(id+"F0.wireOp",EDGE,"E2820"),sQuery(id+"F0.wireOp",EDGE,"E2821"),sQuery(id+"F0.wireOp",EDGE,"E2822"),sQuery(id+"F0.wireOp",EDGE,"E2823"),sQuery(id+"F0.wireOp",EDGE,"E2824"),sQuery(id+"F0.wireOp",EDGE,"E2825"),sQuery(id+"F0.wireOp",EDGE,"E2826"),sQuery(id+"F0.wireOp",EDGE,"E2827"),sQuery(id+"F0.wireOp",EDGE,"E2828"),sQuery(id+"F0.wireOp",EDGE,"E2829"),sQuery(id+"F0.wireOp",EDGE,"E2830"),sQuery(id+"F0.wireOp",EDGE,"E2831"),sQuery(id+"F0.wireOp",EDGE,"E2832"),sQuery(id+"F0.wireOp",EDGE,"E2833"),sQuery(id+"F0.wireOp",EDGE,"E2834"),sQuery(id+"F0.wireOp",EDGE,"E2835"),sQuery(id+"F0.wireOp",EDGE,"E2836"),sQuery(id+"F0.wireOp",EDGE,"E2837"),sQuery(id+"F0.wireOp",EDGE,"E2838"),sQuery(id+"F0.wireOp",EDGE,"E2839"),sQuery(id+"F0.wireOp",EDGE,"E2840"),sQuery(id+"F0.wireOp",EDGE,"E2841"),sQuery(id+"F0.wireOp",EDGE,"E2842"),sQuery(id+"F0.wireOp",EDGE,"E2843"),sQuery(id+"F0.wireOp",EDGE,"E2844"),sQuery(id+"F0.wireOp",EDGE,"E2845"),sQuery(id+"F0.wireOp",EDGE,"E2846"),sQuery(id+"F0.wireOp",EDGE,"E2847"),sQuery(id+"F0.wireOp",EDGE,"E2848"),sQuery(id+"F0.wireOp",EDGE,"E2849"),sQuery(id+"F0.wireOp",EDGE,"E2850"),sQuery(id+"F0.wireOp",EDGE,"E2851"),sQuery(id+"F0.wireOp",EDGE,"E2852"),sQuery(id+"F0.wireOp",EDGE,"E2853"),sQuery(id+"F0.wireOp",EDGE,"E2854"),sQuery(id+"F0.wireOp",EDGE,"E2855"),sQuery(id+"F0.wireOp",EDGE,"E2856"),sQuery(id+"F0.wireOp",EDGE,"E2857"),sQuery(id+"F0.wireOp",EDGE,"E2858"),sQuery(id+"F0.wireOp",EDGE,"E2859"),sQuery(id+"F0.wireOp",EDGE,"E2860"),sQuery(id+"F0.wireOp",EDGE,"E2861"),sQuery(id+"F0.wireOp",EDGE,"E2862"),sQuery(id+"F0.wireOp",EDGE,"E2863"),sQuery(id+"F0.wireOp",EDGE,"E2864"),sQuery(id+"F0.wireOp",EDGE,"E2865"),sQuery(id+"F0.wireOp",EDGE,"E2866"),sQuery(id+"F0.wireOp",EDGE,"E2867"),sQuery(id+"F0.wireOp",EDGE,"E2868"),sQuery(id+"F0.wireOp",EDGE,"E2869"),sQuery(id+"F0.wireOp",EDGE,"E2870"),sQuery(id+"F0.wireOp",EDGE,"E2871"),sQuery(id+"F0.wireOp",EDGE,"E2872"),sQuery(id+"F0.wireOp",EDGE,"E2873"),sQuery(id+"F0.wireOp",EDGE,"E2874"),sQuery(id+"F0.wireOp",EDGE,"E2875"),sQuery(id+"F0.wireOp",EDGE,"E2876"),sQuery(id+"F0.wireOp",EDGE,"E2877"),sQuery(id+"F0.wireOp",EDGE,"E2878"),sQuery(id+"F0.wireOp",EDGE,"E2879"),sQuery(id+"F0.wireOp",EDGE,"E2880"),sQuery(id+"F0.wireOp",EDGE,"E2881"),sQuery(id+"F0.wireOp",EDGE,"E2882"),sQuery(id+"F0.wireOp",EDGE,"E2883"),sQuery(id+"F0.wireOp",EDGE,"E2884"),sQuery(id+"F0.wireOp",EDGE,"E2885"),sQuery(id+"F0.wireOp",EDGE,"E2886"),sQuery(id+"F0.wireOp",EDGE,"E2887"),sQuery(id+"F0.wireOp",EDGE,"E2888"),sQuery(id+"F0.wireOp",EDGE,"E2889"),sQuery(id+"F0.wireOp",EDGE,"E2890"),sQuery(id+"F0.wireOp",EDGE,"E2891"),sQuery(id+"F0.wireOp",EDGE,"E2892"),sQuery(id+"F0.wireOp",EDGE,"E2893"),sQuery(id+"F0.wireOp",EDGE,"E2894"),sQuery(id+"F0.wireOp",EDGE,"E2895"),sQuery(id+"F0.wireOp",EDGE,"E2896"),sQuery(id+"F0.wireOp",EDGE,"E2897"),sQuery(id+"F0.wireOp",EDGE,"E2898"),sQuery(id+"F0.wireOp",EDGE,"E2899"),sQuery(id+"F0.wireOp",EDGE,"E2900"),sQuery(id+"F0.wireOp",EDGE,"E2901"),sQuery(id+"F0.wireOp",EDGE,"E2902"),sQuery(id+"F0.wireOp",EDGE,"E2903"),sQuery(id+"F0.wireOp",EDGE,"E2904"),sQuery(id+"F0.wireOp",EDGE,"E2905"),sQuery(id+"F0.wireOp",EDGE,"E2906"),sQuery(id+"F0.wireOp",EDGE,"E2907"),sQuery(id+"F0.wireOp",EDGE,"E2908"),sQuery(id+"F0.wireOp",EDGE,"E2909"),sQuery(id+"F0.wireOp",EDGE,"E2910"),sQuery(id+"F0.wireOp",EDGE,"E2911"),sQuery(id+"F0.wireOp",EDGE,"E2912"),sQuery(id+"F0.wireOp",EDGE,"E2913"),sQuery(id+"F0.wireOp",EDGE,"E2914"),sQuery(id+"F0.wireOp",EDGE,"E2915"),sQuery(id+"F0.wireOp",EDGE,"E2916"),sQuery(id+"F0.wireOp",EDGE,"E2917"),sQuery(id+"F0.wireOp",EDGE,"E2918"),sQuery(id+"F0.wireOp",EDGE,"E2919"),sQuery(id+"F0.wireOp",EDGE,"E2920"),sQuery(id+"F0.wireOp",EDGE,"E2921"),sQuery(id+"F0.wireOp",EDGE,"E2922"),sQuery(id+"F0.wireOp",EDGE,"E2923"),sQuery(id+"F0.wireOp",EDGE,"E2924"),sQuery(id+"F0.wireOp",EDGE,"E2925"),sQuery(id+"F0.wireOp",EDGE,"E2926"),sQuery(id+"F0.wireOp",EDGE,"E2927"),sQuery(id+"F0.wireOp",EDGE,"E2928"),sQuery(id+"F0.wireOp",EDGE,"E2929"),sQuery(id+"F0.wireOp",EDGE,"E2930"),sQuery(id+"F0.wireOp",EDGE,"E2931"),sQuery(id+"F0.wireOp",EDGE,"E2932"),sQuery(id+"F0.wireOp",EDGE,"E2933"),sQuery(id+"F0.wireOp",EDGE,"E2934"),sQuery(id+"F0.wireOp",EDGE,"E2935"),sQuery(id+"F0.wireOp",EDGE,"E2936"),sQuery(id+"F0.wireOp",EDGE,"E2937"),sQuery(id+"F0.wireOp",EDGE,"E2938"),sQuery(id+"F0.wireOp",EDGE,"E2939"),sQuery(id+"F0.wireOp",EDGE,"E2940"),sQuery(id+"F0.wireOp",EDGE,"E2941"),sQuery(id+"F0.wireOp",EDGE,"E2942"),sQuery(id+"F0.wireOp",EDGE,"E2943"),sQuery(id+"F0.wireOp",EDGE,"E2944"),sQuery(id+"F0.wireOp",EDGE,"E2945"),sQuery(id+"F0.wireOp",EDGE,"E2946"),sQuery(id+"F0.wireOp",EDGE,"E2947"),sQuery(id+"F0.wireOp",EDGE,"E2948"),sQuery(id+"F0.wireOp",EDGE,"E2949"),sQuery(id+"F0.wireOp",EDGE,"E2950"),sQuery(id+"F0.wireOp",EDGE,"E2951"),sQuery(id+"F0.wireOp",EDGE,"E2952"),sQuery(id+"F0.wireOp",EDGE,"E2953"),sQuery(id+"F0.wireOp",EDGE,"E2954"),sQuery(id+"F0.wireOp",EDGE,"E2955"),sQuery(id+"F0.wireOp",EDGE,"E2956"),sQuery(id+"F0.wireOp",EDGE,"E2957"),sQuery(id+"F0.wireOp",EDGE,"E2958"),sQuery(id+"F0.wireOp",EDGE,"E2959"),sQuery(id+"F0.wireOp",EDGE,"E2960"),sQuery(id+"F0.wireOp",EDGE,"E2961"),sQuery(id+"F0.wireOp",EDGE,"E2962"),sQuery(id+"F0.wireOp",EDGE,"E2963"),sQuery(id+"F0.wireOp",EDGE,"E2964"),sQuery(id+"F0.wireOp",EDGE,"E2965"),sQuery(id+"F0.wireOp",EDGE,"E2966"),sQuery(id+"F0.wireOp",EDGE,"E2967"),sQuery(id+"F0.wireOp",EDGE,"E2968"),sQuery(id+"F0.wireOp",EDGE,"E2969"),sQuery(id+"F0.wireOp",EDGE,"E2970"),sQuery(id+"F0.wireOp",EDGE,"E2971"),sQuery(id+"F0.wireOp",EDGE,"E2972"),sQuery(id+"F0.wireOp",EDGE,"E2973"),sQuery(id+"F0.wireOp",EDGE,"E2974"),sQuery(id+"F0.wireOp",EDGE,"E2975"),sQuery(id+"F0.wireOp",EDGE,"E2976"),sQuery(id+"F0.wireOp",EDGE,"E2977"),sQuery(id+"F0.wireOp",EDGE,"E2978"),sQuery(id+"F0.wireOp",EDGE,"E2979"),sQuery(id+"F0.wireOp",EDGE,"E2980"),sQuery(id+"F0.wireOp",EDGE,"E2981"),sQuery(id+"F0.wireOp",EDGE,"E2982"),sQuery(id+"F0.wireOp",EDGE,"E2983"),sQuery(id+"F0.wireOp",EDGE,"E2984"),sQuery(id+"F0.wireOp",EDGE,"E2985"),sQuery(id+"F0.wireOp",EDGE,"E2986"),sQuery(id+"F0.wireOp",EDGE,"E2987"),sQuery(id+"F0.wireOp",EDGE,"E2988"),sQuery(id+"F0.wireOp",EDGE,"E2989"),sQuery(id+"F0.wireOp",EDGE,"E2990"),sQuery(id+"F0.wireOp",EDGE,"E2991"),sQuery(id+"F0.wireOp",EDGE,"E2992"),sQuery(id+"F0.wireOp",EDGE,"E2993"),sQuery(id+"F0.wireOp",EDGE,"E2994"),sQuery(id+"F0.wireOp",EDGE,"E2995"),sQuery(id+"F0.wireOp",EDGE,"E2996"),sQuery(id+"F0.wireOp",EDGE,"E2997"),sQuery(id+"F0.wireOp",EDGE,"E2998"),sQuery(id+"F0.wireOp",EDGE,"E2999"),sQuery(id+"F0.wireOp",EDGE,"E3000"),sQuery(id+"F0.wireOp",EDGE,"E3001"),sQuery(id+"F0.wireOp",EDGE,"E3002"),sQuery(id+"F0.wireOp",EDGE,"E3003"),sQuery(id+"F0.wireOp",EDGE,"E3004"),sQuery(id+"F0.wireOp",EDGE,"E3005"),sQuery(id+"F0.wireOp",EDGE,"E3006"),sQuery(id+"F0.wireOp",EDGE,"E3007"),sQuery(id+"F0.wireOp",EDGE,"E3008"),sQuery(id+"F0.wireOp",EDGE,"E3009"),sQuery(id+"F0.wireOp",EDGE,"E3010"),sQuery(id+"F0.wireOp",EDGE,"E3011"),sQuery(id+"F0.wireOp",EDGE,"E3012"),sQuery(id+"F0.wireOp",EDGE,"E3013"),sQuery(id+"F0.wireOp",EDGE,"E3014"),sQuery(id+"F0.wireOp",EDGE,"E3015"),sQuery(id+"F0.wireOp",EDGE,"E3016"),sQuery(id+"F0.wireOp",EDGE,"E3017"),sQuery(id+"F0.wireOp",EDGE,"E3018"),sQuery(id+"F0.wireOp",EDGE,"E3019"),sQuery(id+"F0.wireOp",EDGE,"E3020"),sQuery(id+"F0.wireOp",EDGE,"E3021"),sQuery(id+"F0.wireOp",EDGE,"E3022"),sQuery(id+"F0.wireOp",EDGE,"E3023"),sQuery(id+"F0.wireOp",EDGE,"E3024"),sQuery(id+"F0.wireOp",EDGE,"E3025"),sQuery(id+"F0.wireOp",EDGE,"E3026"),sQuery(id+"F0.wireOp",EDGE,"E3027"),sQuery(id+"F0.wireOp",EDGE,"E3028"),sQuery(id+"F0.wireOp",EDGE,"E3029"),sQuery(id+"F0.wireOp",EDGE,"E3030"),sQuery(id+"F0.wireOp",EDGE,"E3031"),sQuery(id+"F0.wireOp",EDGE,"E3032"),sQuery(id+"F0.wireOp",EDGE,"E3033"),sQuery(id+"F0.wireOp",EDGE,"E3034"),sQuery(id+"F0.wireOp",EDGE,"E3035"),sQuery(id+"F0.wireOp",EDGE,"E3036"),sQuery(id+"F0.wireOp",EDGE,"E3037"),sQuery(id+"F0.wireOp",EDGE,"E3038"),sQuery(id+"F0.wireOp",EDGE,"E3039"),sQuery(id+"F0.wireOp",EDGE,"E3040"),sQuery(id+"F0.wireOp",EDGE,"E3041"),sQuery(id+"F0.wireOp",EDGE,"E3042"),sQuery(id+"F0.wireOp",EDGE,"E3043"),sQuery(id+"F0.wireOp",EDGE,"E3044"),sQuery(id+"F0.wireOp",EDGE,"E3045"),sQuery(id+"F0.wireOp",EDGE,"E3046"),sQuery(id+"F0.wireOp",EDGE,"E3047"),sQuery(id+"F0.wireOp",EDGE,"E3048"),sQuery(id+"F0.wireOp",EDGE,"E3049"),sQuery(id+"F0.wireOp",EDGE,"E3050"),sQuery(id+"F0.wireOp",EDGE,"E3051"),sQuery(id+"F0.wireOp",EDGE,"E3052"),sQuery(id+"F0.wireOp",EDGE,"E3053"),sQuery(id+"F0.wireOp",EDGE,"E3054"),sQuery(id+"F0.wireOp",EDGE,"E3055"),sQuery(id+"F0.wireOp",EDGE,"E3056"),sQuery(id+"F0.wireOp",EDGE,"E3057"),sQuery(id+"F0.wireOp",EDGE,"E3058"),sQuery(id+"F0.wireOp",EDGE,"E3059"),sQuery(id+"F0.wireOp",EDGE,"E3060"),sQuery(id+"F0.wireOp",EDGE,"E3061"),sQuery(id+"F0.wireOp",EDGE,"E3062"),sQuery(id+"F0.wireOp",EDGE,"E3063"),sQuery(id+"F0.wireOp",EDGE,"E3064"),sQuery(id+"F0.wireOp",EDGE,"E3065"),sQuery(id+"F0.wireOp",EDGE,"E3066"),sQuery(id+"F0.wireOp",EDGE,"E3067"),sQuery(id+"F0.wireOp",EDGE,"E3068"),sQuery(id+"F0.wireOp",EDGE,"E3069"),sQuery(id+"F0.wireOp",EDGE,"E3070"),sQuery(id+"F0.wireOp",EDGE,"E3071"),sQuery(id+"F0.wireOp",EDGE,"E3072"),sQuery(id+"F0.wireOp",EDGE,"E3073"),sQuery(id+"F0.wireOp",EDGE,"E3074"),sQuery(id+"F0.wireOp",EDGE,"E3075"),sQuery(id+"F0.wireOp",EDGE,"E3076"),sQuery(id+"F0.wireOp",EDGE,"E3077"),sQuery(id+"F0.wireOp",EDGE,"E3078"),sQuery(id+"F0.wireOp",EDGE,"E3079"),sQuery(id+"F0.wireOp",EDGE,"E3080"),sQuery(id+"F0.wireOp",EDGE,"E3081"),sQuery(id+"F0.wireOp",EDGE,"E3082"),sQuery(id+"F0.wireOp",EDGE,"E3083"),sQuery(id+"F0.wireOp",EDGE,"E3084"),sQuery(id+"F0.wireOp",EDGE,"E3085"),sQuery(id+"F0.wireOp",EDGE,"E3086"),sQuery(id+"F0.wireOp",EDGE,"E3087"),sQuery(id+"F0.wireOp",EDGE,"E3088"),sQuery(id+"F0.wireOp",EDGE,"E3089"),sQuery(id+"F0.wireOp",EDGE,"E3090"),sQuery(id+"F0.wireOp",EDGE,"E3091"),sQuery(id+"F0.wireOp",EDGE,"E3092"),sQuery(id+"F0.wireOp",EDGE,"E3093"),sQuery(id+"F0.wireOp",EDGE,"E3094"),sQuery(id+"F0.wireOp",EDGE,"E3095"),sQuery(id+"F0.wireOp",EDGE,"E3096"),sQuery(id+"F0.wireOp",EDGE,"E3097"),sQuery(id+"F0.wireOp",EDGE,"E3098"),sQuery(id+"F0.wireOp",EDGE,"E3099"),sQuery(id+"F0.wireOp",EDGE,"E3100"),sQuery(id+"F0.wireOp",EDGE,"E3101"),sQuery(id+"F0.wireOp",EDGE,"E3102"),sQuery(id+"F0.wireOp",EDGE,"E3103"),sQuery(id+"F0.wireOp",EDGE,"E3104"),sQuery(id+"F0.wireOp",EDGE,"E3105"),sQuery(id+"F0.wireOp",EDGE,"E3106"),sQuery(id+"F0.wireOp",EDGE,"E3107"),sQuery(id+"F0.wireOp",EDGE,"E3108"),sQuery(id+"F0.wireOp",EDGE,"E3109"),sQuery(id+"F0.wireOp",EDGE,"E3110"),sQuery(id+"F0.wireOp",EDGE,"E3111"),sQuery(id+"F0.wireOp",EDGE,"E3112"),sQuery(id+"F0.wireOp",EDGE,"E3113"),sQuery(id+"F0.wireOp",EDGE,"E3114"),sQuery(id+"F0.wireOp",EDGE,"E3115"),sQuery(id+"F0.wireOp",EDGE,"E3116"),sQuery(id+"F0.wireOp",EDGE,"E3117"),sQuery(id+"F0.wireOp",EDGE,"E3118"),sQuery(id+"F0.wireOp",EDGE,"E3119"),sQuery(id+"F0.wireOp",EDGE,"E3120"),sQuery(id+"F0.wireOp",EDGE,"E3121"),sQuery(id+"F0.wireOp",EDGE,"E3122"),sQuery(id+"F0.wireOp",EDGE,"E3123"),sQuery(id+"F0.wireOp",EDGE,"E3124"),sQuery(id+"F0.wireOp",EDGE,"E3125"),sQuery(id+"F0.wireOp",EDGE,"E3126"),sQuery(id+"F0.wireOp",EDGE,"E3127"),sQuery(id+"F0.wireOp",EDGE,"E3128"),sQuery(id+"F0.wireOp",EDGE,"E3129"),sQuery(id+"F0.wireOp",EDGE,"E3130"),sQuery(id+"F0.wireOp",EDGE,"E3131"),sQuery(id+"F0.wireOp",EDGE,"E3132"),sQuery(id+"F0.wireOp",EDGE,"E3133"),sQuery(id+"F0.wireOp",EDGE,"E3134"),sQuery(id+"F0.wireOp",EDGE,"E3135"),sQuery(id+"F0.wireOp",EDGE,"E3136"),sQuery(id+"F0.wireOp",EDGE,"E3137"),sQuery(id+"F0.wireOp",EDGE,"E3138"),sQuery(id+"F0.wireOp",EDGE,"E3139"),sQuery(id+"F0.wireOp",EDGE,"E3140"),sQuery(id+"F0.wireOp",EDGE,"E3141"),sQuery(id+"F0.wireOp",EDGE,"E3142"),sQuery(id+"F0.wireOp",EDGE,"E3143"),sQuery(id+"F0.wireOp",EDGE,"E3144"),sQuery(id+"F0.wireOp",EDGE,"E3145"),sQuery(id+"F0.wireOp",EDGE,"E3146"),sQuery(id+"F0.wireOp",EDGE,"E3147"),sQuery(id+"F0.wireOp",EDGE,"E3148"),sQuery(id+"F0.wireOp",EDGE,"E3149"),sQuery(id+"F0.wireOp",EDGE,"E3150"),sQuery(id+"F0.wireOp",EDGE,"E3151"),sQuery(id+"F0.wireOp",EDGE,"E3152"),sQuery(id+"F0.wireOp",EDGE,"E3153"),sQuery(id+"F0.wireOp",EDGE,"E3154"),sQuery(id+"F0.wireOp",EDGE,"E3155"),sQuery(id+"F0.wireOp",EDGE,"E3156"),sQuery(id+"F0.wireOp",EDGE,"E3157"),sQuery(id+"F0.wireOp",EDGE,"E3158"),sQuery(id+"F0.wireOp",EDGE,"E3159"),sQuery(id+"F0.wireOp",EDGE,"E3160"),sQuery(id+"F0.wireOp",EDGE,"E3161"),sQuery(id+"F0.wireOp",EDGE,"E3162"),sQuery(id+"F0.wireOp",EDGE,"E3163"),sQuery(id+"F0.wireOp",EDGE,"E3164"),sQuery(id+"F0.wireOp",EDGE,"E3165"),sQuery(id+"F0.wireOp",EDGE,"E3166"),sQuery(id+"F0.wireOp",EDGE,"E3167"),sQuery(id+"F0.wireOp",EDGE,"E3168"),sQuery(id+"F0.wireOp",EDGE,"E3169"),sQuery(id+"F0.wireOp",EDGE,"E3170"),sQuery(id+"F0.wireOp",EDGE,"E3171"),sQuery(id+"F0.wireOp",EDGE,"E3172"),sQuery(id+"F0.wireOp",EDGE,"E3173"),sQuery(id+"F0.wireOp",EDGE,"E3174"),sQuery(id+"F0.wireOp",EDGE,"E3175"),sQuery(id+"F0.wireOp",EDGE,"E3176"),sQuery(id+"F0.wireOp",EDGE,"E3177"),sQuery(id+"F0.wireOp",EDGE,"E3178"),sQuery(id+"F0.wireOp",EDGE,"E3179"),sQuery(id+"F0.wireOp",EDGE,"E3180"),sQuery(id+"F0.wireOp",EDGE,"E3181"),sQuery(id+"F0.wireOp",EDGE,"E3182"),sQuery(id+"F0.wireOp",EDGE,"E3183"),sQuery(id+"F0.wireOp",EDGE,"E3184"),sQuery(id+"F0.wireOp",EDGE,"E3185"),sQuery(id+"F0.wireOp",EDGE,"E3186"),sQuery(id+"F0.wireOp",EDGE,"E3187"),sQuery(id+"F0.wireOp",EDGE,"E3188"),sQuery(id+"F0.wireOp",EDGE,"E3189"),sQuery(id+"F0.wireOp",EDGE,"E3190"),sQuery(id+"F0.wireOp",EDGE,"E3191"),sQuery(id+"F0.wireOp",EDGE,"E3192"),sQuery(id+"F0.wireOp",EDGE,"E3193"),sQuery(id+"F0.wireOp",EDGE,"E3194"),sQuery(id+"F0.wireOp",EDGE,"E3195"),sQuery(id+"F0.wireOp",EDGE,"E3196"),sQuery(id+"F0.wireOp",EDGE,"E3197"),sQuery(id+"F0.wireOp",EDGE,"E3198"),sQuery(id+"F0.wireOp",EDGE,"E3199"),sQuery(id+"F0.wireOp",EDGE,"E3200"),sQuery(id+"F0.wireOp",EDGE,"E3201"),sQuery(id+"F0.wireOp",EDGE,"E3202"),sQuery(id+"F0.wireOp",EDGE,"E3203"),sQuery(id+"F0.wireOp",EDGE,"E3204"),sQuery(id+"F0.wireOp",EDGE,"E3205"),sQuery(id+"F0.wireOp",EDGE,"E3206"),sQuery(id+"F0.wireOp",EDGE,"E3207"),sQuery(id+"F0.wireOp",EDGE,"E3208"),sQuery(id+"F0.wireOp",EDGE,"E3209"),sQuery(id+"F0.wireOp",EDGE,"E3210"),sQuery(id+"F0.wireOp",EDGE,"E3211"),sQuery(id+"F0.wireOp",EDGE,"E3212"),sQuery(id+"F0.wireOp",EDGE,"E3213"),sQuery(id+"F0.wireOp",EDGE,"E3214"),sQuery(id+"F0.wireOp",EDGE,"E3215"),sQuery(id+"F0.wireOp",EDGE,"E3216"),sQuery(id+"F0.wireOp",EDGE,"E3217"),sQuery(id+"F0.wireOp",EDGE,"E3218"),sQuery(id+"F0.wireOp",EDGE,"E3219"),sQuery(id+"F0.wireOp",EDGE,"E3220"),sQuery(id+"F0.wireOp",EDGE,"E3221"),sQuery(id+"F0.wireOp",EDGE,"E3222"),sQuery(id+"F0.wireOp",EDGE,"E3223"),sQuery(id+"F0.wireOp",EDGE,"E3224"),sQuery(id+"F0.wireOp",EDGE,"E3225"),sQuery(id+"F0.wireOp",EDGE,"E3226"),sQuery(id+"F0.wireOp",EDGE,"E3227"),sQuery(id+"F0.wireOp",EDGE,"E3228"),sQuery(id+"F0.wireOp",EDGE,"E3229"),sQuery(id+"F0.wireOp",EDGE,"E3230"),sQuery(id+"F0.wireOp",EDGE,"E3231"),sQuery(id+"F0.wireOp",EDGE,"E3232"),sQuery(id+"F0.wireOp",EDGE,"E3233"),sQuery(id+"F0.wireOp",EDGE,"E3234"),sQuery(id+"F0.wireOp",EDGE,"E3235"),sQuery(id+"F0.wireOp",EDGE,"E3236"),sQuery(id+"F0.wireOp",EDGE,"E3237"),sQuery(id+"F0.wireOp",EDGE,"E3238"),sQuery(id+"F0.wireOp",EDGE,"E3239"),sQuery(id+"F0.wireOp",EDGE,"E3240"),sQuery(id+"F0.wireOp",EDGE,"E3241"),sQuery(id+"F0.wireOp",EDGE,"E3242"),sQuery(id+"F0.wireOp",EDGE,"E3243"),sQuery(id+"F0.wireOp",EDGE,"E3244"),sQuery(id+"F0.wireOp",EDGE,"E3245"),sQuery(id+"F0.wireOp",EDGE,"E3246"),sQuery(id+"F0.wireOp",EDGE,"E3247"),sQuery(id+"F0.wireOp",EDGE,"E3248"),sQuery(id+"F0.wireOp",EDGE,"E3249"),sQuery(id+"F0.wireOp",EDGE,"E3250"),sQuery(id+"F0.wireOp",EDGE,"E3251"),sQuery(id+"F0.wireOp",EDGE,"E3252"),sQuery(id+"F0.wireOp",EDGE,"E3253"),sQuery(id+"F0.wireOp",EDGE,"E3254"),sQuery(id+"F0.wireOp",EDGE,"E3255"),sQuery(id+"F0.wireOp",EDGE,"E3256"),sQuery(id+"F0.wireOp",EDGE,"E3257"),sQuery(id+"F0.wireOp",EDGE,"E3258"),sQuery(id+"F0.wireOp",EDGE,"E3259"),sQuery(id+"F0.wireOp",EDGE,"E3260"),sQuery(id+"F0.wireOp",EDGE,"E3261"),sQuery(id+"F0.wireOp",EDGE,"E3262"),sQuery(id+"F0.wireOp",EDGE,"E3263"),sQuery(id+"F0.wireOp",EDGE,"E3264"),sQuery(id+"F0.wireOp",EDGE,"E3265"),sQuery(id+"F0.wireOp",EDGE,"E3266"),sQuery(id+"F0.wireOp",EDGE,"E3267"),sQuery(id+"F0.wireOp",EDGE,"E3268"),sQuery(id+"F0.wireOp",EDGE,"E3269"),sQuery(id+"F0.wireOp",EDGE,"E3270"),sQuery(id+"F0.wireOp",EDGE,"E3271"),sQuery(id+"F0.wireOp",EDGE,"E3272"),sQuery(id+"F0.wireOp",EDGE,"E3273"),sQuery(id+"F0.wireOp",EDGE,"E3274"),sQuery(id+"F0.wireOp",EDGE,"E3275"),sQuery(id+"F0.wireOp",EDGE,"E3276"),sQuery(id+"F0.wireOp",EDGE,"E3277"),sQuery(id+"F0.wireOp",EDGE,"E3278"),sQuery(id+"F0.wireOp",EDGE,"E3279"),sQuery(id+"F0.wireOp",EDGE,"E3280"),sQuery(id+"F0.wireOp",EDGE,"E3281"),sQuery(id+"F0.wireOp",EDGE,"E3282"),sQuery(id+"F0.wireOp",EDGE,"E3283"),sQuery(id+"F0.wireOp",EDGE,"E3284"),sQuery(id+"F0.wireOp",EDGE,"E3285"),sQuery(id+"F0.wireOp",EDGE,"E3286"),sQuery(id+"F0.wireOp",EDGE,"E3287"),sQuery(id+"F0.wireOp",EDGE,"E3288"),sQuery(id+"F0.wireOp",EDGE,"E3289"),sQuery(id+"F0.wireOp",EDGE,"E3290"),sQuery(id+"F0.wireOp",EDGE,"E3291"),sQuery(id+"F0.wireOp",EDGE,"E3292"),sQuery(id+"F0.wireOp",EDGE,"E3293"),sQuery(id+"F0.wireOp",EDGE,"E3294"),sQuery(id+"F0.wireOp",EDGE,"E3295"),sQuery(id+"F0.wireOp",EDGE,"E3296"),sQuery(id+"F0.wireOp",EDGE,"E3297"),sQuery(id+"F0.wireOp",EDGE,"E3298"),sQuery(id+"F0.wireOp",EDGE,"E3299"),sQuery(id+"F0.wireOp",EDGE,"E3300"),sQuery(id+"F0.wireOp",EDGE,"E3301"),sQuery(id+"F0.wireOp",EDGE,"E3302"),sQuery(id+"F0.wireOp",EDGE,"E3303"),sQuery(id+"F0.wireOp",EDGE,"E3304"),sQuery(id+"F0.wireOp",EDGE,"E3305"),sQuery(id+"F0.wireOp",EDGE,"E3306"),sQuery(id+"F0.wireOp",EDGE,"E3307"),sQuery(id+"F0.wireOp",EDGE,"E3308"),sQuery(id+"F0.wireOp",EDGE,"E3309"),sQuery(id+"F0.wireOp",EDGE,"E3310"),sQuery(id+"F0.wireOp",EDGE,"E3311"),sQuery(id+"F0.wireOp",EDGE,"E3312"),sQuery(id+"F0.wireOp",EDGE,"E3313"),sQuery(id+"F0.wireOp",EDGE,"E3314"),sQuery(id+"F0.wireOp",EDGE,"E3315"),sQuery(id+"F0.wireOp",EDGE,"E3316"),sQuery(id+"F0.wireOp",EDGE,"E3317"),sQuery(id+"F0.wireOp",EDGE,"E3318"),sQuery(id+"F0.wireOp",EDGE,"E3319"),sQuery(id+"F0.wireOp",EDGE,"E3320"),sQuery(id+"F0.wireOp",EDGE,"E3321"),sQuery(id+"F0.wireOp",EDGE,"E3322"),sQuery(id+"F0.wireOp",EDGE,"E3323"),sQuery(id+"F0.wireOp",EDGE,"E3324"),sQuery(id+"F0.wireOp",EDGE,"E3325"),sQuery(id+"F0.wireOp",EDGE,"E3326"),sQuery(id+"F0.wireOp",EDGE,"E3327"),sQuery(id+"F0.wireOp",EDGE,"E3328"),sQuery(id+"F0.wireOp",EDGE,"E3329"),sQuery(id+"F0.wireOp",EDGE,"E3330"),sQuery(id+"F0.wireOp",EDGE,"E3331"),sQuery(id+"F0.wireOp",EDGE,"E3332"),sQuery(id+"F0.wireOp",EDGE,"E3333"),sQuery(id+"F0.wireOp",EDGE,"E3334"),sQuery(id+"F0.wireOp",EDGE,"E3335"),sQuery(id+"F0.wireOp",EDGE,"E3336"),sQuery(id+"F0.wireOp",EDGE,"E3337"),sQuery(id+"F0.wireOp",EDGE,"E3338"),sQuery(id+"F0.wireOp",EDGE,"E3339"),sQuery(id+"F0.wireOp",EDGE,"E3340"),sQuery(id+"F0.wireOp",EDGE,"E3341"),sQuery(id+"F0.wireOp",EDGE,"E3342"),sQuery(id+"F0.wireOp",EDGE,"E3343"),sQuery(id+"F0.wireOp",EDGE,"E3344"),sQuery(id+"F0.wireOp",EDGE,"E3345"),sQuery(id+"F0.wireOp",EDGE,"E3346"),sQuery(id+"F0.wireOp",EDGE,"E3347"),sQuery(id+"F0.wireOp",EDGE,"E3348"),sQuery(id+"F0.wireOp",EDGE,"E3349"),sQuery(id+"F0.wireOp",EDGE,"E3350"),sQuery(id+"F0.wireOp",EDGE,"E3351"),sQuery(id+"F0.wireOp",EDGE,"E3352"),sQuery(id+"F0.wireOp",EDGE,"E3353"),sQuery(id+"F0.wireOp",EDGE,"E3354"),sQuery(id+"F0.wireOp",EDGE,"E3355"),sQuery(id+"F0.wireOp",EDGE,"E3356"),sQuery(id+"F0.wireOp",EDGE,"E3357"),sQuery(id+"F0.wireOp",EDGE,"E3358"),sQuery(id+"F0.wireOp",EDGE,"E3359"),sQuery(id+"F0.wireOp",EDGE,"E3360"),sQuery(id+"F0.wireOp",EDGE,"E3361"),sQuery(id+"F0.wireOp",EDGE,"E3362"),sQuery(id+"F0.wireOp",EDGE,"E3363"),sQuery(id+"F0.wireOp",EDGE,"E3364"),sQuery(id+"F0.wireOp",EDGE,"E3365"),sQuery(id+"F0.wireOp",EDGE,"E3366"),sQuery(id+"F0.wireOp",EDGE,"E3367"),sQuery(id+"F0.wireOp",EDGE,"E3368"),sQuery(id+"F0.wireOp",EDGE,"E3369"),sQuery(id+"F0.wireOp",EDGE,"E3370"),sQuery(id+"F0.wireOp",EDGE,"E3371"),sQuery(id+"F0.wireOp",EDGE,"E3372"),sQuery(id+"F0.wireOp",EDGE,"E3373"),sQuery(id+"F0.wireOp",EDGE,"E3374"),sQuery(id+"F0.wireOp",EDGE,"E3375"),sQuery(id+"F0.wireOp",EDGE,"E3376"),sQuery(id+"F0.wireOp",EDGE,"E3377"),sQuery(id+"F0.wireOp",EDGE,"E3378"),sQuery(id+"F0.wireOp",EDGE,"E3379"),sQuery(id+"F0.wireOp",EDGE,"E3380"),sQuery(id+"F0.wireOp",EDGE,"E3381"),sQuery(id+"F0.wireOp",EDGE,"E3382"),sQuery(id+"F0.wireOp",EDGE,"E3383"),sQuery(id+"F0.wireOp",EDGE,"E3384"),sQuery(id+"F0.wireOp",EDGE,"E3385"),sQuery(id+"F0.wireOp",EDGE,"E3386"),sQuery(id+"F0.wireOp",EDGE,"E3387"),sQuery(id+"F0.wireOp",EDGE,"E3388"),sQuery(id+"F0.wireOp",EDGE,"E3389"),sQuery(id+"F0.wireOp",EDGE,"E3390"),sQuery(id+"F0.wireOp",EDGE,"E3391"),sQuery(id+"F0.wireOp",EDGE,"E3392"),sQuery(id+"F0.wireOp",EDGE,"E3393"),sQuery(id+"F0.wireOp",EDGE,"E3394"),sQuery(id+"F0.wireOp",EDGE,"E3395"),sQuery(id+"F0.wireOp",EDGE,"E3396"),sQuery(id+"F0.wireOp",EDGE,"E3397"),sQuery(id+"F0.wireOp",EDGE,"E3398"),sQuery(id+"F0.wireOp",EDGE,"E3399"),sQuery(id+"F0.wireOp",EDGE,"E3400"),sQuery(id+"F0.wireOp",EDGE,"E3401"),sQuery(id+"F0.wireOp",EDGE,"E3402"),sQuery(id+"F0.wireOp",EDGE,"E3403"),sQuery(id+"F0.wireOp",EDGE,"E3404"),sQuery(id+"F0.wireOp",EDGE,"E3405"),sQuery(id+"F0.wireOp",EDGE,"E3406"),sQuery(id+"F0.wireOp",EDGE,"E3407"),sQuery(id+"F0.wireOp",EDGE,"E3408"),sQuery(id+"F0.wireOp",EDGE,"E3409"),sQuery(id+"F0.wireOp",EDGE,"E3410"),sQuery(id+"F0.wireOp",EDGE,"E3411"),sQuery(id+"F0.wireOp",EDGE,"E3412"),sQuery(id+"F0.wireOp",EDGE,"E3413"),sQuery(id+"F0.wireOp",EDGE,"E3414"),sQuery(id+"F0.wireOp",EDGE,"E3415"),sQuery(id+"F0.wireOp",EDGE,"E3416"),sQuery(id+"F0.wireOp",EDGE,"E3417"),sQuery(id+"F0.wireOp",EDGE,"E3418"),sQuery(id+"F0.wireOp",EDGE,"E3419"),sQuery(id+"F0.wireOp",EDGE,"E3420"),sQuery(id+"F0.wireOp",EDGE,"E3421"),sQuery(id+"F0.wireOp",EDGE,"E3422"),sQuery(id+"F0.wireOp",EDGE,"E3423"),sQuery(id+"F0.wireOp",EDGE,"E3424"),sQuery(id+"F0.wireOp",EDGE,"E3425"),sQuery(id+"F0.wireOp",EDGE,"E3426"),sQuery(id+"F0.wireOp",EDGE,"E3427"),sQuery(id+"F0.wireOp",EDGE,"E3428"),sQuery(id+"F0.wireOp",EDGE,"E3429"),sQuery(id+"F0.wireOp",EDGE,"E3430"),sQuery(id+"F0.wireOp",EDGE,"E3431"),sQuery(id+"F0.wireOp",EDGE,"E3432"),sQuery(id+"F0.wireOp",EDGE,"E3433"),sQuery(id+"F0.wireOp",EDGE,"E3434"),sQuery(id+"F0.wireOp",EDGE,"E3435"),sQuery(id+"F0.wireOp",EDGE,"E3436"),sQuery(id+"F0.wireOp",EDGE,"E3437"),sQuery(id+"F0.wireOp",EDGE,"E3438"),sQuery(id+"F0.wireOp",EDGE,"E3439"),sQuery(id+"F0.wireOp",EDGE,"E3440"),sQuery(id+"F0.wireOp",EDGE,"E3441"),sQuery(id+"F0.wireOp",EDGE,"E3442"),sQuery(id+"F0.wireOp",EDGE,"E3443"),sQuery(id+"F0.wireOp",EDGE,"E3444"),sQuery(id+"F0.wireOp",EDGE,"E3445"),sQuery(id+"F0.wireOp",EDGE,"E3446"),sQuery(id+"F0.wireOp",EDGE,"E3447"),sQuery(id+"F0.wireOp",EDGE,"E3448"),sQuery(id+"F0.wireOp",EDGE,"E3449"),sQuery(id+"F0.wireOp",EDGE,"E3450"),sQuery(id+"F0.wireOp",EDGE,"E3451"),sQuery(id+"F0.wireOp",EDGE,"E3452"),sQuery(id+"F0.wireOp",EDGE,"E3453"),sQuery(id+"F0.wireOp",EDGE,"E3454"),sQuery(id+"F0.wireOp",EDGE,"E3455"),sQuery(id+"F0.wireOp",EDGE,"E3456"),sQuery(id+"F0.wireOp",EDGE,"E3457"),sQuery(id+"F0.wireOp",EDGE,"E3458"),sQuery(id+"F0.wireOp",EDGE,"E3459"),sQuery(id+"F0.wireOp",EDGE,"E3460"),sQuery(id+"F0.wireOp",EDGE,"E3461"),sQuery(id+"F0.wireOp",EDGE,"E3462"),sQuery(id+"F0.wireOp",EDGE,"E3463"),sQuery(id+"F0.wireOp",EDGE,"E3464"),sQuery(id+"F0.wireOp",EDGE,"E3465"),sQuery(id+"F0.wireOp",EDGE,"E3466"),sQuery(id+"F0.wireOp",EDGE,"E3467"),sQuery(id+"F0.wireOp",EDGE,"E3468"),sQuery(id+"F0.wireOp",EDGE,"E3469"),sQuery(id+"F0.wireOp",EDGE,"E3470"),sQuery(id+"F0.wireOp",EDGE,"E3471"),sQuery(id+"F0.wireOp",EDGE,"E3472"),sQuery(id+"F0.wireOp",EDGE,"E3473"),sQuery(id+"F0.wireOp",EDGE,"E3474"),sQuery(id+"F0.wireOp",EDGE,"E3475"),sQuery(id+"F0.wireOp",EDGE,"E3476"),sQuery(id+"F0.wireOp",EDGE,"E3477"),sQuery(id+"F0.wireOp",EDGE,"E3478"),sQuery(id+"F0.wireOp",EDGE,"E3479"),sQuery(id+"F0.wireOp",EDGE,"E3480"),sQuery(id+"F0.wireOp",EDGE,"E3481"),sQuery(id+"F0.wireOp",EDGE,"E3482"),sQuery(id+"F0.wireOp",EDGE,"E3483"),sQuery(id+"F0.wireOp",EDGE,"E3484"),sQuery(id+"F0.wireOp",EDGE,"E3485"),sQuery(id+"F0.wireOp",EDGE,"E3486"),sQuery(id+"F0.wireOp",EDGE,"E3487"),sQuery(id+"F0.wireOp",EDGE,"E3488"),sQuery(id+"F0.wireOp",EDGE,"E3489"),sQuery(id+"F0.wireOp",EDGE,"E3490"),sQuery(id+"F0.wireOp",EDGE,"E3491"),sQuery(id+"F0.wireOp",EDGE,"E3492"),sQuery(id+"F0.wireOp",EDGE,"E3493"),sQuery(id+"F0.wireOp",EDGE,"E3494"),sQuery(id+"F0.wireOp",EDGE,"E3495"),sQuery(id+"F0.wireOp",EDGE,"E3496"),sQuery(id+"F0.wireOp",EDGE,"E3497"),sQuery(id+"F0.wireOp",EDGE,"E3498"),sQuery(id+"F0.wireOp",EDGE,"E3499"),sQuery(id+"F0.wireOp",EDGE,"E3500"),sQuery(id+"F0.wireOp",EDGE,"E3501"),sQuery(id+"F0.wireOp",EDGE,"E3502"),sQuery(id+"F0.wireOp",EDGE,"E3503"),sQuery(id+"F0.wireOp",EDGE,"E3504"),sQuery(id+"F0.wireOp",EDGE,"E3505"),sQuery(id+"F0.wireOp",EDGE,"E3506"),sQuery(id+"F0.wireOp",EDGE,"E3507"),sQuery(id+"F0.wireOp",EDGE,"E3508"),sQuery(id+"F0.wireOp",EDGE,"E3509"),sQuery(id+"F0.wireOp",EDGE,"E3510"),sQuery(id+"F0.wireOp",EDGE,"E3511"),sQuery(id+"F0.wireOp",EDGE,"E3512"),sQuery(id+"F0.wireOp",EDGE,"E3513"),sQuery(id+"F0.wireOp",EDGE,"E3514"),sQuery(id+"F0.wireOp",EDGE,"E3515"),sQuery(id+"F0.wireOp",EDGE,"E3516"),sQuery(id+"F0.wireOp",EDGE,"E3517"),sQuery(id+"F0.wireOp",EDGE,"E3518"),sQuery(id+"F0.wireOp",EDGE,"E3519"),sQuery(id+"F0.wireOp",EDGE,"E3520"),sQuery(id+"F0.wireOp",EDGE,"E3521"),sQuery(id+"F0.wireOp",EDGE,"E3522"),sQuery(id+"F0.wireOp",EDGE,"E3523"),sQuery(id+"F0.wireOp",EDGE,"E3524"),sQuery(id+"F0.wireOp",EDGE,"E3525"),sQuery(id+"F0.wireOp",EDGE,"E3526"),sQuery(id+"F0.wireOp",EDGE,"E3527"),sQuery(id+"F0.wireOp",EDGE,"E3528"),sQuery(id+"F0.wireOp",EDGE,"E3529"),sQuery(id+"F0.wireOp",EDGE,"E3530"),sQuery(id+"F0.wireOp",EDGE,"E3531"),sQuery(id+"F0.wireOp",EDGE,"E3532"),sQuery(id+"F0.wireOp",EDGE,"E3533"),sQuery(id+"F0.wireOp",EDGE,"E3534"),sQuery(id+"F0.wireOp",EDGE,"E3535"),sQuery(id+"F0.wireOp",EDGE,"E3536"),sQuery(id+"F0.wireOp",EDGE,"E3537"),sQuery(id+"F0.wireOp",EDGE,"E3538"),sQuery(id+"F0.wireOp",EDGE,"E3539"),sQuery(id+"F0.wireOp",EDGE,"E3540"),sQuery(id+"F0.wireOp",EDGE,"E3541"),sQuery(id+"F0.wireOp",EDGE,"E3542"),sQuery(id+"F0.wireOp",EDGE,"E3543"),sQuery(id+"F0.wireOp",EDGE,"E3544"),sQuery(id+"F0.wireOp",EDGE,"E3545"),sQuery(id+"F0.wireOp",EDGE,"E3546"),sQuery(id+"F0.wireOp",EDGE,"E3547"),sQuery(id+"F0.wireOp",EDGE,"E3548"),sQuery(id+"F0.wireOp",EDGE,"E3549"),sQuery(id+"F0.wireOp",EDGE,"E3550"),sQuery(id+"F0.wireOp",EDGE,"E3551"),sQuery(id+"F0.wireOp",EDGE,"E3552"),sQuery(id+"F0.wireOp",EDGE,"E3553"),sQuery(id+"F0.wireOp",EDGE,"E3554"),sQuery(id+"F0.wireOp",EDGE,"E3555"),sQuery(id+"F0.wireOp",EDGE,"E3556"),sQuery(id+"F0.wireOp",EDGE,"E3557"),sQuery(id+"F0.wireOp",EDGE,"E3558"),sQuery(id+"F0.wireOp",EDGE,"E3559"),sQuery(id+"F0.wireOp",EDGE,"E3560"),sQuery(id+"F0.wireOp",EDGE,"E3561"),sQuery(id+"F0.wireOp",EDGE,"E3562"),sQuery(id+"F0.wireOp",EDGE,"E3563"),sQuery(id+"F0.wireOp",EDGE,"E3564"),sQuery(id+"F0.wireOp",EDGE,"E3565"),sQuery(id+"F0.wireOp",EDGE,"E3566"),sQuery(id+"F0.wireOp",EDGE,"E3567"),sQuery(id+"F0.wireOp",EDGE,"E3568"),sQuery(id+"F0.wireOp",EDGE,"E3569"),sQuery(id+"F0.wireOp",EDGE,"E3570"),sQuery(id+"F0.wireOp",EDGE,"E3571"),sQuery(id+"F0.wireOp",EDGE,"E3572"),sQuery(id+"F0.wireOp",EDGE,"E3573"),sQuery(id+"F0.wireOp",EDGE,"E3574"),sQuery(id+"F0.wireOp",EDGE,"E3575"),sQuery(id+"F0.wireOp",EDGE,"E3576"),sQuery(id+"F0.wireOp",EDGE,"E3577"),sQuery(id+"F0.wireOp",EDGE,"E3578"),sQuery(id+"F0.wireOp",EDGE,"E3579"),sQuery(id+"F0.wireOp",EDGE,"E3580"),sQuery(id+"F0.wireOp",EDGE,"E3581"),sQuery(id+"F0.wireOp",EDGE,"E3582"),sQuery(id+"F0.wireOp",EDGE,"E3583"),sQuery(id+"F0.wireOp",EDGE,"E3584"),sQuery(id+"F0.wireOp",EDGE,"E3585"),sQuery(id+"F0.wireOp",EDGE,"E3586"),sQuery(id+"F0.wireOp",EDGE,"E3587"),sQuery(id+"F0.wireOp",EDGE,"E3588"),sQuery(id+"F0.wireOp",EDGE,"E3589"),sQuery(id+"F0.wireOp",EDGE,"E3590"),sQuery(id+"F0.wireOp",EDGE,"E3591"),sQuery(id+"F0.wireOp",EDGE,"E3592"),sQuery(id+"F0.wireOp",EDGE,"E3593"),sQuery(id+"F0.wireOp",EDGE,"E3594"),sQuery(id+"F0.wireOp",EDGE,"E3595"),sQuery(id+"F0.wireOp",EDGE,"E3596"),sQuery(id+"F0.wireOp",EDGE,"E3597"),sQuery(id+"F0.wireOp",EDGE,"E3598"),sQuery(id+"F0.wireOp",EDGE,"E3599"),sQuery(id+"F0.wireOp",EDGE,"E3600"),sQuery(id+"F0.wireOp",EDGE,"E3601"),sQuery(id+"F0.wireOp",EDGE,"E3602"),sQuery(id+"F0.wireOp",EDGE,"E3603"),sQuery(id+"F0.wireOp",EDGE,"E3604"),sQuery(id+"F0.wireOp",EDGE,"E3605"),sQuery(id+"F0.wireOp",EDGE,"E3606"),sQuery(id+"F0.wireOp",EDGE,"E3607"),sQuery(id+"F0.wireOp",EDGE,"E3608"),sQuery(id+"F0.wireOp",EDGE,"E3609"),sQuery(id+"F0.wireOp",EDGE,"E3610"),sQuery(id+"F0.wireOp",EDGE,"E3611"),sQuery(id+"F0.wireOp",EDGE,"E3612"),sQuery(id+"F0.wireOp",EDGE,"E3613"),sQuery(id+"F0.wireOp",EDGE,"E3614"),sQuery(id+"F0.wireOp",EDGE,"E3615"),sQuery(id+"F0.wireOp",EDGE,"E3616"),sQuery(id+"F0.wireOp",EDGE,"E3617"),sQuery(id+"F0.wireOp",EDGE,"E3618"),sQuery(id+"F0.wireOp",EDGE,"E3619"),sQuery(id+"F0.wireOp",EDGE,"E3620"),sQuery(id+"F0.wireOp",EDGE,"E3621"),sQuery(id+"F0.wireOp",EDGE,"E3622"),sQuery(id+"F0.wireOp",EDGE,"E3623"),sQuery(id+"F0.wireOp",EDGE,"E3624"),sQuery(id+"F0.wireOp",EDGE,"E3625"),sQuery(id+"F0.wireOp",EDGE,"E3626"),sQuery(id+"F0.wireOp",EDGE,"E3627"),sQuery(id+"F0.wireOp",EDGE,"E3628"),sQuery(id+"F0.wireOp",EDGE,"E3629"),sQuery(id+"F0.wireOp",EDGE,"E3630"),sQuery(id+"F0.wireOp",EDGE,"E3631"),sQuery(id+"F0.wireOp",EDGE,"E3632"),sQuery(id+"F0.wireOp",EDGE,"E3633"),sQuery(id+"F0.wireOp",EDGE,"E3634"),sQuery(id+"F0.wireOp",EDGE,"E3635"),sQuery(id+"F0.wireOp",EDGE,"E3636"),sQuery(id+"F0.wireOp",EDGE,"E3637"),sQuery(id+"F0.wireOp",EDGE,"E3638"),sQuery(id+"F0.wireOp",EDGE,"E3639"),sQuery(id+"F0.wireOp",EDGE,"E3640"),sQuery(id+"F0.wireOp",EDGE,"E3641"),sQuery(id+"F0.wireOp",EDGE,"E3642"),sQuery(id+"F0.wireOp",EDGE,"E3643"),sQuery(id+"F0.wireOp",EDGE,"E3644"),sQuery(id+"F0.wireOp",EDGE,"E3645"),sQuery(id+"F0.wireOp",EDGE,"E3646"),sQuery(id+"F0.wireOp",EDGE,"E3647"),sQuery(id+"F0.wireOp",EDGE,"E3648"),sQuery(id+"F0.wireOp",EDGE,"E3649"),sQuery(id+"F0.wireOp",EDGE,"E3650"),sQuery(id+"F0.wireOp",EDGE,"E3651"),sQuery(id+"F0.wireOp",EDGE,"E3652"),sQuery(id+"F0.wireOp",EDGE,"E3653"),sQuery(id+"F0.wireOp",EDGE,"E3654"),sQuery(id+"F0.wireOp",EDGE,"E3655"),sQuery(id+"F0.wireOp",EDGE,"E3656"),sQuery(id+"F0.wireOp",EDGE,"E3657"),sQuery(id+"F0.wireOp",EDGE,"E3658"),sQuery(id+"F0.wireOp",EDGE,"E3659"),sQuery(id+"F0.wireOp",EDGE,"E3660"),sQuery(id+"F0.wireOp",EDGE,"E3661"),sQuery(id+"F0.wireOp",EDGE,"E3662"),sQuery(id+"F0.wireOp",EDGE,"E3663"),sQuery(id+"F0.wireOp",EDGE,"E3664"),sQuery(id+"F0.wireOp",EDGE,"E3665"),sQuery(id+"F0.wireOp",EDGE,"E3666"),sQuery(id+"F0.wireOp",EDGE,"E3667"),sQuery(id+"F0.wireOp",EDGE,"E3668"),sQuery(id+"F0.wireOp",EDGE,"E3669"),sQuery(id+"F0.wireOp",EDGE,"E3670"),sQuery(id+"F0.wireOp",EDGE,"E3671"),sQuery(id+"F0.wireOp",EDGE,"E3672"),sQuery(id+"F0.wireOp",EDGE,"E3673"),sQuery(id+"F0.wireOp",EDGE,"E3674"),sQuery(id+"F0.wireOp",EDGE,"E3675"),sQuery(id+"F0.wireOp",EDGE,"E3676"),sQuery(id+"F0.wireOp",EDGE,"E3677"),sQuery(id+"F0.wireOp",EDGE,"E3678"),sQuery(id+"F0.wireOp",EDGE,"E3679"),sQuery(id+"F0.wireOp",EDGE,"E3680"),sQuery(id+"F0.wireOp",EDGE,"E3681"),sQuery(id+"F0.wireOp",EDGE,"E3682"),sQuery(id+"F0.wireOp",EDGE,"E3683"),sQuery(id+"F0.wireOp",EDGE,"E3684"),sQuery(id+"F0.wireOp",EDGE,"E3685"),sQuery(id+"F0.wireOp",EDGE,"E3686"),sQuery(id+"F0.wireOp",EDGE,"E3687"),sQuery(id+"F0.wireOp",EDGE,"E3688"),sQuery(id+"F0.wireOp",EDGE,"E3689"),sQuery(id+"F0.wireOp",EDGE,"E3690"),sQuery(id+"F0.wireOp",EDGE,"E3691"),sQuery(id+"F0.wireOp",EDGE,"E3692"),sQuery(id+"F0.wireOp",EDGE,"E3693"),sQuery(id+"F0.wireOp",EDGE,"E3694"),sQuery(id+"F0.wireOp",EDGE,"E3695"),sQuery(id+"F0.wireOp",EDGE,"E3696"),sQuery(id+"F0.wireOp",EDGE,"E3697"),sQuery(id+"F0.wireOp",EDGE,"E3698"),sQuery(id+"F0.wireOp",EDGE,"E3699"),sQuery(id+"F0.wireOp",EDGE,"E3700"),sQuery(id+"F0.wireOp",EDGE,"E3701"),sQuery(id+"F0.wireOp",EDGE,"E3702"),sQuery(id+"F0.wireOp",EDGE,"E3703"),sQuery(id+"F0.wireOp",EDGE,"E3704"),sQuery(id+"F0.wireOp",EDGE,"E3705"),sQuery(id+"F0.wireOp",EDGE,"E3706"),sQuery(id+"F0.wireOp",EDGE,"E3707"),sQuery(id+"F0.wireOp",EDGE,"E3708"),sQuery(id+"F0.wireOp",EDGE,"E3709"),sQuery(id+"F0.wireOp",EDGE,"E3710"),sQuery(id+"F0.wireOp",EDGE,"E3711"),sQuery(id+"F0.wireOp",EDGE,"E3712"),sQuery(id+"F0.wireOp",EDGE,"E3713"),sQuery(id+"F0.wireOp",EDGE,"E3714"),sQuery(id+"F0.wireOp",EDGE,"E3715"),sQuery(id+"F0.wireOp",EDGE,"E3716"),sQuery(id+"F0.wireOp",EDGE,"E3717"),sQuery(id+"F0.wireOp",EDGE,"E3718"),sQuery(id+"F0.wireOp",EDGE,"E3719"),sQuery(id+"F0.wireOp",EDGE,"E3720"),sQuery(id+"F0.wireOp",EDGE,"E3721"),sQuery(id+"F0.wireOp",EDGE,"E3722"),sQuery(id+"F0.wireOp",EDGE,"E3723"),sQuery(id+"F0.wireOp",EDGE,"E3724"),sQuery(id+"F0.wireOp",EDGE,"E3725"),sQuery(id+"F0.wireOp",EDGE,"E3726"),sQuery(id+"F0.wireOp",EDGE,"E3727"),sQuery(id+"F0.wireOp",EDGE,"E3728"),sQuery(id+"F0.wireOp",EDGE,"E3729"),sQuery(id+"F0.wireOp",EDGE,"E3730"),sQuery(id+"F0.wireOp",EDGE,"E3731"),sQuery(id+"F0.wireOp",EDGE,"E3732"),sQuery(id+"F0.wireOp",EDGE,"E3733"),sQuery(id+"F0.wireOp",EDGE,"E3734"),sQuery(id+"F0.wireOp",EDGE,"E3735"),sQuery(id+"F0.wireOp",EDGE,"E3736"),sQuery(id+"F0.wireOp",EDGE,"E3737"),sQuery(id+"F0.wireOp",EDGE,"E3738"),sQuery(id+"F0.wireOp",EDGE,"E3739"),sQuery(id+"F0.wireOp",EDGE,"E3740"),sQuery(id+"F0.wireOp",EDGE,"E3741"),sQuery(id+"F0.wireOp",EDGE,"E3742"),sQuery(id+"F0.wireOp",EDGE,"E3743"),sQuery(id+"F0.wireOp",EDGE,"E3744"),sQuery(id+"F0.wireOp",EDGE,"E3745"),sQuery(id+"F0.wireOp",EDGE,"E3746"),sQuery(id+"F0.wireOp",EDGE,"E3747"),sQuery(id+"F0.wireOp",EDGE,"E3748"),sQuery(id+"F0.wireOp",EDGE,"E3749"),sQuery(id+"F0.wireOp",EDGE,"E3750"),sQuery(id+"F0.wireOp",EDGE,"E3751"),sQuery(id+"F0.wireOp",EDGE,"E3752"),sQuery(id+"F0.wireOp",EDGE,"E3753"),sQuery(id+"F0.wireOp",EDGE,"E3754"),sQuery(id+"F0.wireOp",EDGE,"E3755"),sQuery(id+"F0.wireOp",EDGE,"E3756"),sQuery(id+"F0.wireOp",EDGE,"E3757"),sQuery(id+"F0.wireOp",EDGE,"E3758"),sQuery(id+"F0.wireOp",EDGE,"E3759"),sQuery(id+"F0.wireOp",EDGE,"E3760"),sQuery(id+"F0.wireOp",EDGE,"E3761"),sQuery(id+"F0.wireOp",EDGE,"E3762"),sQuery(id+"F0.wireOp",EDGE,"E3763"),sQuery(id+"F0.wireOp",EDGE,"E3764"),sQuery(id+"F0.wireOp",EDGE,"E3765"),sQuery(id+"F0.wireOp",EDGE,"E3766"),sQuery(id+"F0.wireOp",EDGE,"E3767"),sQuery(id+"F0.wireOp",EDGE,"E3768"),sQuery(id+"F0.wireOp",EDGE,"E3769"),sQuery(id+"F0.wireOp",EDGE,"E3770"),sQuery(id+"F0.wireOp",EDGE,"E3771"),sQuery(id+"F0.wireOp",EDGE,"E3772"),sQuery(id+"F0.wireOp",EDGE,"E3773"),sQuery(id+"F0.wireOp",EDGE,"E3774"),sQuery(id+"F0.wireOp",EDGE,"E3775"),sQuery(id+"F0.wireOp",EDGE,"E3776"),sQuery(id+"F0.wireOp",EDGE,"E3777"),sQuery(id+"F0.wireOp",EDGE,"E3778"),sQuery(id+"F0.wireOp",EDGE,"E3779"),sQuery(id+"F0.wireOp",EDGE,"E3780"),sQuery(id+"F0.wireOp",EDGE,"E3781"),sQuery(id+"F0.wireOp",EDGE,"E3782"),sQuery(id+"F0.wireOp",EDGE,"E3783"),sQuery(id+"F0.wireOp",EDGE,"E3784"),sQuery(id+"F0.wireOp",EDGE,"E3785"),sQuery(id+"F0.wireOp",EDGE,"E3786"),sQuery(id+"F0.wireOp",EDGE,"E3787"),sQuery(id+"F0.wireOp",EDGE,"E3788"),sQuery(id+"F0.wireOp",EDGE,"E3789"),sQuery(id+"F0.wireOp",EDGE,"E3790"),sQuery(id+"F0.wireOp",EDGE,"E3791"),sQuery(id+"F0.wireOp",EDGE,"E3792"),sQuery(id+"F0.wireOp",EDGE,"E3793"),sQuery(id+"F0.wireOp",EDGE,"E3794"),sQuery(id+"F0.wireOp",EDGE,"E3795"),sQuery(id+"F0.wireOp",EDGE,"E3796"),sQuery(id+"F0.wireOp",EDGE,"E3797"),sQuery(id+"F0.wireOp",EDGE,"E3798"),sQuery(id+"F0.wireOp",EDGE,"E3799"),sQuery(id+"F0.wireOp",EDGE,"E3800"),sQuery(id+"F0.wireOp",EDGE,"E3801"),sQuery(id+"F0.wireOp",EDGE,"E3802"),sQuery(id+"F0.wireOp",EDGE,"E3803"),sQuery(id+"F0.wireOp",EDGE,"E3804"),sQuery(id+"F0.wireOp",EDGE,"E3805"),sQuery(id+"F0.wireOp",EDGE,"E3806"),sQuery(id+"F0.wireOp",EDGE,"E3807"),sQuery(id+"F0.wireOp",EDGE,"E3808"),sQuery(id+"F0.wireOp",EDGE,"E3809"),sQuery(id+"F0.wireOp",EDGE,"E3810"),sQuery(id+"F0.wireOp",EDGE,"E3811"),sQuery(id+"F0.wireOp",EDGE,"E3812"),sQuery(id+"F0.wireOp",EDGE,"E3813"),sQuery(id+"F0.wireOp",EDGE,"E3814"),sQuery(id+"F0.wireOp",EDGE,"E3815"),sQuery(id+"F0.wireOp",EDGE,"E3816"),sQuery(id+"F0.wireOp",EDGE,"E3817"),sQuery(id+"F0.wireOp",EDGE,"E3818"),sQuery(id+"F0.wireOp",EDGE,"E3819"),sQuery(id+"F0.wireOp",EDGE,"E3820"),sQuery(id+"F0.wireOp",EDGE,"E3821"),sQuery(id+"F0.wireOp",EDGE,"E3822"),sQuery(id+"F0.wireOp",EDGE,"E3823"),sQuery(id+"F0.wireOp",EDGE,"E3824"),sQuery(id+"F0.wireOp",EDGE,"E3825"),sQuery(id+"F0.wireOp",EDGE,"E3826"),sQuery(id+"F0.wireOp",EDGE,"E3827"),sQuery(id+"F0.wireOp",EDGE,"E3828"),sQuery(id+"F0.wireOp",EDGE,"E3829"),sQuery(id+"F0.wireOp",EDGE,"E3830"),sQuery(id+"F0.wireOp",EDGE,"E3831"),sQuery(id+"F0.wireOp",EDGE,"E3832"),sQuery(id+"F0.wireOp",EDGE,"E3833"),sQuery(id+"F0.wireOp",EDGE,"E3834"),sQuery(id+"F0.wireOp",EDGE,"E3835"),sQuery(id+"F0.wireOp",EDGE,"E3836"),sQuery(id+"F0.wireOp",EDGE,"E3837"),sQuery(id+"F0.wireOp",EDGE,"E3838"),sQuery(id+"F0.wireOp",EDGE,"E3839"),sQuery(id+"F0.wireOp",EDGE,"E3840"),sQuery(id+"F0.wireOp",EDGE,"E3841"),sQuery(id+"F0.wireOp",EDGE,"E3842"),sQuery(id+"F0.wireOp",EDGE,"E3843"),sQuery(id+"F0.wireOp",EDGE,"E3844"),sQuery(id+"F0.wireOp",EDGE,"E3845"),sQuery(id+"F0.wireOp",EDGE,"E3846"),sQuery(id+"F0.wireOp",EDGE,"E3847"),sQuery(id+"F0.wireOp",EDGE,"E3848"),sQuery(id+"F0.wireOp",EDGE,"E3849"),sQuery(id+"F0.wireOp",EDGE,"E3850"),sQuery(id+"F0.wireOp",EDGE,"E3851"),sQuery(id+"F0.wireOp",EDGE,"E3852"),sQuery(id+"F0.wireOp",EDGE,"E3853"),sQuery(id+"F0.wireOp",EDGE,"E3854"),sQuery(id+"F0.wireOp",EDGE,"E3855"),sQuery(id+"F0.wireOp",EDGE,"E3856"),sQuery(id+"F0.wireOp",EDGE,"E3857"),sQuery(id+"F0.wireOp",EDGE,"E3858"),sQuery(id+"F0.wireOp",EDGE,"E3859"),sQuery(id+"F0.wireOp",EDGE,"E3860"),sQuery(id+"F0.wireOp",EDGE,"E3861"),sQuery(id+"F0.wireOp",EDGE,"E3862"),sQuery(id+"F0.wireOp",EDGE,"E3863"),sQuery(id+"F0.wireOp",EDGE,"E3864"),sQuery(id+"F0.wireOp",EDGE,"E3865"),sQuery(id+"F0.wireOp",EDGE,"E3866"),sQuery(id+"F0.wireOp",EDGE,"E3867"),sQuery(id+"F0.wireOp",EDGE,"E3868"),sQuery(id+"F0.wireOp",EDGE,"E3869"),sQuery(id+"F0.wireOp",EDGE,"E3870"),sQuery(id+"F0.wireOp",EDGE,"E3871"),sQuery(id+"F0.wireOp",EDGE,"E3872"),sQuery(id+"F0.wireOp",EDGE,"E3873"),sQuery(id+"F0.wireOp",EDGE,"E3874"),sQuery(id+"F0.wireOp",EDGE,"E3875"),sQuery(id+"F0.wireOp",EDGE,"E3876"),sQuery(id+"F0.wireOp",EDGE,"E3877"),sQuery(id+"F0.wireOp",EDGE,"E3878"),sQuery(id+"F0.wireOp",EDGE,"E3879"),sQuery(id+"F0.wireOp",EDGE,"E3880"),sQuery(id+"F0.wireOp",EDGE,"E3881"),sQuery(id+"F0.wireOp",EDGE,"E3882"),sQuery(id+"F0.wireOp",EDGE,"E3883"),sQuery(id+"F0.wireOp",EDGE,"E3884"),sQuery(id+"F0.wireOp",EDGE,"E3885"),sQuery(id+"F0.wireOp",EDGE,"E3886"),sQuery(id+"F0.wireOp",EDGE,"E3887"),sQuery(id+"F0.wireOp",EDGE,"E3888"),sQuery(id+"F0.wireOp",EDGE,"E3889"),sQuery(id+"F0.wireOp",EDGE,"E3890"),sQuery(id+"F0.wireOp",EDGE,"E3891"),sQuery(id+"F0.wireOp",EDGE,"E3892"),sQuery(id+"F0.wireOp",EDGE,"E3893"),sQuery(id+"F0.wireOp",EDGE,"E3894"),sQuery(id+"F0.wireOp",EDGE,"E3895"),sQuery(id+"F0.wireOp",EDGE,"E3896"),sQuery(id+"F0.wireOp",EDGE,"E3897"),sQuery(id+"F0.wireOp",EDGE,"E3898"),sQuery(id+"F0.wireOp",EDGE,"E3899"),sQuery(id+"F0.wireOp",EDGE,"E3900"),sQuery(id+"F0.wireOp",EDGE,"E3901"),sQuery(id+"F0.wireOp",EDGE,"E3902"),sQuery(id+"F0.wireOp",EDGE,"E3903"),sQuery(id+"F0.wireOp",EDGE,"E3904"),sQuery(id+"F0.wireOp",EDGE,"E3905"),sQuery(id+"F0.wireOp",EDGE,"E3906"),sQuery(id+"F0.wireOp",EDGE,"E3907"),sQuery(id+"F0.wireOp",EDGE,"E3908"),sQuery(id+"F0.wireOp",EDGE,"E3909"),sQuery(id+"F0.wireOp",EDGE,"E3910"),sQuery(id+"F0.wireOp",EDGE,"E3911"),sQuery(id+"F0.wireOp",EDGE,"E3912"),sQuery(id+"F0.wireOp",EDGE,"E3913"),sQuery(id+"F0.wireOp",EDGE,"E3914"),sQuery(id+"F0.wireOp",EDGE,"E3915"),sQuery(id+"F0.wireOp",EDGE,"E3916"),sQuery(id+"F0.wireOp",EDGE,"E3917"),sQuery(id+"F0.wireOp",EDGE,"E3918"),sQuery(id+"F0.wireOp",EDGE,"E3919"),sQuery(id+"F0.wireOp",EDGE,"E3920"),sQuery(id+"F0.wireOp",EDGE,"E3921"),sQuery(id+"F0.wireOp",EDGE,"E3922"),sQuery(id+"F0.wireOp",EDGE,"E3923"),sQuery(id+"F0.wireOp",EDGE,"E3924"),sQuery(id+"F0.wireOp",EDGE,"E3925"),sQuery(id+"F0.wireOp",EDGE,"E3926"),sQuery(id+"F0.wireOp",EDGE,"E3927"),sQuery(id+"F0.wireOp",EDGE,"E3928"),sQuery(id+"F0.wireOp",EDGE,"E3929"),sQuery(id+"F0.wireOp",EDGE,"E3930"),sQuery(id+"F0.wireOp",EDGE,"E3931"),sQuery(id+"F0.wireOp",EDGE,"E3932"),sQuery(id+"F0.wireOp",EDGE,"E3933"),sQuery(id+"F0.wireOp",EDGE,"E3934"),sQuery(id+"F0.wireOp",EDGE,"E3935"),sQuery(id+"F0.wireOp",EDGE,"E3936"),sQuery(id+"F0.wireOp",EDGE,"E3937"),sQuery(id+"F0.wireOp",EDGE,"E3938"),sQuery(id+"F0.wireOp",EDGE,"E3939"),sQuery(id+"F0.wireOp",EDGE,"E3940"),sQuery(id+"F0.wireOp",EDGE,"E3941"),sQuery(id+"F0.wireOp",EDGE,"E3942"),sQuery(id+"F0.wireOp",EDGE,"E3943"),sQuery(id+"F0.wireOp",EDGE,"E3944"),sQuery(id+"F0.wireOp",EDGE,"E3945"),sQuery(id+"F0.wireOp",EDGE,"E3946"),sQuery(id+"F0.wireOp",EDGE,"E3947"),sQuery(id+"F0.wireOp",EDGE,"E3948"),sQuery(id+"F0.wireOp",EDGE,"E3949"),sQuery(id+"F0.wireOp",EDGE,"E3950"),sQuery(id+"F0.wireOp",EDGE,"E3951"),sQuery(id+"F0.wireOp",EDGE,"E3952"),sQuery(id+"F0.wireOp",EDGE,"E3953"),sQuery(id+"F0.wireOp",EDGE,"E3954"),sQuery(id+"F0.wireOp",EDGE,"E3955"),sQuery(id+"F0.wireOp",EDGE,"E3956"),sQuery(id+"F0.wireOp",EDGE,"E3957"),sQuery(id+"F0.wireOp",EDGE,"E3958"),sQuery(id+"F0.wireOp",EDGE,"E3959"),sQuery(id+"F0.wireOp",EDGE,"E3960"),sQuery(id+"F0.wireOp",EDGE,"E3961"),sQuery(id+"F0.wireOp",EDGE,"E3962"),sQuery(id+"F0.wireOp",EDGE,"E3963"),sQuery(id+"F0.wireOp",EDGE,"E3964"),sQuery(id+"F0.wireOp",EDGE,"E3965"),sQuery(id+"F0.wireOp",EDGE,"E3966"),sQuery(id+"F0.wireOp",EDGE,"E3967"),sQuery(id+"F0.wireOp",EDGE,"E3968"),sQuery(id+"F0.wireOp",EDGE,"E3969"),sQuery(id+"F0.wireOp",EDGE,"E3970"),sQuery(id+"F0.wireOp",EDGE,"E3971"),sQuery(id+"F0.wireOp",EDGE,"E3972"),sQuery(id+"F0.wireOp",EDGE,"E3973"),sQuery(id+"F0.wireOp",EDGE,"E3974"),sQuery(id+"F0.wireOp",EDGE,"E3975"),sQuery(id+"F0.wireOp",EDGE,"E3976"),sQuery(id+"F0.wireOp",EDGE,"E3977"),sQuery(id+"F0.wireOp",EDGE,"E3978"),sQuery(id+"F0.wireOp",EDGE,"E3979"),sQuery(id+"F0.wireOp",EDGE,"E3980"),sQuery(id+"F0.wireOp",EDGE,"E3981"),sQuery(id+"F0.wireOp",EDGE,"E3982"),sQuery(id+"F0.wireOp",EDGE,"E3983"),sQuery(id+"F0.wireOp",EDGE,"E3984"),sQuery(id+"F0.wireOp",EDGE,"E3985"),sQuery(id+"F0.wireOp",EDGE,"E3986"),sQuery(id+"F0.wireOp",EDGE,"E3987"),sQuery(id+"F0.wireOp",EDGE,"E3988"),sQuery(id+"F0.wireOp",EDGE,"E3989"),sQuery(id+"F0.wireOp",EDGE,"E3990"),sQuery(id+"F0.wireOp",EDGE,"E3991"),sQuery(id+"F0.wireOp",EDGE,"E3992"),sQuery(id+"F0.wireOp",EDGE,"E3993"),sQuery(id+"F0.wireOp",EDGE,"E3994"),sQuery(id+"F0.wireOp",EDGE,"E3995"),sQuery(id+"F0.wireOp",EDGE,"E3996"),sQuery(id+"F0.wireOp",EDGE,"E3997"),sQuery(id+"F0.wireOp",EDGE,"E3998"),sQuery(id+"F0.wireOp",EDGE,"E3999"),sQuery(id+"F0.wireOp",EDGE,"E4000"),sQuery(id+"F0.wireOp",EDGE,"E4001"),sQuery(id+"F0.wireOp",EDGE,"E4002"),sQuery(id+"F0.wireOp",EDGE,"E4003"),sQuery(id+"F0.wireOp",EDGE,"E4004"),sQuery(id+"F0.wireOp",EDGE,"E4005"),sQuery(id+"F0.wireOp",EDGE,"E4006"),sQuery(id+"F0.wireOp",EDGE,"E4007"),sQuery(id+"F0.wireOp",EDGE,"E4008"),sQuery(id+"F0.wireOp",EDGE,"E4009"),sQuery(id+"F0.wireOp",EDGE,"E4010"),sQuery(id+"F0.wireOp",EDGE,"E4011"),sQuery(id+"F0.wireOp",EDGE,"E4012"),sQuery(id+"F0.wireOp",EDGE,"E4013"),sQuery(id+"F0.wireOp",EDGE,"E4014"),sQuery(id+"F0.wireOp",EDGE,"E4015"),sQuery(id+"F0.wireOp",EDGE,"E4016"),sQuery(id+"F0.wireOp",EDGE,"E4017"),sQuery(id+"F0.wireOp",EDGE,"E4018"),sQuery(id+"F0.wireOp",EDGE,"E4019"),sQuery(id+"F0.wireOp",EDGE,"E4020"),sQuery(id+"F0.wireOp",EDGE,"E4021"),sQuery(id+"F0.wireOp",EDGE,"E4022"),sQuery(id+"F0.wireOp",EDGE,"E4023"),sQuery(id+"F0.wireOp",EDGE,"E4024"),sQuery(id+"F0.wireOp",EDGE,"E4025"),sQuery(id+"F0.wireOp",EDGE,"E4026"),sQuery(id+"F0.wireOp",EDGE,"E4027"),sQuery(id+"F0.wireOp",EDGE,"E4028"),sQuery(id+"F0.wireOp",EDGE,"E4029"),sQuery(id+"F0.wireOp",EDGE,"E4030"),sQuery(id+"F0.wireOp",EDGE,"E4031"),sQuery(id+"F0.wireOp",EDGE,"E4032"),sQuery(id+"F0.wireOp",EDGE,"E4033"),sQuery(id+"F0.wireOp",EDGE,"E4034"),sQuery(id+"F0.wireOp",EDGE,"E4035"),sQuery(id+"F0.wireOp",EDGE,"E4036"),sQuery(id+"F0.wireOp",EDGE,"E4037"),sQuery(id+"F0.wireOp",EDGE,"E4038"),sQuery(id+"F0.wireOp",EDGE,"E4039"),sQuery(id+"F0.wireOp",EDGE,"E4040"),sQuery(id+"F0.wireOp",EDGE,"E4041"),sQuery(id+"F0.wireOp",EDGE,"E4042"),sQuery(id+"F0.wireOp",EDGE,"E4043"),sQuery(id+"F0.wireOp",EDGE,"E4044"),sQuery(id+"F0.wireOp",EDGE,"E4045"),sQuery(id+"F0.wireOp",EDGE,"E4046"),sQuery(id+"F0.wireOp",EDGE,"E4047"),sQuery(id+"F0.wireOp",EDGE,"E4048"),sQuery(id+"F0.wireOp",EDGE,"E4049"),sQuery(id+"F0.wireOp",EDGE,"E4050"),sQuery(id+"F0.wireOp",EDGE,"E4051"),sQuery(id+"F0.wireOp",EDGE,"E4052"),sQuery(id+"F0.wireOp",EDGE,"E4053"),sQuery(id+"F0.wireOp",EDGE,"E4054"),sQuery(id+"F0.wireOp",EDGE,"E4055"),sQuery(id+"F0.wireOp",EDGE,"E4056"),sQuery(id+"F0.wireOp",EDGE,"E4057"),sQuery(id+"F0.wireOp",EDGE,"E4058"),sQuery(id+"F0.wireOp",EDGE,"E4059"),sQuery(id+"F0.wireOp",EDGE,"E4060"),sQuery(id+"F0.wireOp",EDGE,"E4061"),sQuery(id+"F0.wireOp",EDGE,"E4062"),sQuery(id+"F0.wireOp",EDGE,"E4063"),sQuery(id+"F0.wireOp",EDGE,"E4064"),sQuery(id+"F0.wireOp",EDGE,"E4065"),sQuery(id+"F0.wireOp",EDGE,"E4066"),sQuery(id+"F0.wireOp",EDGE,"E4067"),sQuery(id+"F0.wireOp",EDGE,"E4068"),sQuery(id+"F0.wireOp",EDGE,"E4069"),sQuery(id+"F0.wireOp",EDGE,"E4070"),sQuery(id+"F0.wireOp",EDGE,"E4071"),sQuery(id+"F0.wireOp",EDGE,"E4072"),sQuery(id+"F0.wireOp",EDGE,"E4073"),sQuery(id+"F0.wireOp",EDGE,"E4074"),sQuery(id+"F0.wireOp",EDGE,"E4075"),sQuery(id+"F0.wireOp",EDGE,"E4076"),sQuery(id+"F0.wireOp",EDGE,"E4077"),sQuery(id+"F0.wireOp",EDGE,"E4078"),sQuery(id+"F0.wireOp",EDGE,"E4079"),sQuery(id+"F0.wireOp",EDGE,"E4080"),sQuery(id+"F0.wireOp",EDGE,"E4081"),sQuery(id+"F0.wireOp",EDGE,"E4082"),sQuery(id+"F0.wireOp",EDGE,"E4083"),sQuery(id+"F0.wireOp",EDGE,"E4084"),sQuery(id+"F0.wireOp",EDGE,"E4085"),sQuery(id+"F0.wireOp",EDGE,"E4086"),sQuery(id+"F0.wireOp",EDGE,"E4087"),sQuery(id+"F0.wireOp",EDGE,"E4088"),sQuery(id+"F0.wireOp",EDGE,"E4089"),sQuery(id+"F0.wireOp",EDGE,"E4090"),sQuery(id+"F0.wireOp",EDGE,"E4091"),sQuery(id+"F0.wireOp",EDGE,"E4092"),sQuery(id+"F0.wireOp",EDGE,"E4093"),sQuery(id+"F0.wireOp",EDGE,"E4094"),sQuery(id+"F0.wireOp",EDGE,"E4095"),sQuery(id+"F0.wireOp",EDGE,"E4096"),sQuery(id+"F0.wireOp",EDGE,"E4097"),sQuery(id+"F0.wireOp",EDGE,"E4098"),sQuery(id+"F0.wireOp",EDGE,"E4099"),sQuery(id+"F0.wireOp",EDGE,"E4100"),sQuery(id+"F0.wireOp",EDGE,"E4101"),sQuery(id+"F0.wireOp",EDGE,"E4102"),sQuery(id+"F0.wireOp",EDGE,"E4103"),sQuery(id+"F0.wireOp",EDGE,"E4104"),sQuery(id+"F0.wireOp",EDGE,"E4105"),sQuery(id+"F0.wireOp",EDGE,"E4106"),sQuery(id+"F0.wireOp",EDGE,"E4107"),sQuery(id+"F0.wireOp",EDGE,"E4108"),sQuery(id+"F0.wireOp",EDGE,"E4109"),sQuery(id+"F0.wireOp",EDGE,"E4110"),sQuery(id+"F0.wireOp",EDGE,"E4111"),sQuery(id+"F0.wireOp",EDGE,"E4112"),sQuery(id+"F0.wireOp",EDGE,"E4113"),sQuery(id+"F0.wireOp",EDGE,"E4114"),sQuery(id+"F0.wireOp",EDGE,"E4115"),sQuery(id+"F0.wireOp",EDGE,"E4116"),sQuery(id+"F0.wireOp",EDGE,"E4117"),sQuery(id+"F0.wireOp",EDGE,"E4118"),sQuery(id+"F0.wireOp",EDGE,"E4119"),sQuery(id+"F0.wireOp",EDGE,"E4120"),sQuery(id+"F0.wireOp",EDGE,"E4121"),sQuery(id+"F0.wireOp",EDGE,"E4122"),sQuery(id+"F0.wireOp",EDGE,"E4123"),sQuery(id+"F0.wireOp",EDGE,"E4124"),sQuery(id+"F0.wireOp",EDGE,"E4125"),sQuery(id+"F0.wireOp",EDGE,"E4126"),sQuery(id+"F0.wireOp",EDGE,"E4127"),sQuery(id+"F0.wireOp",EDGE,"E4128"),sQuery(id+"F0.wireOp",EDGE,"E4129"),sQuery(id+"F0.wireOp",EDGE,"E4130"),sQuery(id+"F0.wireOp",EDGE,"E4131"),sQuery(id+"F0.wireOp",EDGE,"E4132"),sQuery(id+"F0.wireOp",EDGE,"E4133"),sQuery(id+"F0.wireOp",EDGE,"E4134"),sQuery(id+"F0.wireOp",EDGE,"E4135"),sQuery(id+"F0.wireOp",EDGE,"E4136"),sQuery(id+"F0.wireOp",EDGE,"E4137"),sQuery(id+"F0.wireOp",EDGE,"E4138"),sQuery(id+"F0.wireOp",EDGE,"E4139"),sQuery(id+"F0.wireOp",EDGE,"E4140"),sQuery(id+"F0.wireOp",EDGE,"E4141"),sQuery(id+"F0.wireOp",EDGE,"E4142"),sQuery(id+"F0.wireOp",EDGE,"E4143"),sQuery(id+"F0.wireOp",EDGE,"E4144"),sQuery(id+"F0.wireOp",EDGE,"E4145"),sQuery(id+"F0.wireOp",EDGE,"E4146"),sQuery(id+"F0.wireOp",EDGE,"E4147"),sQuery(id+"F0.wireOp",EDGE,"E4148"),sQuery(id+"F0.wireOp",EDGE,"E4149"),sQuery(id+"F0.wireOp",EDGE,"E4150"),sQuery(id+"F0.wireOp",EDGE,"E4151"),sQuery(id+"F0.wireOp",EDGE,"E4152"),sQuery(id+"F0.wireOp",EDGE,"E4153"),sQuery(id+"F0.wireOp",EDGE,"E4154"),sQuery(id+"F0.wireOp",EDGE,"E4155"),sQuery(id+"F0.wireOp",EDGE,"E4156"),sQuery(id+"F0.wireOp",EDGE,"E4157"),sQuery(id+"F0.wireOp",EDGE,"E4158"),sQuery(id+"F0.wireOp",EDGE,"E4159"),sQuery(id+"F0.wireOp",EDGE,"E4160"),sQuery(id+"F0.wireOp",EDGE,"E4161"),sQuery(id+"F0.wireOp",EDGE,"E4162"),sQuery(id+"F0.wireOp",EDGE,"E4163"),sQuery(id+"F0.wireOp",EDGE,"E4164"),sQuery(id+"F0.wireOp",EDGE,"E4165"),sQuery(id+"F0.wireOp",EDGE,"E4166"),sQuery(id+"F0.wireOp",EDGE,"E4167"),sQuery(id+"F0.wireOp",EDGE,"E4168"),sQuery(id+"F0.wireOp",EDGE,"E4169"),sQuery(id+"F0.wireOp",EDGE,"E4170"),sQuery(id+"F0.wireOp",EDGE,"E4171"),sQuery(id+"F0.wireOp",EDGE,"E4172"),sQuery(id+"F0.wireOp",EDGE,"E4173"),sQuery(id+"F0.wireOp",EDGE,"E4174"),sQuery(id+"F0.wireOp",EDGE,"E4175"),sQuery(id+"F0.wireOp",EDGE,"E4176"),sQuery(id+"F0.wireOp",EDGE,"E4177"),sQuery(id+"F0.wireOp",EDGE,"E4178"),sQuery(id+"F0.wireOp",EDGE,"E4179"),sQuery(id+"F0.wireOp",EDGE,"E4180"),sQuery(id+"F0.wireOp",EDGE,"E4181"),sQuery(id+"F0.wireOp",EDGE,"E4182"),sQuery(id+"F0.wireOp",EDGE,"E4183"),sQuery(id+"F0.wireOp",EDGE,"E4184"),sQuery(id+"F0.wireOp",EDGE,"E4185"),sQuery(id+"F0.wireOp",EDGE,"E4186"),sQuery(id+"F0.wireOp",EDGE,"E4187"),sQuery(id+"F0.wireOp",EDGE,"E4188"),sQuery(id+"F0.wireOp",EDGE,"E4189"),sQuery(id+"F0.wireOp",EDGE,"E4403"),sQuery(id+"F0.wireOp",EDGE,"E4404")])],"isStart":false}),makeQuery(id+"F3.opExtrude","CAP_FACE",FACE,{"disambiguationData":[OSD([sQuery(id+"F2.wireOp",EDGE,"E4405.bottom"),sQuery(id+"F2.wireOp",EDGE,"E4405.top"),sQuery(id+"F2.wireOp",EDGE,"E4405.left"),sQuery(id+"F2.wireOp",EDGE,"E4405.right")])],"isStart":true})]});
            var sketch = newSketch(context, id + "F4", { "sketchPlane" : qUnion([Q0])});
            skLineSegment(sketch, "E4407.bottom", {"start": v(-30.29, -36.3) * mm, "end": v(-24.79, -36.3) * mm});
            skLineSegment(sketch, "E4407.top", {"start": v(-30.29, -30.8) * mm, "end": v(-24.79, -30.8) * mm});
            skLineSegment(sketch, "E4407.left", {"start": v(-30.29, -36.3) * mm, "end": v(-30.29, -30.8) * mm});
            skLineSegment(sketch, "E4407.right", {"start": v(-24.79, -36.3) * mm, "end": v(-24.79, -30.8) * mm});
            skLineSegment(sketch, "E4408.bottom", {"start": v(-15.29, -36.3) * mm, "end": v(-9.79, -36.3) * mm});
            skLineSegment(sketch, "E4408.top", {"start": v(-15.29, -30.8) * mm, "end": v(-9.79, -30.8) * mm});
            skLineSegment(sketch, "E4408.left", {"start": v(-15.29, -36.3) * mm, "end": v(-15.29, -30.8) * mm});
            skLineSegment(sketch, "E4408.right", {"start": v(-9.79, -36.3) * mm, "end": v(-9.79, -30.8) * mm});
            skLineSegment(sketch, "E4409", {"start": v(-24.79, -30.8) * mm, "end": v(-15.29, -30.8) * mm, "construction": true});
            skLineSegment(sketch, "E4410", {"start": v(-20.04, -30.8) * mm, "end": v(-20.04, -36.3) * mm, "construction": true});
            skLineSegment(sketch, "E4411", {"start": v(-27.54, -30.8) * mm, "end": v(-27.54, -36.3) * mm, "construction": true});
            skLineSegment(sketch, "E4412", {"start": v(-12.54, -30.8) * mm, "end": v(-12.54, -36.3) * mm, "construction": true});
            skSolve(sketch);
        }
        {
            var Q0;
            Q0 = qSketchRegion(id + "F4", true);
            var Q1;
            {var subQ0=sQuery(id+"F0.wireOp",EDGE,"E4404");var subQ1=sQuery(id+"F0.wireOp",EDGE,"E4403");var subQ2=sQuery(id+"F0.wireOp",EDGE,"E4189");var subQ3=sQuery(id+"F0.wireOp",EDGE,"E4188");var subQ4=sQuery(id+"F0.wireOp",EDGE,"E4187");var subQ5=sQuery(id+"F0.wireOp",EDGE,"E4186");var subQ6=sQuery(id+"F0.wireOp",EDGE,"E4185");var subQ7=sQuery(id+"F0.wireOp",EDGE,"E4184");var subQ8=sQuery(id+"F0.wireOp",EDGE,"E4183");var subQ9=sQuery(id+"F0.wireOp",EDGE,"E4182");var subQ10=sQuery(id+"F0.wireOp",EDGE,"E4181");var subQ11=sQuery(id+"F0.wireOp",EDGE,"E4180");var subQ12=sQuery(id+"F0.wireOp",EDGE,"E4179");var subQ13=sQuery(id+"F0.wireOp",EDGE,"E4178");var subQ14=sQuery(id+"F0.wireOp",EDGE,"E4177");var subQ15=sQuery(id+"F0.wireOp",EDGE,"E4176");var subQ16=sQuery(id+"F0.wireOp",EDGE,"E4175");var subQ17=sQuery(id+"F0.wireOp",EDGE,"E4174");var subQ18=sQuery(id+"F0.wireOp",EDGE,"E4173");var subQ19=sQuery(id+"F0.wireOp",EDGE,"E4172");var subQ20=sQuery(id+"F0.wireOp",EDGE,"E4171");var subQ21=sQuery(id+"F0.wireOp",EDGE,"E4170");var subQ22=sQuery(id+"F0.wireOp",EDGE,"E4169");var subQ23=sQuery(id+"F0.wireOp",EDGE,"E4168");var subQ24=sQuery(id+"F0.wireOp",EDGE,"E4167");var subQ25=sQuery(id+"F0.wireOp",EDGE,"E4166");var subQ26=sQuery(id+"F0.wireOp",EDGE,"E4165");var subQ27=sQuery(id+"F0.wireOp",EDGE,"E4164");var subQ28=sQuery(id+"F0.wireOp",EDGE,"E4163");var subQ29=sQuery(id+"F0.wireOp",EDGE,"E4162");var subQ30=sQuery(id+"F0.wireOp",EDGE,"E4161");var subQ31=sQuery(id+"F0.wireOp",EDGE,"E4160");var subQ32=sQuery(id+"F0.wireOp",EDGE,"E4159");var subQ33=sQuery(id+"F0.wireOp",EDGE,"E4158");var subQ34=sQuery(id+"F0.wireOp",EDGE,"E4157");var subQ35=sQuery(id+"F0.wireOp",EDGE,"E4156");var subQ36=sQuery(id+"F0.wireOp",EDGE,"E4155");var subQ37=sQuery(id+"F0.wireOp",EDGE,"E4154");var subQ38=sQuery(id+"F0.wireOp",EDGE,"E4153");var subQ39=sQuery(id+"F0.wireOp",EDGE,"E4152");var subQ40=sQuery(id+"F0.wireOp",EDGE,"E4151");var subQ41=sQuery(id+"F0.wireOp",EDGE,"E4150");var subQ42=sQuery(id+"F0.wireOp",EDGE,"E4149");var subQ43=sQuery(id+"F0.wireOp",EDGE,"E4148");var subQ44=sQuery(id+"F0.wireOp",EDGE,"E4147");var subQ45=sQuery(id+"F0.wireOp",EDGE,"E4146");var subQ46=sQuery(id+"F0.wireOp",EDGE,"E4145");var subQ47=sQuery(id+"F0.wireOp",EDGE,"E4144");var subQ48=sQuery(id+"F0.wireOp",EDGE,"E4143");var subQ49=sQuery(id+"F0.wireOp",EDGE,"E4142");var subQ50=sQuery(id+"F0.wireOp",EDGE,"E4141");var subQ51=sQuery(id+"F0.wireOp",EDGE,"E4140");var subQ52=sQuery(id+"F0.wireOp",EDGE,"E4139");var subQ53=sQuery(id+"F0.wireOp",EDGE,"E4138");var subQ54=sQuery(id+"F0.wireOp",EDGE,"E4137");var subQ55=sQuery(id+"F0.wireOp",EDGE,"E4136");var subQ56=sQuery(id+"F0.wireOp",EDGE,"E4135");var subQ57=sQuery(id+"F0.wireOp",EDGE,"E4134");var subQ58=sQuery(id+"F0.wireOp",EDGE,"E4133");var subQ59=sQuery(id+"F0.wireOp",EDGE,"E4132");var subQ60=sQuery(id+"F0.wireOp",EDGE,"E4131");var subQ61=sQuery(id+"F0.wireOp",EDGE,"E4130");var subQ62=sQuery(id+"F0.wireOp",EDGE,"E4129");var subQ63=sQuery(id+"F0.wireOp",EDGE,"E4128");var subQ64=sQuery(id+"F0.wireOp",EDGE,"E4127");var subQ65=sQuery(id+"F0.wireOp",EDGE,"E4126");var subQ66=sQuery(id+"F0.wireOp",EDGE,"E4125");var subQ67=sQuery(id+"F0.wireOp",EDGE,"E4124");var subQ68=sQuery(id+"F0.wireOp",EDGE,"E4123");var subQ69=sQuery(id+"F0.wireOp",EDGE,"E4122");var subQ70=sQuery(id+"F0.wireOp",EDGE,"E4121");var subQ71=sQuery(id+"F0.wireOp",EDGE,"E4120");var subQ72=sQuery(id+"F0.wireOp",EDGE,"E4119");var subQ73=sQuery(id+"F0.wireOp",EDGE,"E4118");var subQ74=sQuery(id+"F0.wireOp",EDGE,"E4117");var subQ75=sQuery(id+"F0.wireOp",EDGE,"E4116");var subQ76=sQuery(id+"F0.wireOp",EDGE,"E4115");var subQ77=sQuery(id+"F0.wireOp",EDGE,"E4114");var subQ78=sQuery(id+"F0.wireOp",EDGE,"E4113");var subQ79=sQuery(id+"F0.wireOp",EDGE,"E4112");var subQ80=sQuery(id+"F0.wireOp",EDGE,"E4111");var subQ81=sQuery(id+"F0.wireOp",EDGE,"E4110");var subQ82=sQuery(id+"F0.wireOp",EDGE,"E4109");var subQ83=sQuery(id+"F0.wireOp",EDGE,"E4108");var subQ84=sQuery(id+"F0.wireOp",EDGE,"E4107");var subQ85=sQuery(id+"F0.wireOp",EDGE,"E4106");var subQ86=sQuery(id+"F0.wireOp",EDGE,"E4105");var subQ87=sQuery(id+"F0.wireOp",EDGE,"E4104");var subQ88=sQuery(id+"F0.wireOp",EDGE,"E4103");var subQ89=sQuery(id+"F0.wireOp",EDGE,"E4102");var subQ90=sQuery(id+"F0.wireOp",EDGE,"E4101");var subQ91=sQuery(id+"F0.wireOp",EDGE,"E4100");var subQ92=sQuery(id+"F0.wireOp",EDGE,"E4099");var subQ93=sQuery(id+"F0.wireOp",EDGE,"E4098");var subQ94=sQuery(id+"F0.wireOp",EDGE,"E4097");var subQ95=sQuery(id+"F0.wireOp",EDGE,"E4096");var subQ96=sQuery(id+"F0.wireOp",EDGE,"E4095");var subQ97=sQuery(id+"F0.wireOp",EDGE,"E4094");var subQ98=sQuery(id+"F0.wireOp",EDGE,"E4093");var subQ99=sQuery(id+"F0.wireOp",EDGE,"E4092");var subQ100=sQuery(id+"F0.wireOp",EDGE,"E4091");var subQ101=sQuery(id+"F0.wireOp",EDGE,"E4090");var subQ102=sQuery(id+"F0.wireOp",EDGE,"E4089");var subQ103=sQuery(id+"F0.wireOp",EDGE,"E4088");var subQ104=sQuery(id+"F0.wireOp",EDGE,"E4087");var subQ105=sQuery(id+"F0.wireOp",EDGE,"E4086");var subQ106=sQuery(id+"F0.wireOp",EDGE,"E4085");var subQ107=sQuery(id+"F0.wireOp",EDGE,"E4084");var subQ108=sQuery(id+"F0.wireOp",EDGE,"E4083");var subQ109=sQuery(id+"F0.wireOp",EDGE,"E4082");var subQ110=sQuery(id+"F0.wireOp",EDGE,"E4081");var subQ111=sQuery(id+"F0.wireOp",EDGE,"E4080");var subQ112=sQuery(id+"F0.wireOp",EDGE,"E4079");var subQ113=sQuery(id+"F0.wireOp",EDGE,"E4078");var subQ114=sQuery(id+"F0.wireOp",EDGE,"E4077");var subQ115=sQuery(id+"F0.wireOp",EDGE,"E4076");var subQ116=sQuery(id+"F0.wireOp",EDGE,"E4075");var subQ117=sQuery(id+"F0.wireOp",EDGE,"E4074");var subQ118=sQuery(id+"F0.wireOp",EDGE,"E4073");var subQ119=sQuery(id+"F0.wireOp",EDGE,"E4072");var subQ120=sQuery(id+"F0.wireOp",EDGE,"E4071");var subQ121=sQuery(id+"F0.wireOp",EDGE,"E4070");var subQ122=sQuery(id+"F0.wireOp",EDGE,"E4069");var subQ123=sQuery(id+"F0.wireOp",EDGE,"E4068");var subQ124=sQuery(id+"F0.wireOp",EDGE,"E4067");var subQ125=sQuery(id+"F0.wireOp",EDGE,"E4066");var subQ126=sQuery(id+"F0.wireOp",EDGE,"E4065");var subQ127=sQuery(id+"F0.wireOp",EDGE,"E4064");var subQ128=sQuery(id+"F0.wireOp",EDGE,"E4063");var subQ129=sQuery(id+"F0.wireOp",EDGE,"E4062");var subQ130=sQuery(id+"F0.wireOp",EDGE,"E4061");var subQ131=sQuery(id+"F0.wireOp",EDGE,"E4060");var subQ132=sQuery(id+"F0.wireOp",EDGE,"E4059");var subQ133=sQuery(id+"F0.wireOp",EDGE,"E4058");var subQ134=sQuery(id+"F0.wireOp",EDGE,"E4057");var subQ135=sQuery(id+"F0.wireOp",EDGE,"E4056");var subQ136=sQuery(id+"F0.wireOp",EDGE,"E4055");var subQ137=sQuery(id+"F0.wireOp",EDGE,"E4054");var subQ138=sQuery(id+"F0.wireOp",EDGE,"E4053");var subQ139=sQuery(id+"F0.wireOp",EDGE,"E4052");var subQ140=sQuery(id+"F0.wireOp",EDGE,"E4051");var subQ141=sQuery(id+"F0.wireOp",EDGE,"E4050");var subQ142=sQuery(id+"F0.wireOp",EDGE,"E4049");var subQ143=sQuery(id+"F0.wireOp",EDGE,"E4048");var subQ144=sQuery(id+"F0.wireOp",EDGE,"E4047");var subQ145=sQuery(id+"F0.wireOp",EDGE,"E4046");var subQ146=sQuery(id+"F0.wireOp",EDGE,"E4045");var subQ147=sQuery(id+"F0.wireOp",EDGE,"E4044");var subQ148=sQuery(id+"F0.wireOp",EDGE,"E4043");var subQ149=sQuery(id+"F0.wireOp",EDGE,"E4042");var subQ150=sQuery(id+"F0.wireOp",EDGE,"E4041");var subQ151=sQuery(id+"F0.wireOp",EDGE,"E4040");var subQ152=sQuery(id+"F0.wireOp",EDGE,"E4039");var subQ153=sQuery(id+"F0.wireOp",EDGE,"E4038");var subQ154=sQuery(id+"F0.wireOp",EDGE,"E4037");var subQ155=sQuery(id+"F0.wireOp",EDGE,"E4036");var subQ156=sQuery(id+"F0.wireOp",EDGE,"E4035");var subQ157=sQuery(id+"F0.wireOp",EDGE,"E4034");var subQ158=sQuery(id+"F0.wireOp",EDGE,"E4033");var subQ159=sQuery(id+"F0.wireOp",EDGE,"E4032");var subQ160=sQuery(id+"F0.wireOp",EDGE,"E4031");var subQ161=sQuery(id+"F0.wireOp",EDGE,"E4030");var subQ162=sQuery(id+"F0.wireOp",EDGE,"E4029");var subQ163=sQuery(id+"F0.wireOp",EDGE,"E4028");var subQ164=sQuery(id+"F0.wireOp",EDGE,"E4027");var subQ165=sQuery(id+"F0.wireOp",EDGE,"E4026");var subQ166=sQuery(id+"F0.wireOp",EDGE,"E4025");var subQ167=sQuery(id+"F0.wireOp",EDGE,"E4024");var subQ168=sQuery(id+"F0.wireOp",EDGE,"E4023");var subQ169=sQuery(id+"F0.wireOp",EDGE,"E4022");var subQ170=sQuery(id+"F0.wireOp",EDGE,"E4021");var subQ171=sQuery(id+"F0.wireOp",EDGE,"E4020");var subQ172=sQuery(id+"F0.wireOp",EDGE,"E4019");var subQ173=sQuery(id+"F0.wireOp",EDGE,"E4018");var subQ174=sQuery(id+"F0.wireOp",EDGE,"E4017");var subQ175=sQuery(id+"F0.wireOp",EDGE,"E4016");var subQ176=sQuery(id+"F0.wireOp",EDGE,"E4015");var subQ177=sQuery(id+"F0.wireOp",EDGE,"E4014");var subQ178=sQuery(id+"F0.wireOp",EDGE,"E4013");var subQ179=sQuery(id+"F0.wireOp",EDGE,"E4012");var subQ180=sQuery(id+"F0.wireOp",EDGE,"E4011");var subQ181=sQuery(id+"F0.wireOp",EDGE,"E4010");var subQ182=sQuery(id+"F0.wireOp",EDGE,"E4009");var subQ183=sQuery(id+"F0.wireOp",EDGE,"E4008");var subQ184=sQuery(id+"F0.wireOp",EDGE,"E4007");var subQ185=sQuery(id+"F0.wireOp",EDGE,"E4006");var subQ186=sQuery(id+"F0.wireOp",EDGE,"E4005");var subQ187=sQuery(id+"F0.wireOp",EDGE,"E4004");var subQ188=sQuery(id+"F0.wireOp",EDGE,"E4003");var subQ189=sQuery(id+"F0.wireOp",EDGE,"E4002");var subQ190=sQuery(id+"F0.wireOp",EDGE,"E4001");var subQ191=sQuery(id+"F0.wireOp",EDGE,"E4000");var subQ192=sQuery(id+"F0.wireOp",EDGE,"E3999");var subQ193=sQuery(id+"F0.wireOp",EDGE,"E3998");var subQ194=sQuery(id+"F0.wireOp",EDGE,"E3997");var subQ195=sQuery(id+"F0.wireOp",EDGE,"E3996");var subQ196=sQuery(id+"F0.wireOp",EDGE,"E3995");var subQ197=sQuery(id+"F0.wireOp",EDGE,"E3994");var subQ198=sQuery(id+"F0.wireOp",EDGE,"E3993");var subQ199=sQuery(id+"F0.wireOp",EDGE,"E3992");var subQ200=sQuery(id+"F0.wireOp",EDGE,"E3991");var subQ201=sQuery(id+"F0.wireOp",EDGE,"E3990");var subQ202=sQuery(id+"F0.wireOp",EDGE,"E3989");var subQ203=sQuery(id+"F0.wireOp",EDGE,"E3988");var subQ204=sQuery(id+"F0.wireOp",EDGE,"E3987");var subQ205=sQuery(id+"F0.wireOp",EDGE,"E3986");var subQ206=sQuery(id+"F0.wireOp",EDGE,"E3985");var subQ207=sQuery(id+"F0.wireOp",EDGE,"E3984");var subQ208=sQuery(id+"F0.wireOp",EDGE,"E3983");var subQ209=sQuery(id+"F0.wireOp",EDGE,"E3982");var subQ210=sQuery(id+"F0.wireOp",EDGE,"E3981");var subQ211=sQuery(id+"F0.wireOp",EDGE,"E3980");var subQ212=sQuery(id+"F0.wireOp",EDGE,"E3979");var subQ213=sQuery(id+"F0.wireOp",EDGE,"E3978");var subQ214=sQuery(id+"F0.wireOp",EDGE,"E3977");var subQ215=sQuery(id+"F0.wireOp",EDGE,"E3976");var subQ216=sQuery(id+"F0.wireOp",EDGE,"E3975");var subQ217=sQuery(id+"F0.wireOp",EDGE,"E3974");var subQ218=sQuery(id+"F0.wireOp",EDGE,"E3973");var subQ219=sQuery(id+"F0.wireOp",EDGE,"E3972");var subQ220=sQuery(id+"F0.wireOp",EDGE,"E3971");var subQ221=sQuery(id+"F0.wireOp",EDGE,"E3970");var subQ222=sQuery(id+"F0.wireOp",EDGE,"E3969");var subQ223=sQuery(id+"F0.wireOp",EDGE,"E3968");var subQ224=sQuery(id+"F0.wireOp",EDGE,"E3967");var subQ225=sQuery(id+"F0.wireOp",EDGE,"E3966");var subQ226=sQuery(id+"F0.wireOp",EDGE,"E3965");var subQ227=sQuery(id+"F0.wireOp",EDGE,"E3964");var subQ228=sQuery(id+"F0.wireOp",EDGE,"E3963");var subQ229=sQuery(id+"F0.wireOp",EDGE,"E3962");var subQ230=sQuery(id+"F0.wireOp",EDGE,"E3961");var subQ231=sQuery(id+"F0.wireOp",EDGE,"E3960");var subQ232=sQuery(id+"F0.wireOp",EDGE,"E3959");var subQ233=sQuery(id+"F0.wireOp",EDGE,"E3958");var subQ234=sQuery(id+"F0.wireOp",EDGE,"E3957");var subQ235=sQuery(id+"F0.wireOp",EDGE,"E3956");var subQ236=sQuery(id+"F0.wireOp",EDGE,"E3955");var subQ237=sQuery(id+"F0.wireOp",EDGE,"E3954");var subQ238=sQuery(id+"F0.wireOp",EDGE,"E3953");var subQ239=sQuery(id+"F0.wireOp",EDGE,"E3952");var subQ240=sQuery(id+"F0.wireOp",EDGE,"E3951");var subQ241=sQuery(id+"F0.wireOp",EDGE,"E3950");var subQ242=sQuery(id+"F0.wireOp",EDGE,"E3949");var subQ243=sQuery(id+"F0.wireOp",EDGE,"E3948");var subQ244=sQuery(id+"F0.wireOp",EDGE,"E3947");var subQ245=sQuery(id+"F0.wireOp",EDGE,"E3946");var subQ246=sQuery(id+"F0.wireOp",EDGE,"E3945");var subQ247=sQuery(id+"F0.wireOp",EDGE,"E3944");var subQ248=sQuery(id+"F0.wireOp",EDGE,"E3943");var subQ249=sQuery(id+"F0.wireOp",EDGE,"E3942");var subQ250=sQuery(id+"F0.wireOp",EDGE,"E3941");var subQ251=sQuery(id+"F0.wireOp",EDGE,"E3940");var subQ252=sQuery(id+"F0.wireOp",EDGE,"E3939");var subQ253=sQuery(id+"F0.wireOp",EDGE,"E3938");var subQ254=sQuery(id+"F0.wireOp",EDGE,"E3937");var subQ255=sQuery(id+"F0.wireOp",EDGE,"E3936");var subQ256=sQuery(id+"F0.wireOp",EDGE,"E3935");var subQ257=sQuery(id+"F0.wireOp",EDGE,"E3934");var subQ258=sQuery(id+"F0.wireOp",EDGE,"E3933");var subQ259=sQuery(id+"F0.wireOp",EDGE,"E3932");var subQ260=sQuery(id+"F0.wireOp",EDGE,"E3931");var subQ261=sQuery(id+"F0.wireOp",EDGE,"E3930");var subQ262=sQuery(id+"F0.wireOp",EDGE,"E3929");var subQ263=sQuery(id+"F0.wireOp",EDGE,"E3928");var subQ264=sQuery(id+"F0.wireOp",EDGE,"E3927");var subQ265=sQuery(id+"F0.wireOp",EDGE,"E3926");var subQ266=sQuery(id+"F0.wireOp",EDGE,"E3925");var subQ267=sQuery(id+"F0.wireOp",EDGE,"E3924");var subQ268=sQuery(id+"F0.wireOp",EDGE,"E3923");var subQ269=sQuery(id+"F0.wireOp",EDGE,"E3922");var subQ270=sQuery(id+"F0.wireOp",EDGE,"E3921");var subQ271=sQuery(id+"F0.wireOp",EDGE,"E3920");var subQ272=sQuery(id+"F0.wireOp",EDGE,"E3919");var subQ273=sQuery(id+"F0.wireOp",EDGE,"E3918");var subQ274=sQuery(id+"F0.wireOp",EDGE,"E3917");var subQ275=sQuery(id+"F0.wireOp",EDGE,"E3916");var subQ276=sQuery(id+"F0.wireOp",EDGE,"E3915");var subQ277=sQuery(id+"F0.wireOp",EDGE,"E3914");var subQ278=sQuery(id+"F0.wireOp",EDGE,"E3913");var subQ279=sQuery(id+"F0.wireOp",EDGE,"E3912");var subQ280=sQuery(id+"F0.wireOp",EDGE,"E3911");var subQ281=sQuery(id+"F0.wireOp",EDGE,"E3910");var subQ282=sQuery(id+"F0.wireOp",EDGE,"E3909");var subQ283=sQuery(id+"F0.wireOp",EDGE,"E3908");var subQ284=sQuery(id+"F0.wireOp",EDGE,"E3907");var subQ285=sQuery(id+"F0.wireOp",EDGE,"E3906");var subQ286=sQuery(id+"F0.wireOp",EDGE,"E3905");var subQ287=sQuery(id+"F0.wireOp",EDGE,"E3904");var subQ288=sQuery(id+"F0.wireOp",EDGE,"E3903");var subQ289=sQuery(id+"F0.wireOp",EDGE,"E3902");var subQ290=sQuery(id+"F0.wireOp",EDGE,"E3901");var subQ291=sQuery(id+"F0.wireOp",EDGE,"E3900");var subQ292=sQuery(id+"F0.wireOp",EDGE,"E3899");var subQ293=sQuery(id+"F0.wireOp",EDGE,"E3898");var subQ294=sQuery(id+"F0.wireOp",EDGE,"E3897");var subQ295=sQuery(id+"F0.wireOp",EDGE,"E3896");var subQ296=sQuery(id+"F0.wireOp",EDGE,"E3895");var subQ297=sQuery(id+"F0.wireOp",EDGE,"E3894");var subQ298=sQuery(id+"F0.wireOp",EDGE,"E3893");var subQ299=sQuery(id+"F0.wireOp",EDGE,"E3892");var subQ300=sQuery(id+"F0.wireOp",EDGE,"E3891");var subQ301=sQuery(id+"F0.wireOp",EDGE,"E3890");var subQ302=sQuery(id+"F0.wireOp",EDGE,"E3889");var subQ303=sQuery(id+"F0.wireOp",EDGE,"E3888");var subQ304=sQuery(id+"F0.wireOp",EDGE,"E3887");var subQ305=sQuery(id+"F0.wireOp",EDGE,"E3886");var subQ306=sQuery(id+"F0.wireOp",EDGE,"E3885");var subQ307=sQuery(id+"F0.wireOp",EDGE,"E3884");var subQ308=sQuery(id+"F0.wireOp",EDGE,"E3883");var subQ309=sQuery(id+"F0.wireOp",EDGE,"E3882");var subQ310=sQuery(id+"F0.wireOp",EDGE,"E3881");var subQ311=sQuery(id+"F0.wireOp",EDGE,"E3880");var subQ312=sQuery(id+"F0.wireOp",EDGE,"E3879");var subQ313=sQuery(id+"F0.wireOp",EDGE,"E3878");var subQ314=sQuery(id+"F0.wireOp",EDGE,"E3877");var subQ315=sQuery(id+"F0.wireOp",EDGE,"E3876");var subQ316=sQuery(id+"F0.wireOp",EDGE,"E3875");var subQ317=sQuery(id+"F0.wireOp",EDGE,"E3874");var subQ318=sQuery(id+"F0.wireOp",EDGE,"E3873");var subQ319=sQuery(id+"F0.wireOp",EDGE,"E3872");var subQ320=sQuery(id+"F0.wireOp",EDGE,"E3871");var subQ321=sQuery(id+"F0.wireOp",EDGE,"E3870");var subQ322=sQuery(id+"F0.wireOp",EDGE,"E3869");var subQ323=sQuery(id+"F0.wireOp",EDGE,"E3868");var subQ324=sQuery(id+"F0.wireOp",EDGE,"E3867");var subQ325=sQuery(id+"F0.wireOp",EDGE,"E3866");var subQ326=sQuery(id+"F0.wireOp",EDGE,"E3865");var subQ327=sQuery(id+"F0.wireOp",EDGE,"E3864");var subQ328=sQuery(id+"F0.wireOp",EDGE,"E3863");var subQ329=sQuery(id+"F0.wireOp",EDGE,"E3862");var subQ330=sQuery(id+"F0.wireOp",EDGE,"E3861");var subQ331=sQuery(id+"F0.wireOp",EDGE,"E3860");var subQ332=sQuery(id+"F0.wireOp",EDGE,"E3859");var subQ333=sQuery(id+"F0.wireOp",EDGE,"E3858");var subQ334=sQuery(id+"F0.wireOp",EDGE,"E3857");var subQ335=sQuery(id+"F0.wireOp",EDGE,"E3856");var subQ336=sQuery(id+"F0.wireOp",EDGE,"E3855");var subQ337=sQuery(id+"F0.wireOp",EDGE,"E3854");var subQ338=sQuery(id+"F0.wireOp",EDGE,"E3853");var subQ339=sQuery(id+"F0.wireOp",EDGE,"E3852");var subQ340=sQuery(id+"F0.wireOp",EDGE,"E3851");var subQ341=sQuery(id+"F0.wireOp",EDGE,"E3850");var subQ342=sQuery(id+"F0.wireOp",EDGE,"E3849");var subQ343=sQuery(id+"F0.wireOp",EDGE,"E3848");var subQ344=sQuery(id+"F0.wireOp",EDGE,"E3847");var subQ345=sQuery(id+"F0.wireOp",EDGE,"E3846");var subQ346=sQuery(id+"F0.wireOp",EDGE,"E3845");var subQ347=sQuery(id+"F0.wireOp",EDGE,"E3844");var subQ348=sQuery(id+"F0.wireOp",EDGE,"E3843");var subQ349=sQuery(id+"F0.wireOp",EDGE,"E3842");var subQ350=sQuery(id+"F0.wireOp",EDGE,"E3841");var subQ351=sQuery(id+"F0.wireOp",EDGE,"E3840");var subQ352=sQuery(id+"F0.wireOp",EDGE,"E3839");var subQ353=sQuery(id+"F0.wireOp",EDGE,"E3838");var subQ354=sQuery(id+"F0.wireOp",EDGE,"E3837");var subQ355=sQuery(id+"F0.wireOp",EDGE,"E3836");var subQ356=sQuery(id+"F0.wireOp",EDGE,"E3835");var subQ357=sQuery(id+"F0.wireOp",EDGE,"E3834");var subQ358=sQuery(id+"F0.wireOp",EDGE,"E3833");var subQ359=sQuery(id+"F0.wireOp",EDGE,"E3832");var subQ360=sQuery(id+"F0.wireOp",EDGE,"E3831");var subQ361=sQuery(id+"F0.wireOp",EDGE,"E3830");var subQ362=sQuery(id+"F0.wireOp",EDGE,"E3829");var subQ363=sQuery(id+"F0.wireOp",EDGE,"E3828");var subQ364=sQuery(id+"F0.wireOp",EDGE,"E3827");var subQ365=sQuery(id+"F0.wireOp",EDGE,"E3826");var subQ366=sQuery(id+"F0.wireOp",EDGE,"E3825");var subQ367=sQuery(id+"F0.wireOp",EDGE,"E3824");var subQ368=sQuery(id+"F0.wireOp",EDGE,"E3823");var subQ369=sQuery(id+"F0.wireOp",EDGE,"E3822");var subQ370=sQuery(id+"F0.wireOp",EDGE,"E3821");var subQ371=sQuery(id+"F0.wireOp",EDGE,"E3820");var subQ372=sQuery(id+"F0.wireOp",EDGE,"E3819");var subQ373=sQuery(id+"F0.wireOp",EDGE,"E3818");var subQ374=sQuery(id+"F0.wireOp",EDGE,"E3817");var subQ375=sQuery(id+"F0.wireOp",EDGE,"E3816");var subQ376=sQuery(id+"F0.wireOp",EDGE,"E3815");var subQ377=sQuery(id+"F0.wireOp",EDGE,"E3814");var subQ378=sQuery(id+"F0.wireOp",EDGE,"E3813");var subQ379=sQuery(id+"F0.wireOp",EDGE,"E3812");var subQ380=sQuery(id+"F0.wireOp",EDGE,"E3811");var subQ381=sQuery(id+"F0.wireOp",EDGE,"E3810");var subQ382=sQuery(id+"F0.wireOp",EDGE,"E3809");var subQ383=sQuery(id+"F0.wireOp",EDGE,"E3808");var subQ384=sQuery(id+"F0.wireOp",EDGE,"E3807");var subQ385=sQuery(id+"F0.wireOp",EDGE,"E3806");var subQ386=sQuery(id+"F0.wireOp",EDGE,"E3805");var subQ387=sQuery(id+"F0.wireOp",EDGE,"E3804");var subQ388=sQuery(id+"F0.wireOp",EDGE,"E3803");var subQ389=sQuery(id+"F0.wireOp",EDGE,"E3802");var subQ390=sQuery(id+"F0.wireOp",EDGE,"E3801");var subQ391=sQuery(id+"F0.wireOp",EDGE,"E3800");var subQ392=sQuery(id+"F0.wireOp",EDGE,"E3799");var subQ393=sQuery(id+"F0.wireOp",EDGE,"E3798");var subQ394=sQuery(id+"F0.wireOp",EDGE,"E3797");var subQ395=sQuery(id+"F0.wireOp",EDGE,"E3796");var subQ396=sQuery(id+"F0.wireOp",EDGE,"E3795");var subQ397=sQuery(id+"F0.wireOp",EDGE,"E3794");var subQ398=sQuery(id+"F0.wireOp",EDGE,"E3793");var subQ399=sQuery(id+"F0.wireOp",EDGE,"E3792");var subQ400=sQuery(id+"F0.wireOp",EDGE,"E3791");var subQ401=sQuery(id+"F0.wireOp",EDGE,"E3790");var subQ402=sQuery(id+"F0.wireOp",EDGE,"E3789");var subQ403=sQuery(id+"F0.wireOp",EDGE,"E3788");var subQ404=sQuery(id+"F0.wireOp",EDGE,"E3787");var subQ405=sQuery(id+"F0.wireOp",EDGE,"E3786");var subQ406=sQuery(id+"F0.wireOp",EDGE,"E3785");var subQ407=sQuery(id+"F0.wireOp",EDGE,"E3784");var subQ408=sQuery(id+"F0.wireOp",EDGE,"E3783");var subQ409=sQuery(id+"F0.wireOp",EDGE,"E3782");var subQ410=sQuery(id+"F0.wireOp",EDGE,"E3781");var subQ411=sQuery(id+"F0.wireOp",EDGE,"E3780");var subQ412=sQuery(id+"F0.wireOp",EDGE,"E3779");var subQ413=sQuery(id+"F0.wireOp",EDGE,"E3778");var subQ414=sQuery(id+"F0.wireOp",EDGE,"E3777");var subQ415=sQuery(id+"F0.wireOp",EDGE,"E3776");var subQ416=sQuery(id+"F0.wireOp",EDGE,"E3775");var subQ417=sQuery(id+"F0.wireOp",EDGE,"E3774");var subQ418=sQuery(id+"F0.wireOp",EDGE,"E3773");var subQ419=sQuery(id+"F0.wireOp",EDGE,"E3772");var subQ420=sQuery(id+"F0.wireOp",EDGE,"E3771");var subQ421=sQuery(id+"F0.wireOp",EDGE,"E3770");var subQ422=sQuery(id+"F0.wireOp",EDGE,"E3769");var subQ423=sQuery(id+"F0.wireOp",EDGE,"E3768");var subQ424=sQuery(id+"F0.wireOp",EDGE,"E3767");var subQ425=sQuery(id+"F0.wireOp",EDGE,"E3766");var subQ426=sQuery(id+"F0.wireOp",EDGE,"E3765");var subQ427=sQuery(id+"F0.wireOp",EDGE,"E3764");var subQ428=sQuery(id+"F0.wireOp",EDGE,"E3763");var subQ429=sQuery(id+"F0.wireOp",EDGE,"E3762");var subQ430=sQuery(id+"F0.wireOp",EDGE,"E3761");var subQ431=sQuery(id+"F0.wireOp",EDGE,"E3760");var subQ432=sQuery(id+"F0.wireOp",EDGE,"E3759");var subQ433=sQuery(id+"F0.wireOp",EDGE,"E3758");var subQ434=sQuery(id+"F0.wireOp",EDGE,"E3757");var subQ435=sQuery(id+"F0.wireOp",EDGE,"E3756");var subQ436=sQuery(id+"F0.wireOp",EDGE,"E3755");var subQ437=sQuery(id+"F0.wireOp",EDGE,"E3754");var subQ438=sQuery(id+"F0.wireOp",EDGE,"E3753");var subQ439=sQuery(id+"F0.wireOp",EDGE,"E3752");var subQ440=sQuery(id+"F0.wireOp",EDGE,"E3751");var subQ441=sQuery(id+"F0.wireOp",EDGE,"E3750");var subQ442=sQuery(id+"F0.wireOp",EDGE,"E3749");var subQ443=sQuery(id+"F0.wireOp",EDGE,"E3748");var subQ444=sQuery(id+"F0.wireOp",EDGE,"E3747");var subQ445=sQuery(id+"F0.wireOp",EDGE,"E3746");var subQ446=sQuery(id+"F0.wireOp",EDGE,"E3745");var subQ447=sQuery(id+"F0.wireOp",EDGE,"E3744");var subQ448=sQuery(id+"F0.wireOp",EDGE,"E3743");var subQ449=sQuery(id+"F0.wireOp",EDGE,"E3742");var subQ450=sQuery(id+"F0.wireOp",EDGE,"E3741");var subQ451=sQuery(id+"F0.wireOp",EDGE,"E3740");var subQ452=sQuery(id+"F0.wireOp",EDGE,"E3739");var subQ453=sQuery(id+"F0.wireOp",EDGE,"E3738");var subQ454=sQuery(id+"F0.wireOp",EDGE,"E3737");var subQ455=sQuery(id+"F0.wireOp",EDGE,"E3736");var subQ456=sQuery(id+"F0.wireOp",EDGE,"E3735");var subQ457=sQuery(id+"F0.wireOp",EDGE,"E3734");var subQ458=sQuery(id+"F0.wireOp",EDGE,"E3733");var subQ459=sQuery(id+"F0.wireOp",EDGE,"E3732");var subQ460=sQuery(id+"F0.wireOp",EDGE,"E3731");var subQ461=sQuery(id+"F0.wireOp",EDGE,"E3730");var subQ462=sQuery(id+"F0.wireOp",EDGE,"E3729");var subQ463=sQuery(id+"F0.wireOp",EDGE,"E3728");var subQ464=sQuery(id+"F0.wireOp",EDGE,"E3727");var subQ465=sQuery(id+"F0.wireOp",EDGE,"E3726");var subQ466=sQuery(id+"F0.wireOp",EDGE,"E3725");var subQ467=sQuery(id+"F0.wireOp",EDGE,"E3724");var subQ468=sQuery(id+"F0.wireOp",EDGE,"E3723");var subQ469=sQuery(id+"F0.wireOp",EDGE,"E3722");var subQ470=sQuery(id+"F0.wireOp",EDGE,"E3721");var subQ471=sQuery(id+"F0.wireOp",EDGE,"E3720");var subQ472=sQuery(id+"F0.wireOp",EDGE,"E3719");var subQ473=sQuery(id+"F0.wireOp",EDGE,"E3718");var subQ474=sQuery(id+"F0.wireOp",EDGE,"E3717");var subQ475=sQuery(id+"F0.wireOp",EDGE,"E3716");var subQ476=sQuery(id+"F0.wireOp",EDGE,"E3715");var subQ477=sQuery(id+"F0.wireOp",EDGE,"E3714");var subQ478=sQuery(id+"F0.wireOp",EDGE,"E3713");var subQ479=sQuery(id+"F0.wireOp",EDGE,"E3712");var subQ480=sQuery(id+"F0.wireOp",EDGE,"E3711");var subQ481=sQuery(id+"F0.wireOp",EDGE,"E3710");var subQ482=sQuery(id+"F0.wireOp",EDGE,"E3709");var subQ483=sQuery(id+"F0.wireOp",EDGE,"E3708");var subQ484=sQuery(id+"F0.wireOp",EDGE,"E3707");var subQ485=sQuery(id+"F0.wireOp",EDGE,"E3706");var subQ486=sQuery(id+"F0.wireOp",EDGE,"E3705");var subQ487=sQuery(id+"F0.wireOp",EDGE,"E3704");var subQ488=sQuery(id+"F0.wireOp",EDGE,"E3703");var subQ489=sQuery(id+"F0.wireOp",EDGE,"E3702");var subQ490=sQuery(id+"F0.wireOp",EDGE,"E3701");var subQ491=sQuery(id+"F0.wireOp",EDGE,"E3700");var subQ492=sQuery(id+"F0.wireOp",EDGE,"E3699");var subQ493=sQuery(id+"F0.wireOp",EDGE,"E3698");var subQ494=sQuery(id+"F0.wireOp",EDGE,"E3697");var subQ495=sQuery(id+"F0.wireOp",EDGE,"E3696");var subQ496=sQuery(id+"F0.wireOp",EDGE,"E3695");var subQ497=sQuery(id+"F0.wireOp",EDGE,"E3694");var subQ498=sQuery(id+"F0.wireOp",EDGE,"E3693");var subQ499=sQuery(id+"F0.wireOp",EDGE,"E3692");var subQ500=sQuery(id+"F0.wireOp",EDGE,"E3691");var subQ501=sQuery(id+"F0.wireOp",EDGE,"E3690");var subQ502=sQuery(id+"F0.wireOp",EDGE,"E3689");var subQ503=sQuery(id+"F0.wireOp",EDGE,"E3688");var subQ504=sQuery(id+"F0.wireOp",EDGE,"E3687");var subQ505=sQuery(id+"F0.wireOp",EDGE,"E3686");var subQ506=sQuery(id+"F0.wireOp",EDGE,"E3685");var subQ507=sQuery(id+"F0.wireOp",EDGE,"E3684");var subQ508=sQuery(id+"F0.wireOp",EDGE,"E3683");var subQ509=sQuery(id+"F0.wireOp",EDGE,"E3682");var subQ510=sQuery(id+"F0.wireOp",EDGE,"E3681");var subQ511=sQuery(id+"F0.wireOp",EDGE,"E3680");var subQ512=sQuery(id+"F0.wireOp",EDGE,"E3679");var subQ513=sQuery(id+"F0.wireOp",EDGE,"E3678");var subQ514=sQuery(id+"F0.wireOp",EDGE,"E3677");var subQ515=sQuery(id+"F0.wireOp",EDGE,"E3676");var subQ516=sQuery(id+"F0.wireOp",EDGE,"E3675");var subQ517=sQuery(id+"F0.wireOp",EDGE,"E3674");var subQ518=sQuery(id+"F0.wireOp",EDGE,"E3673");var subQ519=sQuery(id+"F0.wireOp",EDGE,"E3672");var subQ520=sQuery(id+"F0.wireOp",EDGE,"E3671");var subQ521=sQuery(id+"F0.wireOp",EDGE,"E3670");var subQ522=sQuery(id+"F0.wireOp",EDGE,"E3669");var subQ523=sQuery(id+"F0.wireOp",EDGE,"E3668");var subQ524=sQuery(id+"F0.wireOp",EDGE,"E3667");var subQ525=sQuery(id+"F0.wireOp",EDGE,"E3666");var subQ526=sQuery(id+"F0.wireOp",EDGE,"E3665");var subQ527=sQuery(id+"F0.wireOp",EDGE,"E3664");var subQ528=sQuery(id+"F0.wireOp",EDGE,"E3663");var subQ529=sQuery(id+"F0.wireOp",EDGE,"E3662");var subQ530=sQuery(id+"F0.wireOp",EDGE,"E3661");var subQ531=sQuery(id+"F0.wireOp",EDGE,"E3660");var subQ532=sQuery(id+"F0.wireOp",EDGE,"E3659");var subQ533=sQuery(id+"F0.wireOp",EDGE,"E3658");var subQ534=sQuery(id+"F0.wireOp",EDGE,"E3657");var subQ535=sQuery(id+"F0.wireOp",EDGE,"E3656");var subQ536=sQuery(id+"F0.wireOp",EDGE,"E3655");var subQ537=sQuery(id+"F0.wireOp",EDGE,"E3654");var subQ538=sQuery(id+"F0.wireOp",EDGE,"E3653");var subQ539=sQuery(id+"F0.wireOp",EDGE,"E3652");var subQ540=sQuery(id+"F0.wireOp",EDGE,"E3651");var subQ541=sQuery(id+"F0.wireOp",EDGE,"E3650");var subQ542=sQuery(id+"F0.wireOp",EDGE,"E3649");var subQ543=sQuery(id+"F0.wireOp",EDGE,"E3648");var subQ544=sQuery(id+"F0.wireOp",EDGE,"E3647");var subQ545=sQuery(id+"F0.wireOp",EDGE,"E3646");var subQ546=sQuery(id+"F0.wireOp",EDGE,"E3645");var subQ547=sQuery(id+"F0.wireOp",EDGE,"E3644");var subQ548=sQuery(id+"F0.wireOp",EDGE,"E3643");var subQ549=sQuery(id+"F0.wireOp",EDGE,"E3642");var subQ550=sQuery(id+"F0.wireOp",EDGE,"E3641");var subQ551=sQuery(id+"F0.wireOp",EDGE,"E3640");var subQ552=sQuery(id+"F0.wireOp",EDGE,"E3639");var subQ553=sQuery(id+"F0.wireOp",EDGE,"E3638");var subQ554=sQuery(id+"F0.wireOp",EDGE,"E3637");var subQ555=sQuery(id+"F0.wireOp",EDGE,"E3636");var subQ556=sQuery(id+"F0.wireOp",EDGE,"E3635");var subQ557=sQuery(id+"F0.wireOp",EDGE,"E3634");var subQ558=sQuery(id+"F0.wireOp",EDGE,"E3633");var subQ559=sQuery(id+"F0.wireOp",EDGE,"E3632");var subQ560=sQuery(id+"F0.wireOp",EDGE,"E3631");var subQ561=sQuery(id+"F0.wireOp",EDGE,"E3630");var subQ562=sQuery(id+"F0.wireOp",EDGE,"E3629");var subQ563=sQuery(id+"F0.wireOp",EDGE,"E3628");var subQ564=sQuery(id+"F0.wireOp",EDGE,"E3627");var subQ565=sQuery(id+"F0.wireOp",EDGE,"E3626");var subQ566=sQuery(id+"F0.wireOp",EDGE,"E3625");var subQ567=sQuery(id+"F0.wireOp",EDGE,"E3624");var subQ568=sQuery(id+"F0.wireOp",EDGE,"E3623");var subQ569=sQuery(id+"F0.wireOp",EDGE,"E3622");var subQ570=sQuery(id+"F0.wireOp",EDGE,"E3621");var subQ571=sQuery(id+"F0.wireOp",EDGE,"E3620");var subQ572=sQuery(id+"F0.wireOp",EDGE,"E3619");var subQ573=sQuery(id+"F0.wireOp",EDGE,"E3618");var subQ574=sQuery(id+"F0.wireOp",EDGE,"E3617");var subQ575=sQuery(id+"F0.wireOp",EDGE,"E3616");var subQ576=sQuery(id+"F0.wireOp",EDGE,"E3615");var subQ577=sQuery(id+"F0.wireOp",EDGE,"E3614");var subQ578=sQuery(id+"F0.wireOp",EDGE,"E3613");var subQ579=sQuery(id+"F0.wireOp",EDGE,"E3612");var subQ580=sQuery(id+"F0.wireOp",EDGE,"E3611");var subQ581=sQuery(id+"F0.wireOp",EDGE,"E3610");var subQ582=sQuery(id+"F0.wireOp",EDGE,"E3609");var subQ583=sQuery(id+"F0.wireOp",EDGE,"E3608");var subQ584=sQuery(id+"F0.wireOp",EDGE,"E3607");var subQ585=sQuery(id+"F0.wireOp",EDGE,"E3606");var subQ586=sQuery(id+"F0.wireOp",EDGE,"E3605");var subQ587=sQuery(id+"F0.wireOp",EDGE,"E3604");var subQ588=sQuery(id+"F0.wireOp",EDGE,"E3603");var subQ589=sQuery(id+"F0.wireOp",EDGE,"E3602");var subQ590=sQuery(id+"F0.wireOp",EDGE,"E3601");var subQ591=sQuery(id+"F0.wireOp",EDGE,"E3600");var subQ592=sQuery(id+"F0.wireOp",EDGE,"E3599");var subQ593=sQuery(id+"F0.wireOp",EDGE,"E3598");var subQ594=sQuery(id+"F0.wireOp",EDGE,"E3597");var subQ595=sQuery(id+"F0.wireOp",EDGE,"E3596");var subQ596=sQuery(id+"F0.wireOp",EDGE,"E3595");var subQ597=sQuery(id+"F0.wireOp",EDGE,"E3594");var subQ598=sQuery(id+"F0.wireOp",EDGE,"E3593");var subQ599=sQuery(id+"F0.wireOp",EDGE,"E3592");var subQ600=sQuery(id+"F0.wireOp",EDGE,"E3591");var subQ601=sQuery(id+"F0.wireOp",EDGE,"E3590");var subQ602=sQuery(id+"F0.wireOp",EDGE,"E3589");var subQ603=sQuery(id+"F0.wireOp",EDGE,"E3588");var subQ604=sQuery(id+"F0.wireOp",EDGE,"E3587");var subQ605=sQuery(id+"F0.wireOp",EDGE,"E3586");var subQ606=sQuery(id+"F0.wireOp",EDGE,"E3585");var subQ607=sQuery(id+"F0.wireOp",EDGE,"E3584");var subQ608=sQuery(id+"F0.wireOp",EDGE,"E3583");var subQ609=sQuery(id+"F0.wireOp",EDGE,"E3582");var subQ610=sQuery(id+"F0.wireOp",EDGE,"E3581");var subQ611=sQuery(id+"F0.wireOp",EDGE,"E3580");var subQ612=sQuery(id+"F0.wireOp",EDGE,"E3579");var subQ613=sQuery(id+"F0.wireOp",EDGE,"E3578");var subQ614=sQuery(id+"F0.wireOp",EDGE,"E3577");var subQ615=sQuery(id+"F0.wireOp",EDGE,"E3576");var subQ616=sQuery(id+"F0.wireOp",EDGE,"E3575");var subQ617=sQuery(id+"F0.wireOp",EDGE,"E3574");var subQ618=sQuery(id+"F0.wireOp",EDGE,"E3573");var subQ619=sQuery(id+"F0.wireOp",EDGE,"E3572");var subQ620=sQuery(id+"F0.wireOp",EDGE,"E3571");var subQ621=sQuery(id+"F0.wireOp",EDGE,"E3570");var subQ622=sQuery(id+"F0.wireOp",EDGE,"E3569");var subQ623=sQuery(id+"F0.wireOp",EDGE,"E3568");var subQ624=sQuery(id+"F0.wireOp",EDGE,"E3567");var subQ625=sQuery(id+"F0.wireOp",EDGE,"E3566");var subQ626=sQuery(id+"F0.wireOp",EDGE,"E3565");var subQ627=sQuery(id+"F0.wireOp",EDGE,"E3564");var subQ628=sQuery(id+"F0.wireOp",EDGE,"E3563");var subQ629=sQuery(id+"F0.wireOp",EDGE,"E3562");var subQ630=sQuery(id+"F0.wireOp",EDGE,"E3561");var subQ631=sQuery(id+"F0.wireOp",EDGE,"E3560");var subQ632=sQuery(id+"F0.wireOp",EDGE,"E3559");var subQ633=sQuery(id+"F0.wireOp",EDGE,"E3558");var subQ634=sQuery(id+"F0.wireOp",EDGE,"E3557");var subQ635=sQuery(id+"F0.wireOp",EDGE,"E3556");var subQ636=sQuery(id+"F0.wireOp",EDGE,"E3555");var subQ637=sQuery(id+"F0.wireOp",EDGE,"E3554");var subQ638=sQuery(id+"F0.wireOp",EDGE,"E3553");var subQ639=sQuery(id+"F0.wireOp",EDGE,"E3552");var subQ640=sQuery(id+"F0.wireOp",EDGE,"E3551");var subQ641=sQuery(id+"F0.wireOp",EDGE,"E3550");var subQ642=sQuery(id+"F0.wireOp",EDGE,"E3549");var subQ643=sQuery(id+"F0.wireOp",EDGE,"E3548");var subQ644=sQuery(id+"F0.wireOp",EDGE,"E3547");var subQ645=sQuery(id+"F0.wireOp",EDGE,"E3546");var subQ646=sQuery(id+"F0.wireOp",EDGE,"E3545");var subQ647=sQuery(id+"F0.wireOp",EDGE,"E3544");var subQ648=sQuery(id+"F0.wireOp",EDGE,"E3543");var subQ649=sQuery(id+"F0.wireOp",EDGE,"E3542");var subQ650=sQuery(id+"F0.wireOp",EDGE,"E3541");var subQ651=sQuery(id+"F0.wireOp",EDGE,"E3540");var subQ652=sQuery(id+"F0.wireOp",EDGE,"E3539");var subQ653=sQuery(id+"F0.wireOp",EDGE,"E3538");var subQ654=sQuery(id+"F0.wireOp",EDGE,"E3537");var subQ655=sQuery(id+"F0.wireOp",EDGE,"E3536");var subQ656=sQuery(id+"F0.wireOp",EDGE,"E3535");var subQ657=sQuery(id+"F0.wireOp",EDGE,"E3534");var subQ658=sQuery(id+"F0.wireOp",EDGE,"E3533");var subQ659=sQuery(id+"F0.wireOp",EDGE,"E3532");var subQ660=sQuery(id+"F0.wireOp",EDGE,"E3531");var subQ661=sQuery(id+"F0.wireOp",EDGE,"E3530");var subQ662=sQuery(id+"F0.wireOp",EDGE,"E3529");var subQ663=sQuery(id+"F0.wireOp",EDGE,"E3528");var subQ664=sQuery(id+"F0.wireOp",EDGE,"E3527");var subQ665=sQuery(id+"F0.wireOp",EDGE,"E3526");var subQ666=sQuery(id+"F0.wireOp",EDGE,"E3525");var subQ667=sQuery(id+"F0.wireOp",EDGE,"E3524");var subQ668=sQuery(id+"F0.wireOp",EDGE,"E3523");var subQ669=sQuery(id+"F0.wireOp",EDGE,"E3522");var subQ670=sQuery(id+"F0.wireOp",EDGE,"E3521");var subQ671=sQuery(id+"F0.wireOp",EDGE,"E3520");var subQ672=sQuery(id+"F0.wireOp",EDGE,"E3519");var subQ673=sQuery(id+"F0.wireOp",EDGE,"E3518");var subQ674=sQuery(id+"F0.wireOp",EDGE,"E3517");var subQ675=sQuery(id+"F0.wireOp",EDGE,"E3516");var subQ676=sQuery(id+"F0.wireOp",EDGE,"E3515");var subQ677=sQuery(id+"F0.wireOp",EDGE,"E3514");var subQ678=sQuery(id+"F0.wireOp",EDGE,"E3513");var subQ679=sQuery(id+"F0.wireOp",EDGE,"E3512");var subQ680=sQuery(id+"F0.wireOp",EDGE,"E3511");var subQ681=sQuery(id+"F0.wireOp",EDGE,"E3510");var subQ682=sQuery(id+"F0.wireOp",EDGE,"E3509");var subQ683=sQuery(id+"F0.wireOp",EDGE,"E3508");var subQ684=sQuery(id+"F0.wireOp",EDGE,"E3507");var subQ685=sQuery(id+"F0.wireOp",EDGE,"E3506");var subQ686=sQuery(id+"F0.wireOp",EDGE,"E3505");var subQ687=sQuery(id+"F0.wireOp",EDGE,"E3504");var subQ688=sQuery(id+"F0.wireOp",EDGE,"E3503");var subQ689=sQuery(id+"F0.wireOp",EDGE,"E3502");var subQ690=sQuery(id+"F0.wireOp",EDGE,"E3501");var subQ691=sQuery(id+"F0.wireOp",EDGE,"E3500");var subQ692=sQuery(id+"F0.wireOp",EDGE,"E3499");var subQ693=sQuery(id+"F0.wireOp",EDGE,"E3498");var subQ694=sQuery(id+"F0.wireOp",EDGE,"E3497");var subQ695=sQuery(id+"F0.wireOp",EDGE,"E3496");var subQ696=sQuery(id+"F0.wireOp",EDGE,"E3495");var subQ697=sQuery(id+"F0.wireOp",EDGE,"E3494");var subQ698=sQuery(id+"F0.wireOp",EDGE,"E3493");var subQ699=sQuery(id+"F0.wireOp",EDGE,"E3492");var subQ700=sQuery(id+"F0.wireOp",EDGE,"E3491");var subQ701=sQuery(id+"F0.wireOp",EDGE,"E3490");var subQ702=sQuery(id+"F0.wireOp",EDGE,"E3489");var subQ703=sQuery(id+"F0.wireOp",EDGE,"E3488");var subQ704=sQuery(id+"F0.wireOp",EDGE,"E3487");var subQ705=sQuery(id+"F0.wireOp",EDGE,"E3486");var subQ706=sQuery(id+"F0.wireOp",EDGE,"E3485");var subQ707=sQuery(id+"F0.wireOp",EDGE,"E3484");var subQ708=sQuery(id+"F0.wireOp",EDGE,"E3483");var subQ709=sQuery(id+"F0.wireOp",EDGE,"E3482");var subQ710=sQuery(id+"F0.wireOp",EDGE,"E3481");var subQ711=sQuery(id+"F0.wireOp",EDGE,"E3480");var subQ712=sQuery(id+"F0.wireOp",EDGE,"E3479");var subQ713=sQuery(id+"F0.wireOp",EDGE,"E3478");var subQ714=sQuery(id+"F0.wireOp",EDGE,"E3477");var subQ715=sQuery(id+"F0.wireOp",EDGE,"E3476");var subQ716=sQuery(id+"F0.wireOp",EDGE,"E3475");var subQ717=sQuery(id+"F0.wireOp",EDGE,"E3474");var subQ718=sQuery(id+"F0.wireOp",EDGE,"E3473");var subQ719=sQuery(id+"F0.wireOp",EDGE,"E3472");var subQ720=sQuery(id+"F0.wireOp",EDGE,"E3471");var subQ721=sQuery(id+"F0.wireOp",EDGE,"E3470");var subQ722=sQuery(id+"F0.wireOp",EDGE,"E3469");var subQ723=sQuery(id+"F0.wireOp",EDGE,"E3468");var subQ724=sQuery(id+"F0.wireOp",EDGE,"E3467");var subQ725=sQuery(id+"F0.wireOp",EDGE,"E3466");var subQ726=sQuery(id+"F0.wireOp",EDGE,"E3465");var subQ727=sQuery(id+"F0.wireOp",EDGE,"E3464");var subQ728=sQuery(id+"F0.wireOp",EDGE,"E3463");var subQ729=sQuery(id+"F0.wireOp",EDGE,"E3462");var subQ730=sQuery(id+"F0.wireOp",EDGE,"E3461");var subQ731=sQuery(id+"F0.wireOp",EDGE,"E3460");var subQ732=sQuery(id+"F0.wireOp",EDGE,"E3459");var subQ733=sQuery(id+"F0.wireOp",EDGE,"E3458");var subQ734=sQuery(id+"F0.wireOp",EDGE,"E3457");var subQ735=sQuery(id+"F0.wireOp",EDGE,"E3456");var subQ736=sQuery(id+"F0.wireOp",EDGE,"E3455");var subQ737=sQuery(id+"F0.wireOp",EDGE,"E3454");var subQ738=sQuery(id+"F0.wireOp",EDGE,"E3453");var subQ739=sQuery(id+"F0.wireOp",EDGE,"E3452");var subQ740=sQuery(id+"F0.wireOp",EDGE,"E3451");var subQ741=sQuery(id+"F0.wireOp",EDGE,"E3450");var subQ742=sQuery(id+"F0.wireOp",EDGE,"E3449");var subQ743=sQuery(id+"F0.wireOp",EDGE,"E3448");var subQ744=sQuery(id+"F0.wireOp",EDGE,"E3447");var subQ745=sQuery(id+"F0.wireOp",EDGE,"E3446");var subQ746=sQuery(id+"F0.wireOp",EDGE,"E3445");var subQ747=sQuery(id+"F0.wireOp",EDGE,"E3444");var subQ748=sQuery(id+"F0.wireOp",EDGE,"E3443");var subQ749=sQuery(id+"F0.wireOp",EDGE,"E3442");var subQ750=sQuery(id+"F0.wireOp",EDGE,"E3441");var subQ751=sQuery(id+"F0.wireOp",EDGE,"E3440");var subQ752=sQuery(id+"F0.wireOp",EDGE,"E3439");var subQ753=sQuery(id+"F0.wireOp",EDGE,"E3438");var subQ754=sQuery(id+"F0.wireOp",EDGE,"E3437");var subQ755=sQuery(id+"F0.wireOp",EDGE,"E3436");var subQ756=sQuery(id+"F0.wireOp",EDGE,"E3435");var subQ757=sQuery(id+"F0.wireOp",EDGE,"E3434");var subQ758=sQuery(id+"F0.wireOp",EDGE,"E3433");var subQ759=sQuery(id+"F0.wireOp",EDGE,"E3432");var subQ760=sQuery(id+"F0.wireOp",EDGE,"E3431");var subQ761=sQuery(id+"F0.wireOp",EDGE,"E3430");var subQ762=sQuery(id+"F0.wireOp",EDGE,"E3429");var subQ763=sQuery(id+"F0.wireOp",EDGE,"E3428");var subQ764=sQuery(id+"F0.wireOp",EDGE,"E3427");var subQ765=sQuery(id+"F0.wireOp",EDGE,"E3426");var subQ766=sQuery(id+"F0.wireOp",EDGE,"E3425");var subQ767=sQuery(id+"F0.wireOp",EDGE,"E3424");var subQ768=sQuery(id+"F0.wireOp",EDGE,"E3423");var subQ769=sQuery(id+"F0.wireOp",EDGE,"E3422");var subQ770=sQuery(id+"F0.wireOp",EDGE,"E3421");var subQ771=sQuery(id+"F0.wireOp",EDGE,"E3420");var subQ772=sQuery(id+"F0.wireOp",EDGE,"E3419");var subQ773=sQuery(id+"F0.wireOp",EDGE,"E3418");var subQ774=sQuery(id+"F0.wireOp",EDGE,"E3417");var subQ775=sQuery(id+"F0.wireOp",EDGE,"E3416");var subQ776=sQuery(id+"F0.wireOp",EDGE,"E3415");var subQ777=sQuery(id+"F0.wireOp",EDGE,"E3414");var subQ778=sQuery(id+"F0.wireOp",EDGE,"E3413");var subQ779=sQuery(id+"F0.wireOp",EDGE,"E3412");var subQ780=sQuery(id+"F0.wireOp",EDGE,"E3411");var subQ781=sQuery(id+"F0.wireOp",EDGE,"E3410");var subQ782=sQuery(id+"F0.wireOp",EDGE,"E3409");var subQ783=sQuery(id+"F0.wireOp",EDGE,"E3408");var subQ784=sQuery(id+"F0.wireOp",EDGE,"E3407");var subQ785=sQuery(id+"F0.wireOp",EDGE,"E3406");var subQ786=sQuery(id+"F0.wireOp",EDGE,"E3405");var subQ787=sQuery(id+"F0.wireOp",EDGE,"E3404");var subQ788=sQuery(id+"F0.wireOp",EDGE,"E3403");var subQ789=sQuery(id+"F0.wireOp",EDGE,"E3402");var subQ790=sQuery(id+"F0.wireOp",EDGE,"E3401");var subQ791=sQuery(id+"F0.wireOp",EDGE,"E3400");var subQ792=sQuery(id+"F0.wireOp",EDGE,"E3399");var subQ793=sQuery(id+"F0.wireOp",EDGE,"E3398");var subQ794=sQuery(id+"F0.wireOp",EDGE,"E3397");var subQ795=sQuery(id+"F0.wireOp",EDGE,"E3396");var subQ796=sQuery(id+"F0.wireOp",EDGE,"E3395");var subQ797=sQuery(id+"F0.wireOp",EDGE,"E3394");var subQ798=sQuery(id+"F0.wireOp",EDGE,"E3393");var subQ799=sQuery(id+"F0.wireOp",EDGE,"E3392");var subQ800=sQuery(id+"F0.wireOp",EDGE,"E3391");var subQ801=sQuery(id+"F0.wireOp",EDGE,"E3390");var subQ802=sQuery(id+"F0.wireOp",EDGE,"E3389");var subQ803=sQuery(id+"F0.wireOp",EDGE,"E3388");var subQ804=sQuery(id+"F0.wireOp",EDGE,"E3387");var subQ805=sQuery(id+"F0.wireOp",EDGE,"E3386");var subQ806=sQuery(id+"F0.wireOp",EDGE,"E3385");var subQ807=sQuery(id+"F0.wireOp",EDGE,"E3384");var subQ808=sQuery(id+"F0.wireOp",EDGE,"E3383");var subQ809=sQuery(id+"F0.wireOp",EDGE,"E3382");var subQ810=sQuery(id+"F0.wireOp",EDGE,"E3381");var subQ811=sQuery(id+"F0.wireOp",EDGE,"E3380");var subQ812=sQuery(id+"F0.wireOp",EDGE,"E3379");var subQ813=sQuery(id+"F0.wireOp",EDGE,"E3378");var subQ814=sQuery(id+"F0.wireOp",EDGE,"E3377");var subQ815=sQuery(id+"F0.wireOp",EDGE,"E3376");var subQ816=sQuery(id+"F0.wireOp",EDGE,"E3375");var subQ817=sQuery(id+"F0.wireOp",EDGE,"E3374");var subQ818=sQuery(id+"F0.wireOp",EDGE,"E3373");var subQ819=sQuery(id+"F0.wireOp",EDGE,"E3372");var subQ820=sQuery(id+"F0.wireOp",EDGE,"E3371");var subQ821=sQuery(id+"F0.wireOp",EDGE,"E3370");var subQ822=sQuery(id+"F0.wireOp",EDGE,"E3369");var subQ823=sQuery(id+"F0.wireOp",EDGE,"E3368");var subQ824=sQuery(id+"F0.wireOp",EDGE,"E3367");var subQ825=sQuery(id+"F0.wireOp",EDGE,"E3366");var subQ826=sQuery(id+"F0.wireOp",EDGE,"E3365");var subQ827=sQuery(id+"F0.wireOp",EDGE,"E3364");var subQ828=sQuery(id+"F0.wireOp",EDGE,"E3363");var subQ829=sQuery(id+"F0.wireOp",EDGE,"E3362");var subQ830=sQuery(id+"F0.wireOp",EDGE,"E3361");var subQ831=sQuery(id+"F0.wireOp",EDGE,"E3360");var subQ832=sQuery(id+"F0.wireOp",EDGE,"E3359");var subQ833=sQuery(id+"F0.wireOp",EDGE,"E3358");var subQ834=sQuery(id+"F0.wireOp",EDGE,"E3357");var subQ835=sQuery(id+"F0.wireOp",EDGE,"E3356");var subQ836=sQuery(id+"F0.wireOp",EDGE,"E3355");var subQ837=sQuery(id+"F0.wireOp",EDGE,"E3354");var subQ838=sQuery(id+"F0.wireOp",EDGE,"E3353");var subQ839=sQuery(id+"F0.wireOp",EDGE,"E3352");var subQ840=sQuery(id+"F0.wireOp",EDGE,"E3351");var subQ841=sQuery(id+"F0.wireOp",EDGE,"E3350");var subQ842=sQuery(id+"F0.wireOp",EDGE,"E3349");var subQ843=sQuery(id+"F0.wireOp",EDGE,"E3348");var subQ844=sQuery(id+"F0.wireOp",EDGE,"E3347");var subQ845=sQuery(id+"F0.wireOp",EDGE,"E3346");var subQ846=sQuery(id+"F0.wireOp",EDGE,"E3345");var subQ847=sQuery(id+"F0.wireOp",EDGE,"E3344");var subQ848=sQuery(id+"F0.wireOp",EDGE,"E3343");var subQ849=sQuery(id+"F0.wireOp",EDGE,"E3342");var subQ850=sQuery(id+"F0.wireOp",EDGE,"E3341");var subQ851=sQuery(id+"F0.wireOp",EDGE,"E3340");var subQ852=sQuery(id+"F0.wireOp",EDGE,"E3339");var subQ853=sQuery(id+"F0.wireOp",EDGE,"E3338");var subQ854=sQuery(id+"F0.wireOp",EDGE,"E3337");var subQ855=sQuery(id+"F0.wireOp",EDGE,"E3336");var subQ856=sQuery(id+"F0.wireOp",EDGE,"E3335");var subQ857=sQuery(id+"F0.wireOp",EDGE,"E3334");var subQ858=sQuery(id+"F0.wireOp",EDGE,"E3333");var subQ859=sQuery(id+"F0.wireOp",EDGE,"E3332");var subQ860=sQuery(id+"F0.wireOp",EDGE,"E3331");var subQ861=sQuery(id+"F0.wireOp",EDGE,"E3330");var subQ862=sQuery(id+"F0.wireOp",EDGE,"E3329");var subQ863=sQuery(id+"F0.wireOp",EDGE,"E3328");var subQ864=sQuery(id+"F0.wireOp",EDGE,"E3327");var subQ865=sQuery(id+"F0.wireOp",EDGE,"E3326");var subQ866=sQuery(id+"F0.wireOp",EDGE,"E3325");var subQ867=sQuery(id+"F0.wireOp",EDGE,"E3324");var subQ868=sQuery(id+"F0.wireOp",EDGE,"E3323");var subQ869=sQuery(id+"F0.wireOp",EDGE,"E3322");var subQ870=sQuery(id+"F0.wireOp",EDGE,"E3321");var subQ871=sQuery(id+"F0.wireOp",EDGE,"E3320");var subQ872=sQuery(id+"F0.wireOp",EDGE,"E3319");var subQ873=sQuery(id+"F0.wireOp",EDGE,"E3318");var subQ874=sQuery(id+"F0.wireOp",EDGE,"E3317");var subQ875=sQuery(id+"F0.wireOp",EDGE,"E3316");var subQ876=sQuery(id+"F0.wireOp",EDGE,"E3315");var subQ877=sQuery(id+"F0.wireOp",EDGE,"E3314");var subQ878=sQuery(id+"F0.wireOp",EDGE,"E3313");var subQ879=sQuery(id+"F0.wireOp",EDGE,"E3312");var subQ880=sQuery(id+"F0.wireOp",EDGE,"E3311");var subQ881=sQuery(id+"F0.wireOp",EDGE,"E3310");var subQ882=sQuery(id+"F0.wireOp",EDGE,"E3309");var subQ883=sQuery(id+"F0.wireOp",EDGE,"E3308");var subQ884=sQuery(id+"F0.wireOp",EDGE,"E3307");var subQ885=sQuery(id+"F0.wireOp",EDGE,"E3306");var subQ886=sQuery(id+"F0.wireOp",EDGE,"E3305");var subQ887=sQuery(id+"F0.wireOp",EDGE,"E3304");var subQ888=sQuery(id+"F0.wireOp",EDGE,"E3303");var subQ889=sQuery(id+"F0.wireOp",EDGE,"E3302");var subQ890=sQuery(id+"F0.wireOp",EDGE,"E3301");var subQ891=sQuery(id+"F0.wireOp",EDGE,"E3300");var subQ892=sQuery(id+"F0.wireOp",EDGE,"E3299");var subQ893=sQuery(id+"F0.wireOp",EDGE,"E3298");var subQ894=sQuery(id+"F0.wireOp",EDGE,"E3297");var subQ895=sQuery(id+"F0.wireOp",EDGE,"E3296");var subQ896=sQuery(id+"F0.wireOp",EDGE,"E3295");var subQ897=sQuery(id+"F0.wireOp",EDGE,"E3294");var subQ898=sQuery(id+"F0.wireOp",EDGE,"E3293");var subQ899=sQuery(id+"F0.wireOp",EDGE,"E3292");var subQ900=sQuery(id+"F0.wireOp",EDGE,"E3291");var subQ901=sQuery(id+"F0.wireOp",EDGE,"E3290");var subQ902=sQuery(id+"F0.wireOp",EDGE,"E3289");var subQ903=sQuery(id+"F0.wireOp",EDGE,"E3288");var subQ904=sQuery(id+"F0.wireOp",EDGE,"E3287");var subQ905=sQuery(id+"F0.wireOp",EDGE,"E3286");var subQ906=sQuery(id+"F0.wireOp",EDGE,"E3285");var subQ907=sQuery(id+"F0.wireOp",EDGE,"E3284");var subQ908=sQuery(id+"F0.wireOp",EDGE,"E3283");var subQ909=sQuery(id+"F0.wireOp",EDGE,"E3282");var subQ910=sQuery(id+"F0.wireOp",EDGE,"E3281");var subQ911=sQuery(id+"F0.wireOp",EDGE,"E3280");var subQ912=sQuery(id+"F0.wireOp",EDGE,"E3279");var subQ913=sQuery(id+"F0.wireOp",EDGE,"E3278");var subQ914=sQuery(id+"F0.wireOp",EDGE,"E3277");var subQ915=sQuery(id+"F0.wireOp",EDGE,"E3276");var subQ916=sQuery(id+"F0.wireOp",EDGE,"E3275");var subQ917=sQuery(id+"F0.wireOp",EDGE,"E3274");var subQ918=sQuery(id+"F0.wireOp",EDGE,"E3273");var subQ919=sQuery(id+"F0.wireOp",EDGE,"E3272");var subQ920=sQuery(id+"F0.wireOp",EDGE,"E3271");var subQ921=sQuery(id+"F0.wireOp",EDGE,"E3270");var subQ922=sQuery(id+"F0.wireOp",EDGE,"E3269");var subQ923=sQuery(id+"F0.wireOp",EDGE,"E3268");var subQ924=sQuery(id+"F0.wireOp",EDGE,"E3267");var subQ925=sQuery(id+"F0.wireOp",EDGE,"E3266");var subQ926=sQuery(id+"F0.wireOp",EDGE,"E3265");var subQ927=sQuery(id+"F0.wireOp",EDGE,"E3264");var subQ928=sQuery(id+"F0.wireOp",EDGE,"E3263");var subQ929=sQuery(id+"F0.wireOp",EDGE,"E3262");var subQ930=sQuery(id+"F0.wireOp",EDGE,"E3261");var subQ931=sQuery(id+"F0.wireOp",EDGE,"E3260");var subQ932=sQuery(id+"F0.wireOp",EDGE,"E3259");var subQ933=sQuery(id+"F0.wireOp",EDGE,"E3258");var subQ934=sQuery(id+"F0.wireOp",EDGE,"E3257");var subQ935=sQuery(id+"F0.wireOp",EDGE,"E3256");var subQ936=sQuery(id+"F0.wireOp",EDGE,"E3255");var subQ937=sQuery(id+"F0.wireOp",EDGE,"E3254");var subQ938=sQuery(id+"F0.wireOp",EDGE,"E3253");var subQ939=sQuery(id+"F0.wireOp",EDGE,"E3252");var subQ940=sQuery(id+"F0.wireOp",EDGE,"E3251");var subQ941=sQuery(id+"F0.wireOp",EDGE,"E3250");var subQ942=sQuery(id+"F0.wireOp",EDGE,"E3249");var subQ943=sQuery(id+"F0.wireOp",EDGE,"E3248");var subQ944=sQuery(id+"F0.wireOp",EDGE,"E3247");var subQ945=sQuery(id+"F0.wireOp",EDGE,"E3246");var subQ946=sQuery(id+"F0.wireOp",EDGE,"E3245");var subQ947=sQuery(id+"F0.wireOp",EDGE,"E3244");var subQ948=sQuery(id+"F0.wireOp",EDGE,"E3243");var subQ949=sQuery(id+"F0.wireOp",EDGE,"E3242");var subQ950=sQuery(id+"F0.wireOp",EDGE,"E3241");var subQ951=sQuery(id+"F0.wireOp",EDGE,"E3240");var subQ952=sQuery(id+"F0.wireOp",EDGE,"E3239");var subQ953=sQuery(id+"F0.wireOp",EDGE,"E3238");var subQ954=sQuery(id+"F0.wireOp",EDGE,"E3237");var subQ955=sQuery(id+"F0.wireOp",EDGE,"E3236");var subQ956=sQuery(id+"F0.wireOp",EDGE,"E3235");var subQ957=sQuery(id+"F0.wireOp",EDGE,"E3234");var subQ958=sQuery(id+"F0.wireOp",EDGE,"E3233");var subQ959=sQuery(id+"F0.wireOp",EDGE,"E3232");var subQ960=sQuery(id+"F0.wireOp",EDGE,"E3231");var subQ961=sQuery(id+"F0.wireOp",EDGE,"E3230");var subQ962=sQuery(id+"F0.wireOp",EDGE,"E3229");var subQ963=sQuery(id+"F0.wireOp",EDGE,"E3228");var subQ964=sQuery(id+"F0.wireOp",EDGE,"E3227");var subQ965=sQuery(id+"F0.wireOp",EDGE,"E3226");var subQ966=sQuery(id+"F0.wireOp",EDGE,"E3225");var subQ967=sQuery(id+"F0.wireOp",EDGE,"E3224");var subQ968=sQuery(id+"F0.wireOp",EDGE,"E3223");var subQ969=sQuery(id+"F0.wireOp",EDGE,"E3222");var subQ970=sQuery(id+"F0.wireOp",EDGE,"E3221");var subQ971=sQuery(id+"F0.wireOp",EDGE,"E3220");var subQ972=sQuery(id+"F0.wireOp",EDGE,"E3219");var subQ973=sQuery(id+"F0.wireOp",EDGE,"E3218");var subQ974=sQuery(id+"F0.wireOp",EDGE,"E3217");var subQ975=sQuery(id+"F0.wireOp",EDGE,"E3216");var subQ976=sQuery(id+"F0.wireOp",EDGE,"E3215");var subQ977=sQuery(id+"F0.wireOp",EDGE,"E3214");var subQ978=sQuery(id+"F0.wireOp",EDGE,"E3213");var subQ979=sQuery(id+"F0.wireOp",EDGE,"E3212");var subQ980=sQuery(id+"F0.wireOp",EDGE,"E3211");var subQ981=sQuery(id+"F0.wireOp",EDGE,"E3210");var subQ982=sQuery(id+"F0.wireOp",EDGE,"E3209");var subQ983=sQuery(id+"F0.wireOp",EDGE,"E3208");var subQ984=sQuery(id+"F0.wireOp",EDGE,"E3207");var subQ985=sQuery(id+"F0.wireOp",EDGE,"E3206");var subQ986=sQuery(id+"F0.wireOp",EDGE,"E3205");var subQ987=sQuery(id+"F0.wireOp",EDGE,"E3204");var subQ988=sQuery(id+"F0.wireOp",EDGE,"E3203");var subQ989=sQuery(id+"F0.wireOp",EDGE,"E3202");var subQ990=sQuery(id+"F0.wireOp",EDGE,"E3201");var subQ991=sQuery(id+"F0.wireOp",EDGE,"E3200");var subQ992=sQuery(id+"F0.wireOp",EDGE,"E3199");var subQ993=sQuery(id+"F0.wireOp",EDGE,"E3198");var subQ994=sQuery(id+"F0.wireOp",EDGE,"E3197");var subQ995=sQuery(id+"F0.wireOp",EDGE,"E3196");var subQ996=sQuery(id+"F0.wireOp",EDGE,"E3195");var subQ997=sQuery(id+"F0.wireOp",EDGE,"E3194");var subQ998=sQuery(id+"F0.wireOp",EDGE,"E3193");var subQ999=sQuery(id+"F0.wireOp",EDGE,"E3192");var subQ1000=sQuery(id+"F0.wireOp",EDGE,"E3191");var subQ1001=sQuery(id+"F0.wireOp",EDGE,"E3190");var subQ1002=sQuery(id+"F0.wireOp",EDGE,"E3189");var subQ1003=sQuery(id+"F0.wireOp",EDGE,"E3188");var subQ1004=sQuery(id+"F0.wireOp",EDGE,"E3187");var subQ1005=sQuery(id+"F0.wireOp",EDGE,"E3186");var subQ1006=sQuery(id+"F0.wireOp",EDGE,"E3185");var subQ1007=sQuery(id+"F0.wireOp",EDGE,"E3184");var subQ1008=sQuery(id+"F0.wireOp",EDGE,"E3183");var subQ1009=sQuery(id+"F0.wireOp",EDGE,"E3182");var subQ1010=sQuery(id+"F0.wireOp",EDGE,"E3181");var subQ1011=sQuery(id+"F0.wireOp",EDGE,"E3180");var subQ1012=sQuery(id+"F0.wireOp",EDGE,"E3179");var subQ1013=sQuery(id+"F0.wireOp",EDGE,"E3178");var subQ1014=sQuery(id+"F0.wireOp",EDGE,"E3177");var subQ1015=sQuery(id+"F0.wireOp",EDGE,"E3176");var subQ1016=sQuery(id+"F0.wireOp",EDGE,"E3175");var subQ1017=sQuery(id+"F0.wireOp",EDGE,"E3174");var subQ1018=sQuery(id+"F0.wireOp",EDGE,"E3173");var subQ1019=sQuery(id+"F0.wireOp",EDGE,"E3172");var subQ1020=sQuery(id+"F0.wireOp",EDGE,"E3171");var subQ1021=sQuery(id+"F0.wireOp",EDGE,"E3170");var subQ1022=sQuery(id+"F0.wireOp",EDGE,"E3169");var subQ1023=sQuery(id+"F0.wireOp",EDGE,"E3168");var subQ1024=sQuery(id+"F0.wireOp",EDGE,"E3167");var subQ1025=sQuery(id+"F0.wireOp",EDGE,"E3166");var subQ1026=sQuery(id+"F0.wireOp",EDGE,"E3165");var subQ1027=sQuery(id+"F0.wireOp",EDGE,"E3164");var subQ1028=sQuery(id+"F0.wireOp",EDGE,"E3163");var subQ1029=sQuery(id+"F0.wireOp",EDGE,"E3162");var subQ1030=sQuery(id+"F0.wireOp",EDGE,"E3161");var subQ1031=sQuery(id+"F0.wireOp",EDGE,"E3160");var subQ1032=sQuery(id+"F0.wireOp",EDGE,"E3159");var subQ1033=sQuery(id+"F0.wireOp",EDGE,"E3158");var subQ1034=sQuery(id+"F0.wireOp",EDGE,"E3157");var subQ1035=sQuery(id+"F0.wireOp",EDGE,"E3156");var subQ1036=sQuery(id+"F0.wireOp",EDGE,"E3155");var subQ1037=sQuery(id+"F0.wireOp",EDGE,"E3154");var subQ1038=sQuery(id+"F0.wireOp",EDGE,"E3153");var subQ1039=sQuery(id+"F0.wireOp",EDGE,"E3152");var subQ1040=sQuery(id+"F0.wireOp",EDGE,"E3151");var subQ1041=sQuery(id+"F0.wireOp",EDGE,"E3150");var subQ1042=sQuery(id+"F0.wireOp",EDGE,"E3149");var subQ1043=sQuery(id+"F0.wireOp",EDGE,"E3148");var subQ1044=sQuery(id+"F0.wireOp",EDGE,"E3147");var subQ1045=sQuery(id+"F0.wireOp",EDGE,"E3146");var subQ1046=sQuery(id+"F0.wireOp",EDGE,"E3145");var subQ1047=sQuery(id+"F0.wireOp",EDGE,"E3144");var subQ1048=sQuery(id+"F0.wireOp",EDGE,"E3143");var subQ1049=sQuery(id+"F0.wireOp",EDGE,"E3142");var subQ1050=sQuery(id+"F0.wireOp",EDGE,"E3141");var subQ1051=sQuery(id+"F0.wireOp",EDGE,"E3140");var subQ1052=sQuery(id+"F0.wireOp",EDGE,"E3139");var subQ1053=sQuery(id+"F0.wireOp",EDGE,"E3138");var subQ1054=sQuery(id+"F0.wireOp",EDGE,"E3137");var subQ1055=sQuery(id+"F0.wireOp",EDGE,"E3136");var subQ1056=sQuery(id+"F0.wireOp",EDGE,"E3135");var subQ1057=sQuery(id+"F0.wireOp",EDGE,"E3134");var subQ1058=sQuery(id+"F0.wireOp",EDGE,"E3133");var subQ1059=sQuery(id+"F0.wireOp",EDGE,"E3132");var subQ1060=sQuery(id+"F0.wireOp",EDGE,"E3131");var subQ1061=sQuery(id+"F0.wireOp",EDGE,"E3130");var subQ1062=sQuery(id+"F0.wireOp",EDGE,"E3129");var subQ1063=sQuery(id+"F0.wireOp",EDGE,"E3128");var subQ1064=sQuery(id+"F0.wireOp",EDGE,"E3127");var subQ1065=sQuery(id+"F0.wireOp",EDGE,"E3126");var subQ1066=sQuery(id+"F0.wireOp",EDGE,"E3125");var subQ1067=sQuery(id+"F0.wireOp",EDGE,"E3124");var subQ1068=sQuery(id+"F0.wireOp",EDGE,"E3123");var subQ1069=sQuery(id+"F0.wireOp",EDGE,"E3122");var subQ1070=sQuery(id+"F0.wireOp",EDGE,"E3121");var subQ1071=sQuery(id+"F0.wireOp",EDGE,"E3120");var subQ1072=sQuery(id+"F0.wireOp",EDGE,"E3119");var subQ1073=sQuery(id+"F0.wireOp",EDGE,"E3118");var subQ1074=sQuery(id+"F0.wireOp",EDGE,"E3117");var subQ1075=sQuery(id+"F0.wireOp",EDGE,"E3116");var subQ1076=sQuery(id+"F0.wireOp",EDGE,"E3115");var subQ1077=sQuery(id+"F0.wireOp",EDGE,"E3114");var subQ1078=sQuery(id+"F0.wireOp",EDGE,"E3113");var subQ1079=sQuery(id+"F0.wireOp",EDGE,"E3112");var subQ1080=sQuery(id+"F0.wireOp",EDGE,"E3111");var subQ1081=sQuery(id+"F0.wireOp",EDGE,"E3110");var subQ1082=sQuery(id+"F0.wireOp",EDGE,"E3109");var subQ1083=sQuery(id+"F0.wireOp",EDGE,"E3108");var subQ1084=sQuery(id+"F0.wireOp",EDGE,"E3107");var subQ1085=sQuery(id+"F0.wireOp",EDGE,"E3106");var subQ1086=sQuery(id+"F0.wireOp",EDGE,"E3105");var subQ1087=sQuery(id+"F0.wireOp",EDGE,"E3104");var subQ1088=sQuery(id+"F0.wireOp",EDGE,"E3103");var subQ1089=sQuery(id+"F0.wireOp",EDGE,"E3102");var subQ1090=sQuery(id+"F0.wireOp",EDGE,"E3101");var subQ1091=sQuery(id+"F0.wireOp",EDGE,"E3100");var subQ1092=sQuery(id+"F0.wireOp",EDGE,"E3099");var subQ1093=sQuery(id+"F0.wireOp",EDGE,"E3098");var subQ1094=sQuery(id+"F0.wireOp",EDGE,"E3097");var subQ1095=sQuery(id+"F0.wireOp",EDGE,"E3096");var subQ1096=sQuery(id+"F0.wireOp",EDGE,"E3095");var subQ1097=sQuery(id+"F0.wireOp",EDGE,"E3094");var subQ1098=sQuery(id+"F0.wireOp",EDGE,"E3093");var subQ1099=sQuery(id+"F0.wireOp",EDGE,"E3092");var subQ1100=sQuery(id+"F0.wireOp",EDGE,"E3091");var subQ1101=sQuery(id+"F0.wireOp",EDGE,"E3090");var subQ1102=sQuery(id+"F0.wireOp",EDGE,"E3089");var subQ1103=sQuery(id+"F0.wireOp",EDGE,"E3088");var subQ1104=sQuery(id+"F0.wireOp",EDGE,"E3087");var subQ1105=sQuery(id+"F0.wireOp",EDGE,"E3086");var subQ1106=sQuery(id+"F0.wireOp",EDGE,"E3085");var subQ1107=sQuery(id+"F0.wireOp",EDGE,"E3084");var subQ1108=sQuery(id+"F0.wireOp",EDGE,"E3083");var subQ1109=sQuery(id+"F0.wireOp",EDGE,"E3082");var subQ1110=sQuery(id+"F0.wireOp",EDGE,"E3081");var subQ1111=sQuery(id+"F0.wireOp",EDGE,"E3080");var subQ1112=sQuery(id+"F0.wireOp",EDGE,"E3079");var subQ1113=sQuery(id+"F0.wireOp",EDGE,"E3078");var subQ1114=sQuery(id+"F0.wireOp",EDGE,"E3077");var subQ1115=sQuery(id+"F0.wireOp",EDGE,"E3076");var subQ1116=sQuery(id+"F0.wireOp",EDGE,"E3075");var subQ1117=sQuery(id+"F0.wireOp",EDGE,"E3074");var subQ1118=sQuery(id+"F0.wireOp",EDGE,"E3073");var subQ1119=sQuery(id+"F0.wireOp",EDGE,"E3072");var subQ1120=sQuery(id+"F0.wireOp",EDGE,"E3071");var subQ1121=sQuery(id+"F0.wireOp",EDGE,"E3070");var subQ1122=sQuery(id+"F0.wireOp",EDGE,"E3069");var subQ1123=sQuery(id+"F0.wireOp",EDGE,"E3068");var subQ1124=sQuery(id+"F0.wireOp",EDGE,"E3067");var subQ1125=sQuery(id+"F0.wireOp",EDGE,"E3066");var subQ1126=sQuery(id+"F0.wireOp",EDGE,"E3065");var subQ1127=sQuery(id+"F0.wireOp",EDGE,"E3064");var subQ1128=sQuery(id+"F0.wireOp",EDGE,"E3063");var subQ1129=sQuery(id+"F0.wireOp",EDGE,"E3062");var subQ1130=sQuery(id+"F0.wireOp",EDGE,"E3061");var subQ1131=sQuery(id+"F0.wireOp",EDGE,"E3060");var subQ1132=sQuery(id+"F0.wireOp",EDGE,"E3059");var subQ1133=sQuery(id+"F0.wireOp",EDGE,"E3058");var subQ1134=sQuery(id+"F0.wireOp",EDGE,"E3057");var subQ1135=sQuery(id+"F0.wireOp",EDGE,"E3056");var subQ1136=sQuery(id+"F0.wireOp",EDGE,"E3055");var subQ1137=sQuery(id+"F0.wireOp",EDGE,"E3054");var subQ1138=sQuery(id+"F0.wireOp",EDGE,"E3053");var subQ1139=sQuery(id+"F0.wireOp",EDGE,"E3052");var subQ1140=sQuery(id+"F0.wireOp",EDGE,"E3051");var subQ1141=sQuery(id+"F0.wireOp",EDGE,"E3050");var subQ1142=sQuery(id+"F0.wireOp",EDGE,"E3049");var subQ1143=sQuery(id+"F0.wireOp",EDGE,"E3048");var subQ1144=sQuery(id+"F0.wireOp",EDGE,"E3047");var subQ1145=sQuery(id+"F0.wireOp",EDGE,"E3046");var subQ1146=sQuery(id+"F0.wireOp",EDGE,"E3045");var subQ1147=sQuery(id+"F0.wireOp",EDGE,"E3044");var subQ1148=sQuery(id+"F0.wireOp",EDGE,"E3043");var subQ1149=sQuery(id+"F0.wireOp",EDGE,"E3042");var subQ1150=sQuery(id+"F0.wireOp",EDGE,"E3041");var subQ1151=sQuery(id+"F0.wireOp",EDGE,"E3040");var subQ1152=sQuery(id+"F0.wireOp",EDGE,"E3039");var subQ1153=sQuery(id+"F0.wireOp",EDGE,"E3038");var subQ1154=sQuery(id+"F0.wireOp",EDGE,"E3037");var subQ1155=sQuery(id+"F0.wireOp",EDGE,"E3036");var subQ1156=sQuery(id+"F0.wireOp",EDGE,"E3035");var subQ1157=sQuery(id+"F0.wireOp",EDGE,"E3034");var subQ1158=sQuery(id+"F0.wireOp",EDGE,"E3033");var subQ1159=sQuery(id+"F0.wireOp",EDGE,"E3032");var subQ1160=sQuery(id+"F0.wireOp",EDGE,"E3031");var subQ1161=sQuery(id+"F0.wireOp",EDGE,"E3030");var subQ1162=sQuery(id+"F0.wireOp",EDGE,"E3029");var subQ1163=sQuery(id+"F0.wireOp",EDGE,"E3028");var subQ1164=sQuery(id+"F0.wireOp",EDGE,"E3027");var subQ1165=sQuery(id+"F0.wireOp",EDGE,"E3026");var subQ1166=sQuery(id+"F0.wireOp",EDGE,"E3025");var subQ1167=sQuery(id+"F0.wireOp",EDGE,"E3024");var subQ1168=sQuery(id+"F0.wireOp",EDGE,"E3023");var subQ1169=sQuery(id+"F0.wireOp",EDGE,"E3022");var subQ1170=sQuery(id+"F0.wireOp",EDGE,"E3021");var subQ1171=sQuery(id+"F0.wireOp",EDGE,"E3020");var subQ1172=sQuery(id+"F0.wireOp",EDGE,"E3019");var subQ1173=sQuery(id+"F0.wireOp",EDGE,"E3018");var subQ1174=sQuery(id+"F0.wireOp",EDGE,"E3017");var subQ1175=sQuery(id+"F0.wireOp",EDGE,"E3016");var subQ1176=sQuery(id+"F0.wireOp",EDGE,"E3015");var subQ1177=sQuery(id+"F0.wireOp",EDGE,"E3014");var subQ1178=sQuery(id+"F0.wireOp",EDGE,"E3013");var subQ1179=sQuery(id+"F0.wireOp",EDGE,"E3012");var subQ1180=sQuery(id+"F0.wireOp",EDGE,"E3011");var subQ1181=sQuery(id+"F0.wireOp",EDGE,"E3010");var subQ1182=sQuery(id+"F0.wireOp",EDGE,"E3009");var subQ1183=sQuery(id+"F0.wireOp",EDGE,"E3008");var subQ1184=sQuery(id+"F0.wireOp",EDGE,"E3007");var subQ1185=sQuery(id+"F0.wireOp",EDGE,"E3006");var subQ1186=sQuery(id+"F0.wireOp",EDGE,"E3005");var subQ1187=sQuery(id+"F0.wireOp",EDGE,"E3004");var subQ1188=sQuery(id+"F0.wireOp",EDGE,"E3003");var subQ1189=sQuery(id+"F0.wireOp",EDGE,"E3002");var subQ1190=sQuery(id+"F0.wireOp",EDGE,"E3001");var subQ1191=sQuery(id+"F0.wireOp",EDGE,"E3000");var subQ1192=sQuery(id+"F0.wireOp",EDGE,"E2999");var subQ1193=sQuery(id+"F0.wireOp",EDGE,"E2998");var subQ1194=sQuery(id+"F0.wireOp",EDGE,"E2997");var subQ1195=sQuery(id+"F0.wireOp",EDGE,"E2996");var subQ1196=sQuery(id+"F0.wireOp",EDGE,"E2995");var subQ1197=sQuery(id+"F0.wireOp",EDGE,"E2994");var subQ1198=sQuery(id+"F0.wireOp",EDGE,"E2993");var subQ1199=sQuery(id+"F0.wireOp",EDGE,"E2992");var subQ1200=sQuery(id+"F0.wireOp",EDGE,"E2991");var subQ1201=sQuery(id+"F0.wireOp",EDGE,"E2990");var subQ1202=sQuery(id+"F0.wireOp",EDGE,"E2989");var subQ1203=sQuery(id+"F0.wireOp",EDGE,"E2988");var subQ1204=sQuery(id+"F0.wireOp",EDGE,"E2987");var subQ1205=sQuery(id+"F0.wireOp",EDGE,"E2986");var subQ1206=sQuery(id+"F0.wireOp",EDGE,"E2985");var subQ1207=sQuery(id+"F0.wireOp",EDGE,"E2984");var subQ1208=sQuery(id+"F0.wireOp",EDGE,"E2983");var subQ1209=sQuery(id+"F0.wireOp",EDGE,"E2982");var subQ1210=sQuery(id+"F0.wireOp",EDGE,"E2981");var subQ1211=sQuery(id+"F0.wireOp",EDGE,"E2980");var subQ1212=sQuery(id+"F0.wireOp",EDGE,"E2979");var subQ1213=sQuery(id+"F0.wireOp",EDGE,"E2978");var subQ1214=sQuery(id+"F0.wireOp",EDGE,"E2977");var subQ1215=sQuery(id+"F0.wireOp",EDGE,"E2976");var subQ1216=sQuery(id+"F0.wireOp",EDGE,"E2975");var subQ1217=sQuery(id+"F0.wireOp",EDGE,"E2974");var subQ1218=sQuery(id+"F0.wireOp",EDGE,"E2973");var subQ1219=sQuery(id+"F0.wireOp",EDGE,"E2972");var subQ1220=sQuery(id+"F0.wireOp",EDGE,"E2971");var subQ1221=sQuery(id+"F0.wireOp",EDGE,"E2970");var subQ1222=sQuery(id+"F0.wireOp",EDGE,"E2969");var subQ1223=sQuery(id+"F0.wireOp",EDGE,"E2968");var subQ1224=sQuery(id+"F0.wireOp",EDGE,"E2967");var subQ1225=sQuery(id+"F0.wireOp",EDGE,"E2966");var subQ1226=sQuery(id+"F0.wireOp",EDGE,"E2965");var subQ1227=sQuery(id+"F0.wireOp",EDGE,"E2964");var subQ1228=sQuery(id+"F0.wireOp",EDGE,"E2963");var subQ1229=sQuery(id+"F0.wireOp",EDGE,"E2962");var subQ1230=sQuery(id+"F0.wireOp",EDGE,"E2961");var subQ1231=sQuery(id+"F0.wireOp",EDGE,"E2960");var subQ1232=sQuery(id+"F0.wireOp",EDGE,"E2959");var subQ1233=sQuery(id+"F0.wireOp",EDGE,"E2958");var subQ1234=sQuery(id+"F0.wireOp",EDGE,"E2957");var subQ1235=sQuery(id+"F0.wireOp",EDGE,"E2956");var subQ1236=sQuery(id+"F0.wireOp",EDGE,"E2955");var subQ1237=sQuery(id+"F0.wireOp",EDGE,"E2954");var subQ1238=sQuery(id+"F0.wireOp",EDGE,"E2953");var subQ1239=sQuery(id+"F0.wireOp",EDGE,"E2952");var subQ1240=sQuery(id+"F0.wireOp",EDGE,"E2951");var subQ1241=sQuery(id+"F0.wireOp",EDGE,"E2950");var subQ1242=sQuery(id+"F0.wireOp",EDGE,"E2949");var subQ1243=sQuery(id+"F0.wireOp",EDGE,"E2948");var subQ1244=sQuery(id+"F0.wireOp",EDGE,"E2947");var subQ1245=sQuery(id+"F0.wireOp",EDGE,"E2946");var subQ1246=sQuery(id+"F0.wireOp",EDGE,"E2945");var subQ1247=sQuery(id+"F0.wireOp",EDGE,"E2944");var subQ1248=sQuery(id+"F0.wireOp",EDGE,"E2943");var subQ1249=sQuery(id+"F0.wireOp",EDGE,"E2942");var subQ1250=sQuery(id+"F0.wireOp",EDGE,"E2941");var subQ1251=sQuery(id+"F0.wireOp",EDGE,"E2940");var subQ1252=sQuery(id+"F0.wireOp",EDGE,"E2939");var subQ1253=sQuery(id+"F0.wireOp",EDGE,"E2938");var subQ1254=sQuery(id+"F0.wireOp",EDGE,"E2937");var subQ1255=sQuery(id+"F0.wireOp",EDGE,"E2936");var subQ1256=sQuery(id+"F0.wireOp",EDGE,"E2935");var subQ1257=sQuery(id+"F0.wireOp",EDGE,"E2934");var subQ1258=sQuery(id+"F0.wireOp",EDGE,"E2933");var subQ1259=sQuery(id+"F0.wireOp",EDGE,"E2932");var subQ1260=sQuery(id+"F0.wireOp",EDGE,"E2931");var subQ1261=sQuery(id+"F0.wireOp",EDGE,"E2930");var subQ1262=sQuery(id+"F0.wireOp",EDGE,"E2929");var subQ1263=sQuery(id+"F0.wireOp",EDGE,"E2928");var subQ1264=sQuery(id+"F0.wireOp",EDGE,"E2927");var subQ1265=sQuery(id+"F0.wireOp",EDGE,"E2926");var subQ1266=sQuery(id+"F0.wireOp",EDGE,"E2925");var subQ1267=sQuery(id+"F0.wireOp",EDGE,"E2924");var subQ1268=sQuery(id+"F0.wireOp",EDGE,"E2923");var subQ1269=sQuery(id+"F0.wireOp",EDGE,"E2922");var subQ1270=sQuery(id+"F0.wireOp",EDGE,"E2921");var subQ1271=sQuery(id+"F0.wireOp",EDGE,"E2920");var subQ1272=sQuery(id+"F0.wireOp",EDGE,"E2919");var subQ1273=sQuery(id+"F0.wireOp",EDGE,"E2918");var subQ1274=sQuery(id+"F0.wireOp",EDGE,"E2917");var subQ1275=sQuery(id+"F0.wireOp",EDGE,"E2916");var subQ1276=sQuery(id+"F0.wireOp",EDGE,"E2915");var subQ1277=sQuery(id+"F0.wireOp",EDGE,"E2914");var subQ1278=sQuery(id+"F0.wireOp",EDGE,"E2913");var subQ1279=sQuery(id+"F0.wireOp",EDGE,"E2912");var subQ1280=sQuery(id+"F0.wireOp",EDGE,"E2911");var subQ1281=sQuery(id+"F0.wireOp",EDGE,"E2910");var subQ1282=sQuery(id+"F0.wireOp",EDGE,"E2909");var subQ1283=sQuery(id+"F0.wireOp",EDGE,"E2908");var subQ1284=sQuery(id+"F0.wireOp",EDGE,"E2907");var subQ1285=sQuery(id+"F0.wireOp",EDGE,"E2906");var subQ1286=sQuery(id+"F0.wireOp",EDGE,"E2905");var subQ1287=sQuery(id+"F0.wireOp",EDGE,"E2904");var subQ1288=sQuery(id+"F0.wireOp",EDGE,"E2903");var subQ1289=sQuery(id+"F0.wireOp",EDGE,"E2902");var subQ1290=sQuery(id+"F0.wireOp",EDGE,"E2901");var subQ1291=sQuery(id+"F0.wireOp",EDGE,"E2900");var subQ1292=sQuery(id+"F0.wireOp",EDGE,"E2899");var subQ1293=sQuery(id+"F0.wireOp",EDGE,"E2898");var subQ1294=sQuery(id+"F0.wireOp",EDGE,"E2897");var subQ1295=sQuery(id+"F0.wireOp",EDGE,"E2896");var subQ1296=sQuery(id+"F0.wireOp",EDGE,"E2895");var subQ1297=sQuery(id+"F0.wireOp",EDGE,"E2894");var subQ1298=sQuery(id+"F0.wireOp",EDGE,"E2893");var subQ1299=sQuery(id+"F0.wireOp",EDGE,"E2892");var subQ1300=sQuery(id+"F0.wireOp",EDGE,"E2891");var subQ1301=sQuery(id+"F0.wireOp",EDGE,"E2890");var subQ1302=sQuery(id+"F0.wireOp",EDGE,"E2889");var subQ1303=sQuery(id+"F0.wireOp",EDGE,"E2888");var subQ1304=sQuery(id+"F0.wireOp",EDGE,"E2887");var subQ1305=sQuery(id+"F0.wireOp",EDGE,"E2886");var subQ1306=sQuery(id+"F0.wireOp",EDGE,"E2885");var subQ1307=sQuery(id+"F0.wireOp",EDGE,"E2884");var subQ1308=sQuery(id+"F0.wireOp",EDGE,"E2883");var subQ1309=sQuery(id+"F0.wireOp",EDGE,"E2882");var subQ1310=sQuery(id+"F0.wireOp",EDGE,"E2881");var subQ1311=sQuery(id+"F0.wireOp",EDGE,"E2880");var subQ1312=sQuery(id+"F0.wireOp",EDGE,"E2879");var subQ1313=sQuery(id+"F0.wireOp",EDGE,"E2878");var subQ1314=sQuery(id+"F0.wireOp",EDGE,"E2877");var subQ1315=sQuery(id+"F0.wireOp",EDGE,"E2876");var subQ1316=sQuery(id+"F0.wireOp",EDGE,"E2875");var subQ1317=sQuery(id+"F0.wireOp",EDGE,"E2874");var subQ1318=sQuery(id+"F0.wireOp",EDGE,"E2873");var subQ1319=sQuery(id+"F0.wireOp",EDGE,"E2872");var subQ1320=sQuery(id+"F0.wireOp",EDGE,"E2871");var subQ1321=sQuery(id+"F0.wireOp",EDGE,"E2870");var subQ1322=sQuery(id+"F0.wireOp",EDGE,"E2869");var subQ1323=sQuery(id+"F0.wireOp",EDGE,"E2868");var subQ1324=sQuery(id+"F0.wireOp",EDGE,"E2867");var subQ1325=sQuery(id+"F0.wireOp",EDGE,"E2866");var subQ1326=sQuery(id+"F0.wireOp",EDGE,"E2865");var subQ1327=sQuery(id+"F0.wireOp",EDGE,"E2864");var subQ1328=sQuery(id+"F0.wireOp",EDGE,"E2863");var subQ1329=sQuery(id+"F0.wireOp",EDGE,"E2862");var subQ1330=sQuery(id+"F0.wireOp",EDGE,"E2861");var subQ1331=sQuery(id+"F0.wireOp",EDGE,"E2860");var subQ1332=sQuery(id+"F0.wireOp",EDGE,"E2859");var subQ1333=sQuery(id+"F0.wireOp",EDGE,"E2858");var subQ1334=sQuery(id+"F0.wireOp",EDGE,"E2857");var subQ1335=sQuery(id+"F0.wireOp",EDGE,"E2856");var subQ1336=sQuery(id+"F0.wireOp",EDGE,"E2855");var subQ1337=sQuery(id+"F0.wireOp",EDGE,"E2854");var subQ1338=sQuery(id+"F0.wireOp",EDGE,"E2853");var subQ1339=sQuery(id+"F0.wireOp",EDGE,"E2852");var subQ1340=sQuery(id+"F0.wireOp",EDGE,"E2851");var subQ1341=sQuery(id+"F0.wireOp",EDGE,"E2850");var subQ1342=sQuery(id+"F0.wireOp",EDGE,"E2849");var subQ1343=sQuery(id+"F0.wireOp",EDGE,"E2848");var subQ1344=sQuery(id+"F0.wireOp",EDGE,"E2847");var subQ1345=sQuery(id+"F0.wireOp",EDGE,"E2846");var subQ1346=sQuery(id+"F0.wireOp",EDGE,"E2845");var subQ1347=sQuery(id+"F0.wireOp",EDGE,"E2844");var subQ1348=sQuery(id+"F0.wireOp",EDGE,"E2843");var subQ1349=sQuery(id+"F0.wireOp",EDGE,"E2842");var subQ1350=sQuery(id+"F0.wireOp",EDGE,"E2841");var subQ1351=sQuery(id+"F0.wireOp",EDGE,"E2840");var subQ1352=sQuery(id+"F0.wireOp",EDGE,"E2839");var subQ1353=sQuery(id+"F0.wireOp",EDGE,"E2838");var subQ1354=sQuery(id+"F0.wireOp",EDGE,"E2837");var subQ1355=sQuery(id+"F0.wireOp",EDGE,"E2836");var subQ1356=sQuery(id+"F0.wireOp",EDGE,"E2835");var subQ1357=sQuery(id+"F0.wireOp",EDGE,"E2834");var subQ1358=sQuery(id+"F0.wireOp",EDGE,"E2833");var subQ1359=sQuery(id+"F0.wireOp",EDGE,"E2832");var subQ1360=sQuery(id+"F0.wireOp",EDGE,"E2831");var subQ1361=sQuery(id+"F0.wireOp",EDGE,"E2830");var subQ1362=sQuery(id+"F0.wireOp",EDGE,"E2829");var subQ1363=sQuery(id+"F0.wireOp",EDGE,"E2828");var subQ1364=sQuery(id+"F0.wireOp",EDGE,"E2827");var subQ1365=sQuery(id+"F0.wireOp",EDGE,"E2826");var subQ1366=sQuery(id+"F0.wireOp",EDGE,"E2825");var subQ1367=sQuery(id+"F0.wireOp",EDGE,"E2824");var subQ1368=sQuery(id+"F0.wireOp",EDGE,"E2823");var subQ1369=sQuery(id+"F0.wireOp",EDGE,"E2822");var subQ1370=sQuery(id+"F0.wireOp",EDGE,"E2821");var subQ1371=sQuery(id+"F0.wireOp",EDGE,"E2820");var subQ1372=sQuery(id+"F0.wireOp",EDGE,"E2819");var subQ1373=sQuery(id+"F0.wireOp",EDGE,"E2818");var subQ1374=sQuery(id+"F0.wireOp",EDGE,"E2817");var subQ1375=sQuery(id+"F0.wireOp",EDGE,"E2816");var subQ1376=sQuery(id+"F0.wireOp",EDGE,"E2815");var subQ1377=sQuery(id+"F0.wireOp",EDGE,"E2814");var subQ1378=sQuery(id+"F0.wireOp",EDGE,"E2813");var subQ1379=sQuery(id+"F0.wireOp",EDGE,"E2812");var subQ1380=sQuery(id+"F0.wireOp",EDGE,"E2811");var subQ1381=sQuery(id+"F0.wireOp",EDGE,"E2810");var subQ1382=sQuery(id+"F0.wireOp",EDGE,"E2809");var subQ1383=sQuery(id+"F0.wireOp",EDGE,"E2808");var subQ1384=sQuery(id+"F0.wireOp",EDGE,"E2807");var subQ1385=sQuery(id+"F0.wireOp",EDGE,"E2806");var subQ1386=sQuery(id+"F0.wireOp",EDGE,"E2805");var subQ1387=sQuery(id+"F0.wireOp",EDGE,"E2804");var subQ1388=sQuery(id+"F0.wireOp",EDGE,"E2803");var subQ1389=sQuery(id+"F0.wireOp",EDGE,"E2802");var subQ1390=sQuery(id+"F0.wireOp",EDGE,"E2801");var subQ1391=sQuery(id+"F0.wireOp",EDGE,"E2800");var subQ1392=sQuery(id+"F0.wireOp",EDGE,"E2799");var subQ1393=sQuery(id+"F0.wireOp",EDGE,"E2798");var subQ1394=sQuery(id+"F0.wireOp",EDGE,"E2797");var subQ1395=sQuery(id+"F0.wireOp",EDGE,"E2796");var subQ1396=sQuery(id+"F0.wireOp",EDGE,"E2795");var subQ1397=sQuery(id+"F0.wireOp",EDGE,"E2794");var subQ1398=sQuery(id+"F0.wireOp",EDGE,"E2793");var subQ1399=sQuery(id+"F0.wireOp",EDGE,"E2792");var subQ1400=sQuery(id+"F0.wireOp",EDGE,"E2791");var subQ1401=sQuery(id+"F0.wireOp",EDGE,"E2790");var subQ1402=sQuery(id+"F0.wireOp",EDGE,"E2789");var subQ1403=sQuery(id+"F0.wireOp",EDGE,"E2788");var subQ1404=sQuery(id+"F0.wireOp",EDGE,"E2787");var subQ1405=sQuery(id+"F0.wireOp",EDGE,"E2786");var subQ1406=sQuery(id+"F0.wireOp",EDGE,"E2785");var subQ1407=sQuery(id+"F0.wireOp",EDGE,"E2784");var subQ1408=sQuery(id+"F0.wireOp",EDGE,"E2783");var subQ1409=sQuery(id+"F0.wireOp",EDGE,"E2782");var subQ1410=sQuery(id+"F0.wireOp",EDGE,"E2781");var subQ1411=sQuery(id+"F0.wireOp",EDGE,"E2780");var subQ1412=sQuery(id+"F0.wireOp",EDGE,"E2779");var subQ1413=sQuery(id+"F0.wireOp",EDGE,"E2778");var subQ1414=sQuery(id+"F0.wireOp",EDGE,"E2777");var subQ1415=sQuery(id+"F0.wireOp",EDGE,"E2776");var subQ1416=sQuery(id+"F0.wireOp",EDGE,"E2775");var subQ1417=sQuery(id+"F0.wireOp",EDGE,"E2774");var subQ1418=sQuery(id+"F0.wireOp",EDGE,"E2773");var subQ1419=sQuery(id+"F0.wireOp",EDGE,"E2772");var subQ1420=sQuery(id+"F0.wireOp",EDGE,"E2771");var subQ1421=sQuery(id+"F0.wireOp",EDGE,"E2770");var subQ1422=sQuery(id+"F0.wireOp",EDGE,"E2769");var subQ1423=sQuery(id+"F0.wireOp",EDGE,"E2768");var subQ1424=sQuery(id+"F0.wireOp",EDGE,"E2767");var subQ1425=sQuery(id+"F0.wireOp",EDGE,"E2766");var subQ1426=sQuery(id+"F0.wireOp",EDGE,"E2765");var subQ1427=sQuery(id+"F0.wireOp",EDGE,"E2764");var subQ1428=sQuery(id+"F0.wireOp",EDGE,"E2763");var subQ1429=sQuery(id+"F0.wireOp",EDGE,"E2762");var subQ1430=sQuery(id+"F0.wireOp",EDGE,"E2761");var subQ1431=sQuery(id+"F0.wireOp",EDGE,"E2760");var subQ1432=sQuery(id+"F0.wireOp",EDGE,"E2759");var subQ1433=sQuery(id+"F0.wireOp",EDGE,"E2758");var subQ1434=sQuery(id+"F0.wireOp",EDGE,"E2757");var subQ1435=sQuery(id+"F0.wireOp",EDGE,"E2756");var subQ1436=sQuery(id+"F0.wireOp",EDGE,"E2755");var subQ1437=sQuery(id+"F0.wireOp",EDGE,"E2754");var subQ1438=sQuery(id+"F0.wireOp",EDGE,"E2753");var subQ1439=sQuery(id+"F0.wireOp",EDGE,"E2752");var subQ1440=sQuery(id+"F0.wireOp",EDGE,"E2751");var subQ1441=sQuery(id+"F0.wireOp",EDGE,"E2750");var subQ1442=sQuery(id+"F0.wireOp",EDGE,"E2749");var subQ1443=sQuery(id+"F0.wireOp",EDGE,"E2748");var subQ1444=sQuery(id+"F0.wireOp",EDGE,"E2747");var subQ1445=sQuery(id+"F0.wireOp",EDGE,"E2746");var subQ1446=sQuery(id+"F0.wireOp",EDGE,"E2745");var subQ1447=sQuery(id+"F0.wireOp",EDGE,"E2744");var subQ1448=sQuery(id+"F0.wireOp",EDGE,"E2743");var subQ1449=sQuery(id+"F0.wireOp",EDGE,"E2742");var subQ1450=sQuery(id+"F0.wireOp",EDGE,"E2741");var subQ1451=sQuery(id+"F0.wireOp",EDGE,"E2740");var subQ1452=sQuery(id+"F0.wireOp",EDGE,"E2739");var subQ1453=sQuery(id+"F0.wireOp",EDGE,"E2738");var subQ1454=sQuery(id+"F0.wireOp",EDGE,"E2737");var subQ1455=sQuery(id+"F0.wireOp",EDGE,"E2736");var subQ1456=sQuery(id+"F0.wireOp",EDGE,"E2735");var subQ1457=sQuery(id+"F0.wireOp",EDGE,"E2734");var subQ1458=sQuery(id+"F0.wireOp",EDGE,"E2733");var subQ1459=sQuery(id+"F0.wireOp",EDGE,"E2732");var subQ1460=sQuery(id+"F0.wireOp",EDGE,"E2731");var subQ1461=sQuery(id+"F0.wireOp",EDGE,"E2730");var subQ1462=sQuery(id+"F0.wireOp",EDGE,"E2729");var subQ1463=sQuery(id+"F0.wireOp",EDGE,"E2728");var subQ1464=sQuery(id+"F0.wireOp",EDGE,"E2727");var subQ1465=sQuery(id+"F0.wireOp",EDGE,"E2726");var subQ1466=sQuery(id+"F0.wireOp",EDGE,"E2725");var subQ1467=sQuery(id+"F0.wireOp",EDGE,"E2724");var subQ1468=sQuery(id+"F0.wireOp",EDGE,"E2723");var subQ1469=sQuery(id+"F0.wireOp",EDGE,"E2722");var subQ1470=sQuery(id+"F0.wireOp",EDGE,"E2721");var subQ1471=sQuery(id+"F0.wireOp",EDGE,"E2720");var subQ1472=sQuery(id+"F0.wireOp",EDGE,"E2719");var subQ1473=sQuery(id+"F0.wireOp",EDGE,"E2718");var subQ1474=sQuery(id+"F0.wireOp",EDGE,"E2717");var subQ1475=sQuery(id+"F0.wireOp",EDGE,"E2716");var subQ1476=sQuery(id+"F0.wireOp",EDGE,"E2715");var subQ1477=sQuery(id+"F0.wireOp",EDGE,"E2714");var subQ1478=sQuery(id+"F0.wireOp",EDGE,"E2713");var subQ1479=sQuery(id+"F0.wireOp",EDGE,"E2712");var subQ1480=sQuery(id+"F0.wireOp",EDGE,"E2711");var subQ1481=sQuery(id+"F0.wireOp",EDGE,"E2710");var subQ1482=sQuery(id+"F0.wireOp",EDGE,"E2709");var subQ1483=sQuery(id+"F0.wireOp",EDGE,"E2708");var subQ1484=sQuery(id+"F0.wireOp",EDGE,"E2707");var subQ1485=sQuery(id+"F0.wireOp",EDGE,"E2706");var subQ1486=sQuery(id+"F0.wireOp",EDGE,"E2705");var subQ1487=sQuery(id+"F0.wireOp",EDGE,"E2704");var subQ1488=sQuery(id+"F0.wireOp",EDGE,"E2703");var subQ1489=sQuery(id+"F0.wireOp",EDGE,"E2702");var subQ1490=sQuery(id+"F0.wireOp",EDGE,"E2701");var subQ1491=sQuery(id+"F0.wireOp",EDGE,"E2700");var subQ1492=sQuery(id+"F0.wireOp",EDGE,"E2699");var subQ1493=sQuery(id+"F0.wireOp",EDGE,"E2698");var subQ1494=sQuery(id+"F0.wireOp",EDGE,"E2697");var subQ1495=sQuery(id+"F0.wireOp",EDGE,"E2696");var subQ1496=sQuery(id+"F0.wireOp",EDGE,"E2695");var subQ1497=sQuery(id+"F0.wireOp",EDGE,"E2694");var subQ1498=sQuery(id+"F0.wireOp",EDGE,"E2693");var subQ1499=sQuery(id+"F0.wireOp",EDGE,"E2692");var subQ1500=sQuery(id+"F0.wireOp",EDGE,"E2691");var subQ1501=sQuery(id+"F0.wireOp",EDGE,"E2690");var subQ1502=sQuery(id+"F0.wireOp",EDGE,"E2689");var subQ1503=sQuery(id+"F0.wireOp",EDGE,"E2688");var subQ1504=sQuery(id+"F0.wireOp",EDGE,"E2687");var subQ1505=sQuery(id+"F0.wireOp",EDGE,"E2686");var subQ1506=sQuery(id+"F0.wireOp",EDGE,"E2685");var subQ1507=sQuery(id+"F0.wireOp",EDGE,"E2684");var subQ1508=sQuery(id+"F0.wireOp",EDGE,"E2683");var subQ1509=sQuery(id+"F0.wireOp",EDGE,"E2682");var subQ1510=sQuery(id+"F0.wireOp",EDGE,"E2681");var subQ1511=sQuery(id+"F0.wireOp",EDGE,"E2680");var subQ1512=sQuery(id+"F0.wireOp",EDGE,"E2679");var subQ1513=sQuery(id+"F0.wireOp",EDGE,"E2678");var subQ1514=sQuery(id+"F0.wireOp",EDGE,"E2677");var subQ1515=sQuery(id+"F0.wireOp",EDGE,"E2676");var subQ1516=sQuery(id+"F0.wireOp",EDGE,"E2675");var subQ1517=sQuery(id+"F0.wireOp",EDGE,"E2674");var subQ1518=sQuery(id+"F0.wireOp",EDGE,"E2673");var subQ1519=sQuery(id+"F0.wireOp",EDGE,"E2672");var subQ1520=sQuery(id+"F0.wireOp",EDGE,"E2671");var subQ1521=sQuery(id+"F0.wireOp",EDGE,"E2670");var subQ1522=sQuery(id+"F0.wireOp",EDGE,"E2669");var subQ1523=sQuery(id+"F0.wireOp",EDGE,"E2668");var subQ1524=sQuery(id+"F0.wireOp",EDGE,"E2667");var subQ1525=sQuery(id+"F0.wireOp",EDGE,"E2666");var subQ1526=sQuery(id+"F0.wireOp",EDGE,"E2665");var subQ1527=sQuery(id+"F0.wireOp",EDGE,"E2664");var subQ1528=sQuery(id+"F0.wireOp",EDGE,"E2663");var subQ1529=sQuery(id+"F0.wireOp",EDGE,"E2662");var subQ1530=sQuery(id+"F0.wireOp",EDGE,"E2661");var subQ1531=sQuery(id+"F0.wireOp",EDGE,"E2660");var subQ1532=sQuery(id+"F0.wireOp",EDGE,"E2659");var subQ1533=sQuery(id+"F0.wireOp",EDGE,"E2658");var subQ1534=sQuery(id+"F0.wireOp",EDGE,"E2657");var subQ1535=sQuery(id+"F0.wireOp",EDGE,"E2656");var subQ1536=sQuery(id+"F0.wireOp",EDGE,"E2655");var subQ1537=sQuery(id+"F0.wireOp",EDGE,"E2654");var subQ1538=sQuery(id+"F0.wireOp",EDGE,"E2653");var subQ1539=sQuery(id+"F0.wireOp",EDGE,"E2652");var subQ1540=sQuery(id+"F0.wireOp",EDGE,"E2651");var subQ1541=sQuery(id+"F0.wireOp",EDGE,"E2650");var subQ1542=sQuery(id+"F0.wireOp",EDGE,"E2649");var subQ1543=sQuery(id+"F0.wireOp",EDGE,"E2648");var subQ1544=sQuery(id+"F0.wireOp",EDGE,"E2647");var subQ1545=sQuery(id+"F0.wireOp",EDGE,"E2646");var subQ1546=sQuery(id+"F0.wireOp",EDGE,"E2645");var subQ1547=sQuery(id+"F0.wireOp",EDGE,"E2644");var subQ1548=sQuery(id+"F0.wireOp",EDGE,"E2643");var subQ1549=sQuery(id+"F0.wireOp",EDGE,"E2642");var subQ1550=sQuery(id+"F0.wireOp",EDGE,"E2641");var subQ1551=sQuery(id+"F0.wireOp",EDGE,"E2640");var subQ1552=sQuery(id+"F0.wireOp",EDGE,"E2639");var subQ1553=sQuery(id+"F0.wireOp",EDGE,"E2638");var subQ1554=sQuery(id+"F0.wireOp",EDGE,"E2637");var subQ1555=sQuery(id+"F0.wireOp",EDGE,"E2636");var subQ1556=sQuery(id+"F0.wireOp",EDGE,"E2635");var subQ1557=sQuery(id+"F0.wireOp",EDGE,"E2634");var subQ1558=sQuery(id+"F0.wireOp",EDGE,"E2633");var subQ1559=sQuery(id+"F0.wireOp",EDGE,"E2632");var subQ1560=sQuery(id+"F0.wireOp",EDGE,"E2631");var subQ1561=sQuery(id+"F0.wireOp",EDGE,"E2630");var subQ1562=sQuery(id+"F0.wireOp",EDGE,"E2629");var subQ1563=sQuery(id+"F0.wireOp",EDGE,"E2628");var subQ1564=sQuery(id+"F0.wireOp",EDGE,"E2627");var subQ1565=sQuery(id+"F0.wireOp",EDGE,"E2626");var subQ1566=sQuery(id+"F0.wireOp",EDGE,"E2625");var subQ1567=sQuery(id+"F0.wireOp",EDGE,"E2624");var subQ1568=sQuery(id+"F0.wireOp",EDGE,"E2623");var subQ1569=sQuery(id+"F0.wireOp",EDGE,"E2622");var subQ1570=sQuery(id+"F0.wireOp",EDGE,"E2621");var subQ1571=sQuery(id+"F0.wireOp",EDGE,"E2620");var subQ1572=sQuery(id+"F0.wireOp",EDGE,"E2619");var subQ1573=sQuery(id+"F0.wireOp",EDGE,"E2618");var subQ1574=sQuery(id+"F0.wireOp",EDGE,"E2617");var subQ1575=sQuery(id+"F0.wireOp",EDGE,"E2616");var subQ1576=sQuery(id+"F0.wireOp",EDGE,"E2615");var subQ1577=sQuery(id+"F0.wireOp",EDGE,"E2614");var subQ1578=sQuery(id+"F0.wireOp",EDGE,"E2613");var subQ1579=sQuery(id+"F0.wireOp",EDGE,"E2612");var subQ1580=sQuery(id+"F0.wireOp",EDGE,"E2611");var subQ1581=sQuery(id+"F0.wireOp",EDGE,"E2610");var subQ1582=sQuery(id+"F0.wireOp",EDGE,"E2609");var subQ1583=sQuery(id+"F0.wireOp",EDGE,"E2608");var subQ1584=sQuery(id+"F0.wireOp",EDGE,"E2607");var subQ1585=sQuery(id+"F0.wireOp",EDGE,"E2606");var subQ1586=sQuery(id+"F0.wireOp",EDGE,"E2605");var subQ1587=sQuery(id+"F0.wireOp",EDGE,"E2604");var subQ1588=sQuery(id+"F0.wireOp",EDGE,"E2603");var subQ1589=sQuery(id+"F0.wireOp",EDGE,"E2602");var subQ1590=sQuery(id+"F0.wireOp",EDGE,"E2601");var subQ1591=sQuery(id+"F0.wireOp",EDGE,"E2600");var subQ1592=sQuery(id+"F0.wireOp",EDGE,"E2599");var subQ1593=sQuery(id+"F0.wireOp",EDGE,"E2598");var subQ1594=sQuery(id+"F0.wireOp",EDGE,"E2597");var subQ1595=sQuery(id+"F0.wireOp",EDGE,"E2596");var subQ1596=sQuery(id+"F0.wireOp",EDGE,"E2595");var subQ1597=sQuery(id+"F0.wireOp",EDGE,"E2594");var subQ1598=sQuery(id+"F0.wireOp",EDGE,"E2593");var subQ1599=sQuery(id+"F0.wireOp",EDGE,"E2592");var subQ1600=sQuery(id+"F0.wireOp",EDGE,"E2591");var subQ1601=sQuery(id+"F0.wireOp",EDGE,"E2590");var subQ1602=sQuery(id+"F0.wireOp",EDGE,"E2589");var subQ1603=sQuery(id+"F0.wireOp",EDGE,"E2588");var subQ1604=sQuery(id+"F0.wireOp",EDGE,"E2587");var subQ1605=sQuery(id+"F0.wireOp",EDGE,"E2586");var subQ1606=sQuery(id+"F0.wireOp",EDGE,"E2585");var subQ1607=sQuery(id+"F0.wireOp",EDGE,"E2584");var subQ1608=sQuery(id+"F0.wireOp",EDGE,"E2583");var subQ1609=sQuery(id+"F0.wireOp",EDGE,"E2582");var subQ1610=sQuery(id+"F0.wireOp",EDGE,"E2581");var subQ1611=sQuery(id+"F0.wireOp",EDGE,"E2580");var subQ1612=sQuery(id+"F0.wireOp",EDGE,"E2579");var subQ1613=sQuery(id+"F0.wireOp",EDGE,"E2578");var subQ1614=sQuery(id+"F0.wireOp",EDGE,"E2577");var subQ1615=sQuery(id+"F0.wireOp",EDGE,"E2576");var subQ1616=sQuery(id+"F0.wireOp",EDGE,"E2575");var subQ1617=sQuery(id+"F0.wireOp",EDGE,"E2574");var subQ1618=sQuery(id+"F0.wireOp",EDGE,"E2573");var subQ1619=sQuery(id+"F0.wireOp",EDGE,"E2572");var subQ1620=sQuery(id+"F0.wireOp",EDGE,"E2571");var subQ1621=sQuery(id+"F0.wireOp",EDGE,"E2570");var subQ1622=sQuery(id+"F0.wireOp",EDGE,"E2569");var subQ1623=sQuery(id+"F0.wireOp",EDGE,"E2568");var subQ1624=sQuery(id+"F0.wireOp",EDGE,"E2567");var subQ1625=sQuery(id+"F0.wireOp",EDGE,"E2566");var subQ1626=sQuery(id+"F0.wireOp",EDGE,"E2565");var subQ1627=sQuery(id+"F0.wireOp",EDGE,"E2564");var subQ1628=sQuery(id+"F0.wireOp",EDGE,"E2563");var subQ1629=sQuery(id+"F0.wireOp",EDGE,"E2562");var subQ1630=sQuery(id+"F0.wireOp",EDGE,"E2561");var subQ1631=sQuery(id+"F0.wireOp",EDGE,"E2560");var subQ1632=sQuery(id+"F0.wireOp",EDGE,"E2559");var subQ1633=sQuery(id+"F0.wireOp",EDGE,"E2558");var subQ1634=sQuery(id+"F0.wireOp",EDGE,"E2557");var subQ1635=sQuery(id+"F0.wireOp",EDGE,"E2556");var subQ1636=sQuery(id+"F0.wireOp",EDGE,"E2555");var subQ1637=sQuery(id+"F0.wireOp",EDGE,"E2554");var subQ1638=sQuery(id+"F0.wireOp",EDGE,"E2553");var subQ1639=sQuery(id+"F0.wireOp",EDGE,"E2552");var subQ1640=sQuery(id+"F0.wireOp",EDGE,"E2551");var subQ1641=sQuery(id+"F0.wireOp",EDGE,"E2550");var subQ1642=sQuery(id+"F0.wireOp",EDGE,"E2549");var subQ1643=sQuery(id+"F0.wireOp",EDGE,"E2548");var subQ1644=sQuery(id+"F0.wireOp",EDGE,"E2547");var subQ1645=sQuery(id+"F0.wireOp",EDGE,"E2546");var subQ1646=sQuery(id+"F0.wireOp",EDGE,"E2545");var subQ1647=sQuery(id+"F0.wireOp",EDGE,"E2544");var subQ1648=sQuery(id+"F0.wireOp",EDGE,"E2543");var subQ1649=sQuery(id+"F0.wireOp",EDGE,"E2542");var subQ1650=sQuery(id+"F0.wireOp",EDGE,"E2541");var subQ1651=sQuery(id+"F0.wireOp",EDGE,"E2540");var subQ1652=sQuery(id+"F0.wireOp",EDGE,"E2539");var subQ1653=sQuery(id+"F0.wireOp",EDGE,"E2538");var subQ1654=sQuery(id+"F0.wireOp",EDGE,"E2537");var subQ1655=sQuery(id+"F0.wireOp",EDGE,"E2536");var subQ1656=sQuery(id+"F0.wireOp",EDGE,"E2535");var subQ1657=sQuery(id+"F0.wireOp",EDGE,"E2534");var subQ1658=sQuery(id+"F0.wireOp",EDGE,"E2533");var subQ1659=sQuery(id+"F0.wireOp",EDGE,"E2532");var subQ1660=sQuery(id+"F0.wireOp",EDGE,"E2531");var subQ1661=sQuery(id+"F0.wireOp",EDGE,"E2530");var subQ1662=sQuery(id+"F0.wireOp",EDGE,"E2529");var subQ1663=sQuery(id+"F0.wireOp",EDGE,"E2528");var subQ1664=sQuery(id+"F0.wireOp",EDGE,"E2527");var subQ1665=sQuery(id+"F0.wireOp",EDGE,"E2526");var subQ1666=sQuery(id+"F0.wireOp",EDGE,"E2525");var subQ1667=sQuery(id+"F0.wireOp",EDGE,"E2524");var subQ1668=sQuery(id+"F0.wireOp",EDGE,"E2523");var subQ1669=sQuery(id+"F0.wireOp",EDGE,"E2522");var subQ1670=sQuery(id+"F0.wireOp",EDGE,"E2521");var subQ1671=sQuery(id+"F0.wireOp",EDGE,"E2520");var subQ1672=sQuery(id+"F0.wireOp",EDGE,"E2519");var subQ1673=sQuery(id+"F0.wireOp",EDGE,"E2518");var subQ1674=sQuery(id+"F0.wireOp",EDGE,"E2517");var subQ1675=sQuery(id+"F0.wireOp",EDGE,"E2516");var subQ1676=sQuery(id+"F0.wireOp",EDGE,"E2515");var subQ1677=sQuery(id+"F0.wireOp",EDGE,"E2514");var subQ1678=sQuery(id+"F0.wireOp",EDGE,"E2513");var subQ1679=sQuery(id+"F0.wireOp",EDGE,"E2512");var subQ1680=sQuery(id+"F0.wireOp",EDGE,"E2511");var subQ1681=sQuery(id+"F0.wireOp",EDGE,"E2510");var subQ1682=sQuery(id+"F0.wireOp",EDGE,"E2509");var subQ1683=sQuery(id+"F0.wireOp",EDGE,"E2508");var subQ1684=sQuery(id+"F0.wireOp",EDGE,"E2507");var subQ1685=sQuery(id+"F0.wireOp",EDGE,"E2506");var subQ1686=sQuery(id+"F0.wireOp",EDGE,"E2505");var subQ1687=sQuery(id+"F0.wireOp",EDGE,"E2504");var subQ1688=sQuery(id+"F0.wireOp",EDGE,"E2503");var subQ1689=sQuery(id+"F0.wireOp",EDGE,"E2502");var subQ1690=sQuery(id+"F0.wireOp",EDGE,"E2501");var subQ1691=sQuery(id+"F0.wireOp",EDGE,"E2500");var subQ1692=sQuery(id+"F0.wireOp",EDGE,"E2499");var subQ1693=sQuery(id+"F0.wireOp",EDGE,"E2498");var subQ1694=sQuery(id+"F0.wireOp",EDGE,"E2497");var subQ1695=sQuery(id+"F0.wireOp",EDGE,"E2496");var subQ1696=sQuery(id+"F0.wireOp",EDGE,"E2495");var subQ1697=sQuery(id+"F0.wireOp",EDGE,"E2494");var subQ1698=sQuery(id+"F0.wireOp",EDGE,"E2493");var subQ1699=sQuery(id+"F0.wireOp",EDGE,"E2492");var subQ1700=sQuery(id+"F0.wireOp",EDGE,"E2491");var subQ1701=sQuery(id+"F0.wireOp",EDGE,"E2490");var subQ1702=sQuery(id+"F0.wireOp",EDGE,"E2489");var subQ1703=sQuery(id+"F0.wireOp",EDGE,"E2488");var subQ1704=sQuery(id+"F0.wireOp",EDGE,"E2487");var subQ1705=sQuery(id+"F0.wireOp",EDGE,"E2486");var subQ1706=sQuery(id+"F0.wireOp",EDGE,"E2485");var subQ1707=sQuery(id+"F0.wireOp",EDGE,"E2484");var subQ1708=sQuery(id+"F0.wireOp",EDGE,"E2483");var subQ1709=sQuery(id+"F0.wireOp",EDGE,"E2482");var subQ1710=sQuery(id+"F0.wireOp",EDGE,"E2481");var subQ1711=sQuery(id+"F0.wireOp",EDGE,"E2480");var subQ1712=sQuery(id+"F0.wireOp",EDGE,"E2479");var subQ1713=sQuery(id+"F0.wireOp",EDGE,"E2478");var subQ1714=sQuery(id+"F0.wireOp",EDGE,"E2477");var subQ1715=sQuery(id+"F0.wireOp",EDGE,"E2476");var subQ1716=sQuery(id+"F0.wireOp",EDGE,"E2475");var subQ1717=sQuery(id+"F0.wireOp",EDGE,"E2474");var subQ1718=sQuery(id+"F0.wireOp",EDGE,"E2473");var subQ1719=sQuery(id+"F0.wireOp",EDGE,"E2472");var subQ1720=sQuery(id+"F0.wireOp",EDGE,"E2471");var subQ1721=sQuery(id+"F0.wireOp",EDGE,"E2470");var subQ1722=sQuery(id+"F0.wireOp",EDGE,"E2469");var subQ1723=sQuery(id+"F0.wireOp",EDGE,"E2468");var subQ1724=sQuery(id+"F0.wireOp",EDGE,"E2467");var subQ1725=sQuery(id+"F0.wireOp",EDGE,"E2466");var subQ1726=sQuery(id+"F0.wireOp",EDGE,"E2465");var subQ1727=sQuery(id+"F0.wireOp",EDGE,"E2464");var subQ1728=sQuery(id+"F0.wireOp",EDGE,"E2463");var subQ1729=sQuery(id+"F0.wireOp",EDGE,"E2462");var subQ1730=sQuery(id+"F0.wireOp",EDGE,"E2461");var subQ1731=sQuery(id+"F0.wireOp",EDGE,"E2460");var subQ1732=sQuery(id+"F0.wireOp",EDGE,"E2459");var subQ1733=sQuery(id+"F0.wireOp",EDGE,"E2458");var subQ1734=sQuery(id+"F0.wireOp",EDGE,"E2457");var subQ1735=sQuery(id+"F0.wireOp",EDGE,"E2456");var subQ1736=sQuery(id+"F0.wireOp",EDGE,"E2455");var subQ1737=sQuery(id+"F0.wireOp",EDGE,"E2454");var subQ1738=sQuery(id+"F0.wireOp",EDGE,"E2453");var subQ1739=sQuery(id+"F0.wireOp",EDGE,"E2452");var subQ1740=sQuery(id+"F0.wireOp",EDGE,"E2451");var subQ1741=sQuery(id+"F0.wireOp",EDGE,"E2450");var subQ1742=sQuery(id+"F0.wireOp",EDGE,"E2449");var subQ1743=sQuery(id+"F0.wireOp",EDGE,"E2448");var subQ1744=sQuery(id+"F0.wireOp",EDGE,"E2447");var subQ1745=sQuery(id+"F0.wireOp",EDGE,"E2446");var subQ1746=sQuery(id+"F0.wireOp",EDGE,"E2445");var subQ1747=sQuery(id+"F0.wireOp",EDGE,"E2444");var subQ1748=sQuery(id+"F0.wireOp",EDGE,"E2443");var subQ1749=sQuery(id+"F0.wireOp",EDGE,"E2442");var subQ1750=sQuery(id+"F0.wireOp",EDGE,"E2441");var subQ1751=sQuery(id+"F0.wireOp",EDGE,"E2440");var subQ1752=sQuery(id+"F0.wireOp",EDGE,"E2439");var subQ1753=sQuery(id+"F0.wireOp",EDGE,"E2438");var subQ1754=sQuery(id+"F0.wireOp",EDGE,"E2437");var subQ1755=sQuery(id+"F0.wireOp",EDGE,"E2436");var subQ1756=sQuery(id+"F0.wireOp",EDGE,"E2435");var subQ1757=sQuery(id+"F0.wireOp",EDGE,"E2434");var subQ1758=sQuery(id+"F0.wireOp",EDGE,"E2433");var subQ1759=sQuery(id+"F0.wireOp",EDGE,"E2432");var subQ1760=sQuery(id+"F0.wireOp",EDGE,"E2431");var subQ1761=sQuery(id+"F0.wireOp",EDGE,"E2430");var subQ1762=sQuery(id+"F0.wireOp",EDGE,"E2429");var subQ1763=sQuery(id+"F0.wireOp",EDGE,"E2428");var subQ1764=sQuery(id+"F0.wireOp",EDGE,"E2427");var subQ1765=sQuery(id+"F0.wireOp",EDGE,"E2426");var subQ1766=sQuery(id+"F0.wireOp",EDGE,"E2425");var subQ1767=sQuery(id+"F0.wireOp",EDGE,"E2424");var subQ1768=sQuery(id+"F0.wireOp",EDGE,"E2423");var subQ1769=sQuery(id+"F0.wireOp",EDGE,"E2422");var subQ1770=sQuery(id+"F0.wireOp",EDGE,"E2421");var subQ1771=sQuery(id+"F0.wireOp",EDGE,"E2420");var subQ1772=sQuery(id+"F0.wireOp",EDGE,"E2419");var subQ1773=sQuery(id+"F0.wireOp",EDGE,"E2418");var subQ1774=sQuery(id+"F0.wireOp",EDGE,"E2417");var subQ1775=sQuery(id+"F0.wireOp",EDGE,"E2416");var subQ1776=sQuery(id+"F0.wireOp",EDGE,"E2415");var subQ1777=sQuery(id+"F0.wireOp",EDGE,"E2414");var subQ1778=sQuery(id+"F0.wireOp",EDGE,"E2413");var subQ1779=sQuery(id+"F0.wireOp",EDGE,"E2412");var subQ1780=sQuery(id+"F0.wireOp",EDGE,"E2411");var subQ1781=sQuery(id+"F0.wireOp",EDGE,"E2410");var subQ1782=sQuery(id+"F0.wireOp",EDGE,"E2409");var subQ1783=sQuery(id+"F0.wireOp",EDGE,"E2408");var subQ1784=sQuery(id+"F0.wireOp",EDGE,"E2407");var subQ1785=sQuery(id+"F0.wireOp",EDGE,"E2406");var subQ1786=sQuery(id+"F0.wireOp",EDGE,"E2405");var subQ1787=sQuery(id+"F0.wireOp",EDGE,"E2404");var subQ1788=sQuery(id+"F0.wireOp",EDGE,"E2403");var subQ1789=sQuery(id+"F0.wireOp",EDGE,"E2402");var subQ1790=sQuery(id+"F0.wireOp",EDGE,"E2401");var subQ1791=sQuery(id+"F0.wireOp",EDGE,"E2400");var subQ1792=sQuery(id+"F0.wireOp",EDGE,"E2399");var subQ1793=sQuery(id+"F0.wireOp",EDGE,"E2398");var subQ1794=sQuery(id+"F0.wireOp",EDGE,"E2397");var subQ1795=sQuery(id+"F0.wireOp",EDGE,"E2396");var subQ1796=sQuery(id+"F0.wireOp",EDGE,"E2395");var subQ1797=sQuery(id+"F0.wireOp",EDGE,"E2394");var subQ1798=sQuery(id+"F0.wireOp",EDGE,"E2393");var subQ1799=sQuery(id+"F0.wireOp",EDGE,"E2392");var subQ1800=sQuery(id+"F0.wireOp",EDGE,"E2391");var subQ1801=sQuery(id+"F0.wireOp",EDGE,"E2390");var subQ1802=sQuery(id+"F0.wireOp",EDGE,"E2389");var subQ1803=sQuery(id+"F0.wireOp",EDGE,"E2388");var subQ1804=sQuery(id+"F0.wireOp",EDGE,"E2387");var subQ1805=sQuery(id+"F0.wireOp",EDGE,"E2386");var subQ1806=sQuery(id+"F0.wireOp",EDGE,"E2385");var subQ1807=sQuery(id+"F0.wireOp",EDGE,"E2384");var subQ1808=sQuery(id+"F0.wireOp",EDGE,"E2383");var subQ1809=sQuery(id+"F0.wireOp",EDGE,"E2382");var subQ1810=sQuery(id+"F0.wireOp",EDGE,"E2381");var subQ1811=sQuery(id+"F0.wireOp",EDGE,"E2380");var subQ1812=sQuery(id+"F0.wireOp",EDGE,"E2379");var subQ1813=sQuery(id+"F0.wireOp",EDGE,"E2378");var subQ1814=sQuery(id+"F0.wireOp",EDGE,"E2377");var subQ1815=sQuery(id+"F0.wireOp",EDGE,"E2376");var subQ1816=sQuery(id+"F0.wireOp",EDGE,"E2375");var subQ1817=sQuery(id+"F0.wireOp",EDGE,"E2374");var subQ1818=sQuery(id+"F0.wireOp",EDGE,"E2373");var subQ1819=sQuery(id+"F0.wireOp",EDGE,"E2372");var subQ1820=sQuery(id+"F0.wireOp",EDGE,"E2371");var subQ1821=sQuery(id+"F0.wireOp",EDGE,"E2370");var subQ1822=sQuery(id+"F0.wireOp",EDGE,"E2369");var subQ1823=sQuery(id+"F0.wireOp",EDGE,"E2368");var subQ1824=sQuery(id+"F0.wireOp",EDGE,"E2367");var subQ1825=sQuery(id+"F0.wireOp",EDGE,"E2366");var subQ1826=sQuery(id+"F0.wireOp",EDGE,"E2365");var subQ1827=sQuery(id+"F0.wireOp",EDGE,"E2364");var subQ1828=sQuery(id+"F0.wireOp",EDGE,"E2363");var subQ1829=sQuery(id+"F0.wireOp",EDGE,"E2362");var subQ1830=sQuery(id+"F0.wireOp",EDGE,"E2361");var subQ1831=sQuery(id+"F0.wireOp",EDGE,"E2360");var subQ1832=sQuery(id+"F0.wireOp",EDGE,"E2359");var subQ1833=sQuery(id+"F0.wireOp",EDGE,"E2358");var subQ1834=sQuery(id+"F0.wireOp",EDGE,"E2357");var subQ1835=sQuery(id+"F0.wireOp",EDGE,"E2356");var subQ1836=sQuery(id+"F0.wireOp",EDGE,"E2355");var subQ1837=sQuery(id+"F0.wireOp",EDGE,"E2354");var subQ1838=sQuery(id+"F0.wireOp",EDGE,"E2353");var subQ1839=sQuery(id+"F0.wireOp",EDGE,"E2352");var subQ1840=sQuery(id+"F0.wireOp",EDGE,"E2351");var subQ1841=sQuery(id+"F0.wireOp",EDGE,"E2350");var subQ1842=sQuery(id+"F0.wireOp",EDGE,"E2349");var subQ1843=sQuery(id+"F0.wireOp",EDGE,"E2348");var subQ1844=sQuery(id+"F0.wireOp",EDGE,"E2347");var subQ1845=sQuery(id+"F0.wireOp",EDGE,"E2346");var subQ1846=sQuery(id+"F0.wireOp",EDGE,"E2345");var subQ1847=sQuery(id+"F0.wireOp",EDGE,"E2344");var subQ1848=sQuery(id+"F0.wireOp",EDGE,"E2343");var subQ1849=sQuery(id+"F0.wireOp",EDGE,"E2342");var subQ1850=sQuery(id+"F0.wireOp",EDGE,"E2341");var subQ1851=sQuery(id+"F0.wireOp",EDGE,"E2340");var subQ1852=sQuery(id+"F0.wireOp",EDGE,"E2339");var subQ1853=sQuery(id+"F0.wireOp",EDGE,"E2338");var subQ1854=sQuery(id+"F0.wireOp",EDGE,"E2337");var subQ1855=sQuery(id+"F0.wireOp",EDGE,"E2336");var subQ1856=sQuery(id+"F0.wireOp",EDGE,"E2335");var subQ1857=sQuery(id+"F0.wireOp",EDGE,"E2334");var subQ1858=sQuery(id+"F0.wireOp",EDGE,"E2333");var subQ1859=sQuery(id+"F0.wireOp",EDGE,"E2332");var subQ1860=sQuery(id+"F0.wireOp",EDGE,"E2331");var subQ1861=sQuery(id+"F0.wireOp",EDGE,"E2330");var subQ1862=sQuery(id+"F0.wireOp",EDGE,"E2329");var subQ1863=sQuery(id+"F0.wireOp",EDGE,"E2328");var subQ1864=sQuery(id+"F0.wireOp",EDGE,"E2327");var subQ1865=sQuery(id+"F0.wireOp",EDGE,"E2326");var subQ1866=sQuery(id+"F0.wireOp",EDGE,"E2325");var subQ1867=sQuery(id+"F0.wireOp",EDGE,"E2324");var subQ1868=sQuery(id+"F0.wireOp",EDGE,"E2323");var subQ1869=sQuery(id+"F0.wireOp",EDGE,"E2322");var subQ1870=sQuery(id+"F0.wireOp",EDGE,"E2321");var subQ1871=sQuery(id+"F0.wireOp",EDGE,"E2320");var subQ1872=sQuery(id+"F0.wireOp",EDGE,"E2319");var subQ1873=sQuery(id+"F0.wireOp",EDGE,"E2318");var subQ1874=sQuery(id+"F0.wireOp",EDGE,"E2317");var subQ1875=sQuery(id+"F0.wireOp",EDGE,"E2316");var subQ1876=sQuery(id+"F0.wireOp",EDGE,"E2315");var subQ1877=sQuery(id+"F0.wireOp",EDGE,"E2314");var subQ1878=sQuery(id+"F0.wireOp",EDGE,"E2313");var subQ1879=sQuery(id+"F0.wireOp",EDGE,"E2312");var subQ1880=sQuery(id+"F0.wireOp",EDGE,"E2311");var subQ1881=sQuery(id+"F0.wireOp",EDGE,"E2310");var subQ1882=sQuery(id+"F0.wireOp",EDGE,"E2309");var subQ1883=sQuery(id+"F0.wireOp",EDGE,"E2308");var subQ1884=sQuery(id+"F0.wireOp",EDGE,"E2307");var subQ1885=sQuery(id+"F0.wireOp",EDGE,"E2306");var subQ1886=sQuery(id+"F0.wireOp",EDGE,"E2305");var subQ1887=sQuery(id+"F0.wireOp",EDGE,"E2304");var subQ1888=sQuery(id+"F0.wireOp",EDGE,"E2303");var subQ1889=sQuery(id+"F0.wireOp",EDGE,"E2302");var subQ1890=sQuery(id+"F0.wireOp",EDGE,"E2301");var subQ1891=sQuery(id+"F0.wireOp",EDGE,"E2300");var subQ1892=sQuery(id+"F0.wireOp",EDGE,"E2299");var subQ1893=sQuery(id+"F0.wireOp",EDGE,"E2298");var subQ1894=sQuery(id+"F0.wireOp",EDGE,"E2297");var subQ1895=sQuery(id+"F0.wireOp",EDGE,"E2296");var subQ1896=sQuery(id+"F0.wireOp",EDGE,"E2295");var subQ1897=sQuery(id+"F0.wireOp",EDGE,"E2294");var subQ1898=sQuery(id+"F0.wireOp",EDGE,"E2293");var subQ1899=sQuery(id+"F0.wireOp",EDGE,"E2292");var subQ1900=sQuery(id+"F0.wireOp",EDGE,"E2291");var subQ1901=sQuery(id+"F0.wireOp",EDGE,"E2290");var subQ1902=sQuery(id+"F0.wireOp",EDGE,"E2289");var subQ1903=sQuery(id+"F0.wireOp",EDGE,"E2288");var subQ1904=sQuery(id+"F0.wireOp",EDGE,"E2287");var subQ1905=sQuery(id+"F0.wireOp",EDGE,"E2286");var subQ1906=sQuery(id+"F0.wireOp",EDGE,"E2285");var subQ1907=sQuery(id+"F0.wireOp",EDGE,"E2284");var subQ1908=sQuery(id+"F0.wireOp",EDGE,"E2283");var subQ1909=sQuery(id+"F0.wireOp",EDGE,"E2282");var subQ1910=sQuery(id+"F0.wireOp",EDGE,"E2281");var subQ1911=sQuery(id+"F0.wireOp",EDGE,"E2280");var subQ1912=sQuery(id+"F0.wireOp",EDGE,"E2279");var subQ1913=sQuery(id+"F0.wireOp",EDGE,"E2278");var subQ1914=sQuery(id+"F0.wireOp",EDGE,"E2277");var subQ1915=sQuery(id+"F0.wireOp",EDGE,"E2276");var subQ1916=sQuery(id+"F0.wireOp",EDGE,"E2275");var subQ1917=sQuery(id+"F0.wireOp",EDGE,"E2274");var subQ1918=sQuery(id+"F0.wireOp",EDGE,"E2273");var subQ1919=sQuery(id+"F0.wireOp",EDGE,"E2272");var subQ1920=sQuery(id+"F0.wireOp",EDGE,"E2271");var subQ1921=sQuery(id+"F0.wireOp",EDGE,"E2270");var subQ1922=sQuery(id+"F0.wireOp",EDGE,"E2269");var subQ1923=sQuery(id+"F0.wireOp",EDGE,"E2268");var subQ1924=sQuery(id+"F0.wireOp",EDGE,"E2267");var subQ1925=sQuery(id+"F0.wireOp",EDGE,"E2266");var subQ1926=sQuery(id+"F0.wireOp",EDGE,"E2265");var subQ1927=sQuery(id+"F0.wireOp",EDGE,"E2264");var subQ1928=sQuery(id+"F0.wireOp",EDGE,"E2263");var subQ1929=sQuery(id+"F0.wireOp",EDGE,"E2262");var subQ1930=sQuery(id+"F0.wireOp",EDGE,"E2261");var subQ1931=sQuery(id+"F0.wireOp",EDGE,"E2260");var subQ1932=sQuery(id+"F0.wireOp",EDGE,"E2259");var subQ1933=sQuery(id+"F0.wireOp",EDGE,"E2258");var subQ1934=sQuery(id+"F0.wireOp",EDGE,"E2257");var subQ1935=sQuery(id+"F0.wireOp",EDGE,"E2256");var subQ1936=sQuery(id+"F0.wireOp",EDGE,"E2255");var subQ1937=sQuery(id+"F0.wireOp",EDGE,"E2254");var subQ1938=sQuery(id+"F0.wireOp",EDGE,"E2253");var subQ1939=sQuery(id+"F0.wireOp",EDGE,"E2252");var subQ1940=sQuery(id+"F0.wireOp",EDGE,"E2251");var subQ1941=sQuery(id+"F0.wireOp",EDGE,"E2250");var subQ1942=sQuery(id+"F0.wireOp",EDGE,"E2249");var subQ1943=sQuery(id+"F0.wireOp",EDGE,"E2248");var subQ1944=sQuery(id+"F0.wireOp",EDGE,"E2247");var subQ1945=sQuery(id+"F0.wireOp",EDGE,"E2246");var subQ1946=sQuery(id+"F0.wireOp",EDGE,"E2245");var subQ1947=sQuery(id+"F0.wireOp",EDGE,"E2244");var subQ1948=sQuery(id+"F0.wireOp",EDGE,"E2243");var subQ1949=sQuery(id+"F0.wireOp",EDGE,"E2242");var subQ1950=sQuery(id+"F0.wireOp",EDGE,"E2241");var subQ1951=sQuery(id+"F0.wireOp",EDGE,"E2240");var subQ1952=sQuery(id+"F0.wireOp",EDGE,"E2239");var subQ1953=sQuery(id+"F0.wireOp",EDGE,"E2238");var subQ1954=sQuery(id+"F0.wireOp",EDGE,"E2237");var subQ1955=sQuery(id+"F0.wireOp",EDGE,"E2236");var subQ1956=sQuery(id+"F0.wireOp",EDGE,"E2235");var subQ1957=sQuery(id+"F0.wireOp",EDGE,"E2234");var subQ1958=sQuery(id+"F0.wireOp",EDGE,"E2233");var subQ1959=sQuery(id+"F0.wireOp",EDGE,"E2232");var subQ1960=sQuery(id+"F0.wireOp",EDGE,"E2231");var subQ1961=sQuery(id+"F0.wireOp",EDGE,"E2230");var subQ1962=sQuery(id+"F0.wireOp",EDGE,"E2229");var subQ1963=sQuery(id+"F0.wireOp",EDGE,"E2228");var subQ1964=sQuery(id+"F0.wireOp",EDGE,"E2227");var subQ1965=sQuery(id+"F0.wireOp",EDGE,"E2226");var subQ1966=sQuery(id+"F0.wireOp",EDGE,"E2225");var subQ1967=sQuery(id+"F0.wireOp",EDGE,"E2224");var subQ1968=sQuery(id+"F0.wireOp",EDGE,"E2223");var subQ1969=sQuery(id+"F0.wireOp",EDGE,"E2222");var subQ1970=sQuery(id+"F0.wireOp",EDGE,"E2221");var subQ1971=sQuery(id+"F0.wireOp",EDGE,"E2220");var subQ1972=sQuery(id+"F0.wireOp",EDGE,"E2219");var subQ1973=sQuery(id+"F0.wireOp",EDGE,"E2218");var subQ1974=sQuery(id+"F0.wireOp",EDGE,"E2217");var subQ1975=sQuery(id+"F0.wireOp",EDGE,"E2216");var subQ1976=sQuery(id+"F0.wireOp",EDGE,"E2215");var subQ1977=sQuery(id+"F0.wireOp",EDGE,"E2214");var subQ1978=sQuery(id+"F0.wireOp",EDGE,"E2213");var subQ1979=sQuery(id+"F0.wireOp",EDGE,"E2212");var subQ1980=sQuery(id+"F0.wireOp",EDGE,"E2211");var subQ1981=sQuery(id+"F0.wireOp",EDGE,"E2210");var subQ1982=sQuery(id+"F0.wireOp",EDGE,"E2209");var subQ1983=sQuery(id+"F0.wireOp",EDGE,"E2208");var subQ1984=sQuery(id+"F0.wireOp",EDGE,"E2207");var subQ1985=sQuery(id+"F0.wireOp",EDGE,"E2206");var subQ1986=sQuery(id+"F0.wireOp",EDGE,"E2205");var subQ1987=sQuery(id+"F0.wireOp",EDGE,"E2204");var subQ1988=sQuery(id+"F0.wireOp",EDGE,"E2203");var subQ1989=sQuery(id+"F0.wireOp",EDGE,"E2202");var subQ1990=sQuery(id+"F0.wireOp",EDGE,"E2201");var subQ1991=sQuery(id+"F0.wireOp",EDGE,"E2200");var subQ1992=sQuery(id+"F0.wireOp",EDGE,"E2199");var subQ1993=sQuery(id+"F0.wireOp",EDGE,"E2198");var subQ1994=sQuery(id+"F0.wireOp",EDGE,"E2197");var subQ1995=sQuery(id+"F0.wireOp",EDGE,"E2196");var subQ1996=sQuery(id+"F0.wireOp",EDGE,"E2195");var subQ1997=sQuery(id+"F0.wireOp",EDGE,"E2194");var subQ1998=sQuery(id+"F0.wireOp",EDGE,"E2193");var subQ1999=sQuery(id+"F0.wireOp",EDGE,"E2192");var subQ2000=sQuery(id+"F0.wireOp",EDGE,"E2191");var subQ2001=sQuery(id+"F0.wireOp",EDGE,"E2190");var subQ2002=sQuery(id+"F0.wireOp",EDGE,"E2189");var subQ2003=sQuery(id+"F0.wireOp",EDGE,"E2188");var subQ2004=sQuery(id+"F0.wireOp",EDGE,"E2187");var subQ2005=sQuery(id+"F0.wireOp",EDGE,"E2186");var subQ2006=sQuery(id+"F0.wireOp",EDGE,"E2185");var subQ2007=sQuery(id+"F0.wireOp",EDGE,"E2184");var subQ2008=sQuery(id+"F0.wireOp",EDGE,"E2183");var subQ2009=sQuery(id+"F0.wireOp",EDGE,"E2182");var subQ2010=sQuery(id+"F0.wireOp",EDGE,"E2181");var subQ2011=sQuery(id+"F0.wireOp",EDGE,"E2180");var subQ2012=sQuery(id+"F0.wireOp",EDGE,"E2179");var subQ2013=sQuery(id+"F0.wireOp",EDGE,"E2178");var subQ2014=sQuery(id+"F0.wireOp",EDGE,"E2177");var subQ2015=sQuery(id+"F0.wireOp",EDGE,"E2176");var subQ2016=sQuery(id+"F0.wireOp",EDGE,"E2175");var subQ2017=sQuery(id+"F0.wireOp",EDGE,"E2174");var subQ2018=sQuery(id+"F0.wireOp",EDGE,"E2173");var subQ2019=sQuery(id+"F0.wireOp",EDGE,"E2172");var subQ2020=sQuery(id+"F0.wireOp",EDGE,"E2171");var subQ2021=sQuery(id+"F0.wireOp",EDGE,"E2170");var subQ2022=sQuery(id+"F0.wireOp",EDGE,"E2169");var subQ2023=sQuery(id+"F0.wireOp",EDGE,"E2168");var subQ2024=sQuery(id+"F0.wireOp",EDGE,"E2167");var subQ2025=sQuery(id+"F0.wireOp",EDGE,"E2166");var subQ2026=sQuery(id+"F0.wireOp",EDGE,"E2165");var subQ2027=sQuery(id+"F0.wireOp",EDGE,"E2164");var subQ2028=sQuery(id+"F0.wireOp",EDGE,"E2163");var subQ2029=sQuery(id+"F0.wireOp",EDGE,"E2162");var subQ2030=sQuery(id+"F0.wireOp",EDGE,"E2161");var subQ2031=sQuery(id+"F0.wireOp",EDGE,"E2160");var subQ2032=sQuery(id+"F0.wireOp",EDGE,"E2159");var subQ2033=sQuery(id+"F0.wireOp",EDGE,"E2158");var subQ2034=sQuery(id+"F0.wireOp",EDGE,"E2157");var subQ2035=sQuery(id+"F0.wireOp",EDGE,"E2156");var subQ2036=sQuery(id+"F0.wireOp",EDGE,"E2155");var subQ2037=sQuery(id+"F0.wireOp",EDGE,"E2154");var subQ2038=sQuery(id+"F0.wireOp",EDGE,"E2153");var subQ2039=sQuery(id+"F0.wireOp",EDGE,"E2152");var subQ2040=sQuery(id+"F0.wireOp",EDGE,"E2151");var subQ2041=sQuery(id+"F0.wireOp",EDGE,"E2150");var subQ2042=sQuery(id+"F0.wireOp",EDGE,"E2149");var subQ2043=sQuery(id+"F0.wireOp",EDGE,"E2148");var subQ2044=sQuery(id+"F0.wireOp",EDGE,"E2147");var subQ2045=sQuery(id+"F0.wireOp",EDGE,"E2146");var subQ2046=sQuery(id+"F0.wireOp",EDGE,"E2145");var subQ2047=sQuery(id+"F0.wireOp",EDGE,"E2144");var subQ2048=sQuery(id+"F0.wireOp",EDGE,"E2143");var subQ2049=sQuery(id+"F0.wireOp",EDGE,"E2142");var subQ2050=sQuery(id+"F0.wireOp",EDGE,"E2141");var subQ2051=sQuery(id+"F0.wireOp",EDGE,"E2140");var subQ2052=sQuery(id+"F0.wireOp",EDGE,"E2139");var subQ2053=sQuery(id+"F0.wireOp",EDGE,"E2138");var subQ2054=sQuery(id+"F0.wireOp",EDGE,"E2137");var subQ2055=sQuery(id+"F0.wireOp",EDGE,"E2136");var subQ2056=sQuery(id+"F0.wireOp",EDGE,"E2135");var subQ2057=sQuery(id+"F0.wireOp",EDGE,"E2134");var subQ2058=sQuery(id+"F0.wireOp",EDGE,"E2133");var subQ2059=sQuery(id+"F0.wireOp",EDGE,"E2132");var subQ2060=sQuery(id+"F0.wireOp",EDGE,"E2131");var subQ2061=sQuery(id+"F0.wireOp",EDGE,"E2130");var subQ2062=sQuery(id+"F0.wireOp",EDGE,"E2129");var subQ2063=sQuery(id+"F0.wireOp",EDGE,"E2128");var subQ2064=sQuery(id+"F0.wireOp",EDGE,"E2127");var subQ2065=sQuery(id+"F0.wireOp",EDGE,"E2126");var subQ2066=sQuery(id+"F0.wireOp",EDGE,"E2125");var subQ2067=sQuery(id+"F0.wireOp",EDGE,"E2124");var subQ2068=sQuery(id+"F0.wireOp",EDGE,"E2123");var subQ2069=sQuery(id+"F0.wireOp",EDGE,"E2122");var subQ2070=sQuery(id+"F0.wireOp",EDGE,"E2121");var subQ2071=sQuery(id+"F0.wireOp",EDGE,"E2120");var subQ2072=sQuery(id+"F0.wireOp",EDGE,"E2119");var subQ2073=sQuery(id+"F0.wireOp",EDGE,"E2118");var subQ2074=sQuery(id+"F0.wireOp",EDGE,"E2117");var subQ2075=sQuery(id+"F0.wireOp",EDGE,"E2116");var subQ2076=sQuery(id+"F0.wireOp",EDGE,"E2115");var subQ2077=sQuery(id+"F0.wireOp",EDGE,"E2114");var subQ2078=sQuery(id+"F0.wireOp",EDGE,"E2113");var subQ2079=sQuery(id+"F0.wireOp",EDGE,"E2112");var subQ2080=sQuery(id+"F0.wireOp",EDGE,"E2111");var subQ2081=sQuery(id+"F0.wireOp",EDGE,"E2110");var subQ2082=sQuery(id+"F0.wireOp",EDGE,"E2109");var subQ2083=sQuery(id+"F0.wireOp",EDGE,"E2108");var subQ2084=sQuery(id+"F0.wireOp",EDGE,"E2107");var subQ2085=sQuery(id+"F0.wireOp",EDGE,"E2106");var subQ2086=sQuery(id+"F0.wireOp",EDGE,"E2105");var subQ2087=sQuery(id+"F0.wireOp",EDGE,"E2104");var subQ2088=sQuery(id+"F0.wireOp",EDGE,"E2103");var subQ2089=sQuery(id+"F0.wireOp",EDGE,"E2102");var subQ2090=sQuery(id+"F0.wireOp",EDGE,"E2101");var subQ2091=sQuery(id+"F0.wireOp",EDGE,"E2100");var subQ2092=sQuery(id+"F0.wireOp",EDGE,"E2099");var subQ2093=sQuery(id+"F0.wireOp",EDGE,"E2098");var subQ2094=sQuery(id+"F0.wireOp",EDGE,"E2097");var subQ2095=sQuery(id+"F0.wireOp",EDGE,"E2096");var subQ2096=sQuery(id+"F0.wireOp",EDGE,"E2095");var subQ2097=sQuery(id+"F0.wireOp",EDGE,"E2094");var subQ2098=sQuery(id+"F0.wireOp",EDGE,"E2093");var subQ2099=sQuery(id+"F0.wireOp",EDGE,"E2092");var subQ2100=sQuery(id+"F0.wireOp",EDGE,"E2091");var subQ2101=sQuery(id+"F0.wireOp",EDGE,"E2090");var subQ2102=sQuery(id+"F0.wireOp",EDGE,"E2089");var subQ2103=sQuery(id+"F0.wireOp",EDGE,"E2088");var subQ2104=sQuery(id+"F0.wireOp",EDGE,"E2087");var subQ2105=sQuery(id+"F0.wireOp",EDGE,"E2086");var subQ2106=sQuery(id+"F0.wireOp",EDGE,"E2085");var subQ2107=sQuery(id+"F0.wireOp",EDGE,"E2084");var subQ2108=sQuery(id+"F0.wireOp",EDGE,"E2083");var subQ2109=sQuery(id+"F0.wireOp",EDGE,"E2082");var subQ2110=sQuery(id+"F0.wireOp",EDGE,"E2081");var subQ2111=sQuery(id+"F0.wireOp",EDGE,"E2080");var subQ2112=sQuery(id+"F0.wireOp",EDGE,"E2079");var subQ2113=sQuery(id+"F0.wireOp",EDGE,"E2078");var subQ2114=sQuery(id+"F0.wireOp",EDGE,"E2077");var subQ2115=sQuery(id+"F0.wireOp",EDGE,"E2076");var subQ2116=sQuery(id+"F0.wireOp",EDGE,"E2075");var subQ2117=sQuery(id+"F0.wireOp",EDGE,"E2074");var subQ2118=sQuery(id+"F0.wireOp",EDGE,"E2073");var subQ2119=sQuery(id+"F0.wireOp",EDGE,"E2072");var subQ2120=sQuery(id+"F0.wireOp",EDGE,"E2071");var subQ2121=sQuery(id+"F0.wireOp",EDGE,"E2070");var subQ2122=sQuery(id+"F0.wireOp",EDGE,"E2069");var subQ2123=sQuery(id+"F0.wireOp",EDGE,"E2068");var subQ2124=sQuery(id+"F0.wireOp",EDGE,"E2067");var subQ2125=sQuery(id+"F0.wireOp",EDGE,"E2066");var subQ2126=sQuery(id+"F0.wireOp",EDGE,"E2065");var subQ2127=sQuery(id+"F0.wireOp",EDGE,"E2064");var subQ2128=sQuery(id+"F0.wireOp",EDGE,"E2063");var subQ2129=sQuery(id+"F0.wireOp",EDGE,"E2062");var subQ2130=sQuery(id+"F0.wireOp",EDGE,"E2061");var subQ2131=sQuery(id+"F0.wireOp",EDGE,"E2060");var subQ2132=sQuery(id+"F0.wireOp",EDGE,"E2059");var subQ2133=sQuery(id+"F0.wireOp",EDGE,"E2058");var subQ2134=sQuery(id+"F0.wireOp",EDGE,"E2057");var subQ2135=sQuery(id+"F0.wireOp",EDGE,"E2056");var subQ2136=sQuery(id+"F0.wireOp",EDGE,"E2055");var subQ2137=sQuery(id+"F0.wireOp",EDGE,"E2054");var subQ2138=sQuery(id+"F0.wireOp",EDGE,"E2053");var subQ2139=sQuery(id+"F0.wireOp",EDGE,"E2052");var subQ2140=sQuery(id+"F0.wireOp",EDGE,"E2051");var subQ2141=sQuery(id+"F0.wireOp",EDGE,"E2050");var subQ2142=sQuery(id+"F0.wireOp",EDGE,"E2049");var subQ2143=sQuery(id+"F0.wireOp",EDGE,"E2048");var subQ2144=sQuery(id+"F0.wireOp",EDGE,"E2047");var subQ2145=sQuery(id+"F0.wireOp",EDGE,"E2046");var subQ2146=sQuery(id+"F0.wireOp",EDGE,"E2045");var subQ2147=sQuery(id+"F0.wireOp",EDGE,"E2044");var subQ2148=sQuery(id+"F0.wireOp",EDGE,"E2043");var subQ2149=sQuery(id+"F0.wireOp",EDGE,"E2042");var subQ2150=sQuery(id+"F0.wireOp",EDGE,"E2041");var subQ2151=sQuery(id+"F0.wireOp",EDGE,"E2040");var subQ2152=sQuery(id+"F0.wireOp",EDGE,"E2039");var subQ2153=sQuery(id+"F0.wireOp",EDGE,"E2038");var subQ2154=sQuery(id+"F0.wireOp",EDGE,"E2037");var subQ2155=sQuery(id+"F0.wireOp",EDGE,"E2036");var subQ2156=sQuery(id+"F0.wireOp",EDGE,"E2035");var subQ2157=sQuery(id+"F0.wireOp",EDGE,"E2034");var subQ2158=sQuery(id+"F0.wireOp",EDGE,"E2033");var subQ2159=sQuery(id+"F0.wireOp",EDGE,"E2032");var subQ2160=sQuery(id+"F0.wireOp",EDGE,"E2031");var subQ2161=sQuery(id+"F0.wireOp",EDGE,"E2030");var subQ2162=sQuery(id+"F0.wireOp",EDGE,"E2029");var subQ2163=sQuery(id+"F0.wireOp",EDGE,"E2028");var subQ2164=sQuery(id+"F0.wireOp",EDGE,"E2027");var subQ2165=sQuery(id+"F0.wireOp",EDGE,"E2026");var subQ2166=sQuery(id+"F0.wireOp",EDGE,"E2025");var subQ2167=sQuery(id+"F0.wireOp",EDGE,"E2024");var subQ2168=sQuery(id+"F0.wireOp",EDGE,"E2023");var subQ2169=sQuery(id+"F0.wireOp",EDGE,"E2022");var subQ2170=sQuery(id+"F0.wireOp",EDGE,"E2021");var subQ2171=sQuery(id+"F0.wireOp",EDGE,"E2020");var subQ2172=sQuery(id+"F0.wireOp",EDGE,"E2019");var subQ2173=sQuery(id+"F0.wireOp",EDGE,"E2018");var subQ2174=sQuery(id+"F0.wireOp",EDGE,"E2017");var subQ2175=sQuery(id+"F0.wireOp",EDGE,"E2016");var subQ2176=sQuery(id+"F0.wireOp",EDGE,"E2015");var subQ2177=sQuery(id+"F0.wireOp",EDGE,"E2014");var subQ2178=sQuery(id+"F0.wireOp",EDGE,"E2013");var subQ2179=sQuery(id+"F0.wireOp",EDGE,"E2012");var subQ2180=sQuery(id+"F0.wireOp",EDGE,"E2011");var subQ2181=sQuery(id+"F0.wireOp",EDGE,"E2010");var subQ2182=sQuery(id+"F0.wireOp",EDGE,"E2009");var subQ2183=sQuery(id+"F0.wireOp",EDGE,"E2008");var subQ2184=sQuery(id+"F0.wireOp",EDGE,"E2007");var subQ2185=sQuery(id+"F0.wireOp",EDGE,"E2006");var subQ2186=sQuery(id+"F0.wireOp",EDGE,"E2005");var subQ2187=sQuery(id+"F0.wireOp",EDGE,"E2004");var subQ2188=sQuery(id+"F0.wireOp",EDGE,"E2003");var subQ2189=sQuery(id+"F0.wireOp",EDGE,"E2002");var subQ2190=sQuery(id+"F0.wireOp",EDGE,"E2001");var subQ2191=sQuery(id+"F0.wireOp",EDGE,"E2000");var subQ2192=sQuery(id+"F0.wireOp",EDGE,"E1999");var subQ2193=sQuery(id+"F0.wireOp",EDGE,"E1998");var subQ2194=sQuery(id+"F0.wireOp",EDGE,"E1997");var subQ2195=sQuery(id+"F0.wireOp",EDGE,"E1996");var subQ2196=sQuery(id+"F0.wireOp",EDGE,"E1995");var subQ2197=sQuery(id+"F0.wireOp",EDGE,"E1994");var subQ2198=sQuery(id+"F0.wireOp",EDGE,"E1993");var subQ2199=sQuery(id+"F0.wireOp",EDGE,"E1992");var subQ2200=sQuery(id+"F0.wireOp",EDGE,"E1991");var subQ2201=sQuery(id+"F0.wireOp",EDGE,"E1990");var subQ2202=sQuery(id+"F0.wireOp",EDGE,"E1989");var subQ2203=sQuery(id+"F0.wireOp",EDGE,"E1988");var subQ2204=sQuery(id+"F0.wireOp",EDGE,"E1987");var subQ2205=sQuery(id+"F0.wireOp",EDGE,"E1986");var subQ2206=sQuery(id+"F0.wireOp",EDGE,"E1985");var subQ2207=sQuery(id+"F0.wireOp",EDGE,"E1984");var subQ2208=sQuery(id+"F0.wireOp",EDGE,"E1983");var subQ2209=sQuery(id+"F0.wireOp",EDGE,"E1982");var subQ2210=sQuery(id+"F0.wireOp",EDGE,"E1981");var subQ2211=sQuery(id+"F0.wireOp",EDGE,"E1980");var subQ2212=sQuery(id+"F0.wireOp",EDGE,"E1979");var subQ2213=sQuery(id+"F0.wireOp",EDGE,"E1978");var subQ2214=sQuery(id+"F0.wireOp",EDGE,"E1977");var subQ2215=sQuery(id+"F0.wireOp",EDGE,"E1976");var subQ2216=sQuery(id+"F0.wireOp",EDGE,"E1975");var subQ2217=sQuery(id+"F0.wireOp",EDGE,"E1974");var subQ2218=sQuery(id+"F0.wireOp",EDGE,"E1973");var subQ2219=sQuery(id+"F0.wireOp",EDGE,"E1972");var subQ2220=sQuery(id+"F0.wireOp",EDGE,"E1971");var subQ2221=sQuery(id+"F0.wireOp",EDGE,"E1970");var subQ2222=sQuery(id+"F0.wireOp",EDGE,"E1969");var subQ2223=sQuery(id+"F0.wireOp",EDGE,"E1968");var subQ2224=sQuery(id+"F0.wireOp",EDGE,"E1967");var subQ2225=sQuery(id+"F0.wireOp",EDGE,"E1966");var subQ2226=sQuery(id+"F0.wireOp",EDGE,"E1965");var subQ2227=sQuery(id+"F0.wireOp",EDGE,"E1964");var subQ2228=sQuery(id+"F0.wireOp",EDGE,"E1963");var subQ2229=sQuery(id+"F0.wireOp",EDGE,"E1962");var subQ2230=sQuery(id+"F0.wireOp",EDGE,"E1961");var subQ2231=sQuery(id+"F0.wireOp",EDGE,"E1960");var subQ2232=sQuery(id+"F0.wireOp",EDGE,"E1959");var subQ2233=sQuery(id+"F0.wireOp",EDGE,"E1958");var subQ2234=sQuery(id+"F0.wireOp",EDGE,"E1957");var subQ2235=sQuery(id+"F0.wireOp",EDGE,"E1956");var subQ2236=sQuery(id+"F0.wireOp",EDGE,"E1955");var subQ2237=sQuery(id+"F0.wireOp",EDGE,"E1954");var subQ2238=sQuery(id+"F0.wireOp",EDGE,"E1953");var subQ2239=sQuery(id+"F0.wireOp",EDGE,"E1952");var subQ2240=sQuery(id+"F0.wireOp",EDGE,"E1951");var subQ2241=sQuery(id+"F0.wireOp",EDGE,"E1950");var subQ2242=sQuery(id+"F0.wireOp",EDGE,"E1949");var subQ2243=sQuery(id+"F0.wireOp",EDGE,"E1948");var subQ2244=sQuery(id+"F0.wireOp",EDGE,"E1947");var subQ2245=sQuery(id+"F0.wireOp",EDGE,"E1946");var subQ2246=sQuery(id+"F0.wireOp",EDGE,"E1945");var subQ2247=sQuery(id+"F0.wireOp",EDGE,"E1944");var subQ2248=sQuery(id+"F0.wireOp",EDGE,"E1943");var subQ2249=sQuery(id+"F0.wireOp",EDGE,"E1942");var subQ2250=sQuery(id+"F0.wireOp",EDGE,"E1941");var subQ2251=sQuery(id+"F0.wireOp",EDGE,"E1940");var subQ2252=sQuery(id+"F0.wireOp",EDGE,"E1939");var subQ2253=sQuery(id+"F0.wireOp",EDGE,"E1938");var subQ2254=sQuery(id+"F0.wireOp",EDGE,"E1937");var subQ2255=sQuery(id+"F0.wireOp",EDGE,"E1936");var subQ2256=sQuery(id+"F0.wireOp",EDGE,"E1935");var subQ2257=sQuery(id+"F0.wireOp",EDGE,"E1934");var subQ2258=sQuery(id+"F0.wireOp",EDGE,"E1933");var subQ2259=sQuery(id+"F0.wireOp",EDGE,"E1932");var subQ2260=sQuery(id+"F0.wireOp",EDGE,"E1931");var subQ2261=sQuery(id+"F0.wireOp",EDGE,"E1930");var subQ2262=sQuery(id+"F0.wireOp",EDGE,"E1929");var subQ2263=sQuery(id+"F0.wireOp",EDGE,"E1928");var subQ2264=sQuery(id+"F0.wireOp",EDGE,"E1927");var subQ2265=sQuery(id+"F0.wireOp",EDGE,"E1926");var subQ2266=sQuery(id+"F0.wireOp",EDGE,"E1925");var subQ2267=sQuery(id+"F0.wireOp",EDGE,"E1924");var subQ2268=sQuery(id+"F0.wireOp",EDGE,"E1923");var subQ2269=sQuery(id+"F0.wireOp",EDGE,"E1922");var subQ2270=sQuery(id+"F0.wireOp",EDGE,"E1921");var subQ2271=sQuery(id+"F0.wireOp",EDGE,"E1920");var subQ2272=sQuery(id+"F0.wireOp",EDGE,"E1919");var subQ2273=sQuery(id+"F0.wireOp",EDGE,"E1918");var subQ2274=sQuery(id+"F0.wireOp",EDGE,"E1917");var subQ2275=sQuery(id+"F0.wireOp",EDGE,"E1916");var subQ2276=sQuery(id+"F0.wireOp",EDGE,"E1915");var subQ2277=sQuery(id+"F0.wireOp",EDGE,"E1914");var subQ2278=sQuery(id+"F0.wireOp",EDGE,"E1913");var subQ2279=sQuery(id+"F0.wireOp",EDGE,"E1912");var subQ2280=sQuery(id+"F0.wireOp",EDGE,"E1911");var subQ2281=sQuery(id+"F0.wireOp",EDGE,"E1910");var subQ2282=sQuery(id+"F0.wireOp",EDGE,"E1909");var subQ2283=sQuery(id+"F0.wireOp",EDGE,"E1908");var subQ2284=sQuery(id+"F0.wireOp",EDGE,"E1907");var subQ2285=sQuery(id+"F0.wireOp",EDGE,"E1906");var subQ2286=sQuery(id+"F0.wireOp",EDGE,"E1905");var subQ2287=sQuery(id+"F0.wireOp",EDGE,"E1904");var subQ2288=sQuery(id+"F0.wireOp",EDGE,"E1903");var subQ2289=sQuery(id+"F0.wireOp",EDGE,"E1902");var subQ2290=sQuery(id+"F0.wireOp",EDGE,"E1901");var subQ2291=sQuery(id+"F0.wireOp",EDGE,"E1900");var subQ2292=sQuery(id+"F0.wireOp",EDGE,"E1899");var subQ2293=sQuery(id+"F0.wireOp",EDGE,"E1898");var subQ2294=sQuery(id+"F0.wireOp",EDGE,"E1897");var subQ2295=sQuery(id+"F0.wireOp",EDGE,"E1896");var subQ2296=sQuery(id+"F0.wireOp",EDGE,"E1895");var subQ2297=sQuery(id+"F0.wireOp",EDGE,"E1894");var subQ2298=sQuery(id+"F0.wireOp",EDGE,"E1893");var subQ2299=sQuery(id+"F0.wireOp",EDGE,"E1892");var subQ2300=sQuery(id+"F0.wireOp",EDGE,"E1891");var subQ2301=sQuery(id+"F0.wireOp",EDGE,"E1890");var subQ2302=sQuery(id+"F0.wireOp",EDGE,"E1889");var subQ2303=sQuery(id+"F0.wireOp",EDGE,"E1888");var subQ2304=sQuery(id+"F0.wireOp",EDGE,"E1887");var subQ2305=sQuery(id+"F0.wireOp",EDGE,"E1886");var subQ2306=sQuery(id+"F0.wireOp",EDGE,"E1885");var subQ2307=sQuery(id+"F0.wireOp",EDGE,"E1884");var subQ2308=sQuery(id+"F0.wireOp",EDGE,"E1883");var subQ2309=sQuery(id+"F0.wireOp",EDGE,"E1882");var subQ2310=sQuery(id+"F0.wireOp",EDGE,"E1881");var subQ2311=sQuery(id+"F0.wireOp",EDGE,"E1880");var subQ2312=sQuery(id+"F0.wireOp",EDGE,"E1879");var subQ2313=sQuery(id+"F0.wireOp",EDGE,"E1878");var subQ2314=sQuery(id+"F0.wireOp",EDGE,"E1877");var subQ2315=sQuery(id+"F0.wireOp",EDGE,"E1876");var subQ2316=sQuery(id+"F0.wireOp",EDGE,"E1875");var subQ2317=sQuery(id+"F0.wireOp",EDGE,"E1874");var subQ2318=sQuery(id+"F0.wireOp",EDGE,"E1873");var subQ2319=sQuery(id+"F0.wireOp",EDGE,"E1872");var subQ2320=sQuery(id+"F0.wireOp",EDGE,"E1871");var subQ2321=sQuery(id+"F0.wireOp",EDGE,"E1870");var subQ2322=sQuery(id+"F0.wireOp",EDGE,"E1869");var subQ2323=sQuery(id+"F0.wireOp",EDGE,"E1868");var subQ2324=sQuery(id+"F0.wireOp",EDGE,"E1867");var subQ2325=sQuery(id+"F0.wireOp",EDGE,"E1866");var subQ2326=sQuery(id+"F0.wireOp",EDGE,"E1865");var subQ2327=sQuery(id+"F0.wireOp",EDGE,"E1864");var subQ2328=sQuery(id+"F0.wireOp",EDGE,"E1863");var subQ2329=sQuery(id+"F0.wireOp",EDGE,"E1862");var subQ2330=sQuery(id+"F0.wireOp",EDGE,"E1861");var subQ2331=sQuery(id+"F0.wireOp",EDGE,"E1860");var subQ2332=sQuery(id+"F0.wireOp",EDGE,"E1859");var subQ2333=sQuery(id+"F0.wireOp",EDGE,"E1858");var subQ2334=sQuery(id+"F0.wireOp",EDGE,"E1857");var subQ2335=sQuery(id+"F0.wireOp",EDGE,"E1856");var subQ2336=sQuery(id+"F0.wireOp",EDGE,"E1855");var subQ2337=sQuery(id+"F0.wireOp",EDGE,"E1854");var subQ2338=sQuery(id+"F0.wireOp",EDGE,"E1853");var subQ2339=sQuery(id+"F0.wireOp",EDGE,"E1852");var subQ2340=sQuery(id+"F0.wireOp",EDGE,"E1851");var subQ2341=sQuery(id+"F0.wireOp",EDGE,"E1850");var subQ2342=sQuery(id+"F0.wireOp",EDGE,"E1849");var subQ2343=sQuery(id+"F0.wireOp",EDGE,"E1848");var subQ2344=sQuery(id+"F0.wireOp",EDGE,"E1847");var subQ2345=sQuery(id+"F0.wireOp",EDGE,"E1846");var subQ2346=sQuery(id+"F0.wireOp",EDGE,"E1845");var subQ2347=sQuery(id+"F0.wireOp",EDGE,"E1844");var subQ2348=sQuery(id+"F0.wireOp",EDGE,"E1843");var subQ2349=sQuery(id+"F0.wireOp",EDGE,"E1842");var subQ2350=sQuery(id+"F0.wireOp",EDGE,"E1841");var subQ2351=sQuery(id+"F0.wireOp",EDGE,"E1840");var subQ2352=sQuery(id+"F0.wireOp",EDGE,"E1839");var subQ2353=sQuery(id+"F0.wireOp",EDGE,"E1838");var subQ2354=sQuery(id+"F0.wireOp",EDGE,"E1837");var subQ2355=sQuery(id+"F0.wireOp",EDGE,"E1836");var subQ2356=sQuery(id+"F0.wireOp",EDGE,"E1835");var subQ2357=sQuery(id+"F0.wireOp",EDGE,"E1834");var subQ2358=sQuery(id+"F0.wireOp",EDGE,"E1833");var subQ2359=sQuery(id+"F0.wireOp",EDGE,"E1832");var subQ2360=sQuery(id+"F0.wireOp",EDGE,"E1831");var subQ2361=sQuery(id+"F0.wireOp",EDGE,"E1830");var subQ2362=sQuery(id+"F0.wireOp",EDGE,"E1829");var subQ2363=sQuery(id+"F0.wireOp",EDGE,"E1828");var subQ2364=sQuery(id+"F0.wireOp",EDGE,"E1827");var subQ2365=sQuery(id+"F0.wireOp",EDGE,"E1826");var subQ2366=sQuery(id+"F0.wireOp",EDGE,"E1825");var subQ2367=sQuery(id+"F0.wireOp",EDGE,"E1824");var subQ2368=sQuery(id+"F0.wireOp",EDGE,"E1823");var subQ2369=sQuery(id+"F0.wireOp",EDGE,"E1822");var subQ2370=sQuery(id+"F0.wireOp",EDGE,"E1821");var subQ2371=sQuery(id+"F0.wireOp",EDGE,"E1820");var subQ2372=sQuery(id+"F0.wireOp",EDGE,"E1819");var subQ2373=sQuery(id+"F0.wireOp",EDGE,"E1818");var subQ2374=sQuery(id+"F0.wireOp",EDGE,"E1817");var subQ2375=sQuery(id+"F0.wireOp",EDGE,"E1816");var subQ2376=sQuery(id+"F0.wireOp",EDGE,"E1815");var subQ2377=sQuery(id+"F0.wireOp",EDGE,"E1814");var subQ2378=sQuery(id+"F0.wireOp",EDGE,"E1813");var subQ2379=sQuery(id+"F0.wireOp",EDGE,"E1812");var subQ2380=sQuery(id+"F0.wireOp",EDGE,"E1811");var subQ2381=sQuery(id+"F0.wireOp",EDGE,"E1810");var subQ2382=sQuery(id+"F0.wireOp",EDGE,"E1809");var subQ2383=sQuery(id+"F0.wireOp",EDGE,"E1808");var subQ2384=sQuery(id+"F0.wireOp",EDGE,"E1807");var subQ2385=sQuery(id+"F0.wireOp",EDGE,"E1806");var subQ2386=sQuery(id+"F0.wireOp",EDGE,"E1805");var subQ2387=sQuery(id+"F0.wireOp",EDGE,"E1804");var subQ2388=sQuery(id+"F0.wireOp",EDGE,"E1803");var subQ2389=sQuery(id+"F0.wireOp",EDGE,"E1802");var subQ2390=sQuery(id+"F0.wireOp",EDGE,"E1801");var subQ2391=sQuery(id+"F0.wireOp",EDGE,"E1800");var subQ2392=sQuery(id+"F0.wireOp",EDGE,"E1799");var subQ2393=sQuery(id+"F0.wireOp",EDGE,"E1798");var subQ2394=sQuery(id+"F0.wireOp",EDGE,"E1797");var subQ2395=sQuery(id+"F0.wireOp",EDGE,"E1796");var subQ2396=sQuery(id+"F0.wireOp",EDGE,"E1795");var subQ2397=sQuery(id+"F0.wireOp",EDGE,"E1794");var subQ2398=sQuery(id+"F0.wireOp",EDGE,"E1793");var subQ2399=sQuery(id+"F0.wireOp",EDGE,"E1792");var subQ2400=sQuery(id+"F0.wireOp",EDGE,"E1791");var subQ2401=sQuery(id+"F0.wireOp",EDGE,"E1790");var subQ2402=sQuery(id+"F0.wireOp",EDGE,"E1789");var subQ2403=sQuery(id+"F0.wireOp",EDGE,"E1788");var subQ2404=sQuery(id+"F0.wireOp",EDGE,"E1787");var subQ2405=sQuery(id+"F0.wireOp",EDGE,"E1786");var subQ2406=sQuery(id+"F0.wireOp",EDGE,"E1785");var subQ2407=sQuery(id+"F0.wireOp",EDGE,"E1784");var subQ2408=sQuery(id+"F0.wireOp",EDGE,"E1783");var subQ2409=sQuery(id+"F0.wireOp",EDGE,"E1782");var subQ2410=sQuery(id+"F0.wireOp",EDGE,"E1781");var subQ2411=sQuery(id+"F0.wireOp",EDGE,"E1780");var subQ2412=sQuery(id+"F0.wireOp",EDGE,"E1779");var subQ2413=sQuery(id+"F0.wireOp",EDGE,"E1778");var subQ2414=sQuery(id+"F0.wireOp",EDGE,"E1777");var subQ2415=sQuery(id+"F0.wireOp",EDGE,"E1776");var subQ2416=sQuery(id+"F0.wireOp",EDGE,"E1775");var subQ2417=sQuery(id+"F0.wireOp",EDGE,"E1774");var subQ2418=sQuery(id+"F0.wireOp",EDGE,"E1773");var subQ2419=sQuery(id+"F0.wireOp",EDGE,"E1772");var subQ2420=sQuery(id+"F0.wireOp",EDGE,"E1771");var subQ2421=sQuery(id+"F0.wireOp",EDGE,"E1770");var subQ2422=sQuery(id+"F0.wireOp",EDGE,"E1769");var subQ2423=sQuery(id+"F0.wireOp",EDGE,"E1768");var subQ2424=sQuery(id+"F0.wireOp",EDGE,"E1767");var subQ2425=sQuery(id+"F0.wireOp",EDGE,"E1766");var subQ2426=sQuery(id+"F0.wireOp",EDGE,"E1765");var subQ2427=sQuery(id+"F0.wireOp",EDGE,"E1764");var subQ2428=sQuery(id+"F0.wireOp",EDGE,"E1763");var subQ2429=sQuery(id+"F0.wireOp",EDGE,"E1762");var subQ2430=sQuery(id+"F0.wireOp",EDGE,"E1761");var subQ2431=sQuery(id+"F0.wireOp",EDGE,"E1760");var subQ2432=sQuery(id+"F0.wireOp",EDGE,"E1759");var subQ2433=sQuery(id+"F0.wireOp",EDGE,"E1758");var subQ2434=sQuery(id+"F0.wireOp",EDGE,"E1757");var subQ2435=sQuery(id+"F0.wireOp",EDGE,"E1756");var subQ2436=sQuery(id+"F0.wireOp",EDGE,"E1755");var subQ2437=sQuery(id+"F0.wireOp",EDGE,"E1754");var subQ2438=sQuery(id+"F0.wireOp",EDGE,"E1753");var subQ2439=sQuery(id+"F0.wireOp",EDGE,"E1752");var subQ2440=sQuery(id+"F0.wireOp",EDGE,"E1751");var subQ2441=sQuery(id+"F0.wireOp",EDGE,"E1750");var subQ2442=sQuery(id+"F0.wireOp",EDGE,"E1749");var subQ2443=sQuery(id+"F0.wireOp",EDGE,"E1748");var subQ2444=sQuery(id+"F0.wireOp",EDGE,"E1747");var subQ2445=sQuery(id+"F0.wireOp",EDGE,"E1746");var subQ2446=sQuery(id+"F0.wireOp",EDGE,"E1745");var subQ2447=sQuery(id+"F0.wireOp",EDGE,"E1744");var subQ2448=sQuery(id+"F0.wireOp",EDGE,"E1743");var subQ2449=sQuery(id+"F0.wireOp",EDGE,"E1742");var subQ2450=sQuery(id+"F0.wireOp",EDGE,"E1741");var subQ2451=sQuery(id+"F0.wireOp",EDGE,"E1740");var subQ2452=sQuery(id+"F0.wireOp",EDGE,"E1739");var subQ2453=sQuery(id+"F0.wireOp",EDGE,"E1738");var subQ2454=sQuery(id+"F0.wireOp",EDGE,"E1737");var subQ2455=sQuery(id+"F0.wireOp",EDGE,"E1736");var subQ2456=sQuery(id+"F0.wireOp",EDGE,"E1735");var subQ2457=sQuery(id+"F0.wireOp",EDGE,"E1734");var subQ2458=sQuery(id+"F0.wireOp",EDGE,"E1733");var subQ2459=sQuery(id+"F0.wireOp",EDGE,"E1732");var subQ2460=sQuery(id+"F0.wireOp",EDGE,"E1731");var subQ2461=sQuery(id+"F0.wireOp",EDGE,"E1730");var subQ2462=sQuery(id+"F0.wireOp",EDGE,"E1729");var subQ2463=sQuery(id+"F0.wireOp",EDGE,"E1728");var subQ2464=sQuery(id+"F0.wireOp",EDGE,"E1727");var subQ2465=sQuery(id+"F0.wireOp",EDGE,"E1726");var subQ2466=sQuery(id+"F0.wireOp",EDGE,"E1725");var subQ2467=sQuery(id+"F0.wireOp",EDGE,"E1724");var subQ2468=sQuery(id+"F0.wireOp",EDGE,"E1723");var subQ2469=sQuery(id+"F0.wireOp",EDGE,"E1722");var subQ2470=sQuery(id+"F0.wireOp",EDGE,"E1721");var subQ2471=sQuery(id+"F0.wireOp",EDGE,"E1720");var subQ2472=sQuery(id+"F0.wireOp",EDGE,"E1719");var subQ2473=sQuery(id+"F0.wireOp",EDGE,"E1718");var subQ2474=sQuery(id+"F0.wireOp",EDGE,"E1717");var subQ2475=sQuery(id+"F0.wireOp",EDGE,"E1716");var subQ2476=sQuery(id+"F0.wireOp",EDGE,"E1715");var subQ2477=sQuery(id+"F0.wireOp",EDGE,"E1714");var subQ2478=sQuery(id+"F0.wireOp",EDGE,"E1713");var subQ2479=sQuery(id+"F0.wireOp",EDGE,"E1712");var subQ2480=sQuery(id+"F0.wireOp",EDGE,"E1711");var subQ2481=sQuery(id+"F0.wireOp",EDGE,"E1710");var subQ2482=sQuery(id+"F0.wireOp",EDGE,"E1709");var subQ2483=sQuery(id+"F0.wireOp",EDGE,"E1708");var subQ2484=sQuery(id+"F0.wireOp",EDGE,"E1707");var subQ2485=sQuery(id+"F0.wireOp",EDGE,"E1706");var subQ2486=sQuery(id+"F0.wireOp",EDGE,"E1705");var subQ2487=sQuery(id+"F0.wireOp",EDGE,"E1704");var subQ2488=sQuery(id+"F0.wireOp",EDGE,"E1703");var subQ2489=sQuery(id+"F0.wireOp",EDGE,"E1702");var subQ2490=sQuery(id+"F0.wireOp",EDGE,"E1701");var subQ2491=sQuery(id+"F0.wireOp",EDGE,"E1700");var subQ2492=sQuery(id+"F0.wireOp",EDGE,"E1699");var subQ2493=sQuery(id+"F0.wireOp",EDGE,"E1698");var subQ2494=sQuery(id+"F0.wireOp",EDGE,"E1697");var subQ2495=sQuery(id+"F0.wireOp",EDGE,"E1696");var subQ2496=sQuery(id+"F0.wireOp",EDGE,"E1695");var subQ2497=sQuery(id+"F0.wireOp",EDGE,"E1694");var subQ2498=sQuery(id+"F0.wireOp",EDGE,"E1693");var subQ2499=sQuery(id+"F0.wireOp",EDGE,"E1692");var subQ2500=sQuery(id+"F0.wireOp",EDGE,"E1691");var subQ2501=sQuery(id+"F0.wireOp",EDGE,"E1690");var subQ2502=sQuery(id+"F0.wireOp",EDGE,"E1689");var subQ2503=sQuery(id+"F0.wireOp",EDGE,"E1688");var subQ2504=sQuery(id+"F0.wireOp",EDGE,"E1687");var subQ2505=sQuery(id+"F0.wireOp",EDGE,"E1686");var subQ2506=sQuery(id+"F0.wireOp",EDGE,"E1685");var subQ2507=sQuery(id+"F0.wireOp",EDGE,"E1684");var subQ2508=sQuery(id+"F0.wireOp",EDGE,"E1683");var subQ2509=sQuery(id+"F0.wireOp",EDGE,"E1682");var subQ2510=sQuery(id+"F0.wireOp",EDGE,"E1681");var subQ2511=sQuery(id+"F0.wireOp",EDGE,"E1680");var subQ2512=sQuery(id+"F0.wireOp",EDGE,"E1679");var subQ2513=sQuery(id+"F0.wireOp",EDGE,"E1678");var subQ2514=sQuery(id+"F0.wireOp",EDGE,"E1677");var subQ2515=sQuery(id+"F0.wireOp",EDGE,"E1676");var subQ2516=sQuery(id+"F0.wireOp",EDGE,"E1675");var subQ2517=sQuery(id+"F0.wireOp",EDGE,"E1674");var subQ2518=sQuery(id+"F0.wireOp",EDGE,"E1673");var subQ2519=sQuery(id+"F0.wireOp",EDGE,"E1672");var subQ2520=sQuery(id+"F0.wireOp",EDGE,"E1671");var subQ2521=sQuery(id+"F0.wireOp",EDGE,"E1670");var subQ2522=sQuery(id+"F0.wireOp",EDGE,"E1669");var subQ2523=sQuery(id+"F0.wireOp",EDGE,"E1668");var subQ2524=sQuery(id+"F0.wireOp",EDGE,"E1667");var subQ2525=sQuery(id+"F0.wireOp",EDGE,"E1666");var subQ2526=sQuery(id+"F0.wireOp",EDGE,"E1665");var subQ2527=sQuery(id+"F0.wireOp",EDGE,"E1664");var subQ2528=sQuery(id+"F0.wireOp",EDGE,"E1663");var subQ2529=sQuery(id+"F0.wireOp",EDGE,"E1662");var subQ2530=sQuery(id+"F0.wireOp",EDGE,"E1661");var subQ2531=sQuery(id+"F0.wireOp",EDGE,"E1660");var subQ2532=sQuery(id+"F0.wireOp",EDGE,"E1659");var subQ2533=sQuery(id+"F0.wireOp",EDGE,"E1658");var subQ2534=sQuery(id+"F0.wireOp",EDGE,"E1657");var subQ2535=sQuery(id+"F0.wireOp",EDGE,"E1656");var subQ2536=sQuery(id+"F0.wireOp",EDGE,"E1655");var subQ2537=sQuery(id+"F0.wireOp",EDGE,"E1654");var subQ2538=sQuery(id+"F0.wireOp",EDGE,"E1653");var subQ2539=sQuery(id+"F0.wireOp",EDGE,"E1652");var subQ2540=sQuery(id+"F0.wireOp",EDGE,"E1651");var subQ2541=sQuery(id+"F0.wireOp",EDGE,"E1650");var subQ2542=sQuery(id+"F0.wireOp",EDGE,"E1649");var subQ2543=sQuery(id+"F0.wireOp",EDGE,"E1648");var subQ2544=sQuery(id+"F0.wireOp",EDGE,"E1647");var subQ2545=sQuery(id+"F0.wireOp",EDGE,"E1646");var subQ2546=sQuery(id+"F0.wireOp",EDGE,"E1645");var subQ2547=sQuery(id+"F0.wireOp",EDGE,"E1644");var subQ2548=sQuery(id+"F0.wireOp",EDGE,"E1643");var subQ2549=sQuery(id+"F0.wireOp",EDGE,"E1642");var subQ2550=sQuery(id+"F0.wireOp",EDGE,"E1641");var subQ2551=sQuery(id+"F0.wireOp",EDGE,"E1640");var subQ2552=sQuery(id+"F0.wireOp",EDGE,"E1639");var subQ2553=sQuery(id+"F0.wireOp",EDGE,"E1638");var subQ2554=sQuery(id+"F0.wireOp",EDGE,"E1637");var subQ2555=sQuery(id+"F0.wireOp",EDGE,"E1636");var subQ2556=sQuery(id+"F0.wireOp",EDGE,"E1635");var subQ2557=sQuery(id+"F0.wireOp",EDGE,"E1634");var subQ2558=sQuery(id+"F0.wireOp",EDGE,"E1633");var subQ2559=sQuery(id+"F0.wireOp",EDGE,"E1632");var subQ2560=sQuery(id+"F0.wireOp",EDGE,"E1631");var subQ2561=sQuery(id+"F0.wireOp",EDGE,"E1630");var subQ2562=sQuery(id+"F0.wireOp",EDGE,"E1629");var subQ2563=sQuery(id+"F0.wireOp",EDGE,"E1628");var subQ2564=sQuery(id+"F0.wireOp",EDGE,"E1627");var subQ2565=sQuery(id+"F0.wireOp",EDGE,"E1626");var subQ2566=sQuery(id+"F0.wireOp",EDGE,"E1625");var subQ2567=sQuery(id+"F0.wireOp",EDGE,"E1624");var subQ2568=sQuery(id+"F0.wireOp",EDGE,"E1623");var subQ2569=sQuery(id+"F0.wireOp",EDGE,"E1622");var subQ2570=sQuery(id+"F0.wireOp",EDGE,"E1621");var subQ2571=sQuery(id+"F0.wireOp",EDGE,"E1620");var subQ2572=sQuery(id+"F0.wireOp",EDGE,"E1619");var subQ2573=sQuery(id+"F0.wireOp",EDGE,"E1618");var subQ2574=sQuery(id+"F0.wireOp",EDGE,"E1617");var subQ2575=sQuery(id+"F0.wireOp",EDGE,"E1616");var subQ2576=sQuery(id+"F0.wireOp",EDGE,"E1615");var subQ2577=sQuery(id+"F0.wireOp",EDGE,"E1614");var subQ2578=sQuery(id+"F0.wireOp",EDGE,"E1613");var subQ2579=sQuery(id+"F0.wireOp",EDGE,"E1612");var subQ2580=sQuery(id+"F0.wireOp",EDGE,"E1611");var subQ2581=sQuery(id+"F0.wireOp",EDGE,"E1610");var subQ2582=sQuery(id+"F0.wireOp",EDGE,"E1609");var subQ2583=sQuery(id+"F0.wireOp",EDGE,"E1608");var subQ2584=sQuery(id+"F0.wireOp",EDGE,"E1607");var subQ2585=sQuery(id+"F0.wireOp",EDGE,"E1606");var subQ2586=sQuery(id+"F0.wireOp",EDGE,"E1605");var subQ2587=sQuery(id+"F0.wireOp",EDGE,"E1604");var subQ2588=sQuery(id+"F0.wireOp",EDGE,"E1603");var subQ2589=sQuery(id+"F0.wireOp",EDGE,"E1602");var subQ2590=sQuery(id+"F0.wireOp",EDGE,"E1601");var subQ2591=sQuery(id+"F0.wireOp",EDGE,"E1600");var subQ2592=sQuery(id+"F0.wireOp",EDGE,"E1599");var subQ2593=sQuery(id+"F0.wireOp",EDGE,"E1598");var subQ2594=sQuery(id+"F0.wireOp",EDGE,"E1597");var subQ2595=sQuery(id+"F0.wireOp",EDGE,"E1596");var subQ2596=sQuery(id+"F0.wireOp",EDGE,"E1595");var subQ2597=sQuery(id+"F0.wireOp",EDGE,"E1594");var subQ2598=sQuery(id+"F0.wireOp",EDGE,"E1593");var subQ2599=sQuery(id+"F0.wireOp",EDGE,"E1592");var subQ2600=sQuery(id+"F0.wireOp",EDGE,"E1591");var subQ2601=sQuery(id+"F0.wireOp",EDGE,"E1590");var subQ2602=sQuery(id+"F0.wireOp",EDGE,"E1589");var subQ2603=sQuery(id+"F0.wireOp",EDGE,"E1588");var subQ2604=sQuery(id+"F0.wireOp",EDGE,"E1587");var subQ2605=sQuery(id+"F0.wireOp",EDGE,"E1586");var subQ2606=sQuery(id+"F0.wireOp",EDGE,"E1585");var subQ2607=sQuery(id+"F0.wireOp",EDGE,"E1584");var subQ2608=sQuery(id+"F0.wireOp",EDGE,"E1583");var subQ2609=sQuery(id+"F0.wireOp",EDGE,"E1582");var subQ2610=sQuery(id+"F0.wireOp",EDGE,"E1581");var subQ2611=sQuery(id+"F0.wireOp",EDGE,"E1580");var subQ2612=sQuery(id+"F0.wireOp",EDGE,"E1579");var subQ2613=sQuery(id+"F0.wireOp",EDGE,"E1578");var subQ2614=sQuery(id+"F0.wireOp",EDGE,"E1577");var subQ2615=sQuery(id+"F0.wireOp",EDGE,"E1576");var subQ2616=sQuery(id+"F0.wireOp",EDGE,"E1575");var subQ2617=sQuery(id+"F0.wireOp",EDGE,"E1574");var subQ2618=sQuery(id+"F0.wireOp",EDGE,"E1573");var subQ2619=sQuery(id+"F0.wireOp",EDGE,"E1572");var subQ2620=sQuery(id+"F0.wireOp",EDGE,"E1571");var subQ2621=sQuery(id+"F0.wireOp",EDGE,"E1570");var subQ2622=sQuery(id+"F0.wireOp",EDGE,"E1569");var subQ2623=sQuery(id+"F0.wireOp",EDGE,"E1568");var subQ2624=sQuery(id+"F0.wireOp",EDGE,"E1567");var subQ2625=sQuery(id+"F0.wireOp",EDGE,"E1566");var subQ2626=sQuery(id+"F0.wireOp",EDGE,"E1565");var subQ2627=sQuery(id+"F0.wireOp",EDGE,"E1564");var subQ2628=sQuery(id+"F0.wireOp",EDGE,"E1563");var subQ2629=sQuery(id+"F0.wireOp",EDGE,"E1562");var subQ2630=sQuery(id+"F0.wireOp",EDGE,"E1561");var subQ2631=sQuery(id+"F0.wireOp",EDGE,"E1560");var subQ2632=sQuery(id+"F0.wireOp",EDGE,"E1559");var subQ2633=sQuery(id+"F0.wireOp",EDGE,"E1558");var subQ2634=sQuery(id+"F0.wireOp",EDGE,"E1557");var subQ2635=sQuery(id+"F0.wireOp",EDGE,"E1556");var subQ2636=sQuery(id+"F0.wireOp",EDGE,"E1555");var subQ2637=sQuery(id+"F0.wireOp",EDGE,"E1554");var subQ2638=sQuery(id+"F0.wireOp",EDGE,"E1553");var subQ2639=sQuery(id+"F0.wireOp",EDGE,"E1552");var subQ2640=sQuery(id+"F0.wireOp",EDGE,"E1551");var subQ2641=sQuery(id+"F0.wireOp",EDGE,"E1550");var subQ2642=sQuery(id+"F0.wireOp",EDGE,"E1549");var subQ2643=sQuery(id+"F0.wireOp",EDGE,"E1548");var subQ2644=sQuery(id+"F0.wireOp",EDGE,"E1547");var subQ2645=sQuery(id+"F0.wireOp",EDGE,"E1546");var subQ2646=sQuery(id+"F0.wireOp",EDGE,"E1545");var subQ2647=sQuery(id+"F0.wireOp",EDGE,"E1544");var subQ2648=sQuery(id+"F0.wireOp",EDGE,"E1543");var subQ2649=sQuery(id+"F0.wireOp",EDGE,"E1542");var subQ2650=sQuery(id+"F0.wireOp",EDGE,"E1541");var subQ2651=sQuery(id+"F0.wireOp",EDGE,"E1540");var subQ2652=sQuery(id+"F0.wireOp",EDGE,"E1539");var subQ2653=sQuery(id+"F0.wireOp",EDGE,"E1538");var subQ2654=sQuery(id+"F0.wireOp",EDGE,"E1537");var subQ2655=sQuery(id+"F0.wireOp",EDGE,"E1536");var subQ2656=sQuery(id+"F0.wireOp",EDGE,"E1535");var subQ2657=sQuery(id+"F0.wireOp",EDGE,"E1534");var subQ2658=sQuery(id+"F0.wireOp",EDGE,"E1533");var subQ2659=sQuery(id+"F0.wireOp",EDGE,"E1532");var subQ2660=sQuery(id+"F0.wireOp",EDGE,"E1531");var subQ2661=sQuery(id+"F0.wireOp",EDGE,"E1530");var subQ2662=sQuery(id+"F0.wireOp",EDGE,"E1529");var subQ2663=sQuery(id+"F0.wireOp",EDGE,"E1528");var subQ2664=sQuery(id+"F0.wireOp",EDGE,"E1527");var subQ2665=sQuery(id+"F0.wireOp",EDGE,"E1526");var subQ2666=sQuery(id+"F0.wireOp",EDGE,"E1525");var subQ2667=sQuery(id+"F0.wireOp",EDGE,"E1524");var subQ2668=sQuery(id+"F0.wireOp",EDGE,"E1523");var subQ2669=sQuery(id+"F0.wireOp",EDGE,"E1522");var subQ2670=sQuery(id+"F0.wireOp",EDGE,"E1521");var subQ2671=sQuery(id+"F0.wireOp",EDGE,"E1520");var subQ2672=sQuery(id+"F0.wireOp",EDGE,"E1519");var subQ2673=sQuery(id+"F0.wireOp",EDGE,"E1518");var subQ2674=sQuery(id+"F0.wireOp",EDGE,"E1517");var subQ2675=sQuery(id+"F0.wireOp",EDGE,"E1516");var subQ2676=sQuery(id+"F0.wireOp",EDGE,"E1515");var subQ2677=sQuery(id+"F0.wireOp",EDGE,"E1514");var subQ2678=sQuery(id+"F0.wireOp",EDGE,"E1513");var subQ2679=sQuery(id+"F0.wireOp",EDGE,"E1512");var subQ2680=sQuery(id+"F0.wireOp",EDGE,"E1511");var subQ2681=sQuery(id+"F0.wireOp",EDGE,"E1510");var subQ2682=sQuery(id+"F0.wireOp",EDGE,"E1509");var subQ2683=sQuery(id+"F0.wireOp",EDGE,"E1508");var subQ2684=sQuery(id+"F0.wireOp",EDGE,"E1507");var subQ2685=sQuery(id+"F0.wireOp",EDGE,"E1506");var subQ2686=sQuery(id+"F0.wireOp",EDGE,"E1505");var subQ2687=sQuery(id+"F0.wireOp",EDGE,"E1504");var subQ2688=sQuery(id+"F0.wireOp",EDGE,"E1503");var subQ2689=sQuery(id+"F0.wireOp",EDGE,"E1502");var subQ2690=sQuery(id+"F0.wireOp",EDGE,"E1501");var subQ2691=sQuery(id+"F0.wireOp",EDGE,"E1500");var subQ2692=sQuery(id+"F0.wireOp",EDGE,"E1499");var subQ2693=sQuery(id+"F0.wireOp",EDGE,"E1498");var subQ2694=sQuery(id+"F0.wireOp",EDGE,"E1497");var subQ2695=sQuery(id+"F0.wireOp",EDGE,"E1496");var subQ2696=sQuery(id+"F0.wireOp",EDGE,"E1495");var subQ2697=sQuery(id+"F0.wireOp",EDGE,"E1494");var subQ2698=sQuery(id+"F0.wireOp",EDGE,"E1493");var subQ2699=sQuery(id+"F0.wireOp",EDGE,"E1492");var subQ2700=sQuery(id+"F0.wireOp",EDGE,"E1491");var subQ2701=sQuery(id+"F0.wireOp",EDGE,"E1490");var subQ2702=sQuery(id+"F0.wireOp",EDGE,"E1489");var subQ2703=sQuery(id+"F0.wireOp",EDGE,"E1488");var subQ2704=sQuery(id+"F0.wireOp",EDGE,"E1487");var subQ2705=sQuery(id+"F0.wireOp",EDGE,"E1486");var subQ2706=sQuery(id+"F0.wireOp",EDGE,"E1485");var subQ2707=sQuery(id+"F0.wireOp",EDGE,"E1484");var subQ2708=sQuery(id+"F0.wireOp",EDGE,"E1483");var subQ2709=sQuery(id+"F0.wireOp",EDGE,"E1482");var subQ2710=sQuery(id+"F0.wireOp",EDGE,"E1481");var subQ2711=sQuery(id+"F0.wireOp",EDGE,"E1480");var subQ2712=sQuery(id+"F0.wireOp",EDGE,"E1479");var subQ2713=sQuery(id+"F0.wireOp",EDGE,"E1478");var subQ2714=sQuery(id+"F0.wireOp",EDGE,"E1477");var subQ2715=sQuery(id+"F0.wireOp",EDGE,"E1476");var subQ2716=sQuery(id+"F0.wireOp",EDGE,"E1475");var subQ2717=sQuery(id+"F0.wireOp",EDGE,"E1474");var subQ2718=sQuery(id+"F0.wireOp",EDGE,"E1473");var subQ2719=sQuery(id+"F0.wireOp",EDGE,"E1472");var subQ2720=sQuery(id+"F0.wireOp",EDGE,"E1471");var subQ2721=sQuery(id+"F0.wireOp",EDGE,"E1470");var subQ2722=sQuery(id+"F0.wireOp",EDGE,"E1469");var subQ2723=sQuery(id+"F0.wireOp",EDGE,"E1468");var subQ2724=sQuery(id+"F0.wireOp",EDGE,"E1467");var subQ2725=sQuery(id+"F0.wireOp",EDGE,"E1466");var subQ2726=sQuery(id+"F0.wireOp",EDGE,"E1465");var subQ2727=sQuery(id+"F0.wireOp",EDGE,"E1464");var subQ2728=sQuery(id+"F0.wireOp",EDGE,"E1463");var subQ2729=sQuery(id+"F0.wireOp",EDGE,"E1462");var subQ2730=sQuery(id+"F0.wireOp",EDGE,"E1461");var subQ2731=sQuery(id+"F0.wireOp",EDGE,"E1460");var subQ2732=sQuery(id+"F0.wireOp",EDGE,"E1459");var subQ2733=sQuery(id+"F0.wireOp",EDGE,"E1458");var subQ2734=sQuery(id+"F0.wireOp",EDGE,"E1457");var subQ2735=sQuery(id+"F0.wireOp",EDGE,"E1456");var subQ2736=sQuery(id+"F0.wireOp",EDGE,"E1455");var subQ2737=sQuery(id+"F0.wireOp",EDGE,"E1454");var subQ2738=sQuery(id+"F0.wireOp",EDGE,"E1453");var subQ2739=sQuery(id+"F0.wireOp",EDGE,"E1452");var subQ2740=sQuery(id+"F0.wireOp",EDGE,"E1451");var subQ2741=sQuery(id+"F0.wireOp",EDGE,"E1450");var subQ2742=sQuery(id+"F0.wireOp",EDGE,"E1449");var subQ2743=sQuery(id+"F0.wireOp",EDGE,"E1448");var subQ2744=sQuery(id+"F0.wireOp",EDGE,"E1447");var subQ2745=sQuery(id+"F0.wireOp",EDGE,"E1446");var subQ2746=sQuery(id+"F0.wireOp",EDGE,"E1445");var subQ2747=sQuery(id+"F0.wireOp",EDGE,"E1444");var subQ2748=sQuery(id+"F0.wireOp",EDGE,"E1443");var subQ2749=sQuery(id+"F0.wireOp",EDGE,"E1442");var subQ2750=sQuery(id+"F0.wireOp",EDGE,"E1441");var subQ2751=sQuery(id+"F0.wireOp",EDGE,"E1440");var subQ2752=sQuery(id+"F0.wireOp",EDGE,"E1439");var subQ2753=sQuery(id+"F0.wireOp",EDGE,"E1438");var subQ2754=sQuery(id+"F0.wireOp",EDGE,"E1437");var subQ2755=sQuery(id+"F0.wireOp",EDGE,"E1436");var subQ2756=sQuery(id+"F0.wireOp",EDGE,"E1435");var subQ2757=sQuery(id+"F0.wireOp",EDGE,"E1434");var subQ2758=sQuery(id+"F0.wireOp",EDGE,"E1433");var subQ2759=sQuery(id+"F0.wireOp",EDGE,"E1432");var subQ2760=sQuery(id+"F0.wireOp",EDGE,"E1431");var subQ2761=sQuery(id+"F0.wireOp",EDGE,"E1430");var subQ2762=sQuery(id+"F0.wireOp",EDGE,"E1429");var subQ2763=sQuery(id+"F0.wireOp",EDGE,"E1428");var subQ2764=sQuery(id+"F0.wireOp",EDGE,"E1427");var subQ2765=sQuery(id+"F0.wireOp",EDGE,"E1426");var subQ2766=sQuery(id+"F0.wireOp",EDGE,"E1425");var subQ2767=sQuery(id+"F0.wireOp",EDGE,"E1424");var subQ2768=sQuery(id+"F0.wireOp",EDGE,"E1423");var subQ2769=sQuery(id+"F0.wireOp",EDGE,"E1422");var subQ2770=sQuery(id+"F0.wireOp",EDGE,"E1421");var subQ2771=sQuery(id+"F0.wireOp",EDGE,"E1420");var subQ2772=sQuery(id+"F0.wireOp",EDGE,"E1419");var subQ2773=sQuery(id+"F0.wireOp",EDGE,"E1418");var subQ2774=sQuery(id+"F0.wireOp",EDGE,"E1417");var subQ2775=sQuery(id+"F0.wireOp",EDGE,"E1416");var subQ2776=sQuery(id+"F0.wireOp",EDGE,"E1415");var subQ2777=sQuery(id+"F0.wireOp",EDGE,"E1414");var subQ2778=sQuery(id+"F0.wireOp",EDGE,"E1413");var subQ2779=sQuery(id+"F0.wireOp",EDGE,"E1412");var subQ2780=sQuery(id+"F0.wireOp",EDGE,"E1411");var subQ2781=sQuery(id+"F0.wireOp",EDGE,"E1410");var subQ2782=sQuery(id+"F0.wireOp",EDGE,"E1409");var subQ2783=sQuery(id+"F0.wireOp",EDGE,"E1408");var subQ2784=sQuery(id+"F0.wireOp",EDGE,"E1407");var subQ2785=sQuery(id+"F0.wireOp",EDGE,"E1406");var subQ2786=sQuery(id+"F0.wireOp",EDGE,"E1405");var subQ2787=sQuery(id+"F0.wireOp",EDGE,"E1404");var subQ2788=sQuery(id+"F0.wireOp",EDGE,"E1403");var subQ2789=sQuery(id+"F0.wireOp",EDGE,"E1402");var subQ2790=sQuery(id+"F0.wireOp",EDGE,"E1401");var subQ2791=sQuery(id+"F0.wireOp",EDGE,"E1400");var subQ2792=sQuery(id+"F0.wireOp",EDGE,"E1399");var subQ2793=sQuery(id+"F0.wireOp",EDGE,"E1398");var subQ2794=sQuery(id+"F0.wireOp",EDGE,"E1397");var subQ2795=sQuery(id+"F0.wireOp",EDGE,"E1396");var subQ2796=sQuery(id+"F0.wireOp",EDGE,"E1395");var subQ2797=sQuery(id+"F0.wireOp",EDGE,"E1394");var subQ2798=sQuery(id+"F0.wireOp",EDGE,"E1393");var subQ2799=sQuery(id+"F0.wireOp",EDGE,"E1392");var subQ2800=sQuery(id+"F0.wireOp",EDGE,"E1391");var subQ2801=sQuery(id+"F0.wireOp",EDGE,"E1390");var subQ2802=sQuery(id+"F0.wireOp",EDGE,"E1389");var subQ2803=sQuery(id+"F0.wireOp",EDGE,"E1388");var subQ2804=sQuery(id+"F0.wireOp",EDGE,"E1387");var subQ2805=sQuery(id+"F0.wireOp",EDGE,"E1386");var subQ2806=sQuery(id+"F0.wireOp",EDGE,"E1385");var subQ2807=sQuery(id+"F0.wireOp",EDGE,"E1384");var subQ2808=sQuery(id+"F0.wireOp",EDGE,"E1383");var subQ2809=sQuery(id+"F0.wireOp",EDGE,"E1382");var subQ2810=sQuery(id+"F0.wireOp",EDGE,"E1381");var subQ2811=sQuery(id+"F0.wireOp",EDGE,"E1380");var subQ2812=sQuery(id+"F0.wireOp",EDGE,"E1379");var subQ2813=sQuery(id+"F0.wireOp",EDGE,"E1378");var subQ2814=sQuery(id+"F0.wireOp",EDGE,"E1377");var subQ2815=sQuery(id+"F0.wireOp",EDGE,"E1376");var subQ2816=sQuery(id+"F0.wireOp",EDGE,"E1375");var subQ2817=sQuery(id+"F0.wireOp",EDGE,"E1374");var subQ2818=sQuery(id+"F0.wireOp",EDGE,"E1373");var subQ2819=sQuery(id+"F0.wireOp",EDGE,"E1372");var subQ2820=sQuery(id+"F0.wireOp",EDGE,"E1371");var subQ2821=sQuery(id+"F0.wireOp",EDGE,"E1370");var subQ2822=sQuery(id+"F0.wireOp",EDGE,"E1369");var subQ2823=sQuery(id+"F0.wireOp",EDGE,"E1368");var subQ2824=sQuery(id+"F0.wireOp",EDGE,"E1367");var subQ2825=sQuery(id+"F0.wireOp",EDGE,"E1366");var subQ2826=sQuery(id+"F0.wireOp",EDGE,"E1365");var subQ2827=sQuery(id+"F0.wireOp",EDGE,"E1364");var subQ2828=sQuery(id+"F0.wireOp",EDGE,"E1363");var subQ2829=sQuery(id+"F0.wireOp",EDGE,"E1362");var subQ2830=sQuery(id+"F0.wireOp",EDGE,"E1361");var subQ2831=sQuery(id+"F0.wireOp",EDGE,"E1360");var subQ2832=sQuery(id+"F0.wireOp",EDGE,"E1359");var subQ2833=sQuery(id+"F0.wireOp",EDGE,"E1358");var subQ2834=sQuery(id+"F0.wireOp",EDGE,"E1357");var subQ2835=sQuery(id+"F0.wireOp",EDGE,"E1356");var subQ2836=sQuery(id+"F0.wireOp",EDGE,"E1355");var subQ2837=sQuery(id+"F0.wireOp",EDGE,"E1354");var subQ2838=sQuery(id+"F0.wireOp",EDGE,"E1353");var subQ2839=sQuery(id+"F0.wireOp",EDGE,"E1352");var subQ2840=sQuery(id+"F0.wireOp",EDGE,"E1351");var subQ2841=sQuery(id+"F0.wireOp",EDGE,"E1350");var subQ2842=sQuery(id+"F0.wireOp",EDGE,"E1349");var subQ2843=sQuery(id+"F0.wireOp",EDGE,"E1348");var subQ2844=sQuery(id+"F0.wireOp",EDGE,"E1347");var subQ2845=sQuery(id+"F0.wireOp",EDGE,"E1346");var subQ2846=sQuery(id+"F0.wireOp",EDGE,"E1345");var subQ2847=sQuery(id+"F0.wireOp",EDGE,"E1344");var subQ2848=sQuery(id+"F0.wireOp",EDGE,"E1343");var subQ2849=sQuery(id+"F0.wireOp",EDGE,"E1342");var subQ2850=sQuery(id+"F0.wireOp",EDGE,"E1341");var subQ2851=sQuery(id+"F0.wireOp",EDGE,"E1340");var subQ2852=sQuery(id+"F0.wireOp",EDGE,"E1339");var subQ2853=sQuery(id+"F0.wireOp",EDGE,"E1338");var subQ2854=sQuery(id+"F0.wireOp",EDGE,"E1337");var subQ2855=sQuery(id+"F0.wireOp",EDGE,"E1336");var subQ2856=sQuery(id+"F0.wireOp",EDGE,"E1335");var subQ2857=sQuery(id+"F0.wireOp",EDGE,"E1334");var subQ2858=sQuery(id+"F0.wireOp",EDGE,"E1333");var subQ2859=sQuery(id+"F0.wireOp",EDGE,"E1332");var subQ2860=sQuery(id+"F0.wireOp",EDGE,"E1331");var subQ2861=sQuery(id+"F0.wireOp",EDGE,"E1330");var subQ2862=sQuery(id+"F0.wireOp",EDGE,"E1329");var subQ2863=sQuery(id+"F0.wireOp",EDGE,"E1328");var subQ2864=sQuery(id+"F0.wireOp",EDGE,"E1327");var subQ2865=sQuery(id+"F0.wireOp",EDGE,"E1326");var subQ2866=sQuery(id+"F0.wireOp",EDGE,"E1325");var subQ2867=sQuery(id+"F0.wireOp",EDGE,"E1324");var subQ2868=sQuery(id+"F0.wireOp",EDGE,"E1323");var subQ2869=sQuery(id+"F0.wireOp",EDGE,"E1322");var subQ2870=sQuery(id+"F0.wireOp",EDGE,"E1321");var subQ2871=sQuery(id+"F0.wireOp",EDGE,"E1320");var subQ2872=sQuery(id+"F0.wireOp",EDGE,"E1319");var subQ2873=sQuery(id+"F0.wireOp",EDGE,"E1318");var subQ2874=sQuery(id+"F0.wireOp",EDGE,"E1317");var subQ2875=sQuery(id+"F0.wireOp",EDGE,"E1316");var subQ2876=sQuery(id+"F0.wireOp",EDGE,"E1315");var subQ2877=sQuery(id+"F0.wireOp",EDGE,"E1314");var subQ2878=sQuery(id+"F0.wireOp",EDGE,"E1313");var subQ2879=sQuery(id+"F0.wireOp",EDGE,"E1312");var subQ2880=sQuery(id+"F0.wireOp",EDGE,"E1311");var subQ2881=sQuery(id+"F0.wireOp",EDGE,"E1310");var subQ2882=sQuery(id+"F0.wireOp",EDGE,"E1309");var subQ2883=sQuery(id+"F0.wireOp",EDGE,"E1308");var subQ2884=sQuery(id+"F0.wireOp",EDGE,"E1307");var subQ2885=sQuery(id+"F0.wireOp",EDGE,"E1306");var subQ2886=sQuery(id+"F0.wireOp",EDGE,"E1305");var subQ2887=sQuery(id+"F0.wireOp",EDGE,"E1304");var subQ2888=sQuery(id+"F0.wireOp",EDGE,"E1303");var subQ2889=sQuery(id+"F0.wireOp",EDGE,"E1302");var subQ2890=sQuery(id+"F0.wireOp",EDGE,"E1301");var subQ2891=sQuery(id+"F0.wireOp",EDGE,"E1300");var subQ2892=sQuery(id+"F0.wireOp",EDGE,"E1299");var subQ2893=sQuery(id+"F0.wireOp",EDGE,"E1298");var subQ2894=sQuery(id+"F0.wireOp",EDGE,"E1297");var subQ2895=sQuery(id+"F0.wireOp",EDGE,"E1296");var subQ2896=sQuery(id+"F0.wireOp",EDGE,"E1295");var subQ2897=sQuery(id+"F0.wireOp",EDGE,"E1294");var subQ2898=sQuery(id+"F0.wireOp",EDGE,"E1293");var subQ2899=sQuery(id+"F0.wireOp",EDGE,"E1292");var subQ2900=sQuery(id+"F0.wireOp",EDGE,"E1291");var subQ2901=sQuery(id+"F0.wireOp",EDGE,"E1290");var subQ2902=sQuery(id+"F0.wireOp",EDGE,"E1289");var subQ2903=sQuery(id+"F0.wireOp",EDGE,"E1288");var subQ2904=sQuery(id+"F0.wireOp",EDGE,"E1287");var subQ2905=sQuery(id+"F0.wireOp",EDGE,"E1286");var subQ2906=sQuery(id+"F0.wireOp",EDGE,"E1285");var subQ2907=sQuery(id+"F0.wireOp",EDGE,"E1284");var subQ2908=sQuery(id+"F0.wireOp",EDGE,"E1283");var subQ2909=sQuery(id+"F0.wireOp",EDGE,"E1282");var subQ2910=sQuery(id+"F0.wireOp",EDGE,"E1281");var subQ2911=sQuery(id+"F0.wireOp",EDGE,"E1280");var subQ2912=sQuery(id+"F0.wireOp",EDGE,"E1279");var subQ2913=sQuery(id+"F0.wireOp",EDGE,"E1278");var subQ2914=sQuery(id+"F0.wireOp",EDGE,"E1277");var subQ2915=sQuery(id+"F0.wireOp",EDGE,"E1276");var subQ2916=sQuery(id+"F0.wireOp",EDGE,"E1275");var subQ2917=sQuery(id+"F0.wireOp",EDGE,"E1274");var subQ2918=sQuery(id+"F0.wireOp",EDGE,"E1273");var subQ2919=sQuery(id+"F0.wireOp",EDGE,"E1272");var subQ2920=sQuery(id+"F0.wireOp",EDGE,"E1271");var subQ2921=sQuery(id+"F0.wireOp",EDGE,"E1270");var subQ2922=sQuery(id+"F0.wireOp",EDGE,"E1269");var subQ2923=sQuery(id+"F0.wireOp",EDGE,"E1268");var subQ2924=sQuery(id+"F0.wireOp",EDGE,"E1267");var subQ2925=sQuery(id+"F0.wireOp",EDGE,"E1266");var subQ2926=sQuery(id+"F0.wireOp",EDGE,"E1265");var subQ2927=sQuery(id+"F0.wireOp",EDGE,"E1264");var subQ2928=sQuery(id+"F0.wireOp",EDGE,"E1263");var subQ2929=sQuery(id+"F0.wireOp",EDGE,"E1262");var subQ2930=sQuery(id+"F0.wireOp",EDGE,"E1261");var subQ2931=sQuery(id+"F0.wireOp",EDGE,"E1260");var subQ2932=sQuery(id+"F0.wireOp",EDGE,"E1259");var subQ2933=sQuery(id+"F0.wireOp",EDGE,"E1258");var subQ2934=sQuery(id+"F0.wireOp",EDGE,"E1257");var subQ2935=sQuery(id+"F0.wireOp",EDGE,"E1256");var subQ2936=sQuery(id+"F0.wireOp",EDGE,"E1255");var subQ2937=sQuery(id+"F0.wireOp",EDGE,"E1254");var subQ2938=sQuery(id+"F0.wireOp",EDGE,"E1253");var subQ2939=sQuery(id+"F0.wireOp",EDGE,"E1252");var subQ2940=sQuery(id+"F0.wireOp",EDGE,"E1251");var subQ2941=sQuery(id+"F0.wireOp",EDGE,"E1250");var subQ2942=sQuery(id+"F0.wireOp",EDGE,"E1249");var subQ2943=sQuery(id+"F0.wireOp",EDGE,"E1248");var subQ2944=sQuery(id+"F0.wireOp",EDGE,"E1247");var subQ2945=sQuery(id+"F0.wireOp",EDGE,"E1246");var subQ2946=sQuery(id+"F0.wireOp",EDGE,"E1245");var subQ2947=sQuery(id+"F0.wireOp",EDGE,"E1244");var subQ2948=sQuery(id+"F0.wireOp",EDGE,"E1243");var subQ2949=sQuery(id+"F0.wireOp",EDGE,"E1242");var subQ2950=sQuery(id+"F0.wireOp",EDGE,"E1241");var subQ2951=sQuery(id+"F0.wireOp",EDGE,"E1240");var subQ2952=sQuery(id+"F0.wireOp",EDGE,"E1239");var subQ2953=sQuery(id+"F0.wireOp",EDGE,"E1238");var subQ2954=sQuery(id+"F0.wireOp",EDGE,"E1237");var subQ2955=sQuery(id+"F0.wireOp",EDGE,"E1236");var subQ2956=sQuery(id+"F0.wireOp",EDGE,"E1235");var subQ2957=sQuery(id+"F0.wireOp",EDGE,"E1234");var subQ2958=sQuery(id+"F0.wireOp",EDGE,"E1233");var subQ2959=sQuery(id+"F0.wireOp",EDGE,"E1232");var subQ2960=sQuery(id+"F0.wireOp",EDGE,"E1231");var subQ2961=sQuery(id+"F0.wireOp",EDGE,"E1230");var subQ2962=sQuery(id+"F0.wireOp",EDGE,"E1229");var subQ2963=sQuery(id+"F0.wireOp",EDGE,"E1228");var subQ2964=sQuery(id+"F0.wireOp",EDGE,"E1227");var subQ2965=sQuery(id+"F0.wireOp",EDGE,"E1226");var subQ2966=sQuery(id+"F0.wireOp",EDGE,"E1225");var subQ2967=sQuery(id+"F0.wireOp",EDGE,"E1224");var subQ2968=sQuery(id+"F0.wireOp",EDGE,"E1223");var subQ2969=sQuery(id+"F0.wireOp",EDGE,"E1222");var subQ2970=sQuery(id+"F0.wireOp",EDGE,"E1221");var subQ2971=sQuery(id+"F0.wireOp",EDGE,"E1220");var subQ2972=sQuery(id+"F0.wireOp",EDGE,"E1219");var subQ2973=sQuery(id+"F0.wireOp",EDGE,"E1218");var subQ2974=sQuery(id+"F0.wireOp",EDGE,"E1217");var subQ2975=sQuery(id+"F0.wireOp",EDGE,"E1216");var subQ2976=sQuery(id+"F0.wireOp",EDGE,"E1215");var subQ2977=sQuery(id+"F0.wireOp",EDGE,"E1214");var subQ2978=sQuery(id+"F0.wireOp",EDGE,"E1213");var subQ2979=sQuery(id+"F0.wireOp",EDGE,"E1212");var subQ2980=sQuery(id+"F0.wireOp",EDGE,"E1211");var subQ2981=sQuery(id+"F0.wireOp",EDGE,"E1210");var subQ2982=sQuery(id+"F0.wireOp",EDGE,"E1209");var subQ2983=sQuery(id+"F0.wireOp",EDGE,"E1208");var subQ2984=sQuery(id+"F0.wireOp",EDGE,"E1207");var subQ2985=sQuery(id+"F0.wireOp",EDGE,"E1206");var subQ2986=sQuery(id+"F0.wireOp",EDGE,"E1205");var subQ2987=sQuery(id+"F0.wireOp",EDGE,"E1204");var subQ2988=sQuery(id+"F0.wireOp",EDGE,"E1203");var subQ2989=sQuery(id+"F0.wireOp",EDGE,"E1202");var subQ2990=sQuery(id+"F0.wireOp",EDGE,"E1201");var subQ2991=sQuery(id+"F0.wireOp",EDGE,"E1200");var subQ2992=sQuery(id+"F0.wireOp",EDGE,"E1199");var subQ2993=sQuery(id+"F0.wireOp",EDGE,"E1198");var subQ2994=sQuery(id+"F0.wireOp",EDGE,"E1197");var subQ2995=sQuery(id+"F0.wireOp",EDGE,"E1196");var subQ2996=sQuery(id+"F0.wireOp",EDGE,"E1195");var subQ2997=sQuery(id+"F0.wireOp",EDGE,"E1194");var subQ2998=sQuery(id+"F0.wireOp",EDGE,"E1193");var subQ2999=sQuery(id+"F0.wireOp",EDGE,"E1192");var subQ3000=sQuery(id+"F0.wireOp",EDGE,"E1191");var subQ3001=sQuery(id+"F0.wireOp",EDGE,"E1190");var subQ3002=sQuery(id+"F0.wireOp",EDGE,"E1189");var subQ3003=sQuery(id+"F0.wireOp",EDGE,"E1188");var subQ3004=sQuery(id+"F0.wireOp",EDGE,"E1187");var subQ3005=sQuery(id+"F0.wireOp",EDGE,"E1186");var subQ3006=sQuery(id+"F0.wireOp",EDGE,"E1185");var subQ3007=sQuery(id+"F0.wireOp",EDGE,"E1184");var subQ3008=sQuery(id+"F0.wireOp",EDGE,"E1183");var subQ3009=sQuery(id+"F0.wireOp",EDGE,"E1182");var subQ3010=sQuery(id+"F0.wireOp",EDGE,"E1181");var subQ3011=sQuery(id+"F0.wireOp",EDGE,"E1180");var subQ3012=sQuery(id+"F0.wireOp",EDGE,"E1179");var subQ3013=sQuery(id+"F0.wireOp",EDGE,"E1178");var subQ3014=sQuery(id+"F0.wireOp",EDGE,"E1177");var subQ3015=sQuery(id+"F0.wireOp",EDGE,"E1176");var subQ3016=sQuery(id+"F0.wireOp",EDGE,"E1175");var subQ3017=sQuery(id+"F0.wireOp",EDGE,"E1174");var subQ3018=sQuery(id+"F0.wireOp",EDGE,"E1173");var subQ3019=sQuery(id+"F0.wireOp",EDGE,"E1172");var subQ3020=sQuery(id+"F0.wireOp",EDGE,"E1171");var subQ3021=sQuery(id+"F0.wireOp",EDGE,"E1170");var subQ3022=sQuery(id+"F0.wireOp",EDGE,"E1169");var subQ3023=sQuery(id+"F0.wireOp",EDGE,"E1168");var subQ3024=sQuery(id+"F0.wireOp",EDGE,"E1167");var subQ3025=sQuery(id+"F0.wireOp",EDGE,"E1166");var subQ3026=sQuery(id+"F0.wireOp",EDGE,"E1165");var subQ3027=sQuery(id+"F0.wireOp",EDGE,"E1164");var subQ3028=sQuery(id+"F0.wireOp",EDGE,"E1163");var subQ3029=sQuery(id+"F0.wireOp",EDGE,"E1162");var subQ3030=sQuery(id+"F0.wireOp",EDGE,"E1161");var subQ3031=sQuery(id+"F0.wireOp",EDGE,"E1160");var subQ3032=sQuery(id+"F0.wireOp",EDGE,"E1159");var subQ3033=sQuery(id+"F0.wireOp",EDGE,"E1158");var subQ3034=sQuery(id+"F0.wireOp",EDGE,"E1157");var subQ3035=sQuery(id+"F0.wireOp",EDGE,"E1156");var subQ3036=sQuery(id+"F0.wireOp",EDGE,"E1155");var subQ3037=sQuery(id+"F0.wireOp",EDGE,"E1154");var subQ3038=sQuery(id+"F0.wireOp",EDGE,"E1153");var subQ3039=sQuery(id+"F0.wireOp",EDGE,"E1152");var subQ3040=sQuery(id+"F0.wireOp",EDGE,"E1151");var subQ3041=sQuery(id+"F0.wireOp",EDGE,"E1150");var subQ3042=sQuery(id+"F0.wireOp",EDGE,"E1149");var subQ3043=sQuery(id+"F0.wireOp",EDGE,"E1148");var subQ3044=sQuery(id+"F0.wireOp",EDGE,"E1147");var subQ3045=sQuery(id+"F0.wireOp",EDGE,"E1146");var subQ3046=sQuery(id+"F0.wireOp",EDGE,"E1145");var subQ3047=sQuery(id+"F0.wireOp",EDGE,"E1144");var subQ3048=sQuery(id+"F0.wireOp",EDGE,"E1143");var subQ3049=sQuery(id+"F0.wireOp",EDGE,"E1142");var subQ3050=sQuery(id+"F0.wireOp",EDGE,"E1141");var subQ3051=sQuery(id+"F0.wireOp",EDGE,"E1140");var subQ3052=sQuery(id+"F0.wireOp",EDGE,"E1139");var subQ3053=sQuery(id+"F0.wireOp",EDGE,"E1138");var subQ3054=sQuery(id+"F0.wireOp",EDGE,"E1138");var subQ3055=sQuery(id+"F0.wireOp",EDGE,"E1137");var subQ3056=sQuery(id+"F0.wireOp",EDGE,"E1136");var subQ3057=sQuery(id+"F0.wireOp",EDGE,"E1135");var subQ3058=sQuery(id+"F0.wireOp",EDGE,"E1134");var subQ3059=sQuery(id+"F0.wireOp",EDGE,"E1133");var subQ3060=sQuery(id+"F0.wireOp",EDGE,"E1132");var subQ3061=sQuery(id+"F0.wireOp",EDGE,"E1131");var subQ3062=sQuery(id+"F0.wireOp",EDGE,"E1130");var subQ3063=sQuery(id+"F0.wireOp",EDGE,"E1129");var subQ3064=sQuery(id+"F0.wireOp",EDGE,"E1128");var subQ3065=sQuery(id+"F0.wireOp",EDGE,"E1127");var subQ3066=sQuery(id+"F0.wireOp",EDGE,"E1126");var subQ3067=sQuery(id+"F0.wireOp",EDGE,"E1125");var subQ3068=sQuery(id+"F0.wireOp",EDGE,"E1124");var subQ3069=sQuery(id+"F0.wireOp",EDGE,"E1123");var subQ3070=sQuery(id+"F0.wireOp",EDGE,"E1122");var subQ3071=sQuery(id+"F0.wireOp",EDGE,"E1121");var subQ3072=sQuery(id+"F0.wireOp",EDGE,"E1120");var subQ3073=sQuery(id+"F0.wireOp",EDGE,"E1119");var subQ3074=sQuery(id+"F0.wireOp",EDGE,"E1118");var subQ3075=sQuery(id+"F0.wireOp",EDGE,"E1117");var subQ3076=sQuery(id+"F0.wireOp",EDGE,"E1116");var subQ3077=sQuery(id+"F0.wireOp",EDGE,"E1115");var subQ3078=sQuery(id+"F0.wireOp",EDGE,"E1114");var subQ3079=sQuery(id+"F0.wireOp",EDGE,"E1113");var subQ3080=sQuery(id+"F0.wireOp",EDGE,"E1112");var subQ3081=sQuery(id+"F0.wireOp",EDGE,"E1111");var subQ3082=sQuery(id+"F0.wireOp",EDGE,"E1110");var subQ3083=sQuery(id+"F0.wireOp",EDGE,"E1109");var subQ3084=sQuery(id+"F0.wireOp",EDGE,"E1108");var subQ3085=sQuery(id+"F0.wireOp",EDGE,"E1107");var subQ3086=sQuery(id+"F0.wireOp",EDGE,"E1106");var subQ3087=sQuery(id+"F0.wireOp",EDGE,"E1105");var subQ3088=sQuery(id+"F0.wireOp",EDGE,"E1104");var subQ3089=sQuery(id+"F0.wireOp",EDGE,"E1103");var subQ3090=sQuery(id+"F0.wireOp",EDGE,"E1102");var subQ3091=sQuery(id+"F0.wireOp",EDGE,"E1101");var subQ3092=sQuery(id+"F0.wireOp",EDGE,"E1100");var subQ3093=sQuery(id+"F0.wireOp",EDGE,"E1099");var subQ3094=sQuery(id+"F0.wireOp",EDGE,"E1098");var subQ3095=sQuery(id+"F0.wireOp",EDGE,"E1097");var subQ3096=sQuery(id+"F0.wireOp",EDGE,"E1096");var subQ3097=sQuery(id+"F0.wireOp",EDGE,"E1095");var subQ3098=sQuery(id+"F0.wireOp",EDGE,"E1094");var subQ3099=sQuery(id+"F0.wireOp",EDGE,"E1093");var subQ3100=sQuery(id+"F0.wireOp",EDGE,"E1092");var subQ3101=sQuery(id+"F0.wireOp",EDGE,"E1091");var subQ3102=sQuery(id+"F0.wireOp",EDGE,"E1090");var subQ3103=sQuery(id+"F0.wireOp",EDGE,"E1089");var subQ3104=sQuery(id+"F0.wireOp",EDGE,"E1088");var subQ3105=sQuery(id+"F0.wireOp",EDGE,"E1087");var subQ3106=sQuery(id+"F0.wireOp",EDGE,"E1086");var subQ3107=sQuery(id+"F0.wireOp",EDGE,"E1085");var subQ3108=sQuery(id+"F0.wireOp",EDGE,"E1084");var subQ3109=sQuery(id+"F0.wireOp",EDGE,"E1083");var subQ3110=sQuery(id+"F0.wireOp",EDGE,"E1082");var subQ3111=sQuery(id+"F0.wireOp",EDGE,"E1081");var subQ3112=sQuery(id+"F0.wireOp",EDGE,"E1080");var subQ3113=sQuery(id+"F0.wireOp",EDGE,"E1079");var subQ3114=sQuery(id+"F0.wireOp",EDGE,"E1078");var subQ3115=sQuery(id+"F0.wireOp",EDGE,"E1077");var subQ3116=sQuery(id+"F0.wireOp",EDGE,"E1076");var subQ3117=sQuery(id+"F0.wireOp",EDGE,"E1075");var subQ3118=sQuery(id+"F0.wireOp",EDGE,"E1074");var subQ3119=sQuery(id+"F0.wireOp",EDGE,"E1073");var subQ3120=sQuery(id+"F0.wireOp",EDGE,"E1072");var subQ3121=sQuery(id+"F0.wireOp",EDGE,"E1071");var subQ3122=sQuery(id+"F0.wireOp",EDGE,"E1070");var subQ3123=sQuery(id+"F0.wireOp",EDGE,"E1069");var subQ3124=sQuery(id+"F0.wireOp",EDGE,"E1068");var subQ3125=sQuery(id+"F0.wireOp",EDGE,"E1067");var subQ3126=sQuery(id+"F0.wireOp",EDGE,"E1066");var subQ3127=sQuery(id+"F0.wireOp",EDGE,"E1065");var subQ3128=sQuery(id+"F0.wireOp",EDGE,"E1064");var subQ3129=sQuery(id+"F0.wireOp",EDGE,"E1063");var subQ3130=sQuery(id+"F0.wireOp",EDGE,"E1062");var subQ3131=sQuery(id+"F0.wireOp",EDGE,"E1061");var subQ3132=sQuery(id+"F0.wireOp",EDGE,"E1060");var subQ3133=sQuery(id+"F0.wireOp",EDGE,"E1059");var subQ3134=sQuery(id+"F0.wireOp",EDGE,"E1058");var subQ3135=sQuery(id+"F0.wireOp",EDGE,"E1057");var subQ3136=sQuery(id+"F0.wireOp",EDGE,"E1056");var subQ3137=sQuery(id+"F0.wireOp",EDGE,"E1055");var subQ3138=sQuery(id+"F0.wireOp",EDGE,"E1054");var subQ3139=sQuery(id+"F0.wireOp",EDGE,"E1053");var subQ3140=sQuery(id+"F0.wireOp",EDGE,"E1052");var subQ3141=sQuery(id+"F0.wireOp",EDGE,"E1051");var subQ3142=sQuery(id+"F0.wireOp",EDGE,"E1050");var subQ3143=sQuery(id+"F0.wireOp",EDGE,"E1049");var subQ3144=sQuery(id+"F0.wireOp",EDGE,"E1048");var subQ3145=sQuery(id+"F0.wireOp",EDGE,"E1047");var subQ3146=sQuery(id+"F0.wireOp",EDGE,"E1046");var subQ3147=sQuery(id+"F0.wireOp",EDGE,"E1045");var subQ3148=sQuery(id+"F0.wireOp",EDGE,"E1044");var subQ3149=sQuery(id+"F0.wireOp",EDGE,"E1043");var subQ3150=sQuery(id+"F0.wireOp",EDGE,"E1042");var subQ3151=sQuery(id+"F0.wireOp",EDGE,"E1041");var subQ3152=sQuery(id+"F0.wireOp",EDGE,"E1040");var subQ3153=sQuery(id+"F0.wireOp",EDGE,"E1039");var subQ3154=sQuery(id+"F0.wireOp",EDGE,"E1038");var subQ3155=sQuery(id+"F0.wireOp",EDGE,"E1037");var subQ3156=sQuery(id+"F0.wireOp",EDGE,"E1036");var subQ3157=sQuery(id+"F0.wireOp",EDGE,"E1035");var subQ3158=sQuery(id+"F0.wireOp",EDGE,"E1034");var subQ3159=sQuery(id+"F0.wireOp",EDGE,"E1033");var subQ3160=sQuery(id+"F0.wireOp",EDGE,"E1032");var subQ3161=sQuery(id+"F0.wireOp",EDGE,"E1031");var subQ3162=sQuery(id+"F0.wireOp",EDGE,"E1030");var subQ3163=sQuery(id+"F0.wireOp",EDGE,"E1029");var subQ3164=sQuery(id+"F0.wireOp",EDGE,"E1028");var subQ3165=sQuery(id+"F0.wireOp",EDGE,"E1027");var subQ3166=sQuery(id+"F0.wireOp",EDGE,"E1026");var subQ3167=sQuery(id+"F0.wireOp",EDGE,"E1025");var subQ3168=sQuery(id+"F0.wireOp",EDGE,"E1024");var subQ3169=sQuery(id+"F0.wireOp",EDGE,"E1023");var subQ3170=sQuery(id+"F0.wireOp",EDGE,"E1022");var subQ3171=sQuery(id+"F0.wireOp",EDGE,"E1021");var subQ3172=sQuery(id+"F0.wireOp",EDGE,"E1020");var subQ3173=sQuery(id+"F0.wireOp",EDGE,"E1019");var subQ3174=sQuery(id+"F0.wireOp",EDGE,"E1018");var subQ3175=sQuery(id+"F0.wireOp",EDGE,"E1017");var subQ3176=sQuery(id+"F0.wireOp",EDGE,"E1016");var subQ3177=sQuery(id+"F0.wireOp",EDGE,"E1015");var subQ3178=sQuery(id+"F0.wireOp",EDGE,"E1014");var subQ3179=sQuery(id+"F0.wireOp",EDGE,"E1013");var subQ3180=sQuery(id+"F0.wireOp",EDGE,"E1012");var subQ3181=sQuery(id+"F0.wireOp",EDGE,"E1011");var subQ3182=sQuery(id+"F0.wireOp",EDGE,"E1010");var subQ3183=sQuery(id+"F0.wireOp",EDGE,"E1009");var subQ3184=sQuery(id+"F0.wireOp",EDGE,"E1008");var subQ3185=sQuery(id+"F0.wireOp",EDGE,"E1007");var subQ3186=sQuery(id+"F0.wireOp",EDGE,"E1006");var subQ3187=sQuery(id+"F0.wireOp",EDGE,"E1005");var subQ3188=sQuery(id+"F0.wireOp",EDGE,"E1004");var subQ3189=sQuery(id+"F0.wireOp",EDGE,"E1003");var subQ3190=sQuery(id+"F0.wireOp",EDGE,"E1002");var subQ3191=sQuery(id+"F0.wireOp",EDGE,"E1001");var subQ3192=sQuery(id+"F0.wireOp",EDGE,"E1000");var subQ3193=sQuery(id+"F0.wireOp",EDGE,"E999");var subQ3194=sQuery(id+"F0.wireOp",EDGE,"E998");var subQ3195=sQuery(id+"F0.wireOp",EDGE,"E997");var subQ3196=sQuery(id+"F0.wireOp",EDGE,"E996");var subQ3197=sQuery(id+"F0.wireOp",EDGE,"E995");var subQ3198=sQuery(id+"F0.wireOp",EDGE,"E994");var subQ3199=sQuery(id+"F0.wireOp",EDGE,"E993");var subQ3200=sQuery(id+"F0.wireOp",EDGE,"E992");var subQ3201=sQuery(id+"F0.wireOp",EDGE,"E991");var subQ3202=sQuery(id+"F0.wireOp",EDGE,"E990");var subQ3203=sQuery(id+"F0.wireOp",EDGE,"E989");var subQ3204=sQuery(id+"F0.wireOp",EDGE,"E988");var subQ3205=sQuery(id+"F0.wireOp",EDGE,"E987");var subQ3206=sQuery(id+"F0.wireOp",EDGE,"E986");var subQ3207=sQuery(id+"F0.wireOp",EDGE,"E985");var subQ3208=sQuery(id+"F0.wireOp",EDGE,"E984");var subQ3209=sQuery(id+"F0.wireOp",EDGE,"E983");var subQ3210=sQuery(id+"F0.wireOp",EDGE,"E982");var subQ3211=sQuery(id+"F0.wireOp",EDGE,"E981");var subQ3212=sQuery(id+"F0.wireOp",EDGE,"E980");var subQ3213=sQuery(id+"F0.wireOp",EDGE,"E979");var subQ3214=sQuery(id+"F0.wireOp",EDGE,"E978");var subQ3215=sQuery(id+"F0.wireOp",EDGE,"E977");var subQ3216=sQuery(id+"F0.wireOp",EDGE,"E976");var subQ3217=sQuery(id+"F0.wireOp",EDGE,"E975");var subQ3218=sQuery(id+"F0.wireOp",EDGE,"E974");var subQ3219=sQuery(id+"F0.wireOp",EDGE,"E973");var subQ3220=sQuery(id+"F0.wireOp",EDGE,"E972");var subQ3221=sQuery(id+"F0.wireOp",EDGE,"E971");var subQ3222=sQuery(id+"F0.wireOp",EDGE,"E970");var subQ3223=sQuery(id+"F0.wireOp",EDGE,"E969");var subQ3224=sQuery(id+"F0.wireOp",EDGE,"E968");var subQ3225=sQuery(id+"F0.wireOp",EDGE,"E967");var subQ3226=sQuery(id+"F0.wireOp",EDGE,"E966");var subQ3227=sQuery(id+"F0.wireOp",EDGE,"E965");var subQ3228=sQuery(id+"F0.wireOp",EDGE,"E964");var subQ3229=sQuery(id+"F0.wireOp",EDGE,"E963");var subQ3230=sQuery(id+"F0.wireOp",EDGE,"E962");var subQ3231=sQuery(id+"F0.wireOp",EDGE,"E961");var subQ3232=sQuery(id+"F0.wireOp",EDGE,"E960");var subQ3233=sQuery(id+"F0.wireOp",EDGE,"E959");var subQ3234=sQuery(id+"F0.wireOp",EDGE,"E958");var subQ3235=sQuery(id+"F0.wireOp",EDGE,"E957");var subQ3236=sQuery(id+"F0.wireOp",EDGE,"E956");var subQ3237=sQuery(id+"F0.wireOp",EDGE,"E955");var subQ3238=sQuery(id+"F0.wireOp",EDGE,"E954");var subQ3239=sQuery(id+"F0.wireOp",EDGE,"E953");var subQ3240=sQuery(id+"F0.wireOp",EDGE,"E952");var subQ3241=sQuery(id+"F0.wireOp",EDGE,"E951");var subQ3242=sQuery(id+"F0.wireOp",EDGE,"E950");var subQ3243=sQuery(id+"F0.wireOp",EDGE,"E949");var subQ3244=sQuery(id+"F0.wireOp",EDGE,"E948");var subQ3245=sQuery(id+"F0.wireOp",EDGE,"E947");var subQ3246=sQuery(id+"F0.wireOp",EDGE,"E946");var subQ3247=sQuery(id+"F0.wireOp",EDGE,"E945");var subQ3248=sQuery(id+"F0.wireOp",EDGE,"E944");var subQ3249=sQuery(id+"F0.wireOp",EDGE,"E943");var subQ3250=sQuery(id+"F0.wireOp",EDGE,"E942");var subQ3251=sQuery(id+"F0.wireOp",EDGE,"E941");var subQ3252=sQuery(id+"F0.wireOp",EDGE,"E940");var subQ3253=sQuery(id+"F0.wireOp",EDGE,"E939");var subQ3254=sQuery(id+"F0.wireOp",EDGE,"E938");var subQ3255=sQuery(id+"F0.wireOp",EDGE,"E937");var subQ3256=sQuery(id+"F0.wireOp",EDGE,"E936");var subQ3257=sQuery(id+"F0.wireOp",EDGE,"E935");var subQ3258=sQuery(id+"F0.wireOp",EDGE,"E934");var subQ3259=sQuery(id+"F0.wireOp",EDGE,"E933");var subQ3260=sQuery(id+"F0.wireOp",EDGE,"E932");var subQ3261=sQuery(id+"F0.wireOp",EDGE,"E931");var subQ3262=sQuery(id+"F0.wireOp",EDGE,"E930");var subQ3263=sQuery(id+"F0.wireOp",EDGE,"E929");var subQ3264=sQuery(id+"F0.wireOp",EDGE,"E928");var subQ3265=sQuery(id+"F0.wireOp",EDGE,"E927");var subQ3266=sQuery(id+"F0.wireOp",EDGE,"E926");var subQ3267=sQuery(id+"F0.wireOp",EDGE,"E925");var subQ3268=sQuery(id+"F0.wireOp",EDGE,"E924");var subQ3269=sQuery(id+"F0.wireOp",EDGE,"E923");var subQ3270=sQuery(id+"F0.wireOp",EDGE,"E922");var subQ3271=sQuery(id+"F0.wireOp",EDGE,"E921");var subQ3272=sQuery(id+"F0.wireOp",EDGE,"E920");var subQ3273=sQuery(id+"F0.wireOp",EDGE,"E919");var subQ3274=sQuery(id+"F0.wireOp",EDGE,"E918");var subQ3275=sQuery(id+"F0.wireOp",EDGE,"E917");var subQ3276=sQuery(id+"F0.wireOp",EDGE,"E916");var subQ3277=sQuery(id+"F0.wireOp",EDGE,"E915");var subQ3278=sQuery(id+"F0.wireOp",EDGE,"E914");var subQ3279=sQuery(id+"F0.wireOp",EDGE,"E913");var subQ3280=sQuery(id+"F0.wireOp",EDGE,"E912");var subQ3281=sQuery(id+"F0.wireOp",EDGE,"E911");var subQ3282=sQuery(id+"F0.wireOp",EDGE,"E910");var subQ3283=sQuery(id+"F0.wireOp",EDGE,"E909");var subQ3284=sQuery(id+"F0.wireOp",EDGE,"E908");var subQ3285=sQuery(id+"F0.wireOp",EDGE,"E907");var subQ3286=sQuery(id+"F0.wireOp",EDGE,"E906");var subQ3287=sQuery(id+"F0.wireOp",EDGE,"E905");var subQ3288=sQuery(id+"F0.wireOp",EDGE,"E904");var subQ3289=sQuery(id+"F0.wireOp",EDGE,"E903");var subQ3290=sQuery(id+"F0.wireOp",EDGE,"E902");var subQ3291=sQuery(id+"F0.wireOp",EDGE,"E901");var subQ3292=sQuery(id+"F0.wireOp",EDGE,"E900");var subQ3293=sQuery(id+"F0.wireOp",EDGE,"E899");var subQ3294=sQuery(id+"F0.wireOp",EDGE,"E898");var subQ3295=sQuery(id+"F0.wireOp",EDGE,"E897");var subQ3296=sQuery(id+"F0.wireOp",EDGE,"E896");var subQ3297=sQuery(id+"F0.wireOp",EDGE,"E895");var subQ3298=sQuery(id+"F0.wireOp",EDGE,"E894");var subQ3299=sQuery(id+"F0.wireOp",EDGE,"E893");var subQ3300=sQuery(id+"F0.wireOp",EDGE,"E892");var subQ3301=sQuery(id+"F0.wireOp",EDGE,"E891");var subQ3302=sQuery(id+"F0.wireOp",EDGE,"E890");var subQ3303=sQuery(id+"F0.wireOp",EDGE,"E889");var subQ3304=sQuery(id+"F0.wireOp",EDGE,"E888");var subQ3305=sQuery(id+"F0.wireOp",EDGE,"E887");var subQ3306=sQuery(id+"F0.wireOp",EDGE,"E886");var subQ3307=sQuery(id+"F0.wireOp",EDGE,"E885");var subQ3308=sQuery(id+"F0.wireOp",EDGE,"E884");var subQ3309=sQuery(id+"F0.wireOp",EDGE,"E883");var subQ3310=sQuery(id+"F0.wireOp",EDGE,"E882");var subQ3311=sQuery(id+"F0.wireOp",EDGE,"E881");var subQ3312=sQuery(id+"F0.wireOp",EDGE,"E880");var subQ3313=sQuery(id+"F0.wireOp",EDGE,"E879");var subQ3314=sQuery(id+"F0.wireOp",EDGE,"E878");var subQ3315=sQuery(id+"F0.wireOp",EDGE,"E877");var subQ3316=sQuery(id+"F0.wireOp",EDGE,"E876");var subQ3317=sQuery(id+"F0.wireOp",EDGE,"E875");var subQ3318=sQuery(id+"F0.wireOp",EDGE,"E874");var subQ3319=sQuery(id+"F0.wireOp",EDGE,"E873");var subQ3320=sQuery(id+"F0.wireOp",EDGE,"E872");var subQ3321=sQuery(id+"F0.wireOp",EDGE,"E871");var subQ3322=sQuery(id+"F0.wireOp",EDGE,"E870");var subQ3323=sQuery(id+"F0.wireOp",EDGE,"E869");var subQ3324=sQuery(id+"F0.wireOp",EDGE,"E868");var subQ3325=sQuery(id+"F0.wireOp",EDGE,"E867");var subQ3326=sQuery(id+"F0.wireOp",EDGE,"E866");var subQ3327=sQuery(id+"F0.wireOp",EDGE,"E865");var subQ3328=sQuery(id+"F0.wireOp",EDGE,"E864");var subQ3329=sQuery(id+"F0.wireOp",EDGE,"E863");var subQ3330=sQuery(id+"F0.wireOp",EDGE,"E862");var subQ3331=sQuery(id+"F0.wireOp",EDGE,"E861");var subQ3332=sQuery(id+"F0.wireOp",EDGE,"E860");var subQ3333=sQuery(id+"F0.wireOp",EDGE,"E859");var subQ3334=sQuery(id+"F0.wireOp",EDGE,"E858");var subQ3335=sQuery(id+"F0.wireOp",EDGE,"E857");var subQ3336=sQuery(id+"F0.wireOp",EDGE,"E856");var subQ3337=sQuery(id+"F0.wireOp",EDGE,"E855");var subQ3338=sQuery(id+"F0.wireOp",EDGE,"E854");var subQ3339=sQuery(id+"F0.wireOp",EDGE,"E853");var subQ3340=sQuery(id+"F0.wireOp",EDGE,"E852");var subQ3341=sQuery(id+"F0.wireOp",EDGE,"E851");var subQ3342=sQuery(id+"F0.wireOp",EDGE,"E850");var subQ3343=sQuery(id+"F0.wireOp",EDGE,"E849");var subQ3344=sQuery(id+"F0.wireOp",EDGE,"E848");var subQ3345=sQuery(id+"F0.wireOp",EDGE,"E847");var subQ3346=sQuery(id+"F0.wireOp",EDGE,"E846");var subQ3347=sQuery(id+"F0.wireOp",EDGE,"E845");var subQ3348=sQuery(id+"F0.wireOp",EDGE,"E844");var subQ3349=sQuery(id+"F0.wireOp",EDGE,"E843");var subQ3350=sQuery(id+"F0.wireOp",EDGE,"E842");var subQ3351=sQuery(id+"F0.wireOp",EDGE,"E841");var subQ3352=sQuery(id+"F0.wireOp",EDGE,"E840");var subQ3353=sQuery(id+"F0.wireOp",EDGE,"E839");var subQ3354=sQuery(id+"F0.wireOp",EDGE,"E838");var subQ3355=sQuery(id+"F0.wireOp",EDGE,"E837");var subQ3356=sQuery(id+"F0.wireOp",EDGE,"E836");var subQ3357=sQuery(id+"F0.wireOp",EDGE,"E835");var subQ3358=sQuery(id+"F0.wireOp",EDGE,"E834");var subQ3359=sQuery(id+"F0.wireOp",EDGE,"E833");var subQ3360=sQuery(id+"F0.wireOp",EDGE,"E832");var subQ3361=sQuery(id+"F0.wireOp",EDGE,"E831");var subQ3362=sQuery(id+"F0.wireOp",EDGE,"E830");var subQ3363=sQuery(id+"F0.wireOp",EDGE,"E829");var subQ3364=sQuery(id+"F0.wireOp",EDGE,"E828");var subQ3365=sQuery(id+"F0.wireOp",EDGE,"E827");var subQ3366=sQuery(id+"F0.wireOp",EDGE,"E826");var subQ3367=sQuery(id+"F0.wireOp",EDGE,"E825");var subQ3368=sQuery(id+"F0.wireOp",EDGE,"E824");var subQ3369=sQuery(id+"F0.wireOp",EDGE,"E823");var subQ3370=sQuery(id+"F0.wireOp",EDGE,"E822");var subQ3371=sQuery(id+"F0.wireOp",EDGE,"E821");var subQ3372=sQuery(id+"F0.wireOp",EDGE,"E820");var subQ3373=sQuery(id+"F0.wireOp",EDGE,"E819");var subQ3374=sQuery(id+"F0.wireOp",EDGE,"E818");var subQ3375=sQuery(id+"F0.wireOp",EDGE,"E817");var subQ3376=sQuery(id+"F0.wireOp",EDGE,"E816");var subQ3377=sQuery(id+"F0.wireOp",EDGE,"E815");var subQ3378=sQuery(id+"F0.wireOp",EDGE,"E814");var subQ3379=sQuery(id+"F0.wireOp",EDGE,"E813");var subQ3380=sQuery(id+"F0.wireOp",EDGE,"E812");var subQ3381=sQuery(id+"F0.wireOp",EDGE,"E811");var subQ3382=sQuery(id+"F0.wireOp",EDGE,"E810");var subQ3383=sQuery(id+"F0.wireOp",EDGE,"E809");var subQ3384=sQuery(id+"F0.wireOp",EDGE,"E808");var subQ3385=sQuery(id+"F0.wireOp",EDGE,"E807");var subQ3386=sQuery(id+"F0.wireOp",EDGE,"E806");var subQ3387=sQuery(id+"F0.wireOp",EDGE,"E805");var subQ3388=sQuery(id+"F0.wireOp",EDGE,"E804");var subQ3389=sQuery(id+"F0.wireOp",EDGE,"E803");var subQ3390=sQuery(id+"F0.wireOp",EDGE,"E802");var subQ3391=sQuery(id+"F0.wireOp",EDGE,"E801");var subQ3392=sQuery(id+"F0.wireOp",EDGE,"E800");var subQ3393=sQuery(id+"F0.wireOp",EDGE,"E799");var subQ3394=sQuery(id+"F0.wireOp",EDGE,"E798");var subQ3395=sQuery(id+"F0.wireOp",EDGE,"E797");var subQ3396=sQuery(id+"F0.wireOp",EDGE,"E796");var subQ3397=sQuery(id+"F0.wireOp",EDGE,"E795");var subQ3398=sQuery(id+"F0.wireOp",EDGE,"E794");var subQ3399=sQuery(id+"F0.wireOp",EDGE,"E793");var subQ3400=sQuery(id+"F0.wireOp",EDGE,"E792");var subQ3401=sQuery(id+"F0.wireOp",EDGE,"E791");var subQ3402=sQuery(id+"F0.wireOp",EDGE,"E790");var subQ3403=sQuery(id+"F0.wireOp",EDGE,"E789");var subQ3404=sQuery(id+"F0.wireOp",EDGE,"E788");var subQ3405=sQuery(id+"F0.wireOp",EDGE,"E787");var subQ3406=sQuery(id+"F0.wireOp",EDGE,"E786");var subQ3407=sQuery(id+"F0.wireOp",EDGE,"E785");var subQ3408=sQuery(id+"F0.wireOp",EDGE,"E784");var subQ3409=sQuery(id+"F0.wireOp",EDGE,"E783");var subQ3410=sQuery(id+"F0.wireOp",EDGE,"E782");var subQ3411=sQuery(id+"F0.wireOp",EDGE,"E781");var subQ3412=sQuery(id+"F0.wireOp",EDGE,"E780");var subQ3413=sQuery(id+"F0.wireOp",EDGE,"E779");var subQ3414=sQuery(id+"F0.wireOp",EDGE,"E778");var subQ3415=sQuery(id+"F0.wireOp",EDGE,"E777");var subQ3416=sQuery(id+"F0.wireOp",EDGE,"E776");var subQ3417=sQuery(id+"F0.wireOp",EDGE,"E775");var subQ3418=sQuery(id+"F0.wireOp",EDGE,"E774");var subQ3419=sQuery(id+"F0.wireOp",EDGE,"E773");var subQ3420=sQuery(id+"F0.wireOp",EDGE,"E772");var subQ3421=sQuery(id+"F0.wireOp",EDGE,"E771");var subQ3422=sQuery(id+"F0.wireOp",EDGE,"E770");var subQ3423=sQuery(id+"F0.wireOp",EDGE,"E769");var subQ3424=sQuery(id+"F0.wireOp",EDGE,"E768");var subQ3425=sQuery(id+"F0.wireOp",EDGE,"E767");var subQ3426=sQuery(id+"F0.wireOp",EDGE,"E766");var subQ3427=sQuery(id+"F0.wireOp",EDGE,"E765");var subQ3428=sQuery(id+"F0.wireOp",EDGE,"E764");var subQ3429=sQuery(id+"F0.wireOp",EDGE,"E763");var subQ3430=sQuery(id+"F0.wireOp",EDGE,"E762");var subQ3431=sQuery(id+"F0.wireOp",EDGE,"E761");var subQ3432=sQuery(id+"F0.wireOp",EDGE,"E760");var subQ3433=sQuery(id+"F0.wireOp",EDGE,"E759");var subQ3434=sQuery(id+"F0.wireOp",EDGE,"E758");var subQ3435=sQuery(id+"F0.wireOp",EDGE,"E757");var subQ3436=sQuery(id+"F0.wireOp",EDGE,"E756");var subQ3437=sQuery(id+"F0.wireOp",EDGE,"E755");var subQ3438=sQuery(id+"F0.wireOp",EDGE,"E754");var subQ3439=sQuery(id+"F0.wireOp",EDGE,"E753");var subQ3440=sQuery(id+"F0.wireOp",EDGE,"E752");var subQ3441=sQuery(id+"F0.wireOp",EDGE,"E751");var subQ3442=sQuery(id+"F0.wireOp",EDGE,"E750");var subQ3443=sQuery(id+"F0.wireOp",EDGE,"E749");var subQ3444=sQuery(id+"F0.wireOp",EDGE,"E748");var subQ3445=sQuery(id+"F0.wireOp",EDGE,"E747");var subQ3446=sQuery(id+"F0.wireOp",EDGE,"E746");var subQ3447=sQuery(id+"F0.wireOp",EDGE,"E745");var subQ3448=sQuery(id+"F0.wireOp",EDGE,"E744");var subQ3449=sQuery(id+"F0.wireOp",EDGE,"E743");var subQ3450=sQuery(id+"F0.wireOp",EDGE,"E742");var subQ3451=sQuery(id+"F0.wireOp",EDGE,"E741");var subQ3452=sQuery(id+"F0.wireOp",EDGE,"E740");var subQ3453=sQuery(id+"F0.wireOp",EDGE,"E739");var subQ3454=sQuery(id+"F0.wireOp",EDGE,"E738");var subQ3455=sQuery(id+"F0.wireOp",EDGE,"E737");var subQ3456=sQuery(id+"F0.wireOp",EDGE,"E736");var subQ3457=sQuery(id+"F0.wireOp",EDGE,"E735");var subQ3458=sQuery(id+"F0.wireOp",EDGE,"E734");var subQ3459=sQuery(id+"F0.wireOp",EDGE,"E733");var subQ3460=sQuery(id+"F0.wireOp",EDGE,"E732");var subQ3461=sQuery(id+"F0.wireOp",EDGE,"E731");var subQ3462=sQuery(id+"F0.wireOp",EDGE,"E730");var subQ3463=sQuery(id+"F0.wireOp",EDGE,"E729");var subQ3464=sQuery(id+"F0.wireOp",EDGE,"E728");var subQ3465=sQuery(id+"F0.wireOp",EDGE,"E727");var subQ3466=sQuery(id+"F0.wireOp",EDGE,"E726");var subQ3467=sQuery(id+"F0.wireOp",EDGE,"E725");var subQ3468=sQuery(id+"F0.wireOp",EDGE,"E724");var subQ3469=sQuery(id+"F0.wireOp",EDGE,"E723");var subQ3470=sQuery(id+"F0.wireOp",EDGE,"E722");var subQ3471=sQuery(id+"F0.wireOp",EDGE,"E721");var subQ3472=sQuery(id+"F0.wireOp",EDGE,"E720");var subQ3473=sQuery(id+"F0.wireOp",EDGE,"E719");var subQ3474=sQuery(id+"F0.wireOp",EDGE,"E718");var subQ3475=sQuery(id+"F0.wireOp",EDGE,"E717");var subQ3476=sQuery(id+"F0.wireOp",EDGE,"E716");var subQ3477=sQuery(id+"F0.wireOp",EDGE,"E715");var subQ3478=sQuery(id+"F0.wireOp",EDGE,"E714");var subQ3479=sQuery(id+"F0.wireOp",EDGE,"E713");var subQ3480=sQuery(id+"F0.wireOp",EDGE,"E712");var subQ3481=sQuery(id+"F0.wireOp",EDGE,"E711");var subQ3482=sQuery(id+"F0.wireOp",EDGE,"E710");var subQ3483=sQuery(id+"F0.wireOp",EDGE,"E709");var subQ3484=sQuery(id+"F0.wireOp",EDGE,"E708");var subQ3485=sQuery(id+"F0.wireOp",EDGE,"E707");var subQ3486=sQuery(id+"F0.wireOp",EDGE,"E706");var subQ3487=sQuery(id+"F0.wireOp",EDGE,"E705");var subQ3488=sQuery(id+"F0.wireOp",EDGE,"E704");var subQ3489=sQuery(id+"F0.wireOp",EDGE,"E703");var subQ3490=sQuery(id+"F0.wireOp",EDGE,"E702");var subQ3491=sQuery(id+"F0.wireOp",EDGE,"E701");var subQ3492=sQuery(id+"F0.wireOp",EDGE,"E700");var subQ3493=sQuery(id+"F0.wireOp",EDGE,"E699");var subQ3494=sQuery(id+"F0.wireOp",EDGE,"E698");var subQ3495=sQuery(id+"F0.wireOp",EDGE,"E697");var subQ3496=sQuery(id+"F0.wireOp",EDGE,"E696");var subQ3497=sQuery(id+"F0.wireOp",EDGE,"E695");var subQ3498=sQuery(id+"F0.wireOp",EDGE,"E694");var subQ3499=sQuery(id+"F0.wireOp",EDGE,"E693");var subQ3500=sQuery(id+"F0.wireOp",EDGE,"E692");var subQ3501=sQuery(id+"F0.wireOp",EDGE,"E691");var subQ3502=sQuery(id+"F0.wireOp",EDGE,"E690");var subQ3503=sQuery(id+"F0.wireOp",EDGE,"E689");var subQ3504=sQuery(id+"F0.wireOp",EDGE,"E688");var subQ3505=sQuery(id+"F0.wireOp",EDGE,"E687");var subQ3506=sQuery(id+"F0.wireOp",EDGE,"E686");var subQ3507=sQuery(id+"F0.wireOp",EDGE,"E685");var subQ3508=sQuery(id+"F0.wireOp",EDGE,"E684");var subQ3509=sQuery(id+"F0.wireOp",EDGE,"E683");var subQ3510=sQuery(id+"F0.wireOp",EDGE,"E682");var subQ3511=sQuery(id+"F0.wireOp",EDGE,"E681");var subQ3512=sQuery(id+"F0.wireOp",EDGE,"E680");var subQ3513=sQuery(id+"F0.wireOp",EDGE,"E679");var subQ3514=sQuery(id+"F0.wireOp",EDGE,"E678");var subQ3515=sQuery(id+"F0.wireOp",EDGE,"E677");var subQ3516=sQuery(id+"F0.wireOp",EDGE,"E676");var subQ3517=sQuery(id+"F0.wireOp",EDGE,"E675");var subQ3518=sQuery(id+"F0.wireOp",EDGE,"E674");var subQ3519=sQuery(id+"F0.wireOp",EDGE,"E673");var subQ3520=sQuery(id+"F0.wireOp",EDGE,"E672");var subQ3521=sQuery(id+"F0.wireOp",EDGE,"E671");var subQ3522=sQuery(id+"F0.wireOp",EDGE,"E670");var subQ3523=sQuery(id+"F0.wireOp",EDGE,"E669");var subQ3524=sQuery(id+"F0.wireOp",EDGE,"E668");var subQ3525=sQuery(id+"F0.wireOp",EDGE,"E667");var subQ3526=sQuery(id+"F0.wireOp",EDGE,"E666");var subQ3527=sQuery(id+"F0.wireOp",EDGE,"E665");var subQ3528=sQuery(id+"F0.wireOp",EDGE,"E664");var subQ3529=sQuery(id+"F0.wireOp",EDGE,"E663");var subQ3530=sQuery(id+"F0.wireOp",EDGE,"E662");var subQ3531=sQuery(id+"F0.wireOp",EDGE,"E661");var subQ3532=sQuery(id+"F0.wireOp",EDGE,"E660");var subQ3533=sQuery(id+"F0.wireOp",EDGE,"E659");var subQ3534=sQuery(id+"F0.wireOp",EDGE,"E658");var subQ3535=sQuery(id+"F0.wireOp",EDGE,"E657");var subQ3536=sQuery(id+"F0.wireOp",EDGE,"E656");var subQ3537=sQuery(id+"F0.wireOp",EDGE,"E655");var subQ3538=sQuery(id+"F0.wireOp",EDGE,"E654");var subQ3539=sQuery(id+"F0.wireOp",EDGE,"E653");var subQ3540=sQuery(id+"F0.wireOp",EDGE,"E652");var subQ3541=sQuery(id+"F0.wireOp",EDGE,"E651");var subQ3542=sQuery(id+"F0.wireOp",EDGE,"E650");var subQ3543=sQuery(id+"F0.wireOp",EDGE,"E649");var subQ3544=sQuery(id+"F0.wireOp",EDGE,"E648");var subQ3545=sQuery(id+"F0.wireOp",EDGE,"E647");var subQ3546=sQuery(id+"F0.wireOp",EDGE,"E646");var subQ3547=sQuery(id+"F0.wireOp",EDGE,"E645");var subQ3548=sQuery(id+"F0.wireOp",EDGE,"E644");var subQ3549=sQuery(id+"F0.wireOp",EDGE,"E643");var subQ3550=sQuery(id+"F0.wireOp",EDGE,"E642");var subQ3551=sQuery(id+"F0.wireOp",EDGE,"E641");var subQ3552=sQuery(id+"F0.wireOp",EDGE,"E640");var subQ3553=sQuery(id+"F0.wireOp",EDGE,"E639");var subQ3554=sQuery(id+"F0.wireOp",EDGE,"E638");var subQ3555=sQuery(id+"F0.wireOp",EDGE,"E637");var subQ3556=sQuery(id+"F0.wireOp",EDGE,"E636");var subQ3557=sQuery(id+"F0.wireOp",EDGE,"E635");var subQ3558=sQuery(id+"F0.wireOp",EDGE,"E634");var subQ3559=sQuery(id+"F0.wireOp",EDGE,"E633");var subQ3560=sQuery(id+"F0.wireOp",EDGE,"E632");var subQ3561=sQuery(id+"F0.wireOp",EDGE,"E631");var subQ3562=sQuery(id+"F0.wireOp",EDGE,"E630");var subQ3563=sQuery(id+"F0.wireOp",EDGE,"E629");var subQ3564=sQuery(id+"F0.wireOp",EDGE,"E628");var subQ3565=sQuery(id+"F0.wireOp",EDGE,"E627");var subQ3566=sQuery(id+"F0.wireOp",EDGE,"E626");var subQ3567=sQuery(id+"F0.wireOp",EDGE,"E625");var subQ3568=sQuery(id+"F0.wireOp",EDGE,"E624");var subQ3569=sQuery(id+"F0.wireOp",EDGE,"E623");var subQ3570=sQuery(id+"F0.wireOp",EDGE,"E622");var subQ3571=sQuery(id+"F0.wireOp",EDGE,"E621");var subQ3572=sQuery(id+"F0.wireOp",EDGE,"E620");var subQ3573=sQuery(id+"F0.wireOp",EDGE,"E619");var subQ3574=sQuery(id+"F0.wireOp",EDGE,"E618");var subQ3575=sQuery(id+"F0.wireOp",EDGE,"E617");var subQ3576=sQuery(id+"F0.wireOp",EDGE,"E616");var subQ3577=sQuery(id+"F0.wireOp",EDGE,"E615");var subQ3578=sQuery(id+"F0.wireOp",EDGE,"E614");var subQ3579=sQuery(id+"F0.wireOp",EDGE,"E613");var subQ3580=sQuery(id+"F0.wireOp",EDGE,"E612");var subQ3581=sQuery(id+"F0.wireOp",EDGE,"E611");var subQ3582=sQuery(id+"F0.wireOp",EDGE,"E610");var subQ3583=sQuery(id+"F0.wireOp",EDGE,"E609");var subQ3584=sQuery(id+"F0.wireOp",EDGE,"E608");var subQ3585=sQuery(id+"F0.wireOp",EDGE,"E607");var subQ3586=sQuery(id+"F0.wireOp",EDGE,"E606");var subQ3587=sQuery(id+"F0.wireOp",EDGE,"E605");var subQ3588=sQuery(id+"F0.wireOp",EDGE,"E604");var subQ3589=sQuery(id+"F0.wireOp",EDGE,"E603");var subQ3590=sQuery(id+"F0.wireOp",EDGE,"E602");var subQ3591=sQuery(id+"F0.wireOp",EDGE,"E601");var subQ3592=sQuery(id+"F0.wireOp",EDGE,"E600");var subQ3593=sQuery(id+"F0.wireOp",EDGE,"E599");var subQ3594=sQuery(id+"F0.wireOp",EDGE,"E598");var subQ3595=sQuery(id+"F0.wireOp",EDGE,"E597");var subQ3596=sQuery(id+"F0.wireOp",EDGE,"E596");var subQ3597=sQuery(id+"F0.wireOp",EDGE,"E595");var subQ3598=sQuery(id+"F0.wireOp",EDGE,"E594");var subQ3599=sQuery(id+"F0.wireOp",EDGE,"E593");var subQ3600=sQuery(id+"F0.wireOp",EDGE,"E592");var subQ3601=sQuery(id+"F0.wireOp",EDGE,"E591");var subQ3602=sQuery(id+"F0.wireOp",EDGE,"E590");var subQ3603=sQuery(id+"F0.wireOp",EDGE,"E589");var subQ3604=sQuery(id+"F0.wireOp",EDGE,"E588");var subQ3605=sQuery(id+"F0.wireOp",EDGE,"E587");var subQ3606=sQuery(id+"F0.wireOp",EDGE,"E586");var subQ3607=sQuery(id+"F0.wireOp",EDGE,"E585");var subQ3608=sQuery(id+"F0.wireOp",EDGE,"E584");var subQ3609=sQuery(id+"F0.wireOp",EDGE,"E583");var subQ3610=sQuery(id+"F0.wireOp",EDGE,"E582");var subQ3611=sQuery(id+"F0.wireOp",EDGE,"E581");var subQ3612=sQuery(id+"F0.wireOp",EDGE,"E580");var subQ3613=sQuery(id+"F0.wireOp",EDGE,"E579");var subQ3614=sQuery(id+"F0.wireOp",EDGE,"E578");var subQ3615=sQuery(id+"F0.wireOp",EDGE,"E577");var subQ3616=sQuery(id+"F0.wireOp",EDGE,"E576");var subQ3617=sQuery(id+"F0.wireOp",EDGE,"E575");var subQ3618=sQuery(id+"F0.wireOp",EDGE,"E574");var subQ3619=sQuery(id+"F0.wireOp",EDGE,"E573");var subQ3620=sQuery(id+"F0.wireOp",EDGE,"E572");var subQ3621=sQuery(id+"F0.wireOp",EDGE,"E571");var subQ3622=sQuery(id+"F0.wireOp",EDGE,"E570");var subQ3623=sQuery(id+"F0.wireOp",EDGE,"E569");var subQ3624=sQuery(id+"F0.wireOp",EDGE,"E568");var subQ3625=sQuery(id+"F0.wireOp",EDGE,"E567");var subQ3626=sQuery(id+"F0.wireOp",EDGE,"E566");var subQ3627=sQuery(id+"F0.wireOp",EDGE,"E565");var subQ3628=sQuery(id+"F0.wireOp",EDGE,"E564");var subQ3629=sQuery(id+"F0.wireOp",EDGE,"E563");var subQ3630=sQuery(id+"F0.wireOp",EDGE,"E562");var subQ3631=sQuery(id+"F0.wireOp",EDGE,"E561");var subQ3632=sQuery(id+"F0.wireOp",EDGE,"E560");var subQ3633=sQuery(id+"F0.wireOp",EDGE,"E559");var subQ3634=sQuery(id+"F0.wireOp",EDGE,"E558");var subQ3635=sQuery(id+"F0.wireOp",EDGE,"E557");var subQ3636=sQuery(id+"F0.wireOp",EDGE,"E556");var subQ3637=sQuery(id+"F0.wireOp",EDGE,"E555");var subQ3638=sQuery(id+"F0.wireOp",EDGE,"E554");var subQ3639=sQuery(id+"F0.wireOp",EDGE,"E553");var subQ3640=sQuery(id+"F0.wireOp",EDGE,"E552");var subQ3641=sQuery(id+"F0.wireOp",EDGE,"E551");var subQ3642=sQuery(id+"F0.wireOp",EDGE,"E550");var subQ3643=sQuery(id+"F0.wireOp",EDGE,"E549");var subQ3644=sQuery(id+"F0.wireOp",EDGE,"E548");var subQ3645=sQuery(id+"F0.wireOp",EDGE,"E547");var subQ3646=sQuery(id+"F0.wireOp",EDGE,"E546");var subQ3647=sQuery(id+"F0.wireOp",EDGE,"E545");var subQ3648=sQuery(id+"F0.wireOp",EDGE,"E544");var subQ3649=sQuery(id+"F0.wireOp",EDGE,"E543");var subQ3650=sQuery(id+"F0.wireOp",EDGE,"E542");var subQ3651=sQuery(id+"F0.wireOp",EDGE,"E541");var subQ3652=sQuery(id+"F0.wireOp",EDGE,"E540");var subQ3653=sQuery(id+"F0.wireOp",EDGE,"E539");var subQ3654=sQuery(id+"F0.wireOp",EDGE,"E538");var subQ3655=sQuery(id+"F0.wireOp",EDGE,"E537");var subQ3656=sQuery(id+"F0.wireOp",EDGE,"E536");var subQ3657=sQuery(id+"F0.wireOp",EDGE,"E535");var subQ3658=sQuery(id+"F0.wireOp",EDGE,"E534");var subQ3659=sQuery(id+"F0.wireOp",EDGE,"E533");var subQ3660=sQuery(id+"F0.wireOp",EDGE,"E532");var subQ3661=sQuery(id+"F0.wireOp",EDGE,"E531");var subQ3662=sQuery(id+"F0.wireOp",EDGE,"E530");var subQ3663=sQuery(id+"F0.wireOp",EDGE,"E529");var subQ3664=sQuery(id+"F0.wireOp",EDGE,"E528");var subQ3665=sQuery(id+"F0.wireOp",EDGE,"E527");var subQ3666=sQuery(id+"F0.wireOp",EDGE,"E526");var subQ3667=sQuery(id+"F0.wireOp",EDGE,"E525");var subQ3668=sQuery(id+"F0.wireOp",EDGE,"E524");var subQ3669=sQuery(id+"F0.wireOp",EDGE,"E523");var subQ3670=sQuery(id+"F0.wireOp",EDGE,"E522");var subQ3671=sQuery(id+"F0.wireOp",EDGE,"E521");var subQ3672=sQuery(id+"F0.wireOp",EDGE,"E520");var subQ3673=sQuery(id+"F0.wireOp",EDGE,"E519");var subQ3674=sQuery(id+"F0.wireOp",EDGE,"E518");var subQ3675=sQuery(id+"F0.wireOp",EDGE,"E517");var subQ3676=sQuery(id+"F0.wireOp",EDGE,"E516");var subQ3677=sQuery(id+"F0.wireOp",EDGE,"E515");var subQ3678=sQuery(id+"F0.wireOp",EDGE,"E514");var subQ3679=sQuery(id+"F0.wireOp",EDGE,"E513");var subQ3680=sQuery(id+"F0.wireOp",EDGE,"E512");var subQ3681=sQuery(id+"F0.wireOp",EDGE,"E511");var subQ3682=sQuery(id+"F0.wireOp",EDGE,"E510");var subQ3683=sQuery(id+"F0.wireOp",EDGE,"E509");var subQ3684=sQuery(id+"F0.wireOp",EDGE,"E508");var subQ3685=sQuery(id+"F0.wireOp",EDGE,"E507");var subQ3686=sQuery(id+"F0.wireOp",EDGE,"E506");var subQ3687=sQuery(id+"F0.wireOp",EDGE,"E505");var subQ3688=sQuery(id+"F0.wireOp",EDGE,"E504");var subQ3689=sQuery(id+"F0.wireOp",EDGE,"E503");var subQ3690=sQuery(id+"F0.wireOp",EDGE,"E502");var subQ3691=sQuery(id+"F0.wireOp",EDGE,"E501");var subQ3692=sQuery(id+"F0.wireOp",EDGE,"E500");var subQ3693=sQuery(id+"F0.wireOp",EDGE,"E499");var subQ3694=sQuery(id+"F0.wireOp",EDGE,"E498");var subQ3695=sQuery(id+"F0.wireOp",EDGE,"E497");var subQ3696=sQuery(id+"F0.wireOp",EDGE,"E496");var subQ3697=sQuery(id+"F0.wireOp",EDGE,"E495");var subQ3698=sQuery(id+"F0.wireOp",EDGE,"E494");var subQ3699=sQuery(id+"F0.wireOp",EDGE,"E493");var subQ3700=sQuery(id+"F0.wireOp",EDGE,"E492");var subQ3701=sQuery(id+"F0.wireOp",EDGE,"E491");var subQ3702=sQuery(id+"F0.wireOp",EDGE,"E490");var subQ3703=sQuery(id+"F0.wireOp",EDGE,"E489");var subQ3704=sQuery(id+"F0.wireOp",EDGE,"E488");var subQ3705=sQuery(id+"F0.wireOp",EDGE,"E487");var subQ3706=sQuery(id+"F0.wireOp",EDGE,"E486");var subQ3707=sQuery(id+"F0.wireOp",EDGE,"E485");var subQ3708=sQuery(id+"F0.wireOp",EDGE,"E484");var subQ3709=sQuery(id+"F0.wireOp",EDGE,"E483");var subQ3710=sQuery(id+"F0.wireOp",EDGE,"E482");var subQ3711=sQuery(id+"F0.wireOp",EDGE,"E481");var subQ3712=sQuery(id+"F0.wireOp",EDGE,"E480");var subQ3713=sQuery(id+"F0.wireOp",EDGE,"E479");var subQ3714=sQuery(id+"F0.wireOp",EDGE,"E478");var subQ3715=sQuery(id+"F0.wireOp",EDGE,"E477");var subQ3716=sQuery(id+"F0.wireOp",EDGE,"E476");var subQ3717=sQuery(id+"F0.wireOp",EDGE,"E475");var subQ3718=sQuery(id+"F0.wireOp",EDGE,"E474");var subQ3719=sQuery(id+"F0.wireOp",EDGE,"E473");var subQ3720=sQuery(id+"F0.wireOp",EDGE,"E472");var subQ3721=sQuery(id+"F0.wireOp",EDGE,"E471");var subQ3722=sQuery(id+"F0.wireOp",EDGE,"E470");var subQ3723=sQuery(id+"F0.wireOp",EDGE,"E469");var subQ3724=sQuery(id+"F0.wireOp",EDGE,"E468");var subQ3725=sQuery(id+"F0.wireOp",EDGE,"E467");var subQ3726=sQuery(id+"F0.wireOp",EDGE,"E466");var subQ3727=sQuery(id+"F0.wireOp",EDGE,"E465");var subQ3728=sQuery(id+"F0.wireOp",EDGE,"E464");var subQ3729=sQuery(id+"F0.wireOp",EDGE,"E463");var subQ3730=sQuery(id+"F0.wireOp",EDGE,"E462");var subQ3731=sQuery(id+"F0.wireOp",EDGE,"E461");var subQ3732=sQuery(id+"F0.wireOp",EDGE,"E460");var subQ3733=sQuery(id+"F0.wireOp",EDGE,"E459");var subQ3734=sQuery(id+"F0.wireOp",EDGE,"E458");var subQ3735=sQuery(id+"F0.wireOp",EDGE,"E457");var subQ3736=sQuery(id+"F0.wireOp",EDGE,"E456");var subQ3737=sQuery(id+"F0.wireOp",EDGE,"E455");var subQ3738=sQuery(id+"F0.wireOp",EDGE,"E454");var subQ3739=sQuery(id+"F0.wireOp",EDGE,"E453");var subQ3740=sQuery(id+"F0.wireOp",EDGE,"E452");var subQ3741=sQuery(id+"F0.wireOp",EDGE,"E451");var subQ3742=sQuery(id+"F0.wireOp",EDGE,"E450");var subQ3743=sQuery(id+"F0.wireOp",EDGE,"E449");var subQ3744=sQuery(id+"F0.wireOp",EDGE,"E448");var subQ3745=sQuery(id+"F0.wireOp",EDGE,"E447");var subQ3746=sQuery(id+"F0.wireOp",EDGE,"E446");var subQ3747=sQuery(id+"F0.wireOp",EDGE,"E445");var subQ3748=sQuery(id+"F0.wireOp",EDGE,"E444");var subQ3749=sQuery(id+"F0.wireOp",EDGE,"E443");var subQ3750=sQuery(id+"F0.wireOp",EDGE,"E442");var subQ3751=sQuery(id+"F0.wireOp",EDGE,"E441");var subQ3752=sQuery(id+"F0.wireOp",EDGE,"E440");var subQ3753=sQuery(id+"F0.wireOp",EDGE,"E439");var subQ3754=sQuery(id+"F0.wireOp",EDGE,"E438");var subQ3755=sQuery(id+"F0.wireOp",EDGE,"E437");var subQ3756=sQuery(id+"F0.wireOp",EDGE,"E436");var subQ3757=sQuery(id+"F0.wireOp",EDGE,"E435");var subQ3758=sQuery(id+"F0.wireOp",EDGE,"E434");var subQ3759=sQuery(id+"F0.wireOp",EDGE,"E433");var subQ3760=sQuery(id+"F0.wireOp",EDGE,"E432");var subQ3761=sQuery(id+"F0.wireOp",EDGE,"E431");var subQ3762=sQuery(id+"F0.wireOp",EDGE,"E430");var subQ3763=sQuery(id+"F0.wireOp",EDGE,"E429");var subQ3764=sQuery(id+"F0.wireOp",EDGE,"E428");var subQ3765=sQuery(id+"F0.wireOp",EDGE,"E427");var subQ3766=sQuery(id+"F0.wireOp",EDGE,"E426");var subQ3767=sQuery(id+"F0.wireOp",EDGE,"E425");var subQ3768=sQuery(id+"F0.wireOp",EDGE,"E424");var subQ3769=sQuery(id+"F0.wireOp",EDGE,"E423");var subQ3770=sQuery(id+"F0.wireOp",EDGE,"E422");var subQ3771=sQuery(id+"F0.wireOp",EDGE,"E421");var subQ3772=sQuery(id+"F0.wireOp",EDGE,"E420");var subQ3773=sQuery(id+"F0.wireOp",EDGE,"E419");var subQ3774=sQuery(id+"F0.wireOp",EDGE,"E418");var subQ3775=sQuery(id+"F0.wireOp",EDGE,"E417");var subQ3776=sQuery(id+"F0.wireOp",EDGE,"E416");var subQ3777=sQuery(id+"F0.wireOp",EDGE,"E415");var subQ3778=sQuery(id+"F0.wireOp",EDGE,"E414");var subQ3779=sQuery(id+"F0.wireOp",EDGE,"E413");var subQ3780=sQuery(id+"F0.wireOp",EDGE,"E412");var subQ3781=sQuery(id+"F0.wireOp",EDGE,"E411");var subQ3782=sQuery(id+"F0.wireOp",EDGE,"E410");var subQ3783=sQuery(id+"F0.wireOp",EDGE,"E409");var subQ3784=sQuery(id+"F0.wireOp",EDGE,"E408");var subQ3785=sQuery(id+"F0.wireOp",EDGE,"E407");var subQ3786=sQuery(id+"F0.wireOp",EDGE,"E406");var subQ3787=sQuery(id+"F0.wireOp",EDGE,"E405");var subQ3788=sQuery(id+"F0.wireOp",EDGE,"E404");var subQ3789=sQuery(id+"F0.wireOp",EDGE,"E403");var subQ3790=sQuery(id+"F0.wireOp",EDGE,"E402");var subQ3791=sQuery(id+"F0.wireOp",EDGE,"E401");var subQ3792=sQuery(id+"F0.wireOp",EDGE,"E400");var subQ3793=sQuery(id+"F0.wireOp",EDGE,"E399");var subQ3794=sQuery(id+"F0.wireOp",EDGE,"E398");var subQ3795=sQuery(id+"F0.wireOp",EDGE,"E397");var subQ3796=sQuery(id+"F0.wireOp",EDGE,"E396");var subQ3797=sQuery(id+"F0.wireOp",EDGE,"E395");var subQ3798=sQuery(id+"F0.wireOp",EDGE,"E394");var subQ3799=sQuery(id+"F0.wireOp",EDGE,"E393");var subQ3800=sQuery(id+"F0.wireOp",EDGE,"E392");var subQ3801=sQuery(id+"F0.wireOp",EDGE,"E391");var subQ3802=sQuery(id+"F0.wireOp",EDGE,"E390");var subQ3803=sQuery(id+"F0.wireOp",EDGE,"E389");var subQ3804=sQuery(id+"F0.wireOp",EDGE,"E388");var subQ3805=sQuery(id+"F0.wireOp",EDGE,"E387");var subQ3806=sQuery(id+"F0.wireOp",EDGE,"E386");var subQ3807=sQuery(id+"F0.wireOp",EDGE,"E385");var subQ3808=sQuery(id+"F0.wireOp",EDGE,"E384");var subQ3809=sQuery(id+"F0.wireOp",EDGE,"E383");var subQ3810=sQuery(id+"F0.wireOp",EDGE,"E382");var subQ3811=sQuery(id+"F0.wireOp",EDGE,"E381");var subQ3812=sQuery(id+"F0.wireOp",EDGE,"E380");var subQ3813=sQuery(id+"F0.wireOp",EDGE,"E379");var subQ3814=sQuery(id+"F0.wireOp",EDGE,"E378");var subQ3815=sQuery(id+"F0.wireOp",EDGE,"E377");var subQ3816=sQuery(id+"F0.wireOp",EDGE,"E376");var subQ3817=sQuery(id+"F0.wireOp",EDGE,"E375");var subQ3818=sQuery(id+"F0.wireOp",EDGE,"E374");var subQ3819=sQuery(id+"F0.wireOp",EDGE,"E373");var subQ3820=sQuery(id+"F0.wireOp",EDGE,"E372");var subQ3821=sQuery(id+"F0.wireOp",EDGE,"E371");var subQ3822=sQuery(id+"F0.wireOp",EDGE,"E370");var subQ3823=sQuery(id+"F0.wireOp",EDGE,"E369");var subQ3824=sQuery(id+"F0.wireOp",EDGE,"E368");var subQ3825=sQuery(id+"F0.wireOp",EDGE,"E367");var subQ3826=sQuery(id+"F0.wireOp",EDGE,"E366");var subQ3827=sQuery(id+"F0.wireOp",EDGE,"E365");var subQ3828=sQuery(id+"F0.wireOp",EDGE,"E364");var subQ3829=sQuery(id+"F0.wireOp",EDGE,"E363");var subQ3830=sQuery(id+"F0.wireOp",EDGE,"E362");var subQ3831=sQuery(id+"F0.wireOp",EDGE,"E361");var subQ3832=sQuery(id+"F0.wireOp",EDGE,"E360");var subQ3833=sQuery(id+"F0.wireOp",EDGE,"E359");var subQ3834=sQuery(id+"F0.wireOp",EDGE,"E358");var subQ3835=sQuery(id+"F0.wireOp",EDGE,"E357");var subQ3836=sQuery(id+"F0.wireOp",EDGE,"E356");var subQ3837=sQuery(id+"F0.wireOp",EDGE,"E355");var subQ3838=sQuery(id+"F0.wireOp",EDGE,"E354");var subQ3839=sQuery(id+"F0.wireOp",EDGE,"E353");var subQ3840=sQuery(id+"F0.wireOp",EDGE,"E352");var subQ3841=sQuery(id+"F0.wireOp",EDGE,"E351");var subQ3842=sQuery(id+"F0.wireOp",EDGE,"E350");var subQ3843=sQuery(id+"F0.wireOp",EDGE,"E349");var subQ3844=sQuery(id+"F0.wireOp",EDGE,"E348");var subQ3845=sQuery(id+"F0.wireOp",EDGE,"E347");var subQ3846=sQuery(id+"F0.wireOp",EDGE,"E346");var subQ3847=sQuery(id+"F0.wireOp",EDGE,"E345");var subQ3848=sQuery(id+"F0.wireOp",EDGE,"E344");var subQ3849=sQuery(id+"F0.wireOp",EDGE,"E343");var subQ3850=sQuery(id+"F0.wireOp",EDGE,"E342");var subQ3851=sQuery(id+"F0.wireOp",EDGE,"E341");var subQ3852=sQuery(id+"F0.wireOp",EDGE,"E340");var subQ3853=sQuery(id+"F0.wireOp",EDGE,"E339");var subQ3854=sQuery(id+"F0.wireOp",EDGE,"E338");var subQ3855=sQuery(id+"F0.wireOp",EDGE,"E337");var subQ3856=sQuery(id+"F0.wireOp",EDGE,"E336");var subQ3857=sQuery(id+"F0.wireOp",EDGE,"E335");var subQ3858=sQuery(id+"F0.wireOp",EDGE,"E334");var subQ3859=sQuery(id+"F0.wireOp",EDGE,"E333");var subQ3860=sQuery(id+"F0.wireOp",EDGE,"E332");var subQ3861=sQuery(id+"F0.wireOp",EDGE,"E331");var subQ3862=sQuery(id+"F0.wireOp",EDGE,"E330");var subQ3863=sQuery(id+"F0.wireOp",EDGE,"E329");var subQ3864=sQuery(id+"F0.wireOp",EDGE,"E328");var subQ3865=sQuery(id+"F0.wireOp",EDGE,"E327");var subQ3866=sQuery(id+"F0.wireOp",EDGE,"E326");var subQ3867=sQuery(id+"F0.wireOp",EDGE,"E325");var subQ3868=sQuery(id+"F0.wireOp",EDGE,"E324");var subQ3869=sQuery(id+"F0.wireOp",EDGE,"E323");var subQ3870=sQuery(id+"F0.wireOp",EDGE,"E322");var subQ3871=sQuery(id+"F0.wireOp",EDGE,"E321");var subQ3872=sQuery(id+"F0.wireOp",EDGE,"E320");var subQ3873=sQuery(id+"F0.wireOp",EDGE,"E319");var subQ3874=sQuery(id+"F0.wireOp",EDGE,"E318");var subQ3875=sQuery(id+"F0.wireOp",EDGE,"E317");var subQ3876=sQuery(id+"F0.wireOp",EDGE,"E316");var subQ3877=sQuery(id+"F0.wireOp",EDGE,"E315");var subQ3878=sQuery(id+"F0.wireOp",EDGE,"E314");var subQ3879=sQuery(id+"F0.wireOp",EDGE,"E313");var subQ3880=sQuery(id+"F0.wireOp",EDGE,"E312");var subQ3881=sQuery(id+"F0.wireOp",EDGE,"E311");var subQ3882=sQuery(id+"F0.wireOp",EDGE,"E310");var subQ3883=sQuery(id+"F0.wireOp",EDGE,"E309");var subQ3884=sQuery(id+"F0.wireOp",EDGE,"E308");var subQ3885=sQuery(id+"F0.wireOp",EDGE,"E307");var subQ3886=sQuery(id+"F0.wireOp",EDGE,"E306");var subQ3887=sQuery(id+"F0.wireOp",EDGE,"E305");var subQ3888=sQuery(id+"F0.wireOp",EDGE,"E304");var subQ3889=sQuery(id+"F0.wireOp",EDGE,"E303");var subQ3890=sQuery(id+"F0.wireOp",EDGE,"E302");var subQ3891=sQuery(id+"F0.wireOp",EDGE,"E301");var subQ3892=sQuery(id+"F0.wireOp",EDGE,"E300");var subQ3893=sQuery(id+"F0.wireOp",EDGE,"E299");var subQ3894=sQuery(id+"F0.wireOp",EDGE,"E298");var subQ3895=sQuery(id+"F0.wireOp",EDGE,"E297");var subQ3896=sQuery(id+"F0.wireOp",EDGE,"E296");var subQ3897=sQuery(id+"F0.wireOp",EDGE,"E295");var subQ3898=sQuery(id+"F0.wireOp",EDGE,"E294");var subQ3899=sQuery(id+"F0.wireOp",EDGE,"E293");var subQ3900=sQuery(id+"F0.wireOp",EDGE,"E292");var subQ3901=sQuery(id+"F0.wireOp",EDGE,"E291");var subQ3902=sQuery(id+"F0.wireOp",EDGE,"E290");var subQ3903=sQuery(id+"F0.wireOp",EDGE,"E289");var subQ3904=sQuery(id+"F0.wireOp",EDGE,"E288");var subQ3905=sQuery(id+"F0.wireOp",EDGE,"E287");var subQ3906=sQuery(id+"F0.wireOp",EDGE,"E286");var subQ3907=sQuery(id+"F0.wireOp",EDGE,"E285");var subQ3908=sQuery(id+"F0.wireOp",EDGE,"E284");var subQ3909=sQuery(id+"F0.wireOp",EDGE,"E283");var subQ3910=sQuery(id+"F0.wireOp",EDGE,"E282");var subQ3911=sQuery(id+"F0.wireOp",EDGE,"E281");var subQ3912=sQuery(id+"F0.wireOp",EDGE,"E280");var subQ3913=sQuery(id+"F0.wireOp",EDGE,"E279");var subQ3914=sQuery(id+"F0.wireOp",EDGE,"E278");var subQ3915=sQuery(id+"F0.wireOp",EDGE,"E277");var subQ3916=sQuery(id+"F0.wireOp",EDGE,"E276");var subQ3917=sQuery(id+"F0.wireOp",EDGE,"E275");var subQ3918=sQuery(id+"F0.wireOp",EDGE,"E274");var subQ3919=sQuery(id+"F0.wireOp",EDGE,"E273");var subQ3920=sQuery(id+"F0.wireOp",EDGE,"E272");var subQ3921=sQuery(id+"F0.wireOp",EDGE,"E271");var subQ3922=sQuery(id+"F0.wireOp",EDGE,"E270");var subQ3923=sQuery(id+"F0.wireOp",EDGE,"E269");var subQ3924=sQuery(id+"F0.wireOp",EDGE,"E268");var subQ3925=sQuery(id+"F0.wireOp",EDGE,"E267");var subQ3926=sQuery(id+"F0.wireOp",EDGE,"E266");var subQ3927=sQuery(id+"F0.wireOp",EDGE,"E265");var subQ3928=sQuery(id+"F0.wireOp",EDGE,"E264");var subQ3929=sQuery(id+"F0.wireOp",EDGE,"E263");var subQ3930=sQuery(id+"F0.wireOp",EDGE,"E262");var subQ3931=sQuery(id+"F0.wireOp",EDGE,"E261");var subQ3932=sQuery(id+"F0.wireOp",EDGE,"E260");var subQ3933=sQuery(id+"F0.wireOp",EDGE,"E259");var subQ3934=sQuery(id+"F0.wireOp",EDGE,"E258");var subQ3935=sQuery(id+"F0.wireOp",EDGE,"E257");var subQ3936=sQuery(id+"F0.wireOp",EDGE,"E256");var subQ3937=sQuery(id+"F0.wireOp",EDGE,"E255");var subQ3938=sQuery(id+"F0.wireOp",EDGE,"E254");var subQ3939=sQuery(id+"F0.wireOp",EDGE,"E253");var subQ3940=sQuery(id+"F0.wireOp",EDGE,"E252");var subQ3941=sQuery(id+"F0.wireOp",EDGE,"E251");var subQ3942=sQuery(id+"F0.wireOp",EDGE,"E250");var subQ3943=sQuery(id+"F0.wireOp",EDGE,"E249");var subQ3944=sQuery(id+"F0.wireOp",EDGE,"E248");var subQ3945=sQuery(id+"F0.wireOp",EDGE,"E247");var subQ3946=sQuery(id+"F0.wireOp",EDGE,"E246");var subQ3947=sQuery(id+"F0.wireOp",EDGE,"E245");var subQ3948=sQuery(id+"F0.wireOp",EDGE,"E244");var subQ3949=sQuery(id+"F0.wireOp",EDGE,"E243");var subQ3950=sQuery(id+"F0.wireOp",EDGE,"E242");var subQ3951=sQuery(id+"F0.wireOp",EDGE,"E241");var subQ3952=sQuery(id+"F0.wireOp",EDGE,"E240");var subQ3953=sQuery(id+"F0.wireOp",EDGE,"E239");var subQ3954=sQuery(id+"F0.wireOp",EDGE,"E238");var subQ3955=sQuery(id+"F0.wireOp",EDGE,"E237");var subQ3956=sQuery(id+"F0.wireOp",EDGE,"E236");var subQ3957=sQuery(id+"F0.wireOp",EDGE,"E235");var subQ3958=sQuery(id+"F0.wireOp",EDGE,"E234");var subQ3959=sQuery(id+"F0.wireOp",EDGE,"E233");var subQ3960=sQuery(id+"F0.wireOp",EDGE,"E232");var subQ3961=sQuery(id+"F0.wireOp",EDGE,"E231");var subQ3962=sQuery(id+"F0.wireOp",EDGE,"E230");var subQ3963=sQuery(id+"F0.wireOp",EDGE,"E229");var subQ3964=sQuery(id+"F0.wireOp",EDGE,"E228");var subQ3965=sQuery(id+"F0.wireOp",EDGE,"E227");var subQ3966=sQuery(id+"F0.wireOp",EDGE,"E226");var subQ3967=sQuery(id+"F0.wireOp",EDGE,"E225");var subQ3968=sQuery(id+"F0.wireOp",EDGE,"E224");var subQ3969=sQuery(id+"F0.wireOp",EDGE,"E223");var subQ3970=sQuery(id+"F0.wireOp",EDGE,"E222");var subQ3971=sQuery(id+"F0.wireOp",EDGE,"E221");var subQ3972=sQuery(id+"F0.wireOp",EDGE,"E220");var subQ3973=sQuery(id+"F0.wireOp",EDGE,"E219");var subQ3974=sQuery(id+"F0.wireOp",EDGE,"E218");var subQ3975=sQuery(id+"F0.wireOp",EDGE,"E217");var subQ3976=sQuery(id+"F0.wireOp",EDGE,"E216");var subQ3977=sQuery(id+"F0.wireOp",EDGE,"E215");var subQ3978=sQuery(id+"F0.wireOp",EDGE,"E214");var subQ3979=sQuery(id+"F0.wireOp",EDGE,"E212");var subQ3980=sQuery(id+"F0.wireOp",EDGE,"E211");var subQ3981=sQuery(id+"F0.wireOp",EDGE,"E210");var subQ3982=sQuery(id+"F0.wireOp",EDGE,"E209");var subQ3983=sQuery(id+"F0.wireOp",EDGE,"E208");var subQ3984=sQuery(id+"F0.wireOp",EDGE,"E207");var subQ3985=sQuery(id+"F0.wireOp",EDGE,"E206");var subQ3986=sQuery(id+"F0.wireOp",EDGE,"E205");var subQ3987=sQuery(id+"F0.wireOp",EDGE,"E204");var subQ3988=sQuery(id+"F0.wireOp",EDGE,"E203");var subQ3989=sQuery(id+"F0.wireOp",EDGE,"E202");var subQ3990=sQuery(id+"F0.wireOp",EDGE,"E201");var subQ3991=sQuery(id+"F0.wireOp",EDGE,"E200");var subQ3992=sQuery(id+"F0.wireOp",EDGE,"E199");var subQ3993=sQuery(id+"F0.wireOp",EDGE,"E198");var subQ3994=sQuery(id+"F0.wireOp",EDGE,"E197");var subQ3995=sQuery(id+"F0.wireOp",EDGE,"E196");var subQ3996=sQuery(id+"F0.wireOp",EDGE,"E195");var subQ3997=sQuery(id+"F0.wireOp",EDGE,"E194");var subQ3998=sQuery(id+"F0.wireOp",EDGE,"E193");var subQ3999=sQuery(id+"F0.wireOp",EDGE,"E192");var subQ4000=sQuery(id+"F0.wireOp",EDGE,"E191");var subQ4001=sQuery(id+"F0.wireOp",EDGE,"E190");var subQ4002=sQuery(id+"F0.wireOp",EDGE,"E189");var subQ4003=sQuery(id+"F0.wireOp",EDGE,"E188");var subQ4004=sQuery(id+"F0.wireOp",EDGE,"E187");var subQ4005=sQuery(id+"F0.wireOp",EDGE,"E186");var subQ4006=sQuery(id+"F0.wireOp",EDGE,"E185");var subQ4007=sQuery(id+"F0.wireOp",EDGE,"E184");var subQ4008=sQuery(id+"F0.wireOp",EDGE,"E183");var subQ4009=sQuery(id+"F0.wireOp",EDGE,"E182");var subQ4010=sQuery(id+"F0.wireOp",EDGE,"E181");var subQ4011=sQuery(id+"F0.wireOp",EDGE,"E180");var subQ4012=sQuery(id+"F0.wireOp",EDGE,"E179");var subQ4013=sQuery(id+"F0.wireOp",EDGE,"E178");var subQ4014=sQuery(id+"F0.wireOp",EDGE,"E177");var subQ4015=sQuery(id+"F0.wireOp",EDGE,"E176");var subQ4016=sQuery(id+"F0.wireOp",EDGE,"E175");var subQ4017=sQuery(id+"F0.wireOp",EDGE,"E174");var subQ4018=sQuery(id+"F0.wireOp",EDGE,"E173");var subQ4019=sQuery(id+"F0.wireOp",EDGE,"E172");var subQ4020=sQuery(id+"F0.wireOp",EDGE,"E171");var subQ4021=sQuery(id+"F0.wireOp",EDGE,"E170");var subQ4022=sQuery(id+"F0.wireOp",EDGE,"E169");var subQ4023=sQuery(id+"F0.wireOp",EDGE,"E168");var subQ4024=sQuery(id+"F0.wireOp",EDGE,"E167");var subQ4025=sQuery(id+"F0.wireOp",EDGE,"E166");var subQ4026=sQuery(id+"F0.wireOp",EDGE,"E165");var subQ4027=sQuery(id+"F0.wireOp",EDGE,"E164");var subQ4028=sQuery(id+"F0.wireOp",EDGE,"E163");var subQ4029=sQuery(id+"F0.wireOp",EDGE,"E162");var subQ4030=sQuery(id+"F0.wireOp",EDGE,"E161");var subQ4031=sQuery(id+"F0.wireOp",EDGE,"E160");var subQ4032=sQuery(id+"F0.wireOp",EDGE,"E159");var subQ4033=sQuery(id+"F0.wireOp",EDGE,"E158");var subQ4034=sQuery(id+"F0.wireOp",EDGE,"E157");var subQ4035=sQuery(id+"F0.wireOp",EDGE,"E156");var subQ4036=sQuery(id+"F0.wireOp",EDGE,"E155");var subQ4037=sQuery(id+"F0.wireOp",EDGE,"E154");var subQ4038=sQuery(id+"F0.wireOp",EDGE,"E153");var subQ4039=sQuery(id+"F0.wireOp",EDGE,"E152");var subQ4040=sQuery(id+"F0.wireOp",EDGE,"E151");var subQ4041=sQuery(id+"F0.wireOp",EDGE,"E150");var subQ4042=sQuery(id+"F0.wireOp",EDGE,"E149");var subQ4043=sQuery(id+"F0.wireOp",EDGE,"E148");var subQ4044=sQuery(id+"F0.wireOp",EDGE,"E147");var subQ4045=sQuery(id+"F0.wireOp",EDGE,"E146");var subQ4046=sQuery(id+"F0.wireOp",EDGE,"E145");var subQ4047=sQuery(id+"F0.wireOp",EDGE,"E144");var subQ4048=sQuery(id+"F0.wireOp",EDGE,"E143");var subQ4049=sQuery(id+"F0.wireOp",EDGE,"E142");var subQ4050=sQuery(id+"F0.wireOp",EDGE,"E141");var subQ4051=sQuery(id+"F0.wireOp",EDGE,"E140");var subQ4052=sQuery(id+"F0.wireOp",EDGE,"E139");var subQ4053=sQuery(id+"F0.wireOp",EDGE,"E138");var subQ4054=sQuery(id+"F0.wireOp",EDGE,"E137");var subQ4055=sQuery(id+"F0.wireOp",EDGE,"E136");var subQ4056=sQuery(id+"F0.wireOp",EDGE,"E135");var subQ4057=sQuery(id+"F0.wireOp",EDGE,"E134");var subQ4058=sQuery(id+"F0.wireOp",EDGE,"E133");var subQ4059=sQuery(id+"F0.wireOp",EDGE,"E132");var subQ4060=sQuery(id+"F0.wireOp",EDGE,"E131");var subQ4061=sQuery(id+"F0.wireOp",EDGE,"E130");var subQ4062=sQuery(id+"F0.wireOp",EDGE,"E129");var subQ4063=sQuery(id+"F0.wireOp",EDGE,"E128");var subQ4064=sQuery(id+"F0.wireOp",EDGE,"E127");var subQ4065=sQuery(id+"F0.wireOp",EDGE,"E126");var subQ4066=sQuery(id+"F0.wireOp",EDGE,"E125");var subQ4067=sQuery(id+"F0.wireOp",EDGE,"E124");var subQ4068=sQuery(id+"F0.wireOp",EDGE,"E123");var subQ4069=sQuery(id+"F0.wireOp",EDGE,"E122");var subQ4070=sQuery(id+"F0.wireOp",EDGE,"E121");var subQ4071=sQuery(id+"F0.wireOp",EDGE,"E120");var subQ4072=sQuery(id+"F0.wireOp",EDGE,"E119");var subQ4073=sQuery(id+"F0.wireOp",EDGE,"E118");var subQ4074=sQuery(id+"F0.wireOp",EDGE,"E117");var subQ4075=sQuery(id+"F0.wireOp",EDGE,"E116");var subQ4076=sQuery(id+"F0.wireOp",EDGE,"E115");var subQ4077=sQuery(id+"F0.wireOp",EDGE,"E114");var subQ4078=sQuery(id+"F0.wireOp",EDGE,"E113");var subQ4079=sQuery(id+"F0.wireOp",EDGE,"E112");var subQ4080=sQuery(id+"F0.wireOp",EDGE,"E111");var subQ4081=sQuery(id+"F0.wireOp",EDGE,"E110");var subQ4082=sQuery(id+"F0.wireOp",EDGE,"E109");var subQ4083=sQuery(id+"F0.wireOp",EDGE,"E108");var subQ4084=sQuery(id+"F0.wireOp",EDGE,"E108");var subQ4085=sQuery(id+"F0.wireOp",EDGE,"E107");var subQ4086=sQuery(id+"F0.wireOp",EDGE,"E106");var subQ4087=sQuery(id+"F0.wireOp",EDGE,"E105");var subQ4088=sQuery(id+"F0.wireOp",EDGE,"E104");var subQ4089=sQuery(id+"F0.wireOp",EDGE,"E103");var subQ4090=sQuery(id+"F0.wireOp",EDGE,"E102");var subQ4091=sQuery(id+"F0.wireOp",EDGE,"E101");var subQ4092=sQuery(id+"F0.wireOp",EDGE,"E100");var subQ4093=sQuery(id+"F0.wireOp",EDGE,"E99");var subQ4094=sQuery(id+"F0.wireOp",EDGE,"E98");var subQ4095=sQuery(id+"F0.wireOp",EDGE,"E97");var subQ4096=sQuery(id+"F0.wireOp",EDGE,"E96");var subQ4097=sQuery(id+"F0.wireOp",EDGE,"E95");var subQ4098=sQuery(id+"F0.wireOp",EDGE,"E94");var subQ4099=sQuery(id+"F0.wireOp",EDGE,"E93");var subQ4100=sQuery(id+"F0.wireOp",EDGE,"E92");var subQ4101=sQuery(id+"F0.wireOp",EDGE,"E91");var subQ4102=sQuery(id+"F0.wireOp",EDGE,"E90");var subQ4103=sQuery(id+"F0.wireOp",EDGE,"E89");var subQ4104=sQuery(id+"F0.wireOp",EDGE,"E88");var subQ4105=sQuery(id+"F0.wireOp",EDGE,"E87");var subQ4106=sQuery(id+"F0.wireOp",EDGE,"E86");var subQ4107=sQuery(id+"F0.wireOp",EDGE,"E85");var subQ4108=sQuery(id+"F0.wireOp",EDGE,"E84");var subQ4109=sQuery(id+"F0.wireOp",EDGE,"E83");var subQ4110=sQuery(id+"F0.wireOp",EDGE,"E82");var subQ4111=sQuery(id+"F0.wireOp",EDGE,"E81");var subQ4112=sQuery(id+"F0.wireOp",EDGE,"E80");var subQ4113=sQuery(id+"F0.wireOp",EDGE,"E79");var subQ4114=sQuery(id+"F0.wireOp",EDGE,"E78");var subQ4115=sQuery(id+"F0.wireOp",EDGE,"E77");var subQ4116=sQuery(id+"F0.wireOp",EDGE,"E76");var subQ4117=sQuery(id+"F0.wireOp",EDGE,"E75");var subQ4118=sQuery(id+"F0.wireOp",EDGE,"E74");var subQ4119=sQuery(id+"F0.wireOp",EDGE,"E73");var subQ4120=sQuery(id+"F0.wireOp",EDGE,"E72");var subQ4121=sQuery(id+"F0.wireOp",EDGE,"E71");var subQ4122=sQuery(id+"F0.wireOp",EDGE,"E70");var subQ4123=sQuery(id+"F0.wireOp",EDGE,"E69");var subQ4124=sQuery(id+"F0.wireOp",EDGE,"E68");var subQ4125=sQuery(id+"F0.wireOp",EDGE,"E67");var subQ4126=sQuery(id+"F0.wireOp",EDGE,"E66");var subQ4127=sQuery(id+"F0.wireOp",EDGE,"E65");var subQ4128=sQuery(id+"F0.wireOp",EDGE,"E64");var subQ4129=sQuery(id+"F0.wireOp",EDGE,"E63");var subQ4130=sQuery(id+"F0.wireOp",EDGE,"E62");var subQ4131=sQuery(id+"F0.wireOp",EDGE,"E61");var subQ4132=sQuery(id+"F0.wireOp",EDGE,"E60");var subQ4133=sQuery(id+"F0.wireOp",EDGE,"E59");var subQ4134=sQuery(id+"F0.wireOp",EDGE,"E58");var subQ4135=sQuery(id+"F0.wireOp",EDGE,"E57");var subQ4136=sQuery(id+"F0.wireOp",EDGE,"E56");var subQ4137=sQuery(id+"F0.wireOp",EDGE,"E55");var subQ4138=sQuery(id+"F0.wireOp",EDGE,"E54");var subQ4139=sQuery(id+"F0.wireOp",EDGE,"E53");var subQ4140=sQuery(id+"F0.wireOp",EDGE,"E52");var subQ4141=sQuery(id+"F0.wireOp",EDGE,"E51");var subQ4142=sQuery(id+"F0.wireOp",EDGE,"E50");var subQ4143=sQuery(id+"F0.wireOp",EDGE,"E49");var subQ4144=sQuery(id+"F0.wireOp",EDGE,"E48");var subQ4145=sQuery(id+"F0.wireOp",EDGE,"E47");var subQ4146=sQuery(id+"F0.wireOp",EDGE,"E46");var subQ4147=sQuery(id+"F0.wireOp",EDGE,"E45");var subQ4148=sQuery(id+"F0.wireOp",EDGE,"E44");var subQ4149=sQuery(id+"F0.wireOp",EDGE,"E43");var subQ4150=sQuery(id+"F0.wireOp",EDGE,"E42");var subQ4151=sQuery(id+"F0.wireOp",EDGE,"E41");var subQ4152=sQuery(id+"F0.wireOp",EDGE,"E40");var subQ4153=sQuery(id+"F0.wireOp",EDGE,"E39");var subQ4154=sQuery(id+"F0.wireOp",EDGE,"E38");var subQ4155=sQuery(id+"F0.wireOp",EDGE,"E37");var subQ4156=sQuery(id+"F0.wireOp",EDGE,"E36");var subQ4157=sQuery(id+"F0.wireOp",EDGE,"E35");var subQ4158=sQuery(id+"F0.wireOp",EDGE,"E34");var subQ4159=sQuery(id+"F0.wireOp",EDGE,"E33");var subQ4160=sQuery(id+"F0.wireOp",EDGE,"E32");var subQ4161=sQuery(id+"F0.wireOp",EDGE,"E31");var subQ4162=sQuery(id+"F0.wireOp",EDGE,"E30");var subQ4163=sQuery(id+"F0.wireOp",EDGE,"E29");var subQ4164=sQuery(id+"F0.wireOp",EDGE,"E28");var subQ4165=sQuery(id+"F0.wireOp",EDGE,"E27");var subQ4166=sQuery(id+"F0.wireOp",EDGE,"E26");var subQ4167=sQuery(id+"F0.wireOp",EDGE,"E25");var subQ4168=sQuery(id+"F0.wireOp",EDGE,"E24");var subQ4169=sQuery(id+"F0.wireOp",EDGE,"E23");var subQ4170=sQuery(id+"F0.wireOp",EDGE,"E22");var subQ4171=sQuery(id+"F0.wireOp",EDGE,"E21");var subQ4172=sQuery(id+"F0.wireOp",EDGE,"E20");var subQ4173=sQuery(id+"F0.wireOp",EDGE,"E19");var subQ4174=sQuery(id+"F0.wireOp",EDGE,"E18");var subQ4175=sQuery(id+"F0.wireOp",EDGE,"E17");var subQ4176=sQuery(id+"F0.wireOp",EDGE,"E16");var subQ4177=sQuery(id+"F0.wireOp",EDGE,"E15");var subQ4178=sQuery(id+"F0.wireOp",EDGE,"E14");var subQ4179=sQuery(id+"F0.wireOp",EDGE,"E13");var subQ4180=sQuery(id+"F0.wireOp",EDGE,"E12");var subQ4181=sQuery(id+"F0.wireOp",EDGE,"E11");var subQ4182=sQuery(id+"F0.wireOp",EDGE,"E10");var subQ4183=sQuery(id+"F0.wireOp",EDGE,"E9");var subQ4184=sQuery(id+"F0.wireOp",EDGE,"E8");var subQ4185=sQuery(id+"F0.wireOp",EDGE,"E7");var subQ4186=sQuery(id+"F0.wireOp",EDGE,"E6");var subQ4187=sQuery(id+"F0.wireOp",EDGE,"E5");var subQ4188=sQuery(id+"F0.wireOp",EDGE,"E4");var subQ4189=sQuery(id+"F0.wireOp",EDGE,"E3");var subQ4190=sQuery(id+"F0.wireOp",EDGE,"E2");var subQ4191=sQuery(id+"F0.wireOp",EDGE,"E1");var subQ4192=sQuery(id+"F0.wireOp",EDGE,"E0");Q1=makeQuery(id+"F3.boolean.opBoolean","MERGE",FACE,{"derivedFrom":[makeQuery(id+"F1.opExtrude","CAP_FACE",FACE,{"disambiguationData":[OSD([subQ4192,subQ4191,subQ4190,subQ4189,subQ4188,subQ4187,subQ4186,subQ4185,subQ4184,subQ4183,subQ4182,subQ4181,subQ4180,subQ4179,subQ4178,subQ4177,subQ4176,subQ4175,subQ4174,subQ4173,subQ4172,subQ4171,subQ4170,subQ4169,subQ4168,subQ4167,subQ4166,subQ4165,subQ4164,subQ4163,subQ4162,subQ4161,subQ4160,subQ4159,subQ4158,subQ4157,subQ4156,subQ4155,subQ4154,subQ4153,subQ4152,subQ4151,subQ4150,subQ4149,subQ4148,subQ4147,subQ4146,subQ4145,subQ4144,subQ4143,subQ4142,subQ4141,subQ4140,subQ4139,subQ4138,subQ4137,subQ4136,subQ4135,subQ4134,subQ4133,subQ4132,subQ4131,subQ4130,subQ4129,subQ4128,subQ4127,subQ4126,subQ4125,subQ4124,subQ4123,subQ4122,subQ4121,subQ4120,subQ4119,subQ4118,subQ4117,subQ4116,subQ4115,subQ4114,subQ4113,subQ4112,subQ4111,subQ4110,subQ4109,subQ4108,subQ4107,subQ4106,subQ4105,subQ4104,subQ4103,subQ4102,subQ4101,subQ4100,subQ4099,subQ4098,subQ4097,subQ4096,subQ4095,subQ4094,subQ4093,subQ4092,subQ4091,subQ4090,subQ4089,subQ4088,subQ4087,subQ4086,subQ4085,subQ4084,subQ4083,subQ4082,subQ4081,subQ4080,subQ4079,subQ4078,subQ4077,subQ4076,subQ4075,subQ4074,subQ4073,subQ4072,subQ4071,subQ4070,subQ4069,subQ4068,subQ4067,subQ4066,subQ4065,subQ4064,subQ4063,subQ4062,subQ4061,subQ4060,subQ4059,subQ4058,subQ4057,subQ4056,subQ4055,subQ4054,subQ4053,subQ4052,subQ4051,subQ4050,subQ4049,subQ4048,subQ4047,subQ4046,subQ4045,subQ4044,subQ4043,subQ4042,subQ4041,subQ4040,subQ4039,subQ4038,subQ4037,subQ4036,subQ4035,subQ4034,subQ4033,subQ4032,subQ4031,subQ4030,subQ4029,subQ4028,subQ4027,subQ4026,subQ4025,subQ4024,subQ4023,subQ4022,subQ4021,subQ4020,subQ4019,subQ4018,subQ4017,subQ4016,subQ4015,subQ4014,subQ4013,subQ4012,subQ4011,subQ4010,subQ4009,subQ4008,subQ4007,subQ4006,subQ4005,subQ4004,subQ4003,subQ4002,subQ4001,subQ4000,subQ3999,subQ3998,subQ3997,subQ3996,subQ3995,subQ3994,subQ3993,subQ3992,subQ3991,subQ3990,subQ3989,subQ3988,subQ3987,subQ3986,subQ3985,subQ3984,subQ3983,subQ3982,subQ3981,subQ3980,subQ3979,subQ3978,subQ3977,subQ3976,subQ3975,subQ3974,subQ3973,subQ3972,subQ3971,subQ3970,subQ3969,subQ3968,subQ3967,subQ3966,subQ3965,subQ3964,subQ3963,subQ3962,subQ3961,subQ3960,subQ3959,subQ3958,subQ3957,subQ3956,subQ3955,subQ3954,subQ3953,subQ3952,subQ3951,subQ3950,subQ3949,subQ3948,subQ3947,subQ3946,subQ3945,subQ3944,subQ3943,subQ3942,subQ3941,subQ3940,subQ3939,subQ3938,subQ3937,subQ3936,subQ3935,subQ3934,subQ3933,subQ3932,subQ3931,subQ3930,subQ3929,subQ3928,subQ3927,subQ3926,subQ3925,subQ3924,subQ3923,subQ3922,subQ3921,subQ3920,subQ3919,subQ3918,subQ3917,subQ3916,subQ3915,subQ3914,subQ3913,subQ3912,subQ3911,subQ3910,subQ3909,subQ3908,subQ3907,subQ3906,subQ3905,subQ3904,subQ3903,subQ3902,subQ3901,subQ3900,subQ3899,subQ3898,subQ3897,subQ3896,subQ3895,subQ3894,subQ3893,subQ3892,subQ3891,subQ3890,subQ3889,subQ3888,subQ3887,subQ3886,subQ3885,subQ3884,subQ3883,subQ3882,subQ3881,subQ3880,subQ3879,subQ3878,subQ3877,subQ3876,subQ3875,subQ3874,subQ3873,subQ3872,subQ3871,subQ3870,subQ3869,subQ3868,subQ3867,subQ3866,subQ3865,subQ3864,subQ3863,subQ3862,subQ3861,subQ3860,subQ3859,subQ3858,subQ3857,subQ3856,subQ3855,subQ3854,subQ3853,subQ3852,subQ3851,subQ3850,subQ3849,subQ3848,subQ3847,subQ3846,subQ3845,subQ3844,subQ3843,subQ3842,subQ3841,subQ3840,subQ3839,subQ3838,subQ3837,subQ3836,subQ3835,subQ3834,subQ3833,subQ3832,subQ3831,subQ3830,subQ3829,subQ3828,subQ3827,subQ3826,subQ3825,subQ3824,subQ3823,subQ3822,subQ3821,subQ3820,subQ3819,subQ3818,subQ3817,subQ3816,subQ3815,subQ3814,subQ3813,subQ3812,subQ3811,subQ3810,subQ3809,subQ3808,subQ3807,subQ3806,subQ3805,subQ3804,subQ3803,subQ3802,subQ3801,subQ3800,subQ3799,subQ3798,subQ3797,subQ3796,subQ3795,subQ3794,subQ3793,subQ3792,subQ3791,subQ3790,subQ3789,subQ3788,subQ3787,subQ3786,subQ3785,subQ3784,subQ3783,subQ3782,subQ3781,subQ3780,subQ3779,subQ3778,subQ3777,subQ3776,subQ3775,subQ3774,subQ3773,subQ3772,subQ3771,subQ3770,subQ3769,subQ3768,subQ3767,subQ3766,subQ3765,subQ3764,subQ3763,subQ3762,subQ3761,subQ3760,subQ3759,subQ3758,subQ3757,subQ3756,subQ3755,subQ3754,subQ3753,subQ3752,subQ3751,subQ3750,subQ3749,subQ3748,subQ3747,subQ3746,subQ3745,subQ3744,subQ3743,subQ3742,subQ3741,subQ3740,subQ3739,subQ3738,subQ3737,subQ3736,subQ3735,subQ3734,subQ3733,subQ3732,subQ3731,subQ3730,subQ3729,subQ3728,subQ3727,subQ3726,subQ3725,subQ3724,subQ3723,subQ3722,subQ3721,subQ3720,subQ3719,subQ3718,subQ3717,subQ3716,subQ3715,subQ3714,subQ3713,subQ3712,subQ3711,subQ3710,subQ3709,subQ3708,subQ3707,subQ3706,subQ3705,subQ3704,subQ3703,subQ3702,subQ3701,subQ3700,subQ3699,subQ3698,subQ3697,subQ3696,subQ3695,subQ3694,subQ3693,subQ3692,subQ3691,subQ3690,subQ3689,subQ3688,subQ3687,subQ3686,subQ3685,subQ3684,subQ3683,subQ3682,subQ3681,subQ3680,subQ3679,subQ3678,subQ3677,subQ3676,subQ3675,subQ3674,subQ3673,subQ3672,subQ3671,subQ3670,subQ3669,subQ3668,subQ3667,subQ3666,subQ3665,subQ3664,subQ3663,subQ3662,subQ3661,subQ3660,subQ3659,subQ3658,subQ3657,subQ3656,subQ3655,subQ3654,subQ3653,subQ3652,subQ3651,subQ3650,subQ3649,subQ3648,subQ3647,subQ3646,subQ3645,subQ3644,subQ3643,subQ3642,subQ3641,subQ3640,subQ3639,subQ3638,subQ3637,subQ3636,subQ3635,subQ3634,subQ3633,subQ3632,subQ3631,subQ3630,subQ3629,subQ3628,subQ3627,subQ3626,subQ3625,subQ3624,subQ3623,subQ3622,subQ3621,subQ3620,subQ3619,subQ3618,subQ3617,subQ3616,subQ3615,subQ3614,subQ3613,subQ3612,subQ3611,subQ3610,subQ3609,subQ3608,subQ3607,subQ3606,subQ3605,subQ3604,subQ3603,subQ3602,subQ3601,subQ3600,subQ3599,subQ3598,subQ3597,subQ3596,subQ3595,subQ3594,subQ3593,subQ3592,subQ3591,subQ3590,subQ3589,subQ3588,subQ3587,subQ3586,subQ3585,subQ3584,subQ3583,subQ3582,subQ3581,subQ3580,subQ3579,subQ3578,subQ3577,subQ3576,subQ3575,subQ3574,subQ3573,subQ3572,subQ3571,subQ3570,subQ3569,subQ3568,subQ3567,subQ3566,subQ3565,subQ3564,subQ3563,subQ3562,subQ3561,subQ3560,subQ3559,subQ3558,subQ3557,subQ3556,subQ3555,subQ3554,subQ3553,subQ3552,subQ3551,subQ3550,subQ3549,subQ3548,subQ3547,subQ3546,subQ3545,subQ3544,subQ3543,subQ3542,subQ3541,subQ3540,subQ3539,subQ3538,subQ3537,subQ3536,subQ3535,subQ3534,subQ3533,subQ3532,subQ3531,subQ3530,subQ3529,subQ3528,subQ3527,subQ3526,subQ3525,subQ3524,subQ3523,subQ3522,subQ3521,subQ3520,subQ3519,subQ3518,subQ3517,subQ3516,subQ3515,subQ3514,subQ3513,subQ3512,subQ3511,subQ3510,subQ3509,subQ3508,subQ3507,subQ3506,subQ3505,subQ3504,subQ3503,subQ3502,subQ3501,subQ3500,subQ3499,subQ3498,subQ3497,subQ3496,subQ3495,subQ3494,subQ3493,subQ3492,subQ3491,subQ3490,subQ3489,subQ3488,subQ3487,subQ3486,subQ3485,subQ3484,subQ3483,subQ3482,subQ3481,subQ3480,subQ3479,subQ3478,subQ3477,subQ3476,subQ3475,subQ3474,subQ3473,subQ3472,subQ3471,subQ3470,subQ3469,subQ3468,subQ3467,subQ3466,subQ3465,subQ3464,subQ3463,subQ3462,subQ3461,subQ3460,subQ3459,subQ3458,subQ3457,subQ3456,subQ3455,subQ3454,subQ3453,subQ3452,subQ3451,subQ3450,subQ3449,subQ3448,subQ3447,subQ3446,subQ3445,subQ3444,subQ3443,subQ3442,subQ3441,subQ3440,subQ3439,subQ3438,subQ3437,subQ3436,subQ3435,subQ3434,subQ3433,subQ3432,subQ3431,subQ3430,subQ3429,subQ3428,subQ3427,subQ3426,subQ3425,subQ3424,subQ3423,subQ3422,subQ3421,subQ3420,subQ3419,subQ3418,subQ3417,subQ3416,subQ3415,subQ3414,subQ3413,subQ3412,subQ3411,subQ3410,subQ3409,subQ3408,subQ3407,subQ3406,subQ3405,subQ3404,subQ3403,subQ3402,subQ3401,subQ3400,subQ3399,subQ3398,subQ3397,subQ3396,subQ3395,subQ3394,subQ3393,subQ3392,subQ3391,subQ3390,subQ3389,subQ3388,subQ3387,subQ3386,subQ3385,subQ3384,subQ3383,subQ3382,subQ3381,subQ3380,subQ3379,subQ3378,subQ3377,subQ3376,subQ3375,subQ3374,subQ3373,subQ3372,subQ3371,subQ3370,subQ3369,subQ3368,subQ3367,subQ3366,subQ3365,subQ3364,subQ3363,subQ3362,subQ3361,subQ3360,subQ3359,subQ3358,subQ3357,subQ3356,subQ3355,subQ3354,subQ3353,subQ3352,subQ3351,subQ3350,subQ3349,subQ3348,subQ3347,subQ3346,subQ3345,subQ3344,subQ3343,subQ3342,subQ3341,subQ3340,subQ3339,subQ3338,subQ3337,subQ3336,subQ3335,subQ3334,subQ3333,subQ3332,subQ3331,subQ3330,subQ3329,subQ3328,subQ3327,subQ3326,subQ3325,subQ3324,subQ3323,subQ3322,subQ3321,subQ3320,subQ3319,subQ3318,subQ3317,subQ3316,subQ3315,subQ3314,subQ3313,subQ3312,subQ3311,subQ3310,subQ3309,subQ3308,subQ3307,subQ3306,subQ3305,subQ3304,subQ3303,subQ3302,subQ3301,subQ3300,subQ3299,subQ3298,subQ3297,subQ3296,subQ3295,subQ3294,subQ3293,subQ3292,subQ3291,subQ3290,subQ3289,subQ3288,subQ3287,subQ3286,subQ3285,subQ3284,subQ3283,subQ3282,subQ3281,subQ3280,subQ3279,subQ3278,subQ3277,subQ3276,subQ3275,subQ3274,subQ3273,subQ3272,subQ3271,subQ3270,subQ3269,subQ3268,subQ3267,subQ3266,subQ3265,subQ3264,subQ3263,subQ3262,subQ3261,subQ3260,subQ3259,subQ3258,subQ3257,subQ3256,subQ3255,subQ3254,subQ3253,subQ3252,subQ3251,subQ3250,subQ3249,subQ3248,subQ3247,subQ3246,subQ3245,subQ3244,subQ3243,subQ3242,subQ3241,subQ3240,subQ3239,subQ3238,subQ3237,subQ3236,subQ3235,subQ3234,subQ3233,subQ3232,subQ3231,subQ3230,subQ3229,subQ3228,subQ3227,subQ3226,subQ3225,subQ3224,subQ3223,subQ3222,subQ3221,subQ3220,subQ3219,subQ3218,subQ3217,subQ3216,subQ3215,subQ3214,subQ3213,subQ3212,subQ3211,subQ3210,subQ3209,subQ3208,subQ3207,subQ3206,subQ3205,subQ3204,subQ3203,subQ3202,subQ3201,subQ3200,subQ3199,subQ3198,subQ3197,subQ3196,subQ3195,subQ3194,subQ3193,subQ3192,subQ3191,subQ3190,subQ3189,subQ3188,subQ3187,subQ3186,subQ3185,subQ3184,subQ3183,subQ3182,subQ3181,subQ3180,subQ3179,subQ3178,subQ3177,subQ3176,subQ3175,subQ3174,subQ3173,subQ3172,subQ3171,subQ3170,subQ3169,subQ3168,subQ3167,subQ3166,subQ3165,subQ3164,subQ3163,subQ3162,subQ3161,subQ3160,subQ3159,subQ3158,subQ3157,subQ3156,subQ3155,subQ3154,subQ3153,subQ3152,subQ3151,subQ3150,subQ3149,subQ3148,subQ3147,subQ3146,subQ3145,subQ3144,subQ3143,subQ3142,subQ3141,subQ3140,subQ3139,subQ3138,subQ3137,subQ3136,subQ3135,subQ3134,subQ3133,subQ3132,subQ3131,subQ3130,subQ3129,subQ3128,subQ3127,subQ3126,subQ3125,subQ3124,subQ3123,subQ3122,subQ3121,subQ3120,subQ3119,subQ3118,subQ3117,subQ3116,subQ3115,subQ3114,subQ3113,subQ3112,subQ3111,subQ3110,subQ3109,subQ3108,subQ3107,subQ3106,subQ3105,subQ3104,subQ3103,subQ3102,subQ3101,subQ3100,subQ3099,subQ3098,subQ3097,subQ3096,subQ3095,subQ3094,subQ3093,subQ3092,subQ3091,subQ3090,subQ3089,subQ3088,subQ3087,subQ3086,subQ3085,subQ3084,subQ3083,subQ3082,subQ3081,subQ3080,subQ3079,subQ3078,subQ3077,subQ3076,subQ3075,subQ3074,subQ3073,subQ3072,subQ3071,subQ3070,subQ3069,subQ3068,subQ3067,subQ3066,subQ3065,subQ3064,subQ3063,subQ3062,subQ3061,subQ3060,subQ3059,subQ3058,subQ3057,subQ3056,subQ3055,subQ3054,subQ3053,subQ3052,subQ3051,subQ3050,subQ3049,subQ3048,subQ3047,subQ3046,subQ3045,subQ3044,subQ3043,subQ3042,subQ3041,subQ3040,subQ3039,subQ3038,subQ3037,subQ3036,subQ3035,subQ3034,subQ3033,subQ3032,subQ3031,subQ3030,subQ3029,subQ3028,subQ3027,subQ3026,subQ3025,subQ3024,subQ3023,subQ3022,subQ3021,subQ3020,subQ3019,subQ3018,subQ3017,subQ3016,subQ3015,subQ3014,subQ3013,subQ3012,subQ3011,subQ3010,subQ3009,subQ3008,subQ3007,subQ3006,subQ3005,subQ3004,subQ3003,subQ3002,subQ3001,subQ3000,subQ2999,subQ2998,subQ2997,subQ2996,subQ2995,subQ2994,subQ2993,subQ2992,subQ2991,subQ2990,subQ2989,subQ2988,subQ2987,subQ2986,subQ2985,subQ2984,subQ2983,subQ2982,subQ2981,subQ2980,subQ2979,subQ2978,subQ2977,subQ2976,subQ2975,subQ2974,subQ2973,subQ2972,subQ2971,subQ2970,subQ2969,subQ2968,subQ2967,subQ2966,subQ2965,subQ2964,subQ2963,subQ2962,subQ2961,subQ2960,subQ2959,subQ2958,subQ2957,subQ2956,subQ2955,subQ2954,subQ2953,subQ2952,subQ2951,subQ2950,subQ2949,subQ2948,subQ2947,subQ2946,subQ2945,subQ2944,subQ2943,subQ2942,subQ2941,subQ2940,subQ2939,subQ2938,subQ2937,subQ2936,subQ2935,subQ2934,subQ2933,subQ2932,subQ2931,subQ2930,subQ2929,subQ2928,subQ2927,subQ2926,subQ2925,subQ2924,subQ2923,subQ2922,subQ2921,subQ2920,subQ2919,subQ2918,subQ2917,subQ2916,subQ2915,subQ2914,subQ2913,subQ2912,subQ2911,subQ2910,subQ2909,subQ2908,subQ2907,subQ2906,subQ2905,subQ2904,subQ2903,subQ2902,subQ2901,subQ2900,subQ2899,subQ2898,subQ2897,subQ2896,subQ2895,subQ2894,subQ2893,subQ2892,subQ2891,subQ2890,subQ2889,subQ2888,subQ2887,subQ2886,subQ2885,subQ2884,subQ2883,subQ2882,subQ2881,subQ2880,subQ2879,subQ2878,subQ2877,subQ2876,subQ2875,subQ2874,subQ2873,subQ2872,subQ2871,subQ2870,subQ2869,subQ2868,subQ2867,subQ2866,subQ2865,subQ2864,subQ2863,subQ2862,subQ2861,subQ2860,subQ2859,subQ2858,subQ2857,subQ2856,subQ2855,subQ2854,subQ2853,subQ2852,subQ2851,subQ2850,subQ2849,subQ2848,subQ2847,subQ2846,subQ2845,subQ2844,subQ2843,subQ2842,subQ2841,subQ2840,subQ2839,subQ2838,subQ2837,subQ2836,subQ2835,subQ2834,subQ2833,subQ2832,subQ2831,subQ2830,subQ2829,subQ2828,subQ2827,subQ2826,subQ2825,subQ2824,subQ2823,subQ2822,subQ2821,subQ2820,subQ2819,subQ2818,subQ2817,subQ2816,subQ2815,subQ2814,subQ2813,subQ2812,subQ2811,subQ2810,subQ2809,subQ2808,subQ2807,subQ2806,subQ2805,subQ2804,subQ2803,subQ2802,subQ2801,subQ2800,subQ2799,subQ2798,subQ2797,subQ2796,subQ2795,subQ2794,subQ2793,subQ2792,subQ2791,subQ2790,subQ2789,subQ2788,subQ2787,subQ2786,subQ2785,subQ2784,subQ2783,subQ2782,subQ2781,subQ2780,subQ2779,subQ2778,subQ2777,subQ2776,subQ2775,subQ2774,subQ2773,subQ2772,subQ2771,subQ2770,subQ2769,subQ2768,subQ2767,subQ2766,subQ2765,subQ2764,subQ2763,subQ2762,subQ2761,subQ2760,subQ2759,subQ2758,subQ2757,subQ2756,subQ2755,subQ2754,subQ2753,subQ2752,subQ2751,subQ2750,subQ2749,subQ2748,subQ2747,subQ2746,subQ2745,subQ2744,subQ2743,subQ2742,subQ2741,subQ2740,subQ2739,subQ2738,subQ2737,subQ2736,subQ2735,subQ2734,subQ2733,subQ2732,subQ2731,subQ2730,subQ2729,subQ2728,subQ2727,subQ2726,subQ2725,subQ2724,subQ2723,subQ2722,subQ2721,subQ2720,subQ2719,subQ2718,subQ2717,subQ2716,subQ2715,subQ2714,subQ2713,subQ2712,subQ2711,subQ2710,subQ2709,subQ2708,subQ2707,subQ2706,subQ2705,subQ2704,subQ2703,subQ2702,subQ2701,subQ2700,subQ2699,subQ2698,subQ2697,subQ2696,subQ2695,subQ2694,subQ2693,subQ2692,subQ2691,subQ2690,subQ2689,subQ2688,subQ2687,subQ2686,subQ2685,subQ2684,subQ2683,subQ2682,subQ2681,subQ2680,subQ2679,subQ2678,subQ2677,subQ2676,subQ2675,subQ2674,subQ2673,subQ2672,subQ2671,subQ2670,subQ2669,subQ2668,subQ2667,subQ2666,subQ2665,subQ2664,subQ2663,subQ2662,subQ2661,subQ2660,subQ2659,subQ2658,subQ2657,subQ2656,subQ2655,subQ2654,subQ2653,subQ2652,subQ2651,subQ2650,subQ2649,subQ2648,subQ2647,subQ2646,subQ2645,subQ2644,subQ2643,subQ2642,subQ2641,subQ2640,subQ2639,subQ2638,subQ2637,subQ2636,subQ2635,subQ2634,subQ2633,subQ2632,subQ2631,subQ2630,subQ2629,subQ2628,subQ2627,subQ2626,subQ2625,subQ2624,subQ2623,subQ2622,subQ2621,subQ2620,subQ2619,subQ2618,subQ2617,subQ2616,subQ2615,subQ2614,subQ2613,subQ2612,subQ2611,subQ2610,subQ2609,subQ2608,subQ2607,subQ2606,subQ2605,subQ2604,subQ2603,subQ2602,subQ2601,subQ2600,subQ2599,subQ2598,subQ2597,subQ2596,subQ2595,subQ2594,subQ2593,subQ2592,subQ2591,subQ2590,subQ2589,subQ2588,subQ2587,subQ2586,subQ2585,subQ2584,subQ2583,subQ2582,subQ2581,subQ2580,subQ2579,subQ2578,subQ2577,subQ2576,subQ2575,subQ2574,subQ2573,subQ2572,subQ2571,subQ2570,subQ2569,subQ2568,subQ2567,subQ2566,subQ2565,subQ2564,subQ2563,subQ2562,subQ2561,subQ2560,subQ2559,subQ2558,subQ2557,subQ2556,subQ2555,subQ2554,subQ2553,subQ2552,subQ2551,subQ2550,subQ2549,subQ2548,subQ2547,subQ2546,subQ2545,subQ2544,subQ2543,subQ2542,subQ2541,subQ2540,subQ2539,subQ2538,subQ2537,subQ2536,subQ2535,subQ2534,subQ2533,subQ2532,subQ2531,subQ2530,subQ2529,subQ2528,subQ2527,subQ2526,subQ2525,subQ2524,subQ2523,subQ2522,subQ2521,subQ2520,subQ2519,subQ2518,subQ2517,subQ2516,subQ2515,subQ2514,subQ2513,subQ2512,subQ2511,subQ2510,subQ2509,subQ2508,subQ2507,subQ2506,subQ2505,subQ2504,subQ2503,subQ2502,subQ2501,subQ2500,subQ2499,subQ2498,subQ2497,subQ2496,subQ2495,subQ2494,subQ2493,subQ2492,subQ2491,subQ2490,subQ2489,subQ2488,subQ2487,subQ2486,subQ2485,subQ2484,subQ2483,subQ2482,subQ2481,subQ2480,subQ2479,subQ2478,subQ2477,subQ2476,subQ2475,subQ2474,subQ2473,subQ2472,subQ2471,subQ2470,subQ2469,subQ2468,subQ2467,subQ2466,subQ2465,subQ2464,subQ2463,subQ2462,subQ2461,subQ2460,subQ2459,subQ2458,subQ2457,subQ2456,subQ2455,subQ2454,subQ2453,subQ2452,subQ2451,subQ2450,subQ2449,subQ2448,subQ2447,subQ2446,subQ2445,subQ2444,subQ2443,subQ2442,subQ2441,subQ2440,subQ2439,subQ2438,subQ2437,subQ2436,subQ2435,subQ2434,subQ2433,subQ2432,subQ2431,subQ2430,subQ2429,subQ2428,subQ2427,subQ2426,subQ2425,subQ2424,subQ2423,subQ2422,subQ2421,subQ2420,subQ2419,subQ2418,subQ2417,subQ2416,subQ2415,subQ2414,subQ2413,subQ2412,subQ2411,subQ2410,subQ2409,subQ2408,subQ2407,subQ2406,subQ2405,subQ2404,subQ2403,subQ2402,subQ2401,subQ2400,subQ2399,subQ2398,subQ2397,subQ2396,subQ2395,subQ2394,subQ2393,subQ2392,subQ2391,subQ2390,subQ2389,subQ2388,subQ2387,subQ2386,subQ2385,subQ2384,subQ2383,subQ2382,subQ2381,subQ2380,subQ2379,subQ2378,subQ2377,subQ2376,subQ2375,subQ2374,subQ2373,subQ2372,subQ2371,subQ2370,subQ2369,subQ2368,subQ2367,subQ2366,subQ2365,subQ2364,subQ2363,subQ2362,subQ2361,subQ2360,subQ2359,subQ2358,subQ2357,subQ2356,subQ2355,subQ2354,subQ2353,subQ2352,subQ2351,subQ2350,subQ2349,subQ2348,subQ2347,subQ2346,subQ2345,subQ2344,subQ2343,subQ2342,subQ2341,subQ2340,subQ2339,subQ2338,subQ2337,subQ2336,subQ2335,subQ2334,subQ2333,subQ2332,subQ2331,subQ2330,subQ2329,subQ2328,subQ2327,subQ2326,subQ2325,subQ2324,subQ2323,subQ2322,subQ2321,subQ2320,subQ2319,subQ2318,subQ2317,subQ2316,subQ2315,subQ2314,subQ2313,subQ2312,subQ2311,subQ2310,subQ2309,subQ2308,subQ2307,subQ2306,subQ2305,subQ2304,subQ2303,subQ2302,subQ2301,subQ2300,subQ2299,subQ2298,subQ2297,subQ2296,subQ2295,subQ2294,subQ2293,subQ2292,subQ2291,subQ2290,subQ2289,subQ2288,subQ2287,subQ2286,subQ2285,subQ2284,subQ2283,subQ2282,subQ2281,subQ2280,subQ2279,subQ2278,subQ2277,subQ2276,subQ2275,subQ2274,subQ2273,subQ2272,subQ2271,subQ2270,subQ2269,subQ2268,subQ2267,subQ2266,subQ2265,subQ2264,subQ2263,subQ2262,subQ2261,subQ2260,subQ2259,subQ2258,subQ2257,subQ2256,subQ2255,subQ2254,subQ2253,subQ2252,subQ2251,subQ2250,subQ2249,subQ2248,subQ2247,subQ2246,subQ2245,subQ2244,subQ2243,subQ2242,subQ2241,subQ2240,subQ2239,subQ2238,subQ2237,subQ2236,subQ2235,subQ2234,subQ2233,subQ2232,subQ2231,subQ2230,subQ2229,subQ2228,subQ2227,subQ2226,subQ2225,subQ2224,subQ2223,subQ2222,subQ2221,subQ2220,subQ2219,subQ2218,subQ2217,subQ2216,subQ2215,subQ2214,subQ2213,subQ2212,subQ2211,subQ2210,subQ2209,subQ2208,subQ2207,subQ2206,subQ2205,subQ2204,subQ2203,subQ2202,subQ2201,subQ2200,subQ2199,subQ2198,subQ2197,subQ2196,subQ2195,subQ2194,subQ2193,subQ2192,subQ2191,subQ2190,subQ2189,subQ2188,subQ2187,subQ2186,subQ2185,subQ2184,subQ2183,subQ2182,subQ2181,subQ2180,subQ2179,subQ2178,subQ2177,subQ2176,subQ2175,subQ2174,subQ2173,subQ2172,subQ2171,subQ2170,subQ2169,subQ2168,subQ2167,subQ2166,subQ2165,subQ2164,subQ2163,subQ2162,subQ2161,subQ2160,subQ2159,subQ2158,subQ2157,subQ2156,subQ2155,subQ2154,subQ2153,subQ2152,subQ2151,subQ2150,subQ2149,subQ2148,subQ2147,subQ2146,subQ2145,subQ2144,subQ2143,subQ2142,subQ2141,subQ2140,subQ2139,subQ2138,subQ2137,subQ2136,subQ2135,subQ2134,subQ2133,subQ2132,subQ2131,subQ2130,subQ2129,subQ2128,subQ2127,subQ2126,subQ2125,subQ2124,subQ2123,subQ2122,subQ2121,subQ2120,subQ2119,subQ2118,subQ2117,subQ2116,subQ2115,subQ2114,subQ2113,subQ2112,subQ2111,subQ2110,subQ2109,subQ2108,subQ2107,subQ2106,subQ2105,subQ2104,subQ2103,subQ2102,subQ2101,subQ2100,subQ2099,subQ2098,subQ2097,subQ2096,subQ2095,subQ2094,subQ2093,subQ2092,subQ2091,subQ2090,subQ2089,subQ2088,subQ2087,subQ2086,subQ2085,subQ2084,subQ2083,subQ2082,subQ2081,subQ2080,subQ2079,subQ2078,subQ2077,subQ2076,subQ2075,subQ2074,subQ2073,subQ2072,subQ2071,subQ2070,subQ2069,subQ2068,subQ2067,subQ2066,subQ2065,subQ2064,subQ2063,subQ2062,subQ2061,subQ2060,subQ2059,subQ2058,subQ2057,subQ2056,subQ2055,subQ2054,subQ2053,subQ2052,subQ2051,subQ2050,subQ2049,subQ2048,subQ2047,subQ2046,subQ2045,subQ2044,subQ2043,subQ2042,subQ2041,subQ2040,subQ2039,subQ2038,subQ2037,subQ2036,subQ2035,subQ2034,subQ2033,subQ2032,subQ2031,subQ2030,subQ2029,subQ2028,subQ2027,subQ2026,subQ2025,subQ2024,subQ2023,subQ2022,subQ2021,subQ2020,subQ2019,subQ2018,subQ2017,subQ2016,subQ2015,subQ2014,subQ2013,subQ2012,subQ2011,subQ2010,subQ2009,subQ2008,subQ2007,subQ2006,subQ2005,subQ2004,subQ2003,subQ2002,subQ2001,subQ2000,subQ1999,subQ1998,subQ1997,subQ1996,subQ1995,subQ1994,subQ1993,subQ1992,subQ1991,subQ1990,subQ1989,subQ1988,subQ1987,subQ1986,subQ1985,subQ1984,subQ1983,subQ1982,subQ1981,subQ1980,subQ1979,subQ1978,subQ1977,subQ1976,subQ1975,subQ1974,subQ1973,subQ1972,subQ1971,subQ1970,subQ1969,subQ1968,subQ1967,subQ1966,subQ1965,subQ1964,subQ1963,subQ1962,subQ1961,subQ1960,subQ1959,subQ1958,subQ1957,subQ1956,subQ1955,subQ1954,subQ1953,subQ1952,subQ1951,subQ1950,subQ1949,subQ1948,subQ1947,subQ1946,subQ1945,subQ1944,subQ1943,subQ1942,subQ1941,subQ1940,subQ1939,subQ1938,subQ1937,subQ1936,subQ1935,subQ1934,subQ1933,subQ1932,subQ1931,subQ1930,subQ1929,subQ1928,subQ1927,subQ1926,subQ1925,subQ1924,subQ1923,subQ1922,subQ1921,subQ1920,subQ1919,subQ1918,subQ1917,subQ1916,subQ1915,subQ1914,subQ1913,subQ1912,subQ1911,subQ1910,subQ1909,subQ1908,subQ1907,subQ1906,subQ1905,subQ1904,subQ1903,subQ1902,subQ1901,subQ1900,subQ1899,subQ1898,subQ1897,subQ1896,subQ1895,subQ1894,subQ1893,subQ1892,subQ1891,subQ1890,subQ1889,subQ1888,subQ1887,subQ1886,subQ1885,subQ1884,subQ1883,subQ1882,subQ1881,subQ1880,subQ1879,subQ1878,subQ1877,subQ1876,subQ1875,subQ1874,subQ1873,subQ1872,subQ1871,subQ1870,subQ1869,subQ1868,subQ1867,subQ1866,subQ1865,subQ1864,subQ1863,subQ1862,subQ1861,subQ1860,subQ1859,subQ1858,subQ1857,subQ1856,subQ1855,subQ1854,subQ1853,subQ1852,subQ1851,subQ1850,subQ1849,subQ1848,subQ1847,subQ1846,subQ1845,subQ1844,subQ1843,subQ1842,subQ1841,subQ1840,subQ1839,subQ1838,subQ1837,subQ1836,subQ1835,subQ1834,subQ1833,subQ1832,subQ1831,subQ1830,subQ1829,subQ1828,subQ1827,subQ1826,subQ1825,subQ1824,subQ1823,subQ1822,subQ1821,subQ1820,subQ1819,subQ1818,subQ1817,subQ1816,subQ1815,subQ1814,subQ1813,subQ1812,subQ1811,subQ1810,subQ1809,subQ1808,subQ1807,subQ1806,subQ1805,subQ1804,subQ1803,subQ1802,subQ1801,subQ1800,subQ1799,subQ1798,subQ1797,subQ1796,subQ1795,subQ1794,subQ1793,subQ1792,subQ1791,subQ1790,subQ1789,subQ1788,subQ1787,subQ1786,subQ1785,subQ1784,subQ1783,subQ1782,subQ1781,subQ1780,subQ1779,subQ1778,subQ1777,subQ1776,subQ1775,subQ1774,subQ1773,subQ1772,subQ1771,subQ1770,subQ1769,subQ1768,subQ1767,subQ1766,subQ1765,subQ1764,subQ1763,subQ1762,subQ1761,subQ1760,subQ1759,subQ1758,subQ1757,subQ1756,subQ1755,subQ1754,subQ1753,subQ1752,subQ1751,subQ1750,subQ1749,subQ1748,subQ1747,subQ1746,subQ1745,subQ1744,subQ1743,subQ1742,subQ1741,subQ1740,subQ1739,subQ1738,subQ1737,subQ1736,subQ1735,subQ1734,subQ1733,subQ1732,subQ1731,subQ1730,subQ1729,subQ1728,subQ1727,subQ1726,subQ1725,subQ1724,subQ1723,subQ1722,subQ1721,subQ1720,subQ1719,subQ1718,subQ1717,subQ1716,subQ1715,subQ1714,subQ1713,subQ1712,subQ1711,subQ1710,subQ1709,subQ1708,subQ1707,subQ1706,subQ1705,subQ1704,subQ1703,subQ1702,subQ1701,subQ1700,subQ1699,subQ1698,subQ1697,subQ1696,subQ1695,subQ1694,subQ1693,subQ1692,subQ1691,subQ1690,subQ1689,subQ1688,subQ1687,subQ1686,subQ1685,subQ1684,subQ1683,subQ1682,subQ1681,subQ1680,subQ1679,subQ1678,subQ1677,subQ1676,subQ1675,subQ1674,subQ1673,subQ1672,subQ1671,subQ1670,subQ1669,subQ1668,subQ1667,subQ1666,subQ1665,subQ1664,subQ1663,subQ1662,subQ1661,subQ1660,subQ1659,subQ1658,subQ1657,subQ1656,subQ1655,subQ1654,subQ1653,subQ1652,subQ1651,subQ1650,subQ1649,subQ1648,subQ1647,subQ1646,subQ1645,subQ1644,subQ1643,subQ1642,subQ1641,subQ1640,subQ1639,subQ1638,subQ1637,subQ1636,subQ1635,subQ1634,subQ1633,subQ1632,subQ1631,subQ1630,subQ1629,subQ1628,subQ1627,subQ1626,subQ1625,subQ1624,subQ1623,subQ1622,subQ1621,subQ1620,subQ1619,subQ1618,subQ1617,subQ1616,subQ1615,subQ1614,subQ1613,subQ1612,subQ1611,subQ1610,subQ1609,subQ1608,subQ1607,subQ1606,subQ1605,subQ1604,subQ1603,subQ1602,subQ1601,subQ1600,subQ1599,subQ1598,subQ1597,subQ1596,subQ1595,subQ1594,subQ1593,subQ1592,subQ1591,subQ1590,subQ1589,subQ1588,subQ1587,subQ1586,subQ1585,subQ1584,subQ1583,subQ1582,subQ1581,subQ1580,subQ1579,subQ1578,subQ1577,subQ1576,subQ1575,subQ1574,subQ1573,subQ1572,subQ1571,subQ1570,subQ1569,subQ1568,subQ1567,subQ1566,subQ1565,subQ1564,subQ1563,subQ1562,subQ1561,subQ1560,subQ1559,subQ1558,subQ1557,subQ1556,subQ1555,subQ1554,subQ1553,subQ1552,subQ1551,subQ1550,subQ1549,subQ1548,subQ1547,subQ1546,subQ1545,subQ1544,subQ1543,subQ1542,subQ1541,subQ1540,subQ1539,subQ1538,subQ1537,subQ1536,subQ1535,subQ1534,subQ1533,subQ1532,subQ1531,subQ1530,subQ1529,subQ1528,subQ1527,subQ1526,subQ1525,subQ1524,subQ1523,subQ1522,subQ1521,subQ1520,subQ1519,subQ1518,subQ1517,subQ1516,subQ1515,subQ1514,subQ1513,subQ1512,subQ1511,subQ1510,subQ1509,subQ1508,subQ1507,subQ1506,subQ1505,subQ1504,subQ1503,subQ1502,subQ1501,subQ1500,subQ1499,subQ1498,subQ1497,subQ1496,subQ1495,subQ1494,subQ1493,subQ1492,subQ1491,subQ1490,subQ1489,subQ1488,subQ1487,subQ1486,subQ1485,subQ1484,subQ1483,subQ1482,subQ1481,subQ1480,subQ1479,subQ1478,subQ1477,subQ1476,subQ1475,subQ1474,subQ1473,subQ1472,subQ1471,subQ1470,subQ1469,subQ1468,subQ1467,subQ1466,subQ1465,subQ1464,subQ1463,subQ1462,subQ1461,subQ1460,subQ1459,subQ1458,subQ1457,subQ1456,subQ1455,subQ1454,subQ1453,subQ1452,subQ1451,subQ1450,subQ1449,subQ1448,subQ1447,subQ1446,subQ1445,subQ1444,subQ1443,subQ1442,subQ1441,subQ1440,subQ1439,subQ1438,subQ1437,subQ1436,subQ1435,subQ1434,subQ1433,subQ1432,subQ1431,subQ1430,subQ1429,subQ1428,subQ1427,subQ1426,subQ1425,subQ1424,subQ1423,subQ1422,subQ1421,subQ1420,subQ1419,subQ1418,subQ1417,subQ1416,subQ1415,subQ1414,subQ1413,subQ1412,subQ1411,subQ1410,subQ1409,subQ1408,subQ1407,subQ1406,subQ1405,subQ1404,subQ1403,subQ1402,subQ1401,subQ1400,subQ1399,subQ1398,subQ1397,subQ1396,subQ1395,subQ1394,subQ1393,subQ1392,subQ1391,subQ1390,subQ1389,subQ1388,subQ1387,subQ1386,subQ1385,subQ1384,subQ1383,subQ1382,subQ1381,subQ1380,subQ1379,subQ1378,subQ1377,subQ1376,subQ1375,subQ1374,subQ1373,subQ1372,subQ1371,subQ1370,subQ1369,subQ1368,subQ1367,subQ1366,subQ1365,subQ1364,subQ1363,subQ1362,subQ1361,subQ1360,subQ1359,subQ1358,subQ1357,subQ1356,subQ1355,subQ1354,subQ1353,subQ1352,subQ1351,subQ1350,subQ1349,subQ1348,subQ1347,subQ1346,subQ1345,subQ1344,subQ1343,subQ1342,subQ1341,subQ1340,subQ1339,subQ1338,subQ1337,subQ1336,subQ1335,subQ1334,subQ1333,subQ1332,subQ1331,subQ1330,subQ1329,subQ1328,subQ1327,subQ1326,subQ1325,subQ1324,subQ1323,subQ1322,subQ1321,subQ1320,subQ1319,subQ1318,subQ1317,subQ1316,subQ1315,subQ1314,subQ1313,subQ1312,subQ1311,subQ1310,subQ1309,subQ1308,subQ1307,subQ1306,subQ1305,subQ1304,subQ1303,subQ1302,subQ1301,subQ1300,subQ1299,subQ1298,subQ1297,subQ1296,subQ1295,subQ1294,subQ1293,subQ1292,subQ1291,subQ1290,subQ1289,subQ1288,subQ1287,subQ1286,subQ1285,subQ1284,subQ1283,subQ1282,subQ1281,subQ1280,subQ1279,subQ1278,subQ1277,subQ1276,subQ1275,subQ1274,subQ1273,subQ1272,subQ1271,subQ1270,subQ1269,subQ1268,subQ1267,subQ1266,subQ1265,subQ1264,subQ1263,subQ1262,subQ1261,subQ1260,subQ1259,subQ1258,subQ1257,subQ1256,subQ1255,subQ1254,subQ1253,subQ1252,subQ1251,subQ1250,subQ1249,subQ1248,subQ1247,subQ1246,subQ1245,subQ1244,subQ1243,subQ1242,subQ1241,subQ1240,subQ1239,subQ1238,subQ1237,subQ1236,subQ1235,subQ1234,subQ1233,subQ1232,subQ1231,subQ1230,subQ1229,subQ1228,subQ1227,subQ1226,subQ1225,subQ1224,subQ1223,subQ1222,subQ1221,subQ1220,subQ1219,subQ1218,subQ1217,subQ1216,subQ1215,subQ1214,subQ1213,subQ1212,subQ1211,subQ1210,subQ1209,subQ1208,subQ1207,subQ1206,subQ1205,subQ1204,subQ1203,subQ1202,subQ1201,subQ1200,subQ1199,subQ1198,subQ1197,subQ1196,subQ1195,subQ1194,subQ1193,subQ1192,subQ1191,subQ1190,subQ1189,subQ1188,subQ1187,subQ1186,subQ1185,subQ1184,subQ1183,subQ1182,subQ1181,subQ1180,subQ1179,subQ1178,subQ1177,subQ1176,subQ1175,subQ1174,subQ1173,subQ1172,subQ1171,subQ1170,subQ1169,subQ1168,subQ1167,subQ1166,subQ1165,subQ1164,subQ1163,subQ1162,subQ1161,subQ1160,subQ1159,subQ1158,subQ1157,subQ1156,subQ1155,subQ1154,subQ1153,subQ1152,subQ1151,subQ1150,subQ1149,subQ1148,subQ1147,subQ1146,subQ1145,subQ1144,subQ1143,subQ1142,subQ1141,subQ1140,subQ1139,subQ1138,subQ1137,subQ1136,subQ1135,subQ1134,subQ1133,subQ1132,subQ1131,subQ1130,subQ1129,subQ1128,subQ1127,subQ1126,subQ1125,subQ1124,subQ1123,subQ1122,subQ1121,subQ1120,subQ1119,subQ1118,subQ1117,subQ1116,subQ1115,subQ1114,subQ1113,subQ1112,subQ1111,subQ1110,subQ1109,subQ1108,subQ1107,subQ1106,subQ1105,subQ1104,subQ1103,subQ1102,subQ1101,subQ1100,subQ1099,subQ1098,subQ1097,subQ1096,subQ1095,subQ1094,subQ1093,subQ1092,subQ1091,subQ1090,subQ1089,subQ1088,subQ1087,subQ1086,subQ1085,subQ1084,subQ1083,subQ1082,subQ1081,subQ1080,subQ1079,subQ1078,subQ1077,subQ1076,subQ1075,subQ1074,subQ1073,subQ1072,subQ1071,subQ1070,subQ1069,subQ1068,subQ1067,subQ1066,subQ1065,subQ1064,subQ1063,subQ1062,subQ1061,subQ1060,subQ1059,subQ1058,subQ1057,subQ1056,subQ1055,subQ1054,subQ1053,subQ1052,subQ1051,subQ1050,subQ1049,subQ1048,subQ1047,subQ1046,subQ1045,subQ1044,subQ1043,subQ1042,subQ1041,subQ1040,subQ1039,subQ1038,subQ1037,subQ1036,subQ1035,subQ1034,subQ1033,subQ1032,subQ1031,subQ1030,subQ1029,subQ1028,subQ1027,subQ1026,subQ1025,subQ1024,subQ1023,subQ1022,subQ1021,subQ1020,subQ1019,subQ1018,subQ1017,subQ1016,subQ1015,subQ1014,subQ1013,subQ1012,subQ1011,subQ1010,subQ1009,subQ1008,subQ1007,subQ1006,subQ1005,subQ1004,subQ1003,subQ1002,subQ1001,subQ1000,subQ999,subQ998,subQ997,subQ996,subQ995,subQ994,subQ993,subQ992,subQ991,subQ990,subQ989,subQ988,subQ987,subQ986,subQ985,subQ984,subQ983,subQ982,subQ981,subQ980,subQ979,subQ978,subQ977,subQ976,subQ975,subQ974,subQ973,subQ972,subQ971,subQ970,subQ969,subQ968,subQ967,subQ966,subQ965,subQ964,subQ963,subQ962,subQ961,subQ960,subQ959,subQ958,subQ957,subQ956,subQ955,subQ954,subQ953,subQ952,subQ951,subQ950,subQ949,subQ948,subQ947,subQ946,subQ945,subQ944,subQ943,subQ942,subQ941,subQ940,subQ939,subQ938,subQ937,subQ936,subQ935,subQ934,subQ933,subQ932,subQ931,subQ930,subQ929,subQ928,subQ927,subQ926,subQ925,subQ924,subQ923,subQ922,subQ921,subQ920,subQ919,subQ918,subQ917,subQ916,subQ915,subQ914,subQ913,subQ912,subQ911,subQ910,subQ909,subQ908,subQ907,subQ906,subQ905,subQ904,subQ903,subQ902,subQ901,subQ900,subQ899,subQ898,subQ897,subQ896,subQ895,subQ894,subQ893,subQ892,subQ891,subQ890,subQ889,subQ888,subQ887,subQ886,subQ885,subQ884,subQ883,subQ882,subQ881,subQ880,subQ879,subQ878,subQ877,subQ876,subQ875,subQ874,subQ873,subQ872,subQ871,subQ870,subQ869,subQ868,subQ867,subQ866,subQ865,subQ864,subQ863,subQ862,subQ861,subQ860,subQ859,subQ858,subQ857,subQ856,subQ855,subQ854,subQ853,subQ852,subQ851,subQ850,subQ849,subQ848,subQ847,subQ846,subQ845,subQ844,subQ843,subQ842,subQ841,subQ840,subQ839,subQ838,subQ837,subQ836,subQ835,subQ834,subQ833,subQ832,subQ831,subQ830,subQ829,subQ828,subQ827,subQ826,subQ825,subQ824,subQ823,subQ822,subQ821,subQ820,subQ819,subQ818,subQ817,subQ816,subQ815,subQ814,subQ813,subQ812,subQ811,subQ810,subQ809,subQ808,subQ807,subQ806,subQ805,subQ804,subQ803,subQ802,subQ801,subQ800,subQ799,subQ798,subQ797,subQ796,subQ795,subQ794,subQ793,subQ792,subQ791,subQ790,subQ789,subQ788,subQ787,subQ786,subQ785,subQ784,subQ783,subQ782,subQ781,subQ780,subQ779,subQ778,subQ777,subQ776,subQ775,subQ774,subQ773,subQ772,subQ771,subQ770,subQ769,subQ768,subQ767,subQ766,subQ765,subQ764,subQ763,subQ762,subQ761,subQ760,subQ759,subQ758,subQ757,subQ756,subQ755,subQ754,subQ753,subQ752,subQ751,subQ750,subQ749,subQ748,subQ747,subQ746,subQ745,subQ744,subQ743,subQ742,subQ741,subQ740,subQ739,subQ738,subQ737,subQ736,subQ735,subQ734,subQ733,subQ732,subQ731,subQ730,subQ729,subQ728,subQ727,subQ726,subQ725,subQ724,subQ723,subQ722,subQ721,subQ720,subQ719,subQ718,subQ717,subQ716,subQ715,subQ714,subQ713,subQ712,subQ711,subQ710,subQ709,subQ708,subQ707,subQ706,subQ705,subQ704,subQ703,subQ702,subQ701,subQ700,subQ699,subQ698,subQ697,subQ696,subQ695,subQ694,subQ693,subQ692,subQ691,subQ690,subQ689,subQ688,subQ687,subQ686,subQ685,subQ684,subQ683,subQ682,subQ681,subQ680,subQ679,subQ678,subQ677,subQ676,subQ675,subQ674,subQ673,subQ672,subQ671,subQ670,subQ669,subQ668,subQ667,subQ666,subQ665,subQ664,subQ663,subQ662,subQ661,subQ660,subQ659,subQ658,subQ657,subQ656,subQ655,subQ654,subQ653,subQ652,subQ651,subQ650,subQ649,subQ648,subQ647,subQ646,subQ645,subQ644,subQ643,subQ642,subQ641,subQ640,subQ639,subQ638,subQ637,subQ636,subQ635,subQ634,subQ633,subQ632,subQ631,subQ630,subQ629,subQ628,subQ627,subQ626,subQ625,subQ624,subQ623,subQ622,subQ621,subQ620,subQ619,subQ618,subQ617,subQ616,subQ615,subQ614,subQ613,subQ612,subQ611,subQ610,subQ609,subQ608,subQ607,subQ606,subQ605,subQ604,subQ603,subQ602,subQ601,subQ600,subQ599,subQ598,subQ597,subQ596,subQ595,subQ594,subQ593,subQ592,subQ591,subQ590,subQ589,subQ588,subQ587,subQ586,subQ585,subQ584,subQ583,subQ582,subQ581,subQ580,subQ579,subQ578,subQ577,subQ576,subQ575,subQ574,subQ573,subQ572,subQ571,subQ570,subQ569,subQ568,subQ567,subQ566,subQ565,subQ564,subQ563,subQ562,subQ561,subQ560,subQ559,subQ558,subQ557,subQ556,subQ555,subQ554,subQ553,subQ552,subQ551,subQ550,subQ549,subQ548,subQ547,subQ546,subQ545,subQ544,subQ543,subQ542,subQ541,subQ540,subQ539,subQ538,subQ537,subQ536,subQ535,subQ534,subQ533,subQ532,subQ531,subQ530,subQ529,subQ528,subQ527,subQ526,subQ525,subQ524,subQ523,subQ522,subQ521,subQ520,subQ519,subQ518,subQ517,subQ516,subQ515,subQ514,subQ513,subQ512,subQ511,subQ510,subQ509,subQ508,subQ507,subQ506,subQ505,subQ504,subQ503,subQ502,subQ501,subQ500,subQ499,subQ498,subQ497,subQ496,subQ495,subQ494,subQ493,subQ492,subQ491,subQ490,subQ489,subQ488,subQ487,subQ486,subQ485,subQ484,subQ483,subQ482,subQ481,subQ480,subQ479,subQ478,subQ477,subQ476,subQ475,subQ474,subQ473,subQ472,subQ471,subQ470,subQ469,subQ468,subQ467,subQ466,subQ465,subQ464,subQ463,subQ462,subQ461,subQ460,subQ459,subQ458,subQ457,subQ456,subQ455,subQ454,subQ453,subQ452,subQ451,subQ450,subQ449,subQ448,subQ447,subQ446,subQ445,subQ444,subQ443,subQ442,subQ441,subQ440,subQ439,subQ438,subQ437,subQ436,subQ435,subQ434,subQ433,subQ432,subQ431,subQ430,subQ429,subQ428,subQ427,subQ426,subQ425,subQ424,subQ423,subQ422,subQ421,subQ420,subQ419,subQ418,subQ417,subQ416,subQ415,subQ414,subQ413,subQ412,subQ411,subQ410,subQ409,subQ408,subQ407,subQ406,subQ405,subQ404,subQ403,subQ402,subQ401,subQ400,subQ399,subQ398,subQ397,subQ396,subQ395,subQ394,subQ393,subQ392,subQ391,subQ390,subQ389,subQ388,subQ387,subQ386,subQ385,subQ384,subQ383,subQ382,subQ381,subQ380,subQ379,subQ378,subQ377,subQ376,subQ375,subQ374,subQ373,subQ372,subQ371,subQ370,subQ369,subQ368,subQ367,subQ366,subQ365,subQ364,subQ363,subQ362,subQ361,subQ360,subQ359,subQ358,subQ357,subQ356,subQ355,subQ354,subQ353,subQ352,subQ351,subQ350,subQ349,subQ348,subQ347,subQ346,subQ345,subQ344,subQ343,subQ342,subQ341,subQ340,subQ339,subQ338,subQ337,subQ336,subQ335,subQ334,subQ333,subQ332,subQ331,subQ330,subQ329,subQ328,subQ327,subQ326,subQ325,subQ324,subQ323,subQ322,subQ321,subQ320,subQ319,subQ318,subQ317,subQ316,subQ315,subQ314,subQ313,subQ312,subQ311,subQ310,subQ309,subQ308,subQ307,subQ306,subQ305,subQ304,subQ303,subQ302,subQ301,subQ300,subQ299,subQ298,subQ297,subQ296,subQ295,subQ294,subQ293,subQ292,subQ291,subQ290,subQ289,subQ288,subQ287,subQ286,subQ285,subQ284,subQ283,subQ282,subQ281,subQ280,subQ279,subQ278,subQ277,subQ276,subQ275,subQ274,subQ273,subQ272,subQ271,subQ270,subQ269,subQ268,subQ267,subQ266,subQ265,subQ264,subQ263,subQ262,subQ261,subQ260,subQ259,subQ258,subQ257,subQ256,subQ255,subQ254,subQ253,subQ252,subQ251,subQ250,subQ249,subQ248,subQ247,subQ246,subQ245,subQ244,subQ243,subQ242,subQ241,subQ240,subQ239,subQ238,subQ237,subQ236,subQ235,subQ234,subQ233,subQ232,subQ231,subQ230,subQ229,subQ228,subQ227,subQ226,subQ225,subQ224,subQ223,subQ222,subQ221,subQ220,subQ219,subQ218,subQ217,subQ216,subQ215,subQ214,subQ213,subQ212,subQ211,subQ210,subQ209,subQ208,subQ207,subQ206,subQ205,subQ204,subQ203,subQ202,subQ201,subQ200,subQ199,subQ198,subQ197,subQ196,subQ195,subQ194,subQ193,subQ192,subQ191,subQ190,subQ189,subQ188,subQ187,subQ186,subQ185,subQ184,subQ183,subQ182,subQ181,subQ180,subQ179,subQ178,subQ177,subQ176,subQ175,subQ174,subQ173,subQ172,subQ171,subQ170,subQ169,subQ168,subQ167,subQ166,subQ165,subQ164,subQ163,subQ162,subQ161,subQ160,subQ159,subQ158,subQ157,subQ156,subQ155,subQ154,subQ153,subQ152,subQ151,subQ150,subQ149,subQ148,subQ147,subQ146,subQ145,subQ144,subQ143,subQ142,subQ141,subQ140,subQ139,subQ138,subQ137,subQ136,subQ135,subQ134,subQ133,subQ132,subQ131,subQ130,subQ129,subQ128,subQ127,subQ126,subQ125,subQ124,subQ123,subQ122,subQ121,subQ120,subQ119,subQ118,subQ117,subQ116,subQ115,subQ114,subQ113,subQ112,subQ111,subQ110,subQ109,subQ108,subQ107,subQ106,subQ105,subQ104,subQ103,subQ102,subQ101,subQ100,subQ99,subQ98,subQ97,subQ96,subQ95,subQ94,subQ93,subQ92,subQ91,subQ90,subQ89,subQ88,subQ87,subQ86,subQ85,subQ84,subQ83,subQ82,subQ81,subQ80,subQ79,subQ78,subQ77,subQ76,subQ75,subQ74,subQ73,subQ72,subQ71,subQ70,subQ69,subQ68,subQ67,subQ66,subQ65,subQ64,subQ63,subQ62,subQ61,subQ60,subQ59,subQ58,subQ57,subQ56,subQ55,subQ54,subQ53,subQ52,subQ51,subQ50,subQ49,subQ48,subQ47,subQ46,subQ45,subQ44,subQ43,subQ42,subQ41,subQ40,subQ39,subQ38,subQ37,subQ36,subQ35,subQ34,subQ33,subQ32,subQ31,subQ30,subQ29,subQ28,subQ27,subQ26,subQ25,subQ24,subQ23,subQ22,subQ21,subQ20,subQ19,subQ18,subQ17,subQ16,subQ15,subQ14,subQ13,subQ12,subQ11,subQ10,subQ9,subQ8,subQ7,subQ6,subQ5,subQ4,subQ3,subQ2,subQ1,subQ0])],"isStart":true}),makeQuery(id+"F3.opExtrude","CAP_FACE",FACE,{"disambiguationData":[OSD([subQ4192,subQ4191,subQ4190,subQ4189,subQ4188,subQ4187,subQ4186,subQ4185,subQ4184,subQ4183,subQ4182,subQ4181,subQ4180,subQ4179,subQ4178,subQ4177,subQ4176,subQ4175,subQ4174,subQ4173,subQ4172,subQ4171,subQ4170,subQ4169,subQ4168,subQ4167,subQ4166,subQ4165,subQ4164,subQ4163,subQ4162,subQ4161,subQ4160,subQ4159,subQ4158,subQ4157,subQ4156,subQ4155,subQ4154,subQ4153,subQ4152,subQ4151,subQ4150,subQ4149,subQ4148,subQ4147,subQ4146,subQ4145,subQ4144,subQ4143,subQ4142,subQ4141,subQ4140,subQ4139,subQ4138,subQ4137,subQ4136,subQ4135,subQ4134,subQ4133,subQ4132,subQ4131,subQ4130,subQ4129,subQ4128,subQ4127,subQ4126,subQ4125,subQ4124,subQ4123,subQ4122,subQ4121,subQ4120,subQ4119,subQ4118,subQ4117,subQ4116,subQ4115,subQ4114,subQ4113,subQ4112,subQ4111,subQ4110,subQ4109,subQ4108,subQ4107,subQ4106,subQ4105,subQ4104,subQ4103,subQ4102,subQ4101,subQ4100,subQ4099,subQ4098,subQ4097,subQ4096,subQ4095,subQ4094,subQ4093,subQ4092,subQ4091,subQ4090,subQ4089,subQ4088,subQ4087,subQ4086,subQ4085,subQ4084,subQ4083,subQ4082,subQ4081,subQ4080,subQ4079,subQ4078,subQ4077,subQ4076,subQ4075,subQ4074,subQ4073,subQ4072,subQ4071,subQ4070,subQ4069,subQ4068,subQ4067,subQ4066,subQ4065,subQ4064,subQ4063,subQ4062,subQ4061,subQ4060,subQ4059,subQ4058,subQ4057,subQ4056,subQ4055,subQ4054,subQ4053,subQ4052,subQ4051,subQ4050,subQ4049,subQ4048,subQ4047,subQ4046,subQ4045,subQ4044,subQ4043,subQ4042,subQ4041,subQ4040,subQ4039,subQ4038,subQ4037,subQ4036,subQ4035,subQ4034,subQ4033,subQ4032,subQ4031,subQ4030,subQ4029,subQ4028,subQ4027,subQ4026,subQ4025,subQ4024,subQ4023,subQ4022,subQ4021,subQ4020,subQ4019,subQ4018,subQ4017,subQ4016,subQ4015,subQ4014,subQ4013,subQ4012,subQ4011,subQ4010,subQ4009,subQ4008,subQ4007,subQ4006,subQ4005,subQ4004,subQ4003,subQ4002,subQ4001,subQ4000,subQ3999,subQ3998,subQ3997,subQ3996,subQ3995,subQ3994,subQ3993,subQ3992,subQ3991,subQ3990,subQ3989,subQ3988,subQ3987,subQ3986,subQ3985,subQ3984,subQ3983,subQ3982,subQ3981,subQ3980,subQ3979,subQ3978,subQ3977,subQ3976,subQ3975,subQ3974,subQ3973,subQ3972,subQ3971,subQ3970,subQ3969,subQ3968,subQ3967,subQ3966,subQ3965,subQ3964,subQ3963,subQ3962,subQ3961,subQ3960,subQ3959,subQ3958,subQ3957,subQ3956,subQ3955,subQ3954,subQ3953,subQ3952,subQ3951,subQ3950,subQ3949,subQ3948,subQ3947,subQ3946,subQ3945,subQ3944,subQ3943,subQ3942,subQ3941,subQ3940,subQ3939,subQ3938,subQ3937,subQ3936,subQ3935,subQ3934,subQ3933,subQ3932,subQ3931,subQ3930,subQ3929,subQ3928,subQ3927,subQ3926,subQ3925,subQ3924,subQ3923,subQ3922,subQ3921,subQ3920,subQ3919,subQ3918,subQ3917,subQ3916,subQ3915,subQ3914,subQ3913,subQ3912,subQ3911,subQ3910,subQ3909,subQ3908,subQ3907,subQ3906,subQ3905,subQ3904,subQ3903,subQ3902,subQ3901,subQ3900,subQ3899,subQ3898,subQ3897,subQ3896,subQ3895,subQ3894,subQ3893,subQ3892,subQ3891,subQ3890,subQ3889,subQ3888,subQ3887,subQ3886,subQ3885,subQ3884,subQ3883,subQ3882,subQ3881,subQ3880,subQ3879,subQ3878,subQ3877,subQ3876,subQ3875,subQ3874,subQ3873,subQ3872,subQ3871,subQ3870,subQ3869,subQ3868,subQ3867,subQ3866,subQ3865,subQ3864,subQ3863,subQ3862,subQ3861,subQ3860,subQ3859,subQ3858,subQ3857,subQ3856,subQ3855,subQ3854,subQ3853,subQ3852,subQ3851,subQ3850,subQ3849,subQ3848,subQ3847,subQ3846,subQ3845,subQ3844,subQ3843,subQ3842,subQ3841,subQ3840,subQ3839,subQ3838,subQ3837,subQ3836,subQ3835,subQ3834,subQ3833,subQ3832,subQ3831,subQ3830,subQ3829,subQ3828,subQ3827,subQ3826,subQ3825,subQ3824,subQ3823,subQ3822,subQ3821,subQ3820,subQ3819,subQ3818,subQ3817,subQ3816,subQ3815,subQ3814,subQ3813,subQ3812,subQ3811,subQ3810,subQ3809,subQ3808,subQ3807,subQ3806,subQ3805,subQ3804,subQ3803,subQ3802,subQ3801,subQ3800,subQ3799,subQ3798,subQ3797,subQ3796,subQ3795,subQ3794,subQ3793,subQ3792,subQ3791,subQ3790,subQ3789,subQ3788,subQ3787,subQ3786,subQ3785,subQ3784,subQ3783,subQ3782,subQ3781,subQ3780,subQ3779,subQ3778,subQ3777,subQ3776,subQ3775,subQ3774,subQ3773,subQ3772,subQ3771,subQ3770,subQ3769,subQ3768,subQ3767,subQ3766,subQ3765,subQ3764,subQ3763,subQ3762,subQ3761,subQ3760,subQ3759,subQ3758,subQ3757,subQ3756,subQ3755,subQ3754,subQ3753,subQ3752,subQ3751,subQ3750,subQ3749,subQ3748,subQ3747,subQ3746,subQ3745,subQ3744,subQ3743,subQ3742,subQ3741,subQ3740,subQ3739,subQ3738,subQ3737,subQ3736,subQ3735,subQ3734,subQ3733,subQ3732,subQ3731,subQ3730,subQ3729,subQ3728,subQ3727,subQ3726,subQ3725,subQ3724,subQ3723,subQ3722,subQ3721,subQ3720,subQ3719,subQ3718,subQ3717,subQ3716,subQ3715,subQ3714,subQ3713,subQ3712,subQ3711,subQ3710,subQ3709,subQ3708,subQ3707,subQ3706,subQ3705,subQ3704,subQ3703,subQ3702,subQ3701,subQ3700,subQ3699,subQ3698,subQ3697,subQ3696,subQ3695,subQ3694,subQ3693,subQ3692,subQ3691,subQ3690,subQ3689,subQ3688,subQ3687,subQ3686,subQ3685,subQ3684,subQ3683,subQ3682,subQ3681,subQ3680,subQ3679,subQ3678,subQ3677,subQ3676,subQ3675,subQ3674,subQ3673,subQ3672,subQ3671,subQ3670,subQ3669,subQ3668,subQ3667,subQ3666,subQ3665,subQ3664,subQ3663,subQ3662,subQ3661,subQ3660,subQ3659,subQ3658,subQ3657,subQ3656,subQ3655,subQ3654,subQ3653,subQ3652,subQ3651,subQ3650,subQ3649,subQ3648,subQ3647,subQ3646,subQ3645,subQ3644,subQ3643,subQ3642,subQ3641,subQ3640,subQ3639,subQ3638,subQ3637,subQ3636,subQ3635,subQ3634,subQ3633,subQ3632,subQ3631,subQ3630,subQ3629,subQ3628,subQ3627,subQ3626,subQ3625,subQ3624,subQ3623,subQ3622,subQ3621,subQ3620,subQ3619,subQ3618,subQ3617,subQ3616,subQ3615,subQ3614,subQ3613,subQ3612,subQ3611,subQ3610,subQ3609,subQ3608,subQ3607,subQ3606,subQ3605,subQ3604,subQ3603,subQ3602,subQ3601,subQ3600,subQ3599,subQ3598,subQ3597,subQ3596,subQ3595,subQ3594,subQ3593,subQ3592,subQ3591,subQ3590,subQ3589,subQ3588,subQ3587,subQ3586,subQ3585,subQ3584,subQ3583,subQ3582,subQ3581,subQ3580,subQ3579,subQ3578,subQ3577,subQ3576,subQ3575,subQ3574,subQ3573,subQ3572,subQ3571,subQ3570,subQ3569,subQ3568,subQ3567,subQ3566,subQ3565,subQ3564,subQ3563,subQ3562,subQ3561,subQ3560,subQ3559,subQ3558,subQ3557,subQ3556,subQ3555,subQ3554,subQ3553,subQ3552,subQ3551,subQ3550,subQ3549,subQ3548,subQ3547,subQ3546,subQ3545,subQ3544,subQ3543,subQ3542,subQ3541,subQ3540,subQ3539,subQ3538,subQ3537,subQ3536,subQ3535,subQ3534,subQ3533,subQ3532,subQ3531,subQ3530,subQ3529,subQ3528,subQ3527,subQ3526,subQ3525,subQ3524,subQ3523,subQ3522,subQ3521,subQ3520,subQ3519,subQ3518,subQ3517,subQ3516,subQ3515,subQ3514,subQ3513,subQ3512,subQ3511,subQ3510,subQ3509,subQ3508,subQ3507,subQ3506,subQ3505,subQ3504,subQ3503,subQ3502,subQ3501,subQ3500,subQ3499,subQ3498,subQ3497,subQ3496,subQ3495,subQ3494,subQ3493,subQ3492,subQ3491,subQ3490,subQ3489,subQ3488,subQ3487,subQ3486,subQ3485,subQ3484,subQ3483,subQ3482,subQ3481,subQ3480,subQ3479,subQ3478,subQ3477,subQ3476,subQ3475,subQ3474,subQ3473,subQ3472,subQ3471,subQ3470,subQ3469,subQ3468,subQ3467,subQ3466,subQ3465,subQ3464,subQ3463,subQ3462,subQ3461,subQ3460,subQ3459,subQ3458,subQ3457,subQ3456,subQ3455,subQ3454,subQ3453,subQ3452,subQ3451,subQ3450,subQ3449,subQ3448,subQ3447,subQ3446,subQ3445,subQ3444,subQ3443,subQ3442,subQ3441,subQ3440,subQ3439,subQ3438,subQ3437,subQ3436,subQ3435,subQ3434,subQ3433,subQ3432,subQ3431,subQ3430,subQ3429,subQ3428,subQ3427,subQ3426,subQ3425,subQ3424,subQ3423,subQ3422,subQ3421,subQ3420,subQ3419,subQ3418,subQ3417,subQ3416,subQ3415,subQ3414,subQ3413,subQ3412,subQ3411,subQ3410,subQ3409,subQ3408,subQ3407,subQ3406,subQ3405,subQ3404,subQ3403,subQ3402,subQ3401,subQ3400,subQ3399,subQ3398,subQ3397,subQ3396,subQ3395,subQ3394,subQ3393,subQ3392,subQ3391,subQ3390,subQ3389,subQ3388,subQ3387,subQ3386,subQ3385,subQ3384,subQ3383,subQ3382,subQ3381,subQ3380,subQ3379,subQ3378,subQ3377,subQ3376,subQ3375,subQ3374,subQ3373,subQ3372,subQ3371,subQ3370,subQ3369,subQ3368,subQ3367,subQ3366,subQ3365,subQ3364,subQ3363,subQ3362,subQ3361,subQ3360,subQ3359,subQ3358,subQ3357,subQ3356,subQ3355,subQ3354,subQ3353,subQ3352,subQ3351,subQ3350,subQ3349,subQ3348,subQ3347,subQ3346,subQ3345,subQ3344,subQ3343,subQ3342,subQ3341,subQ3340,subQ3339,subQ3338,subQ3337,subQ3336,subQ3335,subQ3334,subQ3333,subQ3332,subQ3331,subQ3330,subQ3329,subQ3328,subQ3327,subQ3326,subQ3325,subQ3324,subQ3323,subQ3322,subQ3321,subQ3320,subQ3319,subQ3318,subQ3317,subQ3316,subQ3315,subQ3314,subQ3313,subQ3312,subQ3311,subQ3310,subQ3309,subQ3308,subQ3307,subQ3306,subQ3305,subQ3304,subQ3303,subQ3302,subQ3301,subQ3300,subQ3299,subQ3298,subQ3297,subQ3296,subQ3295,subQ3294,subQ3293,subQ3292,subQ3291,subQ3290,subQ3289,subQ3288,subQ3287,subQ3286,subQ3285,subQ3284,subQ3283,subQ3282,subQ3281,subQ3280,subQ3279,subQ3278,subQ3277,subQ3276,subQ3275,subQ3274,subQ3273,subQ3272,subQ3271,subQ3270,subQ3269,subQ3268,subQ3267,subQ3266,subQ3265,subQ3264,subQ3263,subQ3262,subQ3261,subQ3260,subQ3259,subQ3258,subQ3257,subQ3256,subQ3255,subQ3254,subQ3253,subQ3252,subQ3251,subQ3250,subQ3249,subQ3248,subQ3247,subQ3246,subQ3245,subQ3244,subQ3243,subQ3242,subQ3241,subQ3240,subQ3239,subQ3238,subQ3237,subQ3236,subQ3235,subQ3234,subQ3233,subQ3232,subQ3231,subQ3230,subQ3229,subQ3228,subQ3227,subQ3226,subQ3225,subQ3224,subQ3223,subQ3222,subQ3221,subQ3220,subQ3219,subQ3218,subQ3217,subQ3216,subQ3215,subQ3214,subQ3213,subQ3212,subQ3211,subQ3210,subQ3209,subQ3208,subQ3207,subQ3206,subQ3205,subQ3204,subQ3203,subQ3202,subQ3201,subQ3200,subQ3199,subQ3198,subQ3197,subQ3196,subQ3195,subQ3194,subQ3193,subQ3192,subQ3191,subQ3190,subQ3189,subQ3188,subQ3187,subQ3186,subQ3185,subQ3184,subQ3183,subQ3182,subQ3181,subQ3180,subQ3179,subQ3178,subQ3177,subQ3176,subQ3175,subQ3174,subQ3173,subQ3172,subQ3171,subQ3170,subQ3169,subQ3168,subQ3167,subQ3166,subQ3165,subQ3164,subQ3163,subQ3162,subQ3161,subQ3160,subQ3159,subQ3158,subQ3157,subQ3156,subQ3155,subQ3154,subQ3153,subQ3152,subQ3151,subQ3150,subQ3149,subQ3148,subQ3147,subQ3146,subQ3145,subQ3144,subQ3143,subQ3142,subQ3141,subQ3140,subQ3139,subQ3138,subQ3137,subQ3136,subQ3135,subQ3134,subQ3133,subQ3132,subQ3131,subQ3130,subQ3129,subQ3128,subQ3127,subQ3126,subQ3125,subQ3124,subQ3123,subQ3122,subQ3121,subQ3120,subQ3119,subQ3118,subQ3117,subQ3116,subQ3115,subQ3114,subQ3113,subQ3112,subQ3111,subQ3110,subQ3109,subQ3108,subQ3107,subQ3106,subQ3105,subQ3104,subQ3103,subQ3102,subQ3101,subQ3100,subQ3099,subQ3098,subQ3097,subQ3096,subQ3095,subQ3094,subQ3093,subQ3092,subQ3091,subQ3090,subQ3089,subQ3088,subQ3087,subQ3086,subQ3085,subQ3084,subQ3083,subQ3082,subQ3081,subQ3080,subQ3079,subQ3078,subQ3077,subQ3076,subQ3075,subQ3074,subQ3073,subQ3072,subQ3071,subQ3070,subQ3069,subQ3068,subQ3067,subQ3066,subQ3065,subQ3064,subQ3063,subQ3062,subQ3061,subQ3060,subQ3059,subQ3058,subQ3057,subQ3056,subQ3055,subQ3054,subQ3053,subQ3052,subQ3051,subQ3050,subQ3049,subQ3048,subQ3047,subQ3046,subQ3045,subQ3044,subQ3043,subQ3042,subQ3041,subQ3040,subQ3039,subQ3038,subQ3037,subQ3036,subQ3035,subQ3034,subQ3033,subQ3032,subQ3031,subQ3030,subQ3029,subQ3028,subQ3027,subQ3026,subQ3025,subQ3024,subQ3023,subQ3022,subQ3021,subQ3020,subQ3019,subQ3018,subQ3017,subQ3016,subQ3015,subQ3014,subQ3013,subQ3012,subQ3011,subQ3010,subQ3009,subQ3008,subQ3007,subQ3006,subQ3005,subQ3004,subQ3003,subQ3002,subQ3001,subQ3000,subQ2999,subQ2998,subQ2997,subQ2996,subQ2995,subQ2994,subQ2993,subQ2992,subQ2991,subQ2990,subQ2989,subQ2988,subQ2987,subQ2986,subQ2985,subQ2984,subQ2983,subQ2982,subQ2981,subQ2980,subQ2979,subQ2978,subQ2977,subQ2976,subQ2975,subQ2974,subQ2973,subQ2972,subQ2971,subQ2970,subQ2969,subQ2968,subQ2967,subQ2966,subQ2965,subQ2964,subQ2963,subQ2962,subQ2961,subQ2960,subQ2959,subQ2958,subQ2957,subQ2956,subQ2955,subQ2954,subQ2953,subQ2952,subQ2951,subQ2950,subQ2949,subQ2948,subQ2947,subQ2946,subQ2945,subQ2944,subQ2943,subQ2942,subQ2941,subQ2940,subQ2939,subQ2938,subQ2937,subQ2936,subQ2935,subQ2934,subQ2933,subQ2932,subQ2931,subQ2930,subQ2929,subQ2928,subQ2927,subQ2926,subQ2925,subQ2924,subQ2923,subQ2922,subQ2921,subQ2920,subQ2919,subQ2918,subQ2917,subQ2916,subQ2915,subQ2914,subQ2913,subQ2912,subQ2911,subQ2910,subQ2909,subQ2908,subQ2907,subQ2906,subQ2905,subQ2904,subQ2903,subQ2902,subQ2901,subQ2900,subQ2899,subQ2898,subQ2897,subQ2896,subQ2895,subQ2894,subQ2893,subQ2892,subQ2891,subQ2890,subQ2889,subQ2888,subQ2887,subQ2886,subQ2885,subQ2884,subQ2883,subQ2882,subQ2881,subQ2880,subQ2879,subQ2878,subQ2877,subQ2876,subQ2875,subQ2874,subQ2873,subQ2872,subQ2871,subQ2870,subQ2869,subQ2868,subQ2867,subQ2866,subQ2865,subQ2864,subQ2863,subQ2862,subQ2861,subQ2860,subQ2859,subQ2858,subQ2857,subQ2856,subQ2855,subQ2854,subQ2853,subQ2852,subQ2851,subQ2850,subQ2849,subQ2848,subQ2847,subQ2846,subQ2845,subQ2844,subQ2843,subQ2842,subQ2841,subQ2840,subQ2839,subQ2838,subQ2837,subQ2836,subQ2835,subQ2834,subQ2833,subQ2832,subQ2831,subQ2830,subQ2829,subQ2828,subQ2827,subQ2826,subQ2825,subQ2824,subQ2823,subQ2822,subQ2821,subQ2820,subQ2819,subQ2818,subQ2817,subQ2816,subQ2815,subQ2814,subQ2813,subQ2812,subQ2811,subQ2810,subQ2809,subQ2808,subQ2807,subQ2806,subQ2805,subQ2804,subQ2803,subQ2802,subQ2801,subQ2800,subQ2799,subQ2798,subQ2797,subQ2796,subQ2795,subQ2794,subQ2793,subQ2792,subQ2791,subQ2790,subQ2789,subQ2788,subQ2787,subQ2786,subQ2785,subQ2784,subQ2783,subQ2782,subQ2781,subQ2780,subQ2779,subQ2778,subQ2777,subQ2776,subQ2775,subQ2774,subQ2773,subQ2772,subQ2771,subQ2770,subQ2769,subQ2768,subQ2767,subQ2766,subQ2765,subQ2764,subQ2763,subQ2762,subQ2761,subQ2760,subQ2759,subQ2758,subQ2757,subQ2756,subQ2755,subQ2754,subQ2753,subQ2752,subQ2751,subQ2750,subQ2749,subQ2748,subQ2747,subQ2746,subQ2745,subQ2744,subQ2743,subQ2742,subQ2741,subQ2740,subQ2739,subQ2738,subQ2737,subQ2736,subQ2735,subQ2734,subQ2733,subQ2732,subQ2731,subQ2730,subQ2729,subQ2728,subQ2727,subQ2726,subQ2725,subQ2724,subQ2723,subQ2722,subQ2721,subQ2720,subQ2719,subQ2718,subQ2717,subQ2716,subQ2715,subQ2714,subQ2713,subQ2712,subQ2711,subQ2710,subQ2709,subQ2708,subQ2707,subQ2706,subQ2705,subQ2704,subQ2703,subQ2702,subQ2701,subQ2700,subQ2699,subQ2698,subQ2697,subQ2696,subQ2695,subQ2694,subQ2693,subQ2692,subQ2691,subQ2690,subQ2689,subQ2688,subQ2687,subQ2686,subQ2685,subQ2684,subQ2683,subQ2682,subQ2681,subQ2680,subQ2679,subQ2678,subQ2677,subQ2676,subQ2675,subQ2674,subQ2673,subQ2672,subQ2671,subQ2670,subQ2669,subQ2668,subQ2667,subQ2666,subQ2665,subQ2664,subQ2663,subQ2662,subQ2661,subQ2660,subQ2659,subQ2658,subQ2657,subQ2656,subQ2655,subQ2654,subQ2653,subQ2652,subQ2651,subQ2650,subQ2649,subQ2648,subQ2647,subQ2646,subQ2645,subQ2644,subQ2643,subQ2642,subQ2641,subQ2640,subQ2639,subQ2638,subQ2637,subQ2636,subQ2635,subQ2634,subQ2633,subQ2632,subQ2631,subQ2630,subQ2629,subQ2628,subQ2627,subQ2626,subQ2625,subQ2624,subQ2623,subQ2622,subQ2621,subQ2620,subQ2619,subQ2618,subQ2617,subQ2616,subQ2615,subQ2614,subQ2613,subQ2612,subQ2611,subQ2610,subQ2609,subQ2608,subQ2607,subQ2606,subQ2605,subQ2604,subQ2603,subQ2602,subQ2601,subQ2600,subQ2599,subQ2598,subQ2597,subQ2596,subQ2595,subQ2594,subQ2593,subQ2592,subQ2591,subQ2590,subQ2589,subQ2588,subQ2587,subQ2586,subQ2585,subQ2584,subQ2583,subQ2582,subQ2581,subQ2580,subQ2579,subQ2578,subQ2577,subQ2576,subQ2575,subQ2574,subQ2573,subQ2572,subQ2571,subQ2570,subQ2569,subQ2568,subQ2567,subQ2566,subQ2565,subQ2564,subQ2563,subQ2562,subQ2561,subQ2560,subQ2559,subQ2558,subQ2557,subQ2556,subQ2555,subQ2554,subQ2553,subQ2552,subQ2551,subQ2550,subQ2549,subQ2548,subQ2547,subQ2546,subQ2545,subQ2544,subQ2543,subQ2542,subQ2541,subQ2540,subQ2539,subQ2538,subQ2537,subQ2536,subQ2535,subQ2534,subQ2533,subQ2532,subQ2531,subQ2530,subQ2529,subQ2528,subQ2527,subQ2526,subQ2525,subQ2524,subQ2523,subQ2522,subQ2521,subQ2520,subQ2519,subQ2518,subQ2517,subQ2516,subQ2515,subQ2514,subQ2513,subQ2512,subQ2511,subQ2510,subQ2509,subQ2508,subQ2507,subQ2506,subQ2505,subQ2504,subQ2503,subQ2502,subQ2501,subQ2500,subQ2499,subQ2498,subQ2497,subQ2496,subQ2495,subQ2494,subQ2493,subQ2492,subQ2491,subQ2490,subQ2489,subQ2488,subQ2487,subQ2486,subQ2485,subQ2484,subQ2483,subQ2482,subQ2481,subQ2480,subQ2479,subQ2478,subQ2477,subQ2476,subQ2475,subQ2474,subQ2473,subQ2472,subQ2471,subQ2470,subQ2469,subQ2468,subQ2467,subQ2466,subQ2465,subQ2464,subQ2463,subQ2462,subQ2461,subQ2460,subQ2459,subQ2458,subQ2457,subQ2456,subQ2455,subQ2454,subQ2453,subQ2452,subQ2451,subQ2450,subQ2449,subQ2448,subQ2447,subQ2446,subQ2445,subQ2444,subQ2443,subQ2442,subQ2441,subQ2440,subQ2439,subQ2438,subQ2437,subQ2436,subQ2435,subQ2434,subQ2433,subQ2432,subQ2431,subQ2430,subQ2429,subQ2428,subQ2427,subQ2426,subQ2425,subQ2424,subQ2423,subQ2422,subQ2421,subQ2420,subQ2419,subQ2418,subQ2417,subQ2416,subQ2415,subQ2414,subQ2413,subQ2412,subQ2411,subQ2410,subQ2409,subQ2408,subQ2407,subQ2406,subQ2405,subQ2404,subQ2403,subQ2402,subQ2401,subQ2400,subQ2399,subQ2398,subQ2397,subQ2396,subQ2395,subQ2394,subQ2393,subQ2392,subQ2391,subQ2390,subQ2389,subQ2388,subQ2387,subQ2386,subQ2385,subQ2384,subQ2383,subQ2382,subQ2381,subQ2380,subQ2379,subQ2378,subQ2377,subQ2376,subQ2375,subQ2374,subQ2373,subQ2372,subQ2371,subQ2370,subQ2369,subQ2368,subQ2367,subQ2366,subQ2365,subQ2364,subQ2363,subQ2362,subQ2361,subQ2360,subQ2359,subQ2358,subQ2357,subQ2356,subQ2355,subQ2354,subQ2353,subQ2352,subQ2351,subQ2350,subQ2349,subQ2348,subQ2347,subQ2346,subQ2345,subQ2344,subQ2343,subQ2342,subQ2341,subQ2340,subQ2339,subQ2338,subQ2337,subQ2336,subQ2335,subQ2334,subQ2333,subQ2332,subQ2331,subQ2330,subQ2329,subQ2328,subQ2327,subQ2326,subQ2325,subQ2324,subQ2323,subQ2322,subQ2321,subQ2320,subQ2319,subQ2318,subQ2317,subQ2316,subQ2315,subQ2314,subQ2313,subQ2312,subQ2311,subQ2310,subQ2309,subQ2308,subQ2307,subQ2306,subQ2305,subQ2304,subQ2303,subQ2302,subQ2301,subQ2300,subQ2299,subQ2298,subQ2297,subQ2296,subQ2295,subQ2294,subQ2293,subQ2292,subQ2291,subQ2290,subQ2289,subQ2288,subQ2287,subQ2286,subQ2285,subQ2284,subQ2283,subQ2282,subQ2281,subQ2280,subQ2279,subQ2278,subQ2277,subQ2276,subQ2275,subQ2274,subQ2273,subQ2272,subQ2271,subQ2270,subQ2269,subQ2268,subQ2267,subQ2266,subQ2265,subQ2264,subQ2263,subQ2262,subQ2261,subQ2260,subQ2259,subQ2258,subQ2257,subQ2256,subQ2255,subQ2254,subQ2253,subQ2252,subQ2251,subQ2250,subQ2249,subQ2248,subQ2247,subQ2246,subQ2245,subQ2244,subQ2243,subQ2242,subQ2241,subQ2240,subQ2239,subQ2238,subQ2237,subQ2236,subQ2235,subQ2234,subQ2233,subQ2232,subQ2231,subQ2230,subQ2229,subQ2228,subQ2227,subQ2226,subQ2225,subQ2224,subQ2223,subQ2222,subQ2221,subQ2220,subQ2219,subQ2218,subQ2217,subQ2216,subQ2215,subQ2214,subQ2213,subQ2212,subQ2211,subQ2210,subQ2209,subQ2208,subQ2207,subQ2206,subQ2205,subQ2204,subQ2203,subQ2202,subQ2201,subQ2200,subQ2199,subQ2198,subQ2197,subQ2196,subQ2195,subQ2194,subQ2193,subQ2192,subQ2191,subQ2190,subQ2189,subQ2188,subQ2187,subQ2186,subQ2185,subQ2184,subQ2183,subQ2182,subQ2181,subQ2180,subQ2179,subQ2178,subQ2177,subQ2176,subQ2175,subQ2174,subQ2173,subQ2172,subQ2171,subQ2170,subQ2169,subQ2168,subQ2167,subQ2166,subQ2165,subQ2164,subQ2163,subQ2162,subQ2161,subQ2160,subQ2159,subQ2158,subQ2157,subQ2156,subQ2155,subQ2154,subQ2153,subQ2152,subQ2151,subQ2150,subQ2149,subQ2148,subQ2147,subQ2146,subQ2145,subQ2144,subQ2143,subQ2142,subQ2141,subQ2140,subQ2139,subQ2138,subQ2137,subQ2136,subQ2135,subQ2134,subQ2133,subQ2132,subQ2131,subQ2130,subQ2129,subQ2128,subQ2127,subQ2126,subQ2125,subQ2124,subQ2123,subQ2122,subQ2121,subQ2120,subQ2119,subQ2118,subQ2117,subQ2116,subQ2115,subQ2114,subQ2113,subQ2112,subQ2111,subQ2110,subQ2109,subQ2108,subQ2107,subQ2106,subQ2105,subQ2104,subQ2103,subQ2102,subQ2101,subQ2100,subQ2099,subQ2098,subQ2097,subQ2096,subQ2095,subQ2094,subQ2093,subQ2092,subQ2091,subQ2090,subQ2089,subQ2088,subQ2087,subQ2086,subQ2085,subQ2084,subQ2083,subQ2082,subQ2081,subQ2080,subQ2079,subQ2078,subQ2077,subQ2076,subQ2075,subQ2074,subQ2073,subQ2072,subQ2071,subQ2070,subQ2069,subQ2068,subQ2067,subQ2066,subQ2065,subQ2064,subQ2063,subQ2062,subQ2061,subQ2060,subQ2059,subQ2058,subQ2057,subQ2056,subQ2055,subQ2054,subQ2053,subQ2052,subQ2051,subQ2050,subQ2049,subQ2048,subQ2047,subQ2046,subQ2045,subQ2044,subQ2043,subQ2042,subQ2041,subQ2040,subQ2039,subQ2038,subQ2037,subQ2036,subQ2035,subQ2034,subQ2033,subQ2032,subQ2031,subQ2030,subQ2029,subQ2028,subQ2027,subQ2026,subQ2025,subQ2024,subQ2023,subQ2022,subQ2021,subQ2020,subQ2019,subQ2018,subQ2017,subQ2016,subQ2015,subQ2014,subQ2013,subQ2012,subQ2011,subQ2010,subQ2009,subQ2008,subQ2007,subQ2006,subQ2005,subQ2004,subQ2003,subQ2002,subQ2001,subQ2000,subQ1999,subQ1998,subQ1997,subQ1996,subQ1995,subQ1994,subQ1993,subQ1992,subQ1991,subQ1990,subQ1989,subQ1988,subQ1987,subQ1986,subQ1985,subQ1984,subQ1983,subQ1982,subQ1981,subQ1980,subQ1979,subQ1978,subQ1977,subQ1976,subQ1975,subQ1974,subQ1973,subQ1972,subQ1971,subQ1970,subQ1969,subQ1968,subQ1967,subQ1966,subQ1965,subQ1964,subQ1963,subQ1962,subQ1961,subQ1960,subQ1959,subQ1958,subQ1957,subQ1956,subQ1955,subQ1954,subQ1953,subQ1952,subQ1951,subQ1950,subQ1949,subQ1948,subQ1947,subQ1946,subQ1945,subQ1944,subQ1943,subQ1942,subQ1941,subQ1940,subQ1939,subQ1938,subQ1937,subQ1936,subQ1935,subQ1934,subQ1933,subQ1932,subQ1931,subQ1930,subQ1929,subQ1928,subQ1927,subQ1926,subQ1925,subQ1924,subQ1923,subQ1922,subQ1921,subQ1920,subQ1919,subQ1918,subQ1917,subQ1916,subQ1915,subQ1914,subQ1913,subQ1912,subQ1911,subQ1910,subQ1909,subQ1908,subQ1907,subQ1906,subQ1905,subQ1904,subQ1903,subQ1902,subQ1901,subQ1900,subQ1899,subQ1898,subQ1897,subQ1896,subQ1895,subQ1894,subQ1893,subQ1892,subQ1891,subQ1890,subQ1889,subQ1888,subQ1887,subQ1886,subQ1885,subQ1884,subQ1883,subQ1882,subQ1881,subQ1880,subQ1879,subQ1878,subQ1877,subQ1876,subQ1875,subQ1874,subQ1873,subQ1872,subQ1871,subQ1870,subQ1869,subQ1868,subQ1867,subQ1866,subQ1865,subQ1864,subQ1863,subQ1862,subQ1861,subQ1860,subQ1859,subQ1858,subQ1857,subQ1856,subQ1855,subQ1854,subQ1853,subQ1852,subQ1851,subQ1850,subQ1849,subQ1848,subQ1847,subQ1846,subQ1845,subQ1844,subQ1843,subQ1842,subQ1841,subQ1840,subQ1839,subQ1838,subQ1837,subQ1836,subQ1835,subQ1834,subQ1833,subQ1832,subQ1831,subQ1830,subQ1829,subQ1828,subQ1827,subQ1826,subQ1825,subQ1824,subQ1823,subQ1822,subQ1821,subQ1820,subQ1819,subQ1818,subQ1817,subQ1816,subQ1815,subQ1814,subQ1813,subQ1812,subQ1811,subQ1810,subQ1809,subQ1808,subQ1807,subQ1806,subQ1805,subQ1804,subQ1803,subQ1802,subQ1801,subQ1800,subQ1799,subQ1798,subQ1797,subQ1796,subQ1795,subQ1794,subQ1793,subQ1792,subQ1791,subQ1790,subQ1789,subQ1788,subQ1787,subQ1786,subQ1785,subQ1784,subQ1783,subQ1782,subQ1781,subQ1780,subQ1779,subQ1778,subQ1777,subQ1776,subQ1775,subQ1774,subQ1773,subQ1772,subQ1771,subQ1770,subQ1769,subQ1768,subQ1767,subQ1766,subQ1765,subQ1764,subQ1763,subQ1762,subQ1761,subQ1760,subQ1759,subQ1758,subQ1757,subQ1756,subQ1755,subQ1754,subQ1753,subQ1752,subQ1751,subQ1750,subQ1749,subQ1748,subQ1747,subQ1746,subQ1745,subQ1744,subQ1743,subQ1742,subQ1741,subQ1740,subQ1739,subQ1738,subQ1737,subQ1736,subQ1735,subQ1734,subQ1733,subQ1732,subQ1731,subQ1730,subQ1729,subQ1728,subQ1727,subQ1726,subQ1725,subQ1724,subQ1723,subQ1722,subQ1721,subQ1720,subQ1719,subQ1718,subQ1717,subQ1716,subQ1715,subQ1714,subQ1713,subQ1712,subQ1711,subQ1710,subQ1709,subQ1708,subQ1707,subQ1706,subQ1705,subQ1704,subQ1703,subQ1702,subQ1701,subQ1700,subQ1699,subQ1698,subQ1697,subQ1696,subQ1695,subQ1694,subQ1693,subQ1692,subQ1691,subQ1690,subQ1689,subQ1688,subQ1687,subQ1686,subQ1685,subQ1684,subQ1683,subQ1682,subQ1681,subQ1680,subQ1679,subQ1678,subQ1677,subQ1676,subQ1675,subQ1674,subQ1673,subQ1672,subQ1671,subQ1670,subQ1669,subQ1668,subQ1667,subQ1666,subQ1665,subQ1664,subQ1663,subQ1662,subQ1661,subQ1660,subQ1659,subQ1658,subQ1657,subQ1656,subQ1655,subQ1654,subQ1653,subQ1652,subQ1651,subQ1650,subQ1649,subQ1648,subQ1647,subQ1646,subQ1645,subQ1644,subQ1643,subQ1642,subQ1641,subQ1640,subQ1639,subQ1638,subQ1637,subQ1636,subQ1635,subQ1634,subQ1633,subQ1632,subQ1631,subQ1630,subQ1629,subQ1628,subQ1627,subQ1626,subQ1625,subQ1624,subQ1623,subQ1622,subQ1621,subQ1620,subQ1619,subQ1618,subQ1617,subQ1616,subQ1615,subQ1614,subQ1613,subQ1612,subQ1611,subQ1610,subQ1609,subQ1608,subQ1607,subQ1606,subQ1605,subQ1604,subQ1603,subQ1602,subQ1601,subQ1600,subQ1599,subQ1598,subQ1597,subQ1596,subQ1595,subQ1594,subQ1593,subQ1592,subQ1591,subQ1590,subQ1589,subQ1588,subQ1587,subQ1586,subQ1585,subQ1584,subQ1583,subQ1582,subQ1581,subQ1580,subQ1579,subQ1578,subQ1577,subQ1576,subQ1575,subQ1574,subQ1573,subQ1572,subQ1571,subQ1570,subQ1569,subQ1568,subQ1567,subQ1566,subQ1565,subQ1564,subQ1563,subQ1562,subQ1561,subQ1560,subQ1559,subQ1558,subQ1557,subQ1556,subQ1555,subQ1554,subQ1553,subQ1552,subQ1551,subQ1550,subQ1549,subQ1548,subQ1547,subQ1546,subQ1545,subQ1544,subQ1543,subQ1542,subQ1541,subQ1540,subQ1539,subQ1538,subQ1537,subQ1536,subQ1535,subQ1534,subQ1533,subQ1532,subQ1531,subQ1530,subQ1529,subQ1528,subQ1527,subQ1526,subQ1525,subQ1524,subQ1523,subQ1522,subQ1521,subQ1520,subQ1519,subQ1518,subQ1517,subQ1516,subQ1515,subQ1514,subQ1513,subQ1512,subQ1511,subQ1510,subQ1509,subQ1508,subQ1507,subQ1506,subQ1505,subQ1504,subQ1503,subQ1502,subQ1501,subQ1500,subQ1499,subQ1498,subQ1497,subQ1496,subQ1495,subQ1494,subQ1493,subQ1492,subQ1491,subQ1490,subQ1489,subQ1488,subQ1487,subQ1486,subQ1485,subQ1484,subQ1483,subQ1482,subQ1481,subQ1480,subQ1479,subQ1478,subQ1477,subQ1476,subQ1475,subQ1474,subQ1473,subQ1472,subQ1471,subQ1470,subQ1469,subQ1468,subQ1467,subQ1466,subQ1465,subQ1464,subQ1463,subQ1462,subQ1461,subQ1460,subQ1459,subQ1458,subQ1457,subQ1456,subQ1455,subQ1454,subQ1453,subQ1452,subQ1451,subQ1450,subQ1449,subQ1448,subQ1447,subQ1446,subQ1445,subQ1444,subQ1443,subQ1442,subQ1441,subQ1440,subQ1439,subQ1438,subQ1437,subQ1436,subQ1435,subQ1434,subQ1433,subQ1432,subQ1431,subQ1430,subQ1429,subQ1428,subQ1427,subQ1426,subQ1425,subQ1424,subQ1423,subQ1422,subQ1421,subQ1420,subQ1419,subQ1418,subQ1417,subQ1416,subQ1415,subQ1414,subQ1413,subQ1412,subQ1411,subQ1410,subQ1409,subQ1408,subQ1407,subQ1406,subQ1405,subQ1404,subQ1403,subQ1402,subQ1401,subQ1400,subQ1399,subQ1398,subQ1397,subQ1396,subQ1395,subQ1394,subQ1393,subQ1392,subQ1391,subQ1390,subQ1389,subQ1388,subQ1387,subQ1386,subQ1385,subQ1384,subQ1383,subQ1382,subQ1381,subQ1380,subQ1379,subQ1378,subQ1377,subQ1376,subQ1375,subQ1374,subQ1373,subQ1372,subQ1371,subQ1370,subQ1369,subQ1368,subQ1367,subQ1366,subQ1365,subQ1364,subQ1363,subQ1362,subQ1361,subQ1360,subQ1359,subQ1358,subQ1357,subQ1356,subQ1355,subQ1354,subQ1353,subQ1352,subQ1351,subQ1350,subQ1349,subQ1348,subQ1347,subQ1346,subQ1345,subQ1344,subQ1343,subQ1342,subQ1341,subQ1340,subQ1339,subQ1338,subQ1337,subQ1336,subQ1335,subQ1334,subQ1333,subQ1332,subQ1331,subQ1330,subQ1329,subQ1328,subQ1327,subQ1326,subQ1325,subQ1324,subQ1323,subQ1322,subQ1321,subQ1320,subQ1319,subQ1318,subQ1317,subQ1316,subQ1315,subQ1314,subQ1313,subQ1312,subQ1311,subQ1310,subQ1309,subQ1308,subQ1307,subQ1306,subQ1305,subQ1304,subQ1303,subQ1302,subQ1301,subQ1300,subQ1299,subQ1298,subQ1297,subQ1296,subQ1295,subQ1294,subQ1293,subQ1292,subQ1291,subQ1290,subQ1289,subQ1288,subQ1287,subQ1286,subQ1285,subQ1284,subQ1283,subQ1282,subQ1281,subQ1280,subQ1279,subQ1278,subQ1277,subQ1276,subQ1275,subQ1274,subQ1273,subQ1272,subQ1271,subQ1270,subQ1269,subQ1268,subQ1267,subQ1266,subQ1265,subQ1264,subQ1263,subQ1262,subQ1261,subQ1260,subQ1259,subQ1258,subQ1257,subQ1256,subQ1255,subQ1254,subQ1253,subQ1252,subQ1251,subQ1250,subQ1249,subQ1248,subQ1247,subQ1246,subQ1245,subQ1244,subQ1243,subQ1242,subQ1241,subQ1240,subQ1239,subQ1238,subQ1237,subQ1236,subQ1235,subQ1234,subQ1233,subQ1232,subQ1231,subQ1230,subQ1229,subQ1228,subQ1227,subQ1226,subQ1225,subQ1224,subQ1223,subQ1222,subQ1221,subQ1220,subQ1219,subQ1218,subQ1217,subQ1216,subQ1215,subQ1214,subQ1213,subQ1212,subQ1211,subQ1210,subQ1209,subQ1208,subQ1207,subQ1206,subQ1205,subQ1204,subQ1203,subQ1202,subQ1201,subQ1200,subQ1199,subQ1198,subQ1197,subQ1196,subQ1195,subQ1194,subQ1193,subQ1192,subQ1191,subQ1190,subQ1189,subQ1188,subQ1187,subQ1186,subQ1185,subQ1184,subQ1183,subQ1182,subQ1181,subQ1180,subQ1179,subQ1178,subQ1177,subQ1176,subQ1175,subQ1174,subQ1173,subQ1172,subQ1171,subQ1170,subQ1169,subQ1168,subQ1167,subQ1166,subQ1165,subQ1164,subQ1163,subQ1162,subQ1161,subQ1160,subQ1159,subQ1158,subQ1157,subQ1156,subQ1155,subQ1154,subQ1153,subQ1152,subQ1151,subQ1150,subQ1149,subQ1148,subQ1147,subQ1146,subQ1145,subQ1144,subQ1143,subQ1142,subQ1141,subQ1140,subQ1139,subQ1138,subQ1137,subQ1136,subQ1135,subQ1134,subQ1133,subQ1132,subQ1131,subQ1130,subQ1129,subQ1128,subQ1127,subQ1126,subQ1125,subQ1124,subQ1123,subQ1122,subQ1121,subQ1120,subQ1119,subQ1118,subQ1117,subQ1116,subQ1115,subQ1114,subQ1113,subQ1112,subQ1111,subQ1110,subQ1109,subQ1108,subQ1107,subQ1106,subQ1105,subQ1104,subQ1103,subQ1102,subQ1101,subQ1100,subQ1099,subQ1098,subQ1097,subQ1096,subQ1095,subQ1094,subQ1093,subQ1092,subQ1091,subQ1090,subQ1089,subQ1088,subQ1087,subQ1086,subQ1085,subQ1084,subQ1083,subQ1082,subQ1081,subQ1080,subQ1079,subQ1078,subQ1077,subQ1076,subQ1075,subQ1074,subQ1073,subQ1072,subQ1071,subQ1070,subQ1069,subQ1068,subQ1067,subQ1066,subQ1065,subQ1064,subQ1063,subQ1062,subQ1061,subQ1060,subQ1059,subQ1058,subQ1057,subQ1056,subQ1055,subQ1054,subQ1053,subQ1052,subQ1051,subQ1050,subQ1049,subQ1048,subQ1047,subQ1046,subQ1045,subQ1044,subQ1043,subQ1042,subQ1041,subQ1040,subQ1039,subQ1038,subQ1037,subQ1036,subQ1035,subQ1034,subQ1033,subQ1032,subQ1031,subQ1030,subQ1029,subQ1028,subQ1027,subQ1026,subQ1025,subQ1024,subQ1023,subQ1022,subQ1021,subQ1020,subQ1019,subQ1018,subQ1017,subQ1016,subQ1015,subQ1014,subQ1013,subQ1012,subQ1011,subQ1010,subQ1009,subQ1008,subQ1007,subQ1006,subQ1005,subQ1004,subQ1003,subQ1002,subQ1001,subQ1000,subQ999,subQ998,subQ997,subQ996,subQ995,subQ994,subQ993,subQ992,subQ991,subQ990,subQ989,subQ988,subQ987,subQ986,subQ985,subQ984,subQ983,subQ982,subQ981,subQ980,subQ979,subQ978,subQ977,subQ976,subQ975,subQ974,subQ973,subQ972,subQ971,subQ970,subQ969,subQ968,subQ967,subQ966,subQ965,subQ964,subQ963,subQ962,subQ961,subQ960,subQ959,subQ958,subQ957,subQ956,subQ955,subQ954,subQ953,subQ952,subQ951,subQ950,subQ949,subQ948,subQ947,subQ946,subQ945,subQ944,subQ943,subQ942,subQ941,subQ940,subQ939,subQ938,subQ937,subQ936,subQ935,subQ934,subQ933,subQ932,subQ931,subQ930,subQ929,subQ928,subQ927,subQ926,subQ925,subQ924,subQ923,subQ922,subQ921,subQ920,subQ919,subQ918,subQ917,subQ916,subQ915,subQ914,subQ913,subQ912,subQ911,subQ910,subQ909,subQ908,subQ907,subQ906,subQ905,subQ904,subQ903,subQ902,subQ901,subQ900,subQ899,subQ898,subQ897,subQ896,subQ895,subQ894,subQ893,subQ892,subQ891,subQ890,subQ889,subQ888,subQ887,subQ886,subQ885,subQ884,subQ883,subQ882,subQ881,subQ880,subQ879,subQ878,subQ877,subQ876,subQ875,subQ874,subQ873,subQ872,subQ871,subQ870,subQ869,subQ868,subQ867,subQ866,subQ865,subQ864,subQ863,subQ862,subQ861,subQ860,subQ859,subQ858,subQ857,subQ856,subQ855,subQ854,subQ853,subQ852,subQ851,subQ850,subQ849,subQ848,subQ847,subQ846,subQ845,subQ844,subQ843,subQ842,subQ841,subQ840,subQ839,subQ838,subQ837,subQ836,subQ835,subQ834,subQ833,subQ832,subQ831,subQ830,subQ829,subQ828,subQ827,subQ826,subQ825,subQ824,subQ823,subQ822,subQ821,subQ820,subQ819,subQ818,subQ817,subQ816,subQ815,subQ814,subQ813,subQ812,subQ811,subQ810,subQ809,subQ808,subQ807,subQ806,subQ805,subQ804,subQ803,subQ802,subQ801,subQ800,subQ799,subQ798,subQ797,subQ796,subQ795,subQ794,subQ793,subQ792,subQ791,subQ790,subQ789,subQ788,subQ787,subQ786,subQ785,subQ784,subQ783,subQ782,subQ781,subQ780,subQ779,subQ778,subQ777,subQ776,subQ775,subQ774,subQ773,subQ772,subQ771,subQ770,subQ769,subQ768,subQ767,subQ766,subQ765,subQ764,subQ763,subQ762,subQ761,subQ760,subQ759,subQ758,subQ757,subQ756,subQ755,subQ754,subQ753,subQ752,subQ751,subQ750,subQ749,subQ748,subQ747,subQ746,subQ745,subQ744,subQ743,subQ742,subQ741,subQ740,subQ739,subQ738,subQ737,subQ736,subQ735,subQ734,subQ733,subQ732,subQ731,subQ730,subQ729,subQ728,subQ727,subQ726,subQ725,subQ724,subQ723,subQ722,subQ721,subQ720,subQ719,subQ718,subQ717,subQ716,subQ715,subQ714,subQ713,subQ712,subQ711,subQ710,subQ709,subQ708,subQ707,subQ706,subQ705,subQ704,subQ703,subQ702,subQ701,subQ700,subQ699,subQ698,subQ697,subQ696,subQ695,subQ694,subQ693,subQ692,subQ691,subQ690,subQ689,subQ688,subQ687,subQ686,subQ685,subQ684,subQ683,subQ682,subQ681,subQ680,subQ679,subQ678,subQ677,subQ676,subQ675,subQ674,subQ673,subQ672,subQ671,subQ670,subQ669,subQ668,subQ667,subQ666,subQ665,subQ664,subQ663,subQ662,subQ661,subQ660,subQ659,subQ658,subQ657,subQ656,subQ655,subQ654,subQ653,subQ652,subQ651,subQ650,subQ649,subQ648,subQ647,subQ646,subQ645,subQ644,subQ643,subQ642,subQ641,subQ640,subQ639,subQ638,subQ637,subQ636,subQ635,subQ634,subQ633,subQ632,subQ631,subQ630,subQ629,subQ628,subQ627,subQ626,subQ625,subQ624,subQ623,subQ622,subQ621,subQ620,subQ619,subQ618,subQ617,subQ616,subQ615,subQ614,subQ613,subQ612,subQ611,subQ610,subQ609,subQ608,subQ607,subQ606,subQ605,subQ604,subQ603,subQ602,subQ601,subQ600,subQ599,subQ598,subQ597,subQ596,subQ595,subQ594,subQ593,subQ592,subQ591,subQ590,subQ589,subQ588,subQ587,subQ586,subQ585,subQ584,subQ583,subQ582,subQ581,subQ580,subQ579,subQ578,subQ577,subQ576,subQ575,subQ574,subQ573,subQ572,subQ571,subQ570,subQ569,subQ568,subQ567,subQ566,subQ565,subQ564,subQ563,subQ562,subQ561,subQ560,subQ559,subQ558,subQ557,subQ556,subQ555,subQ554,subQ553,subQ552,subQ551,subQ550,subQ549,subQ548,subQ547,subQ546,subQ545,subQ544,subQ543,subQ542,subQ541,subQ540,subQ539,subQ538,subQ537,subQ536,subQ535,subQ534,subQ533,subQ532,subQ531,subQ530,subQ529,subQ528,subQ527,subQ526,subQ525,subQ524,subQ523,subQ522,subQ521,subQ520,subQ519,subQ518,subQ517,subQ516,subQ515,subQ514,subQ513,subQ512,subQ511,subQ510,subQ509,subQ508,subQ507,subQ506,subQ505,subQ504,subQ503,subQ502,subQ501,subQ500,subQ499,subQ498,subQ497,subQ496,subQ495,subQ494,subQ493,subQ492,subQ491,subQ490,subQ489,subQ488,subQ487,subQ486,subQ485,subQ484,subQ483,subQ482,subQ481,subQ480,subQ479,subQ478,subQ477,subQ476,subQ475,subQ474,subQ473,subQ472,subQ471,subQ470,subQ469,subQ468,subQ467,subQ466,subQ465,subQ464,subQ463,subQ462,subQ461,subQ460,subQ459,subQ458,subQ457,subQ456,subQ455,subQ454,subQ453,subQ452,subQ451,subQ450,subQ449,subQ448,subQ447,subQ446,subQ445,subQ444,subQ443,subQ442,subQ441,subQ440,subQ439,subQ438,subQ437,subQ436,subQ435,subQ434,subQ433,subQ432,subQ431,subQ430,subQ429,subQ428,subQ427,subQ426,subQ425,subQ424,subQ423,subQ422,subQ421,subQ420,subQ419,subQ418,subQ417,subQ416,subQ415,subQ414,subQ413,subQ412,subQ411,subQ410,subQ409,subQ408,subQ407,subQ406,subQ405,subQ404,subQ403,subQ402,subQ401,subQ400,subQ399,subQ398,subQ397,subQ396,subQ395,subQ394,subQ393,subQ392,subQ391,subQ390,subQ389,subQ388,subQ387,subQ386,subQ385,subQ384,subQ383,subQ382,subQ381,subQ380,subQ379,subQ378,subQ377,subQ376,subQ375,subQ374,subQ373,subQ372,subQ371,subQ370,subQ369,subQ368,subQ367,subQ366,subQ365,subQ364,subQ363,subQ362,subQ361,subQ360,subQ359,subQ358,subQ357,subQ356,subQ355,subQ354,subQ353,subQ352,subQ351,subQ350,subQ349,subQ348,subQ347,subQ346,subQ345,subQ344,subQ343,subQ342,subQ341,subQ340,subQ339,subQ338,subQ337,subQ336,subQ335,subQ334,subQ333,subQ332,subQ331,subQ330,subQ329,subQ328,subQ327,subQ326,subQ325,subQ324,subQ323,subQ322,subQ321,subQ320,subQ319,subQ318,subQ317,subQ316,subQ315,subQ314,subQ313,subQ312,subQ311,subQ310,subQ309,subQ308,subQ307,subQ306,subQ305,subQ304,subQ303,subQ302,subQ301,subQ300,subQ299,subQ298,subQ297,subQ296,subQ295,subQ294,subQ293,subQ292,subQ291,subQ290,subQ289,subQ288,subQ287,subQ286,subQ285,subQ284,subQ283,subQ282,subQ281,subQ280,subQ279,subQ278,subQ277,subQ276,subQ275,subQ274,subQ273,subQ272,subQ271,subQ270,subQ269,subQ268,subQ267,subQ266,subQ265,subQ264,subQ263,subQ262,subQ261,subQ260,subQ259,subQ258,subQ257,subQ256,subQ255,subQ254,subQ253,subQ252,subQ251,subQ250,subQ249,subQ248,subQ247,subQ246,subQ245,subQ244,subQ243,subQ242,subQ241,subQ240,subQ239,subQ238,subQ237,subQ236,subQ235,subQ234,subQ233,subQ232,subQ231,subQ230,subQ229,subQ228,subQ227,subQ226,subQ225,subQ224,subQ223,subQ222,subQ221,subQ220,subQ219,subQ218,subQ217,subQ216,subQ215,subQ214,subQ213,subQ212,subQ211,subQ210,subQ209,subQ208,subQ207,subQ206,subQ205,subQ204,subQ203,subQ202,subQ201,subQ200,subQ199,subQ198,subQ197,subQ196,subQ195,subQ194,subQ193,subQ192,subQ191,subQ190,subQ189,subQ188,subQ187,subQ186,subQ185,subQ184,subQ183,subQ182,subQ181,subQ180,subQ179,subQ178,subQ177,subQ176,subQ175,subQ174,subQ173,subQ172,subQ171,subQ170,subQ169,subQ168,subQ167,subQ166,subQ165,subQ164,subQ163,subQ162,subQ161,subQ160,subQ159,subQ158,subQ157,subQ156,subQ155,subQ154,subQ153,subQ152,subQ151,subQ150,subQ149,subQ148,subQ147,subQ146,subQ145,subQ144,subQ143,subQ142,subQ141,subQ140,subQ139,subQ138,subQ137,subQ136,subQ135,subQ134,subQ133,subQ132,subQ131,subQ130,subQ129,subQ128,subQ127,subQ126,subQ125,subQ124,subQ123,subQ122,subQ121,subQ120,subQ119,subQ118,subQ117,subQ116,subQ115,subQ114,subQ113,subQ112,subQ111,subQ110,subQ109,subQ108,subQ107,subQ106,subQ105,subQ104,subQ103,subQ102,subQ101,subQ100,subQ99,subQ98,subQ97,subQ96,subQ95,subQ94,subQ93,subQ92,subQ91,subQ90,subQ89,subQ88,subQ87,subQ86,subQ85,subQ84,subQ83,subQ82,subQ81,subQ80,subQ79,subQ78,subQ77,subQ76,subQ75,subQ74,subQ73,subQ72,subQ71,subQ70,subQ69,subQ68,subQ67,subQ66,subQ65,subQ64,subQ63,subQ62,subQ61,subQ60,subQ59,subQ58,subQ57,subQ56,subQ55,subQ54,subQ53,subQ52,subQ51,subQ50,subQ49,subQ48,subQ47,subQ46,subQ45,subQ44,subQ43,subQ42,subQ41,subQ40,subQ39,subQ38,subQ37,subQ36,subQ35,subQ34,subQ33,subQ32,subQ31,subQ30,subQ29,subQ28,subQ27,subQ26,subQ25,subQ24,subQ23,subQ22,subQ21,subQ20,subQ19,subQ18,subQ17,subQ16,subQ15,subQ14,subQ13,subQ12,subQ11,subQ10,subQ9,subQ8,subQ7,subQ6,subQ5,subQ4,subQ3,subQ2,subQ1,subQ0])],"isStart":false})]});}
            extrude(context, id + "F5", {"entities" : qUnion([Q0]), "operationType" : NewBodyOperationType.REMOVE, "endBound" : BoundingType.UP_TO_SURFACE, "oppositeDirection" : true, "endBoundEntityFace" : qUnion([Q1]), "depth" : 25 * mm});
        }
    });
